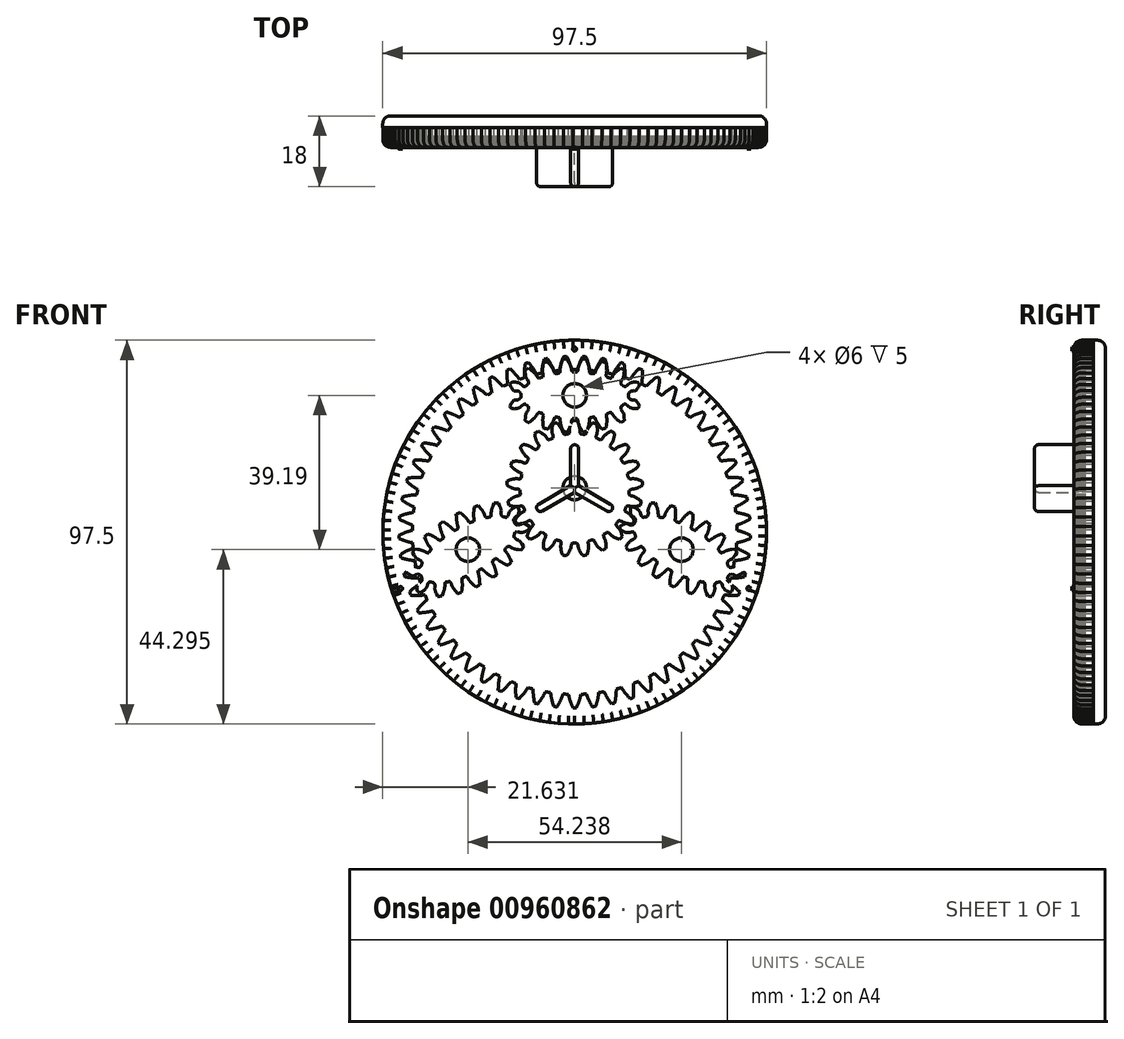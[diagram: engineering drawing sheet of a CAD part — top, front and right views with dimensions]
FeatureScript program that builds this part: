
annotation { "Feature Type Name" : "Feature", "Feature Type Description" : "" }
export const myFeature = defineFeature(function(context is Context, id is Id, definition is map)
    precondition{}
    {
        {
            var Q0;
            Q0=qCreatedBy(makeId("Front.planeOp"),FACE);
            var sketch = newSketch(context, id + "F0", { "sketchPlane" : qUnion([Q0])});
            skCircle(sketch, "E0", {"center": v(0, 0) * mm, "radius": 42.52 * mm});
            skCircle(sketch, "E1", {"center": v(0, 11.2) * mm, "radius": 15.75 * mm});
            skLineSegment(sketch, "E2", {"start": v(0, 11.2) * mm, "end": v(40.7, -12.3) * mm, "construction": true});
            skEllipse(sketch, "E3", {"center": v(0, 34.73) * mm, "majorRadius": 2 * mm, "minorRadius": 1 * mm, "majorAxis": v(1, 0)});
            skPoint(sketch, "E4", {"position": v(13.64, 3.33) * mm});
            skPoint(sketch, "E5", {"position": v(23.23, -11.2) * mm});
            skPoint(sketch, "E6", {"position": v(-15.56, 34.73) * mm});
            skPoint(sketch, "E7", {"position": v(0, 26.95) * mm});
            skPoint(sketch, "E8.center.orphan", {"position": v(27.12, -4.46) * mm});
            skLineSegment(sketch, "E9", {"start": v(27.12, -4.46) * mm, "end": v(23.23, -11.2) * mm, "construction": true});
            skEllipse(sketch, "E10", {"center": v(27.12, -4.46) * mm, "majorRadius": 2 * mm, "minorRadius": 1 * mm, "majorAxis": v(-0.87, 0.5)});
            skPoint(sketch, "E11", {"position": v(0, -4.55) * mm});
            skPoint(sketch, "E12", {"position": v(40.99, -11.3) * mm});
            skPoint(sketch, "E13", {"position": v(0, -42.52) * mm});
            skEllipse(sketch, "E14.MirrorC", {"center": v(-27.12, -4.46) * mm, "majorRadius": 2 * mm, "minorRadius": 1 * mm, "majorAxis": v(0.87, 0.5)});
            skSolve(sketch);
        }
        {
            var Q0;
            Q0=qCreatedBy(makeId("Top.planeOp"),FACE);
            var sketch = newSketch(context, id + "F1", { "sketchPlane" : qUnion([Q0])});
            skLineSegment(sketch, "E15", {"start": v(0, 8.57) * mm, "end": v(0, -10.97) * mm});
            skSolve(sketch);
        }
        {
            var Q0;
            Q0=qCreatedBy(makeId("Front.planeOp"),FACE);
            var sketch = newSketch(context, id + "F2", { "sketchPlane" : qUnion([Q0])});
            skLineSegment(sketch, "E16", {"start": v(-1.48, -8.52) * mm, "end": v(-1.41, -8.38) * mm});
            skLineSegment(sketch, "E17", {"start": v(-1.41, -8.38) * mm, "end": v(-1.35, -8.26) * mm});
            skLineSegment(sketch, "E18", {"start": v(-1.35, -8.26) * mm, "end": v(-1.3, -8.13) * mm});
            skLineSegment(sketch, "E19", {"start": v(-1.3, -8.13) * mm, "end": v(-1.25, -8.02) * mm});
            skLineSegment(sketch, "E20", {"start": v(-1.25, -8.02) * mm, "end": v(-1.2, -7.9) * mm});
            skLineSegment(sketch, "E21", {"start": v(-1.2, -7.9) * mm, "end": v(-1.15, -7.8) * mm});
            skLineSegment(sketch, "E22", {"start": v(-1.15, -7.8) * mm, "end": v(-1.1, -7.69) * mm});
            skLineSegment(sketch, "E23", {"start": v(-1.1, -7.69) * mm, "end": v(-1.07, -7.59) * mm});
            skLineSegment(sketch, "E24", {"start": v(-1.07, -7.59) * mm, "end": v(-1.04, -7.5) * mm});
            skLineSegment(sketch, "E25", {"start": v(-1.04, -7.5) * mm, "end": v(-1.01, -7.44) * mm});
            skLineSegment(sketch, "E26", {"start": v(-1.01, -7.44) * mm, "end": v(-1, -7.38) * mm});
            skLineSegment(sketch, "E27", {"start": v(-1, -7.38) * mm, "end": v(-0.97, -7.32) * mm});
            skLineSegment(sketch, "E28", {"start": v(-0.97, -7.32) * mm, "end": v(-0.93, -7.21) * mm});
            skLineSegment(sketch, "E29", {"start": v(-0.93, -7.21) * mm, "end": v(-0.9, -7.1) * mm});
            skLineSegment(sketch, "E30", {"start": v(-0.9, -7.1) * mm, "end": v(-0.86, -6.99) * mm});
            skLineSegment(sketch, "E31", {"start": v(-0.86, -6.99) * mm, "end": v(-0.83, -6.88) * mm});
            skLineSegment(sketch, "E32", {"start": v(-0.83, -6.88) * mm, "end": v(-0.8, -6.8) * mm});
            skLineSegment(sketch, "E33", {"start": v(-0.8, -6.8) * mm, "end": v(-0.78, -6.7) * mm});
            skLineSegment(sketch, "E34", {"start": v(-0.78, -6.7) * mm, "end": v(-0.76, -6.63) * mm});
            skLineSegment(sketch, "E35", {"start": v(-0.76, -6.63) * mm, "end": v(-0.74, -6.56) * mm});
            skLineSegment(sketch, "E36", {"start": v(-0.74, -6.56) * mm, "end": v(-0.66, -6.21) * mm});
            skLineSegment(sketch, "E37", {"start": v(-0.66, -6.21) * mm, "end": v(-0.65, -6.18) * mm});
            skLineSegment(sketch, "E38", {"start": v(-0.65, -6.18) * mm, "end": v(-0.64, -6.16) * mm});
            skLineSegment(sketch, "E39", {"start": v(-0.64, -6.16) * mm, "end": v(-0.63, -6.1) * mm});
            skLineSegment(sketch, "E40", {"start": v(-0.63, -6.1) * mm, "end": v(-0.61, -6.09) * mm});
            skLineSegment(sketch, "E41", {"start": v(-0.61, -6.09) * mm, "end": v(-0.6, -6.04) * mm});
            skLineSegment(sketch, "E42", {"start": v(-0.6, -6.04) * mm, "end": v(-0.57, -6) * mm});
            skLineSegment(sketch, "E43", {"start": v(-0.57, -6) * mm, "end": v(-0.54, -5.97) * mm});
            skLineSegment(sketch, "E44", {"start": v(-0.54, -5.97) * mm, "end": v(-0.52, -5.95) * mm});
            skLineSegment(sketch, "E45", {"start": v(-0.52, -5.95) * mm, "end": v(-0.49, -5.93) * mm});
            skLineSegment(sketch, "E46", {"start": v(-0.49, -5.93) * mm, "end": v(-0.47, -5.91) * mm});
            skLineSegment(sketch, "E47", {"start": v(-0.47, -5.91) * mm, "end": v(-0.46, -5.91) * mm});
            skLineSegment(sketch, "E48", {"start": v(-0.46, -5.91) * mm, "end": v(-0.45, -5.9) * mm});
            skLineSegment(sketch, "E49", {"start": v(-0.45, -5.9) * mm, "end": v(-0.44, -5.9) * mm});
            skLineSegment(sketch, "E50", {"start": v(-0.44, -5.9) * mm, "end": v(-0.43, -5.9) * mm});
            skLineSegment(sketch, "E51", {"start": v(-0.43, -5.9) * mm, "end": v(-0.26, -5.9) * mm});
            skLineSegment(sketch, "E52", {"start": v(-0.26, -5.9) * mm, "end": v(-0.05, -5.9) * mm});
            skLineSegment(sketch, "E53", {"start": v(-0.05, -5.9) * mm, "end": v(0.12, -5.9) * mm});
            skLineSegment(sketch, "E54", {"start": v(0.12, -5.9) * mm, "end": v(0.32, -5.9) * mm});
            skLineSegment(sketch, "E55", {"start": v(0.32, -5.9) * mm, "end": v(0.5, -5.9) * mm});
            skLineSegment(sketch, "E56", {"start": v(0.5, -5.9) * mm, "end": v(0.51, -5.9) * mm});
            skLineSegment(sketch, "E57", {"start": v(0.51, -5.9) * mm, "end": v(0.52, -5.9) * mm});
            skLineSegment(sketch, "E58", {"start": v(0.52, -5.9) * mm, "end": v(0.53, -5.9) * mm});
            skLineSegment(sketch, "E59", {"start": v(0.53, -5.9) * mm, "end": v(0.54, -5.91) * mm});
            skLineSegment(sketch, "E60", {"start": v(0.54, -5.91) * mm, "end": v(0.56, -5.92) * mm});
            skLineSegment(sketch, "E61", {"start": v(0.56, -5.92) * mm, "end": v(0.58, -5.94) * mm});
            skLineSegment(sketch, "E62", {"start": v(0.58, -5.94) * mm, "end": v(0.6, -5.96) * mm});
            skLineSegment(sketch, "E63", {"start": v(0.6, -5.96) * mm, "end": v(0.62, -5.98) * mm});
            skLineSegment(sketch, "E64", {"start": v(0.62, -5.98) * mm, "end": v(0.64, -6) * mm});
            skLineSegment(sketch, "E65", {"start": v(0.64, -6) * mm, "end": v(0.66, -6.03) * mm});
            skLineSegment(sketch, "E66", {"start": v(0.66, -6.03) * mm, "end": v(0.68, -6.07) * mm});
            skLineSegment(sketch, "E67", {"start": v(0.68, -6.07) * mm, "end": v(0.7, -6.11) * mm});
            skLineSegment(sketch, "E68", {"start": v(0.7, -6.11) * mm, "end": v(0.72, -6.16) * mm});
            skLineSegment(sketch, "E69", {"start": v(0.72, -6.16) * mm, "end": v(0.73, -6.18) * mm});
            skLineSegment(sketch, "E70", {"start": v(0.73, -6.18) * mm, "end": v(0.83, -6.58) * mm});
            skLineSegment(sketch, "E71", {"start": v(0.83, -6.58) * mm, "end": v(0.84, -6.66) * mm});
            skLineSegment(sketch, "E72", {"start": v(0.84, -6.66) * mm, "end": v(0.86, -6.73) * mm});
            skLineSegment(sketch, "E73", {"start": v(0.86, -6.73) * mm, "end": v(0.89, -6.81) * mm});
            skLineSegment(sketch, "E74", {"start": v(0.89, -6.81) * mm, "end": v(0.9, -6.88) * mm});
            skLineSegment(sketch, "E75", {"start": v(0.9, -6.88) * mm, "end": v(0.93, -6.97) * mm});
            skLineSegment(sketch, "E76", {"start": v(0.93, -6.97) * mm, "end": v(0.96, -7.05) * mm});
            skLineSegment(sketch, "E77", {"start": v(0.96, -7.05) * mm, "end": v(0.99, -7.14) * mm});
            skLineSegment(sketch, "E78", {"start": v(0.99, -7.14) * mm, "end": v(1.02, -7.22) * mm});
            skLineSegment(sketch, "E79", {"start": v(1.02, -7.22) * mm, "end": v(1.05, -7.31) * mm});
            skLineSegment(sketch, "E80", {"start": v(1.05, -7.31) * mm, "end": v(1.07, -7.38) * mm});
            skLineSegment(sketch, "E81", {"start": v(1.07, -7.38) * mm, "end": v(1.09, -7.42) * mm});
            skLineSegment(sketch, "E82", {"start": v(1.09, -7.42) * mm, "end": v(1.11, -7.5) * mm});
            skLineSegment(sketch, "E83", {"start": v(1.11, -7.5) * mm, "end": v(1.16, -7.6) * mm});
            skLineSegment(sketch, "E84", {"start": v(1.16, -7.6) * mm, "end": v(1.2, -7.74) * mm});
            skLineSegment(sketch, "E85", {"start": v(1.2, -7.74) * mm, "end": v(1.27, -7.88) * mm});
            skLineSegment(sketch, "E86", {"start": v(1.27, -7.88) * mm, "end": v(1.33, -8.02) * mm});
            skLineSegment(sketch, "E87", {"start": v(1.33, -8.02) * mm, "end": v(1.39, -8.16) * mm});
            skLineSegment(sketch, "E88", {"start": v(1.39, -8.16) * mm, "end": v(1.45, -8.3) * mm});
            skLineSegment(sketch, "E89", {"start": v(1.45, -8.3) * mm, "end": v(1.52, -8.43) * mm});
            skLineSegment(sketch, "E90", {"start": v(1.52, -8.43) * mm, "end": v(1.59, -8.57) * mm});
            skLineSegment(sketch, "E91", {"start": v(1.59, -8.57) * mm, "end": v(1.95, -9.28) * mm});
            skLineSegment(sketch, "E92", {"start": v(1.95, -9.28) * mm, "end": v(2, -9.28) * mm});
            skLineSegment(sketch, "E93", {"start": v(2, -9.28) * mm, "end": v(2.29, -9.26) * mm});
            skLineSegment(sketch, "E94", {"start": v(2.29, -9.26) * mm, "end": v(2.57, -9.24) * mm});
            skLineSegment(sketch, "E95", {"start": v(2.57, -9.24) * mm, "end": v(2.85, -9.22) * mm});
            skLineSegment(sketch, "E96", {"start": v(2.85, -9.22) * mm, "end": v(3.08, -9.2) * mm});
            skLineSegment(sketch, "E97", {"start": v(3.08, -9.2) * mm, "end": v(3.35, -8.36) * mm});
            skLineSegment(sketch, "E98", {"start": v(3.35, -8.36) * mm, "end": v(3.4, -8.2) * mm});
            skLineSegment(sketch, "E99", {"start": v(3.4, -8.2) * mm, "end": v(3.44, -8.05) * mm});
            skLineSegment(sketch, "E100", {"start": v(3.44, -8.05) * mm, "end": v(3.48, -7.9) * mm});
            skLineSegment(sketch, "E101", {"start": v(3.48, -7.9) * mm, "end": v(3.52, -7.76) * mm});
            skLineSegment(sketch, "E102", {"start": v(3.52, -7.76) * mm, "end": v(3.55, -7.64) * mm});
            skLineSegment(sketch, "E103", {"start": v(3.55, -7.64) * mm, "end": v(3.58, -7.5) * mm});
            skLineSegment(sketch, "E104", {"start": v(3.58, -7.5) * mm, "end": v(3.6, -7.4) * mm});
            skLineSegment(sketch, "E105", {"start": v(3.6, -7.4) * mm, "end": v(3.63, -7.29) * mm});
            skLineSegment(sketch, "E106", {"start": v(3.63, -7.29) * mm, "end": v(3.64, -7.22) * mm});
            skLineSegment(sketch, "E107", {"start": v(3.64, -7.22) * mm, "end": v(3.65, -7.19) * mm});
            skLineSegment(sketch, "E108", {"start": v(3.65, -7.19) * mm, "end": v(3.66, -7.12) * mm});
            skLineSegment(sketch, "E109", {"start": v(3.66, -7.12) * mm, "end": v(3.68, -7.04) * mm});
            skLineSegment(sketch, "E110", {"start": v(3.68, -7.04) * mm, "end": v(3.7, -6.95) * mm});
            skLineSegment(sketch, "E111", {"start": v(3.7, -6.95) * mm, "end": v(3.7, -6.86) * mm});
            skLineSegment(sketch, "E112", {"start": v(3.7, -6.86) * mm, "end": v(3.72, -6.76) * mm});
            skLineSegment(sketch, "E113", {"start": v(3.72, -6.76) * mm, "end": v(3.73, -6.68) * mm});
            skLineSegment(sketch, "E114", {"start": v(3.73, -6.68) * mm, "end": v(3.74, -6.6) * mm});
            skLineSegment(sketch, "E115", {"start": v(3.74, -6.6) * mm, "end": v(3.74, -6.54) * mm});
            skLineSegment(sketch, "E116", {"start": v(3.74, -6.54) * mm, "end": v(3.75, -6.48) * mm});
            skLineSegment(sketch, "E117", {"start": v(3.75, -6.48) * mm, "end": v(3.75, -6.43) * mm});
            skLineSegment(sketch, "E118", {"start": v(3.75, -6.43) * mm, "end": v(3.75, -6.38) * mm});
            skLineSegment(sketch, "E119", {"start": v(3.75, -6.38) * mm, "end": v(3.76, -6.1) * mm});
            skLineSegment(sketch, "E120", {"start": v(3.76, -6.1) * mm, "end": v(3.77, -6.09) * mm});
            skLineSegment(sketch, "E121", {"start": v(3.77, -6.09) * mm, "end": v(3.77, -6.01) * mm});
            skLineSegment(sketch, "E122", {"start": v(3.77, -6.01) * mm, "end": v(3.78, -5.98) * mm});
            skLineSegment(sketch, "E123", {"start": v(3.78, -5.98) * mm, "end": v(3.79, -5.95) * mm});
            skLineSegment(sketch, "E124", {"start": v(3.79, -5.95) * mm, "end": v(3.8, -5.9) * mm});
            skLineSegment(sketch, "E125", {"start": v(3.8, -5.9) * mm, "end": v(3.8, -5.87) * mm});
            skLineSegment(sketch, "E126", {"start": v(3.8, -5.87) * mm, "end": v(3.82, -5.85) * mm});
            skLineSegment(sketch, "E127", {"start": v(3.82, -5.85) * mm, "end": v(3.82, -5.8) * mm});
            skLineSegment(sketch, "E128", {"start": v(3.82, -5.8) * mm, "end": v(3.84, -5.78) * mm});
            skLineSegment(sketch, "E129", {"start": v(3.84, -5.78) * mm, "end": v(3.86, -5.74) * mm});
            skLineSegment(sketch, "E130", {"start": v(3.86, -5.74) * mm, "end": v(3.88, -5.7) * mm});
            skLineSegment(sketch, "E131", {"start": v(3.88, -5.7) * mm, "end": v(3.9, -5.68) * mm});
            skLineSegment(sketch, "E132", {"start": v(3.9, -5.68) * mm, "end": v(3.92, -5.66) * mm});
            skLineSegment(sketch, "E133", {"start": v(3.92, -5.66) * mm, "end": v(3.94, -5.65) * mm});
            skLineSegment(sketch, "E134", {"start": v(3.94, -5.65) * mm, "end": v(3.95, -5.64) * mm});
            skLineSegment(sketch, "E135", {"start": v(3.95, -5.64) * mm, "end": v(3.95, -5.64) * mm});
            skLineSegment(sketch, "E136", {"start": v(3.95, -5.64) * mm, "end": v(3.97, -5.64) * mm});
            skLineSegment(sketch, "E137", {"start": v(3.97, -5.64) * mm, "end": v(3.98, -5.63) * mm});
            skLineSegment(sketch, "E138", {"start": v(3.98, -5.63) * mm, "end": v(4.18, -5.6) * mm});
            skLineSegment(sketch, "E139", {"start": v(4.18, -5.6) * mm, "end": v(4.38, -5.57) * mm});
            skLineSegment(sketch, "E140", {"start": v(4.38, -5.57) * mm, "end": v(4.5, -5.55) * mm});
            skLineSegment(sketch, "E141", {"start": v(4.5, -5.55) * mm, "end": v(4.7, -5.52) * mm});
            skLineSegment(sketch, "E142", {"start": v(4.7, -5.52) * mm, "end": v(4.9, -5.48) * mm});
            skLineSegment(sketch, "E143", {"start": v(4.9, -5.48) * mm, "end": v(4.9, -5.49) * mm});
            skLineSegment(sketch, "E144", {"start": v(4.9, -5.49) * mm, "end": v(4.92, -5.49) * mm});
            skLineSegment(sketch, "E145", {"start": v(4.92, -5.49) * mm, "end": v(4.93, -5.49) * mm});
            skLineSegment(sketch, "E146", {"start": v(4.93, -5.49) * mm, "end": v(4.94, -5.49) * mm});
            skLineSegment(sketch, "E147", {"start": v(4.94, -5.49) * mm, "end": v(4.96, -5.5) * mm});
            skLineSegment(sketch, "E148", {"start": v(4.96, -5.5) * mm, "end": v(4.99, -5.51) * mm});
            skLineSegment(sketch, "E149", {"start": v(4.99, -5.51) * mm, "end": v(5.01, -5.53) * mm});
            skLineSegment(sketch, "E150", {"start": v(5.01, -5.53) * mm, "end": v(5.04, -5.55) * mm});
            skLineSegment(sketch, "E151", {"start": v(5.04, -5.55) * mm, "end": v(5.07, -5.58) * mm});
            skLineSegment(sketch, "E152", {"start": v(5.07, -5.58) * mm, "end": v(5.1, -5.61) * mm});
            skLineSegment(sketch, "E153", {"start": v(5.1, -5.61) * mm, "end": v(5.12, -5.63) * mm});
            skLineSegment(sketch, "E154", {"start": v(5.12, -5.63) * mm, "end": v(5.14, -5.68) * mm});
            skLineSegment(sketch, "E155", {"start": v(5.14, -5.68) * mm, "end": v(5.16, -5.7) * mm});
            skLineSegment(sketch, "E156", {"start": v(5.16, -5.7) * mm, "end": v(5.17, -5.73) * mm});
            skLineSegment(sketch, "E157", {"start": v(5.17, -5.73) * mm, "end": v(5.33, -6.11) * mm});
            skLineSegment(sketch, "E158", {"start": v(5.33, -6.11) * mm, "end": v(5.37, -6.2) * mm});
            skLineSegment(sketch, "E159", {"start": v(5.37, -6.2) * mm, "end": v(5.4, -6.28) * mm});
            skLineSegment(sketch, "E160", {"start": v(5.4, -6.28) * mm, "end": v(5.44, -6.37) * mm});
            skLineSegment(sketch, "E161", {"start": v(5.44, -6.37) * mm, "end": v(5.48, -6.45) * mm});
            skLineSegment(sketch, "E162", {"start": v(5.48, -6.45) * mm, "end": v(5.52, -6.54) * mm});
            skLineSegment(sketch, "E163", {"start": v(5.52, -6.54) * mm, "end": v(5.57, -6.62) * mm});
            skLineSegment(sketch, "E164", {"start": v(5.57, -6.62) * mm, "end": v(5.61, -6.71) * mm});
            skLineSegment(sketch, "E165", {"start": v(5.61, -6.71) * mm, "end": v(5.66, -6.8) * mm});
            skLineSegment(sketch, "E166", {"start": v(5.66, -6.8) * mm, "end": v(5.7, -6.86) * mm});
            skLineSegment(sketch, "E167", {"start": v(5.7, -6.86) * mm, "end": v(5.7, -6.9) * mm});
            skLineSegment(sketch, "E168", {"start": v(5.7, -6.9) * mm, "end": v(5.74, -6.95) * mm});
            skLineSegment(sketch, "E169", {"start": v(5.74, -6.95) * mm, "end": v(5.8, -7.04) * mm});
            skLineSegment(sketch, "E170", {"start": v(5.8, -7.04) * mm, "end": v(5.84, -7.13) * mm});
            skLineSegment(sketch, "E171", {"start": v(5.84, -7.13) * mm, "end": v(5.9, -7.23) * mm});
            skLineSegment(sketch, "E172", {"start": v(5.9, -7.23) * mm, "end": v(5.98, -7.34) * mm});
            skLineSegment(sketch, "E173", {"start": v(5.98, -7.34) * mm, "end": v(6.05, -7.45) * mm});
            skLineSegment(sketch, "E174", {"start": v(6.05, -7.45) * mm, "end": v(6.13, -7.57) * mm});
            skLineSegment(sketch, "E175", {"start": v(6.13, -7.57) * mm, "end": v(6.2, -7.68) * mm});
            skLineSegment(sketch, "E176", {"start": v(6.2, -7.68) * mm, "end": v(6.28, -7.78) * mm});
            skLineSegment(sketch, "E177", {"start": v(6.28, -7.78) * mm, "end": v(6.36, -7.9) * mm});
            skLineSegment(sketch, "E178", {"start": v(6.36, -7.9) * mm, "end": v(6.45, -8.01) * mm});
            skLineSegment(sketch, "E179", {"start": v(6.45, -8.01) * mm, "end": v(6.9, -8.58) * mm});
            skLineSegment(sketch, "E180", {"start": v(6.9, -8.58) * mm, "end": v(6.97, -8.56) * mm});
            skLineSegment(sketch, "E181", {"start": v(6.97, -8.56) * mm, "end": v(7.16, -8.52) * mm});
            skLineSegment(sketch, "E182", {"start": v(7.16, -8.52) * mm, "end": v(7.35, -8.47) * mm});
            skLineSegment(sketch, "E183", {"start": v(7.35, -8.47) * mm, "end": v(7.52, -8.43) * mm});
            skLineSegment(sketch, "E184", {"start": v(7.52, -8.43) * mm, "end": v(7.7, -8.38) * mm});
            skLineSegment(sketch, "E185", {"start": v(7.7, -8.38) * mm, "end": v(7.87, -8.33) * mm});
            skLineSegment(sketch, "E186", {"start": v(7.87, -8.33) * mm, "end": v(7.96, -8.31) * mm});
            skLineSegment(sketch, "E187", {"start": v(7.96, -8.31) * mm, "end": v(8.07, -7.58) * mm});
            skLineSegment(sketch, "E188", {"start": v(8.07, -7.58) * mm, "end": v(8.1, -7.45) * mm});
            skLineSegment(sketch, "E189", {"start": v(8.1, -7.45) * mm, "end": v(8.12, -7.3) * mm});
            skLineSegment(sketch, "E190", {"start": v(8.12, -7.3) * mm, "end": v(8.13, -7.14) * mm});
            skLineSegment(sketch, "E191", {"start": v(8.13, -7.14) * mm, "end": v(8.15, -7) * mm});
            skLineSegment(sketch, "E192", {"start": v(8.15, -7) * mm, "end": v(8.16, -6.88) * mm});
            skLineSegment(sketch, "E193", {"start": v(8.16, -6.88) * mm, "end": v(8.17, -6.76) * mm});
            skLineSegment(sketch, "E194", {"start": v(8.17, -6.76) * mm, "end": v(8.17, -6.65) * mm});
            skLineSegment(sketch, "E195", {"start": v(8.17, -6.65) * mm, "end": v(8.18, -6.54) * mm});
            skLineSegment(sketch, "E196", {"start": v(8.18, -6.54) * mm, "end": v(8.18, -6.42) * mm});
            skLineSegment(sketch, "E197", {"start": v(8.18, -6.42) * mm, "end": v(8.18, -6.32) * mm});
            skLineSegment(sketch, "E198", {"start": v(8.18, -6.32) * mm, "end": v(8.18, -6.26) * mm});
            skLineSegment(sketch, "E199", {"start": v(8.18, -6.26) * mm, "end": v(8.18, -6.23) * mm});
            skLineSegment(sketch, "E200", {"start": v(8.18, -6.23) * mm, "end": v(8.18, -6.2) * mm});
            skLineSegment(sketch, "E201", {"start": v(8.18, -6.2) * mm, "end": v(8.18, -6.1) * mm});
            skLineSegment(sketch, "E202", {"start": v(8.18, -6.1) * mm, "end": v(8.18, -6.02) * mm});
            skLineSegment(sketch, "E203", {"start": v(8.18, -6.02) * mm, "end": v(8.17, -5.95) * mm});
            skLineSegment(sketch, "E204", {"start": v(8.17, -5.95) * mm, "end": v(8.17, -5.89) * mm});
            skLineSegment(sketch, "E205", {"start": v(8.17, -5.89) * mm, "end": v(8.16, -5.83) * mm});
            skLineSegment(sketch, "E206", {"start": v(8.16, -5.83) * mm, "end": v(8.16, -5.78) * mm});
            skLineSegment(sketch, "E207", {"start": v(8.16, -5.78) * mm, "end": v(8.15, -5.75) * mm});
            skLineSegment(sketch, "E208", {"start": v(8.15, -5.75) * mm, "end": v(8.15, -5.72) * mm});
            skLineSegment(sketch, "E209", {"start": v(8.15, -5.72) * mm, "end": v(8.14, -5.72) * mm});
            skLineSegment(sketch, "E210", {"start": v(8.14, -5.72) * mm, "end": v(8.06, -5.39) * mm});
            skLineSegment(sketch, "E211", {"start": v(8.06, -5.39) * mm, "end": v(8.07, -5.38) * mm});
            skLineSegment(sketch, "E212", {"start": v(8.07, -5.38) * mm, "end": v(8.04, -5.27) * mm});
            skLineSegment(sketch, "E213", {"start": v(8.04, -5.27) * mm, "end": v(8.06, -5.27) * mm});
            skLineSegment(sketch, "E214", {"start": v(8.06, -5.27) * mm, "end": v(8.04, -5.16) * mm});
            skLineSegment(sketch, "E215", {"start": v(8.04, -5.16) * mm, "end": v(8.05, -5.16) * mm});
            skLineSegment(sketch, "E216", {"start": v(8.05, -5.16) * mm, "end": v(8.03, -5.07) * mm});
            skLineSegment(sketch, "E217", {"start": v(8.03, -5.07) * mm, "end": v(8.05, -5.06) * mm});
            skLineSegment(sketch, "E218", {"start": v(8.05, -5.06) * mm, "end": v(8.04, -4.98) * mm});
            skLineSegment(sketch, "E219", {"start": v(8.04, -4.98) * mm, "end": v(8.05, -4.98) * mm});
            skLineSegment(sketch, "E220", {"start": v(8.05, -4.98) * mm, "end": v(8.05, -4.92) * mm});
            skLineSegment(sketch, "E221", {"start": v(8.05, -4.92) * mm, "end": v(8.07, -4.9) * mm});
            skLineSegment(sketch, "E222", {"start": v(8.07, -4.9) * mm, "end": v(8.06, -4.85) * mm});
            skLineSegment(sketch, "E223", {"start": v(8.06, -4.85) * mm, "end": v(8.08, -4.82) * mm});
            skLineSegment(sketch, "E224", {"start": v(8.08, -4.82) * mm, "end": v(8.1, -4.8) * mm});
            skLineSegment(sketch, "E225", {"start": v(8.1, -4.8) * mm, "end": v(8.1, -4.75) * mm});
            skLineSegment(sketch, "E226", {"start": v(8.1, -4.75) * mm, "end": v(8.13, -4.71) * mm});
            skLineSegment(sketch, "E227", {"start": v(8.13, -4.71) * mm, "end": v(8.16, -4.68) * mm});
            skLineSegment(sketch, "E228", {"start": v(8.16, -4.68) * mm, "end": v(8.17, -4.66) * mm});
            skLineSegment(sketch, "E229", {"start": v(8.17, -4.66) * mm, "end": v(8.18, -4.66) * mm});
            skLineSegment(sketch, "E230", {"start": v(8.18, -4.66) * mm, "end": v(8.2, -4.65) * mm});
            skLineSegment(sketch, "E231", {"start": v(8.2, -4.65) * mm, "end": v(8.2, -4.64) * mm});
            skLineSegment(sketch, "E232", {"start": v(8.2, -4.64) * mm, "end": v(8.44, -4.56) * mm});
            skLineSegment(sketch, "E233", {"start": v(8.44, -4.56) * mm, "end": v(8.6, -4.5) * mm});
            skLineSegment(sketch, "E234", {"start": v(8.6, -4.5) * mm, "end": v(8.68, -4.47) * mm});
            skLineSegment(sketch, "E235", {"start": v(8.68, -4.47) * mm, "end": v(8.82, -4.42) * mm});
            skLineSegment(sketch, "E236", {"start": v(8.82, -4.42) * mm, "end": v(9.07, -4.32) * mm});
            skLineSegment(sketch, "E237", {"start": v(9.07, -4.32) * mm, "end": v(9.08, -4.32) * mm});
            skLineSegment(sketch, "E238", {"start": v(9.08, -4.32) * mm, "end": v(9.1, -4.32) * mm});
            skLineSegment(sketch, "E239", {"start": v(9.1, -4.32) * mm, "end": v(9.1, -4.32) * mm});
            skLineSegment(sketch, "E240", {"start": v(9.1, -4.32) * mm, "end": v(9.11, -4.32) * mm});
            skLineSegment(sketch, "E241", {"start": v(9.11, -4.32) * mm, "end": v(9.15, -4.32) * mm});
            skLineSegment(sketch, "E242", {"start": v(9.15, -4.32) * mm, "end": v(9.19, -4.33) * mm});
            skLineSegment(sketch, "E243", {"start": v(9.19, -4.33) * mm, "end": v(9.22, -4.35) * mm});
            skLineSegment(sketch, "E244", {"start": v(9.22, -4.35) * mm, "end": v(9.26, -4.36) * mm});
            skLineSegment(sketch, "E245", {"start": v(9.26, -4.36) * mm, "end": v(9.3, -4.39) * mm});
            skLineSegment(sketch, "E246", {"start": v(9.3, -4.39) * mm, "end": v(9.33, -4.41) * mm});
            skLineSegment(sketch, "E247", {"start": v(9.33, -4.41) * mm, "end": v(9.35, -4.43) * mm});
            skLineSegment(sketch, "E248", {"start": v(9.35, -4.43) * mm, "end": v(9.38, -4.47) * mm});
            skLineSegment(sketch, "E249", {"start": v(9.38, -4.47) * mm, "end": v(9.4, -4.49) * mm});
            skLineSegment(sketch, "E250", {"start": v(9.4, -4.49) * mm, "end": v(9.43, -4.5) * mm});
            skLineSegment(sketch, "E251", {"start": v(9.43, -4.5) * mm, "end": v(9.46, -4.56) * mm});
            skLineSegment(sketch, "E252", {"start": v(9.46, -4.56) * mm, "end": v(9.48, -4.58) * mm});
            skLineSegment(sketch, "E253", {"start": v(9.48, -4.58) * mm, "end": v(9.5, -4.6) * mm});
            skLineSegment(sketch, "E254", {"start": v(9.5, -4.6) * mm, "end": v(9.65, -4.87) * mm});
            skLineSegment(sketch, "E255", {"start": v(9.65, -4.87) * mm, "end": v(9.68, -4.92) * mm});
            skLineSegment(sketch, "E256", {"start": v(9.68, -4.92) * mm, "end": v(9.72, -4.97) * mm});
            skLineSegment(sketch, "E257", {"start": v(9.72, -4.97) * mm, "end": v(9.76, -5.03) * mm});
            skLineSegment(sketch, "E258", {"start": v(9.76, -5.03) * mm, "end": v(9.8, -5.1) * mm});
            skLineSegment(sketch, "E259", {"start": v(9.8, -5.1) * mm, "end": v(9.84, -5.15) * mm});
            skLineSegment(sketch, "E260", {"start": v(9.84, -5.15) * mm, "end": v(9.88, -5.21) * mm});
            skLineSegment(sketch, "E261", {"start": v(9.88, -5.21) * mm, "end": v(9.93, -5.27) * mm});
            skLineSegment(sketch, "E262", {"start": v(9.93, -5.27) * mm, "end": v(9.98, -5.34) * mm});
            skLineSegment(sketch, "E263", {"start": v(9.98, -5.34) * mm, "end": v(10.03, -5.4) * mm});
            skLineSegment(sketch, "E264", {"start": v(10.03, -5.4) * mm, "end": v(10.1, -5.48) * mm});
            skLineSegment(sketch, "E265", {"start": v(10.1, -5.48) * mm, "end": v(10.12, -5.51) * mm});
            skLineSegment(sketch, "E266", {"start": v(10.12, -5.51) * mm, "end": v(10.14, -5.54) * mm});
            skLineSegment(sketch, "E267", {"start": v(10.14, -5.54) * mm, "end": v(10.18, -5.58) * mm});
            skLineSegment(sketch, "E268", {"start": v(10.18, -5.58) * mm, "end": v(10.24, -5.65) * mm});
            skLineSegment(sketch, "E269", {"start": v(10.24, -5.65) * mm, "end": v(10.32, -5.73) * mm});
            skLineSegment(sketch, "E270", {"start": v(10.32, -5.73) * mm, "end": v(10.4, -5.81) * mm});
            skLineSegment(sketch, "E271", {"start": v(10.4, -5.81) * mm, "end": v(10.47, -5.89) * mm});
            skLineSegment(sketch, "E272", {"start": v(10.47, -5.89) * mm, "end": v(10.56, -5.97) * mm});
            skLineSegment(sketch, "E273", {"start": v(10.56, -5.97) * mm, "end": v(10.65, -6.06) * mm});
            skLineSegment(sketch, "E274", {"start": v(10.65, -6.06) * mm, "end": v(10.75, -6.15) * mm});
            skLineSegment(sketch, "E275", {"start": v(10.75, -6.15) * mm, "end": v(10.86, -6.25) * mm});
            skLineSegment(sketch, "E276", {"start": v(10.86, -6.25) * mm, "end": v(10.99, -6.34) * mm});
            skLineSegment(sketch, "E277", {"start": v(10.99, -6.34) * mm, "end": v(11.12, -6.44) * mm});
            skLineSegment(sketch, "E278", {"start": v(11.12, -6.44) * mm, "end": v(11.73, -6.89) * mm});
            skLineSegment(sketch, "E279", {"start": v(11.73, -6.89) * mm, "end": v(11.8, -6.85) * mm});
            skLineSegment(sketch, "E280", {"start": v(11.8, -6.85) * mm, "end": v(11.9, -6.8) * mm});
            skLineSegment(sketch, "E281", {"start": v(11.9, -6.8) * mm, "end": v(11.98, -6.76) * mm});
            skLineSegment(sketch, "E282", {"start": v(11.98, -6.76) * mm, "end": v(12.07, -6.71) * mm});
            skLineSegment(sketch, "E283", {"start": v(12.07, -6.71) * mm, "end": v(12.16, -6.66) * mm});
            skLineSegment(sketch, "E284", {"start": v(12.16, -6.66) * mm, "end": v(12.24, -6.62) * mm});
            skLineSegment(sketch, "E285", {"start": v(12.24, -6.62) * mm, "end": v(12.32, -6.57) * mm});
            skLineSegment(sketch, "E286", {"start": v(12.32, -6.57) * mm, "end": v(12.4, -6.53) * mm});
            skLineSegment(sketch, "E287", {"start": v(12.4, -6.53) * mm, "end": v(12.49, -6.48) * mm});
            skLineSegment(sketch, "E288", {"start": v(12.49, -6.48) * mm, "end": v(12.56, -6.44) * mm});
            skLineSegment(sketch, "E289", {"start": v(12.56, -6.44) * mm, "end": v(12.64, -6.4) * mm});
            skLineSegment(sketch, "E290", {"start": v(12.64, -6.4) * mm, "end": v(12.64, -6.39) * mm});
            skLineSegment(sketch, "E291", {"start": v(12.64, -6.39) * mm, "end": v(12.59, -5.58) * mm});
            skLineSegment(sketch, "E292", {"start": v(12.59, -5.58) * mm, "end": v(12.57, -5.42) * mm});
            skLineSegment(sketch, "E293", {"start": v(12.57, -5.42) * mm, "end": v(12.56, -5.27) * mm});
            skLineSegment(sketch, "E294", {"start": v(12.56, -5.27) * mm, "end": v(12.54, -5.14) * mm});
            skLineSegment(sketch, "E295", {"start": v(12.54, -5.14) * mm, "end": v(12.52, -5) * mm});
            skLineSegment(sketch, "E296", {"start": v(12.52, -5) * mm, "end": v(12.5, -4.88) * mm});
            skLineSegment(sketch, "E297", {"start": v(12.5, -4.88) * mm, "end": v(12.47, -4.77) * mm});
            skLineSegment(sketch, "E298", {"start": v(12.47, -4.77) * mm, "end": v(12.44, -4.66) * mm});
            skLineSegment(sketch, "E299", {"start": v(12.44, -4.66) * mm, "end": v(12.42, -4.56) * mm});
            skLineSegment(sketch, "E300", {"start": v(12.42, -4.56) * mm, "end": v(12.4, -4.47) * mm});
            skLineSegment(sketch, "E301", {"start": v(12.4, -4.47) * mm, "end": v(12.37, -4.39) * mm});
            skLineSegment(sketch, "E302", {"start": v(12.37, -4.39) * mm, "end": v(12.36, -4.36) * mm});
            skLineSegment(sketch, "E303", {"start": v(12.36, -4.36) * mm, "end": v(12.35, -4.34) * mm});
            skLineSegment(sketch, "E304", {"start": v(12.35, -4.34) * mm, "end": v(12.34, -4.31) * mm});
            skLineSegment(sketch, "E305", {"start": v(12.34, -4.31) * mm, "end": v(12.34, -4.31) * mm});
            skLineSegment(sketch, "E306", {"start": v(12.34, -4.31) * mm, "end": v(12.18, -4.17) * mm});
            skLineSegment(sketch, "E307", {"start": v(12.18, -4.17) * mm, "end": v(12.2, -4.14) * mm});
            skLineSegment(sketch, "E308", {"start": v(12.2, -4.14) * mm, "end": v(12.02, -3.96) * mm});
            skLineSegment(sketch, "E309", {"start": v(12.02, -3.96) * mm, "end": v(12.04, -3.93) * mm});
            skLineSegment(sketch, "E310", {"start": v(12.04, -3.93) * mm, "end": v(11.9, -3.78) * mm});
            skLineSegment(sketch, "E311", {"start": v(11.9, -3.78) * mm, "end": v(11.93, -3.74) * mm});
            skLineSegment(sketch, "E312", {"start": v(11.93, -3.74) * mm, "end": v(11.82, -3.6) * mm});
            skLineSegment(sketch, "E313", {"start": v(11.82, -3.6) * mm, "end": v(11.85, -3.56) * mm});
            skLineSegment(sketch, "E314", {"start": v(11.85, -3.56) * mm, "end": v(11.77, -3.45) * mm});
            skLineSegment(sketch, "E315", {"start": v(11.77, -3.45) * mm, "end": v(11.8, -3.4) * mm});
            skLineSegment(sketch, "E316", {"start": v(11.8, -3.4) * mm, "end": v(11.74, -3.3) * mm});
            skLineSegment(sketch, "E317", {"start": v(11.74, -3.3) * mm, "end": v(11.77, -3.27) * mm});
            skLineSegment(sketch, "E318", {"start": v(11.77, -3.27) * mm, "end": v(11.72, -3.18) * mm});
            skLineSegment(sketch, "E319", {"start": v(11.72, -3.18) * mm, "end": v(11.76, -3.14) * mm});
            skLineSegment(sketch, "E320", {"start": v(11.76, -3.14) * mm, "end": v(11.73, -3.08) * mm});
            skLineSegment(sketch, "E321", {"start": v(11.73, -3.08) * mm, "end": v(11.76, -3.04) * mm});
            skLineSegment(sketch, "E322", {"start": v(11.76, -3.04) * mm, "end": v(11.74, -3) * mm});
            skLineSegment(sketch, "E323", {"start": v(11.74, -3) * mm, "end": v(11.78, -2.95) * mm});
            skLineSegment(sketch, "E324", {"start": v(11.78, -2.95) * mm, "end": v(11.77, -2.92) * mm});
            skLineSegment(sketch, "E325", {"start": v(11.77, -2.92) * mm, "end": v(11.8, -2.87) * mm});
            skLineSegment(sketch, "E326", {"start": v(11.8, -2.87) * mm, "end": v(11.8, -2.86) * mm});
            skLineSegment(sketch, "E327", {"start": v(11.8, -2.86) * mm, "end": v(11.8, -2.85) * mm});
            skLineSegment(sketch, "E328", {"start": v(11.8, -2.85) * mm, "end": v(11.83, -2.83) * mm});
            skLineSegment(sketch, "E329", {"start": v(11.83, -2.83) * mm, "end": v(11.85, -2.8) * mm});
            skLineSegment(sketch, "E330", {"start": v(11.85, -2.8) * mm, "end": v(12.07, -2.63) * mm});
            skLineSegment(sketch, "E331", {"start": v(12.07, -2.63) * mm, "end": v(12.16, -2.55) * mm});
            skLineSegment(sketch, "E332", {"start": v(12.16, -2.55) * mm, "end": v(12.2, -2.52) * mm});
            skLineSegment(sketch, "E333", {"start": v(12.2, -2.52) * mm, "end": v(12.3, -2.44) * mm});
            skLineSegment(sketch, "E334", {"start": v(12.3, -2.44) * mm, "end": v(12.5, -2.25) * mm});
            skLineSegment(sketch, "E335", {"start": v(12.5, -2.25) * mm, "end": v(12.53, -2.24) * mm});
            skLineSegment(sketch, "E336", {"start": v(12.53, -2.24) * mm, "end": v(12.56, -2.22) * mm});
            skLineSegment(sketch, "E337", {"start": v(12.56, -2.22) * mm, "end": v(12.56, -2.22) * mm});
            skLineSegment(sketch, "E338", {"start": v(12.56, -2.22) * mm, "end": v(12.58, -2.22) * mm});
            skLineSegment(sketch, "E339", {"start": v(12.58, -2.22) * mm, "end": v(12.63, -2.2) * mm});
            skLineSegment(sketch, "E340", {"start": v(12.63, -2.2) * mm, "end": v(12.65, -2.2) * mm});
            skLineSegment(sketch, "E341", {"start": v(12.65, -2.2) * mm, "end": v(12.7, -2.18) * mm});
            skLineSegment(sketch, "E342", {"start": v(12.7, -2.18) * mm, "end": v(12.73, -2.2) * mm});
            skLineSegment(sketch, "E343", {"start": v(12.73, -2.2) * mm, "end": v(12.76, -2.18) * mm});
            skLineSegment(sketch, "E344", {"start": v(12.76, -2.18) * mm, "end": v(12.8, -2.2) * mm});
            skLineSegment(sketch, "E345", {"start": v(12.8, -2.2) * mm, "end": v(12.83, -2.19) * mm});
            skLineSegment(sketch, "E346", {"start": v(12.83, -2.19) * mm, "end": v(12.87, -2.22) * mm});
            skLineSegment(sketch, "E347", {"start": v(12.87, -2.22) * mm, "end": v(12.9, -2.2) * mm});
            skLineSegment(sketch, "E348", {"start": v(12.9, -2.2) * mm, "end": v(12.94, -2.24) * mm});
            skLineSegment(sketch, "E349", {"start": v(12.94, -2.24) * mm, "end": v(12.96, -2.23) * mm});
            skLineSegment(sketch, "E350", {"start": v(12.96, -2.23) * mm, "end": v(13.01, -2.27) * mm});
            skLineSegment(sketch, "E351", {"start": v(13.01, -2.27) * mm, "end": v(13.03, -2.26) * mm});
            skLineSegment(sketch, "E352", {"start": v(13.03, -2.26) * mm, "end": v(13.08, -2.3) * mm});
            skLineSegment(sketch, "E353", {"start": v(13.08, -2.3) * mm, "end": v(13.1, -2.3) * mm});
            skLineSegment(sketch, "E354", {"start": v(13.1, -2.3) * mm, "end": v(13.15, -2.35) * mm});
            skLineSegment(sketch, "E355", {"start": v(13.15, -2.35) * mm, "end": v(13.17, -2.34) * mm});
            skLineSegment(sketch, "E356", {"start": v(13.17, -2.34) * mm, "end": v(13.23, -2.4) * mm});
            skLineSegment(sketch, "E357", {"start": v(13.23, -2.4) * mm, "end": v(13.24, -2.4) * mm});
            skLineSegment(sketch, "E358", {"start": v(13.24, -2.4) * mm, "end": v(13.3, -2.45) * mm});
            skLineSegment(sketch, "E359", {"start": v(13.3, -2.45) * mm, "end": v(13.3, -2.45) * mm});
            skLineSegment(sketch, "E360", {"start": v(13.3, -2.45) * mm, "end": v(13.57, -2.73) * mm});
            skLineSegment(sketch, "E361", {"start": v(13.57, -2.73) * mm, "end": v(13.6, -2.75) * mm});
            skLineSegment(sketch, "E362", {"start": v(13.6, -2.75) * mm, "end": v(13.61, -2.77) * mm});
            skLineSegment(sketch, "E363", {"start": v(13.61, -2.77) * mm, "end": v(13.64, -2.8) * mm});
            skLineSegment(sketch, "E364", {"start": v(13.64, -2.8) * mm, "end": v(13.66, -2.81) * mm});
            skLineSegment(sketch, "E365", {"start": v(13.66, -2.81) * mm, "end": v(13.7, -2.84) * mm});
            skLineSegment(sketch, "E366", {"start": v(13.7, -2.84) * mm, "end": v(13.73, -2.87) * mm});
            skLineSegment(sketch, "E367", {"start": v(13.73, -2.87) * mm, "end": v(13.77, -2.9) * mm});
            skLineSegment(sketch, "E368", {"start": v(13.77, -2.9) * mm, "end": v(13.8, -2.92) * mm});
            skLineSegment(sketch, "E369", {"start": v(13.8, -2.92) * mm, "end": v(13.86, -2.96) * mm});
            skLineSegment(sketch, "E370", {"start": v(13.86, -2.96) * mm, "end": v(13.9, -2.99) * mm});
            skLineSegment(sketch, "E371", {"start": v(13.9, -2.99) * mm, "end": v(13.93, -3) * mm});
            skLineSegment(sketch, "E372", {"start": v(13.93, -3) * mm, "end": v(13.95, -3.02) * mm});
            skLineSegment(sketch, "E373", {"start": v(13.95, -3.02) * mm, "end": v(13.98, -3.03) * mm});
            skLineSegment(sketch, "E374", {"start": v(13.98, -3.03) * mm, "end": v(14.05, -3.06) * mm});
            skLineSegment(sketch, "E375", {"start": v(14.05, -3.06) * mm, "end": v(14.12, -3.1) * mm});
            skLineSegment(sketch, "E376", {"start": v(14.12, -3.1) * mm, "end": v(14.2, -3.14) * mm});
            skLineSegment(sketch, "E377", {"start": v(14.2, -3.14) * mm, "end": v(14.31, -3.18) * mm});
            skLineSegment(sketch, "E378", {"start": v(14.31, -3.18) * mm, "end": v(14.43, -3.22) * mm});
            skLineSegment(sketch, "E379", {"start": v(14.43, -3.22) * mm, "end": v(14.56, -3.25) * mm});
            skLineSegment(sketch, "E380", {"start": v(14.56, -3.25) * mm, "end": v(14.72, -3.29) * mm});
            skLineSegment(sketch, "E381", {"start": v(14.72, -3.29) * mm, "end": v(14.9, -3.32) * mm});
            skLineSegment(sketch, "E382", {"start": v(14.9, -3.32) * mm, "end": v(15.09, -3.34) * mm});
            skLineSegment(sketch, "E383", {"start": v(15.09, -3.34) * mm, "end": v(15.31, -3.34) * mm});
            skLineSegment(sketch, "E384", {"start": v(15.31, -3.34) * mm, "end": v(15.56, -3.33) * mm});
            skLineSegment(sketch, "E385", {"start": v(15.56, -3.33) * mm, "end": v(16.1, -3.28) * mm});
            skLineSegment(sketch, "E386", {"start": v(16.1, -3.28) * mm, "end": v(16.1, -3.27) * mm});
            skLineSegment(sketch, "E387", {"start": v(16.1, -3.27) * mm, "end": v(16.12, -3.24) * mm});
            skLineSegment(sketch, "E388", {"start": v(16.12, -3.24) * mm, "end": v(16.14, -3.2) * mm});
            skLineSegment(sketch, "E389", {"start": v(16.14, -3.2) * mm, "end": v(16.17, -3.17) * mm});
            skLineSegment(sketch, "E390", {"start": v(16.17, -3.17) * mm, "end": v(16.19, -3.14) * mm});
            skLineSegment(sketch, "E391", {"start": v(16.19, -3.14) * mm, "end": v(16.2, -3.1) * mm});
            skLineSegment(sketch, "E392", {"start": v(16.2, -3.1) * mm, "end": v(16.23, -3.07) * mm});
            skLineSegment(sketch, "E393", {"start": v(16.23, -3.07) * mm, "end": v(16.25, -3.04) * mm});
            skLineSegment(sketch, "E394", {"start": v(16.25, -3.04) * mm, "end": v(16.27, -3) * mm});
            skLineSegment(sketch, "E395", {"start": v(16.27, -3) * mm, "end": v(16.29, -2.98) * mm});
            skLineSegment(sketch, "E396", {"start": v(16.29, -2.98) * mm, "end": v(16.3, -2.94) * mm});
            skLineSegment(sketch, "E397", {"start": v(16.3, -2.94) * mm, "end": v(16.32, -2.91) * mm});
            skLineSegment(sketch, "E398", {"start": v(16.32, -2.91) * mm, "end": v(16.34, -2.88) * mm});
            skLineSegment(sketch, "E399", {"start": v(16.34, -2.88) * mm, "end": v(16.36, -2.85) * mm});
            skLineSegment(sketch, "E400", {"start": v(16.36, -2.85) * mm, "end": v(16.38, -2.81) * mm});
            skLineSegment(sketch, "E401", {"start": v(16.38, -2.81) * mm, "end": v(16.4, -2.78) * mm});
            skLineSegment(sketch, "E402", {"start": v(16.4, -2.78) * mm, "end": v(16.41, -2.75) * mm});
            skLineSegment(sketch, "E403", {"start": v(16.41, -2.75) * mm, "end": v(16.43, -2.72) * mm});
            skLineSegment(sketch, "E404", {"start": v(16.43, -2.72) * mm, "end": v(16.45, -2.69) * mm});
            skLineSegment(sketch, "E405", {"start": v(16.45, -2.69) * mm, "end": v(16.17, -2.14) * mm});
            skLineSegment(sketch, "E406", {"start": v(16.17, -2.14) * mm, "end": v(16.07, -1.96) * mm});
            skLineSegment(sketch, "E407", {"start": v(16.07, -1.96) * mm, "end": v(15.97, -1.8) * mm});
            skLineSegment(sketch, "E408", {"start": v(15.97, -1.8) * mm, "end": v(15.86, -1.65) * mm});
            skLineSegment(sketch, "E409", {"start": v(15.86, -1.65) * mm, "end": v(15.76, -1.52) * mm});
            skLineSegment(sketch, "E410", {"start": v(15.76, -1.52) * mm, "end": v(15.65, -1.4) * mm});
            skLineSegment(sketch, "E411", {"start": v(15.65, -1.4) * mm, "end": v(15.55, -1.3) * mm});
            skLineSegment(sketch, "E412", {"start": v(15.55, -1.3) * mm, "end": v(15.45, -1.2) * mm});
            skLineSegment(sketch, "E413", {"start": v(15.45, -1.2) * mm, "end": v(15.37, -1.14) * mm});
            skLineSegment(sketch, "E414", {"start": v(15.37, -1.14) * mm, "end": v(15.32, -1.1) * mm});
            skLineSegment(sketch, "E415", {"start": v(15.32, -1.1) * mm, "end": v(15.23, -1.14) * mm});
            skLineSegment(sketch, "E416", {"start": v(15.23, -1.14) * mm, "end": v(15.2, -1.12) * mm});
            skLineSegment(sketch, "E417", {"start": v(15.2, -1.12) * mm, "end": v(15.03, -1.17) * mm});
            skLineSegment(sketch, "E418", {"start": v(15.03, -1.17) * mm, "end": v(15.01, -1.14) * mm});
            skLineSegment(sketch, "E419", {"start": v(15.01, -1.14) * mm, "end": v(14.84, -1.18) * mm});
            skLineSegment(sketch, "E420", {"start": v(14.84, -1.18) * mm, "end": v(14.82, -1.14) * mm});
            skLineSegment(sketch, "E421", {"start": v(14.82, -1.14) * mm, "end": v(14.65, -1.17) * mm});
            skLineSegment(sketch, "E422", {"start": v(14.65, -1.17) * mm, "end": v(14.62, -1.12) * mm});
            skLineSegment(sketch, "E423", {"start": v(14.62, -1.12) * mm, "end": v(14.46, -1.13) * mm});
            skLineSegment(sketch, "E424", {"start": v(14.46, -1.13) * mm, "end": v(14.43, -1.07) * mm});
            skLineSegment(sketch, "E425", {"start": v(14.43, -1.07) * mm, "end": v(14.28, -1.08) * mm});
            skLineSegment(sketch, "E426", {"start": v(14.28, -1.08) * mm, "end": v(14.25, -1) * mm});
            skLineSegment(sketch, "E427", {"start": v(14.25, -1) * mm, "end": v(14.11, -1) * mm});
            skLineSegment(sketch, "E428", {"start": v(14.11, -1) * mm, "end": v(14.08, -0.91) * mm});
            skLineSegment(sketch, "E429", {"start": v(14.08, -0.91) * mm, "end": v(13.96, -0.9) * mm});
            skLineSegment(sketch, "E430", {"start": v(13.96, -0.9) * mm, "end": v(13.94, -0.8) * mm});
            skLineSegment(sketch, "E431", {"start": v(13.94, -0.8) * mm, "end": v(13.84, -0.78) * mm});
            skLineSegment(sketch, "E432", {"start": v(13.84, -0.78) * mm, "end": v(13.82, -0.66) * mm});
            skLineSegment(sketch, "E433", {"start": v(13.82, -0.66) * mm, "end": v(13.75, -0.64) * mm});
            skLineSegment(sketch, "E434", {"start": v(13.75, -0.64) * mm, "end": v(13.74, -0.52) * mm});
            skLineSegment(sketch, "E435", {"start": v(13.74, -0.52) * mm, "end": v(13.7, -0.5) * mm});
            skLineSegment(sketch, "E436", {"start": v(13.7, -0.5) * mm, "end": v(13.7, -0.5) * mm});
            skLineSegment(sketch, "E437", {"start": v(13.7, -0.5) * mm, "end": v(13.7, -0.49) * mm});
            skLineSegment(sketch, "E438", {"start": v(13.7, -0.49) * mm, "end": v(13.7, -0.35) * mm});
            skLineSegment(sketch, "E439", {"start": v(13.7, -0.35) * mm, "end": v(13.67, -0.34) * mm});
            skLineSegment(sketch, "E440", {"start": v(13.67, -0.34) * mm, "end": v(13.7, -0.08) * mm});
            skLineSegment(sketch, "E441", {"start": v(13.7, -0.08) * mm, "end": v(13.7, -0.02) * mm});
            skLineSegment(sketch, "E442", {"start": v(13.7, -0.02) * mm, "end": v(13.7, 0.02) * mm});
            skLineSegment(sketch, "E443", {"start": v(13.7, 0.02) * mm, "end": v(13.7, 0.08) * mm});
            skLineSegment(sketch, "E444", {"start": v(13.7, 0.08) * mm, "end": v(13.67, 0.35) * mm});
            skLineSegment(sketch, "E445", {"start": v(13.67, 0.35) * mm, "end": v(13.7, 0.35) * mm});
            skLineSegment(sketch, "E446", {"start": v(13.7, 0.35) * mm, "end": v(13.7, 0.5) * mm});
            skLineSegment(sketch, "E447", {"start": v(13.7, 0.5) * mm, "end": v(13.7, 0.5) * mm});
            skLineSegment(sketch, "E448", {"start": v(13.7, 0.5) * mm, "end": v(13.74, 0.52) * mm});
            skLineSegment(sketch, "E449", {"start": v(13.74, 0.52) * mm, "end": v(13.75, 0.65) * mm});
            skLineSegment(sketch, "E450", {"start": v(13.75, 0.65) * mm, "end": v(13.82, 0.67) * mm});
            skLineSegment(sketch, "E451", {"start": v(13.82, 0.67) * mm, "end": v(13.84, 0.78) * mm});
            skLineSegment(sketch, "E452", {"start": v(13.84, 0.78) * mm, "end": v(13.94, 0.8) * mm});
            skLineSegment(sketch, "E453", {"start": v(13.94, 0.8) * mm, "end": v(13.96, 0.9) * mm});
            skLineSegment(sketch, "E454", {"start": v(13.96, 0.9) * mm, "end": v(14.08, 0.91) * mm});
            skLineSegment(sketch, "E455", {"start": v(14.08, 0.91) * mm, "end": v(14.11, 1) * mm});
            skLineSegment(sketch, "E456", {"start": v(14.11, 1) * mm, "end": v(14.25, 1) * mm});
            skLineSegment(sketch, "E457", {"start": v(14.25, 1) * mm, "end": v(14.28, 1.08) * mm});
            skLineSegment(sketch, "E458", {"start": v(14.28, 1.08) * mm, "end": v(14.43, 1.08) * mm});
            skLineSegment(sketch, "E459", {"start": v(14.43, 1.08) * mm, "end": v(14.46, 1.14) * mm});
            skLineSegment(sketch, "E460", {"start": v(14.46, 1.14) * mm, "end": v(14.62, 1.12) * mm});
            skLineSegment(sketch, "E461", {"start": v(14.62, 1.12) * mm, "end": v(14.65, 1.17) * mm});
            skLineSegment(sketch, "E462", {"start": v(14.65, 1.17) * mm, "end": v(14.82, 1.14) * mm});
            skLineSegment(sketch, "E463", {"start": v(14.82, 1.14) * mm, "end": v(14.84, 1.18) * mm});
            skLineSegment(sketch, "E464", {"start": v(14.84, 1.18) * mm, "end": v(15.01, 1.14) * mm});
            skLineSegment(sketch, "E465", {"start": v(15.01, 1.14) * mm, "end": v(15.03, 1.17) * mm});
            skLineSegment(sketch, "E466", {"start": v(15.03, 1.17) * mm, "end": v(15.2, 1.12) * mm});
            skLineSegment(sketch, "E467", {"start": v(15.2, 1.12) * mm, "end": v(15.23, 1.14) * mm});
            skLineSegment(sketch, "E468", {"start": v(15.23, 1.14) * mm, "end": v(15.32, 1.11) * mm});
            skLineSegment(sketch, "E469", {"start": v(15.32, 1.11) * mm, "end": v(15.37, 1.14) * mm});
            skLineSegment(sketch, "E470", {"start": v(15.37, 1.14) * mm, "end": v(15.46, 1.2) * mm});
            skLineSegment(sketch, "E471", {"start": v(15.46, 1.2) * mm, "end": v(15.55, 1.3) * mm});
            skLineSegment(sketch, "E472", {"start": v(15.55, 1.3) * mm, "end": v(15.65, 1.4) * mm});
            skLineSegment(sketch, "E473", {"start": v(15.65, 1.4) * mm, "end": v(15.76, 1.52) * mm});
            skLineSegment(sketch, "E474", {"start": v(15.76, 1.52) * mm, "end": v(15.86, 1.65) * mm});
            skLineSegment(sketch, "E475", {"start": v(15.86, 1.65) * mm, "end": v(15.97, 1.8) * mm});
            skLineSegment(sketch, "E476", {"start": v(15.97, 1.8) * mm, "end": v(16.07, 1.97) * mm});
            skLineSegment(sketch, "E477", {"start": v(16.07, 1.97) * mm, "end": v(16.17, 2.14) * mm});
            skLineSegment(sketch, "E478", {"start": v(16.17, 2.14) * mm, "end": v(16.45, 2.69) * mm});
            skLineSegment(sketch, "E479", {"start": v(16.45, 2.69) * mm, "end": v(16.43, 2.7) * mm});
            skLineSegment(sketch, "E480", {"start": v(16.43, 2.7) * mm, "end": v(16.42, 2.74) * mm});
            skLineSegment(sketch, "E481", {"start": v(16.42, 2.74) * mm, "end": v(16.4, 2.77) * mm});
            skLineSegment(sketch, "E482", {"start": v(16.4, 2.77) * mm, "end": v(16.38, 2.8) * mm});
            skLineSegment(sketch, "E483", {"start": v(16.38, 2.8) * mm, "end": v(16.37, 2.84) * mm});
            skLineSegment(sketch, "E484", {"start": v(16.37, 2.84) * mm, "end": v(16.35, 2.87) * mm});
            skLineSegment(sketch, "E485", {"start": v(16.35, 2.87) * mm, "end": v(16.33, 2.9) * mm});
            skLineSegment(sketch, "E486", {"start": v(16.33, 2.9) * mm, "end": v(16.31, 2.93) * mm});
            skLineSegment(sketch, "E487", {"start": v(16.31, 2.93) * mm, "end": v(16.3, 2.97) * mm});
            skLineSegment(sketch, "E488", {"start": v(16.3, 2.97) * mm, "end": v(16.27, 3) * mm});
            skLineSegment(sketch, "E489", {"start": v(16.27, 3) * mm, "end": v(16.25, 3.03) * mm});
            skLineSegment(sketch, "E490", {"start": v(16.25, 3.03) * mm, "end": v(16.23, 3.07) * mm});
            skLineSegment(sketch, "E491", {"start": v(16.23, 3.07) * mm, "end": v(16.21, 3.1) * mm});
            skLineSegment(sketch, "E492", {"start": v(16.21, 3.1) * mm, "end": v(16.2, 3.13) * mm});
            skLineSegment(sketch, "E493", {"start": v(16.2, 3.13) * mm, "end": v(16.17, 3.16) * mm});
            skLineSegment(sketch, "E494", {"start": v(16.17, 3.16) * mm, "end": v(16.15, 3.2) * mm});
            skLineSegment(sketch, "E495", {"start": v(16.15, 3.2) * mm, "end": v(16.13, 3.23) * mm});
            skLineSegment(sketch, "E496", {"start": v(16.13, 3.23) * mm, "end": v(16.1, 3.26) * mm});
            skLineSegment(sketch, "E497", {"start": v(16.1, 3.26) * mm, "end": v(16.09, 3.3) * mm});
            skLineSegment(sketch, "E498", {"start": v(16.09, 3.3) * mm, "end": v(16.07, 3.32) * mm});
            skLineSegment(sketch, "E499", {"start": v(16.07, 3.32) * mm, "end": v(15.54, 3.37) * mm});
            skLineSegment(sketch, "E500", {"start": v(15.54, 3.37) * mm, "end": v(15.3, 3.38) * mm});
            skLineSegment(sketch, "E501", {"start": v(15.3, 3.38) * mm, "end": v(15.07, 3.37) * mm});
            skLineSegment(sketch, "E502", {"start": v(15.07, 3.37) * mm, "end": v(14.87, 3.35) * mm});
            skLineSegment(sketch, "E503", {"start": v(14.87, 3.35) * mm, "end": v(14.7, 3.32) * mm});
            skLineSegment(sketch, "E504", {"start": v(14.7, 3.32) * mm, "end": v(14.54, 3.29) * mm});
            skLineSegment(sketch, "E505", {"start": v(14.54, 3.29) * mm, "end": v(14.4, 3.25) * mm});
            skLineSegment(sketch, "E506", {"start": v(14.4, 3.25) * mm, "end": v(14.29, 3.2) * mm});
            skLineSegment(sketch, "E507", {"start": v(14.29, 3.2) * mm, "end": v(14.19, 3.17) * mm});
            skLineSegment(sketch, "E508", {"start": v(14.19, 3.17) * mm, "end": v(14.1, 3.13) * mm});
            skLineSegment(sketch, "E509", {"start": v(14.1, 3.13) * mm, "end": v(14.02, 3.1) * mm});
            skLineSegment(sketch, "E510", {"start": v(14.02, 3.1) * mm, "end": v(13.95, 3.06) * mm});
            skLineSegment(sketch, "E511", {"start": v(13.95, 3.06) * mm, "end": v(13.93, 3.04) * mm});
            skLineSegment(sketch, "E512", {"start": v(13.93, 3.04) * mm, "end": v(13.9, 3.03) * mm});
            skLineSegment(sketch, "E513", {"start": v(13.9, 3.03) * mm, "end": v(13.88, 3.02) * mm});
            skLineSegment(sketch, "E514", {"start": v(13.88, 3.02) * mm, "end": v(13.83, 2.98) * mm});
            skLineSegment(sketch, "E515", {"start": v(13.83, 2.98) * mm, "end": v(13.78, 2.95) * mm});
            skLineSegment(sketch, "E516", {"start": v(13.78, 2.95) * mm, "end": v(13.74, 2.92) * mm});
            skLineSegment(sketch, "E517", {"start": v(13.74, 2.92) * mm, "end": v(13.7, 2.9) * mm});
            skLineSegment(sketch, "E518", {"start": v(13.7, 2.9) * mm, "end": v(13.67, 2.86) * mm});
            skLineSegment(sketch, "E519", {"start": v(13.67, 2.86) * mm, "end": v(13.64, 2.84) * mm});
            skLineSegment(sketch, "E520", {"start": v(13.64, 2.84) * mm, "end": v(13.6, 2.81) * mm});
            skLineSegment(sketch, "E521", {"start": v(13.6, 2.81) * mm, "end": v(13.58, 2.8) * mm});
            skLineSegment(sketch, "E522", {"start": v(13.58, 2.8) * mm, "end": v(13.56, 2.77) * mm});
            skLineSegment(sketch, "E523", {"start": v(13.56, 2.77) * mm, "end": v(13.54, 2.75) * mm});
            skLineSegment(sketch, "E524", {"start": v(13.54, 2.75) * mm, "end": v(13.28, 2.48) * mm});
            skLineSegment(sketch, "E525", {"start": v(13.28, 2.48) * mm, "end": v(13.27, 2.48) * mm});
            skLineSegment(sketch, "E526", {"start": v(13.27, 2.48) * mm, "end": v(13.22, 2.42) * mm});
            skLineSegment(sketch, "E527", {"start": v(13.22, 2.42) * mm, "end": v(13.2, 2.43) * mm});
            skLineSegment(sketch, "E528", {"start": v(13.2, 2.43) * mm, "end": v(13.15, 2.37) * mm});
            skLineSegment(sketch, "E529", {"start": v(13.15, 2.37) * mm, "end": v(13.13, 2.38) * mm});
            skLineSegment(sketch, "E530", {"start": v(13.13, 2.38) * mm, "end": v(13.08, 2.32) * mm});
            skLineSegment(sketch, "E531", {"start": v(13.08, 2.32) * mm, "end": v(13.06, 2.33) * mm});
            skLineSegment(sketch, "E532", {"start": v(13.06, 2.33) * mm, "end": v(13.01, 2.29) * mm});
            skLineSegment(sketch, "E533", {"start": v(13.01, 2.29) * mm, "end": v(13, 2.3) * mm});
            skLineSegment(sketch, "E534", {"start": v(13, 2.3) * mm, "end": v(12.94, 2.26) * mm});
            skLineSegment(sketch, "E535", {"start": v(12.94, 2.26) * mm, "end": v(12.92, 2.27) * mm});
            skLineSegment(sketch, "E536", {"start": v(12.92, 2.27) * mm, "end": v(12.87, 2.23) * mm});
            skLineSegment(sketch, "E537", {"start": v(12.87, 2.23) * mm, "end": v(12.85, 2.25) * mm});
            skLineSegment(sketch, "E538", {"start": v(12.85, 2.25) * mm, "end": v(12.8, 2.21) * mm});
            skLineSegment(sketch, "E539", {"start": v(12.8, 2.21) * mm, "end": v(12.78, 2.23) * mm});
            skLineSegment(sketch, "E540", {"start": v(12.78, 2.23) * mm, "end": v(12.74, 2.2) * mm});
            skLineSegment(sketch, "E541", {"start": v(12.74, 2.2) * mm, "end": v(12.7, 2.23) * mm});
            skLineSegment(sketch, "E542", {"start": v(12.7, 2.23) * mm, "end": v(12.67, 2.2) * mm});
            skLineSegment(sketch, "E543", {"start": v(12.67, 2.2) * mm, "end": v(12.63, 2.23) * mm});
            skLineSegment(sketch, "E544", {"start": v(12.63, 2.23) * mm, "end": v(12.6, 2.22) * mm});
            skLineSegment(sketch, "E545", {"start": v(12.6, 2.22) * mm, "end": v(12.55, 2.24) * mm});
            skLineSegment(sketch, "E546", {"start": v(12.55, 2.24) * mm, "end": v(12.54, 2.24) * mm});
            skLineSegment(sketch, "E547", {"start": v(12.54, 2.24) * mm, "end": v(12.54, 2.24) * mm});
            skLineSegment(sketch, "E548", {"start": v(12.54, 2.24) * mm, "end": v(12.49, 2.28) * mm});
            skLineSegment(sketch, "E549", {"start": v(12.49, 2.28) * mm, "end": v(12.48, 2.27) * mm});
            skLineSegment(sketch, "E550", {"start": v(12.48, 2.27) * mm, "end": v(12.27, 2.46) * mm});
            skLineSegment(sketch, "E551", {"start": v(12.27, 2.46) * mm, "end": v(12.18, 2.54) * mm});
            skLineSegment(sketch, "E552", {"start": v(12.18, 2.54) * mm, "end": v(12.14, 2.57) * mm});
            skLineSegment(sketch, "E553", {"start": v(12.14, 2.57) * mm, "end": v(12.05, 2.65) * mm});
            skLineSegment(sketch, "E554", {"start": v(12.05, 2.65) * mm, "end": v(11.82, 2.82) * mm});
            skLineSegment(sketch, "E555", {"start": v(11.82, 2.82) * mm, "end": v(11.8, 2.85) * mm});
            skLineSegment(sketch, "E556", {"start": v(11.8, 2.85) * mm, "end": v(11.78, 2.87) * mm});
            skLineSegment(sketch, "E557", {"start": v(11.78, 2.87) * mm, "end": v(11.78, 2.88) * mm});
            skLineSegment(sketch, "E558", {"start": v(11.78, 2.88) * mm, "end": v(11.78, 2.9) * mm});
            skLineSegment(sketch, "E559", {"start": v(11.78, 2.9) * mm, "end": v(11.74, 2.94) * mm});
            skLineSegment(sketch, "E560", {"start": v(11.74, 2.94) * mm, "end": v(11.76, 2.97) * mm});
            skLineSegment(sketch, "E561", {"start": v(11.76, 2.97) * mm, "end": v(11.72, 3.01) * mm});
            skLineSegment(sketch, "E562", {"start": v(11.72, 3.01) * mm, "end": v(11.74, 3.06) * mm});
            skLineSegment(sketch, "E563", {"start": v(11.74, 3.06) * mm, "end": v(11.7, 3.1) * mm});
            skLineSegment(sketch, "E564", {"start": v(11.7, 3.1) * mm, "end": v(11.73, 3.16) * mm});
            skLineSegment(sketch, "E565", {"start": v(11.73, 3.16) * mm, "end": v(11.7, 3.2) * mm});
            skLineSegment(sketch, "E566", {"start": v(11.7, 3.2) * mm, "end": v(11.74, 3.28) * mm});
            skLineSegment(sketch, "E567", {"start": v(11.74, 3.28) * mm, "end": v(11.71, 3.32) * mm});
            skLineSegment(sketch, "E568", {"start": v(11.71, 3.32) * mm, "end": v(11.77, 3.42) * mm});
            skLineSegment(sketch, "E569", {"start": v(11.77, 3.42) * mm, "end": v(11.74, 3.46) * mm});
            skLineSegment(sketch, "E570", {"start": v(11.74, 3.46) * mm, "end": v(11.82, 3.58) * mm});
            skLineSegment(sketch, "E571", {"start": v(11.82, 3.58) * mm, "end": v(11.8, 3.62) * mm});
            skLineSegment(sketch, "E572", {"start": v(11.8, 3.62) * mm, "end": v(11.9, 3.76) * mm});
            skLineSegment(sketch, "E573", {"start": v(11.9, 3.76) * mm, "end": v(11.88, 3.8) * mm});
            skLineSegment(sketch, "E574", {"start": v(11.88, 3.8) * mm, "end": v(12, 3.95) * mm});
            skLineSegment(sketch, "E575", {"start": v(12, 3.95) * mm, "end": v(12, 3.98) * mm});
            skLineSegment(sketch, "E576", {"start": v(12, 3.98) * mm, "end": v(12.16, 4.15) * mm});
            skLineSegment(sketch, "E577", {"start": v(12.16, 4.15) * mm, "end": v(12.15, 4.18) * mm});
            skLineSegment(sketch, "E578", {"start": v(12.15, 4.18) * mm, "end": v(12.3, 4.33) * mm});
            skLineSegment(sketch, "E579", {"start": v(12.3, 4.33) * mm, "end": v(12.3, 4.34) * mm});
            skLineSegment(sketch, "E580", {"start": v(12.3, 4.34) * mm, "end": v(12.32, 4.36) * mm});
            skLineSegment(sketch, "E581", {"start": v(12.32, 4.36) * mm, "end": v(12.32, 4.37) * mm});
            skLineSegment(sketch, "E582", {"start": v(12.32, 4.37) * mm, "end": v(12.34, 4.41) * mm});
            skLineSegment(sketch, "E583", {"start": v(12.34, 4.41) * mm, "end": v(12.36, 4.49) * mm});
            skLineSegment(sketch, "E584", {"start": v(12.36, 4.49) * mm, "end": v(12.39, 4.58) * mm});
            skLineSegment(sketch, "E585", {"start": v(12.39, 4.58) * mm, "end": v(12.41, 4.68) * mm});
            skLineSegment(sketch, "E586", {"start": v(12.41, 4.68) * mm, "end": v(12.44, 4.8) * mm});
            skLineSegment(sketch, "E587", {"start": v(12.44, 4.8) * mm, "end": v(12.46, 4.91) * mm});
            skLineSegment(sketch, "E588", {"start": v(12.46, 4.91) * mm, "end": v(12.49, 5.04) * mm});
            skLineSegment(sketch, "E589", {"start": v(12.49, 5.04) * mm, "end": v(12.5, 5.17) * mm});
            skLineSegment(sketch, "E590", {"start": v(12.5, 5.17) * mm, "end": v(12.52, 5.3) * mm});
            skLineSegment(sketch, "E591", {"start": v(12.52, 5.3) * mm, "end": v(12.54, 5.46) * mm});
            skLineSegment(sketch, "E592", {"start": v(12.54, 5.46) * mm, "end": v(12.55, 5.61) * mm});
            skLineSegment(sketch, "E593", {"start": v(12.55, 5.61) * mm, "end": v(12.6, 6.41) * mm});
            skLineSegment(sketch, "E594", {"start": v(12.6, 6.41) * mm, "end": v(12.59, 6.42) * mm});
            skLineSegment(sketch, "E595", {"start": v(12.59, 6.42) * mm, "end": v(12.51, 6.47) * mm});
            skLineSegment(sketch, "E596", {"start": v(12.51, 6.47) * mm, "end": v(12.43, 6.51) * mm});
            skLineSegment(sketch, "E597", {"start": v(12.43, 6.51) * mm, "end": v(12.35, 6.56) * mm});
            skLineSegment(sketch, "E598", {"start": v(12.35, 6.56) * mm, "end": v(12.27, 6.6) * mm});
            skLineSegment(sketch, "E599", {"start": v(12.27, 6.6) * mm, "end": v(12.18, 6.65) * mm});
            skLineSegment(sketch, "E600", {"start": v(12.18, 6.65) * mm, "end": v(12.1, 6.7) * mm});
            skLineSegment(sketch, "E601", {"start": v(12.1, 6.7) * mm, "end": v(12, 6.74) * mm});
            skLineSegment(sketch, "E602", {"start": v(12, 6.74) * mm, "end": v(11.92, 6.8) * mm});
            skLineSegment(sketch, "E603", {"start": v(11.92, 6.8) * mm, "end": v(11.83, 6.84) * mm});
            skLineSegment(sketch, "E604", {"start": v(11.83, 6.84) * mm, "end": v(11.74, 6.88) * mm});
            skLineSegment(sketch, "E605", {"start": v(11.74, 6.88) * mm, "end": v(11.7, 6.9) * mm});
            skLineSegment(sketch, "E606", {"start": v(11.7, 6.9) * mm, "end": v(11.07, 6.46) * mm});
            skLineSegment(sketch, "E607", {"start": v(11.07, 6.46) * mm, "end": v(10.95, 6.36) * mm});
            skLineSegment(sketch, "E608", {"start": v(10.95, 6.36) * mm, "end": v(10.83, 6.27) * mm});
            skLineSegment(sketch, "E609", {"start": v(10.83, 6.27) * mm, "end": v(10.72, 6.17) * mm});
            skLineSegment(sketch, "E610", {"start": v(10.72, 6.17) * mm, "end": v(10.62, 6.08) * mm});
            skLineSegment(sketch, "E611", {"start": v(10.62, 6.08) * mm, "end": v(10.52, 6) * mm});
            skLineSegment(sketch, "E612", {"start": v(10.52, 6) * mm, "end": v(10.44, 5.9) * mm});
            skLineSegment(sketch, "E613", {"start": v(10.44, 5.9) * mm, "end": v(10.36, 5.83) * mm});
            skLineSegment(sketch, "E614", {"start": v(10.36, 5.83) * mm, "end": v(10.28, 5.75) * mm});
            skLineSegment(sketch, "E615", {"start": v(10.28, 5.75) * mm, "end": v(10.2, 5.67) * mm});
            skLineSegment(sketch, "E616", {"start": v(10.2, 5.67) * mm, "end": v(10.14, 5.6) * mm});
            skLineSegment(sketch, "E617", {"start": v(10.14, 5.6) * mm, "end": v(10.1, 5.55) * mm});
            skLineSegment(sketch, "E618", {"start": v(10.1, 5.55) * mm, "end": v(10.1, 5.54) * mm});
            skLineSegment(sketch, "E619", {"start": v(10.1, 5.54) * mm, "end": v(10.06, 5.5) * mm});
            skLineSegment(sketch, "E620", {"start": v(10.06, 5.5) * mm, "end": v(10, 5.43) * mm});
            skLineSegment(sketch, "E621", {"start": v(10, 5.43) * mm, "end": v(9.94, 5.35) * mm});
            skLineSegment(sketch, "E622", {"start": v(9.94, 5.35) * mm, "end": v(9.9, 5.28) * mm});
            skLineSegment(sketch, "E623", {"start": v(9.9, 5.28) * mm, "end": v(9.85, 5.23) * mm});
            skLineSegment(sketch, "E624", {"start": v(9.85, 5.23) * mm, "end": v(9.8, 5.17) * mm});
            skLineSegment(sketch, "E625", {"start": v(9.8, 5.17) * mm, "end": v(9.77, 5.1) * mm});
            skLineSegment(sketch, "E626", {"start": v(9.77, 5.1) * mm, "end": v(9.73, 5.05) * mm});
            skLineSegment(sketch, "E627", {"start": v(9.73, 5.05) * mm, "end": v(9.68, 4.98) * mm});
            skLineSegment(sketch, "E628", {"start": v(9.68, 4.98) * mm, "end": v(9.65, 4.93) * mm});
            skLineSegment(sketch, "E629", {"start": v(9.65, 4.93) * mm, "end": v(9.43, 4.58) * mm});
            skLineSegment(sketch, "E630", {"start": v(9.43, 4.58) * mm, "end": v(9.43, 4.58) * mm});
            skLineSegment(sketch, "E631", {"start": v(9.43, 4.58) * mm, "end": v(9.4, 4.53) * mm});
            skLineSegment(sketch, "E632", {"start": v(9.4, 4.53) * mm, "end": v(9.39, 4.53) * mm});
            skLineSegment(sketch, "E633", {"start": v(9.39, 4.53) * mm, "end": v(9.36, 4.48) * mm});
            skLineSegment(sketch, "E634", {"start": v(9.36, 4.48) * mm, "end": v(9.35, 4.48) * mm});
            skLineSegment(sketch, "E635", {"start": v(9.35, 4.48) * mm, "end": v(9.32, 4.44) * mm});
            skLineSegment(sketch, "E636", {"start": v(9.32, 4.44) * mm, "end": v(9.3, 4.45) * mm});
            skLineSegment(sketch, "E637", {"start": v(9.3, 4.45) * mm, "end": v(9.28, 4.41) * mm});
            skLineSegment(sketch, "E638", {"start": v(9.28, 4.41) * mm, "end": v(9.27, 4.42) * mm});
            skLineSegment(sketch, "E639", {"start": v(9.27, 4.42) * mm, "end": v(9.24, 4.39) * mm});
            skLineSegment(sketch, "E640", {"start": v(9.24, 4.39) * mm, "end": v(9.2, 4.37) * mm});
            skLineSegment(sketch, "E641", {"start": v(9.2, 4.37) * mm, "end": v(9.17, 4.35) * mm});
            skLineSegment(sketch, "E642", {"start": v(9.17, 4.35) * mm, "end": v(9.13, 4.34) * mm});
            skLineSegment(sketch, "E643", {"start": v(9.13, 4.34) * mm, "end": v(9.1, 4.33) * mm});
            skLineSegment(sketch, "E644", {"start": v(9.1, 4.33) * mm, "end": v(9.07, 4.33) * mm});
            skLineSegment(sketch, "E645", {"start": v(9.07, 4.33) * mm, "end": v(9.07, 4.33) * mm});
            skLineSegment(sketch, "E646", {"start": v(9.07, 4.33) * mm, "end": v(9.06, 4.33) * mm});
            skLineSegment(sketch, "E647", {"start": v(9.06, 4.33) * mm, "end": v(9.04, 4.34) * mm});
            skLineSegment(sketch, "E648", {"start": v(9.04, 4.34) * mm, "end": v(9.03, 4.34) * mm});
            skLineSegment(sketch, "E649", {"start": v(9.03, 4.34) * mm, "end": v(8.8, 4.43) * mm});
            skLineSegment(sketch, "E650", {"start": v(8.8, 4.43) * mm, "end": v(8.64, 4.49) * mm});
            skLineSegment(sketch, "E651", {"start": v(8.64, 4.49) * mm, "end": v(8.57, 4.52) * mm});
            skLineSegment(sketch, "E652", {"start": v(8.57, 4.52) * mm, "end": v(8.41, 4.57) * mm});
            skLineSegment(sketch, "E653", {"start": v(8.41, 4.57) * mm, "end": v(8.17, 4.65) * mm});
            skLineSegment(sketch, "E654", {"start": v(8.17, 4.65) * mm, "end": v(8.16, 4.66) * mm});
            skLineSegment(sketch, "E655", {"start": v(8.16, 4.66) * mm, "end": v(8.15, 4.67) * mm});
            skLineSegment(sketch, "E656", {"start": v(8.15, 4.67) * mm, "end": v(8.14, 4.67) * mm});
            skLineSegment(sketch, "E657", {"start": v(8.14, 4.67) * mm, "end": v(8.14, 4.68) * mm});
            skLineSegment(sketch, "E658", {"start": v(8.14, 4.68) * mm, "end": v(8.11, 4.7) * mm});
            skLineSegment(sketch, "E659", {"start": v(8.11, 4.7) * mm, "end": v(8.09, 4.75) * mm});
            skLineSegment(sketch, "E660", {"start": v(8.09, 4.75) * mm, "end": v(8.06, 4.77) * mm});
            skLineSegment(sketch, "E661", {"start": v(8.06, 4.77) * mm, "end": v(8.06, 4.8) * mm});
            skLineSegment(sketch, "E662", {"start": v(8.06, 4.8) * mm, "end": v(8.04, 4.84) * mm});
            skLineSegment(sketch, "E663", {"start": v(8.04, 4.84) * mm, "end": v(8.03, 4.86) * mm});
            skLineSegment(sketch, "E664", {"start": v(8.03, 4.86) * mm, "end": v(8.03, 4.92) * mm});
            skLineSegment(sketch, "E665", {"start": v(8.03, 4.92) * mm, "end": v(8.01, 4.93) * mm});
            skLineSegment(sketch, "E666", {"start": v(8.01, 4.93) * mm, "end": v(8.02, 5) * mm});
            skLineSegment(sketch, "E667", {"start": v(8.02, 5) * mm, "end": v(8, 5) * mm});
            skLineSegment(sketch, "E668", {"start": v(8, 5) * mm, "end": v(8.02, 5.08) * mm});
            skLineSegment(sketch, "E669", {"start": v(8.02, 5.08) * mm, "end": v(8, 5.09) * mm});
            skLineSegment(sketch, "E670", {"start": v(8, 5.09) * mm, "end": v(8.02, 5.17) * mm});
            skLineSegment(sketch, "E671", {"start": v(8.02, 5.17) * mm, "end": v(8, 5.18) * mm});
            skLineSegment(sketch, "E672", {"start": v(8, 5.18) * mm, "end": v(8.02, 5.27) * mm});
            skLineSegment(sketch, "E673", {"start": v(8.02, 5.27) * mm, "end": v(8.01, 5.28) * mm});
            skLineSegment(sketch, "E674", {"start": v(8.01, 5.28) * mm, "end": v(8.04, 5.39) * mm});
            skLineSegment(sketch, "E675", {"start": v(8.04, 5.39) * mm, "end": v(8.03, 5.4) * mm});
            skLineSegment(sketch, "E676", {"start": v(8.03, 5.4) * mm, "end": v(8.1, 5.72) * mm});
            skLineSegment(sketch, "E677", {"start": v(8.1, 5.72) * mm, "end": v(8.11, 5.73) * mm});
            skLineSegment(sketch, "E678", {"start": v(8.11, 5.73) * mm, "end": v(8.12, 5.76) * mm});
            skLineSegment(sketch, "E679", {"start": v(8.12, 5.76) * mm, "end": v(8.12, 5.8) * mm});
            skLineSegment(sketch, "E680", {"start": v(8.12, 5.8) * mm, "end": v(8.13, 5.84) * mm});
            skLineSegment(sketch, "E681", {"start": v(8.13, 5.84) * mm, "end": v(8.13, 5.9) * mm});
            skLineSegment(sketch, "E682", {"start": v(8.13, 5.9) * mm, "end": v(8.14, 5.96) * mm});
            skLineSegment(sketch, "E683", {"start": v(8.14, 5.96) * mm, "end": v(8.14, 6.03) * mm});
            skLineSegment(sketch, "E684", {"start": v(8.14, 6.03) * mm, "end": v(8.15, 6.12) * mm});
            skLineSegment(sketch, "E685", {"start": v(8.15, 6.12) * mm, "end": v(8.15, 6.2) * mm});
            skLineSegment(sketch, "E686", {"start": v(8.15, 6.2) * mm, "end": v(8.15, 6.25) * mm});
            skLineSegment(sketch, "E687", {"start": v(8.15, 6.25) * mm, "end": v(8.15, 6.27) * mm});
            skLineSegment(sketch, "E688", {"start": v(8.15, 6.27) * mm, "end": v(8.15, 6.33) * mm});
            skLineSegment(sketch, "E689", {"start": v(8.15, 6.33) * mm, "end": v(8.15, 6.44) * mm});
            skLineSegment(sketch, "E690", {"start": v(8.15, 6.44) * mm, "end": v(8.14, 6.56) * mm});
            skLineSegment(sketch, "E691", {"start": v(8.14, 6.56) * mm, "end": v(8.14, 6.67) * mm});
            skLineSegment(sketch, "E692", {"start": v(8.14, 6.67) * mm, "end": v(8.13, 6.78) * mm});
            skLineSegment(sketch, "E693", {"start": v(8.13, 6.78) * mm, "end": v(8.12, 6.9) * mm});
            skLineSegment(sketch, "E694", {"start": v(8.12, 6.9) * mm, "end": v(8.11, 7.02) * mm});
            skLineSegment(sketch, "E695", {"start": v(8.11, 7.02) * mm, "end": v(8.1, 7.16) * mm});
            skLineSegment(sketch, "E696", {"start": v(8.1, 7.16) * mm, "end": v(8.08, 7.3) * mm});
            skLineSegment(sketch, "E697", {"start": v(8.08, 7.3) * mm, "end": v(8.06, 7.46) * mm});
            skLineSegment(sketch, "E698", {"start": v(8.06, 7.46) * mm, "end": v(7.93, 8.32) * mm});
            skLineSegment(sketch, "E699", {"start": v(7.93, 8.32) * mm, "end": v(7.93, 8.32) * mm});
            skLineSegment(sketch, "E700", {"start": v(7.93, 8.32) * mm, "end": v(7.76, 8.37) * mm});
            skLineSegment(sketch, "E701", {"start": v(7.76, 8.37) * mm, "end": v(7.58, 8.41) * mm});
            skLineSegment(sketch, "E702", {"start": v(7.58, 8.41) * mm, "end": v(7.4, 8.46) * mm});
            skLineSegment(sketch, "E703", {"start": v(7.4, 8.46) * mm, "end": v(7.22, 8.5) * mm});
            skLineSegment(sketch, "E704", {"start": v(7.22, 8.5) * mm, "end": v(7.03, 8.55) * mm});
            skLineSegment(sketch, "E705", {"start": v(7.03, 8.55) * mm, "end": v(6.86, 8.6) * mm});
            skLineSegment(sketch, "E706", {"start": v(6.86, 8.6) * mm, "end": v(6.42, 8.03) * mm});
            skLineSegment(sketch, "E707", {"start": v(6.42, 8.03) * mm, "end": v(6.33, 7.9) * mm});
            skLineSegment(sketch, "E708", {"start": v(6.33, 7.9) * mm, "end": v(6.25, 7.8) * mm});
            skLineSegment(sketch, "E709", {"start": v(6.25, 7.8) * mm, "end": v(6.17, 7.69) * mm});
            skLineSegment(sketch, "E710", {"start": v(6.17, 7.69) * mm, "end": v(6.09, 7.58) * mm});
            skLineSegment(sketch, "E711", {"start": v(6.09, 7.58) * mm, "end": v(6.01, 7.47) * mm});
            skLineSegment(sketch, "E712", {"start": v(6.01, 7.47) * mm, "end": v(5.94, 7.35) * mm});
            skLineSegment(sketch, "E713", {"start": v(5.94, 7.35) * mm, "end": v(5.87, 7.24) * mm});
            skLineSegment(sketch, "E714", {"start": v(5.87, 7.24) * mm, "end": v(5.8, 7.13) * mm});
            skLineSegment(sketch, "E715", {"start": v(5.8, 7.13) * mm, "end": v(5.75, 7.05) * mm});
            skLineSegment(sketch, "E716", {"start": v(5.75, 7.05) * mm, "end": v(5.7, 6.96) * mm});
            skLineSegment(sketch, "E717", {"start": v(5.7, 6.96) * mm, "end": v(5.67, 6.9) * mm});
            skLineSegment(sketch, "E718", {"start": v(5.67, 6.9) * mm, "end": v(5.65, 6.87) * mm});
            skLineSegment(sketch, "E719", {"start": v(5.65, 6.87) * mm, "end": v(5.63, 6.82) * mm});
            skLineSegment(sketch, "E720", {"start": v(5.63, 6.82) * mm, "end": v(5.58, 6.72) * mm});
            skLineSegment(sketch, "E721", {"start": v(5.58, 6.72) * mm, "end": v(5.53, 6.63) * mm});
            skLineSegment(sketch, "E722", {"start": v(5.53, 6.63) * mm, "end": v(5.49, 6.55) * mm});
            skLineSegment(sketch, "E723", {"start": v(5.49, 6.55) * mm, "end": v(5.45, 6.46) * mm});
            skLineSegment(sketch, "E724", {"start": v(5.45, 6.46) * mm, "end": v(5.4, 6.37) * mm});
            skLineSegment(sketch, "E725", {"start": v(5.4, 6.37) * mm, "end": v(5.37, 6.3) * mm});
            skLineSegment(sketch, "E726", {"start": v(5.37, 6.3) * mm, "end": v(5.33, 6.2) * mm});
            skLineSegment(sketch, "E727", {"start": v(5.33, 6.2) * mm, "end": v(5.3, 6.12) * mm});
            skLineSegment(sketch, "E728", {"start": v(5.3, 6.12) * mm, "end": v(5.14, 5.74) * mm});
            skLineSegment(sketch, "E729", {"start": v(5.14, 5.74) * mm, "end": v(5.13, 5.74) * mm});
            skLineSegment(sketch, "E730", {"start": v(5.13, 5.74) * mm, "end": v(5.11, 5.69) * mm});
            skLineSegment(sketch, "E731", {"start": v(5.11, 5.69) * mm, "end": v(5.1, 5.69) * mm});
            skLineSegment(sketch, "E732", {"start": v(5.1, 5.69) * mm, "end": v(5.08, 5.64) * mm});
            skLineSegment(sketch, "E733", {"start": v(5.08, 5.64) * mm, "end": v(5.07, 5.64) * mm});
            skLineSegment(sketch, "E734", {"start": v(5.07, 5.64) * mm, "end": v(5.05, 5.6) * mm});
            skLineSegment(sketch, "E735", {"start": v(5.05, 5.6) * mm, "end": v(5.04, 5.6) * mm});
            skLineSegment(sketch, "E736", {"start": v(5.04, 5.6) * mm, "end": v(5.02, 5.57) * mm});
            skLineSegment(sketch, "E737", {"start": v(5.02, 5.57) * mm, "end": v(5, 5.55) * mm});
            skLineSegment(sketch, "E738", {"start": v(5, 5.55) * mm, "end": v(4.97, 5.53) * mm});
            skLineSegment(sketch, "E739", {"start": v(4.97, 5.53) * mm, "end": v(4.94, 5.51) * mm});
            skLineSegment(sketch, "E740", {"start": v(4.94, 5.51) * mm, "end": v(4.91, 5.5) * mm});
            skLineSegment(sketch, "E741", {"start": v(4.91, 5.5) * mm, "end": v(4.9, 5.5) * mm});
            skLineSegment(sketch, "E742", {"start": v(4.9, 5.5) * mm, "end": v(4.89, 5.5) * mm});
            skLineSegment(sketch, "E743", {"start": v(4.89, 5.5) * mm, "end": v(4.88, 5.5) * mm});
            skLineSegment(sketch, "E744", {"start": v(4.88, 5.5) * mm, "end": v(4.86, 5.5) * mm});
            skLineSegment(sketch, "E745", {"start": v(4.86, 5.5) * mm, "end": v(4.86, 5.5) * mm});
            skLineSegment(sketch, "E746", {"start": v(4.86, 5.5) * mm, "end": v(4.66, 5.53) * mm});
            skLineSegment(sketch, "E747", {"start": v(4.66, 5.53) * mm, "end": v(4.46, 5.56) * mm});
            skLineSegment(sketch, "E748", {"start": v(4.46, 5.56) * mm, "end": v(4.34, 5.58) * mm});
            skLineSegment(sketch, "E749", {"start": v(4.34, 5.58) * mm, "end": v(4.14, 5.61) * mm});
            skLineSegment(sketch, "E750", {"start": v(4.14, 5.61) * mm, "end": v(3.94, 5.64) * mm});
            skLineSegment(sketch, "E751", {"start": v(3.94, 5.64) * mm, "end": v(3.93, 5.64) * mm});
            skLineSegment(sketch, "E752", {"start": v(3.93, 5.64) * mm, "end": v(3.92, 5.65) * mm});
            skLineSegment(sketch, "E753", {"start": v(3.92, 5.65) * mm, "end": v(3.91, 5.65) * mm});
            skLineSegment(sketch, "E754", {"start": v(3.91, 5.65) * mm, "end": v(3.9, 5.66) * mm});
            skLineSegment(sketch, "E755", {"start": v(3.9, 5.66) * mm, "end": v(3.89, 5.67) * mm});
            skLineSegment(sketch, "E756", {"start": v(3.89, 5.67) * mm, "end": v(3.87, 5.69) * mm});
            skLineSegment(sketch, "E757", {"start": v(3.87, 5.69) * mm, "end": v(3.85, 5.71) * mm});
            skLineSegment(sketch, "E758", {"start": v(3.85, 5.71) * mm, "end": v(3.82, 5.75) * mm});
            skLineSegment(sketch, "E759", {"start": v(3.82, 5.75) * mm, "end": v(3.8, 5.79) * mm});
            skLineSegment(sketch, "E760", {"start": v(3.8, 5.79) * mm, "end": v(3.79, 5.83) * mm});
            skLineSegment(sketch, "E761", {"start": v(3.79, 5.83) * mm, "end": v(3.77, 5.86) * mm});
            skLineSegment(sketch, "E762", {"start": v(3.77, 5.86) * mm, "end": v(3.77, 5.9) * mm});
            skLineSegment(sketch, "E763", {"start": v(3.77, 5.9) * mm, "end": v(3.76, 5.93) * mm});
            skLineSegment(sketch, "E764", {"start": v(3.76, 5.93) * mm, "end": v(3.75, 5.96) * mm});
            skLineSegment(sketch, "E765", {"start": v(3.75, 5.96) * mm, "end": v(3.74, 6.02) * mm});
            skLineSegment(sketch, "E766", {"start": v(3.74, 6.02) * mm, "end": v(3.74, 6.02) * mm});
            skLineSegment(sketch, "E767", {"start": v(3.74, 6.02) * mm, "end": v(3.73, 6.1) * mm});
            skLineSegment(sketch, "E768", {"start": v(3.73, 6.1) * mm, "end": v(3.73, 6.1) * mm});
            skLineSegment(sketch, "E769", {"start": v(3.73, 6.1) * mm, "end": v(3.72, 6.38) * mm});
            skLineSegment(sketch, "E770", {"start": v(3.72, 6.38) * mm, "end": v(3.71, 6.44) * mm});
            skLineSegment(sketch, "E771", {"start": v(3.71, 6.44) * mm, "end": v(3.71, 6.48) * mm});
            skLineSegment(sketch, "E772", {"start": v(3.71, 6.48) * mm, "end": v(3.7, 6.54) * mm});
            skLineSegment(sketch, "E773", {"start": v(3.7, 6.54) * mm, "end": v(3.7, 6.61) * mm});
            skLineSegment(sketch, "E774", {"start": v(3.7, 6.61) * mm, "end": v(3.7, 6.69) * mm});
            skLineSegment(sketch, "E775", {"start": v(3.7, 6.69) * mm, "end": v(3.68, 6.77) * mm});
            skLineSegment(sketch, "E776", {"start": v(3.68, 6.77) * mm, "end": v(3.67, 6.86) * mm});
            skLineSegment(sketch, "E777", {"start": v(3.67, 6.86) * mm, "end": v(3.65, 6.96) * mm});
            skLineSegment(sketch, "E778", {"start": v(3.65, 6.96) * mm, "end": v(3.64, 7.04) * mm});
            skLineSegment(sketch, "E779", {"start": v(3.64, 7.04) * mm, "end": v(3.63, 7.13) * mm});
            skLineSegment(sketch, "E780", {"start": v(3.63, 7.13) * mm, "end": v(3.61, 7.19) * mm});
            skLineSegment(sketch, "E781", {"start": v(3.61, 7.19) * mm, "end": v(3.6, 7.23) * mm});
            skLineSegment(sketch, "E782", {"start": v(3.6, 7.23) * mm, "end": v(3.6, 7.3) * mm});
            skLineSegment(sketch, "E783", {"start": v(3.6, 7.3) * mm, "end": v(3.57, 7.4) * mm});
            skLineSegment(sketch, "E784", {"start": v(3.57, 7.4) * mm, "end": v(3.54, 7.52) * mm});
            skLineSegment(sketch, "E785", {"start": v(3.54, 7.52) * mm, "end": v(3.51, 7.64) * mm});
            skLineSegment(sketch, "E786", {"start": v(3.51, 7.64) * mm, "end": v(3.48, 7.77) * mm});
            skLineSegment(sketch, "E787", {"start": v(3.48, 7.77) * mm, "end": v(3.45, 7.9) * mm});
            skLineSegment(sketch, "E788", {"start": v(3.45, 7.9) * mm, "end": v(3.4, 8.05) * mm});
            skLineSegment(sketch, "E789", {"start": v(3.4, 8.05) * mm, "end": v(3.36, 8.2) * mm});
            skLineSegment(sketch, "E790", {"start": v(3.36, 8.2) * mm, "end": v(3.3, 8.37) * mm});
            skLineSegment(sketch, "E791", {"start": v(3.3, 8.37) * mm, "end": v(3.04, 9.2) * mm});
            skLineSegment(sketch, "E792", {"start": v(3.04, 9.2) * mm, "end": v(2.93, 9.21) * mm});
            skLineSegment(sketch, "E793", {"start": v(2.93, 9.21) * mm, "end": v(2.66, 9.23) * mm});
            skLineSegment(sketch, "E794", {"start": v(2.66, 9.23) * mm, "end": v(2.38, 9.26) * mm});
            skLineSegment(sketch, "E795", {"start": v(2.38, 9.26) * mm, "end": v(2.1, 9.28) * mm});
            skLineSegment(sketch, "E796", {"start": v(2.1, 9.28) * mm, "end": v(1.9, 9.29) * mm});
            skLineSegment(sketch, "E797", {"start": v(1.9, 9.29) * mm, "end": v(1.53, 8.53) * mm});
            skLineSegment(sketch, "E798", {"start": v(1.53, 8.53) * mm, "end": v(1.46, 8.4) * mm});
            skLineSegment(sketch, "E799", {"start": v(1.46, 8.4) * mm, "end": v(1.4, 8.26) * mm});
            skLineSegment(sketch, "E800", {"start": v(1.4, 8.26) * mm, "end": v(1.33, 8.11) * mm});
            skLineSegment(sketch, "E801", {"start": v(1.33, 8.11) * mm, "end": v(1.27, 7.98) * mm});
            skLineSegment(sketch, "E802", {"start": v(1.27, 7.98) * mm, "end": v(1.21, 7.84) * mm});
            skLineSegment(sketch, "E803", {"start": v(1.21, 7.84) * mm, "end": v(1.15, 7.7) * mm});
            skLineSegment(sketch, "E804", {"start": v(1.15, 7.7) * mm, "end": v(1.11, 7.59) * mm});
            skLineSegment(sketch, "E805", {"start": v(1.11, 7.59) * mm, "end": v(1.08, 7.5) * mm});
            skLineSegment(sketch, "E806", {"start": v(1.08, 7.5) * mm, "end": v(1.05, 7.43) * mm});
            skLineSegment(sketch, "E807", {"start": v(1.05, 7.43) * mm, "end": v(1.03, 7.38) * mm});
            skLineSegment(sketch, "E808", {"start": v(1.03, 7.38) * mm, "end": v(1, 7.32) * mm});
            skLineSegment(sketch, "E809", {"start": v(1, 7.32) * mm, "end": v(0.98, 7.23) * mm});
            skLineSegment(sketch, "E810", {"start": v(0.98, 7.23) * mm, "end": v(0.95, 7.14) * mm});
            skLineSegment(sketch, "E811", {"start": v(0.95, 7.14) * mm, "end": v(0.92, 7.05) * mm});
            skLineSegment(sketch, "E812", {"start": v(0.92, 7.05) * mm, "end": v(0.9, 6.97) * mm});
            skLineSegment(sketch, "E813", {"start": v(0.9, 6.97) * mm, "end": v(0.87, 6.9) * mm});
            skLineSegment(sketch, "E814", {"start": v(0.87, 6.9) * mm, "end": v(0.85, 6.81) * mm});
            skLineSegment(sketch, "E815", {"start": v(0.85, 6.81) * mm, "end": v(0.83, 6.73) * mm});
            skLineSegment(sketch, "E816", {"start": v(0.83, 6.73) * mm, "end": v(0.8, 6.66) * mm});
            skLineSegment(sketch, "E817", {"start": v(0.8, 6.66) * mm, "end": v(0.8, 6.59) * mm});
            skLineSegment(sketch, "E818", {"start": v(0.8, 6.59) * mm, "end": v(0.7, 6.19) * mm});
            skLineSegment(sketch, "E819", {"start": v(0.7, 6.19) * mm, "end": v(0.68, 6.16) * mm});
            skLineSegment(sketch, "E820", {"start": v(0.68, 6.16) * mm, "end": v(0.67, 6.12) * mm});
            skLineSegment(sketch, "E821", {"start": v(0.67, 6.12) * mm, "end": v(0.65, 6.07) * mm});
            skLineSegment(sketch, "E822", {"start": v(0.65, 6.07) * mm, "end": v(0.63, 6.04) * mm});
            skLineSegment(sketch, "E823", {"start": v(0.63, 6.04) * mm, "end": v(0.6, 6) * mm});
            skLineSegment(sketch, "E824", {"start": v(0.6, 6) * mm, "end": v(0.59, 5.98) * mm});
            skLineSegment(sketch, "E825", {"start": v(0.59, 5.98) * mm, "end": v(0.57, 5.96) * mm});
            skLineSegment(sketch, "E826", {"start": v(0.57, 5.96) * mm, "end": v(0.55, 5.94) * mm});
            skLineSegment(sketch, "E827", {"start": v(0.55, 5.94) * mm, "end": v(0.53, 5.93) * mm});
            skLineSegment(sketch, "E828", {"start": v(0.53, 5.93) * mm, "end": v(0.5, 5.92) * mm});
            skLineSegment(sketch, "E829", {"start": v(0.5, 5.92) * mm, "end": v(0.5, 5.91) * mm});
            skLineSegment(sketch, "E830", {"start": v(0.5, 5.91) * mm, "end": v(0.5, 5.9) * mm});
            skLineSegment(sketch, "E831", {"start": v(0.5, 5.9) * mm, "end": v(0.48, 5.9) * mm});
            skLineSegment(sketch, "E832", {"start": v(0.48, 5.9) * mm, "end": v(0.47, 5.9) * mm});
            skLineSegment(sketch, "E833", {"start": v(0.47, 5.9) * mm, "end": v(0.3, 5.9) * mm});
            skLineSegment(sketch, "E834", {"start": v(0.3, 5.9) * mm, "end": v(0.08, 5.9) * mm});
            skLineSegment(sketch, "E835", {"start": v(0.08, 5.9) * mm, "end": v(-0.08, 5.9) * mm});
            skLineSegment(sketch, "E836", {"start": v(-0.08, 5.9) * mm, "end": v(-0.29, 5.9) * mm});
            skLineSegment(sketch, "E837", {"start": v(-0.29, 5.9) * mm, "end": v(-0.47, 5.9) * mm});
            skLineSegment(sketch, "E838", {"start": v(-0.47, 5.9) * mm, "end": v(-0.48, 5.9) * mm});
            skLineSegment(sketch, "E839", {"start": v(-0.48, 5.9) * mm, "end": v(-0.48, 5.9) * mm});
            skLineSegment(sketch, "E840", {"start": v(-0.48, 5.9) * mm, "end": v(-0.5, 5.91) * mm});
            skLineSegment(sketch, "E841", {"start": v(-0.5, 5.91) * mm, "end": v(-0.5, 5.92) * mm});
            skLineSegment(sketch, "E842", {"start": v(-0.5, 5.92) * mm, "end": v(-0.52, 5.93) * mm});
            skLineSegment(sketch, "E843", {"start": v(-0.52, 5.93) * mm, "end": v(-0.54, 5.94) * mm});
            skLineSegment(sketch, "E844", {"start": v(-0.54, 5.94) * mm, "end": v(-0.57, 5.97) * mm});
            skLineSegment(sketch, "E845", {"start": v(-0.57, 5.97) * mm, "end": v(-0.6, 6) * mm});
            skLineSegment(sketch, "E846", {"start": v(-0.6, 6) * mm, "end": v(-0.62, 6.03) * mm});
            skLineSegment(sketch, "E847", {"start": v(-0.62, 6.03) * mm, "end": v(-0.64, 6.07) * mm});
            skLineSegment(sketch, "E848", {"start": v(-0.64, 6.07) * mm, "end": v(-0.66, 6.12) * mm});
            skLineSegment(sketch, "E849", {"start": v(-0.66, 6.12) * mm, "end": v(-0.68, 6.14) * mm});
            skLineSegment(sketch, "E850", {"start": v(-0.68, 6.14) * mm, "end": v(-0.69, 6.2) * mm});
            skLineSegment(sketch, "E851", {"start": v(-0.69, 6.2) * mm, "end": v(-0.7, 6.2) * mm});
            skLineSegment(sketch, "E852", {"start": v(-0.7, 6.2) * mm, "end": v(-0.78, 6.58) * mm});
            skLineSegment(sketch, "E853", {"start": v(-0.78, 6.58) * mm, "end": v(-0.8, 6.65) * mm});
            skLineSegment(sketch, "E854", {"start": v(-0.8, 6.65) * mm, "end": v(-0.82, 6.73) * mm});
            skLineSegment(sketch, "E855", {"start": v(-0.82, 6.73) * mm, "end": v(-0.85, 6.83) * mm});
            skLineSegment(sketch, "E856", {"start": v(-0.85, 6.83) * mm, "end": v(-0.88, 6.92) * mm});
            skLineSegment(sketch, "E857", {"start": v(-0.88, 6.92) * mm, "end": v(-0.9, 7.02) * mm});
            skLineSegment(sketch, "E858", {"start": v(-0.9, 7.02) * mm, "end": v(-0.94, 7.14) * mm});
            skLineSegment(sketch, "E859", {"start": v(-0.94, 7.14) * mm, "end": v(-0.98, 7.23) * mm});
            skLineSegment(sketch, "E860", {"start": v(-0.98, 7.23) * mm, "end": v(-1, 7.32) * mm});
            skLineSegment(sketch, "E861", {"start": v(-1, 7.32) * mm, "end": v(-1.03, 7.39) * mm});
            skLineSegment(sketch, "E862", {"start": v(-1.03, 7.39) * mm, "end": v(-1.05, 7.43) * mm});
            skLineSegment(sketch, "E863", {"start": v(-1.05, 7.43) * mm, "end": v(-1.07, 7.5) * mm});
            skLineSegment(sketch, "E864", {"start": v(-1.07, 7.5) * mm, "end": v(-1.1, 7.6) * mm});
            skLineSegment(sketch, "E865", {"start": v(-1.1, 7.6) * mm, "end": v(-1.15, 7.7) * mm});
            skLineSegment(sketch, "E866", {"start": v(-1.15, 7.7) * mm, "end": v(-1.19, 7.8) * mm});
            skLineSegment(sketch, "E867", {"start": v(-1.19, 7.8) * mm, "end": v(-1.24, 7.9) * mm});
            skLineSegment(sketch, "E868", {"start": v(-1.24, 7.9) * mm, "end": v(-1.28, 8.02) * mm});
            skLineSegment(sketch, "E869", {"start": v(-1.28, 8.02) * mm, "end": v(-1.34, 8.14) * mm});
            skLineSegment(sketch, "E870", {"start": v(-1.34, 8.14) * mm, "end": v(-1.4, 8.26) * mm});
            skLineSegment(sketch, "E871", {"start": v(-1.4, 8.26) * mm, "end": v(-1.45, 8.39) * mm});
            skLineSegment(sketch, "E872", {"start": v(-1.45, 8.39) * mm, "end": v(-1.52, 8.52) * mm});
            skLineSegment(sketch, "E873", {"start": v(-1.52, 8.52) * mm, "end": v(-1.9, 9.29) * mm});
            skLineSegment(sketch, "E874", {"start": v(-1.9, 9.29) * mm, "end": v(-2.13, 9.27) * mm});
            skLineSegment(sketch, "E875", {"start": v(-2.13, 9.27) * mm, "end": v(-2.5, 9.25) * mm});
            skLineSegment(sketch, "E876", {"start": v(-2.5, 9.25) * mm, "end": v(-2.86, 9.22) * mm});
            skLineSegment(sketch, "E877", {"start": v(-2.86, 9.22) * mm, "end": v(-3.03, 9.2) * mm});
            skLineSegment(sketch, "E878", {"start": v(-3.03, 9.2) * mm, "end": v(-3.28, 8.45) * mm});
            skLineSegment(sketch, "E879", {"start": v(-3.28, 8.45) * mm, "end": v(-3.32, 8.32) * mm});
            skLineSegment(sketch, "E880", {"start": v(-3.32, 8.32) * mm, "end": v(-3.36, 8.19) * mm});
            skLineSegment(sketch, "E881", {"start": v(-3.36, 8.19) * mm, "end": v(-3.4, 8.06) * mm});
            skLineSegment(sketch, "E882", {"start": v(-3.4, 8.06) * mm, "end": v(-3.44, 7.93) * mm});
            skLineSegment(sketch, "E883", {"start": v(-3.44, 7.93) * mm, "end": v(-3.47, 7.8) * mm});
            skLineSegment(sketch, "E884", {"start": v(-3.47, 7.8) * mm, "end": v(-3.5, 7.69) * mm});
            skLineSegment(sketch, "E885", {"start": v(-3.5, 7.69) * mm, "end": v(-3.53, 7.56) * mm});
            skLineSegment(sketch, "E886", {"start": v(-3.53, 7.56) * mm, "end": v(-3.56, 7.44) * mm});
            skLineSegment(sketch, "E887", {"start": v(-3.56, 7.44) * mm, "end": v(-3.58, 7.33) * mm});
            skLineSegment(sketch, "E888", {"start": v(-3.58, 7.33) * mm, "end": v(-3.6, 7.24) * mm});
            skLineSegment(sketch, "E889", {"start": v(-3.6, 7.24) * mm, "end": v(-3.61, 7.18) * mm});
            skLineSegment(sketch, "E890", {"start": v(-3.61, 7.18) * mm, "end": v(-3.63, 7.1) * mm});
            skLineSegment(sketch, "E891", {"start": v(-3.63, 7.1) * mm, "end": v(-3.64, 7) * mm});
            skLineSegment(sketch, "E892", {"start": v(-3.64, 7) * mm, "end": v(-3.66, 6.89) * mm});
            skLineSegment(sketch, "E893", {"start": v(-3.66, 6.89) * mm, "end": v(-3.68, 6.8) * mm});
            skLineSegment(sketch, "E894", {"start": v(-3.68, 6.8) * mm, "end": v(-3.69, 6.7) * mm});
            skLineSegment(sketch, "E895", {"start": v(-3.69, 6.7) * mm, "end": v(-3.7, 6.62) * mm});
            skLineSegment(sketch, "E896", {"start": v(-3.7, 6.62) * mm, "end": v(-3.7, 6.54) * mm});
            skLineSegment(sketch, "E897", {"start": v(-3.7, 6.54) * mm, "end": v(-3.7, 6.47) * mm});
            skLineSegment(sketch, "E898", {"start": v(-3.7, 6.47) * mm, "end": v(-3.71, 6.4) * mm});
            skLineSegment(sketch, "E899", {"start": v(-3.71, 6.4) * mm, "end": v(-3.73, 6.07) * mm});
            skLineSegment(sketch, "E900", {"start": v(-3.73, 6.07) * mm, "end": v(-3.73, 6.07) * mm});
            skLineSegment(sketch, "E901", {"start": v(-3.73, 6.07) * mm, "end": v(-3.74, 5.99) * mm});
            skLineSegment(sketch, "E902", {"start": v(-3.74, 5.99) * mm, "end": v(-3.75, 5.95) * mm});
            skLineSegment(sketch, "E903", {"start": v(-3.75, 5.95) * mm, "end": v(-3.76, 5.91) * mm});
            skLineSegment(sketch, "E904", {"start": v(-3.76, 5.91) * mm, "end": v(-3.77, 5.86) * mm});
            skLineSegment(sketch, "E905", {"start": v(-3.77, 5.86) * mm, "end": v(-3.78, 5.83) * mm});
            skLineSegment(sketch, "E906", {"start": v(-3.78, 5.83) * mm, "end": v(-3.8, 5.8) * mm});
            skLineSegment(sketch, "E907", {"start": v(-3.8, 5.8) * mm, "end": v(-3.8, 5.76) * mm});
            skLineSegment(sketch, "E908", {"start": v(-3.8, 5.76) * mm, "end": v(-3.83, 5.74) * mm});
            skLineSegment(sketch, "E909", {"start": v(-3.83, 5.74) * mm, "end": v(-3.85, 5.7) * mm});
            skLineSegment(sketch, "E910", {"start": v(-3.85, 5.7) * mm, "end": v(-3.87, 5.68) * mm});
            skLineSegment(sketch, "E911", {"start": v(-3.87, 5.68) * mm, "end": v(-3.9, 5.66) * mm});
            skLineSegment(sketch, "E912", {"start": v(-3.9, 5.66) * mm, "end": v(-3.9, 5.65) * mm});
            skLineSegment(sketch, "E913", {"start": v(-3.9, 5.65) * mm, "end": v(-3.92, 5.65) * mm});
            skLineSegment(sketch, "E914", {"start": v(-3.92, 5.65) * mm, "end": v(-3.93, 5.64) * mm});
            skLineSegment(sketch, "E915", {"start": v(-3.93, 5.64) * mm, "end": v(-3.95, 5.64) * mm});
            skLineSegment(sketch, "E916", {"start": v(-3.95, 5.64) * mm, "end": v(-4.05, 5.62) * mm});
            skLineSegment(sketch, "E917", {"start": v(-4.05, 5.62) * mm, "end": v(-4.3, 5.58) * mm});
            skLineSegment(sketch, "E918", {"start": v(-4.3, 5.58) * mm, "end": v(-4.49, 5.56) * mm});
            skLineSegment(sketch, "E919", {"start": v(-4.49, 5.56) * mm, "end": v(-4.75, 5.51) * mm});
            skLineSegment(sketch, "E920", {"start": v(-4.75, 5.51) * mm, "end": v(-4.85, 5.5) * mm});
            skLineSegment(sketch, "E921", {"start": v(-4.85, 5.5) * mm, "end": v(-4.85, 5.5) * mm});
            skLineSegment(sketch, "E922", {"start": v(-4.85, 5.5) * mm, "end": v(-4.88, 5.5) * mm});
            skLineSegment(sketch, "E923", {"start": v(-4.88, 5.5) * mm, "end": v(-4.89, 5.5) * mm});
            skLineSegment(sketch, "E924", {"start": v(-4.89, 5.5) * mm, "end": v(-4.9, 5.5) * mm});
            skLineSegment(sketch, "E925", {"start": v(-4.9, 5.5) * mm, "end": v(-4.92, 5.5) * mm});
            skLineSegment(sketch, "E926", {"start": v(-4.92, 5.5) * mm, "end": v(-4.94, 5.52) * mm});
            skLineSegment(sketch, "E927", {"start": v(-4.94, 5.52) * mm, "end": v(-4.97, 5.53) * mm});
            skLineSegment(sketch, "E928", {"start": v(-4.97, 5.53) * mm, "end": v(-5, 5.55) * mm});
            skLineSegment(sketch, "E929", {"start": v(-5, 5.55) * mm, "end": v(-5.02, 5.58) * mm});
            skLineSegment(sketch, "E930", {"start": v(-5.02, 5.58) * mm, "end": v(-5.05, 5.6) * mm});
            skLineSegment(sketch, "E931", {"start": v(-5.05, 5.6) * mm, "end": v(-5.07, 5.64) * mm});
            skLineSegment(sketch, "E932", {"start": v(-5.07, 5.64) * mm, "end": v(-5.08, 5.64) * mm});
            skLineSegment(sketch, "E933", {"start": v(-5.08, 5.64) * mm, "end": v(-5.1, 5.68) * mm});
            skLineSegment(sketch, "E934", {"start": v(-5.1, 5.68) * mm, "end": v(-5.1, 5.68) * mm});
            skLineSegment(sketch, "E935", {"start": v(-5.1, 5.68) * mm, "end": v(-5.12, 5.72) * mm});
            skLineSegment(sketch, "E936", {"start": v(-5.12, 5.72) * mm, "end": v(-5.12, 5.72) * mm});
            skLineSegment(sketch, "E937", {"start": v(-5.12, 5.72) * mm, "end": v(-5.14, 5.76) * mm});
            skLineSegment(sketch, "E938", {"start": v(-5.14, 5.76) * mm, "end": v(-5.14, 5.76) * mm});
            skLineSegment(sketch, "E939", {"start": v(-5.14, 5.76) * mm, "end": v(-5.27, 6.08) * mm});
            skLineSegment(sketch, "E940", {"start": v(-5.27, 6.08) * mm, "end": v(-5.3, 6.15) * mm});
            skLineSegment(sketch, "E941", {"start": v(-5.3, 6.15) * mm, "end": v(-5.33, 6.22) * mm});
            skLineSegment(sketch, "E942", {"start": v(-5.33, 6.22) * mm, "end": v(-5.36, 6.29) * mm});
            skLineSegment(sketch, "E943", {"start": v(-5.36, 6.29) * mm, "end": v(-5.4, 6.36) * mm});
            skLineSegment(sketch, "E944", {"start": v(-5.4, 6.36) * mm, "end": v(-5.43, 6.43) * mm});
            skLineSegment(sketch, "E945", {"start": v(-5.43, 6.43) * mm, "end": v(-5.47, 6.51) * mm});
            skLineSegment(sketch, "E946", {"start": v(-5.47, 6.51) * mm, "end": v(-5.51, 6.6) * mm});
            skLineSegment(sketch, "E947", {"start": v(-5.51, 6.6) * mm, "end": v(-5.56, 6.7) * mm});
            skLineSegment(sketch, "E948", {"start": v(-5.56, 6.7) * mm, "end": v(-5.6, 6.78) * mm});
            skLineSegment(sketch, "E949", {"start": v(-5.6, 6.78) * mm, "end": v(-5.65, 6.86) * mm});
            skLineSegment(sketch, "E950", {"start": v(-5.65, 6.86) * mm, "end": v(-5.67, 6.9) * mm});
            skLineSegment(sketch, "E951", {"start": v(-5.67, 6.9) * mm, "end": v(-5.72, 6.99) * mm});
            skLineSegment(sketch, "E952", {"start": v(-5.72, 6.99) * mm, "end": v(-5.78, 7.1) * mm});
            skLineSegment(sketch, "E953", {"start": v(-5.78, 7.1) * mm, "end": v(-5.85, 7.2) * mm});
            skLineSegment(sketch, "E954", {"start": v(-5.85, 7.2) * mm, "end": v(-5.92, 7.32) * mm});
            skLineSegment(sketch, "E955", {"start": v(-5.92, 7.32) * mm, "end": v(-6, 7.44) * mm});
            skLineSegment(sketch, "E956", {"start": v(-6, 7.44) * mm, "end": v(-6.08, 7.57) * mm});
            skLineSegment(sketch, "E957", {"start": v(-6.08, 7.57) * mm, "end": v(-6.17, 7.7) * mm});
            skLineSegment(sketch, "E958", {"start": v(-6.17, 7.7) * mm, "end": v(-6.27, 7.83) * mm});
            skLineSegment(sketch, "E959", {"start": v(-6.27, 7.83) * mm, "end": v(-6.37, 7.97) * mm});
            skLineSegment(sketch, "E960", {"start": v(-6.37, 7.97) * mm, "end": v(-6.85, 8.6) * mm});
            skLineSegment(sketch, "E961", {"start": v(-6.85, 8.6) * mm, "end": v(-7.2, 8.5) * mm});
            skLineSegment(sketch, "E962", {"start": v(-7.2, 8.5) * mm, "end": v(-7.6, 8.4) * mm});
            skLineSegment(sketch, "E963", {"start": v(-7.6, 8.4) * mm, "end": v(-7.92, 8.32) * mm});
            skLineSegment(sketch, "E964", {"start": v(-7.92, 8.32) * mm, "end": v(-8.04, 7.56) * mm});
            skLineSegment(sketch, "E965", {"start": v(-8.04, 7.56) * mm, "end": v(-8.06, 7.4) * mm});
            skLineSegment(sketch, "E966", {"start": v(-8.06, 7.4) * mm, "end": v(-8.08, 7.24) * mm});
            skLineSegment(sketch, "E967", {"start": v(-8.08, 7.24) * mm, "end": v(-8.1, 7.09) * mm});
            skLineSegment(sketch, "E968", {"start": v(-8.1, 7.09) * mm, "end": v(-8.12, 6.94) * mm});
            skLineSegment(sketch, "E969", {"start": v(-8.12, 6.94) * mm, "end": v(-8.13, 6.79) * mm});
            skLineSegment(sketch, "E970", {"start": v(-8.13, 6.79) * mm, "end": v(-8.14, 6.64) * mm});
            skLineSegment(sketch, "E971", {"start": v(-8.14, 6.64) * mm, "end": v(-8.14, 6.51) * mm});
            skLineSegment(sketch, "E972", {"start": v(-8.14, 6.51) * mm, "end": v(-8.14, 6.38) * mm});
            skLineSegment(sketch, "E973", {"start": v(-8.14, 6.38) * mm, "end": v(-8.15, 6.3) * mm});
            skLineSegment(sketch, "E974", {"start": v(-8.15, 6.3) * mm, "end": v(-8.14, 6.24) * mm});
            skLineSegment(sketch, "E975", {"start": v(-8.14, 6.24) * mm, "end": v(-8.14, 6.15) * mm});
            skLineSegment(sketch, "E976", {"start": v(-8.14, 6.15) * mm, "end": v(-8.14, 6.05) * mm});
            skLineSegment(sketch, "E977", {"start": v(-8.14, 6.05) * mm, "end": v(-8.13, 5.96) * mm});
            skLineSegment(sketch, "E978", {"start": v(-8.13, 5.96) * mm, "end": v(-8.13, 5.89) * mm});
            skLineSegment(sketch, "E979", {"start": v(-8.13, 5.89) * mm, "end": v(-8.12, 5.82) * mm});
            skLineSegment(sketch, "E980", {"start": v(-8.12, 5.82) * mm, "end": v(-8.11, 5.77) * mm});
            skLineSegment(sketch, "E981", {"start": v(-8.11, 5.77) * mm, "end": v(-8.1, 5.74) * mm});
            skLineSegment(sketch, "E982", {"start": v(-8.1, 5.74) * mm, "end": v(-8.1, 5.73) * mm});
            skLineSegment(sketch, "E983", {"start": v(-8.1, 5.73) * mm, "end": v(-8.03, 5.44) * mm});
            skLineSegment(sketch, "E984", {"start": v(-8.03, 5.44) * mm, "end": v(-8.04, 5.43) * mm});
            skLineSegment(sketch, "E985", {"start": v(-8.04, 5.43) * mm, "end": v(-8, 5.3) * mm});
            skLineSegment(sketch, "E986", {"start": v(-8, 5.3) * mm, "end": v(-8.02, 5.29) * mm});
            skLineSegment(sketch, "E987", {"start": v(-8.02, 5.29) * mm, "end": v(-8, 5.17) * mm});
            skLineSegment(sketch, "E988", {"start": v(-8, 5.17) * mm, "end": v(-8.01, 5.16) * mm});
            skLineSegment(sketch, "E989", {"start": v(-8.01, 5.16) * mm, "end": v(-8, 5.06) * mm});
            skLineSegment(sketch, "E990", {"start": v(-8, 5.06) * mm, "end": v(-8.02, 5.05) * mm});
            skLineSegment(sketch, "E991", {"start": v(-8.02, 5.05) * mm, "end": v(-8, 4.96) * mm});
            skLineSegment(sketch, "E992", {"start": v(-8, 4.96) * mm, "end": v(-8.03, 4.95) * mm});
            skLineSegment(sketch, "E993", {"start": v(-8.03, 4.95) * mm, "end": v(-8.02, 4.88) * mm});
            skLineSegment(sketch, "E994", {"start": v(-8.02, 4.88) * mm, "end": v(-8.04, 4.87) * mm});
            skLineSegment(sketch, "E995", {"start": v(-8.04, 4.87) * mm, "end": v(-8.04, 4.82) * mm});
            skLineSegment(sketch, "E996", {"start": v(-8.04, 4.82) * mm, "end": v(-8.07, 4.8) * mm});
            skLineSegment(sketch, "E997", {"start": v(-8.07, 4.8) * mm, "end": v(-8.06, 4.76) * mm});
            skLineSegment(sketch, "E998", {"start": v(-8.06, 4.76) * mm, "end": v(-8.1, 4.75) * mm});
            skLineSegment(sketch, "E999", {"start": v(-8.1, 4.75) * mm, "end": v(-8.1, 4.71) * mm});
            skLineSegment(sketch, "E1000", {"start": v(-8.1, 4.71) * mm, "end": v(-8.13, 4.68) * mm});
            skLineSegment(sketch, "E1001", {"start": v(-8.13, 4.68) * mm, "end": v(-8.15, 4.67) * mm});
            skLineSegment(sketch, "E1002", {"start": v(-8.15, 4.67) * mm, "end": v(-8.17, 4.66) * mm});
            skLineSegment(sketch, "E1003", {"start": v(-8.17, 4.66) * mm, "end": v(-8.19, 4.65) * mm});
            skLineSegment(sketch, "E1004", {"start": v(-8.19, 4.65) * mm, "end": v(-8.26, 4.62) * mm});
            skLineSegment(sketch, "E1005", {"start": v(-8.26, 4.62) * mm, "end": v(-8.51, 4.53) * mm});
            skLineSegment(sketch, "E1006", {"start": v(-8.51, 4.53) * mm, "end": v(-8.7, 4.47) * mm});
            skLineSegment(sketch, "E1007", {"start": v(-8.7, 4.47) * mm, "end": v(-8.94, 4.37) * mm});
            skLineSegment(sketch, "E1008", {"start": v(-8.94, 4.37) * mm, "end": v(-9, 4.34) * mm});
            skLineSegment(sketch, "E1009", {"start": v(-9, 4.34) * mm, "end": v(-9, 4.35) * mm});
            skLineSegment(sketch, "E1010", {"start": v(-9, 4.35) * mm, "end": v(-9.05, 4.33) * mm});
            skLineSegment(sketch, "E1011", {"start": v(-9.05, 4.33) * mm, "end": v(-9.07, 4.33) * mm});
            skLineSegment(sketch, "E1012", {"start": v(-9.07, 4.33) * mm, "end": v(-9.07, 4.33) * mm});
            skLineSegment(sketch, "E1013", {"start": v(-9.07, 4.33) * mm, "end": v(-9.09, 4.33) * mm});
            skLineSegment(sketch, "E1014", {"start": v(-9.09, 4.33) * mm, "end": v(-9.11, 4.34) * mm});
            skLineSegment(sketch, "E1015", {"start": v(-9.11, 4.34) * mm, "end": v(-9.14, 4.35) * mm});
            skLineSegment(sketch, "E1016", {"start": v(-9.14, 4.35) * mm, "end": v(-9.17, 4.34) * mm});
            skLineSegment(sketch, "E1017", {"start": v(-9.17, 4.34) * mm, "end": v(-9.19, 4.37) * mm});
            skLineSegment(sketch, "E1018", {"start": v(-9.19, 4.37) * mm, "end": v(-9.21, 4.36) * mm});
            skLineSegment(sketch, "E1019", {"start": v(-9.21, 4.36) * mm, "end": v(-9.23, 4.4) * mm});
            skLineSegment(sketch, "E1020", {"start": v(-9.23, 4.4) * mm, "end": v(-9.25, 4.4) * mm});
            skLineSegment(sketch, "E1021", {"start": v(-9.25, 4.4) * mm, "end": v(-9.28, 4.43) * mm});
            skLineSegment(sketch, "E1022", {"start": v(-9.28, 4.43) * mm, "end": v(-9.3, 4.42) * mm});
            skLineSegment(sketch, "E1023", {"start": v(-9.3, 4.42) * mm, "end": v(-9.32, 4.46) * mm});
            skLineSegment(sketch, "E1024", {"start": v(-9.32, 4.46) * mm, "end": v(-9.33, 4.46) * mm});
            skLineSegment(sketch, "E1025", {"start": v(-9.33, 4.46) * mm, "end": v(-9.37, 4.5) * mm});
            skLineSegment(sketch, "E1026", {"start": v(-9.37, 4.5) * mm, "end": v(-9.38, 4.5) * mm});
            skLineSegment(sketch, "E1027", {"start": v(-9.38, 4.5) * mm, "end": v(-9.4, 4.56) * mm});
            skLineSegment(sketch, "E1028", {"start": v(-9.4, 4.56) * mm, "end": v(-9.42, 4.56) * mm});
            skLineSegment(sketch, "E1029", {"start": v(-9.42, 4.56) * mm, "end": v(-9.45, 4.6) * mm});
            skLineSegment(sketch, "E1030", {"start": v(-9.45, 4.6) * mm, "end": v(-9.45, 4.6) * mm});
            skLineSegment(sketch, "E1031", {"start": v(-9.45, 4.6) * mm, "end": v(-9.62, 4.9) * mm});
            skLineSegment(sketch, "E1032", {"start": v(-9.62, 4.9) * mm, "end": v(-9.66, 4.95) * mm});
            skLineSegment(sketch, "E1033", {"start": v(-9.66, 4.95) * mm, "end": v(-9.7, 5.01) * mm});
            skLineSegment(sketch, "E1034", {"start": v(-9.7, 5.01) * mm, "end": v(-9.74, 5.08) * mm});
            skLineSegment(sketch, "E1035", {"start": v(-9.74, 5.08) * mm, "end": v(-9.8, 5.15) * mm});
            skLineSegment(sketch, "E1036", {"start": v(-9.8, 5.15) * mm, "end": v(-9.84, 5.22) * mm});
            skLineSegment(sketch, "E1037", {"start": v(-9.84, 5.22) * mm, "end": v(-9.9, 5.3) * mm});
            skLineSegment(sketch, "E1038", {"start": v(-9.9, 5.3) * mm, "end": v(-9.96, 5.37) * mm});
            skLineSegment(sketch, "E1039", {"start": v(-9.96, 5.37) * mm, "end": v(-10.03, 5.46) * mm});
            skLineSegment(sketch, "E1040", {"start": v(-10.03, 5.46) * mm, "end": v(-10.08, 5.52) * mm});
            skLineSegment(sketch, "E1041", {"start": v(-10.08, 5.52) * mm, "end": v(-10.12, 5.57) * mm});
            skLineSegment(sketch, "E1042", {"start": v(-10.12, 5.57) * mm, "end": v(-10.17, 5.63) * mm});
            skLineSegment(sketch, "E1043", {"start": v(-10.17, 5.63) * mm, "end": v(-10.26, 5.73) * mm});
            skLineSegment(sketch, "E1044", {"start": v(-10.26, 5.73) * mm, "end": v(-10.35, 5.82) * mm});
            skLineSegment(sketch, "E1045", {"start": v(-10.35, 5.82) * mm, "end": v(-10.45, 5.92) * mm});
            skLineSegment(sketch, "E1046", {"start": v(-10.45, 5.92) * mm, "end": v(-10.56, 6.03) * mm});
            skLineSegment(sketch, "E1047", {"start": v(-10.56, 6.03) * mm, "end": v(-10.68, 6.14) * mm});
            skLineSegment(sketch, "E1048", {"start": v(-10.68, 6.14) * mm, "end": v(-10.8, 6.25) * mm});
            skLineSegment(sketch, "E1049", {"start": v(-10.8, 6.25) * mm, "end": v(-10.95, 6.36) * mm});
            skLineSegment(sketch, "E1050", {"start": v(-10.95, 6.36) * mm, "end": v(-11.1, 6.48) * mm});
            skLineSegment(sketch, "E1051", {"start": v(-11.1, 6.48) * mm, "end": v(-11.7, 6.9) * mm});
            skLineSegment(sketch, "E1052", {"start": v(-11.7, 6.9) * mm, "end": v(-12.07, 6.7) * mm});
            skLineSegment(sketch, "E1053", {"start": v(-12.07, 6.7) * mm, "end": v(-12.45, 6.5) * mm});
            skLineSegment(sketch, "E1054", {"start": v(-12.45, 6.5) * mm, "end": v(-12.6, 6.41) * mm});
            skLineSegment(sketch, "E1055", {"start": v(-12.6, 6.41) * mm, "end": v(-12.55, 5.63) * mm});
            skLineSegment(sketch, "E1056", {"start": v(-12.55, 5.63) * mm, "end": v(-12.54, 5.44) * mm});
            skLineSegment(sketch, "E1057", {"start": v(-12.54, 5.44) * mm, "end": v(-12.52, 5.27) * mm});
            skLineSegment(sketch, "E1058", {"start": v(-12.52, 5.27) * mm, "end": v(-12.5, 5.1) * mm});
            skLineSegment(sketch, "E1059", {"start": v(-12.5, 5.1) * mm, "end": v(-12.47, 4.95) * mm});
            skLineSegment(sketch, "E1060", {"start": v(-12.47, 4.95) * mm, "end": v(-12.44, 4.8) * mm});
            skLineSegment(sketch, "E1061", {"start": v(-12.44, 4.8) * mm, "end": v(-12.41, 4.67) * mm});
            skLineSegment(sketch, "E1062", {"start": v(-12.41, 4.67) * mm, "end": v(-12.38, 4.55) * mm});
            skLineSegment(sketch, "E1063", {"start": v(-12.38, 4.55) * mm, "end": v(-12.35, 4.45) * mm});
            skLineSegment(sketch, "E1064", {"start": v(-12.35, 4.45) * mm, "end": v(-12.33, 4.39) * mm});
            skLineSegment(sketch, "E1065", {"start": v(-12.33, 4.39) * mm, "end": v(-12.31, 4.35) * mm});
            skLineSegment(sketch, "E1066", {"start": v(-12.31, 4.35) * mm, "end": v(-12.3, 4.33) * mm});
            skLineSegment(sketch, "E1067", {"start": v(-12.3, 4.33) * mm, "end": v(-12.18, 4.22) * mm});
            skLineSegment(sketch, "E1068", {"start": v(-12.18, 4.22) * mm, "end": v(-12.19, 4.19) * mm});
            skLineSegment(sketch, "E1069", {"start": v(-12.19, 4.19) * mm, "end": v(-12.02, 4.02) * mm});
            skLineSegment(sketch, "E1070", {"start": v(-12.02, 4.02) * mm, "end": v(-12.03, 3.98) * mm});
            skLineSegment(sketch, "E1071", {"start": v(-12.03, 3.98) * mm, "end": v(-11.9, 3.82) * mm});
            skLineSegment(sketch, "E1072", {"start": v(-11.9, 3.82) * mm, "end": v(-11.91, 3.78) * mm});
            skLineSegment(sketch, "E1073", {"start": v(-11.91, 3.78) * mm, "end": v(-11.8, 3.64) * mm});
            skLineSegment(sketch, "E1074", {"start": v(-11.8, 3.64) * mm, "end": v(-11.83, 3.6) * mm});
            skLineSegment(sketch, "E1075", {"start": v(-11.83, 3.6) * mm, "end": v(-11.74, 3.47) * mm});
            skLineSegment(sketch, "E1076", {"start": v(-11.74, 3.47) * mm, "end": v(-11.77, 3.43) * mm});
            skLineSegment(sketch, "E1077", {"start": v(-11.77, 3.43) * mm, "end": v(-11.7, 3.32) * mm});
            skLineSegment(sketch, "E1078", {"start": v(-11.7, 3.32) * mm, "end": v(-11.74, 3.28) * mm});
            skLineSegment(sketch, "E1079", {"start": v(-11.74, 3.28) * mm, "end": v(-11.7, 3.2) * mm});
            skLineSegment(sketch, "E1080", {"start": v(-11.7, 3.2) * mm, "end": v(-11.74, 3.15) * mm});
            skLineSegment(sketch, "E1081", {"start": v(-11.74, 3.15) * mm, "end": v(-11.7, 3.08) * mm});
            skLineSegment(sketch, "E1082", {"start": v(-11.7, 3.08) * mm, "end": v(-11.74, 3.03) * mm});
            skLineSegment(sketch, "E1083", {"start": v(-11.74, 3.03) * mm, "end": v(-11.72, 2.98) * mm});
            skLineSegment(sketch, "E1084", {"start": v(-11.72, 2.98) * mm, "end": v(-11.77, 2.94) * mm});
            skLineSegment(sketch, "E1085", {"start": v(-11.77, 2.94) * mm, "end": v(-11.77, 2.9) * mm});
            skLineSegment(sketch, "E1086", {"start": v(-11.77, 2.9) * mm, "end": v(-11.79, 2.86) * mm});
            skLineSegment(sketch, "E1087", {"start": v(-11.79, 2.86) * mm, "end": v(-11.8, 2.84) * mm});
            skLineSegment(sketch, "E1088", {"start": v(-11.8, 2.84) * mm, "end": v(-11.85, 2.8) * mm});
            skLineSegment(sketch, "E1089", {"start": v(-11.85, 2.8) * mm, "end": v(-11.85, 2.8) * mm});
            skLineSegment(sketch, "E1090", {"start": v(-11.85, 2.8) * mm, "end": v(-11.93, 2.74) * mm});
            skLineSegment(sketch, "E1091", {"start": v(-11.93, 2.74) * mm, "end": v(-12.1, 2.6) * mm});
            skLineSegment(sketch, "E1092", {"start": v(-12.1, 2.6) * mm, "end": v(-12.21, 2.5) * mm});
            skLineSegment(sketch, "E1093", {"start": v(-12.21, 2.5) * mm, "end": v(-12.37, 2.37) * mm});
            skLineSegment(sketch, "E1094", {"start": v(-12.37, 2.37) * mm, "end": v(-12.44, 2.3) * mm});
            skLineSegment(sketch, "E1095", {"start": v(-12.44, 2.3) * mm, "end": v(-12.45, 2.3) * mm});
            skLineSegment(sketch, "E1096", {"start": v(-12.45, 2.3) * mm, "end": v(-12.5, 2.25) * mm});
            skLineSegment(sketch, "E1097", {"start": v(-12.5, 2.25) * mm, "end": v(-12.51, 2.26) * mm});
            skLineSegment(sketch, "E1098", {"start": v(-12.51, 2.26) * mm, "end": v(-12.54, 2.24) * mm});
            skLineSegment(sketch, "E1099", {"start": v(-12.54, 2.24) * mm, "end": v(-12.57, 2.22) * mm});
            skLineSegment(sketch, "E1100", {"start": v(-12.57, 2.22) * mm, "end": v(-12.6, 2.24) * mm});
            skLineSegment(sketch, "E1101", {"start": v(-12.6, 2.24) * mm, "end": v(-12.65, 2.2) * mm});
            skLineSegment(sketch, "E1102", {"start": v(-12.65, 2.2) * mm, "end": v(-12.68, 2.23) * mm});
            skLineSegment(sketch, "E1103", {"start": v(-12.68, 2.23) * mm, "end": v(-12.72, 2.2) * mm});
            skLineSegment(sketch, "E1104", {"start": v(-12.72, 2.2) * mm, "end": v(-12.77, 2.23) * mm});
            skLineSegment(sketch, "E1105", {"start": v(-12.77, 2.23) * mm, "end": v(-12.8, 2.2) * mm});
            skLineSegment(sketch, "E1106", {"start": v(-12.8, 2.2) * mm, "end": v(-12.86, 2.25) * mm});
            skLineSegment(sketch, "E1107", {"start": v(-12.86, 2.25) * mm, "end": v(-12.88, 2.23) * mm});
            skLineSegment(sketch, "E1108", {"start": v(-12.88, 2.23) * mm, "end": v(-12.94, 2.28) * mm});
            skLineSegment(sketch, "E1109", {"start": v(-12.94, 2.28) * mm, "end": v(-12.97, 2.26) * mm});
            skLineSegment(sketch, "E1110", {"start": v(-12.97, 2.26) * mm, "end": v(-13.03, 2.32) * mm});
            skLineSegment(sketch, "E1111", {"start": v(-13.03, 2.32) * mm, "end": v(-13.05, 2.3) * mm});
            skLineSegment(sketch, "E1112", {"start": v(-13.05, 2.3) * mm, "end": v(-13.12, 2.37) * mm});
            skLineSegment(sketch, "E1113", {"start": v(-13.12, 2.37) * mm, "end": v(-13.13, 2.36) * mm});
            skLineSegment(sketch, "E1114", {"start": v(-13.13, 2.36) * mm, "end": v(-13.2, 2.42) * mm});
            skLineSegment(sketch, "E1115", {"start": v(-13.2, 2.42) * mm, "end": v(-13.21, 2.42) * mm});
            skLineSegment(sketch, "E1116", {"start": v(-13.21, 2.42) * mm, "end": v(-13.28, 2.49) * mm});
            skLineSegment(sketch, "E1117", {"start": v(-13.28, 2.49) * mm, "end": v(-13.3, 2.49) * mm});
            skLineSegment(sketch, "E1118", {"start": v(-13.3, 2.49) * mm, "end": v(-13.54, 2.74) * mm});
            skLineSegment(sketch, "E1119", {"start": v(-13.54, 2.74) * mm, "end": v(-13.56, 2.77) * mm});
            skLineSegment(sketch, "E1120", {"start": v(-13.56, 2.77) * mm, "end": v(-13.59, 2.8) * mm});
            skLineSegment(sketch, "E1121", {"start": v(-13.59, 2.8) * mm, "end": v(-13.62, 2.82) * mm});
            skLineSegment(sketch, "E1122", {"start": v(-13.62, 2.82) * mm, "end": v(-13.65, 2.85) * mm});
            skLineSegment(sketch, "E1123", {"start": v(-13.65, 2.85) * mm, "end": v(-13.7, 2.88) * mm});
            skLineSegment(sketch, "E1124", {"start": v(-13.7, 2.88) * mm, "end": v(-13.74, 2.92) * mm});
            skLineSegment(sketch, "E1125", {"start": v(-13.74, 2.92) * mm, "end": v(-13.8, 2.95) * mm});
            skLineSegment(sketch, "E1126", {"start": v(-13.8, 2.95) * mm, "end": v(-13.85, 3) * mm});
            skLineSegment(sketch, "E1127", {"start": v(-13.85, 3) * mm, "end": v(-13.9, 3.02) * mm});
            skLineSegment(sketch, "E1128", {"start": v(-13.9, 3.02) * mm, "end": v(-13.93, 3.04) * mm});
            skLineSegment(sketch, "E1129", {"start": v(-13.93, 3.04) * mm, "end": v(-13.99, 3.07) * mm});
            skLineSegment(sketch, "E1130", {"start": v(-13.99, 3.07) * mm, "end": v(-14.07, 3.12) * mm});
            skLineSegment(sketch, "E1131", {"start": v(-14.07, 3.12) * mm, "end": v(-14.17, 3.16) * mm});
            skLineSegment(sketch, "E1132", {"start": v(-14.17, 3.16) * mm, "end": v(-14.28, 3.2) * mm});
            skLineSegment(sketch, "E1133", {"start": v(-14.28, 3.2) * mm, "end": v(-14.4, 3.25) * mm});
            skLineSegment(sketch, "E1134", {"start": v(-14.4, 3.25) * mm, "end": v(-14.55, 3.29) * mm});
            skLineSegment(sketch, "E1135", {"start": v(-14.55, 3.29) * mm, "end": v(-14.72, 3.32) * mm});
            skLineSegment(sketch, "E1136", {"start": v(-14.72, 3.32) * mm, "end": v(-14.9, 3.35) * mm});
            skLineSegment(sketch, "E1137", {"start": v(-14.9, 3.35) * mm, "end": v(-15.1, 3.37) * mm});
            skLineSegment(sketch, "E1138", {"start": v(-15.1, 3.37) * mm, "end": v(-15.33, 3.37) * mm});
            skLineSegment(sketch, "E1139", {"start": v(-15.33, 3.37) * mm, "end": v(-15.65, 3.36) * mm});
            skLineSegment(sketch, "E1140", {"start": v(-15.65, 3.36) * mm, "end": v(-16.07, 3.3) * mm});
            skLineSegment(sketch, "E1141", {"start": v(-16.07, 3.3) * mm, "end": v(-16.18, 3.14) * mm});
            skLineSegment(sketch, "E1142", {"start": v(-16.18, 3.14) * mm, "end": v(-16.38, 2.8) * mm});
            skLineSegment(sketch, "E1143", {"start": v(-16.38, 2.8) * mm, "end": v(-16.45, 2.67) * mm});
            skLineSegment(sketch, "E1144", {"start": v(-16.45, 2.67) * mm, "end": v(-16.17, 2.13) * mm});
            skLineSegment(sketch, "E1145", {"start": v(-16.17, 2.13) * mm, "end": v(-16.06, 1.94) * mm});
            skLineSegment(sketch, "E1146", {"start": v(-16.06, 1.94) * mm, "end": v(-15.95, 1.76) * mm});
            skLineSegment(sketch, "E1147", {"start": v(-15.95, 1.76) * mm, "end": v(-15.84, 1.6) * mm});
            skLineSegment(sketch, "E1148", {"start": v(-15.84, 1.6) * mm, "end": v(-15.73, 1.47) * mm});
            skLineSegment(sketch, "E1149", {"start": v(-15.73, 1.47) * mm, "end": v(-15.63, 1.35) * mm});
            skLineSegment(sketch, "E1150", {"start": v(-15.63, 1.35) * mm, "end": v(-15.53, 1.25) * mm});
            skLineSegment(sketch, "E1151", {"start": v(-15.53, 1.25) * mm, "end": v(-15.41, 1.16) * mm});
            skLineSegment(sketch, "E1152", {"start": v(-15.41, 1.16) * mm, "end": v(-15.32, 1.1) * mm});
            skLineSegment(sketch, "E1153", {"start": v(-15.32, 1.1) * mm, "end": v(-15.2, 1.13) * mm});
            skLineSegment(sketch, "E1154", {"start": v(-15.2, 1.13) * mm, "end": v(-15.19, 1.1) * mm});
            skLineSegment(sketch, "E1155", {"start": v(-15.19, 1.1) * mm, "end": v(-15, 1.16) * mm});
            skLineSegment(sketch, "E1156", {"start": v(-15, 1.16) * mm, "end": v(-14.98, 1.13) * mm});
            skLineSegment(sketch, "E1157", {"start": v(-14.98, 1.13) * mm, "end": v(-14.8, 1.16) * mm});
            skLineSegment(sketch, "E1158", {"start": v(-14.8, 1.16) * mm, "end": v(-14.77, 1.12) * mm});
            skLineSegment(sketch, "E1159", {"start": v(-14.77, 1.12) * mm, "end": v(-14.6, 1.15) * mm});
            skLineSegment(sketch, "E1160", {"start": v(-14.6, 1.15) * mm, "end": v(-14.57, 1.1) * mm});
            skLineSegment(sketch, "E1161", {"start": v(-14.57, 1.1) * mm, "end": v(-14.41, 1.11) * mm});
            skLineSegment(sketch, "E1162", {"start": v(-14.41, 1.11) * mm, "end": v(-14.38, 1.05) * mm});
            skLineSegment(sketch, "E1163", {"start": v(-14.38, 1.05) * mm, "end": v(-14.23, 1.05) * mm});
            skLineSegment(sketch, "E1164", {"start": v(-14.23, 1.05) * mm, "end": v(-14.2, 0.94) * mm});
            skLineSegment(sketch, "E1165", {"start": v(-14.2, 0.94) * mm, "end": v(-14, 0.92) * mm});
            skLineSegment(sketch, "E1166", {"start": v(-14, 0.92) * mm, "end": v(-13.97, 0.78) * mm});
            skLineSegment(sketch, "E1167", {"start": v(-13.97, 0.78) * mm, "end": v(-13.83, 0.75) * mm});
            skLineSegment(sketch, "E1168", {"start": v(-13.83, 0.75) * mm, "end": v(-13.8, 0.59) * mm});
            skLineSegment(sketch, "E1169", {"start": v(-13.8, 0.59) * mm, "end": v(-13.71, 0.56) * mm});
            skLineSegment(sketch, "E1170", {"start": v(-13.71, 0.56) * mm, "end": v(-13.7, 0.5) * mm});
            skLineSegment(sketch, "E1171", {"start": v(-13.7, 0.5) * mm, "end": v(-13.69, 0.49) * mm});
            skLineSegment(sketch, "E1172", {"start": v(-13.69, 0.49) * mm, "end": v(-13.69, 0.42) * mm});
            skLineSegment(sketch, "E1173", {"start": v(-13.69, 0.42) * mm, "end": v(-13.67, 0.42) * mm});
            skLineSegment(sketch, "E1174", {"start": v(-13.67, 0.42) * mm, "end": v(-13.68, 0.21) * mm});
            skLineSegment(sketch, "E1175", {"start": v(-13.68, 0.21) * mm, "end": v(-13.68, 0.2) * mm});
            skLineSegment(sketch, "E1176", {"start": v(-13.68, 0.2) * mm, "end": v(-13.68, 0.18) * mm});
            skLineSegment(sketch, "E1177", {"start": v(-13.68, 0.18) * mm, "end": v(-13.69, 0.03) * mm});
            skLineSegment(sketch, "E1178", {"start": v(-13.69, 0.03) * mm, "end": v(-13.69, -0.05) * mm});
            skLineSegment(sketch, "E1179", {"start": v(-13.69, -0.05) * mm, "end": v(-13.68, -0.2) * mm});
            skLineSegment(sketch, "E1180", {"start": v(-13.68, -0.2) * mm, "end": v(-13.68, -0.23) * mm});
            skLineSegment(sketch, "E1181", {"start": v(-13.68, -0.23) * mm, "end": v(-13.68, -0.23) * mm});
            skLineSegment(sketch, "E1182", {"start": v(-13.68, -0.23) * mm, "end": v(-13.67, -0.43) * mm});
            skLineSegment(sketch, "E1183", {"start": v(-13.67, -0.43) * mm, "end": v(-13.68, -0.44) * mm});
            skLineSegment(sketch, "E1184", {"start": v(-13.68, -0.44) * mm, "end": v(-13.68, -0.5) * mm});
            skLineSegment(sketch, "E1185", {"start": v(-13.68, -0.5) * mm, "end": v(-13.7, -0.51) * mm});
            skLineSegment(sketch, "E1186", {"start": v(-13.7, -0.51) * mm, "end": v(-13.7, -0.57) * mm});
            skLineSegment(sketch, "E1187", {"start": v(-13.7, -0.57) * mm, "end": v(-13.8, -0.6) * mm});
            skLineSegment(sketch, "E1188", {"start": v(-13.8, -0.6) * mm, "end": v(-13.82, -0.77) * mm});
            skLineSegment(sketch, "E1189", {"start": v(-13.82, -0.77) * mm, "end": v(-13.96, -0.8) * mm});
            skLineSegment(sketch, "E1190", {"start": v(-13.96, -0.8) * mm, "end": v(-14, -0.94) * mm});
            skLineSegment(sketch, "E1191", {"start": v(-14, -0.94) * mm, "end": v(-14.19, -0.96) * mm});
            skLineSegment(sketch, "E1192", {"start": v(-14.19, -0.96) * mm, "end": v(-14.23, -1.07) * mm});
            skLineSegment(sketch, "E1193", {"start": v(-14.23, -1.07) * mm, "end": v(-14.37, -1.07) * mm});
            skLineSegment(sketch, "E1194", {"start": v(-14.37, -1.07) * mm, "end": v(-14.4, -1.13) * mm});
            skLineSegment(sketch, "E1195", {"start": v(-14.4, -1.13) * mm, "end": v(-14.56, -1.12) * mm});
            skLineSegment(sketch, "E1196", {"start": v(-14.56, -1.12) * mm, "end": v(-14.6, -1.17) * mm});
            skLineSegment(sketch, "E1197", {"start": v(-14.6, -1.17) * mm, "end": v(-14.77, -1.15) * mm});
            skLineSegment(sketch, "E1198", {"start": v(-14.77, -1.15) * mm, "end": v(-14.79, -1.2) * mm});
            skLineSegment(sketch, "E1199", {"start": v(-14.79, -1.2) * mm, "end": v(-14.97, -1.15) * mm});
            skLineSegment(sketch, "E1200", {"start": v(-14.97, -1.15) * mm, "end": v(-15, -1.19) * mm});
            skLineSegment(sketch, "E1201", {"start": v(-15, -1.19) * mm, "end": v(-15.18, -1.14) * mm});
            skLineSegment(sketch, "E1202", {"start": v(-15.18, -1.14) * mm, "end": v(-15.2, -1.16) * mm});
            skLineSegment(sketch, "E1203", {"start": v(-15.2, -1.16) * mm, "end": v(-15.3, -1.13) * mm});
            skLineSegment(sketch, "E1204", {"start": v(-15.3, -1.13) * mm, "end": v(-15.4, -1.19) * mm});
            skLineSegment(sketch, "E1205", {"start": v(-15.4, -1.19) * mm, "end": v(-15.52, -1.29) * mm});
            skLineSegment(sketch, "E1206", {"start": v(-15.52, -1.29) * mm, "end": v(-15.62, -1.39) * mm});
            skLineSegment(sketch, "E1207", {"start": v(-15.62, -1.39) * mm, "end": v(-15.72, -1.5) * mm});
            skLineSegment(sketch, "E1208", {"start": v(-15.72, -1.5) * mm, "end": v(-15.83, -1.64) * mm});
            skLineSegment(sketch, "E1209", {"start": v(-15.83, -1.64) * mm, "end": v(-15.94, -1.8) * mm});
            skLineSegment(sketch, "E1210", {"start": v(-15.94, -1.8) * mm, "end": v(-16.05, -1.97) * mm});
            skLineSegment(sketch, "E1211", {"start": v(-16.05, -1.97) * mm, "end": v(-16.16, -2.16) * mm});
            skLineSegment(sketch, "E1212", {"start": v(-16.16, -2.16) * mm, "end": v(-16.43, -2.7) * mm});
            skLineSegment(sketch, "E1213", {"start": v(-16.43, -2.7) * mm, "end": v(-16.25, -3.03) * mm});
            skLineSegment(sketch, "E1214", {"start": v(-16.25, -3.03) * mm, "end": v(-16.05, -3.34) * mm});
            skLineSegment(sketch, "E1215", {"start": v(-16.05, -3.34) * mm, "end": v(-15.62, -3.4) * mm});
            skLineSegment(sketch, "E1216", {"start": v(-15.62, -3.4) * mm, "end": v(-15.3, -3.4) * mm});
            skLineSegment(sketch, "E1217", {"start": v(-15.3, -3.4) * mm, "end": v(-15.08, -3.4) * mm});
            skLineSegment(sketch, "E1218", {"start": v(-15.08, -3.4) * mm, "end": v(-14.87, -3.38) * mm});
            skLineSegment(sketch, "E1219", {"start": v(-14.87, -3.38) * mm, "end": v(-14.7, -3.35) * mm});
            skLineSegment(sketch, "E1220", {"start": v(-14.7, -3.35) * mm, "end": v(-14.53, -3.31) * mm});
            skLineSegment(sketch, "E1221", {"start": v(-14.53, -3.31) * mm, "end": v(-14.39, -3.27) * mm});
            skLineSegment(sketch, "E1222", {"start": v(-14.39, -3.27) * mm, "end": v(-14.26, -3.23) * mm});
            skLineSegment(sketch, "E1223", {"start": v(-14.26, -3.23) * mm, "end": v(-14.15, -3.19) * mm});
            skLineSegment(sketch, "E1224", {"start": v(-14.15, -3.19) * mm, "end": v(-14.05, -3.14) * mm});
            skLineSegment(sketch, "E1225", {"start": v(-14.05, -3.14) * mm, "end": v(-13.97, -3.1) * mm});
            skLineSegment(sketch, "E1226", {"start": v(-13.97, -3.1) * mm, "end": v(-13.9, -3.07) * mm});
            skLineSegment(sketch, "E1227", {"start": v(-13.9, -3.07) * mm, "end": v(-13.87, -3.05) * mm});
            skLineSegment(sketch, "E1228", {"start": v(-13.87, -3.05) * mm, "end": v(-13.82, -3.02) * mm});
            skLineSegment(sketch, "E1229", {"start": v(-13.82, -3.02) * mm, "end": v(-13.77, -2.98) * mm});
            skLineSegment(sketch, "E1230", {"start": v(-13.77, -2.98) * mm, "end": v(-13.72, -2.94) * mm});
            skLineSegment(sketch, "E1231", {"start": v(-13.72, -2.94) * mm, "end": v(-13.67, -2.9) * mm});
            skLineSegment(sketch, "E1232", {"start": v(-13.67, -2.9) * mm, "end": v(-13.63, -2.87) * mm});
            skLineSegment(sketch, "E1233", {"start": v(-13.63, -2.87) * mm, "end": v(-13.6, -2.84) * mm});
            skLineSegment(sketch, "E1234", {"start": v(-13.6, -2.84) * mm, "end": v(-13.56, -2.81) * mm});
            skLineSegment(sketch, "E1235", {"start": v(-13.56, -2.81) * mm, "end": v(-13.53, -2.79) * mm});
            skLineSegment(sketch, "E1236", {"start": v(-13.53, -2.79) * mm, "end": v(-13.5, -2.76) * mm});
            skLineSegment(sketch, "E1237", {"start": v(-13.5, -2.76) * mm, "end": v(-13.27, -2.5) * mm});
            skLineSegment(sketch, "E1238", {"start": v(-13.27, -2.5) * mm, "end": v(-13.26, -2.5) * mm});
            skLineSegment(sketch, "E1239", {"start": v(-13.26, -2.5) * mm, "end": v(-13.19, -2.44) * mm});
            skLineSegment(sketch, "E1240", {"start": v(-13.19, -2.44) * mm, "end": v(-13.17, -2.44) * mm});
            skLineSegment(sketch, "E1241", {"start": v(-13.17, -2.44) * mm, "end": v(-13.1, -2.38) * mm});
            skLineSegment(sketch, "E1242", {"start": v(-13.1, -2.38) * mm, "end": v(-13.1, -2.39) * mm});
            skLineSegment(sketch, "E1243", {"start": v(-13.1, -2.39) * mm, "end": v(-13.02, -2.33) * mm});
            skLineSegment(sketch, "E1244", {"start": v(-13.02, -2.33) * mm, "end": v(-13, -2.34) * mm});
            skLineSegment(sketch, "E1245", {"start": v(-13, -2.34) * mm, "end": v(-12.94, -2.28) * mm});
            skLineSegment(sketch, "E1246", {"start": v(-12.94, -2.28) * mm, "end": v(-12.92, -2.3) * mm});
            skLineSegment(sketch, "E1247", {"start": v(-12.92, -2.3) * mm, "end": v(-12.86, -2.25) * mm});
            skLineSegment(sketch, "E1248", {"start": v(-12.86, -2.25) * mm, "end": v(-12.83, -2.27) * mm});
            skLineSegment(sketch, "E1249", {"start": v(-12.83, -2.27) * mm, "end": v(-12.78, -2.23) * mm});
            skLineSegment(sketch, "E1250", {"start": v(-12.78, -2.23) * mm, "end": v(-12.75, -2.25) * mm});
            skLineSegment(sketch, "E1251", {"start": v(-12.75, -2.25) * mm, "end": v(-12.7, -2.22) * mm});
            skLineSegment(sketch, "E1252", {"start": v(-12.7, -2.22) * mm, "end": v(-12.66, -2.25) * mm});
            skLineSegment(sketch, "E1253", {"start": v(-12.66, -2.25) * mm, "end": v(-12.62, -2.22) * mm});
            skLineSegment(sketch, "E1254", {"start": v(-12.62, -2.22) * mm, "end": v(-12.58, -2.26) * mm});
            skLineSegment(sketch, "E1255", {"start": v(-12.58, -2.26) * mm, "end": v(-12.54, -2.25) * mm});
            skLineSegment(sketch, "E1256", {"start": v(-12.54, -2.25) * mm, "end": v(-12.5, -2.26) * mm});
            skLineSegment(sketch, "E1257", {"start": v(-12.5, -2.26) * mm, "end": v(-12.48, -2.27) * mm});
            skLineSegment(sketch, "E1258", {"start": v(-12.48, -2.27) * mm, "end": v(-12.42, -2.32) * mm});
            skLineSegment(sketch, "E1259", {"start": v(-12.42, -2.32) * mm, "end": v(-12.42, -2.32) * mm});
            skLineSegment(sketch, "E1260", {"start": v(-12.42, -2.32) * mm, "end": v(-12.35, -2.38) * mm});
            skLineSegment(sketch, "E1261", {"start": v(-12.35, -2.38) * mm, "end": v(-12.2, -2.52) * mm});
            skLineSegment(sketch, "E1262", {"start": v(-12.2, -2.52) * mm, "end": v(-12.08, -2.62) * mm});
            skLineSegment(sketch, "E1263", {"start": v(-12.08, -2.62) * mm, "end": v(-11.9, -2.76) * mm});
            skLineSegment(sketch, "E1264", {"start": v(-11.9, -2.76) * mm, "end": v(-11.83, -2.81) * mm});
            skLineSegment(sketch, "E1265", {"start": v(-11.83, -2.81) * mm, "end": v(-11.8, -2.84) * mm});
            skLineSegment(sketch, "E1266", {"start": v(-11.8, -2.84) * mm, "end": v(-11.78, -2.87) * mm});
            skLineSegment(sketch, "E1267", {"start": v(-11.78, -2.87) * mm, "end": v(-11.75, -2.9) * mm});
            skLineSegment(sketch, "E1268", {"start": v(-11.75, -2.9) * mm, "end": v(-11.73, -2.92) * mm});
            skLineSegment(sketch, "E1269", {"start": v(-11.73, -2.92) * mm, "end": v(-11.75, -2.95) * mm});
            skLineSegment(sketch, "E1270", {"start": v(-11.75, -2.95) * mm, "end": v(-11.7, -3) * mm});
            skLineSegment(sketch, "E1271", {"start": v(-11.7, -3) * mm, "end": v(-11.72, -3.05) * mm});
            skLineSegment(sketch, "E1272", {"start": v(-11.72, -3.05) * mm, "end": v(-11.68, -3.1) * mm});
            skLineSegment(sketch, "E1273", {"start": v(-11.68, -3.1) * mm, "end": v(-11.71, -3.16) * mm});
            skLineSegment(sketch, "E1274", {"start": v(-11.71, -3.16) * mm, "end": v(-11.67, -3.2) * mm});
            skLineSegment(sketch, "E1275", {"start": v(-11.67, -3.2) * mm, "end": v(-11.72, -3.3) * mm});
            skLineSegment(sketch, "E1276", {"start": v(-11.72, -3.3) * mm, "end": v(-11.68, -3.34) * mm});
            skLineSegment(sketch, "E1277", {"start": v(-11.68, -3.34) * mm, "end": v(-11.75, -3.44) * mm});
            skLineSegment(sketch, "E1278", {"start": v(-11.75, -3.44) * mm, "end": v(-11.72, -3.49) * mm});
            skLineSegment(sketch, "E1279", {"start": v(-11.72, -3.49) * mm, "end": v(-11.8, -3.61) * mm});
            skLineSegment(sketch, "E1280", {"start": v(-11.8, -3.61) * mm, "end": v(-11.78, -3.65) * mm});
            skLineSegment(sketch, "E1281", {"start": v(-11.78, -3.65) * mm, "end": v(-11.89, -3.8) * mm});
            skLineSegment(sketch, "E1282", {"start": v(-11.89, -3.8) * mm, "end": v(-11.86, -3.83) * mm});
            skLineSegment(sketch, "E1283", {"start": v(-11.86, -3.83) * mm, "end": v(-12, -4) * mm});
            skLineSegment(sketch, "E1284", {"start": v(-12, -4) * mm, "end": v(-11.99, -4.03) * mm});
            skLineSegment(sketch, "E1285", {"start": v(-11.99, -4.03) * mm, "end": v(-12.16, -4.2) * mm});
            skLineSegment(sketch, "E1286", {"start": v(-12.16, -4.2) * mm, "end": v(-12.14, -4.23) * mm});
            skLineSegment(sketch, "E1287", {"start": v(-12.14, -4.23) * mm, "end": v(-12.28, -4.35) * mm});
            skLineSegment(sketch, "E1288", {"start": v(-12.28, -4.35) * mm, "end": v(-12.28, -4.37) * mm});
            skLineSegment(sketch, "E1289", {"start": v(-12.28, -4.37) * mm, "end": v(-12.3, -4.4) * mm});
            skLineSegment(sketch, "E1290", {"start": v(-12.3, -4.4) * mm, "end": v(-12.32, -4.47) * mm});
            skLineSegment(sketch, "E1291", {"start": v(-12.32, -4.47) * mm, "end": v(-12.35, -4.57) * mm});
            skLineSegment(sketch, "E1292", {"start": v(-12.35, -4.57) * mm, "end": v(-12.38, -4.69) * mm});
            skLineSegment(sketch, "E1293", {"start": v(-12.38, -4.69) * mm, "end": v(-12.4, -4.82) * mm});
            skLineSegment(sketch, "E1294", {"start": v(-12.4, -4.82) * mm, "end": v(-12.44, -4.96) * mm});
            skLineSegment(sketch, "E1295", {"start": v(-12.44, -4.96) * mm, "end": v(-12.46, -5.12) * mm});
            skLineSegment(sketch, "E1296", {"start": v(-12.46, -5.12) * mm, "end": v(-12.49, -5.29) * mm});
            skLineSegment(sketch, "E1297", {"start": v(-12.49, -5.29) * mm, "end": v(-12.5, -5.46) * mm});
            skLineSegment(sketch, "E1298", {"start": v(-12.5, -5.46) * mm, "end": v(-12.52, -5.64) * mm});
            skLineSegment(sketch, "E1299", {"start": v(-12.52, -5.64) * mm, "end": v(-12.57, -6.43) * mm});
            skLineSegment(sketch, "E1300", {"start": v(-12.57, -6.43) * mm, "end": v(-12.2, -6.64) * mm});
            skLineSegment(sketch, "E1301", {"start": v(-12.2, -6.64) * mm, "end": v(-11.8, -6.84) * mm});
            skLineSegment(sketch, "E1302", {"start": v(-11.8, -6.84) * mm, "end": v(-11.66, -6.92) * mm});
            skLineSegment(sketch, "E1303", {"start": v(-11.66, -6.92) * mm, "end": v(-11.07, -6.5) * mm});
            skLineSegment(sketch, "E1304", {"start": v(-11.07, -6.5) * mm, "end": v(-10.92, -6.38) * mm});
            skLineSegment(sketch, "E1305", {"start": v(-10.92, -6.38) * mm, "end": v(-10.77, -6.26) * mm});
            skLineSegment(sketch, "E1306", {"start": v(-10.77, -6.26) * mm, "end": v(-10.64, -6.15) * mm});
            skLineSegment(sketch, "E1307", {"start": v(-10.64, -6.15) * mm, "end": v(-10.53, -6.04) * mm});
            skLineSegment(sketch, "E1308", {"start": v(-10.53, -6.04) * mm, "end": v(-10.42, -5.94) * mm});
            skLineSegment(sketch, "E1309", {"start": v(-10.42, -5.94) * mm, "end": v(-10.32, -5.83) * mm});
            skLineSegment(sketch, "E1310", {"start": v(-10.32, -5.83) * mm, "end": v(-10.23, -5.74) * mm});
            skLineSegment(sketch, "E1311", {"start": v(-10.23, -5.74) * mm, "end": v(-10.14, -5.65) * mm});
            skLineSegment(sketch, "E1312", {"start": v(-10.14, -5.65) * mm, "end": v(-10.08, -5.58) * mm});
            skLineSegment(sketch, "E1313", {"start": v(-10.08, -5.58) * mm, "end": v(-10.04, -5.53) * mm});
            skLineSegment(sketch, "E1314", {"start": v(-10.04, -5.53) * mm, "end": v(-10, -5.47) * mm});
            skLineSegment(sketch, "E1315", {"start": v(-10, -5.47) * mm, "end": v(-9.93, -5.39) * mm});
            skLineSegment(sketch, "E1316", {"start": v(-9.93, -5.39) * mm, "end": v(-9.86, -5.3) * mm});
            skLineSegment(sketch, "E1317", {"start": v(-9.86, -5.3) * mm, "end": v(-9.8, -5.23) * mm});
            skLineSegment(sketch, "E1318", {"start": v(-9.8, -5.23) * mm, "end": v(-9.76, -5.16) * mm});
            skLineSegment(sketch, "E1319", {"start": v(-9.76, -5.16) * mm, "end": v(-9.71, -5.09) * mm});
            skLineSegment(sketch, "E1320", {"start": v(-9.71, -5.09) * mm, "end": v(-9.67, -5.02) * mm});
            skLineSegment(sketch, "E1321", {"start": v(-9.67, -5.02) * mm, "end": v(-9.63, -4.96) * mm});
            skLineSegment(sketch, "E1322", {"start": v(-9.63, -4.96) * mm, "end": v(-9.59, -4.9) * mm});
            skLineSegment(sketch, "E1323", {"start": v(-9.59, -4.9) * mm, "end": v(-9.42, -4.62) * mm});
            skLineSegment(sketch, "E1324", {"start": v(-9.42, -4.62) * mm, "end": v(-9.4, -4.6) * mm});
            skLineSegment(sketch, "E1325", {"start": v(-9.4, -4.6) * mm, "end": v(-9.38, -4.57) * mm});
            skLineSegment(sketch, "E1326", {"start": v(-9.38, -4.57) * mm, "end": v(-9.34, -4.52) * mm});
            skLineSegment(sketch, "E1327", {"start": v(-9.34, -4.52) * mm, "end": v(-9.32, -4.5) * mm});
            skLineSegment(sketch, "E1328", {"start": v(-9.32, -4.5) * mm, "end": v(-9.3, -4.48) * mm});
            skLineSegment(sketch, "E1329", {"start": v(-9.3, -4.48) * mm, "end": v(-9.26, -4.43) * mm});
            skLineSegment(sketch, "E1330", {"start": v(-9.26, -4.43) * mm, "end": v(-9.23, -4.42) * mm});
            skLineSegment(sketch, "E1331", {"start": v(-9.23, -4.42) * mm, "end": v(-9.2, -4.4) * mm});
            skLineSegment(sketch, "E1332", {"start": v(-9.2, -4.4) * mm, "end": v(-9.18, -4.37) * mm});
            skLineSegment(sketch, "E1333", {"start": v(-9.18, -4.37) * mm, "end": v(-9.15, -4.37) * mm});
            skLineSegment(sketch, "E1334", {"start": v(-9.15, -4.37) * mm, "end": v(-9.11, -4.36) * mm});
            skLineSegment(sketch, "E1335", {"start": v(-9.11, -4.36) * mm, "end": v(-9.08, -4.35) * mm});
            skLineSegment(sketch, "E1336", {"start": v(-9.08, -4.35) * mm, "end": v(-9.05, -4.34) * mm});
            skLineSegment(sketch, "E1337", {"start": v(-9.05, -4.34) * mm, "end": v(-9.03, -4.34) * mm});
            skLineSegment(sketch, "E1338", {"start": v(-9.03, -4.34) * mm, "end": v(-9, -4.35) * mm});
            skLineSegment(sketch, "E1339", {"start": v(-9, -4.35) * mm, "end": v(-8.98, -4.35) * mm});
            skLineSegment(sketch, "E1340", {"start": v(-8.98, -4.35) * mm, "end": v(-8.91, -4.38) * mm});
            skLineSegment(sketch, "E1341", {"start": v(-8.91, -4.38) * mm, "end": v(-8.66, -4.48) * mm});
            skLineSegment(sketch, "E1342", {"start": v(-8.66, -4.48) * mm, "end": v(-8.48, -4.54) * mm});
            skLineSegment(sketch, "E1343", {"start": v(-8.48, -4.54) * mm, "end": v(-8.22, -4.63) * mm});
            skLineSegment(sketch, "E1344", {"start": v(-8.22, -4.63) * mm, "end": v(-8.16, -4.66) * mm});
            skLineSegment(sketch, "E1345", {"start": v(-8.16, -4.66) * mm, "end": v(-8.14, -4.66) * mm});
            skLineSegment(sketch, "E1346", {"start": v(-8.14, -4.66) * mm, "end": v(-8.12, -4.67) * mm});
            skLineSegment(sketch, "E1347", {"start": v(-8.12, -4.67) * mm, "end": v(-8.1, -4.68) * mm});
            skLineSegment(sketch, "E1348", {"start": v(-8.1, -4.68) * mm, "end": v(-8.09, -4.7) * mm});
            skLineSegment(sketch, "E1349", {"start": v(-8.09, -4.7) * mm, "end": v(-8.06, -4.73) * mm});
            skLineSegment(sketch, "E1350", {"start": v(-8.06, -4.73) * mm, "end": v(-8.06, -4.76) * mm});
            skLineSegment(sketch, "E1351", {"start": v(-8.06, -4.76) * mm, "end": v(-8.03, -4.77) * mm});
            skLineSegment(sketch, "E1352", {"start": v(-8.03, -4.77) * mm, "end": v(-8.03, -4.81) * mm});
            skLineSegment(sketch, "E1353", {"start": v(-8.03, -4.81) * mm, "end": v(-8, -4.82) * mm});
            skLineSegment(sketch, "E1354", {"start": v(-8, -4.82) * mm, "end": v(-8.01, -4.88) * mm});
            skLineSegment(sketch, "E1355", {"start": v(-8.01, -4.88) * mm, "end": v(-7.99, -4.9) * mm});
            skLineSegment(sketch, "E1356", {"start": v(-7.99, -4.9) * mm, "end": v(-8, -4.96) * mm});
            skLineSegment(sketch, "E1357", {"start": v(-8, -4.96) * mm, "end": v(-7.97, -4.97) * mm});
            skLineSegment(sketch, "E1358", {"start": v(-7.97, -4.97) * mm, "end": v(-7.98, -5.05) * mm});
            skLineSegment(sketch, "E1359", {"start": v(-7.98, -5.05) * mm, "end": v(-7.97, -5.06) * mm});
            skLineSegment(sketch, "E1360", {"start": v(-7.97, -5.06) * mm, "end": v(-7.98, -5.16) * mm});
            skLineSegment(sketch, "E1361", {"start": v(-7.98, -5.16) * mm, "end": v(-7.97, -5.17) * mm});
            skLineSegment(sketch, "E1362", {"start": v(-7.97, -5.17) * mm, "end": v(-7.99, -5.3) * mm});
            skLineSegment(sketch, "E1363", {"start": v(-7.99, -5.3) * mm, "end": v(-7.98, -5.3) * mm});
            skLineSegment(sketch, "E1364", {"start": v(-7.98, -5.3) * mm, "end": v(-8, -5.44) * mm});
            skLineSegment(sketch, "E1365", {"start": v(-8, -5.44) * mm, "end": v(-8, -5.44) * mm});
            skLineSegment(sketch, "E1366", {"start": v(-8, -5.44) * mm, "end": v(-8.07, -5.73) * mm});
            skLineSegment(sketch, "E1367", {"start": v(-8.07, -5.73) * mm, "end": v(-8.07, -5.74) * mm});
            skLineSegment(sketch, "E1368", {"start": v(-8.07, -5.74) * mm, "end": v(-8.08, -5.78) * mm});
            skLineSegment(sketch, "E1369", {"start": v(-8.08, -5.78) * mm, "end": v(-8.09, -5.83) * mm});
            skLineSegment(sketch, "E1370", {"start": v(-8.09, -5.83) * mm, "end": v(-8.1, -5.9) * mm});
            skLineSegment(sketch, "E1371", {"start": v(-8.1, -5.9) * mm, "end": v(-8.1, -5.97) * mm});
            skLineSegment(sketch, "E1372", {"start": v(-8.1, -5.97) * mm, "end": v(-8.1, -6.06) * mm});
            skLineSegment(sketch, "E1373", {"start": v(-8.1, -6.06) * mm, "end": v(-8.1, -6.16) * mm});
            skLineSegment(sketch, "E1374", {"start": v(-8.1, -6.16) * mm, "end": v(-8.11, -6.24) * mm});
            skLineSegment(sketch, "E1375", {"start": v(-8.11, -6.24) * mm, "end": v(-8.11, -6.3) * mm});
            skLineSegment(sketch, "E1376", {"start": v(-8.11, -6.3) * mm, "end": v(-8.1, -6.4) * mm});
            skLineSegment(sketch, "E1377", {"start": v(-8.1, -6.4) * mm, "end": v(-8.1, -6.52) * mm});
            skLineSegment(sketch, "E1378", {"start": v(-8.1, -6.52) * mm, "end": v(-8.1, -6.66) * mm});
            skLineSegment(sketch, "E1379", {"start": v(-8.1, -6.66) * mm, "end": v(-8.1, -6.8) * mm});
            skLineSegment(sketch, "E1380", {"start": v(-8.1, -6.8) * mm, "end": v(-8.08, -6.94) * mm});
            skLineSegment(sketch, "E1381", {"start": v(-8.08, -6.94) * mm, "end": v(-8.06, -7.1) * mm});
            skLineSegment(sketch, "E1382", {"start": v(-8.06, -7.1) * mm, "end": v(-8.05, -7.25) * mm});
            skLineSegment(sketch, "E1383", {"start": v(-8.05, -7.25) * mm, "end": v(-8.03, -7.4) * mm});
            skLineSegment(sketch, "E1384", {"start": v(-8.03, -7.4) * mm, "end": v(-8, -7.57) * mm});
            skLineSegment(sketch, "E1385", {"start": v(-8, -7.57) * mm, "end": v(-7.88, -8.33) * mm});
            skLineSegment(sketch, "E1386", {"start": v(-7.88, -8.33) * mm, "end": v(-7.74, -8.37) * mm});
            skLineSegment(sketch, "E1387", {"start": v(-7.74, -8.37) * mm, "end": v(-7.33, -8.47) * mm});
            skLineSegment(sketch, "E1388", {"start": v(-7.33, -8.47) * mm, "end": v(-6.92, -8.57) * mm});
            skLineSegment(sketch, "E1389", {"start": v(-6.92, -8.57) * mm, "end": v(-6.8, -8.6) * mm});
            skLineSegment(sketch, "E1390", {"start": v(-6.8, -8.6) * mm, "end": v(-6.33, -7.98) * mm});
            skLineSegment(sketch, "E1391", {"start": v(-6.33, -7.98) * mm, "end": v(-6.23, -7.84) * mm});
            skLineSegment(sketch, "E1392", {"start": v(-6.23, -7.84) * mm, "end": v(-6.13, -7.7) * mm});
            skLineSegment(sketch, "E1393", {"start": v(-6.13, -7.7) * mm, "end": v(-6.04, -7.57) * mm});
            skLineSegment(sketch, "E1394", {"start": v(-6.04, -7.57) * mm, "end": v(-5.96, -7.45) * mm});
            skLineSegment(sketch, "E1395", {"start": v(-5.96, -7.45) * mm, "end": v(-5.88, -7.33) * mm});
            skLineSegment(sketch, "E1396", {"start": v(-5.88, -7.33) * mm, "end": v(-5.81, -7.21) * mm});
            skLineSegment(sketch, "E1397", {"start": v(-5.81, -7.21) * mm, "end": v(-5.74, -7.1) * mm});
            skLineSegment(sketch, "E1398", {"start": v(-5.74, -7.1) * mm, "end": v(-5.68, -6.99) * mm});
            skLineSegment(sketch, "E1399", {"start": v(-5.68, -6.99) * mm, "end": v(-5.64, -6.92) * mm});
            skLineSegment(sketch, "E1400", {"start": v(-5.64, -6.92) * mm, "end": v(-5.61, -6.86) * mm});
            skLineSegment(sketch, "E1401", {"start": v(-5.61, -6.86) * mm, "end": v(-5.57, -6.8) * mm});
            skLineSegment(sketch, "E1402", {"start": v(-5.57, -6.8) * mm, "end": v(-5.52, -6.7) * mm});
            skLineSegment(sketch, "E1403", {"start": v(-5.52, -6.7) * mm, "end": v(-5.48, -6.6) * mm});
            skLineSegment(sketch, "E1404", {"start": v(-5.48, -6.6) * mm, "end": v(-5.43, -6.52) * mm});
            skLineSegment(sketch, "E1405", {"start": v(-5.43, -6.52) * mm, "end": v(-5.4, -6.44) * mm});
            skLineSegment(sketch, "E1406", {"start": v(-5.4, -6.44) * mm, "end": v(-5.36, -6.36) * mm});
            skLineSegment(sketch, "E1407", {"start": v(-5.36, -6.36) * mm, "end": v(-5.33, -6.3) * mm});
            skLineSegment(sketch, "E1408", {"start": v(-5.33, -6.3) * mm, "end": v(-5.3, -6.22) * mm});
            skLineSegment(sketch, "E1409", {"start": v(-5.3, -6.22) * mm, "end": v(-5.26, -6.15) * mm});
            skLineSegment(sketch, "E1410", {"start": v(-5.26, -6.15) * mm, "end": v(-5.24, -6.1) * mm});
            skLineSegment(sketch, "E1411", {"start": v(-5.24, -6.1) * mm, "end": v(-5.1, -5.76) * mm});
            skLineSegment(sketch, "E1412", {"start": v(-5.1, -5.76) * mm, "end": v(-5.1, -5.74) * mm});
            skLineSegment(sketch, "E1413", {"start": v(-5.1, -5.74) * mm, "end": v(-5.07, -5.7) * mm});
            skLineSegment(sketch, "E1414", {"start": v(-5.07, -5.7) * mm, "end": v(-5.05, -5.66) * mm});
            skLineSegment(sketch, "E1415", {"start": v(-5.05, -5.66) * mm, "end": v(-5.03, -5.63) * mm});
            skLineSegment(sketch, "E1416", {"start": v(-5.03, -5.63) * mm, "end": v(-5, -5.6) * mm});
            skLineSegment(sketch, "E1417", {"start": v(-5, -5.6) * mm, "end": v(-4.98, -5.57) * mm});
            skLineSegment(sketch, "E1418", {"start": v(-4.98, -5.57) * mm, "end": v(-4.95, -5.55) * mm});
            skLineSegment(sketch, "E1419", {"start": v(-4.95, -5.55) * mm, "end": v(-4.92, -5.53) * mm});
            skLineSegment(sketch, "E1420", {"start": v(-4.92, -5.53) * mm, "end": v(-4.9, -5.51) * mm});
            skLineSegment(sketch, "E1421", {"start": v(-4.9, -5.51) * mm, "end": v(-4.87, -5.5) * mm});
            skLineSegment(sketch, "E1422", {"start": v(-4.87, -5.5) * mm, "end": v(-4.86, -5.5) * mm});
            skLineSegment(sketch, "E1423", {"start": v(-4.86, -5.5) * mm, "end": v(-4.85, -5.5) * mm});
            skLineSegment(sketch, "E1424", {"start": v(-4.85, -5.5) * mm, "end": v(-4.83, -5.5) * mm});
            skLineSegment(sketch, "E1425", {"start": v(-4.83, -5.5) * mm, "end": v(-4.82, -5.5) * mm});
            skLineSegment(sketch, "E1426", {"start": v(-4.82, -5.5) * mm, "end": v(-4.72, -5.52) * mm});
            skLineSegment(sketch, "E1427", {"start": v(-4.72, -5.52) * mm, "end": v(-4.46, -5.56) * mm});
            skLineSegment(sketch, "E1428", {"start": v(-4.46, -5.56) * mm, "end": v(-4.27, -5.59) * mm});
            skLineSegment(sketch, "E1429", {"start": v(-4.27, -5.59) * mm, "end": v(-4.02, -5.63) * mm});
            skLineSegment(sketch, "E1430", {"start": v(-4.02, -5.63) * mm, "end": v(-3.91, -5.64) * mm});
            skLineSegment(sketch, "E1431", {"start": v(-3.91, -5.64) * mm, "end": v(-3.9, -5.64) * mm});
            skLineSegment(sketch, "E1432", {"start": v(-3.9, -5.64) * mm, "end": v(-3.89, -5.65) * mm});
            skLineSegment(sketch, "E1433", {"start": v(-3.89, -5.65) * mm, "end": v(-3.87, -5.65) * mm});
            skLineSegment(sketch, "E1434", {"start": v(-3.87, -5.65) * mm, "end": v(-3.86, -5.66) * mm});
            skLineSegment(sketch, "E1435", {"start": v(-3.86, -5.66) * mm, "end": v(-3.84, -5.68) * mm});
            skLineSegment(sketch, "E1436", {"start": v(-3.84, -5.68) * mm, "end": v(-3.81, -5.7) * mm});
            skLineSegment(sketch, "E1437", {"start": v(-3.81, -5.7) * mm, "end": v(-3.8, -5.74) * mm});
            skLineSegment(sketch, "E1438", {"start": v(-3.8, -5.74) * mm, "end": v(-3.77, -5.78) * mm});
            skLineSegment(sketch, "E1439", {"start": v(-3.77, -5.78) * mm, "end": v(-3.75, -5.8) * mm});
            skLineSegment(sketch, "E1440", {"start": v(-3.75, -5.8) * mm, "end": v(-3.75, -5.85) * mm});
            skLineSegment(sketch, "E1441", {"start": v(-3.75, -5.85) * mm, "end": v(-3.73, -5.89) * mm});
            skLineSegment(sketch, "E1442", {"start": v(-3.73, -5.89) * mm, "end": v(-3.72, -5.92) * mm});
            skLineSegment(sketch, "E1443", {"start": v(-3.72, -5.92) * mm, "end": v(-3.71, -5.99) * mm});
            skLineSegment(sketch, "E1444", {"start": v(-3.71, -5.99) * mm, "end": v(-3.7, -5.99) * mm});
            skLineSegment(sketch, "E1445", {"start": v(-3.7, -5.99) * mm, "end": v(-3.7, -6.07) * mm});
            skLineSegment(sketch, "E1446", {"start": v(-3.7, -6.07) * mm, "end": v(-3.7, -6.07) * mm});
            skLineSegment(sketch, "E1447", {"start": v(-3.7, -6.07) * mm, "end": v(-3.68, -6.4) * mm});
            skLineSegment(sketch, "E1448", {"start": v(-3.68, -6.4) * mm, "end": v(-3.67, -6.47) * mm});
            skLineSegment(sketch, "E1449", {"start": v(-3.67, -6.47) * mm, "end": v(-3.67, -6.54) * mm});
            skLineSegment(sketch, "E1450", {"start": v(-3.67, -6.54) * mm, "end": v(-3.66, -6.62) * mm});
            skLineSegment(sketch, "E1451", {"start": v(-3.66, -6.62) * mm, "end": v(-3.65, -6.7) * mm});
            skLineSegment(sketch, "E1452", {"start": v(-3.65, -6.7) * mm, "end": v(-3.64, -6.8) * mm});
            skLineSegment(sketch, "E1453", {"start": v(-3.64, -6.8) * mm, "end": v(-3.62, -6.9) * mm});
            skLineSegment(sketch, "E1454", {"start": v(-3.62, -6.9) * mm, "end": v(-3.6, -7) * mm});
            skLineSegment(sketch, "E1455", {"start": v(-3.6, -7) * mm, "end": v(-3.6, -7.1) * mm});
            skLineSegment(sketch, "E1456", {"start": v(-3.6, -7.1) * mm, "end": v(-3.57, -7.18) * mm});
            skLineSegment(sketch, "E1457", {"start": v(-3.57, -7.18) * mm, "end": v(-3.56, -7.24) * mm});
            skLineSegment(sketch, "E1458", {"start": v(-3.56, -7.24) * mm, "end": v(-3.55, -7.32) * mm});
            skLineSegment(sketch, "E1459", {"start": v(-3.55, -7.32) * mm, "end": v(-3.52, -7.44) * mm});
            skLineSegment(sketch, "E1460", {"start": v(-3.52, -7.44) * mm, "end": v(-3.5, -7.56) * mm});
            skLineSegment(sketch, "E1461", {"start": v(-3.5, -7.56) * mm, "end": v(-3.46, -7.68) * mm});
            skLineSegment(sketch, "E1462", {"start": v(-3.46, -7.68) * mm, "end": v(-3.43, -7.8) * mm});
            skLineSegment(sketch, "E1463", {"start": v(-3.43, -7.8) * mm, "end": v(-3.4, -7.93) * mm});
            skLineSegment(sketch, "E1464", {"start": v(-3.4, -7.93) * mm, "end": v(-3.36, -8.06) * mm});
            skLineSegment(sketch, "E1465", {"start": v(-3.36, -8.06) * mm, "end": v(-3.33, -8.19) * mm});
            skLineSegment(sketch, "E1466", {"start": v(-3.33, -8.19) * mm, "end": v(-3.28, -8.32) * mm});
            skLineSegment(sketch, "E1467", {"start": v(-3.28, -8.32) * mm, "end": v(-3.24, -8.45) * mm});
            skLineSegment(sketch, "E1468", {"start": v(-3.24, -8.45) * mm, "end": v(-3, -9.2) * mm});
            skLineSegment(sketch, "E1469", {"start": v(-3, -9.2) * mm, "end": v(-2.98, -9.2) * mm});
            skLineSegment(sketch, "E1470", {"start": v(-2.98, -9.2) * mm, "end": v(-2.61, -9.24) * mm});
            skLineSegment(sketch, "E1471", {"start": v(-2.61, -9.24) * mm, "end": v(-2.25, -9.26) * mm});
            skLineSegment(sketch, "E1472", {"start": v(-2.25, -9.26) * mm, "end": v(-1.89, -9.29) * mm});
            skLineSegment(sketch, "E1473", {"start": v(-1.89, -9.29) * mm, "end": v(-1.86, -9.29) * mm});
            skLineSegment(sketch, "E1474", {"start": v(-1.86, -9.29) * mm, "end": v(-1.48, -8.52) * mm});
            skSolve(sketch);
        }
        {
            var Q0;
            Q0 = qSketchRegion(id + "F2", true);
            extrude(context, id + "F3", {"entities" : qUnion([Q0]), "depth" : 5 * mm, "offsetDistance" : 25 * mm});
        }
        {
            var Q0;
            Q0=qCreatedBy(makeId("Front.planeOp"),FACE);
            var sketch = newSketch(context, id + "F4", { "sketchPlane" : qUnion([Q0])});
            skCircle(sketch, "E1475", {"center": v(0, 0) * mm, "radius": 3 * mm});
            skSolve(sketch);
        }
        {
            var Q0;
            Q0 = qSketchRegion(id + "F4", true);
            var Q1;
            Q1=makeQuery(id+"F3.opExtrude","CAP_FACE",FACE,{"disambiguationData":[OSD([sQuery(id+"F2.wireOp",EDGE,"E16"),sQuery(id+"F2.wireOp",EDGE,"E17"),sQuery(id+"F2.wireOp",EDGE,"E18"),sQuery(id+"F2.wireOp",EDGE,"E19"),sQuery(id+"F2.wireOp",EDGE,"E20"),sQuery(id+"F2.wireOp",EDGE,"E21"),sQuery(id+"F2.wireOp",EDGE,"E22"),sQuery(id+"F2.wireOp",EDGE,"E23"),sQuery(id+"F2.wireOp",EDGE,"E24"),sQuery(id+"F2.wireOp",EDGE,"E25"),sQuery(id+"F2.wireOp",EDGE,"E26"),sQuery(id+"F2.wireOp",EDGE,"E27"),sQuery(id+"F2.wireOp",EDGE,"E28"),sQuery(id+"F2.wireOp",EDGE,"E29"),sQuery(id+"F2.wireOp",EDGE,"E30"),sQuery(id+"F2.wireOp",EDGE,"E31"),sQuery(id+"F2.wireOp",EDGE,"E32"),sQuery(id+"F2.wireOp",EDGE,"E33"),sQuery(id+"F2.wireOp",EDGE,"E34"),sQuery(id+"F2.wireOp",EDGE,"E35"),sQuery(id+"F2.wireOp",EDGE,"E36"),sQuery(id+"F2.wireOp",EDGE,"E37"),sQuery(id+"F2.wireOp",EDGE,"E38"),sQuery(id+"F2.wireOp",EDGE,"E39"),sQuery(id+"F2.wireOp",EDGE,"E40"),sQuery(id+"F2.wireOp",EDGE,"E41"),sQuery(id+"F2.wireOp",EDGE,"E42"),sQuery(id+"F2.wireOp",EDGE,"E43"),sQuery(id+"F2.wireOp",EDGE,"E44"),sQuery(id+"F2.wireOp",EDGE,"E45"),sQuery(id+"F2.wireOp",EDGE,"E46"),sQuery(id+"F2.wireOp",EDGE,"E47"),sQuery(id+"F2.wireOp",EDGE,"E48"),sQuery(id+"F2.wireOp",EDGE,"E49"),sQuery(id+"F2.wireOp",EDGE,"E50"),sQuery(id+"F2.wireOp",EDGE,"E51"),sQuery(id+"F2.wireOp",EDGE,"E52"),sQuery(id+"F2.wireOp",EDGE,"E53"),sQuery(id+"F2.wireOp",EDGE,"E54"),sQuery(id+"F2.wireOp",EDGE,"E55"),sQuery(id+"F2.wireOp",EDGE,"E56"),sQuery(id+"F2.wireOp",EDGE,"E57"),sQuery(id+"F2.wireOp",EDGE,"E58"),sQuery(id+"F2.wireOp",EDGE,"E59"),sQuery(id+"F2.wireOp",EDGE,"E60"),sQuery(id+"F2.wireOp",EDGE,"E61"),sQuery(id+"F2.wireOp",EDGE,"E62"),sQuery(id+"F2.wireOp",EDGE,"E63"),sQuery(id+"F2.wireOp",EDGE,"E64"),sQuery(id+"F2.wireOp",EDGE,"E65"),sQuery(id+"F2.wireOp",EDGE,"E66"),sQuery(id+"F2.wireOp",EDGE,"E67"),sQuery(id+"F2.wireOp",EDGE,"E68"),sQuery(id+"F2.wireOp",EDGE,"E69"),sQuery(id+"F2.wireOp",EDGE,"E70"),sQuery(id+"F2.wireOp",EDGE,"E71"),sQuery(id+"F2.wireOp",EDGE,"E72"),sQuery(id+"F2.wireOp",EDGE,"E73"),sQuery(id+"F2.wireOp",EDGE,"E74"),sQuery(id+"F2.wireOp",EDGE,"E75"),sQuery(id+"F2.wireOp",EDGE,"E76"),sQuery(id+"F2.wireOp",EDGE,"E77"),sQuery(id+"F2.wireOp",EDGE,"E78"),sQuery(id+"F2.wireOp",EDGE,"E79"),sQuery(id+"F2.wireOp",EDGE,"E80"),sQuery(id+"F2.wireOp",EDGE,"E81"),sQuery(id+"F2.wireOp",EDGE,"E82"),sQuery(id+"F2.wireOp",EDGE,"E83"),sQuery(id+"F2.wireOp",EDGE,"E84"),sQuery(id+"F2.wireOp",EDGE,"E85"),sQuery(id+"F2.wireOp",EDGE,"E86"),sQuery(id+"F2.wireOp",EDGE,"E87"),sQuery(id+"F2.wireOp",EDGE,"E88"),sQuery(id+"F2.wireOp",EDGE,"E89"),sQuery(id+"F2.wireOp",EDGE,"E90"),sQuery(id+"F2.wireOp",EDGE,"E91"),sQuery(id+"F2.wireOp",EDGE,"E92"),sQuery(id+"F2.wireOp",EDGE,"E93"),sQuery(id+"F2.wireOp",EDGE,"E94"),sQuery(id+"F2.wireOp",EDGE,"E95"),sQuery(id+"F2.wireOp",EDGE,"E96"),sQuery(id+"F2.wireOp",EDGE,"E97"),sQuery(id+"F2.wireOp",EDGE,"E98"),sQuery(id+"F2.wireOp",EDGE,"E99"),sQuery(id+"F2.wireOp",EDGE,"E100"),sQuery(id+"F2.wireOp",EDGE,"E101"),sQuery(id+"F2.wireOp",EDGE,"E102"),sQuery(id+"F2.wireOp",EDGE,"E103"),sQuery(id+"F2.wireOp",EDGE,"E104"),sQuery(id+"F2.wireOp",EDGE,"E105"),sQuery(id+"F2.wireOp",EDGE,"E106"),sQuery(id+"F2.wireOp",EDGE,"E107"),sQuery(id+"F2.wireOp",EDGE,"E108"),sQuery(id+"F2.wireOp",EDGE,"E109"),sQuery(id+"F2.wireOp",EDGE,"E110"),sQuery(id+"F2.wireOp",EDGE,"E111"),sQuery(id+"F2.wireOp",EDGE,"E112"),sQuery(id+"F2.wireOp",EDGE,"E113"),sQuery(id+"F2.wireOp",EDGE,"E114"),sQuery(id+"F2.wireOp",EDGE,"E115"),sQuery(id+"F2.wireOp",EDGE,"E116"),sQuery(id+"F2.wireOp",EDGE,"E117"),sQuery(id+"F2.wireOp",EDGE,"E118"),sQuery(id+"F2.wireOp",EDGE,"E119"),sQuery(id+"F2.wireOp",EDGE,"E120"),sQuery(id+"F2.wireOp",EDGE,"E121"),sQuery(id+"F2.wireOp",EDGE,"E122"),sQuery(id+"F2.wireOp",EDGE,"E123"),sQuery(id+"F2.wireOp",EDGE,"E124"),sQuery(id+"F2.wireOp",EDGE,"E125"),sQuery(id+"F2.wireOp",EDGE,"E126"),sQuery(id+"F2.wireOp",EDGE,"E127"),sQuery(id+"F2.wireOp",EDGE,"E128"),sQuery(id+"F2.wireOp",EDGE,"E129"),sQuery(id+"F2.wireOp",EDGE,"E130"),sQuery(id+"F2.wireOp",EDGE,"E131"),sQuery(id+"F2.wireOp",EDGE,"E132"),sQuery(id+"F2.wireOp",EDGE,"E133"),sQuery(id+"F2.wireOp",EDGE,"E134"),sQuery(id+"F2.wireOp",EDGE,"E135"),sQuery(id+"F2.wireOp",EDGE,"E136"),sQuery(id+"F2.wireOp",EDGE,"E137"),sQuery(id+"F2.wireOp",EDGE,"E138"),sQuery(id+"F2.wireOp",EDGE,"E139"),sQuery(id+"F2.wireOp",EDGE,"E140"),sQuery(id+"F2.wireOp",EDGE,"E141"),sQuery(id+"F2.wireOp",EDGE,"E142"),sQuery(id+"F2.wireOp",EDGE,"E143"),sQuery(id+"F2.wireOp",EDGE,"E144"),sQuery(id+"F2.wireOp",EDGE,"E145"),sQuery(id+"F2.wireOp",EDGE,"E146"),sQuery(id+"F2.wireOp",EDGE,"E147"),sQuery(id+"F2.wireOp",EDGE,"E148"),sQuery(id+"F2.wireOp",EDGE,"E149"),sQuery(id+"F2.wireOp",EDGE,"E150"),sQuery(id+"F2.wireOp",EDGE,"E151"),sQuery(id+"F2.wireOp",EDGE,"E152"),sQuery(id+"F2.wireOp",EDGE,"E153"),sQuery(id+"F2.wireOp",EDGE,"E154"),sQuery(id+"F2.wireOp",EDGE,"E155"),sQuery(id+"F2.wireOp",EDGE,"E156"),sQuery(id+"F2.wireOp",EDGE,"E157"),sQuery(id+"F2.wireOp",EDGE,"E158"),sQuery(id+"F2.wireOp",EDGE,"E159"),sQuery(id+"F2.wireOp",EDGE,"E160"),sQuery(id+"F2.wireOp",EDGE,"E161"),sQuery(id+"F2.wireOp",EDGE,"E162"),sQuery(id+"F2.wireOp",EDGE,"E163"),sQuery(id+"F2.wireOp",EDGE,"E164"),sQuery(id+"F2.wireOp",EDGE,"E165"),sQuery(id+"F2.wireOp",EDGE,"E166"),sQuery(id+"F2.wireOp",EDGE,"E167"),sQuery(id+"F2.wireOp",EDGE,"E168"),sQuery(id+"F2.wireOp",EDGE,"E169"),sQuery(id+"F2.wireOp",EDGE,"E170"),sQuery(id+"F2.wireOp",EDGE,"E171"),sQuery(id+"F2.wireOp",EDGE,"E172"),sQuery(id+"F2.wireOp",EDGE,"E173"),sQuery(id+"F2.wireOp",EDGE,"E174"),sQuery(id+"F2.wireOp",EDGE,"E175"),sQuery(id+"F2.wireOp",EDGE,"E176"),sQuery(id+"F2.wireOp",EDGE,"E177"),sQuery(id+"F2.wireOp",EDGE,"E178"),sQuery(id+"F2.wireOp",EDGE,"E179"),sQuery(id+"F2.wireOp",EDGE,"E180"),sQuery(id+"F2.wireOp",EDGE,"E181"),sQuery(id+"F2.wireOp",EDGE,"E182"),sQuery(id+"F2.wireOp",EDGE,"E183"),sQuery(id+"F2.wireOp",EDGE,"E184"),sQuery(id+"F2.wireOp",EDGE,"E185"),sQuery(id+"F2.wireOp",EDGE,"E186"),sQuery(id+"F2.wireOp",EDGE,"E187"),sQuery(id+"F2.wireOp",EDGE,"E188"),sQuery(id+"F2.wireOp",EDGE,"E189"),sQuery(id+"F2.wireOp",EDGE,"E190"),sQuery(id+"F2.wireOp",EDGE,"E191"),sQuery(id+"F2.wireOp",EDGE,"E192"),sQuery(id+"F2.wireOp",EDGE,"E193"),sQuery(id+"F2.wireOp",EDGE,"E194"),sQuery(id+"F2.wireOp",EDGE,"E195"),sQuery(id+"F2.wireOp",EDGE,"E196"),sQuery(id+"F2.wireOp",EDGE,"E197"),sQuery(id+"F2.wireOp",EDGE,"E198"),sQuery(id+"F2.wireOp",EDGE,"E199"),sQuery(id+"F2.wireOp",EDGE,"E200"),sQuery(id+"F2.wireOp",EDGE,"E201"),sQuery(id+"F2.wireOp",EDGE,"E202"),sQuery(id+"F2.wireOp",EDGE,"E203"),sQuery(id+"F2.wireOp",EDGE,"E204"),sQuery(id+"F2.wireOp",EDGE,"E205"),sQuery(id+"F2.wireOp",EDGE,"E206"),sQuery(id+"F2.wireOp",EDGE,"E207"),sQuery(id+"F2.wireOp",EDGE,"E208"),sQuery(id+"F2.wireOp",EDGE,"E209"),sQuery(id+"F2.wireOp",EDGE,"E210"),sQuery(id+"F2.wireOp",EDGE,"E211"),sQuery(id+"F2.wireOp",EDGE,"E212"),sQuery(id+"F2.wireOp",EDGE,"E213"),sQuery(id+"F2.wireOp",EDGE,"E214"),sQuery(id+"F2.wireOp",EDGE,"E215"),sQuery(id+"F2.wireOp",EDGE,"E216"),sQuery(id+"F2.wireOp",EDGE,"E217"),sQuery(id+"F2.wireOp",EDGE,"E218"),sQuery(id+"F2.wireOp",EDGE,"E219"),sQuery(id+"F2.wireOp",EDGE,"E220"),sQuery(id+"F2.wireOp",EDGE,"E221"),sQuery(id+"F2.wireOp",EDGE,"E222"),sQuery(id+"F2.wireOp",EDGE,"E223"),sQuery(id+"F2.wireOp",EDGE,"E224"),sQuery(id+"F2.wireOp",EDGE,"E225"),sQuery(id+"F2.wireOp",EDGE,"E226"),sQuery(id+"F2.wireOp",EDGE,"E227"),sQuery(id+"F2.wireOp",EDGE,"E228"),sQuery(id+"F2.wireOp",EDGE,"E229"),sQuery(id+"F2.wireOp",EDGE,"E230"),sQuery(id+"F2.wireOp",EDGE,"E231"),sQuery(id+"F2.wireOp",EDGE,"E232"),sQuery(id+"F2.wireOp",EDGE,"E233"),sQuery(id+"F2.wireOp",EDGE,"E234"),sQuery(id+"F2.wireOp",EDGE,"E235"),sQuery(id+"F2.wireOp",EDGE,"E236"),sQuery(id+"F2.wireOp",EDGE,"E237"),sQuery(id+"F2.wireOp",EDGE,"E238"),sQuery(id+"F2.wireOp",EDGE,"E239"),sQuery(id+"F2.wireOp",EDGE,"E240"),sQuery(id+"F2.wireOp",EDGE,"E241"),sQuery(id+"F2.wireOp",EDGE,"E242"),sQuery(id+"F2.wireOp",EDGE,"E243"),sQuery(id+"F2.wireOp",EDGE,"E244"),sQuery(id+"F2.wireOp",EDGE,"E245"),sQuery(id+"F2.wireOp",EDGE,"E246"),sQuery(id+"F2.wireOp",EDGE,"E247"),sQuery(id+"F2.wireOp",EDGE,"E248"),sQuery(id+"F2.wireOp",EDGE,"E249"),sQuery(id+"F2.wireOp",EDGE,"E250"),sQuery(id+"F2.wireOp",EDGE,"E251"),sQuery(id+"F2.wireOp",EDGE,"E252"),sQuery(id+"F2.wireOp",EDGE,"E253"),sQuery(id+"F2.wireOp",EDGE,"E254"),sQuery(id+"F2.wireOp",EDGE,"E255"),sQuery(id+"F2.wireOp",EDGE,"E256"),sQuery(id+"F2.wireOp",EDGE,"E257"),sQuery(id+"F2.wireOp",EDGE,"E258"),sQuery(id+"F2.wireOp",EDGE,"E259"),sQuery(id+"F2.wireOp",EDGE,"E260"),sQuery(id+"F2.wireOp",EDGE,"E261"),sQuery(id+"F2.wireOp",EDGE,"E262"),sQuery(id+"F2.wireOp",EDGE,"E263"),sQuery(id+"F2.wireOp",EDGE,"E264"),sQuery(id+"F2.wireOp",EDGE,"E265"),sQuery(id+"F2.wireOp",EDGE,"E266"),sQuery(id+"F2.wireOp",EDGE,"E267"),sQuery(id+"F2.wireOp",EDGE,"E268"),sQuery(id+"F2.wireOp",EDGE,"E269"),sQuery(id+"F2.wireOp",EDGE,"E270"),sQuery(id+"F2.wireOp",EDGE,"E271"),sQuery(id+"F2.wireOp",EDGE,"E272"),sQuery(id+"F2.wireOp",EDGE,"E273"),sQuery(id+"F2.wireOp",EDGE,"E274"),sQuery(id+"F2.wireOp",EDGE,"E275"),sQuery(id+"F2.wireOp",EDGE,"E276"),sQuery(id+"F2.wireOp",EDGE,"E277"),sQuery(id+"F2.wireOp",EDGE,"E278"),sQuery(id+"F2.wireOp",EDGE,"E279"),sQuery(id+"F2.wireOp",EDGE,"E280"),sQuery(id+"F2.wireOp",EDGE,"E281"),sQuery(id+"F2.wireOp",EDGE,"E282"),sQuery(id+"F2.wireOp",EDGE,"E283"),sQuery(id+"F2.wireOp",EDGE,"E284"),sQuery(id+"F2.wireOp",EDGE,"E285"),sQuery(id+"F2.wireOp",EDGE,"E286"),sQuery(id+"F2.wireOp",EDGE,"E287"),sQuery(id+"F2.wireOp",EDGE,"E288"),sQuery(id+"F2.wireOp",EDGE,"E289"),sQuery(id+"F2.wireOp",EDGE,"E290"),sQuery(id+"F2.wireOp",EDGE,"E291"),sQuery(id+"F2.wireOp",EDGE,"E292"),sQuery(id+"F2.wireOp",EDGE,"E293"),sQuery(id+"F2.wireOp",EDGE,"E294"),sQuery(id+"F2.wireOp",EDGE,"E295"),sQuery(id+"F2.wireOp",EDGE,"E296"),sQuery(id+"F2.wireOp",EDGE,"E297"),sQuery(id+"F2.wireOp",EDGE,"E298"),sQuery(id+"F2.wireOp",EDGE,"E299"),sQuery(id+"F2.wireOp",EDGE,"E300"),sQuery(id+"F2.wireOp",EDGE,"E301"),sQuery(id+"F2.wireOp",EDGE,"E302"),sQuery(id+"F2.wireOp",EDGE,"E303"),sQuery(id+"F2.wireOp",EDGE,"E304"),sQuery(id+"F2.wireOp",EDGE,"E305"),sQuery(id+"F2.wireOp",EDGE,"E306"),sQuery(id+"F2.wireOp",EDGE,"E307"),sQuery(id+"F2.wireOp",EDGE,"E308"),sQuery(id+"F2.wireOp",EDGE,"E309"),sQuery(id+"F2.wireOp",EDGE,"E310"),sQuery(id+"F2.wireOp",EDGE,"E311"),sQuery(id+"F2.wireOp",EDGE,"E312"),sQuery(id+"F2.wireOp",EDGE,"E313"),sQuery(id+"F2.wireOp",EDGE,"E314"),sQuery(id+"F2.wireOp",EDGE,"E315"),sQuery(id+"F2.wireOp",EDGE,"E316"),sQuery(id+"F2.wireOp",EDGE,"E317"),sQuery(id+"F2.wireOp",EDGE,"E318"),sQuery(id+"F2.wireOp",EDGE,"E319"),sQuery(id+"F2.wireOp",EDGE,"E320"),sQuery(id+"F2.wireOp",EDGE,"E321"),sQuery(id+"F2.wireOp",EDGE,"E322"),sQuery(id+"F2.wireOp",EDGE,"E323"),sQuery(id+"F2.wireOp",EDGE,"E324"),sQuery(id+"F2.wireOp",EDGE,"E325"),sQuery(id+"F2.wireOp",EDGE,"E326"),sQuery(id+"F2.wireOp",EDGE,"E327"),sQuery(id+"F2.wireOp",EDGE,"E328"),sQuery(id+"F2.wireOp",EDGE,"E329"),sQuery(id+"F2.wireOp",EDGE,"E330"),sQuery(id+"F2.wireOp",EDGE,"E331"),sQuery(id+"F2.wireOp",EDGE,"E332"),sQuery(id+"F2.wireOp",EDGE,"E333"),sQuery(id+"F2.wireOp",EDGE,"E334"),sQuery(id+"F2.wireOp",EDGE,"E335"),sQuery(id+"F2.wireOp",EDGE,"E336"),sQuery(id+"F2.wireOp",EDGE,"E337"),sQuery(id+"F2.wireOp",EDGE,"E338"),sQuery(id+"F2.wireOp",EDGE,"E339"),sQuery(id+"F2.wireOp",EDGE,"E340"),sQuery(id+"F2.wireOp",EDGE,"E341"),sQuery(id+"F2.wireOp",EDGE,"E342"),sQuery(id+"F2.wireOp",EDGE,"E343"),sQuery(id+"F2.wireOp",EDGE,"E344"),sQuery(id+"F2.wireOp",EDGE,"E345"),sQuery(id+"F2.wireOp",EDGE,"E346"),sQuery(id+"F2.wireOp",EDGE,"E347"),sQuery(id+"F2.wireOp",EDGE,"E348"),sQuery(id+"F2.wireOp",EDGE,"E349"),sQuery(id+"F2.wireOp",EDGE,"E350"),sQuery(id+"F2.wireOp",EDGE,"E351"),sQuery(id+"F2.wireOp",EDGE,"E352"),sQuery(id+"F2.wireOp",EDGE,"E353"),sQuery(id+"F2.wireOp",EDGE,"E354"),sQuery(id+"F2.wireOp",EDGE,"E355"),sQuery(id+"F2.wireOp",EDGE,"E356"),sQuery(id+"F2.wireOp",EDGE,"E357"),sQuery(id+"F2.wireOp",EDGE,"E358"),sQuery(id+"F2.wireOp",EDGE,"E359"),sQuery(id+"F2.wireOp",EDGE,"E360"),sQuery(id+"F2.wireOp",EDGE,"E361"),sQuery(id+"F2.wireOp",EDGE,"E362"),sQuery(id+"F2.wireOp",EDGE,"E363"),sQuery(id+"F2.wireOp",EDGE,"E364"),sQuery(id+"F2.wireOp",EDGE,"E365"),sQuery(id+"F2.wireOp",EDGE,"E366"),sQuery(id+"F2.wireOp",EDGE,"E367"),sQuery(id+"F2.wireOp",EDGE,"E368"),sQuery(id+"F2.wireOp",EDGE,"E369"),sQuery(id+"F2.wireOp",EDGE,"E370"),sQuery(id+"F2.wireOp",EDGE,"E371"),sQuery(id+"F2.wireOp",EDGE,"E372"),sQuery(id+"F2.wireOp",EDGE,"E373"),sQuery(id+"F2.wireOp",EDGE,"E374"),sQuery(id+"F2.wireOp",EDGE,"E375"),sQuery(id+"F2.wireOp",EDGE,"E376"),sQuery(id+"F2.wireOp",EDGE,"E377"),sQuery(id+"F2.wireOp",EDGE,"E378"),sQuery(id+"F2.wireOp",EDGE,"E379"),sQuery(id+"F2.wireOp",EDGE,"E380"),sQuery(id+"F2.wireOp",EDGE,"E381"),sQuery(id+"F2.wireOp",EDGE,"E382"),sQuery(id+"F2.wireOp",EDGE,"E383"),sQuery(id+"F2.wireOp",EDGE,"E384"),sQuery(id+"F2.wireOp",EDGE,"E385"),sQuery(id+"F2.wireOp",EDGE,"E386"),sQuery(id+"F2.wireOp",EDGE,"E387"),sQuery(id+"F2.wireOp",EDGE,"E388"),sQuery(id+"F2.wireOp",EDGE,"E389"),sQuery(id+"F2.wireOp",EDGE,"E390"),sQuery(id+"F2.wireOp",EDGE,"E391"),sQuery(id+"F2.wireOp",EDGE,"E392"),sQuery(id+"F2.wireOp",EDGE,"E393"),sQuery(id+"F2.wireOp",EDGE,"E394"),sQuery(id+"F2.wireOp",EDGE,"E395"),sQuery(id+"F2.wireOp",EDGE,"E396"),sQuery(id+"F2.wireOp",EDGE,"E397"),sQuery(id+"F2.wireOp",EDGE,"E398"),sQuery(id+"F2.wireOp",EDGE,"E399"),sQuery(id+"F2.wireOp",EDGE,"E400"),sQuery(id+"F2.wireOp",EDGE,"E401"),sQuery(id+"F2.wireOp",EDGE,"E402"),sQuery(id+"F2.wireOp",EDGE,"E403"),sQuery(id+"F2.wireOp",EDGE,"E404"),sQuery(id+"F2.wireOp",EDGE,"E405"),sQuery(id+"F2.wireOp",EDGE,"E406"),sQuery(id+"F2.wireOp",EDGE,"E407"),sQuery(id+"F2.wireOp",EDGE,"E408"),sQuery(id+"F2.wireOp",EDGE,"E409"),sQuery(id+"F2.wireOp",EDGE,"E410"),sQuery(id+"F2.wireOp",EDGE,"E411"),sQuery(id+"F2.wireOp",EDGE,"E412"),sQuery(id+"F2.wireOp",EDGE,"E413"),sQuery(id+"F2.wireOp",EDGE,"E414"),sQuery(id+"F2.wireOp",EDGE,"E415"),sQuery(id+"F2.wireOp",EDGE,"E416"),sQuery(id+"F2.wireOp",EDGE,"E417"),sQuery(id+"F2.wireOp",EDGE,"E418"),sQuery(id+"F2.wireOp",EDGE,"E419"),sQuery(id+"F2.wireOp",EDGE,"E420"),sQuery(id+"F2.wireOp",EDGE,"E421"),sQuery(id+"F2.wireOp",EDGE,"E422"),sQuery(id+"F2.wireOp",EDGE,"E423"),sQuery(id+"F2.wireOp",EDGE,"E424"),sQuery(id+"F2.wireOp",EDGE,"E425"),sQuery(id+"F2.wireOp",EDGE,"E426"),sQuery(id+"F2.wireOp",EDGE,"E427"),sQuery(id+"F2.wireOp",EDGE,"E428"),sQuery(id+"F2.wireOp",EDGE,"E429"),sQuery(id+"F2.wireOp",EDGE,"E430"),sQuery(id+"F2.wireOp",EDGE,"E431"),sQuery(id+"F2.wireOp",EDGE,"E432"),sQuery(id+"F2.wireOp",EDGE,"E433"),sQuery(id+"F2.wireOp",EDGE,"E434"),sQuery(id+"F2.wireOp",EDGE,"E435"),sQuery(id+"F2.wireOp",EDGE,"E436"),sQuery(id+"F2.wireOp",EDGE,"E437"),sQuery(id+"F2.wireOp",EDGE,"E438"),sQuery(id+"F2.wireOp",EDGE,"E439"),sQuery(id+"F2.wireOp",EDGE,"E440"),sQuery(id+"F2.wireOp",EDGE,"E441"),sQuery(id+"F2.wireOp",EDGE,"E442"),sQuery(id+"F2.wireOp",EDGE,"E443"),sQuery(id+"F2.wireOp",EDGE,"E444"),sQuery(id+"F2.wireOp",EDGE,"E445"),sQuery(id+"F2.wireOp",EDGE,"E446"),sQuery(id+"F2.wireOp",EDGE,"E447"),sQuery(id+"F2.wireOp",EDGE,"E447"),sQuery(id+"F2.wireOp",EDGE,"E447"),sQuery(id+"F2.wireOp",EDGE,"E448"),sQuery(id+"F2.wireOp",EDGE,"E449"),sQuery(id+"F2.wireOp",EDGE,"E450"),sQuery(id+"F2.wireOp",EDGE,"E451"),sQuery(id+"F2.wireOp",EDGE,"E452"),sQuery(id+"F2.wireOp",EDGE,"E453"),sQuery(id+"F2.wireOp",EDGE,"E454"),sQuery(id+"F2.wireOp",EDGE,"E455"),sQuery(id+"F2.wireOp",EDGE,"E456"),sQuery(id+"F2.wireOp",EDGE,"E457"),sQuery(id+"F2.wireOp",EDGE,"E458"),sQuery(id+"F2.wireOp",EDGE,"E459"),sQuery(id+"F2.wireOp",EDGE,"E460"),sQuery(id+"F2.wireOp",EDGE,"E461"),sQuery(id+"F2.wireOp",EDGE,"E462"),sQuery(id+"F2.wireOp",EDGE,"E463"),sQuery(id+"F2.wireOp",EDGE,"E464"),sQuery(id+"F2.wireOp",EDGE,"E465"),sQuery(id+"F2.wireOp",EDGE,"E466"),sQuery(id+"F2.wireOp",EDGE,"E467"),sQuery(id+"F2.wireOp",EDGE,"E468"),sQuery(id+"F2.wireOp",EDGE,"E469"),sQuery(id+"F2.wireOp",EDGE,"E470"),sQuery(id+"F2.wireOp",EDGE,"E471"),sQuery(id+"F2.wireOp",EDGE,"E472"),sQuery(id+"F2.wireOp",EDGE,"E473"),sQuery(id+"F2.wireOp",EDGE,"E474"),sQuery(id+"F2.wireOp",EDGE,"E475"),sQuery(id+"F2.wireOp",EDGE,"E476"),sQuery(id+"F2.wireOp",EDGE,"E477"),sQuery(id+"F2.wireOp",EDGE,"E478"),sQuery(id+"F2.wireOp",EDGE,"E479"),sQuery(id+"F2.wireOp",EDGE,"E480"),sQuery(id+"F2.wireOp",EDGE,"E481"),sQuery(id+"F2.wireOp",EDGE,"E482"),sQuery(id+"F2.wireOp",EDGE,"E483"),sQuery(id+"F2.wireOp",EDGE,"E484"),sQuery(id+"F2.wireOp",EDGE,"E485"),sQuery(id+"F2.wireOp",EDGE,"E486"),sQuery(id+"F2.wireOp",EDGE,"E487"),sQuery(id+"F2.wireOp",EDGE,"E488"),sQuery(id+"F2.wireOp",EDGE,"E489"),sQuery(id+"F2.wireOp",EDGE,"E490"),sQuery(id+"F2.wireOp",EDGE,"E491"),sQuery(id+"F2.wireOp",EDGE,"E492"),sQuery(id+"F2.wireOp",EDGE,"E493"),sQuery(id+"F2.wireOp",EDGE,"E494"),sQuery(id+"F2.wireOp",EDGE,"E495"),sQuery(id+"F2.wireOp",EDGE,"E496"),sQuery(id+"F2.wireOp",EDGE,"E497"),sQuery(id+"F2.wireOp",EDGE,"E498"),sQuery(id+"F2.wireOp",EDGE,"E499"),sQuery(id+"F2.wireOp",EDGE,"E500"),sQuery(id+"F2.wireOp",EDGE,"E501"),sQuery(id+"F2.wireOp",EDGE,"E502"),sQuery(id+"F2.wireOp",EDGE,"E503"),sQuery(id+"F2.wireOp",EDGE,"E504"),sQuery(id+"F2.wireOp",EDGE,"E505"),sQuery(id+"F2.wireOp",EDGE,"E506"),sQuery(id+"F2.wireOp",EDGE,"E507"),sQuery(id+"F2.wireOp",EDGE,"E508"),sQuery(id+"F2.wireOp",EDGE,"E509"),sQuery(id+"F2.wireOp",EDGE,"E510"),sQuery(id+"F2.wireOp",EDGE,"E511"),sQuery(id+"F2.wireOp",EDGE,"E512"),sQuery(id+"F2.wireOp",EDGE,"E513"),sQuery(id+"F2.wireOp",EDGE,"E514"),sQuery(id+"F2.wireOp",EDGE,"E515"),sQuery(id+"F2.wireOp",EDGE,"E516"),sQuery(id+"F2.wireOp",EDGE,"E517"),sQuery(id+"F2.wireOp",EDGE,"E518"),sQuery(id+"F2.wireOp",EDGE,"E519"),sQuery(id+"F2.wireOp",EDGE,"E520"),sQuery(id+"F2.wireOp",EDGE,"E521"),sQuery(id+"F2.wireOp",EDGE,"E522"),sQuery(id+"F2.wireOp",EDGE,"E523"),sQuery(id+"F2.wireOp",EDGE,"E524"),sQuery(id+"F2.wireOp",EDGE,"E525"),sQuery(id+"F2.wireOp",EDGE,"E526"),sQuery(id+"F2.wireOp",EDGE,"E527"),sQuery(id+"F2.wireOp",EDGE,"E528"),sQuery(id+"F2.wireOp",EDGE,"E529"),sQuery(id+"F2.wireOp",EDGE,"E530"),sQuery(id+"F2.wireOp",EDGE,"E531"),sQuery(id+"F2.wireOp",EDGE,"E532"),sQuery(id+"F2.wireOp",EDGE,"E533"),sQuery(id+"F2.wireOp",EDGE,"E534"),sQuery(id+"F2.wireOp",EDGE,"E535"),sQuery(id+"F2.wireOp",EDGE,"E536"),sQuery(id+"F2.wireOp",EDGE,"E537"),sQuery(id+"F2.wireOp",EDGE,"E538"),sQuery(id+"F2.wireOp",EDGE,"E539"),sQuery(id+"F2.wireOp",EDGE,"E540"),sQuery(id+"F2.wireOp",EDGE,"E541"),sQuery(id+"F2.wireOp",EDGE,"E542"),sQuery(id+"F2.wireOp",EDGE,"E543"),sQuery(id+"F2.wireOp",EDGE,"E544"),sQuery(id+"F2.wireOp",EDGE,"E545"),sQuery(id+"F2.wireOp",EDGE,"E546"),sQuery(id+"F2.wireOp",EDGE,"E547"),sQuery(id+"F2.wireOp",EDGE,"E547"),sQuery(id+"F2.wireOp",EDGE,"E548"),sQuery(id+"F2.wireOp",EDGE,"E549"),sQuery(id+"F2.wireOp",EDGE,"E550"),sQuery(id+"F2.wireOp",EDGE,"E551"),sQuery(id+"F2.wireOp",EDGE,"E552"),sQuery(id+"F2.wireOp",EDGE,"E553"),sQuery(id+"F2.wireOp",EDGE,"E554"),sQuery(id+"F2.wireOp",EDGE,"E555"),sQuery(id+"F2.wireOp",EDGE,"E556"),sQuery(id+"F2.wireOp",EDGE,"E557"),sQuery(id+"F2.wireOp",EDGE,"E558"),sQuery(id+"F2.wireOp",EDGE,"E559"),sQuery(id+"F2.wireOp",EDGE,"E560"),sQuery(id+"F2.wireOp",EDGE,"E561"),sQuery(id+"F2.wireOp",EDGE,"E562"),sQuery(id+"F2.wireOp",EDGE,"E563"),sQuery(id+"F2.wireOp",EDGE,"E564"),sQuery(id+"F2.wireOp",EDGE,"E565"),sQuery(id+"F2.wireOp",EDGE,"E566"),sQuery(id+"F2.wireOp",EDGE,"E567"),sQuery(id+"F2.wireOp",EDGE,"E568"),sQuery(id+"F2.wireOp",EDGE,"E569"),sQuery(id+"F2.wireOp",EDGE,"E570"),sQuery(id+"F2.wireOp",EDGE,"E571"),sQuery(id+"F2.wireOp",EDGE,"E572"),sQuery(id+"F2.wireOp",EDGE,"E573"),sQuery(id+"F2.wireOp",EDGE,"E574"),sQuery(id+"F2.wireOp",EDGE,"E575"),sQuery(id+"F2.wireOp",EDGE,"E576"),sQuery(id+"F2.wireOp",EDGE,"E577"),sQuery(id+"F2.wireOp",EDGE,"E578"),sQuery(id+"F2.wireOp",EDGE,"E579"),sQuery(id+"F2.wireOp",EDGE,"E580"),sQuery(id+"F2.wireOp",EDGE,"E581"),sQuery(id+"F2.wireOp",EDGE,"E582"),sQuery(id+"F2.wireOp",EDGE,"E583"),sQuery(id+"F2.wireOp",EDGE,"E584"),sQuery(id+"F2.wireOp",EDGE,"E585"),sQuery(id+"F2.wireOp",EDGE,"E586"),sQuery(id+"F2.wireOp",EDGE,"E587"),sQuery(id+"F2.wireOp",EDGE,"E588"),sQuery(id+"F2.wireOp",EDGE,"E589"),sQuery(id+"F2.wireOp",EDGE,"E590"),sQuery(id+"F2.wireOp",EDGE,"E591"),sQuery(id+"F2.wireOp",EDGE,"E592"),sQuery(id+"F2.wireOp",EDGE,"E593"),sQuery(id+"F2.wireOp",EDGE,"E594"),sQuery(id+"F2.wireOp",EDGE,"E595"),sQuery(id+"F2.wireOp",EDGE,"E596"),sQuery(id+"F2.wireOp",EDGE,"E597"),sQuery(id+"F2.wireOp",EDGE,"E598"),sQuery(id+"F2.wireOp",EDGE,"E599"),sQuery(id+"F2.wireOp",EDGE,"E600"),sQuery(id+"F2.wireOp",EDGE,"E601"),sQuery(id+"F2.wireOp",EDGE,"E602"),sQuery(id+"F2.wireOp",EDGE,"E603"),sQuery(id+"F2.wireOp",EDGE,"E604"),sQuery(id+"F2.wireOp",EDGE,"E605"),sQuery(id+"F2.wireOp",EDGE,"E606"),sQuery(id+"F2.wireOp",EDGE,"E607"),sQuery(id+"F2.wireOp",EDGE,"E608"),sQuery(id+"F2.wireOp",EDGE,"E609"),sQuery(id+"F2.wireOp",EDGE,"E610"),sQuery(id+"F2.wireOp",EDGE,"E611"),sQuery(id+"F2.wireOp",EDGE,"E612"),sQuery(id+"F2.wireOp",EDGE,"E613"),sQuery(id+"F2.wireOp",EDGE,"E614"),sQuery(id+"F2.wireOp",EDGE,"E615"),sQuery(id+"F2.wireOp",EDGE,"E616"),sQuery(id+"F2.wireOp",EDGE,"E617"),sQuery(id+"F2.wireOp",EDGE,"E618"),sQuery(id+"F2.wireOp",EDGE,"E619"),sQuery(id+"F2.wireOp",EDGE,"E620"),sQuery(id+"F2.wireOp",EDGE,"E621"),sQuery(id+"F2.wireOp",EDGE,"E622"),sQuery(id+"F2.wireOp",EDGE,"E623"),sQuery(id+"F2.wireOp",EDGE,"E624"),sQuery(id+"F2.wireOp",EDGE,"E625"),sQuery(id+"F2.wireOp",EDGE,"E626"),sQuery(id+"F2.wireOp",EDGE,"E627"),sQuery(id+"F2.wireOp",EDGE,"E628"),sQuery(id+"F2.wireOp",EDGE,"E629"),sQuery(id+"F2.wireOp",EDGE,"E630"),sQuery(id+"F2.wireOp",EDGE,"E631"),sQuery(id+"F2.wireOp",EDGE,"E632"),sQuery(id+"F2.wireOp",EDGE,"E633"),sQuery(id+"F2.wireOp",EDGE,"E634"),sQuery(id+"F2.wireOp",EDGE,"E635"),sQuery(id+"F2.wireOp",EDGE,"E636"),sQuery(id+"F2.wireOp",EDGE,"E637"),sQuery(id+"F2.wireOp",EDGE,"E638"),sQuery(id+"F2.wireOp",EDGE,"E639"),sQuery(id+"F2.wireOp",EDGE,"E640"),sQuery(id+"F2.wireOp",EDGE,"E641"),sQuery(id+"F2.wireOp",EDGE,"E642"),sQuery(id+"F2.wireOp",EDGE,"E643"),sQuery(id+"F2.wireOp",EDGE,"E644"),sQuery(id+"F2.wireOp",EDGE,"E645"),sQuery(id+"F2.wireOp",EDGE,"E646"),sQuery(id+"F2.wireOp",EDGE,"E647"),sQuery(id+"F2.wireOp",EDGE,"E648"),sQuery(id+"F2.wireOp",EDGE,"E649"),sQuery(id+"F2.wireOp",EDGE,"E650"),sQuery(id+"F2.wireOp",EDGE,"E651"),sQuery(id+"F2.wireOp",EDGE,"E652"),sQuery(id+"F2.wireOp",EDGE,"E653"),sQuery(id+"F2.wireOp",EDGE,"E654"),sQuery(id+"F2.wireOp",EDGE,"E655"),sQuery(id+"F2.wireOp",EDGE,"E656"),sQuery(id+"F2.wireOp",EDGE,"E657"),sQuery(id+"F2.wireOp",EDGE,"E658"),sQuery(id+"F2.wireOp",EDGE,"E659"),sQuery(id+"F2.wireOp",EDGE,"E660"),sQuery(id+"F2.wireOp",EDGE,"E661"),sQuery(id+"F2.wireOp",EDGE,"E662"),sQuery(id+"F2.wireOp",EDGE,"E663"),sQuery(id+"F2.wireOp",EDGE,"E664"),sQuery(id+"F2.wireOp",EDGE,"E665"),sQuery(id+"F2.wireOp",EDGE,"E666"),sQuery(id+"F2.wireOp",EDGE,"E667"),sQuery(id+"F2.wireOp",EDGE,"E668"),sQuery(id+"F2.wireOp",EDGE,"E669"),sQuery(id+"F2.wireOp",EDGE,"E670"),sQuery(id+"F2.wireOp",EDGE,"E671"),sQuery(id+"F2.wireOp",EDGE,"E672"),sQuery(id+"F2.wireOp",EDGE,"E673"),sQuery(id+"F2.wireOp",EDGE,"E674"),sQuery(id+"F2.wireOp",EDGE,"E675"),sQuery(id+"F2.wireOp",EDGE,"E676"),sQuery(id+"F2.wireOp",EDGE,"E677"),sQuery(id+"F2.wireOp",EDGE,"E678"),sQuery(id+"F2.wireOp",EDGE,"E679"),sQuery(id+"F2.wireOp",EDGE,"E680"),sQuery(id+"F2.wireOp",EDGE,"E681"),sQuery(id+"F2.wireOp",EDGE,"E682"),sQuery(id+"F2.wireOp",EDGE,"E683"),sQuery(id+"F2.wireOp",EDGE,"E684"),sQuery(id+"F2.wireOp",EDGE,"E685"),sQuery(id+"F2.wireOp",EDGE,"E686"),sQuery(id+"F2.wireOp",EDGE,"E687"),sQuery(id+"F2.wireOp",EDGE,"E688"),sQuery(id+"F2.wireOp",EDGE,"E689"),sQuery(id+"F2.wireOp",EDGE,"E690"),sQuery(id+"F2.wireOp",EDGE,"E691"),sQuery(id+"F2.wireOp",EDGE,"E692"),sQuery(id+"F2.wireOp",EDGE,"E693"),sQuery(id+"F2.wireOp",EDGE,"E694"),sQuery(id+"F2.wireOp",EDGE,"E695"),sQuery(id+"F2.wireOp",EDGE,"E696"),sQuery(id+"F2.wireOp",EDGE,"E697"),sQuery(id+"F2.wireOp",EDGE,"E698"),sQuery(id+"F2.wireOp",EDGE,"E699"),sQuery(id+"F2.wireOp",EDGE,"E700"),sQuery(id+"F2.wireOp",EDGE,"E701"),sQuery(id+"F2.wireOp",EDGE,"E702"),sQuery(id+"F2.wireOp",EDGE,"E703"),sQuery(id+"F2.wireOp",EDGE,"E704"),sQuery(id+"F2.wireOp",EDGE,"E705"),sQuery(id+"F2.wireOp",EDGE,"E706"),sQuery(id+"F2.wireOp",EDGE,"E707"),sQuery(id+"F2.wireOp",EDGE,"E708"),sQuery(id+"F2.wireOp",EDGE,"E709"),sQuery(id+"F2.wireOp",EDGE,"E710"),sQuery(id+"F2.wireOp",EDGE,"E711"),sQuery(id+"F2.wireOp",EDGE,"E712"),sQuery(id+"F2.wireOp",EDGE,"E713"),sQuery(id+"F2.wireOp",EDGE,"E714"),sQuery(id+"F2.wireOp",EDGE,"E715"),sQuery(id+"F2.wireOp",EDGE,"E716"),sQuery(id+"F2.wireOp",EDGE,"E717"),sQuery(id+"F2.wireOp",EDGE,"E718"),sQuery(id+"F2.wireOp",EDGE,"E719"),sQuery(id+"F2.wireOp",EDGE,"E720"),sQuery(id+"F2.wireOp",EDGE,"E721"),sQuery(id+"F2.wireOp",EDGE,"E722"),sQuery(id+"F2.wireOp",EDGE,"E723"),sQuery(id+"F2.wireOp",EDGE,"E724"),sQuery(id+"F2.wireOp",EDGE,"E725"),sQuery(id+"F2.wireOp",EDGE,"E726"),sQuery(id+"F2.wireOp",EDGE,"E727"),sQuery(id+"F2.wireOp",EDGE,"E728"),sQuery(id+"F2.wireOp",EDGE,"E729"),sQuery(id+"F2.wireOp",EDGE,"E730"),sQuery(id+"F2.wireOp",EDGE,"E731"),sQuery(id+"F2.wireOp",EDGE,"E732"),sQuery(id+"F2.wireOp",EDGE,"E733"),sQuery(id+"F2.wireOp",EDGE,"E734"),sQuery(id+"F2.wireOp",EDGE,"E735"),sQuery(id+"F2.wireOp",EDGE,"E736"),sQuery(id+"F2.wireOp",EDGE,"E737"),sQuery(id+"F2.wireOp",EDGE,"E738"),sQuery(id+"F2.wireOp",EDGE,"E739"),sQuery(id+"F2.wireOp",EDGE,"E740"),sQuery(id+"F2.wireOp",EDGE,"E741"),sQuery(id+"F2.wireOp",EDGE,"E742"),sQuery(id+"F2.wireOp",EDGE,"E743"),sQuery(id+"F2.wireOp",EDGE,"E744"),sQuery(id+"F2.wireOp",EDGE,"E745"),sQuery(id+"F2.wireOp",EDGE,"E746"),sQuery(id+"F2.wireOp",EDGE,"E747"),sQuery(id+"F2.wireOp",EDGE,"E748"),sQuery(id+"F2.wireOp",EDGE,"E749"),sQuery(id+"F2.wireOp",EDGE,"E750"),sQuery(id+"F2.wireOp",EDGE,"E751"),sQuery(id+"F2.wireOp",EDGE,"E752"),sQuery(id+"F2.wireOp",EDGE,"E753"),sQuery(id+"F2.wireOp",EDGE,"E754"),sQuery(id+"F2.wireOp",EDGE,"E755"),sQuery(id+"F2.wireOp",EDGE,"E756"),sQuery(id+"F2.wireOp",EDGE,"E757"),sQuery(id+"F2.wireOp",EDGE,"E758"),sQuery(id+"F2.wireOp",EDGE,"E759"),sQuery(id+"F2.wireOp",EDGE,"E760"),sQuery(id+"F2.wireOp",EDGE,"E761"),sQuery(id+"F2.wireOp",EDGE,"E762"),sQuery(id+"F2.wireOp",EDGE,"E763"),sQuery(id+"F2.wireOp",EDGE,"E764"),sQuery(id+"F2.wireOp",EDGE,"E765"),sQuery(id+"F2.wireOp",EDGE,"E766"),sQuery(id+"F2.wireOp",EDGE,"E767"),sQuery(id+"F2.wireOp",EDGE,"E768"),sQuery(id+"F2.wireOp",EDGE,"E769"),sQuery(id+"F2.wireOp",EDGE,"E770"),sQuery(id+"F2.wireOp",EDGE,"E771"),sQuery(id+"F2.wireOp",EDGE,"E772"),sQuery(id+"F2.wireOp",EDGE,"E773"),sQuery(id+"F2.wireOp",EDGE,"E774"),sQuery(id+"F2.wireOp",EDGE,"E775"),sQuery(id+"F2.wireOp",EDGE,"E776"),sQuery(id+"F2.wireOp",EDGE,"E777"),sQuery(id+"F2.wireOp",EDGE,"E778"),sQuery(id+"F2.wireOp",EDGE,"E779"),sQuery(id+"F2.wireOp",EDGE,"E780"),sQuery(id+"F2.wireOp",EDGE,"E781"),sQuery(id+"F2.wireOp",EDGE,"E782"),sQuery(id+"F2.wireOp",EDGE,"E783"),sQuery(id+"F2.wireOp",EDGE,"E784"),sQuery(id+"F2.wireOp",EDGE,"E785"),sQuery(id+"F2.wireOp",EDGE,"E786"),sQuery(id+"F2.wireOp",EDGE,"E787"),sQuery(id+"F2.wireOp",EDGE,"E788"),sQuery(id+"F2.wireOp",EDGE,"E789"),sQuery(id+"F2.wireOp",EDGE,"E790"),sQuery(id+"F2.wireOp",EDGE,"E791"),sQuery(id+"F2.wireOp",EDGE,"E792"),sQuery(id+"F2.wireOp",EDGE,"E793"),sQuery(id+"F2.wireOp",EDGE,"E794"),sQuery(id+"F2.wireOp",EDGE,"E795"),sQuery(id+"F2.wireOp",EDGE,"E796"),sQuery(id+"F2.wireOp",EDGE,"E797"),sQuery(id+"F2.wireOp",EDGE,"E798"),sQuery(id+"F2.wireOp",EDGE,"E799"),sQuery(id+"F2.wireOp",EDGE,"E800"),sQuery(id+"F2.wireOp",EDGE,"E801"),sQuery(id+"F2.wireOp",EDGE,"E802"),sQuery(id+"F2.wireOp",EDGE,"E803"),sQuery(id+"F2.wireOp",EDGE,"E804"),sQuery(id+"F2.wireOp",EDGE,"E805"),sQuery(id+"F2.wireOp",EDGE,"E806"),sQuery(id+"F2.wireOp",EDGE,"E807"),sQuery(id+"F2.wireOp",EDGE,"E808"),sQuery(id+"F2.wireOp",EDGE,"E809"),sQuery(id+"F2.wireOp",EDGE,"E810"),sQuery(id+"F2.wireOp",EDGE,"E811"),sQuery(id+"F2.wireOp",EDGE,"E812"),sQuery(id+"F2.wireOp",EDGE,"E813"),sQuery(id+"F2.wireOp",EDGE,"E814"),sQuery(id+"F2.wireOp",EDGE,"E815"),sQuery(id+"F2.wireOp",EDGE,"E816"),sQuery(id+"F2.wireOp",EDGE,"E817"),sQuery(id+"F2.wireOp",EDGE,"E818"),sQuery(id+"F2.wireOp",EDGE,"E819"),sQuery(id+"F2.wireOp",EDGE,"E820"),sQuery(id+"F2.wireOp",EDGE,"E821"),sQuery(id+"F2.wireOp",EDGE,"E822"),sQuery(id+"F2.wireOp",EDGE,"E823"),sQuery(id+"F2.wireOp",EDGE,"E824"),sQuery(id+"F2.wireOp",EDGE,"E825"),sQuery(id+"F2.wireOp",EDGE,"E826"),sQuery(id+"F2.wireOp",EDGE,"E827"),sQuery(id+"F2.wireOp",EDGE,"E828"),sQuery(id+"F2.wireOp",EDGE,"E829"),sQuery(id+"F2.wireOp",EDGE,"E830"),sQuery(id+"F2.wireOp",EDGE,"E831"),sQuery(id+"F2.wireOp",EDGE,"E832"),sQuery(id+"F2.wireOp",EDGE,"E833"),sQuery(id+"F2.wireOp",EDGE,"E834"),sQuery(id+"F2.wireOp",EDGE,"E835"),sQuery(id+"F2.wireOp",EDGE,"E836"),sQuery(id+"F2.wireOp",EDGE,"E837"),sQuery(id+"F2.wireOp",EDGE,"E838"),sQuery(id+"F2.wireOp",EDGE,"E839"),sQuery(id+"F2.wireOp",EDGE,"E840"),sQuery(id+"F2.wireOp",EDGE,"E841"),sQuery(id+"F2.wireOp",EDGE,"E842"),sQuery(id+"F2.wireOp",EDGE,"E843"),sQuery(id+"F2.wireOp",EDGE,"E844"),sQuery(id+"F2.wireOp",EDGE,"E845"),sQuery(id+"F2.wireOp",EDGE,"E846"),sQuery(id+"F2.wireOp",EDGE,"E847"),sQuery(id+"F2.wireOp",EDGE,"E848"),sQuery(id+"F2.wireOp",EDGE,"E849"),sQuery(id+"F2.wireOp",EDGE,"E850"),sQuery(id+"F2.wireOp",EDGE,"E851"),sQuery(id+"F2.wireOp",EDGE,"E852"),sQuery(id+"F2.wireOp",EDGE,"E853"),sQuery(id+"F2.wireOp",EDGE,"E854"),sQuery(id+"F2.wireOp",EDGE,"E855"),sQuery(id+"F2.wireOp",EDGE,"E856"),sQuery(id+"F2.wireOp",EDGE,"E857"),sQuery(id+"F2.wireOp",EDGE,"E858"),sQuery(id+"F2.wireOp",EDGE,"E859"),sQuery(id+"F2.wireOp",EDGE,"E860"),sQuery(id+"F2.wireOp",EDGE,"E861"),sQuery(id+"F2.wireOp",EDGE,"E862"),sQuery(id+"F2.wireOp",EDGE,"E863"),sQuery(id+"F2.wireOp",EDGE,"E864"),sQuery(id+"F2.wireOp",EDGE,"E865"),sQuery(id+"F2.wireOp",EDGE,"E866"),sQuery(id+"F2.wireOp",EDGE,"E867"),sQuery(id+"F2.wireOp",EDGE,"E868"),sQuery(id+"F2.wireOp",EDGE,"E869"),sQuery(id+"F2.wireOp",EDGE,"E870"),sQuery(id+"F2.wireOp",EDGE,"E871"),sQuery(id+"F2.wireOp",EDGE,"E872"),sQuery(id+"F2.wireOp",EDGE,"E873"),sQuery(id+"F2.wireOp",EDGE,"E874"),sQuery(id+"F2.wireOp",EDGE,"E875"),sQuery(id+"F2.wireOp",EDGE,"E876"),sQuery(id+"F2.wireOp",EDGE,"E877"),sQuery(id+"F2.wireOp",EDGE,"E878"),sQuery(id+"F2.wireOp",EDGE,"E879"),sQuery(id+"F2.wireOp",EDGE,"E880"),sQuery(id+"F2.wireOp",EDGE,"E881"),sQuery(id+"F2.wireOp",EDGE,"E882"),sQuery(id+"F2.wireOp",EDGE,"E883"),sQuery(id+"F2.wireOp",EDGE,"E884"),sQuery(id+"F2.wireOp",EDGE,"E885"),sQuery(id+"F2.wireOp",EDGE,"E886"),sQuery(id+"F2.wireOp",EDGE,"E887"),sQuery(id+"F2.wireOp",EDGE,"E888"),sQuery(id+"F2.wireOp",EDGE,"E889"),sQuery(id+"F2.wireOp",EDGE,"E890"),sQuery(id+"F2.wireOp",EDGE,"E891"),sQuery(id+"F2.wireOp",EDGE,"E892"),sQuery(id+"F2.wireOp",EDGE,"E893"),sQuery(id+"F2.wireOp",EDGE,"E894"),sQuery(id+"F2.wireOp",EDGE,"E895"),sQuery(id+"F2.wireOp",EDGE,"E896"),sQuery(id+"F2.wireOp",EDGE,"E897"),sQuery(id+"F2.wireOp",EDGE,"E898"),sQuery(id+"F2.wireOp",EDGE,"E899"),sQuery(id+"F2.wireOp",EDGE,"E900"),sQuery(id+"F2.wireOp",EDGE,"E901"),sQuery(id+"F2.wireOp",EDGE,"E902"),sQuery(id+"F2.wireOp",EDGE,"E903"),sQuery(id+"F2.wireOp",EDGE,"E904"),sQuery(id+"F2.wireOp",EDGE,"E905"),sQuery(id+"F2.wireOp",EDGE,"E906"),sQuery(id+"F2.wireOp",EDGE,"E907"),sQuery(id+"F2.wireOp",EDGE,"E908"),sQuery(id+"F2.wireOp",EDGE,"E909"),sQuery(id+"F2.wireOp",EDGE,"E910"),sQuery(id+"F2.wireOp",EDGE,"E911"),sQuery(id+"F2.wireOp",EDGE,"E912"),sQuery(id+"F2.wireOp",EDGE,"E913"),sQuery(id+"F2.wireOp",EDGE,"E914"),sQuery(id+"F2.wireOp",EDGE,"E915"),sQuery(id+"F2.wireOp",EDGE,"E916"),sQuery(id+"F2.wireOp",EDGE,"E917"),sQuery(id+"F2.wireOp",EDGE,"E918"),sQuery(id+"F2.wireOp",EDGE,"E919"),sQuery(id+"F2.wireOp",EDGE,"E920"),sQuery(id+"F2.wireOp",EDGE,"E921"),sQuery(id+"F2.wireOp",EDGE,"E922"),sQuery(id+"F2.wireOp",EDGE,"E923"),sQuery(id+"F2.wireOp",EDGE,"E924"),sQuery(id+"F2.wireOp",EDGE,"E925"),sQuery(id+"F2.wireOp",EDGE,"E926"),sQuery(id+"F2.wireOp",EDGE,"E927"),sQuery(id+"F2.wireOp",EDGE,"E928"),sQuery(id+"F2.wireOp",EDGE,"E929"),sQuery(id+"F2.wireOp",EDGE,"E930"),sQuery(id+"F2.wireOp",EDGE,"E931"),sQuery(id+"F2.wireOp",EDGE,"E932"),sQuery(id+"F2.wireOp",EDGE,"E933"),sQuery(id+"F2.wireOp",EDGE,"E934"),sQuery(id+"F2.wireOp",EDGE,"E935"),sQuery(id+"F2.wireOp",EDGE,"E936"),sQuery(id+"F2.wireOp",EDGE,"E937"),sQuery(id+"F2.wireOp",EDGE,"E938"),sQuery(id+"F2.wireOp",EDGE,"E939"),sQuery(id+"F2.wireOp",EDGE,"E940"),sQuery(id+"F2.wireOp",EDGE,"E941"),sQuery(id+"F2.wireOp",EDGE,"E942"),sQuery(id+"F2.wireOp",EDGE,"E943"),sQuery(id+"F2.wireOp",EDGE,"E944"),sQuery(id+"F2.wireOp",EDGE,"E945"),sQuery(id+"F2.wireOp",EDGE,"E946"),sQuery(id+"F2.wireOp",EDGE,"E947"),sQuery(id+"F2.wireOp",EDGE,"E948"),sQuery(id+"F2.wireOp",EDGE,"E949"),sQuery(id+"F2.wireOp",EDGE,"E950"),sQuery(id+"F2.wireOp",EDGE,"E951"),sQuery(id+"F2.wireOp",EDGE,"E952"),sQuery(id+"F2.wireOp",EDGE,"E953"),sQuery(id+"F2.wireOp",EDGE,"E954"),sQuery(id+"F2.wireOp",EDGE,"E955"),sQuery(id+"F2.wireOp",EDGE,"E956"),sQuery(id+"F2.wireOp",EDGE,"E957"),sQuery(id+"F2.wireOp",EDGE,"E958"),sQuery(id+"F2.wireOp",EDGE,"E959"),sQuery(id+"F2.wireOp",EDGE,"E960"),sQuery(id+"F2.wireOp",EDGE,"E961"),sQuery(id+"F2.wireOp",EDGE,"E962"),sQuery(id+"F2.wireOp",EDGE,"E963"),sQuery(id+"F2.wireOp",EDGE,"E964"),sQuery(id+"F2.wireOp",EDGE,"E965"),sQuery(id+"F2.wireOp",EDGE,"E966"),sQuery(id+"F2.wireOp",EDGE,"E967"),sQuery(id+"F2.wireOp",EDGE,"E968"),sQuery(id+"F2.wireOp",EDGE,"E969"),sQuery(id+"F2.wireOp",EDGE,"E970"),sQuery(id+"F2.wireOp",EDGE,"E971"),sQuery(id+"F2.wireOp",EDGE,"E972"),sQuery(id+"F2.wireOp",EDGE,"E973"),sQuery(id+"F2.wireOp",EDGE,"E974"),sQuery(id+"F2.wireOp",EDGE,"E975"),sQuery(id+"F2.wireOp",EDGE,"E976"),sQuery(id+"F2.wireOp",EDGE,"E977"),sQuery(id+"F2.wireOp",EDGE,"E978"),sQuery(id+"F2.wireOp",EDGE,"E979"),sQuery(id+"F2.wireOp",EDGE,"E980"),sQuery(id+"F2.wireOp",EDGE,"E981"),sQuery(id+"F2.wireOp",EDGE,"E982"),sQuery(id+"F2.wireOp",EDGE,"E983"),sQuery(id+"F2.wireOp",EDGE,"E984"),sQuery(id+"F2.wireOp",EDGE,"E985"),sQuery(id+"F2.wireOp",EDGE,"E986"),sQuery(id+"F2.wireOp",EDGE,"E987"),sQuery(id+"F2.wireOp",EDGE,"E988"),sQuery(id+"F2.wireOp",EDGE,"E989"),sQuery(id+"F2.wireOp",EDGE,"E990"),sQuery(id+"F2.wireOp",EDGE,"E991"),sQuery(id+"F2.wireOp",EDGE,"E992"),sQuery(id+"F2.wireOp",EDGE,"E993"),sQuery(id+"F2.wireOp",EDGE,"E994"),sQuery(id+"F2.wireOp",EDGE,"E995"),sQuery(id+"F2.wireOp",EDGE,"E996"),sQuery(id+"F2.wireOp",EDGE,"E997"),sQuery(id+"F2.wireOp",EDGE,"E998"),sQuery(id+"F2.wireOp",EDGE,"E999"),sQuery(id+"F2.wireOp",EDGE,"E1000"),sQuery(id+"F2.wireOp",EDGE,"E1001"),sQuery(id+"F2.wireOp",EDGE,"E1002"),sQuery(id+"F2.wireOp",EDGE,"E1003"),sQuery(id+"F2.wireOp",EDGE,"E1004"),sQuery(id+"F2.wireOp",EDGE,"E1005"),sQuery(id+"F2.wireOp",EDGE,"E1006"),sQuery(id+"F2.wireOp",EDGE,"E1007"),sQuery(id+"F2.wireOp",EDGE,"E1008"),sQuery(id+"F2.wireOp",EDGE,"E1009"),sQuery(id+"F2.wireOp",EDGE,"E1010"),sQuery(id+"F2.wireOp",EDGE,"E1011"),sQuery(id+"F2.wireOp",EDGE,"E1012"),sQuery(id+"F2.wireOp",EDGE,"E1013"),sQuery(id+"F2.wireOp",EDGE,"E1014"),sQuery(id+"F2.wireOp",EDGE,"E1015"),sQuery(id+"F2.wireOp",EDGE,"E1016"),sQuery(id+"F2.wireOp",EDGE,"E1017"),sQuery(id+"F2.wireOp",EDGE,"E1018"),sQuery(id+"F2.wireOp",EDGE,"E1019"),sQuery(id+"F2.wireOp",EDGE,"E1020"),sQuery(id+"F2.wireOp",EDGE,"E1021"),sQuery(id+"F2.wireOp",EDGE,"E1022"),sQuery(id+"F2.wireOp",EDGE,"E1023"),sQuery(id+"F2.wireOp",EDGE,"E1024"),sQuery(id+"F2.wireOp",EDGE,"E1025"),sQuery(id+"F2.wireOp",EDGE,"E1026"),sQuery(id+"F2.wireOp",EDGE,"E1027"),sQuery(id+"F2.wireOp",EDGE,"E1028"),sQuery(id+"F2.wireOp",EDGE,"E1029"),sQuery(id+"F2.wireOp",EDGE,"E1030"),sQuery(id+"F2.wireOp",EDGE,"E1031"),sQuery(id+"F2.wireOp",EDGE,"E1032"),sQuery(id+"F2.wireOp",EDGE,"E1033"),sQuery(id+"F2.wireOp",EDGE,"E1034"),sQuery(id+"F2.wireOp",EDGE,"E1035"),sQuery(id+"F2.wireOp",EDGE,"E1036"),sQuery(id+"F2.wireOp",EDGE,"E1037"),sQuery(id+"F2.wireOp",EDGE,"E1038"),sQuery(id+"F2.wireOp",EDGE,"E1039"),sQuery(id+"F2.wireOp",EDGE,"E1040"),sQuery(id+"F2.wireOp",EDGE,"E1041"),sQuery(id+"F2.wireOp",EDGE,"E1042"),sQuery(id+"F2.wireOp",EDGE,"E1043"),sQuery(id+"F2.wireOp",EDGE,"E1044"),sQuery(id+"F2.wireOp",EDGE,"E1045"),sQuery(id+"F2.wireOp",EDGE,"E1046"),sQuery(id+"F2.wireOp",EDGE,"E1047"),sQuery(id+"F2.wireOp",EDGE,"E1048"),sQuery(id+"F2.wireOp",EDGE,"E1049"),sQuery(id+"F2.wireOp",EDGE,"E1050"),sQuery(id+"F2.wireOp",EDGE,"E1051"),sQuery(id+"F2.wireOp",EDGE,"E1052"),sQuery(id+"F2.wireOp",EDGE,"E1053"),sQuery(id+"F2.wireOp",EDGE,"E1054"),sQuery(id+"F2.wireOp",EDGE,"E1055"),sQuery(id+"F2.wireOp",EDGE,"E1056"),sQuery(id+"F2.wireOp",EDGE,"E1057"),sQuery(id+"F2.wireOp",EDGE,"E1058"),sQuery(id+"F2.wireOp",EDGE,"E1059"),sQuery(id+"F2.wireOp",EDGE,"E1060"),sQuery(id+"F2.wireOp",EDGE,"E1061"),sQuery(id+"F2.wireOp",EDGE,"E1062"),sQuery(id+"F2.wireOp",EDGE,"E1063"),sQuery(id+"F2.wireOp",EDGE,"E1064"),sQuery(id+"F2.wireOp",EDGE,"E1065"),sQuery(id+"F2.wireOp",EDGE,"E1066"),sQuery(id+"F2.wireOp",EDGE,"E1067"),sQuery(id+"F2.wireOp",EDGE,"E1068"),sQuery(id+"F2.wireOp",EDGE,"E1069"),sQuery(id+"F2.wireOp",EDGE,"E1070"),sQuery(id+"F2.wireOp",EDGE,"E1071"),sQuery(id+"F2.wireOp",EDGE,"E1072"),sQuery(id+"F2.wireOp",EDGE,"E1073"),sQuery(id+"F2.wireOp",EDGE,"E1074"),sQuery(id+"F2.wireOp",EDGE,"E1075"),sQuery(id+"F2.wireOp",EDGE,"E1076"),sQuery(id+"F2.wireOp",EDGE,"E1077"),sQuery(id+"F2.wireOp",EDGE,"E1078"),sQuery(id+"F2.wireOp",EDGE,"E1079"),sQuery(id+"F2.wireOp",EDGE,"E1080"),sQuery(id+"F2.wireOp",EDGE,"E1081"),sQuery(id+"F2.wireOp",EDGE,"E1082"),sQuery(id+"F2.wireOp",EDGE,"E1083"),sQuery(id+"F2.wireOp",EDGE,"E1084"),sQuery(id+"F2.wireOp",EDGE,"E1085"),sQuery(id+"F2.wireOp",EDGE,"E1086"),sQuery(id+"F2.wireOp",EDGE,"E1087"),sQuery(id+"F2.wireOp",EDGE,"E1088"),sQuery(id+"F2.wireOp",EDGE,"E1089"),sQuery(id+"F2.wireOp",EDGE,"E1090"),sQuery(id+"F2.wireOp",EDGE,"E1091"),sQuery(id+"F2.wireOp",EDGE,"E1092"),sQuery(id+"F2.wireOp",EDGE,"E1093"),sQuery(id+"F2.wireOp",EDGE,"E1094"),sQuery(id+"F2.wireOp",EDGE,"E1095"),sQuery(id+"F2.wireOp",EDGE,"E1096"),sQuery(id+"F2.wireOp",EDGE,"E1097"),sQuery(id+"F2.wireOp",EDGE,"E1098"),sQuery(id+"F2.wireOp",EDGE,"E1099"),sQuery(id+"F2.wireOp",EDGE,"E1100"),sQuery(id+"F2.wireOp",EDGE,"E1101"),sQuery(id+"F2.wireOp",EDGE,"E1102"),sQuery(id+"F2.wireOp",EDGE,"E1103"),sQuery(id+"F2.wireOp",EDGE,"E1104"),sQuery(id+"F2.wireOp",EDGE,"E1105"),sQuery(id+"F2.wireOp",EDGE,"E1106"),sQuery(id+"F2.wireOp",EDGE,"E1107"),sQuery(id+"F2.wireOp",EDGE,"E1108"),sQuery(id+"F2.wireOp",EDGE,"E1109"),sQuery(id+"F2.wireOp",EDGE,"E1110"),sQuery(id+"F2.wireOp",EDGE,"E1111"),sQuery(id+"F2.wireOp",EDGE,"E1112"),sQuery(id+"F2.wireOp",EDGE,"E1113"),sQuery(id+"F2.wireOp",EDGE,"E1114"),sQuery(id+"F2.wireOp",EDGE,"E1115"),sQuery(id+"F2.wireOp",EDGE,"E1116"),sQuery(id+"F2.wireOp",EDGE,"E1117"),sQuery(id+"F2.wireOp",EDGE,"E1118"),sQuery(id+"F2.wireOp",EDGE,"E1119"),sQuery(id+"F2.wireOp",EDGE,"E1120"),sQuery(id+"F2.wireOp",EDGE,"E1121"),sQuery(id+"F2.wireOp",EDGE,"E1122"),sQuery(id+"F2.wireOp",EDGE,"E1123"),sQuery(id+"F2.wireOp",EDGE,"E1124"),sQuery(id+"F2.wireOp",EDGE,"E1125"),sQuery(id+"F2.wireOp",EDGE,"E1126"),sQuery(id+"F2.wireOp",EDGE,"E1127"),sQuery(id+"F2.wireOp",EDGE,"E1128"),sQuery(id+"F2.wireOp",EDGE,"E1129"),sQuery(id+"F2.wireOp",EDGE,"E1130"),sQuery(id+"F2.wireOp",EDGE,"E1131"),sQuery(id+"F2.wireOp",EDGE,"E1132"),sQuery(id+"F2.wireOp",EDGE,"E1133"),sQuery(id+"F2.wireOp",EDGE,"E1134"),sQuery(id+"F2.wireOp",EDGE,"E1135"),sQuery(id+"F2.wireOp",EDGE,"E1136"),sQuery(id+"F2.wireOp",EDGE,"E1137"),sQuery(id+"F2.wireOp",EDGE,"E1138"),sQuery(id+"F2.wireOp",EDGE,"E1139"),sQuery(id+"F2.wireOp",EDGE,"E1140"),sQuery(id+"F2.wireOp",EDGE,"E1141"),sQuery(id+"F2.wireOp",EDGE,"E1142"),sQuery(id+"F2.wireOp",EDGE,"E1143"),sQuery(id+"F2.wireOp",EDGE,"E1144"),sQuery(id+"F2.wireOp",EDGE,"E1145"),sQuery(id+"F2.wireOp",EDGE,"E1146"),sQuery(id+"F2.wireOp",EDGE,"E1147"),sQuery(id+"F2.wireOp",EDGE,"E1148"),sQuery(id+"F2.wireOp",EDGE,"E1149"),sQuery(id+"F2.wireOp",EDGE,"E1150"),sQuery(id+"F2.wireOp",EDGE,"E1151"),sQuery(id+"F2.wireOp",EDGE,"E1152"),sQuery(id+"F2.wireOp",EDGE,"E1153"),sQuery(id+"F2.wireOp",EDGE,"E1154"),sQuery(id+"F2.wireOp",EDGE,"E1155"),sQuery(id+"F2.wireOp",EDGE,"E1156"),sQuery(id+"F2.wireOp",EDGE,"E1157"),sQuery(id+"F2.wireOp",EDGE,"E1158"),sQuery(id+"F2.wireOp",EDGE,"E1159"),sQuery(id+"F2.wireOp",EDGE,"E1160"),sQuery(id+"F2.wireOp",EDGE,"E1161"),sQuery(id+"F2.wireOp",EDGE,"E1162"),sQuery(id+"F2.wireOp",EDGE,"E1163"),sQuery(id+"F2.wireOp",EDGE,"E1164"),sQuery(id+"F2.wireOp",EDGE,"E1165"),sQuery(id+"F2.wireOp",EDGE,"E1166"),sQuery(id+"F2.wireOp",EDGE,"E1167"),sQuery(id+"F2.wireOp",EDGE,"E1168"),sQuery(id+"F2.wireOp",EDGE,"E1169"),sQuery(id+"F2.wireOp",EDGE,"E1170"),sQuery(id+"F2.wireOp",EDGE,"E1171"),sQuery(id+"F2.wireOp",EDGE,"E1172"),sQuery(id+"F2.wireOp",EDGE,"E1173"),sQuery(id+"F2.wireOp",EDGE,"E1174"),sQuery(id+"F2.wireOp",EDGE,"E1175"),sQuery(id+"F2.wireOp",EDGE,"E1176"),sQuery(id+"F2.wireOp",EDGE,"E1177"),sQuery(id+"F2.wireOp",EDGE,"E1178"),sQuery(id+"F2.wireOp",EDGE,"E1179"),sQuery(id+"F2.wireOp",EDGE,"E1180"),sQuery(id+"F2.wireOp",EDGE,"E1181"),sQuery(id+"F2.wireOp",EDGE,"E1182"),sQuery(id+"F2.wireOp",EDGE,"E1183"),sQuery(id+"F2.wireOp",EDGE,"E1184"),sQuery(id+"F2.wireOp",EDGE,"E1185"),sQuery(id+"F2.wireOp",EDGE,"E1186"),sQuery(id+"F2.wireOp",EDGE,"E1187"),sQuery(id+"F2.wireOp",EDGE,"E1188"),sQuery(id+"F2.wireOp",EDGE,"E1189"),sQuery(id+"F2.wireOp",EDGE,"E1190"),sQuery(id+"F2.wireOp",EDGE,"E1191"),sQuery(id+"F2.wireOp",EDGE,"E1192"),sQuery(id+"F2.wireOp",EDGE,"E1193"),sQuery(id+"F2.wireOp",EDGE,"E1194"),sQuery(id+"F2.wireOp",EDGE,"E1195"),sQuery(id+"F2.wireOp",EDGE,"E1196"),sQuery(id+"F2.wireOp",EDGE,"E1197"),sQuery(id+"F2.wireOp",EDGE,"E1198"),sQuery(id+"F2.wireOp",EDGE,"E1199"),sQuery(id+"F2.wireOp",EDGE,"E1200"),sQuery(id+"F2.wireOp",EDGE,"E1201"),sQuery(id+"F2.wireOp",EDGE,"E1202"),sQuery(id+"F2.wireOp",EDGE,"E1203"),sQuery(id+"F2.wireOp",EDGE,"E1204"),sQuery(id+"F2.wireOp",EDGE,"E1205"),sQuery(id+"F2.wireOp",EDGE,"E1206"),sQuery(id+"F2.wireOp",EDGE,"E1207"),sQuery(id+"F2.wireOp",EDGE,"E1208"),sQuery(id+"F2.wireOp",EDGE,"E1209"),sQuery(id+"F2.wireOp",EDGE,"E1210"),sQuery(id+"F2.wireOp",EDGE,"E1211"),sQuery(id+"F2.wireOp",EDGE,"E1212"),sQuery(id+"F2.wireOp",EDGE,"E1213"),sQuery(id+"F2.wireOp",EDGE,"E1214"),sQuery(id+"F2.wireOp",EDGE,"E1215"),sQuery(id+"F2.wireOp",EDGE,"E1216"),sQuery(id+"F2.wireOp",EDGE,"E1217"),sQuery(id+"F2.wireOp",EDGE,"E1218"),sQuery(id+"F2.wireOp",EDGE,"E1219"),sQuery(id+"F2.wireOp",EDGE,"E1220"),sQuery(id+"F2.wireOp",EDGE,"E1221"),sQuery(id+"F2.wireOp",EDGE,"E1222"),sQuery(id+"F2.wireOp",EDGE,"E1223"),sQuery(id+"F2.wireOp",EDGE,"E1224"),sQuery(id+"F2.wireOp",EDGE,"E1225"),sQuery(id+"F2.wireOp",EDGE,"E1226"),sQuery(id+"F2.wireOp",EDGE,"E1227"),sQuery(id+"F2.wireOp",EDGE,"E1228"),sQuery(id+"F2.wireOp",EDGE,"E1229"),sQuery(id+"F2.wireOp",EDGE,"E1230"),sQuery(id+"F2.wireOp",EDGE,"E1231"),sQuery(id+"F2.wireOp",EDGE,"E1232"),sQuery(id+"F2.wireOp",EDGE,"E1233"),sQuery(id+"F2.wireOp",EDGE,"E1234"),sQuery(id+"F2.wireOp",EDGE,"E1235"),sQuery(id+"F2.wireOp",EDGE,"E1236"),sQuery(id+"F2.wireOp",EDGE,"E1237"),sQuery(id+"F2.wireOp",EDGE,"E1238"),sQuery(id+"F2.wireOp",EDGE,"E1239"),sQuery(id+"F2.wireOp",EDGE,"E1240"),sQuery(id+"F2.wireOp",EDGE,"E1241"),sQuery(id+"F2.wireOp",EDGE,"E1242"),sQuery(id+"F2.wireOp",EDGE,"E1243"),sQuery(id+"F2.wireOp",EDGE,"E1244"),sQuery(id+"F2.wireOp",EDGE,"E1245"),sQuery(id+"F2.wireOp",EDGE,"E1246"),sQuery(id+"F2.wireOp",EDGE,"E1247"),sQuery(id+"F2.wireOp",EDGE,"E1248"),sQuery(id+"F2.wireOp",EDGE,"E1249"),sQuery(id+"F2.wireOp",EDGE,"E1250"),sQuery(id+"F2.wireOp",EDGE,"E1251"),sQuery(id+"F2.wireOp",EDGE,"E1252"),sQuery(id+"F2.wireOp",EDGE,"E1253"),sQuery(id+"F2.wireOp",EDGE,"E1254"),sQuery(id+"F2.wireOp",EDGE,"E1255"),sQuery(id+"F2.wireOp",EDGE,"E1256"),sQuery(id+"F2.wireOp",EDGE,"E1257"),sQuery(id+"F2.wireOp",EDGE,"E1258"),sQuery(id+"F2.wireOp",EDGE,"E1259"),sQuery(id+"F2.wireOp",EDGE,"E1260"),sQuery(id+"F2.wireOp",EDGE,"E1261"),sQuery(id+"F2.wireOp",EDGE,"E1262"),sQuery(id+"F2.wireOp",EDGE,"E1263"),sQuery(id+"F2.wireOp",EDGE,"E1264"),sQuery(id+"F2.wireOp",EDGE,"E1265"),sQuery(id+"F2.wireOp",EDGE,"E1266"),sQuery(id+"F2.wireOp",EDGE,"E1267"),sQuery(id+"F2.wireOp",EDGE,"E1268"),sQuery(id+"F2.wireOp",EDGE,"E1269"),sQuery(id+"F2.wireOp",EDGE,"E1270"),sQuery(id+"F2.wireOp",EDGE,"E1271"),sQuery(id+"F2.wireOp",EDGE,"E1272"),sQuery(id+"F2.wireOp",EDGE,"E1273"),sQuery(id+"F2.wireOp",EDGE,"E1274"),sQuery(id+"F2.wireOp",EDGE,"E1275"),sQuery(id+"F2.wireOp",EDGE,"E1276"),sQuery(id+"F2.wireOp",EDGE,"E1277"),sQuery(id+"F2.wireOp",EDGE,"E1278"),sQuery(id+"F2.wireOp",EDGE,"E1279"),sQuery(id+"F2.wireOp",EDGE,"E1280"),sQuery(id+"F2.wireOp",EDGE,"E1281"),sQuery(id+"F2.wireOp",EDGE,"E1282"),sQuery(id+"F2.wireOp",EDGE,"E1283"),sQuery(id+"F2.wireOp",EDGE,"E1284"),sQuery(id+"F2.wireOp",EDGE,"E1285"),sQuery(id+"F2.wireOp",EDGE,"E1286"),sQuery(id+"F2.wireOp",EDGE,"E1287"),sQuery(id+"F2.wireOp",EDGE,"E1288"),sQuery(id+"F2.wireOp",EDGE,"E1289"),sQuery(id+"F2.wireOp",EDGE,"E1290"),sQuery(id+"F2.wireOp",EDGE,"E1291"),sQuery(id+"F2.wireOp",EDGE,"E1292"),sQuery(id+"F2.wireOp",EDGE,"E1293"),sQuery(id+"F2.wireOp",EDGE,"E1294"),sQuery(id+"F2.wireOp",EDGE,"E1295"),sQuery(id+"F2.wireOp",EDGE,"E1296"),sQuery(id+"F2.wireOp",EDGE,"E1297"),sQuery(id+"F2.wireOp",EDGE,"E1298"),sQuery(id+"F2.wireOp",EDGE,"E1299"),sQuery(id+"F2.wireOp",EDGE,"E1300"),sQuery(id+"F2.wireOp",EDGE,"E1301"),sQuery(id+"F2.wireOp",EDGE,"E1302"),sQuery(id+"F2.wireOp",EDGE,"E1303"),sQuery(id+"F2.wireOp",EDGE,"E1304"),sQuery(id+"F2.wireOp",EDGE,"E1305"),sQuery(id+"F2.wireOp",EDGE,"E1306"),sQuery(id+"F2.wireOp",EDGE,"E1307"),sQuery(id+"F2.wireOp",EDGE,"E1308"),sQuery(id+"F2.wireOp",EDGE,"E1309"),sQuery(id+"F2.wireOp",EDGE,"E1310"),sQuery(id+"F2.wireOp",EDGE,"E1311"),sQuery(id+"F2.wireOp",EDGE,"E1312"),sQuery(id+"F2.wireOp",EDGE,"E1313"),sQuery(id+"F2.wireOp",EDGE,"E1314"),sQuery(id+"F2.wireOp",EDGE,"E1315"),sQuery(id+"F2.wireOp",EDGE,"E1316"),sQuery(id+"F2.wireOp",EDGE,"E1317"),sQuery(id+"F2.wireOp",EDGE,"E1318"),sQuery(id+"F2.wireOp",EDGE,"E1319"),sQuery(id+"F2.wireOp",EDGE,"E1320"),sQuery(id+"F2.wireOp",EDGE,"E1321"),sQuery(id+"F2.wireOp",EDGE,"E1322"),sQuery(id+"F2.wireOp",EDGE,"E1323"),sQuery(id+"F2.wireOp",EDGE,"E1324"),sQuery(id+"F2.wireOp",EDGE,"E1325"),sQuery(id+"F2.wireOp",EDGE,"E1326"),sQuery(id+"F2.wireOp",EDGE,"E1327"),sQuery(id+"F2.wireOp",EDGE,"E1328"),sQuery(id+"F2.wireOp",EDGE,"E1329"),sQuery(id+"F2.wireOp",EDGE,"E1330"),sQuery(id+"F2.wireOp",EDGE,"E1331"),sQuery(id+"F2.wireOp",EDGE,"E1332"),sQuery(id+"F2.wireOp",EDGE,"E1333"),sQuery(id+"F2.wireOp",EDGE,"E1334"),sQuery(id+"F2.wireOp",EDGE,"E1335"),sQuery(id+"F2.wireOp",EDGE,"E1336"),sQuery(id+"F2.wireOp",EDGE,"E1337"),sQuery(id+"F2.wireOp",EDGE,"E1338"),sQuery(id+"F2.wireOp",EDGE,"E1339"),sQuery(id+"F2.wireOp",EDGE,"E1340"),sQuery(id+"F2.wireOp",EDGE,"E1341"),sQuery(id+"F2.wireOp",EDGE,"E1342"),sQuery(id+"F2.wireOp",EDGE,"E1343"),sQuery(id+"F2.wireOp",EDGE,"E1344"),sQuery(id+"F2.wireOp",EDGE,"E1345"),sQuery(id+"F2.wireOp",EDGE,"E1346"),sQuery(id+"F2.wireOp",EDGE,"E1347"),sQuery(id+"F2.wireOp",EDGE,"E1348"),sQuery(id+"F2.wireOp",EDGE,"E1349"),sQuery(id+"F2.wireOp",EDGE,"E1350"),sQuery(id+"F2.wireOp",EDGE,"E1351"),sQuery(id+"F2.wireOp",EDGE,"E1352"),sQuery(id+"F2.wireOp",EDGE,"E1353"),sQuery(id+"F2.wireOp",EDGE,"E1354"),sQuery(id+"F2.wireOp",EDGE,"E1355"),sQuery(id+"F2.wireOp",EDGE,"E1356"),sQuery(id+"F2.wireOp",EDGE,"E1357"),sQuery(id+"F2.wireOp",EDGE,"E1358"),sQuery(id+"F2.wireOp",EDGE,"E1359"),sQuery(id+"F2.wireOp",EDGE,"E1360"),sQuery(id+"F2.wireOp",EDGE,"E1361"),sQuery(id+"F2.wireOp",EDGE,"E1362"),sQuery(id+"F2.wireOp",EDGE,"E1363"),sQuery(id+"F2.wireOp",EDGE,"E1364"),sQuery(id+"F2.wireOp",EDGE,"E1365"),sQuery(id+"F2.wireOp",EDGE,"E1366"),sQuery(id+"F2.wireOp",EDGE,"E1367"),sQuery(id+"F2.wireOp",EDGE,"E1368"),sQuery(id+"F2.wireOp",EDGE,"E1369"),sQuery(id+"F2.wireOp",EDGE,"E1370"),sQuery(id+"F2.wireOp",EDGE,"E1371"),sQuery(id+"F2.wireOp",EDGE,"E1372"),sQuery(id+"F2.wireOp",EDGE,"E1373"),sQuery(id+"F2.wireOp",EDGE,"E1374"),sQuery(id+"F2.wireOp",EDGE,"E1375"),sQuery(id+"F2.wireOp",EDGE,"E1376"),sQuery(id+"F2.wireOp",EDGE,"E1377"),sQuery(id+"F2.wireOp",EDGE,"E1378"),sQuery(id+"F2.wireOp",EDGE,"E1379"),sQuery(id+"F2.wireOp",EDGE,"E1380"),sQuery(id+"F2.wireOp",EDGE,"E1381"),sQuery(id+"F2.wireOp",EDGE,"E1382"),sQuery(id+"F2.wireOp",EDGE,"E1383"),sQuery(id+"F2.wireOp",EDGE,"E1384"),sQuery(id+"F2.wireOp",EDGE,"E1385"),sQuery(id+"F2.wireOp",EDGE,"E1386"),sQuery(id+"F2.wireOp",EDGE,"E1387"),sQuery(id+"F2.wireOp",EDGE,"E1388"),sQuery(id+"F2.wireOp",EDGE,"E1389"),sQuery(id+"F2.wireOp",EDGE,"E1390"),sQuery(id+"F2.wireOp",EDGE,"E1391"),sQuery(id+"F2.wireOp",EDGE,"E1392"),sQuery(id+"F2.wireOp",EDGE,"E1393"),sQuery(id+"F2.wireOp",EDGE,"E1394"),sQuery(id+"F2.wireOp",EDGE,"E1395"),sQuery(id+"F2.wireOp",EDGE,"E1396"),sQuery(id+"F2.wireOp",EDGE,"E1397"),sQuery(id+"F2.wireOp",EDGE,"E1398"),sQuery(id+"F2.wireOp",EDGE,"E1399"),sQuery(id+"F2.wireOp",EDGE,"E1400"),sQuery(id+"F2.wireOp",EDGE,"E1401"),sQuery(id+"F2.wireOp",EDGE,"E1402"),sQuery(id+"F2.wireOp",EDGE,"E1403"),sQuery(id+"F2.wireOp",EDGE,"E1404"),sQuery(id+"F2.wireOp",EDGE,"E1405"),sQuery(id+"F2.wireOp",EDGE,"E1406"),sQuery(id+"F2.wireOp",EDGE,"E1407"),sQuery(id+"F2.wireOp",EDGE,"E1408"),sQuery(id+"F2.wireOp",EDGE,"E1409"),sQuery(id+"F2.wireOp",EDGE,"E1410"),sQuery(id+"F2.wireOp",EDGE,"E1411"),sQuery(id+"F2.wireOp",EDGE,"E1412"),sQuery(id+"F2.wireOp",EDGE,"E1413"),sQuery(id+"F2.wireOp",EDGE,"E1414"),sQuery(id+"F2.wireOp",EDGE,"E1415"),sQuery(id+"F2.wireOp",EDGE,"E1416"),sQuery(id+"F2.wireOp",EDGE,"E1417"),sQuery(id+"F2.wireOp",EDGE,"E1418"),sQuery(id+"F2.wireOp",EDGE,"E1419"),sQuery(id+"F2.wireOp",EDGE,"E1420"),sQuery(id+"F2.wireOp",EDGE,"E1421"),sQuery(id+"F2.wireOp",EDGE,"E1422"),sQuery(id+"F2.wireOp",EDGE,"E1423"),sQuery(id+"F2.wireOp",EDGE,"E1424"),sQuery(id+"F2.wireOp",EDGE,"E1425"),sQuery(id+"F2.wireOp",EDGE,"E1426"),sQuery(id+"F2.wireOp",EDGE,"E1427"),sQuery(id+"F2.wireOp",EDGE,"E1428"),sQuery(id+"F2.wireOp",EDGE,"E1429"),sQuery(id+"F2.wireOp",EDGE,"E1430"),sQuery(id+"F2.wireOp",EDGE,"E1431"),sQuery(id+"F2.wireOp",EDGE,"E1432"),sQuery(id+"F2.wireOp",EDGE,"E1433"),sQuery(id+"F2.wireOp",EDGE,"E1434"),sQuery(id+"F2.wireOp",EDGE,"E1435"),sQuery(id+"F2.wireOp",EDGE,"E1436"),sQuery(id+"F2.wireOp",EDGE,"E1437"),sQuery(id+"F2.wireOp",EDGE,"E1438"),sQuery(id+"F2.wireOp",EDGE,"E1439"),sQuery(id+"F2.wireOp",EDGE,"E1440"),sQuery(id+"F2.wireOp",EDGE,"E1441"),sQuery(id+"F2.wireOp",EDGE,"E1442"),sQuery(id+"F2.wireOp",EDGE,"E1443"),sQuery(id+"F2.wireOp",EDGE,"E1444"),sQuery(id+"F2.wireOp",EDGE,"E1445"),sQuery(id+"F2.wireOp",EDGE,"E1446"),sQuery(id+"F2.wireOp",EDGE,"E1447"),sQuery(id+"F2.wireOp",EDGE,"E1448"),sQuery(id+"F2.wireOp",EDGE,"E1449"),sQuery(id+"F2.wireOp",EDGE,"E1450"),sQuery(id+"F2.wireOp",EDGE,"E1451"),sQuery(id+"F2.wireOp",EDGE,"E1452"),sQuery(id+"F2.wireOp",EDGE,"E1453"),sQuery(id+"F2.wireOp",EDGE,"E1454"),sQuery(id+"F2.wireOp",EDGE,"E1455"),sQuery(id+"F2.wireOp",EDGE,"E1456"),sQuery(id+"F2.wireOp",EDGE,"E1457"),sQuery(id+"F2.wireOp",EDGE,"E1458"),sQuery(id+"F2.wireOp",EDGE,"E1459"),sQuery(id+"F2.wireOp",EDGE,"E1460"),sQuery(id+"F2.wireOp",EDGE,"E1461"),sQuery(id+"F2.wireOp",EDGE,"E1462"),sQuery(id+"F2.wireOp",EDGE,"E1463"),sQuery(id+"F2.wireOp",EDGE,"E1464"),sQuery(id+"F2.wireOp",EDGE,"E1465"),sQuery(id+"F2.wireOp",EDGE,"E1466"),sQuery(id+"F2.wireOp",EDGE,"E1467"),sQuery(id+"F2.wireOp",EDGE,"E1468"),sQuery(id+"F2.wireOp",EDGE,"E1469"),sQuery(id+"F2.wireOp",EDGE,"E1470"),sQuery(id+"F2.wireOp",EDGE,"E1471"),sQuery(id+"F2.wireOp",EDGE,"E1472"),sQuery(id+"F2.wireOp",EDGE,"E1473"),sQuery(id+"F2.wireOp",EDGE,"E1474")])],"isStart":false});
            extrude(context, id + "F5", {"entities" : qUnion([Q0]), "operationType" : NewBodyOperationType.REMOVE, "endBound" : BoundingType.UP_TO_SURFACE, "depth" : 25 * mm, "endBoundEntityFace" : qUnion([Q1]), "offsetDistance" : 25 * mm});
        }
        {
            var Q0;
            Q0=makeQuery(id+"F3.opExtrude","SWEPT_BODY",BODY,{"disambiguationData":[OSD([sQuery(id+"F2.wireOp",EDGE,"E16"),sQuery(id+"F2.wireOp",EDGE,"E17"),sQuery(id+"F2.wireOp",EDGE,"E18"),sQuery(id+"F2.wireOp",EDGE,"E19"),sQuery(id+"F2.wireOp",EDGE,"E20"),sQuery(id+"F2.wireOp",EDGE,"E21"),sQuery(id+"F2.wireOp",EDGE,"E22"),sQuery(id+"F2.wireOp",EDGE,"E23"),sQuery(id+"F2.wireOp",EDGE,"E24"),sQuery(id+"F2.wireOp",EDGE,"E25"),sQuery(id+"F2.wireOp",EDGE,"E26"),sQuery(id+"F2.wireOp",EDGE,"E27"),sQuery(id+"F2.wireOp",EDGE,"E28"),sQuery(id+"F2.wireOp",EDGE,"E29"),sQuery(id+"F2.wireOp",EDGE,"E30"),sQuery(id+"F2.wireOp",EDGE,"E31"),sQuery(id+"F2.wireOp",EDGE,"E32"),sQuery(id+"F2.wireOp",EDGE,"E33"),sQuery(id+"F2.wireOp",EDGE,"E34"),sQuery(id+"F2.wireOp",EDGE,"E35"),sQuery(id+"F2.wireOp",EDGE,"E36"),sQuery(id+"F2.wireOp",EDGE,"E37"),sQuery(id+"F2.wireOp",EDGE,"E38"),sQuery(id+"F2.wireOp",EDGE,"E39"),sQuery(id+"F2.wireOp",EDGE,"E40"),sQuery(id+"F2.wireOp",EDGE,"E41"),sQuery(id+"F2.wireOp",EDGE,"E42"),sQuery(id+"F2.wireOp",EDGE,"E43"),sQuery(id+"F2.wireOp",EDGE,"E44"),sQuery(id+"F2.wireOp",EDGE,"E45"),sQuery(id+"F2.wireOp",EDGE,"E46"),sQuery(id+"F2.wireOp",EDGE,"E47"),sQuery(id+"F2.wireOp",EDGE,"E48"),sQuery(id+"F2.wireOp",EDGE,"E49"),sQuery(id+"F2.wireOp",EDGE,"E50"),sQuery(id+"F2.wireOp",EDGE,"E51"),sQuery(id+"F2.wireOp",EDGE,"E52"),sQuery(id+"F2.wireOp",EDGE,"E53"),sQuery(id+"F2.wireOp",EDGE,"E54"),sQuery(id+"F2.wireOp",EDGE,"E55"),sQuery(id+"F2.wireOp",EDGE,"E56"),sQuery(id+"F2.wireOp",EDGE,"E57"),sQuery(id+"F2.wireOp",EDGE,"E58"),sQuery(id+"F2.wireOp",EDGE,"E59"),sQuery(id+"F2.wireOp",EDGE,"E60"),sQuery(id+"F2.wireOp",EDGE,"E61"),sQuery(id+"F2.wireOp",EDGE,"E62"),sQuery(id+"F2.wireOp",EDGE,"E63"),sQuery(id+"F2.wireOp",EDGE,"E64"),sQuery(id+"F2.wireOp",EDGE,"E65"),sQuery(id+"F2.wireOp",EDGE,"E66"),sQuery(id+"F2.wireOp",EDGE,"E67"),sQuery(id+"F2.wireOp",EDGE,"E68"),sQuery(id+"F2.wireOp",EDGE,"E69"),sQuery(id+"F2.wireOp",EDGE,"E70"),sQuery(id+"F2.wireOp",EDGE,"E71"),sQuery(id+"F2.wireOp",EDGE,"E72"),sQuery(id+"F2.wireOp",EDGE,"E73"),sQuery(id+"F2.wireOp",EDGE,"E74"),sQuery(id+"F2.wireOp",EDGE,"E75"),sQuery(id+"F2.wireOp",EDGE,"E76"),sQuery(id+"F2.wireOp",EDGE,"E77"),sQuery(id+"F2.wireOp",EDGE,"E78"),sQuery(id+"F2.wireOp",EDGE,"E79"),sQuery(id+"F2.wireOp",EDGE,"E80"),sQuery(id+"F2.wireOp",EDGE,"E81"),sQuery(id+"F2.wireOp",EDGE,"E82"),sQuery(id+"F2.wireOp",EDGE,"E83"),sQuery(id+"F2.wireOp",EDGE,"E84"),sQuery(id+"F2.wireOp",EDGE,"E85"),sQuery(id+"F2.wireOp",EDGE,"E86"),sQuery(id+"F2.wireOp",EDGE,"E87"),sQuery(id+"F2.wireOp",EDGE,"E88"),sQuery(id+"F2.wireOp",EDGE,"E89"),sQuery(id+"F2.wireOp",EDGE,"E90"),sQuery(id+"F2.wireOp",EDGE,"E91"),sQuery(id+"F2.wireOp",EDGE,"E92"),sQuery(id+"F2.wireOp",EDGE,"E93"),sQuery(id+"F2.wireOp",EDGE,"E94"),sQuery(id+"F2.wireOp",EDGE,"E95"),sQuery(id+"F2.wireOp",EDGE,"E96"),sQuery(id+"F2.wireOp",EDGE,"E97"),sQuery(id+"F2.wireOp",EDGE,"E98"),sQuery(id+"F2.wireOp",EDGE,"E99"),sQuery(id+"F2.wireOp",EDGE,"E100"),sQuery(id+"F2.wireOp",EDGE,"E101"),sQuery(id+"F2.wireOp",EDGE,"E102"),sQuery(id+"F2.wireOp",EDGE,"E103"),sQuery(id+"F2.wireOp",EDGE,"E104"),sQuery(id+"F2.wireOp",EDGE,"E105"),sQuery(id+"F2.wireOp",EDGE,"E106"),sQuery(id+"F2.wireOp",EDGE,"E107"),sQuery(id+"F2.wireOp",EDGE,"E108"),sQuery(id+"F2.wireOp",EDGE,"E109"),sQuery(id+"F2.wireOp",EDGE,"E110"),sQuery(id+"F2.wireOp",EDGE,"E111"),sQuery(id+"F2.wireOp",EDGE,"E112"),sQuery(id+"F2.wireOp",EDGE,"E113"),sQuery(id+"F2.wireOp",EDGE,"E114"),sQuery(id+"F2.wireOp",EDGE,"E115"),sQuery(id+"F2.wireOp",EDGE,"E116"),sQuery(id+"F2.wireOp",EDGE,"E117"),sQuery(id+"F2.wireOp",EDGE,"E118"),sQuery(id+"F2.wireOp",EDGE,"E119"),sQuery(id+"F2.wireOp",EDGE,"E120"),sQuery(id+"F2.wireOp",EDGE,"E121"),sQuery(id+"F2.wireOp",EDGE,"E122"),sQuery(id+"F2.wireOp",EDGE,"E123"),sQuery(id+"F2.wireOp",EDGE,"E124"),sQuery(id+"F2.wireOp",EDGE,"E125"),sQuery(id+"F2.wireOp",EDGE,"E126"),sQuery(id+"F2.wireOp",EDGE,"E127"),sQuery(id+"F2.wireOp",EDGE,"E128"),sQuery(id+"F2.wireOp",EDGE,"E129"),sQuery(id+"F2.wireOp",EDGE,"E130"),sQuery(id+"F2.wireOp",EDGE,"E131"),sQuery(id+"F2.wireOp",EDGE,"E132"),sQuery(id+"F2.wireOp",EDGE,"E133"),sQuery(id+"F2.wireOp",EDGE,"E134"),sQuery(id+"F2.wireOp",EDGE,"E135"),sQuery(id+"F2.wireOp",EDGE,"E136"),sQuery(id+"F2.wireOp",EDGE,"E137"),sQuery(id+"F2.wireOp",EDGE,"E138"),sQuery(id+"F2.wireOp",EDGE,"E139"),sQuery(id+"F2.wireOp",EDGE,"E140"),sQuery(id+"F2.wireOp",EDGE,"E141"),sQuery(id+"F2.wireOp",EDGE,"E142"),sQuery(id+"F2.wireOp",EDGE,"E143"),sQuery(id+"F2.wireOp",EDGE,"E144"),sQuery(id+"F2.wireOp",EDGE,"E145"),sQuery(id+"F2.wireOp",EDGE,"E146"),sQuery(id+"F2.wireOp",EDGE,"E147"),sQuery(id+"F2.wireOp",EDGE,"E148"),sQuery(id+"F2.wireOp",EDGE,"E149"),sQuery(id+"F2.wireOp",EDGE,"E150"),sQuery(id+"F2.wireOp",EDGE,"E151"),sQuery(id+"F2.wireOp",EDGE,"E152"),sQuery(id+"F2.wireOp",EDGE,"E153"),sQuery(id+"F2.wireOp",EDGE,"E154"),sQuery(id+"F2.wireOp",EDGE,"E155"),sQuery(id+"F2.wireOp",EDGE,"E156"),sQuery(id+"F2.wireOp",EDGE,"E157"),sQuery(id+"F2.wireOp",EDGE,"E158"),sQuery(id+"F2.wireOp",EDGE,"E159"),sQuery(id+"F2.wireOp",EDGE,"E160"),sQuery(id+"F2.wireOp",EDGE,"E161"),sQuery(id+"F2.wireOp",EDGE,"E162"),sQuery(id+"F2.wireOp",EDGE,"E163"),sQuery(id+"F2.wireOp",EDGE,"E164"),sQuery(id+"F2.wireOp",EDGE,"E165"),sQuery(id+"F2.wireOp",EDGE,"E166"),sQuery(id+"F2.wireOp",EDGE,"E167"),sQuery(id+"F2.wireOp",EDGE,"E168"),sQuery(id+"F2.wireOp",EDGE,"E169"),sQuery(id+"F2.wireOp",EDGE,"E170"),sQuery(id+"F2.wireOp",EDGE,"E171"),sQuery(id+"F2.wireOp",EDGE,"E172"),sQuery(id+"F2.wireOp",EDGE,"E173"),sQuery(id+"F2.wireOp",EDGE,"E174"),sQuery(id+"F2.wireOp",EDGE,"E175"),sQuery(id+"F2.wireOp",EDGE,"E176"),sQuery(id+"F2.wireOp",EDGE,"E177"),sQuery(id+"F2.wireOp",EDGE,"E178"),sQuery(id+"F2.wireOp",EDGE,"E179"),sQuery(id+"F2.wireOp",EDGE,"E180"),sQuery(id+"F2.wireOp",EDGE,"E181"),sQuery(id+"F2.wireOp",EDGE,"E182"),sQuery(id+"F2.wireOp",EDGE,"E183"),sQuery(id+"F2.wireOp",EDGE,"E184"),sQuery(id+"F2.wireOp",EDGE,"E185"),sQuery(id+"F2.wireOp",EDGE,"E186"),sQuery(id+"F2.wireOp",EDGE,"E187"),sQuery(id+"F2.wireOp",EDGE,"E188"),sQuery(id+"F2.wireOp",EDGE,"E189"),sQuery(id+"F2.wireOp",EDGE,"E190"),sQuery(id+"F2.wireOp",EDGE,"E191"),sQuery(id+"F2.wireOp",EDGE,"E192"),sQuery(id+"F2.wireOp",EDGE,"E193"),sQuery(id+"F2.wireOp",EDGE,"E194"),sQuery(id+"F2.wireOp",EDGE,"E195"),sQuery(id+"F2.wireOp",EDGE,"E196"),sQuery(id+"F2.wireOp",EDGE,"E197"),sQuery(id+"F2.wireOp",EDGE,"E198"),sQuery(id+"F2.wireOp",EDGE,"E199"),sQuery(id+"F2.wireOp",EDGE,"E200"),sQuery(id+"F2.wireOp",EDGE,"E201"),sQuery(id+"F2.wireOp",EDGE,"E202"),sQuery(id+"F2.wireOp",EDGE,"E203"),sQuery(id+"F2.wireOp",EDGE,"E204"),sQuery(id+"F2.wireOp",EDGE,"E205"),sQuery(id+"F2.wireOp",EDGE,"E206"),sQuery(id+"F2.wireOp",EDGE,"E207"),sQuery(id+"F2.wireOp",EDGE,"E208"),sQuery(id+"F2.wireOp",EDGE,"E209"),sQuery(id+"F2.wireOp",EDGE,"E210"),sQuery(id+"F2.wireOp",EDGE,"E211"),sQuery(id+"F2.wireOp",EDGE,"E212"),sQuery(id+"F2.wireOp",EDGE,"E213"),sQuery(id+"F2.wireOp",EDGE,"E214"),sQuery(id+"F2.wireOp",EDGE,"E215"),sQuery(id+"F2.wireOp",EDGE,"E216"),sQuery(id+"F2.wireOp",EDGE,"E217"),sQuery(id+"F2.wireOp",EDGE,"E218"),sQuery(id+"F2.wireOp",EDGE,"E219"),sQuery(id+"F2.wireOp",EDGE,"E220"),sQuery(id+"F2.wireOp",EDGE,"E221"),sQuery(id+"F2.wireOp",EDGE,"E222"),sQuery(id+"F2.wireOp",EDGE,"E223"),sQuery(id+"F2.wireOp",EDGE,"E224"),sQuery(id+"F2.wireOp",EDGE,"E225"),sQuery(id+"F2.wireOp",EDGE,"E226"),sQuery(id+"F2.wireOp",EDGE,"E227"),sQuery(id+"F2.wireOp",EDGE,"E228"),sQuery(id+"F2.wireOp",EDGE,"E229"),sQuery(id+"F2.wireOp",EDGE,"E230"),sQuery(id+"F2.wireOp",EDGE,"E231"),sQuery(id+"F2.wireOp",EDGE,"E232"),sQuery(id+"F2.wireOp",EDGE,"E233"),sQuery(id+"F2.wireOp",EDGE,"E234"),sQuery(id+"F2.wireOp",EDGE,"E235"),sQuery(id+"F2.wireOp",EDGE,"E236"),sQuery(id+"F2.wireOp",EDGE,"E237"),sQuery(id+"F2.wireOp",EDGE,"E238"),sQuery(id+"F2.wireOp",EDGE,"E239"),sQuery(id+"F2.wireOp",EDGE,"E240"),sQuery(id+"F2.wireOp",EDGE,"E241"),sQuery(id+"F2.wireOp",EDGE,"E242"),sQuery(id+"F2.wireOp",EDGE,"E243"),sQuery(id+"F2.wireOp",EDGE,"E244"),sQuery(id+"F2.wireOp",EDGE,"E245"),sQuery(id+"F2.wireOp",EDGE,"E246"),sQuery(id+"F2.wireOp",EDGE,"E247"),sQuery(id+"F2.wireOp",EDGE,"E248"),sQuery(id+"F2.wireOp",EDGE,"E249"),sQuery(id+"F2.wireOp",EDGE,"E250"),sQuery(id+"F2.wireOp",EDGE,"E251"),sQuery(id+"F2.wireOp",EDGE,"E252"),sQuery(id+"F2.wireOp",EDGE,"E253"),sQuery(id+"F2.wireOp",EDGE,"E254"),sQuery(id+"F2.wireOp",EDGE,"E255"),sQuery(id+"F2.wireOp",EDGE,"E256"),sQuery(id+"F2.wireOp",EDGE,"E257"),sQuery(id+"F2.wireOp",EDGE,"E258"),sQuery(id+"F2.wireOp",EDGE,"E259"),sQuery(id+"F2.wireOp",EDGE,"E260"),sQuery(id+"F2.wireOp",EDGE,"E261"),sQuery(id+"F2.wireOp",EDGE,"E262"),sQuery(id+"F2.wireOp",EDGE,"E263"),sQuery(id+"F2.wireOp",EDGE,"E264"),sQuery(id+"F2.wireOp",EDGE,"E265"),sQuery(id+"F2.wireOp",EDGE,"E266"),sQuery(id+"F2.wireOp",EDGE,"E267"),sQuery(id+"F2.wireOp",EDGE,"E268"),sQuery(id+"F2.wireOp",EDGE,"E269"),sQuery(id+"F2.wireOp",EDGE,"E270"),sQuery(id+"F2.wireOp",EDGE,"E271"),sQuery(id+"F2.wireOp",EDGE,"E272"),sQuery(id+"F2.wireOp",EDGE,"E273"),sQuery(id+"F2.wireOp",EDGE,"E274"),sQuery(id+"F2.wireOp",EDGE,"E275"),sQuery(id+"F2.wireOp",EDGE,"E276"),sQuery(id+"F2.wireOp",EDGE,"E277"),sQuery(id+"F2.wireOp",EDGE,"E278"),sQuery(id+"F2.wireOp",EDGE,"E279"),sQuery(id+"F2.wireOp",EDGE,"E280"),sQuery(id+"F2.wireOp",EDGE,"E281"),sQuery(id+"F2.wireOp",EDGE,"E282"),sQuery(id+"F2.wireOp",EDGE,"E283"),sQuery(id+"F2.wireOp",EDGE,"E284"),sQuery(id+"F2.wireOp",EDGE,"E285"),sQuery(id+"F2.wireOp",EDGE,"E286"),sQuery(id+"F2.wireOp",EDGE,"E287"),sQuery(id+"F2.wireOp",EDGE,"E288"),sQuery(id+"F2.wireOp",EDGE,"E289"),sQuery(id+"F2.wireOp",EDGE,"E290"),sQuery(id+"F2.wireOp",EDGE,"E291"),sQuery(id+"F2.wireOp",EDGE,"E292"),sQuery(id+"F2.wireOp",EDGE,"E293"),sQuery(id+"F2.wireOp",EDGE,"E294"),sQuery(id+"F2.wireOp",EDGE,"E295"),sQuery(id+"F2.wireOp",EDGE,"E296"),sQuery(id+"F2.wireOp",EDGE,"E297"),sQuery(id+"F2.wireOp",EDGE,"E298"),sQuery(id+"F2.wireOp",EDGE,"E299"),sQuery(id+"F2.wireOp",EDGE,"E300"),sQuery(id+"F2.wireOp",EDGE,"E301"),sQuery(id+"F2.wireOp",EDGE,"E302"),sQuery(id+"F2.wireOp",EDGE,"E303"),sQuery(id+"F2.wireOp",EDGE,"E304"),sQuery(id+"F2.wireOp",EDGE,"E305"),sQuery(id+"F2.wireOp",EDGE,"E306"),sQuery(id+"F2.wireOp",EDGE,"E307"),sQuery(id+"F2.wireOp",EDGE,"E308"),sQuery(id+"F2.wireOp",EDGE,"E309"),sQuery(id+"F2.wireOp",EDGE,"E310"),sQuery(id+"F2.wireOp",EDGE,"E311"),sQuery(id+"F2.wireOp",EDGE,"E312"),sQuery(id+"F2.wireOp",EDGE,"E313"),sQuery(id+"F2.wireOp",EDGE,"E314"),sQuery(id+"F2.wireOp",EDGE,"E315"),sQuery(id+"F2.wireOp",EDGE,"E316"),sQuery(id+"F2.wireOp",EDGE,"E317"),sQuery(id+"F2.wireOp",EDGE,"E318"),sQuery(id+"F2.wireOp",EDGE,"E319"),sQuery(id+"F2.wireOp",EDGE,"E320"),sQuery(id+"F2.wireOp",EDGE,"E321"),sQuery(id+"F2.wireOp",EDGE,"E322"),sQuery(id+"F2.wireOp",EDGE,"E323"),sQuery(id+"F2.wireOp",EDGE,"E324"),sQuery(id+"F2.wireOp",EDGE,"E325"),sQuery(id+"F2.wireOp",EDGE,"E326"),sQuery(id+"F2.wireOp",EDGE,"E327"),sQuery(id+"F2.wireOp",EDGE,"E328"),sQuery(id+"F2.wireOp",EDGE,"E329"),sQuery(id+"F2.wireOp",EDGE,"E330"),sQuery(id+"F2.wireOp",EDGE,"E331"),sQuery(id+"F2.wireOp",EDGE,"E332"),sQuery(id+"F2.wireOp",EDGE,"E333"),sQuery(id+"F2.wireOp",EDGE,"E334"),sQuery(id+"F2.wireOp",EDGE,"E335"),sQuery(id+"F2.wireOp",EDGE,"E336"),sQuery(id+"F2.wireOp",EDGE,"E337"),sQuery(id+"F2.wireOp",EDGE,"E338"),sQuery(id+"F2.wireOp",EDGE,"E339"),sQuery(id+"F2.wireOp",EDGE,"E340"),sQuery(id+"F2.wireOp",EDGE,"E341"),sQuery(id+"F2.wireOp",EDGE,"E342"),sQuery(id+"F2.wireOp",EDGE,"E343"),sQuery(id+"F2.wireOp",EDGE,"E344"),sQuery(id+"F2.wireOp",EDGE,"E345"),sQuery(id+"F2.wireOp",EDGE,"E346"),sQuery(id+"F2.wireOp",EDGE,"E347"),sQuery(id+"F2.wireOp",EDGE,"E348"),sQuery(id+"F2.wireOp",EDGE,"E349"),sQuery(id+"F2.wireOp",EDGE,"E350"),sQuery(id+"F2.wireOp",EDGE,"E351"),sQuery(id+"F2.wireOp",EDGE,"E352"),sQuery(id+"F2.wireOp",EDGE,"E353"),sQuery(id+"F2.wireOp",EDGE,"E354"),sQuery(id+"F2.wireOp",EDGE,"E355"),sQuery(id+"F2.wireOp",EDGE,"E356"),sQuery(id+"F2.wireOp",EDGE,"E357"),sQuery(id+"F2.wireOp",EDGE,"E358"),sQuery(id+"F2.wireOp",EDGE,"E359"),sQuery(id+"F2.wireOp",EDGE,"E360"),sQuery(id+"F2.wireOp",EDGE,"E361"),sQuery(id+"F2.wireOp",EDGE,"E362"),sQuery(id+"F2.wireOp",EDGE,"E363"),sQuery(id+"F2.wireOp",EDGE,"E364"),sQuery(id+"F2.wireOp",EDGE,"E365"),sQuery(id+"F2.wireOp",EDGE,"E366"),sQuery(id+"F2.wireOp",EDGE,"E367"),sQuery(id+"F2.wireOp",EDGE,"E368"),sQuery(id+"F2.wireOp",EDGE,"E369"),sQuery(id+"F2.wireOp",EDGE,"E370"),sQuery(id+"F2.wireOp",EDGE,"E371"),sQuery(id+"F2.wireOp",EDGE,"E372"),sQuery(id+"F2.wireOp",EDGE,"E373"),sQuery(id+"F2.wireOp",EDGE,"E374"),sQuery(id+"F2.wireOp",EDGE,"E375"),sQuery(id+"F2.wireOp",EDGE,"E376"),sQuery(id+"F2.wireOp",EDGE,"E377"),sQuery(id+"F2.wireOp",EDGE,"E378"),sQuery(id+"F2.wireOp",EDGE,"E379"),sQuery(id+"F2.wireOp",EDGE,"E380"),sQuery(id+"F2.wireOp",EDGE,"E381"),sQuery(id+"F2.wireOp",EDGE,"E382"),sQuery(id+"F2.wireOp",EDGE,"E383"),sQuery(id+"F2.wireOp",EDGE,"E384"),sQuery(id+"F2.wireOp",EDGE,"E385"),sQuery(id+"F2.wireOp",EDGE,"E386"),sQuery(id+"F2.wireOp",EDGE,"E387"),sQuery(id+"F2.wireOp",EDGE,"E388"),sQuery(id+"F2.wireOp",EDGE,"E389"),sQuery(id+"F2.wireOp",EDGE,"E390"),sQuery(id+"F2.wireOp",EDGE,"E391"),sQuery(id+"F2.wireOp",EDGE,"E392"),sQuery(id+"F2.wireOp",EDGE,"E393"),sQuery(id+"F2.wireOp",EDGE,"E394"),sQuery(id+"F2.wireOp",EDGE,"E395"),sQuery(id+"F2.wireOp",EDGE,"E396"),sQuery(id+"F2.wireOp",EDGE,"E397"),sQuery(id+"F2.wireOp",EDGE,"E398"),sQuery(id+"F2.wireOp",EDGE,"E399"),sQuery(id+"F2.wireOp",EDGE,"E400"),sQuery(id+"F2.wireOp",EDGE,"E401"),sQuery(id+"F2.wireOp",EDGE,"E402"),sQuery(id+"F2.wireOp",EDGE,"E403"),sQuery(id+"F2.wireOp",EDGE,"E404"),sQuery(id+"F2.wireOp",EDGE,"E405"),sQuery(id+"F2.wireOp",EDGE,"E406"),sQuery(id+"F2.wireOp",EDGE,"E407"),sQuery(id+"F2.wireOp",EDGE,"E408"),sQuery(id+"F2.wireOp",EDGE,"E409"),sQuery(id+"F2.wireOp",EDGE,"E410"),sQuery(id+"F2.wireOp",EDGE,"E411"),sQuery(id+"F2.wireOp",EDGE,"E412"),sQuery(id+"F2.wireOp",EDGE,"E413"),sQuery(id+"F2.wireOp",EDGE,"E414"),sQuery(id+"F2.wireOp",EDGE,"E415"),sQuery(id+"F2.wireOp",EDGE,"E416"),sQuery(id+"F2.wireOp",EDGE,"E417"),sQuery(id+"F2.wireOp",EDGE,"E418"),sQuery(id+"F2.wireOp",EDGE,"E419"),sQuery(id+"F2.wireOp",EDGE,"E420"),sQuery(id+"F2.wireOp",EDGE,"E421"),sQuery(id+"F2.wireOp",EDGE,"E422"),sQuery(id+"F2.wireOp",EDGE,"E423"),sQuery(id+"F2.wireOp",EDGE,"E424"),sQuery(id+"F2.wireOp",EDGE,"E425"),sQuery(id+"F2.wireOp",EDGE,"E426"),sQuery(id+"F2.wireOp",EDGE,"E427"),sQuery(id+"F2.wireOp",EDGE,"E428"),sQuery(id+"F2.wireOp",EDGE,"E429"),sQuery(id+"F2.wireOp",EDGE,"E430"),sQuery(id+"F2.wireOp",EDGE,"E431"),sQuery(id+"F2.wireOp",EDGE,"E432"),sQuery(id+"F2.wireOp",EDGE,"E433"),sQuery(id+"F2.wireOp",EDGE,"E434"),sQuery(id+"F2.wireOp",EDGE,"E435"),sQuery(id+"F2.wireOp",EDGE,"E436"),sQuery(id+"F2.wireOp",EDGE,"E437"),sQuery(id+"F2.wireOp",EDGE,"E438"),sQuery(id+"F2.wireOp",EDGE,"E439"),sQuery(id+"F2.wireOp",EDGE,"E440"),sQuery(id+"F2.wireOp",EDGE,"E441"),sQuery(id+"F2.wireOp",EDGE,"E442"),sQuery(id+"F2.wireOp",EDGE,"E443"),sQuery(id+"F2.wireOp",EDGE,"E444"),sQuery(id+"F2.wireOp",EDGE,"E445"),sQuery(id+"F2.wireOp",EDGE,"E446"),sQuery(id+"F2.wireOp",EDGE,"E447"),sQuery(id+"F2.wireOp",EDGE,"E447"),sQuery(id+"F2.wireOp",EDGE,"E447"),sQuery(id+"F2.wireOp",EDGE,"E448"),sQuery(id+"F2.wireOp",EDGE,"E449"),sQuery(id+"F2.wireOp",EDGE,"E450"),sQuery(id+"F2.wireOp",EDGE,"E451"),sQuery(id+"F2.wireOp",EDGE,"E452"),sQuery(id+"F2.wireOp",EDGE,"E453"),sQuery(id+"F2.wireOp",EDGE,"E454"),sQuery(id+"F2.wireOp",EDGE,"E455"),sQuery(id+"F2.wireOp",EDGE,"E456"),sQuery(id+"F2.wireOp",EDGE,"E457"),sQuery(id+"F2.wireOp",EDGE,"E458"),sQuery(id+"F2.wireOp",EDGE,"E459"),sQuery(id+"F2.wireOp",EDGE,"E460"),sQuery(id+"F2.wireOp",EDGE,"E461"),sQuery(id+"F2.wireOp",EDGE,"E462"),sQuery(id+"F2.wireOp",EDGE,"E463"),sQuery(id+"F2.wireOp",EDGE,"E464"),sQuery(id+"F2.wireOp",EDGE,"E465"),sQuery(id+"F2.wireOp",EDGE,"E466"),sQuery(id+"F2.wireOp",EDGE,"E467"),sQuery(id+"F2.wireOp",EDGE,"E468"),sQuery(id+"F2.wireOp",EDGE,"E469"),sQuery(id+"F2.wireOp",EDGE,"E470"),sQuery(id+"F2.wireOp",EDGE,"E471"),sQuery(id+"F2.wireOp",EDGE,"E472"),sQuery(id+"F2.wireOp",EDGE,"E473"),sQuery(id+"F2.wireOp",EDGE,"E474"),sQuery(id+"F2.wireOp",EDGE,"E475"),sQuery(id+"F2.wireOp",EDGE,"E476"),sQuery(id+"F2.wireOp",EDGE,"E477"),sQuery(id+"F2.wireOp",EDGE,"E478"),sQuery(id+"F2.wireOp",EDGE,"E479"),sQuery(id+"F2.wireOp",EDGE,"E480"),sQuery(id+"F2.wireOp",EDGE,"E481"),sQuery(id+"F2.wireOp",EDGE,"E482"),sQuery(id+"F2.wireOp",EDGE,"E483"),sQuery(id+"F2.wireOp",EDGE,"E484"),sQuery(id+"F2.wireOp",EDGE,"E485"),sQuery(id+"F2.wireOp",EDGE,"E486"),sQuery(id+"F2.wireOp",EDGE,"E487"),sQuery(id+"F2.wireOp",EDGE,"E488"),sQuery(id+"F2.wireOp",EDGE,"E489"),sQuery(id+"F2.wireOp",EDGE,"E490"),sQuery(id+"F2.wireOp",EDGE,"E491"),sQuery(id+"F2.wireOp",EDGE,"E492"),sQuery(id+"F2.wireOp",EDGE,"E493"),sQuery(id+"F2.wireOp",EDGE,"E494"),sQuery(id+"F2.wireOp",EDGE,"E495"),sQuery(id+"F2.wireOp",EDGE,"E496"),sQuery(id+"F2.wireOp",EDGE,"E497"),sQuery(id+"F2.wireOp",EDGE,"E498"),sQuery(id+"F2.wireOp",EDGE,"E499"),sQuery(id+"F2.wireOp",EDGE,"E500"),sQuery(id+"F2.wireOp",EDGE,"E501"),sQuery(id+"F2.wireOp",EDGE,"E502"),sQuery(id+"F2.wireOp",EDGE,"E503"),sQuery(id+"F2.wireOp",EDGE,"E504"),sQuery(id+"F2.wireOp",EDGE,"E505"),sQuery(id+"F2.wireOp",EDGE,"E506"),sQuery(id+"F2.wireOp",EDGE,"E507"),sQuery(id+"F2.wireOp",EDGE,"E508"),sQuery(id+"F2.wireOp",EDGE,"E509"),sQuery(id+"F2.wireOp",EDGE,"E510"),sQuery(id+"F2.wireOp",EDGE,"E511"),sQuery(id+"F2.wireOp",EDGE,"E512"),sQuery(id+"F2.wireOp",EDGE,"E513"),sQuery(id+"F2.wireOp",EDGE,"E514"),sQuery(id+"F2.wireOp",EDGE,"E515"),sQuery(id+"F2.wireOp",EDGE,"E516"),sQuery(id+"F2.wireOp",EDGE,"E517"),sQuery(id+"F2.wireOp",EDGE,"E518"),sQuery(id+"F2.wireOp",EDGE,"E519"),sQuery(id+"F2.wireOp",EDGE,"E520"),sQuery(id+"F2.wireOp",EDGE,"E521"),sQuery(id+"F2.wireOp",EDGE,"E522"),sQuery(id+"F2.wireOp",EDGE,"E523"),sQuery(id+"F2.wireOp",EDGE,"E524"),sQuery(id+"F2.wireOp",EDGE,"E525"),sQuery(id+"F2.wireOp",EDGE,"E526"),sQuery(id+"F2.wireOp",EDGE,"E527"),sQuery(id+"F2.wireOp",EDGE,"E528"),sQuery(id+"F2.wireOp",EDGE,"E529"),sQuery(id+"F2.wireOp",EDGE,"E530"),sQuery(id+"F2.wireOp",EDGE,"E531"),sQuery(id+"F2.wireOp",EDGE,"E532"),sQuery(id+"F2.wireOp",EDGE,"E533"),sQuery(id+"F2.wireOp",EDGE,"E534"),sQuery(id+"F2.wireOp",EDGE,"E535"),sQuery(id+"F2.wireOp",EDGE,"E536"),sQuery(id+"F2.wireOp",EDGE,"E537"),sQuery(id+"F2.wireOp",EDGE,"E538"),sQuery(id+"F2.wireOp",EDGE,"E539"),sQuery(id+"F2.wireOp",EDGE,"E540"),sQuery(id+"F2.wireOp",EDGE,"E541"),sQuery(id+"F2.wireOp",EDGE,"E542"),sQuery(id+"F2.wireOp",EDGE,"E543"),sQuery(id+"F2.wireOp",EDGE,"E544"),sQuery(id+"F2.wireOp",EDGE,"E545"),sQuery(id+"F2.wireOp",EDGE,"E546"),sQuery(id+"F2.wireOp",EDGE,"E547"),sQuery(id+"F2.wireOp",EDGE,"E547"),sQuery(id+"F2.wireOp",EDGE,"E548"),sQuery(id+"F2.wireOp",EDGE,"E549"),sQuery(id+"F2.wireOp",EDGE,"E550"),sQuery(id+"F2.wireOp",EDGE,"E551"),sQuery(id+"F2.wireOp",EDGE,"E552"),sQuery(id+"F2.wireOp",EDGE,"E553"),sQuery(id+"F2.wireOp",EDGE,"E554"),sQuery(id+"F2.wireOp",EDGE,"E555"),sQuery(id+"F2.wireOp",EDGE,"E556"),sQuery(id+"F2.wireOp",EDGE,"E557"),sQuery(id+"F2.wireOp",EDGE,"E558"),sQuery(id+"F2.wireOp",EDGE,"E559"),sQuery(id+"F2.wireOp",EDGE,"E560"),sQuery(id+"F2.wireOp",EDGE,"E561"),sQuery(id+"F2.wireOp",EDGE,"E562"),sQuery(id+"F2.wireOp",EDGE,"E563"),sQuery(id+"F2.wireOp",EDGE,"E564"),sQuery(id+"F2.wireOp",EDGE,"E565"),sQuery(id+"F2.wireOp",EDGE,"E566"),sQuery(id+"F2.wireOp",EDGE,"E567"),sQuery(id+"F2.wireOp",EDGE,"E568"),sQuery(id+"F2.wireOp",EDGE,"E569"),sQuery(id+"F2.wireOp",EDGE,"E570"),sQuery(id+"F2.wireOp",EDGE,"E571"),sQuery(id+"F2.wireOp",EDGE,"E572"),sQuery(id+"F2.wireOp",EDGE,"E573"),sQuery(id+"F2.wireOp",EDGE,"E574"),sQuery(id+"F2.wireOp",EDGE,"E575"),sQuery(id+"F2.wireOp",EDGE,"E576"),sQuery(id+"F2.wireOp",EDGE,"E577"),sQuery(id+"F2.wireOp",EDGE,"E578"),sQuery(id+"F2.wireOp",EDGE,"E579"),sQuery(id+"F2.wireOp",EDGE,"E580"),sQuery(id+"F2.wireOp",EDGE,"E581"),sQuery(id+"F2.wireOp",EDGE,"E582"),sQuery(id+"F2.wireOp",EDGE,"E583"),sQuery(id+"F2.wireOp",EDGE,"E584"),sQuery(id+"F2.wireOp",EDGE,"E585"),sQuery(id+"F2.wireOp",EDGE,"E586"),sQuery(id+"F2.wireOp",EDGE,"E587"),sQuery(id+"F2.wireOp",EDGE,"E588"),sQuery(id+"F2.wireOp",EDGE,"E589"),sQuery(id+"F2.wireOp",EDGE,"E590"),sQuery(id+"F2.wireOp",EDGE,"E591"),sQuery(id+"F2.wireOp",EDGE,"E592"),sQuery(id+"F2.wireOp",EDGE,"E593"),sQuery(id+"F2.wireOp",EDGE,"E594"),sQuery(id+"F2.wireOp",EDGE,"E595"),sQuery(id+"F2.wireOp",EDGE,"E596"),sQuery(id+"F2.wireOp",EDGE,"E597"),sQuery(id+"F2.wireOp",EDGE,"E598"),sQuery(id+"F2.wireOp",EDGE,"E599"),sQuery(id+"F2.wireOp",EDGE,"E600"),sQuery(id+"F2.wireOp",EDGE,"E601"),sQuery(id+"F2.wireOp",EDGE,"E602"),sQuery(id+"F2.wireOp",EDGE,"E603"),sQuery(id+"F2.wireOp",EDGE,"E604"),sQuery(id+"F2.wireOp",EDGE,"E605"),sQuery(id+"F2.wireOp",EDGE,"E606"),sQuery(id+"F2.wireOp",EDGE,"E607"),sQuery(id+"F2.wireOp",EDGE,"E608"),sQuery(id+"F2.wireOp",EDGE,"E609"),sQuery(id+"F2.wireOp",EDGE,"E610"),sQuery(id+"F2.wireOp",EDGE,"E611"),sQuery(id+"F2.wireOp",EDGE,"E612"),sQuery(id+"F2.wireOp",EDGE,"E613"),sQuery(id+"F2.wireOp",EDGE,"E614"),sQuery(id+"F2.wireOp",EDGE,"E615"),sQuery(id+"F2.wireOp",EDGE,"E616"),sQuery(id+"F2.wireOp",EDGE,"E617"),sQuery(id+"F2.wireOp",EDGE,"E618"),sQuery(id+"F2.wireOp",EDGE,"E619"),sQuery(id+"F2.wireOp",EDGE,"E620"),sQuery(id+"F2.wireOp",EDGE,"E621"),sQuery(id+"F2.wireOp",EDGE,"E622"),sQuery(id+"F2.wireOp",EDGE,"E623"),sQuery(id+"F2.wireOp",EDGE,"E624"),sQuery(id+"F2.wireOp",EDGE,"E625"),sQuery(id+"F2.wireOp",EDGE,"E626"),sQuery(id+"F2.wireOp",EDGE,"E627"),sQuery(id+"F2.wireOp",EDGE,"E628"),sQuery(id+"F2.wireOp",EDGE,"E629"),sQuery(id+"F2.wireOp",EDGE,"E630"),sQuery(id+"F2.wireOp",EDGE,"E631"),sQuery(id+"F2.wireOp",EDGE,"E632"),sQuery(id+"F2.wireOp",EDGE,"E633"),sQuery(id+"F2.wireOp",EDGE,"E634"),sQuery(id+"F2.wireOp",EDGE,"E635"),sQuery(id+"F2.wireOp",EDGE,"E636"),sQuery(id+"F2.wireOp",EDGE,"E637"),sQuery(id+"F2.wireOp",EDGE,"E638"),sQuery(id+"F2.wireOp",EDGE,"E639"),sQuery(id+"F2.wireOp",EDGE,"E640"),sQuery(id+"F2.wireOp",EDGE,"E641"),sQuery(id+"F2.wireOp",EDGE,"E642"),sQuery(id+"F2.wireOp",EDGE,"E643"),sQuery(id+"F2.wireOp",EDGE,"E644"),sQuery(id+"F2.wireOp",EDGE,"E645"),sQuery(id+"F2.wireOp",EDGE,"E646"),sQuery(id+"F2.wireOp",EDGE,"E647"),sQuery(id+"F2.wireOp",EDGE,"E648"),sQuery(id+"F2.wireOp",EDGE,"E649"),sQuery(id+"F2.wireOp",EDGE,"E650"),sQuery(id+"F2.wireOp",EDGE,"E651"),sQuery(id+"F2.wireOp",EDGE,"E652"),sQuery(id+"F2.wireOp",EDGE,"E653"),sQuery(id+"F2.wireOp",EDGE,"E654"),sQuery(id+"F2.wireOp",EDGE,"E655"),sQuery(id+"F2.wireOp",EDGE,"E656"),sQuery(id+"F2.wireOp",EDGE,"E657"),sQuery(id+"F2.wireOp",EDGE,"E658"),sQuery(id+"F2.wireOp",EDGE,"E659"),sQuery(id+"F2.wireOp",EDGE,"E660"),sQuery(id+"F2.wireOp",EDGE,"E661"),sQuery(id+"F2.wireOp",EDGE,"E662"),sQuery(id+"F2.wireOp",EDGE,"E663"),sQuery(id+"F2.wireOp",EDGE,"E664"),sQuery(id+"F2.wireOp",EDGE,"E665"),sQuery(id+"F2.wireOp",EDGE,"E666"),sQuery(id+"F2.wireOp",EDGE,"E667"),sQuery(id+"F2.wireOp",EDGE,"E668"),sQuery(id+"F2.wireOp",EDGE,"E669"),sQuery(id+"F2.wireOp",EDGE,"E670"),sQuery(id+"F2.wireOp",EDGE,"E671"),sQuery(id+"F2.wireOp",EDGE,"E672"),sQuery(id+"F2.wireOp",EDGE,"E673"),sQuery(id+"F2.wireOp",EDGE,"E674"),sQuery(id+"F2.wireOp",EDGE,"E675"),sQuery(id+"F2.wireOp",EDGE,"E676"),sQuery(id+"F2.wireOp",EDGE,"E677"),sQuery(id+"F2.wireOp",EDGE,"E678"),sQuery(id+"F2.wireOp",EDGE,"E679"),sQuery(id+"F2.wireOp",EDGE,"E680"),sQuery(id+"F2.wireOp",EDGE,"E681"),sQuery(id+"F2.wireOp",EDGE,"E682"),sQuery(id+"F2.wireOp",EDGE,"E683"),sQuery(id+"F2.wireOp",EDGE,"E684"),sQuery(id+"F2.wireOp",EDGE,"E685"),sQuery(id+"F2.wireOp",EDGE,"E686"),sQuery(id+"F2.wireOp",EDGE,"E687"),sQuery(id+"F2.wireOp",EDGE,"E688"),sQuery(id+"F2.wireOp",EDGE,"E689"),sQuery(id+"F2.wireOp",EDGE,"E690"),sQuery(id+"F2.wireOp",EDGE,"E691"),sQuery(id+"F2.wireOp",EDGE,"E692"),sQuery(id+"F2.wireOp",EDGE,"E693"),sQuery(id+"F2.wireOp",EDGE,"E694"),sQuery(id+"F2.wireOp",EDGE,"E695"),sQuery(id+"F2.wireOp",EDGE,"E696"),sQuery(id+"F2.wireOp",EDGE,"E697"),sQuery(id+"F2.wireOp",EDGE,"E698"),sQuery(id+"F2.wireOp",EDGE,"E699"),sQuery(id+"F2.wireOp",EDGE,"E700"),sQuery(id+"F2.wireOp",EDGE,"E701"),sQuery(id+"F2.wireOp",EDGE,"E702"),sQuery(id+"F2.wireOp",EDGE,"E703"),sQuery(id+"F2.wireOp",EDGE,"E704"),sQuery(id+"F2.wireOp",EDGE,"E705"),sQuery(id+"F2.wireOp",EDGE,"E706"),sQuery(id+"F2.wireOp",EDGE,"E707"),sQuery(id+"F2.wireOp",EDGE,"E708"),sQuery(id+"F2.wireOp",EDGE,"E709"),sQuery(id+"F2.wireOp",EDGE,"E710"),sQuery(id+"F2.wireOp",EDGE,"E711"),sQuery(id+"F2.wireOp",EDGE,"E712"),sQuery(id+"F2.wireOp",EDGE,"E713"),sQuery(id+"F2.wireOp",EDGE,"E714"),sQuery(id+"F2.wireOp",EDGE,"E715"),sQuery(id+"F2.wireOp",EDGE,"E716"),sQuery(id+"F2.wireOp",EDGE,"E717"),sQuery(id+"F2.wireOp",EDGE,"E718"),sQuery(id+"F2.wireOp",EDGE,"E719"),sQuery(id+"F2.wireOp",EDGE,"E720"),sQuery(id+"F2.wireOp",EDGE,"E721"),sQuery(id+"F2.wireOp",EDGE,"E722"),sQuery(id+"F2.wireOp",EDGE,"E723"),sQuery(id+"F2.wireOp",EDGE,"E724"),sQuery(id+"F2.wireOp",EDGE,"E725"),sQuery(id+"F2.wireOp",EDGE,"E726"),sQuery(id+"F2.wireOp",EDGE,"E727"),sQuery(id+"F2.wireOp",EDGE,"E728"),sQuery(id+"F2.wireOp",EDGE,"E729"),sQuery(id+"F2.wireOp",EDGE,"E730"),sQuery(id+"F2.wireOp",EDGE,"E731"),sQuery(id+"F2.wireOp",EDGE,"E732"),sQuery(id+"F2.wireOp",EDGE,"E733"),sQuery(id+"F2.wireOp",EDGE,"E734"),sQuery(id+"F2.wireOp",EDGE,"E735"),sQuery(id+"F2.wireOp",EDGE,"E736"),sQuery(id+"F2.wireOp",EDGE,"E737"),sQuery(id+"F2.wireOp",EDGE,"E738"),sQuery(id+"F2.wireOp",EDGE,"E739"),sQuery(id+"F2.wireOp",EDGE,"E740"),sQuery(id+"F2.wireOp",EDGE,"E741"),sQuery(id+"F2.wireOp",EDGE,"E742"),sQuery(id+"F2.wireOp",EDGE,"E743"),sQuery(id+"F2.wireOp",EDGE,"E744"),sQuery(id+"F2.wireOp",EDGE,"E745"),sQuery(id+"F2.wireOp",EDGE,"E746"),sQuery(id+"F2.wireOp",EDGE,"E747"),sQuery(id+"F2.wireOp",EDGE,"E748"),sQuery(id+"F2.wireOp",EDGE,"E749"),sQuery(id+"F2.wireOp",EDGE,"E750"),sQuery(id+"F2.wireOp",EDGE,"E751"),sQuery(id+"F2.wireOp",EDGE,"E752"),sQuery(id+"F2.wireOp",EDGE,"E753"),sQuery(id+"F2.wireOp",EDGE,"E754"),sQuery(id+"F2.wireOp",EDGE,"E755"),sQuery(id+"F2.wireOp",EDGE,"E756"),sQuery(id+"F2.wireOp",EDGE,"E757"),sQuery(id+"F2.wireOp",EDGE,"E758"),sQuery(id+"F2.wireOp",EDGE,"E759"),sQuery(id+"F2.wireOp",EDGE,"E760"),sQuery(id+"F2.wireOp",EDGE,"E761"),sQuery(id+"F2.wireOp",EDGE,"E762"),sQuery(id+"F2.wireOp",EDGE,"E763"),sQuery(id+"F2.wireOp",EDGE,"E764"),sQuery(id+"F2.wireOp",EDGE,"E765"),sQuery(id+"F2.wireOp",EDGE,"E766"),sQuery(id+"F2.wireOp",EDGE,"E767"),sQuery(id+"F2.wireOp",EDGE,"E768"),sQuery(id+"F2.wireOp",EDGE,"E769"),sQuery(id+"F2.wireOp",EDGE,"E770"),sQuery(id+"F2.wireOp",EDGE,"E771"),sQuery(id+"F2.wireOp",EDGE,"E772"),sQuery(id+"F2.wireOp",EDGE,"E773"),sQuery(id+"F2.wireOp",EDGE,"E774"),sQuery(id+"F2.wireOp",EDGE,"E775"),sQuery(id+"F2.wireOp",EDGE,"E776"),sQuery(id+"F2.wireOp",EDGE,"E777"),sQuery(id+"F2.wireOp",EDGE,"E778"),sQuery(id+"F2.wireOp",EDGE,"E779"),sQuery(id+"F2.wireOp",EDGE,"E780"),sQuery(id+"F2.wireOp",EDGE,"E781"),sQuery(id+"F2.wireOp",EDGE,"E782"),sQuery(id+"F2.wireOp",EDGE,"E783"),sQuery(id+"F2.wireOp",EDGE,"E784"),sQuery(id+"F2.wireOp",EDGE,"E785"),sQuery(id+"F2.wireOp",EDGE,"E786"),sQuery(id+"F2.wireOp",EDGE,"E787"),sQuery(id+"F2.wireOp",EDGE,"E788"),sQuery(id+"F2.wireOp",EDGE,"E789"),sQuery(id+"F2.wireOp",EDGE,"E790"),sQuery(id+"F2.wireOp",EDGE,"E791"),sQuery(id+"F2.wireOp",EDGE,"E792"),sQuery(id+"F2.wireOp",EDGE,"E793"),sQuery(id+"F2.wireOp",EDGE,"E794"),sQuery(id+"F2.wireOp",EDGE,"E795"),sQuery(id+"F2.wireOp",EDGE,"E796"),sQuery(id+"F2.wireOp",EDGE,"E797"),sQuery(id+"F2.wireOp",EDGE,"E798"),sQuery(id+"F2.wireOp",EDGE,"E799"),sQuery(id+"F2.wireOp",EDGE,"E800"),sQuery(id+"F2.wireOp",EDGE,"E801"),sQuery(id+"F2.wireOp",EDGE,"E802"),sQuery(id+"F2.wireOp",EDGE,"E803"),sQuery(id+"F2.wireOp",EDGE,"E804"),sQuery(id+"F2.wireOp",EDGE,"E805"),sQuery(id+"F2.wireOp",EDGE,"E806"),sQuery(id+"F2.wireOp",EDGE,"E807"),sQuery(id+"F2.wireOp",EDGE,"E808"),sQuery(id+"F2.wireOp",EDGE,"E809"),sQuery(id+"F2.wireOp",EDGE,"E810"),sQuery(id+"F2.wireOp",EDGE,"E811"),sQuery(id+"F2.wireOp",EDGE,"E812"),sQuery(id+"F2.wireOp",EDGE,"E813"),sQuery(id+"F2.wireOp",EDGE,"E814"),sQuery(id+"F2.wireOp",EDGE,"E815"),sQuery(id+"F2.wireOp",EDGE,"E816"),sQuery(id+"F2.wireOp",EDGE,"E817"),sQuery(id+"F2.wireOp",EDGE,"E818"),sQuery(id+"F2.wireOp",EDGE,"E819"),sQuery(id+"F2.wireOp",EDGE,"E820"),sQuery(id+"F2.wireOp",EDGE,"E821"),sQuery(id+"F2.wireOp",EDGE,"E822"),sQuery(id+"F2.wireOp",EDGE,"E823"),sQuery(id+"F2.wireOp",EDGE,"E824"),sQuery(id+"F2.wireOp",EDGE,"E825"),sQuery(id+"F2.wireOp",EDGE,"E826"),sQuery(id+"F2.wireOp",EDGE,"E827"),sQuery(id+"F2.wireOp",EDGE,"E828"),sQuery(id+"F2.wireOp",EDGE,"E829"),sQuery(id+"F2.wireOp",EDGE,"E830"),sQuery(id+"F2.wireOp",EDGE,"E831"),sQuery(id+"F2.wireOp",EDGE,"E832"),sQuery(id+"F2.wireOp",EDGE,"E833"),sQuery(id+"F2.wireOp",EDGE,"E834"),sQuery(id+"F2.wireOp",EDGE,"E835"),sQuery(id+"F2.wireOp",EDGE,"E836"),sQuery(id+"F2.wireOp",EDGE,"E837"),sQuery(id+"F2.wireOp",EDGE,"E838"),sQuery(id+"F2.wireOp",EDGE,"E839"),sQuery(id+"F2.wireOp",EDGE,"E840"),sQuery(id+"F2.wireOp",EDGE,"E841"),sQuery(id+"F2.wireOp",EDGE,"E842"),sQuery(id+"F2.wireOp",EDGE,"E843"),sQuery(id+"F2.wireOp",EDGE,"E844"),sQuery(id+"F2.wireOp",EDGE,"E845"),sQuery(id+"F2.wireOp",EDGE,"E846"),sQuery(id+"F2.wireOp",EDGE,"E847"),sQuery(id+"F2.wireOp",EDGE,"E848"),sQuery(id+"F2.wireOp",EDGE,"E849"),sQuery(id+"F2.wireOp",EDGE,"E850"),sQuery(id+"F2.wireOp",EDGE,"E851"),sQuery(id+"F2.wireOp",EDGE,"E852"),sQuery(id+"F2.wireOp",EDGE,"E853"),sQuery(id+"F2.wireOp",EDGE,"E854"),sQuery(id+"F2.wireOp",EDGE,"E855"),sQuery(id+"F2.wireOp",EDGE,"E856"),sQuery(id+"F2.wireOp",EDGE,"E857"),sQuery(id+"F2.wireOp",EDGE,"E858"),sQuery(id+"F2.wireOp",EDGE,"E859"),sQuery(id+"F2.wireOp",EDGE,"E860"),sQuery(id+"F2.wireOp",EDGE,"E861"),sQuery(id+"F2.wireOp",EDGE,"E862"),sQuery(id+"F2.wireOp",EDGE,"E863"),sQuery(id+"F2.wireOp",EDGE,"E864"),sQuery(id+"F2.wireOp",EDGE,"E865"),sQuery(id+"F2.wireOp",EDGE,"E866"),sQuery(id+"F2.wireOp",EDGE,"E867"),sQuery(id+"F2.wireOp",EDGE,"E868"),sQuery(id+"F2.wireOp",EDGE,"E869"),sQuery(id+"F2.wireOp",EDGE,"E870"),sQuery(id+"F2.wireOp",EDGE,"E871"),sQuery(id+"F2.wireOp",EDGE,"E872"),sQuery(id+"F2.wireOp",EDGE,"E873"),sQuery(id+"F2.wireOp",EDGE,"E874"),sQuery(id+"F2.wireOp",EDGE,"E875"),sQuery(id+"F2.wireOp",EDGE,"E876"),sQuery(id+"F2.wireOp",EDGE,"E877"),sQuery(id+"F2.wireOp",EDGE,"E878"),sQuery(id+"F2.wireOp",EDGE,"E879"),sQuery(id+"F2.wireOp",EDGE,"E880"),sQuery(id+"F2.wireOp",EDGE,"E881"),sQuery(id+"F2.wireOp",EDGE,"E882"),sQuery(id+"F2.wireOp",EDGE,"E883"),sQuery(id+"F2.wireOp",EDGE,"E884"),sQuery(id+"F2.wireOp",EDGE,"E885"),sQuery(id+"F2.wireOp",EDGE,"E886"),sQuery(id+"F2.wireOp",EDGE,"E887"),sQuery(id+"F2.wireOp",EDGE,"E888"),sQuery(id+"F2.wireOp",EDGE,"E889"),sQuery(id+"F2.wireOp",EDGE,"E890"),sQuery(id+"F2.wireOp",EDGE,"E891"),sQuery(id+"F2.wireOp",EDGE,"E892"),sQuery(id+"F2.wireOp",EDGE,"E893"),sQuery(id+"F2.wireOp",EDGE,"E894"),sQuery(id+"F2.wireOp",EDGE,"E895"),sQuery(id+"F2.wireOp",EDGE,"E896"),sQuery(id+"F2.wireOp",EDGE,"E897"),sQuery(id+"F2.wireOp",EDGE,"E898"),sQuery(id+"F2.wireOp",EDGE,"E899"),sQuery(id+"F2.wireOp",EDGE,"E900"),sQuery(id+"F2.wireOp",EDGE,"E901"),sQuery(id+"F2.wireOp",EDGE,"E902"),sQuery(id+"F2.wireOp",EDGE,"E903"),sQuery(id+"F2.wireOp",EDGE,"E904"),sQuery(id+"F2.wireOp",EDGE,"E905"),sQuery(id+"F2.wireOp",EDGE,"E906"),sQuery(id+"F2.wireOp",EDGE,"E907"),sQuery(id+"F2.wireOp",EDGE,"E908"),sQuery(id+"F2.wireOp",EDGE,"E909"),sQuery(id+"F2.wireOp",EDGE,"E910"),sQuery(id+"F2.wireOp",EDGE,"E911"),sQuery(id+"F2.wireOp",EDGE,"E912"),sQuery(id+"F2.wireOp",EDGE,"E913"),sQuery(id+"F2.wireOp",EDGE,"E914"),sQuery(id+"F2.wireOp",EDGE,"E915"),sQuery(id+"F2.wireOp",EDGE,"E916"),sQuery(id+"F2.wireOp",EDGE,"E917"),sQuery(id+"F2.wireOp",EDGE,"E918"),sQuery(id+"F2.wireOp",EDGE,"E919"),sQuery(id+"F2.wireOp",EDGE,"E920"),sQuery(id+"F2.wireOp",EDGE,"E921"),sQuery(id+"F2.wireOp",EDGE,"E922"),sQuery(id+"F2.wireOp",EDGE,"E923"),sQuery(id+"F2.wireOp",EDGE,"E924"),sQuery(id+"F2.wireOp",EDGE,"E925"),sQuery(id+"F2.wireOp",EDGE,"E926"),sQuery(id+"F2.wireOp",EDGE,"E927"),sQuery(id+"F2.wireOp",EDGE,"E928"),sQuery(id+"F2.wireOp",EDGE,"E929"),sQuery(id+"F2.wireOp",EDGE,"E930"),sQuery(id+"F2.wireOp",EDGE,"E931"),sQuery(id+"F2.wireOp",EDGE,"E932"),sQuery(id+"F2.wireOp",EDGE,"E933"),sQuery(id+"F2.wireOp",EDGE,"E934"),sQuery(id+"F2.wireOp",EDGE,"E935"),sQuery(id+"F2.wireOp",EDGE,"E936"),sQuery(id+"F2.wireOp",EDGE,"E937"),sQuery(id+"F2.wireOp",EDGE,"E938"),sQuery(id+"F2.wireOp",EDGE,"E939"),sQuery(id+"F2.wireOp",EDGE,"E940"),sQuery(id+"F2.wireOp",EDGE,"E941"),sQuery(id+"F2.wireOp",EDGE,"E942"),sQuery(id+"F2.wireOp",EDGE,"E943"),sQuery(id+"F2.wireOp",EDGE,"E944"),sQuery(id+"F2.wireOp",EDGE,"E945"),sQuery(id+"F2.wireOp",EDGE,"E946"),sQuery(id+"F2.wireOp",EDGE,"E947"),sQuery(id+"F2.wireOp",EDGE,"E948"),sQuery(id+"F2.wireOp",EDGE,"E949"),sQuery(id+"F2.wireOp",EDGE,"E950"),sQuery(id+"F2.wireOp",EDGE,"E951"),sQuery(id+"F2.wireOp",EDGE,"E952"),sQuery(id+"F2.wireOp",EDGE,"E953"),sQuery(id+"F2.wireOp",EDGE,"E954"),sQuery(id+"F2.wireOp",EDGE,"E955"),sQuery(id+"F2.wireOp",EDGE,"E956"),sQuery(id+"F2.wireOp",EDGE,"E957"),sQuery(id+"F2.wireOp",EDGE,"E958"),sQuery(id+"F2.wireOp",EDGE,"E959"),sQuery(id+"F2.wireOp",EDGE,"E960"),sQuery(id+"F2.wireOp",EDGE,"E961"),sQuery(id+"F2.wireOp",EDGE,"E962"),sQuery(id+"F2.wireOp",EDGE,"E963"),sQuery(id+"F2.wireOp",EDGE,"E964"),sQuery(id+"F2.wireOp",EDGE,"E965"),sQuery(id+"F2.wireOp",EDGE,"E966"),sQuery(id+"F2.wireOp",EDGE,"E967"),sQuery(id+"F2.wireOp",EDGE,"E968"),sQuery(id+"F2.wireOp",EDGE,"E969"),sQuery(id+"F2.wireOp",EDGE,"E970"),sQuery(id+"F2.wireOp",EDGE,"E971"),sQuery(id+"F2.wireOp",EDGE,"E972"),sQuery(id+"F2.wireOp",EDGE,"E973"),sQuery(id+"F2.wireOp",EDGE,"E974"),sQuery(id+"F2.wireOp",EDGE,"E975"),sQuery(id+"F2.wireOp",EDGE,"E976"),sQuery(id+"F2.wireOp",EDGE,"E977"),sQuery(id+"F2.wireOp",EDGE,"E978"),sQuery(id+"F2.wireOp",EDGE,"E979"),sQuery(id+"F2.wireOp",EDGE,"E980"),sQuery(id+"F2.wireOp",EDGE,"E981"),sQuery(id+"F2.wireOp",EDGE,"E982"),sQuery(id+"F2.wireOp",EDGE,"E983"),sQuery(id+"F2.wireOp",EDGE,"E984"),sQuery(id+"F2.wireOp",EDGE,"E985"),sQuery(id+"F2.wireOp",EDGE,"E986"),sQuery(id+"F2.wireOp",EDGE,"E987"),sQuery(id+"F2.wireOp",EDGE,"E988"),sQuery(id+"F2.wireOp",EDGE,"E989"),sQuery(id+"F2.wireOp",EDGE,"E990"),sQuery(id+"F2.wireOp",EDGE,"E991"),sQuery(id+"F2.wireOp",EDGE,"E992"),sQuery(id+"F2.wireOp",EDGE,"E993"),sQuery(id+"F2.wireOp",EDGE,"E994"),sQuery(id+"F2.wireOp",EDGE,"E995"),sQuery(id+"F2.wireOp",EDGE,"E996"),sQuery(id+"F2.wireOp",EDGE,"E997"),sQuery(id+"F2.wireOp",EDGE,"E998"),sQuery(id+"F2.wireOp",EDGE,"E999"),sQuery(id+"F2.wireOp",EDGE,"E1000"),sQuery(id+"F2.wireOp",EDGE,"E1001"),sQuery(id+"F2.wireOp",EDGE,"E1002"),sQuery(id+"F2.wireOp",EDGE,"E1003"),sQuery(id+"F2.wireOp",EDGE,"E1004"),sQuery(id+"F2.wireOp",EDGE,"E1005"),sQuery(id+"F2.wireOp",EDGE,"E1006"),sQuery(id+"F2.wireOp",EDGE,"E1007"),sQuery(id+"F2.wireOp",EDGE,"E1008"),sQuery(id+"F2.wireOp",EDGE,"E1009"),sQuery(id+"F2.wireOp",EDGE,"E1010"),sQuery(id+"F2.wireOp",EDGE,"E1011"),sQuery(id+"F2.wireOp",EDGE,"E1012"),sQuery(id+"F2.wireOp",EDGE,"E1013"),sQuery(id+"F2.wireOp",EDGE,"E1014"),sQuery(id+"F2.wireOp",EDGE,"E1015"),sQuery(id+"F2.wireOp",EDGE,"E1016"),sQuery(id+"F2.wireOp",EDGE,"E1017"),sQuery(id+"F2.wireOp",EDGE,"E1018"),sQuery(id+"F2.wireOp",EDGE,"E1019"),sQuery(id+"F2.wireOp",EDGE,"E1020"),sQuery(id+"F2.wireOp",EDGE,"E1021"),sQuery(id+"F2.wireOp",EDGE,"E1022"),sQuery(id+"F2.wireOp",EDGE,"E1023"),sQuery(id+"F2.wireOp",EDGE,"E1024"),sQuery(id+"F2.wireOp",EDGE,"E1025"),sQuery(id+"F2.wireOp",EDGE,"E1026"),sQuery(id+"F2.wireOp",EDGE,"E1027"),sQuery(id+"F2.wireOp",EDGE,"E1028"),sQuery(id+"F2.wireOp",EDGE,"E1029"),sQuery(id+"F2.wireOp",EDGE,"E1030"),sQuery(id+"F2.wireOp",EDGE,"E1031"),sQuery(id+"F2.wireOp",EDGE,"E1032"),sQuery(id+"F2.wireOp",EDGE,"E1033"),sQuery(id+"F2.wireOp",EDGE,"E1034"),sQuery(id+"F2.wireOp",EDGE,"E1035"),sQuery(id+"F2.wireOp",EDGE,"E1036"),sQuery(id+"F2.wireOp",EDGE,"E1037"),sQuery(id+"F2.wireOp",EDGE,"E1038"),sQuery(id+"F2.wireOp",EDGE,"E1039"),sQuery(id+"F2.wireOp",EDGE,"E1040"),sQuery(id+"F2.wireOp",EDGE,"E1041"),sQuery(id+"F2.wireOp",EDGE,"E1042"),sQuery(id+"F2.wireOp",EDGE,"E1043"),sQuery(id+"F2.wireOp",EDGE,"E1044"),sQuery(id+"F2.wireOp",EDGE,"E1045"),sQuery(id+"F2.wireOp",EDGE,"E1046"),sQuery(id+"F2.wireOp",EDGE,"E1047"),sQuery(id+"F2.wireOp",EDGE,"E1048"),sQuery(id+"F2.wireOp",EDGE,"E1049"),sQuery(id+"F2.wireOp",EDGE,"E1050"),sQuery(id+"F2.wireOp",EDGE,"E1051"),sQuery(id+"F2.wireOp",EDGE,"E1052"),sQuery(id+"F2.wireOp",EDGE,"E1053"),sQuery(id+"F2.wireOp",EDGE,"E1054"),sQuery(id+"F2.wireOp",EDGE,"E1055"),sQuery(id+"F2.wireOp",EDGE,"E1056"),sQuery(id+"F2.wireOp",EDGE,"E1057"),sQuery(id+"F2.wireOp",EDGE,"E1058"),sQuery(id+"F2.wireOp",EDGE,"E1059"),sQuery(id+"F2.wireOp",EDGE,"E1060"),sQuery(id+"F2.wireOp",EDGE,"E1061"),sQuery(id+"F2.wireOp",EDGE,"E1062"),sQuery(id+"F2.wireOp",EDGE,"E1063"),sQuery(id+"F2.wireOp",EDGE,"E1064"),sQuery(id+"F2.wireOp",EDGE,"E1065"),sQuery(id+"F2.wireOp",EDGE,"E1066"),sQuery(id+"F2.wireOp",EDGE,"E1067"),sQuery(id+"F2.wireOp",EDGE,"E1068"),sQuery(id+"F2.wireOp",EDGE,"E1069"),sQuery(id+"F2.wireOp",EDGE,"E1070"),sQuery(id+"F2.wireOp",EDGE,"E1071"),sQuery(id+"F2.wireOp",EDGE,"E1072"),sQuery(id+"F2.wireOp",EDGE,"E1073"),sQuery(id+"F2.wireOp",EDGE,"E1074"),sQuery(id+"F2.wireOp",EDGE,"E1075"),sQuery(id+"F2.wireOp",EDGE,"E1076"),sQuery(id+"F2.wireOp",EDGE,"E1077"),sQuery(id+"F2.wireOp",EDGE,"E1078"),sQuery(id+"F2.wireOp",EDGE,"E1079"),sQuery(id+"F2.wireOp",EDGE,"E1080"),sQuery(id+"F2.wireOp",EDGE,"E1081"),sQuery(id+"F2.wireOp",EDGE,"E1082"),sQuery(id+"F2.wireOp",EDGE,"E1083"),sQuery(id+"F2.wireOp",EDGE,"E1084"),sQuery(id+"F2.wireOp",EDGE,"E1085"),sQuery(id+"F2.wireOp",EDGE,"E1086"),sQuery(id+"F2.wireOp",EDGE,"E1087"),sQuery(id+"F2.wireOp",EDGE,"E1088"),sQuery(id+"F2.wireOp",EDGE,"E1089"),sQuery(id+"F2.wireOp",EDGE,"E1090"),sQuery(id+"F2.wireOp",EDGE,"E1091"),sQuery(id+"F2.wireOp",EDGE,"E1092"),sQuery(id+"F2.wireOp",EDGE,"E1093"),sQuery(id+"F2.wireOp",EDGE,"E1094"),sQuery(id+"F2.wireOp",EDGE,"E1095"),sQuery(id+"F2.wireOp",EDGE,"E1096"),sQuery(id+"F2.wireOp",EDGE,"E1097"),sQuery(id+"F2.wireOp",EDGE,"E1098"),sQuery(id+"F2.wireOp",EDGE,"E1099"),sQuery(id+"F2.wireOp",EDGE,"E1100"),sQuery(id+"F2.wireOp",EDGE,"E1101"),sQuery(id+"F2.wireOp",EDGE,"E1102"),sQuery(id+"F2.wireOp",EDGE,"E1103"),sQuery(id+"F2.wireOp",EDGE,"E1104"),sQuery(id+"F2.wireOp",EDGE,"E1105"),sQuery(id+"F2.wireOp",EDGE,"E1106"),sQuery(id+"F2.wireOp",EDGE,"E1107"),sQuery(id+"F2.wireOp",EDGE,"E1108"),sQuery(id+"F2.wireOp",EDGE,"E1109"),sQuery(id+"F2.wireOp",EDGE,"E1110"),sQuery(id+"F2.wireOp",EDGE,"E1111"),sQuery(id+"F2.wireOp",EDGE,"E1112"),sQuery(id+"F2.wireOp",EDGE,"E1113"),sQuery(id+"F2.wireOp",EDGE,"E1114"),sQuery(id+"F2.wireOp",EDGE,"E1115"),sQuery(id+"F2.wireOp",EDGE,"E1116"),sQuery(id+"F2.wireOp",EDGE,"E1117"),sQuery(id+"F2.wireOp",EDGE,"E1118"),sQuery(id+"F2.wireOp",EDGE,"E1119"),sQuery(id+"F2.wireOp",EDGE,"E1120"),sQuery(id+"F2.wireOp",EDGE,"E1121"),sQuery(id+"F2.wireOp",EDGE,"E1122"),sQuery(id+"F2.wireOp",EDGE,"E1123"),sQuery(id+"F2.wireOp",EDGE,"E1124"),sQuery(id+"F2.wireOp",EDGE,"E1125"),sQuery(id+"F2.wireOp",EDGE,"E1126"),sQuery(id+"F2.wireOp",EDGE,"E1127"),sQuery(id+"F2.wireOp",EDGE,"E1128"),sQuery(id+"F2.wireOp",EDGE,"E1129"),sQuery(id+"F2.wireOp",EDGE,"E1130"),sQuery(id+"F2.wireOp",EDGE,"E1131"),sQuery(id+"F2.wireOp",EDGE,"E1132"),sQuery(id+"F2.wireOp",EDGE,"E1133"),sQuery(id+"F2.wireOp",EDGE,"E1134"),sQuery(id+"F2.wireOp",EDGE,"E1135"),sQuery(id+"F2.wireOp",EDGE,"E1136"),sQuery(id+"F2.wireOp",EDGE,"E1137"),sQuery(id+"F2.wireOp",EDGE,"E1138"),sQuery(id+"F2.wireOp",EDGE,"E1139"),sQuery(id+"F2.wireOp",EDGE,"E1140"),sQuery(id+"F2.wireOp",EDGE,"E1141"),sQuery(id+"F2.wireOp",EDGE,"E1142"),sQuery(id+"F2.wireOp",EDGE,"E1143"),sQuery(id+"F2.wireOp",EDGE,"E1144"),sQuery(id+"F2.wireOp",EDGE,"E1145"),sQuery(id+"F2.wireOp",EDGE,"E1146"),sQuery(id+"F2.wireOp",EDGE,"E1147"),sQuery(id+"F2.wireOp",EDGE,"E1148"),sQuery(id+"F2.wireOp",EDGE,"E1149"),sQuery(id+"F2.wireOp",EDGE,"E1150"),sQuery(id+"F2.wireOp",EDGE,"E1151"),sQuery(id+"F2.wireOp",EDGE,"E1152"),sQuery(id+"F2.wireOp",EDGE,"E1153"),sQuery(id+"F2.wireOp",EDGE,"E1154"),sQuery(id+"F2.wireOp",EDGE,"E1155"),sQuery(id+"F2.wireOp",EDGE,"E1156"),sQuery(id+"F2.wireOp",EDGE,"E1157"),sQuery(id+"F2.wireOp",EDGE,"E1158"),sQuery(id+"F2.wireOp",EDGE,"E1159"),sQuery(id+"F2.wireOp",EDGE,"E1160"),sQuery(id+"F2.wireOp",EDGE,"E1161"),sQuery(id+"F2.wireOp",EDGE,"E1162"),sQuery(id+"F2.wireOp",EDGE,"E1163"),sQuery(id+"F2.wireOp",EDGE,"E1164"),sQuery(id+"F2.wireOp",EDGE,"E1165"),sQuery(id+"F2.wireOp",EDGE,"E1166"),sQuery(id+"F2.wireOp",EDGE,"E1167"),sQuery(id+"F2.wireOp",EDGE,"E1168"),sQuery(id+"F2.wireOp",EDGE,"E1169"),sQuery(id+"F2.wireOp",EDGE,"E1170"),sQuery(id+"F2.wireOp",EDGE,"E1171"),sQuery(id+"F2.wireOp",EDGE,"E1172"),sQuery(id+"F2.wireOp",EDGE,"E1173"),sQuery(id+"F2.wireOp",EDGE,"E1174"),sQuery(id+"F2.wireOp",EDGE,"E1175"),sQuery(id+"F2.wireOp",EDGE,"E1176"),sQuery(id+"F2.wireOp",EDGE,"E1177"),sQuery(id+"F2.wireOp",EDGE,"E1178"),sQuery(id+"F2.wireOp",EDGE,"E1179"),sQuery(id+"F2.wireOp",EDGE,"E1180"),sQuery(id+"F2.wireOp",EDGE,"E1181"),sQuery(id+"F2.wireOp",EDGE,"E1182"),sQuery(id+"F2.wireOp",EDGE,"E1183"),sQuery(id+"F2.wireOp",EDGE,"E1184"),sQuery(id+"F2.wireOp",EDGE,"E1185"),sQuery(id+"F2.wireOp",EDGE,"E1186"),sQuery(id+"F2.wireOp",EDGE,"E1187"),sQuery(id+"F2.wireOp",EDGE,"E1188"),sQuery(id+"F2.wireOp",EDGE,"E1189"),sQuery(id+"F2.wireOp",EDGE,"E1190"),sQuery(id+"F2.wireOp",EDGE,"E1191"),sQuery(id+"F2.wireOp",EDGE,"E1192"),sQuery(id+"F2.wireOp",EDGE,"E1193"),sQuery(id+"F2.wireOp",EDGE,"E1194"),sQuery(id+"F2.wireOp",EDGE,"E1195"),sQuery(id+"F2.wireOp",EDGE,"E1196"),sQuery(id+"F2.wireOp",EDGE,"E1197"),sQuery(id+"F2.wireOp",EDGE,"E1198"),sQuery(id+"F2.wireOp",EDGE,"E1199"),sQuery(id+"F2.wireOp",EDGE,"E1200"),sQuery(id+"F2.wireOp",EDGE,"E1201"),sQuery(id+"F2.wireOp",EDGE,"E1202"),sQuery(id+"F2.wireOp",EDGE,"E1203"),sQuery(id+"F2.wireOp",EDGE,"E1204"),sQuery(id+"F2.wireOp",EDGE,"E1205"),sQuery(id+"F2.wireOp",EDGE,"E1206"),sQuery(id+"F2.wireOp",EDGE,"E1207"),sQuery(id+"F2.wireOp",EDGE,"E1208"),sQuery(id+"F2.wireOp",EDGE,"E1209"),sQuery(id+"F2.wireOp",EDGE,"E1210"),sQuery(id+"F2.wireOp",EDGE,"E1211"),sQuery(id+"F2.wireOp",EDGE,"E1212"),sQuery(id+"F2.wireOp",EDGE,"E1213"),sQuery(id+"F2.wireOp",EDGE,"E1214"),sQuery(id+"F2.wireOp",EDGE,"E1215"),sQuery(id+"F2.wireOp",EDGE,"E1216"),sQuery(id+"F2.wireOp",EDGE,"E1217"),sQuery(id+"F2.wireOp",EDGE,"E1218"),sQuery(id+"F2.wireOp",EDGE,"E1219"),sQuery(id+"F2.wireOp",EDGE,"E1220"),sQuery(id+"F2.wireOp",EDGE,"E1221"),sQuery(id+"F2.wireOp",EDGE,"E1222"),sQuery(id+"F2.wireOp",EDGE,"E1223"),sQuery(id+"F2.wireOp",EDGE,"E1224"),sQuery(id+"F2.wireOp",EDGE,"E1225"),sQuery(id+"F2.wireOp",EDGE,"E1226"),sQuery(id+"F2.wireOp",EDGE,"E1227"),sQuery(id+"F2.wireOp",EDGE,"E1228"),sQuery(id+"F2.wireOp",EDGE,"E1229"),sQuery(id+"F2.wireOp",EDGE,"E1230"),sQuery(id+"F2.wireOp",EDGE,"E1231"),sQuery(id+"F2.wireOp",EDGE,"E1232"),sQuery(id+"F2.wireOp",EDGE,"E1233"),sQuery(id+"F2.wireOp",EDGE,"E1234"),sQuery(id+"F2.wireOp",EDGE,"E1235"),sQuery(id+"F2.wireOp",EDGE,"E1236"),sQuery(id+"F2.wireOp",EDGE,"E1237"),sQuery(id+"F2.wireOp",EDGE,"E1238"),sQuery(id+"F2.wireOp",EDGE,"E1239"),sQuery(id+"F2.wireOp",EDGE,"E1240"),sQuery(id+"F2.wireOp",EDGE,"E1241"),sQuery(id+"F2.wireOp",EDGE,"E1242"),sQuery(id+"F2.wireOp",EDGE,"E1243"),sQuery(id+"F2.wireOp",EDGE,"E1244"),sQuery(id+"F2.wireOp",EDGE,"E1245"),sQuery(id+"F2.wireOp",EDGE,"E1246"),sQuery(id+"F2.wireOp",EDGE,"E1247"),sQuery(id+"F2.wireOp",EDGE,"E1248"),sQuery(id+"F2.wireOp",EDGE,"E1249"),sQuery(id+"F2.wireOp",EDGE,"E1250"),sQuery(id+"F2.wireOp",EDGE,"E1251"),sQuery(id+"F2.wireOp",EDGE,"E1252"),sQuery(id+"F2.wireOp",EDGE,"E1253"),sQuery(id+"F2.wireOp",EDGE,"E1254"),sQuery(id+"F2.wireOp",EDGE,"E1255"),sQuery(id+"F2.wireOp",EDGE,"E1256"),sQuery(id+"F2.wireOp",EDGE,"E1257"),sQuery(id+"F2.wireOp",EDGE,"E1258"),sQuery(id+"F2.wireOp",EDGE,"E1259"),sQuery(id+"F2.wireOp",EDGE,"E1260"),sQuery(id+"F2.wireOp",EDGE,"E1261"),sQuery(id+"F2.wireOp",EDGE,"E1262"),sQuery(id+"F2.wireOp",EDGE,"E1263"),sQuery(id+"F2.wireOp",EDGE,"E1264"),sQuery(id+"F2.wireOp",EDGE,"E1265"),sQuery(id+"F2.wireOp",EDGE,"E1266"),sQuery(id+"F2.wireOp",EDGE,"E1267"),sQuery(id+"F2.wireOp",EDGE,"E1268"),sQuery(id+"F2.wireOp",EDGE,"E1269"),sQuery(id+"F2.wireOp",EDGE,"E1270"),sQuery(id+"F2.wireOp",EDGE,"E1271"),sQuery(id+"F2.wireOp",EDGE,"E1272"),sQuery(id+"F2.wireOp",EDGE,"E1273"),sQuery(id+"F2.wireOp",EDGE,"E1274"),sQuery(id+"F2.wireOp",EDGE,"E1275"),sQuery(id+"F2.wireOp",EDGE,"E1276"),sQuery(id+"F2.wireOp",EDGE,"E1277"),sQuery(id+"F2.wireOp",EDGE,"E1278"),sQuery(id+"F2.wireOp",EDGE,"E1279"),sQuery(id+"F2.wireOp",EDGE,"E1280"),sQuery(id+"F2.wireOp",EDGE,"E1281"),sQuery(id+"F2.wireOp",EDGE,"E1282"),sQuery(id+"F2.wireOp",EDGE,"E1283"),sQuery(id+"F2.wireOp",EDGE,"E1284"),sQuery(id+"F2.wireOp",EDGE,"E1285"),sQuery(id+"F2.wireOp",EDGE,"E1286"),sQuery(id+"F2.wireOp",EDGE,"E1287"),sQuery(id+"F2.wireOp",EDGE,"E1288"),sQuery(id+"F2.wireOp",EDGE,"E1289"),sQuery(id+"F2.wireOp",EDGE,"E1290"),sQuery(id+"F2.wireOp",EDGE,"E1291"),sQuery(id+"F2.wireOp",EDGE,"E1292"),sQuery(id+"F2.wireOp",EDGE,"E1293"),sQuery(id+"F2.wireOp",EDGE,"E1294"),sQuery(id+"F2.wireOp",EDGE,"E1295"),sQuery(id+"F2.wireOp",EDGE,"E1296"),sQuery(id+"F2.wireOp",EDGE,"E1297"),sQuery(id+"F2.wireOp",EDGE,"E1298"),sQuery(id+"F2.wireOp",EDGE,"E1299"),sQuery(id+"F2.wireOp",EDGE,"E1300"),sQuery(id+"F2.wireOp",EDGE,"E1301"),sQuery(id+"F2.wireOp",EDGE,"E1302"),sQuery(id+"F2.wireOp",EDGE,"E1303"),sQuery(id+"F2.wireOp",EDGE,"E1304"),sQuery(id+"F2.wireOp",EDGE,"E1305"),sQuery(id+"F2.wireOp",EDGE,"E1306"),sQuery(id+"F2.wireOp",EDGE,"E1307"),sQuery(id+"F2.wireOp",EDGE,"E1308"),sQuery(id+"F2.wireOp",EDGE,"E1309"),sQuery(id+"F2.wireOp",EDGE,"E1310"),sQuery(id+"F2.wireOp",EDGE,"E1311"),sQuery(id+"F2.wireOp",EDGE,"E1312"),sQuery(id+"F2.wireOp",EDGE,"E1313"),sQuery(id+"F2.wireOp",EDGE,"E1314"),sQuery(id+"F2.wireOp",EDGE,"E1315"),sQuery(id+"F2.wireOp",EDGE,"E1316"),sQuery(id+"F2.wireOp",EDGE,"E1317"),sQuery(id+"F2.wireOp",EDGE,"E1318"),sQuery(id+"F2.wireOp",EDGE,"E1319"),sQuery(id+"F2.wireOp",EDGE,"E1320"),sQuery(id+"F2.wireOp",EDGE,"E1321"),sQuery(id+"F2.wireOp",EDGE,"E1322"),sQuery(id+"F2.wireOp",EDGE,"E1323"),sQuery(id+"F2.wireOp",EDGE,"E1324"),sQuery(id+"F2.wireOp",EDGE,"E1325"),sQuery(id+"F2.wireOp",EDGE,"E1326"),sQuery(id+"F2.wireOp",EDGE,"E1327"),sQuery(id+"F2.wireOp",EDGE,"E1328"),sQuery(id+"F2.wireOp",EDGE,"E1329"),sQuery(id+"F2.wireOp",EDGE,"E1330"),sQuery(id+"F2.wireOp",EDGE,"E1331"),sQuery(id+"F2.wireOp",EDGE,"E1332"),sQuery(id+"F2.wireOp",EDGE,"E1333"),sQuery(id+"F2.wireOp",EDGE,"E1334"),sQuery(id+"F2.wireOp",EDGE,"E1335"),sQuery(id+"F2.wireOp",EDGE,"E1336"),sQuery(id+"F2.wireOp",EDGE,"E1337"),sQuery(id+"F2.wireOp",EDGE,"E1338"),sQuery(id+"F2.wireOp",EDGE,"E1339"),sQuery(id+"F2.wireOp",EDGE,"E1340"),sQuery(id+"F2.wireOp",EDGE,"E1341"),sQuery(id+"F2.wireOp",EDGE,"E1342"),sQuery(id+"F2.wireOp",EDGE,"E1343"),sQuery(id+"F2.wireOp",EDGE,"E1344"),sQuery(id+"F2.wireOp",EDGE,"E1345"),sQuery(id+"F2.wireOp",EDGE,"E1346"),sQuery(id+"F2.wireOp",EDGE,"E1347"),sQuery(id+"F2.wireOp",EDGE,"E1348"),sQuery(id+"F2.wireOp",EDGE,"E1349"),sQuery(id+"F2.wireOp",EDGE,"E1350"),sQuery(id+"F2.wireOp",EDGE,"E1351"),sQuery(id+"F2.wireOp",EDGE,"E1352"),sQuery(id+"F2.wireOp",EDGE,"E1353"),sQuery(id+"F2.wireOp",EDGE,"E1354"),sQuery(id+"F2.wireOp",EDGE,"E1355"),sQuery(id+"F2.wireOp",EDGE,"E1356"),sQuery(id+"F2.wireOp",EDGE,"E1357"),sQuery(id+"F2.wireOp",EDGE,"E1358"),sQuery(id+"F2.wireOp",EDGE,"E1359"),sQuery(id+"F2.wireOp",EDGE,"E1360"),sQuery(id+"F2.wireOp",EDGE,"E1361"),sQuery(id+"F2.wireOp",EDGE,"E1362"),sQuery(id+"F2.wireOp",EDGE,"E1363"),sQuery(id+"F2.wireOp",EDGE,"E1364"),sQuery(id+"F2.wireOp",EDGE,"E1365"),sQuery(id+"F2.wireOp",EDGE,"E1366"),sQuery(id+"F2.wireOp",EDGE,"E1367"),sQuery(id+"F2.wireOp",EDGE,"E1368"),sQuery(id+"F2.wireOp",EDGE,"E1369"),sQuery(id+"F2.wireOp",EDGE,"E1370"),sQuery(id+"F2.wireOp",EDGE,"E1371"),sQuery(id+"F2.wireOp",EDGE,"E1372"),sQuery(id+"F2.wireOp",EDGE,"E1373"),sQuery(id+"F2.wireOp",EDGE,"E1374"),sQuery(id+"F2.wireOp",EDGE,"E1375"),sQuery(id+"F2.wireOp",EDGE,"E1376"),sQuery(id+"F2.wireOp",EDGE,"E1377"),sQuery(id+"F2.wireOp",EDGE,"E1378"),sQuery(id+"F2.wireOp",EDGE,"E1379"),sQuery(id+"F2.wireOp",EDGE,"E1380"),sQuery(id+"F2.wireOp",EDGE,"E1381"),sQuery(id+"F2.wireOp",EDGE,"E1382"),sQuery(id+"F2.wireOp",EDGE,"E1383"),sQuery(id+"F2.wireOp",EDGE,"E1384"),sQuery(id+"F2.wireOp",EDGE,"E1385"),sQuery(id+"F2.wireOp",EDGE,"E1386"),sQuery(id+"F2.wireOp",EDGE,"E1387"),sQuery(id+"F2.wireOp",EDGE,"E1388"),sQuery(id+"F2.wireOp",EDGE,"E1389"),sQuery(id+"F2.wireOp",EDGE,"E1390"),sQuery(id+"F2.wireOp",EDGE,"E1391"),sQuery(id+"F2.wireOp",EDGE,"E1392"),sQuery(id+"F2.wireOp",EDGE,"E1393"),sQuery(id+"F2.wireOp",EDGE,"E1394"),sQuery(id+"F2.wireOp",EDGE,"E1395"),sQuery(id+"F2.wireOp",EDGE,"E1396"),sQuery(id+"F2.wireOp",EDGE,"E1397"),sQuery(id+"F2.wireOp",EDGE,"E1398"),sQuery(id+"F2.wireOp",EDGE,"E1399"),sQuery(id+"F2.wireOp",EDGE,"E1400"),sQuery(id+"F2.wireOp",EDGE,"E1401"),sQuery(id+"F2.wireOp",EDGE,"E1402"),sQuery(id+"F2.wireOp",EDGE,"E1403"),sQuery(id+"F2.wireOp",EDGE,"E1404"),sQuery(id+"F2.wireOp",EDGE,"E1405"),sQuery(id+"F2.wireOp",EDGE,"E1406"),sQuery(id+"F2.wireOp",EDGE,"E1407"),sQuery(id+"F2.wireOp",EDGE,"E1408"),sQuery(id+"F2.wireOp",EDGE,"E1409"),sQuery(id+"F2.wireOp",EDGE,"E1410"),sQuery(id+"F2.wireOp",EDGE,"E1411"),sQuery(id+"F2.wireOp",EDGE,"E1412"),sQuery(id+"F2.wireOp",EDGE,"E1413"),sQuery(id+"F2.wireOp",EDGE,"E1414"),sQuery(id+"F2.wireOp",EDGE,"E1415"),sQuery(id+"F2.wireOp",EDGE,"E1416"),sQuery(id+"F2.wireOp",EDGE,"E1417"),sQuery(id+"F2.wireOp",EDGE,"E1418"),sQuery(id+"F2.wireOp",EDGE,"E1419"),sQuery(id+"F2.wireOp",EDGE,"E1420"),sQuery(id+"F2.wireOp",EDGE,"E1421"),sQuery(id+"F2.wireOp",EDGE,"E1422"),sQuery(id+"F2.wireOp",EDGE,"E1423"),sQuery(id+"F2.wireOp",EDGE,"E1424"),sQuery(id+"F2.wireOp",EDGE,"E1425"),sQuery(id+"F2.wireOp",EDGE,"E1426"),sQuery(id+"F2.wireOp",EDGE,"E1427"),sQuery(id+"F2.wireOp",EDGE,"E1428"),sQuery(id+"F2.wireOp",EDGE,"E1429"),sQuery(id+"F2.wireOp",EDGE,"E1430"),sQuery(id+"F2.wireOp",EDGE,"E1431"),sQuery(id+"F2.wireOp",EDGE,"E1432"),sQuery(id+"F2.wireOp",EDGE,"E1433"),sQuery(id+"F2.wireOp",EDGE,"E1434"),sQuery(id+"F2.wireOp",EDGE,"E1435"),sQuery(id+"F2.wireOp",EDGE,"E1436"),sQuery(id+"F2.wireOp",EDGE,"E1437"),sQuery(id+"F2.wireOp",EDGE,"E1438"),sQuery(id+"F2.wireOp",EDGE,"E1439"),sQuery(id+"F2.wireOp",EDGE,"E1440"),sQuery(id+"F2.wireOp",EDGE,"E1441"),sQuery(id+"F2.wireOp",EDGE,"E1442"),sQuery(id+"F2.wireOp",EDGE,"E1443"),sQuery(id+"F2.wireOp",EDGE,"E1444"),sQuery(id+"F2.wireOp",EDGE,"E1445"),sQuery(id+"F2.wireOp",EDGE,"E1446"),sQuery(id+"F2.wireOp",EDGE,"E1447"),sQuery(id+"F2.wireOp",EDGE,"E1448"),sQuery(id+"F2.wireOp",EDGE,"E1449"),sQuery(id+"F2.wireOp",EDGE,"E1450"),sQuery(id+"F2.wireOp",EDGE,"E1451"),sQuery(id+"F2.wireOp",EDGE,"E1452"),sQuery(id+"F2.wireOp",EDGE,"E1453"),sQuery(id+"F2.wireOp",EDGE,"E1454"),sQuery(id+"F2.wireOp",EDGE,"E1455"),sQuery(id+"F2.wireOp",EDGE,"E1456"),sQuery(id+"F2.wireOp",EDGE,"E1457"),sQuery(id+"F2.wireOp",EDGE,"E1458"),sQuery(id+"F2.wireOp",EDGE,"E1459"),sQuery(id+"F2.wireOp",EDGE,"E1460"),sQuery(id+"F2.wireOp",EDGE,"E1461"),sQuery(id+"F2.wireOp",EDGE,"E1462"),sQuery(id+"F2.wireOp",EDGE,"E1463"),sQuery(id+"F2.wireOp",EDGE,"E1464"),sQuery(id+"F2.wireOp",EDGE,"E1465"),sQuery(id+"F2.wireOp",EDGE,"E1466"),sQuery(id+"F2.wireOp",EDGE,"E1467"),sQuery(id+"F2.wireOp",EDGE,"E1468"),sQuery(id+"F2.wireOp",EDGE,"E1469"),sQuery(id+"F2.wireOp",EDGE,"E1470"),sQuery(id+"F2.wireOp",EDGE,"E1471"),sQuery(id+"F2.wireOp",EDGE,"E1472"),sQuery(id+"F2.wireOp",EDGE,"E1473"),sQuery(id+"F2.wireOp",EDGE,"E1474")])]});
            var Q1;
            Q1=sQuery(id+"F1.wireOp",EDGE,"E15");
            transform(context, id + "F6", {"entities" : qUnion([Q0]), "transformType" : TransformType.ROTATION, "transformAxis" : qUnion([Q1]), "angle" : 30 * degree, "makeCopy" : true});
        }
        {
            var Q0;
            Q0=makeQuery(id+"F3.opExtrude","SWEPT_BODY",BODY,{"disambiguationData":[OSD([sQuery(id+"F2.wireOp",EDGE,"E16"),sQuery(id+"F2.wireOp",EDGE,"E17"),sQuery(id+"F2.wireOp",EDGE,"E18"),sQuery(id+"F2.wireOp",EDGE,"E19"),sQuery(id+"F2.wireOp",EDGE,"E20"),sQuery(id+"F2.wireOp",EDGE,"E21"),sQuery(id+"F2.wireOp",EDGE,"E22"),sQuery(id+"F2.wireOp",EDGE,"E23"),sQuery(id+"F2.wireOp",EDGE,"E24"),sQuery(id+"F2.wireOp",EDGE,"E25"),sQuery(id+"F2.wireOp",EDGE,"E26"),sQuery(id+"F2.wireOp",EDGE,"E27"),sQuery(id+"F2.wireOp",EDGE,"E28"),sQuery(id+"F2.wireOp",EDGE,"E29"),sQuery(id+"F2.wireOp",EDGE,"E30"),sQuery(id+"F2.wireOp",EDGE,"E31"),sQuery(id+"F2.wireOp",EDGE,"E32"),sQuery(id+"F2.wireOp",EDGE,"E33"),sQuery(id+"F2.wireOp",EDGE,"E34"),sQuery(id+"F2.wireOp",EDGE,"E35"),sQuery(id+"F2.wireOp",EDGE,"E36"),sQuery(id+"F2.wireOp",EDGE,"E37"),sQuery(id+"F2.wireOp",EDGE,"E38"),sQuery(id+"F2.wireOp",EDGE,"E39"),sQuery(id+"F2.wireOp",EDGE,"E40"),sQuery(id+"F2.wireOp",EDGE,"E41"),sQuery(id+"F2.wireOp",EDGE,"E42"),sQuery(id+"F2.wireOp",EDGE,"E43"),sQuery(id+"F2.wireOp",EDGE,"E44"),sQuery(id+"F2.wireOp",EDGE,"E45"),sQuery(id+"F2.wireOp",EDGE,"E46"),sQuery(id+"F2.wireOp",EDGE,"E47"),sQuery(id+"F2.wireOp",EDGE,"E48"),sQuery(id+"F2.wireOp",EDGE,"E49"),sQuery(id+"F2.wireOp",EDGE,"E50"),sQuery(id+"F2.wireOp",EDGE,"E51"),sQuery(id+"F2.wireOp",EDGE,"E52"),sQuery(id+"F2.wireOp",EDGE,"E53"),sQuery(id+"F2.wireOp",EDGE,"E54"),sQuery(id+"F2.wireOp",EDGE,"E55"),sQuery(id+"F2.wireOp",EDGE,"E56"),sQuery(id+"F2.wireOp",EDGE,"E57"),sQuery(id+"F2.wireOp",EDGE,"E58"),sQuery(id+"F2.wireOp",EDGE,"E59"),sQuery(id+"F2.wireOp",EDGE,"E60"),sQuery(id+"F2.wireOp",EDGE,"E61"),sQuery(id+"F2.wireOp",EDGE,"E62"),sQuery(id+"F2.wireOp",EDGE,"E63"),sQuery(id+"F2.wireOp",EDGE,"E64"),sQuery(id+"F2.wireOp",EDGE,"E65"),sQuery(id+"F2.wireOp",EDGE,"E66"),sQuery(id+"F2.wireOp",EDGE,"E67"),sQuery(id+"F2.wireOp",EDGE,"E68"),sQuery(id+"F2.wireOp",EDGE,"E69"),sQuery(id+"F2.wireOp",EDGE,"E70"),sQuery(id+"F2.wireOp",EDGE,"E71"),sQuery(id+"F2.wireOp",EDGE,"E72"),sQuery(id+"F2.wireOp",EDGE,"E73"),sQuery(id+"F2.wireOp",EDGE,"E74"),sQuery(id+"F2.wireOp",EDGE,"E75"),sQuery(id+"F2.wireOp",EDGE,"E76"),sQuery(id+"F2.wireOp",EDGE,"E77"),sQuery(id+"F2.wireOp",EDGE,"E78"),sQuery(id+"F2.wireOp",EDGE,"E79"),sQuery(id+"F2.wireOp",EDGE,"E80"),sQuery(id+"F2.wireOp",EDGE,"E81"),sQuery(id+"F2.wireOp",EDGE,"E82"),sQuery(id+"F2.wireOp",EDGE,"E83"),sQuery(id+"F2.wireOp",EDGE,"E84"),sQuery(id+"F2.wireOp",EDGE,"E85"),sQuery(id+"F2.wireOp",EDGE,"E86"),sQuery(id+"F2.wireOp",EDGE,"E87"),sQuery(id+"F2.wireOp",EDGE,"E88"),sQuery(id+"F2.wireOp",EDGE,"E89"),sQuery(id+"F2.wireOp",EDGE,"E90"),sQuery(id+"F2.wireOp",EDGE,"E91"),sQuery(id+"F2.wireOp",EDGE,"E92"),sQuery(id+"F2.wireOp",EDGE,"E93"),sQuery(id+"F2.wireOp",EDGE,"E94"),sQuery(id+"F2.wireOp",EDGE,"E95"),sQuery(id+"F2.wireOp",EDGE,"E96"),sQuery(id+"F2.wireOp",EDGE,"E97"),sQuery(id+"F2.wireOp",EDGE,"E98"),sQuery(id+"F2.wireOp",EDGE,"E99"),sQuery(id+"F2.wireOp",EDGE,"E100"),sQuery(id+"F2.wireOp",EDGE,"E101"),sQuery(id+"F2.wireOp",EDGE,"E102"),sQuery(id+"F2.wireOp",EDGE,"E103"),sQuery(id+"F2.wireOp",EDGE,"E104"),sQuery(id+"F2.wireOp",EDGE,"E105"),sQuery(id+"F2.wireOp",EDGE,"E106"),sQuery(id+"F2.wireOp",EDGE,"E107"),sQuery(id+"F2.wireOp",EDGE,"E108"),sQuery(id+"F2.wireOp",EDGE,"E109"),sQuery(id+"F2.wireOp",EDGE,"E110"),sQuery(id+"F2.wireOp",EDGE,"E111"),sQuery(id+"F2.wireOp",EDGE,"E112"),sQuery(id+"F2.wireOp",EDGE,"E113"),sQuery(id+"F2.wireOp",EDGE,"E114"),sQuery(id+"F2.wireOp",EDGE,"E115"),sQuery(id+"F2.wireOp",EDGE,"E116"),sQuery(id+"F2.wireOp",EDGE,"E117"),sQuery(id+"F2.wireOp",EDGE,"E118"),sQuery(id+"F2.wireOp",EDGE,"E119"),sQuery(id+"F2.wireOp",EDGE,"E120"),sQuery(id+"F2.wireOp",EDGE,"E121"),sQuery(id+"F2.wireOp",EDGE,"E122"),sQuery(id+"F2.wireOp",EDGE,"E123"),sQuery(id+"F2.wireOp",EDGE,"E124"),sQuery(id+"F2.wireOp",EDGE,"E125"),sQuery(id+"F2.wireOp",EDGE,"E126"),sQuery(id+"F2.wireOp",EDGE,"E127"),sQuery(id+"F2.wireOp",EDGE,"E128"),sQuery(id+"F2.wireOp",EDGE,"E129"),sQuery(id+"F2.wireOp",EDGE,"E130"),sQuery(id+"F2.wireOp",EDGE,"E131"),sQuery(id+"F2.wireOp",EDGE,"E132"),sQuery(id+"F2.wireOp",EDGE,"E133"),sQuery(id+"F2.wireOp",EDGE,"E134"),sQuery(id+"F2.wireOp",EDGE,"E135"),sQuery(id+"F2.wireOp",EDGE,"E136"),sQuery(id+"F2.wireOp",EDGE,"E137"),sQuery(id+"F2.wireOp",EDGE,"E138"),sQuery(id+"F2.wireOp",EDGE,"E139"),sQuery(id+"F2.wireOp",EDGE,"E140"),sQuery(id+"F2.wireOp",EDGE,"E141"),sQuery(id+"F2.wireOp",EDGE,"E142"),sQuery(id+"F2.wireOp",EDGE,"E143"),sQuery(id+"F2.wireOp",EDGE,"E144"),sQuery(id+"F2.wireOp",EDGE,"E145"),sQuery(id+"F2.wireOp",EDGE,"E146"),sQuery(id+"F2.wireOp",EDGE,"E147"),sQuery(id+"F2.wireOp",EDGE,"E148"),sQuery(id+"F2.wireOp",EDGE,"E149"),sQuery(id+"F2.wireOp",EDGE,"E150"),sQuery(id+"F2.wireOp",EDGE,"E151"),sQuery(id+"F2.wireOp",EDGE,"E152"),sQuery(id+"F2.wireOp",EDGE,"E153"),sQuery(id+"F2.wireOp",EDGE,"E154"),sQuery(id+"F2.wireOp",EDGE,"E155"),sQuery(id+"F2.wireOp",EDGE,"E156"),sQuery(id+"F2.wireOp",EDGE,"E157"),sQuery(id+"F2.wireOp",EDGE,"E158"),sQuery(id+"F2.wireOp",EDGE,"E159"),sQuery(id+"F2.wireOp",EDGE,"E160"),sQuery(id+"F2.wireOp",EDGE,"E161"),sQuery(id+"F2.wireOp",EDGE,"E162"),sQuery(id+"F2.wireOp",EDGE,"E163"),sQuery(id+"F2.wireOp",EDGE,"E164"),sQuery(id+"F2.wireOp",EDGE,"E165"),sQuery(id+"F2.wireOp",EDGE,"E166"),sQuery(id+"F2.wireOp",EDGE,"E167"),sQuery(id+"F2.wireOp",EDGE,"E168"),sQuery(id+"F2.wireOp",EDGE,"E169"),sQuery(id+"F2.wireOp",EDGE,"E170"),sQuery(id+"F2.wireOp",EDGE,"E171"),sQuery(id+"F2.wireOp",EDGE,"E172"),sQuery(id+"F2.wireOp",EDGE,"E173"),sQuery(id+"F2.wireOp",EDGE,"E174"),sQuery(id+"F2.wireOp",EDGE,"E175"),sQuery(id+"F2.wireOp",EDGE,"E176"),sQuery(id+"F2.wireOp",EDGE,"E177"),sQuery(id+"F2.wireOp",EDGE,"E178"),sQuery(id+"F2.wireOp",EDGE,"E179"),sQuery(id+"F2.wireOp",EDGE,"E180"),sQuery(id+"F2.wireOp",EDGE,"E181"),sQuery(id+"F2.wireOp",EDGE,"E182"),sQuery(id+"F2.wireOp",EDGE,"E183"),sQuery(id+"F2.wireOp",EDGE,"E184"),sQuery(id+"F2.wireOp",EDGE,"E185"),sQuery(id+"F2.wireOp",EDGE,"E186"),sQuery(id+"F2.wireOp",EDGE,"E187"),sQuery(id+"F2.wireOp",EDGE,"E188"),sQuery(id+"F2.wireOp",EDGE,"E189"),sQuery(id+"F2.wireOp",EDGE,"E190"),sQuery(id+"F2.wireOp",EDGE,"E191"),sQuery(id+"F2.wireOp",EDGE,"E192"),sQuery(id+"F2.wireOp",EDGE,"E193"),sQuery(id+"F2.wireOp",EDGE,"E194"),sQuery(id+"F2.wireOp",EDGE,"E195"),sQuery(id+"F2.wireOp",EDGE,"E196"),sQuery(id+"F2.wireOp",EDGE,"E197"),sQuery(id+"F2.wireOp",EDGE,"E198"),sQuery(id+"F2.wireOp",EDGE,"E199"),sQuery(id+"F2.wireOp",EDGE,"E200"),sQuery(id+"F2.wireOp",EDGE,"E201"),sQuery(id+"F2.wireOp",EDGE,"E202"),sQuery(id+"F2.wireOp",EDGE,"E203"),sQuery(id+"F2.wireOp",EDGE,"E204"),sQuery(id+"F2.wireOp",EDGE,"E205"),sQuery(id+"F2.wireOp",EDGE,"E206"),sQuery(id+"F2.wireOp",EDGE,"E207"),sQuery(id+"F2.wireOp",EDGE,"E208"),sQuery(id+"F2.wireOp",EDGE,"E209"),sQuery(id+"F2.wireOp",EDGE,"E210"),sQuery(id+"F2.wireOp",EDGE,"E211"),sQuery(id+"F2.wireOp",EDGE,"E212"),sQuery(id+"F2.wireOp",EDGE,"E213"),sQuery(id+"F2.wireOp",EDGE,"E214"),sQuery(id+"F2.wireOp",EDGE,"E215"),sQuery(id+"F2.wireOp",EDGE,"E216"),sQuery(id+"F2.wireOp",EDGE,"E217"),sQuery(id+"F2.wireOp",EDGE,"E218"),sQuery(id+"F2.wireOp",EDGE,"E219"),sQuery(id+"F2.wireOp",EDGE,"E220"),sQuery(id+"F2.wireOp",EDGE,"E221"),sQuery(id+"F2.wireOp",EDGE,"E222"),sQuery(id+"F2.wireOp",EDGE,"E223"),sQuery(id+"F2.wireOp",EDGE,"E224"),sQuery(id+"F2.wireOp",EDGE,"E225"),sQuery(id+"F2.wireOp",EDGE,"E226"),sQuery(id+"F2.wireOp",EDGE,"E227"),sQuery(id+"F2.wireOp",EDGE,"E228"),sQuery(id+"F2.wireOp",EDGE,"E229"),sQuery(id+"F2.wireOp",EDGE,"E230"),sQuery(id+"F2.wireOp",EDGE,"E231"),sQuery(id+"F2.wireOp",EDGE,"E232"),sQuery(id+"F2.wireOp",EDGE,"E233"),sQuery(id+"F2.wireOp",EDGE,"E234"),sQuery(id+"F2.wireOp",EDGE,"E235"),sQuery(id+"F2.wireOp",EDGE,"E236"),sQuery(id+"F2.wireOp",EDGE,"E237"),sQuery(id+"F2.wireOp",EDGE,"E238"),sQuery(id+"F2.wireOp",EDGE,"E239"),sQuery(id+"F2.wireOp",EDGE,"E240"),sQuery(id+"F2.wireOp",EDGE,"E241"),sQuery(id+"F2.wireOp",EDGE,"E242"),sQuery(id+"F2.wireOp",EDGE,"E243"),sQuery(id+"F2.wireOp",EDGE,"E244"),sQuery(id+"F2.wireOp",EDGE,"E245"),sQuery(id+"F2.wireOp",EDGE,"E246"),sQuery(id+"F2.wireOp",EDGE,"E247"),sQuery(id+"F2.wireOp",EDGE,"E248"),sQuery(id+"F2.wireOp",EDGE,"E249"),sQuery(id+"F2.wireOp",EDGE,"E250"),sQuery(id+"F2.wireOp",EDGE,"E251"),sQuery(id+"F2.wireOp",EDGE,"E252"),sQuery(id+"F2.wireOp",EDGE,"E253"),sQuery(id+"F2.wireOp",EDGE,"E254"),sQuery(id+"F2.wireOp",EDGE,"E255"),sQuery(id+"F2.wireOp",EDGE,"E256"),sQuery(id+"F2.wireOp",EDGE,"E257"),sQuery(id+"F2.wireOp",EDGE,"E258"),sQuery(id+"F2.wireOp",EDGE,"E259"),sQuery(id+"F2.wireOp",EDGE,"E260"),sQuery(id+"F2.wireOp",EDGE,"E261"),sQuery(id+"F2.wireOp",EDGE,"E262"),sQuery(id+"F2.wireOp",EDGE,"E263"),sQuery(id+"F2.wireOp",EDGE,"E264"),sQuery(id+"F2.wireOp",EDGE,"E265"),sQuery(id+"F2.wireOp",EDGE,"E266"),sQuery(id+"F2.wireOp",EDGE,"E267"),sQuery(id+"F2.wireOp",EDGE,"E268"),sQuery(id+"F2.wireOp",EDGE,"E269"),sQuery(id+"F2.wireOp",EDGE,"E270"),sQuery(id+"F2.wireOp",EDGE,"E271"),sQuery(id+"F2.wireOp",EDGE,"E272"),sQuery(id+"F2.wireOp",EDGE,"E273"),sQuery(id+"F2.wireOp",EDGE,"E274"),sQuery(id+"F2.wireOp",EDGE,"E275"),sQuery(id+"F2.wireOp",EDGE,"E276"),sQuery(id+"F2.wireOp",EDGE,"E277"),sQuery(id+"F2.wireOp",EDGE,"E278"),sQuery(id+"F2.wireOp",EDGE,"E279"),sQuery(id+"F2.wireOp",EDGE,"E280"),sQuery(id+"F2.wireOp",EDGE,"E281"),sQuery(id+"F2.wireOp",EDGE,"E282"),sQuery(id+"F2.wireOp",EDGE,"E283"),sQuery(id+"F2.wireOp",EDGE,"E284"),sQuery(id+"F2.wireOp",EDGE,"E285"),sQuery(id+"F2.wireOp",EDGE,"E286"),sQuery(id+"F2.wireOp",EDGE,"E287"),sQuery(id+"F2.wireOp",EDGE,"E288"),sQuery(id+"F2.wireOp",EDGE,"E289"),sQuery(id+"F2.wireOp",EDGE,"E290"),sQuery(id+"F2.wireOp",EDGE,"E291"),sQuery(id+"F2.wireOp",EDGE,"E292"),sQuery(id+"F2.wireOp",EDGE,"E293"),sQuery(id+"F2.wireOp",EDGE,"E294"),sQuery(id+"F2.wireOp",EDGE,"E295"),sQuery(id+"F2.wireOp",EDGE,"E296"),sQuery(id+"F2.wireOp",EDGE,"E297"),sQuery(id+"F2.wireOp",EDGE,"E298"),sQuery(id+"F2.wireOp",EDGE,"E299"),sQuery(id+"F2.wireOp",EDGE,"E300"),sQuery(id+"F2.wireOp",EDGE,"E301"),sQuery(id+"F2.wireOp",EDGE,"E302"),sQuery(id+"F2.wireOp",EDGE,"E303"),sQuery(id+"F2.wireOp",EDGE,"E304"),sQuery(id+"F2.wireOp",EDGE,"E305"),sQuery(id+"F2.wireOp",EDGE,"E306"),sQuery(id+"F2.wireOp",EDGE,"E307"),sQuery(id+"F2.wireOp",EDGE,"E308"),sQuery(id+"F2.wireOp",EDGE,"E309"),sQuery(id+"F2.wireOp",EDGE,"E310"),sQuery(id+"F2.wireOp",EDGE,"E311"),sQuery(id+"F2.wireOp",EDGE,"E312"),sQuery(id+"F2.wireOp",EDGE,"E313"),sQuery(id+"F2.wireOp",EDGE,"E314"),sQuery(id+"F2.wireOp",EDGE,"E315"),sQuery(id+"F2.wireOp",EDGE,"E316"),sQuery(id+"F2.wireOp",EDGE,"E317"),sQuery(id+"F2.wireOp",EDGE,"E318"),sQuery(id+"F2.wireOp",EDGE,"E319"),sQuery(id+"F2.wireOp",EDGE,"E320"),sQuery(id+"F2.wireOp",EDGE,"E321"),sQuery(id+"F2.wireOp",EDGE,"E322"),sQuery(id+"F2.wireOp",EDGE,"E323"),sQuery(id+"F2.wireOp",EDGE,"E324"),sQuery(id+"F2.wireOp",EDGE,"E325"),sQuery(id+"F2.wireOp",EDGE,"E326"),sQuery(id+"F2.wireOp",EDGE,"E327"),sQuery(id+"F2.wireOp",EDGE,"E328"),sQuery(id+"F2.wireOp",EDGE,"E329"),sQuery(id+"F2.wireOp",EDGE,"E330"),sQuery(id+"F2.wireOp",EDGE,"E331"),sQuery(id+"F2.wireOp",EDGE,"E332"),sQuery(id+"F2.wireOp",EDGE,"E333"),sQuery(id+"F2.wireOp",EDGE,"E334"),sQuery(id+"F2.wireOp",EDGE,"E335"),sQuery(id+"F2.wireOp",EDGE,"E336"),sQuery(id+"F2.wireOp",EDGE,"E337"),sQuery(id+"F2.wireOp",EDGE,"E338"),sQuery(id+"F2.wireOp",EDGE,"E339"),sQuery(id+"F2.wireOp",EDGE,"E340"),sQuery(id+"F2.wireOp",EDGE,"E341"),sQuery(id+"F2.wireOp",EDGE,"E342"),sQuery(id+"F2.wireOp",EDGE,"E343"),sQuery(id+"F2.wireOp",EDGE,"E344"),sQuery(id+"F2.wireOp",EDGE,"E345"),sQuery(id+"F2.wireOp",EDGE,"E346"),sQuery(id+"F2.wireOp",EDGE,"E347"),sQuery(id+"F2.wireOp",EDGE,"E348"),sQuery(id+"F2.wireOp",EDGE,"E349"),sQuery(id+"F2.wireOp",EDGE,"E350"),sQuery(id+"F2.wireOp",EDGE,"E351"),sQuery(id+"F2.wireOp",EDGE,"E352"),sQuery(id+"F2.wireOp",EDGE,"E353"),sQuery(id+"F2.wireOp",EDGE,"E354"),sQuery(id+"F2.wireOp",EDGE,"E355"),sQuery(id+"F2.wireOp",EDGE,"E356"),sQuery(id+"F2.wireOp",EDGE,"E357"),sQuery(id+"F2.wireOp",EDGE,"E358"),sQuery(id+"F2.wireOp",EDGE,"E359"),sQuery(id+"F2.wireOp",EDGE,"E360"),sQuery(id+"F2.wireOp",EDGE,"E361"),sQuery(id+"F2.wireOp",EDGE,"E362"),sQuery(id+"F2.wireOp",EDGE,"E363"),sQuery(id+"F2.wireOp",EDGE,"E364"),sQuery(id+"F2.wireOp",EDGE,"E365"),sQuery(id+"F2.wireOp",EDGE,"E366"),sQuery(id+"F2.wireOp",EDGE,"E367"),sQuery(id+"F2.wireOp",EDGE,"E368"),sQuery(id+"F2.wireOp",EDGE,"E369"),sQuery(id+"F2.wireOp",EDGE,"E370"),sQuery(id+"F2.wireOp",EDGE,"E371"),sQuery(id+"F2.wireOp",EDGE,"E372"),sQuery(id+"F2.wireOp",EDGE,"E373"),sQuery(id+"F2.wireOp",EDGE,"E374"),sQuery(id+"F2.wireOp",EDGE,"E375"),sQuery(id+"F2.wireOp",EDGE,"E376"),sQuery(id+"F2.wireOp",EDGE,"E377"),sQuery(id+"F2.wireOp",EDGE,"E378"),sQuery(id+"F2.wireOp",EDGE,"E379"),sQuery(id+"F2.wireOp",EDGE,"E380"),sQuery(id+"F2.wireOp",EDGE,"E381"),sQuery(id+"F2.wireOp",EDGE,"E382"),sQuery(id+"F2.wireOp",EDGE,"E383"),sQuery(id+"F2.wireOp",EDGE,"E384"),sQuery(id+"F2.wireOp",EDGE,"E385"),sQuery(id+"F2.wireOp",EDGE,"E386"),sQuery(id+"F2.wireOp",EDGE,"E387"),sQuery(id+"F2.wireOp",EDGE,"E388"),sQuery(id+"F2.wireOp",EDGE,"E389"),sQuery(id+"F2.wireOp",EDGE,"E390"),sQuery(id+"F2.wireOp",EDGE,"E391"),sQuery(id+"F2.wireOp",EDGE,"E392"),sQuery(id+"F2.wireOp",EDGE,"E393"),sQuery(id+"F2.wireOp",EDGE,"E394"),sQuery(id+"F2.wireOp",EDGE,"E395"),sQuery(id+"F2.wireOp",EDGE,"E396"),sQuery(id+"F2.wireOp",EDGE,"E397"),sQuery(id+"F2.wireOp",EDGE,"E398"),sQuery(id+"F2.wireOp",EDGE,"E399"),sQuery(id+"F2.wireOp",EDGE,"E400"),sQuery(id+"F2.wireOp",EDGE,"E401"),sQuery(id+"F2.wireOp",EDGE,"E402"),sQuery(id+"F2.wireOp",EDGE,"E403"),sQuery(id+"F2.wireOp",EDGE,"E404"),sQuery(id+"F2.wireOp",EDGE,"E405"),sQuery(id+"F2.wireOp",EDGE,"E406"),sQuery(id+"F2.wireOp",EDGE,"E407"),sQuery(id+"F2.wireOp",EDGE,"E408"),sQuery(id+"F2.wireOp",EDGE,"E409"),sQuery(id+"F2.wireOp",EDGE,"E410"),sQuery(id+"F2.wireOp",EDGE,"E411"),sQuery(id+"F2.wireOp",EDGE,"E412"),sQuery(id+"F2.wireOp",EDGE,"E413"),sQuery(id+"F2.wireOp",EDGE,"E414"),sQuery(id+"F2.wireOp",EDGE,"E415"),sQuery(id+"F2.wireOp",EDGE,"E416"),sQuery(id+"F2.wireOp",EDGE,"E417"),sQuery(id+"F2.wireOp",EDGE,"E418"),sQuery(id+"F2.wireOp",EDGE,"E419"),sQuery(id+"F2.wireOp",EDGE,"E420"),sQuery(id+"F2.wireOp",EDGE,"E421"),sQuery(id+"F2.wireOp",EDGE,"E422"),sQuery(id+"F2.wireOp",EDGE,"E423"),sQuery(id+"F2.wireOp",EDGE,"E424"),sQuery(id+"F2.wireOp",EDGE,"E425"),sQuery(id+"F2.wireOp",EDGE,"E426"),sQuery(id+"F2.wireOp",EDGE,"E427"),sQuery(id+"F2.wireOp",EDGE,"E428"),sQuery(id+"F2.wireOp",EDGE,"E429"),sQuery(id+"F2.wireOp",EDGE,"E430"),sQuery(id+"F2.wireOp",EDGE,"E431"),sQuery(id+"F2.wireOp",EDGE,"E432"),sQuery(id+"F2.wireOp",EDGE,"E433"),sQuery(id+"F2.wireOp",EDGE,"E434"),sQuery(id+"F2.wireOp",EDGE,"E435"),sQuery(id+"F2.wireOp",EDGE,"E436"),sQuery(id+"F2.wireOp",EDGE,"E437"),sQuery(id+"F2.wireOp",EDGE,"E438"),sQuery(id+"F2.wireOp",EDGE,"E439"),sQuery(id+"F2.wireOp",EDGE,"E440"),sQuery(id+"F2.wireOp",EDGE,"E441"),sQuery(id+"F2.wireOp",EDGE,"E442"),sQuery(id+"F2.wireOp",EDGE,"E443"),sQuery(id+"F2.wireOp",EDGE,"E444"),sQuery(id+"F2.wireOp",EDGE,"E445"),sQuery(id+"F2.wireOp",EDGE,"E446"),sQuery(id+"F2.wireOp",EDGE,"E447"),sQuery(id+"F2.wireOp",EDGE,"E447"),sQuery(id+"F2.wireOp",EDGE,"E447"),sQuery(id+"F2.wireOp",EDGE,"E448"),sQuery(id+"F2.wireOp",EDGE,"E449"),sQuery(id+"F2.wireOp",EDGE,"E450"),sQuery(id+"F2.wireOp",EDGE,"E451"),sQuery(id+"F2.wireOp",EDGE,"E452"),sQuery(id+"F2.wireOp",EDGE,"E453"),sQuery(id+"F2.wireOp",EDGE,"E454"),sQuery(id+"F2.wireOp",EDGE,"E455"),sQuery(id+"F2.wireOp",EDGE,"E456"),sQuery(id+"F2.wireOp",EDGE,"E457"),sQuery(id+"F2.wireOp",EDGE,"E458"),sQuery(id+"F2.wireOp",EDGE,"E459"),sQuery(id+"F2.wireOp",EDGE,"E460"),sQuery(id+"F2.wireOp",EDGE,"E461"),sQuery(id+"F2.wireOp",EDGE,"E462"),sQuery(id+"F2.wireOp",EDGE,"E463"),sQuery(id+"F2.wireOp",EDGE,"E464"),sQuery(id+"F2.wireOp",EDGE,"E465"),sQuery(id+"F2.wireOp",EDGE,"E466"),sQuery(id+"F2.wireOp",EDGE,"E467"),sQuery(id+"F2.wireOp",EDGE,"E468"),sQuery(id+"F2.wireOp",EDGE,"E469"),sQuery(id+"F2.wireOp",EDGE,"E470"),sQuery(id+"F2.wireOp",EDGE,"E471"),sQuery(id+"F2.wireOp",EDGE,"E472"),sQuery(id+"F2.wireOp",EDGE,"E473"),sQuery(id+"F2.wireOp",EDGE,"E474"),sQuery(id+"F2.wireOp",EDGE,"E475"),sQuery(id+"F2.wireOp",EDGE,"E476"),sQuery(id+"F2.wireOp",EDGE,"E477"),sQuery(id+"F2.wireOp",EDGE,"E478"),sQuery(id+"F2.wireOp",EDGE,"E479"),sQuery(id+"F2.wireOp",EDGE,"E480"),sQuery(id+"F2.wireOp",EDGE,"E481"),sQuery(id+"F2.wireOp",EDGE,"E482"),sQuery(id+"F2.wireOp",EDGE,"E483"),sQuery(id+"F2.wireOp",EDGE,"E484"),sQuery(id+"F2.wireOp",EDGE,"E485"),sQuery(id+"F2.wireOp",EDGE,"E486"),sQuery(id+"F2.wireOp",EDGE,"E487"),sQuery(id+"F2.wireOp",EDGE,"E488"),sQuery(id+"F2.wireOp",EDGE,"E489"),sQuery(id+"F2.wireOp",EDGE,"E490"),sQuery(id+"F2.wireOp",EDGE,"E491"),sQuery(id+"F2.wireOp",EDGE,"E492"),sQuery(id+"F2.wireOp",EDGE,"E493"),sQuery(id+"F2.wireOp",EDGE,"E494"),sQuery(id+"F2.wireOp",EDGE,"E495"),sQuery(id+"F2.wireOp",EDGE,"E496"),sQuery(id+"F2.wireOp",EDGE,"E497"),sQuery(id+"F2.wireOp",EDGE,"E498"),sQuery(id+"F2.wireOp",EDGE,"E499"),sQuery(id+"F2.wireOp",EDGE,"E500"),sQuery(id+"F2.wireOp",EDGE,"E501"),sQuery(id+"F2.wireOp",EDGE,"E502"),sQuery(id+"F2.wireOp",EDGE,"E503"),sQuery(id+"F2.wireOp",EDGE,"E504"),sQuery(id+"F2.wireOp",EDGE,"E505"),sQuery(id+"F2.wireOp",EDGE,"E506"),sQuery(id+"F2.wireOp",EDGE,"E507"),sQuery(id+"F2.wireOp",EDGE,"E508"),sQuery(id+"F2.wireOp",EDGE,"E509"),sQuery(id+"F2.wireOp",EDGE,"E510"),sQuery(id+"F2.wireOp",EDGE,"E511"),sQuery(id+"F2.wireOp",EDGE,"E512"),sQuery(id+"F2.wireOp",EDGE,"E513"),sQuery(id+"F2.wireOp",EDGE,"E514"),sQuery(id+"F2.wireOp",EDGE,"E515"),sQuery(id+"F2.wireOp",EDGE,"E516"),sQuery(id+"F2.wireOp",EDGE,"E517"),sQuery(id+"F2.wireOp",EDGE,"E518"),sQuery(id+"F2.wireOp",EDGE,"E519"),sQuery(id+"F2.wireOp",EDGE,"E520"),sQuery(id+"F2.wireOp",EDGE,"E521"),sQuery(id+"F2.wireOp",EDGE,"E522"),sQuery(id+"F2.wireOp",EDGE,"E523"),sQuery(id+"F2.wireOp",EDGE,"E524"),sQuery(id+"F2.wireOp",EDGE,"E525"),sQuery(id+"F2.wireOp",EDGE,"E526"),sQuery(id+"F2.wireOp",EDGE,"E527"),sQuery(id+"F2.wireOp",EDGE,"E528"),sQuery(id+"F2.wireOp",EDGE,"E529"),sQuery(id+"F2.wireOp",EDGE,"E530"),sQuery(id+"F2.wireOp",EDGE,"E531"),sQuery(id+"F2.wireOp",EDGE,"E532"),sQuery(id+"F2.wireOp",EDGE,"E533"),sQuery(id+"F2.wireOp",EDGE,"E534"),sQuery(id+"F2.wireOp",EDGE,"E535"),sQuery(id+"F2.wireOp",EDGE,"E536"),sQuery(id+"F2.wireOp",EDGE,"E537"),sQuery(id+"F2.wireOp",EDGE,"E538"),sQuery(id+"F2.wireOp",EDGE,"E539"),sQuery(id+"F2.wireOp",EDGE,"E540"),sQuery(id+"F2.wireOp",EDGE,"E541"),sQuery(id+"F2.wireOp",EDGE,"E542"),sQuery(id+"F2.wireOp",EDGE,"E543"),sQuery(id+"F2.wireOp",EDGE,"E544"),sQuery(id+"F2.wireOp",EDGE,"E545"),sQuery(id+"F2.wireOp",EDGE,"E546"),sQuery(id+"F2.wireOp",EDGE,"E547"),sQuery(id+"F2.wireOp",EDGE,"E547"),sQuery(id+"F2.wireOp",EDGE,"E548"),sQuery(id+"F2.wireOp",EDGE,"E549"),sQuery(id+"F2.wireOp",EDGE,"E550"),sQuery(id+"F2.wireOp",EDGE,"E551"),sQuery(id+"F2.wireOp",EDGE,"E552"),sQuery(id+"F2.wireOp",EDGE,"E553"),sQuery(id+"F2.wireOp",EDGE,"E554"),sQuery(id+"F2.wireOp",EDGE,"E555"),sQuery(id+"F2.wireOp",EDGE,"E556"),sQuery(id+"F2.wireOp",EDGE,"E557"),sQuery(id+"F2.wireOp",EDGE,"E558"),sQuery(id+"F2.wireOp",EDGE,"E559"),sQuery(id+"F2.wireOp",EDGE,"E560"),sQuery(id+"F2.wireOp",EDGE,"E561"),sQuery(id+"F2.wireOp",EDGE,"E562"),sQuery(id+"F2.wireOp",EDGE,"E563"),sQuery(id+"F2.wireOp",EDGE,"E564"),sQuery(id+"F2.wireOp",EDGE,"E565"),sQuery(id+"F2.wireOp",EDGE,"E566"),sQuery(id+"F2.wireOp",EDGE,"E567"),sQuery(id+"F2.wireOp",EDGE,"E568"),sQuery(id+"F2.wireOp",EDGE,"E569"),sQuery(id+"F2.wireOp",EDGE,"E570"),sQuery(id+"F2.wireOp",EDGE,"E571"),sQuery(id+"F2.wireOp",EDGE,"E572"),sQuery(id+"F2.wireOp",EDGE,"E573"),sQuery(id+"F2.wireOp",EDGE,"E574"),sQuery(id+"F2.wireOp",EDGE,"E575"),sQuery(id+"F2.wireOp",EDGE,"E576"),sQuery(id+"F2.wireOp",EDGE,"E577"),sQuery(id+"F2.wireOp",EDGE,"E578"),sQuery(id+"F2.wireOp",EDGE,"E579"),sQuery(id+"F2.wireOp",EDGE,"E580"),sQuery(id+"F2.wireOp",EDGE,"E581"),sQuery(id+"F2.wireOp",EDGE,"E582"),sQuery(id+"F2.wireOp",EDGE,"E583"),sQuery(id+"F2.wireOp",EDGE,"E584"),sQuery(id+"F2.wireOp",EDGE,"E585"),sQuery(id+"F2.wireOp",EDGE,"E586"),sQuery(id+"F2.wireOp",EDGE,"E587"),sQuery(id+"F2.wireOp",EDGE,"E588"),sQuery(id+"F2.wireOp",EDGE,"E589"),sQuery(id+"F2.wireOp",EDGE,"E590"),sQuery(id+"F2.wireOp",EDGE,"E591"),sQuery(id+"F2.wireOp",EDGE,"E592"),sQuery(id+"F2.wireOp",EDGE,"E593"),sQuery(id+"F2.wireOp",EDGE,"E594"),sQuery(id+"F2.wireOp",EDGE,"E595"),sQuery(id+"F2.wireOp",EDGE,"E596"),sQuery(id+"F2.wireOp",EDGE,"E597"),sQuery(id+"F2.wireOp",EDGE,"E598"),sQuery(id+"F2.wireOp",EDGE,"E599"),sQuery(id+"F2.wireOp",EDGE,"E600"),sQuery(id+"F2.wireOp",EDGE,"E601"),sQuery(id+"F2.wireOp",EDGE,"E602"),sQuery(id+"F2.wireOp",EDGE,"E603"),sQuery(id+"F2.wireOp",EDGE,"E604"),sQuery(id+"F2.wireOp",EDGE,"E605"),sQuery(id+"F2.wireOp",EDGE,"E606"),sQuery(id+"F2.wireOp",EDGE,"E607"),sQuery(id+"F2.wireOp",EDGE,"E608"),sQuery(id+"F2.wireOp",EDGE,"E609"),sQuery(id+"F2.wireOp",EDGE,"E610"),sQuery(id+"F2.wireOp",EDGE,"E611"),sQuery(id+"F2.wireOp",EDGE,"E612"),sQuery(id+"F2.wireOp",EDGE,"E613"),sQuery(id+"F2.wireOp",EDGE,"E614"),sQuery(id+"F2.wireOp",EDGE,"E615"),sQuery(id+"F2.wireOp",EDGE,"E616"),sQuery(id+"F2.wireOp",EDGE,"E617"),sQuery(id+"F2.wireOp",EDGE,"E618"),sQuery(id+"F2.wireOp",EDGE,"E619"),sQuery(id+"F2.wireOp",EDGE,"E620"),sQuery(id+"F2.wireOp",EDGE,"E621"),sQuery(id+"F2.wireOp",EDGE,"E622"),sQuery(id+"F2.wireOp",EDGE,"E623"),sQuery(id+"F2.wireOp",EDGE,"E624"),sQuery(id+"F2.wireOp",EDGE,"E625"),sQuery(id+"F2.wireOp",EDGE,"E626"),sQuery(id+"F2.wireOp",EDGE,"E627"),sQuery(id+"F2.wireOp",EDGE,"E628"),sQuery(id+"F2.wireOp",EDGE,"E629"),sQuery(id+"F2.wireOp",EDGE,"E630"),sQuery(id+"F2.wireOp",EDGE,"E631"),sQuery(id+"F2.wireOp",EDGE,"E632"),sQuery(id+"F2.wireOp",EDGE,"E633"),sQuery(id+"F2.wireOp",EDGE,"E634"),sQuery(id+"F2.wireOp",EDGE,"E635"),sQuery(id+"F2.wireOp",EDGE,"E636"),sQuery(id+"F2.wireOp",EDGE,"E637"),sQuery(id+"F2.wireOp",EDGE,"E638"),sQuery(id+"F2.wireOp",EDGE,"E639"),sQuery(id+"F2.wireOp",EDGE,"E640"),sQuery(id+"F2.wireOp",EDGE,"E641"),sQuery(id+"F2.wireOp",EDGE,"E642"),sQuery(id+"F2.wireOp",EDGE,"E643"),sQuery(id+"F2.wireOp",EDGE,"E644"),sQuery(id+"F2.wireOp",EDGE,"E645"),sQuery(id+"F2.wireOp",EDGE,"E646"),sQuery(id+"F2.wireOp",EDGE,"E647"),sQuery(id+"F2.wireOp",EDGE,"E648"),sQuery(id+"F2.wireOp",EDGE,"E649"),sQuery(id+"F2.wireOp",EDGE,"E650"),sQuery(id+"F2.wireOp",EDGE,"E651"),sQuery(id+"F2.wireOp",EDGE,"E652"),sQuery(id+"F2.wireOp",EDGE,"E653"),sQuery(id+"F2.wireOp",EDGE,"E654"),sQuery(id+"F2.wireOp",EDGE,"E655"),sQuery(id+"F2.wireOp",EDGE,"E656"),sQuery(id+"F2.wireOp",EDGE,"E657"),sQuery(id+"F2.wireOp",EDGE,"E658"),sQuery(id+"F2.wireOp",EDGE,"E659"),sQuery(id+"F2.wireOp",EDGE,"E660"),sQuery(id+"F2.wireOp",EDGE,"E661"),sQuery(id+"F2.wireOp",EDGE,"E662"),sQuery(id+"F2.wireOp",EDGE,"E663"),sQuery(id+"F2.wireOp",EDGE,"E664"),sQuery(id+"F2.wireOp",EDGE,"E665"),sQuery(id+"F2.wireOp",EDGE,"E666"),sQuery(id+"F2.wireOp",EDGE,"E667"),sQuery(id+"F2.wireOp",EDGE,"E668"),sQuery(id+"F2.wireOp",EDGE,"E669"),sQuery(id+"F2.wireOp",EDGE,"E670"),sQuery(id+"F2.wireOp",EDGE,"E671"),sQuery(id+"F2.wireOp",EDGE,"E672"),sQuery(id+"F2.wireOp",EDGE,"E673"),sQuery(id+"F2.wireOp",EDGE,"E674"),sQuery(id+"F2.wireOp",EDGE,"E675"),sQuery(id+"F2.wireOp",EDGE,"E676"),sQuery(id+"F2.wireOp",EDGE,"E677"),sQuery(id+"F2.wireOp",EDGE,"E678"),sQuery(id+"F2.wireOp",EDGE,"E679"),sQuery(id+"F2.wireOp",EDGE,"E680"),sQuery(id+"F2.wireOp",EDGE,"E681"),sQuery(id+"F2.wireOp",EDGE,"E682"),sQuery(id+"F2.wireOp",EDGE,"E683"),sQuery(id+"F2.wireOp",EDGE,"E684"),sQuery(id+"F2.wireOp",EDGE,"E685"),sQuery(id+"F2.wireOp",EDGE,"E686"),sQuery(id+"F2.wireOp",EDGE,"E687"),sQuery(id+"F2.wireOp",EDGE,"E688"),sQuery(id+"F2.wireOp",EDGE,"E689"),sQuery(id+"F2.wireOp",EDGE,"E690"),sQuery(id+"F2.wireOp",EDGE,"E691"),sQuery(id+"F2.wireOp",EDGE,"E692"),sQuery(id+"F2.wireOp",EDGE,"E693"),sQuery(id+"F2.wireOp",EDGE,"E694"),sQuery(id+"F2.wireOp",EDGE,"E695"),sQuery(id+"F2.wireOp",EDGE,"E696"),sQuery(id+"F2.wireOp",EDGE,"E697"),sQuery(id+"F2.wireOp",EDGE,"E698"),sQuery(id+"F2.wireOp",EDGE,"E699"),sQuery(id+"F2.wireOp",EDGE,"E700"),sQuery(id+"F2.wireOp",EDGE,"E701"),sQuery(id+"F2.wireOp",EDGE,"E702"),sQuery(id+"F2.wireOp",EDGE,"E703"),sQuery(id+"F2.wireOp",EDGE,"E704"),sQuery(id+"F2.wireOp",EDGE,"E705"),sQuery(id+"F2.wireOp",EDGE,"E706"),sQuery(id+"F2.wireOp",EDGE,"E707"),sQuery(id+"F2.wireOp",EDGE,"E708"),sQuery(id+"F2.wireOp",EDGE,"E709"),sQuery(id+"F2.wireOp",EDGE,"E710"),sQuery(id+"F2.wireOp",EDGE,"E711"),sQuery(id+"F2.wireOp",EDGE,"E712"),sQuery(id+"F2.wireOp",EDGE,"E713"),sQuery(id+"F2.wireOp",EDGE,"E714"),sQuery(id+"F2.wireOp",EDGE,"E715"),sQuery(id+"F2.wireOp",EDGE,"E716"),sQuery(id+"F2.wireOp",EDGE,"E717"),sQuery(id+"F2.wireOp",EDGE,"E718"),sQuery(id+"F2.wireOp",EDGE,"E719"),sQuery(id+"F2.wireOp",EDGE,"E720"),sQuery(id+"F2.wireOp",EDGE,"E721"),sQuery(id+"F2.wireOp",EDGE,"E722"),sQuery(id+"F2.wireOp",EDGE,"E723"),sQuery(id+"F2.wireOp",EDGE,"E724"),sQuery(id+"F2.wireOp",EDGE,"E725"),sQuery(id+"F2.wireOp",EDGE,"E726"),sQuery(id+"F2.wireOp",EDGE,"E727"),sQuery(id+"F2.wireOp",EDGE,"E728"),sQuery(id+"F2.wireOp",EDGE,"E729"),sQuery(id+"F2.wireOp",EDGE,"E730"),sQuery(id+"F2.wireOp",EDGE,"E731"),sQuery(id+"F2.wireOp",EDGE,"E732"),sQuery(id+"F2.wireOp",EDGE,"E733"),sQuery(id+"F2.wireOp",EDGE,"E734"),sQuery(id+"F2.wireOp",EDGE,"E735"),sQuery(id+"F2.wireOp",EDGE,"E736"),sQuery(id+"F2.wireOp",EDGE,"E737"),sQuery(id+"F2.wireOp",EDGE,"E738"),sQuery(id+"F2.wireOp",EDGE,"E739"),sQuery(id+"F2.wireOp",EDGE,"E740"),sQuery(id+"F2.wireOp",EDGE,"E741"),sQuery(id+"F2.wireOp",EDGE,"E742"),sQuery(id+"F2.wireOp",EDGE,"E743"),sQuery(id+"F2.wireOp",EDGE,"E744"),sQuery(id+"F2.wireOp",EDGE,"E745"),sQuery(id+"F2.wireOp",EDGE,"E746"),sQuery(id+"F2.wireOp",EDGE,"E747"),sQuery(id+"F2.wireOp",EDGE,"E748"),sQuery(id+"F2.wireOp",EDGE,"E749"),sQuery(id+"F2.wireOp",EDGE,"E750"),sQuery(id+"F2.wireOp",EDGE,"E751"),sQuery(id+"F2.wireOp",EDGE,"E752"),sQuery(id+"F2.wireOp",EDGE,"E753"),sQuery(id+"F2.wireOp",EDGE,"E754"),sQuery(id+"F2.wireOp",EDGE,"E755"),sQuery(id+"F2.wireOp",EDGE,"E756"),sQuery(id+"F2.wireOp",EDGE,"E757"),sQuery(id+"F2.wireOp",EDGE,"E758"),sQuery(id+"F2.wireOp",EDGE,"E759"),sQuery(id+"F2.wireOp",EDGE,"E760"),sQuery(id+"F2.wireOp",EDGE,"E761"),sQuery(id+"F2.wireOp",EDGE,"E762"),sQuery(id+"F2.wireOp",EDGE,"E763"),sQuery(id+"F2.wireOp",EDGE,"E764"),sQuery(id+"F2.wireOp",EDGE,"E765"),sQuery(id+"F2.wireOp",EDGE,"E766"),sQuery(id+"F2.wireOp",EDGE,"E767"),sQuery(id+"F2.wireOp",EDGE,"E768"),sQuery(id+"F2.wireOp",EDGE,"E769"),sQuery(id+"F2.wireOp",EDGE,"E770"),sQuery(id+"F2.wireOp",EDGE,"E771"),sQuery(id+"F2.wireOp",EDGE,"E772"),sQuery(id+"F2.wireOp",EDGE,"E773"),sQuery(id+"F2.wireOp",EDGE,"E774"),sQuery(id+"F2.wireOp",EDGE,"E775"),sQuery(id+"F2.wireOp",EDGE,"E776"),sQuery(id+"F2.wireOp",EDGE,"E777"),sQuery(id+"F2.wireOp",EDGE,"E778"),sQuery(id+"F2.wireOp",EDGE,"E779"),sQuery(id+"F2.wireOp",EDGE,"E780"),sQuery(id+"F2.wireOp",EDGE,"E781"),sQuery(id+"F2.wireOp",EDGE,"E782"),sQuery(id+"F2.wireOp",EDGE,"E783"),sQuery(id+"F2.wireOp",EDGE,"E784"),sQuery(id+"F2.wireOp",EDGE,"E785"),sQuery(id+"F2.wireOp",EDGE,"E786"),sQuery(id+"F2.wireOp",EDGE,"E787"),sQuery(id+"F2.wireOp",EDGE,"E788"),sQuery(id+"F2.wireOp",EDGE,"E789"),sQuery(id+"F2.wireOp",EDGE,"E790"),sQuery(id+"F2.wireOp",EDGE,"E791"),sQuery(id+"F2.wireOp",EDGE,"E792"),sQuery(id+"F2.wireOp",EDGE,"E793"),sQuery(id+"F2.wireOp",EDGE,"E794"),sQuery(id+"F2.wireOp",EDGE,"E795"),sQuery(id+"F2.wireOp",EDGE,"E796"),sQuery(id+"F2.wireOp",EDGE,"E797"),sQuery(id+"F2.wireOp",EDGE,"E798"),sQuery(id+"F2.wireOp",EDGE,"E799"),sQuery(id+"F2.wireOp",EDGE,"E800"),sQuery(id+"F2.wireOp",EDGE,"E801"),sQuery(id+"F2.wireOp",EDGE,"E802"),sQuery(id+"F2.wireOp",EDGE,"E803"),sQuery(id+"F2.wireOp",EDGE,"E804"),sQuery(id+"F2.wireOp",EDGE,"E805"),sQuery(id+"F2.wireOp",EDGE,"E806"),sQuery(id+"F2.wireOp",EDGE,"E807"),sQuery(id+"F2.wireOp",EDGE,"E808"),sQuery(id+"F2.wireOp",EDGE,"E809"),sQuery(id+"F2.wireOp",EDGE,"E810"),sQuery(id+"F2.wireOp",EDGE,"E811"),sQuery(id+"F2.wireOp",EDGE,"E812"),sQuery(id+"F2.wireOp",EDGE,"E813"),sQuery(id+"F2.wireOp",EDGE,"E814"),sQuery(id+"F2.wireOp",EDGE,"E815"),sQuery(id+"F2.wireOp",EDGE,"E816"),sQuery(id+"F2.wireOp",EDGE,"E817"),sQuery(id+"F2.wireOp",EDGE,"E818"),sQuery(id+"F2.wireOp",EDGE,"E819"),sQuery(id+"F2.wireOp",EDGE,"E820"),sQuery(id+"F2.wireOp",EDGE,"E821"),sQuery(id+"F2.wireOp",EDGE,"E822"),sQuery(id+"F2.wireOp",EDGE,"E823"),sQuery(id+"F2.wireOp",EDGE,"E824"),sQuery(id+"F2.wireOp",EDGE,"E825"),sQuery(id+"F2.wireOp",EDGE,"E826"),sQuery(id+"F2.wireOp",EDGE,"E827"),sQuery(id+"F2.wireOp",EDGE,"E828"),sQuery(id+"F2.wireOp",EDGE,"E829"),sQuery(id+"F2.wireOp",EDGE,"E830"),sQuery(id+"F2.wireOp",EDGE,"E831"),sQuery(id+"F2.wireOp",EDGE,"E832"),sQuery(id+"F2.wireOp",EDGE,"E833"),sQuery(id+"F2.wireOp",EDGE,"E834"),sQuery(id+"F2.wireOp",EDGE,"E835"),sQuery(id+"F2.wireOp",EDGE,"E836"),sQuery(id+"F2.wireOp",EDGE,"E837"),sQuery(id+"F2.wireOp",EDGE,"E838"),sQuery(id+"F2.wireOp",EDGE,"E839"),sQuery(id+"F2.wireOp",EDGE,"E840"),sQuery(id+"F2.wireOp",EDGE,"E841"),sQuery(id+"F2.wireOp",EDGE,"E842"),sQuery(id+"F2.wireOp",EDGE,"E843"),sQuery(id+"F2.wireOp",EDGE,"E844"),sQuery(id+"F2.wireOp",EDGE,"E845"),sQuery(id+"F2.wireOp",EDGE,"E846"),sQuery(id+"F2.wireOp",EDGE,"E847"),sQuery(id+"F2.wireOp",EDGE,"E848"),sQuery(id+"F2.wireOp",EDGE,"E849"),sQuery(id+"F2.wireOp",EDGE,"E850"),sQuery(id+"F2.wireOp",EDGE,"E851"),sQuery(id+"F2.wireOp",EDGE,"E852"),sQuery(id+"F2.wireOp",EDGE,"E853"),sQuery(id+"F2.wireOp",EDGE,"E854"),sQuery(id+"F2.wireOp",EDGE,"E855"),sQuery(id+"F2.wireOp",EDGE,"E856"),sQuery(id+"F2.wireOp",EDGE,"E857"),sQuery(id+"F2.wireOp",EDGE,"E858"),sQuery(id+"F2.wireOp",EDGE,"E859"),sQuery(id+"F2.wireOp",EDGE,"E860"),sQuery(id+"F2.wireOp",EDGE,"E861"),sQuery(id+"F2.wireOp",EDGE,"E862"),sQuery(id+"F2.wireOp",EDGE,"E863"),sQuery(id+"F2.wireOp",EDGE,"E864"),sQuery(id+"F2.wireOp",EDGE,"E865"),sQuery(id+"F2.wireOp",EDGE,"E866"),sQuery(id+"F2.wireOp",EDGE,"E867"),sQuery(id+"F2.wireOp",EDGE,"E868"),sQuery(id+"F2.wireOp",EDGE,"E869"),sQuery(id+"F2.wireOp",EDGE,"E870"),sQuery(id+"F2.wireOp",EDGE,"E871"),sQuery(id+"F2.wireOp",EDGE,"E872"),sQuery(id+"F2.wireOp",EDGE,"E873"),sQuery(id+"F2.wireOp",EDGE,"E874"),sQuery(id+"F2.wireOp",EDGE,"E875"),sQuery(id+"F2.wireOp",EDGE,"E876"),sQuery(id+"F2.wireOp",EDGE,"E877"),sQuery(id+"F2.wireOp",EDGE,"E878"),sQuery(id+"F2.wireOp",EDGE,"E879"),sQuery(id+"F2.wireOp",EDGE,"E880"),sQuery(id+"F2.wireOp",EDGE,"E881"),sQuery(id+"F2.wireOp",EDGE,"E882"),sQuery(id+"F2.wireOp",EDGE,"E883"),sQuery(id+"F2.wireOp",EDGE,"E884"),sQuery(id+"F2.wireOp",EDGE,"E885"),sQuery(id+"F2.wireOp",EDGE,"E886"),sQuery(id+"F2.wireOp",EDGE,"E887"),sQuery(id+"F2.wireOp",EDGE,"E888"),sQuery(id+"F2.wireOp",EDGE,"E889"),sQuery(id+"F2.wireOp",EDGE,"E890"),sQuery(id+"F2.wireOp",EDGE,"E891"),sQuery(id+"F2.wireOp",EDGE,"E892"),sQuery(id+"F2.wireOp",EDGE,"E893"),sQuery(id+"F2.wireOp",EDGE,"E894"),sQuery(id+"F2.wireOp",EDGE,"E895"),sQuery(id+"F2.wireOp",EDGE,"E896"),sQuery(id+"F2.wireOp",EDGE,"E897"),sQuery(id+"F2.wireOp",EDGE,"E898"),sQuery(id+"F2.wireOp",EDGE,"E899"),sQuery(id+"F2.wireOp",EDGE,"E900"),sQuery(id+"F2.wireOp",EDGE,"E901"),sQuery(id+"F2.wireOp",EDGE,"E902"),sQuery(id+"F2.wireOp",EDGE,"E903"),sQuery(id+"F2.wireOp",EDGE,"E904"),sQuery(id+"F2.wireOp",EDGE,"E905"),sQuery(id+"F2.wireOp",EDGE,"E906"),sQuery(id+"F2.wireOp",EDGE,"E907"),sQuery(id+"F2.wireOp",EDGE,"E908"),sQuery(id+"F2.wireOp",EDGE,"E909"),sQuery(id+"F2.wireOp",EDGE,"E910"),sQuery(id+"F2.wireOp",EDGE,"E911"),sQuery(id+"F2.wireOp",EDGE,"E912"),sQuery(id+"F2.wireOp",EDGE,"E913"),sQuery(id+"F2.wireOp",EDGE,"E914"),sQuery(id+"F2.wireOp",EDGE,"E915"),sQuery(id+"F2.wireOp",EDGE,"E916"),sQuery(id+"F2.wireOp",EDGE,"E917"),sQuery(id+"F2.wireOp",EDGE,"E918"),sQuery(id+"F2.wireOp",EDGE,"E919"),sQuery(id+"F2.wireOp",EDGE,"E920"),sQuery(id+"F2.wireOp",EDGE,"E921"),sQuery(id+"F2.wireOp",EDGE,"E922"),sQuery(id+"F2.wireOp",EDGE,"E923"),sQuery(id+"F2.wireOp",EDGE,"E924"),sQuery(id+"F2.wireOp",EDGE,"E925"),sQuery(id+"F2.wireOp",EDGE,"E926"),sQuery(id+"F2.wireOp",EDGE,"E927"),sQuery(id+"F2.wireOp",EDGE,"E928"),sQuery(id+"F2.wireOp",EDGE,"E929"),sQuery(id+"F2.wireOp",EDGE,"E930"),sQuery(id+"F2.wireOp",EDGE,"E931"),sQuery(id+"F2.wireOp",EDGE,"E932"),sQuery(id+"F2.wireOp",EDGE,"E933"),sQuery(id+"F2.wireOp",EDGE,"E934"),sQuery(id+"F2.wireOp",EDGE,"E935"),sQuery(id+"F2.wireOp",EDGE,"E936"),sQuery(id+"F2.wireOp",EDGE,"E937"),sQuery(id+"F2.wireOp",EDGE,"E938"),sQuery(id+"F2.wireOp",EDGE,"E939"),sQuery(id+"F2.wireOp",EDGE,"E940"),sQuery(id+"F2.wireOp",EDGE,"E941"),sQuery(id+"F2.wireOp",EDGE,"E942"),sQuery(id+"F2.wireOp",EDGE,"E943"),sQuery(id+"F2.wireOp",EDGE,"E944"),sQuery(id+"F2.wireOp",EDGE,"E945"),sQuery(id+"F2.wireOp",EDGE,"E946"),sQuery(id+"F2.wireOp",EDGE,"E947"),sQuery(id+"F2.wireOp",EDGE,"E948"),sQuery(id+"F2.wireOp",EDGE,"E949"),sQuery(id+"F2.wireOp",EDGE,"E950"),sQuery(id+"F2.wireOp",EDGE,"E951"),sQuery(id+"F2.wireOp",EDGE,"E952"),sQuery(id+"F2.wireOp",EDGE,"E953"),sQuery(id+"F2.wireOp",EDGE,"E954"),sQuery(id+"F2.wireOp",EDGE,"E955"),sQuery(id+"F2.wireOp",EDGE,"E956"),sQuery(id+"F2.wireOp",EDGE,"E957"),sQuery(id+"F2.wireOp",EDGE,"E958"),sQuery(id+"F2.wireOp",EDGE,"E959"),sQuery(id+"F2.wireOp",EDGE,"E960"),sQuery(id+"F2.wireOp",EDGE,"E961"),sQuery(id+"F2.wireOp",EDGE,"E962"),sQuery(id+"F2.wireOp",EDGE,"E963"),sQuery(id+"F2.wireOp",EDGE,"E964"),sQuery(id+"F2.wireOp",EDGE,"E965"),sQuery(id+"F2.wireOp",EDGE,"E966"),sQuery(id+"F2.wireOp",EDGE,"E967"),sQuery(id+"F2.wireOp",EDGE,"E968"),sQuery(id+"F2.wireOp",EDGE,"E969"),sQuery(id+"F2.wireOp",EDGE,"E970"),sQuery(id+"F2.wireOp",EDGE,"E971"),sQuery(id+"F2.wireOp",EDGE,"E972"),sQuery(id+"F2.wireOp",EDGE,"E973"),sQuery(id+"F2.wireOp",EDGE,"E974"),sQuery(id+"F2.wireOp",EDGE,"E975"),sQuery(id+"F2.wireOp",EDGE,"E976"),sQuery(id+"F2.wireOp",EDGE,"E977"),sQuery(id+"F2.wireOp",EDGE,"E978"),sQuery(id+"F2.wireOp",EDGE,"E979"),sQuery(id+"F2.wireOp",EDGE,"E980"),sQuery(id+"F2.wireOp",EDGE,"E981"),sQuery(id+"F2.wireOp",EDGE,"E982"),sQuery(id+"F2.wireOp",EDGE,"E983"),sQuery(id+"F2.wireOp",EDGE,"E984"),sQuery(id+"F2.wireOp",EDGE,"E985"),sQuery(id+"F2.wireOp",EDGE,"E986"),sQuery(id+"F2.wireOp",EDGE,"E987"),sQuery(id+"F2.wireOp",EDGE,"E988"),sQuery(id+"F2.wireOp",EDGE,"E989"),sQuery(id+"F2.wireOp",EDGE,"E990"),sQuery(id+"F2.wireOp",EDGE,"E991"),sQuery(id+"F2.wireOp",EDGE,"E992"),sQuery(id+"F2.wireOp",EDGE,"E993"),sQuery(id+"F2.wireOp",EDGE,"E994"),sQuery(id+"F2.wireOp",EDGE,"E995"),sQuery(id+"F2.wireOp",EDGE,"E996"),sQuery(id+"F2.wireOp",EDGE,"E997"),sQuery(id+"F2.wireOp",EDGE,"E998"),sQuery(id+"F2.wireOp",EDGE,"E999"),sQuery(id+"F2.wireOp",EDGE,"E1000"),sQuery(id+"F2.wireOp",EDGE,"E1001"),sQuery(id+"F2.wireOp",EDGE,"E1002"),sQuery(id+"F2.wireOp",EDGE,"E1003"),sQuery(id+"F2.wireOp",EDGE,"E1004"),sQuery(id+"F2.wireOp",EDGE,"E1005"),sQuery(id+"F2.wireOp",EDGE,"E1006"),sQuery(id+"F2.wireOp",EDGE,"E1007"),sQuery(id+"F2.wireOp",EDGE,"E1008"),sQuery(id+"F2.wireOp",EDGE,"E1009"),sQuery(id+"F2.wireOp",EDGE,"E1010"),sQuery(id+"F2.wireOp",EDGE,"E1011"),sQuery(id+"F2.wireOp",EDGE,"E1012"),sQuery(id+"F2.wireOp",EDGE,"E1013"),sQuery(id+"F2.wireOp",EDGE,"E1014"),sQuery(id+"F2.wireOp",EDGE,"E1015"),sQuery(id+"F2.wireOp",EDGE,"E1016"),sQuery(id+"F2.wireOp",EDGE,"E1017"),sQuery(id+"F2.wireOp",EDGE,"E1018"),sQuery(id+"F2.wireOp",EDGE,"E1019"),sQuery(id+"F2.wireOp",EDGE,"E1020"),sQuery(id+"F2.wireOp",EDGE,"E1021"),sQuery(id+"F2.wireOp",EDGE,"E1022"),sQuery(id+"F2.wireOp",EDGE,"E1023"),sQuery(id+"F2.wireOp",EDGE,"E1024"),sQuery(id+"F2.wireOp",EDGE,"E1025"),sQuery(id+"F2.wireOp",EDGE,"E1026"),sQuery(id+"F2.wireOp",EDGE,"E1027"),sQuery(id+"F2.wireOp",EDGE,"E1028"),sQuery(id+"F2.wireOp",EDGE,"E1029"),sQuery(id+"F2.wireOp",EDGE,"E1030"),sQuery(id+"F2.wireOp",EDGE,"E1031"),sQuery(id+"F2.wireOp",EDGE,"E1032"),sQuery(id+"F2.wireOp",EDGE,"E1033"),sQuery(id+"F2.wireOp",EDGE,"E1034"),sQuery(id+"F2.wireOp",EDGE,"E1035"),sQuery(id+"F2.wireOp",EDGE,"E1036"),sQuery(id+"F2.wireOp",EDGE,"E1037"),sQuery(id+"F2.wireOp",EDGE,"E1038"),sQuery(id+"F2.wireOp",EDGE,"E1039"),sQuery(id+"F2.wireOp",EDGE,"E1040"),sQuery(id+"F2.wireOp",EDGE,"E1041"),sQuery(id+"F2.wireOp",EDGE,"E1042"),sQuery(id+"F2.wireOp",EDGE,"E1043"),sQuery(id+"F2.wireOp",EDGE,"E1044"),sQuery(id+"F2.wireOp",EDGE,"E1045"),sQuery(id+"F2.wireOp",EDGE,"E1046"),sQuery(id+"F2.wireOp",EDGE,"E1047"),sQuery(id+"F2.wireOp",EDGE,"E1048"),sQuery(id+"F2.wireOp",EDGE,"E1049"),sQuery(id+"F2.wireOp",EDGE,"E1050"),sQuery(id+"F2.wireOp",EDGE,"E1051"),sQuery(id+"F2.wireOp",EDGE,"E1052"),sQuery(id+"F2.wireOp",EDGE,"E1053"),sQuery(id+"F2.wireOp",EDGE,"E1054"),sQuery(id+"F2.wireOp",EDGE,"E1055"),sQuery(id+"F2.wireOp",EDGE,"E1056"),sQuery(id+"F2.wireOp",EDGE,"E1057"),sQuery(id+"F2.wireOp",EDGE,"E1058"),sQuery(id+"F2.wireOp",EDGE,"E1059"),sQuery(id+"F2.wireOp",EDGE,"E1060"),sQuery(id+"F2.wireOp",EDGE,"E1061"),sQuery(id+"F2.wireOp",EDGE,"E1062"),sQuery(id+"F2.wireOp",EDGE,"E1063"),sQuery(id+"F2.wireOp",EDGE,"E1064"),sQuery(id+"F2.wireOp",EDGE,"E1065"),sQuery(id+"F2.wireOp",EDGE,"E1066"),sQuery(id+"F2.wireOp",EDGE,"E1067"),sQuery(id+"F2.wireOp",EDGE,"E1068"),sQuery(id+"F2.wireOp",EDGE,"E1069"),sQuery(id+"F2.wireOp",EDGE,"E1070"),sQuery(id+"F2.wireOp",EDGE,"E1071"),sQuery(id+"F2.wireOp",EDGE,"E1072"),sQuery(id+"F2.wireOp",EDGE,"E1073"),sQuery(id+"F2.wireOp",EDGE,"E1074"),sQuery(id+"F2.wireOp",EDGE,"E1075"),sQuery(id+"F2.wireOp",EDGE,"E1076"),sQuery(id+"F2.wireOp",EDGE,"E1077"),sQuery(id+"F2.wireOp",EDGE,"E1078"),sQuery(id+"F2.wireOp",EDGE,"E1079"),sQuery(id+"F2.wireOp",EDGE,"E1080"),sQuery(id+"F2.wireOp",EDGE,"E1081"),sQuery(id+"F2.wireOp",EDGE,"E1082"),sQuery(id+"F2.wireOp",EDGE,"E1083"),sQuery(id+"F2.wireOp",EDGE,"E1084"),sQuery(id+"F2.wireOp",EDGE,"E1085"),sQuery(id+"F2.wireOp",EDGE,"E1086"),sQuery(id+"F2.wireOp",EDGE,"E1087"),sQuery(id+"F2.wireOp",EDGE,"E1088"),sQuery(id+"F2.wireOp",EDGE,"E1089"),sQuery(id+"F2.wireOp",EDGE,"E1090"),sQuery(id+"F2.wireOp",EDGE,"E1091"),sQuery(id+"F2.wireOp",EDGE,"E1092"),sQuery(id+"F2.wireOp",EDGE,"E1093"),sQuery(id+"F2.wireOp",EDGE,"E1094"),sQuery(id+"F2.wireOp",EDGE,"E1095"),sQuery(id+"F2.wireOp",EDGE,"E1096"),sQuery(id+"F2.wireOp",EDGE,"E1097"),sQuery(id+"F2.wireOp",EDGE,"E1098"),sQuery(id+"F2.wireOp",EDGE,"E1099"),sQuery(id+"F2.wireOp",EDGE,"E1100"),sQuery(id+"F2.wireOp",EDGE,"E1101"),sQuery(id+"F2.wireOp",EDGE,"E1102"),sQuery(id+"F2.wireOp",EDGE,"E1103"),sQuery(id+"F2.wireOp",EDGE,"E1104"),sQuery(id+"F2.wireOp",EDGE,"E1105"),sQuery(id+"F2.wireOp",EDGE,"E1106"),sQuery(id+"F2.wireOp",EDGE,"E1107"),sQuery(id+"F2.wireOp",EDGE,"E1108"),sQuery(id+"F2.wireOp",EDGE,"E1109"),sQuery(id+"F2.wireOp",EDGE,"E1110"),sQuery(id+"F2.wireOp",EDGE,"E1111"),sQuery(id+"F2.wireOp",EDGE,"E1112"),sQuery(id+"F2.wireOp",EDGE,"E1113"),sQuery(id+"F2.wireOp",EDGE,"E1114"),sQuery(id+"F2.wireOp",EDGE,"E1115"),sQuery(id+"F2.wireOp",EDGE,"E1116"),sQuery(id+"F2.wireOp",EDGE,"E1117"),sQuery(id+"F2.wireOp",EDGE,"E1118"),sQuery(id+"F2.wireOp",EDGE,"E1119"),sQuery(id+"F2.wireOp",EDGE,"E1120"),sQuery(id+"F2.wireOp",EDGE,"E1121"),sQuery(id+"F2.wireOp",EDGE,"E1122"),sQuery(id+"F2.wireOp",EDGE,"E1123"),sQuery(id+"F2.wireOp",EDGE,"E1124"),sQuery(id+"F2.wireOp",EDGE,"E1125"),sQuery(id+"F2.wireOp",EDGE,"E1126"),sQuery(id+"F2.wireOp",EDGE,"E1127"),sQuery(id+"F2.wireOp",EDGE,"E1128"),sQuery(id+"F2.wireOp",EDGE,"E1129"),sQuery(id+"F2.wireOp",EDGE,"E1130"),sQuery(id+"F2.wireOp",EDGE,"E1131"),sQuery(id+"F2.wireOp",EDGE,"E1132"),sQuery(id+"F2.wireOp",EDGE,"E1133"),sQuery(id+"F2.wireOp",EDGE,"E1134"),sQuery(id+"F2.wireOp",EDGE,"E1135"),sQuery(id+"F2.wireOp",EDGE,"E1136"),sQuery(id+"F2.wireOp",EDGE,"E1137"),sQuery(id+"F2.wireOp",EDGE,"E1138"),sQuery(id+"F2.wireOp",EDGE,"E1139"),sQuery(id+"F2.wireOp",EDGE,"E1140"),sQuery(id+"F2.wireOp",EDGE,"E1141"),sQuery(id+"F2.wireOp",EDGE,"E1142"),sQuery(id+"F2.wireOp",EDGE,"E1143"),sQuery(id+"F2.wireOp",EDGE,"E1144"),sQuery(id+"F2.wireOp",EDGE,"E1145"),sQuery(id+"F2.wireOp",EDGE,"E1146"),sQuery(id+"F2.wireOp",EDGE,"E1147"),sQuery(id+"F2.wireOp",EDGE,"E1148"),sQuery(id+"F2.wireOp",EDGE,"E1149"),sQuery(id+"F2.wireOp",EDGE,"E1150"),sQuery(id+"F2.wireOp",EDGE,"E1151"),sQuery(id+"F2.wireOp",EDGE,"E1152"),sQuery(id+"F2.wireOp",EDGE,"E1153"),sQuery(id+"F2.wireOp",EDGE,"E1154"),sQuery(id+"F2.wireOp",EDGE,"E1155"),sQuery(id+"F2.wireOp",EDGE,"E1156"),sQuery(id+"F2.wireOp",EDGE,"E1157"),sQuery(id+"F2.wireOp",EDGE,"E1158"),sQuery(id+"F2.wireOp",EDGE,"E1159"),sQuery(id+"F2.wireOp",EDGE,"E1160"),sQuery(id+"F2.wireOp",EDGE,"E1161"),sQuery(id+"F2.wireOp",EDGE,"E1162"),sQuery(id+"F2.wireOp",EDGE,"E1163"),sQuery(id+"F2.wireOp",EDGE,"E1164"),sQuery(id+"F2.wireOp",EDGE,"E1165"),sQuery(id+"F2.wireOp",EDGE,"E1166"),sQuery(id+"F2.wireOp",EDGE,"E1167"),sQuery(id+"F2.wireOp",EDGE,"E1168"),sQuery(id+"F2.wireOp",EDGE,"E1169"),sQuery(id+"F2.wireOp",EDGE,"E1170"),sQuery(id+"F2.wireOp",EDGE,"E1171"),sQuery(id+"F2.wireOp",EDGE,"E1172"),sQuery(id+"F2.wireOp",EDGE,"E1173"),sQuery(id+"F2.wireOp",EDGE,"E1174"),sQuery(id+"F2.wireOp",EDGE,"E1175"),sQuery(id+"F2.wireOp",EDGE,"E1176"),sQuery(id+"F2.wireOp",EDGE,"E1177"),sQuery(id+"F2.wireOp",EDGE,"E1178"),sQuery(id+"F2.wireOp",EDGE,"E1179"),sQuery(id+"F2.wireOp",EDGE,"E1180"),sQuery(id+"F2.wireOp",EDGE,"E1181"),sQuery(id+"F2.wireOp",EDGE,"E1182"),sQuery(id+"F2.wireOp",EDGE,"E1183"),sQuery(id+"F2.wireOp",EDGE,"E1184"),sQuery(id+"F2.wireOp",EDGE,"E1185"),sQuery(id+"F2.wireOp",EDGE,"E1186"),sQuery(id+"F2.wireOp",EDGE,"E1187"),sQuery(id+"F2.wireOp",EDGE,"E1188"),sQuery(id+"F2.wireOp",EDGE,"E1189"),sQuery(id+"F2.wireOp",EDGE,"E1190"),sQuery(id+"F2.wireOp",EDGE,"E1191"),sQuery(id+"F2.wireOp",EDGE,"E1192"),sQuery(id+"F2.wireOp",EDGE,"E1193"),sQuery(id+"F2.wireOp",EDGE,"E1194"),sQuery(id+"F2.wireOp",EDGE,"E1195"),sQuery(id+"F2.wireOp",EDGE,"E1196"),sQuery(id+"F2.wireOp",EDGE,"E1197"),sQuery(id+"F2.wireOp",EDGE,"E1198"),sQuery(id+"F2.wireOp",EDGE,"E1199"),sQuery(id+"F2.wireOp",EDGE,"E1200"),sQuery(id+"F2.wireOp",EDGE,"E1201"),sQuery(id+"F2.wireOp",EDGE,"E1202"),sQuery(id+"F2.wireOp",EDGE,"E1203"),sQuery(id+"F2.wireOp",EDGE,"E1204"),sQuery(id+"F2.wireOp",EDGE,"E1205"),sQuery(id+"F2.wireOp",EDGE,"E1206"),sQuery(id+"F2.wireOp",EDGE,"E1207"),sQuery(id+"F2.wireOp",EDGE,"E1208"),sQuery(id+"F2.wireOp",EDGE,"E1209"),sQuery(id+"F2.wireOp",EDGE,"E1210"),sQuery(id+"F2.wireOp",EDGE,"E1211"),sQuery(id+"F2.wireOp",EDGE,"E1212"),sQuery(id+"F2.wireOp",EDGE,"E1213"),sQuery(id+"F2.wireOp",EDGE,"E1214"),sQuery(id+"F2.wireOp",EDGE,"E1215"),sQuery(id+"F2.wireOp",EDGE,"E1216"),sQuery(id+"F2.wireOp",EDGE,"E1217"),sQuery(id+"F2.wireOp",EDGE,"E1218"),sQuery(id+"F2.wireOp",EDGE,"E1219"),sQuery(id+"F2.wireOp",EDGE,"E1220"),sQuery(id+"F2.wireOp",EDGE,"E1221"),sQuery(id+"F2.wireOp",EDGE,"E1222"),sQuery(id+"F2.wireOp",EDGE,"E1223"),sQuery(id+"F2.wireOp",EDGE,"E1224"),sQuery(id+"F2.wireOp",EDGE,"E1225"),sQuery(id+"F2.wireOp",EDGE,"E1226"),sQuery(id+"F2.wireOp",EDGE,"E1227"),sQuery(id+"F2.wireOp",EDGE,"E1228"),sQuery(id+"F2.wireOp",EDGE,"E1229"),sQuery(id+"F2.wireOp",EDGE,"E1230"),sQuery(id+"F2.wireOp",EDGE,"E1231"),sQuery(id+"F2.wireOp",EDGE,"E1232"),sQuery(id+"F2.wireOp",EDGE,"E1233"),sQuery(id+"F2.wireOp",EDGE,"E1234"),sQuery(id+"F2.wireOp",EDGE,"E1235"),sQuery(id+"F2.wireOp",EDGE,"E1236"),sQuery(id+"F2.wireOp",EDGE,"E1237"),sQuery(id+"F2.wireOp",EDGE,"E1238"),sQuery(id+"F2.wireOp",EDGE,"E1239"),sQuery(id+"F2.wireOp",EDGE,"E1240"),sQuery(id+"F2.wireOp",EDGE,"E1241"),sQuery(id+"F2.wireOp",EDGE,"E1242"),sQuery(id+"F2.wireOp",EDGE,"E1243"),sQuery(id+"F2.wireOp",EDGE,"E1244"),sQuery(id+"F2.wireOp",EDGE,"E1245"),sQuery(id+"F2.wireOp",EDGE,"E1246"),sQuery(id+"F2.wireOp",EDGE,"E1247"),sQuery(id+"F2.wireOp",EDGE,"E1248"),sQuery(id+"F2.wireOp",EDGE,"E1249"),sQuery(id+"F2.wireOp",EDGE,"E1250"),sQuery(id+"F2.wireOp",EDGE,"E1251"),sQuery(id+"F2.wireOp",EDGE,"E1252"),sQuery(id+"F2.wireOp",EDGE,"E1253"),sQuery(id+"F2.wireOp",EDGE,"E1254"),sQuery(id+"F2.wireOp",EDGE,"E1255"),sQuery(id+"F2.wireOp",EDGE,"E1256"),sQuery(id+"F2.wireOp",EDGE,"E1257"),sQuery(id+"F2.wireOp",EDGE,"E1258"),sQuery(id+"F2.wireOp",EDGE,"E1259"),sQuery(id+"F2.wireOp",EDGE,"E1260"),sQuery(id+"F2.wireOp",EDGE,"E1261"),sQuery(id+"F2.wireOp",EDGE,"E1262"),sQuery(id+"F2.wireOp",EDGE,"E1263"),sQuery(id+"F2.wireOp",EDGE,"E1264"),sQuery(id+"F2.wireOp",EDGE,"E1265"),sQuery(id+"F2.wireOp",EDGE,"E1266"),sQuery(id+"F2.wireOp",EDGE,"E1267"),sQuery(id+"F2.wireOp",EDGE,"E1268"),sQuery(id+"F2.wireOp",EDGE,"E1269"),sQuery(id+"F2.wireOp",EDGE,"E1270"),sQuery(id+"F2.wireOp",EDGE,"E1271"),sQuery(id+"F2.wireOp",EDGE,"E1272"),sQuery(id+"F2.wireOp",EDGE,"E1273"),sQuery(id+"F2.wireOp",EDGE,"E1274"),sQuery(id+"F2.wireOp",EDGE,"E1275"),sQuery(id+"F2.wireOp",EDGE,"E1276"),sQuery(id+"F2.wireOp",EDGE,"E1277"),sQuery(id+"F2.wireOp",EDGE,"E1278"),sQuery(id+"F2.wireOp",EDGE,"E1279"),sQuery(id+"F2.wireOp",EDGE,"E1280"),sQuery(id+"F2.wireOp",EDGE,"E1281"),sQuery(id+"F2.wireOp",EDGE,"E1282"),sQuery(id+"F2.wireOp",EDGE,"E1283"),sQuery(id+"F2.wireOp",EDGE,"E1284"),sQuery(id+"F2.wireOp",EDGE,"E1285"),sQuery(id+"F2.wireOp",EDGE,"E1286"),sQuery(id+"F2.wireOp",EDGE,"E1287"),sQuery(id+"F2.wireOp",EDGE,"E1288"),sQuery(id+"F2.wireOp",EDGE,"E1289"),sQuery(id+"F2.wireOp",EDGE,"E1290"),sQuery(id+"F2.wireOp",EDGE,"E1291"),sQuery(id+"F2.wireOp",EDGE,"E1292"),sQuery(id+"F2.wireOp",EDGE,"E1293"),sQuery(id+"F2.wireOp",EDGE,"E1294"),sQuery(id+"F2.wireOp",EDGE,"E1295"),sQuery(id+"F2.wireOp",EDGE,"E1296"),sQuery(id+"F2.wireOp",EDGE,"E1297"),sQuery(id+"F2.wireOp",EDGE,"E1298"),sQuery(id+"F2.wireOp",EDGE,"E1299"),sQuery(id+"F2.wireOp",EDGE,"E1300"),sQuery(id+"F2.wireOp",EDGE,"E1301"),sQuery(id+"F2.wireOp",EDGE,"E1302"),sQuery(id+"F2.wireOp",EDGE,"E1303"),sQuery(id+"F2.wireOp",EDGE,"E1304"),sQuery(id+"F2.wireOp",EDGE,"E1305"),sQuery(id+"F2.wireOp",EDGE,"E1306"),sQuery(id+"F2.wireOp",EDGE,"E1307"),sQuery(id+"F2.wireOp",EDGE,"E1308"),sQuery(id+"F2.wireOp",EDGE,"E1309"),sQuery(id+"F2.wireOp",EDGE,"E1310"),sQuery(id+"F2.wireOp",EDGE,"E1311"),sQuery(id+"F2.wireOp",EDGE,"E1312"),sQuery(id+"F2.wireOp",EDGE,"E1313"),sQuery(id+"F2.wireOp",EDGE,"E1314"),sQuery(id+"F2.wireOp",EDGE,"E1315"),sQuery(id+"F2.wireOp",EDGE,"E1316"),sQuery(id+"F2.wireOp",EDGE,"E1317"),sQuery(id+"F2.wireOp",EDGE,"E1318"),sQuery(id+"F2.wireOp",EDGE,"E1319"),sQuery(id+"F2.wireOp",EDGE,"E1320"),sQuery(id+"F2.wireOp",EDGE,"E1321"),sQuery(id+"F2.wireOp",EDGE,"E1322"),sQuery(id+"F2.wireOp",EDGE,"E1323"),sQuery(id+"F2.wireOp",EDGE,"E1324"),sQuery(id+"F2.wireOp",EDGE,"E1325"),sQuery(id+"F2.wireOp",EDGE,"E1326"),sQuery(id+"F2.wireOp",EDGE,"E1327"),sQuery(id+"F2.wireOp",EDGE,"E1328"),sQuery(id+"F2.wireOp",EDGE,"E1329"),sQuery(id+"F2.wireOp",EDGE,"E1330"),sQuery(id+"F2.wireOp",EDGE,"E1331"),sQuery(id+"F2.wireOp",EDGE,"E1332"),sQuery(id+"F2.wireOp",EDGE,"E1333"),sQuery(id+"F2.wireOp",EDGE,"E1334"),sQuery(id+"F2.wireOp",EDGE,"E1335"),sQuery(id+"F2.wireOp",EDGE,"E1336"),sQuery(id+"F2.wireOp",EDGE,"E1337"),sQuery(id+"F2.wireOp",EDGE,"E1338"),sQuery(id+"F2.wireOp",EDGE,"E1339"),sQuery(id+"F2.wireOp",EDGE,"E1340"),sQuery(id+"F2.wireOp",EDGE,"E1341"),sQuery(id+"F2.wireOp",EDGE,"E1342"),sQuery(id+"F2.wireOp",EDGE,"E1343"),sQuery(id+"F2.wireOp",EDGE,"E1344"),sQuery(id+"F2.wireOp",EDGE,"E1345"),sQuery(id+"F2.wireOp",EDGE,"E1346"),sQuery(id+"F2.wireOp",EDGE,"E1347"),sQuery(id+"F2.wireOp",EDGE,"E1348"),sQuery(id+"F2.wireOp",EDGE,"E1349"),sQuery(id+"F2.wireOp",EDGE,"E1350"),sQuery(id+"F2.wireOp",EDGE,"E1351"),sQuery(id+"F2.wireOp",EDGE,"E1352"),sQuery(id+"F2.wireOp",EDGE,"E1353"),sQuery(id+"F2.wireOp",EDGE,"E1354"),sQuery(id+"F2.wireOp",EDGE,"E1355"),sQuery(id+"F2.wireOp",EDGE,"E1356"),sQuery(id+"F2.wireOp",EDGE,"E1357"),sQuery(id+"F2.wireOp",EDGE,"E1358"),sQuery(id+"F2.wireOp",EDGE,"E1359"),sQuery(id+"F2.wireOp",EDGE,"E1360"),sQuery(id+"F2.wireOp",EDGE,"E1361"),sQuery(id+"F2.wireOp",EDGE,"E1362"),sQuery(id+"F2.wireOp",EDGE,"E1363"),sQuery(id+"F2.wireOp",EDGE,"E1364"),sQuery(id+"F2.wireOp",EDGE,"E1365"),sQuery(id+"F2.wireOp",EDGE,"E1366"),sQuery(id+"F2.wireOp",EDGE,"E1367"),sQuery(id+"F2.wireOp",EDGE,"E1368"),sQuery(id+"F2.wireOp",EDGE,"E1369"),sQuery(id+"F2.wireOp",EDGE,"E1370"),sQuery(id+"F2.wireOp",EDGE,"E1371"),sQuery(id+"F2.wireOp",EDGE,"E1372"),sQuery(id+"F2.wireOp",EDGE,"E1373"),sQuery(id+"F2.wireOp",EDGE,"E1374"),sQuery(id+"F2.wireOp",EDGE,"E1375"),sQuery(id+"F2.wireOp",EDGE,"E1376"),sQuery(id+"F2.wireOp",EDGE,"E1377"),sQuery(id+"F2.wireOp",EDGE,"E1378"),sQuery(id+"F2.wireOp",EDGE,"E1379"),sQuery(id+"F2.wireOp",EDGE,"E1380"),sQuery(id+"F2.wireOp",EDGE,"E1381"),sQuery(id+"F2.wireOp",EDGE,"E1382"),sQuery(id+"F2.wireOp",EDGE,"E1383"),sQuery(id+"F2.wireOp",EDGE,"E1384"),sQuery(id+"F2.wireOp",EDGE,"E1385"),sQuery(id+"F2.wireOp",EDGE,"E1386"),sQuery(id+"F2.wireOp",EDGE,"E1387"),sQuery(id+"F2.wireOp",EDGE,"E1388"),sQuery(id+"F2.wireOp",EDGE,"E1389"),sQuery(id+"F2.wireOp",EDGE,"E1390"),sQuery(id+"F2.wireOp",EDGE,"E1391"),sQuery(id+"F2.wireOp",EDGE,"E1392"),sQuery(id+"F2.wireOp",EDGE,"E1393"),sQuery(id+"F2.wireOp",EDGE,"E1394"),sQuery(id+"F2.wireOp",EDGE,"E1395"),sQuery(id+"F2.wireOp",EDGE,"E1396"),sQuery(id+"F2.wireOp",EDGE,"E1397"),sQuery(id+"F2.wireOp",EDGE,"E1398"),sQuery(id+"F2.wireOp",EDGE,"E1399"),sQuery(id+"F2.wireOp",EDGE,"E1400"),sQuery(id+"F2.wireOp",EDGE,"E1401"),sQuery(id+"F2.wireOp",EDGE,"E1402"),sQuery(id+"F2.wireOp",EDGE,"E1403"),sQuery(id+"F2.wireOp",EDGE,"E1404"),sQuery(id+"F2.wireOp",EDGE,"E1405"),sQuery(id+"F2.wireOp",EDGE,"E1406"),sQuery(id+"F2.wireOp",EDGE,"E1407"),sQuery(id+"F2.wireOp",EDGE,"E1408"),sQuery(id+"F2.wireOp",EDGE,"E1409"),sQuery(id+"F2.wireOp",EDGE,"E1410"),sQuery(id+"F2.wireOp",EDGE,"E1411"),sQuery(id+"F2.wireOp",EDGE,"E1412"),sQuery(id+"F2.wireOp",EDGE,"E1413"),sQuery(id+"F2.wireOp",EDGE,"E1414"),sQuery(id+"F2.wireOp",EDGE,"E1415"),sQuery(id+"F2.wireOp",EDGE,"E1416"),sQuery(id+"F2.wireOp",EDGE,"E1417"),sQuery(id+"F2.wireOp",EDGE,"E1418"),sQuery(id+"F2.wireOp",EDGE,"E1419"),sQuery(id+"F2.wireOp",EDGE,"E1420"),sQuery(id+"F2.wireOp",EDGE,"E1421"),sQuery(id+"F2.wireOp",EDGE,"E1422"),sQuery(id+"F2.wireOp",EDGE,"E1423"),sQuery(id+"F2.wireOp",EDGE,"E1424"),sQuery(id+"F2.wireOp",EDGE,"E1425"),sQuery(id+"F2.wireOp",EDGE,"E1426"),sQuery(id+"F2.wireOp",EDGE,"E1427"),sQuery(id+"F2.wireOp",EDGE,"E1428"),sQuery(id+"F2.wireOp",EDGE,"E1429"),sQuery(id+"F2.wireOp",EDGE,"E1430"),sQuery(id+"F2.wireOp",EDGE,"E1431"),sQuery(id+"F2.wireOp",EDGE,"E1432"),sQuery(id+"F2.wireOp",EDGE,"E1433"),sQuery(id+"F2.wireOp",EDGE,"E1434"),sQuery(id+"F2.wireOp",EDGE,"E1435"),sQuery(id+"F2.wireOp",EDGE,"E1436"),sQuery(id+"F2.wireOp",EDGE,"E1437"),sQuery(id+"F2.wireOp",EDGE,"E1438"),sQuery(id+"F2.wireOp",EDGE,"E1439"),sQuery(id+"F2.wireOp",EDGE,"E1440"),sQuery(id+"F2.wireOp",EDGE,"E1441"),sQuery(id+"F2.wireOp",EDGE,"E1442"),sQuery(id+"F2.wireOp",EDGE,"E1443"),sQuery(id+"F2.wireOp",EDGE,"E1444"),sQuery(id+"F2.wireOp",EDGE,"E1445"),sQuery(id+"F2.wireOp",EDGE,"E1446"),sQuery(id+"F2.wireOp",EDGE,"E1447"),sQuery(id+"F2.wireOp",EDGE,"E1448"),sQuery(id+"F2.wireOp",EDGE,"E1449"),sQuery(id+"F2.wireOp",EDGE,"E1450"),sQuery(id+"F2.wireOp",EDGE,"E1451"),sQuery(id+"F2.wireOp",EDGE,"E1452"),sQuery(id+"F2.wireOp",EDGE,"E1453"),sQuery(id+"F2.wireOp",EDGE,"E1454"),sQuery(id+"F2.wireOp",EDGE,"E1455"),sQuery(id+"F2.wireOp",EDGE,"E1456"),sQuery(id+"F2.wireOp",EDGE,"E1457"),sQuery(id+"F2.wireOp",EDGE,"E1458"),sQuery(id+"F2.wireOp",EDGE,"E1459"),sQuery(id+"F2.wireOp",EDGE,"E1460"),sQuery(id+"F2.wireOp",EDGE,"E1461"),sQuery(id+"F2.wireOp",EDGE,"E1462"),sQuery(id+"F2.wireOp",EDGE,"E1463"),sQuery(id+"F2.wireOp",EDGE,"E1464"),sQuery(id+"F2.wireOp",EDGE,"E1465"),sQuery(id+"F2.wireOp",EDGE,"E1466"),sQuery(id+"F2.wireOp",EDGE,"E1467"),sQuery(id+"F2.wireOp",EDGE,"E1468"),sQuery(id+"F2.wireOp",EDGE,"E1469"),sQuery(id+"F2.wireOp",EDGE,"E1470"),sQuery(id+"F2.wireOp",EDGE,"E1471"),sQuery(id+"F2.wireOp",EDGE,"E1472"),sQuery(id+"F2.wireOp",EDGE,"E1473"),sQuery(id+"F2.wireOp",EDGE,"E1474")])]});
            var Q1;
            Q1=sQuery(id+"F1.wireOp",EDGE,"E15");
            transform(context, id + "F7", {"entities" : qUnion([Q0]), "transformType" : TransformType.ROTATION, "transformAxis" : qUnion([Q1]), "angle" : 30 * degree, "oppositeDirection" : true, "makeCopy" : true});
        }
        {
            var Q0;
            Q0=makeQuery(id+"F7.opPattern","COPY",BODY,{"derivedFrom":makeQuery(id+"F3.opExtrude","SWEPT_BODY",BODY,{"disambiguationData":[OSD([sQuery(id+"F2.wireOp",EDGE,"E16"),sQuery(id+"F2.wireOp",EDGE,"E17"),sQuery(id+"F2.wireOp",EDGE,"E18"),sQuery(id+"F2.wireOp",EDGE,"E19"),sQuery(id+"F2.wireOp",EDGE,"E20"),sQuery(id+"F2.wireOp",EDGE,"E21"),sQuery(id+"F2.wireOp",EDGE,"E22"),sQuery(id+"F2.wireOp",EDGE,"E23"),sQuery(id+"F2.wireOp",EDGE,"E24"),sQuery(id+"F2.wireOp",EDGE,"E25"),sQuery(id+"F2.wireOp",EDGE,"E26"),sQuery(id+"F2.wireOp",EDGE,"E27"),sQuery(id+"F2.wireOp",EDGE,"E28"),sQuery(id+"F2.wireOp",EDGE,"E29"),sQuery(id+"F2.wireOp",EDGE,"E30"),sQuery(id+"F2.wireOp",EDGE,"E31"),sQuery(id+"F2.wireOp",EDGE,"E32"),sQuery(id+"F2.wireOp",EDGE,"E33"),sQuery(id+"F2.wireOp",EDGE,"E34"),sQuery(id+"F2.wireOp",EDGE,"E35"),sQuery(id+"F2.wireOp",EDGE,"E36"),sQuery(id+"F2.wireOp",EDGE,"E37"),sQuery(id+"F2.wireOp",EDGE,"E38"),sQuery(id+"F2.wireOp",EDGE,"E39"),sQuery(id+"F2.wireOp",EDGE,"E40"),sQuery(id+"F2.wireOp",EDGE,"E41"),sQuery(id+"F2.wireOp",EDGE,"E42"),sQuery(id+"F2.wireOp",EDGE,"E43"),sQuery(id+"F2.wireOp",EDGE,"E44"),sQuery(id+"F2.wireOp",EDGE,"E45"),sQuery(id+"F2.wireOp",EDGE,"E46"),sQuery(id+"F2.wireOp",EDGE,"E47"),sQuery(id+"F2.wireOp",EDGE,"E48"),sQuery(id+"F2.wireOp",EDGE,"E49"),sQuery(id+"F2.wireOp",EDGE,"E50"),sQuery(id+"F2.wireOp",EDGE,"E51"),sQuery(id+"F2.wireOp",EDGE,"E52"),sQuery(id+"F2.wireOp",EDGE,"E53"),sQuery(id+"F2.wireOp",EDGE,"E54"),sQuery(id+"F2.wireOp",EDGE,"E55"),sQuery(id+"F2.wireOp",EDGE,"E56"),sQuery(id+"F2.wireOp",EDGE,"E57"),sQuery(id+"F2.wireOp",EDGE,"E58"),sQuery(id+"F2.wireOp",EDGE,"E59"),sQuery(id+"F2.wireOp",EDGE,"E60"),sQuery(id+"F2.wireOp",EDGE,"E61"),sQuery(id+"F2.wireOp",EDGE,"E62"),sQuery(id+"F2.wireOp",EDGE,"E63"),sQuery(id+"F2.wireOp",EDGE,"E64"),sQuery(id+"F2.wireOp",EDGE,"E65"),sQuery(id+"F2.wireOp",EDGE,"E66"),sQuery(id+"F2.wireOp",EDGE,"E67"),sQuery(id+"F2.wireOp",EDGE,"E68"),sQuery(id+"F2.wireOp",EDGE,"E69"),sQuery(id+"F2.wireOp",EDGE,"E70"),sQuery(id+"F2.wireOp",EDGE,"E71"),sQuery(id+"F2.wireOp",EDGE,"E72"),sQuery(id+"F2.wireOp",EDGE,"E73"),sQuery(id+"F2.wireOp",EDGE,"E74"),sQuery(id+"F2.wireOp",EDGE,"E75"),sQuery(id+"F2.wireOp",EDGE,"E76"),sQuery(id+"F2.wireOp",EDGE,"E77"),sQuery(id+"F2.wireOp",EDGE,"E78"),sQuery(id+"F2.wireOp",EDGE,"E79"),sQuery(id+"F2.wireOp",EDGE,"E80"),sQuery(id+"F2.wireOp",EDGE,"E81"),sQuery(id+"F2.wireOp",EDGE,"E82"),sQuery(id+"F2.wireOp",EDGE,"E83"),sQuery(id+"F2.wireOp",EDGE,"E84"),sQuery(id+"F2.wireOp",EDGE,"E85"),sQuery(id+"F2.wireOp",EDGE,"E86"),sQuery(id+"F2.wireOp",EDGE,"E87"),sQuery(id+"F2.wireOp",EDGE,"E88"),sQuery(id+"F2.wireOp",EDGE,"E89"),sQuery(id+"F2.wireOp",EDGE,"E90"),sQuery(id+"F2.wireOp",EDGE,"E91"),sQuery(id+"F2.wireOp",EDGE,"E92"),sQuery(id+"F2.wireOp",EDGE,"E93"),sQuery(id+"F2.wireOp",EDGE,"E94"),sQuery(id+"F2.wireOp",EDGE,"E95"),sQuery(id+"F2.wireOp",EDGE,"E96"),sQuery(id+"F2.wireOp",EDGE,"E97"),sQuery(id+"F2.wireOp",EDGE,"E98"),sQuery(id+"F2.wireOp",EDGE,"E99"),sQuery(id+"F2.wireOp",EDGE,"E100"),sQuery(id+"F2.wireOp",EDGE,"E101"),sQuery(id+"F2.wireOp",EDGE,"E102"),sQuery(id+"F2.wireOp",EDGE,"E103"),sQuery(id+"F2.wireOp",EDGE,"E104"),sQuery(id+"F2.wireOp",EDGE,"E105"),sQuery(id+"F2.wireOp",EDGE,"E106"),sQuery(id+"F2.wireOp",EDGE,"E107"),sQuery(id+"F2.wireOp",EDGE,"E108"),sQuery(id+"F2.wireOp",EDGE,"E109"),sQuery(id+"F2.wireOp",EDGE,"E110"),sQuery(id+"F2.wireOp",EDGE,"E111"),sQuery(id+"F2.wireOp",EDGE,"E112"),sQuery(id+"F2.wireOp",EDGE,"E113"),sQuery(id+"F2.wireOp",EDGE,"E114"),sQuery(id+"F2.wireOp",EDGE,"E115"),sQuery(id+"F2.wireOp",EDGE,"E116"),sQuery(id+"F2.wireOp",EDGE,"E117"),sQuery(id+"F2.wireOp",EDGE,"E118"),sQuery(id+"F2.wireOp",EDGE,"E119"),sQuery(id+"F2.wireOp",EDGE,"E120"),sQuery(id+"F2.wireOp",EDGE,"E121"),sQuery(id+"F2.wireOp",EDGE,"E122"),sQuery(id+"F2.wireOp",EDGE,"E123"),sQuery(id+"F2.wireOp",EDGE,"E124"),sQuery(id+"F2.wireOp",EDGE,"E125"),sQuery(id+"F2.wireOp",EDGE,"E126"),sQuery(id+"F2.wireOp",EDGE,"E127"),sQuery(id+"F2.wireOp",EDGE,"E128"),sQuery(id+"F2.wireOp",EDGE,"E129"),sQuery(id+"F2.wireOp",EDGE,"E130"),sQuery(id+"F2.wireOp",EDGE,"E131"),sQuery(id+"F2.wireOp",EDGE,"E132"),sQuery(id+"F2.wireOp",EDGE,"E133"),sQuery(id+"F2.wireOp",EDGE,"E134"),sQuery(id+"F2.wireOp",EDGE,"E135"),sQuery(id+"F2.wireOp",EDGE,"E136"),sQuery(id+"F2.wireOp",EDGE,"E137"),sQuery(id+"F2.wireOp",EDGE,"E138"),sQuery(id+"F2.wireOp",EDGE,"E139"),sQuery(id+"F2.wireOp",EDGE,"E140"),sQuery(id+"F2.wireOp",EDGE,"E141"),sQuery(id+"F2.wireOp",EDGE,"E142"),sQuery(id+"F2.wireOp",EDGE,"E143"),sQuery(id+"F2.wireOp",EDGE,"E144"),sQuery(id+"F2.wireOp",EDGE,"E145"),sQuery(id+"F2.wireOp",EDGE,"E146"),sQuery(id+"F2.wireOp",EDGE,"E147"),sQuery(id+"F2.wireOp",EDGE,"E148"),sQuery(id+"F2.wireOp",EDGE,"E149"),sQuery(id+"F2.wireOp",EDGE,"E150"),sQuery(id+"F2.wireOp",EDGE,"E151"),sQuery(id+"F2.wireOp",EDGE,"E152"),sQuery(id+"F2.wireOp",EDGE,"E153"),sQuery(id+"F2.wireOp",EDGE,"E154"),sQuery(id+"F2.wireOp",EDGE,"E155"),sQuery(id+"F2.wireOp",EDGE,"E156"),sQuery(id+"F2.wireOp",EDGE,"E157"),sQuery(id+"F2.wireOp",EDGE,"E158"),sQuery(id+"F2.wireOp",EDGE,"E159"),sQuery(id+"F2.wireOp",EDGE,"E160"),sQuery(id+"F2.wireOp",EDGE,"E161"),sQuery(id+"F2.wireOp",EDGE,"E162"),sQuery(id+"F2.wireOp",EDGE,"E163"),sQuery(id+"F2.wireOp",EDGE,"E164"),sQuery(id+"F2.wireOp",EDGE,"E165"),sQuery(id+"F2.wireOp",EDGE,"E166"),sQuery(id+"F2.wireOp",EDGE,"E167"),sQuery(id+"F2.wireOp",EDGE,"E168"),sQuery(id+"F2.wireOp",EDGE,"E169"),sQuery(id+"F2.wireOp",EDGE,"E170"),sQuery(id+"F2.wireOp",EDGE,"E171"),sQuery(id+"F2.wireOp",EDGE,"E172"),sQuery(id+"F2.wireOp",EDGE,"E173"),sQuery(id+"F2.wireOp",EDGE,"E174"),sQuery(id+"F2.wireOp",EDGE,"E175"),sQuery(id+"F2.wireOp",EDGE,"E176"),sQuery(id+"F2.wireOp",EDGE,"E177"),sQuery(id+"F2.wireOp",EDGE,"E178"),sQuery(id+"F2.wireOp",EDGE,"E179"),sQuery(id+"F2.wireOp",EDGE,"E180"),sQuery(id+"F2.wireOp",EDGE,"E181"),sQuery(id+"F2.wireOp",EDGE,"E182"),sQuery(id+"F2.wireOp",EDGE,"E183"),sQuery(id+"F2.wireOp",EDGE,"E184"),sQuery(id+"F2.wireOp",EDGE,"E185"),sQuery(id+"F2.wireOp",EDGE,"E186"),sQuery(id+"F2.wireOp",EDGE,"E187"),sQuery(id+"F2.wireOp",EDGE,"E188"),sQuery(id+"F2.wireOp",EDGE,"E189"),sQuery(id+"F2.wireOp",EDGE,"E190"),sQuery(id+"F2.wireOp",EDGE,"E191"),sQuery(id+"F2.wireOp",EDGE,"E192"),sQuery(id+"F2.wireOp",EDGE,"E193"),sQuery(id+"F2.wireOp",EDGE,"E194"),sQuery(id+"F2.wireOp",EDGE,"E195"),sQuery(id+"F2.wireOp",EDGE,"E196"),sQuery(id+"F2.wireOp",EDGE,"E197"),sQuery(id+"F2.wireOp",EDGE,"E198"),sQuery(id+"F2.wireOp",EDGE,"E199"),sQuery(id+"F2.wireOp",EDGE,"E200"),sQuery(id+"F2.wireOp",EDGE,"E201"),sQuery(id+"F2.wireOp",EDGE,"E202"),sQuery(id+"F2.wireOp",EDGE,"E203"),sQuery(id+"F2.wireOp",EDGE,"E204"),sQuery(id+"F2.wireOp",EDGE,"E205"),sQuery(id+"F2.wireOp",EDGE,"E206"),sQuery(id+"F2.wireOp",EDGE,"E207"),sQuery(id+"F2.wireOp",EDGE,"E208"),sQuery(id+"F2.wireOp",EDGE,"E209"),sQuery(id+"F2.wireOp",EDGE,"E210"),sQuery(id+"F2.wireOp",EDGE,"E211"),sQuery(id+"F2.wireOp",EDGE,"E212"),sQuery(id+"F2.wireOp",EDGE,"E213"),sQuery(id+"F2.wireOp",EDGE,"E214"),sQuery(id+"F2.wireOp",EDGE,"E215"),sQuery(id+"F2.wireOp",EDGE,"E216"),sQuery(id+"F2.wireOp",EDGE,"E217"),sQuery(id+"F2.wireOp",EDGE,"E218"),sQuery(id+"F2.wireOp",EDGE,"E219"),sQuery(id+"F2.wireOp",EDGE,"E220"),sQuery(id+"F2.wireOp",EDGE,"E221"),sQuery(id+"F2.wireOp",EDGE,"E222"),sQuery(id+"F2.wireOp",EDGE,"E223"),sQuery(id+"F2.wireOp",EDGE,"E224"),sQuery(id+"F2.wireOp",EDGE,"E225"),sQuery(id+"F2.wireOp",EDGE,"E226"),sQuery(id+"F2.wireOp",EDGE,"E227"),sQuery(id+"F2.wireOp",EDGE,"E228"),sQuery(id+"F2.wireOp",EDGE,"E229"),sQuery(id+"F2.wireOp",EDGE,"E230"),sQuery(id+"F2.wireOp",EDGE,"E231"),sQuery(id+"F2.wireOp",EDGE,"E232"),sQuery(id+"F2.wireOp",EDGE,"E233"),sQuery(id+"F2.wireOp",EDGE,"E234"),sQuery(id+"F2.wireOp",EDGE,"E235"),sQuery(id+"F2.wireOp",EDGE,"E236"),sQuery(id+"F2.wireOp",EDGE,"E237"),sQuery(id+"F2.wireOp",EDGE,"E238"),sQuery(id+"F2.wireOp",EDGE,"E239"),sQuery(id+"F2.wireOp",EDGE,"E240"),sQuery(id+"F2.wireOp",EDGE,"E241"),sQuery(id+"F2.wireOp",EDGE,"E242"),sQuery(id+"F2.wireOp",EDGE,"E243"),sQuery(id+"F2.wireOp",EDGE,"E244"),sQuery(id+"F2.wireOp",EDGE,"E245"),sQuery(id+"F2.wireOp",EDGE,"E246"),sQuery(id+"F2.wireOp",EDGE,"E247"),sQuery(id+"F2.wireOp",EDGE,"E248"),sQuery(id+"F2.wireOp",EDGE,"E249"),sQuery(id+"F2.wireOp",EDGE,"E250"),sQuery(id+"F2.wireOp",EDGE,"E251"),sQuery(id+"F2.wireOp",EDGE,"E252"),sQuery(id+"F2.wireOp",EDGE,"E253"),sQuery(id+"F2.wireOp",EDGE,"E254"),sQuery(id+"F2.wireOp",EDGE,"E255"),sQuery(id+"F2.wireOp",EDGE,"E256"),sQuery(id+"F2.wireOp",EDGE,"E257"),sQuery(id+"F2.wireOp",EDGE,"E258"),sQuery(id+"F2.wireOp",EDGE,"E259"),sQuery(id+"F2.wireOp",EDGE,"E260"),sQuery(id+"F2.wireOp",EDGE,"E261"),sQuery(id+"F2.wireOp",EDGE,"E262"),sQuery(id+"F2.wireOp",EDGE,"E263"),sQuery(id+"F2.wireOp",EDGE,"E264"),sQuery(id+"F2.wireOp",EDGE,"E265"),sQuery(id+"F2.wireOp",EDGE,"E266"),sQuery(id+"F2.wireOp",EDGE,"E267"),sQuery(id+"F2.wireOp",EDGE,"E268"),sQuery(id+"F2.wireOp",EDGE,"E269"),sQuery(id+"F2.wireOp",EDGE,"E270"),sQuery(id+"F2.wireOp",EDGE,"E271"),sQuery(id+"F2.wireOp",EDGE,"E272"),sQuery(id+"F2.wireOp",EDGE,"E273"),sQuery(id+"F2.wireOp",EDGE,"E274"),sQuery(id+"F2.wireOp",EDGE,"E275"),sQuery(id+"F2.wireOp",EDGE,"E276"),sQuery(id+"F2.wireOp",EDGE,"E277"),sQuery(id+"F2.wireOp",EDGE,"E278"),sQuery(id+"F2.wireOp",EDGE,"E279"),sQuery(id+"F2.wireOp",EDGE,"E280"),sQuery(id+"F2.wireOp",EDGE,"E281"),sQuery(id+"F2.wireOp",EDGE,"E282"),sQuery(id+"F2.wireOp",EDGE,"E283"),sQuery(id+"F2.wireOp",EDGE,"E284"),sQuery(id+"F2.wireOp",EDGE,"E285"),sQuery(id+"F2.wireOp",EDGE,"E286"),sQuery(id+"F2.wireOp",EDGE,"E287"),sQuery(id+"F2.wireOp",EDGE,"E288"),sQuery(id+"F2.wireOp",EDGE,"E289"),sQuery(id+"F2.wireOp",EDGE,"E290"),sQuery(id+"F2.wireOp",EDGE,"E291"),sQuery(id+"F2.wireOp",EDGE,"E292"),sQuery(id+"F2.wireOp",EDGE,"E293"),sQuery(id+"F2.wireOp",EDGE,"E294"),sQuery(id+"F2.wireOp",EDGE,"E295"),sQuery(id+"F2.wireOp",EDGE,"E296"),sQuery(id+"F2.wireOp",EDGE,"E297"),sQuery(id+"F2.wireOp",EDGE,"E298"),sQuery(id+"F2.wireOp",EDGE,"E299"),sQuery(id+"F2.wireOp",EDGE,"E300"),sQuery(id+"F2.wireOp",EDGE,"E301"),sQuery(id+"F2.wireOp",EDGE,"E302"),sQuery(id+"F2.wireOp",EDGE,"E303"),sQuery(id+"F2.wireOp",EDGE,"E304"),sQuery(id+"F2.wireOp",EDGE,"E305"),sQuery(id+"F2.wireOp",EDGE,"E306"),sQuery(id+"F2.wireOp",EDGE,"E307"),sQuery(id+"F2.wireOp",EDGE,"E308"),sQuery(id+"F2.wireOp",EDGE,"E309"),sQuery(id+"F2.wireOp",EDGE,"E310"),sQuery(id+"F2.wireOp",EDGE,"E311"),sQuery(id+"F2.wireOp",EDGE,"E312"),sQuery(id+"F2.wireOp",EDGE,"E313"),sQuery(id+"F2.wireOp",EDGE,"E314"),sQuery(id+"F2.wireOp",EDGE,"E315"),sQuery(id+"F2.wireOp",EDGE,"E316"),sQuery(id+"F2.wireOp",EDGE,"E317"),sQuery(id+"F2.wireOp",EDGE,"E318"),sQuery(id+"F2.wireOp",EDGE,"E319"),sQuery(id+"F2.wireOp",EDGE,"E320"),sQuery(id+"F2.wireOp",EDGE,"E321"),sQuery(id+"F2.wireOp",EDGE,"E322"),sQuery(id+"F2.wireOp",EDGE,"E323"),sQuery(id+"F2.wireOp",EDGE,"E324"),sQuery(id+"F2.wireOp",EDGE,"E325"),sQuery(id+"F2.wireOp",EDGE,"E326"),sQuery(id+"F2.wireOp",EDGE,"E327"),sQuery(id+"F2.wireOp",EDGE,"E328"),sQuery(id+"F2.wireOp",EDGE,"E329"),sQuery(id+"F2.wireOp",EDGE,"E330"),sQuery(id+"F2.wireOp",EDGE,"E331"),sQuery(id+"F2.wireOp",EDGE,"E332"),sQuery(id+"F2.wireOp",EDGE,"E333"),sQuery(id+"F2.wireOp",EDGE,"E334"),sQuery(id+"F2.wireOp",EDGE,"E335"),sQuery(id+"F2.wireOp",EDGE,"E336"),sQuery(id+"F2.wireOp",EDGE,"E337"),sQuery(id+"F2.wireOp",EDGE,"E338"),sQuery(id+"F2.wireOp",EDGE,"E339"),sQuery(id+"F2.wireOp",EDGE,"E340"),sQuery(id+"F2.wireOp",EDGE,"E341"),sQuery(id+"F2.wireOp",EDGE,"E342"),sQuery(id+"F2.wireOp",EDGE,"E343"),sQuery(id+"F2.wireOp",EDGE,"E344"),sQuery(id+"F2.wireOp",EDGE,"E345"),sQuery(id+"F2.wireOp",EDGE,"E346"),sQuery(id+"F2.wireOp",EDGE,"E347"),sQuery(id+"F2.wireOp",EDGE,"E348"),sQuery(id+"F2.wireOp",EDGE,"E349"),sQuery(id+"F2.wireOp",EDGE,"E350"),sQuery(id+"F2.wireOp",EDGE,"E351"),sQuery(id+"F2.wireOp",EDGE,"E352"),sQuery(id+"F2.wireOp",EDGE,"E353"),sQuery(id+"F2.wireOp",EDGE,"E354"),sQuery(id+"F2.wireOp",EDGE,"E355"),sQuery(id+"F2.wireOp",EDGE,"E356"),sQuery(id+"F2.wireOp",EDGE,"E357"),sQuery(id+"F2.wireOp",EDGE,"E358"),sQuery(id+"F2.wireOp",EDGE,"E359"),sQuery(id+"F2.wireOp",EDGE,"E360"),sQuery(id+"F2.wireOp",EDGE,"E361"),sQuery(id+"F2.wireOp",EDGE,"E362"),sQuery(id+"F2.wireOp",EDGE,"E363"),sQuery(id+"F2.wireOp",EDGE,"E364"),sQuery(id+"F2.wireOp",EDGE,"E365"),sQuery(id+"F2.wireOp",EDGE,"E366"),sQuery(id+"F2.wireOp",EDGE,"E367"),sQuery(id+"F2.wireOp",EDGE,"E368"),sQuery(id+"F2.wireOp",EDGE,"E369"),sQuery(id+"F2.wireOp",EDGE,"E370"),sQuery(id+"F2.wireOp",EDGE,"E371"),sQuery(id+"F2.wireOp",EDGE,"E372"),sQuery(id+"F2.wireOp",EDGE,"E373"),sQuery(id+"F2.wireOp",EDGE,"E374"),sQuery(id+"F2.wireOp",EDGE,"E375"),sQuery(id+"F2.wireOp",EDGE,"E376"),sQuery(id+"F2.wireOp",EDGE,"E377"),sQuery(id+"F2.wireOp",EDGE,"E378"),sQuery(id+"F2.wireOp",EDGE,"E379"),sQuery(id+"F2.wireOp",EDGE,"E380"),sQuery(id+"F2.wireOp",EDGE,"E381"),sQuery(id+"F2.wireOp",EDGE,"E382"),sQuery(id+"F2.wireOp",EDGE,"E383"),sQuery(id+"F2.wireOp",EDGE,"E384"),sQuery(id+"F2.wireOp",EDGE,"E385"),sQuery(id+"F2.wireOp",EDGE,"E386"),sQuery(id+"F2.wireOp",EDGE,"E387"),sQuery(id+"F2.wireOp",EDGE,"E388"),sQuery(id+"F2.wireOp",EDGE,"E389"),sQuery(id+"F2.wireOp",EDGE,"E390"),sQuery(id+"F2.wireOp",EDGE,"E391"),sQuery(id+"F2.wireOp",EDGE,"E392"),sQuery(id+"F2.wireOp",EDGE,"E393"),sQuery(id+"F2.wireOp",EDGE,"E394"),sQuery(id+"F2.wireOp",EDGE,"E395"),sQuery(id+"F2.wireOp",EDGE,"E396"),sQuery(id+"F2.wireOp",EDGE,"E397"),sQuery(id+"F2.wireOp",EDGE,"E398"),sQuery(id+"F2.wireOp",EDGE,"E399"),sQuery(id+"F2.wireOp",EDGE,"E400"),sQuery(id+"F2.wireOp",EDGE,"E401"),sQuery(id+"F2.wireOp",EDGE,"E402"),sQuery(id+"F2.wireOp",EDGE,"E403"),sQuery(id+"F2.wireOp",EDGE,"E404"),sQuery(id+"F2.wireOp",EDGE,"E405"),sQuery(id+"F2.wireOp",EDGE,"E406"),sQuery(id+"F2.wireOp",EDGE,"E407"),sQuery(id+"F2.wireOp",EDGE,"E408"),sQuery(id+"F2.wireOp",EDGE,"E409"),sQuery(id+"F2.wireOp",EDGE,"E410"),sQuery(id+"F2.wireOp",EDGE,"E411"),sQuery(id+"F2.wireOp",EDGE,"E412"),sQuery(id+"F2.wireOp",EDGE,"E413"),sQuery(id+"F2.wireOp",EDGE,"E414"),sQuery(id+"F2.wireOp",EDGE,"E415"),sQuery(id+"F2.wireOp",EDGE,"E416"),sQuery(id+"F2.wireOp",EDGE,"E417"),sQuery(id+"F2.wireOp",EDGE,"E418"),sQuery(id+"F2.wireOp",EDGE,"E419"),sQuery(id+"F2.wireOp",EDGE,"E420"),sQuery(id+"F2.wireOp",EDGE,"E421"),sQuery(id+"F2.wireOp",EDGE,"E422"),sQuery(id+"F2.wireOp",EDGE,"E423"),sQuery(id+"F2.wireOp",EDGE,"E424"),sQuery(id+"F2.wireOp",EDGE,"E425"),sQuery(id+"F2.wireOp",EDGE,"E426"),sQuery(id+"F2.wireOp",EDGE,"E427"),sQuery(id+"F2.wireOp",EDGE,"E428"),sQuery(id+"F2.wireOp",EDGE,"E429"),sQuery(id+"F2.wireOp",EDGE,"E430"),sQuery(id+"F2.wireOp",EDGE,"E431"),sQuery(id+"F2.wireOp",EDGE,"E432"),sQuery(id+"F2.wireOp",EDGE,"E433"),sQuery(id+"F2.wireOp",EDGE,"E434"),sQuery(id+"F2.wireOp",EDGE,"E435"),sQuery(id+"F2.wireOp",EDGE,"E436"),sQuery(id+"F2.wireOp",EDGE,"E437"),sQuery(id+"F2.wireOp",EDGE,"E438"),sQuery(id+"F2.wireOp",EDGE,"E439"),sQuery(id+"F2.wireOp",EDGE,"E440"),sQuery(id+"F2.wireOp",EDGE,"E441"),sQuery(id+"F2.wireOp",EDGE,"E442"),sQuery(id+"F2.wireOp",EDGE,"E443"),sQuery(id+"F2.wireOp",EDGE,"E444"),sQuery(id+"F2.wireOp",EDGE,"E445"),sQuery(id+"F2.wireOp",EDGE,"E446"),sQuery(id+"F2.wireOp",EDGE,"E447"),sQuery(id+"F2.wireOp",EDGE,"E447"),sQuery(id+"F2.wireOp",EDGE,"E447"),sQuery(id+"F2.wireOp",EDGE,"E448"),sQuery(id+"F2.wireOp",EDGE,"E449"),sQuery(id+"F2.wireOp",EDGE,"E450"),sQuery(id+"F2.wireOp",EDGE,"E451"),sQuery(id+"F2.wireOp",EDGE,"E452"),sQuery(id+"F2.wireOp",EDGE,"E453"),sQuery(id+"F2.wireOp",EDGE,"E454"),sQuery(id+"F2.wireOp",EDGE,"E455"),sQuery(id+"F2.wireOp",EDGE,"E456"),sQuery(id+"F2.wireOp",EDGE,"E457"),sQuery(id+"F2.wireOp",EDGE,"E458"),sQuery(id+"F2.wireOp",EDGE,"E459"),sQuery(id+"F2.wireOp",EDGE,"E460"),sQuery(id+"F2.wireOp",EDGE,"E461"),sQuery(id+"F2.wireOp",EDGE,"E462"),sQuery(id+"F2.wireOp",EDGE,"E463"),sQuery(id+"F2.wireOp",EDGE,"E464"),sQuery(id+"F2.wireOp",EDGE,"E465"),sQuery(id+"F2.wireOp",EDGE,"E466"),sQuery(id+"F2.wireOp",EDGE,"E467"),sQuery(id+"F2.wireOp",EDGE,"E468"),sQuery(id+"F2.wireOp",EDGE,"E469"),sQuery(id+"F2.wireOp",EDGE,"E470"),sQuery(id+"F2.wireOp",EDGE,"E471"),sQuery(id+"F2.wireOp",EDGE,"E472"),sQuery(id+"F2.wireOp",EDGE,"E473"),sQuery(id+"F2.wireOp",EDGE,"E474"),sQuery(id+"F2.wireOp",EDGE,"E475"),sQuery(id+"F2.wireOp",EDGE,"E476"),sQuery(id+"F2.wireOp",EDGE,"E477"),sQuery(id+"F2.wireOp",EDGE,"E478"),sQuery(id+"F2.wireOp",EDGE,"E479"),sQuery(id+"F2.wireOp",EDGE,"E480"),sQuery(id+"F2.wireOp",EDGE,"E481"),sQuery(id+"F2.wireOp",EDGE,"E482"),sQuery(id+"F2.wireOp",EDGE,"E483"),sQuery(id+"F2.wireOp",EDGE,"E484"),sQuery(id+"F2.wireOp",EDGE,"E485"),sQuery(id+"F2.wireOp",EDGE,"E486"),sQuery(id+"F2.wireOp",EDGE,"E487"),sQuery(id+"F2.wireOp",EDGE,"E488"),sQuery(id+"F2.wireOp",EDGE,"E489"),sQuery(id+"F2.wireOp",EDGE,"E490"),sQuery(id+"F2.wireOp",EDGE,"E491"),sQuery(id+"F2.wireOp",EDGE,"E492"),sQuery(id+"F2.wireOp",EDGE,"E493"),sQuery(id+"F2.wireOp",EDGE,"E494"),sQuery(id+"F2.wireOp",EDGE,"E495"),sQuery(id+"F2.wireOp",EDGE,"E496"),sQuery(id+"F2.wireOp",EDGE,"E497"),sQuery(id+"F2.wireOp",EDGE,"E498"),sQuery(id+"F2.wireOp",EDGE,"E499"),sQuery(id+"F2.wireOp",EDGE,"E500"),sQuery(id+"F2.wireOp",EDGE,"E501"),sQuery(id+"F2.wireOp",EDGE,"E502"),sQuery(id+"F2.wireOp",EDGE,"E503"),sQuery(id+"F2.wireOp",EDGE,"E504"),sQuery(id+"F2.wireOp",EDGE,"E505"),sQuery(id+"F2.wireOp",EDGE,"E506"),sQuery(id+"F2.wireOp",EDGE,"E507"),sQuery(id+"F2.wireOp",EDGE,"E508"),sQuery(id+"F2.wireOp",EDGE,"E509"),sQuery(id+"F2.wireOp",EDGE,"E510"),sQuery(id+"F2.wireOp",EDGE,"E511"),sQuery(id+"F2.wireOp",EDGE,"E512"),sQuery(id+"F2.wireOp",EDGE,"E513"),sQuery(id+"F2.wireOp",EDGE,"E514"),sQuery(id+"F2.wireOp",EDGE,"E515"),sQuery(id+"F2.wireOp",EDGE,"E516"),sQuery(id+"F2.wireOp",EDGE,"E517"),sQuery(id+"F2.wireOp",EDGE,"E518"),sQuery(id+"F2.wireOp",EDGE,"E519"),sQuery(id+"F2.wireOp",EDGE,"E520"),sQuery(id+"F2.wireOp",EDGE,"E521"),sQuery(id+"F2.wireOp",EDGE,"E522"),sQuery(id+"F2.wireOp",EDGE,"E523"),sQuery(id+"F2.wireOp",EDGE,"E524"),sQuery(id+"F2.wireOp",EDGE,"E525"),sQuery(id+"F2.wireOp",EDGE,"E526"),sQuery(id+"F2.wireOp",EDGE,"E527"),sQuery(id+"F2.wireOp",EDGE,"E528"),sQuery(id+"F2.wireOp",EDGE,"E529"),sQuery(id+"F2.wireOp",EDGE,"E530"),sQuery(id+"F2.wireOp",EDGE,"E531"),sQuery(id+"F2.wireOp",EDGE,"E532"),sQuery(id+"F2.wireOp",EDGE,"E533"),sQuery(id+"F2.wireOp",EDGE,"E534"),sQuery(id+"F2.wireOp",EDGE,"E535"),sQuery(id+"F2.wireOp",EDGE,"E536"),sQuery(id+"F2.wireOp",EDGE,"E537"),sQuery(id+"F2.wireOp",EDGE,"E538"),sQuery(id+"F2.wireOp",EDGE,"E539"),sQuery(id+"F2.wireOp",EDGE,"E540"),sQuery(id+"F2.wireOp",EDGE,"E541"),sQuery(id+"F2.wireOp",EDGE,"E542"),sQuery(id+"F2.wireOp",EDGE,"E543"),sQuery(id+"F2.wireOp",EDGE,"E544"),sQuery(id+"F2.wireOp",EDGE,"E545"),sQuery(id+"F2.wireOp",EDGE,"E546"),sQuery(id+"F2.wireOp",EDGE,"E547"),sQuery(id+"F2.wireOp",EDGE,"E547"),sQuery(id+"F2.wireOp",EDGE,"E548"),sQuery(id+"F2.wireOp",EDGE,"E549"),sQuery(id+"F2.wireOp",EDGE,"E550"),sQuery(id+"F2.wireOp",EDGE,"E551"),sQuery(id+"F2.wireOp",EDGE,"E552"),sQuery(id+"F2.wireOp",EDGE,"E553"),sQuery(id+"F2.wireOp",EDGE,"E554"),sQuery(id+"F2.wireOp",EDGE,"E555"),sQuery(id+"F2.wireOp",EDGE,"E556"),sQuery(id+"F2.wireOp",EDGE,"E557"),sQuery(id+"F2.wireOp",EDGE,"E558"),sQuery(id+"F2.wireOp",EDGE,"E559"),sQuery(id+"F2.wireOp",EDGE,"E560"),sQuery(id+"F2.wireOp",EDGE,"E561"),sQuery(id+"F2.wireOp",EDGE,"E562"),sQuery(id+"F2.wireOp",EDGE,"E563"),sQuery(id+"F2.wireOp",EDGE,"E564"),sQuery(id+"F2.wireOp",EDGE,"E565"),sQuery(id+"F2.wireOp",EDGE,"E566"),sQuery(id+"F2.wireOp",EDGE,"E567"),sQuery(id+"F2.wireOp",EDGE,"E568"),sQuery(id+"F2.wireOp",EDGE,"E569"),sQuery(id+"F2.wireOp",EDGE,"E570"),sQuery(id+"F2.wireOp",EDGE,"E571"),sQuery(id+"F2.wireOp",EDGE,"E572"),sQuery(id+"F2.wireOp",EDGE,"E573"),sQuery(id+"F2.wireOp",EDGE,"E574"),sQuery(id+"F2.wireOp",EDGE,"E575"),sQuery(id+"F2.wireOp",EDGE,"E576"),sQuery(id+"F2.wireOp",EDGE,"E577"),sQuery(id+"F2.wireOp",EDGE,"E578"),sQuery(id+"F2.wireOp",EDGE,"E579"),sQuery(id+"F2.wireOp",EDGE,"E580"),sQuery(id+"F2.wireOp",EDGE,"E581"),sQuery(id+"F2.wireOp",EDGE,"E582"),sQuery(id+"F2.wireOp",EDGE,"E583"),sQuery(id+"F2.wireOp",EDGE,"E584"),sQuery(id+"F2.wireOp",EDGE,"E585"),sQuery(id+"F2.wireOp",EDGE,"E586"),sQuery(id+"F2.wireOp",EDGE,"E587"),sQuery(id+"F2.wireOp",EDGE,"E588"),sQuery(id+"F2.wireOp",EDGE,"E589"),sQuery(id+"F2.wireOp",EDGE,"E590"),sQuery(id+"F2.wireOp",EDGE,"E591"),sQuery(id+"F2.wireOp",EDGE,"E592"),sQuery(id+"F2.wireOp",EDGE,"E593"),sQuery(id+"F2.wireOp",EDGE,"E594"),sQuery(id+"F2.wireOp",EDGE,"E595"),sQuery(id+"F2.wireOp",EDGE,"E596"),sQuery(id+"F2.wireOp",EDGE,"E597"),sQuery(id+"F2.wireOp",EDGE,"E598"),sQuery(id+"F2.wireOp",EDGE,"E599"),sQuery(id+"F2.wireOp",EDGE,"E600"),sQuery(id+"F2.wireOp",EDGE,"E601"),sQuery(id+"F2.wireOp",EDGE,"E602"),sQuery(id+"F2.wireOp",EDGE,"E603"),sQuery(id+"F2.wireOp",EDGE,"E604"),sQuery(id+"F2.wireOp",EDGE,"E605"),sQuery(id+"F2.wireOp",EDGE,"E606"),sQuery(id+"F2.wireOp",EDGE,"E607"),sQuery(id+"F2.wireOp",EDGE,"E608"),sQuery(id+"F2.wireOp",EDGE,"E609"),sQuery(id+"F2.wireOp",EDGE,"E610"),sQuery(id+"F2.wireOp",EDGE,"E611"),sQuery(id+"F2.wireOp",EDGE,"E612"),sQuery(id+"F2.wireOp",EDGE,"E613"),sQuery(id+"F2.wireOp",EDGE,"E614"),sQuery(id+"F2.wireOp",EDGE,"E615"),sQuery(id+"F2.wireOp",EDGE,"E616"),sQuery(id+"F2.wireOp",EDGE,"E617"),sQuery(id+"F2.wireOp",EDGE,"E618"),sQuery(id+"F2.wireOp",EDGE,"E619"),sQuery(id+"F2.wireOp",EDGE,"E620"),sQuery(id+"F2.wireOp",EDGE,"E621"),sQuery(id+"F2.wireOp",EDGE,"E622"),sQuery(id+"F2.wireOp",EDGE,"E623"),sQuery(id+"F2.wireOp",EDGE,"E624"),sQuery(id+"F2.wireOp",EDGE,"E625"),sQuery(id+"F2.wireOp",EDGE,"E626"),sQuery(id+"F2.wireOp",EDGE,"E627"),sQuery(id+"F2.wireOp",EDGE,"E628"),sQuery(id+"F2.wireOp",EDGE,"E629"),sQuery(id+"F2.wireOp",EDGE,"E630"),sQuery(id+"F2.wireOp",EDGE,"E631"),sQuery(id+"F2.wireOp",EDGE,"E632"),sQuery(id+"F2.wireOp",EDGE,"E633"),sQuery(id+"F2.wireOp",EDGE,"E634"),sQuery(id+"F2.wireOp",EDGE,"E635"),sQuery(id+"F2.wireOp",EDGE,"E636"),sQuery(id+"F2.wireOp",EDGE,"E637"),sQuery(id+"F2.wireOp",EDGE,"E638"),sQuery(id+"F2.wireOp",EDGE,"E639"),sQuery(id+"F2.wireOp",EDGE,"E640"),sQuery(id+"F2.wireOp",EDGE,"E641"),sQuery(id+"F2.wireOp",EDGE,"E642"),sQuery(id+"F2.wireOp",EDGE,"E643"),sQuery(id+"F2.wireOp",EDGE,"E644"),sQuery(id+"F2.wireOp",EDGE,"E645"),sQuery(id+"F2.wireOp",EDGE,"E646"),sQuery(id+"F2.wireOp",EDGE,"E647"),sQuery(id+"F2.wireOp",EDGE,"E648"),sQuery(id+"F2.wireOp",EDGE,"E649"),sQuery(id+"F2.wireOp",EDGE,"E650"),sQuery(id+"F2.wireOp",EDGE,"E651"),sQuery(id+"F2.wireOp",EDGE,"E652"),sQuery(id+"F2.wireOp",EDGE,"E653"),sQuery(id+"F2.wireOp",EDGE,"E654"),sQuery(id+"F2.wireOp",EDGE,"E655"),sQuery(id+"F2.wireOp",EDGE,"E656"),sQuery(id+"F2.wireOp",EDGE,"E657"),sQuery(id+"F2.wireOp",EDGE,"E658"),sQuery(id+"F2.wireOp",EDGE,"E659"),sQuery(id+"F2.wireOp",EDGE,"E660"),sQuery(id+"F2.wireOp",EDGE,"E661"),sQuery(id+"F2.wireOp",EDGE,"E662"),sQuery(id+"F2.wireOp",EDGE,"E663"),sQuery(id+"F2.wireOp",EDGE,"E664"),sQuery(id+"F2.wireOp",EDGE,"E665"),sQuery(id+"F2.wireOp",EDGE,"E666"),sQuery(id+"F2.wireOp",EDGE,"E667"),sQuery(id+"F2.wireOp",EDGE,"E668"),sQuery(id+"F2.wireOp",EDGE,"E669"),sQuery(id+"F2.wireOp",EDGE,"E670"),sQuery(id+"F2.wireOp",EDGE,"E671"),sQuery(id+"F2.wireOp",EDGE,"E672"),sQuery(id+"F2.wireOp",EDGE,"E673"),sQuery(id+"F2.wireOp",EDGE,"E674"),sQuery(id+"F2.wireOp",EDGE,"E675"),sQuery(id+"F2.wireOp",EDGE,"E676"),sQuery(id+"F2.wireOp",EDGE,"E677"),sQuery(id+"F2.wireOp",EDGE,"E678"),sQuery(id+"F2.wireOp",EDGE,"E679"),sQuery(id+"F2.wireOp",EDGE,"E680"),sQuery(id+"F2.wireOp",EDGE,"E681"),sQuery(id+"F2.wireOp",EDGE,"E682"),sQuery(id+"F2.wireOp",EDGE,"E683"),sQuery(id+"F2.wireOp",EDGE,"E684"),sQuery(id+"F2.wireOp",EDGE,"E685"),sQuery(id+"F2.wireOp",EDGE,"E686"),sQuery(id+"F2.wireOp",EDGE,"E687"),sQuery(id+"F2.wireOp",EDGE,"E688"),sQuery(id+"F2.wireOp",EDGE,"E689"),sQuery(id+"F2.wireOp",EDGE,"E690"),sQuery(id+"F2.wireOp",EDGE,"E691"),sQuery(id+"F2.wireOp",EDGE,"E692"),sQuery(id+"F2.wireOp",EDGE,"E693"),sQuery(id+"F2.wireOp",EDGE,"E694"),sQuery(id+"F2.wireOp",EDGE,"E695"),sQuery(id+"F2.wireOp",EDGE,"E696"),sQuery(id+"F2.wireOp",EDGE,"E697"),sQuery(id+"F2.wireOp",EDGE,"E698"),sQuery(id+"F2.wireOp",EDGE,"E699"),sQuery(id+"F2.wireOp",EDGE,"E700"),sQuery(id+"F2.wireOp",EDGE,"E701"),sQuery(id+"F2.wireOp",EDGE,"E702"),sQuery(id+"F2.wireOp",EDGE,"E703"),sQuery(id+"F2.wireOp",EDGE,"E704"),sQuery(id+"F2.wireOp",EDGE,"E705"),sQuery(id+"F2.wireOp",EDGE,"E706"),sQuery(id+"F2.wireOp",EDGE,"E707"),sQuery(id+"F2.wireOp",EDGE,"E708"),sQuery(id+"F2.wireOp",EDGE,"E709"),sQuery(id+"F2.wireOp",EDGE,"E710"),sQuery(id+"F2.wireOp",EDGE,"E711"),sQuery(id+"F2.wireOp",EDGE,"E712"),sQuery(id+"F2.wireOp",EDGE,"E713"),sQuery(id+"F2.wireOp",EDGE,"E714"),sQuery(id+"F2.wireOp",EDGE,"E715"),sQuery(id+"F2.wireOp",EDGE,"E716"),sQuery(id+"F2.wireOp",EDGE,"E717"),sQuery(id+"F2.wireOp",EDGE,"E718"),sQuery(id+"F2.wireOp",EDGE,"E719"),sQuery(id+"F2.wireOp",EDGE,"E720"),sQuery(id+"F2.wireOp",EDGE,"E721"),sQuery(id+"F2.wireOp",EDGE,"E722"),sQuery(id+"F2.wireOp",EDGE,"E723"),sQuery(id+"F2.wireOp",EDGE,"E724"),sQuery(id+"F2.wireOp",EDGE,"E725"),sQuery(id+"F2.wireOp",EDGE,"E726"),sQuery(id+"F2.wireOp",EDGE,"E727"),sQuery(id+"F2.wireOp",EDGE,"E728"),sQuery(id+"F2.wireOp",EDGE,"E729"),sQuery(id+"F2.wireOp",EDGE,"E730"),sQuery(id+"F2.wireOp",EDGE,"E731"),sQuery(id+"F2.wireOp",EDGE,"E732"),sQuery(id+"F2.wireOp",EDGE,"E733"),sQuery(id+"F2.wireOp",EDGE,"E734"),sQuery(id+"F2.wireOp",EDGE,"E735"),sQuery(id+"F2.wireOp",EDGE,"E736"),sQuery(id+"F2.wireOp",EDGE,"E737"),sQuery(id+"F2.wireOp",EDGE,"E738"),sQuery(id+"F2.wireOp",EDGE,"E739"),sQuery(id+"F2.wireOp",EDGE,"E740"),sQuery(id+"F2.wireOp",EDGE,"E741"),sQuery(id+"F2.wireOp",EDGE,"E742"),sQuery(id+"F2.wireOp",EDGE,"E743"),sQuery(id+"F2.wireOp",EDGE,"E744"),sQuery(id+"F2.wireOp",EDGE,"E745"),sQuery(id+"F2.wireOp",EDGE,"E746"),sQuery(id+"F2.wireOp",EDGE,"E747"),sQuery(id+"F2.wireOp",EDGE,"E748"),sQuery(id+"F2.wireOp",EDGE,"E749"),sQuery(id+"F2.wireOp",EDGE,"E750"),sQuery(id+"F2.wireOp",EDGE,"E751"),sQuery(id+"F2.wireOp",EDGE,"E752"),sQuery(id+"F2.wireOp",EDGE,"E753"),sQuery(id+"F2.wireOp",EDGE,"E754"),sQuery(id+"F2.wireOp",EDGE,"E755"),sQuery(id+"F2.wireOp",EDGE,"E756"),sQuery(id+"F2.wireOp",EDGE,"E757"),sQuery(id+"F2.wireOp",EDGE,"E758"),sQuery(id+"F2.wireOp",EDGE,"E759"),sQuery(id+"F2.wireOp",EDGE,"E760"),sQuery(id+"F2.wireOp",EDGE,"E761"),sQuery(id+"F2.wireOp",EDGE,"E762"),sQuery(id+"F2.wireOp",EDGE,"E763"),sQuery(id+"F2.wireOp",EDGE,"E764"),sQuery(id+"F2.wireOp",EDGE,"E765"),sQuery(id+"F2.wireOp",EDGE,"E766"),sQuery(id+"F2.wireOp",EDGE,"E767"),sQuery(id+"F2.wireOp",EDGE,"E768"),sQuery(id+"F2.wireOp",EDGE,"E769"),sQuery(id+"F2.wireOp",EDGE,"E770"),sQuery(id+"F2.wireOp",EDGE,"E771"),sQuery(id+"F2.wireOp",EDGE,"E772"),sQuery(id+"F2.wireOp",EDGE,"E773"),sQuery(id+"F2.wireOp",EDGE,"E774"),sQuery(id+"F2.wireOp",EDGE,"E775"),sQuery(id+"F2.wireOp",EDGE,"E776"),sQuery(id+"F2.wireOp",EDGE,"E777"),sQuery(id+"F2.wireOp",EDGE,"E778"),sQuery(id+"F2.wireOp",EDGE,"E779"),sQuery(id+"F2.wireOp",EDGE,"E780"),sQuery(id+"F2.wireOp",EDGE,"E781"),sQuery(id+"F2.wireOp",EDGE,"E782"),sQuery(id+"F2.wireOp",EDGE,"E783"),sQuery(id+"F2.wireOp",EDGE,"E784"),sQuery(id+"F2.wireOp",EDGE,"E785"),sQuery(id+"F2.wireOp",EDGE,"E786"),sQuery(id+"F2.wireOp",EDGE,"E787"),sQuery(id+"F2.wireOp",EDGE,"E788"),sQuery(id+"F2.wireOp",EDGE,"E789"),sQuery(id+"F2.wireOp",EDGE,"E790"),sQuery(id+"F2.wireOp",EDGE,"E791"),sQuery(id+"F2.wireOp",EDGE,"E792"),sQuery(id+"F2.wireOp",EDGE,"E793"),sQuery(id+"F2.wireOp",EDGE,"E794"),sQuery(id+"F2.wireOp",EDGE,"E795"),sQuery(id+"F2.wireOp",EDGE,"E796"),sQuery(id+"F2.wireOp",EDGE,"E797"),sQuery(id+"F2.wireOp",EDGE,"E798"),sQuery(id+"F2.wireOp",EDGE,"E799"),sQuery(id+"F2.wireOp",EDGE,"E800"),sQuery(id+"F2.wireOp",EDGE,"E801"),sQuery(id+"F2.wireOp",EDGE,"E802"),sQuery(id+"F2.wireOp",EDGE,"E803"),sQuery(id+"F2.wireOp",EDGE,"E804"),sQuery(id+"F2.wireOp",EDGE,"E805"),sQuery(id+"F2.wireOp",EDGE,"E806"),sQuery(id+"F2.wireOp",EDGE,"E807"),sQuery(id+"F2.wireOp",EDGE,"E808"),sQuery(id+"F2.wireOp",EDGE,"E809"),sQuery(id+"F2.wireOp",EDGE,"E810"),sQuery(id+"F2.wireOp",EDGE,"E811"),sQuery(id+"F2.wireOp",EDGE,"E812"),sQuery(id+"F2.wireOp",EDGE,"E813"),sQuery(id+"F2.wireOp",EDGE,"E814"),sQuery(id+"F2.wireOp",EDGE,"E815"),sQuery(id+"F2.wireOp",EDGE,"E816"),sQuery(id+"F2.wireOp",EDGE,"E817"),sQuery(id+"F2.wireOp",EDGE,"E818"),sQuery(id+"F2.wireOp",EDGE,"E819"),sQuery(id+"F2.wireOp",EDGE,"E820"),sQuery(id+"F2.wireOp",EDGE,"E821"),sQuery(id+"F2.wireOp",EDGE,"E822"),sQuery(id+"F2.wireOp",EDGE,"E823"),sQuery(id+"F2.wireOp",EDGE,"E824"),sQuery(id+"F2.wireOp",EDGE,"E825"),sQuery(id+"F2.wireOp",EDGE,"E826"),sQuery(id+"F2.wireOp",EDGE,"E827"),sQuery(id+"F2.wireOp",EDGE,"E828"),sQuery(id+"F2.wireOp",EDGE,"E829"),sQuery(id+"F2.wireOp",EDGE,"E830"),sQuery(id+"F2.wireOp",EDGE,"E831"),sQuery(id+"F2.wireOp",EDGE,"E832"),sQuery(id+"F2.wireOp",EDGE,"E833"),sQuery(id+"F2.wireOp",EDGE,"E834"),sQuery(id+"F2.wireOp",EDGE,"E835"),sQuery(id+"F2.wireOp",EDGE,"E836"),sQuery(id+"F2.wireOp",EDGE,"E837"),sQuery(id+"F2.wireOp",EDGE,"E838"),sQuery(id+"F2.wireOp",EDGE,"E839"),sQuery(id+"F2.wireOp",EDGE,"E840"),sQuery(id+"F2.wireOp",EDGE,"E841"),sQuery(id+"F2.wireOp",EDGE,"E842"),sQuery(id+"F2.wireOp",EDGE,"E843"),sQuery(id+"F2.wireOp",EDGE,"E844"),sQuery(id+"F2.wireOp",EDGE,"E845"),sQuery(id+"F2.wireOp",EDGE,"E846"),sQuery(id+"F2.wireOp",EDGE,"E847"),sQuery(id+"F2.wireOp",EDGE,"E848"),sQuery(id+"F2.wireOp",EDGE,"E849"),sQuery(id+"F2.wireOp",EDGE,"E850"),sQuery(id+"F2.wireOp",EDGE,"E851"),sQuery(id+"F2.wireOp",EDGE,"E852"),sQuery(id+"F2.wireOp",EDGE,"E853"),sQuery(id+"F2.wireOp",EDGE,"E854"),sQuery(id+"F2.wireOp",EDGE,"E855"),sQuery(id+"F2.wireOp",EDGE,"E856"),sQuery(id+"F2.wireOp",EDGE,"E857"),sQuery(id+"F2.wireOp",EDGE,"E858"),sQuery(id+"F2.wireOp",EDGE,"E859"),sQuery(id+"F2.wireOp",EDGE,"E860"),sQuery(id+"F2.wireOp",EDGE,"E861"),sQuery(id+"F2.wireOp",EDGE,"E862"),sQuery(id+"F2.wireOp",EDGE,"E863"),sQuery(id+"F2.wireOp",EDGE,"E864"),sQuery(id+"F2.wireOp",EDGE,"E865"),sQuery(id+"F2.wireOp",EDGE,"E866"),sQuery(id+"F2.wireOp",EDGE,"E867"),sQuery(id+"F2.wireOp",EDGE,"E868"),sQuery(id+"F2.wireOp",EDGE,"E869"),sQuery(id+"F2.wireOp",EDGE,"E870"),sQuery(id+"F2.wireOp",EDGE,"E871"),sQuery(id+"F2.wireOp",EDGE,"E872"),sQuery(id+"F2.wireOp",EDGE,"E873"),sQuery(id+"F2.wireOp",EDGE,"E874"),sQuery(id+"F2.wireOp",EDGE,"E875"),sQuery(id+"F2.wireOp",EDGE,"E876"),sQuery(id+"F2.wireOp",EDGE,"E877"),sQuery(id+"F2.wireOp",EDGE,"E878"),sQuery(id+"F2.wireOp",EDGE,"E879"),sQuery(id+"F2.wireOp",EDGE,"E880"),sQuery(id+"F2.wireOp",EDGE,"E881"),sQuery(id+"F2.wireOp",EDGE,"E882"),sQuery(id+"F2.wireOp",EDGE,"E883"),sQuery(id+"F2.wireOp",EDGE,"E884"),sQuery(id+"F2.wireOp",EDGE,"E885"),sQuery(id+"F2.wireOp",EDGE,"E886"),sQuery(id+"F2.wireOp",EDGE,"E887"),sQuery(id+"F2.wireOp",EDGE,"E888"),sQuery(id+"F2.wireOp",EDGE,"E889"),sQuery(id+"F2.wireOp",EDGE,"E890"),sQuery(id+"F2.wireOp",EDGE,"E891"),sQuery(id+"F2.wireOp",EDGE,"E892"),sQuery(id+"F2.wireOp",EDGE,"E893"),sQuery(id+"F2.wireOp",EDGE,"E894"),sQuery(id+"F2.wireOp",EDGE,"E895"),sQuery(id+"F2.wireOp",EDGE,"E896"),sQuery(id+"F2.wireOp",EDGE,"E897"),sQuery(id+"F2.wireOp",EDGE,"E898"),sQuery(id+"F2.wireOp",EDGE,"E899"),sQuery(id+"F2.wireOp",EDGE,"E900"),sQuery(id+"F2.wireOp",EDGE,"E901"),sQuery(id+"F2.wireOp",EDGE,"E902"),sQuery(id+"F2.wireOp",EDGE,"E903"),sQuery(id+"F2.wireOp",EDGE,"E904"),sQuery(id+"F2.wireOp",EDGE,"E905"),sQuery(id+"F2.wireOp",EDGE,"E906"),sQuery(id+"F2.wireOp",EDGE,"E907"),sQuery(id+"F2.wireOp",EDGE,"E908"),sQuery(id+"F2.wireOp",EDGE,"E909"),sQuery(id+"F2.wireOp",EDGE,"E910"),sQuery(id+"F2.wireOp",EDGE,"E911"),sQuery(id+"F2.wireOp",EDGE,"E912"),sQuery(id+"F2.wireOp",EDGE,"E913"),sQuery(id+"F2.wireOp",EDGE,"E914"),sQuery(id+"F2.wireOp",EDGE,"E915"),sQuery(id+"F2.wireOp",EDGE,"E916"),sQuery(id+"F2.wireOp",EDGE,"E917"),sQuery(id+"F2.wireOp",EDGE,"E918"),sQuery(id+"F2.wireOp",EDGE,"E919"),sQuery(id+"F2.wireOp",EDGE,"E920"),sQuery(id+"F2.wireOp",EDGE,"E921"),sQuery(id+"F2.wireOp",EDGE,"E922"),sQuery(id+"F2.wireOp",EDGE,"E923"),sQuery(id+"F2.wireOp",EDGE,"E924"),sQuery(id+"F2.wireOp",EDGE,"E925"),sQuery(id+"F2.wireOp",EDGE,"E926"),sQuery(id+"F2.wireOp",EDGE,"E927"),sQuery(id+"F2.wireOp",EDGE,"E928"),sQuery(id+"F2.wireOp",EDGE,"E929"),sQuery(id+"F2.wireOp",EDGE,"E930"),sQuery(id+"F2.wireOp",EDGE,"E931"),sQuery(id+"F2.wireOp",EDGE,"E932"),sQuery(id+"F2.wireOp",EDGE,"E933"),sQuery(id+"F2.wireOp",EDGE,"E934"),sQuery(id+"F2.wireOp",EDGE,"E935"),sQuery(id+"F2.wireOp",EDGE,"E936"),sQuery(id+"F2.wireOp",EDGE,"E937"),sQuery(id+"F2.wireOp",EDGE,"E938"),sQuery(id+"F2.wireOp",EDGE,"E939"),sQuery(id+"F2.wireOp",EDGE,"E940"),sQuery(id+"F2.wireOp",EDGE,"E941"),sQuery(id+"F2.wireOp",EDGE,"E942"),sQuery(id+"F2.wireOp",EDGE,"E943"),sQuery(id+"F2.wireOp",EDGE,"E944"),sQuery(id+"F2.wireOp",EDGE,"E945"),sQuery(id+"F2.wireOp",EDGE,"E946"),sQuery(id+"F2.wireOp",EDGE,"E947"),sQuery(id+"F2.wireOp",EDGE,"E948"),sQuery(id+"F2.wireOp",EDGE,"E949"),sQuery(id+"F2.wireOp",EDGE,"E950"),sQuery(id+"F2.wireOp",EDGE,"E951"),sQuery(id+"F2.wireOp",EDGE,"E952"),sQuery(id+"F2.wireOp",EDGE,"E953"),sQuery(id+"F2.wireOp",EDGE,"E954"),sQuery(id+"F2.wireOp",EDGE,"E955"),sQuery(id+"F2.wireOp",EDGE,"E956"),sQuery(id+"F2.wireOp",EDGE,"E957"),sQuery(id+"F2.wireOp",EDGE,"E958"),sQuery(id+"F2.wireOp",EDGE,"E959"),sQuery(id+"F2.wireOp",EDGE,"E960"),sQuery(id+"F2.wireOp",EDGE,"E961"),sQuery(id+"F2.wireOp",EDGE,"E962"),sQuery(id+"F2.wireOp",EDGE,"E963"),sQuery(id+"F2.wireOp",EDGE,"E964"),sQuery(id+"F2.wireOp",EDGE,"E965"),sQuery(id+"F2.wireOp",EDGE,"E966"),sQuery(id+"F2.wireOp",EDGE,"E967"),sQuery(id+"F2.wireOp",EDGE,"E968"),sQuery(id+"F2.wireOp",EDGE,"E969"),sQuery(id+"F2.wireOp",EDGE,"E970"),sQuery(id+"F2.wireOp",EDGE,"E971"),sQuery(id+"F2.wireOp",EDGE,"E972"),sQuery(id+"F2.wireOp",EDGE,"E973"),sQuery(id+"F2.wireOp",EDGE,"E974"),sQuery(id+"F2.wireOp",EDGE,"E975"),sQuery(id+"F2.wireOp",EDGE,"E976"),sQuery(id+"F2.wireOp",EDGE,"E977"),sQuery(id+"F2.wireOp",EDGE,"E978"),sQuery(id+"F2.wireOp",EDGE,"E979"),sQuery(id+"F2.wireOp",EDGE,"E980"),sQuery(id+"F2.wireOp",EDGE,"E981"),sQuery(id+"F2.wireOp",EDGE,"E982"),sQuery(id+"F2.wireOp",EDGE,"E983"),sQuery(id+"F2.wireOp",EDGE,"E984"),sQuery(id+"F2.wireOp",EDGE,"E985"),sQuery(id+"F2.wireOp",EDGE,"E986"),sQuery(id+"F2.wireOp",EDGE,"E987"),sQuery(id+"F2.wireOp",EDGE,"E988"),sQuery(id+"F2.wireOp",EDGE,"E989"),sQuery(id+"F2.wireOp",EDGE,"E990"),sQuery(id+"F2.wireOp",EDGE,"E991"),sQuery(id+"F2.wireOp",EDGE,"E992"),sQuery(id+"F2.wireOp",EDGE,"E993"),sQuery(id+"F2.wireOp",EDGE,"E994"),sQuery(id+"F2.wireOp",EDGE,"E995"),sQuery(id+"F2.wireOp",EDGE,"E996"),sQuery(id+"F2.wireOp",EDGE,"E997"),sQuery(id+"F2.wireOp",EDGE,"E998"),sQuery(id+"F2.wireOp",EDGE,"E999"),sQuery(id+"F2.wireOp",EDGE,"E1000"),sQuery(id+"F2.wireOp",EDGE,"E1001"),sQuery(id+"F2.wireOp",EDGE,"E1002"),sQuery(id+"F2.wireOp",EDGE,"E1003"),sQuery(id+"F2.wireOp",EDGE,"E1004"),sQuery(id+"F2.wireOp",EDGE,"E1005"),sQuery(id+"F2.wireOp",EDGE,"E1006"),sQuery(id+"F2.wireOp",EDGE,"E1007"),sQuery(id+"F2.wireOp",EDGE,"E1008"),sQuery(id+"F2.wireOp",EDGE,"E1009"),sQuery(id+"F2.wireOp",EDGE,"E1010"),sQuery(id+"F2.wireOp",EDGE,"E1011"),sQuery(id+"F2.wireOp",EDGE,"E1012"),sQuery(id+"F2.wireOp",EDGE,"E1013"),sQuery(id+"F2.wireOp",EDGE,"E1014"),sQuery(id+"F2.wireOp",EDGE,"E1015"),sQuery(id+"F2.wireOp",EDGE,"E1016"),sQuery(id+"F2.wireOp",EDGE,"E1017"),sQuery(id+"F2.wireOp",EDGE,"E1018"),sQuery(id+"F2.wireOp",EDGE,"E1019"),sQuery(id+"F2.wireOp",EDGE,"E1020"),sQuery(id+"F2.wireOp",EDGE,"E1021"),sQuery(id+"F2.wireOp",EDGE,"E1022"),sQuery(id+"F2.wireOp",EDGE,"E1023"),sQuery(id+"F2.wireOp",EDGE,"E1024"),sQuery(id+"F2.wireOp",EDGE,"E1025"),sQuery(id+"F2.wireOp",EDGE,"E1026"),sQuery(id+"F2.wireOp",EDGE,"E1027"),sQuery(id+"F2.wireOp",EDGE,"E1028"),sQuery(id+"F2.wireOp",EDGE,"E1029"),sQuery(id+"F2.wireOp",EDGE,"E1030"),sQuery(id+"F2.wireOp",EDGE,"E1031"),sQuery(id+"F2.wireOp",EDGE,"E1032"),sQuery(id+"F2.wireOp",EDGE,"E1033"),sQuery(id+"F2.wireOp",EDGE,"E1034"),sQuery(id+"F2.wireOp",EDGE,"E1035"),sQuery(id+"F2.wireOp",EDGE,"E1036"),sQuery(id+"F2.wireOp",EDGE,"E1037"),sQuery(id+"F2.wireOp",EDGE,"E1038"),sQuery(id+"F2.wireOp",EDGE,"E1039"),sQuery(id+"F2.wireOp",EDGE,"E1040"),sQuery(id+"F2.wireOp",EDGE,"E1041"),sQuery(id+"F2.wireOp",EDGE,"E1042"),sQuery(id+"F2.wireOp",EDGE,"E1043"),sQuery(id+"F2.wireOp",EDGE,"E1044"),sQuery(id+"F2.wireOp",EDGE,"E1045"),sQuery(id+"F2.wireOp",EDGE,"E1046"),sQuery(id+"F2.wireOp",EDGE,"E1047"),sQuery(id+"F2.wireOp",EDGE,"E1048"),sQuery(id+"F2.wireOp",EDGE,"E1049"),sQuery(id+"F2.wireOp",EDGE,"E1050"),sQuery(id+"F2.wireOp",EDGE,"E1051"),sQuery(id+"F2.wireOp",EDGE,"E1052"),sQuery(id+"F2.wireOp",EDGE,"E1053"),sQuery(id+"F2.wireOp",EDGE,"E1054"),sQuery(id+"F2.wireOp",EDGE,"E1055"),sQuery(id+"F2.wireOp",EDGE,"E1056"),sQuery(id+"F2.wireOp",EDGE,"E1057"),sQuery(id+"F2.wireOp",EDGE,"E1058"),sQuery(id+"F2.wireOp",EDGE,"E1059"),sQuery(id+"F2.wireOp",EDGE,"E1060"),sQuery(id+"F2.wireOp",EDGE,"E1061"),sQuery(id+"F2.wireOp",EDGE,"E1062"),sQuery(id+"F2.wireOp",EDGE,"E1063"),sQuery(id+"F2.wireOp",EDGE,"E1064"),sQuery(id+"F2.wireOp",EDGE,"E1065"),sQuery(id+"F2.wireOp",EDGE,"E1066"),sQuery(id+"F2.wireOp",EDGE,"E1067"),sQuery(id+"F2.wireOp",EDGE,"E1068"),sQuery(id+"F2.wireOp",EDGE,"E1069"),sQuery(id+"F2.wireOp",EDGE,"E1070"),sQuery(id+"F2.wireOp",EDGE,"E1071"),sQuery(id+"F2.wireOp",EDGE,"E1072"),sQuery(id+"F2.wireOp",EDGE,"E1073"),sQuery(id+"F2.wireOp",EDGE,"E1074"),sQuery(id+"F2.wireOp",EDGE,"E1075"),sQuery(id+"F2.wireOp",EDGE,"E1076"),sQuery(id+"F2.wireOp",EDGE,"E1077"),sQuery(id+"F2.wireOp",EDGE,"E1078"),sQuery(id+"F2.wireOp",EDGE,"E1079"),sQuery(id+"F2.wireOp",EDGE,"E1080"),sQuery(id+"F2.wireOp",EDGE,"E1081"),sQuery(id+"F2.wireOp",EDGE,"E1082"),sQuery(id+"F2.wireOp",EDGE,"E1083"),sQuery(id+"F2.wireOp",EDGE,"E1084"),sQuery(id+"F2.wireOp",EDGE,"E1085"),sQuery(id+"F2.wireOp",EDGE,"E1086"),sQuery(id+"F2.wireOp",EDGE,"E1087"),sQuery(id+"F2.wireOp",EDGE,"E1088"),sQuery(id+"F2.wireOp",EDGE,"E1089"),sQuery(id+"F2.wireOp",EDGE,"E1090"),sQuery(id+"F2.wireOp",EDGE,"E1091"),sQuery(id+"F2.wireOp",EDGE,"E1092"),sQuery(id+"F2.wireOp",EDGE,"E1093"),sQuery(id+"F2.wireOp",EDGE,"E1094"),sQuery(id+"F2.wireOp",EDGE,"E1095"),sQuery(id+"F2.wireOp",EDGE,"E1096"),sQuery(id+"F2.wireOp",EDGE,"E1097"),sQuery(id+"F2.wireOp",EDGE,"E1098"),sQuery(id+"F2.wireOp",EDGE,"E1099"),sQuery(id+"F2.wireOp",EDGE,"E1100"),sQuery(id+"F2.wireOp",EDGE,"E1101"),sQuery(id+"F2.wireOp",EDGE,"E1102"),sQuery(id+"F2.wireOp",EDGE,"E1103"),sQuery(id+"F2.wireOp",EDGE,"E1104"),sQuery(id+"F2.wireOp",EDGE,"E1105"),sQuery(id+"F2.wireOp",EDGE,"E1106"),sQuery(id+"F2.wireOp",EDGE,"E1107"),sQuery(id+"F2.wireOp",EDGE,"E1108"),sQuery(id+"F2.wireOp",EDGE,"E1109"),sQuery(id+"F2.wireOp",EDGE,"E1110"),sQuery(id+"F2.wireOp",EDGE,"E1111"),sQuery(id+"F2.wireOp",EDGE,"E1112"),sQuery(id+"F2.wireOp",EDGE,"E1113"),sQuery(id+"F2.wireOp",EDGE,"E1114"),sQuery(id+"F2.wireOp",EDGE,"E1115"),sQuery(id+"F2.wireOp",EDGE,"E1116"),sQuery(id+"F2.wireOp",EDGE,"E1117"),sQuery(id+"F2.wireOp",EDGE,"E1118"),sQuery(id+"F2.wireOp",EDGE,"E1119"),sQuery(id+"F2.wireOp",EDGE,"E1120"),sQuery(id+"F2.wireOp",EDGE,"E1121"),sQuery(id+"F2.wireOp",EDGE,"E1122"),sQuery(id+"F2.wireOp",EDGE,"E1123"),sQuery(id+"F2.wireOp",EDGE,"E1124"),sQuery(id+"F2.wireOp",EDGE,"E1125"),sQuery(id+"F2.wireOp",EDGE,"E1126"),sQuery(id+"F2.wireOp",EDGE,"E1127"),sQuery(id+"F2.wireOp",EDGE,"E1128"),sQuery(id+"F2.wireOp",EDGE,"E1129"),sQuery(id+"F2.wireOp",EDGE,"E1130"),sQuery(id+"F2.wireOp",EDGE,"E1131"),sQuery(id+"F2.wireOp",EDGE,"E1132"),sQuery(id+"F2.wireOp",EDGE,"E1133"),sQuery(id+"F2.wireOp",EDGE,"E1134"),sQuery(id+"F2.wireOp",EDGE,"E1135"),sQuery(id+"F2.wireOp",EDGE,"E1136"),sQuery(id+"F2.wireOp",EDGE,"E1137"),sQuery(id+"F2.wireOp",EDGE,"E1138"),sQuery(id+"F2.wireOp",EDGE,"E1139"),sQuery(id+"F2.wireOp",EDGE,"E1140"),sQuery(id+"F2.wireOp",EDGE,"E1141"),sQuery(id+"F2.wireOp",EDGE,"E1142"),sQuery(id+"F2.wireOp",EDGE,"E1143"),sQuery(id+"F2.wireOp",EDGE,"E1144"),sQuery(id+"F2.wireOp",EDGE,"E1145"),sQuery(id+"F2.wireOp",EDGE,"E1146"),sQuery(id+"F2.wireOp",EDGE,"E1147"),sQuery(id+"F2.wireOp",EDGE,"E1148"),sQuery(id+"F2.wireOp",EDGE,"E1149"),sQuery(id+"F2.wireOp",EDGE,"E1150"),sQuery(id+"F2.wireOp",EDGE,"E1151"),sQuery(id+"F2.wireOp",EDGE,"E1152"),sQuery(id+"F2.wireOp",EDGE,"E1153"),sQuery(id+"F2.wireOp",EDGE,"E1154"),sQuery(id+"F2.wireOp",EDGE,"E1155"),sQuery(id+"F2.wireOp",EDGE,"E1156"),sQuery(id+"F2.wireOp",EDGE,"E1157"),sQuery(id+"F2.wireOp",EDGE,"E1158"),sQuery(id+"F2.wireOp",EDGE,"E1159"),sQuery(id+"F2.wireOp",EDGE,"E1160"),sQuery(id+"F2.wireOp",EDGE,"E1161"),sQuery(id+"F2.wireOp",EDGE,"E1162"),sQuery(id+"F2.wireOp",EDGE,"E1163"),sQuery(id+"F2.wireOp",EDGE,"E1164"),sQuery(id+"F2.wireOp",EDGE,"E1165"),sQuery(id+"F2.wireOp",EDGE,"E1166"),sQuery(id+"F2.wireOp",EDGE,"E1167"),sQuery(id+"F2.wireOp",EDGE,"E1168"),sQuery(id+"F2.wireOp",EDGE,"E1169"),sQuery(id+"F2.wireOp",EDGE,"E1170"),sQuery(id+"F2.wireOp",EDGE,"E1171"),sQuery(id+"F2.wireOp",EDGE,"E1172"),sQuery(id+"F2.wireOp",EDGE,"E1173"),sQuery(id+"F2.wireOp",EDGE,"E1174"),sQuery(id+"F2.wireOp",EDGE,"E1175"),sQuery(id+"F2.wireOp",EDGE,"E1176"),sQuery(id+"F2.wireOp",EDGE,"E1177"),sQuery(id+"F2.wireOp",EDGE,"E1178"),sQuery(id+"F2.wireOp",EDGE,"E1179"),sQuery(id+"F2.wireOp",EDGE,"E1180"),sQuery(id+"F2.wireOp",EDGE,"E1181"),sQuery(id+"F2.wireOp",EDGE,"E1182"),sQuery(id+"F2.wireOp",EDGE,"E1183"),sQuery(id+"F2.wireOp",EDGE,"E1184"),sQuery(id+"F2.wireOp",EDGE,"E1185"),sQuery(id+"F2.wireOp",EDGE,"E1186"),sQuery(id+"F2.wireOp",EDGE,"E1187"),sQuery(id+"F2.wireOp",EDGE,"E1188"),sQuery(id+"F2.wireOp",EDGE,"E1189"),sQuery(id+"F2.wireOp",EDGE,"E1190"),sQuery(id+"F2.wireOp",EDGE,"E1191"),sQuery(id+"F2.wireOp",EDGE,"E1192"),sQuery(id+"F2.wireOp",EDGE,"E1193"),sQuery(id+"F2.wireOp",EDGE,"E1194"),sQuery(id+"F2.wireOp",EDGE,"E1195"),sQuery(id+"F2.wireOp",EDGE,"E1196"),sQuery(id+"F2.wireOp",EDGE,"E1197"),sQuery(id+"F2.wireOp",EDGE,"E1198"),sQuery(id+"F2.wireOp",EDGE,"E1199"),sQuery(id+"F2.wireOp",EDGE,"E1200"),sQuery(id+"F2.wireOp",EDGE,"E1201"),sQuery(id+"F2.wireOp",EDGE,"E1202"),sQuery(id+"F2.wireOp",EDGE,"E1203"),sQuery(id+"F2.wireOp",EDGE,"E1204"),sQuery(id+"F2.wireOp",EDGE,"E1205"),sQuery(id+"F2.wireOp",EDGE,"E1206"),sQuery(id+"F2.wireOp",EDGE,"E1207"),sQuery(id+"F2.wireOp",EDGE,"E1208"),sQuery(id+"F2.wireOp",EDGE,"E1209"),sQuery(id+"F2.wireOp",EDGE,"E1210"),sQuery(id+"F2.wireOp",EDGE,"E1211"),sQuery(id+"F2.wireOp",EDGE,"E1212"),sQuery(id+"F2.wireOp",EDGE,"E1213"),sQuery(id+"F2.wireOp",EDGE,"E1214"),sQuery(id+"F2.wireOp",EDGE,"E1215"),sQuery(id+"F2.wireOp",EDGE,"E1216"),sQuery(id+"F2.wireOp",EDGE,"E1217"),sQuery(id+"F2.wireOp",EDGE,"E1218"),sQuery(id+"F2.wireOp",EDGE,"E1219"),sQuery(id+"F2.wireOp",EDGE,"E1220"),sQuery(id+"F2.wireOp",EDGE,"E1221"),sQuery(id+"F2.wireOp",EDGE,"E1222"),sQuery(id+"F2.wireOp",EDGE,"E1223"),sQuery(id+"F2.wireOp",EDGE,"E1224"),sQuery(id+"F2.wireOp",EDGE,"E1225"),sQuery(id+"F2.wireOp",EDGE,"E1226"),sQuery(id+"F2.wireOp",EDGE,"E1227"),sQuery(id+"F2.wireOp",EDGE,"E1228"),sQuery(id+"F2.wireOp",EDGE,"E1229"),sQuery(id+"F2.wireOp",EDGE,"E1230"),sQuery(id+"F2.wireOp",EDGE,"E1231"),sQuery(id+"F2.wireOp",EDGE,"E1232"),sQuery(id+"F2.wireOp",EDGE,"E1233"),sQuery(id+"F2.wireOp",EDGE,"E1234"),sQuery(id+"F2.wireOp",EDGE,"E1235"),sQuery(id+"F2.wireOp",EDGE,"E1236"),sQuery(id+"F2.wireOp",EDGE,"E1237"),sQuery(id+"F2.wireOp",EDGE,"E1238"),sQuery(id+"F2.wireOp",EDGE,"E1239"),sQuery(id+"F2.wireOp",EDGE,"E1240"),sQuery(id+"F2.wireOp",EDGE,"E1241"),sQuery(id+"F2.wireOp",EDGE,"E1242"),sQuery(id+"F2.wireOp",EDGE,"E1243"),sQuery(id+"F2.wireOp",EDGE,"E1244"),sQuery(id+"F2.wireOp",EDGE,"E1245"),sQuery(id+"F2.wireOp",EDGE,"E1246"),sQuery(id+"F2.wireOp",EDGE,"E1247"),sQuery(id+"F2.wireOp",EDGE,"E1248"),sQuery(id+"F2.wireOp",EDGE,"E1249"),sQuery(id+"F2.wireOp",EDGE,"E1250"),sQuery(id+"F2.wireOp",EDGE,"E1251"),sQuery(id+"F2.wireOp",EDGE,"E1252"),sQuery(id+"F2.wireOp",EDGE,"E1253"),sQuery(id+"F2.wireOp",EDGE,"E1254"),sQuery(id+"F2.wireOp",EDGE,"E1255"),sQuery(id+"F2.wireOp",EDGE,"E1256"),sQuery(id+"F2.wireOp",EDGE,"E1257"),sQuery(id+"F2.wireOp",EDGE,"E1258"),sQuery(id+"F2.wireOp",EDGE,"E1259"),sQuery(id+"F2.wireOp",EDGE,"E1260"),sQuery(id+"F2.wireOp",EDGE,"E1261"),sQuery(id+"F2.wireOp",EDGE,"E1262"),sQuery(id+"F2.wireOp",EDGE,"E1263"),sQuery(id+"F2.wireOp",EDGE,"E1264"),sQuery(id+"F2.wireOp",EDGE,"E1265"),sQuery(id+"F2.wireOp",EDGE,"E1266"),sQuery(id+"F2.wireOp",EDGE,"E1267"),sQuery(id+"F2.wireOp",EDGE,"E1268"),sQuery(id+"F2.wireOp",EDGE,"E1269"),sQuery(id+"F2.wireOp",EDGE,"E1270"),sQuery(id+"F2.wireOp",EDGE,"E1271"),sQuery(id+"F2.wireOp",EDGE,"E1272"),sQuery(id+"F2.wireOp",EDGE,"E1273"),sQuery(id+"F2.wireOp",EDGE,"E1274"),sQuery(id+"F2.wireOp",EDGE,"E1275"),sQuery(id+"F2.wireOp",EDGE,"E1276"),sQuery(id+"F2.wireOp",EDGE,"E1277"),sQuery(id+"F2.wireOp",EDGE,"E1278"),sQuery(id+"F2.wireOp",EDGE,"E1279"),sQuery(id+"F2.wireOp",EDGE,"E1280"),sQuery(id+"F2.wireOp",EDGE,"E1281"),sQuery(id+"F2.wireOp",EDGE,"E1282"),sQuery(id+"F2.wireOp",EDGE,"E1283"),sQuery(id+"F2.wireOp",EDGE,"E1284"),sQuery(id+"F2.wireOp",EDGE,"E1285"),sQuery(id+"F2.wireOp",EDGE,"E1286"),sQuery(id+"F2.wireOp",EDGE,"E1287"),sQuery(id+"F2.wireOp",EDGE,"E1288"),sQuery(id+"F2.wireOp",EDGE,"E1289"),sQuery(id+"F2.wireOp",EDGE,"E1290"),sQuery(id+"F2.wireOp",EDGE,"E1291"),sQuery(id+"F2.wireOp",EDGE,"E1292"),sQuery(id+"F2.wireOp",EDGE,"E1293"),sQuery(id+"F2.wireOp",EDGE,"E1294"),sQuery(id+"F2.wireOp",EDGE,"E1295"),sQuery(id+"F2.wireOp",EDGE,"E1296"),sQuery(id+"F2.wireOp",EDGE,"E1297"),sQuery(id+"F2.wireOp",EDGE,"E1298"),sQuery(id+"F2.wireOp",EDGE,"E1299"),sQuery(id+"F2.wireOp",EDGE,"E1300"),sQuery(id+"F2.wireOp",EDGE,"E1301"),sQuery(id+"F2.wireOp",EDGE,"E1302"),sQuery(id+"F2.wireOp",EDGE,"E1303"),sQuery(id+"F2.wireOp",EDGE,"E1304"),sQuery(id+"F2.wireOp",EDGE,"E1305"),sQuery(id+"F2.wireOp",EDGE,"E1306"),sQuery(id+"F2.wireOp",EDGE,"E1307"),sQuery(id+"F2.wireOp",EDGE,"E1308"),sQuery(id+"F2.wireOp",EDGE,"E1309"),sQuery(id+"F2.wireOp",EDGE,"E1310"),sQuery(id+"F2.wireOp",EDGE,"E1311"),sQuery(id+"F2.wireOp",EDGE,"E1312"),sQuery(id+"F2.wireOp",EDGE,"E1313"),sQuery(id+"F2.wireOp",EDGE,"E1314"),sQuery(id+"F2.wireOp",EDGE,"E1315"),sQuery(id+"F2.wireOp",EDGE,"E1316"),sQuery(id+"F2.wireOp",EDGE,"E1317"),sQuery(id+"F2.wireOp",EDGE,"E1318"),sQuery(id+"F2.wireOp",EDGE,"E1319"),sQuery(id+"F2.wireOp",EDGE,"E1320"),sQuery(id+"F2.wireOp",EDGE,"E1321"),sQuery(id+"F2.wireOp",EDGE,"E1322"),sQuery(id+"F2.wireOp",EDGE,"E1323"),sQuery(id+"F2.wireOp",EDGE,"E1324"),sQuery(id+"F2.wireOp",EDGE,"E1325"),sQuery(id+"F2.wireOp",EDGE,"E1326"),sQuery(id+"F2.wireOp",EDGE,"E1327"),sQuery(id+"F2.wireOp",EDGE,"E1328"),sQuery(id+"F2.wireOp",EDGE,"E1329"),sQuery(id+"F2.wireOp",EDGE,"E1330"),sQuery(id+"F2.wireOp",EDGE,"E1331"),sQuery(id+"F2.wireOp",EDGE,"E1332"),sQuery(id+"F2.wireOp",EDGE,"E1333"),sQuery(id+"F2.wireOp",EDGE,"E1334"),sQuery(id+"F2.wireOp",EDGE,"E1335"),sQuery(id+"F2.wireOp",EDGE,"E1336"),sQuery(id+"F2.wireOp",EDGE,"E1337"),sQuery(id+"F2.wireOp",EDGE,"E1338"),sQuery(id+"F2.wireOp",EDGE,"E1339"),sQuery(id+"F2.wireOp",EDGE,"E1340"),sQuery(id+"F2.wireOp",EDGE,"E1341"),sQuery(id+"F2.wireOp",EDGE,"E1342"),sQuery(id+"F2.wireOp",EDGE,"E1343"),sQuery(id+"F2.wireOp",EDGE,"E1344"),sQuery(id+"F2.wireOp",EDGE,"E1345"),sQuery(id+"F2.wireOp",EDGE,"E1346"),sQuery(id+"F2.wireOp",EDGE,"E1347"),sQuery(id+"F2.wireOp",EDGE,"E1348"),sQuery(id+"F2.wireOp",EDGE,"E1349"),sQuery(id+"F2.wireOp",EDGE,"E1350"),sQuery(id+"F2.wireOp",EDGE,"E1351"),sQuery(id+"F2.wireOp",EDGE,"E1352"),sQuery(id+"F2.wireOp",EDGE,"E1353"),sQuery(id+"F2.wireOp",EDGE,"E1354"),sQuery(id+"F2.wireOp",EDGE,"E1355"),sQuery(id+"F2.wireOp",EDGE,"E1356"),sQuery(id+"F2.wireOp",EDGE,"E1357"),sQuery(id+"F2.wireOp",EDGE,"E1358"),sQuery(id+"F2.wireOp",EDGE,"E1359"),sQuery(id+"F2.wireOp",EDGE,"E1360"),sQuery(id+"F2.wireOp",EDGE,"E1361"),sQuery(id+"F2.wireOp",EDGE,"E1362"),sQuery(id+"F2.wireOp",EDGE,"E1363"),sQuery(id+"F2.wireOp",EDGE,"E1364"),sQuery(id+"F2.wireOp",EDGE,"E1365"),sQuery(id+"F2.wireOp",EDGE,"E1366"),sQuery(id+"F2.wireOp",EDGE,"E1367"),sQuery(id+"F2.wireOp",EDGE,"E1368"),sQuery(id+"F2.wireOp",EDGE,"E1369"),sQuery(id+"F2.wireOp",EDGE,"E1370"),sQuery(id+"F2.wireOp",EDGE,"E1371"),sQuery(id+"F2.wireOp",EDGE,"E1372"),sQuery(id+"F2.wireOp",EDGE,"E1373"),sQuery(id+"F2.wireOp",EDGE,"E1374"),sQuery(id+"F2.wireOp",EDGE,"E1375"),sQuery(id+"F2.wireOp",EDGE,"E1376"),sQuery(id+"F2.wireOp",EDGE,"E1377"),sQuery(id+"F2.wireOp",EDGE,"E1378"),sQuery(id+"F2.wireOp",EDGE,"E1379"),sQuery(id+"F2.wireOp",EDGE,"E1380"),sQuery(id+"F2.wireOp",EDGE,"E1381"),sQuery(id+"F2.wireOp",EDGE,"E1382"),sQuery(id+"F2.wireOp",EDGE,"E1383"),sQuery(id+"F2.wireOp",EDGE,"E1384"),sQuery(id+"F2.wireOp",EDGE,"E1385"),sQuery(id+"F2.wireOp",EDGE,"E1386"),sQuery(id+"F2.wireOp",EDGE,"E1387"),sQuery(id+"F2.wireOp",EDGE,"E1388"),sQuery(id+"F2.wireOp",EDGE,"E1389"),sQuery(id+"F2.wireOp",EDGE,"E1390"),sQuery(id+"F2.wireOp",EDGE,"E1391"),sQuery(id+"F2.wireOp",EDGE,"E1392"),sQuery(id+"F2.wireOp",EDGE,"E1393"),sQuery(id+"F2.wireOp",EDGE,"E1394"),sQuery(id+"F2.wireOp",EDGE,"E1395"),sQuery(id+"F2.wireOp",EDGE,"E1396"),sQuery(id+"F2.wireOp",EDGE,"E1397"),sQuery(id+"F2.wireOp",EDGE,"E1398"),sQuery(id+"F2.wireOp",EDGE,"E1399"),sQuery(id+"F2.wireOp",EDGE,"E1400"),sQuery(id+"F2.wireOp",EDGE,"E1401"),sQuery(id+"F2.wireOp",EDGE,"E1402"),sQuery(id+"F2.wireOp",EDGE,"E1403"),sQuery(id+"F2.wireOp",EDGE,"E1404"),sQuery(id+"F2.wireOp",EDGE,"E1405"),sQuery(id+"F2.wireOp",EDGE,"E1406"),sQuery(id+"F2.wireOp",EDGE,"E1407"),sQuery(id+"F2.wireOp",EDGE,"E1408"),sQuery(id+"F2.wireOp",EDGE,"E1409"),sQuery(id+"F2.wireOp",EDGE,"E1410"),sQuery(id+"F2.wireOp",EDGE,"E1411"),sQuery(id+"F2.wireOp",EDGE,"E1412"),sQuery(id+"F2.wireOp",EDGE,"E1413"),sQuery(id+"F2.wireOp",EDGE,"E1414"),sQuery(id+"F2.wireOp",EDGE,"E1415"),sQuery(id+"F2.wireOp",EDGE,"E1416"),sQuery(id+"F2.wireOp",EDGE,"E1417"),sQuery(id+"F2.wireOp",EDGE,"E1418"),sQuery(id+"F2.wireOp",EDGE,"E1419"),sQuery(id+"F2.wireOp",EDGE,"E1420"),sQuery(id+"F2.wireOp",EDGE,"E1421"),sQuery(id+"F2.wireOp",EDGE,"E1422"),sQuery(id+"F2.wireOp",EDGE,"E1423"),sQuery(id+"F2.wireOp",EDGE,"E1424"),sQuery(id+"F2.wireOp",EDGE,"E1425"),sQuery(id+"F2.wireOp",EDGE,"E1426"),sQuery(id+"F2.wireOp",EDGE,"E1427"),sQuery(id+"F2.wireOp",EDGE,"E1428"),sQuery(id+"F2.wireOp",EDGE,"E1429"),sQuery(id+"F2.wireOp",EDGE,"E1430"),sQuery(id+"F2.wireOp",EDGE,"E1431"),sQuery(id+"F2.wireOp",EDGE,"E1432"),sQuery(id+"F2.wireOp",EDGE,"E1433"),sQuery(id+"F2.wireOp",EDGE,"E1434"),sQuery(id+"F2.wireOp",EDGE,"E1435"),sQuery(id+"F2.wireOp",EDGE,"E1436"),sQuery(id+"F2.wireOp",EDGE,"E1437"),sQuery(id+"F2.wireOp",EDGE,"E1438"),sQuery(id+"F2.wireOp",EDGE,"E1439"),sQuery(id+"F2.wireOp",EDGE,"E1440"),sQuery(id+"F2.wireOp",EDGE,"E1441"),sQuery(id+"F2.wireOp",EDGE,"E1442"),sQuery(id+"F2.wireOp",EDGE,"E1443"),sQuery(id+"F2.wireOp",EDGE,"E1444"),sQuery(id+"F2.wireOp",EDGE,"E1445"),sQuery(id+"F2.wireOp",EDGE,"E1446"),sQuery(id+"F2.wireOp",EDGE,"E1447"),sQuery(id+"F2.wireOp",EDGE,"E1448"),sQuery(id+"F2.wireOp",EDGE,"E1449"),sQuery(id+"F2.wireOp",EDGE,"E1450"),sQuery(id+"F2.wireOp",EDGE,"E1451"),sQuery(id+"F2.wireOp",EDGE,"E1452"),sQuery(id+"F2.wireOp",EDGE,"E1453"),sQuery(id+"F2.wireOp",EDGE,"E1454"),sQuery(id+"F2.wireOp",EDGE,"E1455"),sQuery(id+"F2.wireOp",EDGE,"E1456"),sQuery(id+"F2.wireOp",EDGE,"E1457"),sQuery(id+"F2.wireOp",EDGE,"E1458"),sQuery(id+"F2.wireOp",EDGE,"E1459"),sQuery(id+"F2.wireOp",EDGE,"E1460"),sQuery(id+"F2.wireOp",EDGE,"E1461"),sQuery(id+"F2.wireOp",EDGE,"E1462"),sQuery(id+"F2.wireOp",EDGE,"E1463"),sQuery(id+"F2.wireOp",EDGE,"E1464"),sQuery(id+"F2.wireOp",EDGE,"E1465"),sQuery(id+"F2.wireOp",EDGE,"E1466"),sQuery(id+"F2.wireOp",EDGE,"E1467"),sQuery(id+"F2.wireOp",EDGE,"E1468"),sQuery(id+"F2.wireOp",EDGE,"E1469"),sQuery(id+"F2.wireOp",EDGE,"E1470"),sQuery(id+"F2.wireOp",EDGE,"E1471"),sQuery(id+"F2.wireOp",EDGE,"E1472"),sQuery(id+"F2.wireOp",EDGE,"E1473"),sQuery(id+"F2.wireOp",EDGE,"E1474")])]}),"instanceName":"1"});
            var Q1;
            Q1=sQuery(id+"F0.wireOp",VERTEX,"E0.center");
            var Q2;
            Q2=sQuery(id+"F0.wireOp",VERTEX,"E8.center.orphan");
            transform(context, id + "F8", {"entities" : qUnion([Q0]), "transformType" : TransformType.TRANSLATION_ENTITY, "oppositeDirectionEntity" : false, "transformLine" : qUnion([Q1, Q2]), "makeCopy" : false});
        }
        {
            var Q0;
            Q0=makeQuery(id+"F6.opPattern","COPY",BODY,{"derivedFrom":makeQuery(id+"F3.opExtrude","SWEPT_BODY",BODY,{"disambiguationData":[OSD([sQuery(id+"F2.wireOp",EDGE,"E16"),sQuery(id+"F2.wireOp",EDGE,"E17"),sQuery(id+"F2.wireOp",EDGE,"E18"),sQuery(id+"F2.wireOp",EDGE,"E19"),sQuery(id+"F2.wireOp",EDGE,"E20"),sQuery(id+"F2.wireOp",EDGE,"E21"),sQuery(id+"F2.wireOp",EDGE,"E22"),sQuery(id+"F2.wireOp",EDGE,"E23"),sQuery(id+"F2.wireOp",EDGE,"E24"),sQuery(id+"F2.wireOp",EDGE,"E25"),sQuery(id+"F2.wireOp",EDGE,"E26"),sQuery(id+"F2.wireOp",EDGE,"E27"),sQuery(id+"F2.wireOp",EDGE,"E28"),sQuery(id+"F2.wireOp",EDGE,"E29"),sQuery(id+"F2.wireOp",EDGE,"E30"),sQuery(id+"F2.wireOp",EDGE,"E31"),sQuery(id+"F2.wireOp",EDGE,"E32"),sQuery(id+"F2.wireOp",EDGE,"E33"),sQuery(id+"F2.wireOp",EDGE,"E34"),sQuery(id+"F2.wireOp",EDGE,"E35"),sQuery(id+"F2.wireOp",EDGE,"E36"),sQuery(id+"F2.wireOp",EDGE,"E37"),sQuery(id+"F2.wireOp",EDGE,"E38"),sQuery(id+"F2.wireOp",EDGE,"E39"),sQuery(id+"F2.wireOp",EDGE,"E40"),sQuery(id+"F2.wireOp",EDGE,"E41"),sQuery(id+"F2.wireOp",EDGE,"E42"),sQuery(id+"F2.wireOp",EDGE,"E43"),sQuery(id+"F2.wireOp",EDGE,"E44"),sQuery(id+"F2.wireOp",EDGE,"E45"),sQuery(id+"F2.wireOp",EDGE,"E46"),sQuery(id+"F2.wireOp",EDGE,"E47"),sQuery(id+"F2.wireOp",EDGE,"E48"),sQuery(id+"F2.wireOp",EDGE,"E49"),sQuery(id+"F2.wireOp",EDGE,"E50"),sQuery(id+"F2.wireOp",EDGE,"E51"),sQuery(id+"F2.wireOp",EDGE,"E52"),sQuery(id+"F2.wireOp",EDGE,"E53"),sQuery(id+"F2.wireOp",EDGE,"E54"),sQuery(id+"F2.wireOp",EDGE,"E55"),sQuery(id+"F2.wireOp",EDGE,"E56"),sQuery(id+"F2.wireOp",EDGE,"E57"),sQuery(id+"F2.wireOp",EDGE,"E58"),sQuery(id+"F2.wireOp",EDGE,"E59"),sQuery(id+"F2.wireOp",EDGE,"E60"),sQuery(id+"F2.wireOp",EDGE,"E61"),sQuery(id+"F2.wireOp",EDGE,"E62"),sQuery(id+"F2.wireOp",EDGE,"E63"),sQuery(id+"F2.wireOp",EDGE,"E64"),sQuery(id+"F2.wireOp",EDGE,"E65"),sQuery(id+"F2.wireOp",EDGE,"E66"),sQuery(id+"F2.wireOp",EDGE,"E67"),sQuery(id+"F2.wireOp",EDGE,"E68"),sQuery(id+"F2.wireOp",EDGE,"E69"),sQuery(id+"F2.wireOp",EDGE,"E70"),sQuery(id+"F2.wireOp",EDGE,"E71"),sQuery(id+"F2.wireOp",EDGE,"E72"),sQuery(id+"F2.wireOp",EDGE,"E73"),sQuery(id+"F2.wireOp",EDGE,"E74"),sQuery(id+"F2.wireOp",EDGE,"E75"),sQuery(id+"F2.wireOp",EDGE,"E76"),sQuery(id+"F2.wireOp",EDGE,"E77"),sQuery(id+"F2.wireOp",EDGE,"E78"),sQuery(id+"F2.wireOp",EDGE,"E79"),sQuery(id+"F2.wireOp",EDGE,"E80"),sQuery(id+"F2.wireOp",EDGE,"E81"),sQuery(id+"F2.wireOp",EDGE,"E82"),sQuery(id+"F2.wireOp",EDGE,"E83"),sQuery(id+"F2.wireOp",EDGE,"E84"),sQuery(id+"F2.wireOp",EDGE,"E85"),sQuery(id+"F2.wireOp",EDGE,"E86"),sQuery(id+"F2.wireOp",EDGE,"E87"),sQuery(id+"F2.wireOp",EDGE,"E88"),sQuery(id+"F2.wireOp",EDGE,"E89"),sQuery(id+"F2.wireOp",EDGE,"E90"),sQuery(id+"F2.wireOp",EDGE,"E91"),sQuery(id+"F2.wireOp",EDGE,"E92"),sQuery(id+"F2.wireOp",EDGE,"E93"),sQuery(id+"F2.wireOp",EDGE,"E94"),sQuery(id+"F2.wireOp",EDGE,"E95"),sQuery(id+"F2.wireOp",EDGE,"E96"),sQuery(id+"F2.wireOp",EDGE,"E97"),sQuery(id+"F2.wireOp",EDGE,"E98"),sQuery(id+"F2.wireOp",EDGE,"E99"),sQuery(id+"F2.wireOp",EDGE,"E100"),sQuery(id+"F2.wireOp",EDGE,"E101"),sQuery(id+"F2.wireOp",EDGE,"E102"),sQuery(id+"F2.wireOp",EDGE,"E103"),sQuery(id+"F2.wireOp",EDGE,"E104"),sQuery(id+"F2.wireOp",EDGE,"E105"),sQuery(id+"F2.wireOp",EDGE,"E106"),sQuery(id+"F2.wireOp",EDGE,"E107"),sQuery(id+"F2.wireOp",EDGE,"E108"),sQuery(id+"F2.wireOp",EDGE,"E109"),sQuery(id+"F2.wireOp",EDGE,"E110"),sQuery(id+"F2.wireOp",EDGE,"E111"),sQuery(id+"F2.wireOp",EDGE,"E112"),sQuery(id+"F2.wireOp",EDGE,"E113"),sQuery(id+"F2.wireOp",EDGE,"E114"),sQuery(id+"F2.wireOp",EDGE,"E115"),sQuery(id+"F2.wireOp",EDGE,"E116"),sQuery(id+"F2.wireOp",EDGE,"E117"),sQuery(id+"F2.wireOp",EDGE,"E118"),sQuery(id+"F2.wireOp",EDGE,"E119"),sQuery(id+"F2.wireOp",EDGE,"E120"),sQuery(id+"F2.wireOp",EDGE,"E121"),sQuery(id+"F2.wireOp",EDGE,"E122"),sQuery(id+"F2.wireOp",EDGE,"E123"),sQuery(id+"F2.wireOp",EDGE,"E124"),sQuery(id+"F2.wireOp",EDGE,"E125"),sQuery(id+"F2.wireOp",EDGE,"E126"),sQuery(id+"F2.wireOp",EDGE,"E127"),sQuery(id+"F2.wireOp",EDGE,"E128"),sQuery(id+"F2.wireOp",EDGE,"E129"),sQuery(id+"F2.wireOp",EDGE,"E130"),sQuery(id+"F2.wireOp",EDGE,"E131"),sQuery(id+"F2.wireOp",EDGE,"E132"),sQuery(id+"F2.wireOp",EDGE,"E133"),sQuery(id+"F2.wireOp",EDGE,"E134"),sQuery(id+"F2.wireOp",EDGE,"E135"),sQuery(id+"F2.wireOp",EDGE,"E136"),sQuery(id+"F2.wireOp",EDGE,"E137"),sQuery(id+"F2.wireOp",EDGE,"E138"),sQuery(id+"F2.wireOp",EDGE,"E139"),sQuery(id+"F2.wireOp",EDGE,"E140"),sQuery(id+"F2.wireOp",EDGE,"E141"),sQuery(id+"F2.wireOp",EDGE,"E142"),sQuery(id+"F2.wireOp",EDGE,"E143"),sQuery(id+"F2.wireOp",EDGE,"E144"),sQuery(id+"F2.wireOp",EDGE,"E145"),sQuery(id+"F2.wireOp",EDGE,"E146"),sQuery(id+"F2.wireOp",EDGE,"E147"),sQuery(id+"F2.wireOp",EDGE,"E148"),sQuery(id+"F2.wireOp",EDGE,"E149"),sQuery(id+"F2.wireOp",EDGE,"E150"),sQuery(id+"F2.wireOp",EDGE,"E151"),sQuery(id+"F2.wireOp",EDGE,"E152"),sQuery(id+"F2.wireOp",EDGE,"E153"),sQuery(id+"F2.wireOp",EDGE,"E154"),sQuery(id+"F2.wireOp",EDGE,"E155"),sQuery(id+"F2.wireOp",EDGE,"E156"),sQuery(id+"F2.wireOp",EDGE,"E157"),sQuery(id+"F2.wireOp",EDGE,"E158"),sQuery(id+"F2.wireOp",EDGE,"E159"),sQuery(id+"F2.wireOp",EDGE,"E160"),sQuery(id+"F2.wireOp",EDGE,"E161"),sQuery(id+"F2.wireOp",EDGE,"E162"),sQuery(id+"F2.wireOp",EDGE,"E163"),sQuery(id+"F2.wireOp",EDGE,"E164"),sQuery(id+"F2.wireOp",EDGE,"E165"),sQuery(id+"F2.wireOp",EDGE,"E166"),sQuery(id+"F2.wireOp",EDGE,"E167"),sQuery(id+"F2.wireOp",EDGE,"E168"),sQuery(id+"F2.wireOp",EDGE,"E169"),sQuery(id+"F2.wireOp",EDGE,"E170"),sQuery(id+"F2.wireOp",EDGE,"E171"),sQuery(id+"F2.wireOp",EDGE,"E172"),sQuery(id+"F2.wireOp",EDGE,"E173"),sQuery(id+"F2.wireOp",EDGE,"E174"),sQuery(id+"F2.wireOp",EDGE,"E175"),sQuery(id+"F2.wireOp",EDGE,"E176"),sQuery(id+"F2.wireOp",EDGE,"E177"),sQuery(id+"F2.wireOp",EDGE,"E178"),sQuery(id+"F2.wireOp",EDGE,"E179"),sQuery(id+"F2.wireOp",EDGE,"E180"),sQuery(id+"F2.wireOp",EDGE,"E181"),sQuery(id+"F2.wireOp",EDGE,"E182"),sQuery(id+"F2.wireOp",EDGE,"E183"),sQuery(id+"F2.wireOp",EDGE,"E184"),sQuery(id+"F2.wireOp",EDGE,"E185"),sQuery(id+"F2.wireOp",EDGE,"E186"),sQuery(id+"F2.wireOp",EDGE,"E187"),sQuery(id+"F2.wireOp",EDGE,"E188"),sQuery(id+"F2.wireOp",EDGE,"E189"),sQuery(id+"F2.wireOp",EDGE,"E190"),sQuery(id+"F2.wireOp",EDGE,"E191"),sQuery(id+"F2.wireOp",EDGE,"E192"),sQuery(id+"F2.wireOp",EDGE,"E193"),sQuery(id+"F2.wireOp",EDGE,"E194"),sQuery(id+"F2.wireOp",EDGE,"E195"),sQuery(id+"F2.wireOp",EDGE,"E196"),sQuery(id+"F2.wireOp",EDGE,"E197"),sQuery(id+"F2.wireOp",EDGE,"E198"),sQuery(id+"F2.wireOp",EDGE,"E199"),sQuery(id+"F2.wireOp",EDGE,"E200"),sQuery(id+"F2.wireOp",EDGE,"E201"),sQuery(id+"F2.wireOp",EDGE,"E202"),sQuery(id+"F2.wireOp",EDGE,"E203"),sQuery(id+"F2.wireOp",EDGE,"E204"),sQuery(id+"F2.wireOp",EDGE,"E205"),sQuery(id+"F2.wireOp",EDGE,"E206"),sQuery(id+"F2.wireOp",EDGE,"E207"),sQuery(id+"F2.wireOp",EDGE,"E208"),sQuery(id+"F2.wireOp",EDGE,"E209"),sQuery(id+"F2.wireOp",EDGE,"E210"),sQuery(id+"F2.wireOp",EDGE,"E211"),sQuery(id+"F2.wireOp",EDGE,"E212"),sQuery(id+"F2.wireOp",EDGE,"E213"),sQuery(id+"F2.wireOp",EDGE,"E214"),sQuery(id+"F2.wireOp",EDGE,"E215"),sQuery(id+"F2.wireOp",EDGE,"E216"),sQuery(id+"F2.wireOp",EDGE,"E217"),sQuery(id+"F2.wireOp",EDGE,"E218"),sQuery(id+"F2.wireOp",EDGE,"E219"),sQuery(id+"F2.wireOp",EDGE,"E220"),sQuery(id+"F2.wireOp",EDGE,"E221"),sQuery(id+"F2.wireOp",EDGE,"E222"),sQuery(id+"F2.wireOp",EDGE,"E223"),sQuery(id+"F2.wireOp",EDGE,"E224"),sQuery(id+"F2.wireOp",EDGE,"E225"),sQuery(id+"F2.wireOp",EDGE,"E226"),sQuery(id+"F2.wireOp",EDGE,"E227"),sQuery(id+"F2.wireOp",EDGE,"E228"),sQuery(id+"F2.wireOp",EDGE,"E229"),sQuery(id+"F2.wireOp",EDGE,"E230"),sQuery(id+"F2.wireOp",EDGE,"E231"),sQuery(id+"F2.wireOp",EDGE,"E232"),sQuery(id+"F2.wireOp",EDGE,"E233"),sQuery(id+"F2.wireOp",EDGE,"E234"),sQuery(id+"F2.wireOp",EDGE,"E235"),sQuery(id+"F2.wireOp",EDGE,"E236"),sQuery(id+"F2.wireOp",EDGE,"E237"),sQuery(id+"F2.wireOp",EDGE,"E238"),sQuery(id+"F2.wireOp",EDGE,"E239"),sQuery(id+"F2.wireOp",EDGE,"E240"),sQuery(id+"F2.wireOp",EDGE,"E241"),sQuery(id+"F2.wireOp",EDGE,"E242"),sQuery(id+"F2.wireOp",EDGE,"E243"),sQuery(id+"F2.wireOp",EDGE,"E244"),sQuery(id+"F2.wireOp",EDGE,"E245"),sQuery(id+"F2.wireOp",EDGE,"E246"),sQuery(id+"F2.wireOp",EDGE,"E247"),sQuery(id+"F2.wireOp",EDGE,"E248"),sQuery(id+"F2.wireOp",EDGE,"E249"),sQuery(id+"F2.wireOp",EDGE,"E250"),sQuery(id+"F2.wireOp",EDGE,"E251"),sQuery(id+"F2.wireOp",EDGE,"E252"),sQuery(id+"F2.wireOp",EDGE,"E253"),sQuery(id+"F2.wireOp",EDGE,"E254"),sQuery(id+"F2.wireOp",EDGE,"E255"),sQuery(id+"F2.wireOp",EDGE,"E256"),sQuery(id+"F2.wireOp",EDGE,"E257"),sQuery(id+"F2.wireOp",EDGE,"E258"),sQuery(id+"F2.wireOp",EDGE,"E259"),sQuery(id+"F2.wireOp",EDGE,"E260"),sQuery(id+"F2.wireOp",EDGE,"E261"),sQuery(id+"F2.wireOp",EDGE,"E262"),sQuery(id+"F2.wireOp",EDGE,"E263"),sQuery(id+"F2.wireOp",EDGE,"E264"),sQuery(id+"F2.wireOp",EDGE,"E265"),sQuery(id+"F2.wireOp",EDGE,"E266"),sQuery(id+"F2.wireOp",EDGE,"E267"),sQuery(id+"F2.wireOp",EDGE,"E268"),sQuery(id+"F2.wireOp",EDGE,"E269"),sQuery(id+"F2.wireOp",EDGE,"E270"),sQuery(id+"F2.wireOp",EDGE,"E271"),sQuery(id+"F2.wireOp",EDGE,"E272"),sQuery(id+"F2.wireOp",EDGE,"E273"),sQuery(id+"F2.wireOp",EDGE,"E274"),sQuery(id+"F2.wireOp",EDGE,"E275"),sQuery(id+"F2.wireOp",EDGE,"E276"),sQuery(id+"F2.wireOp",EDGE,"E277"),sQuery(id+"F2.wireOp",EDGE,"E278"),sQuery(id+"F2.wireOp",EDGE,"E279"),sQuery(id+"F2.wireOp",EDGE,"E280"),sQuery(id+"F2.wireOp",EDGE,"E281"),sQuery(id+"F2.wireOp",EDGE,"E282"),sQuery(id+"F2.wireOp",EDGE,"E283"),sQuery(id+"F2.wireOp",EDGE,"E284"),sQuery(id+"F2.wireOp",EDGE,"E285"),sQuery(id+"F2.wireOp",EDGE,"E286"),sQuery(id+"F2.wireOp",EDGE,"E287"),sQuery(id+"F2.wireOp",EDGE,"E288"),sQuery(id+"F2.wireOp",EDGE,"E289"),sQuery(id+"F2.wireOp",EDGE,"E290"),sQuery(id+"F2.wireOp",EDGE,"E291"),sQuery(id+"F2.wireOp",EDGE,"E292"),sQuery(id+"F2.wireOp",EDGE,"E293"),sQuery(id+"F2.wireOp",EDGE,"E294"),sQuery(id+"F2.wireOp",EDGE,"E295"),sQuery(id+"F2.wireOp",EDGE,"E296"),sQuery(id+"F2.wireOp",EDGE,"E297"),sQuery(id+"F2.wireOp",EDGE,"E298"),sQuery(id+"F2.wireOp",EDGE,"E299"),sQuery(id+"F2.wireOp",EDGE,"E300"),sQuery(id+"F2.wireOp",EDGE,"E301"),sQuery(id+"F2.wireOp",EDGE,"E302"),sQuery(id+"F2.wireOp",EDGE,"E303"),sQuery(id+"F2.wireOp",EDGE,"E304"),sQuery(id+"F2.wireOp",EDGE,"E305"),sQuery(id+"F2.wireOp",EDGE,"E306"),sQuery(id+"F2.wireOp",EDGE,"E307"),sQuery(id+"F2.wireOp",EDGE,"E308"),sQuery(id+"F2.wireOp",EDGE,"E309"),sQuery(id+"F2.wireOp",EDGE,"E310"),sQuery(id+"F2.wireOp",EDGE,"E311"),sQuery(id+"F2.wireOp",EDGE,"E312"),sQuery(id+"F2.wireOp",EDGE,"E313"),sQuery(id+"F2.wireOp",EDGE,"E314"),sQuery(id+"F2.wireOp",EDGE,"E315"),sQuery(id+"F2.wireOp",EDGE,"E316"),sQuery(id+"F2.wireOp",EDGE,"E317"),sQuery(id+"F2.wireOp",EDGE,"E318"),sQuery(id+"F2.wireOp",EDGE,"E319"),sQuery(id+"F2.wireOp",EDGE,"E320"),sQuery(id+"F2.wireOp",EDGE,"E321"),sQuery(id+"F2.wireOp",EDGE,"E322"),sQuery(id+"F2.wireOp",EDGE,"E323"),sQuery(id+"F2.wireOp",EDGE,"E324"),sQuery(id+"F2.wireOp",EDGE,"E325"),sQuery(id+"F2.wireOp",EDGE,"E326"),sQuery(id+"F2.wireOp",EDGE,"E327"),sQuery(id+"F2.wireOp",EDGE,"E328"),sQuery(id+"F2.wireOp",EDGE,"E329"),sQuery(id+"F2.wireOp",EDGE,"E330"),sQuery(id+"F2.wireOp",EDGE,"E331"),sQuery(id+"F2.wireOp",EDGE,"E332"),sQuery(id+"F2.wireOp",EDGE,"E333"),sQuery(id+"F2.wireOp",EDGE,"E334"),sQuery(id+"F2.wireOp",EDGE,"E335"),sQuery(id+"F2.wireOp",EDGE,"E336"),sQuery(id+"F2.wireOp",EDGE,"E337"),sQuery(id+"F2.wireOp",EDGE,"E338"),sQuery(id+"F2.wireOp",EDGE,"E339"),sQuery(id+"F2.wireOp",EDGE,"E340"),sQuery(id+"F2.wireOp",EDGE,"E341"),sQuery(id+"F2.wireOp",EDGE,"E342"),sQuery(id+"F2.wireOp",EDGE,"E343"),sQuery(id+"F2.wireOp",EDGE,"E344"),sQuery(id+"F2.wireOp",EDGE,"E345"),sQuery(id+"F2.wireOp",EDGE,"E346"),sQuery(id+"F2.wireOp",EDGE,"E347"),sQuery(id+"F2.wireOp",EDGE,"E348"),sQuery(id+"F2.wireOp",EDGE,"E349"),sQuery(id+"F2.wireOp",EDGE,"E350"),sQuery(id+"F2.wireOp",EDGE,"E351"),sQuery(id+"F2.wireOp",EDGE,"E352"),sQuery(id+"F2.wireOp",EDGE,"E353"),sQuery(id+"F2.wireOp",EDGE,"E354"),sQuery(id+"F2.wireOp",EDGE,"E355"),sQuery(id+"F2.wireOp",EDGE,"E356"),sQuery(id+"F2.wireOp",EDGE,"E357"),sQuery(id+"F2.wireOp",EDGE,"E358"),sQuery(id+"F2.wireOp",EDGE,"E359"),sQuery(id+"F2.wireOp",EDGE,"E360"),sQuery(id+"F2.wireOp",EDGE,"E361"),sQuery(id+"F2.wireOp",EDGE,"E362"),sQuery(id+"F2.wireOp",EDGE,"E363"),sQuery(id+"F2.wireOp",EDGE,"E364"),sQuery(id+"F2.wireOp",EDGE,"E365"),sQuery(id+"F2.wireOp",EDGE,"E366"),sQuery(id+"F2.wireOp",EDGE,"E367"),sQuery(id+"F2.wireOp",EDGE,"E368"),sQuery(id+"F2.wireOp",EDGE,"E369"),sQuery(id+"F2.wireOp",EDGE,"E370"),sQuery(id+"F2.wireOp",EDGE,"E371"),sQuery(id+"F2.wireOp",EDGE,"E372"),sQuery(id+"F2.wireOp",EDGE,"E373"),sQuery(id+"F2.wireOp",EDGE,"E374"),sQuery(id+"F2.wireOp",EDGE,"E375"),sQuery(id+"F2.wireOp",EDGE,"E376"),sQuery(id+"F2.wireOp",EDGE,"E377"),sQuery(id+"F2.wireOp",EDGE,"E378"),sQuery(id+"F2.wireOp",EDGE,"E379"),sQuery(id+"F2.wireOp",EDGE,"E380"),sQuery(id+"F2.wireOp",EDGE,"E381"),sQuery(id+"F2.wireOp",EDGE,"E382"),sQuery(id+"F2.wireOp",EDGE,"E383"),sQuery(id+"F2.wireOp",EDGE,"E384"),sQuery(id+"F2.wireOp",EDGE,"E385"),sQuery(id+"F2.wireOp",EDGE,"E386"),sQuery(id+"F2.wireOp",EDGE,"E387"),sQuery(id+"F2.wireOp",EDGE,"E388"),sQuery(id+"F2.wireOp",EDGE,"E389"),sQuery(id+"F2.wireOp",EDGE,"E390"),sQuery(id+"F2.wireOp",EDGE,"E391"),sQuery(id+"F2.wireOp",EDGE,"E392"),sQuery(id+"F2.wireOp",EDGE,"E393"),sQuery(id+"F2.wireOp",EDGE,"E394"),sQuery(id+"F2.wireOp",EDGE,"E395"),sQuery(id+"F2.wireOp",EDGE,"E396"),sQuery(id+"F2.wireOp",EDGE,"E397"),sQuery(id+"F2.wireOp",EDGE,"E398"),sQuery(id+"F2.wireOp",EDGE,"E399"),sQuery(id+"F2.wireOp",EDGE,"E400"),sQuery(id+"F2.wireOp",EDGE,"E401"),sQuery(id+"F2.wireOp",EDGE,"E402"),sQuery(id+"F2.wireOp",EDGE,"E403"),sQuery(id+"F2.wireOp",EDGE,"E404"),sQuery(id+"F2.wireOp",EDGE,"E405"),sQuery(id+"F2.wireOp",EDGE,"E406"),sQuery(id+"F2.wireOp",EDGE,"E407"),sQuery(id+"F2.wireOp",EDGE,"E408"),sQuery(id+"F2.wireOp",EDGE,"E409"),sQuery(id+"F2.wireOp",EDGE,"E410"),sQuery(id+"F2.wireOp",EDGE,"E411"),sQuery(id+"F2.wireOp",EDGE,"E412"),sQuery(id+"F2.wireOp",EDGE,"E413"),sQuery(id+"F2.wireOp",EDGE,"E414"),sQuery(id+"F2.wireOp",EDGE,"E415"),sQuery(id+"F2.wireOp",EDGE,"E416"),sQuery(id+"F2.wireOp",EDGE,"E417"),sQuery(id+"F2.wireOp",EDGE,"E418"),sQuery(id+"F2.wireOp",EDGE,"E419"),sQuery(id+"F2.wireOp",EDGE,"E420"),sQuery(id+"F2.wireOp",EDGE,"E421"),sQuery(id+"F2.wireOp",EDGE,"E422"),sQuery(id+"F2.wireOp",EDGE,"E423"),sQuery(id+"F2.wireOp",EDGE,"E424"),sQuery(id+"F2.wireOp",EDGE,"E425"),sQuery(id+"F2.wireOp",EDGE,"E426"),sQuery(id+"F2.wireOp",EDGE,"E427"),sQuery(id+"F2.wireOp",EDGE,"E428"),sQuery(id+"F2.wireOp",EDGE,"E429"),sQuery(id+"F2.wireOp",EDGE,"E430"),sQuery(id+"F2.wireOp",EDGE,"E431"),sQuery(id+"F2.wireOp",EDGE,"E432"),sQuery(id+"F2.wireOp",EDGE,"E433"),sQuery(id+"F2.wireOp",EDGE,"E434"),sQuery(id+"F2.wireOp",EDGE,"E435"),sQuery(id+"F2.wireOp",EDGE,"E436"),sQuery(id+"F2.wireOp",EDGE,"E437"),sQuery(id+"F2.wireOp",EDGE,"E438"),sQuery(id+"F2.wireOp",EDGE,"E439"),sQuery(id+"F2.wireOp",EDGE,"E440"),sQuery(id+"F2.wireOp",EDGE,"E441"),sQuery(id+"F2.wireOp",EDGE,"E442"),sQuery(id+"F2.wireOp",EDGE,"E443"),sQuery(id+"F2.wireOp",EDGE,"E444"),sQuery(id+"F2.wireOp",EDGE,"E445"),sQuery(id+"F2.wireOp",EDGE,"E446"),sQuery(id+"F2.wireOp",EDGE,"E447"),sQuery(id+"F2.wireOp",EDGE,"E447"),sQuery(id+"F2.wireOp",EDGE,"E447"),sQuery(id+"F2.wireOp",EDGE,"E448"),sQuery(id+"F2.wireOp",EDGE,"E449"),sQuery(id+"F2.wireOp",EDGE,"E450"),sQuery(id+"F2.wireOp",EDGE,"E451"),sQuery(id+"F2.wireOp",EDGE,"E452"),sQuery(id+"F2.wireOp",EDGE,"E453"),sQuery(id+"F2.wireOp",EDGE,"E454"),sQuery(id+"F2.wireOp",EDGE,"E455"),sQuery(id+"F2.wireOp",EDGE,"E456"),sQuery(id+"F2.wireOp",EDGE,"E457"),sQuery(id+"F2.wireOp",EDGE,"E458"),sQuery(id+"F2.wireOp",EDGE,"E459"),sQuery(id+"F2.wireOp",EDGE,"E460"),sQuery(id+"F2.wireOp",EDGE,"E461"),sQuery(id+"F2.wireOp",EDGE,"E462"),sQuery(id+"F2.wireOp",EDGE,"E463"),sQuery(id+"F2.wireOp",EDGE,"E464"),sQuery(id+"F2.wireOp",EDGE,"E465"),sQuery(id+"F2.wireOp",EDGE,"E466"),sQuery(id+"F2.wireOp",EDGE,"E467"),sQuery(id+"F2.wireOp",EDGE,"E468"),sQuery(id+"F2.wireOp",EDGE,"E469"),sQuery(id+"F2.wireOp",EDGE,"E470"),sQuery(id+"F2.wireOp",EDGE,"E471"),sQuery(id+"F2.wireOp",EDGE,"E472"),sQuery(id+"F2.wireOp",EDGE,"E473"),sQuery(id+"F2.wireOp",EDGE,"E474"),sQuery(id+"F2.wireOp",EDGE,"E475"),sQuery(id+"F2.wireOp",EDGE,"E476"),sQuery(id+"F2.wireOp",EDGE,"E477"),sQuery(id+"F2.wireOp",EDGE,"E478"),sQuery(id+"F2.wireOp",EDGE,"E479"),sQuery(id+"F2.wireOp",EDGE,"E480"),sQuery(id+"F2.wireOp",EDGE,"E481"),sQuery(id+"F2.wireOp",EDGE,"E482"),sQuery(id+"F2.wireOp",EDGE,"E483"),sQuery(id+"F2.wireOp",EDGE,"E484"),sQuery(id+"F2.wireOp",EDGE,"E485"),sQuery(id+"F2.wireOp",EDGE,"E486"),sQuery(id+"F2.wireOp",EDGE,"E487"),sQuery(id+"F2.wireOp",EDGE,"E488"),sQuery(id+"F2.wireOp",EDGE,"E489"),sQuery(id+"F2.wireOp",EDGE,"E490"),sQuery(id+"F2.wireOp",EDGE,"E491"),sQuery(id+"F2.wireOp",EDGE,"E492"),sQuery(id+"F2.wireOp",EDGE,"E493"),sQuery(id+"F2.wireOp",EDGE,"E494"),sQuery(id+"F2.wireOp",EDGE,"E495"),sQuery(id+"F2.wireOp",EDGE,"E496"),sQuery(id+"F2.wireOp",EDGE,"E497"),sQuery(id+"F2.wireOp",EDGE,"E498"),sQuery(id+"F2.wireOp",EDGE,"E499"),sQuery(id+"F2.wireOp",EDGE,"E500"),sQuery(id+"F2.wireOp",EDGE,"E501"),sQuery(id+"F2.wireOp",EDGE,"E502"),sQuery(id+"F2.wireOp",EDGE,"E503"),sQuery(id+"F2.wireOp",EDGE,"E504"),sQuery(id+"F2.wireOp",EDGE,"E505"),sQuery(id+"F2.wireOp",EDGE,"E506"),sQuery(id+"F2.wireOp",EDGE,"E507"),sQuery(id+"F2.wireOp",EDGE,"E508"),sQuery(id+"F2.wireOp",EDGE,"E509"),sQuery(id+"F2.wireOp",EDGE,"E510"),sQuery(id+"F2.wireOp",EDGE,"E511"),sQuery(id+"F2.wireOp",EDGE,"E512"),sQuery(id+"F2.wireOp",EDGE,"E513"),sQuery(id+"F2.wireOp",EDGE,"E514"),sQuery(id+"F2.wireOp",EDGE,"E515"),sQuery(id+"F2.wireOp",EDGE,"E516"),sQuery(id+"F2.wireOp",EDGE,"E517"),sQuery(id+"F2.wireOp",EDGE,"E518"),sQuery(id+"F2.wireOp",EDGE,"E519"),sQuery(id+"F2.wireOp",EDGE,"E520"),sQuery(id+"F2.wireOp",EDGE,"E521"),sQuery(id+"F2.wireOp",EDGE,"E522"),sQuery(id+"F2.wireOp",EDGE,"E523"),sQuery(id+"F2.wireOp",EDGE,"E524"),sQuery(id+"F2.wireOp",EDGE,"E525"),sQuery(id+"F2.wireOp",EDGE,"E526"),sQuery(id+"F2.wireOp",EDGE,"E527"),sQuery(id+"F2.wireOp",EDGE,"E528"),sQuery(id+"F2.wireOp",EDGE,"E529"),sQuery(id+"F2.wireOp",EDGE,"E530"),sQuery(id+"F2.wireOp",EDGE,"E531"),sQuery(id+"F2.wireOp",EDGE,"E532"),sQuery(id+"F2.wireOp",EDGE,"E533"),sQuery(id+"F2.wireOp",EDGE,"E534"),sQuery(id+"F2.wireOp",EDGE,"E535"),sQuery(id+"F2.wireOp",EDGE,"E536"),sQuery(id+"F2.wireOp",EDGE,"E537"),sQuery(id+"F2.wireOp",EDGE,"E538"),sQuery(id+"F2.wireOp",EDGE,"E539"),sQuery(id+"F2.wireOp",EDGE,"E540"),sQuery(id+"F2.wireOp",EDGE,"E541"),sQuery(id+"F2.wireOp",EDGE,"E542"),sQuery(id+"F2.wireOp",EDGE,"E543"),sQuery(id+"F2.wireOp",EDGE,"E544"),sQuery(id+"F2.wireOp",EDGE,"E545"),sQuery(id+"F2.wireOp",EDGE,"E546"),sQuery(id+"F2.wireOp",EDGE,"E547"),sQuery(id+"F2.wireOp",EDGE,"E547"),sQuery(id+"F2.wireOp",EDGE,"E548"),sQuery(id+"F2.wireOp",EDGE,"E549"),sQuery(id+"F2.wireOp",EDGE,"E550"),sQuery(id+"F2.wireOp",EDGE,"E551"),sQuery(id+"F2.wireOp",EDGE,"E552"),sQuery(id+"F2.wireOp",EDGE,"E553"),sQuery(id+"F2.wireOp",EDGE,"E554"),sQuery(id+"F2.wireOp",EDGE,"E555"),sQuery(id+"F2.wireOp",EDGE,"E556"),sQuery(id+"F2.wireOp",EDGE,"E557"),sQuery(id+"F2.wireOp",EDGE,"E558"),sQuery(id+"F2.wireOp",EDGE,"E559"),sQuery(id+"F2.wireOp",EDGE,"E560"),sQuery(id+"F2.wireOp",EDGE,"E561"),sQuery(id+"F2.wireOp",EDGE,"E562"),sQuery(id+"F2.wireOp",EDGE,"E563"),sQuery(id+"F2.wireOp",EDGE,"E564"),sQuery(id+"F2.wireOp",EDGE,"E565"),sQuery(id+"F2.wireOp",EDGE,"E566"),sQuery(id+"F2.wireOp",EDGE,"E567"),sQuery(id+"F2.wireOp",EDGE,"E568"),sQuery(id+"F2.wireOp",EDGE,"E569"),sQuery(id+"F2.wireOp",EDGE,"E570"),sQuery(id+"F2.wireOp",EDGE,"E571"),sQuery(id+"F2.wireOp",EDGE,"E572"),sQuery(id+"F2.wireOp",EDGE,"E573"),sQuery(id+"F2.wireOp",EDGE,"E574"),sQuery(id+"F2.wireOp",EDGE,"E575"),sQuery(id+"F2.wireOp",EDGE,"E576"),sQuery(id+"F2.wireOp",EDGE,"E577"),sQuery(id+"F2.wireOp",EDGE,"E578"),sQuery(id+"F2.wireOp",EDGE,"E579"),sQuery(id+"F2.wireOp",EDGE,"E580"),sQuery(id+"F2.wireOp",EDGE,"E581"),sQuery(id+"F2.wireOp",EDGE,"E582"),sQuery(id+"F2.wireOp",EDGE,"E583"),sQuery(id+"F2.wireOp",EDGE,"E584"),sQuery(id+"F2.wireOp",EDGE,"E585"),sQuery(id+"F2.wireOp",EDGE,"E586"),sQuery(id+"F2.wireOp",EDGE,"E587"),sQuery(id+"F2.wireOp",EDGE,"E588"),sQuery(id+"F2.wireOp",EDGE,"E589"),sQuery(id+"F2.wireOp",EDGE,"E590"),sQuery(id+"F2.wireOp",EDGE,"E591"),sQuery(id+"F2.wireOp",EDGE,"E592"),sQuery(id+"F2.wireOp",EDGE,"E593"),sQuery(id+"F2.wireOp",EDGE,"E594"),sQuery(id+"F2.wireOp",EDGE,"E595"),sQuery(id+"F2.wireOp",EDGE,"E596"),sQuery(id+"F2.wireOp",EDGE,"E597"),sQuery(id+"F2.wireOp",EDGE,"E598"),sQuery(id+"F2.wireOp",EDGE,"E599"),sQuery(id+"F2.wireOp",EDGE,"E600"),sQuery(id+"F2.wireOp",EDGE,"E601"),sQuery(id+"F2.wireOp",EDGE,"E602"),sQuery(id+"F2.wireOp",EDGE,"E603"),sQuery(id+"F2.wireOp",EDGE,"E604"),sQuery(id+"F2.wireOp",EDGE,"E605"),sQuery(id+"F2.wireOp",EDGE,"E606"),sQuery(id+"F2.wireOp",EDGE,"E607"),sQuery(id+"F2.wireOp",EDGE,"E608"),sQuery(id+"F2.wireOp",EDGE,"E609"),sQuery(id+"F2.wireOp",EDGE,"E610"),sQuery(id+"F2.wireOp",EDGE,"E611"),sQuery(id+"F2.wireOp",EDGE,"E612"),sQuery(id+"F2.wireOp",EDGE,"E613"),sQuery(id+"F2.wireOp",EDGE,"E614"),sQuery(id+"F2.wireOp",EDGE,"E615"),sQuery(id+"F2.wireOp",EDGE,"E616"),sQuery(id+"F2.wireOp",EDGE,"E617"),sQuery(id+"F2.wireOp",EDGE,"E618"),sQuery(id+"F2.wireOp",EDGE,"E619"),sQuery(id+"F2.wireOp",EDGE,"E620"),sQuery(id+"F2.wireOp",EDGE,"E621"),sQuery(id+"F2.wireOp",EDGE,"E622"),sQuery(id+"F2.wireOp",EDGE,"E623"),sQuery(id+"F2.wireOp",EDGE,"E624"),sQuery(id+"F2.wireOp",EDGE,"E625"),sQuery(id+"F2.wireOp",EDGE,"E626"),sQuery(id+"F2.wireOp",EDGE,"E627"),sQuery(id+"F2.wireOp",EDGE,"E628"),sQuery(id+"F2.wireOp",EDGE,"E629"),sQuery(id+"F2.wireOp",EDGE,"E630"),sQuery(id+"F2.wireOp",EDGE,"E631"),sQuery(id+"F2.wireOp",EDGE,"E632"),sQuery(id+"F2.wireOp",EDGE,"E633"),sQuery(id+"F2.wireOp",EDGE,"E634"),sQuery(id+"F2.wireOp",EDGE,"E635"),sQuery(id+"F2.wireOp",EDGE,"E636"),sQuery(id+"F2.wireOp",EDGE,"E637"),sQuery(id+"F2.wireOp",EDGE,"E638"),sQuery(id+"F2.wireOp",EDGE,"E639"),sQuery(id+"F2.wireOp",EDGE,"E640"),sQuery(id+"F2.wireOp",EDGE,"E641"),sQuery(id+"F2.wireOp",EDGE,"E642"),sQuery(id+"F2.wireOp",EDGE,"E643"),sQuery(id+"F2.wireOp",EDGE,"E644"),sQuery(id+"F2.wireOp",EDGE,"E645"),sQuery(id+"F2.wireOp",EDGE,"E646"),sQuery(id+"F2.wireOp",EDGE,"E647"),sQuery(id+"F2.wireOp",EDGE,"E648"),sQuery(id+"F2.wireOp",EDGE,"E649"),sQuery(id+"F2.wireOp",EDGE,"E650"),sQuery(id+"F2.wireOp",EDGE,"E651"),sQuery(id+"F2.wireOp",EDGE,"E652"),sQuery(id+"F2.wireOp",EDGE,"E653"),sQuery(id+"F2.wireOp",EDGE,"E654"),sQuery(id+"F2.wireOp",EDGE,"E655"),sQuery(id+"F2.wireOp",EDGE,"E656"),sQuery(id+"F2.wireOp",EDGE,"E657"),sQuery(id+"F2.wireOp",EDGE,"E658"),sQuery(id+"F2.wireOp",EDGE,"E659"),sQuery(id+"F2.wireOp",EDGE,"E660"),sQuery(id+"F2.wireOp",EDGE,"E661"),sQuery(id+"F2.wireOp",EDGE,"E662"),sQuery(id+"F2.wireOp",EDGE,"E663"),sQuery(id+"F2.wireOp",EDGE,"E664"),sQuery(id+"F2.wireOp",EDGE,"E665"),sQuery(id+"F2.wireOp",EDGE,"E666"),sQuery(id+"F2.wireOp",EDGE,"E667"),sQuery(id+"F2.wireOp",EDGE,"E668"),sQuery(id+"F2.wireOp",EDGE,"E669"),sQuery(id+"F2.wireOp",EDGE,"E670"),sQuery(id+"F2.wireOp",EDGE,"E671"),sQuery(id+"F2.wireOp",EDGE,"E672"),sQuery(id+"F2.wireOp",EDGE,"E673"),sQuery(id+"F2.wireOp",EDGE,"E674"),sQuery(id+"F2.wireOp",EDGE,"E675"),sQuery(id+"F2.wireOp",EDGE,"E676"),sQuery(id+"F2.wireOp",EDGE,"E677"),sQuery(id+"F2.wireOp",EDGE,"E678"),sQuery(id+"F2.wireOp",EDGE,"E679"),sQuery(id+"F2.wireOp",EDGE,"E680"),sQuery(id+"F2.wireOp",EDGE,"E681"),sQuery(id+"F2.wireOp",EDGE,"E682"),sQuery(id+"F2.wireOp",EDGE,"E683"),sQuery(id+"F2.wireOp",EDGE,"E684"),sQuery(id+"F2.wireOp",EDGE,"E685"),sQuery(id+"F2.wireOp",EDGE,"E686"),sQuery(id+"F2.wireOp",EDGE,"E687"),sQuery(id+"F2.wireOp",EDGE,"E688"),sQuery(id+"F2.wireOp",EDGE,"E689"),sQuery(id+"F2.wireOp",EDGE,"E690"),sQuery(id+"F2.wireOp",EDGE,"E691"),sQuery(id+"F2.wireOp",EDGE,"E692"),sQuery(id+"F2.wireOp",EDGE,"E693"),sQuery(id+"F2.wireOp",EDGE,"E694"),sQuery(id+"F2.wireOp",EDGE,"E695"),sQuery(id+"F2.wireOp",EDGE,"E696"),sQuery(id+"F2.wireOp",EDGE,"E697"),sQuery(id+"F2.wireOp",EDGE,"E698"),sQuery(id+"F2.wireOp",EDGE,"E699"),sQuery(id+"F2.wireOp",EDGE,"E700"),sQuery(id+"F2.wireOp",EDGE,"E701"),sQuery(id+"F2.wireOp",EDGE,"E702"),sQuery(id+"F2.wireOp",EDGE,"E703"),sQuery(id+"F2.wireOp",EDGE,"E704"),sQuery(id+"F2.wireOp",EDGE,"E705"),sQuery(id+"F2.wireOp",EDGE,"E706"),sQuery(id+"F2.wireOp",EDGE,"E707"),sQuery(id+"F2.wireOp",EDGE,"E708"),sQuery(id+"F2.wireOp",EDGE,"E709"),sQuery(id+"F2.wireOp",EDGE,"E710"),sQuery(id+"F2.wireOp",EDGE,"E711"),sQuery(id+"F2.wireOp",EDGE,"E712"),sQuery(id+"F2.wireOp",EDGE,"E713"),sQuery(id+"F2.wireOp",EDGE,"E714"),sQuery(id+"F2.wireOp",EDGE,"E715"),sQuery(id+"F2.wireOp",EDGE,"E716"),sQuery(id+"F2.wireOp",EDGE,"E717"),sQuery(id+"F2.wireOp",EDGE,"E718"),sQuery(id+"F2.wireOp",EDGE,"E719"),sQuery(id+"F2.wireOp",EDGE,"E720"),sQuery(id+"F2.wireOp",EDGE,"E721"),sQuery(id+"F2.wireOp",EDGE,"E722"),sQuery(id+"F2.wireOp",EDGE,"E723"),sQuery(id+"F2.wireOp",EDGE,"E724"),sQuery(id+"F2.wireOp",EDGE,"E725"),sQuery(id+"F2.wireOp",EDGE,"E726"),sQuery(id+"F2.wireOp",EDGE,"E727"),sQuery(id+"F2.wireOp",EDGE,"E728"),sQuery(id+"F2.wireOp",EDGE,"E729"),sQuery(id+"F2.wireOp",EDGE,"E730"),sQuery(id+"F2.wireOp",EDGE,"E731"),sQuery(id+"F2.wireOp",EDGE,"E732"),sQuery(id+"F2.wireOp",EDGE,"E733"),sQuery(id+"F2.wireOp",EDGE,"E734"),sQuery(id+"F2.wireOp",EDGE,"E735"),sQuery(id+"F2.wireOp",EDGE,"E736"),sQuery(id+"F2.wireOp",EDGE,"E737"),sQuery(id+"F2.wireOp",EDGE,"E738"),sQuery(id+"F2.wireOp",EDGE,"E739"),sQuery(id+"F2.wireOp",EDGE,"E740"),sQuery(id+"F2.wireOp",EDGE,"E741"),sQuery(id+"F2.wireOp",EDGE,"E742"),sQuery(id+"F2.wireOp",EDGE,"E743"),sQuery(id+"F2.wireOp",EDGE,"E744"),sQuery(id+"F2.wireOp",EDGE,"E745"),sQuery(id+"F2.wireOp",EDGE,"E746"),sQuery(id+"F2.wireOp",EDGE,"E747"),sQuery(id+"F2.wireOp",EDGE,"E748"),sQuery(id+"F2.wireOp",EDGE,"E749"),sQuery(id+"F2.wireOp",EDGE,"E750"),sQuery(id+"F2.wireOp",EDGE,"E751"),sQuery(id+"F2.wireOp",EDGE,"E752"),sQuery(id+"F2.wireOp",EDGE,"E753"),sQuery(id+"F2.wireOp",EDGE,"E754"),sQuery(id+"F2.wireOp",EDGE,"E755"),sQuery(id+"F2.wireOp",EDGE,"E756"),sQuery(id+"F2.wireOp",EDGE,"E757"),sQuery(id+"F2.wireOp",EDGE,"E758"),sQuery(id+"F2.wireOp",EDGE,"E759"),sQuery(id+"F2.wireOp",EDGE,"E760"),sQuery(id+"F2.wireOp",EDGE,"E761"),sQuery(id+"F2.wireOp",EDGE,"E762"),sQuery(id+"F2.wireOp",EDGE,"E763"),sQuery(id+"F2.wireOp",EDGE,"E764"),sQuery(id+"F2.wireOp",EDGE,"E765"),sQuery(id+"F2.wireOp",EDGE,"E766"),sQuery(id+"F2.wireOp",EDGE,"E767"),sQuery(id+"F2.wireOp",EDGE,"E768"),sQuery(id+"F2.wireOp",EDGE,"E769"),sQuery(id+"F2.wireOp",EDGE,"E770"),sQuery(id+"F2.wireOp",EDGE,"E771"),sQuery(id+"F2.wireOp",EDGE,"E772"),sQuery(id+"F2.wireOp",EDGE,"E773"),sQuery(id+"F2.wireOp",EDGE,"E774"),sQuery(id+"F2.wireOp",EDGE,"E775"),sQuery(id+"F2.wireOp",EDGE,"E776"),sQuery(id+"F2.wireOp",EDGE,"E777"),sQuery(id+"F2.wireOp",EDGE,"E778"),sQuery(id+"F2.wireOp",EDGE,"E779"),sQuery(id+"F2.wireOp",EDGE,"E780"),sQuery(id+"F2.wireOp",EDGE,"E781"),sQuery(id+"F2.wireOp",EDGE,"E782"),sQuery(id+"F2.wireOp",EDGE,"E783"),sQuery(id+"F2.wireOp",EDGE,"E784"),sQuery(id+"F2.wireOp",EDGE,"E785"),sQuery(id+"F2.wireOp",EDGE,"E786"),sQuery(id+"F2.wireOp",EDGE,"E787"),sQuery(id+"F2.wireOp",EDGE,"E788"),sQuery(id+"F2.wireOp",EDGE,"E789"),sQuery(id+"F2.wireOp",EDGE,"E790"),sQuery(id+"F2.wireOp",EDGE,"E791"),sQuery(id+"F2.wireOp",EDGE,"E792"),sQuery(id+"F2.wireOp",EDGE,"E793"),sQuery(id+"F2.wireOp",EDGE,"E794"),sQuery(id+"F2.wireOp",EDGE,"E795"),sQuery(id+"F2.wireOp",EDGE,"E796"),sQuery(id+"F2.wireOp",EDGE,"E797"),sQuery(id+"F2.wireOp",EDGE,"E798"),sQuery(id+"F2.wireOp",EDGE,"E799"),sQuery(id+"F2.wireOp",EDGE,"E800"),sQuery(id+"F2.wireOp",EDGE,"E801"),sQuery(id+"F2.wireOp",EDGE,"E802"),sQuery(id+"F2.wireOp",EDGE,"E803"),sQuery(id+"F2.wireOp",EDGE,"E804"),sQuery(id+"F2.wireOp",EDGE,"E805"),sQuery(id+"F2.wireOp",EDGE,"E806"),sQuery(id+"F2.wireOp",EDGE,"E807"),sQuery(id+"F2.wireOp",EDGE,"E808"),sQuery(id+"F2.wireOp",EDGE,"E809"),sQuery(id+"F2.wireOp",EDGE,"E810"),sQuery(id+"F2.wireOp",EDGE,"E811"),sQuery(id+"F2.wireOp",EDGE,"E812"),sQuery(id+"F2.wireOp",EDGE,"E813"),sQuery(id+"F2.wireOp",EDGE,"E814"),sQuery(id+"F2.wireOp",EDGE,"E815"),sQuery(id+"F2.wireOp",EDGE,"E816"),sQuery(id+"F2.wireOp",EDGE,"E817"),sQuery(id+"F2.wireOp",EDGE,"E818"),sQuery(id+"F2.wireOp",EDGE,"E819"),sQuery(id+"F2.wireOp",EDGE,"E820"),sQuery(id+"F2.wireOp",EDGE,"E821"),sQuery(id+"F2.wireOp",EDGE,"E822"),sQuery(id+"F2.wireOp",EDGE,"E823"),sQuery(id+"F2.wireOp",EDGE,"E824"),sQuery(id+"F2.wireOp",EDGE,"E825"),sQuery(id+"F2.wireOp",EDGE,"E826"),sQuery(id+"F2.wireOp",EDGE,"E827"),sQuery(id+"F2.wireOp",EDGE,"E828"),sQuery(id+"F2.wireOp",EDGE,"E829"),sQuery(id+"F2.wireOp",EDGE,"E830"),sQuery(id+"F2.wireOp",EDGE,"E831"),sQuery(id+"F2.wireOp",EDGE,"E832"),sQuery(id+"F2.wireOp",EDGE,"E833"),sQuery(id+"F2.wireOp",EDGE,"E834"),sQuery(id+"F2.wireOp",EDGE,"E835"),sQuery(id+"F2.wireOp",EDGE,"E836"),sQuery(id+"F2.wireOp",EDGE,"E837"),sQuery(id+"F2.wireOp",EDGE,"E838"),sQuery(id+"F2.wireOp",EDGE,"E839"),sQuery(id+"F2.wireOp",EDGE,"E840"),sQuery(id+"F2.wireOp",EDGE,"E841"),sQuery(id+"F2.wireOp",EDGE,"E842"),sQuery(id+"F2.wireOp",EDGE,"E843"),sQuery(id+"F2.wireOp",EDGE,"E844"),sQuery(id+"F2.wireOp",EDGE,"E845"),sQuery(id+"F2.wireOp",EDGE,"E846"),sQuery(id+"F2.wireOp",EDGE,"E847"),sQuery(id+"F2.wireOp",EDGE,"E848"),sQuery(id+"F2.wireOp",EDGE,"E849"),sQuery(id+"F2.wireOp",EDGE,"E850"),sQuery(id+"F2.wireOp",EDGE,"E851"),sQuery(id+"F2.wireOp",EDGE,"E852"),sQuery(id+"F2.wireOp",EDGE,"E853"),sQuery(id+"F2.wireOp",EDGE,"E854"),sQuery(id+"F2.wireOp",EDGE,"E855"),sQuery(id+"F2.wireOp",EDGE,"E856"),sQuery(id+"F2.wireOp",EDGE,"E857"),sQuery(id+"F2.wireOp",EDGE,"E858"),sQuery(id+"F2.wireOp",EDGE,"E859"),sQuery(id+"F2.wireOp",EDGE,"E860"),sQuery(id+"F2.wireOp",EDGE,"E861"),sQuery(id+"F2.wireOp",EDGE,"E862"),sQuery(id+"F2.wireOp",EDGE,"E863"),sQuery(id+"F2.wireOp",EDGE,"E864"),sQuery(id+"F2.wireOp",EDGE,"E865"),sQuery(id+"F2.wireOp",EDGE,"E866"),sQuery(id+"F2.wireOp",EDGE,"E867"),sQuery(id+"F2.wireOp",EDGE,"E868"),sQuery(id+"F2.wireOp",EDGE,"E869"),sQuery(id+"F2.wireOp",EDGE,"E870"),sQuery(id+"F2.wireOp",EDGE,"E871"),sQuery(id+"F2.wireOp",EDGE,"E872"),sQuery(id+"F2.wireOp",EDGE,"E873"),sQuery(id+"F2.wireOp",EDGE,"E874"),sQuery(id+"F2.wireOp",EDGE,"E875"),sQuery(id+"F2.wireOp",EDGE,"E876"),sQuery(id+"F2.wireOp",EDGE,"E877"),sQuery(id+"F2.wireOp",EDGE,"E878"),sQuery(id+"F2.wireOp",EDGE,"E879"),sQuery(id+"F2.wireOp",EDGE,"E880"),sQuery(id+"F2.wireOp",EDGE,"E881"),sQuery(id+"F2.wireOp",EDGE,"E882"),sQuery(id+"F2.wireOp",EDGE,"E883"),sQuery(id+"F2.wireOp",EDGE,"E884"),sQuery(id+"F2.wireOp",EDGE,"E885"),sQuery(id+"F2.wireOp",EDGE,"E886"),sQuery(id+"F2.wireOp",EDGE,"E887"),sQuery(id+"F2.wireOp",EDGE,"E888"),sQuery(id+"F2.wireOp",EDGE,"E889"),sQuery(id+"F2.wireOp",EDGE,"E890"),sQuery(id+"F2.wireOp",EDGE,"E891"),sQuery(id+"F2.wireOp",EDGE,"E892"),sQuery(id+"F2.wireOp",EDGE,"E893"),sQuery(id+"F2.wireOp",EDGE,"E894"),sQuery(id+"F2.wireOp",EDGE,"E895"),sQuery(id+"F2.wireOp",EDGE,"E896"),sQuery(id+"F2.wireOp",EDGE,"E897"),sQuery(id+"F2.wireOp",EDGE,"E898"),sQuery(id+"F2.wireOp",EDGE,"E899"),sQuery(id+"F2.wireOp",EDGE,"E900"),sQuery(id+"F2.wireOp",EDGE,"E901"),sQuery(id+"F2.wireOp",EDGE,"E902"),sQuery(id+"F2.wireOp",EDGE,"E903"),sQuery(id+"F2.wireOp",EDGE,"E904"),sQuery(id+"F2.wireOp",EDGE,"E905"),sQuery(id+"F2.wireOp",EDGE,"E906"),sQuery(id+"F2.wireOp",EDGE,"E907"),sQuery(id+"F2.wireOp",EDGE,"E908"),sQuery(id+"F2.wireOp",EDGE,"E909"),sQuery(id+"F2.wireOp",EDGE,"E910"),sQuery(id+"F2.wireOp",EDGE,"E911"),sQuery(id+"F2.wireOp",EDGE,"E912"),sQuery(id+"F2.wireOp",EDGE,"E913"),sQuery(id+"F2.wireOp",EDGE,"E914"),sQuery(id+"F2.wireOp",EDGE,"E915"),sQuery(id+"F2.wireOp",EDGE,"E916"),sQuery(id+"F2.wireOp",EDGE,"E917"),sQuery(id+"F2.wireOp",EDGE,"E918"),sQuery(id+"F2.wireOp",EDGE,"E919"),sQuery(id+"F2.wireOp",EDGE,"E920"),sQuery(id+"F2.wireOp",EDGE,"E921"),sQuery(id+"F2.wireOp",EDGE,"E922"),sQuery(id+"F2.wireOp",EDGE,"E923"),sQuery(id+"F2.wireOp",EDGE,"E924"),sQuery(id+"F2.wireOp",EDGE,"E925"),sQuery(id+"F2.wireOp",EDGE,"E926"),sQuery(id+"F2.wireOp",EDGE,"E927"),sQuery(id+"F2.wireOp",EDGE,"E928"),sQuery(id+"F2.wireOp",EDGE,"E929"),sQuery(id+"F2.wireOp",EDGE,"E930"),sQuery(id+"F2.wireOp",EDGE,"E931"),sQuery(id+"F2.wireOp",EDGE,"E932"),sQuery(id+"F2.wireOp",EDGE,"E933"),sQuery(id+"F2.wireOp",EDGE,"E934"),sQuery(id+"F2.wireOp",EDGE,"E935"),sQuery(id+"F2.wireOp",EDGE,"E936"),sQuery(id+"F2.wireOp",EDGE,"E937"),sQuery(id+"F2.wireOp",EDGE,"E938"),sQuery(id+"F2.wireOp",EDGE,"E939"),sQuery(id+"F2.wireOp",EDGE,"E940"),sQuery(id+"F2.wireOp",EDGE,"E941"),sQuery(id+"F2.wireOp",EDGE,"E942"),sQuery(id+"F2.wireOp",EDGE,"E943"),sQuery(id+"F2.wireOp",EDGE,"E944"),sQuery(id+"F2.wireOp",EDGE,"E945"),sQuery(id+"F2.wireOp",EDGE,"E946"),sQuery(id+"F2.wireOp",EDGE,"E947"),sQuery(id+"F2.wireOp",EDGE,"E948"),sQuery(id+"F2.wireOp",EDGE,"E949"),sQuery(id+"F2.wireOp",EDGE,"E950"),sQuery(id+"F2.wireOp",EDGE,"E951"),sQuery(id+"F2.wireOp",EDGE,"E952"),sQuery(id+"F2.wireOp",EDGE,"E953"),sQuery(id+"F2.wireOp",EDGE,"E954"),sQuery(id+"F2.wireOp",EDGE,"E955"),sQuery(id+"F2.wireOp",EDGE,"E956"),sQuery(id+"F2.wireOp",EDGE,"E957"),sQuery(id+"F2.wireOp",EDGE,"E958"),sQuery(id+"F2.wireOp",EDGE,"E959"),sQuery(id+"F2.wireOp",EDGE,"E960"),sQuery(id+"F2.wireOp",EDGE,"E961"),sQuery(id+"F2.wireOp",EDGE,"E962"),sQuery(id+"F2.wireOp",EDGE,"E963"),sQuery(id+"F2.wireOp",EDGE,"E964"),sQuery(id+"F2.wireOp",EDGE,"E965"),sQuery(id+"F2.wireOp",EDGE,"E966"),sQuery(id+"F2.wireOp",EDGE,"E967"),sQuery(id+"F2.wireOp",EDGE,"E968"),sQuery(id+"F2.wireOp",EDGE,"E969"),sQuery(id+"F2.wireOp",EDGE,"E970"),sQuery(id+"F2.wireOp",EDGE,"E971"),sQuery(id+"F2.wireOp",EDGE,"E972"),sQuery(id+"F2.wireOp",EDGE,"E973"),sQuery(id+"F2.wireOp",EDGE,"E974"),sQuery(id+"F2.wireOp",EDGE,"E975"),sQuery(id+"F2.wireOp",EDGE,"E976"),sQuery(id+"F2.wireOp",EDGE,"E977"),sQuery(id+"F2.wireOp",EDGE,"E978"),sQuery(id+"F2.wireOp",EDGE,"E979"),sQuery(id+"F2.wireOp",EDGE,"E980"),sQuery(id+"F2.wireOp",EDGE,"E981"),sQuery(id+"F2.wireOp",EDGE,"E982"),sQuery(id+"F2.wireOp",EDGE,"E983"),sQuery(id+"F2.wireOp",EDGE,"E984"),sQuery(id+"F2.wireOp",EDGE,"E985"),sQuery(id+"F2.wireOp",EDGE,"E986"),sQuery(id+"F2.wireOp",EDGE,"E987"),sQuery(id+"F2.wireOp",EDGE,"E988"),sQuery(id+"F2.wireOp",EDGE,"E989"),sQuery(id+"F2.wireOp",EDGE,"E990"),sQuery(id+"F2.wireOp",EDGE,"E991"),sQuery(id+"F2.wireOp",EDGE,"E992"),sQuery(id+"F2.wireOp",EDGE,"E993"),sQuery(id+"F2.wireOp",EDGE,"E994"),sQuery(id+"F2.wireOp",EDGE,"E995"),sQuery(id+"F2.wireOp",EDGE,"E996"),sQuery(id+"F2.wireOp",EDGE,"E997"),sQuery(id+"F2.wireOp",EDGE,"E998"),sQuery(id+"F2.wireOp",EDGE,"E999"),sQuery(id+"F2.wireOp",EDGE,"E1000"),sQuery(id+"F2.wireOp",EDGE,"E1001"),sQuery(id+"F2.wireOp",EDGE,"E1002"),sQuery(id+"F2.wireOp",EDGE,"E1003"),sQuery(id+"F2.wireOp",EDGE,"E1004"),sQuery(id+"F2.wireOp",EDGE,"E1005"),sQuery(id+"F2.wireOp",EDGE,"E1006"),sQuery(id+"F2.wireOp",EDGE,"E1007"),sQuery(id+"F2.wireOp",EDGE,"E1008"),sQuery(id+"F2.wireOp",EDGE,"E1009"),sQuery(id+"F2.wireOp",EDGE,"E1010"),sQuery(id+"F2.wireOp",EDGE,"E1011"),sQuery(id+"F2.wireOp",EDGE,"E1012"),sQuery(id+"F2.wireOp",EDGE,"E1013"),sQuery(id+"F2.wireOp",EDGE,"E1014"),sQuery(id+"F2.wireOp",EDGE,"E1015"),sQuery(id+"F2.wireOp",EDGE,"E1016"),sQuery(id+"F2.wireOp",EDGE,"E1017"),sQuery(id+"F2.wireOp",EDGE,"E1018"),sQuery(id+"F2.wireOp",EDGE,"E1019"),sQuery(id+"F2.wireOp",EDGE,"E1020"),sQuery(id+"F2.wireOp",EDGE,"E1021"),sQuery(id+"F2.wireOp",EDGE,"E1022"),sQuery(id+"F2.wireOp",EDGE,"E1023"),sQuery(id+"F2.wireOp",EDGE,"E1024"),sQuery(id+"F2.wireOp",EDGE,"E1025"),sQuery(id+"F2.wireOp",EDGE,"E1026"),sQuery(id+"F2.wireOp",EDGE,"E1027"),sQuery(id+"F2.wireOp",EDGE,"E1028"),sQuery(id+"F2.wireOp",EDGE,"E1029"),sQuery(id+"F2.wireOp",EDGE,"E1030"),sQuery(id+"F2.wireOp",EDGE,"E1031"),sQuery(id+"F2.wireOp",EDGE,"E1032"),sQuery(id+"F2.wireOp",EDGE,"E1033"),sQuery(id+"F2.wireOp",EDGE,"E1034"),sQuery(id+"F2.wireOp",EDGE,"E1035"),sQuery(id+"F2.wireOp",EDGE,"E1036"),sQuery(id+"F2.wireOp",EDGE,"E1037"),sQuery(id+"F2.wireOp",EDGE,"E1038"),sQuery(id+"F2.wireOp",EDGE,"E1039"),sQuery(id+"F2.wireOp",EDGE,"E1040"),sQuery(id+"F2.wireOp",EDGE,"E1041"),sQuery(id+"F2.wireOp",EDGE,"E1042"),sQuery(id+"F2.wireOp",EDGE,"E1043"),sQuery(id+"F2.wireOp",EDGE,"E1044"),sQuery(id+"F2.wireOp",EDGE,"E1045"),sQuery(id+"F2.wireOp",EDGE,"E1046"),sQuery(id+"F2.wireOp",EDGE,"E1047"),sQuery(id+"F2.wireOp",EDGE,"E1048"),sQuery(id+"F2.wireOp",EDGE,"E1049"),sQuery(id+"F2.wireOp",EDGE,"E1050"),sQuery(id+"F2.wireOp",EDGE,"E1051"),sQuery(id+"F2.wireOp",EDGE,"E1052"),sQuery(id+"F2.wireOp",EDGE,"E1053"),sQuery(id+"F2.wireOp",EDGE,"E1054"),sQuery(id+"F2.wireOp",EDGE,"E1055"),sQuery(id+"F2.wireOp",EDGE,"E1056"),sQuery(id+"F2.wireOp",EDGE,"E1057"),sQuery(id+"F2.wireOp",EDGE,"E1058"),sQuery(id+"F2.wireOp",EDGE,"E1059"),sQuery(id+"F2.wireOp",EDGE,"E1060"),sQuery(id+"F2.wireOp",EDGE,"E1061"),sQuery(id+"F2.wireOp",EDGE,"E1062"),sQuery(id+"F2.wireOp",EDGE,"E1063"),sQuery(id+"F2.wireOp",EDGE,"E1064"),sQuery(id+"F2.wireOp",EDGE,"E1065"),sQuery(id+"F2.wireOp",EDGE,"E1066"),sQuery(id+"F2.wireOp",EDGE,"E1067"),sQuery(id+"F2.wireOp",EDGE,"E1068"),sQuery(id+"F2.wireOp",EDGE,"E1069"),sQuery(id+"F2.wireOp",EDGE,"E1070"),sQuery(id+"F2.wireOp",EDGE,"E1071"),sQuery(id+"F2.wireOp",EDGE,"E1072"),sQuery(id+"F2.wireOp",EDGE,"E1073"),sQuery(id+"F2.wireOp",EDGE,"E1074"),sQuery(id+"F2.wireOp",EDGE,"E1075"),sQuery(id+"F2.wireOp",EDGE,"E1076"),sQuery(id+"F2.wireOp",EDGE,"E1077"),sQuery(id+"F2.wireOp",EDGE,"E1078"),sQuery(id+"F2.wireOp",EDGE,"E1079"),sQuery(id+"F2.wireOp",EDGE,"E1080"),sQuery(id+"F2.wireOp",EDGE,"E1081"),sQuery(id+"F2.wireOp",EDGE,"E1082"),sQuery(id+"F2.wireOp",EDGE,"E1083"),sQuery(id+"F2.wireOp",EDGE,"E1084"),sQuery(id+"F2.wireOp",EDGE,"E1085"),sQuery(id+"F2.wireOp",EDGE,"E1086"),sQuery(id+"F2.wireOp",EDGE,"E1087"),sQuery(id+"F2.wireOp",EDGE,"E1088"),sQuery(id+"F2.wireOp",EDGE,"E1089"),sQuery(id+"F2.wireOp",EDGE,"E1090"),sQuery(id+"F2.wireOp",EDGE,"E1091"),sQuery(id+"F2.wireOp",EDGE,"E1092"),sQuery(id+"F2.wireOp",EDGE,"E1093"),sQuery(id+"F2.wireOp",EDGE,"E1094"),sQuery(id+"F2.wireOp",EDGE,"E1095"),sQuery(id+"F2.wireOp",EDGE,"E1096"),sQuery(id+"F2.wireOp",EDGE,"E1097"),sQuery(id+"F2.wireOp",EDGE,"E1098"),sQuery(id+"F2.wireOp",EDGE,"E1099"),sQuery(id+"F2.wireOp",EDGE,"E1100"),sQuery(id+"F2.wireOp",EDGE,"E1101"),sQuery(id+"F2.wireOp",EDGE,"E1102"),sQuery(id+"F2.wireOp",EDGE,"E1103"),sQuery(id+"F2.wireOp",EDGE,"E1104"),sQuery(id+"F2.wireOp",EDGE,"E1105"),sQuery(id+"F2.wireOp",EDGE,"E1106"),sQuery(id+"F2.wireOp",EDGE,"E1107"),sQuery(id+"F2.wireOp",EDGE,"E1108"),sQuery(id+"F2.wireOp",EDGE,"E1109"),sQuery(id+"F2.wireOp",EDGE,"E1110"),sQuery(id+"F2.wireOp",EDGE,"E1111"),sQuery(id+"F2.wireOp",EDGE,"E1112"),sQuery(id+"F2.wireOp",EDGE,"E1113"),sQuery(id+"F2.wireOp",EDGE,"E1114"),sQuery(id+"F2.wireOp",EDGE,"E1115"),sQuery(id+"F2.wireOp",EDGE,"E1116"),sQuery(id+"F2.wireOp",EDGE,"E1117"),sQuery(id+"F2.wireOp",EDGE,"E1118"),sQuery(id+"F2.wireOp",EDGE,"E1119"),sQuery(id+"F2.wireOp",EDGE,"E1120"),sQuery(id+"F2.wireOp",EDGE,"E1121"),sQuery(id+"F2.wireOp",EDGE,"E1122"),sQuery(id+"F2.wireOp",EDGE,"E1123"),sQuery(id+"F2.wireOp",EDGE,"E1124"),sQuery(id+"F2.wireOp",EDGE,"E1125"),sQuery(id+"F2.wireOp",EDGE,"E1126"),sQuery(id+"F2.wireOp",EDGE,"E1127"),sQuery(id+"F2.wireOp",EDGE,"E1128"),sQuery(id+"F2.wireOp",EDGE,"E1129"),sQuery(id+"F2.wireOp",EDGE,"E1130"),sQuery(id+"F2.wireOp",EDGE,"E1131"),sQuery(id+"F2.wireOp",EDGE,"E1132"),sQuery(id+"F2.wireOp",EDGE,"E1133"),sQuery(id+"F2.wireOp",EDGE,"E1134"),sQuery(id+"F2.wireOp",EDGE,"E1135"),sQuery(id+"F2.wireOp",EDGE,"E1136"),sQuery(id+"F2.wireOp",EDGE,"E1137"),sQuery(id+"F2.wireOp",EDGE,"E1138"),sQuery(id+"F2.wireOp",EDGE,"E1139"),sQuery(id+"F2.wireOp",EDGE,"E1140"),sQuery(id+"F2.wireOp",EDGE,"E1141"),sQuery(id+"F2.wireOp",EDGE,"E1142"),sQuery(id+"F2.wireOp",EDGE,"E1143"),sQuery(id+"F2.wireOp",EDGE,"E1144"),sQuery(id+"F2.wireOp",EDGE,"E1145"),sQuery(id+"F2.wireOp",EDGE,"E1146"),sQuery(id+"F2.wireOp",EDGE,"E1147"),sQuery(id+"F2.wireOp",EDGE,"E1148"),sQuery(id+"F2.wireOp",EDGE,"E1149"),sQuery(id+"F2.wireOp",EDGE,"E1150"),sQuery(id+"F2.wireOp",EDGE,"E1151"),sQuery(id+"F2.wireOp",EDGE,"E1152"),sQuery(id+"F2.wireOp",EDGE,"E1153"),sQuery(id+"F2.wireOp",EDGE,"E1154"),sQuery(id+"F2.wireOp",EDGE,"E1155"),sQuery(id+"F2.wireOp",EDGE,"E1156"),sQuery(id+"F2.wireOp",EDGE,"E1157"),sQuery(id+"F2.wireOp",EDGE,"E1158"),sQuery(id+"F2.wireOp",EDGE,"E1159"),sQuery(id+"F2.wireOp",EDGE,"E1160"),sQuery(id+"F2.wireOp",EDGE,"E1161"),sQuery(id+"F2.wireOp",EDGE,"E1162"),sQuery(id+"F2.wireOp",EDGE,"E1163"),sQuery(id+"F2.wireOp",EDGE,"E1164"),sQuery(id+"F2.wireOp",EDGE,"E1165"),sQuery(id+"F2.wireOp",EDGE,"E1166"),sQuery(id+"F2.wireOp",EDGE,"E1167"),sQuery(id+"F2.wireOp",EDGE,"E1168"),sQuery(id+"F2.wireOp",EDGE,"E1169"),sQuery(id+"F2.wireOp",EDGE,"E1170"),sQuery(id+"F2.wireOp",EDGE,"E1171"),sQuery(id+"F2.wireOp",EDGE,"E1172"),sQuery(id+"F2.wireOp",EDGE,"E1173"),sQuery(id+"F2.wireOp",EDGE,"E1174"),sQuery(id+"F2.wireOp",EDGE,"E1175"),sQuery(id+"F2.wireOp",EDGE,"E1176"),sQuery(id+"F2.wireOp",EDGE,"E1177"),sQuery(id+"F2.wireOp",EDGE,"E1178"),sQuery(id+"F2.wireOp",EDGE,"E1179"),sQuery(id+"F2.wireOp",EDGE,"E1180"),sQuery(id+"F2.wireOp",EDGE,"E1181"),sQuery(id+"F2.wireOp",EDGE,"E1182"),sQuery(id+"F2.wireOp",EDGE,"E1183"),sQuery(id+"F2.wireOp",EDGE,"E1184"),sQuery(id+"F2.wireOp",EDGE,"E1185"),sQuery(id+"F2.wireOp",EDGE,"E1186"),sQuery(id+"F2.wireOp",EDGE,"E1187"),sQuery(id+"F2.wireOp",EDGE,"E1188"),sQuery(id+"F2.wireOp",EDGE,"E1189"),sQuery(id+"F2.wireOp",EDGE,"E1190"),sQuery(id+"F2.wireOp",EDGE,"E1191"),sQuery(id+"F2.wireOp",EDGE,"E1192"),sQuery(id+"F2.wireOp",EDGE,"E1193"),sQuery(id+"F2.wireOp",EDGE,"E1194"),sQuery(id+"F2.wireOp",EDGE,"E1195"),sQuery(id+"F2.wireOp",EDGE,"E1196"),sQuery(id+"F2.wireOp",EDGE,"E1197"),sQuery(id+"F2.wireOp",EDGE,"E1198"),sQuery(id+"F2.wireOp",EDGE,"E1199"),sQuery(id+"F2.wireOp",EDGE,"E1200"),sQuery(id+"F2.wireOp",EDGE,"E1201"),sQuery(id+"F2.wireOp",EDGE,"E1202"),sQuery(id+"F2.wireOp",EDGE,"E1203"),sQuery(id+"F2.wireOp",EDGE,"E1204"),sQuery(id+"F2.wireOp",EDGE,"E1205"),sQuery(id+"F2.wireOp",EDGE,"E1206"),sQuery(id+"F2.wireOp",EDGE,"E1207"),sQuery(id+"F2.wireOp",EDGE,"E1208"),sQuery(id+"F2.wireOp",EDGE,"E1209"),sQuery(id+"F2.wireOp",EDGE,"E1210"),sQuery(id+"F2.wireOp",EDGE,"E1211"),sQuery(id+"F2.wireOp",EDGE,"E1212"),sQuery(id+"F2.wireOp",EDGE,"E1213"),sQuery(id+"F2.wireOp",EDGE,"E1214"),sQuery(id+"F2.wireOp",EDGE,"E1215"),sQuery(id+"F2.wireOp",EDGE,"E1216"),sQuery(id+"F2.wireOp",EDGE,"E1217"),sQuery(id+"F2.wireOp",EDGE,"E1218"),sQuery(id+"F2.wireOp",EDGE,"E1219"),sQuery(id+"F2.wireOp",EDGE,"E1220"),sQuery(id+"F2.wireOp",EDGE,"E1221"),sQuery(id+"F2.wireOp",EDGE,"E1222"),sQuery(id+"F2.wireOp",EDGE,"E1223"),sQuery(id+"F2.wireOp",EDGE,"E1224"),sQuery(id+"F2.wireOp",EDGE,"E1225"),sQuery(id+"F2.wireOp",EDGE,"E1226"),sQuery(id+"F2.wireOp",EDGE,"E1227"),sQuery(id+"F2.wireOp",EDGE,"E1228"),sQuery(id+"F2.wireOp",EDGE,"E1229"),sQuery(id+"F2.wireOp",EDGE,"E1230"),sQuery(id+"F2.wireOp",EDGE,"E1231"),sQuery(id+"F2.wireOp",EDGE,"E1232"),sQuery(id+"F2.wireOp",EDGE,"E1233"),sQuery(id+"F2.wireOp",EDGE,"E1234"),sQuery(id+"F2.wireOp",EDGE,"E1235"),sQuery(id+"F2.wireOp",EDGE,"E1236"),sQuery(id+"F2.wireOp",EDGE,"E1237"),sQuery(id+"F2.wireOp",EDGE,"E1238"),sQuery(id+"F2.wireOp",EDGE,"E1239"),sQuery(id+"F2.wireOp",EDGE,"E1240"),sQuery(id+"F2.wireOp",EDGE,"E1241"),sQuery(id+"F2.wireOp",EDGE,"E1242"),sQuery(id+"F2.wireOp",EDGE,"E1243"),sQuery(id+"F2.wireOp",EDGE,"E1244"),sQuery(id+"F2.wireOp",EDGE,"E1245"),sQuery(id+"F2.wireOp",EDGE,"E1246"),sQuery(id+"F2.wireOp",EDGE,"E1247"),sQuery(id+"F2.wireOp",EDGE,"E1248"),sQuery(id+"F2.wireOp",EDGE,"E1249"),sQuery(id+"F2.wireOp",EDGE,"E1250"),sQuery(id+"F2.wireOp",EDGE,"E1251"),sQuery(id+"F2.wireOp",EDGE,"E1252"),sQuery(id+"F2.wireOp",EDGE,"E1253"),sQuery(id+"F2.wireOp",EDGE,"E1254"),sQuery(id+"F2.wireOp",EDGE,"E1255"),sQuery(id+"F2.wireOp",EDGE,"E1256"),sQuery(id+"F2.wireOp",EDGE,"E1257"),sQuery(id+"F2.wireOp",EDGE,"E1258"),sQuery(id+"F2.wireOp",EDGE,"E1259"),sQuery(id+"F2.wireOp",EDGE,"E1260"),sQuery(id+"F2.wireOp",EDGE,"E1261"),sQuery(id+"F2.wireOp",EDGE,"E1262"),sQuery(id+"F2.wireOp",EDGE,"E1263"),sQuery(id+"F2.wireOp",EDGE,"E1264"),sQuery(id+"F2.wireOp",EDGE,"E1265"),sQuery(id+"F2.wireOp",EDGE,"E1266"),sQuery(id+"F2.wireOp",EDGE,"E1267"),sQuery(id+"F2.wireOp",EDGE,"E1268"),sQuery(id+"F2.wireOp",EDGE,"E1269"),sQuery(id+"F2.wireOp",EDGE,"E1270"),sQuery(id+"F2.wireOp",EDGE,"E1271"),sQuery(id+"F2.wireOp",EDGE,"E1272"),sQuery(id+"F2.wireOp",EDGE,"E1273"),sQuery(id+"F2.wireOp",EDGE,"E1274"),sQuery(id+"F2.wireOp",EDGE,"E1275"),sQuery(id+"F2.wireOp",EDGE,"E1276"),sQuery(id+"F2.wireOp",EDGE,"E1277"),sQuery(id+"F2.wireOp",EDGE,"E1278"),sQuery(id+"F2.wireOp",EDGE,"E1279"),sQuery(id+"F2.wireOp",EDGE,"E1280"),sQuery(id+"F2.wireOp",EDGE,"E1281"),sQuery(id+"F2.wireOp",EDGE,"E1282"),sQuery(id+"F2.wireOp",EDGE,"E1283"),sQuery(id+"F2.wireOp",EDGE,"E1284"),sQuery(id+"F2.wireOp",EDGE,"E1285"),sQuery(id+"F2.wireOp",EDGE,"E1286"),sQuery(id+"F2.wireOp",EDGE,"E1287"),sQuery(id+"F2.wireOp",EDGE,"E1288"),sQuery(id+"F2.wireOp",EDGE,"E1289"),sQuery(id+"F2.wireOp",EDGE,"E1290"),sQuery(id+"F2.wireOp",EDGE,"E1291"),sQuery(id+"F2.wireOp",EDGE,"E1292"),sQuery(id+"F2.wireOp",EDGE,"E1293"),sQuery(id+"F2.wireOp",EDGE,"E1294"),sQuery(id+"F2.wireOp",EDGE,"E1295"),sQuery(id+"F2.wireOp",EDGE,"E1296"),sQuery(id+"F2.wireOp",EDGE,"E1297"),sQuery(id+"F2.wireOp",EDGE,"E1298"),sQuery(id+"F2.wireOp",EDGE,"E1299"),sQuery(id+"F2.wireOp",EDGE,"E1300"),sQuery(id+"F2.wireOp",EDGE,"E1301"),sQuery(id+"F2.wireOp",EDGE,"E1302"),sQuery(id+"F2.wireOp",EDGE,"E1303"),sQuery(id+"F2.wireOp",EDGE,"E1304"),sQuery(id+"F2.wireOp",EDGE,"E1305"),sQuery(id+"F2.wireOp",EDGE,"E1306"),sQuery(id+"F2.wireOp",EDGE,"E1307"),sQuery(id+"F2.wireOp",EDGE,"E1308"),sQuery(id+"F2.wireOp",EDGE,"E1309"),sQuery(id+"F2.wireOp",EDGE,"E1310"),sQuery(id+"F2.wireOp",EDGE,"E1311"),sQuery(id+"F2.wireOp",EDGE,"E1312"),sQuery(id+"F2.wireOp",EDGE,"E1313"),sQuery(id+"F2.wireOp",EDGE,"E1314"),sQuery(id+"F2.wireOp",EDGE,"E1315"),sQuery(id+"F2.wireOp",EDGE,"E1316"),sQuery(id+"F2.wireOp",EDGE,"E1317"),sQuery(id+"F2.wireOp",EDGE,"E1318"),sQuery(id+"F2.wireOp",EDGE,"E1319"),sQuery(id+"F2.wireOp",EDGE,"E1320"),sQuery(id+"F2.wireOp",EDGE,"E1321"),sQuery(id+"F2.wireOp",EDGE,"E1322"),sQuery(id+"F2.wireOp",EDGE,"E1323"),sQuery(id+"F2.wireOp",EDGE,"E1324"),sQuery(id+"F2.wireOp",EDGE,"E1325"),sQuery(id+"F2.wireOp",EDGE,"E1326"),sQuery(id+"F2.wireOp",EDGE,"E1327"),sQuery(id+"F2.wireOp",EDGE,"E1328"),sQuery(id+"F2.wireOp",EDGE,"E1329"),sQuery(id+"F2.wireOp",EDGE,"E1330"),sQuery(id+"F2.wireOp",EDGE,"E1331"),sQuery(id+"F2.wireOp",EDGE,"E1332"),sQuery(id+"F2.wireOp",EDGE,"E1333"),sQuery(id+"F2.wireOp",EDGE,"E1334"),sQuery(id+"F2.wireOp",EDGE,"E1335"),sQuery(id+"F2.wireOp",EDGE,"E1336"),sQuery(id+"F2.wireOp",EDGE,"E1337"),sQuery(id+"F2.wireOp",EDGE,"E1338"),sQuery(id+"F2.wireOp",EDGE,"E1339"),sQuery(id+"F2.wireOp",EDGE,"E1340"),sQuery(id+"F2.wireOp",EDGE,"E1341"),sQuery(id+"F2.wireOp",EDGE,"E1342"),sQuery(id+"F2.wireOp",EDGE,"E1343"),sQuery(id+"F2.wireOp",EDGE,"E1344"),sQuery(id+"F2.wireOp",EDGE,"E1345"),sQuery(id+"F2.wireOp",EDGE,"E1346"),sQuery(id+"F2.wireOp",EDGE,"E1347"),sQuery(id+"F2.wireOp",EDGE,"E1348"),sQuery(id+"F2.wireOp",EDGE,"E1349"),sQuery(id+"F2.wireOp",EDGE,"E1350"),sQuery(id+"F2.wireOp",EDGE,"E1351"),sQuery(id+"F2.wireOp",EDGE,"E1352"),sQuery(id+"F2.wireOp",EDGE,"E1353"),sQuery(id+"F2.wireOp",EDGE,"E1354"),sQuery(id+"F2.wireOp",EDGE,"E1355"),sQuery(id+"F2.wireOp",EDGE,"E1356"),sQuery(id+"F2.wireOp",EDGE,"E1357"),sQuery(id+"F2.wireOp",EDGE,"E1358"),sQuery(id+"F2.wireOp",EDGE,"E1359"),sQuery(id+"F2.wireOp",EDGE,"E1360"),sQuery(id+"F2.wireOp",EDGE,"E1361"),sQuery(id+"F2.wireOp",EDGE,"E1362"),sQuery(id+"F2.wireOp",EDGE,"E1363"),sQuery(id+"F2.wireOp",EDGE,"E1364"),sQuery(id+"F2.wireOp",EDGE,"E1365"),sQuery(id+"F2.wireOp",EDGE,"E1366"),sQuery(id+"F2.wireOp",EDGE,"E1367"),sQuery(id+"F2.wireOp",EDGE,"E1368"),sQuery(id+"F2.wireOp",EDGE,"E1369"),sQuery(id+"F2.wireOp",EDGE,"E1370"),sQuery(id+"F2.wireOp",EDGE,"E1371"),sQuery(id+"F2.wireOp",EDGE,"E1372"),sQuery(id+"F2.wireOp",EDGE,"E1373"),sQuery(id+"F2.wireOp",EDGE,"E1374"),sQuery(id+"F2.wireOp",EDGE,"E1375"),sQuery(id+"F2.wireOp",EDGE,"E1376"),sQuery(id+"F2.wireOp",EDGE,"E1377"),sQuery(id+"F2.wireOp",EDGE,"E1378"),sQuery(id+"F2.wireOp",EDGE,"E1379"),sQuery(id+"F2.wireOp",EDGE,"E1380"),sQuery(id+"F2.wireOp",EDGE,"E1381"),sQuery(id+"F2.wireOp",EDGE,"E1382"),sQuery(id+"F2.wireOp",EDGE,"E1383"),sQuery(id+"F2.wireOp",EDGE,"E1384"),sQuery(id+"F2.wireOp",EDGE,"E1385"),sQuery(id+"F2.wireOp",EDGE,"E1386"),sQuery(id+"F2.wireOp",EDGE,"E1387"),sQuery(id+"F2.wireOp",EDGE,"E1388"),sQuery(id+"F2.wireOp",EDGE,"E1389"),sQuery(id+"F2.wireOp",EDGE,"E1390"),sQuery(id+"F2.wireOp",EDGE,"E1391"),sQuery(id+"F2.wireOp",EDGE,"E1392"),sQuery(id+"F2.wireOp",EDGE,"E1393"),sQuery(id+"F2.wireOp",EDGE,"E1394"),sQuery(id+"F2.wireOp",EDGE,"E1395"),sQuery(id+"F2.wireOp",EDGE,"E1396"),sQuery(id+"F2.wireOp",EDGE,"E1397"),sQuery(id+"F2.wireOp",EDGE,"E1398"),sQuery(id+"F2.wireOp",EDGE,"E1399"),sQuery(id+"F2.wireOp",EDGE,"E1400"),sQuery(id+"F2.wireOp",EDGE,"E1401"),sQuery(id+"F2.wireOp",EDGE,"E1402"),sQuery(id+"F2.wireOp",EDGE,"E1403"),sQuery(id+"F2.wireOp",EDGE,"E1404"),sQuery(id+"F2.wireOp",EDGE,"E1405"),sQuery(id+"F2.wireOp",EDGE,"E1406"),sQuery(id+"F2.wireOp",EDGE,"E1407"),sQuery(id+"F2.wireOp",EDGE,"E1408"),sQuery(id+"F2.wireOp",EDGE,"E1409"),sQuery(id+"F2.wireOp",EDGE,"E1410"),sQuery(id+"F2.wireOp",EDGE,"E1411"),sQuery(id+"F2.wireOp",EDGE,"E1412"),sQuery(id+"F2.wireOp",EDGE,"E1413"),sQuery(id+"F2.wireOp",EDGE,"E1414"),sQuery(id+"F2.wireOp",EDGE,"E1415"),sQuery(id+"F2.wireOp",EDGE,"E1416"),sQuery(id+"F2.wireOp",EDGE,"E1417"),sQuery(id+"F2.wireOp",EDGE,"E1418"),sQuery(id+"F2.wireOp",EDGE,"E1419"),sQuery(id+"F2.wireOp",EDGE,"E1420"),sQuery(id+"F2.wireOp",EDGE,"E1421"),sQuery(id+"F2.wireOp",EDGE,"E1422"),sQuery(id+"F2.wireOp",EDGE,"E1423"),sQuery(id+"F2.wireOp",EDGE,"E1424"),sQuery(id+"F2.wireOp",EDGE,"E1425"),sQuery(id+"F2.wireOp",EDGE,"E1426"),sQuery(id+"F2.wireOp",EDGE,"E1427"),sQuery(id+"F2.wireOp",EDGE,"E1428"),sQuery(id+"F2.wireOp",EDGE,"E1429"),sQuery(id+"F2.wireOp",EDGE,"E1430"),sQuery(id+"F2.wireOp",EDGE,"E1431"),sQuery(id+"F2.wireOp",EDGE,"E1432"),sQuery(id+"F2.wireOp",EDGE,"E1433"),sQuery(id+"F2.wireOp",EDGE,"E1434"),sQuery(id+"F2.wireOp",EDGE,"E1435"),sQuery(id+"F2.wireOp",EDGE,"E1436"),sQuery(id+"F2.wireOp",EDGE,"E1437"),sQuery(id+"F2.wireOp",EDGE,"E1438"),sQuery(id+"F2.wireOp",EDGE,"E1439"),sQuery(id+"F2.wireOp",EDGE,"E1440"),sQuery(id+"F2.wireOp",EDGE,"E1441"),sQuery(id+"F2.wireOp",EDGE,"E1442"),sQuery(id+"F2.wireOp",EDGE,"E1443"),sQuery(id+"F2.wireOp",EDGE,"E1444"),sQuery(id+"F2.wireOp",EDGE,"E1445"),sQuery(id+"F2.wireOp",EDGE,"E1446"),sQuery(id+"F2.wireOp",EDGE,"E1447"),sQuery(id+"F2.wireOp",EDGE,"E1448"),sQuery(id+"F2.wireOp",EDGE,"E1449"),sQuery(id+"F2.wireOp",EDGE,"E1450"),sQuery(id+"F2.wireOp",EDGE,"E1451"),sQuery(id+"F2.wireOp",EDGE,"E1452"),sQuery(id+"F2.wireOp",EDGE,"E1453"),sQuery(id+"F2.wireOp",EDGE,"E1454"),sQuery(id+"F2.wireOp",EDGE,"E1455"),sQuery(id+"F2.wireOp",EDGE,"E1456"),sQuery(id+"F2.wireOp",EDGE,"E1457"),sQuery(id+"F2.wireOp",EDGE,"E1458"),sQuery(id+"F2.wireOp",EDGE,"E1459"),sQuery(id+"F2.wireOp",EDGE,"E1460"),sQuery(id+"F2.wireOp",EDGE,"E1461"),sQuery(id+"F2.wireOp",EDGE,"E1462"),sQuery(id+"F2.wireOp",EDGE,"E1463"),sQuery(id+"F2.wireOp",EDGE,"E1464"),sQuery(id+"F2.wireOp",EDGE,"E1465"),sQuery(id+"F2.wireOp",EDGE,"E1466"),sQuery(id+"F2.wireOp",EDGE,"E1467"),sQuery(id+"F2.wireOp",EDGE,"E1468"),sQuery(id+"F2.wireOp",EDGE,"E1469"),sQuery(id+"F2.wireOp",EDGE,"E1470"),sQuery(id+"F2.wireOp",EDGE,"E1471"),sQuery(id+"F2.wireOp",EDGE,"E1472"),sQuery(id+"F2.wireOp",EDGE,"E1473"),sQuery(id+"F2.wireOp",EDGE,"E1474")])]}),"instanceName":"1"});
            var Q1;
            Q1=sQuery(id+"F0.wireOp",VERTEX,"E0.center");
            var Q2;
            Q2=sQuery(id+"F0.wireOp",VERTEX,"E14.MirrorC.center");
            transform(context, id + "F9", {"entities" : qUnion([Q0]), "transformType" : TransformType.TRANSLATION_ENTITY, "oppositeDirectionEntity" : false, "transformLine" : qUnion([Q1, Q2]), "makeCopy" : false});
        }
        {
            var Q0;
            Q0=makeQuery(id+"F3.opExtrude","SWEPT_BODY",BODY,{"disambiguationData":[OSD([sQuery(id+"F2.wireOp",EDGE,"E16"),sQuery(id+"F2.wireOp",EDGE,"E17"),sQuery(id+"F2.wireOp",EDGE,"E18"),sQuery(id+"F2.wireOp",EDGE,"E19"),sQuery(id+"F2.wireOp",EDGE,"E20"),sQuery(id+"F2.wireOp",EDGE,"E21"),sQuery(id+"F2.wireOp",EDGE,"E22"),sQuery(id+"F2.wireOp",EDGE,"E23"),sQuery(id+"F2.wireOp",EDGE,"E24"),sQuery(id+"F2.wireOp",EDGE,"E25"),sQuery(id+"F2.wireOp",EDGE,"E26"),sQuery(id+"F2.wireOp",EDGE,"E27"),sQuery(id+"F2.wireOp",EDGE,"E28"),sQuery(id+"F2.wireOp",EDGE,"E29"),sQuery(id+"F2.wireOp",EDGE,"E30"),sQuery(id+"F2.wireOp",EDGE,"E31"),sQuery(id+"F2.wireOp",EDGE,"E32"),sQuery(id+"F2.wireOp",EDGE,"E33"),sQuery(id+"F2.wireOp",EDGE,"E34"),sQuery(id+"F2.wireOp",EDGE,"E35"),sQuery(id+"F2.wireOp",EDGE,"E36"),sQuery(id+"F2.wireOp",EDGE,"E37"),sQuery(id+"F2.wireOp",EDGE,"E38"),sQuery(id+"F2.wireOp",EDGE,"E39"),sQuery(id+"F2.wireOp",EDGE,"E40"),sQuery(id+"F2.wireOp",EDGE,"E41"),sQuery(id+"F2.wireOp",EDGE,"E42"),sQuery(id+"F2.wireOp",EDGE,"E43"),sQuery(id+"F2.wireOp",EDGE,"E44"),sQuery(id+"F2.wireOp",EDGE,"E45"),sQuery(id+"F2.wireOp",EDGE,"E46"),sQuery(id+"F2.wireOp",EDGE,"E47"),sQuery(id+"F2.wireOp",EDGE,"E48"),sQuery(id+"F2.wireOp",EDGE,"E49"),sQuery(id+"F2.wireOp",EDGE,"E50"),sQuery(id+"F2.wireOp",EDGE,"E51"),sQuery(id+"F2.wireOp",EDGE,"E52"),sQuery(id+"F2.wireOp",EDGE,"E53"),sQuery(id+"F2.wireOp",EDGE,"E54"),sQuery(id+"F2.wireOp",EDGE,"E55"),sQuery(id+"F2.wireOp",EDGE,"E56"),sQuery(id+"F2.wireOp",EDGE,"E57"),sQuery(id+"F2.wireOp",EDGE,"E58"),sQuery(id+"F2.wireOp",EDGE,"E59"),sQuery(id+"F2.wireOp",EDGE,"E60"),sQuery(id+"F2.wireOp",EDGE,"E61"),sQuery(id+"F2.wireOp",EDGE,"E62"),sQuery(id+"F2.wireOp",EDGE,"E63"),sQuery(id+"F2.wireOp",EDGE,"E64"),sQuery(id+"F2.wireOp",EDGE,"E65"),sQuery(id+"F2.wireOp",EDGE,"E66"),sQuery(id+"F2.wireOp",EDGE,"E67"),sQuery(id+"F2.wireOp",EDGE,"E68"),sQuery(id+"F2.wireOp",EDGE,"E69"),sQuery(id+"F2.wireOp",EDGE,"E70"),sQuery(id+"F2.wireOp",EDGE,"E71"),sQuery(id+"F2.wireOp",EDGE,"E72"),sQuery(id+"F2.wireOp",EDGE,"E73"),sQuery(id+"F2.wireOp",EDGE,"E74"),sQuery(id+"F2.wireOp",EDGE,"E75"),sQuery(id+"F2.wireOp",EDGE,"E76"),sQuery(id+"F2.wireOp",EDGE,"E77"),sQuery(id+"F2.wireOp",EDGE,"E78"),sQuery(id+"F2.wireOp",EDGE,"E79"),sQuery(id+"F2.wireOp",EDGE,"E80"),sQuery(id+"F2.wireOp",EDGE,"E81"),sQuery(id+"F2.wireOp",EDGE,"E82"),sQuery(id+"F2.wireOp",EDGE,"E83"),sQuery(id+"F2.wireOp",EDGE,"E84"),sQuery(id+"F2.wireOp",EDGE,"E85"),sQuery(id+"F2.wireOp",EDGE,"E86"),sQuery(id+"F2.wireOp",EDGE,"E87"),sQuery(id+"F2.wireOp",EDGE,"E88"),sQuery(id+"F2.wireOp",EDGE,"E89"),sQuery(id+"F2.wireOp",EDGE,"E90"),sQuery(id+"F2.wireOp",EDGE,"E91"),sQuery(id+"F2.wireOp",EDGE,"E92"),sQuery(id+"F2.wireOp",EDGE,"E93"),sQuery(id+"F2.wireOp",EDGE,"E94"),sQuery(id+"F2.wireOp",EDGE,"E95"),sQuery(id+"F2.wireOp",EDGE,"E96"),sQuery(id+"F2.wireOp",EDGE,"E97"),sQuery(id+"F2.wireOp",EDGE,"E98"),sQuery(id+"F2.wireOp",EDGE,"E99"),sQuery(id+"F2.wireOp",EDGE,"E100"),sQuery(id+"F2.wireOp",EDGE,"E101"),sQuery(id+"F2.wireOp",EDGE,"E102"),sQuery(id+"F2.wireOp",EDGE,"E103"),sQuery(id+"F2.wireOp",EDGE,"E104"),sQuery(id+"F2.wireOp",EDGE,"E105"),sQuery(id+"F2.wireOp",EDGE,"E106"),sQuery(id+"F2.wireOp",EDGE,"E107"),sQuery(id+"F2.wireOp",EDGE,"E108"),sQuery(id+"F2.wireOp",EDGE,"E109"),sQuery(id+"F2.wireOp",EDGE,"E110"),sQuery(id+"F2.wireOp",EDGE,"E111"),sQuery(id+"F2.wireOp",EDGE,"E112"),sQuery(id+"F2.wireOp",EDGE,"E113"),sQuery(id+"F2.wireOp",EDGE,"E114"),sQuery(id+"F2.wireOp",EDGE,"E115"),sQuery(id+"F2.wireOp",EDGE,"E116"),sQuery(id+"F2.wireOp",EDGE,"E117"),sQuery(id+"F2.wireOp",EDGE,"E118"),sQuery(id+"F2.wireOp",EDGE,"E119"),sQuery(id+"F2.wireOp",EDGE,"E120"),sQuery(id+"F2.wireOp",EDGE,"E121"),sQuery(id+"F2.wireOp",EDGE,"E122"),sQuery(id+"F2.wireOp",EDGE,"E123"),sQuery(id+"F2.wireOp",EDGE,"E124"),sQuery(id+"F2.wireOp",EDGE,"E125"),sQuery(id+"F2.wireOp",EDGE,"E126"),sQuery(id+"F2.wireOp",EDGE,"E127"),sQuery(id+"F2.wireOp",EDGE,"E128"),sQuery(id+"F2.wireOp",EDGE,"E129"),sQuery(id+"F2.wireOp",EDGE,"E130"),sQuery(id+"F2.wireOp",EDGE,"E131"),sQuery(id+"F2.wireOp",EDGE,"E132"),sQuery(id+"F2.wireOp",EDGE,"E133"),sQuery(id+"F2.wireOp",EDGE,"E134"),sQuery(id+"F2.wireOp",EDGE,"E135"),sQuery(id+"F2.wireOp",EDGE,"E136"),sQuery(id+"F2.wireOp",EDGE,"E137"),sQuery(id+"F2.wireOp",EDGE,"E138"),sQuery(id+"F2.wireOp",EDGE,"E139"),sQuery(id+"F2.wireOp",EDGE,"E140"),sQuery(id+"F2.wireOp",EDGE,"E141"),sQuery(id+"F2.wireOp",EDGE,"E142"),sQuery(id+"F2.wireOp",EDGE,"E143"),sQuery(id+"F2.wireOp",EDGE,"E144"),sQuery(id+"F2.wireOp",EDGE,"E145"),sQuery(id+"F2.wireOp",EDGE,"E146"),sQuery(id+"F2.wireOp",EDGE,"E147"),sQuery(id+"F2.wireOp",EDGE,"E148"),sQuery(id+"F2.wireOp",EDGE,"E149"),sQuery(id+"F2.wireOp",EDGE,"E150"),sQuery(id+"F2.wireOp",EDGE,"E151"),sQuery(id+"F2.wireOp",EDGE,"E152"),sQuery(id+"F2.wireOp",EDGE,"E153"),sQuery(id+"F2.wireOp",EDGE,"E154"),sQuery(id+"F2.wireOp",EDGE,"E155"),sQuery(id+"F2.wireOp",EDGE,"E156"),sQuery(id+"F2.wireOp",EDGE,"E157"),sQuery(id+"F2.wireOp",EDGE,"E158"),sQuery(id+"F2.wireOp",EDGE,"E159"),sQuery(id+"F2.wireOp",EDGE,"E160"),sQuery(id+"F2.wireOp",EDGE,"E161"),sQuery(id+"F2.wireOp",EDGE,"E162"),sQuery(id+"F2.wireOp",EDGE,"E163"),sQuery(id+"F2.wireOp",EDGE,"E164"),sQuery(id+"F2.wireOp",EDGE,"E165"),sQuery(id+"F2.wireOp",EDGE,"E166"),sQuery(id+"F2.wireOp",EDGE,"E167"),sQuery(id+"F2.wireOp",EDGE,"E168"),sQuery(id+"F2.wireOp",EDGE,"E169"),sQuery(id+"F2.wireOp",EDGE,"E170"),sQuery(id+"F2.wireOp",EDGE,"E171"),sQuery(id+"F2.wireOp",EDGE,"E172"),sQuery(id+"F2.wireOp",EDGE,"E173"),sQuery(id+"F2.wireOp",EDGE,"E174"),sQuery(id+"F2.wireOp",EDGE,"E175"),sQuery(id+"F2.wireOp",EDGE,"E176"),sQuery(id+"F2.wireOp",EDGE,"E177"),sQuery(id+"F2.wireOp",EDGE,"E178"),sQuery(id+"F2.wireOp",EDGE,"E179"),sQuery(id+"F2.wireOp",EDGE,"E180"),sQuery(id+"F2.wireOp",EDGE,"E181"),sQuery(id+"F2.wireOp",EDGE,"E182"),sQuery(id+"F2.wireOp",EDGE,"E183"),sQuery(id+"F2.wireOp",EDGE,"E184"),sQuery(id+"F2.wireOp",EDGE,"E185"),sQuery(id+"F2.wireOp",EDGE,"E186"),sQuery(id+"F2.wireOp",EDGE,"E187"),sQuery(id+"F2.wireOp",EDGE,"E188"),sQuery(id+"F2.wireOp",EDGE,"E189"),sQuery(id+"F2.wireOp",EDGE,"E190"),sQuery(id+"F2.wireOp",EDGE,"E191"),sQuery(id+"F2.wireOp",EDGE,"E192"),sQuery(id+"F2.wireOp",EDGE,"E193"),sQuery(id+"F2.wireOp",EDGE,"E194"),sQuery(id+"F2.wireOp",EDGE,"E195"),sQuery(id+"F2.wireOp",EDGE,"E196"),sQuery(id+"F2.wireOp",EDGE,"E197"),sQuery(id+"F2.wireOp",EDGE,"E198"),sQuery(id+"F2.wireOp",EDGE,"E199"),sQuery(id+"F2.wireOp",EDGE,"E200"),sQuery(id+"F2.wireOp",EDGE,"E201"),sQuery(id+"F2.wireOp",EDGE,"E202"),sQuery(id+"F2.wireOp",EDGE,"E203"),sQuery(id+"F2.wireOp",EDGE,"E204"),sQuery(id+"F2.wireOp",EDGE,"E205"),sQuery(id+"F2.wireOp",EDGE,"E206"),sQuery(id+"F2.wireOp",EDGE,"E207"),sQuery(id+"F2.wireOp",EDGE,"E208"),sQuery(id+"F2.wireOp",EDGE,"E209"),sQuery(id+"F2.wireOp",EDGE,"E210"),sQuery(id+"F2.wireOp",EDGE,"E211"),sQuery(id+"F2.wireOp",EDGE,"E212"),sQuery(id+"F2.wireOp",EDGE,"E213"),sQuery(id+"F2.wireOp",EDGE,"E214"),sQuery(id+"F2.wireOp",EDGE,"E215"),sQuery(id+"F2.wireOp",EDGE,"E216"),sQuery(id+"F2.wireOp",EDGE,"E217"),sQuery(id+"F2.wireOp",EDGE,"E218"),sQuery(id+"F2.wireOp",EDGE,"E219"),sQuery(id+"F2.wireOp",EDGE,"E220"),sQuery(id+"F2.wireOp",EDGE,"E221"),sQuery(id+"F2.wireOp",EDGE,"E222"),sQuery(id+"F2.wireOp",EDGE,"E223"),sQuery(id+"F2.wireOp",EDGE,"E224"),sQuery(id+"F2.wireOp",EDGE,"E225"),sQuery(id+"F2.wireOp",EDGE,"E226"),sQuery(id+"F2.wireOp",EDGE,"E227"),sQuery(id+"F2.wireOp",EDGE,"E228"),sQuery(id+"F2.wireOp",EDGE,"E229"),sQuery(id+"F2.wireOp",EDGE,"E230"),sQuery(id+"F2.wireOp",EDGE,"E231"),sQuery(id+"F2.wireOp",EDGE,"E232"),sQuery(id+"F2.wireOp",EDGE,"E233"),sQuery(id+"F2.wireOp",EDGE,"E234"),sQuery(id+"F2.wireOp",EDGE,"E235"),sQuery(id+"F2.wireOp",EDGE,"E236"),sQuery(id+"F2.wireOp",EDGE,"E237"),sQuery(id+"F2.wireOp",EDGE,"E238"),sQuery(id+"F2.wireOp",EDGE,"E239"),sQuery(id+"F2.wireOp",EDGE,"E240"),sQuery(id+"F2.wireOp",EDGE,"E241"),sQuery(id+"F2.wireOp",EDGE,"E242"),sQuery(id+"F2.wireOp",EDGE,"E243"),sQuery(id+"F2.wireOp",EDGE,"E244"),sQuery(id+"F2.wireOp",EDGE,"E245"),sQuery(id+"F2.wireOp",EDGE,"E246"),sQuery(id+"F2.wireOp",EDGE,"E247"),sQuery(id+"F2.wireOp",EDGE,"E248"),sQuery(id+"F2.wireOp",EDGE,"E249"),sQuery(id+"F2.wireOp",EDGE,"E250"),sQuery(id+"F2.wireOp",EDGE,"E251"),sQuery(id+"F2.wireOp",EDGE,"E252"),sQuery(id+"F2.wireOp",EDGE,"E253"),sQuery(id+"F2.wireOp",EDGE,"E254"),sQuery(id+"F2.wireOp",EDGE,"E255"),sQuery(id+"F2.wireOp",EDGE,"E256"),sQuery(id+"F2.wireOp",EDGE,"E257"),sQuery(id+"F2.wireOp",EDGE,"E258"),sQuery(id+"F2.wireOp",EDGE,"E259"),sQuery(id+"F2.wireOp",EDGE,"E260"),sQuery(id+"F2.wireOp",EDGE,"E261"),sQuery(id+"F2.wireOp",EDGE,"E262"),sQuery(id+"F2.wireOp",EDGE,"E263"),sQuery(id+"F2.wireOp",EDGE,"E264"),sQuery(id+"F2.wireOp",EDGE,"E265"),sQuery(id+"F2.wireOp",EDGE,"E266"),sQuery(id+"F2.wireOp",EDGE,"E267"),sQuery(id+"F2.wireOp",EDGE,"E268"),sQuery(id+"F2.wireOp",EDGE,"E269"),sQuery(id+"F2.wireOp",EDGE,"E270"),sQuery(id+"F2.wireOp",EDGE,"E271"),sQuery(id+"F2.wireOp",EDGE,"E272"),sQuery(id+"F2.wireOp",EDGE,"E273"),sQuery(id+"F2.wireOp",EDGE,"E274"),sQuery(id+"F2.wireOp",EDGE,"E275"),sQuery(id+"F2.wireOp",EDGE,"E276"),sQuery(id+"F2.wireOp",EDGE,"E277"),sQuery(id+"F2.wireOp",EDGE,"E278"),sQuery(id+"F2.wireOp",EDGE,"E279"),sQuery(id+"F2.wireOp",EDGE,"E280"),sQuery(id+"F2.wireOp",EDGE,"E281"),sQuery(id+"F2.wireOp",EDGE,"E282"),sQuery(id+"F2.wireOp",EDGE,"E283"),sQuery(id+"F2.wireOp",EDGE,"E284"),sQuery(id+"F2.wireOp",EDGE,"E285"),sQuery(id+"F2.wireOp",EDGE,"E286"),sQuery(id+"F2.wireOp",EDGE,"E287"),sQuery(id+"F2.wireOp",EDGE,"E288"),sQuery(id+"F2.wireOp",EDGE,"E289"),sQuery(id+"F2.wireOp",EDGE,"E290"),sQuery(id+"F2.wireOp",EDGE,"E291"),sQuery(id+"F2.wireOp",EDGE,"E292"),sQuery(id+"F2.wireOp",EDGE,"E293"),sQuery(id+"F2.wireOp",EDGE,"E294"),sQuery(id+"F2.wireOp",EDGE,"E295"),sQuery(id+"F2.wireOp",EDGE,"E296"),sQuery(id+"F2.wireOp",EDGE,"E297"),sQuery(id+"F2.wireOp",EDGE,"E298"),sQuery(id+"F2.wireOp",EDGE,"E299"),sQuery(id+"F2.wireOp",EDGE,"E300"),sQuery(id+"F2.wireOp",EDGE,"E301"),sQuery(id+"F2.wireOp",EDGE,"E302"),sQuery(id+"F2.wireOp",EDGE,"E303"),sQuery(id+"F2.wireOp",EDGE,"E304"),sQuery(id+"F2.wireOp",EDGE,"E305"),sQuery(id+"F2.wireOp",EDGE,"E306"),sQuery(id+"F2.wireOp",EDGE,"E307"),sQuery(id+"F2.wireOp",EDGE,"E308"),sQuery(id+"F2.wireOp",EDGE,"E309"),sQuery(id+"F2.wireOp",EDGE,"E310"),sQuery(id+"F2.wireOp",EDGE,"E311"),sQuery(id+"F2.wireOp",EDGE,"E312"),sQuery(id+"F2.wireOp",EDGE,"E313"),sQuery(id+"F2.wireOp",EDGE,"E314"),sQuery(id+"F2.wireOp",EDGE,"E315"),sQuery(id+"F2.wireOp",EDGE,"E316"),sQuery(id+"F2.wireOp",EDGE,"E317"),sQuery(id+"F2.wireOp",EDGE,"E318"),sQuery(id+"F2.wireOp",EDGE,"E319"),sQuery(id+"F2.wireOp",EDGE,"E320"),sQuery(id+"F2.wireOp",EDGE,"E321"),sQuery(id+"F2.wireOp",EDGE,"E322"),sQuery(id+"F2.wireOp",EDGE,"E323"),sQuery(id+"F2.wireOp",EDGE,"E324"),sQuery(id+"F2.wireOp",EDGE,"E325"),sQuery(id+"F2.wireOp",EDGE,"E326"),sQuery(id+"F2.wireOp",EDGE,"E327"),sQuery(id+"F2.wireOp",EDGE,"E328"),sQuery(id+"F2.wireOp",EDGE,"E329"),sQuery(id+"F2.wireOp",EDGE,"E330"),sQuery(id+"F2.wireOp",EDGE,"E331"),sQuery(id+"F2.wireOp",EDGE,"E332"),sQuery(id+"F2.wireOp",EDGE,"E333"),sQuery(id+"F2.wireOp",EDGE,"E334"),sQuery(id+"F2.wireOp",EDGE,"E335"),sQuery(id+"F2.wireOp",EDGE,"E336"),sQuery(id+"F2.wireOp",EDGE,"E337"),sQuery(id+"F2.wireOp",EDGE,"E338"),sQuery(id+"F2.wireOp",EDGE,"E339"),sQuery(id+"F2.wireOp",EDGE,"E340"),sQuery(id+"F2.wireOp",EDGE,"E341"),sQuery(id+"F2.wireOp",EDGE,"E342"),sQuery(id+"F2.wireOp",EDGE,"E343"),sQuery(id+"F2.wireOp",EDGE,"E344"),sQuery(id+"F2.wireOp",EDGE,"E345"),sQuery(id+"F2.wireOp",EDGE,"E346"),sQuery(id+"F2.wireOp",EDGE,"E347"),sQuery(id+"F2.wireOp",EDGE,"E348"),sQuery(id+"F2.wireOp",EDGE,"E349"),sQuery(id+"F2.wireOp",EDGE,"E350"),sQuery(id+"F2.wireOp",EDGE,"E351"),sQuery(id+"F2.wireOp",EDGE,"E352"),sQuery(id+"F2.wireOp",EDGE,"E353"),sQuery(id+"F2.wireOp",EDGE,"E354"),sQuery(id+"F2.wireOp",EDGE,"E355"),sQuery(id+"F2.wireOp",EDGE,"E356"),sQuery(id+"F2.wireOp",EDGE,"E357"),sQuery(id+"F2.wireOp",EDGE,"E358"),sQuery(id+"F2.wireOp",EDGE,"E359"),sQuery(id+"F2.wireOp",EDGE,"E360"),sQuery(id+"F2.wireOp",EDGE,"E361"),sQuery(id+"F2.wireOp",EDGE,"E362"),sQuery(id+"F2.wireOp",EDGE,"E363"),sQuery(id+"F2.wireOp",EDGE,"E364"),sQuery(id+"F2.wireOp",EDGE,"E365"),sQuery(id+"F2.wireOp",EDGE,"E366"),sQuery(id+"F2.wireOp",EDGE,"E367"),sQuery(id+"F2.wireOp",EDGE,"E368"),sQuery(id+"F2.wireOp",EDGE,"E369"),sQuery(id+"F2.wireOp",EDGE,"E370"),sQuery(id+"F2.wireOp",EDGE,"E371"),sQuery(id+"F2.wireOp",EDGE,"E372"),sQuery(id+"F2.wireOp",EDGE,"E373"),sQuery(id+"F2.wireOp",EDGE,"E374"),sQuery(id+"F2.wireOp",EDGE,"E375"),sQuery(id+"F2.wireOp",EDGE,"E376"),sQuery(id+"F2.wireOp",EDGE,"E377"),sQuery(id+"F2.wireOp",EDGE,"E378"),sQuery(id+"F2.wireOp",EDGE,"E379"),sQuery(id+"F2.wireOp",EDGE,"E380"),sQuery(id+"F2.wireOp",EDGE,"E381"),sQuery(id+"F2.wireOp",EDGE,"E382"),sQuery(id+"F2.wireOp",EDGE,"E383"),sQuery(id+"F2.wireOp",EDGE,"E384"),sQuery(id+"F2.wireOp",EDGE,"E385"),sQuery(id+"F2.wireOp",EDGE,"E386"),sQuery(id+"F2.wireOp",EDGE,"E387"),sQuery(id+"F2.wireOp",EDGE,"E388"),sQuery(id+"F2.wireOp",EDGE,"E389"),sQuery(id+"F2.wireOp",EDGE,"E390"),sQuery(id+"F2.wireOp",EDGE,"E391"),sQuery(id+"F2.wireOp",EDGE,"E392"),sQuery(id+"F2.wireOp",EDGE,"E393"),sQuery(id+"F2.wireOp",EDGE,"E394"),sQuery(id+"F2.wireOp",EDGE,"E395"),sQuery(id+"F2.wireOp",EDGE,"E396"),sQuery(id+"F2.wireOp",EDGE,"E397"),sQuery(id+"F2.wireOp",EDGE,"E398"),sQuery(id+"F2.wireOp",EDGE,"E399"),sQuery(id+"F2.wireOp",EDGE,"E400"),sQuery(id+"F2.wireOp",EDGE,"E401"),sQuery(id+"F2.wireOp",EDGE,"E402"),sQuery(id+"F2.wireOp",EDGE,"E403"),sQuery(id+"F2.wireOp",EDGE,"E404"),sQuery(id+"F2.wireOp",EDGE,"E405"),sQuery(id+"F2.wireOp",EDGE,"E406"),sQuery(id+"F2.wireOp",EDGE,"E407"),sQuery(id+"F2.wireOp",EDGE,"E408"),sQuery(id+"F2.wireOp",EDGE,"E409"),sQuery(id+"F2.wireOp",EDGE,"E410"),sQuery(id+"F2.wireOp",EDGE,"E411"),sQuery(id+"F2.wireOp",EDGE,"E412"),sQuery(id+"F2.wireOp",EDGE,"E413"),sQuery(id+"F2.wireOp",EDGE,"E414"),sQuery(id+"F2.wireOp",EDGE,"E415"),sQuery(id+"F2.wireOp",EDGE,"E416"),sQuery(id+"F2.wireOp",EDGE,"E417"),sQuery(id+"F2.wireOp",EDGE,"E418"),sQuery(id+"F2.wireOp",EDGE,"E419"),sQuery(id+"F2.wireOp",EDGE,"E420"),sQuery(id+"F2.wireOp",EDGE,"E421"),sQuery(id+"F2.wireOp",EDGE,"E422"),sQuery(id+"F2.wireOp",EDGE,"E423"),sQuery(id+"F2.wireOp",EDGE,"E424"),sQuery(id+"F2.wireOp",EDGE,"E425"),sQuery(id+"F2.wireOp",EDGE,"E426"),sQuery(id+"F2.wireOp",EDGE,"E427"),sQuery(id+"F2.wireOp",EDGE,"E428"),sQuery(id+"F2.wireOp",EDGE,"E429"),sQuery(id+"F2.wireOp",EDGE,"E430"),sQuery(id+"F2.wireOp",EDGE,"E431"),sQuery(id+"F2.wireOp",EDGE,"E432"),sQuery(id+"F2.wireOp",EDGE,"E433"),sQuery(id+"F2.wireOp",EDGE,"E434"),sQuery(id+"F2.wireOp",EDGE,"E435"),sQuery(id+"F2.wireOp",EDGE,"E436"),sQuery(id+"F2.wireOp",EDGE,"E437"),sQuery(id+"F2.wireOp",EDGE,"E438"),sQuery(id+"F2.wireOp",EDGE,"E439"),sQuery(id+"F2.wireOp",EDGE,"E440"),sQuery(id+"F2.wireOp",EDGE,"E441"),sQuery(id+"F2.wireOp",EDGE,"E442"),sQuery(id+"F2.wireOp",EDGE,"E443"),sQuery(id+"F2.wireOp",EDGE,"E444"),sQuery(id+"F2.wireOp",EDGE,"E445"),sQuery(id+"F2.wireOp",EDGE,"E446"),sQuery(id+"F2.wireOp",EDGE,"E447"),sQuery(id+"F2.wireOp",EDGE,"E447"),sQuery(id+"F2.wireOp",EDGE,"E447"),sQuery(id+"F2.wireOp",EDGE,"E448"),sQuery(id+"F2.wireOp",EDGE,"E449"),sQuery(id+"F2.wireOp",EDGE,"E450"),sQuery(id+"F2.wireOp",EDGE,"E451"),sQuery(id+"F2.wireOp",EDGE,"E452"),sQuery(id+"F2.wireOp",EDGE,"E453"),sQuery(id+"F2.wireOp",EDGE,"E454"),sQuery(id+"F2.wireOp",EDGE,"E455"),sQuery(id+"F2.wireOp",EDGE,"E456"),sQuery(id+"F2.wireOp",EDGE,"E457"),sQuery(id+"F2.wireOp",EDGE,"E458"),sQuery(id+"F2.wireOp",EDGE,"E459"),sQuery(id+"F2.wireOp",EDGE,"E460"),sQuery(id+"F2.wireOp",EDGE,"E461"),sQuery(id+"F2.wireOp",EDGE,"E462"),sQuery(id+"F2.wireOp",EDGE,"E463"),sQuery(id+"F2.wireOp",EDGE,"E464"),sQuery(id+"F2.wireOp",EDGE,"E465"),sQuery(id+"F2.wireOp",EDGE,"E466"),sQuery(id+"F2.wireOp",EDGE,"E467"),sQuery(id+"F2.wireOp",EDGE,"E468"),sQuery(id+"F2.wireOp",EDGE,"E469"),sQuery(id+"F2.wireOp",EDGE,"E470"),sQuery(id+"F2.wireOp",EDGE,"E471"),sQuery(id+"F2.wireOp",EDGE,"E472"),sQuery(id+"F2.wireOp",EDGE,"E473"),sQuery(id+"F2.wireOp",EDGE,"E474"),sQuery(id+"F2.wireOp",EDGE,"E475"),sQuery(id+"F2.wireOp",EDGE,"E476"),sQuery(id+"F2.wireOp",EDGE,"E477"),sQuery(id+"F2.wireOp",EDGE,"E478"),sQuery(id+"F2.wireOp",EDGE,"E479"),sQuery(id+"F2.wireOp",EDGE,"E480"),sQuery(id+"F2.wireOp",EDGE,"E481"),sQuery(id+"F2.wireOp",EDGE,"E482"),sQuery(id+"F2.wireOp",EDGE,"E483"),sQuery(id+"F2.wireOp",EDGE,"E484"),sQuery(id+"F2.wireOp",EDGE,"E485"),sQuery(id+"F2.wireOp",EDGE,"E486"),sQuery(id+"F2.wireOp",EDGE,"E487"),sQuery(id+"F2.wireOp",EDGE,"E488"),sQuery(id+"F2.wireOp",EDGE,"E489"),sQuery(id+"F2.wireOp",EDGE,"E490"),sQuery(id+"F2.wireOp",EDGE,"E491"),sQuery(id+"F2.wireOp",EDGE,"E492"),sQuery(id+"F2.wireOp",EDGE,"E493"),sQuery(id+"F2.wireOp",EDGE,"E494"),sQuery(id+"F2.wireOp",EDGE,"E495"),sQuery(id+"F2.wireOp",EDGE,"E496"),sQuery(id+"F2.wireOp",EDGE,"E497"),sQuery(id+"F2.wireOp",EDGE,"E498"),sQuery(id+"F2.wireOp",EDGE,"E499"),sQuery(id+"F2.wireOp",EDGE,"E500"),sQuery(id+"F2.wireOp",EDGE,"E501"),sQuery(id+"F2.wireOp",EDGE,"E502"),sQuery(id+"F2.wireOp",EDGE,"E503"),sQuery(id+"F2.wireOp",EDGE,"E504"),sQuery(id+"F2.wireOp",EDGE,"E505"),sQuery(id+"F2.wireOp",EDGE,"E506"),sQuery(id+"F2.wireOp",EDGE,"E507"),sQuery(id+"F2.wireOp",EDGE,"E508"),sQuery(id+"F2.wireOp",EDGE,"E509"),sQuery(id+"F2.wireOp",EDGE,"E510"),sQuery(id+"F2.wireOp",EDGE,"E511"),sQuery(id+"F2.wireOp",EDGE,"E512"),sQuery(id+"F2.wireOp",EDGE,"E513"),sQuery(id+"F2.wireOp",EDGE,"E514"),sQuery(id+"F2.wireOp",EDGE,"E515"),sQuery(id+"F2.wireOp",EDGE,"E516"),sQuery(id+"F2.wireOp",EDGE,"E517"),sQuery(id+"F2.wireOp",EDGE,"E518"),sQuery(id+"F2.wireOp",EDGE,"E519"),sQuery(id+"F2.wireOp",EDGE,"E520"),sQuery(id+"F2.wireOp",EDGE,"E521"),sQuery(id+"F2.wireOp",EDGE,"E522"),sQuery(id+"F2.wireOp",EDGE,"E523"),sQuery(id+"F2.wireOp",EDGE,"E524"),sQuery(id+"F2.wireOp",EDGE,"E525"),sQuery(id+"F2.wireOp",EDGE,"E526"),sQuery(id+"F2.wireOp",EDGE,"E527"),sQuery(id+"F2.wireOp",EDGE,"E528"),sQuery(id+"F2.wireOp",EDGE,"E529"),sQuery(id+"F2.wireOp",EDGE,"E530"),sQuery(id+"F2.wireOp",EDGE,"E531"),sQuery(id+"F2.wireOp",EDGE,"E532"),sQuery(id+"F2.wireOp",EDGE,"E533"),sQuery(id+"F2.wireOp",EDGE,"E534"),sQuery(id+"F2.wireOp",EDGE,"E535"),sQuery(id+"F2.wireOp",EDGE,"E536"),sQuery(id+"F2.wireOp",EDGE,"E537"),sQuery(id+"F2.wireOp",EDGE,"E538"),sQuery(id+"F2.wireOp",EDGE,"E539"),sQuery(id+"F2.wireOp",EDGE,"E540"),sQuery(id+"F2.wireOp",EDGE,"E541"),sQuery(id+"F2.wireOp",EDGE,"E542"),sQuery(id+"F2.wireOp",EDGE,"E543"),sQuery(id+"F2.wireOp",EDGE,"E544"),sQuery(id+"F2.wireOp",EDGE,"E545"),sQuery(id+"F2.wireOp",EDGE,"E546"),sQuery(id+"F2.wireOp",EDGE,"E547"),sQuery(id+"F2.wireOp",EDGE,"E547"),sQuery(id+"F2.wireOp",EDGE,"E548"),sQuery(id+"F2.wireOp",EDGE,"E549"),sQuery(id+"F2.wireOp",EDGE,"E550"),sQuery(id+"F2.wireOp",EDGE,"E551"),sQuery(id+"F2.wireOp",EDGE,"E552"),sQuery(id+"F2.wireOp",EDGE,"E553"),sQuery(id+"F2.wireOp",EDGE,"E554"),sQuery(id+"F2.wireOp",EDGE,"E555"),sQuery(id+"F2.wireOp",EDGE,"E556"),sQuery(id+"F2.wireOp",EDGE,"E557"),sQuery(id+"F2.wireOp",EDGE,"E558"),sQuery(id+"F2.wireOp",EDGE,"E559"),sQuery(id+"F2.wireOp",EDGE,"E560"),sQuery(id+"F2.wireOp",EDGE,"E561"),sQuery(id+"F2.wireOp",EDGE,"E562"),sQuery(id+"F2.wireOp",EDGE,"E563"),sQuery(id+"F2.wireOp",EDGE,"E564"),sQuery(id+"F2.wireOp",EDGE,"E565"),sQuery(id+"F2.wireOp",EDGE,"E566"),sQuery(id+"F2.wireOp",EDGE,"E567"),sQuery(id+"F2.wireOp",EDGE,"E568"),sQuery(id+"F2.wireOp",EDGE,"E569"),sQuery(id+"F2.wireOp",EDGE,"E570"),sQuery(id+"F2.wireOp",EDGE,"E571"),sQuery(id+"F2.wireOp",EDGE,"E572"),sQuery(id+"F2.wireOp",EDGE,"E573"),sQuery(id+"F2.wireOp",EDGE,"E574"),sQuery(id+"F2.wireOp",EDGE,"E575"),sQuery(id+"F2.wireOp",EDGE,"E576"),sQuery(id+"F2.wireOp",EDGE,"E577"),sQuery(id+"F2.wireOp",EDGE,"E578"),sQuery(id+"F2.wireOp",EDGE,"E579"),sQuery(id+"F2.wireOp",EDGE,"E580"),sQuery(id+"F2.wireOp",EDGE,"E581"),sQuery(id+"F2.wireOp",EDGE,"E582"),sQuery(id+"F2.wireOp",EDGE,"E583"),sQuery(id+"F2.wireOp",EDGE,"E584"),sQuery(id+"F2.wireOp",EDGE,"E585"),sQuery(id+"F2.wireOp",EDGE,"E586"),sQuery(id+"F2.wireOp",EDGE,"E587"),sQuery(id+"F2.wireOp",EDGE,"E588"),sQuery(id+"F2.wireOp",EDGE,"E589"),sQuery(id+"F2.wireOp",EDGE,"E590"),sQuery(id+"F2.wireOp",EDGE,"E591"),sQuery(id+"F2.wireOp",EDGE,"E592"),sQuery(id+"F2.wireOp",EDGE,"E593"),sQuery(id+"F2.wireOp",EDGE,"E594"),sQuery(id+"F2.wireOp",EDGE,"E595"),sQuery(id+"F2.wireOp",EDGE,"E596"),sQuery(id+"F2.wireOp",EDGE,"E597"),sQuery(id+"F2.wireOp",EDGE,"E598"),sQuery(id+"F2.wireOp",EDGE,"E599"),sQuery(id+"F2.wireOp",EDGE,"E600"),sQuery(id+"F2.wireOp",EDGE,"E601"),sQuery(id+"F2.wireOp",EDGE,"E602"),sQuery(id+"F2.wireOp",EDGE,"E603"),sQuery(id+"F2.wireOp",EDGE,"E604"),sQuery(id+"F2.wireOp",EDGE,"E605"),sQuery(id+"F2.wireOp",EDGE,"E606"),sQuery(id+"F2.wireOp",EDGE,"E607"),sQuery(id+"F2.wireOp",EDGE,"E608"),sQuery(id+"F2.wireOp",EDGE,"E609"),sQuery(id+"F2.wireOp",EDGE,"E610"),sQuery(id+"F2.wireOp",EDGE,"E611"),sQuery(id+"F2.wireOp",EDGE,"E612"),sQuery(id+"F2.wireOp",EDGE,"E613"),sQuery(id+"F2.wireOp",EDGE,"E614"),sQuery(id+"F2.wireOp",EDGE,"E615"),sQuery(id+"F2.wireOp",EDGE,"E616"),sQuery(id+"F2.wireOp",EDGE,"E617"),sQuery(id+"F2.wireOp",EDGE,"E618"),sQuery(id+"F2.wireOp",EDGE,"E619"),sQuery(id+"F2.wireOp",EDGE,"E620"),sQuery(id+"F2.wireOp",EDGE,"E621"),sQuery(id+"F2.wireOp",EDGE,"E622"),sQuery(id+"F2.wireOp",EDGE,"E623"),sQuery(id+"F2.wireOp",EDGE,"E624"),sQuery(id+"F2.wireOp",EDGE,"E625"),sQuery(id+"F2.wireOp",EDGE,"E626"),sQuery(id+"F2.wireOp",EDGE,"E627"),sQuery(id+"F2.wireOp",EDGE,"E628"),sQuery(id+"F2.wireOp",EDGE,"E629"),sQuery(id+"F2.wireOp",EDGE,"E630"),sQuery(id+"F2.wireOp",EDGE,"E631"),sQuery(id+"F2.wireOp",EDGE,"E632"),sQuery(id+"F2.wireOp",EDGE,"E633"),sQuery(id+"F2.wireOp",EDGE,"E634"),sQuery(id+"F2.wireOp",EDGE,"E635"),sQuery(id+"F2.wireOp",EDGE,"E636"),sQuery(id+"F2.wireOp",EDGE,"E637"),sQuery(id+"F2.wireOp",EDGE,"E638"),sQuery(id+"F2.wireOp",EDGE,"E639"),sQuery(id+"F2.wireOp",EDGE,"E640"),sQuery(id+"F2.wireOp",EDGE,"E641"),sQuery(id+"F2.wireOp",EDGE,"E642"),sQuery(id+"F2.wireOp",EDGE,"E643"),sQuery(id+"F2.wireOp",EDGE,"E644"),sQuery(id+"F2.wireOp",EDGE,"E645"),sQuery(id+"F2.wireOp",EDGE,"E646"),sQuery(id+"F2.wireOp",EDGE,"E647"),sQuery(id+"F2.wireOp",EDGE,"E648"),sQuery(id+"F2.wireOp",EDGE,"E649"),sQuery(id+"F2.wireOp",EDGE,"E650"),sQuery(id+"F2.wireOp",EDGE,"E651"),sQuery(id+"F2.wireOp",EDGE,"E652"),sQuery(id+"F2.wireOp",EDGE,"E653"),sQuery(id+"F2.wireOp",EDGE,"E654"),sQuery(id+"F2.wireOp",EDGE,"E655"),sQuery(id+"F2.wireOp",EDGE,"E656"),sQuery(id+"F2.wireOp",EDGE,"E657"),sQuery(id+"F2.wireOp",EDGE,"E658"),sQuery(id+"F2.wireOp",EDGE,"E659"),sQuery(id+"F2.wireOp",EDGE,"E660"),sQuery(id+"F2.wireOp",EDGE,"E661"),sQuery(id+"F2.wireOp",EDGE,"E662"),sQuery(id+"F2.wireOp",EDGE,"E663"),sQuery(id+"F2.wireOp",EDGE,"E664"),sQuery(id+"F2.wireOp",EDGE,"E665"),sQuery(id+"F2.wireOp",EDGE,"E666"),sQuery(id+"F2.wireOp",EDGE,"E667"),sQuery(id+"F2.wireOp",EDGE,"E668"),sQuery(id+"F2.wireOp",EDGE,"E669"),sQuery(id+"F2.wireOp",EDGE,"E670"),sQuery(id+"F2.wireOp",EDGE,"E671"),sQuery(id+"F2.wireOp",EDGE,"E672"),sQuery(id+"F2.wireOp",EDGE,"E673"),sQuery(id+"F2.wireOp",EDGE,"E674"),sQuery(id+"F2.wireOp",EDGE,"E675"),sQuery(id+"F2.wireOp",EDGE,"E676"),sQuery(id+"F2.wireOp",EDGE,"E677"),sQuery(id+"F2.wireOp",EDGE,"E678"),sQuery(id+"F2.wireOp",EDGE,"E679"),sQuery(id+"F2.wireOp",EDGE,"E680"),sQuery(id+"F2.wireOp",EDGE,"E681"),sQuery(id+"F2.wireOp",EDGE,"E682"),sQuery(id+"F2.wireOp",EDGE,"E683"),sQuery(id+"F2.wireOp",EDGE,"E684"),sQuery(id+"F2.wireOp",EDGE,"E685"),sQuery(id+"F2.wireOp",EDGE,"E686"),sQuery(id+"F2.wireOp",EDGE,"E687"),sQuery(id+"F2.wireOp",EDGE,"E688"),sQuery(id+"F2.wireOp",EDGE,"E689"),sQuery(id+"F2.wireOp",EDGE,"E690"),sQuery(id+"F2.wireOp",EDGE,"E691"),sQuery(id+"F2.wireOp",EDGE,"E692"),sQuery(id+"F2.wireOp",EDGE,"E693"),sQuery(id+"F2.wireOp",EDGE,"E694"),sQuery(id+"F2.wireOp",EDGE,"E695"),sQuery(id+"F2.wireOp",EDGE,"E696"),sQuery(id+"F2.wireOp",EDGE,"E697"),sQuery(id+"F2.wireOp",EDGE,"E698"),sQuery(id+"F2.wireOp",EDGE,"E699"),sQuery(id+"F2.wireOp",EDGE,"E700"),sQuery(id+"F2.wireOp",EDGE,"E701"),sQuery(id+"F2.wireOp",EDGE,"E702"),sQuery(id+"F2.wireOp",EDGE,"E703"),sQuery(id+"F2.wireOp",EDGE,"E704"),sQuery(id+"F2.wireOp",EDGE,"E705"),sQuery(id+"F2.wireOp",EDGE,"E706"),sQuery(id+"F2.wireOp",EDGE,"E707"),sQuery(id+"F2.wireOp",EDGE,"E708"),sQuery(id+"F2.wireOp",EDGE,"E709"),sQuery(id+"F2.wireOp",EDGE,"E710"),sQuery(id+"F2.wireOp",EDGE,"E711"),sQuery(id+"F2.wireOp",EDGE,"E712"),sQuery(id+"F2.wireOp",EDGE,"E713"),sQuery(id+"F2.wireOp",EDGE,"E714"),sQuery(id+"F2.wireOp",EDGE,"E715"),sQuery(id+"F2.wireOp",EDGE,"E716"),sQuery(id+"F2.wireOp",EDGE,"E717"),sQuery(id+"F2.wireOp",EDGE,"E718"),sQuery(id+"F2.wireOp",EDGE,"E719"),sQuery(id+"F2.wireOp",EDGE,"E720"),sQuery(id+"F2.wireOp",EDGE,"E721"),sQuery(id+"F2.wireOp",EDGE,"E722"),sQuery(id+"F2.wireOp",EDGE,"E723"),sQuery(id+"F2.wireOp",EDGE,"E724"),sQuery(id+"F2.wireOp",EDGE,"E725"),sQuery(id+"F2.wireOp",EDGE,"E726"),sQuery(id+"F2.wireOp",EDGE,"E727"),sQuery(id+"F2.wireOp",EDGE,"E728"),sQuery(id+"F2.wireOp",EDGE,"E729"),sQuery(id+"F2.wireOp",EDGE,"E730"),sQuery(id+"F2.wireOp",EDGE,"E731"),sQuery(id+"F2.wireOp",EDGE,"E732"),sQuery(id+"F2.wireOp",EDGE,"E733"),sQuery(id+"F2.wireOp",EDGE,"E734"),sQuery(id+"F2.wireOp",EDGE,"E735"),sQuery(id+"F2.wireOp",EDGE,"E736"),sQuery(id+"F2.wireOp",EDGE,"E737"),sQuery(id+"F2.wireOp",EDGE,"E738"),sQuery(id+"F2.wireOp",EDGE,"E739"),sQuery(id+"F2.wireOp",EDGE,"E740"),sQuery(id+"F2.wireOp",EDGE,"E741"),sQuery(id+"F2.wireOp",EDGE,"E742"),sQuery(id+"F2.wireOp",EDGE,"E743"),sQuery(id+"F2.wireOp",EDGE,"E744"),sQuery(id+"F2.wireOp",EDGE,"E745"),sQuery(id+"F2.wireOp",EDGE,"E746"),sQuery(id+"F2.wireOp",EDGE,"E747"),sQuery(id+"F2.wireOp",EDGE,"E748"),sQuery(id+"F2.wireOp",EDGE,"E749"),sQuery(id+"F2.wireOp",EDGE,"E750"),sQuery(id+"F2.wireOp",EDGE,"E751"),sQuery(id+"F2.wireOp",EDGE,"E752"),sQuery(id+"F2.wireOp",EDGE,"E753"),sQuery(id+"F2.wireOp",EDGE,"E754"),sQuery(id+"F2.wireOp",EDGE,"E755"),sQuery(id+"F2.wireOp",EDGE,"E756"),sQuery(id+"F2.wireOp",EDGE,"E757"),sQuery(id+"F2.wireOp",EDGE,"E758"),sQuery(id+"F2.wireOp",EDGE,"E759"),sQuery(id+"F2.wireOp",EDGE,"E760"),sQuery(id+"F2.wireOp",EDGE,"E761"),sQuery(id+"F2.wireOp",EDGE,"E762"),sQuery(id+"F2.wireOp",EDGE,"E763"),sQuery(id+"F2.wireOp",EDGE,"E764"),sQuery(id+"F2.wireOp",EDGE,"E765"),sQuery(id+"F2.wireOp",EDGE,"E766"),sQuery(id+"F2.wireOp",EDGE,"E767"),sQuery(id+"F2.wireOp",EDGE,"E768"),sQuery(id+"F2.wireOp",EDGE,"E769"),sQuery(id+"F2.wireOp",EDGE,"E770"),sQuery(id+"F2.wireOp",EDGE,"E771"),sQuery(id+"F2.wireOp",EDGE,"E772"),sQuery(id+"F2.wireOp",EDGE,"E773"),sQuery(id+"F2.wireOp",EDGE,"E774"),sQuery(id+"F2.wireOp",EDGE,"E775"),sQuery(id+"F2.wireOp",EDGE,"E776"),sQuery(id+"F2.wireOp",EDGE,"E777"),sQuery(id+"F2.wireOp",EDGE,"E778"),sQuery(id+"F2.wireOp",EDGE,"E779"),sQuery(id+"F2.wireOp",EDGE,"E780"),sQuery(id+"F2.wireOp",EDGE,"E781"),sQuery(id+"F2.wireOp",EDGE,"E782"),sQuery(id+"F2.wireOp",EDGE,"E783"),sQuery(id+"F2.wireOp",EDGE,"E784"),sQuery(id+"F2.wireOp",EDGE,"E785"),sQuery(id+"F2.wireOp",EDGE,"E786"),sQuery(id+"F2.wireOp",EDGE,"E787"),sQuery(id+"F2.wireOp",EDGE,"E788"),sQuery(id+"F2.wireOp",EDGE,"E789"),sQuery(id+"F2.wireOp",EDGE,"E790"),sQuery(id+"F2.wireOp",EDGE,"E791"),sQuery(id+"F2.wireOp",EDGE,"E792"),sQuery(id+"F2.wireOp",EDGE,"E793"),sQuery(id+"F2.wireOp",EDGE,"E794"),sQuery(id+"F2.wireOp",EDGE,"E795"),sQuery(id+"F2.wireOp",EDGE,"E796"),sQuery(id+"F2.wireOp",EDGE,"E797"),sQuery(id+"F2.wireOp",EDGE,"E798"),sQuery(id+"F2.wireOp",EDGE,"E799"),sQuery(id+"F2.wireOp",EDGE,"E800"),sQuery(id+"F2.wireOp",EDGE,"E801"),sQuery(id+"F2.wireOp",EDGE,"E802"),sQuery(id+"F2.wireOp",EDGE,"E803"),sQuery(id+"F2.wireOp",EDGE,"E804"),sQuery(id+"F2.wireOp",EDGE,"E805"),sQuery(id+"F2.wireOp",EDGE,"E806"),sQuery(id+"F2.wireOp",EDGE,"E807"),sQuery(id+"F2.wireOp",EDGE,"E808"),sQuery(id+"F2.wireOp",EDGE,"E809"),sQuery(id+"F2.wireOp",EDGE,"E810"),sQuery(id+"F2.wireOp",EDGE,"E811"),sQuery(id+"F2.wireOp",EDGE,"E812"),sQuery(id+"F2.wireOp",EDGE,"E813"),sQuery(id+"F2.wireOp",EDGE,"E814"),sQuery(id+"F2.wireOp",EDGE,"E815"),sQuery(id+"F2.wireOp",EDGE,"E816"),sQuery(id+"F2.wireOp",EDGE,"E817"),sQuery(id+"F2.wireOp",EDGE,"E818"),sQuery(id+"F2.wireOp",EDGE,"E819"),sQuery(id+"F2.wireOp",EDGE,"E820"),sQuery(id+"F2.wireOp",EDGE,"E821"),sQuery(id+"F2.wireOp",EDGE,"E822"),sQuery(id+"F2.wireOp",EDGE,"E823"),sQuery(id+"F2.wireOp",EDGE,"E824"),sQuery(id+"F2.wireOp",EDGE,"E825"),sQuery(id+"F2.wireOp",EDGE,"E826"),sQuery(id+"F2.wireOp",EDGE,"E827"),sQuery(id+"F2.wireOp",EDGE,"E828"),sQuery(id+"F2.wireOp",EDGE,"E829"),sQuery(id+"F2.wireOp",EDGE,"E830"),sQuery(id+"F2.wireOp",EDGE,"E831"),sQuery(id+"F2.wireOp",EDGE,"E832"),sQuery(id+"F2.wireOp",EDGE,"E833"),sQuery(id+"F2.wireOp",EDGE,"E834"),sQuery(id+"F2.wireOp",EDGE,"E835"),sQuery(id+"F2.wireOp",EDGE,"E836"),sQuery(id+"F2.wireOp",EDGE,"E837"),sQuery(id+"F2.wireOp",EDGE,"E838"),sQuery(id+"F2.wireOp",EDGE,"E839"),sQuery(id+"F2.wireOp",EDGE,"E840"),sQuery(id+"F2.wireOp",EDGE,"E841"),sQuery(id+"F2.wireOp",EDGE,"E842"),sQuery(id+"F2.wireOp",EDGE,"E843"),sQuery(id+"F2.wireOp",EDGE,"E844"),sQuery(id+"F2.wireOp",EDGE,"E845"),sQuery(id+"F2.wireOp",EDGE,"E846"),sQuery(id+"F2.wireOp",EDGE,"E847"),sQuery(id+"F2.wireOp",EDGE,"E848"),sQuery(id+"F2.wireOp",EDGE,"E849"),sQuery(id+"F2.wireOp",EDGE,"E850"),sQuery(id+"F2.wireOp",EDGE,"E851"),sQuery(id+"F2.wireOp",EDGE,"E852"),sQuery(id+"F2.wireOp",EDGE,"E853"),sQuery(id+"F2.wireOp",EDGE,"E854"),sQuery(id+"F2.wireOp",EDGE,"E855"),sQuery(id+"F2.wireOp",EDGE,"E856"),sQuery(id+"F2.wireOp",EDGE,"E857"),sQuery(id+"F2.wireOp",EDGE,"E858"),sQuery(id+"F2.wireOp",EDGE,"E859"),sQuery(id+"F2.wireOp",EDGE,"E860"),sQuery(id+"F2.wireOp",EDGE,"E861"),sQuery(id+"F2.wireOp",EDGE,"E862"),sQuery(id+"F2.wireOp",EDGE,"E863"),sQuery(id+"F2.wireOp",EDGE,"E864"),sQuery(id+"F2.wireOp",EDGE,"E865"),sQuery(id+"F2.wireOp",EDGE,"E866"),sQuery(id+"F2.wireOp",EDGE,"E867"),sQuery(id+"F2.wireOp",EDGE,"E868"),sQuery(id+"F2.wireOp",EDGE,"E869"),sQuery(id+"F2.wireOp",EDGE,"E870"),sQuery(id+"F2.wireOp",EDGE,"E871"),sQuery(id+"F2.wireOp",EDGE,"E872"),sQuery(id+"F2.wireOp",EDGE,"E873"),sQuery(id+"F2.wireOp",EDGE,"E874"),sQuery(id+"F2.wireOp",EDGE,"E875"),sQuery(id+"F2.wireOp",EDGE,"E876"),sQuery(id+"F2.wireOp",EDGE,"E877"),sQuery(id+"F2.wireOp",EDGE,"E878"),sQuery(id+"F2.wireOp",EDGE,"E879"),sQuery(id+"F2.wireOp",EDGE,"E880"),sQuery(id+"F2.wireOp",EDGE,"E881"),sQuery(id+"F2.wireOp",EDGE,"E882"),sQuery(id+"F2.wireOp",EDGE,"E883"),sQuery(id+"F2.wireOp",EDGE,"E884"),sQuery(id+"F2.wireOp",EDGE,"E885"),sQuery(id+"F2.wireOp",EDGE,"E886"),sQuery(id+"F2.wireOp",EDGE,"E887"),sQuery(id+"F2.wireOp",EDGE,"E888"),sQuery(id+"F2.wireOp",EDGE,"E889"),sQuery(id+"F2.wireOp",EDGE,"E890"),sQuery(id+"F2.wireOp",EDGE,"E891"),sQuery(id+"F2.wireOp",EDGE,"E892"),sQuery(id+"F2.wireOp",EDGE,"E893"),sQuery(id+"F2.wireOp",EDGE,"E894"),sQuery(id+"F2.wireOp",EDGE,"E895"),sQuery(id+"F2.wireOp",EDGE,"E896"),sQuery(id+"F2.wireOp",EDGE,"E897"),sQuery(id+"F2.wireOp",EDGE,"E898"),sQuery(id+"F2.wireOp",EDGE,"E899"),sQuery(id+"F2.wireOp",EDGE,"E900"),sQuery(id+"F2.wireOp",EDGE,"E901"),sQuery(id+"F2.wireOp",EDGE,"E902"),sQuery(id+"F2.wireOp",EDGE,"E903"),sQuery(id+"F2.wireOp",EDGE,"E904"),sQuery(id+"F2.wireOp",EDGE,"E905"),sQuery(id+"F2.wireOp",EDGE,"E906"),sQuery(id+"F2.wireOp",EDGE,"E907"),sQuery(id+"F2.wireOp",EDGE,"E908"),sQuery(id+"F2.wireOp",EDGE,"E909"),sQuery(id+"F2.wireOp",EDGE,"E910"),sQuery(id+"F2.wireOp",EDGE,"E911"),sQuery(id+"F2.wireOp",EDGE,"E912"),sQuery(id+"F2.wireOp",EDGE,"E913"),sQuery(id+"F2.wireOp",EDGE,"E914"),sQuery(id+"F2.wireOp",EDGE,"E915"),sQuery(id+"F2.wireOp",EDGE,"E916"),sQuery(id+"F2.wireOp",EDGE,"E917"),sQuery(id+"F2.wireOp",EDGE,"E918"),sQuery(id+"F2.wireOp",EDGE,"E919"),sQuery(id+"F2.wireOp",EDGE,"E920"),sQuery(id+"F2.wireOp",EDGE,"E921"),sQuery(id+"F2.wireOp",EDGE,"E922"),sQuery(id+"F2.wireOp",EDGE,"E923"),sQuery(id+"F2.wireOp",EDGE,"E924"),sQuery(id+"F2.wireOp",EDGE,"E925"),sQuery(id+"F2.wireOp",EDGE,"E926"),sQuery(id+"F2.wireOp",EDGE,"E927"),sQuery(id+"F2.wireOp",EDGE,"E928"),sQuery(id+"F2.wireOp",EDGE,"E929"),sQuery(id+"F2.wireOp",EDGE,"E930"),sQuery(id+"F2.wireOp",EDGE,"E931"),sQuery(id+"F2.wireOp",EDGE,"E932"),sQuery(id+"F2.wireOp",EDGE,"E933"),sQuery(id+"F2.wireOp",EDGE,"E934"),sQuery(id+"F2.wireOp",EDGE,"E935"),sQuery(id+"F2.wireOp",EDGE,"E936"),sQuery(id+"F2.wireOp",EDGE,"E937"),sQuery(id+"F2.wireOp",EDGE,"E938"),sQuery(id+"F2.wireOp",EDGE,"E939"),sQuery(id+"F2.wireOp",EDGE,"E940"),sQuery(id+"F2.wireOp",EDGE,"E941"),sQuery(id+"F2.wireOp",EDGE,"E942"),sQuery(id+"F2.wireOp",EDGE,"E943"),sQuery(id+"F2.wireOp",EDGE,"E944"),sQuery(id+"F2.wireOp",EDGE,"E945"),sQuery(id+"F2.wireOp",EDGE,"E946"),sQuery(id+"F2.wireOp",EDGE,"E947"),sQuery(id+"F2.wireOp",EDGE,"E948"),sQuery(id+"F2.wireOp",EDGE,"E949"),sQuery(id+"F2.wireOp",EDGE,"E950"),sQuery(id+"F2.wireOp",EDGE,"E951"),sQuery(id+"F2.wireOp",EDGE,"E952"),sQuery(id+"F2.wireOp",EDGE,"E953"),sQuery(id+"F2.wireOp",EDGE,"E954"),sQuery(id+"F2.wireOp",EDGE,"E955"),sQuery(id+"F2.wireOp",EDGE,"E956"),sQuery(id+"F2.wireOp",EDGE,"E957"),sQuery(id+"F2.wireOp",EDGE,"E958"),sQuery(id+"F2.wireOp",EDGE,"E959"),sQuery(id+"F2.wireOp",EDGE,"E960"),sQuery(id+"F2.wireOp",EDGE,"E961"),sQuery(id+"F2.wireOp",EDGE,"E962"),sQuery(id+"F2.wireOp",EDGE,"E963"),sQuery(id+"F2.wireOp",EDGE,"E964"),sQuery(id+"F2.wireOp",EDGE,"E965"),sQuery(id+"F2.wireOp",EDGE,"E966"),sQuery(id+"F2.wireOp",EDGE,"E967"),sQuery(id+"F2.wireOp",EDGE,"E968"),sQuery(id+"F2.wireOp",EDGE,"E969"),sQuery(id+"F2.wireOp",EDGE,"E970"),sQuery(id+"F2.wireOp",EDGE,"E971"),sQuery(id+"F2.wireOp",EDGE,"E972"),sQuery(id+"F2.wireOp",EDGE,"E973"),sQuery(id+"F2.wireOp",EDGE,"E974"),sQuery(id+"F2.wireOp",EDGE,"E975"),sQuery(id+"F2.wireOp",EDGE,"E976"),sQuery(id+"F2.wireOp",EDGE,"E977"),sQuery(id+"F2.wireOp",EDGE,"E978"),sQuery(id+"F2.wireOp",EDGE,"E979"),sQuery(id+"F2.wireOp",EDGE,"E980"),sQuery(id+"F2.wireOp",EDGE,"E981"),sQuery(id+"F2.wireOp",EDGE,"E982"),sQuery(id+"F2.wireOp",EDGE,"E983"),sQuery(id+"F2.wireOp",EDGE,"E984"),sQuery(id+"F2.wireOp",EDGE,"E985"),sQuery(id+"F2.wireOp",EDGE,"E986"),sQuery(id+"F2.wireOp",EDGE,"E987"),sQuery(id+"F2.wireOp",EDGE,"E988"),sQuery(id+"F2.wireOp",EDGE,"E989"),sQuery(id+"F2.wireOp",EDGE,"E990"),sQuery(id+"F2.wireOp",EDGE,"E991"),sQuery(id+"F2.wireOp",EDGE,"E992"),sQuery(id+"F2.wireOp",EDGE,"E993"),sQuery(id+"F2.wireOp",EDGE,"E994"),sQuery(id+"F2.wireOp",EDGE,"E995"),sQuery(id+"F2.wireOp",EDGE,"E996"),sQuery(id+"F2.wireOp",EDGE,"E997"),sQuery(id+"F2.wireOp",EDGE,"E998"),sQuery(id+"F2.wireOp",EDGE,"E999"),sQuery(id+"F2.wireOp",EDGE,"E1000"),sQuery(id+"F2.wireOp",EDGE,"E1001"),sQuery(id+"F2.wireOp",EDGE,"E1002"),sQuery(id+"F2.wireOp",EDGE,"E1003"),sQuery(id+"F2.wireOp",EDGE,"E1004"),sQuery(id+"F2.wireOp",EDGE,"E1005"),sQuery(id+"F2.wireOp",EDGE,"E1006"),sQuery(id+"F2.wireOp",EDGE,"E1007"),sQuery(id+"F2.wireOp",EDGE,"E1008"),sQuery(id+"F2.wireOp",EDGE,"E1009"),sQuery(id+"F2.wireOp",EDGE,"E1010"),sQuery(id+"F2.wireOp",EDGE,"E1011"),sQuery(id+"F2.wireOp",EDGE,"E1012"),sQuery(id+"F2.wireOp",EDGE,"E1013"),sQuery(id+"F2.wireOp",EDGE,"E1014"),sQuery(id+"F2.wireOp",EDGE,"E1015"),sQuery(id+"F2.wireOp",EDGE,"E1016"),sQuery(id+"F2.wireOp",EDGE,"E1017"),sQuery(id+"F2.wireOp",EDGE,"E1018"),sQuery(id+"F2.wireOp",EDGE,"E1019"),sQuery(id+"F2.wireOp",EDGE,"E1020"),sQuery(id+"F2.wireOp",EDGE,"E1021"),sQuery(id+"F2.wireOp",EDGE,"E1022"),sQuery(id+"F2.wireOp",EDGE,"E1023"),sQuery(id+"F2.wireOp",EDGE,"E1024"),sQuery(id+"F2.wireOp",EDGE,"E1025"),sQuery(id+"F2.wireOp",EDGE,"E1026"),sQuery(id+"F2.wireOp",EDGE,"E1027"),sQuery(id+"F2.wireOp",EDGE,"E1028"),sQuery(id+"F2.wireOp",EDGE,"E1029"),sQuery(id+"F2.wireOp",EDGE,"E1030"),sQuery(id+"F2.wireOp",EDGE,"E1031"),sQuery(id+"F2.wireOp",EDGE,"E1032"),sQuery(id+"F2.wireOp",EDGE,"E1033"),sQuery(id+"F2.wireOp",EDGE,"E1034"),sQuery(id+"F2.wireOp",EDGE,"E1035"),sQuery(id+"F2.wireOp",EDGE,"E1036"),sQuery(id+"F2.wireOp",EDGE,"E1037"),sQuery(id+"F2.wireOp",EDGE,"E1038"),sQuery(id+"F2.wireOp",EDGE,"E1039"),sQuery(id+"F2.wireOp",EDGE,"E1040"),sQuery(id+"F2.wireOp",EDGE,"E1041"),sQuery(id+"F2.wireOp",EDGE,"E1042"),sQuery(id+"F2.wireOp",EDGE,"E1043"),sQuery(id+"F2.wireOp",EDGE,"E1044"),sQuery(id+"F2.wireOp",EDGE,"E1045"),sQuery(id+"F2.wireOp",EDGE,"E1046"),sQuery(id+"F2.wireOp",EDGE,"E1047"),sQuery(id+"F2.wireOp",EDGE,"E1048"),sQuery(id+"F2.wireOp",EDGE,"E1049"),sQuery(id+"F2.wireOp",EDGE,"E1050"),sQuery(id+"F2.wireOp",EDGE,"E1051"),sQuery(id+"F2.wireOp",EDGE,"E1052"),sQuery(id+"F2.wireOp",EDGE,"E1053"),sQuery(id+"F2.wireOp",EDGE,"E1054"),sQuery(id+"F2.wireOp",EDGE,"E1055"),sQuery(id+"F2.wireOp",EDGE,"E1056"),sQuery(id+"F2.wireOp",EDGE,"E1057"),sQuery(id+"F2.wireOp",EDGE,"E1058"),sQuery(id+"F2.wireOp",EDGE,"E1059"),sQuery(id+"F2.wireOp",EDGE,"E1060"),sQuery(id+"F2.wireOp",EDGE,"E1061"),sQuery(id+"F2.wireOp",EDGE,"E1062"),sQuery(id+"F2.wireOp",EDGE,"E1063"),sQuery(id+"F2.wireOp",EDGE,"E1064"),sQuery(id+"F2.wireOp",EDGE,"E1065"),sQuery(id+"F2.wireOp",EDGE,"E1066"),sQuery(id+"F2.wireOp",EDGE,"E1067"),sQuery(id+"F2.wireOp",EDGE,"E1068"),sQuery(id+"F2.wireOp",EDGE,"E1069"),sQuery(id+"F2.wireOp",EDGE,"E1070"),sQuery(id+"F2.wireOp",EDGE,"E1071"),sQuery(id+"F2.wireOp",EDGE,"E1072"),sQuery(id+"F2.wireOp",EDGE,"E1073"),sQuery(id+"F2.wireOp",EDGE,"E1074"),sQuery(id+"F2.wireOp",EDGE,"E1075"),sQuery(id+"F2.wireOp",EDGE,"E1076"),sQuery(id+"F2.wireOp",EDGE,"E1077"),sQuery(id+"F2.wireOp",EDGE,"E1078"),sQuery(id+"F2.wireOp",EDGE,"E1079"),sQuery(id+"F2.wireOp",EDGE,"E1080"),sQuery(id+"F2.wireOp",EDGE,"E1081"),sQuery(id+"F2.wireOp",EDGE,"E1082"),sQuery(id+"F2.wireOp",EDGE,"E1083"),sQuery(id+"F2.wireOp",EDGE,"E1084"),sQuery(id+"F2.wireOp",EDGE,"E1085"),sQuery(id+"F2.wireOp",EDGE,"E1086"),sQuery(id+"F2.wireOp",EDGE,"E1087"),sQuery(id+"F2.wireOp",EDGE,"E1088"),sQuery(id+"F2.wireOp",EDGE,"E1089"),sQuery(id+"F2.wireOp",EDGE,"E1090"),sQuery(id+"F2.wireOp",EDGE,"E1091"),sQuery(id+"F2.wireOp",EDGE,"E1092"),sQuery(id+"F2.wireOp",EDGE,"E1093"),sQuery(id+"F2.wireOp",EDGE,"E1094"),sQuery(id+"F2.wireOp",EDGE,"E1095"),sQuery(id+"F2.wireOp",EDGE,"E1096"),sQuery(id+"F2.wireOp",EDGE,"E1097"),sQuery(id+"F2.wireOp",EDGE,"E1098"),sQuery(id+"F2.wireOp",EDGE,"E1099"),sQuery(id+"F2.wireOp",EDGE,"E1100"),sQuery(id+"F2.wireOp",EDGE,"E1101"),sQuery(id+"F2.wireOp",EDGE,"E1102"),sQuery(id+"F2.wireOp",EDGE,"E1103"),sQuery(id+"F2.wireOp",EDGE,"E1104"),sQuery(id+"F2.wireOp",EDGE,"E1105"),sQuery(id+"F2.wireOp",EDGE,"E1106"),sQuery(id+"F2.wireOp",EDGE,"E1107"),sQuery(id+"F2.wireOp",EDGE,"E1108"),sQuery(id+"F2.wireOp",EDGE,"E1109"),sQuery(id+"F2.wireOp",EDGE,"E1110"),sQuery(id+"F2.wireOp",EDGE,"E1111"),sQuery(id+"F2.wireOp",EDGE,"E1112"),sQuery(id+"F2.wireOp",EDGE,"E1113"),sQuery(id+"F2.wireOp",EDGE,"E1114"),sQuery(id+"F2.wireOp",EDGE,"E1115"),sQuery(id+"F2.wireOp",EDGE,"E1116"),sQuery(id+"F2.wireOp",EDGE,"E1117"),sQuery(id+"F2.wireOp",EDGE,"E1118"),sQuery(id+"F2.wireOp",EDGE,"E1119"),sQuery(id+"F2.wireOp",EDGE,"E1120"),sQuery(id+"F2.wireOp",EDGE,"E1121"),sQuery(id+"F2.wireOp",EDGE,"E1122"),sQuery(id+"F2.wireOp",EDGE,"E1123"),sQuery(id+"F2.wireOp",EDGE,"E1124"),sQuery(id+"F2.wireOp",EDGE,"E1125"),sQuery(id+"F2.wireOp",EDGE,"E1126"),sQuery(id+"F2.wireOp",EDGE,"E1127"),sQuery(id+"F2.wireOp",EDGE,"E1128"),sQuery(id+"F2.wireOp",EDGE,"E1129"),sQuery(id+"F2.wireOp",EDGE,"E1130"),sQuery(id+"F2.wireOp",EDGE,"E1131"),sQuery(id+"F2.wireOp",EDGE,"E1132"),sQuery(id+"F2.wireOp",EDGE,"E1133"),sQuery(id+"F2.wireOp",EDGE,"E1134"),sQuery(id+"F2.wireOp",EDGE,"E1135"),sQuery(id+"F2.wireOp",EDGE,"E1136"),sQuery(id+"F2.wireOp",EDGE,"E1137"),sQuery(id+"F2.wireOp",EDGE,"E1138"),sQuery(id+"F2.wireOp",EDGE,"E1139"),sQuery(id+"F2.wireOp",EDGE,"E1140"),sQuery(id+"F2.wireOp",EDGE,"E1141"),sQuery(id+"F2.wireOp",EDGE,"E1142"),sQuery(id+"F2.wireOp",EDGE,"E1143"),sQuery(id+"F2.wireOp",EDGE,"E1144"),sQuery(id+"F2.wireOp",EDGE,"E1145"),sQuery(id+"F2.wireOp",EDGE,"E1146"),sQuery(id+"F2.wireOp",EDGE,"E1147"),sQuery(id+"F2.wireOp",EDGE,"E1148"),sQuery(id+"F2.wireOp",EDGE,"E1149"),sQuery(id+"F2.wireOp",EDGE,"E1150"),sQuery(id+"F2.wireOp",EDGE,"E1151"),sQuery(id+"F2.wireOp",EDGE,"E1152"),sQuery(id+"F2.wireOp",EDGE,"E1153"),sQuery(id+"F2.wireOp",EDGE,"E1154"),sQuery(id+"F2.wireOp",EDGE,"E1155"),sQuery(id+"F2.wireOp",EDGE,"E1156"),sQuery(id+"F2.wireOp",EDGE,"E1157"),sQuery(id+"F2.wireOp",EDGE,"E1158"),sQuery(id+"F2.wireOp",EDGE,"E1159"),sQuery(id+"F2.wireOp",EDGE,"E1160"),sQuery(id+"F2.wireOp",EDGE,"E1161"),sQuery(id+"F2.wireOp",EDGE,"E1162"),sQuery(id+"F2.wireOp",EDGE,"E1163"),sQuery(id+"F2.wireOp",EDGE,"E1164"),sQuery(id+"F2.wireOp",EDGE,"E1165"),sQuery(id+"F2.wireOp",EDGE,"E1166"),sQuery(id+"F2.wireOp",EDGE,"E1167"),sQuery(id+"F2.wireOp",EDGE,"E1168"),sQuery(id+"F2.wireOp",EDGE,"E1169"),sQuery(id+"F2.wireOp",EDGE,"E1170"),sQuery(id+"F2.wireOp",EDGE,"E1171"),sQuery(id+"F2.wireOp",EDGE,"E1172"),sQuery(id+"F2.wireOp",EDGE,"E1173"),sQuery(id+"F2.wireOp",EDGE,"E1174"),sQuery(id+"F2.wireOp",EDGE,"E1175"),sQuery(id+"F2.wireOp",EDGE,"E1176"),sQuery(id+"F2.wireOp",EDGE,"E1177"),sQuery(id+"F2.wireOp",EDGE,"E1178"),sQuery(id+"F2.wireOp",EDGE,"E1179"),sQuery(id+"F2.wireOp",EDGE,"E1180"),sQuery(id+"F2.wireOp",EDGE,"E1181"),sQuery(id+"F2.wireOp",EDGE,"E1182"),sQuery(id+"F2.wireOp",EDGE,"E1183"),sQuery(id+"F2.wireOp",EDGE,"E1184"),sQuery(id+"F2.wireOp",EDGE,"E1185"),sQuery(id+"F2.wireOp",EDGE,"E1186"),sQuery(id+"F2.wireOp",EDGE,"E1187"),sQuery(id+"F2.wireOp",EDGE,"E1188"),sQuery(id+"F2.wireOp",EDGE,"E1189"),sQuery(id+"F2.wireOp",EDGE,"E1190"),sQuery(id+"F2.wireOp",EDGE,"E1191"),sQuery(id+"F2.wireOp",EDGE,"E1192"),sQuery(id+"F2.wireOp",EDGE,"E1193"),sQuery(id+"F2.wireOp",EDGE,"E1194"),sQuery(id+"F2.wireOp",EDGE,"E1195"),sQuery(id+"F2.wireOp",EDGE,"E1196"),sQuery(id+"F2.wireOp",EDGE,"E1197"),sQuery(id+"F2.wireOp",EDGE,"E1198"),sQuery(id+"F2.wireOp",EDGE,"E1199"),sQuery(id+"F2.wireOp",EDGE,"E1200"),sQuery(id+"F2.wireOp",EDGE,"E1201"),sQuery(id+"F2.wireOp",EDGE,"E1202"),sQuery(id+"F2.wireOp",EDGE,"E1203"),sQuery(id+"F2.wireOp",EDGE,"E1204"),sQuery(id+"F2.wireOp",EDGE,"E1205"),sQuery(id+"F2.wireOp",EDGE,"E1206"),sQuery(id+"F2.wireOp",EDGE,"E1207"),sQuery(id+"F2.wireOp",EDGE,"E1208"),sQuery(id+"F2.wireOp",EDGE,"E1209"),sQuery(id+"F2.wireOp",EDGE,"E1210"),sQuery(id+"F2.wireOp",EDGE,"E1211"),sQuery(id+"F2.wireOp",EDGE,"E1212"),sQuery(id+"F2.wireOp",EDGE,"E1213"),sQuery(id+"F2.wireOp",EDGE,"E1214"),sQuery(id+"F2.wireOp",EDGE,"E1215"),sQuery(id+"F2.wireOp",EDGE,"E1216"),sQuery(id+"F2.wireOp",EDGE,"E1217"),sQuery(id+"F2.wireOp",EDGE,"E1218"),sQuery(id+"F2.wireOp",EDGE,"E1219"),sQuery(id+"F2.wireOp",EDGE,"E1220"),sQuery(id+"F2.wireOp",EDGE,"E1221"),sQuery(id+"F2.wireOp",EDGE,"E1222"),sQuery(id+"F2.wireOp",EDGE,"E1223"),sQuery(id+"F2.wireOp",EDGE,"E1224"),sQuery(id+"F2.wireOp",EDGE,"E1225"),sQuery(id+"F2.wireOp",EDGE,"E1226"),sQuery(id+"F2.wireOp",EDGE,"E1227"),sQuery(id+"F2.wireOp",EDGE,"E1228"),sQuery(id+"F2.wireOp",EDGE,"E1229"),sQuery(id+"F2.wireOp",EDGE,"E1230"),sQuery(id+"F2.wireOp",EDGE,"E1231"),sQuery(id+"F2.wireOp",EDGE,"E1232"),sQuery(id+"F2.wireOp",EDGE,"E1233"),sQuery(id+"F2.wireOp",EDGE,"E1234"),sQuery(id+"F2.wireOp",EDGE,"E1235"),sQuery(id+"F2.wireOp",EDGE,"E1236"),sQuery(id+"F2.wireOp",EDGE,"E1237"),sQuery(id+"F2.wireOp",EDGE,"E1238"),sQuery(id+"F2.wireOp",EDGE,"E1239"),sQuery(id+"F2.wireOp",EDGE,"E1240"),sQuery(id+"F2.wireOp",EDGE,"E1241"),sQuery(id+"F2.wireOp",EDGE,"E1242"),sQuery(id+"F2.wireOp",EDGE,"E1243"),sQuery(id+"F2.wireOp",EDGE,"E1244"),sQuery(id+"F2.wireOp",EDGE,"E1245"),sQuery(id+"F2.wireOp",EDGE,"E1246"),sQuery(id+"F2.wireOp",EDGE,"E1247"),sQuery(id+"F2.wireOp",EDGE,"E1248"),sQuery(id+"F2.wireOp",EDGE,"E1249"),sQuery(id+"F2.wireOp",EDGE,"E1250"),sQuery(id+"F2.wireOp",EDGE,"E1251"),sQuery(id+"F2.wireOp",EDGE,"E1252"),sQuery(id+"F2.wireOp",EDGE,"E1253"),sQuery(id+"F2.wireOp",EDGE,"E1254"),sQuery(id+"F2.wireOp",EDGE,"E1255"),sQuery(id+"F2.wireOp",EDGE,"E1256"),sQuery(id+"F2.wireOp",EDGE,"E1257"),sQuery(id+"F2.wireOp",EDGE,"E1258"),sQuery(id+"F2.wireOp",EDGE,"E1259"),sQuery(id+"F2.wireOp",EDGE,"E1260"),sQuery(id+"F2.wireOp",EDGE,"E1261"),sQuery(id+"F2.wireOp",EDGE,"E1262"),sQuery(id+"F2.wireOp",EDGE,"E1263"),sQuery(id+"F2.wireOp",EDGE,"E1264"),sQuery(id+"F2.wireOp",EDGE,"E1265"),sQuery(id+"F2.wireOp",EDGE,"E1266"),sQuery(id+"F2.wireOp",EDGE,"E1267"),sQuery(id+"F2.wireOp",EDGE,"E1268"),sQuery(id+"F2.wireOp",EDGE,"E1269"),sQuery(id+"F2.wireOp",EDGE,"E1270"),sQuery(id+"F2.wireOp",EDGE,"E1271"),sQuery(id+"F2.wireOp",EDGE,"E1272"),sQuery(id+"F2.wireOp",EDGE,"E1273"),sQuery(id+"F2.wireOp",EDGE,"E1274"),sQuery(id+"F2.wireOp",EDGE,"E1275"),sQuery(id+"F2.wireOp",EDGE,"E1276"),sQuery(id+"F2.wireOp",EDGE,"E1277"),sQuery(id+"F2.wireOp",EDGE,"E1278"),sQuery(id+"F2.wireOp",EDGE,"E1279"),sQuery(id+"F2.wireOp",EDGE,"E1280"),sQuery(id+"F2.wireOp",EDGE,"E1281"),sQuery(id+"F2.wireOp",EDGE,"E1282"),sQuery(id+"F2.wireOp",EDGE,"E1283"),sQuery(id+"F2.wireOp",EDGE,"E1284"),sQuery(id+"F2.wireOp",EDGE,"E1285"),sQuery(id+"F2.wireOp",EDGE,"E1286"),sQuery(id+"F2.wireOp",EDGE,"E1287"),sQuery(id+"F2.wireOp",EDGE,"E1288"),sQuery(id+"F2.wireOp",EDGE,"E1289"),sQuery(id+"F2.wireOp",EDGE,"E1290"),sQuery(id+"F2.wireOp",EDGE,"E1291"),sQuery(id+"F2.wireOp",EDGE,"E1292"),sQuery(id+"F2.wireOp",EDGE,"E1293"),sQuery(id+"F2.wireOp",EDGE,"E1294"),sQuery(id+"F2.wireOp",EDGE,"E1295"),sQuery(id+"F2.wireOp",EDGE,"E1296"),sQuery(id+"F2.wireOp",EDGE,"E1297"),sQuery(id+"F2.wireOp",EDGE,"E1298"),sQuery(id+"F2.wireOp",EDGE,"E1299"),sQuery(id+"F2.wireOp",EDGE,"E1300"),sQuery(id+"F2.wireOp",EDGE,"E1301"),sQuery(id+"F2.wireOp",EDGE,"E1302"),sQuery(id+"F2.wireOp",EDGE,"E1303"),sQuery(id+"F2.wireOp",EDGE,"E1304"),sQuery(id+"F2.wireOp",EDGE,"E1305"),sQuery(id+"F2.wireOp",EDGE,"E1306"),sQuery(id+"F2.wireOp",EDGE,"E1307"),sQuery(id+"F2.wireOp",EDGE,"E1308"),sQuery(id+"F2.wireOp",EDGE,"E1309"),sQuery(id+"F2.wireOp",EDGE,"E1310"),sQuery(id+"F2.wireOp",EDGE,"E1311"),sQuery(id+"F2.wireOp",EDGE,"E1312"),sQuery(id+"F2.wireOp",EDGE,"E1313"),sQuery(id+"F2.wireOp",EDGE,"E1314"),sQuery(id+"F2.wireOp",EDGE,"E1315"),sQuery(id+"F2.wireOp",EDGE,"E1316"),sQuery(id+"F2.wireOp",EDGE,"E1317"),sQuery(id+"F2.wireOp",EDGE,"E1318"),sQuery(id+"F2.wireOp",EDGE,"E1319"),sQuery(id+"F2.wireOp",EDGE,"E1320"),sQuery(id+"F2.wireOp",EDGE,"E1321"),sQuery(id+"F2.wireOp",EDGE,"E1322"),sQuery(id+"F2.wireOp",EDGE,"E1323"),sQuery(id+"F2.wireOp",EDGE,"E1324"),sQuery(id+"F2.wireOp",EDGE,"E1325"),sQuery(id+"F2.wireOp",EDGE,"E1326"),sQuery(id+"F2.wireOp",EDGE,"E1327"),sQuery(id+"F2.wireOp",EDGE,"E1328"),sQuery(id+"F2.wireOp",EDGE,"E1329"),sQuery(id+"F2.wireOp",EDGE,"E1330"),sQuery(id+"F2.wireOp",EDGE,"E1331"),sQuery(id+"F2.wireOp",EDGE,"E1332"),sQuery(id+"F2.wireOp",EDGE,"E1333"),sQuery(id+"F2.wireOp",EDGE,"E1334"),sQuery(id+"F2.wireOp",EDGE,"E1335"),sQuery(id+"F2.wireOp",EDGE,"E1336"),sQuery(id+"F2.wireOp",EDGE,"E1337"),sQuery(id+"F2.wireOp",EDGE,"E1338"),sQuery(id+"F2.wireOp",EDGE,"E1339"),sQuery(id+"F2.wireOp",EDGE,"E1340"),sQuery(id+"F2.wireOp",EDGE,"E1341"),sQuery(id+"F2.wireOp",EDGE,"E1342"),sQuery(id+"F2.wireOp",EDGE,"E1343"),sQuery(id+"F2.wireOp",EDGE,"E1344"),sQuery(id+"F2.wireOp",EDGE,"E1345"),sQuery(id+"F2.wireOp",EDGE,"E1346"),sQuery(id+"F2.wireOp",EDGE,"E1347"),sQuery(id+"F2.wireOp",EDGE,"E1348"),sQuery(id+"F2.wireOp",EDGE,"E1349"),sQuery(id+"F2.wireOp",EDGE,"E1350"),sQuery(id+"F2.wireOp",EDGE,"E1351"),sQuery(id+"F2.wireOp",EDGE,"E1352"),sQuery(id+"F2.wireOp",EDGE,"E1353"),sQuery(id+"F2.wireOp",EDGE,"E1354"),sQuery(id+"F2.wireOp",EDGE,"E1355"),sQuery(id+"F2.wireOp",EDGE,"E1356"),sQuery(id+"F2.wireOp",EDGE,"E1357"),sQuery(id+"F2.wireOp",EDGE,"E1358"),sQuery(id+"F2.wireOp",EDGE,"E1359"),sQuery(id+"F2.wireOp",EDGE,"E1360"),sQuery(id+"F2.wireOp",EDGE,"E1361"),sQuery(id+"F2.wireOp",EDGE,"E1362"),sQuery(id+"F2.wireOp",EDGE,"E1363"),sQuery(id+"F2.wireOp",EDGE,"E1364"),sQuery(id+"F2.wireOp",EDGE,"E1365"),sQuery(id+"F2.wireOp",EDGE,"E1366"),sQuery(id+"F2.wireOp",EDGE,"E1367"),sQuery(id+"F2.wireOp",EDGE,"E1368"),sQuery(id+"F2.wireOp",EDGE,"E1369"),sQuery(id+"F2.wireOp",EDGE,"E1370"),sQuery(id+"F2.wireOp",EDGE,"E1371"),sQuery(id+"F2.wireOp",EDGE,"E1372"),sQuery(id+"F2.wireOp",EDGE,"E1373"),sQuery(id+"F2.wireOp",EDGE,"E1374"),sQuery(id+"F2.wireOp",EDGE,"E1375"),sQuery(id+"F2.wireOp",EDGE,"E1376"),sQuery(id+"F2.wireOp",EDGE,"E1377"),sQuery(id+"F2.wireOp",EDGE,"E1378"),sQuery(id+"F2.wireOp",EDGE,"E1379"),sQuery(id+"F2.wireOp",EDGE,"E1380"),sQuery(id+"F2.wireOp",EDGE,"E1381"),sQuery(id+"F2.wireOp",EDGE,"E1382"),sQuery(id+"F2.wireOp",EDGE,"E1383"),sQuery(id+"F2.wireOp",EDGE,"E1384"),sQuery(id+"F2.wireOp",EDGE,"E1385"),sQuery(id+"F2.wireOp",EDGE,"E1386"),sQuery(id+"F2.wireOp",EDGE,"E1387"),sQuery(id+"F2.wireOp",EDGE,"E1388"),sQuery(id+"F2.wireOp",EDGE,"E1389"),sQuery(id+"F2.wireOp",EDGE,"E1390"),sQuery(id+"F2.wireOp",EDGE,"E1391"),sQuery(id+"F2.wireOp",EDGE,"E1392"),sQuery(id+"F2.wireOp",EDGE,"E1393"),sQuery(id+"F2.wireOp",EDGE,"E1394"),sQuery(id+"F2.wireOp",EDGE,"E1395"),sQuery(id+"F2.wireOp",EDGE,"E1396"),sQuery(id+"F2.wireOp",EDGE,"E1397"),sQuery(id+"F2.wireOp",EDGE,"E1398"),sQuery(id+"F2.wireOp",EDGE,"E1399"),sQuery(id+"F2.wireOp",EDGE,"E1400"),sQuery(id+"F2.wireOp",EDGE,"E1401"),sQuery(id+"F2.wireOp",EDGE,"E1402"),sQuery(id+"F2.wireOp",EDGE,"E1403"),sQuery(id+"F2.wireOp",EDGE,"E1404"),sQuery(id+"F2.wireOp",EDGE,"E1405"),sQuery(id+"F2.wireOp",EDGE,"E1406"),sQuery(id+"F2.wireOp",EDGE,"E1407"),sQuery(id+"F2.wireOp",EDGE,"E1408"),sQuery(id+"F2.wireOp",EDGE,"E1409"),sQuery(id+"F2.wireOp",EDGE,"E1410"),sQuery(id+"F2.wireOp",EDGE,"E1411"),sQuery(id+"F2.wireOp",EDGE,"E1412"),sQuery(id+"F2.wireOp",EDGE,"E1413"),sQuery(id+"F2.wireOp",EDGE,"E1414"),sQuery(id+"F2.wireOp",EDGE,"E1415"),sQuery(id+"F2.wireOp",EDGE,"E1416"),sQuery(id+"F2.wireOp",EDGE,"E1417"),sQuery(id+"F2.wireOp",EDGE,"E1418"),sQuery(id+"F2.wireOp",EDGE,"E1419"),sQuery(id+"F2.wireOp",EDGE,"E1420"),sQuery(id+"F2.wireOp",EDGE,"E1421"),sQuery(id+"F2.wireOp",EDGE,"E1422"),sQuery(id+"F2.wireOp",EDGE,"E1423"),sQuery(id+"F2.wireOp",EDGE,"E1424"),sQuery(id+"F2.wireOp",EDGE,"E1425"),sQuery(id+"F2.wireOp",EDGE,"E1426"),sQuery(id+"F2.wireOp",EDGE,"E1427"),sQuery(id+"F2.wireOp",EDGE,"E1428"),sQuery(id+"F2.wireOp",EDGE,"E1429"),sQuery(id+"F2.wireOp",EDGE,"E1430"),sQuery(id+"F2.wireOp",EDGE,"E1431"),sQuery(id+"F2.wireOp",EDGE,"E1432"),sQuery(id+"F2.wireOp",EDGE,"E1433"),sQuery(id+"F2.wireOp",EDGE,"E1434"),sQuery(id+"F2.wireOp",EDGE,"E1435"),sQuery(id+"F2.wireOp",EDGE,"E1436"),sQuery(id+"F2.wireOp",EDGE,"E1437"),sQuery(id+"F2.wireOp",EDGE,"E1438"),sQuery(id+"F2.wireOp",EDGE,"E1439"),sQuery(id+"F2.wireOp",EDGE,"E1440"),sQuery(id+"F2.wireOp",EDGE,"E1441"),sQuery(id+"F2.wireOp",EDGE,"E1442"),sQuery(id+"F2.wireOp",EDGE,"E1443"),sQuery(id+"F2.wireOp",EDGE,"E1444"),sQuery(id+"F2.wireOp",EDGE,"E1445"),sQuery(id+"F2.wireOp",EDGE,"E1446"),sQuery(id+"F2.wireOp",EDGE,"E1447"),sQuery(id+"F2.wireOp",EDGE,"E1448"),sQuery(id+"F2.wireOp",EDGE,"E1449"),sQuery(id+"F2.wireOp",EDGE,"E1450"),sQuery(id+"F2.wireOp",EDGE,"E1451"),sQuery(id+"F2.wireOp",EDGE,"E1452"),sQuery(id+"F2.wireOp",EDGE,"E1453"),sQuery(id+"F2.wireOp",EDGE,"E1454"),sQuery(id+"F2.wireOp",EDGE,"E1455"),sQuery(id+"F2.wireOp",EDGE,"E1456"),sQuery(id+"F2.wireOp",EDGE,"E1457"),sQuery(id+"F2.wireOp",EDGE,"E1458"),sQuery(id+"F2.wireOp",EDGE,"E1459"),sQuery(id+"F2.wireOp",EDGE,"E1460"),sQuery(id+"F2.wireOp",EDGE,"E1461"),sQuery(id+"F2.wireOp",EDGE,"E1462"),sQuery(id+"F2.wireOp",EDGE,"E1463"),sQuery(id+"F2.wireOp",EDGE,"E1464"),sQuery(id+"F2.wireOp",EDGE,"E1465"),sQuery(id+"F2.wireOp",EDGE,"E1466"),sQuery(id+"F2.wireOp",EDGE,"E1467"),sQuery(id+"F2.wireOp",EDGE,"E1468"),sQuery(id+"F2.wireOp",EDGE,"E1469"),sQuery(id+"F2.wireOp",EDGE,"E1470"),sQuery(id+"F2.wireOp",EDGE,"E1471"),sQuery(id+"F2.wireOp",EDGE,"E1472"),sQuery(id+"F2.wireOp",EDGE,"E1473"),sQuery(id+"F2.wireOp",EDGE,"E1474")])]});
            var Q1;
            Q1=sQuery(id+"F0.wireOp",VERTEX,"E0.center");
            var Q2;
            Q2=sQuery(id+"F0.wireOp",VERTEX,"E3.center");
            transform(context, id + "F10", {"entities" : qUnion([Q0]), "transformType" : TransformType.TRANSLATION_ENTITY, "oppositeDirectionEntity" : false, "transformLine" : qUnion([Q1, Q2]), "makeCopy" : false});
        }
        {
            var Q0;
            Q0=qCreatedBy(makeId("Front.planeOp"),FACE);
            var sketch = newSketch(context, id + "F11", { "sketchPlane" : qUnion([Q0])});
            skLineSegment(sketch, "E1476", {"start": v(14.68, -1.33) * mm, "end": v(14.85, -1.32) * mm});
            skLineSegment(sketch, "E1477", {"start": v(14.85, -1.32) * mm, "end": v(15.03, -1.3) * mm});
            skLineSegment(sketch, "E1478", {"start": v(15.03, -1.3) * mm, "end": v(15.2, -1.28) * mm});
            skLineSegment(sketch, "E1479", {"start": v(15.2, -1.28) * mm, "end": v(15.36, -1.25) * mm});
            skLineSegment(sketch, "E1480", {"start": v(15.36, -1.25) * mm, "end": v(15.53, -1.2) * mm});
            skLineSegment(sketch, "E1481", {"start": v(15.53, -1.2) * mm, "end": v(15.7, -1.16) * mm});
            skLineSegment(sketch, "E1482", {"start": v(15.7, -1.16) * mm, "end": v(15.87, -1.1) * mm});
            skLineSegment(sketch, "E1483", {"start": v(15.87, -1.1) * mm, "end": v(16.03, -1.05) * mm});
            skLineSegment(sketch, "E1484", {"start": v(16.03, -1.05) * mm, "end": v(16.2, -1) * mm});
            skLineSegment(sketch, "E1485", {"start": v(16.2, -1) * mm, "end": v(16.35, -0.93) * mm});
            skLineSegment(sketch, "E1486", {"start": v(16.35, -0.93) * mm, "end": v(16.52, -0.86) * mm});
            skLineSegment(sketch, "E1487", {"start": v(16.52, -0.86) * mm, "end": v(16.67, -0.79) * mm});
            skLineSegment(sketch, "E1488", {"start": v(16.67, -0.79) * mm, "end": v(16.84, -0.7) * mm});
            skLineSegment(sketch, "E1489", {"start": v(16.84, -0.7) * mm, "end": v(17, -0.63) * mm});
            skLineSegment(sketch, "E1490", {"start": v(17, -0.63) * mm, "end": v(17.15, -0.54) * mm});
            skLineSegment(sketch, "E1491", {"start": v(17.15, -0.54) * mm, "end": v(17.18, -0.53) * mm});
            skLineSegment(sketch, "E1492", {"start": v(17.18, -0.53) * mm, "end": v(17.19, -0.34) * mm});
            skLineSegment(sketch, "E1493", {"start": v(17.19, -0.34) * mm, "end": v(17.19, -0.15) * mm});
            skLineSegment(sketch, "E1494", {"start": v(17.19, -0.15) * mm, "end": v(17.19, 0.05) * mm});
            skLineSegment(sketch, "E1495", {"start": v(17.19, 0.05) * mm, "end": v(17.19, 0.24) * mm});
            skLineSegment(sketch, "E1496", {"start": v(17.19, 0.24) * mm, "end": v(17.18, 0.43) * mm});
            skLineSegment(sketch, "E1497", {"start": v(17.18, 0.43) * mm, "end": v(17.18, 0.53) * mm});
            skLineSegment(sketch, "E1498", {"start": v(17.18, 0.53) * mm, "end": v(17.02, 0.62) * mm});
            skLineSegment(sketch, "E1499", {"start": v(17.02, 0.62) * mm, "end": v(16.86, 0.7) * mm});
            skLineSegment(sketch, "E1500", {"start": v(16.86, 0.7) * mm, "end": v(16.7, 0.78) * mm});
            skLineSegment(sketch, "E1501", {"start": v(16.7, 0.78) * mm, "end": v(16.52, 0.86) * mm});
            skLineSegment(sketch, "E1502", {"start": v(16.52, 0.86) * mm, "end": v(16.36, 0.93) * mm});
            skLineSegment(sketch, "E1503", {"start": v(16.36, 0.93) * mm, "end": v(16.19, 1) * mm});
            skLineSegment(sketch, "E1504", {"start": v(16.19, 1) * mm, "end": v(16.02, 1.06) * mm});
            skLineSegment(sketch, "E1505", {"start": v(16.02, 1.06) * mm, "end": v(15.85, 1.12) * mm});
            skLineSegment(sketch, "E1506", {"start": v(15.85, 1.12) * mm, "end": v(15.68, 1.17) * mm});
            skLineSegment(sketch, "E1507", {"start": v(15.68, 1.17) * mm, "end": v(15.5, 1.22) * mm});
            skLineSegment(sketch, "E1508", {"start": v(15.5, 1.22) * mm, "end": v(15.31, 1.26) * mm});
            skLineSegment(sketch, "E1509", {"start": v(15.31, 1.26) * mm, "end": v(15.12, 1.3) * mm});
            skLineSegment(sketch, "E1510", {"start": v(15.12, 1.3) * mm, "end": v(14.95, 1.32) * mm});
            skLineSegment(sketch, "E1511", {"start": v(14.95, 1.32) * mm, "end": v(14.78, 1.33) * mm});
            skLineSegment(sketch, "E1512", {"start": v(14.78, 1.33) * mm, "end": v(14.74, 1.33) * mm});
            skLineSegment(sketch, "E1513", {"start": v(14.74, 1.33) * mm, "end": v(14.55, 1.32) * mm});
            skLineSegment(sketch, "E1514", {"start": v(14.55, 1.32) * mm, "end": v(14.35, 1.32) * mm});
            skLineSegment(sketch, "E1515", {"start": v(14.35, 1.32) * mm, "end": v(14.18, 1.33) * mm});
            skLineSegment(sketch, "E1516", {"start": v(14.18, 1.33) * mm, "end": v(14, 1.37) * mm});
            skLineSegment(sketch, "E1517", {"start": v(14, 1.37) * mm, "end": v(13.85, 1.45) * mm});
            skLineSegment(sketch, "E1518", {"start": v(13.85, 1.45) * mm, "end": v(13.75, 1.54) * mm});
            skLineSegment(sketch, "E1519", {"start": v(13.75, 1.54) * mm, "end": v(13.72, 1.73) * mm});
            skLineSegment(sketch, "E1520", {"start": v(13.72, 1.73) * mm, "end": v(13.69, 1.91) * mm});
            skLineSegment(sketch, "E1521", {"start": v(13.69, 1.91) * mm, "end": v(13.66, 2.1) * mm});
            skLineSegment(sketch, "E1522", {"start": v(13.66, 2.1) * mm, "end": v(13.62, 2.28) * mm});
            skLineSegment(sketch, "E1523", {"start": v(13.62, 2.28) * mm, "end": v(13.6, 2.47) * mm});
            skLineSegment(sketch, "E1524", {"start": v(13.6, 2.47) * mm, "end": v(13.59, 2.57) * mm});
            skLineSegment(sketch, "E1525", {"start": v(13.59, 2.57) * mm, "end": v(13.67, 2.73) * mm});
            skLineSegment(sketch, "E1526", {"start": v(13.67, 2.73) * mm, "end": v(13.8, 2.84) * mm});
            skLineSegment(sketch, "E1527", {"start": v(13.8, 2.84) * mm, "end": v(13.95, 2.93) * mm});
            skLineSegment(sketch, "E1528", {"start": v(13.95, 2.93) * mm, "end": v(14.13, 2.99) * mm});
            skLineSegment(sketch, "E1529", {"start": v(14.13, 2.99) * mm, "end": v(14.3, 3.04) * mm});
            skLineSegment(sketch, "E1530", {"start": v(14.3, 3.04) * mm, "end": v(14.47, 3.1) * mm});
            skLineSegment(sketch, "E1531", {"start": v(14.47, 3.1) * mm, "end": v(14.63, 3.15) * mm});
            skLineSegment(sketch, "E1532", {"start": v(14.63, 3.15) * mm, "end": v(14.8, 3.22) * mm});
            skLineSegment(sketch, "E1533", {"start": v(14.8, 3.22) * mm, "end": v(14.95, 3.3) * mm});
            skLineSegment(sketch, "E1534", {"start": v(14.95, 3.3) * mm, "end": v(15.1, 3.38) * mm});
            skLineSegment(sketch, "E1535", {"start": v(15.1, 3.38) * mm, "end": v(15.24, 3.47) * mm});
            skLineSegment(sketch, "E1536", {"start": v(15.24, 3.47) * mm, "end": v(15.39, 3.57) * mm});
            skLineSegment(sketch, "E1537", {"start": v(15.39, 3.57) * mm, "end": v(15.53, 3.67) * mm});
            skLineSegment(sketch, "E1538", {"start": v(15.53, 3.67) * mm, "end": v(15.67, 3.77) * mm});
            skLineSegment(sketch, "E1539", {"start": v(15.67, 3.77) * mm, "end": v(15.81, 3.88) * mm});
            skLineSegment(sketch, "E1540", {"start": v(15.81, 3.88) * mm, "end": v(15.94, 3.99) * mm});
            skLineSegment(sketch, "E1541", {"start": v(15.94, 3.99) * mm, "end": v(16.08, 4.1) * mm});
            skLineSegment(sketch, "E1542", {"start": v(16.08, 4.1) * mm, "end": v(16.21, 4.23) * mm});
            skLineSegment(sketch, "E1543", {"start": v(16.21, 4.23) * mm, "end": v(16.34, 4.35) * mm});
            skLineSegment(sketch, "E1544", {"start": v(16.34, 4.35) * mm, "end": v(16.46, 4.47) * mm});
            skLineSegment(sketch, "E1545", {"start": v(16.46, 4.47) * mm, "end": v(16.57, 4.58) * mm});
            skLineSegment(sketch, "E1546", {"start": v(16.57, 4.58) * mm, "end": v(16.52, 4.76) * mm});
            skLineSegment(sketch, "E1547", {"start": v(16.52, 4.76) * mm, "end": v(16.47, 4.94) * mm});
            skLineSegment(sketch, "E1548", {"start": v(16.47, 4.94) * mm, "end": v(16.4, 5.14) * mm});
            skLineSegment(sketch, "E1549", {"start": v(16.4, 5.14) * mm, "end": v(16.35, 5.32) * mm});
            skLineSegment(sketch, "E1550", {"start": v(16.35, 5.32) * mm, "end": v(16.3, 5.5) * mm});
            skLineSegment(sketch, "E1551", {"start": v(16.3, 5.5) * mm, "end": v(16.26, 5.58) * mm});
            skLineSegment(sketch, "E1552", {"start": v(16.26, 5.58) * mm, "end": v(16.08, 5.62) * mm});
            skLineSegment(sketch, "E1553", {"start": v(16.08, 5.62) * mm, "end": v(15.9, 5.65) * mm});
            skLineSegment(sketch, "E1554", {"start": v(15.9, 5.65) * mm, "end": v(15.72, 5.68) * mm});
            skLineSegment(sketch, "E1555", {"start": v(15.72, 5.68) * mm, "end": v(15.53, 5.7) * mm});
            skLineSegment(sketch, "E1556", {"start": v(15.53, 5.7) * mm, "end": v(15.36, 5.72) * mm});
            skLineSegment(sketch, "E1557", {"start": v(15.36, 5.72) * mm, "end": v(15.17, 5.74) * mm});
            skLineSegment(sketch, "E1558", {"start": v(15.17, 5.74) * mm, "end": v(15, 5.75) * mm});
            skLineSegment(sketch, "E1559", {"start": v(15, 5.75) * mm, "end": v(14.81, 5.76) * mm});
            skLineSegment(sketch, "E1560", {"start": v(14.81, 5.76) * mm, "end": v(14.74, 5.76) * mm});
            skLineSegment(sketch, "E1561", {"start": v(14.74, 5.76) * mm, "end": v(14.54, 5.75) * mm});
            skLineSegment(sketch, "E1562", {"start": v(14.54, 5.75) * mm, "end": v(14.37, 5.74) * mm});
            skLineSegment(sketch, "E1563", {"start": v(14.37, 5.74) * mm, "end": v(14.18, 5.73) * mm});
            skLineSegment(sketch, "E1564", {"start": v(14.18, 5.73) * mm, "end": v(14, 5.7) * mm});
            skLineSegment(sketch, "E1565", {"start": v(14, 5.7) * mm, "end": v(13.83, 5.67) * mm});
            skLineSegment(sketch, "E1566", {"start": v(13.83, 5.67) * mm, "end": v(13.67, 5.62) * mm});
            skLineSegment(sketch, "E1567", {"start": v(13.67, 5.62) * mm, "end": v(13.5, 5.56) * mm});
            skLineSegment(sketch, "E1568", {"start": v(13.5, 5.56) * mm, "end": v(13.33, 5.5) * mm});
            skLineSegment(sketch, "E1569", {"start": v(13.33, 5.5) * mm, "end": v(13.15, 5.47) * mm});
            skLineSegment(sketch, "E1570", {"start": v(13.15, 5.47) * mm, "end": v(13, 5.46) * mm});
            skLineSegment(sketch, "E1571", {"start": v(13, 5.46) * mm, "end": v(12.82, 5.48) * mm});
            skLineSegment(sketch, "E1572", {"start": v(12.82, 5.48) * mm, "end": v(12.69, 5.54) * mm});
            skLineSegment(sketch, "E1573", {"start": v(12.69, 5.54) * mm, "end": v(12.6, 5.71) * mm});
            skLineSegment(sketch, "E1574", {"start": v(12.6, 5.71) * mm, "end": v(12.51, 5.88) * mm});
            skLineSegment(sketch, "E1575", {"start": v(12.51, 5.88) * mm, "end": v(12.43, 6.05) * mm});
            skLineSegment(sketch, "E1576", {"start": v(12.43, 6.05) * mm, "end": v(12.34, 6.21) * mm});
            skLineSegment(sketch, "E1577", {"start": v(12.34, 6.21) * mm, "end": v(12.26, 6.38) * mm});
            skLineSegment(sketch, "E1578", {"start": v(12.26, 6.38) * mm, "end": v(12.22, 6.48) * mm});
            skLineSegment(sketch, "E1579", {"start": v(12.22, 6.48) * mm, "end": v(12.26, 6.66) * mm});
            skLineSegment(sketch, "E1580", {"start": v(12.26, 6.66) * mm, "end": v(12.35, 6.8) * mm});
            skLineSegment(sketch, "E1581", {"start": v(12.35, 6.8) * mm, "end": v(12.46, 6.93) * mm});
            skLineSegment(sketch, "E1582", {"start": v(12.46, 6.93) * mm, "end": v(12.62, 7.03) * mm});
            skLineSegment(sketch, "E1583", {"start": v(12.62, 7.03) * mm, "end": v(12.77, 7.14) * mm});
            skLineSegment(sketch, "E1584", {"start": v(12.77, 7.14) * mm, "end": v(12.91, 7.24) * mm});
            skLineSegment(sketch, "E1585", {"start": v(12.91, 7.24) * mm, "end": v(13.05, 7.34) * mm});
            skLineSegment(sketch, "E1586", {"start": v(13.05, 7.34) * mm, "end": v(13.18, 7.46) * mm});
            skLineSegment(sketch, "E1587", {"start": v(13.18, 7.46) * mm, "end": v(13.3, 7.58) * mm});
            skLineSegment(sketch, "E1588", {"start": v(13.3, 7.58) * mm, "end": v(13.42, 7.7) * mm});
            skLineSegment(sketch, "E1589", {"start": v(13.42, 7.7) * mm, "end": v(13.54, 7.83) * mm});
            skLineSegment(sketch, "E1590", {"start": v(13.54, 7.83) * mm, "end": v(13.65, 7.96) * mm});
            skLineSegment(sketch, "E1591", {"start": v(13.65, 7.96) * mm, "end": v(13.76, 8.1) * mm});
            skLineSegment(sketch, "E1592", {"start": v(13.76, 8.1) * mm, "end": v(13.86, 8.24) * mm});
            skLineSegment(sketch, "E1593", {"start": v(13.86, 8.24) * mm, "end": v(13.96, 8.39) * mm});
            skLineSegment(sketch, "E1594", {"start": v(13.96, 8.39) * mm, "end": v(14.06, 8.53) * mm});
            skLineSegment(sketch, "E1595", {"start": v(14.06, 8.53) * mm, "end": v(14.15, 8.69) * mm});
            skLineSegment(sketch, "E1596", {"start": v(14.15, 8.69) * mm, "end": v(14.24, 8.84) * mm});
            skLineSegment(sketch, "E1597", {"start": v(14.24, 8.84) * mm, "end": v(14.33, 8.99) * mm});
            skLineSegment(sketch, "E1598", {"start": v(14.33, 8.99) * mm, "end": v(14.41, 9.14) * mm});
            skLineSegment(sketch, "E1599", {"start": v(14.41, 9.14) * mm, "end": v(14.48, 9.28) * mm});
            skLineSegment(sketch, "E1600", {"start": v(14.48, 9.28) * mm, "end": v(14.38, 9.44) * mm});
            skLineSegment(sketch, "E1601", {"start": v(14.38, 9.44) * mm, "end": v(14.27, 9.6) * mm});
            skLineSegment(sketch, "E1602", {"start": v(14.27, 9.6) * mm, "end": v(14.16, 9.76) * mm});
            skLineSegment(sketch, "E1603", {"start": v(14.16, 9.76) * mm, "end": v(14.05, 9.92) * mm});
            skLineSegment(sketch, "E1604", {"start": v(14.05, 9.92) * mm, "end": v(13.94, 10.07) * mm});
            skLineSegment(sketch, "E1605", {"start": v(13.94, 10.07) * mm, "end": v(13.89, 10.15) * mm});
            skLineSegment(sketch, "E1606", {"start": v(13.89, 10.15) * mm, "end": v(13.7, 10.13) * mm});
            skLineSegment(sketch, "E1607", {"start": v(13.7, 10.13) * mm, "end": v(13.53, 10.1) * mm});
            skLineSegment(sketch, "E1608", {"start": v(13.53, 10.1) * mm, "end": v(13.34, 10.08) * mm});
            skLineSegment(sketch, "E1609", {"start": v(13.34, 10.08) * mm, "end": v(13.16, 10.05) * mm});
            skLineSegment(sketch, "E1610", {"start": v(13.16, 10.05) * mm, "end": v(12.99, 10.02) * mm});
            skLineSegment(sketch, "E1611", {"start": v(12.99, 10.02) * mm, "end": v(12.8, 9.98) * mm});
            skLineSegment(sketch, "E1612", {"start": v(12.8, 9.98) * mm, "end": v(12.63, 9.93) * mm});
            skLineSegment(sketch, "E1613", {"start": v(12.63, 9.93) * mm, "end": v(12.45, 9.88) * mm});
            skLineSegment(sketch, "E1614", {"start": v(12.45, 9.88) * mm, "end": v(12.29, 9.83) * mm});
            skLineSegment(sketch, "E1615", {"start": v(12.29, 9.83) * mm, "end": v(12.11, 9.77) * mm});
            skLineSegment(sketch, "E1616", {"start": v(12.11, 9.77) * mm, "end": v(11.93, 9.7) * mm});
            skLineSegment(sketch, "E1617", {"start": v(11.93, 9.7) * mm, "end": v(11.76, 9.62) * mm});
            skLineSegment(sketch, "E1618", {"start": v(11.76, 9.62) * mm, "end": v(11.6, 9.54) * mm});
            skLineSegment(sketch, "E1619", {"start": v(11.6, 9.54) * mm, "end": v(11.45, 9.45) * mm});
            skLineSegment(sketch, "E1620", {"start": v(11.45, 9.45) * mm, "end": v(11.3, 9.34) * mm});
            skLineSegment(sketch, "E1621", {"start": v(11.3, 9.34) * mm, "end": v(11.14, 9.23) * mm});
            skLineSegment(sketch, "E1622", {"start": v(11.14, 9.23) * mm, "end": v(11, 9.15) * mm});
            skLineSegment(sketch, "E1623", {"start": v(11, 9.15) * mm, "end": v(10.83, 9.07) * mm});
            skLineSegment(sketch, "E1624", {"start": v(10.83, 9.07) * mm, "end": v(10.65, 9.03) * mm});
            skLineSegment(sketch, "E1625", {"start": v(10.65, 9.03) * mm, "end": v(10.62, 9.03) * mm});
            skLineSegment(sketch, "E1626", {"start": v(10.62, 9.03) * mm, "end": v(10.49, 9.05) * mm});
            skLineSegment(sketch, "E1627", {"start": v(10.49, 9.05) * mm, "end": v(10.35, 9.19) * mm});
            skLineSegment(sketch, "E1628", {"start": v(10.35, 9.19) * mm, "end": v(10.22, 9.32) * mm});
            skLineSegment(sketch, "E1629", {"start": v(10.22, 9.32) * mm, "end": v(10.1, 9.46) * mm});
            skLineSegment(sketch, "E1630", {"start": v(10.1, 9.46) * mm, "end": v(9.96, 9.6) * mm});
            skLineSegment(sketch, "E1631", {"start": v(9.96, 9.6) * mm, "end": v(9.83, 9.73) * mm});
            skLineSegment(sketch, "E1632", {"start": v(9.83, 9.73) * mm, "end": v(9.77, 9.81) * mm});
            skLineSegment(sketch, "E1633", {"start": v(9.77, 9.81) * mm, "end": v(9.75, 10) * mm});
            skLineSegment(sketch, "E1634", {"start": v(9.75, 10) * mm, "end": v(9.8, 10.16) * mm});
            skLineSegment(sketch, "E1635", {"start": v(9.8, 10.16) * mm, "end": v(9.87, 10.31) * mm});
            skLineSegment(sketch, "E1636", {"start": v(9.87, 10.31) * mm, "end": v(9.98, 10.46) * mm});
            skLineSegment(sketch, "E1637", {"start": v(9.98, 10.46) * mm, "end": v(10.1, 10.6) * mm});
            skLineSegment(sketch, "E1638", {"start": v(10.1, 10.6) * mm, "end": v(10.2, 10.74) * mm});
            skLineSegment(sketch, "E1639", {"start": v(10.2, 10.74) * mm, "end": v(10.3, 10.88) * mm});
            skLineSegment(sketch, "E1640", {"start": v(10.3, 10.88) * mm, "end": v(10.4, 11.03) * mm});
            skLineSegment(sketch, "E1641", {"start": v(10.4, 11.03) * mm, "end": v(10.48, 11.18) * mm});
            skLineSegment(sketch, "E1642", {"start": v(10.48, 11.18) * mm, "end": v(10.56, 11.33) * mm});
            skLineSegment(sketch, "E1643", {"start": v(10.56, 11.33) * mm, "end": v(10.63, 11.49) * mm});
            skLineSegment(sketch, "E1644", {"start": v(10.63, 11.49) * mm, "end": v(10.7, 11.65) * mm});
            skLineSegment(sketch, "E1645", {"start": v(10.7, 11.65) * mm, "end": v(10.76, 11.81) * mm});
            skLineSegment(sketch, "E1646", {"start": v(10.76, 11.81) * mm, "end": v(10.81, 11.98) * mm});
            skLineSegment(sketch, "E1647", {"start": v(10.81, 11.98) * mm, "end": v(10.87, 12.15) * mm});
            skLineSegment(sketch, "E1648", {"start": v(10.87, 12.15) * mm, "end": v(10.92, 12.31) * mm});
            skLineSegment(sketch, "E1649", {"start": v(10.92, 12.31) * mm, "end": v(10.96, 12.49) * mm});
            skLineSegment(sketch, "E1650", {"start": v(10.96, 12.49) * mm, "end": v(11, 12.66) * mm});
            skLineSegment(sketch, "E1651", {"start": v(11, 12.66) * mm, "end": v(11.04, 12.83) * mm});
            skLineSegment(sketch, "E1652", {"start": v(11.04, 12.83) * mm, "end": v(11.07, 13) * mm});
            skLineSegment(sketch, "E1653", {"start": v(11.07, 13) * mm, "end": v(11.1, 13.15) * mm});
            skLineSegment(sketch, "E1654", {"start": v(11.1, 13.15) * mm, "end": v(10.96, 13.27) * mm});
            skLineSegment(sketch, "E1655", {"start": v(10.96, 13.27) * mm, "end": v(10.81, 13.4) * mm});
            skLineSegment(sketch, "E1656", {"start": v(10.81, 13.4) * mm, "end": v(10.65, 13.52) * mm});
            skLineSegment(sketch, "E1657", {"start": v(10.65, 13.52) * mm, "end": v(10.5, 13.64) * mm});
            skLineSegment(sketch, "E1658", {"start": v(10.5, 13.64) * mm, "end": v(10.35, 13.75) * mm});
            skLineSegment(sketch, "E1659", {"start": v(10.35, 13.75) * mm, "end": v(10.28, 13.8) * mm});
            skLineSegment(sketch, "E1660", {"start": v(10.28, 13.8) * mm, "end": v(10.1, 13.73) * mm});
            skLineSegment(sketch, "E1661", {"start": v(10.1, 13.73) * mm, "end": v(9.95, 13.67) * mm});
            skLineSegment(sketch, "E1662", {"start": v(9.95, 13.67) * mm, "end": v(9.77, 13.58) * mm});
            skLineSegment(sketch, "E1663", {"start": v(9.77, 13.58) * mm, "end": v(9.6, 13.5) * mm});
            skLineSegment(sketch, "E1664", {"start": v(9.6, 13.5) * mm, "end": v(9.45, 13.42) * mm});
            skLineSegment(sketch, "E1665", {"start": v(9.45, 13.42) * mm, "end": v(9.3, 13.32) * mm});
            skLineSegment(sketch, "E1666", {"start": v(9.3, 13.32) * mm, "end": v(9.14, 13.23) * mm});
            skLineSegment(sketch, "E1667", {"start": v(9.14, 13.23) * mm, "end": v(8.98, 13.13) * mm});
            skLineSegment(sketch, "E1668", {"start": v(8.98, 13.13) * mm, "end": v(8.84, 13.04) * mm});
            skLineSegment(sketch, "E1669", {"start": v(8.84, 13.04) * mm, "end": v(8.7, 12.92) * mm});
            skLineSegment(sketch, "E1670", {"start": v(8.7, 12.92) * mm, "end": v(8.54, 12.8) * mm});
            skLineSegment(sketch, "E1671", {"start": v(8.54, 12.8) * mm, "end": v(8.4, 12.68) * mm});
            skLineSegment(sketch, "E1672", {"start": v(8.4, 12.68) * mm, "end": v(8.27, 12.56) * mm});
            skLineSegment(sketch, "E1673", {"start": v(8.27, 12.56) * mm, "end": v(8.15, 12.43) * mm});
            skLineSegment(sketch, "E1674", {"start": v(8.15, 12.43) * mm, "end": v(8.04, 12.28) * mm});
            skLineSegment(sketch, "E1675", {"start": v(8.04, 12.28) * mm, "end": v(7.92, 12.13) * mm});
            skLineSegment(sketch, "E1676", {"start": v(7.92, 12.13) * mm, "end": v(7.81, 12) * mm});
            skLineSegment(sketch, "E1677", {"start": v(7.81, 12) * mm, "end": v(7.67, 11.88) * mm});
            skLineSegment(sketch, "E1678", {"start": v(7.67, 11.88) * mm, "end": v(7.51, 11.79) * mm});
            skLineSegment(sketch, "E1679", {"start": v(7.51, 11.79) * mm, "end": v(7.37, 11.76) * mm});
            skLineSegment(sketch, "E1680", {"start": v(7.37, 11.76) * mm, "end": v(7.32, 11.77) * mm});
            skLineSegment(sketch, "E1681", {"start": v(7.32, 11.77) * mm, "end": v(7.15, 11.86) * mm});
            skLineSegment(sketch, "E1682", {"start": v(7.15, 11.86) * mm, "end": v(6.99, 11.95) * mm});
            skLineSegment(sketch, "E1683", {"start": v(6.99, 11.95) * mm, "end": v(6.83, 12.04) * mm});
            skLineSegment(sketch, "E1684", {"start": v(6.83, 12.04) * mm, "end": v(6.66, 12.13) * mm});
            skLineSegment(sketch, "E1685", {"start": v(6.66, 12.13) * mm, "end": v(6.5, 12.23) * mm});
            skLineSegment(sketch, "E1686", {"start": v(6.5, 12.23) * mm, "end": v(6.42, 12.3) * mm});
            skLineSegment(sketch, "E1687", {"start": v(6.42, 12.3) * mm, "end": v(6.36, 12.47) * mm});
            skLineSegment(sketch, "E1688", {"start": v(6.36, 12.47) * mm, "end": v(6.36, 12.65) * mm});
            skLineSegment(sketch, "E1689", {"start": v(6.36, 12.65) * mm, "end": v(6.4, 12.83) * mm});
            skLineSegment(sketch, "E1690", {"start": v(6.4, 12.83) * mm, "end": v(6.47, 13) * mm});
            skLineSegment(sketch, "E1691", {"start": v(6.47, 13) * mm, "end": v(6.54, 13.18) * mm});
            skLineSegment(sketch, "E1692", {"start": v(6.54, 13.18) * mm, "end": v(6.6, 13.34) * mm});
            skLineSegment(sketch, "E1693", {"start": v(6.6, 13.34) * mm, "end": v(6.65, 13.5) * mm});
            skLineSegment(sketch, "E1694", {"start": v(6.65, 13.5) * mm, "end": v(6.7, 13.66) * mm});
            skLineSegment(sketch, "E1695", {"start": v(6.7, 13.66) * mm, "end": v(6.72, 13.83) * mm});
            skLineSegment(sketch, "E1696", {"start": v(6.72, 13.83) * mm, "end": v(6.75, 14) * mm});
            skLineSegment(sketch, "E1697", {"start": v(6.75, 14) * mm, "end": v(6.77, 14.19) * mm});
            skLineSegment(sketch, "E1698", {"start": v(6.77, 14.19) * mm, "end": v(6.79, 14.36) * mm});
            skLineSegment(sketch, "E1699", {"start": v(6.79, 14.36) * mm, "end": v(6.8, 14.54) * mm});
            skLineSegment(sketch, "E1700", {"start": v(6.8, 14.54) * mm, "end": v(6.8, 14.7) * mm});
            skLineSegment(sketch, "E1701", {"start": v(6.8, 14.7) * mm, "end": v(6.8, 14.89) * mm});
            skLineSegment(sketch, "E1702", {"start": v(6.8, 14.89) * mm, "end": v(6.8, 15.07) * mm});
            skLineSegment(sketch, "E1703", {"start": v(6.8, 15.07) * mm, "end": v(6.79, 15.24) * mm});
            skLineSegment(sketch, "E1704", {"start": v(6.79, 15.24) * mm, "end": v(6.78, 15.42) * mm});
            skLineSegment(sketch, "E1705", {"start": v(6.78, 15.42) * mm, "end": v(6.76, 15.59) * mm});
            skLineSegment(sketch, "E1706", {"start": v(6.76, 15.59) * mm, "end": v(6.74, 15.77) * mm});
            skLineSegment(sketch, "E1707", {"start": v(6.74, 15.77) * mm, "end": v(6.73, 15.86) * mm});
            skLineSegment(sketch, "E1708", {"start": v(6.73, 15.86) * mm, "end": v(6.55, 15.93) * mm});
            skLineSegment(sketch, "E1709", {"start": v(6.55, 15.93) * mm, "end": v(6.38, 16) * mm});
            skLineSegment(sketch, "E1710", {"start": v(6.38, 16) * mm, "end": v(6.19, 16.08) * mm});
            skLineSegment(sketch, "E1711", {"start": v(6.19, 16.08) * mm, "end": v(6.01, 16.14) * mm});
            skLineSegment(sketch, "E1712", {"start": v(6.01, 16.14) * mm, "end": v(5.84, 16.2) * mm});
            skLineSegment(sketch, "E1713", {"start": v(5.84, 16.2) * mm, "end": v(5.75, 16.24) * mm});
            skLineSegment(sketch, "E1714", {"start": v(5.75, 16.24) * mm, "end": v(5.6, 16.12) * mm});
            skLineSegment(sketch, "E1715", {"start": v(5.6, 16.12) * mm, "end": v(5.48, 16) * mm});
            skLineSegment(sketch, "E1716", {"start": v(5.48, 16) * mm, "end": v(5.33, 15.88) * mm});
            skLineSegment(sketch, "E1717", {"start": v(5.33, 15.88) * mm, "end": v(5.2, 15.75) * mm});
            skLineSegment(sketch, "E1718", {"start": v(5.2, 15.75) * mm, "end": v(5.08, 15.63) * mm});
            skLineSegment(sketch, "E1719", {"start": v(5.08, 15.63) * mm, "end": v(4.95, 15.49) * mm});
            skLineSegment(sketch, "E1720", {"start": v(4.95, 15.49) * mm, "end": v(4.83, 15.36) * mm});
            skLineSegment(sketch, "E1721", {"start": v(4.83, 15.36) * mm, "end": v(4.71, 15.22) * mm});
            skLineSegment(sketch, "E1722", {"start": v(4.71, 15.22) * mm, "end": v(4.6, 15.08) * mm});
            skLineSegment(sketch, "E1723", {"start": v(4.6, 15.08) * mm, "end": v(4.5, 14.93) * mm});
            skLineSegment(sketch, "E1724", {"start": v(4.5, 14.93) * mm, "end": v(4.38, 14.77) * mm});
            skLineSegment(sketch, "E1725", {"start": v(4.38, 14.77) * mm, "end": v(4.28, 14.6) * mm});
            skLineSegment(sketch, "E1726", {"start": v(4.28, 14.6) * mm, "end": v(4.2, 14.45) * mm});
            skLineSegment(sketch, "E1727", {"start": v(4.2, 14.45) * mm, "end": v(4.12, 14.3) * mm});
            skLineSegment(sketch, "E1728", {"start": v(4.12, 14.3) * mm, "end": v(4.06, 14.12) * mm});
            skLineSegment(sketch, "E1729", {"start": v(4.06, 14.12) * mm, "end": v(4, 13.94) * mm});
            skLineSegment(sketch, "E1730", {"start": v(4, 13.94) * mm, "end": v(3.92, 13.79) * mm});
            skLineSegment(sketch, "E1731", {"start": v(3.92, 13.79) * mm, "end": v(3.83, 13.63) * mm});
            skLineSegment(sketch, "E1732", {"start": v(3.83, 13.63) * mm, "end": v(3.7, 13.5) * mm});
            skLineSegment(sketch, "E1733", {"start": v(3.7, 13.5) * mm, "end": v(3.55, 13.42) * mm});
            skLineSegment(sketch, "E1734", {"start": v(3.55, 13.42) * mm, "end": v(3.52, 13.42) * mm});
            skLineSegment(sketch, "E1735", {"start": v(3.52, 13.42) * mm, "end": v(3.34, 13.46) * mm});
            skLineSegment(sketch, "E1736", {"start": v(3.34, 13.46) * mm, "end": v(3.15, 13.5) * mm});
            skLineSegment(sketch, "E1737", {"start": v(3.15, 13.5) * mm, "end": v(2.97, 13.54) * mm});
            skLineSegment(sketch, "E1738", {"start": v(2.97, 13.54) * mm, "end": v(2.79, 13.58) * mm});
            skLineSegment(sketch, "E1739", {"start": v(2.79, 13.58) * mm, "end": v(2.6, 13.62) * mm});
            skLineSegment(sketch, "E1740", {"start": v(2.6, 13.62) * mm, "end": v(2.5, 13.66) * mm});
            skLineSegment(sketch, "E1741", {"start": v(2.5, 13.66) * mm, "end": v(2.4, 13.8) * mm});
            skLineSegment(sketch, "E1742", {"start": v(2.4, 13.8) * mm, "end": v(2.35, 13.98) * mm});
            skLineSegment(sketch, "E1743", {"start": v(2.35, 13.98) * mm, "end": v(2.33, 14.16) * mm});
            skLineSegment(sketch, "E1744", {"start": v(2.33, 14.16) * mm, "end": v(2.34, 14.35) * mm});
            skLineSegment(sketch, "E1745", {"start": v(2.34, 14.35) * mm, "end": v(2.36, 14.54) * mm});
            skLineSegment(sketch, "E1746", {"start": v(2.36, 14.54) * mm, "end": v(2.37, 14.7) * mm});
            skLineSegment(sketch, "E1747", {"start": v(2.37, 14.7) * mm, "end": v(2.37, 14.88) * mm});
            skLineSegment(sketch, "E1748", {"start": v(2.37, 14.88) * mm, "end": v(2.36, 15.05) * mm});
            skLineSegment(sketch, "E1749", {"start": v(2.36, 15.05) * mm, "end": v(2.34, 15.22) * mm});
            skLineSegment(sketch, "E1750", {"start": v(2.34, 15.22) * mm, "end": v(2.32, 15.4) * mm});
            skLineSegment(sketch, "E1751", {"start": v(2.32, 15.4) * mm, "end": v(2.29, 15.57) * mm});
            skLineSegment(sketch, "E1752", {"start": v(2.29, 15.57) * mm, "end": v(2.25, 15.74) * mm});
            skLineSegment(sketch, "E1753", {"start": v(2.25, 15.74) * mm, "end": v(2.2, 15.92) * mm});
            skLineSegment(sketch, "E1754", {"start": v(2.2, 15.92) * mm, "end": v(2.16, 16.08) * mm});
            skLineSegment(sketch, "E1755", {"start": v(2.16, 16.08) * mm, "end": v(2.1, 16.25) * mm});
            skLineSegment(sketch, "E1756", {"start": v(2.1, 16.25) * mm, "end": v(2.05, 16.42) * mm});
            skLineSegment(sketch, "E1757", {"start": v(2.05, 16.42) * mm, "end": v(2, 16.58) * mm});
            skLineSegment(sketch, "E1758", {"start": v(2, 16.58) * mm, "end": v(1.93, 16.75) * mm});
            skLineSegment(sketch, "E1759", {"start": v(1.93, 16.75) * mm, "end": v(1.86, 16.9) * mm});
            skLineSegment(sketch, "E1760", {"start": v(1.86, 16.9) * mm, "end": v(1.79, 17.07) * mm});
            skLineSegment(sketch, "E1761", {"start": v(1.79, 17.07) * mm, "end": v(1.75, 17.15) * mm});
            skLineSegment(sketch, "E1762", {"start": v(1.75, 17.15) * mm, "end": v(1.56, 17.17) * mm});
            skLineSegment(sketch, "E1763", {"start": v(1.56, 17.17) * mm, "end": v(1.38, 17.19) * mm});
            skLineSegment(sketch, "E1764", {"start": v(1.38, 17.19) * mm, "end": v(1.17, 17.2) * mm});
            skLineSegment(sketch, "E1765", {"start": v(1.17, 17.2) * mm, "end": v(0.99, 17.22) * mm});
            skLineSegment(sketch, "E1766", {"start": v(0.99, 17.22) * mm, "end": v(0.8, 17.23) * mm});
            skLineSegment(sketch, "E1767", {"start": v(0.8, 17.23) * mm, "end": v(0.7, 17.23) * mm});
            skLineSegment(sketch, "E1768", {"start": v(0.7, 17.23) * mm, "end": v(0.6, 17.07) * mm});
            skLineSegment(sketch, "E1769", {"start": v(0.6, 17.07) * mm, "end": v(0.51, 16.93) * mm});
            skLineSegment(sketch, "E1770", {"start": v(0.51, 16.93) * mm, "end": v(0.41, 16.76) * mm});
            skLineSegment(sketch, "E1771", {"start": v(0.41, 16.76) * mm, "end": v(0.32, 16.6) * mm});
            skLineSegment(sketch, "E1772", {"start": v(0.32, 16.6) * mm, "end": v(0.24, 16.45) * mm});
            skLineSegment(sketch, "E1773", {"start": v(0.24, 16.45) * mm, "end": v(0.16, 16.28) * mm});
            skLineSegment(sketch, "E1774", {"start": v(0.16, 16.28) * mm, "end": v(0.09, 16.12) * mm});
            skLineSegment(sketch, "E1775", {"start": v(0.09, 16.12) * mm, "end": v(0.01, 15.95) * mm});
            skLineSegment(sketch, "E1776", {"start": v(0.01, 15.95) * mm, "end": v(-0.05, 15.79) * mm});
            skLineSegment(sketch, "E1777", {"start": v(-0.05, 15.79) * mm, "end": v(-0.1, 15.6) * mm});
            skLineSegment(sketch, "E1778", {"start": v(-0.1, 15.6) * mm, "end": v(-0.17, 15.42) * mm});
            skLineSegment(sketch, "E1779", {"start": v(-0.17, 15.42) * mm, "end": v(-0.22, 15.24) * mm});
            skLineSegment(sketch, "E1780", {"start": v(-0.22, 15.24) * mm, "end": v(-0.25, 15.07) * mm});
            skLineSegment(sketch, "E1781", {"start": v(-0.25, 15.07) * mm, "end": v(-0.28, 14.9) * mm});
            skLineSegment(sketch, "E1782", {"start": v(-0.28, 14.9) * mm, "end": v(-0.29, 14.7) * mm});
            skLineSegment(sketch, "E1783", {"start": v(-0.29, 14.7) * mm, "end": v(-0.3, 14.52) * mm});
            skLineSegment(sketch, "E1784", {"start": v(-0.3, 14.52) * mm, "end": v(-0.32, 14.35) * mm});
            skLineSegment(sketch, "E1785", {"start": v(-0.32, 14.35) * mm, "end": v(-0.36, 14.17) * mm});
            skLineSegment(sketch, "E1786", {"start": v(-0.36, 14.17) * mm, "end": v(-0.45, 14) * mm});
            skLineSegment(sketch, "E1787", {"start": v(-0.45, 14) * mm, "end": v(-0.56, 13.9) * mm});
            skLineSegment(sketch, "E1788", {"start": v(-0.56, 13.9) * mm, "end": v(-0.75, 13.87) * mm});
            skLineSegment(sketch, "E1789", {"start": v(-0.75, 13.87) * mm, "end": v(-0.94, 13.85) * mm});
            skLineSegment(sketch, "E1790", {"start": v(-0.94, 13.85) * mm, "end": v(-1.13, 13.84) * mm});
            skLineSegment(sketch, "E1791", {"start": v(-1.13, 13.84) * mm, "end": v(-1.31, 13.82) * mm});
            skLineSegment(sketch, "E1792", {"start": v(-1.31, 13.82) * mm, "end": v(-1.5, 13.8) * mm});
            skLineSegment(sketch, "E1793", {"start": v(-1.5, 13.8) * mm, "end": v(-1.53, 13.8) * mm});
            skLineSegment(sketch, "E1794", {"start": v(-1.53, 13.8) * mm, "end": v(-1.63, 13.81) * mm});
            skLineSegment(sketch, "E1795", {"start": v(-1.63, 13.81) * mm, "end": v(-1.78, 13.92) * mm});
            skLineSegment(sketch, "E1796", {"start": v(-1.78, 13.92) * mm, "end": v(-1.88, 14.07) * mm});
            skLineSegment(sketch, "E1797", {"start": v(-1.88, 14.07) * mm, "end": v(-1.95, 14.24) * mm});
            skLineSegment(sketch, "E1798", {"start": v(-1.95, 14.24) * mm, "end": v(-2, 14.42) * mm});
            skLineSegment(sketch, "E1799", {"start": v(-2, 14.42) * mm, "end": v(-2.03, 14.6) * mm});
            skLineSegment(sketch, "E1800", {"start": v(-2.03, 14.6) * mm, "end": v(-2.07, 14.77) * mm});
            skLineSegment(sketch, "E1801", {"start": v(-2.07, 14.77) * mm, "end": v(-2.12, 14.93) * mm});
            skLineSegment(sketch, "E1802", {"start": v(-2.12, 14.93) * mm, "end": v(-2.18, 15.1) * mm});
            skLineSegment(sketch, "E1803", {"start": v(-2.18, 15.1) * mm, "end": v(-2.25, 15.25) * mm});
            skLineSegment(sketch, "E1804", {"start": v(-2.25, 15.25) * mm, "end": v(-2.32, 15.41) * mm});
            skLineSegment(sketch, "E1805", {"start": v(-2.32, 15.41) * mm, "end": v(-2.4, 15.57) * mm});
            skLineSegment(sketch, "E1806", {"start": v(-2.4, 15.57) * mm, "end": v(-2.5, 15.72) * mm});
            skLineSegment(sketch, "E1807", {"start": v(-2.5, 15.72) * mm, "end": v(-2.59, 15.88) * mm});
            skLineSegment(sketch, "E1808", {"start": v(-2.59, 15.88) * mm, "end": v(-2.68, 16.02) * mm});
            skLineSegment(sketch, "E1809", {"start": v(-2.68, 16.02) * mm, "end": v(-2.78, 16.17) * mm});
            skLineSegment(sketch, "E1810", {"start": v(-2.78, 16.17) * mm, "end": v(-2.88, 16.31) * mm});
            skLineSegment(sketch, "E1811", {"start": v(-2.88, 16.31) * mm, "end": v(-2.99, 16.45) * mm});
            skLineSegment(sketch, "E1812", {"start": v(-2.99, 16.45) * mm, "end": v(-3.1, 16.59) * mm});
            skLineSegment(sketch, "E1813", {"start": v(-3.1, 16.59) * mm, "end": v(-3.2, 16.72) * mm});
            skLineSegment(sketch, "E1814", {"start": v(-3.2, 16.72) * mm, "end": v(-3.32, 16.86) * mm});
            skLineSegment(sketch, "E1815", {"start": v(-3.32, 16.86) * mm, "end": v(-3.39, 16.93) * mm});
            skLineSegment(sketch, "E1816", {"start": v(-3.39, 16.93) * mm, "end": v(-3.57, 16.89) * mm});
            skLineSegment(sketch, "E1817", {"start": v(-3.57, 16.89) * mm, "end": v(-3.75, 16.85) * mm});
            skLineSegment(sketch, "E1818", {"start": v(-3.75, 16.85) * mm, "end": v(-3.95, 16.8) * mm});
            skLineSegment(sketch, "E1819", {"start": v(-3.95, 16.8) * mm, "end": v(-4.14, 16.76) * mm});
            skLineSegment(sketch, "E1820", {"start": v(-4.14, 16.76) * mm, "end": v(-4.32, 16.72) * mm});
            skLineSegment(sketch, "E1821", {"start": v(-4.32, 16.72) * mm, "end": v(-4.41, 16.7) * mm});
            skLineSegment(sketch, "E1822", {"start": v(-4.41, 16.7) * mm, "end": v(-4.46, 16.51) * mm});
            skLineSegment(sketch, "E1823", {"start": v(-4.46, 16.51) * mm, "end": v(-4.5, 16.35) * mm});
            skLineSegment(sketch, "E1824", {"start": v(-4.5, 16.35) * mm, "end": v(-4.55, 16.16) * mm});
            skLineSegment(sketch, "E1825", {"start": v(-4.55, 16.16) * mm, "end": v(-4.59, 15.98) * mm});
            skLineSegment(sketch, "E1826", {"start": v(-4.59, 15.98) * mm, "end": v(-4.62, 15.8) * mm});
            skLineSegment(sketch, "E1827", {"start": v(-4.62, 15.8) * mm, "end": v(-4.65, 15.62) * mm});
            skLineSegment(sketch, "E1828", {"start": v(-4.65, 15.62) * mm, "end": v(-4.67, 15.44) * mm});
            skLineSegment(sketch, "E1829", {"start": v(-4.67, 15.44) * mm, "end": v(-4.69, 15.26) * mm});
            skLineSegment(sketch, "E1830", {"start": v(-4.69, 15.26) * mm, "end": v(-4.7, 15.09) * mm});
            skLineSegment(sketch, "E1831", {"start": v(-4.7, 15.09) * mm, "end": v(-4.7, 14.9) * mm});
            skLineSegment(sketch, "E1832", {"start": v(-4.7, 14.9) * mm, "end": v(-4.7, 14.7) * mm});
            skLineSegment(sketch, "E1833", {"start": v(-4.7, 14.7) * mm, "end": v(-4.7, 14.52) * mm});
            skLineSegment(sketch, "E1834", {"start": v(-4.7, 14.52) * mm, "end": v(-4.68, 14.34) * mm});
            skLineSegment(sketch, "E1835", {"start": v(-4.68, 14.34) * mm, "end": v(-4.66, 14.17) * mm});
            skLineSegment(sketch, "E1836", {"start": v(-4.66, 14.17) * mm, "end": v(-4.6, 13.99) * mm});
            skLineSegment(sketch, "E1837", {"start": v(-4.6, 13.99) * mm, "end": v(-4.56, 13.8) * mm});
            skLineSegment(sketch, "E1838", {"start": v(-4.56, 13.8) * mm, "end": v(-4.53, 13.64) * mm});
            skLineSegment(sketch, "E1839", {"start": v(-4.53, 13.64) * mm, "end": v(-4.53, 13.45) * mm});
            skLineSegment(sketch, "E1840", {"start": v(-4.53, 13.45) * mm, "end": v(-4.56, 13.27) * mm});
            skLineSegment(sketch, "E1841", {"start": v(-4.56, 13.27) * mm, "end": v(-4.64, 13.13) * mm});
            skLineSegment(sketch, "E1842", {"start": v(-4.64, 13.13) * mm, "end": v(-4.81, 13.05) * mm});
            skLineSegment(sketch, "E1843", {"start": v(-4.81, 13.05) * mm, "end": v(-4.98, 12.98) * mm});
            skLineSegment(sketch, "E1844", {"start": v(-4.98, 12.98) * mm, "end": v(-5.16, 12.9) * mm});
            skLineSegment(sketch, "E1845", {"start": v(-5.16, 12.9) * mm, "end": v(-5.33, 12.83) * mm});
            skLineSegment(sketch, "E1846", {"start": v(-5.33, 12.83) * mm, "end": v(-5.5, 12.76) * mm});
            skLineSegment(sketch, "E1847", {"start": v(-5.5, 12.76) * mm, "end": v(-5.6, 12.73) * mm});
            skLineSegment(sketch, "E1848", {"start": v(-5.6, 12.73) * mm, "end": v(-5.78, 12.78) * mm});
            skLineSegment(sketch, "E1849", {"start": v(-5.78, 12.78) * mm, "end": v(-5.92, 12.88) * mm});
            skLineSegment(sketch, "E1850", {"start": v(-5.92, 12.88) * mm, "end": v(-6.03, 13) * mm});
            skLineSegment(sketch, "E1851", {"start": v(-6.03, 13) * mm, "end": v(-6.13, 13.17) * mm});
            skLineSegment(sketch, "E1852", {"start": v(-6.13, 13.17) * mm, "end": v(-6.22, 13.33) * mm});
            skLineSegment(sketch, "E1853", {"start": v(-6.22, 13.33) * mm, "end": v(-6.3, 13.48) * mm});
            skLineSegment(sketch, "E1854", {"start": v(-6.3, 13.48) * mm, "end": v(-6.4, 13.62) * mm});
            skLineSegment(sketch, "E1855", {"start": v(-6.4, 13.62) * mm, "end": v(-6.5, 13.76) * mm});
            skLineSegment(sketch, "E1856", {"start": v(-6.5, 13.76) * mm, "end": v(-6.62, 13.9) * mm});
            skLineSegment(sketch, "E1857", {"start": v(-6.62, 13.9) * mm, "end": v(-6.73, 14.02) * mm});
            skLineSegment(sketch, "E1858", {"start": v(-6.73, 14.02) * mm, "end": v(-6.85, 14.15) * mm});
            skLineSegment(sketch, "E1859", {"start": v(-6.85, 14.15) * mm, "end": v(-6.97, 14.27) * mm});
            skLineSegment(sketch, "E1860", {"start": v(-6.97, 14.27) * mm, "end": v(-7.1, 14.38) * mm});
            skLineSegment(sketch, "E1861", {"start": v(-7.1, 14.38) * mm, "end": v(-7.24, 14.5) * mm});
            skLineSegment(sketch, "E1862", {"start": v(-7.24, 14.5) * mm, "end": v(-7.38, 14.61) * mm});
            skLineSegment(sketch, "E1863", {"start": v(-7.38, 14.61) * mm, "end": v(-7.51, 14.72) * mm});
            skLineSegment(sketch, "E1864", {"start": v(-7.51, 14.72) * mm, "end": v(-7.66, 14.82) * mm});
            skLineSegment(sketch, "E1865", {"start": v(-7.66, 14.82) * mm, "end": v(-7.8, 14.93) * mm});
            skLineSegment(sketch, "E1866", {"start": v(-7.8, 14.93) * mm, "end": v(-7.95, 15.02) * mm});
            skLineSegment(sketch, "E1867", {"start": v(-7.95, 15.02) * mm, "end": v(-8.1, 15.12) * mm});
            skLineSegment(sketch, "E1868", {"start": v(-8.1, 15.12) * mm, "end": v(-8.23, 15.2) * mm});
            skLineSegment(sketch, "E1869", {"start": v(-8.23, 15.2) * mm, "end": v(-8.4, 15.1) * mm});
            skLineSegment(sketch, "E1870", {"start": v(-8.4, 15.1) * mm, "end": v(-8.56, 15.01) * mm});
            skLineSegment(sketch, "E1871", {"start": v(-8.56, 15.01) * mm, "end": v(-8.73, 14.91) * mm});
            skLineSegment(sketch, "E1872", {"start": v(-8.73, 14.91) * mm, "end": v(-8.9, 14.82) * mm});
            skLineSegment(sketch, "E1873", {"start": v(-8.9, 14.82) * mm, "end": v(-9.06, 14.72) * mm});
            skLineSegment(sketch, "E1874", {"start": v(-9.06, 14.72) * mm, "end": v(-9.14, 14.67) * mm});
            skLineSegment(sketch, "E1875", {"start": v(-9.14, 14.67) * mm, "end": v(-9.13, 14.48) * mm});
            skLineSegment(sketch, "E1876", {"start": v(-9.13, 14.48) * mm, "end": v(-9.12, 14.31) * mm});
            skLineSegment(sketch, "E1877", {"start": v(-9.12, 14.31) * mm, "end": v(-9.11, 14.12) * mm});
            skLineSegment(sketch, "E1878", {"start": v(-9.11, 14.12) * mm, "end": v(-9.1, 13.93) * mm});
            skLineSegment(sketch, "E1879", {"start": v(-9.1, 13.93) * mm, "end": v(-9.07, 13.76) * mm});
            skLineSegment(sketch, "E1880", {"start": v(-9.07, 13.76) * mm, "end": v(-9.05, 13.57) * mm});
            skLineSegment(sketch, "E1881", {"start": v(-9.05, 13.57) * mm, "end": v(-9.02, 13.4) * mm});
            skLineSegment(sketch, "E1882", {"start": v(-9.02, 13.4) * mm, "end": v(-8.98, 13.22) * mm});
            skLineSegment(sketch, "E1883", {"start": v(-8.98, 13.22) * mm, "end": v(-8.94, 13.05) * mm});
            skLineSegment(sketch, "E1884", {"start": v(-8.94, 13.05) * mm, "end": v(-8.9, 12.87) * mm});
            skLineSegment(sketch, "E1885", {"start": v(-8.9, 12.87) * mm, "end": v(-8.84, 12.68) * mm});
            skLineSegment(sketch, "E1886", {"start": v(-8.84, 12.68) * mm, "end": v(-8.77, 12.5) * mm});
            skLineSegment(sketch, "E1887", {"start": v(-8.77, 12.5) * mm, "end": v(-8.7, 12.34) * mm});
            skLineSegment(sketch, "E1888", {"start": v(-8.7, 12.34) * mm, "end": v(-8.63, 12.19) * mm});
            skLineSegment(sketch, "E1889", {"start": v(-8.63, 12.19) * mm, "end": v(-8.53, 12.02) * mm});
            skLineSegment(sketch, "E1890", {"start": v(-8.53, 12.02) * mm, "end": v(-8.43, 11.86) * mm});
            skLineSegment(sketch, "E1891", {"start": v(-8.43, 11.86) * mm, "end": v(-8.35, 11.71) * mm});
            skLineSegment(sketch, "E1892", {"start": v(-8.35, 11.71) * mm, "end": v(-8.3, 11.54) * mm});
            skLineSegment(sketch, "E1893", {"start": v(-8.3, 11.54) * mm, "end": v(-8.27, 11.36) * mm});
            skLineSegment(sketch, "E1894", {"start": v(-8.27, 11.36) * mm, "end": v(-8.3, 11.2) * mm});
            skLineSegment(sketch, "E1895", {"start": v(-8.3, 11.2) * mm, "end": v(-8.45, 11.07) * mm});
            skLineSegment(sketch, "E1896", {"start": v(-8.45, 11.07) * mm, "end": v(-8.6, 10.95) * mm});
            skLineSegment(sketch, "E1897", {"start": v(-8.6, 10.95) * mm, "end": v(-8.74, 10.83) * mm});
            skLineSegment(sketch, "E1898", {"start": v(-8.74, 10.83) * mm, "end": v(-8.88, 10.71) * mm});
            skLineSegment(sketch, "E1899", {"start": v(-8.88, 10.71) * mm, "end": v(-9.02, 10.6) * mm});
            skLineSegment(sketch, "E1900", {"start": v(-9.02, 10.6) * mm, "end": v(-9.11, 10.53) * mm});
            skLineSegment(sketch, "E1901", {"start": v(-9.11, 10.53) * mm, "end": v(-9.2, 10.52) * mm});
            skLineSegment(sketch, "E1902", {"start": v(-9.2, 10.52) * mm, "end": v(-9.38, 10.55) * mm});
            skLineSegment(sketch, "E1903", {"start": v(-9.38, 10.55) * mm, "end": v(-9.54, 10.63) * mm});
            skLineSegment(sketch, "E1904", {"start": v(-9.54, 10.63) * mm, "end": v(-9.68, 10.73) * mm});
            skLineSegment(sketch, "E1905", {"start": v(-9.68, 10.73) * mm, "end": v(-9.82, 10.86) * mm});
            skLineSegment(sketch, "E1906", {"start": v(-9.82, 10.86) * mm, "end": v(-9.96, 11) * mm});
            skLineSegment(sketch, "E1907", {"start": v(-9.96, 11) * mm, "end": v(-10.1, 11.11) * mm});
            skLineSegment(sketch, "E1908", {"start": v(-10.1, 11.11) * mm, "end": v(-10.23, 11.22) * mm});
            skLineSegment(sketch, "E1909", {"start": v(-10.23, 11.22) * mm, "end": v(-10.37, 11.31) * mm});
            skLineSegment(sketch, "E1910", {"start": v(-10.37, 11.31) * mm, "end": v(-10.52, 11.4) * mm});
            skLineSegment(sketch, "E1911", {"start": v(-10.52, 11.4) * mm, "end": v(-10.67, 11.5) * mm});
            skLineSegment(sketch, "E1912", {"start": v(-10.67, 11.5) * mm, "end": v(-10.83, 11.57) * mm});
            skLineSegment(sketch, "E1913", {"start": v(-10.83, 11.57) * mm, "end": v(-10.98, 11.65) * mm});
            skLineSegment(sketch, "E1914", {"start": v(-10.98, 11.65) * mm, "end": v(-11.14, 11.72) * mm});
            skLineSegment(sketch, "E1915", {"start": v(-11.14, 11.72) * mm, "end": v(-11.3, 11.78) * mm});
            skLineSegment(sketch, "E1916", {"start": v(-11.3, 11.78) * mm, "end": v(-11.46, 11.84) * mm});
            skLineSegment(sketch, "E1917", {"start": v(-11.46, 11.84) * mm, "end": v(-11.63, 11.9) * mm});
            skLineSegment(sketch, "E1918", {"start": v(-11.63, 11.9) * mm, "end": v(-11.8, 11.96) * mm});
            skLineSegment(sketch, "E1919", {"start": v(-11.8, 11.96) * mm, "end": v(-11.97, 12.01) * mm});
            skLineSegment(sketch, "E1920", {"start": v(-11.97, 12.01) * mm, "end": v(-12.14, 12.06) * mm});
            skLineSegment(sketch, "E1921", {"start": v(-12.14, 12.06) * mm, "end": v(-12.31, 12.1) * mm});
            skLineSegment(sketch, "E1922", {"start": v(-12.31, 12.1) * mm, "end": v(-12.34, 12.11) * mm});
            skLineSegment(sketch, "E1923", {"start": v(-12.34, 12.11) * mm, "end": v(-12.47, 11.98) * mm});
            skLineSegment(sketch, "E1924", {"start": v(-12.47, 11.98) * mm, "end": v(-12.6, 11.84) * mm});
            skLineSegment(sketch, "E1925", {"start": v(-12.6, 11.84) * mm, "end": v(-12.74, 11.7) * mm});
            skLineSegment(sketch, "E1926", {"start": v(-12.74, 11.7) * mm, "end": v(-12.87, 11.55) * mm});
            skLineSegment(sketch, "E1927", {"start": v(-12.87, 11.55) * mm, "end": v(-13, 11.41) * mm});
            skLineSegment(sketch, "E1928", {"start": v(-13, 11.41) * mm, "end": v(-13.06, 11.34) * mm});
            skLineSegment(sketch, "E1929", {"start": v(-13.06, 11.34) * mm, "end": v(-13, 11.16) * mm});
            skLineSegment(sketch, "E1930", {"start": v(-13, 11.16) * mm, "end": v(-12.94, 11) * mm});
            skLineSegment(sketch, "E1931", {"start": v(-12.94, 11) * mm, "end": v(-12.87, 10.82) * mm});
            skLineSegment(sketch, "E1932", {"start": v(-12.87, 10.82) * mm, "end": v(-12.8, 10.65) * mm});
            skLineSegment(sketch, "E1933", {"start": v(-12.8, 10.65) * mm, "end": v(-12.73, 10.5) * mm});
            skLineSegment(sketch, "E1934", {"start": v(-12.73, 10.5) * mm, "end": v(-12.65, 10.32) * mm});
            skLineSegment(sketch, "E1935", {"start": v(-12.65, 10.32) * mm, "end": v(-12.57, 10.16) * mm});
            skLineSegment(sketch, "E1936", {"start": v(-12.57, 10.16) * mm, "end": v(-12.48, 10) * mm});
            skLineSegment(sketch, "E1937", {"start": v(-12.48, 10) * mm, "end": v(-12.4, 9.85) * mm});
            skLineSegment(sketch, "E1938", {"start": v(-12.4, 9.85) * mm, "end": v(-12.3, 9.7) * mm});
            skLineSegment(sketch, "E1939", {"start": v(-12.3, 9.7) * mm, "end": v(-12.19, 9.53) * mm});
            skLineSegment(sketch, "E1940", {"start": v(-12.19, 9.53) * mm, "end": v(-12.07, 9.38) * mm});
            skLineSegment(sketch, "E1941", {"start": v(-12.07, 9.38) * mm, "end": v(-11.96, 9.25) * mm});
            skLineSegment(sketch, "E1942", {"start": v(-11.96, 9.25) * mm, "end": v(-11.84, 9.12) * mm});
            skLineSegment(sketch, "E1943", {"start": v(-11.84, 9.12) * mm, "end": v(-11.7, 9) * mm});
            skLineSegment(sketch, "E1944", {"start": v(-11.7, 9) * mm, "end": v(-11.56, 8.87) * mm});
            skLineSegment(sketch, "E1945", {"start": v(-11.56, 8.87) * mm, "end": v(-11.44, 8.75) * mm});
            skLineSegment(sketch, "E1946", {"start": v(-11.44, 8.75) * mm, "end": v(-11.33, 8.6) * mm});
            skLineSegment(sketch, "E1947", {"start": v(-11.33, 8.6) * mm, "end": v(-11.25, 8.43) * mm});
            skLineSegment(sketch, "E1948", {"start": v(-11.25, 8.43) * mm, "end": v(-11.24, 8.27) * mm});
            skLineSegment(sketch, "E1949", {"start": v(-11.24, 8.27) * mm, "end": v(-11.34, 8.1) * mm});
            skLineSegment(sketch, "E1950", {"start": v(-11.34, 8.1) * mm, "end": v(-11.44, 7.95) * mm});
            skLineSegment(sketch, "E1951", {"start": v(-11.44, 7.95) * mm, "end": v(-11.54, 7.8) * mm});
            skLineSegment(sketch, "E1952", {"start": v(-11.54, 7.8) * mm, "end": v(-11.65, 7.64) * mm});
            skLineSegment(sketch, "E1953", {"start": v(-11.65, 7.64) * mm, "end": v(-11.75, 7.48) * mm});
            skLineSegment(sketch, "E1954", {"start": v(-11.75, 7.48) * mm, "end": v(-11.81, 7.4) * mm});
            skLineSegment(sketch, "E1955", {"start": v(-11.81, 7.4) * mm, "end": v(-11.98, 7.34) * mm});
            skLineSegment(sketch, "E1956", {"start": v(-11.98, 7.34) * mm, "end": v(-12.04, 7.34) * mm});
            skLineSegment(sketch, "E1957", {"start": v(-12.04, 7.34) * mm, "end": v(-12.22, 7.36) * mm});
            skLineSegment(sketch, "E1958", {"start": v(-12.22, 7.36) * mm, "end": v(-12.4, 7.4) * mm});
            skLineSegment(sketch, "E1959", {"start": v(-12.4, 7.4) * mm, "end": v(-12.56, 7.5) * mm});
            skLineSegment(sketch, "E1960", {"start": v(-12.56, 7.5) * mm, "end": v(-12.73, 7.57) * mm});
            skLineSegment(sketch, "E1961", {"start": v(-12.73, 7.57) * mm, "end": v(-12.89, 7.65) * mm});
            skLineSegment(sketch, "E1962", {"start": v(-12.89, 7.65) * mm, "end": v(-13.05, 7.7) * mm});
            skLineSegment(sketch, "E1963", {"start": v(-13.05, 7.7) * mm, "end": v(-13.2, 7.76) * mm});
            skLineSegment(sketch, "E1964", {"start": v(-13.2, 7.76) * mm, "end": v(-13.37, 7.8) * mm});
            skLineSegment(sketch, "E1965", {"start": v(-13.37, 7.8) * mm, "end": v(-13.54, 7.84) * mm});
            skLineSegment(sketch, "E1966", {"start": v(-13.54, 7.84) * mm, "end": v(-13.7, 7.88) * mm});
            skLineSegment(sketch, "E1967", {"start": v(-13.7, 7.88) * mm, "end": v(-13.88, 7.9) * mm});
            skLineSegment(sketch, "E1968", {"start": v(-13.88, 7.9) * mm, "end": v(-14.05, 7.93) * mm});
            skLineSegment(sketch, "E1969", {"start": v(-14.05, 7.93) * mm, "end": v(-14.22, 7.94) * mm});
            skLineSegment(sketch, "E1970", {"start": v(-14.22, 7.94) * mm, "end": v(-14.4, 7.96) * mm});
            skLineSegment(sketch, "E1971", {"start": v(-14.4, 7.96) * mm, "end": v(-14.57, 7.96) * mm});
            skLineSegment(sketch, "E1972", {"start": v(-14.57, 7.96) * mm, "end": v(-14.74, 7.97) * mm});
            skLineSegment(sketch, "E1973", {"start": v(-14.74, 7.97) * mm, "end": v(-14.87, 7.97) * mm});
            skLineSegment(sketch, "E1974", {"start": v(-14.87, 7.97) * mm, "end": v(-15.04, 7.97) * mm});
            skLineSegment(sketch, "E1975", {"start": v(-15.04, 7.97) * mm, "end": v(-15.21, 7.96) * mm});
            skLineSegment(sketch, "E1976", {"start": v(-15.21, 7.96) * mm, "end": v(-15.37, 7.95) * mm});
            skLineSegment(sketch, "E1977", {"start": v(-15.37, 7.95) * mm, "end": v(-15.45, 7.79) * mm});
            skLineSegment(sketch, "E1978", {"start": v(-15.45, 7.79) * mm, "end": v(-15.54, 7.62) * mm});
            skLineSegment(sketch, "E1979", {"start": v(-15.54, 7.62) * mm, "end": v(-15.63, 7.43) * mm});
            skLineSegment(sketch, "E1980", {"start": v(-15.63, 7.43) * mm, "end": v(-15.7, 7.26) * mm});
            skLineSegment(sketch, "E1981", {"start": v(-15.7, 7.26) * mm, "end": v(-15.78, 7.1) * mm});
            skLineSegment(sketch, "E1982", {"start": v(-15.78, 7.1) * mm, "end": v(-15.82, 7) * mm});
            skLineSegment(sketch, "E1983", {"start": v(-15.82, 7) * mm, "end": v(-15.71, 6.86) * mm});
            skLineSegment(sketch, "E1984", {"start": v(-15.71, 6.86) * mm, "end": v(-15.61, 6.72) * mm});
            skLineSegment(sketch, "E1985", {"start": v(-15.61, 6.72) * mm, "end": v(-15.5, 6.57) * mm});
            skLineSegment(sketch, "E1986", {"start": v(-15.5, 6.57) * mm, "end": v(-15.37, 6.42) * mm});
            skLineSegment(sketch, "E1987", {"start": v(-15.37, 6.42) * mm, "end": v(-15.26, 6.3) * mm});
            skLineSegment(sketch, "E1988", {"start": v(-15.26, 6.3) * mm, "end": v(-15.13, 6.15) * mm});
            skLineSegment(sketch, "E1989", {"start": v(-15.13, 6.15) * mm, "end": v(-15, 6.03) * mm});
            skLineSegment(sketch, "E1990", {"start": v(-15, 6.03) * mm, "end": v(-14.88, 5.9) * mm});
            skLineSegment(sketch, "E1991", {"start": v(-14.88, 5.9) * mm, "end": v(-14.75, 5.78) * mm});
            skLineSegment(sketch, "E1992", {"start": v(-14.75, 5.78) * mm, "end": v(-14.6, 5.66) * mm});
            skLineSegment(sketch, "E1993", {"start": v(-14.6, 5.66) * mm, "end": v(-14.46, 5.54) * mm});
            skLineSegment(sketch, "E1994", {"start": v(-14.46, 5.54) * mm, "end": v(-14.3, 5.42) * mm});
            skLineSegment(sketch, "E1995", {"start": v(-14.3, 5.42) * mm, "end": v(-14.16, 5.33) * mm});
            skLineSegment(sketch, "E1996", {"start": v(-14.16, 5.33) * mm, "end": v(-14, 5.24) * mm});
            skLineSegment(sketch, "E1997", {"start": v(-14, 5.24) * mm, "end": v(-13.83, 5.16) * mm});
            skLineSegment(sketch, "E1998", {"start": v(-13.83, 5.16) * mm, "end": v(-13.66, 5.09) * mm});
            skLineSegment(sketch, "E1999", {"start": v(-13.66, 5.09) * mm, "end": v(-13.51, 5) * mm});
            skLineSegment(sketch, "E2000", {"start": v(-13.51, 5) * mm, "end": v(-13.36, 4.9) * mm});
            skLineSegment(sketch, "E2001", {"start": v(-13.36, 4.9) * mm, "end": v(-13.24, 4.76) * mm});
            skLineSegment(sketch, "E2002", {"start": v(-13.24, 4.76) * mm, "end": v(-13.18, 4.6) * mm});
            skLineSegment(sketch, "E2003", {"start": v(-13.18, 4.6) * mm, "end": v(-13.23, 4.42) * mm});
            skLineSegment(sketch, "E2004", {"start": v(-13.23, 4.42) * mm, "end": v(-13.28, 4.24) * mm});
            skLineSegment(sketch, "E2005", {"start": v(-13.28, 4.24) * mm, "end": v(-13.33, 4.06) * mm});
            skLineSegment(sketch, "E2006", {"start": v(-13.33, 4.06) * mm, "end": v(-13.38, 3.88) * mm});
            skLineSegment(sketch, "E2007", {"start": v(-13.38, 3.88) * mm, "end": v(-13.43, 3.7) * mm});
            skLineSegment(sketch, "E2008", {"start": v(-13.43, 3.7) * mm, "end": v(-13.47, 3.6) * mm});
            skLineSegment(sketch, "E2009", {"start": v(-13.47, 3.6) * mm, "end": v(-13.62, 3.5) * mm});
            skLineSegment(sketch, "E2010", {"start": v(-13.62, 3.5) * mm, "end": v(-13.78, 3.45) * mm});
            skLineSegment(sketch, "E2011", {"start": v(-13.78, 3.45) * mm, "end": v(-13.95, 3.44) * mm});
            skLineSegment(sketch, "E2012", {"start": v(-13.95, 3.44) * mm, "end": v(-14.14, 3.47) * mm});
            skLineSegment(sketch, "E2013", {"start": v(-14.14, 3.47) * mm, "end": v(-14.33, 3.5) * mm});
            skLineSegment(sketch, "E2014", {"start": v(-14.33, 3.5) * mm, "end": v(-14.5, 3.52) * mm});
            skLineSegment(sketch, "E2015", {"start": v(-14.5, 3.52) * mm, "end": v(-14.67, 3.54) * mm});
            skLineSegment(sketch, "E2016", {"start": v(-14.67, 3.54) * mm, "end": v(-14.84, 3.54) * mm});
            skLineSegment(sketch, "E2017", {"start": v(-14.84, 3.54) * mm, "end": v(-14.86, 3.54) * mm});
            skLineSegment(sketch, "E2018", {"start": v(-14.86, 3.54) * mm, "end": v(-15.04, 3.54) * mm});
            skLineSegment(sketch, "E2019", {"start": v(-15.04, 3.54) * mm, "end": v(-15.2, 3.53) * mm});
            skLineSegment(sketch, "E2020", {"start": v(-15.2, 3.53) * mm, "end": v(-15.38, 3.5) * mm});
            skLineSegment(sketch, "E2021", {"start": v(-15.38, 3.5) * mm, "end": v(-15.56, 3.49) * mm});
            skLineSegment(sketch, "E2022", {"start": v(-15.56, 3.49) * mm, "end": v(-15.73, 3.46) * mm});
            skLineSegment(sketch, "E2023", {"start": v(-15.73, 3.46) * mm, "end": v(-15.9, 3.42) * mm});
            skLineSegment(sketch, "E2024", {"start": v(-15.9, 3.42) * mm, "end": v(-16.08, 3.38) * mm});
            skLineSegment(sketch, "E2025", {"start": v(-16.08, 3.38) * mm, "end": v(-16.25, 3.34) * mm});
            skLineSegment(sketch, "E2026", {"start": v(-16.25, 3.34) * mm, "end": v(-16.41, 3.3) * mm});
            skLineSegment(sketch, "E2027", {"start": v(-16.41, 3.3) * mm, "end": v(-16.59, 3.24) * mm});
            skLineSegment(sketch, "E2028", {"start": v(-16.59, 3.24) * mm, "end": v(-16.75, 3.2) * mm});
            skLineSegment(sketch, "E2029", {"start": v(-16.75, 3.2) * mm, "end": v(-16.92, 3.13) * mm});
            skLineSegment(sketch, "E2030", {"start": v(-16.92, 3.13) * mm, "end": v(-17.03, 3.09) * mm});
            skLineSegment(sketch, "E2031", {"start": v(-17.03, 3.09) * mm, "end": v(-17.06, 2.9) * mm});
            skLineSegment(sketch, "E2032", {"start": v(-17.06, 2.9) * mm, "end": v(-17.1, 2.72) * mm});
            skLineSegment(sketch, "E2033", {"start": v(-17.1, 2.72) * mm, "end": v(-17.13, 2.52) * mm});
            skLineSegment(sketch, "E2034", {"start": v(-17.13, 2.52) * mm, "end": v(-17.15, 2.33) * mm});
            skLineSegment(sketch, "E2035", {"start": v(-17.15, 2.33) * mm, "end": v(-17.18, 2.14) * mm});
            skLineSegment(sketch, "E2036", {"start": v(-17.18, 2.14) * mm, "end": v(-17.19, 2.05) * mm});
            skLineSegment(sketch, "E2037", {"start": v(-17.19, 2.05) * mm, "end": v(-17.04, 1.94) * mm});
            skLineSegment(sketch, "E2038", {"start": v(-17.04, 1.94) * mm, "end": v(-16.9, 1.84) * mm});
            skLineSegment(sketch, "E2039", {"start": v(-16.9, 1.84) * mm, "end": v(-16.74, 1.73) * mm});
            skLineSegment(sketch, "E2040", {"start": v(-16.74, 1.73) * mm, "end": v(-16.59, 1.63) * mm});
            skLineSegment(sketch, "E2041", {"start": v(-16.59, 1.63) * mm, "end": v(-16.44, 1.53) * mm});
            skLineSegment(sketch, "E2042", {"start": v(-16.44, 1.53) * mm, "end": v(-16.28, 1.44) * mm});
            skLineSegment(sketch, "E2043", {"start": v(-16.28, 1.44) * mm, "end": v(-16.12, 1.35) * mm});
            skLineSegment(sketch, "E2044", {"start": v(-16.12, 1.35) * mm, "end": v(-15.96, 1.27) * mm});
            skLineSegment(sketch, "E2045", {"start": v(-15.96, 1.27) * mm, "end": v(-15.8, 1.2) * mm});
            skLineSegment(sketch, "E2046", {"start": v(-15.8, 1.2) * mm, "end": v(-15.63, 1.12) * mm});
            skLineSegment(sketch, "E2047", {"start": v(-15.63, 1.12) * mm, "end": v(-15.45, 1.05) * mm});
            skLineSegment(sketch, "E2048", {"start": v(-15.45, 1.05) * mm, "end": v(-15.27, 0.98) * mm});
            skLineSegment(sketch, "E2049", {"start": v(-15.27, 0.98) * mm, "end": v(-15.1, 0.94) * mm});
            skLineSegment(sketch, "E2050", {"start": v(-15.1, 0.94) * mm, "end": v(-14.93, 0.9) * mm});
            skLineSegment(sketch, "E2051", {"start": v(-14.93, 0.9) * mm, "end": v(-14.74, 0.88) * mm});
            skLineSegment(sketch, "E2052", {"start": v(-14.74, 0.88) * mm, "end": v(-14.56, 0.85) * mm});
            skLineSegment(sketch, "E2053", {"start": v(-14.56, 0.85) * mm, "end": v(-14.39, 0.82) * mm});
            skLineSegment(sketch, "E2054", {"start": v(-14.39, 0.82) * mm, "end": v(-14.22, 0.76) * mm});
            skLineSegment(sketch, "E2055", {"start": v(-14.22, 0.76) * mm, "end": v(-14.06, 0.66) * mm});
            skLineSegment(sketch, "E2056", {"start": v(-14.06, 0.66) * mm, "end": v(-13.95, 0.54) * mm});
            skLineSegment(sketch, "E2057", {"start": v(-13.95, 0.54) * mm, "end": v(-13.95, 0.35) * mm});
            skLineSegment(sketch, "E2058", {"start": v(-13.95, 0.35) * mm, "end": v(-13.94, 0.16) * mm});
            skLineSegment(sketch, "E2059", {"start": v(-13.94, 0.16) * mm, "end": v(-13.94, -0.03) * mm});
            skLineSegment(sketch, "E2060", {"start": v(-13.94, -0.03) * mm, "end": v(-13.93, -0.22) * mm});
            skLineSegment(sketch, "E2061", {"start": v(-13.93, -0.22) * mm, "end": v(-13.93, -0.4) * mm});
            skLineSegment(sketch, "E2062", {"start": v(-13.93, -0.4) * mm, "end": v(-13.94, -0.5) * mm});
            skLineSegment(sketch, "E2063", {"start": v(-13.94, -0.5) * mm, "end": v(-14.05, -0.65) * mm});
            skLineSegment(sketch, "E2064", {"start": v(-14.05, -0.65) * mm, "end": v(-14.2, -0.75) * mm});
            skLineSegment(sketch, "E2065", {"start": v(-14.2, -0.75) * mm, "end": v(-14.35, -0.8) * mm});
            skLineSegment(sketch, "E2066", {"start": v(-14.35, -0.8) * mm, "end": v(-14.54, -0.84) * mm});
            skLineSegment(sketch, "E2067", {"start": v(-14.54, -0.84) * mm, "end": v(-14.72, -0.87) * mm});
            skLineSegment(sketch, "E2068", {"start": v(-14.72, -0.87) * mm, "end": v(-14.9, -0.9) * mm});
            skLineSegment(sketch, "E2069", {"start": v(-14.9, -0.9) * mm, "end": v(-15.06, -0.93) * mm});
            skLineSegment(sketch, "E2070", {"start": v(-15.06, -0.93) * mm, "end": v(-15.23, -0.97) * mm});
            skLineSegment(sketch, "E2071", {"start": v(-15.23, -0.97) * mm, "end": v(-15.4, -1.03) * mm});
            skLineSegment(sketch, "E2072", {"start": v(-15.4, -1.03) * mm, "end": v(-15.55, -1.09) * mm});
            skLineSegment(sketch, "E2073", {"start": v(-15.55, -1.09) * mm, "end": v(-15.71, -1.15) * mm});
            skLineSegment(sketch, "E2074", {"start": v(-15.71, -1.15) * mm, "end": v(-15.87, -1.22) * mm});
            skLineSegment(sketch, "E2075", {"start": v(-15.87, -1.22) * mm, "end": v(-16.02, -1.3) * mm});
            skLineSegment(sketch, "E2076", {"start": v(-16.02, -1.3) * mm, "end": v(-16.18, -1.38) * mm});
            skLineSegment(sketch, "E2077", {"start": v(-16.18, -1.38) * mm, "end": v(-16.33, -1.47) * mm});
            skLineSegment(sketch, "E2078", {"start": v(-16.33, -1.47) * mm, "end": v(-16.48, -1.56) * mm});
            skLineSegment(sketch, "E2079", {"start": v(-16.48, -1.56) * mm, "end": v(-16.64, -1.66) * mm});
            skLineSegment(sketch, "E2080", {"start": v(-16.64, -1.66) * mm, "end": v(-16.78, -1.76) * mm});
            skLineSegment(sketch, "E2081", {"start": v(-16.78, -1.76) * mm, "end": v(-16.92, -1.85) * mm});
            skLineSegment(sketch, "E2082", {"start": v(-16.92, -1.85) * mm, "end": v(-17.07, -1.96) * mm});
            skLineSegment(sketch, "E2083", {"start": v(-17.07, -1.96) * mm, "end": v(-17.19, -2.05) * mm});
            skLineSegment(sketch, "E2084", {"start": v(-17.19, -2.05) * mm, "end": v(-17.17, -2.24) * mm});
            skLineSegment(sketch, "E2085", {"start": v(-17.17, -2.24) * mm, "end": v(-17.14, -2.42) * mm});
            skLineSegment(sketch, "E2086", {"start": v(-17.14, -2.42) * mm, "end": v(-17.11, -2.63) * mm});
            skLineSegment(sketch, "E2087", {"start": v(-17.11, -2.63) * mm, "end": v(-17.08, -2.81) * mm});
            skLineSegment(sketch, "E2088", {"start": v(-17.08, -2.81) * mm, "end": v(-17.05, -3) * mm});
            skLineSegment(sketch, "E2089", {"start": v(-17.05, -3) * mm, "end": v(-17.03, -3.09) * mm});
            skLineSegment(sketch, "E2090", {"start": v(-17.03, -3.09) * mm, "end": v(-16.86, -3.15) * mm});
            skLineSegment(sketch, "E2091", {"start": v(-16.86, -3.15) * mm, "end": v(-16.7, -3.2) * mm});
            skLineSegment(sketch, "E2092", {"start": v(-16.7, -3.2) * mm, "end": v(-16.5, -3.27) * mm});
            skLineSegment(sketch, "E2093", {"start": v(-16.5, -3.27) * mm, "end": v(-16.33, -3.32) * mm});
            skLineSegment(sketch, "E2094", {"start": v(-16.33, -3.32) * mm, "end": v(-16.16, -3.36) * mm});
            skLineSegment(sketch, "E2095", {"start": v(-16.16, -3.36) * mm, "end": v(-15.98, -3.4) * mm});
            skLineSegment(sketch, "E2096", {"start": v(-15.98, -3.4) * mm, "end": v(-15.8, -3.44) * mm});
            skLineSegment(sketch, "E2097", {"start": v(-15.8, -3.44) * mm, "end": v(-15.62, -3.47) * mm});
            skLineSegment(sketch, "E2098", {"start": v(-15.62, -3.47) * mm, "end": v(-15.46, -3.5) * mm});
            skLineSegment(sketch, "E2099", {"start": v(-15.46, -3.5) * mm, "end": v(-15.27, -3.52) * mm});
            skLineSegment(sketch, "E2100", {"start": v(-15.27, -3.52) * mm, "end": v(-15.07, -3.54) * mm});
            skLineSegment(sketch, "E2101", {"start": v(-15.07, -3.54) * mm, "end": v(-14.88, -3.54) * mm});
            skLineSegment(sketch, "E2102", {"start": v(-14.88, -3.54) * mm, "end": v(-14.7, -3.54) * mm});
            skLineSegment(sketch, "E2103", {"start": v(-14.7, -3.54) * mm, "end": v(-14.53, -3.52) * mm});
            skLineSegment(sketch, "E2104", {"start": v(-14.53, -3.52) * mm, "end": v(-14.35, -3.5) * mm});
            skLineSegment(sketch, "E2105", {"start": v(-14.35, -3.5) * mm, "end": v(-14.16, -3.46) * mm});
            skLineSegment(sketch, "E2106", {"start": v(-14.16, -3.46) * mm, "end": v(-14, -3.44) * mm});
            skLineSegment(sketch, "E2107", {"start": v(-14, -3.44) * mm, "end": v(-13.81, -3.45) * mm});
            skLineSegment(sketch, "E2108", {"start": v(-13.81, -3.45) * mm, "end": v(-13.63, -3.5) * mm});
            skLineSegment(sketch, "E2109", {"start": v(-13.63, -3.5) * mm, "end": v(-13.5, -3.58) * mm});
            skLineSegment(sketch, "E2110", {"start": v(-13.5, -3.58) * mm, "end": v(-13.43, -3.76) * mm});
            skLineSegment(sketch, "E2111", {"start": v(-13.43, -3.76) * mm, "end": v(-13.37, -3.94) * mm});
            skLineSegment(sketch, "E2112", {"start": v(-13.37, -3.94) * mm, "end": v(-13.31, -4.12) * mm});
            skLineSegment(sketch, "E2113", {"start": v(-13.31, -4.12) * mm, "end": v(-13.25, -4.3) * mm});
            skLineSegment(sketch, "E2114", {"start": v(-13.25, -4.3) * mm, "end": v(-13.2, -4.47) * mm});
            skLineSegment(sketch, "E2115", {"start": v(-13.2, -4.47) * mm, "end": v(-13.17, -4.57) * mm});
            skLineSegment(sketch, "E2116", {"start": v(-13.17, -4.57) * mm, "end": v(-13.23, -4.75) * mm});
            skLineSegment(sketch, "E2117", {"start": v(-13.23, -4.75) * mm, "end": v(-13.34, -4.88) * mm});
            skLineSegment(sketch, "E2118", {"start": v(-13.34, -4.88) * mm, "end": v(-13.48, -4.98) * mm});
            skLineSegment(sketch, "E2119", {"start": v(-13.48, -4.98) * mm, "end": v(-13.65, -5.07) * mm});
            skLineSegment(sketch, "E2120", {"start": v(-13.65, -5.07) * mm, "end": v(-13.82, -5.15) * mm});
            skLineSegment(sketch, "E2121", {"start": v(-13.82, -5.15) * mm, "end": v(-13.97, -5.22) * mm});
            skLineSegment(sketch, "E2122", {"start": v(-13.97, -5.22) * mm, "end": v(-14.12, -5.3) * mm});
            skLineSegment(sketch, "E2123", {"start": v(-14.12, -5.3) * mm, "end": v(-14.27, -5.4) * mm});
            skLineSegment(sketch, "E2124", {"start": v(-14.27, -5.4) * mm, "end": v(-14.4, -5.5) * mm});
            skLineSegment(sketch, "E2125", {"start": v(-14.4, -5.5) * mm, "end": v(-14.54, -5.6) * mm});
            skLineSegment(sketch, "E2126", {"start": v(-14.54, -5.6) * mm, "end": v(-14.68, -5.71) * mm});
            skLineSegment(sketch, "E2127", {"start": v(-14.68, -5.71) * mm, "end": v(-14.8, -5.83) * mm});
            skLineSegment(sketch, "E2128", {"start": v(-14.8, -5.83) * mm, "end": v(-14.93, -5.95) * mm});
            skLineSegment(sketch, "E2129", {"start": v(-14.93, -5.95) * mm, "end": v(-15.06, -6.07) * mm});
            skLineSegment(sketch, "E2130", {"start": v(-15.06, -6.07) * mm, "end": v(-15.18, -6.2) * mm});
            skLineSegment(sketch, "E2131", {"start": v(-15.18, -6.2) * mm, "end": v(-15.3, -6.33) * mm});
            skLineSegment(sketch, "E2132", {"start": v(-15.3, -6.33) * mm, "end": v(-15.41, -6.47) * mm});
            skLineSegment(sketch, "E2133", {"start": v(-15.41, -6.47) * mm, "end": v(-15.52, -6.6) * mm});
            skLineSegment(sketch, "E2134", {"start": v(-15.52, -6.6) * mm, "end": v(-15.63, -6.74) * mm});
            skLineSegment(sketch, "E2135", {"start": v(-15.63, -6.74) * mm, "end": v(-15.73, -6.88) * mm});
            skLineSegment(sketch, "E2136", {"start": v(-15.73, -6.88) * mm, "end": v(-15.82, -7) * mm});
            skLineSegment(sketch, "E2137", {"start": v(-15.82, -7) * mm, "end": v(-15.75, -7.18) * mm});
            skLineSegment(sketch, "E2138", {"start": v(-15.75, -7.18) * mm, "end": v(-15.67, -7.35) * mm});
            skLineSegment(sketch, "E2139", {"start": v(-15.67, -7.35) * mm, "end": v(-15.58, -7.53) * mm});
            skLineSegment(sketch, "E2140", {"start": v(-15.58, -7.53) * mm, "end": v(-15.5, -7.7) * mm});
            skLineSegment(sketch, "E2141", {"start": v(-15.5, -7.7) * mm, "end": v(-15.41, -7.87) * mm});
            skLineSegment(sketch, "E2142", {"start": v(-15.41, -7.87) * mm, "end": v(-15.37, -7.95) * mm});
            skLineSegment(sketch, "E2143", {"start": v(-15.37, -7.95) * mm, "end": v(-15.18, -7.96) * mm});
            skLineSegment(sketch, "E2144", {"start": v(-15.18, -7.96) * mm, "end": v(-15, -7.97) * mm});
            skLineSegment(sketch, "E2145", {"start": v(-15, -7.97) * mm, "end": v(-14.82, -7.97) * mm});
            skLineSegment(sketch, "E2146", {"start": v(-14.82, -7.97) * mm, "end": v(-14.63, -7.97) * mm});
            skLineSegment(sketch, "E2147", {"start": v(-14.63, -7.97) * mm, "end": v(-14.46, -7.96) * mm});
            skLineSegment(sketch, "E2148", {"start": v(-14.46, -7.96) * mm, "end": v(-14.27, -7.95) * mm});
            skLineSegment(sketch, "E2149", {"start": v(-14.27, -7.95) * mm, "end": v(-14.1, -7.93) * mm});
            skLineSegment(sketch, "E2150", {"start": v(-14.1, -7.93) * mm, "end": v(-13.9, -7.9) * mm});
            skLineSegment(sketch, "E2151", {"start": v(-13.9, -7.9) * mm, "end": v(-13.74, -7.88) * mm});
            skLineSegment(sketch, "E2152", {"start": v(-13.74, -7.88) * mm, "end": v(-13.55, -7.85) * mm});
            skLineSegment(sketch, "E2153", {"start": v(-13.55, -7.85) * mm, "end": v(-13.36, -7.8) * mm});
            skLineSegment(sketch, "E2154", {"start": v(-13.36, -7.8) * mm, "end": v(-13.18, -7.75) * mm});
            skLineSegment(sketch, "E2155", {"start": v(-13.18, -7.75) * mm, "end": v(-13.02, -7.7) * mm});
            skLineSegment(sketch, "E2156", {"start": v(-13.02, -7.7) * mm, "end": v(-12.85, -7.63) * mm});
            skLineSegment(sketch, "E2157", {"start": v(-12.85, -7.63) * mm, "end": v(-12.68, -7.55) * mm});
            skLineSegment(sketch, "E2158", {"start": v(-12.68, -7.55) * mm, "end": v(-12.52, -7.46) * mm});
            skLineSegment(sketch, "E2159", {"start": v(-12.52, -7.46) * mm, "end": v(-12.36, -7.4) * mm});
            skLineSegment(sketch, "E2160", {"start": v(-12.36, -7.4) * mm, "end": v(-12.18, -7.35) * mm});
            skLineSegment(sketch, "E2161", {"start": v(-12.18, -7.35) * mm, "end": v(-12, -7.34) * mm});
            skLineSegment(sketch, "E2162", {"start": v(-12, -7.34) * mm, "end": v(-11.84, -7.38) * mm});
            skLineSegment(sketch, "E2163", {"start": v(-11.84, -7.38) * mm, "end": v(-11.73, -7.53) * mm});
            skLineSegment(sketch, "E2164", {"start": v(-11.73, -7.53) * mm, "end": v(-11.62, -7.69) * mm});
            skLineSegment(sketch, "E2165", {"start": v(-11.62, -7.69) * mm, "end": v(-11.51, -7.84) * mm});
            skLineSegment(sketch, "E2166", {"start": v(-11.51, -7.84) * mm, "end": v(-11.4, -8) * mm});
            skLineSegment(sketch, "E2167", {"start": v(-11.4, -8) * mm, "end": v(-11.3, -8.15) * mm});
            skLineSegment(sketch, "E2168", {"start": v(-11.3, -8.15) * mm, "end": v(-11.24, -8.24) * mm});
            skLineSegment(sketch, "E2169", {"start": v(-11.24, -8.24) * mm, "end": v(-11.25, -8.42) * mm});
            skLineSegment(sketch, "E2170", {"start": v(-11.25, -8.42) * mm, "end": v(-11.32, -8.58) * mm});
            skLineSegment(sketch, "E2171", {"start": v(-11.32, -8.58) * mm, "end": v(-11.41, -8.72) * mm});
            skLineSegment(sketch, "E2172", {"start": v(-11.41, -8.72) * mm, "end": v(-11.55, -8.85) * mm});
            skLineSegment(sketch, "E2173", {"start": v(-11.55, -8.85) * mm, "end": v(-11.69, -8.98) * mm});
            skLineSegment(sketch, "E2174", {"start": v(-11.69, -8.98) * mm, "end": v(-11.81, -9.1) * mm});
            skLineSegment(sketch, "E2175", {"start": v(-11.81, -9.1) * mm, "end": v(-11.93, -9.22) * mm});
            skLineSegment(sketch, "E2176", {"start": v(-11.93, -9.22) * mm, "end": v(-12.05, -9.35) * mm});
            skLineSegment(sketch, "E2177", {"start": v(-12.05, -9.35) * mm, "end": v(-12.15, -9.48) * mm});
            skLineSegment(sketch, "E2178", {"start": v(-12.15, -9.48) * mm, "end": v(-12.25, -9.62) * mm});
            skLineSegment(sketch, "E2179", {"start": v(-12.25, -9.62) * mm, "end": v(-12.34, -9.77) * mm});
            skLineSegment(sketch, "E2180", {"start": v(-12.34, -9.77) * mm, "end": v(-12.43, -9.92) * mm});
            skLineSegment(sketch, "E2181", {"start": v(-12.43, -9.92) * mm, "end": v(-12.52, -10.07) * mm});
            skLineSegment(sketch, "E2182", {"start": v(-12.52, -10.07) * mm, "end": v(-12.6, -10.22) * mm});
            skLineSegment(sketch, "E2183", {"start": v(-12.6, -10.22) * mm, "end": v(-12.68, -10.38) * mm});
            skLineSegment(sketch, "E2184", {"start": v(-12.68, -10.38) * mm, "end": v(-12.75, -10.54) * mm});
            skLineSegment(sketch, "E2185", {"start": v(-12.75, -10.54) * mm, "end": v(-12.82, -10.7) * mm});
            skLineSegment(sketch, "E2186", {"start": v(-12.82, -10.7) * mm, "end": v(-12.89, -10.87) * mm});
            skLineSegment(sketch, "E2187", {"start": v(-12.89, -10.87) * mm, "end": v(-12.95, -11.03) * mm});
            skLineSegment(sketch, "E2188", {"start": v(-12.95, -11.03) * mm, "end": v(-13, -11.2) * mm});
            skLineSegment(sketch, "E2189", {"start": v(-13, -11.2) * mm, "end": v(-13.06, -11.34) * mm});
            skLineSegment(sketch, "E2190", {"start": v(-13.06, -11.34) * mm, "end": v(-12.93, -11.48) * mm});
            skLineSegment(sketch, "E2191", {"start": v(-12.93, -11.48) * mm, "end": v(-12.8, -11.62) * mm});
            skLineSegment(sketch, "E2192", {"start": v(-12.8, -11.62) * mm, "end": v(-12.67, -11.77) * mm});
            skLineSegment(sketch, "E2193", {"start": v(-12.67, -11.77) * mm, "end": v(-12.54, -11.9) * mm});
            skLineSegment(sketch, "E2194", {"start": v(-12.54, -11.9) * mm, "end": v(-12.4, -12.05) * mm});
            skLineSegment(sketch, "E2195", {"start": v(-12.4, -12.05) * mm, "end": v(-12.34, -12.11) * mm});
            skLineSegment(sketch, "E2196", {"start": v(-12.34, -12.11) * mm, "end": v(-12.16, -12.07) * mm});
            skLineSegment(sketch, "E2197", {"start": v(-12.16, -12.07) * mm, "end": v(-12, -12.02) * mm});
            skLineSegment(sketch, "E2198", {"start": v(-12, -12.02) * mm, "end": v(-11.81, -11.96) * mm});
            skLineSegment(sketch, "E2199", {"start": v(-11.81, -11.96) * mm, "end": v(-11.64, -11.9) * mm});
            skLineSegment(sketch, "E2200", {"start": v(-11.64, -11.9) * mm, "end": v(-11.47, -11.85) * mm});
            skLineSegment(sketch, "E2201", {"start": v(-11.47, -11.85) * mm, "end": v(-11.3, -11.78) * mm});
            skLineSegment(sketch, "E2202", {"start": v(-11.3, -11.78) * mm, "end": v(-11.13, -11.71) * mm});
            skLineSegment(sketch, "E2203", {"start": v(-11.13, -11.71) * mm, "end": v(-10.96, -11.64) * mm});
            skLineSegment(sketch, "E2204", {"start": v(-10.96, -11.64) * mm, "end": v(-10.8, -11.56) * mm});
            skLineSegment(sketch, "E2205", {"start": v(-10.8, -11.56) * mm, "end": v(-10.64, -11.48) * mm});
            skLineSegment(sketch, "E2206", {"start": v(-10.64, -11.48) * mm, "end": v(-10.47, -11.38) * mm});
            skLineSegment(sketch, "E2207", {"start": v(-10.47, -11.38) * mm, "end": v(-10.31, -11.28) * mm});
            skLineSegment(sketch, "E2208", {"start": v(-10.31, -11.28) * mm, "end": v(-10.17, -11.17) * mm});
            skLineSegment(sketch, "E2209", {"start": v(-10.17, -11.17) * mm, "end": v(-10.03, -11.06) * mm});
            skLineSegment(sketch, "E2210", {"start": v(-10.03, -11.06) * mm, "end": v(-9.9, -10.93) * mm});
            skLineSegment(sketch, "E2211", {"start": v(-9.9, -10.93) * mm, "end": v(-9.77, -10.8) * mm});
            skLineSegment(sketch, "E2212", {"start": v(-9.77, -10.8) * mm, "end": v(-9.63, -10.7) * mm});
            skLineSegment(sketch, "E2213", {"start": v(-9.63, -10.7) * mm, "end": v(-9.48, -10.6) * mm});
            skLineSegment(sketch, "E2214", {"start": v(-9.48, -10.6) * mm, "end": v(-9.3, -10.53) * mm});
            skLineSegment(sketch, "E2215", {"start": v(-9.3, -10.53) * mm, "end": v(-9.14, -10.53) * mm});
            skLineSegment(sketch, "E2216", {"start": v(-9.14, -10.53) * mm, "end": v(-9, -10.64) * mm});
            skLineSegment(sketch, "E2217", {"start": v(-9, -10.64) * mm, "end": v(-8.84, -10.75) * mm});
            skLineSegment(sketch, "E2218", {"start": v(-8.84, -10.75) * mm, "end": v(-8.7, -10.87) * mm});
            skLineSegment(sketch, "E2219", {"start": v(-8.7, -10.87) * mm, "end": v(-8.54, -10.98) * mm});
            skLineSegment(sketch, "E2220", {"start": v(-8.54, -10.98) * mm, "end": v(-8.4, -11.1) * mm});
            skLineSegment(sketch, "E2221", {"start": v(-8.4, -11.1) * mm, "end": v(-8.32, -11.17) * mm});
            skLineSegment(sketch, "E2222", {"start": v(-8.32, -11.17) * mm, "end": v(-8.27, -11.34) * mm});
            skLineSegment(sketch, "E2223", {"start": v(-8.27, -11.34) * mm, "end": v(-8.29, -11.51) * mm});
            skLineSegment(sketch, "E2224", {"start": v(-8.29, -11.51) * mm, "end": v(-8.34, -11.68) * mm});
            skLineSegment(sketch, "E2225", {"start": v(-8.34, -11.68) * mm, "end": v(-8.43, -11.84) * mm});
            skLineSegment(sketch, "E2226", {"start": v(-8.43, -11.84) * mm, "end": v(-8.52, -12) * mm});
            skLineSegment(sketch, "E2227", {"start": v(-8.52, -12) * mm, "end": v(-8.6, -12.15) * mm});
            skLineSegment(sketch, "E2228", {"start": v(-8.6, -12.15) * mm, "end": v(-8.69, -12.3) * mm});
            skLineSegment(sketch, "E2229", {"start": v(-8.69, -12.3) * mm, "end": v(-8.76, -12.47) * mm});
            skLineSegment(sketch, "E2230", {"start": v(-8.76, -12.47) * mm, "end": v(-8.82, -12.63) * mm});
            skLineSegment(sketch, "E2231", {"start": v(-8.82, -12.63) * mm, "end": v(-8.87, -12.79) * mm});
            skLineSegment(sketch, "E2232", {"start": v(-8.87, -12.79) * mm, "end": v(-8.92, -12.95) * mm});
            skLineSegment(sketch, "E2233", {"start": v(-8.92, -12.95) * mm, "end": v(-8.96, -13.12) * mm});
            skLineSegment(sketch, "E2234", {"start": v(-8.96, -13.12) * mm, "end": v(-9, -13.3) * mm});
            skLineSegment(sketch, "E2235", {"start": v(-9, -13.3) * mm, "end": v(-9.03, -13.47) * mm});
            skLineSegment(sketch, "E2236", {"start": v(-9.03, -13.47) * mm, "end": v(-9.06, -13.64) * mm});
            skLineSegment(sketch, "E2237", {"start": v(-9.06, -13.64) * mm, "end": v(-9.08, -13.81) * mm});
            skLineSegment(sketch, "E2238", {"start": v(-9.08, -13.81) * mm, "end": v(-9.1, -14) * mm});
            skLineSegment(sketch, "E2239", {"start": v(-9.1, -14) * mm, "end": v(-9.12, -14.17) * mm});
            skLineSegment(sketch, "E2240", {"start": v(-9.12, -14.17) * mm, "end": v(-9.13, -14.34) * mm});
            skLineSegment(sketch, "E2241", {"start": v(-9.13, -14.34) * mm, "end": v(-9.13, -14.52) * mm});
            skLineSegment(sketch, "E2242", {"start": v(-9.13, -14.52) * mm, "end": v(-9.14, -14.67) * mm});
            skLineSegment(sketch, "E2243", {"start": v(-9.14, -14.67) * mm, "end": v(-8.98, -14.77) * mm});
            skLineSegment(sketch, "E2244", {"start": v(-8.98, -14.77) * mm, "end": v(-8.81, -14.86) * mm});
            skLineSegment(sketch, "E2245", {"start": v(-8.81, -14.86) * mm, "end": v(-8.64, -14.97) * mm});
            skLineSegment(sketch, "E2246", {"start": v(-8.64, -14.97) * mm, "end": v(-8.47, -15.06) * mm});
            skLineSegment(sketch, "E2247", {"start": v(-8.47, -15.06) * mm, "end": v(-8.3, -15.15) * mm});
            skLineSegment(sketch, "E2248", {"start": v(-8.3, -15.15) * mm, "end": v(-8.23, -15.2) * mm});
            skLineSegment(sketch, "E2249", {"start": v(-8.23, -15.2) * mm, "end": v(-8.07, -15.1) * mm});
            skLineSegment(sketch, "E2250", {"start": v(-8.07, -15.1) * mm, "end": v(-7.92, -15) * mm});
            skLineSegment(sketch, "E2251", {"start": v(-7.92, -15) * mm, "end": v(-7.76, -14.9) * mm});
            skLineSegment(sketch, "E2252", {"start": v(-7.76, -14.9) * mm, "end": v(-7.61, -14.8) * mm});
            skLineSegment(sketch, "E2253", {"start": v(-7.61, -14.8) * mm, "end": v(-7.47, -14.68) * mm});
            skLineSegment(sketch, "E2254", {"start": v(-7.47, -14.68) * mm, "end": v(-7.32, -14.57) * mm});
            skLineSegment(sketch, "E2255", {"start": v(-7.32, -14.57) * mm, "end": v(-7.19, -14.46) * mm});
            skLineSegment(sketch, "E2256", {"start": v(-7.19, -14.46) * mm, "end": v(-7.05, -14.33) * mm});
            skLineSegment(sketch, "E2257", {"start": v(-7.05, -14.33) * mm, "end": v(-6.92, -14.22) * mm});
            skLineSegment(sketch, "E2258", {"start": v(-6.92, -14.22) * mm, "end": v(-6.79, -14.08) * mm});
            skLineSegment(sketch, "E2259", {"start": v(-6.79, -14.08) * mm, "end": v(-6.66, -13.94) * mm});
            skLineSegment(sketch, "E2260", {"start": v(-6.66, -13.94) * mm, "end": v(-6.53, -13.8) * mm});
            skLineSegment(sketch, "E2261", {"start": v(-6.53, -13.8) * mm, "end": v(-6.43, -13.66) * mm});
            skLineSegment(sketch, "E2262", {"start": v(-6.43, -13.66) * mm, "end": v(-6.33, -13.51) * mm});
            skLineSegment(sketch, "E2263", {"start": v(-6.33, -13.51) * mm, "end": v(-6.24, -13.35) * mm});
            skLineSegment(sketch, "E2264", {"start": v(-6.24, -13.35) * mm, "end": v(-6.15, -13.18) * mm});
            skLineSegment(sketch, "E2265", {"start": v(-6.15, -13.18) * mm, "end": v(-6.06, -13.04) * mm});
            skLineSegment(sketch, "E2266", {"start": v(-6.06, -13.04) * mm, "end": v(-5.94, -12.9) * mm});
            skLineSegment(sketch, "E2267", {"start": v(-5.94, -12.9) * mm, "end": v(-5.8, -12.79) * mm});
            skLineSegment(sketch, "E2268", {"start": v(-5.8, -12.79) * mm, "end": v(-5.63, -12.73) * mm});
            skLineSegment(sketch, "E2269", {"start": v(-5.63, -12.73) * mm, "end": v(-5.46, -12.8) * mm});
            skLineSegment(sketch, "E2270", {"start": v(-5.46, -12.8) * mm, "end": v(-5.28, -12.86) * mm});
            skLineSegment(sketch, "E2271", {"start": v(-5.28, -12.86) * mm, "end": v(-5.1, -12.93) * mm});
            skLineSegment(sketch, "E2272", {"start": v(-5.1, -12.93) * mm, "end": v(-4.93, -13) * mm});
            skLineSegment(sketch, "E2273", {"start": v(-4.93, -13) * mm, "end": v(-4.75, -13.06) * mm});
            skLineSegment(sketch, "E2274", {"start": v(-4.75, -13.06) * mm, "end": v(-4.66, -13.1) * mm});
            skLineSegment(sketch, "E2275", {"start": v(-4.66, -13.1) * mm, "end": v(-4.56, -13.26) * mm});
            skLineSegment(sketch, "E2276", {"start": v(-4.56, -13.26) * mm, "end": v(-4.53, -13.43) * mm});
            skLineSegment(sketch, "E2277", {"start": v(-4.53, -13.43) * mm, "end": v(-4.53, -13.6) * mm});
            skLineSegment(sketch, "E2278", {"start": v(-4.53, -13.6) * mm, "end": v(-4.57, -13.78) * mm});
            skLineSegment(sketch, "E2279", {"start": v(-4.57, -13.78) * mm, "end": v(-4.6, -13.96) * mm});
            skLineSegment(sketch, "E2280", {"start": v(-4.6, -13.96) * mm, "end": v(-4.65, -14.13) * mm});
            skLineSegment(sketch, "E2281", {"start": v(-4.65, -14.13) * mm, "end": v(-4.68, -14.3) * mm});
            skLineSegment(sketch, "E2282", {"start": v(-4.68, -14.3) * mm, "end": v(-4.7, -14.48) * mm});
            skLineSegment(sketch, "E2283", {"start": v(-4.7, -14.48) * mm, "end": v(-4.7, -14.65) * mm});
            skLineSegment(sketch, "E2284", {"start": v(-4.7, -14.65) * mm, "end": v(-4.7, -14.82) * mm});
            skLineSegment(sketch, "E2285", {"start": v(-4.7, -14.82) * mm, "end": v(-4.7, -14.99) * mm});
            skLineSegment(sketch, "E2286", {"start": v(-4.7, -14.99) * mm, "end": v(-4.7, -15.16) * mm});
            skLineSegment(sketch, "E2287", {"start": v(-4.7, -15.16) * mm, "end": v(-4.68, -15.34) * mm});
            skLineSegment(sketch, "E2288", {"start": v(-4.68, -15.34) * mm, "end": v(-4.66, -15.51) * mm});
            skLineSegment(sketch, "E2289", {"start": v(-4.66, -15.51) * mm, "end": v(-4.64, -15.69) * mm});
            skLineSegment(sketch, "E2290", {"start": v(-4.64, -15.69) * mm, "end": v(-4.6, -15.86) * mm});
            skLineSegment(sketch, "E2291", {"start": v(-4.6, -15.86) * mm, "end": v(-4.57, -16.04) * mm});
            skLineSegment(sketch, "E2292", {"start": v(-4.57, -16.04) * mm, "end": v(-4.54, -16.2) * mm});
            skLineSegment(sketch, "E2293", {"start": v(-4.54, -16.2) * mm, "end": v(-4.5, -16.37) * mm});
            skLineSegment(sketch, "E2294", {"start": v(-4.5, -16.37) * mm, "end": v(-4.45, -16.55) * mm});
            skLineSegment(sketch, "E2295", {"start": v(-4.45, -16.55) * mm, "end": v(-4.41, -16.7) * mm});
            skLineSegment(sketch, "E2296", {"start": v(-4.41, -16.7) * mm, "end": v(-4.23, -16.74) * mm});
            skLineSegment(sketch, "E2297", {"start": v(-4.23, -16.74) * mm, "end": v(-4.04, -16.78) * mm});
            skLineSegment(sketch, "E2298", {"start": v(-4.04, -16.78) * mm, "end": v(-3.85, -16.83) * mm});
            skLineSegment(sketch, "E2299", {"start": v(-3.85, -16.83) * mm, "end": v(-3.66, -16.87) * mm});
            skLineSegment(sketch, "E2300", {"start": v(-3.66, -16.87) * mm, "end": v(-3.48, -16.9) * mm});
            skLineSegment(sketch, "E2301", {"start": v(-3.48, -16.9) * mm, "end": v(-3.39, -16.93) * mm});
            skLineSegment(sketch, "E2302", {"start": v(-3.39, -16.93) * mm, "end": v(-3.26, -16.79) * mm});
            skLineSegment(sketch, "E2303", {"start": v(-3.26, -16.79) * mm, "end": v(-3.15, -16.66) * mm});
            skLineSegment(sketch, "E2304", {"start": v(-3.15, -16.66) * mm, "end": v(-3.03, -16.5) * mm});
            skLineSegment(sketch, "E2305", {"start": v(-3.03, -16.5) * mm, "end": v(-2.92, -16.36) * mm});
            skLineSegment(sketch, "E2306", {"start": v(-2.92, -16.36) * mm, "end": v(-2.81, -16.22) * mm});
            skLineSegment(sketch, "E2307", {"start": v(-2.81, -16.22) * mm, "end": v(-2.7, -16.06) * mm});
            skLineSegment(sketch, "E2308", {"start": v(-2.7, -16.06) * mm, "end": v(-2.6, -15.91) * mm});
            skLineSegment(sketch, "E2309", {"start": v(-2.6, -15.91) * mm, "end": v(-2.51, -15.76) * mm});
            skLineSegment(sketch, "E2310", {"start": v(-2.51, -15.76) * mm, "end": v(-2.43, -15.6) * mm});
            skLineSegment(sketch, "E2311", {"start": v(-2.43, -15.6) * mm, "end": v(-2.34, -15.44) * mm});
            skLineSegment(sketch, "E2312", {"start": v(-2.34, -15.44) * mm, "end": v(-2.25, -15.27) * mm});
            skLineSegment(sketch, "E2313", {"start": v(-2.25, -15.27) * mm, "end": v(-2.18, -15.1) * mm});
            skLineSegment(sketch, "E2314", {"start": v(-2.18, -15.1) * mm, "end": v(-2.12, -14.93) * mm});
            skLineSegment(sketch, "E2315", {"start": v(-2.12, -14.93) * mm, "end": v(-2.07, -14.76) * mm});
            skLineSegment(sketch, "E2316", {"start": v(-2.07, -14.76) * mm, "end": v(-2.03, -14.58) * mm});
            skLineSegment(sketch, "E2317", {"start": v(-2.03, -14.58) * mm, "end": v(-2, -14.4) * mm});
            skLineSegment(sketch, "E2318", {"start": v(-2, -14.4) * mm, "end": v(-1.95, -14.23) * mm});
            skLineSegment(sketch, "E2319", {"start": v(-1.95, -14.23) * mm, "end": v(-1.87, -14.06) * mm});
            skLineSegment(sketch, "E2320", {"start": v(-1.87, -14.06) * mm, "end": v(-1.77, -13.9) * mm});
            skLineSegment(sketch, "E2321", {"start": v(-1.77, -13.9) * mm, "end": v(-1.63, -13.81) * mm});
            skLineSegment(sketch, "E2322", {"start": v(-1.63, -13.81) * mm, "end": v(-1.45, -13.82) * mm});
            skLineSegment(sketch, "E2323", {"start": v(-1.45, -13.82) * mm, "end": v(-1.26, -13.83) * mm});
            skLineSegment(sketch, "E2324", {"start": v(-1.26, -13.83) * mm, "end": v(-1.07, -13.84) * mm});
            skLineSegment(sketch, "E2325", {"start": v(-1.07, -13.84) * mm, "end": v(-0.88, -13.85) * mm});
            skLineSegment(sketch, "E2326", {"start": v(-0.88, -13.85) * mm, "end": v(-0.7, -13.86) * mm});
            skLineSegment(sketch, "E2327", {"start": v(-0.7, -13.86) * mm, "end": v(-0.6, -13.88) * mm});
            skLineSegment(sketch, "E2328", {"start": v(-0.6, -13.88) * mm, "end": v(-0.45, -14) * mm});
            skLineSegment(sketch, "E2329", {"start": v(-0.45, -14) * mm, "end": v(-0.37, -14.15) * mm});
            skLineSegment(sketch, "E2330", {"start": v(-0.37, -14.15) * mm, "end": v(-0.32, -14.31) * mm});
            skLineSegment(sketch, "E2331", {"start": v(-0.32, -14.31) * mm, "end": v(-0.3, -14.5) * mm});
            skLineSegment(sketch, "E2332", {"start": v(-0.3, -14.5) * mm, "end": v(-0.3, -14.68) * mm});
            skLineSegment(sketch, "E2333", {"start": v(-0.3, -14.68) * mm, "end": v(-0.28, -14.85) * mm});
            skLineSegment(sketch, "E2334", {"start": v(-0.28, -14.85) * mm, "end": v(-0.26, -15.03) * mm});
            skLineSegment(sketch, "E2335", {"start": v(-0.26, -15.03) * mm, "end": v(-0.22, -15.2) * mm});
            skLineSegment(sketch, "E2336", {"start": v(-0.22, -15.2) * mm, "end": v(-0.18, -15.37) * mm});
            skLineSegment(sketch, "E2337", {"start": v(-0.18, -15.37) * mm, "end": v(-0.14, -15.53) * mm});
            skLineSegment(sketch, "E2338", {"start": v(-0.14, -15.53) * mm, "end": v(-0.08, -15.7) * mm});
            skLineSegment(sketch, "E2339", {"start": v(-0.08, -15.7) * mm, "end": v(-0.02, -15.85) * mm});
            skLineSegment(sketch, "E2340", {"start": v(-0.02, -15.85) * mm, "end": v(0.04, -16.02) * mm});
            skLineSegment(sketch, "E2341", {"start": v(0.04, -16.02) * mm, "end": v(0.11, -16.18) * mm});
            skLineSegment(sketch, "E2342", {"start": v(0.11, -16.18) * mm, "end": v(0.19, -16.34) * mm});
            skLineSegment(sketch, "E2343", {"start": v(0.19, -16.34) * mm, "end": v(0.27, -16.5) * mm});
            skLineSegment(sketch, "E2344", {"start": v(0.27, -16.5) * mm, "end": v(0.35, -16.65) * mm});
            skLineSegment(sketch, "E2345", {"start": v(0.35, -16.65) * mm, "end": v(0.44, -16.8) * mm});
            skLineSegment(sketch, "E2346", {"start": v(0.44, -16.8) * mm, "end": v(0.53, -16.95) * mm});
            skLineSegment(sketch, "E2347", {"start": v(0.53, -16.95) * mm, "end": v(0.62, -17.1) * mm});
            skLineSegment(sketch, "E2348", {"start": v(0.62, -17.1) * mm, "end": v(0.7, -17.23) * mm});
            skLineSegment(sketch, "E2349", {"start": v(0.7, -17.23) * mm, "end": v(0.9, -17.22) * mm});
            skLineSegment(sketch, "E2350", {"start": v(0.9, -17.22) * mm, "end": v(1.08, -17.21) * mm});
            skLineSegment(sketch, "E2351", {"start": v(1.08, -17.21) * mm, "end": v(1.28, -17.2) * mm});
            skLineSegment(sketch, "E2352", {"start": v(1.28, -17.2) * mm, "end": v(1.47, -17.18) * mm});
            skLineSegment(sketch, "E2353", {"start": v(1.47, -17.18) * mm, "end": v(1.66, -17.16) * mm});
            skLineSegment(sketch, "E2354", {"start": v(1.66, -17.16) * mm, "end": v(1.75, -17.15) * mm});
            skLineSegment(sketch, "E2355", {"start": v(1.75, -17.15) * mm, "end": v(1.83, -16.98) * mm});
            skLineSegment(sketch, "E2356", {"start": v(1.83, -16.98) * mm, "end": v(1.9, -16.83) * mm});
            skLineSegment(sketch, "E2357", {"start": v(1.9, -16.83) * mm, "end": v(1.97, -16.65) * mm});
            skLineSegment(sketch, "E2358", {"start": v(1.97, -16.65) * mm, "end": v(2.03, -16.47) * mm});
            skLineSegment(sketch, "E2359", {"start": v(2.03, -16.47) * mm, "end": v(2.09, -16.3) * mm});
            skLineSegment(sketch, "E2360", {"start": v(2.09, -16.3) * mm, "end": v(2.15, -16.13) * mm});
            skLineSegment(sketch, "E2361", {"start": v(2.15, -16.13) * mm, "end": v(2.2, -15.96) * mm});
            skLineSegment(sketch, "E2362", {"start": v(2.2, -15.96) * mm, "end": v(2.24, -15.78) * mm});
            skLineSegment(sketch, "E2363", {"start": v(2.24, -15.78) * mm, "end": v(2.28, -15.61) * mm});
            skLineSegment(sketch, "E2364", {"start": v(2.28, -15.61) * mm, "end": v(2.31, -15.43) * mm});
            skLineSegment(sketch, "E2365", {"start": v(2.31, -15.43) * mm, "end": v(2.34, -15.24) * mm});
            skLineSegment(sketch, "E2366", {"start": v(2.34, -15.24) * mm, "end": v(2.36, -15.05) * mm});
            skLineSegment(sketch, "E2367", {"start": v(2.36, -15.05) * mm, "end": v(2.37, -14.87) * mm});
            skLineSegment(sketch, "E2368", {"start": v(2.37, -14.87) * mm, "end": v(2.37, -14.7) * mm});
            skLineSegment(sketch, "E2369", {"start": v(2.37, -14.7) * mm, "end": v(2.35, -14.5) * mm});
            skLineSegment(sketch, "E2370", {"start": v(2.35, -14.5) * mm, "end": v(2.33, -14.32) * mm});
            skLineSegment(sketch, "E2371", {"start": v(2.33, -14.32) * mm, "end": v(2.33, -14.15) * mm});
            skLineSegment(sketch, "E2372", {"start": v(2.33, -14.15) * mm, "end": v(2.35, -13.97) * mm});
            skLineSegment(sketch, "E2373", {"start": v(2.35, -13.97) * mm, "end": v(2.4, -13.8) * mm});
            skLineSegment(sketch, "E2374", {"start": v(2.4, -13.8) * mm, "end": v(2.5, -13.66) * mm});
            skLineSegment(sketch, "E2375", {"start": v(2.5, -13.66) * mm, "end": v(2.69, -13.61) * mm});
            skLineSegment(sketch, "E2376", {"start": v(2.69, -13.61) * mm, "end": v(2.87, -13.57) * mm});
            skLineSegment(sketch, "E2377", {"start": v(2.87, -13.57) * mm, "end": v(3.05, -13.52) * mm});
            skLineSegment(sketch, "E2378", {"start": v(3.05, -13.52) * mm, "end": v(3.24, -13.48) * mm});
            skLineSegment(sketch, "E2379", {"start": v(3.24, -13.48) * mm, "end": v(3.42, -13.43) * mm});
            skLineSegment(sketch, "E2380", {"start": v(3.42, -13.43) * mm, "end": v(3.52, -13.42) * mm});
            skLineSegment(sketch, "E2381", {"start": v(3.52, -13.42) * mm, "end": v(3.69, -13.49) * mm});
            skLineSegment(sketch, "E2382", {"start": v(3.69, -13.49) * mm, "end": v(3.8, -13.61) * mm});
            skLineSegment(sketch, "E2383", {"start": v(3.8, -13.61) * mm, "end": v(3.9, -13.75) * mm});
            skLineSegment(sketch, "E2384", {"start": v(3.9, -13.75) * mm, "end": v(3.98, -13.93) * mm});
            skLineSegment(sketch, "E2385", {"start": v(3.98, -13.93) * mm, "end": v(4.05, -14.1) * mm});
            skLineSegment(sketch, "E2386", {"start": v(4.05, -14.1) * mm, "end": v(4.1, -14.26) * mm});
            skLineSegment(sketch, "E2387", {"start": v(4.1, -14.26) * mm, "end": v(4.18, -14.42) * mm});
            skLineSegment(sketch, "E2388", {"start": v(4.18, -14.42) * mm, "end": v(4.26, -14.57) * mm});
            skLineSegment(sketch, "E2389", {"start": v(4.26, -14.57) * mm, "end": v(4.35, -14.72) * mm});
            skLineSegment(sketch, "E2390", {"start": v(4.35, -14.72) * mm, "end": v(4.44, -14.86) * mm});
            skLineSegment(sketch, "E2391", {"start": v(4.44, -14.86) * mm, "end": v(4.55, -15) * mm});
            skLineSegment(sketch, "E2392", {"start": v(4.55, -15) * mm, "end": v(4.65, -15.14) * mm});
            skLineSegment(sketch, "E2393", {"start": v(4.65, -15.14) * mm, "end": v(4.76, -15.27) * mm});
            skLineSegment(sketch, "E2394", {"start": v(4.76, -15.27) * mm, "end": v(4.88, -15.4) * mm});
            skLineSegment(sketch, "E2395", {"start": v(4.88, -15.4) * mm, "end": v(5, -15.54) * mm});
            skLineSegment(sketch, "E2396", {"start": v(5, -15.54) * mm, "end": v(5.11, -15.66) * mm});
            skLineSegment(sketch, "E2397", {"start": v(5.11, -15.66) * mm, "end": v(5.24, -15.8) * mm});
            skLineSegment(sketch, "E2398", {"start": v(5.24, -15.8) * mm, "end": v(5.37, -15.91) * mm});
            skLineSegment(sketch, "E2399", {"start": v(5.37, -15.91) * mm, "end": v(5.5, -16.03) * mm});
            skLineSegment(sketch, "E2400", {"start": v(5.5, -16.03) * mm, "end": v(5.63, -16.14) * mm});
            skLineSegment(sketch, "E2401", {"start": v(5.63, -16.14) * mm, "end": v(5.75, -16.24) * mm});
            skLineSegment(sketch, "E2402", {"start": v(5.75, -16.24) * mm, "end": v(5.93, -16.18) * mm});
            skLineSegment(sketch, "E2403", {"start": v(5.93, -16.18) * mm, "end": v(6.1, -16.11) * mm});
            skLineSegment(sketch, "E2404", {"start": v(6.1, -16.11) * mm, "end": v(6.3, -16.04) * mm});
            skLineSegment(sketch, "E2405", {"start": v(6.3, -16.04) * mm, "end": v(6.47, -15.97) * mm});
            skLineSegment(sketch, "E2406", {"start": v(6.47, -15.97) * mm, "end": v(6.64, -15.9) * mm});
            skLineSegment(sketch, "E2407", {"start": v(6.64, -15.9) * mm, "end": v(6.73, -15.86) * mm});
            skLineSegment(sketch, "E2408", {"start": v(6.73, -15.86) * mm, "end": v(6.75, -15.67) * mm});
            skLineSegment(sketch, "E2409", {"start": v(6.75, -15.67) * mm, "end": v(6.77, -15.5) * mm});
            skLineSegment(sketch, "E2410", {"start": v(6.77, -15.5) * mm, "end": v(6.78, -15.3) * mm});
            skLineSegment(sketch, "E2411", {"start": v(6.78, -15.3) * mm, "end": v(6.8, -15.12) * mm});
            skLineSegment(sketch, "E2412", {"start": v(6.8, -15.12) * mm, "end": v(6.8, -14.95) * mm});
            skLineSegment(sketch, "E2413", {"start": v(6.8, -14.95) * mm, "end": v(6.8, -14.76) * mm});
            skLineSegment(sketch, "E2414", {"start": v(6.8, -14.76) * mm, "end": v(6.8, -14.58) * mm});
            skLineSegment(sketch, "E2415", {"start": v(6.8, -14.58) * mm, "end": v(6.79, -14.4) * mm});
            skLineSegment(sketch, "E2416", {"start": v(6.79, -14.4) * mm, "end": v(6.78, -14.23) * mm});
            skLineSegment(sketch, "E2417", {"start": v(6.78, -14.23) * mm, "end": v(6.76, -14.04) * mm});
            skLineSegment(sketch, "E2418", {"start": v(6.76, -14.04) * mm, "end": v(6.73, -13.85) * mm});
            skLineSegment(sketch, "E2419", {"start": v(6.73, -13.85) * mm, "end": v(6.7, -13.66) * mm});
            skLineSegment(sketch, "E2420", {"start": v(6.7, -13.66) * mm, "end": v(6.65, -13.5) * mm});
            skLineSegment(sketch, "E2421", {"start": v(6.65, -13.5) * mm, "end": v(6.6, -13.33) * mm});
            skLineSegment(sketch, "E2422", {"start": v(6.6, -13.33) * mm, "end": v(6.52, -13.15) * mm});
            skLineSegment(sketch, "E2423", {"start": v(6.52, -13.15) * mm, "end": v(6.45, -12.98) * mm});
            skLineSegment(sketch, "E2424", {"start": v(6.45, -12.98) * mm, "end": v(6.4, -12.82) * mm});
            skLineSegment(sketch, "E2425", {"start": v(6.4, -12.82) * mm, "end": v(6.36, -12.64) * mm});
            skLineSegment(sketch, "E2426", {"start": v(6.36, -12.64) * mm, "end": v(6.36, -12.45) * mm});
            skLineSegment(sketch, "E2427", {"start": v(6.36, -12.45) * mm, "end": v(6.42, -12.3) * mm});
            skLineSegment(sketch, "E2428", {"start": v(6.42, -12.3) * mm, "end": v(6.58, -12.2) * mm});
            skLineSegment(sketch, "E2429", {"start": v(6.58, -12.2) * mm, "end": v(6.74, -12.1) * mm});
            skLineSegment(sketch, "E2430", {"start": v(6.74, -12.1) * mm, "end": v(6.9, -12) * mm});
            skLineSegment(sketch, "E2431", {"start": v(6.9, -12) * mm, "end": v(7.06, -11.9) * mm});
            skLineSegment(sketch, "E2432", {"start": v(7.06, -11.9) * mm, "end": v(7.22, -11.8) * mm});
            skLineSegment(sketch, "E2433", {"start": v(7.22, -11.8) * mm, "end": v(7.32, -11.77) * mm});
            skLineSegment(sketch, "E2434", {"start": v(7.32, -11.77) * mm, "end": v(7.5, -11.78) * mm});
            skLineSegment(sketch, "E2435", {"start": v(7.5, -11.78) * mm, "end": v(7.65, -11.86) * mm});
            skLineSegment(sketch, "E2436", {"start": v(7.65, -11.86) * mm, "end": v(7.78, -11.97) * mm});
            skLineSegment(sketch, "E2437", {"start": v(7.78, -11.97) * mm, "end": v(7.9, -12.12) * mm});
            skLineSegment(sketch, "E2438", {"start": v(7.9, -12.12) * mm, "end": v(8.02, -12.26) * mm});
            skLineSegment(sketch, "E2439", {"start": v(8.02, -12.26) * mm, "end": v(8.13, -12.4) * mm});
            skLineSegment(sketch, "E2440", {"start": v(8.13, -12.4) * mm, "end": v(8.24, -12.53) * mm});
            skLineSegment(sketch, "E2441", {"start": v(8.24, -12.53) * mm, "end": v(8.37, -12.65) * mm});
            skLineSegment(sketch, "E2442", {"start": v(8.37, -12.65) * mm, "end": v(8.5, -12.76) * mm});
            skLineSegment(sketch, "E2443", {"start": v(8.5, -12.76) * mm, "end": v(8.62, -12.87) * mm});
            skLineSegment(sketch, "E2444", {"start": v(8.62, -12.87) * mm, "end": v(8.76, -12.98) * mm});
            skLineSegment(sketch, "E2445", {"start": v(8.76, -12.98) * mm, "end": v(8.9, -13.08) * mm});
            skLineSegment(sketch, "E2446", {"start": v(8.9, -13.08) * mm, "end": v(9.05, -13.17) * mm});
            skLineSegment(sketch, "E2447", {"start": v(9.05, -13.17) * mm, "end": v(9.2, -13.27) * mm});
            skLineSegment(sketch, "E2448", {"start": v(9.2, -13.27) * mm, "end": v(9.35, -13.36) * mm});
            skLineSegment(sketch, "E2449", {"start": v(9.35, -13.36) * mm, "end": v(9.5, -13.44) * mm});
            skLineSegment(sketch, "E2450", {"start": v(9.5, -13.44) * mm, "end": v(9.66, -13.53) * mm});
            skLineSegment(sketch, "E2451", {"start": v(9.66, -13.53) * mm, "end": v(9.82, -13.6) * mm});
            skLineSegment(sketch, "E2452", {"start": v(9.82, -13.6) * mm, "end": v(9.98, -13.68) * mm});
            skLineSegment(sketch, "E2453", {"start": v(9.98, -13.68) * mm, "end": v(10.14, -13.75) * mm});
            skLineSegment(sketch, "E2454", {"start": v(10.14, -13.75) * mm, "end": v(10.28, -13.8) * mm});
            skLineSegment(sketch, "E2455", {"start": v(10.28, -13.8) * mm, "end": v(10.43, -13.7) * mm});
            skLineSegment(sketch, "E2456", {"start": v(10.43, -13.7) * mm, "end": v(10.58, -13.58) * mm});
            skLineSegment(sketch, "E2457", {"start": v(10.58, -13.58) * mm, "end": v(10.74, -13.45) * mm});
            skLineSegment(sketch, "E2458", {"start": v(10.74, -13.45) * mm, "end": v(10.88, -13.33) * mm});
            skLineSegment(sketch, "E2459", {"start": v(10.88, -13.33) * mm, "end": v(11.03, -13.21) * mm});
            skLineSegment(sketch, "E2460", {"start": v(11.03, -13.21) * mm, "end": v(11.1, -13.15) * mm});
            skLineSegment(sketch, "E2461", {"start": v(11.1, -13.15) * mm, "end": v(11.07, -12.97) * mm});
            skLineSegment(sketch, "E2462", {"start": v(11.07, -12.97) * mm, "end": v(11.03, -12.8) * mm});
            skLineSegment(sketch, "E2463", {"start": v(11.03, -12.8) * mm, "end": v(11, -12.61) * mm});
            skLineSegment(sketch, "E2464", {"start": v(11, -12.61) * mm, "end": v(10.95, -12.43) * mm});
            skLineSegment(sketch, "E2465", {"start": v(10.95, -12.43) * mm, "end": v(10.9, -12.26) * mm});
            skLineSegment(sketch, "E2466", {"start": v(10.9, -12.26) * mm, "end": v(10.85, -12.08) * mm});
            skLineSegment(sketch, "E2467", {"start": v(10.85, -12.08) * mm, "end": v(10.8, -11.91) * mm});
            skLineSegment(sketch, "E2468", {"start": v(10.8, -11.91) * mm, "end": v(10.73, -11.74) * mm});
            skLineSegment(sketch, "E2469", {"start": v(10.73, -11.74) * mm, "end": v(10.67, -11.58) * mm});
            skLineSegment(sketch, "E2470", {"start": v(10.67, -11.58) * mm, "end": v(10.6, -11.4) * mm});
            skLineSegment(sketch, "E2471", {"start": v(10.6, -11.4) * mm, "end": v(10.5, -11.23) * mm});
            skLineSegment(sketch, "E2472", {"start": v(10.5, -11.23) * mm, "end": v(10.42, -11.07) * mm});
            skLineSegment(sketch, "E2473", {"start": v(10.42, -11.07) * mm, "end": v(10.33, -10.92) * mm});
            skLineSegment(sketch, "E2474", {"start": v(10.33, -10.92) * mm, "end": v(10.23, -10.77) * mm});
            skLineSegment(sketch, "E2475", {"start": v(10.23, -10.77) * mm, "end": v(10.1, -10.63) * mm});
            skLineSegment(sketch, "E2476", {"start": v(10.1, -10.63) * mm, "end": v(9.98, -10.48) * mm});
            skLineSegment(sketch, "E2477", {"start": v(9.98, -10.48) * mm, "end": v(9.89, -10.34) * mm});
            skLineSegment(sketch, "E2478", {"start": v(9.89, -10.34) * mm, "end": v(9.8, -10.18) * mm});
            skLineSegment(sketch, "E2479", {"start": v(9.8, -10.18) * mm, "end": v(9.75, -10) * mm});
            skLineSegment(sketch, "E2480", {"start": v(9.75, -10) * mm, "end": v(9.76, -9.84) * mm});
            skLineSegment(sketch, "E2481", {"start": v(9.76, -9.84) * mm, "end": v(9.88, -9.7) * mm});
            skLineSegment(sketch, "E2482", {"start": v(9.88, -9.7) * mm, "end": v(10, -9.56) * mm});
            skLineSegment(sketch, "E2483", {"start": v(10, -9.56) * mm, "end": v(10.13, -9.42) * mm});
            skLineSegment(sketch, "E2484", {"start": v(10.13, -9.42) * mm, "end": v(10.26, -9.28) * mm});
            skLineSegment(sketch, "E2485", {"start": v(10.26, -9.28) * mm, "end": v(10.38, -9.14) * mm});
            skLineSegment(sketch, "E2486", {"start": v(10.38, -9.14) * mm, "end": v(10.46, -9.07) * mm});
            skLineSegment(sketch, "E2487", {"start": v(10.46, -9.07) * mm, "end": v(10.63, -9.03) * mm});
            skLineSegment(sketch, "E2488", {"start": v(10.63, -9.03) * mm, "end": v(10.8, -9.06) * mm});
            skLineSegment(sketch, "E2489", {"start": v(10.8, -9.06) * mm, "end": v(10.96, -9.13) * mm});
            skLineSegment(sketch, "E2490", {"start": v(10.96, -9.13) * mm, "end": v(11.12, -9.23) * mm});
            skLineSegment(sketch, "E2491", {"start": v(11.12, -9.23) * mm, "end": v(11.28, -9.34) * mm});
            skLineSegment(sketch, "E2492", {"start": v(11.28, -9.34) * mm, "end": v(11.42, -9.43) * mm});
            skLineSegment(sketch, "E2493", {"start": v(11.42, -9.43) * mm, "end": v(11.56, -9.52) * mm});
            skLineSegment(sketch, "E2494", {"start": v(11.56, -9.52) * mm, "end": v(11.72, -9.6) * mm});
            skLineSegment(sketch, "E2495", {"start": v(11.72, -9.6) * mm, "end": v(11.88, -9.68) * mm});
            skLineSegment(sketch, "E2496", {"start": v(11.88, -9.68) * mm, "end": v(12.03, -9.74) * mm});
            skLineSegment(sketch, "E2497", {"start": v(12.03, -9.74) * mm, "end": v(12.2, -9.8) * mm});
            skLineSegment(sketch, "E2498", {"start": v(12.2, -9.8) * mm, "end": v(12.36, -9.85) * mm});
            skLineSegment(sketch, "E2499", {"start": v(12.36, -9.85) * mm, "end": v(12.53, -9.9) * mm});
            skLineSegment(sketch, "E2500", {"start": v(12.53, -9.9) * mm, "end": v(12.7, -9.95) * mm});
            skLineSegment(sketch, "E2501", {"start": v(12.7, -9.95) * mm, "end": v(12.87, -10) * mm});
            skLineSegment(sketch, "E2502", {"start": v(12.87, -10) * mm, "end": v(13.04, -10.03) * mm});
            skLineSegment(sketch, "E2503", {"start": v(13.04, -10.03) * mm, "end": v(13.22, -10.06) * mm});
            skLineSegment(sketch, "E2504", {"start": v(13.22, -10.06) * mm, "end": v(13.4, -10.09) * mm});
            skLineSegment(sketch, "E2505", {"start": v(13.4, -10.09) * mm, "end": v(13.56, -10.11) * mm});
            skLineSegment(sketch, "E2506", {"start": v(13.56, -10.11) * mm, "end": v(13.74, -10.13) * mm});
            skLineSegment(sketch, "E2507", {"start": v(13.74, -10.13) * mm, "end": v(13.89, -10.15) * mm});
            skLineSegment(sketch, "E2508", {"start": v(13.89, -10.15) * mm, "end": v(14, -10) * mm});
            skLineSegment(sketch, "E2509", {"start": v(14, -10) * mm, "end": v(14.1, -9.84) * mm});
            skLineSegment(sketch, "E2510", {"start": v(14.1, -9.84) * mm, "end": v(14.22, -9.67) * mm});
            skLineSegment(sketch, "E2511", {"start": v(14.22, -9.67) * mm, "end": v(14.33, -9.52) * mm});
            skLineSegment(sketch, "E2512", {"start": v(14.33, -9.52) * mm, "end": v(14.43, -9.36) * mm});
            skLineSegment(sketch, "E2513", {"start": v(14.43, -9.36) * mm, "end": v(14.48, -9.28) * mm});
            skLineSegment(sketch, "E2514", {"start": v(14.48, -9.28) * mm, "end": v(14.4, -9.11) * mm});
            skLineSegment(sketch, "E2515", {"start": v(14.4, -9.11) * mm, "end": v(14.31, -8.96) * mm});
            skLineSegment(sketch, "E2516", {"start": v(14.31, -8.96) * mm, "end": v(14.22, -8.8) * mm});
            skLineSegment(sketch, "E2517", {"start": v(14.22, -8.8) * mm, "end": v(14.12, -8.64) * mm});
            skLineSegment(sketch, "E2518", {"start": v(14.12, -8.64) * mm, "end": v(14.03, -8.49) * mm});
            skLineSegment(sketch, "E2519", {"start": v(14.03, -8.49) * mm, "end": v(13.92, -8.33) * mm});
            skLineSegment(sketch, "E2520", {"start": v(13.92, -8.33) * mm, "end": v(13.82, -8.19) * mm});
            skLineSegment(sketch, "E2521", {"start": v(13.82, -8.19) * mm, "end": v(13.71, -8.04) * mm});
            skLineSegment(sketch, "E2522", {"start": v(13.71, -8.04) * mm, "end": v(13.6, -7.9) * mm});
            skLineSegment(sketch, "E2523", {"start": v(13.6, -7.9) * mm, "end": v(13.48, -7.76) * mm});
            skLineSegment(sketch, "E2524", {"start": v(13.48, -7.76) * mm, "end": v(13.35, -7.62) * mm});
            skLineSegment(sketch, "E2525", {"start": v(13.35, -7.62) * mm, "end": v(13.21, -7.49) * mm});
            skLineSegment(sketch, "E2526", {"start": v(13.21, -7.49) * mm, "end": v(13.08, -7.37) * mm});
            skLineSegment(sketch, "E2527", {"start": v(13.08, -7.37) * mm, "end": v(12.94, -7.26) * mm});
            skLineSegment(sketch, "E2528", {"start": v(12.94, -7.26) * mm, "end": v(12.79, -7.16) * mm});
            skLineSegment(sketch, "E2529", {"start": v(12.79, -7.16) * mm, "end": v(12.63, -7.06) * mm});
            skLineSegment(sketch, "E2530", {"start": v(12.63, -7.06) * mm, "end": v(12.5, -6.95) * mm});
            skLineSegment(sketch, "E2531", {"start": v(12.5, -6.95) * mm, "end": v(12.36, -6.82) * mm});
            skLineSegment(sketch, "E2532", {"start": v(12.36, -6.82) * mm, "end": v(12.26, -6.67) * mm});
            skLineSegment(sketch, "E2533", {"start": v(12.26, -6.67) * mm, "end": v(12.22, -6.5) * mm});
            skLineSegment(sketch, "E2534", {"start": v(12.22, -6.5) * mm, "end": v(12.3, -6.34) * mm});
            skLineSegment(sketch, "E2535", {"start": v(12.3, -6.34) * mm, "end": v(12.38, -6.17) * mm});
            skLineSegment(sketch, "E2536", {"start": v(12.38, -6.17) * mm, "end": v(12.45, -6) * mm});
            skLineSegment(sketch, "E2537", {"start": v(12.45, -6) * mm, "end": v(12.53, -5.82) * mm});
            skLineSegment(sketch, "E2538", {"start": v(12.53, -5.82) * mm, "end": v(12.6, -5.65) * mm});
            skLineSegment(sketch, "E2539", {"start": v(12.6, -5.65) * mm, "end": v(12.66, -5.56) * mm});
            skLineSegment(sketch, "E2540", {"start": v(12.66, -5.56) * mm, "end": v(12.82, -5.48) * mm});
            skLineSegment(sketch, "E2541", {"start": v(12.82, -5.48) * mm, "end": v(13, -5.46) * mm});
            skLineSegment(sketch, "E2542", {"start": v(13, -5.46) * mm, "end": v(13.16, -5.47) * mm});
            skLineSegment(sketch, "E2543", {"start": v(13.16, -5.47) * mm, "end": v(13.34, -5.53) * mm});
            skLineSegment(sketch, "E2544", {"start": v(13.34, -5.53) * mm, "end": v(13.52, -5.58) * mm});
            skLineSegment(sketch, "E2545", {"start": v(13.52, -5.58) * mm, "end": v(13.69, -5.63) * mm});
            skLineSegment(sketch, "E2546", {"start": v(13.69, -5.63) * mm, "end": v(13.86, -5.67) * mm});
            skLineSegment(sketch, "E2547", {"start": v(13.86, -5.67) * mm, "end": v(14.03, -5.7) * mm});
            skLineSegment(sketch, "E2548", {"start": v(14.03, -5.7) * mm, "end": v(14.2, -5.73) * mm});
            skLineSegment(sketch, "E2549", {"start": v(14.2, -5.73) * mm, "end": v(14.37, -5.74) * mm});
            skLineSegment(sketch, "E2550", {"start": v(14.37, -5.74) * mm, "end": v(14.54, -5.75) * mm});
            skLineSegment(sketch, "E2551", {"start": v(14.54, -5.75) * mm, "end": v(14.71, -5.76) * mm});
            skLineSegment(sketch, "E2552", {"start": v(14.71, -5.76) * mm, "end": v(14.89, -5.75) * mm});
            skLineSegment(sketch, "E2553", {"start": v(14.89, -5.75) * mm, "end": v(15.06, -5.75) * mm});
            skLineSegment(sketch, "E2554", {"start": v(15.06, -5.75) * mm, "end": v(15.24, -5.74) * mm});
            skLineSegment(sketch, "E2555", {"start": v(15.24, -5.74) * mm, "end": v(15.41, -5.72) * mm});
            skLineSegment(sketch, "E2556", {"start": v(15.41, -5.72) * mm, "end": v(15.6, -5.7) * mm});
            skLineSegment(sketch, "E2557", {"start": v(15.6, -5.7) * mm, "end": v(15.77, -5.67) * mm});
            skLineSegment(sketch, "E2558", {"start": v(15.77, -5.67) * mm, "end": v(15.94, -5.65) * mm});
            skLineSegment(sketch, "E2559", {"start": v(15.94, -5.65) * mm, "end": v(16.11, -5.61) * mm});
            skLineSegment(sketch, "E2560", {"start": v(16.11, -5.61) * mm, "end": v(16.26, -5.58) * mm});
            skLineSegment(sketch, "E2561", {"start": v(16.26, -5.58) * mm, "end": v(16.32, -5.4) * mm});
            skLineSegment(sketch, "E2562", {"start": v(16.32, -5.4) * mm, "end": v(16.38, -5.23) * mm});
            skLineSegment(sketch, "E2563", {"start": v(16.38, -5.23) * mm, "end": v(16.44, -5.03) * mm});
            skLineSegment(sketch, "E2564", {"start": v(16.44, -5.03) * mm, "end": v(16.5, -4.85) * mm});
            skLineSegment(sketch, "E2565", {"start": v(16.5, -4.85) * mm, "end": v(16.54, -4.67) * mm});
            skLineSegment(sketch, "E2566", {"start": v(16.54, -4.67) * mm, "end": v(16.57, -4.58) * mm});
            skLineSegment(sketch, "E2567", {"start": v(16.57, -4.58) * mm, "end": v(16.44, -4.45) * mm});
            skLineSegment(sketch, "E2568", {"start": v(16.44, -4.45) * mm, "end": v(16.32, -4.33) * mm});
            skLineSegment(sketch, "E2569", {"start": v(16.32, -4.33) * mm, "end": v(16.18, -4.2) * mm});
            skLineSegment(sketch, "E2570", {"start": v(16.18, -4.2) * mm, "end": v(16.04, -4.07) * mm});
            skLineSegment(sketch, "E2571", {"start": v(16.04, -4.07) * mm, "end": v(15.9, -3.96) * mm});
            skLineSegment(sketch, "E2572", {"start": v(15.9, -3.96) * mm, "end": v(15.76, -3.84) * mm});
            skLineSegment(sketch, "E2573", {"start": v(15.76, -3.84) * mm, "end": v(15.62, -3.73) * mm});
            skLineSegment(sketch, "E2574", {"start": v(15.62, -3.73) * mm, "end": v(15.47, -3.62) * mm});
            skLineSegment(sketch, "E2575", {"start": v(15.47, -3.62) * mm, "end": v(15.33, -3.53) * mm});
            skLineSegment(sketch, "E2576", {"start": v(15.33, -3.53) * mm, "end": v(15.17, -3.43) * mm});
            skLineSegment(sketch, "E2577", {"start": v(15.17, -3.43) * mm, "end": v(15, -3.33) * mm});
            skLineSegment(sketch, "E2578", {"start": v(15, -3.33) * mm, "end": v(14.83, -3.24) * mm});
            skLineSegment(sketch, "E2579", {"start": v(14.83, -3.24) * mm, "end": v(14.67, -3.17) * mm});
            skLineSegment(sketch, "E2580", {"start": v(14.67, -3.17) * mm, "end": v(14.5, -3.1) * mm});
            skLineSegment(sketch, "E2581", {"start": v(14.5, -3.1) * mm, "end": v(14.33, -3.05) * mm});
            skLineSegment(sketch, "E2582", {"start": v(14.33, -3.05) * mm, "end": v(14.14, -3) * mm});
            skLineSegment(sketch, "E2583", {"start": v(14.14, -3) * mm, "end": v(13.98, -2.94) * mm});
            skLineSegment(sketch, "E2584", {"start": v(13.98, -2.94) * mm, "end": v(13.82, -2.86) * mm});
            skLineSegment(sketch, "E2585", {"start": v(13.82, -2.86) * mm, "end": v(13.68, -2.74) * mm});
            skLineSegment(sketch, "E2586", {"start": v(13.68, -2.74) * mm, "end": v(13.6, -2.6) * mm});
            skLineSegment(sketch, "E2587", {"start": v(13.6, -2.6) * mm, "end": v(13.62, -2.41) * mm});
            skLineSegment(sketch, "E2588", {"start": v(13.62, -2.41) * mm, "end": v(13.64, -2.23) * mm});
            skLineSegment(sketch, "E2589", {"start": v(13.64, -2.23) * mm, "end": v(13.67, -2.04) * mm});
            skLineSegment(sketch, "E2590", {"start": v(13.67, -2.04) * mm, "end": v(13.69, -1.85) * mm});
            skLineSegment(sketch, "E2591", {"start": v(13.69, -1.85) * mm, "end": v(13.71, -1.67) * mm});
            skLineSegment(sketch, "E2592", {"start": v(13.71, -1.67) * mm, "end": v(13.74, -1.57) * mm});
            skLineSegment(sketch, "E2593", {"start": v(13.74, -1.57) * mm, "end": v(13.86, -1.44) * mm});
            skLineSegment(sketch, "E2594", {"start": v(13.86, -1.44) * mm, "end": v(14.02, -1.37) * mm});
            skLineSegment(sketch, "E2595", {"start": v(14.02, -1.37) * mm, "end": v(14.19, -1.33) * mm});
            skLineSegment(sketch, "E2596", {"start": v(14.19, -1.33) * mm, "end": v(14.38, -1.33) * mm});
            skLineSegment(sketch, "E2597", {"start": v(14.38, -1.33) * mm, "end": v(14.57, -1.33) * mm});
            skLineSegment(sketch, "E2598", {"start": v(14.57, -1.33) * mm, "end": v(14.68, -1.33) * mm});
            skSolve(sketch);
        }
        {
            var Q0;
            Q0 = qSketchRegion(id + "F11", true);
            extrude(context, id + "F12", {"entities" : qUnion([Q0]), "depth" : 5 * mm, "offsetDistance" : 25 * mm});
        }
        {
            var Q0;
            Q0=qCreatedBy(makeId("Front.planeOp"),FACE);
            var sketch = newSketch(context, id + "F13", { "sketchPlane" : qUnion([Q0])});
            skCircle(sketch, "E2599", {"center": v(0, 0) * mm, "radius": 3 * mm});
            skSolve(sketch);
        }
        {
            var Q0;
            Q0 = qSketchRegion(id + "F13", true);
            var Q1;
            Q1=makeQuery(id+"F12.opExtrude","CAP_FACE",FACE,{"disambiguationData":[OSD([sQuery(id+"F11.wireOp",EDGE,"E1476"),sQuery(id+"F11.wireOp",EDGE,"E1477"),sQuery(id+"F11.wireOp",EDGE,"E1478"),sQuery(id+"F11.wireOp",EDGE,"E1479"),sQuery(id+"F11.wireOp",EDGE,"E1480"),sQuery(id+"F11.wireOp",EDGE,"E1481"),sQuery(id+"F11.wireOp",EDGE,"E1482"),sQuery(id+"F11.wireOp",EDGE,"E1483"),sQuery(id+"F11.wireOp",EDGE,"E1484"),sQuery(id+"F11.wireOp",EDGE,"E1485"),sQuery(id+"F11.wireOp",EDGE,"E1486"),sQuery(id+"F11.wireOp",EDGE,"E1487"),sQuery(id+"F11.wireOp",EDGE,"E1488"),sQuery(id+"F11.wireOp",EDGE,"E1489"),sQuery(id+"F11.wireOp",EDGE,"E1490"),sQuery(id+"F11.wireOp",EDGE,"E1491"),sQuery(id+"F11.wireOp",EDGE,"E1492"),sQuery(id+"F11.wireOp",EDGE,"E1493"),sQuery(id+"F11.wireOp",EDGE,"E1494"),sQuery(id+"F11.wireOp",EDGE,"E1495"),sQuery(id+"F11.wireOp",EDGE,"E1496"),sQuery(id+"F11.wireOp",EDGE,"E1497"),sQuery(id+"F11.wireOp",EDGE,"E1498"),sQuery(id+"F11.wireOp",EDGE,"E1499"),sQuery(id+"F11.wireOp",EDGE,"E1500"),sQuery(id+"F11.wireOp",EDGE,"E1501"),sQuery(id+"F11.wireOp",EDGE,"E1502"),sQuery(id+"F11.wireOp",EDGE,"E1503"),sQuery(id+"F11.wireOp",EDGE,"E1504"),sQuery(id+"F11.wireOp",EDGE,"E1505"),sQuery(id+"F11.wireOp",EDGE,"E1506"),sQuery(id+"F11.wireOp",EDGE,"E1507"),sQuery(id+"F11.wireOp",EDGE,"E1508"),sQuery(id+"F11.wireOp",EDGE,"E1509"),sQuery(id+"F11.wireOp",EDGE,"E1510"),sQuery(id+"F11.wireOp",EDGE,"E1511"),sQuery(id+"F11.wireOp",EDGE,"E1512"),sQuery(id+"F11.wireOp",EDGE,"E1513"),sQuery(id+"F11.wireOp",EDGE,"E1514"),sQuery(id+"F11.wireOp",EDGE,"E1515"),sQuery(id+"F11.wireOp",EDGE,"E1516"),sQuery(id+"F11.wireOp",EDGE,"E1517"),sQuery(id+"F11.wireOp",EDGE,"E1518"),sQuery(id+"F11.wireOp",EDGE,"E1519"),sQuery(id+"F11.wireOp",EDGE,"E1520"),sQuery(id+"F11.wireOp",EDGE,"E1521"),sQuery(id+"F11.wireOp",EDGE,"E1522"),sQuery(id+"F11.wireOp",EDGE,"E1523"),sQuery(id+"F11.wireOp",EDGE,"E1524"),sQuery(id+"F11.wireOp",EDGE,"E1525"),sQuery(id+"F11.wireOp",EDGE,"E1526"),sQuery(id+"F11.wireOp",EDGE,"E1527"),sQuery(id+"F11.wireOp",EDGE,"E1528"),sQuery(id+"F11.wireOp",EDGE,"E1529"),sQuery(id+"F11.wireOp",EDGE,"E1530"),sQuery(id+"F11.wireOp",EDGE,"E1531"),sQuery(id+"F11.wireOp",EDGE,"E1532"),sQuery(id+"F11.wireOp",EDGE,"E1533"),sQuery(id+"F11.wireOp",EDGE,"E1534"),sQuery(id+"F11.wireOp",EDGE,"E1535"),sQuery(id+"F11.wireOp",EDGE,"E1536"),sQuery(id+"F11.wireOp",EDGE,"E1537"),sQuery(id+"F11.wireOp",EDGE,"E1538"),sQuery(id+"F11.wireOp",EDGE,"E1539"),sQuery(id+"F11.wireOp",EDGE,"E1540"),sQuery(id+"F11.wireOp",EDGE,"E1541"),sQuery(id+"F11.wireOp",EDGE,"E1542"),sQuery(id+"F11.wireOp",EDGE,"E1543"),sQuery(id+"F11.wireOp",EDGE,"E1544"),sQuery(id+"F11.wireOp",EDGE,"E1545"),sQuery(id+"F11.wireOp",EDGE,"E1546"),sQuery(id+"F11.wireOp",EDGE,"E1547"),sQuery(id+"F11.wireOp",EDGE,"E1548"),sQuery(id+"F11.wireOp",EDGE,"E1549"),sQuery(id+"F11.wireOp",EDGE,"E1550"),sQuery(id+"F11.wireOp",EDGE,"E1551"),sQuery(id+"F11.wireOp",EDGE,"E1552"),sQuery(id+"F11.wireOp",EDGE,"E1553"),sQuery(id+"F11.wireOp",EDGE,"E1554"),sQuery(id+"F11.wireOp",EDGE,"E1555"),sQuery(id+"F11.wireOp",EDGE,"E1556"),sQuery(id+"F11.wireOp",EDGE,"E1557"),sQuery(id+"F11.wireOp",EDGE,"E1558"),sQuery(id+"F11.wireOp",EDGE,"E1559"),sQuery(id+"F11.wireOp",EDGE,"E1560"),sQuery(id+"F11.wireOp",EDGE,"E1561"),sQuery(id+"F11.wireOp",EDGE,"E1562"),sQuery(id+"F11.wireOp",EDGE,"E1563"),sQuery(id+"F11.wireOp",EDGE,"E1564"),sQuery(id+"F11.wireOp",EDGE,"E1565"),sQuery(id+"F11.wireOp",EDGE,"E1566"),sQuery(id+"F11.wireOp",EDGE,"E1567"),sQuery(id+"F11.wireOp",EDGE,"E1568"),sQuery(id+"F11.wireOp",EDGE,"E1569"),sQuery(id+"F11.wireOp",EDGE,"E1570"),sQuery(id+"F11.wireOp",EDGE,"E1571"),sQuery(id+"F11.wireOp",EDGE,"E1572"),sQuery(id+"F11.wireOp",EDGE,"E1573"),sQuery(id+"F11.wireOp",EDGE,"E1574"),sQuery(id+"F11.wireOp",EDGE,"E1575"),sQuery(id+"F11.wireOp",EDGE,"E1576"),sQuery(id+"F11.wireOp",EDGE,"E1577"),sQuery(id+"F11.wireOp",EDGE,"E1578"),sQuery(id+"F11.wireOp",EDGE,"E1579"),sQuery(id+"F11.wireOp",EDGE,"E1580"),sQuery(id+"F11.wireOp",EDGE,"E1581"),sQuery(id+"F11.wireOp",EDGE,"E1582"),sQuery(id+"F11.wireOp",EDGE,"E1583"),sQuery(id+"F11.wireOp",EDGE,"E1584"),sQuery(id+"F11.wireOp",EDGE,"E1585"),sQuery(id+"F11.wireOp",EDGE,"E1586"),sQuery(id+"F11.wireOp",EDGE,"E1587"),sQuery(id+"F11.wireOp",EDGE,"E1588"),sQuery(id+"F11.wireOp",EDGE,"E1589"),sQuery(id+"F11.wireOp",EDGE,"E1590"),sQuery(id+"F11.wireOp",EDGE,"E1591"),sQuery(id+"F11.wireOp",EDGE,"E1592"),sQuery(id+"F11.wireOp",EDGE,"E1593"),sQuery(id+"F11.wireOp",EDGE,"E1594"),sQuery(id+"F11.wireOp",EDGE,"E1595"),sQuery(id+"F11.wireOp",EDGE,"E1596"),sQuery(id+"F11.wireOp",EDGE,"E1597"),sQuery(id+"F11.wireOp",EDGE,"E1598"),sQuery(id+"F11.wireOp",EDGE,"E1599"),sQuery(id+"F11.wireOp",EDGE,"E1600"),sQuery(id+"F11.wireOp",EDGE,"E1601"),sQuery(id+"F11.wireOp",EDGE,"E1602"),sQuery(id+"F11.wireOp",EDGE,"E1603"),sQuery(id+"F11.wireOp",EDGE,"E1604"),sQuery(id+"F11.wireOp",EDGE,"E1605"),sQuery(id+"F11.wireOp",EDGE,"E1606"),sQuery(id+"F11.wireOp",EDGE,"E1607"),sQuery(id+"F11.wireOp",EDGE,"E1608"),sQuery(id+"F11.wireOp",EDGE,"E1609"),sQuery(id+"F11.wireOp",EDGE,"E1610"),sQuery(id+"F11.wireOp",EDGE,"E1611"),sQuery(id+"F11.wireOp",EDGE,"E1612"),sQuery(id+"F11.wireOp",EDGE,"E1613"),sQuery(id+"F11.wireOp",EDGE,"E1614"),sQuery(id+"F11.wireOp",EDGE,"E1615"),sQuery(id+"F11.wireOp",EDGE,"E1616"),sQuery(id+"F11.wireOp",EDGE,"E1617"),sQuery(id+"F11.wireOp",EDGE,"E1618"),sQuery(id+"F11.wireOp",EDGE,"E1619"),sQuery(id+"F11.wireOp",EDGE,"E1620"),sQuery(id+"F11.wireOp",EDGE,"E1621"),sQuery(id+"F11.wireOp",EDGE,"E1622"),sQuery(id+"F11.wireOp",EDGE,"E1623"),sQuery(id+"F11.wireOp",EDGE,"E1624"),sQuery(id+"F11.wireOp",EDGE,"E1625"),sQuery(id+"F11.wireOp",EDGE,"E1626"),sQuery(id+"F11.wireOp",EDGE,"E1627"),sQuery(id+"F11.wireOp",EDGE,"E1628"),sQuery(id+"F11.wireOp",EDGE,"E1629"),sQuery(id+"F11.wireOp",EDGE,"E1630"),sQuery(id+"F11.wireOp",EDGE,"E1631"),sQuery(id+"F11.wireOp",EDGE,"E1632"),sQuery(id+"F11.wireOp",EDGE,"E1633"),sQuery(id+"F11.wireOp",EDGE,"E1634"),sQuery(id+"F11.wireOp",EDGE,"E1635"),sQuery(id+"F11.wireOp",EDGE,"E1636"),sQuery(id+"F11.wireOp",EDGE,"E1637"),sQuery(id+"F11.wireOp",EDGE,"E1638"),sQuery(id+"F11.wireOp",EDGE,"E1639"),sQuery(id+"F11.wireOp",EDGE,"E1640"),sQuery(id+"F11.wireOp",EDGE,"E1641"),sQuery(id+"F11.wireOp",EDGE,"E1642"),sQuery(id+"F11.wireOp",EDGE,"E1643"),sQuery(id+"F11.wireOp",EDGE,"E1644"),sQuery(id+"F11.wireOp",EDGE,"E1645"),sQuery(id+"F11.wireOp",EDGE,"E1646"),sQuery(id+"F11.wireOp",EDGE,"E1647"),sQuery(id+"F11.wireOp",EDGE,"E1648"),sQuery(id+"F11.wireOp",EDGE,"E1649"),sQuery(id+"F11.wireOp",EDGE,"E1650"),sQuery(id+"F11.wireOp",EDGE,"E1651"),sQuery(id+"F11.wireOp",EDGE,"E1652"),sQuery(id+"F11.wireOp",EDGE,"E1653"),sQuery(id+"F11.wireOp",EDGE,"E1654"),sQuery(id+"F11.wireOp",EDGE,"E1655"),sQuery(id+"F11.wireOp",EDGE,"E1656"),sQuery(id+"F11.wireOp",EDGE,"E1657"),sQuery(id+"F11.wireOp",EDGE,"E1658"),sQuery(id+"F11.wireOp",EDGE,"E1659"),sQuery(id+"F11.wireOp",EDGE,"E1660"),sQuery(id+"F11.wireOp",EDGE,"E1661"),sQuery(id+"F11.wireOp",EDGE,"E1662"),sQuery(id+"F11.wireOp",EDGE,"E1663"),sQuery(id+"F11.wireOp",EDGE,"E1664"),sQuery(id+"F11.wireOp",EDGE,"E1665"),sQuery(id+"F11.wireOp",EDGE,"E1666"),sQuery(id+"F11.wireOp",EDGE,"E1667"),sQuery(id+"F11.wireOp",EDGE,"E1668"),sQuery(id+"F11.wireOp",EDGE,"E1669"),sQuery(id+"F11.wireOp",EDGE,"E1670"),sQuery(id+"F11.wireOp",EDGE,"E1671"),sQuery(id+"F11.wireOp",EDGE,"E1672"),sQuery(id+"F11.wireOp",EDGE,"E1673"),sQuery(id+"F11.wireOp",EDGE,"E1674"),sQuery(id+"F11.wireOp",EDGE,"E1675"),sQuery(id+"F11.wireOp",EDGE,"E1676"),sQuery(id+"F11.wireOp",EDGE,"E1677"),sQuery(id+"F11.wireOp",EDGE,"E1678"),sQuery(id+"F11.wireOp",EDGE,"E1679"),sQuery(id+"F11.wireOp",EDGE,"E1680"),sQuery(id+"F11.wireOp",EDGE,"E1681"),sQuery(id+"F11.wireOp",EDGE,"E1682"),sQuery(id+"F11.wireOp",EDGE,"E1683"),sQuery(id+"F11.wireOp",EDGE,"E1684"),sQuery(id+"F11.wireOp",EDGE,"E1685"),sQuery(id+"F11.wireOp",EDGE,"E1686"),sQuery(id+"F11.wireOp",EDGE,"E1687"),sQuery(id+"F11.wireOp",EDGE,"E1688"),sQuery(id+"F11.wireOp",EDGE,"E1689"),sQuery(id+"F11.wireOp",EDGE,"E1690"),sQuery(id+"F11.wireOp",EDGE,"E1691"),sQuery(id+"F11.wireOp",EDGE,"E1692"),sQuery(id+"F11.wireOp",EDGE,"E1693"),sQuery(id+"F11.wireOp",EDGE,"E1694"),sQuery(id+"F11.wireOp",EDGE,"E1695"),sQuery(id+"F11.wireOp",EDGE,"E1696"),sQuery(id+"F11.wireOp",EDGE,"E1697"),sQuery(id+"F11.wireOp",EDGE,"E1698"),sQuery(id+"F11.wireOp",EDGE,"E1699"),sQuery(id+"F11.wireOp",EDGE,"E1700"),sQuery(id+"F11.wireOp",EDGE,"E1701"),sQuery(id+"F11.wireOp",EDGE,"E1702"),sQuery(id+"F11.wireOp",EDGE,"E1703"),sQuery(id+"F11.wireOp",EDGE,"E1704"),sQuery(id+"F11.wireOp",EDGE,"E1705"),sQuery(id+"F11.wireOp",EDGE,"E1706"),sQuery(id+"F11.wireOp",EDGE,"E1707"),sQuery(id+"F11.wireOp",EDGE,"E1708"),sQuery(id+"F11.wireOp",EDGE,"E1709"),sQuery(id+"F11.wireOp",EDGE,"E1710"),sQuery(id+"F11.wireOp",EDGE,"E1711"),sQuery(id+"F11.wireOp",EDGE,"E1712"),sQuery(id+"F11.wireOp",EDGE,"E1713"),sQuery(id+"F11.wireOp",EDGE,"E1714"),sQuery(id+"F11.wireOp",EDGE,"E1715"),sQuery(id+"F11.wireOp",EDGE,"E1716"),sQuery(id+"F11.wireOp",EDGE,"E1717"),sQuery(id+"F11.wireOp",EDGE,"E1718"),sQuery(id+"F11.wireOp",EDGE,"E1719"),sQuery(id+"F11.wireOp",EDGE,"E1720"),sQuery(id+"F11.wireOp",EDGE,"E1721"),sQuery(id+"F11.wireOp",EDGE,"E1722"),sQuery(id+"F11.wireOp",EDGE,"E1723"),sQuery(id+"F11.wireOp",EDGE,"E1724"),sQuery(id+"F11.wireOp",EDGE,"E1725"),sQuery(id+"F11.wireOp",EDGE,"E1726"),sQuery(id+"F11.wireOp",EDGE,"E1727"),sQuery(id+"F11.wireOp",EDGE,"E1728"),sQuery(id+"F11.wireOp",EDGE,"E1729"),sQuery(id+"F11.wireOp",EDGE,"E1730"),sQuery(id+"F11.wireOp",EDGE,"E1731"),sQuery(id+"F11.wireOp",EDGE,"E1732"),sQuery(id+"F11.wireOp",EDGE,"E1733"),sQuery(id+"F11.wireOp",EDGE,"E1734"),sQuery(id+"F11.wireOp",EDGE,"E1735"),sQuery(id+"F11.wireOp",EDGE,"E1736"),sQuery(id+"F11.wireOp",EDGE,"E1737"),sQuery(id+"F11.wireOp",EDGE,"E1738"),sQuery(id+"F11.wireOp",EDGE,"E1739"),sQuery(id+"F11.wireOp",EDGE,"E1740"),sQuery(id+"F11.wireOp",EDGE,"E1741"),sQuery(id+"F11.wireOp",EDGE,"E1742"),sQuery(id+"F11.wireOp",EDGE,"E1743"),sQuery(id+"F11.wireOp",EDGE,"E1744"),sQuery(id+"F11.wireOp",EDGE,"E1745"),sQuery(id+"F11.wireOp",EDGE,"E1746"),sQuery(id+"F11.wireOp",EDGE,"E1747"),sQuery(id+"F11.wireOp",EDGE,"E1748"),sQuery(id+"F11.wireOp",EDGE,"E1749"),sQuery(id+"F11.wireOp",EDGE,"E1750"),sQuery(id+"F11.wireOp",EDGE,"E1751"),sQuery(id+"F11.wireOp",EDGE,"E1752"),sQuery(id+"F11.wireOp",EDGE,"E1753"),sQuery(id+"F11.wireOp",EDGE,"E1754"),sQuery(id+"F11.wireOp",EDGE,"E1755"),sQuery(id+"F11.wireOp",EDGE,"E1756"),sQuery(id+"F11.wireOp",EDGE,"E1757"),sQuery(id+"F11.wireOp",EDGE,"E1758"),sQuery(id+"F11.wireOp",EDGE,"E1759"),sQuery(id+"F11.wireOp",EDGE,"E1760"),sQuery(id+"F11.wireOp",EDGE,"E1761"),sQuery(id+"F11.wireOp",EDGE,"E1762"),sQuery(id+"F11.wireOp",EDGE,"E1763"),sQuery(id+"F11.wireOp",EDGE,"E1764"),sQuery(id+"F11.wireOp",EDGE,"E1765"),sQuery(id+"F11.wireOp",EDGE,"E1766"),sQuery(id+"F11.wireOp",EDGE,"E1767"),sQuery(id+"F11.wireOp",EDGE,"E1768"),sQuery(id+"F11.wireOp",EDGE,"E1769"),sQuery(id+"F11.wireOp",EDGE,"E1770"),sQuery(id+"F11.wireOp",EDGE,"E1771"),sQuery(id+"F11.wireOp",EDGE,"E1772"),sQuery(id+"F11.wireOp",EDGE,"E1773"),sQuery(id+"F11.wireOp",EDGE,"E1774"),sQuery(id+"F11.wireOp",EDGE,"E1775"),sQuery(id+"F11.wireOp",EDGE,"E1776"),sQuery(id+"F11.wireOp",EDGE,"E1777"),sQuery(id+"F11.wireOp",EDGE,"E1778"),sQuery(id+"F11.wireOp",EDGE,"E1779"),sQuery(id+"F11.wireOp",EDGE,"E1780"),sQuery(id+"F11.wireOp",EDGE,"E1781"),sQuery(id+"F11.wireOp",EDGE,"E1782"),sQuery(id+"F11.wireOp",EDGE,"E1783"),sQuery(id+"F11.wireOp",EDGE,"E1784"),sQuery(id+"F11.wireOp",EDGE,"E1785"),sQuery(id+"F11.wireOp",EDGE,"E1786"),sQuery(id+"F11.wireOp",EDGE,"E1787"),sQuery(id+"F11.wireOp",EDGE,"E1788"),sQuery(id+"F11.wireOp",EDGE,"E1789"),sQuery(id+"F11.wireOp",EDGE,"E1790"),sQuery(id+"F11.wireOp",EDGE,"E1791"),sQuery(id+"F11.wireOp",EDGE,"E1792"),sQuery(id+"F11.wireOp",EDGE,"E1793"),sQuery(id+"F11.wireOp",EDGE,"E1794"),sQuery(id+"F11.wireOp",EDGE,"E1795"),sQuery(id+"F11.wireOp",EDGE,"E1796"),sQuery(id+"F11.wireOp",EDGE,"E1797"),sQuery(id+"F11.wireOp",EDGE,"E1798"),sQuery(id+"F11.wireOp",EDGE,"E1799"),sQuery(id+"F11.wireOp",EDGE,"E1800"),sQuery(id+"F11.wireOp",EDGE,"E1801"),sQuery(id+"F11.wireOp",EDGE,"E1802"),sQuery(id+"F11.wireOp",EDGE,"E1803"),sQuery(id+"F11.wireOp",EDGE,"E1804"),sQuery(id+"F11.wireOp",EDGE,"E1805"),sQuery(id+"F11.wireOp",EDGE,"E1806"),sQuery(id+"F11.wireOp",EDGE,"E1807"),sQuery(id+"F11.wireOp",EDGE,"E1808"),sQuery(id+"F11.wireOp",EDGE,"E1809"),sQuery(id+"F11.wireOp",EDGE,"E1810"),sQuery(id+"F11.wireOp",EDGE,"E1811"),sQuery(id+"F11.wireOp",EDGE,"E1812"),sQuery(id+"F11.wireOp",EDGE,"E1813"),sQuery(id+"F11.wireOp",EDGE,"E1814"),sQuery(id+"F11.wireOp",EDGE,"E1815"),sQuery(id+"F11.wireOp",EDGE,"E1816"),sQuery(id+"F11.wireOp",EDGE,"E1817"),sQuery(id+"F11.wireOp",EDGE,"E1818"),sQuery(id+"F11.wireOp",EDGE,"E1819"),sQuery(id+"F11.wireOp",EDGE,"E1820"),sQuery(id+"F11.wireOp",EDGE,"E1821"),sQuery(id+"F11.wireOp",EDGE,"E1822"),sQuery(id+"F11.wireOp",EDGE,"E1823"),sQuery(id+"F11.wireOp",EDGE,"E1824"),sQuery(id+"F11.wireOp",EDGE,"E1825"),sQuery(id+"F11.wireOp",EDGE,"E1826"),sQuery(id+"F11.wireOp",EDGE,"E1827"),sQuery(id+"F11.wireOp",EDGE,"E1828"),sQuery(id+"F11.wireOp",EDGE,"E1829"),sQuery(id+"F11.wireOp",EDGE,"E1830"),sQuery(id+"F11.wireOp",EDGE,"E1831"),sQuery(id+"F11.wireOp",EDGE,"E1832"),sQuery(id+"F11.wireOp",EDGE,"E1833"),sQuery(id+"F11.wireOp",EDGE,"E1834"),sQuery(id+"F11.wireOp",EDGE,"E1835"),sQuery(id+"F11.wireOp",EDGE,"E1836"),sQuery(id+"F11.wireOp",EDGE,"E1837"),sQuery(id+"F11.wireOp",EDGE,"E1838"),sQuery(id+"F11.wireOp",EDGE,"E1839"),sQuery(id+"F11.wireOp",EDGE,"E1840"),sQuery(id+"F11.wireOp",EDGE,"E1841"),sQuery(id+"F11.wireOp",EDGE,"E1842"),sQuery(id+"F11.wireOp",EDGE,"E1843"),sQuery(id+"F11.wireOp",EDGE,"E1844"),sQuery(id+"F11.wireOp",EDGE,"E1845"),sQuery(id+"F11.wireOp",EDGE,"E1846"),sQuery(id+"F11.wireOp",EDGE,"E1847"),sQuery(id+"F11.wireOp",EDGE,"E1848"),sQuery(id+"F11.wireOp",EDGE,"E1849"),sQuery(id+"F11.wireOp",EDGE,"E1850"),sQuery(id+"F11.wireOp",EDGE,"E1851"),sQuery(id+"F11.wireOp",EDGE,"E1852"),sQuery(id+"F11.wireOp",EDGE,"E1853"),sQuery(id+"F11.wireOp",EDGE,"E1854"),sQuery(id+"F11.wireOp",EDGE,"E1855"),sQuery(id+"F11.wireOp",EDGE,"E1856"),sQuery(id+"F11.wireOp",EDGE,"E1857"),sQuery(id+"F11.wireOp",EDGE,"E1858"),sQuery(id+"F11.wireOp",EDGE,"E1859"),sQuery(id+"F11.wireOp",EDGE,"E1860"),sQuery(id+"F11.wireOp",EDGE,"E1861"),sQuery(id+"F11.wireOp",EDGE,"E1862"),sQuery(id+"F11.wireOp",EDGE,"E1863"),sQuery(id+"F11.wireOp",EDGE,"E1864"),sQuery(id+"F11.wireOp",EDGE,"E1865"),sQuery(id+"F11.wireOp",EDGE,"E1866"),sQuery(id+"F11.wireOp",EDGE,"E1867"),sQuery(id+"F11.wireOp",EDGE,"E1868"),sQuery(id+"F11.wireOp",EDGE,"E1869"),sQuery(id+"F11.wireOp",EDGE,"E1870"),sQuery(id+"F11.wireOp",EDGE,"E1871"),sQuery(id+"F11.wireOp",EDGE,"E1872"),sQuery(id+"F11.wireOp",EDGE,"E1873"),sQuery(id+"F11.wireOp",EDGE,"E1874"),sQuery(id+"F11.wireOp",EDGE,"E1875"),sQuery(id+"F11.wireOp",EDGE,"E1876"),sQuery(id+"F11.wireOp",EDGE,"E1877"),sQuery(id+"F11.wireOp",EDGE,"E1878"),sQuery(id+"F11.wireOp",EDGE,"E1879"),sQuery(id+"F11.wireOp",EDGE,"E1880"),sQuery(id+"F11.wireOp",EDGE,"E1881"),sQuery(id+"F11.wireOp",EDGE,"E1882"),sQuery(id+"F11.wireOp",EDGE,"E1883"),sQuery(id+"F11.wireOp",EDGE,"E1884"),sQuery(id+"F11.wireOp",EDGE,"E1885"),sQuery(id+"F11.wireOp",EDGE,"E1886"),sQuery(id+"F11.wireOp",EDGE,"E1887"),sQuery(id+"F11.wireOp",EDGE,"E1888"),sQuery(id+"F11.wireOp",EDGE,"E1889"),sQuery(id+"F11.wireOp",EDGE,"E1890"),sQuery(id+"F11.wireOp",EDGE,"E1891"),sQuery(id+"F11.wireOp",EDGE,"E1892"),sQuery(id+"F11.wireOp",EDGE,"E1893"),sQuery(id+"F11.wireOp",EDGE,"E1894"),sQuery(id+"F11.wireOp",EDGE,"E1895"),sQuery(id+"F11.wireOp",EDGE,"E1896"),sQuery(id+"F11.wireOp",EDGE,"E1897"),sQuery(id+"F11.wireOp",EDGE,"E1898"),sQuery(id+"F11.wireOp",EDGE,"E1899"),sQuery(id+"F11.wireOp",EDGE,"E1900"),sQuery(id+"F11.wireOp",EDGE,"E1901"),sQuery(id+"F11.wireOp",EDGE,"E1902"),sQuery(id+"F11.wireOp",EDGE,"E1903"),sQuery(id+"F11.wireOp",EDGE,"E1904"),sQuery(id+"F11.wireOp",EDGE,"E1905"),sQuery(id+"F11.wireOp",EDGE,"E1906"),sQuery(id+"F11.wireOp",EDGE,"E1907"),sQuery(id+"F11.wireOp",EDGE,"E1908"),sQuery(id+"F11.wireOp",EDGE,"E1909"),sQuery(id+"F11.wireOp",EDGE,"E1910"),sQuery(id+"F11.wireOp",EDGE,"E1911"),sQuery(id+"F11.wireOp",EDGE,"E1912"),sQuery(id+"F11.wireOp",EDGE,"E1913"),sQuery(id+"F11.wireOp",EDGE,"E1914"),sQuery(id+"F11.wireOp",EDGE,"E1915"),sQuery(id+"F11.wireOp",EDGE,"E1916"),sQuery(id+"F11.wireOp",EDGE,"E1917"),sQuery(id+"F11.wireOp",EDGE,"E1918"),sQuery(id+"F11.wireOp",EDGE,"E1919"),sQuery(id+"F11.wireOp",EDGE,"E1920"),sQuery(id+"F11.wireOp",EDGE,"E1921"),sQuery(id+"F11.wireOp",EDGE,"E1922"),sQuery(id+"F11.wireOp",EDGE,"E1923"),sQuery(id+"F11.wireOp",EDGE,"E1924"),sQuery(id+"F11.wireOp",EDGE,"E1925"),sQuery(id+"F11.wireOp",EDGE,"E1926"),sQuery(id+"F11.wireOp",EDGE,"E1927"),sQuery(id+"F11.wireOp",EDGE,"E1928"),sQuery(id+"F11.wireOp",EDGE,"E1929"),sQuery(id+"F11.wireOp",EDGE,"E1930"),sQuery(id+"F11.wireOp",EDGE,"E1931"),sQuery(id+"F11.wireOp",EDGE,"E1932"),sQuery(id+"F11.wireOp",EDGE,"E1933"),sQuery(id+"F11.wireOp",EDGE,"E1934"),sQuery(id+"F11.wireOp",EDGE,"E1935"),sQuery(id+"F11.wireOp",EDGE,"E1936"),sQuery(id+"F11.wireOp",EDGE,"E1937"),sQuery(id+"F11.wireOp",EDGE,"E1938"),sQuery(id+"F11.wireOp",EDGE,"E1939"),sQuery(id+"F11.wireOp",EDGE,"E1940"),sQuery(id+"F11.wireOp",EDGE,"E1941"),sQuery(id+"F11.wireOp",EDGE,"E1942"),sQuery(id+"F11.wireOp",EDGE,"E1943"),sQuery(id+"F11.wireOp",EDGE,"E1944"),sQuery(id+"F11.wireOp",EDGE,"E1945"),sQuery(id+"F11.wireOp",EDGE,"E1946"),sQuery(id+"F11.wireOp",EDGE,"E1947"),sQuery(id+"F11.wireOp",EDGE,"E1948"),sQuery(id+"F11.wireOp",EDGE,"E1949"),sQuery(id+"F11.wireOp",EDGE,"E1950"),sQuery(id+"F11.wireOp",EDGE,"E1951"),sQuery(id+"F11.wireOp",EDGE,"E1952"),sQuery(id+"F11.wireOp",EDGE,"E1953"),sQuery(id+"F11.wireOp",EDGE,"E1954"),sQuery(id+"F11.wireOp",EDGE,"E1955"),sQuery(id+"F11.wireOp",EDGE,"E1956"),sQuery(id+"F11.wireOp",EDGE,"E1957"),sQuery(id+"F11.wireOp",EDGE,"E1958"),sQuery(id+"F11.wireOp",EDGE,"E1959"),sQuery(id+"F11.wireOp",EDGE,"E1960"),sQuery(id+"F11.wireOp",EDGE,"E1961"),sQuery(id+"F11.wireOp",EDGE,"E1962"),sQuery(id+"F11.wireOp",EDGE,"E1963"),sQuery(id+"F11.wireOp",EDGE,"E1964"),sQuery(id+"F11.wireOp",EDGE,"E1965"),sQuery(id+"F11.wireOp",EDGE,"E1966"),sQuery(id+"F11.wireOp",EDGE,"E1967"),sQuery(id+"F11.wireOp",EDGE,"E1968"),sQuery(id+"F11.wireOp",EDGE,"E1969"),sQuery(id+"F11.wireOp",EDGE,"E1970"),sQuery(id+"F11.wireOp",EDGE,"E1971"),sQuery(id+"F11.wireOp",EDGE,"E1972"),sQuery(id+"F11.wireOp",EDGE,"E1973"),sQuery(id+"F11.wireOp",EDGE,"E1974"),sQuery(id+"F11.wireOp",EDGE,"E1975"),sQuery(id+"F11.wireOp",EDGE,"E1976"),sQuery(id+"F11.wireOp",EDGE,"E1977"),sQuery(id+"F11.wireOp",EDGE,"E1978"),sQuery(id+"F11.wireOp",EDGE,"E1979"),sQuery(id+"F11.wireOp",EDGE,"E1980"),sQuery(id+"F11.wireOp",EDGE,"E1981"),sQuery(id+"F11.wireOp",EDGE,"E1982"),sQuery(id+"F11.wireOp",EDGE,"E1983"),sQuery(id+"F11.wireOp",EDGE,"E1984"),sQuery(id+"F11.wireOp",EDGE,"E1985"),sQuery(id+"F11.wireOp",EDGE,"E1986"),sQuery(id+"F11.wireOp",EDGE,"E1987"),sQuery(id+"F11.wireOp",EDGE,"E1988"),sQuery(id+"F11.wireOp",EDGE,"E1989"),sQuery(id+"F11.wireOp",EDGE,"E1990"),sQuery(id+"F11.wireOp",EDGE,"E1991"),sQuery(id+"F11.wireOp",EDGE,"E1992"),sQuery(id+"F11.wireOp",EDGE,"E1993"),sQuery(id+"F11.wireOp",EDGE,"E1994"),sQuery(id+"F11.wireOp",EDGE,"E1995"),sQuery(id+"F11.wireOp",EDGE,"E1996"),sQuery(id+"F11.wireOp",EDGE,"E1997"),sQuery(id+"F11.wireOp",EDGE,"E1998"),sQuery(id+"F11.wireOp",EDGE,"E1999"),sQuery(id+"F11.wireOp",EDGE,"E2000"),sQuery(id+"F11.wireOp",EDGE,"E2001"),sQuery(id+"F11.wireOp",EDGE,"E2002"),sQuery(id+"F11.wireOp",EDGE,"E2003"),sQuery(id+"F11.wireOp",EDGE,"E2004"),sQuery(id+"F11.wireOp",EDGE,"E2005"),sQuery(id+"F11.wireOp",EDGE,"E2006"),sQuery(id+"F11.wireOp",EDGE,"E2007"),sQuery(id+"F11.wireOp",EDGE,"E2008"),sQuery(id+"F11.wireOp",EDGE,"E2009"),sQuery(id+"F11.wireOp",EDGE,"E2010"),sQuery(id+"F11.wireOp",EDGE,"E2011"),sQuery(id+"F11.wireOp",EDGE,"E2012"),sQuery(id+"F11.wireOp",EDGE,"E2013"),sQuery(id+"F11.wireOp",EDGE,"E2014"),sQuery(id+"F11.wireOp",EDGE,"E2015"),sQuery(id+"F11.wireOp",EDGE,"E2016"),sQuery(id+"F11.wireOp",EDGE,"E2017"),sQuery(id+"F11.wireOp",EDGE,"E2018"),sQuery(id+"F11.wireOp",EDGE,"E2019"),sQuery(id+"F11.wireOp",EDGE,"E2020"),sQuery(id+"F11.wireOp",EDGE,"E2021"),sQuery(id+"F11.wireOp",EDGE,"E2022"),sQuery(id+"F11.wireOp",EDGE,"E2023"),sQuery(id+"F11.wireOp",EDGE,"E2024"),sQuery(id+"F11.wireOp",EDGE,"E2025"),sQuery(id+"F11.wireOp",EDGE,"E2026"),sQuery(id+"F11.wireOp",EDGE,"E2027"),sQuery(id+"F11.wireOp",EDGE,"E2028"),sQuery(id+"F11.wireOp",EDGE,"E2029"),sQuery(id+"F11.wireOp",EDGE,"E2030"),sQuery(id+"F11.wireOp",EDGE,"E2031"),sQuery(id+"F11.wireOp",EDGE,"E2032"),sQuery(id+"F11.wireOp",EDGE,"E2033"),sQuery(id+"F11.wireOp",EDGE,"E2034"),sQuery(id+"F11.wireOp",EDGE,"E2035"),sQuery(id+"F11.wireOp",EDGE,"E2036"),sQuery(id+"F11.wireOp",EDGE,"E2037"),sQuery(id+"F11.wireOp",EDGE,"E2038"),sQuery(id+"F11.wireOp",EDGE,"E2039"),sQuery(id+"F11.wireOp",EDGE,"E2040"),sQuery(id+"F11.wireOp",EDGE,"E2041"),sQuery(id+"F11.wireOp",EDGE,"E2042"),sQuery(id+"F11.wireOp",EDGE,"E2043"),sQuery(id+"F11.wireOp",EDGE,"E2044"),sQuery(id+"F11.wireOp",EDGE,"E2045"),sQuery(id+"F11.wireOp",EDGE,"E2046"),sQuery(id+"F11.wireOp",EDGE,"E2047"),sQuery(id+"F11.wireOp",EDGE,"E2048"),sQuery(id+"F11.wireOp",EDGE,"E2049"),sQuery(id+"F11.wireOp",EDGE,"E2050"),sQuery(id+"F11.wireOp",EDGE,"E2051"),sQuery(id+"F11.wireOp",EDGE,"E2052"),sQuery(id+"F11.wireOp",EDGE,"E2053"),sQuery(id+"F11.wireOp",EDGE,"E2054"),sQuery(id+"F11.wireOp",EDGE,"E2055"),sQuery(id+"F11.wireOp",EDGE,"E2056"),sQuery(id+"F11.wireOp",EDGE,"E2057"),sQuery(id+"F11.wireOp",EDGE,"E2058"),sQuery(id+"F11.wireOp",EDGE,"E2059"),sQuery(id+"F11.wireOp",EDGE,"E2060"),sQuery(id+"F11.wireOp",EDGE,"E2061"),sQuery(id+"F11.wireOp",EDGE,"E2062"),sQuery(id+"F11.wireOp",EDGE,"E2063"),sQuery(id+"F11.wireOp",EDGE,"E2064"),sQuery(id+"F11.wireOp",EDGE,"E2065"),sQuery(id+"F11.wireOp",EDGE,"E2066"),sQuery(id+"F11.wireOp",EDGE,"E2067"),sQuery(id+"F11.wireOp",EDGE,"E2068"),sQuery(id+"F11.wireOp",EDGE,"E2069"),sQuery(id+"F11.wireOp",EDGE,"E2070"),sQuery(id+"F11.wireOp",EDGE,"E2071"),sQuery(id+"F11.wireOp",EDGE,"E2072"),sQuery(id+"F11.wireOp",EDGE,"E2073"),sQuery(id+"F11.wireOp",EDGE,"E2074"),sQuery(id+"F11.wireOp",EDGE,"E2075"),sQuery(id+"F11.wireOp",EDGE,"E2076"),sQuery(id+"F11.wireOp",EDGE,"E2077"),sQuery(id+"F11.wireOp",EDGE,"E2078"),sQuery(id+"F11.wireOp",EDGE,"E2079"),sQuery(id+"F11.wireOp",EDGE,"E2080"),sQuery(id+"F11.wireOp",EDGE,"E2081"),sQuery(id+"F11.wireOp",EDGE,"E2082"),sQuery(id+"F11.wireOp",EDGE,"E2083"),sQuery(id+"F11.wireOp",EDGE,"E2084"),sQuery(id+"F11.wireOp",EDGE,"E2085"),sQuery(id+"F11.wireOp",EDGE,"E2086"),sQuery(id+"F11.wireOp",EDGE,"E2087"),sQuery(id+"F11.wireOp",EDGE,"E2088"),sQuery(id+"F11.wireOp",EDGE,"E2089"),sQuery(id+"F11.wireOp",EDGE,"E2090"),sQuery(id+"F11.wireOp",EDGE,"E2091"),sQuery(id+"F11.wireOp",EDGE,"E2092"),sQuery(id+"F11.wireOp",EDGE,"E2093"),sQuery(id+"F11.wireOp",EDGE,"E2094"),sQuery(id+"F11.wireOp",EDGE,"E2095"),sQuery(id+"F11.wireOp",EDGE,"E2096"),sQuery(id+"F11.wireOp",EDGE,"E2097"),sQuery(id+"F11.wireOp",EDGE,"E2098"),sQuery(id+"F11.wireOp",EDGE,"E2099"),sQuery(id+"F11.wireOp",EDGE,"E2100"),sQuery(id+"F11.wireOp",EDGE,"E2101"),sQuery(id+"F11.wireOp",EDGE,"E2102"),sQuery(id+"F11.wireOp",EDGE,"E2103"),sQuery(id+"F11.wireOp",EDGE,"E2104"),sQuery(id+"F11.wireOp",EDGE,"E2105"),sQuery(id+"F11.wireOp",EDGE,"E2106"),sQuery(id+"F11.wireOp",EDGE,"E2107"),sQuery(id+"F11.wireOp",EDGE,"E2108"),sQuery(id+"F11.wireOp",EDGE,"E2109"),sQuery(id+"F11.wireOp",EDGE,"E2110"),sQuery(id+"F11.wireOp",EDGE,"E2111"),sQuery(id+"F11.wireOp",EDGE,"E2112"),sQuery(id+"F11.wireOp",EDGE,"E2113"),sQuery(id+"F11.wireOp",EDGE,"E2114"),sQuery(id+"F11.wireOp",EDGE,"E2115"),sQuery(id+"F11.wireOp",EDGE,"E2116"),sQuery(id+"F11.wireOp",EDGE,"E2117"),sQuery(id+"F11.wireOp",EDGE,"E2118"),sQuery(id+"F11.wireOp",EDGE,"E2119"),sQuery(id+"F11.wireOp",EDGE,"E2120"),sQuery(id+"F11.wireOp",EDGE,"E2121"),sQuery(id+"F11.wireOp",EDGE,"E2122"),sQuery(id+"F11.wireOp",EDGE,"E2123"),sQuery(id+"F11.wireOp",EDGE,"E2124"),sQuery(id+"F11.wireOp",EDGE,"E2125"),sQuery(id+"F11.wireOp",EDGE,"E2126"),sQuery(id+"F11.wireOp",EDGE,"E2127"),sQuery(id+"F11.wireOp",EDGE,"E2128"),sQuery(id+"F11.wireOp",EDGE,"E2129"),sQuery(id+"F11.wireOp",EDGE,"E2130"),sQuery(id+"F11.wireOp",EDGE,"E2131"),sQuery(id+"F11.wireOp",EDGE,"E2132"),sQuery(id+"F11.wireOp",EDGE,"E2133"),sQuery(id+"F11.wireOp",EDGE,"E2134"),sQuery(id+"F11.wireOp",EDGE,"E2135"),sQuery(id+"F11.wireOp",EDGE,"E2136"),sQuery(id+"F11.wireOp",EDGE,"E2137"),sQuery(id+"F11.wireOp",EDGE,"E2138"),sQuery(id+"F11.wireOp",EDGE,"E2139"),sQuery(id+"F11.wireOp",EDGE,"E2140"),sQuery(id+"F11.wireOp",EDGE,"E2141"),sQuery(id+"F11.wireOp",EDGE,"E2142"),sQuery(id+"F11.wireOp",EDGE,"E2143"),sQuery(id+"F11.wireOp",EDGE,"E2144"),sQuery(id+"F11.wireOp",EDGE,"E2145"),sQuery(id+"F11.wireOp",EDGE,"E2146"),sQuery(id+"F11.wireOp",EDGE,"E2147"),sQuery(id+"F11.wireOp",EDGE,"E2148"),sQuery(id+"F11.wireOp",EDGE,"E2149"),sQuery(id+"F11.wireOp",EDGE,"E2150"),sQuery(id+"F11.wireOp",EDGE,"E2151"),sQuery(id+"F11.wireOp",EDGE,"E2152"),sQuery(id+"F11.wireOp",EDGE,"E2153"),sQuery(id+"F11.wireOp",EDGE,"E2154"),sQuery(id+"F11.wireOp",EDGE,"E2155"),sQuery(id+"F11.wireOp",EDGE,"E2156"),sQuery(id+"F11.wireOp",EDGE,"E2157"),sQuery(id+"F11.wireOp",EDGE,"E2158"),sQuery(id+"F11.wireOp",EDGE,"E2159"),sQuery(id+"F11.wireOp",EDGE,"E2160"),sQuery(id+"F11.wireOp",EDGE,"E2161"),sQuery(id+"F11.wireOp",EDGE,"E2162"),sQuery(id+"F11.wireOp",EDGE,"E2163"),sQuery(id+"F11.wireOp",EDGE,"E2164"),sQuery(id+"F11.wireOp",EDGE,"E2165"),sQuery(id+"F11.wireOp",EDGE,"E2166"),sQuery(id+"F11.wireOp",EDGE,"E2167"),sQuery(id+"F11.wireOp",EDGE,"E2168"),sQuery(id+"F11.wireOp",EDGE,"E2169"),sQuery(id+"F11.wireOp",EDGE,"E2170"),sQuery(id+"F11.wireOp",EDGE,"E2171"),sQuery(id+"F11.wireOp",EDGE,"E2172"),sQuery(id+"F11.wireOp",EDGE,"E2173"),sQuery(id+"F11.wireOp",EDGE,"E2174"),sQuery(id+"F11.wireOp",EDGE,"E2175"),sQuery(id+"F11.wireOp",EDGE,"E2176"),sQuery(id+"F11.wireOp",EDGE,"E2177"),sQuery(id+"F11.wireOp",EDGE,"E2178"),sQuery(id+"F11.wireOp",EDGE,"E2179"),sQuery(id+"F11.wireOp",EDGE,"E2180"),sQuery(id+"F11.wireOp",EDGE,"E2181"),sQuery(id+"F11.wireOp",EDGE,"E2182"),sQuery(id+"F11.wireOp",EDGE,"E2183"),sQuery(id+"F11.wireOp",EDGE,"E2184"),sQuery(id+"F11.wireOp",EDGE,"E2185"),sQuery(id+"F11.wireOp",EDGE,"E2186"),sQuery(id+"F11.wireOp",EDGE,"E2187"),sQuery(id+"F11.wireOp",EDGE,"E2188"),sQuery(id+"F11.wireOp",EDGE,"E2189"),sQuery(id+"F11.wireOp",EDGE,"E2190"),sQuery(id+"F11.wireOp",EDGE,"E2191"),sQuery(id+"F11.wireOp",EDGE,"E2192"),sQuery(id+"F11.wireOp",EDGE,"E2193"),sQuery(id+"F11.wireOp",EDGE,"E2194"),sQuery(id+"F11.wireOp",EDGE,"E2195"),sQuery(id+"F11.wireOp",EDGE,"E2196"),sQuery(id+"F11.wireOp",EDGE,"E2197"),sQuery(id+"F11.wireOp",EDGE,"E2198"),sQuery(id+"F11.wireOp",EDGE,"E2199"),sQuery(id+"F11.wireOp",EDGE,"E2200"),sQuery(id+"F11.wireOp",EDGE,"E2201"),sQuery(id+"F11.wireOp",EDGE,"E2202"),sQuery(id+"F11.wireOp",EDGE,"E2203"),sQuery(id+"F11.wireOp",EDGE,"E2204"),sQuery(id+"F11.wireOp",EDGE,"E2205"),sQuery(id+"F11.wireOp",EDGE,"E2206"),sQuery(id+"F11.wireOp",EDGE,"E2207"),sQuery(id+"F11.wireOp",EDGE,"E2208"),sQuery(id+"F11.wireOp",EDGE,"E2209"),sQuery(id+"F11.wireOp",EDGE,"E2210"),sQuery(id+"F11.wireOp",EDGE,"E2211"),sQuery(id+"F11.wireOp",EDGE,"E2212"),sQuery(id+"F11.wireOp",EDGE,"E2213"),sQuery(id+"F11.wireOp",EDGE,"E2214"),sQuery(id+"F11.wireOp",EDGE,"E2215"),sQuery(id+"F11.wireOp",EDGE,"E2216"),sQuery(id+"F11.wireOp",EDGE,"E2217"),sQuery(id+"F11.wireOp",EDGE,"E2218"),sQuery(id+"F11.wireOp",EDGE,"E2219"),sQuery(id+"F11.wireOp",EDGE,"E2220"),sQuery(id+"F11.wireOp",EDGE,"E2221"),sQuery(id+"F11.wireOp",EDGE,"E2222"),sQuery(id+"F11.wireOp",EDGE,"E2223"),sQuery(id+"F11.wireOp",EDGE,"E2224"),sQuery(id+"F11.wireOp",EDGE,"E2225"),sQuery(id+"F11.wireOp",EDGE,"E2226"),sQuery(id+"F11.wireOp",EDGE,"E2227"),sQuery(id+"F11.wireOp",EDGE,"E2228"),sQuery(id+"F11.wireOp",EDGE,"E2229"),sQuery(id+"F11.wireOp",EDGE,"E2230"),sQuery(id+"F11.wireOp",EDGE,"E2231"),sQuery(id+"F11.wireOp",EDGE,"E2232"),sQuery(id+"F11.wireOp",EDGE,"E2233"),sQuery(id+"F11.wireOp",EDGE,"E2234"),sQuery(id+"F11.wireOp",EDGE,"E2235"),sQuery(id+"F11.wireOp",EDGE,"E2236"),sQuery(id+"F11.wireOp",EDGE,"E2237"),sQuery(id+"F11.wireOp",EDGE,"E2238"),sQuery(id+"F11.wireOp",EDGE,"E2239"),sQuery(id+"F11.wireOp",EDGE,"E2240"),sQuery(id+"F11.wireOp",EDGE,"E2241"),sQuery(id+"F11.wireOp",EDGE,"E2242"),sQuery(id+"F11.wireOp",EDGE,"E2243"),sQuery(id+"F11.wireOp",EDGE,"E2244"),sQuery(id+"F11.wireOp",EDGE,"E2245"),sQuery(id+"F11.wireOp",EDGE,"E2246"),sQuery(id+"F11.wireOp",EDGE,"E2247"),sQuery(id+"F11.wireOp",EDGE,"E2248"),sQuery(id+"F11.wireOp",EDGE,"E2249"),sQuery(id+"F11.wireOp",EDGE,"E2250"),sQuery(id+"F11.wireOp",EDGE,"E2251"),sQuery(id+"F11.wireOp",EDGE,"E2252"),sQuery(id+"F11.wireOp",EDGE,"E2253"),sQuery(id+"F11.wireOp",EDGE,"E2254"),sQuery(id+"F11.wireOp",EDGE,"E2255"),sQuery(id+"F11.wireOp",EDGE,"E2256"),sQuery(id+"F11.wireOp",EDGE,"E2257"),sQuery(id+"F11.wireOp",EDGE,"E2258"),sQuery(id+"F11.wireOp",EDGE,"E2259"),sQuery(id+"F11.wireOp",EDGE,"E2260"),sQuery(id+"F11.wireOp",EDGE,"E2261"),sQuery(id+"F11.wireOp",EDGE,"E2262"),sQuery(id+"F11.wireOp",EDGE,"E2263"),sQuery(id+"F11.wireOp",EDGE,"E2264"),sQuery(id+"F11.wireOp",EDGE,"E2265"),sQuery(id+"F11.wireOp",EDGE,"E2266"),sQuery(id+"F11.wireOp",EDGE,"E2267"),sQuery(id+"F11.wireOp",EDGE,"E2268"),sQuery(id+"F11.wireOp",EDGE,"E2269"),sQuery(id+"F11.wireOp",EDGE,"E2270"),sQuery(id+"F11.wireOp",EDGE,"E2271"),sQuery(id+"F11.wireOp",EDGE,"E2272"),sQuery(id+"F11.wireOp",EDGE,"E2273"),sQuery(id+"F11.wireOp",EDGE,"E2274"),sQuery(id+"F11.wireOp",EDGE,"E2275"),sQuery(id+"F11.wireOp",EDGE,"E2276"),sQuery(id+"F11.wireOp",EDGE,"E2277"),sQuery(id+"F11.wireOp",EDGE,"E2278"),sQuery(id+"F11.wireOp",EDGE,"E2279"),sQuery(id+"F11.wireOp",EDGE,"E2280"),sQuery(id+"F11.wireOp",EDGE,"E2281"),sQuery(id+"F11.wireOp",EDGE,"E2282"),sQuery(id+"F11.wireOp",EDGE,"E2283"),sQuery(id+"F11.wireOp",EDGE,"E2284"),sQuery(id+"F11.wireOp",EDGE,"E2285"),sQuery(id+"F11.wireOp",EDGE,"E2286"),sQuery(id+"F11.wireOp",EDGE,"E2287"),sQuery(id+"F11.wireOp",EDGE,"E2288"),sQuery(id+"F11.wireOp",EDGE,"E2289"),sQuery(id+"F11.wireOp",EDGE,"E2290"),sQuery(id+"F11.wireOp",EDGE,"E2291"),sQuery(id+"F11.wireOp",EDGE,"E2292"),sQuery(id+"F11.wireOp",EDGE,"E2293"),sQuery(id+"F11.wireOp",EDGE,"E2294"),sQuery(id+"F11.wireOp",EDGE,"E2295"),sQuery(id+"F11.wireOp",EDGE,"E2296"),sQuery(id+"F11.wireOp",EDGE,"E2297"),sQuery(id+"F11.wireOp",EDGE,"E2298"),sQuery(id+"F11.wireOp",EDGE,"E2299"),sQuery(id+"F11.wireOp",EDGE,"E2300"),sQuery(id+"F11.wireOp",EDGE,"E2301"),sQuery(id+"F11.wireOp",EDGE,"E2302"),sQuery(id+"F11.wireOp",EDGE,"E2303"),sQuery(id+"F11.wireOp",EDGE,"E2304"),sQuery(id+"F11.wireOp",EDGE,"E2305"),sQuery(id+"F11.wireOp",EDGE,"E2306"),sQuery(id+"F11.wireOp",EDGE,"E2307"),sQuery(id+"F11.wireOp",EDGE,"E2308"),sQuery(id+"F11.wireOp",EDGE,"E2309"),sQuery(id+"F11.wireOp",EDGE,"E2310"),sQuery(id+"F11.wireOp",EDGE,"E2311"),sQuery(id+"F11.wireOp",EDGE,"E2312"),sQuery(id+"F11.wireOp",EDGE,"E2313"),sQuery(id+"F11.wireOp",EDGE,"E2314"),sQuery(id+"F11.wireOp",EDGE,"E2315"),sQuery(id+"F11.wireOp",EDGE,"E2316"),sQuery(id+"F11.wireOp",EDGE,"E2317"),sQuery(id+"F11.wireOp",EDGE,"E2318"),sQuery(id+"F11.wireOp",EDGE,"E2319"),sQuery(id+"F11.wireOp",EDGE,"E2320"),sQuery(id+"F11.wireOp",EDGE,"E2321"),sQuery(id+"F11.wireOp",EDGE,"E2322"),sQuery(id+"F11.wireOp",EDGE,"E2323"),sQuery(id+"F11.wireOp",EDGE,"E2324"),sQuery(id+"F11.wireOp",EDGE,"E2325"),sQuery(id+"F11.wireOp",EDGE,"E2326"),sQuery(id+"F11.wireOp",EDGE,"E2327"),sQuery(id+"F11.wireOp",EDGE,"E2328"),sQuery(id+"F11.wireOp",EDGE,"E2329"),sQuery(id+"F11.wireOp",EDGE,"E2330"),sQuery(id+"F11.wireOp",EDGE,"E2331"),sQuery(id+"F11.wireOp",EDGE,"E2332"),sQuery(id+"F11.wireOp",EDGE,"E2333"),sQuery(id+"F11.wireOp",EDGE,"E2334"),sQuery(id+"F11.wireOp",EDGE,"E2335"),sQuery(id+"F11.wireOp",EDGE,"E2336"),sQuery(id+"F11.wireOp",EDGE,"E2337"),sQuery(id+"F11.wireOp",EDGE,"E2338"),sQuery(id+"F11.wireOp",EDGE,"E2339"),sQuery(id+"F11.wireOp",EDGE,"E2340"),sQuery(id+"F11.wireOp",EDGE,"E2341"),sQuery(id+"F11.wireOp",EDGE,"E2342"),sQuery(id+"F11.wireOp",EDGE,"E2343"),sQuery(id+"F11.wireOp",EDGE,"E2344"),sQuery(id+"F11.wireOp",EDGE,"E2345"),sQuery(id+"F11.wireOp",EDGE,"E2346"),sQuery(id+"F11.wireOp",EDGE,"E2347"),sQuery(id+"F11.wireOp",EDGE,"E2348"),sQuery(id+"F11.wireOp",EDGE,"E2349"),sQuery(id+"F11.wireOp",EDGE,"E2350"),sQuery(id+"F11.wireOp",EDGE,"E2351"),sQuery(id+"F11.wireOp",EDGE,"E2352"),sQuery(id+"F11.wireOp",EDGE,"E2353"),sQuery(id+"F11.wireOp",EDGE,"E2354"),sQuery(id+"F11.wireOp",EDGE,"E2355"),sQuery(id+"F11.wireOp",EDGE,"E2356"),sQuery(id+"F11.wireOp",EDGE,"E2357"),sQuery(id+"F11.wireOp",EDGE,"E2358"),sQuery(id+"F11.wireOp",EDGE,"E2359"),sQuery(id+"F11.wireOp",EDGE,"E2360"),sQuery(id+"F11.wireOp",EDGE,"E2361"),sQuery(id+"F11.wireOp",EDGE,"E2362"),sQuery(id+"F11.wireOp",EDGE,"E2363"),sQuery(id+"F11.wireOp",EDGE,"E2364"),sQuery(id+"F11.wireOp",EDGE,"E2365"),sQuery(id+"F11.wireOp",EDGE,"E2366"),sQuery(id+"F11.wireOp",EDGE,"E2367"),sQuery(id+"F11.wireOp",EDGE,"E2368"),sQuery(id+"F11.wireOp",EDGE,"E2369"),sQuery(id+"F11.wireOp",EDGE,"E2370"),sQuery(id+"F11.wireOp",EDGE,"E2371"),sQuery(id+"F11.wireOp",EDGE,"E2372"),sQuery(id+"F11.wireOp",EDGE,"E2373"),sQuery(id+"F11.wireOp",EDGE,"E2374"),sQuery(id+"F11.wireOp",EDGE,"E2375"),sQuery(id+"F11.wireOp",EDGE,"E2376"),sQuery(id+"F11.wireOp",EDGE,"E2377"),sQuery(id+"F11.wireOp",EDGE,"E2378"),sQuery(id+"F11.wireOp",EDGE,"E2379"),sQuery(id+"F11.wireOp",EDGE,"E2380"),sQuery(id+"F11.wireOp",EDGE,"E2381"),sQuery(id+"F11.wireOp",EDGE,"E2382"),sQuery(id+"F11.wireOp",EDGE,"E2383"),sQuery(id+"F11.wireOp",EDGE,"E2384"),sQuery(id+"F11.wireOp",EDGE,"E2385"),sQuery(id+"F11.wireOp",EDGE,"E2386"),sQuery(id+"F11.wireOp",EDGE,"E2387"),sQuery(id+"F11.wireOp",EDGE,"E2388"),sQuery(id+"F11.wireOp",EDGE,"E2389"),sQuery(id+"F11.wireOp",EDGE,"E2390"),sQuery(id+"F11.wireOp",EDGE,"E2391"),sQuery(id+"F11.wireOp",EDGE,"E2392"),sQuery(id+"F11.wireOp",EDGE,"E2393"),sQuery(id+"F11.wireOp",EDGE,"E2394"),sQuery(id+"F11.wireOp",EDGE,"E2395"),sQuery(id+"F11.wireOp",EDGE,"E2396"),sQuery(id+"F11.wireOp",EDGE,"E2397"),sQuery(id+"F11.wireOp",EDGE,"E2398"),sQuery(id+"F11.wireOp",EDGE,"E2399"),sQuery(id+"F11.wireOp",EDGE,"E2400"),sQuery(id+"F11.wireOp",EDGE,"E2401"),sQuery(id+"F11.wireOp",EDGE,"E2402"),sQuery(id+"F11.wireOp",EDGE,"E2403"),sQuery(id+"F11.wireOp",EDGE,"E2404"),sQuery(id+"F11.wireOp",EDGE,"E2405"),sQuery(id+"F11.wireOp",EDGE,"E2406"),sQuery(id+"F11.wireOp",EDGE,"E2407"),sQuery(id+"F11.wireOp",EDGE,"E2408"),sQuery(id+"F11.wireOp",EDGE,"E2409"),sQuery(id+"F11.wireOp",EDGE,"E2410"),sQuery(id+"F11.wireOp",EDGE,"E2411"),sQuery(id+"F11.wireOp",EDGE,"E2412"),sQuery(id+"F11.wireOp",EDGE,"E2413"),sQuery(id+"F11.wireOp",EDGE,"E2414"),sQuery(id+"F11.wireOp",EDGE,"E2415"),sQuery(id+"F11.wireOp",EDGE,"E2416"),sQuery(id+"F11.wireOp",EDGE,"E2417"),sQuery(id+"F11.wireOp",EDGE,"E2418"),sQuery(id+"F11.wireOp",EDGE,"E2419"),sQuery(id+"F11.wireOp",EDGE,"E2420"),sQuery(id+"F11.wireOp",EDGE,"E2421"),sQuery(id+"F11.wireOp",EDGE,"E2422"),sQuery(id+"F11.wireOp",EDGE,"E2423"),sQuery(id+"F11.wireOp",EDGE,"E2424"),sQuery(id+"F11.wireOp",EDGE,"E2425"),sQuery(id+"F11.wireOp",EDGE,"E2426"),sQuery(id+"F11.wireOp",EDGE,"E2427"),sQuery(id+"F11.wireOp",EDGE,"E2428"),sQuery(id+"F11.wireOp",EDGE,"E2429"),sQuery(id+"F11.wireOp",EDGE,"E2430"),sQuery(id+"F11.wireOp",EDGE,"E2431"),sQuery(id+"F11.wireOp",EDGE,"E2432"),sQuery(id+"F11.wireOp",EDGE,"E2433"),sQuery(id+"F11.wireOp",EDGE,"E2434"),sQuery(id+"F11.wireOp",EDGE,"E2435"),sQuery(id+"F11.wireOp",EDGE,"E2436"),sQuery(id+"F11.wireOp",EDGE,"E2437"),sQuery(id+"F11.wireOp",EDGE,"E2438"),sQuery(id+"F11.wireOp",EDGE,"E2439"),sQuery(id+"F11.wireOp",EDGE,"E2440"),sQuery(id+"F11.wireOp",EDGE,"E2441"),sQuery(id+"F11.wireOp",EDGE,"E2442"),sQuery(id+"F11.wireOp",EDGE,"E2443"),sQuery(id+"F11.wireOp",EDGE,"E2444"),sQuery(id+"F11.wireOp",EDGE,"E2445"),sQuery(id+"F11.wireOp",EDGE,"E2446"),sQuery(id+"F11.wireOp",EDGE,"E2447"),sQuery(id+"F11.wireOp",EDGE,"E2448"),sQuery(id+"F11.wireOp",EDGE,"E2449"),sQuery(id+"F11.wireOp",EDGE,"E2450"),sQuery(id+"F11.wireOp",EDGE,"E2451"),sQuery(id+"F11.wireOp",EDGE,"E2452"),sQuery(id+"F11.wireOp",EDGE,"E2453"),sQuery(id+"F11.wireOp",EDGE,"E2454"),sQuery(id+"F11.wireOp",EDGE,"E2455"),sQuery(id+"F11.wireOp",EDGE,"E2456"),sQuery(id+"F11.wireOp",EDGE,"E2457"),sQuery(id+"F11.wireOp",EDGE,"E2458"),sQuery(id+"F11.wireOp",EDGE,"E2459"),sQuery(id+"F11.wireOp",EDGE,"E2460"),sQuery(id+"F11.wireOp",EDGE,"E2461"),sQuery(id+"F11.wireOp",EDGE,"E2462"),sQuery(id+"F11.wireOp",EDGE,"E2463"),sQuery(id+"F11.wireOp",EDGE,"E2464"),sQuery(id+"F11.wireOp",EDGE,"E2465"),sQuery(id+"F11.wireOp",EDGE,"E2466"),sQuery(id+"F11.wireOp",EDGE,"E2467"),sQuery(id+"F11.wireOp",EDGE,"E2468"),sQuery(id+"F11.wireOp",EDGE,"E2469"),sQuery(id+"F11.wireOp",EDGE,"E2470"),sQuery(id+"F11.wireOp",EDGE,"E2471"),sQuery(id+"F11.wireOp",EDGE,"E2472"),sQuery(id+"F11.wireOp",EDGE,"E2473"),sQuery(id+"F11.wireOp",EDGE,"E2474"),sQuery(id+"F11.wireOp",EDGE,"E2475"),sQuery(id+"F11.wireOp",EDGE,"E2476"),sQuery(id+"F11.wireOp",EDGE,"E2477"),sQuery(id+"F11.wireOp",EDGE,"E2478"),sQuery(id+"F11.wireOp",EDGE,"E2479"),sQuery(id+"F11.wireOp",EDGE,"E2480"),sQuery(id+"F11.wireOp",EDGE,"E2481"),sQuery(id+"F11.wireOp",EDGE,"E2482"),sQuery(id+"F11.wireOp",EDGE,"E2483"),sQuery(id+"F11.wireOp",EDGE,"E2484"),sQuery(id+"F11.wireOp",EDGE,"E2485"),sQuery(id+"F11.wireOp",EDGE,"E2486"),sQuery(id+"F11.wireOp",EDGE,"E2487"),sQuery(id+"F11.wireOp",EDGE,"E2488"),sQuery(id+"F11.wireOp",EDGE,"E2489"),sQuery(id+"F11.wireOp",EDGE,"E2490"),sQuery(id+"F11.wireOp",EDGE,"E2491"),sQuery(id+"F11.wireOp",EDGE,"E2492"),sQuery(id+"F11.wireOp",EDGE,"E2493"),sQuery(id+"F11.wireOp",EDGE,"E2494"),sQuery(id+"F11.wireOp",EDGE,"E2495"),sQuery(id+"F11.wireOp",EDGE,"E2496"),sQuery(id+"F11.wireOp",EDGE,"E2497"),sQuery(id+"F11.wireOp",EDGE,"E2498"),sQuery(id+"F11.wireOp",EDGE,"E2499"),sQuery(id+"F11.wireOp",EDGE,"E2500"),sQuery(id+"F11.wireOp",EDGE,"E2501"),sQuery(id+"F11.wireOp",EDGE,"E2502"),sQuery(id+"F11.wireOp",EDGE,"E2503"),sQuery(id+"F11.wireOp",EDGE,"E2504"),sQuery(id+"F11.wireOp",EDGE,"E2505"),sQuery(id+"F11.wireOp",EDGE,"E2506"),sQuery(id+"F11.wireOp",EDGE,"E2507"),sQuery(id+"F11.wireOp",EDGE,"E2508"),sQuery(id+"F11.wireOp",EDGE,"E2509"),sQuery(id+"F11.wireOp",EDGE,"E2510"),sQuery(id+"F11.wireOp",EDGE,"E2511"),sQuery(id+"F11.wireOp",EDGE,"E2512"),sQuery(id+"F11.wireOp",EDGE,"E2513"),sQuery(id+"F11.wireOp",EDGE,"E2514"),sQuery(id+"F11.wireOp",EDGE,"E2515"),sQuery(id+"F11.wireOp",EDGE,"E2516"),sQuery(id+"F11.wireOp",EDGE,"E2517"),sQuery(id+"F11.wireOp",EDGE,"E2518"),sQuery(id+"F11.wireOp",EDGE,"E2519"),sQuery(id+"F11.wireOp",EDGE,"E2520"),sQuery(id+"F11.wireOp",EDGE,"E2521"),sQuery(id+"F11.wireOp",EDGE,"E2522"),sQuery(id+"F11.wireOp",EDGE,"E2523"),sQuery(id+"F11.wireOp",EDGE,"E2524"),sQuery(id+"F11.wireOp",EDGE,"E2525"),sQuery(id+"F11.wireOp",EDGE,"E2526"),sQuery(id+"F11.wireOp",EDGE,"E2527"),sQuery(id+"F11.wireOp",EDGE,"E2528"),sQuery(id+"F11.wireOp",EDGE,"E2529"),sQuery(id+"F11.wireOp",EDGE,"E2530"),sQuery(id+"F11.wireOp",EDGE,"E2531"),sQuery(id+"F11.wireOp",EDGE,"E2532"),sQuery(id+"F11.wireOp",EDGE,"E2533"),sQuery(id+"F11.wireOp",EDGE,"E2534"),sQuery(id+"F11.wireOp",EDGE,"E2535"),sQuery(id+"F11.wireOp",EDGE,"E2536"),sQuery(id+"F11.wireOp",EDGE,"E2537"),sQuery(id+"F11.wireOp",EDGE,"E2538"),sQuery(id+"F11.wireOp",EDGE,"E2539"),sQuery(id+"F11.wireOp",EDGE,"E2540"),sQuery(id+"F11.wireOp",EDGE,"E2541"),sQuery(id+"F11.wireOp",EDGE,"E2542"),sQuery(id+"F11.wireOp",EDGE,"E2543"),sQuery(id+"F11.wireOp",EDGE,"E2544"),sQuery(id+"F11.wireOp",EDGE,"E2545"),sQuery(id+"F11.wireOp",EDGE,"E2546"),sQuery(id+"F11.wireOp",EDGE,"E2547"),sQuery(id+"F11.wireOp",EDGE,"E2548"),sQuery(id+"F11.wireOp",EDGE,"E2549"),sQuery(id+"F11.wireOp",EDGE,"E2550"),sQuery(id+"F11.wireOp",EDGE,"E2551"),sQuery(id+"F11.wireOp",EDGE,"E2552"),sQuery(id+"F11.wireOp",EDGE,"E2553"),sQuery(id+"F11.wireOp",EDGE,"E2554"),sQuery(id+"F11.wireOp",EDGE,"E2555"),sQuery(id+"F11.wireOp",EDGE,"E2556"),sQuery(id+"F11.wireOp",EDGE,"E2557"),sQuery(id+"F11.wireOp",EDGE,"E2558"),sQuery(id+"F11.wireOp",EDGE,"E2559"),sQuery(id+"F11.wireOp",EDGE,"E2560"),sQuery(id+"F11.wireOp",EDGE,"E2561"),sQuery(id+"F11.wireOp",EDGE,"E2562"),sQuery(id+"F11.wireOp",EDGE,"E2563"),sQuery(id+"F11.wireOp",EDGE,"E2564"),sQuery(id+"F11.wireOp",EDGE,"E2565"),sQuery(id+"F11.wireOp",EDGE,"E2566"),sQuery(id+"F11.wireOp",EDGE,"E2567"),sQuery(id+"F11.wireOp",EDGE,"E2568"),sQuery(id+"F11.wireOp",EDGE,"E2569"),sQuery(id+"F11.wireOp",EDGE,"E2570"),sQuery(id+"F11.wireOp",EDGE,"E2571"),sQuery(id+"F11.wireOp",EDGE,"E2572"),sQuery(id+"F11.wireOp",EDGE,"E2573"),sQuery(id+"F11.wireOp",EDGE,"E2574"),sQuery(id+"F11.wireOp",EDGE,"E2575"),sQuery(id+"F11.wireOp",EDGE,"E2576"),sQuery(id+"F11.wireOp",EDGE,"E2577"),sQuery(id+"F11.wireOp",EDGE,"E2578"),sQuery(id+"F11.wireOp",EDGE,"E2579"),sQuery(id+"F11.wireOp",EDGE,"E2580"),sQuery(id+"F11.wireOp",EDGE,"E2581"),sQuery(id+"F11.wireOp",EDGE,"E2582"),sQuery(id+"F11.wireOp",EDGE,"E2583"),sQuery(id+"F11.wireOp",EDGE,"E2584"),sQuery(id+"F11.wireOp",EDGE,"E2585"),sQuery(id+"F11.wireOp",EDGE,"E2586"),sQuery(id+"F11.wireOp",EDGE,"E2587"),sQuery(id+"F11.wireOp",EDGE,"E2588"),sQuery(id+"F11.wireOp",EDGE,"E2589"),sQuery(id+"F11.wireOp",EDGE,"E2590"),sQuery(id+"F11.wireOp",EDGE,"E2591"),sQuery(id+"F11.wireOp",EDGE,"E2592"),sQuery(id+"F11.wireOp",EDGE,"E2593"),sQuery(id+"F11.wireOp",EDGE,"E2594"),sQuery(id+"F11.wireOp",EDGE,"E2595"),sQuery(id+"F11.wireOp",EDGE,"E2596"),sQuery(id+"F11.wireOp",EDGE,"E2597"),sQuery(id+"F11.wireOp",EDGE,"E2598")])],"isStart":false});
            extrude(context, id + "F14", {"entities" : qUnion([Q0]), "operationType" : NewBodyOperationType.REMOVE, "endBound" : BoundingType.UP_TO_SURFACE, "depth" : 25 * mm, "endBoundEntityFace" : qUnion([Q1]), "offsetDistance" : 25 * mm});
        }
        {
            var Q0;
            Q0=makeQuery(id+"F12.opExtrude","SWEPT_BODY",BODY,{"disambiguationData":[OSD([sQuery(id+"F11.wireOp",EDGE,"E1476"),sQuery(id+"F11.wireOp",EDGE,"E1477"),sQuery(id+"F11.wireOp",EDGE,"E1478"),sQuery(id+"F11.wireOp",EDGE,"E1479"),sQuery(id+"F11.wireOp",EDGE,"E1480"),sQuery(id+"F11.wireOp",EDGE,"E1481"),sQuery(id+"F11.wireOp",EDGE,"E1482"),sQuery(id+"F11.wireOp",EDGE,"E1483"),sQuery(id+"F11.wireOp",EDGE,"E1484"),sQuery(id+"F11.wireOp",EDGE,"E1485"),sQuery(id+"F11.wireOp",EDGE,"E1486"),sQuery(id+"F11.wireOp",EDGE,"E1487"),sQuery(id+"F11.wireOp",EDGE,"E1488"),sQuery(id+"F11.wireOp",EDGE,"E1489"),sQuery(id+"F11.wireOp",EDGE,"E1490"),sQuery(id+"F11.wireOp",EDGE,"E1491"),sQuery(id+"F11.wireOp",EDGE,"E1492"),sQuery(id+"F11.wireOp",EDGE,"E1493"),sQuery(id+"F11.wireOp",EDGE,"E1494"),sQuery(id+"F11.wireOp",EDGE,"E1495"),sQuery(id+"F11.wireOp",EDGE,"E1496"),sQuery(id+"F11.wireOp",EDGE,"E1497"),sQuery(id+"F11.wireOp",EDGE,"E1498"),sQuery(id+"F11.wireOp",EDGE,"E1499"),sQuery(id+"F11.wireOp",EDGE,"E1500"),sQuery(id+"F11.wireOp",EDGE,"E1501"),sQuery(id+"F11.wireOp",EDGE,"E1502"),sQuery(id+"F11.wireOp",EDGE,"E1503"),sQuery(id+"F11.wireOp",EDGE,"E1504"),sQuery(id+"F11.wireOp",EDGE,"E1505"),sQuery(id+"F11.wireOp",EDGE,"E1506"),sQuery(id+"F11.wireOp",EDGE,"E1507"),sQuery(id+"F11.wireOp",EDGE,"E1508"),sQuery(id+"F11.wireOp",EDGE,"E1509"),sQuery(id+"F11.wireOp",EDGE,"E1510"),sQuery(id+"F11.wireOp",EDGE,"E1511"),sQuery(id+"F11.wireOp",EDGE,"E1512"),sQuery(id+"F11.wireOp",EDGE,"E1513"),sQuery(id+"F11.wireOp",EDGE,"E1514"),sQuery(id+"F11.wireOp",EDGE,"E1515"),sQuery(id+"F11.wireOp",EDGE,"E1516"),sQuery(id+"F11.wireOp",EDGE,"E1517"),sQuery(id+"F11.wireOp",EDGE,"E1518"),sQuery(id+"F11.wireOp",EDGE,"E1519"),sQuery(id+"F11.wireOp",EDGE,"E1520"),sQuery(id+"F11.wireOp",EDGE,"E1521"),sQuery(id+"F11.wireOp",EDGE,"E1522"),sQuery(id+"F11.wireOp",EDGE,"E1523"),sQuery(id+"F11.wireOp",EDGE,"E1524"),sQuery(id+"F11.wireOp",EDGE,"E1525"),sQuery(id+"F11.wireOp",EDGE,"E1526"),sQuery(id+"F11.wireOp",EDGE,"E1527"),sQuery(id+"F11.wireOp",EDGE,"E1528"),sQuery(id+"F11.wireOp",EDGE,"E1529"),sQuery(id+"F11.wireOp",EDGE,"E1530"),sQuery(id+"F11.wireOp",EDGE,"E1531"),sQuery(id+"F11.wireOp",EDGE,"E1532"),sQuery(id+"F11.wireOp",EDGE,"E1533"),sQuery(id+"F11.wireOp",EDGE,"E1534"),sQuery(id+"F11.wireOp",EDGE,"E1535"),sQuery(id+"F11.wireOp",EDGE,"E1536"),sQuery(id+"F11.wireOp",EDGE,"E1537"),sQuery(id+"F11.wireOp",EDGE,"E1538"),sQuery(id+"F11.wireOp",EDGE,"E1539"),sQuery(id+"F11.wireOp",EDGE,"E1540"),sQuery(id+"F11.wireOp",EDGE,"E1541"),sQuery(id+"F11.wireOp",EDGE,"E1542"),sQuery(id+"F11.wireOp",EDGE,"E1543"),sQuery(id+"F11.wireOp",EDGE,"E1544"),sQuery(id+"F11.wireOp",EDGE,"E1545"),sQuery(id+"F11.wireOp",EDGE,"E1546"),sQuery(id+"F11.wireOp",EDGE,"E1547"),sQuery(id+"F11.wireOp",EDGE,"E1548"),sQuery(id+"F11.wireOp",EDGE,"E1549"),sQuery(id+"F11.wireOp",EDGE,"E1550"),sQuery(id+"F11.wireOp",EDGE,"E1551"),sQuery(id+"F11.wireOp",EDGE,"E1552"),sQuery(id+"F11.wireOp",EDGE,"E1553"),sQuery(id+"F11.wireOp",EDGE,"E1554"),sQuery(id+"F11.wireOp",EDGE,"E1555"),sQuery(id+"F11.wireOp",EDGE,"E1556"),sQuery(id+"F11.wireOp",EDGE,"E1557"),sQuery(id+"F11.wireOp",EDGE,"E1558"),sQuery(id+"F11.wireOp",EDGE,"E1559"),sQuery(id+"F11.wireOp",EDGE,"E1560"),sQuery(id+"F11.wireOp",EDGE,"E1561"),sQuery(id+"F11.wireOp",EDGE,"E1562"),sQuery(id+"F11.wireOp",EDGE,"E1563"),sQuery(id+"F11.wireOp",EDGE,"E1564"),sQuery(id+"F11.wireOp",EDGE,"E1565"),sQuery(id+"F11.wireOp",EDGE,"E1566"),sQuery(id+"F11.wireOp",EDGE,"E1567"),sQuery(id+"F11.wireOp",EDGE,"E1568"),sQuery(id+"F11.wireOp",EDGE,"E1569"),sQuery(id+"F11.wireOp",EDGE,"E1570"),sQuery(id+"F11.wireOp",EDGE,"E1571"),sQuery(id+"F11.wireOp",EDGE,"E1572"),sQuery(id+"F11.wireOp",EDGE,"E1573"),sQuery(id+"F11.wireOp",EDGE,"E1574"),sQuery(id+"F11.wireOp",EDGE,"E1575"),sQuery(id+"F11.wireOp",EDGE,"E1576"),sQuery(id+"F11.wireOp",EDGE,"E1577"),sQuery(id+"F11.wireOp",EDGE,"E1578"),sQuery(id+"F11.wireOp",EDGE,"E1579"),sQuery(id+"F11.wireOp",EDGE,"E1580"),sQuery(id+"F11.wireOp",EDGE,"E1581"),sQuery(id+"F11.wireOp",EDGE,"E1582"),sQuery(id+"F11.wireOp",EDGE,"E1583"),sQuery(id+"F11.wireOp",EDGE,"E1584"),sQuery(id+"F11.wireOp",EDGE,"E1585"),sQuery(id+"F11.wireOp",EDGE,"E1586"),sQuery(id+"F11.wireOp",EDGE,"E1587"),sQuery(id+"F11.wireOp",EDGE,"E1588"),sQuery(id+"F11.wireOp",EDGE,"E1589"),sQuery(id+"F11.wireOp",EDGE,"E1590"),sQuery(id+"F11.wireOp",EDGE,"E1591"),sQuery(id+"F11.wireOp",EDGE,"E1592"),sQuery(id+"F11.wireOp",EDGE,"E1593"),sQuery(id+"F11.wireOp",EDGE,"E1594"),sQuery(id+"F11.wireOp",EDGE,"E1595"),sQuery(id+"F11.wireOp",EDGE,"E1596"),sQuery(id+"F11.wireOp",EDGE,"E1597"),sQuery(id+"F11.wireOp",EDGE,"E1598"),sQuery(id+"F11.wireOp",EDGE,"E1599"),sQuery(id+"F11.wireOp",EDGE,"E1600"),sQuery(id+"F11.wireOp",EDGE,"E1601"),sQuery(id+"F11.wireOp",EDGE,"E1602"),sQuery(id+"F11.wireOp",EDGE,"E1603"),sQuery(id+"F11.wireOp",EDGE,"E1604"),sQuery(id+"F11.wireOp",EDGE,"E1605"),sQuery(id+"F11.wireOp",EDGE,"E1606"),sQuery(id+"F11.wireOp",EDGE,"E1607"),sQuery(id+"F11.wireOp",EDGE,"E1608"),sQuery(id+"F11.wireOp",EDGE,"E1609"),sQuery(id+"F11.wireOp",EDGE,"E1610"),sQuery(id+"F11.wireOp",EDGE,"E1611"),sQuery(id+"F11.wireOp",EDGE,"E1612"),sQuery(id+"F11.wireOp",EDGE,"E1613"),sQuery(id+"F11.wireOp",EDGE,"E1614"),sQuery(id+"F11.wireOp",EDGE,"E1615"),sQuery(id+"F11.wireOp",EDGE,"E1616"),sQuery(id+"F11.wireOp",EDGE,"E1617"),sQuery(id+"F11.wireOp",EDGE,"E1618"),sQuery(id+"F11.wireOp",EDGE,"E1619"),sQuery(id+"F11.wireOp",EDGE,"E1620"),sQuery(id+"F11.wireOp",EDGE,"E1621"),sQuery(id+"F11.wireOp",EDGE,"E1622"),sQuery(id+"F11.wireOp",EDGE,"E1623"),sQuery(id+"F11.wireOp",EDGE,"E1624"),sQuery(id+"F11.wireOp",EDGE,"E1625"),sQuery(id+"F11.wireOp",EDGE,"E1626"),sQuery(id+"F11.wireOp",EDGE,"E1627"),sQuery(id+"F11.wireOp",EDGE,"E1628"),sQuery(id+"F11.wireOp",EDGE,"E1629"),sQuery(id+"F11.wireOp",EDGE,"E1630"),sQuery(id+"F11.wireOp",EDGE,"E1631"),sQuery(id+"F11.wireOp",EDGE,"E1632"),sQuery(id+"F11.wireOp",EDGE,"E1633"),sQuery(id+"F11.wireOp",EDGE,"E1634"),sQuery(id+"F11.wireOp",EDGE,"E1635"),sQuery(id+"F11.wireOp",EDGE,"E1636"),sQuery(id+"F11.wireOp",EDGE,"E1637"),sQuery(id+"F11.wireOp",EDGE,"E1638"),sQuery(id+"F11.wireOp",EDGE,"E1639"),sQuery(id+"F11.wireOp",EDGE,"E1640"),sQuery(id+"F11.wireOp",EDGE,"E1641"),sQuery(id+"F11.wireOp",EDGE,"E1642"),sQuery(id+"F11.wireOp",EDGE,"E1643"),sQuery(id+"F11.wireOp",EDGE,"E1644"),sQuery(id+"F11.wireOp",EDGE,"E1645"),sQuery(id+"F11.wireOp",EDGE,"E1646"),sQuery(id+"F11.wireOp",EDGE,"E1647"),sQuery(id+"F11.wireOp",EDGE,"E1648"),sQuery(id+"F11.wireOp",EDGE,"E1649"),sQuery(id+"F11.wireOp",EDGE,"E1650"),sQuery(id+"F11.wireOp",EDGE,"E1651"),sQuery(id+"F11.wireOp",EDGE,"E1652"),sQuery(id+"F11.wireOp",EDGE,"E1653"),sQuery(id+"F11.wireOp",EDGE,"E1654"),sQuery(id+"F11.wireOp",EDGE,"E1655"),sQuery(id+"F11.wireOp",EDGE,"E1656"),sQuery(id+"F11.wireOp",EDGE,"E1657"),sQuery(id+"F11.wireOp",EDGE,"E1658"),sQuery(id+"F11.wireOp",EDGE,"E1659"),sQuery(id+"F11.wireOp",EDGE,"E1660"),sQuery(id+"F11.wireOp",EDGE,"E1661"),sQuery(id+"F11.wireOp",EDGE,"E1662"),sQuery(id+"F11.wireOp",EDGE,"E1663"),sQuery(id+"F11.wireOp",EDGE,"E1664"),sQuery(id+"F11.wireOp",EDGE,"E1665"),sQuery(id+"F11.wireOp",EDGE,"E1666"),sQuery(id+"F11.wireOp",EDGE,"E1667"),sQuery(id+"F11.wireOp",EDGE,"E1668"),sQuery(id+"F11.wireOp",EDGE,"E1669"),sQuery(id+"F11.wireOp",EDGE,"E1670"),sQuery(id+"F11.wireOp",EDGE,"E1671"),sQuery(id+"F11.wireOp",EDGE,"E1672"),sQuery(id+"F11.wireOp",EDGE,"E1673"),sQuery(id+"F11.wireOp",EDGE,"E1674"),sQuery(id+"F11.wireOp",EDGE,"E1675"),sQuery(id+"F11.wireOp",EDGE,"E1676"),sQuery(id+"F11.wireOp",EDGE,"E1677"),sQuery(id+"F11.wireOp",EDGE,"E1678"),sQuery(id+"F11.wireOp",EDGE,"E1679"),sQuery(id+"F11.wireOp",EDGE,"E1680"),sQuery(id+"F11.wireOp",EDGE,"E1681"),sQuery(id+"F11.wireOp",EDGE,"E1682"),sQuery(id+"F11.wireOp",EDGE,"E1683"),sQuery(id+"F11.wireOp",EDGE,"E1684"),sQuery(id+"F11.wireOp",EDGE,"E1685"),sQuery(id+"F11.wireOp",EDGE,"E1686"),sQuery(id+"F11.wireOp",EDGE,"E1687"),sQuery(id+"F11.wireOp",EDGE,"E1688"),sQuery(id+"F11.wireOp",EDGE,"E1689"),sQuery(id+"F11.wireOp",EDGE,"E1690"),sQuery(id+"F11.wireOp",EDGE,"E1691"),sQuery(id+"F11.wireOp",EDGE,"E1692"),sQuery(id+"F11.wireOp",EDGE,"E1693"),sQuery(id+"F11.wireOp",EDGE,"E1694"),sQuery(id+"F11.wireOp",EDGE,"E1695"),sQuery(id+"F11.wireOp",EDGE,"E1696"),sQuery(id+"F11.wireOp",EDGE,"E1697"),sQuery(id+"F11.wireOp",EDGE,"E1698"),sQuery(id+"F11.wireOp",EDGE,"E1699"),sQuery(id+"F11.wireOp",EDGE,"E1700"),sQuery(id+"F11.wireOp",EDGE,"E1701"),sQuery(id+"F11.wireOp",EDGE,"E1702"),sQuery(id+"F11.wireOp",EDGE,"E1703"),sQuery(id+"F11.wireOp",EDGE,"E1704"),sQuery(id+"F11.wireOp",EDGE,"E1705"),sQuery(id+"F11.wireOp",EDGE,"E1706"),sQuery(id+"F11.wireOp",EDGE,"E1707"),sQuery(id+"F11.wireOp",EDGE,"E1708"),sQuery(id+"F11.wireOp",EDGE,"E1709"),sQuery(id+"F11.wireOp",EDGE,"E1710"),sQuery(id+"F11.wireOp",EDGE,"E1711"),sQuery(id+"F11.wireOp",EDGE,"E1712"),sQuery(id+"F11.wireOp",EDGE,"E1713"),sQuery(id+"F11.wireOp",EDGE,"E1714"),sQuery(id+"F11.wireOp",EDGE,"E1715"),sQuery(id+"F11.wireOp",EDGE,"E1716"),sQuery(id+"F11.wireOp",EDGE,"E1717"),sQuery(id+"F11.wireOp",EDGE,"E1718"),sQuery(id+"F11.wireOp",EDGE,"E1719"),sQuery(id+"F11.wireOp",EDGE,"E1720"),sQuery(id+"F11.wireOp",EDGE,"E1721"),sQuery(id+"F11.wireOp",EDGE,"E1722"),sQuery(id+"F11.wireOp",EDGE,"E1723"),sQuery(id+"F11.wireOp",EDGE,"E1724"),sQuery(id+"F11.wireOp",EDGE,"E1725"),sQuery(id+"F11.wireOp",EDGE,"E1726"),sQuery(id+"F11.wireOp",EDGE,"E1727"),sQuery(id+"F11.wireOp",EDGE,"E1728"),sQuery(id+"F11.wireOp",EDGE,"E1729"),sQuery(id+"F11.wireOp",EDGE,"E1730"),sQuery(id+"F11.wireOp",EDGE,"E1731"),sQuery(id+"F11.wireOp",EDGE,"E1732"),sQuery(id+"F11.wireOp",EDGE,"E1733"),sQuery(id+"F11.wireOp",EDGE,"E1734"),sQuery(id+"F11.wireOp",EDGE,"E1735"),sQuery(id+"F11.wireOp",EDGE,"E1736"),sQuery(id+"F11.wireOp",EDGE,"E1737"),sQuery(id+"F11.wireOp",EDGE,"E1738"),sQuery(id+"F11.wireOp",EDGE,"E1739"),sQuery(id+"F11.wireOp",EDGE,"E1740"),sQuery(id+"F11.wireOp",EDGE,"E1741"),sQuery(id+"F11.wireOp",EDGE,"E1742"),sQuery(id+"F11.wireOp",EDGE,"E1743"),sQuery(id+"F11.wireOp",EDGE,"E1744"),sQuery(id+"F11.wireOp",EDGE,"E1745"),sQuery(id+"F11.wireOp",EDGE,"E1746"),sQuery(id+"F11.wireOp",EDGE,"E1747"),sQuery(id+"F11.wireOp",EDGE,"E1748"),sQuery(id+"F11.wireOp",EDGE,"E1749"),sQuery(id+"F11.wireOp",EDGE,"E1750"),sQuery(id+"F11.wireOp",EDGE,"E1751"),sQuery(id+"F11.wireOp",EDGE,"E1752"),sQuery(id+"F11.wireOp",EDGE,"E1753"),sQuery(id+"F11.wireOp",EDGE,"E1754"),sQuery(id+"F11.wireOp",EDGE,"E1755"),sQuery(id+"F11.wireOp",EDGE,"E1756"),sQuery(id+"F11.wireOp",EDGE,"E1757"),sQuery(id+"F11.wireOp",EDGE,"E1758"),sQuery(id+"F11.wireOp",EDGE,"E1759"),sQuery(id+"F11.wireOp",EDGE,"E1760"),sQuery(id+"F11.wireOp",EDGE,"E1761"),sQuery(id+"F11.wireOp",EDGE,"E1762"),sQuery(id+"F11.wireOp",EDGE,"E1763"),sQuery(id+"F11.wireOp",EDGE,"E1764"),sQuery(id+"F11.wireOp",EDGE,"E1765"),sQuery(id+"F11.wireOp",EDGE,"E1766"),sQuery(id+"F11.wireOp",EDGE,"E1767"),sQuery(id+"F11.wireOp",EDGE,"E1768"),sQuery(id+"F11.wireOp",EDGE,"E1769"),sQuery(id+"F11.wireOp",EDGE,"E1770"),sQuery(id+"F11.wireOp",EDGE,"E1771"),sQuery(id+"F11.wireOp",EDGE,"E1772"),sQuery(id+"F11.wireOp",EDGE,"E1773"),sQuery(id+"F11.wireOp",EDGE,"E1774"),sQuery(id+"F11.wireOp",EDGE,"E1775"),sQuery(id+"F11.wireOp",EDGE,"E1776"),sQuery(id+"F11.wireOp",EDGE,"E1777"),sQuery(id+"F11.wireOp",EDGE,"E1778"),sQuery(id+"F11.wireOp",EDGE,"E1779"),sQuery(id+"F11.wireOp",EDGE,"E1780"),sQuery(id+"F11.wireOp",EDGE,"E1781"),sQuery(id+"F11.wireOp",EDGE,"E1782"),sQuery(id+"F11.wireOp",EDGE,"E1783"),sQuery(id+"F11.wireOp",EDGE,"E1784"),sQuery(id+"F11.wireOp",EDGE,"E1785"),sQuery(id+"F11.wireOp",EDGE,"E1786"),sQuery(id+"F11.wireOp",EDGE,"E1787"),sQuery(id+"F11.wireOp",EDGE,"E1788"),sQuery(id+"F11.wireOp",EDGE,"E1789"),sQuery(id+"F11.wireOp",EDGE,"E1790"),sQuery(id+"F11.wireOp",EDGE,"E1791"),sQuery(id+"F11.wireOp",EDGE,"E1792"),sQuery(id+"F11.wireOp",EDGE,"E1793"),sQuery(id+"F11.wireOp",EDGE,"E1794"),sQuery(id+"F11.wireOp",EDGE,"E1795"),sQuery(id+"F11.wireOp",EDGE,"E1796"),sQuery(id+"F11.wireOp",EDGE,"E1797"),sQuery(id+"F11.wireOp",EDGE,"E1798"),sQuery(id+"F11.wireOp",EDGE,"E1799"),sQuery(id+"F11.wireOp",EDGE,"E1800"),sQuery(id+"F11.wireOp",EDGE,"E1801"),sQuery(id+"F11.wireOp",EDGE,"E1802"),sQuery(id+"F11.wireOp",EDGE,"E1803"),sQuery(id+"F11.wireOp",EDGE,"E1804"),sQuery(id+"F11.wireOp",EDGE,"E1805"),sQuery(id+"F11.wireOp",EDGE,"E1806"),sQuery(id+"F11.wireOp",EDGE,"E1807"),sQuery(id+"F11.wireOp",EDGE,"E1808"),sQuery(id+"F11.wireOp",EDGE,"E1809"),sQuery(id+"F11.wireOp",EDGE,"E1810"),sQuery(id+"F11.wireOp",EDGE,"E1811"),sQuery(id+"F11.wireOp",EDGE,"E1812"),sQuery(id+"F11.wireOp",EDGE,"E1813"),sQuery(id+"F11.wireOp",EDGE,"E1814"),sQuery(id+"F11.wireOp",EDGE,"E1815"),sQuery(id+"F11.wireOp",EDGE,"E1816"),sQuery(id+"F11.wireOp",EDGE,"E1817"),sQuery(id+"F11.wireOp",EDGE,"E1818"),sQuery(id+"F11.wireOp",EDGE,"E1819"),sQuery(id+"F11.wireOp",EDGE,"E1820"),sQuery(id+"F11.wireOp",EDGE,"E1821"),sQuery(id+"F11.wireOp",EDGE,"E1822"),sQuery(id+"F11.wireOp",EDGE,"E1823"),sQuery(id+"F11.wireOp",EDGE,"E1824"),sQuery(id+"F11.wireOp",EDGE,"E1825"),sQuery(id+"F11.wireOp",EDGE,"E1826"),sQuery(id+"F11.wireOp",EDGE,"E1827"),sQuery(id+"F11.wireOp",EDGE,"E1828"),sQuery(id+"F11.wireOp",EDGE,"E1829"),sQuery(id+"F11.wireOp",EDGE,"E1830"),sQuery(id+"F11.wireOp",EDGE,"E1831"),sQuery(id+"F11.wireOp",EDGE,"E1832"),sQuery(id+"F11.wireOp",EDGE,"E1833"),sQuery(id+"F11.wireOp",EDGE,"E1834"),sQuery(id+"F11.wireOp",EDGE,"E1835"),sQuery(id+"F11.wireOp",EDGE,"E1836"),sQuery(id+"F11.wireOp",EDGE,"E1837"),sQuery(id+"F11.wireOp",EDGE,"E1838"),sQuery(id+"F11.wireOp",EDGE,"E1839"),sQuery(id+"F11.wireOp",EDGE,"E1840"),sQuery(id+"F11.wireOp",EDGE,"E1841"),sQuery(id+"F11.wireOp",EDGE,"E1842"),sQuery(id+"F11.wireOp",EDGE,"E1843"),sQuery(id+"F11.wireOp",EDGE,"E1844"),sQuery(id+"F11.wireOp",EDGE,"E1845"),sQuery(id+"F11.wireOp",EDGE,"E1846"),sQuery(id+"F11.wireOp",EDGE,"E1847"),sQuery(id+"F11.wireOp",EDGE,"E1848"),sQuery(id+"F11.wireOp",EDGE,"E1849"),sQuery(id+"F11.wireOp",EDGE,"E1850"),sQuery(id+"F11.wireOp",EDGE,"E1851"),sQuery(id+"F11.wireOp",EDGE,"E1852"),sQuery(id+"F11.wireOp",EDGE,"E1853"),sQuery(id+"F11.wireOp",EDGE,"E1854"),sQuery(id+"F11.wireOp",EDGE,"E1855"),sQuery(id+"F11.wireOp",EDGE,"E1856"),sQuery(id+"F11.wireOp",EDGE,"E1857"),sQuery(id+"F11.wireOp",EDGE,"E1858"),sQuery(id+"F11.wireOp",EDGE,"E1859"),sQuery(id+"F11.wireOp",EDGE,"E1860"),sQuery(id+"F11.wireOp",EDGE,"E1861"),sQuery(id+"F11.wireOp",EDGE,"E1862"),sQuery(id+"F11.wireOp",EDGE,"E1863"),sQuery(id+"F11.wireOp",EDGE,"E1864"),sQuery(id+"F11.wireOp",EDGE,"E1865"),sQuery(id+"F11.wireOp",EDGE,"E1866"),sQuery(id+"F11.wireOp",EDGE,"E1867"),sQuery(id+"F11.wireOp",EDGE,"E1868"),sQuery(id+"F11.wireOp",EDGE,"E1869"),sQuery(id+"F11.wireOp",EDGE,"E1870"),sQuery(id+"F11.wireOp",EDGE,"E1871"),sQuery(id+"F11.wireOp",EDGE,"E1872"),sQuery(id+"F11.wireOp",EDGE,"E1873"),sQuery(id+"F11.wireOp",EDGE,"E1874"),sQuery(id+"F11.wireOp",EDGE,"E1875"),sQuery(id+"F11.wireOp",EDGE,"E1876"),sQuery(id+"F11.wireOp",EDGE,"E1877"),sQuery(id+"F11.wireOp",EDGE,"E1878"),sQuery(id+"F11.wireOp",EDGE,"E1879"),sQuery(id+"F11.wireOp",EDGE,"E1880"),sQuery(id+"F11.wireOp",EDGE,"E1881"),sQuery(id+"F11.wireOp",EDGE,"E1882"),sQuery(id+"F11.wireOp",EDGE,"E1883"),sQuery(id+"F11.wireOp",EDGE,"E1884"),sQuery(id+"F11.wireOp",EDGE,"E1885"),sQuery(id+"F11.wireOp",EDGE,"E1886"),sQuery(id+"F11.wireOp",EDGE,"E1887"),sQuery(id+"F11.wireOp",EDGE,"E1888"),sQuery(id+"F11.wireOp",EDGE,"E1889"),sQuery(id+"F11.wireOp",EDGE,"E1890"),sQuery(id+"F11.wireOp",EDGE,"E1891"),sQuery(id+"F11.wireOp",EDGE,"E1892"),sQuery(id+"F11.wireOp",EDGE,"E1893"),sQuery(id+"F11.wireOp",EDGE,"E1894"),sQuery(id+"F11.wireOp",EDGE,"E1895"),sQuery(id+"F11.wireOp",EDGE,"E1896"),sQuery(id+"F11.wireOp",EDGE,"E1897"),sQuery(id+"F11.wireOp",EDGE,"E1898"),sQuery(id+"F11.wireOp",EDGE,"E1899"),sQuery(id+"F11.wireOp",EDGE,"E1900"),sQuery(id+"F11.wireOp",EDGE,"E1901"),sQuery(id+"F11.wireOp",EDGE,"E1902"),sQuery(id+"F11.wireOp",EDGE,"E1903"),sQuery(id+"F11.wireOp",EDGE,"E1904"),sQuery(id+"F11.wireOp",EDGE,"E1905"),sQuery(id+"F11.wireOp",EDGE,"E1906"),sQuery(id+"F11.wireOp",EDGE,"E1907"),sQuery(id+"F11.wireOp",EDGE,"E1908"),sQuery(id+"F11.wireOp",EDGE,"E1909"),sQuery(id+"F11.wireOp",EDGE,"E1910"),sQuery(id+"F11.wireOp",EDGE,"E1911"),sQuery(id+"F11.wireOp",EDGE,"E1912"),sQuery(id+"F11.wireOp",EDGE,"E1913"),sQuery(id+"F11.wireOp",EDGE,"E1914"),sQuery(id+"F11.wireOp",EDGE,"E1915"),sQuery(id+"F11.wireOp",EDGE,"E1916"),sQuery(id+"F11.wireOp",EDGE,"E1917"),sQuery(id+"F11.wireOp",EDGE,"E1918"),sQuery(id+"F11.wireOp",EDGE,"E1919"),sQuery(id+"F11.wireOp",EDGE,"E1920"),sQuery(id+"F11.wireOp",EDGE,"E1921"),sQuery(id+"F11.wireOp",EDGE,"E1922"),sQuery(id+"F11.wireOp",EDGE,"E1923"),sQuery(id+"F11.wireOp",EDGE,"E1924"),sQuery(id+"F11.wireOp",EDGE,"E1925"),sQuery(id+"F11.wireOp",EDGE,"E1926"),sQuery(id+"F11.wireOp",EDGE,"E1927"),sQuery(id+"F11.wireOp",EDGE,"E1928"),sQuery(id+"F11.wireOp",EDGE,"E1929"),sQuery(id+"F11.wireOp",EDGE,"E1930"),sQuery(id+"F11.wireOp",EDGE,"E1931"),sQuery(id+"F11.wireOp",EDGE,"E1932"),sQuery(id+"F11.wireOp",EDGE,"E1933"),sQuery(id+"F11.wireOp",EDGE,"E1934"),sQuery(id+"F11.wireOp",EDGE,"E1935"),sQuery(id+"F11.wireOp",EDGE,"E1936"),sQuery(id+"F11.wireOp",EDGE,"E1937"),sQuery(id+"F11.wireOp",EDGE,"E1938"),sQuery(id+"F11.wireOp",EDGE,"E1939"),sQuery(id+"F11.wireOp",EDGE,"E1940"),sQuery(id+"F11.wireOp",EDGE,"E1941"),sQuery(id+"F11.wireOp",EDGE,"E1942"),sQuery(id+"F11.wireOp",EDGE,"E1943"),sQuery(id+"F11.wireOp",EDGE,"E1944"),sQuery(id+"F11.wireOp",EDGE,"E1945"),sQuery(id+"F11.wireOp",EDGE,"E1946"),sQuery(id+"F11.wireOp",EDGE,"E1947"),sQuery(id+"F11.wireOp",EDGE,"E1948"),sQuery(id+"F11.wireOp",EDGE,"E1949"),sQuery(id+"F11.wireOp",EDGE,"E1950"),sQuery(id+"F11.wireOp",EDGE,"E1951"),sQuery(id+"F11.wireOp",EDGE,"E1952"),sQuery(id+"F11.wireOp",EDGE,"E1953"),sQuery(id+"F11.wireOp",EDGE,"E1954"),sQuery(id+"F11.wireOp",EDGE,"E1955"),sQuery(id+"F11.wireOp",EDGE,"E1956"),sQuery(id+"F11.wireOp",EDGE,"E1957"),sQuery(id+"F11.wireOp",EDGE,"E1958"),sQuery(id+"F11.wireOp",EDGE,"E1959"),sQuery(id+"F11.wireOp",EDGE,"E1960"),sQuery(id+"F11.wireOp",EDGE,"E1961"),sQuery(id+"F11.wireOp",EDGE,"E1962"),sQuery(id+"F11.wireOp",EDGE,"E1963"),sQuery(id+"F11.wireOp",EDGE,"E1964"),sQuery(id+"F11.wireOp",EDGE,"E1965"),sQuery(id+"F11.wireOp",EDGE,"E1966"),sQuery(id+"F11.wireOp",EDGE,"E1967"),sQuery(id+"F11.wireOp",EDGE,"E1968"),sQuery(id+"F11.wireOp",EDGE,"E1969"),sQuery(id+"F11.wireOp",EDGE,"E1970"),sQuery(id+"F11.wireOp",EDGE,"E1971"),sQuery(id+"F11.wireOp",EDGE,"E1972"),sQuery(id+"F11.wireOp",EDGE,"E1973"),sQuery(id+"F11.wireOp",EDGE,"E1974"),sQuery(id+"F11.wireOp",EDGE,"E1975"),sQuery(id+"F11.wireOp",EDGE,"E1976"),sQuery(id+"F11.wireOp",EDGE,"E1977"),sQuery(id+"F11.wireOp",EDGE,"E1978"),sQuery(id+"F11.wireOp",EDGE,"E1979"),sQuery(id+"F11.wireOp",EDGE,"E1980"),sQuery(id+"F11.wireOp",EDGE,"E1981"),sQuery(id+"F11.wireOp",EDGE,"E1982"),sQuery(id+"F11.wireOp",EDGE,"E1983"),sQuery(id+"F11.wireOp",EDGE,"E1984"),sQuery(id+"F11.wireOp",EDGE,"E1985"),sQuery(id+"F11.wireOp",EDGE,"E1986"),sQuery(id+"F11.wireOp",EDGE,"E1987"),sQuery(id+"F11.wireOp",EDGE,"E1988"),sQuery(id+"F11.wireOp",EDGE,"E1989"),sQuery(id+"F11.wireOp",EDGE,"E1990"),sQuery(id+"F11.wireOp",EDGE,"E1991"),sQuery(id+"F11.wireOp",EDGE,"E1992"),sQuery(id+"F11.wireOp",EDGE,"E1993"),sQuery(id+"F11.wireOp",EDGE,"E1994"),sQuery(id+"F11.wireOp",EDGE,"E1995"),sQuery(id+"F11.wireOp",EDGE,"E1996"),sQuery(id+"F11.wireOp",EDGE,"E1997"),sQuery(id+"F11.wireOp",EDGE,"E1998"),sQuery(id+"F11.wireOp",EDGE,"E1999"),sQuery(id+"F11.wireOp",EDGE,"E2000"),sQuery(id+"F11.wireOp",EDGE,"E2001"),sQuery(id+"F11.wireOp",EDGE,"E2002"),sQuery(id+"F11.wireOp",EDGE,"E2003"),sQuery(id+"F11.wireOp",EDGE,"E2004"),sQuery(id+"F11.wireOp",EDGE,"E2005"),sQuery(id+"F11.wireOp",EDGE,"E2006"),sQuery(id+"F11.wireOp",EDGE,"E2007"),sQuery(id+"F11.wireOp",EDGE,"E2008"),sQuery(id+"F11.wireOp",EDGE,"E2009"),sQuery(id+"F11.wireOp",EDGE,"E2010"),sQuery(id+"F11.wireOp",EDGE,"E2011"),sQuery(id+"F11.wireOp",EDGE,"E2012"),sQuery(id+"F11.wireOp",EDGE,"E2013"),sQuery(id+"F11.wireOp",EDGE,"E2014"),sQuery(id+"F11.wireOp",EDGE,"E2015"),sQuery(id+"F11.wireOp",EDGE,"E2016"),sQuery(id+"F11.wireOp",EDGE,"E2017"),sQuery(id+"F11.wireOp",EDGE,"E2018"),sQuery(id+"F11.wireOp",EDGE,"E2019"),sQuery(id+"F11.wireOp",EDGE,"E2020"),sQuery(id+"F11.wireOp",EDGE,"E2021"),sQuery(id+"F11.wireOp",EDGE,"E2022"),sQuery(id+"F11.wireOp",EDGE,"E2023"),sQuery(id+"F11.wireOp",EDGE,"E2024"),sQuery(id+"F11.wireOp",EDGE,"E2025"),sQuery(id+"F11.wireOp",EDGE,"E2026"),sQuery(id+"F11.wireOp",EDGE,"E2027"),sQuery(id+"F11.wireOp",EDGE,"E2028"),sQuery(id+"F11.wireOp",EDGE,"E2029"),sQuery(id+"F11.wireOp",EDGE,"E2030"),sQuery(id+"F11.wireOp",EDGE,"E2031"),sQuery(id+"F11.wireOp",EDGE,"E2032"),sQuery(id+"F11.wireOp",EDGE,"E2033"),sQuery(id+"F11.wireOp",EDGE,"E2034"),sQuery(id+"F11.wireOp",EDGE,"E2035"),sQuery(id+"F11.wireOp",EDGE,"E2036"),sQuery(id+"F11.wireOp",EDGE,"E2037"),sQuery(id+"F11.wireOp",EDGE,"E2038"),sQuery(id+"F11.wireOp",EDGE,"E2039"),sQuery(id+"F11.wireOp",EDGE,"E2040"),sQuery(id+"F11.wireOp",EDGE,"E2041"),sQuery(id+"F11.wireOp",EDGE,"E2042"),sQuery(id+"F11.wireOp",EDGE,"E2043"),sQuery(id+"F11.wireOp",EDGE,"E2044"),sQuery(id+"F11.wireOp",EDGE,"E2045"),sQuery(id+"F11.wireOp",EDGE,"E2046"),sQuery(id+"F11.wireOp",EDGE,"E2047"),sQuery(id+"F11.wireOp",EDGE,"E2048"),sQuery(id+"F11.wireOp",EDGE,"E2049"),sQuery(id+"F11.wireOp",EDGE,"E2050"),sQuery(id+"F11.wireOp",EDGE,"E2051"),sQuery(id+"F11.wireOp",EDGE,"E2052"),sQuery(id+"F11.wireOp",EDGE,"E2053"),sQuery(id+"F11.wireOp",EDGE,"E2054"),sQuery(id+"F11.wireOp",EDGE,"E2055"),sQuery(id+"F11.wireOp",EDGE,"E2056"),sQuery(id+"F11.wireOp",EDGE,"E2057"),sQuery(id+"F11.wireOp",EDGE,"E2058"),sQuery(id+"F11.wireOp",EDGE,"E2059"),sQuery(id+"F11.wireOp",EDGE,"E2060"),sQuery(id+"F11.wireOp",EDGE,"E2061"),sQuery(id+"F11.wireOp",EDGE,"E2062"),sQuery(id+"F11.wireOp",EDGE,"E2063"),sQuery(id+"F11.wireOp",EDGE,"E2064"),sQuery(id+"F11.wireOp",EDGE,"E2065"),sQuery(id+"F11.wireOp",EDGE,"E2066"),sQuery(id+"F11.wireOp",EDGE,"E2067"),sQuery(id+"F11.wireOp",EDGE,"E2068"),sQuery(id+"F11.wireOp",EDGE,"E2069"),sQuery(id+"F11.wireOp",EDGE,"E2070"),sQuery(id+"F11.wireOp",EDGE,"E2071"),sQuery(id+"F11.wireOp",EDGE,"E2072"),sQuery(id+"F11.wireOp",EDGE,"E2073"),sQuery(id+"F11.wireOp",EDGE,"E2074"),sQuery(id+"F11.wireOp",EDGE,"E2075"),sQuery(id+"F11.wireOp",EDGE,"E2076"),sQuery(id+"F11.wireOp",EDGE,"E2077"),sQuery(id+"F11.wireOp",EDGE,"E2078"),sQuery(id+"F11.wireOp",EDGE,"E2079"),sQuery(id+"F11.wireOp",EDGE,"E2080"),sQuery(id+"F11.wireOp",EDGE,"E2081"),sQuery(id+"F11.wireOp",EDGE,"E2082"),sQuery(id+"F11.wireOp",EDGE,"E2083"),sQuery(id+"F11.wireOp",EDGE,"E2084"),sQuery(id+"F11.wireOp",EDGE,"E2085"),sQuery(id+"F11.wireOp",EDGE,"E2086"),sQuery(id+"F11.wireOp",EDGE,"E2087"),sQuery(id+"F11.wireOp",EDGE,"E2088"),sQuery(id+"F11.wireOp",EDGE,"E2089"),sQuery(id+"F11.wireOp",EDGE,"E2090"),sQuery(id+"F11.wireOp",EDGE,"E2091"),sQuery(id+"F11.wireOp",EDGE,"E2092"),sQuery(id+"F11.wireOp",EDGE,"E2093"),sQuery(id+"F11.wireOp",EDGE,"E2094"),sQuery(id+"F11.wireOp",EDGE,"E2095"),sQuery(id+"F11.wireOp",EDGE,"E2096"),sQuery(id+"F11.wireOp",EDGE,"E2097"),sQuery(id+"F11.wireOp",EDGE,"E2098"),sQuery(id+"F11.wireOp",EDGE,"E2099"),sQuery(id+"F11.wireOp",EDGE,"E2100"),sQuery(id+"F11.wireOp",EDGE,"E2101"),sQuery(id+"F11.wireOp",EDGE,"E2102"),sQuery(id+"F11.wireOp",EDGE,"E2103"),sQuery(id+"F11.wireOp",EDGE,"E2104"),sQuery(id+"F11.wireOp",EDGE,"E2105"),sQuery(id+"F11.wireOp",EDGE,"E2106"),sQuery(id+"F11.wireOp",EDGE,"E2107"),sQuery(id+"F11.wireOp",EDGE,"E2108"),sQuery(id+"F11.wireOp",EDGE,"E2109"),sQuery(id+"F11.wireOp",EDGE,"E2110"),sQuery(id+"F11.wireOp",EDGE,"E2111"),sQuery(id+"F11.wireOp",EDGE,"E2112"),sQuery(id+"F11.wireOp",EDGE,"E2113"),sQuery(id+"F11.wireOp",EDGE,"E2114"),sQuery(id+"F11.wireOp",EDGE,"E2115"),sQuery(id+"F11.wireOp",EDGE,"E2116"),sQuery(id+"F11.wireOp",EDGE,"E2117"),sQuery(id+"F11.wireOp",EDGE,"E2118"),sQuery(id+"F11.wireOp",EDGE,"E2119"),sQuery(id+"F11.wireOp",EDGE,"E2120"),sQuery(id+"F11.wireOp",EDGE,"E2121"),sQuery(id+"F11.wireOp",EDGE,"E2122"),sQuery(id+"F11.wireOp",EDGE,"E2123"),sQuery(id+"F11.wireOp",EDGE,"E2124"),sQuery(id+"F11.wireOp",EDGE,"E2125"),sQuery(id+"F11.wireOp",EDGE,"E2126"),sQuery(id+"F11.wireOp",EDGE,"E2127"),sQuery(id+"F11.wireOp",EDGE,"E2128"),sQuery(id+"F11.wireOp",EDGE,"E2129"),sQuery(id+"F11.wireOp",EDGE,"E2130"),sQuery(id+"F11.wireOp",EDGE,"E2131"),sQuery(id+"F11.wireOp",EDGE,"E2132"),sQuery(id+"F11.wireOp",EDGE,"E2133"),sQuery(id+"F11.wireOp",EDGE,"E2134"),sQuery(id+"F11.wireOp",EDGE,"E2135"),sQuery(id+"F11.wireOp",EDGE,"E2136"),sQuery(id+"F11.wireOp",EDGE,"E2137"),sQuery(id+"F11.wireOp",EDGE,"E2138"),sQuery(id+"F11.wireOp",EDGE,"E2139"),sQuery(id+"F11.wireOp",EDGE,"E2140"),sQuery(id+"F11.wireOp",EDGE,"E2141"),sQuery(id+"F11.wireOp",EDGE,"E2142"),sQuery(id+"F11.wireOp",EDGE,"E2143"),sQuery(id+"F11.wireOp",EDGE,"E2144"),sQuery(id+"F11.wireOp",EDGE,"E2145"),sQuery(id+"F11.wireOp",EDGE,"E2146"),sQuery(id+"F11.wireOp",EDGE,"E2147"),sQuery(id+"F11.wireOp",EDGE,"E2148"),sQuery(id+"F11.wireOp",EDGE,"E2149"),sQuery(id+"F11.wireOp",EDGE,"E2150"),sQuery(id+"F11.wireOp",EDGE,"E2151"),sQuery(id+"F11.wireOp",EDGE,"E2152"),sQuery(id+"F11.wireOp",EDGE,"E2153"),sQuery(id+"F11.wireOp",EDGE,"E2154"),sQuery(id+"F11.wireOp",EDGE,"E2155"),sQuery(id+"F11.wireOp",EDGE,"E2156"),sQuery(id+"F11.wireOp",EDGE,"E2157"),sQuery(id+"F11.wireOp",EDGE,"E2158"),sQuery(id+"F11.wireOp",EDGE,"E2159"),sQuery(id+"F11.wireOp",EDGE,"E2160"),sQuery(id+"F11.wireOp",EDGE,"E2161"),sQuery(id+"F11.wireOp",EDGE,"E2162"),sQuery(id+"F11.wireOp",EDGE,"E2163"),sQuery(id+"F11.wireOp",EDGE,"E2164"),sQuery(id+"F11.wireOp",EDGE,"E2165"),sQuery(id+"F11.wireOp",EDGE,"E2166"),sQuery(id+"F11.wireOp",EDGE,"E2167"),sQuery(id+"F11.wireOp",EDGE,"E2168"),sQuery(id+"F11.wireOp",EDGE,"E2169"),sQuery(id+"F11.wireOp",EDGE,"E2170"),sQuery(id+"F11.wireOp",EDGE,"E2171"),sQuery(id+"F11.wireOp",EDGE,"E2172"),sQuery(id+"F11.wireOp",EDGE,"E2173"),sQuery(id+"F11.wireOp",EDGE,"E2174"),sQuery(id+"F11.wireOp",EDGE,"E2175"),sQuery(id+"F11.wireOp",EDGE,"E2176"),sQuery(id+"F11.wireOp",EDGE,"E2177"),sQuery(id+"F11.wireOp",EDGE,"E2178"),sQuery(id+"F11.wireOp",EDGE,"E2179"),sQuery(id+"F11.wireOp",EDGE,"E2180"),sQuery(id+"F11.wireOp",EDGE,"E2181"),sQuery(id+"F11.wireOp",EDGE,"E2182"),sQuery(id+"F11.wireOp",EDGE,"E2183"),sQuery(id+"F11.wireOp",EDGE,"E2184"),sQuery(id+"F11.wireOp",EDGE,"E2185"),sQuery(id+"F11.wireOp",EDGE,"E2186"),sQuery(id+"F11.wireOp",EDGE,"E2187"),sQuery(id+"F11.wireOp",EDGE,"E2188"),sQuery(id+"F11.wireOp",EDGE,"E2189"),sQuery(id+"F11.wireOp",EDGE,"E2190"),sQuery(id+"F11.wireOp",EDGE,"E2191"),sQuery(id+"F11.wireOp",EDGE,"E2192"),sQuery(id+"F11.wireOp",EDGE,"E2193"),sQuery(id+"F11.wireOp",EDGE,"E2194"),sQuery(id+"F11.wireOp",EDGE,"E2195"),sQuery(id+"F11.wireOp",EDGE,"E2196"),sQuery(id+"F11.wireOp",EDGE,"E2197"),sQuery(id+"F11.wireOp",EDGE,"E2198"),sQuery(id+"F11.wireOp",EDGE,"E2199"),sQuery(id+"F11.wireOp",EDGE,"E2200"),sQuery(id+"F11.wireOp",EDGE,"E2201"),sQuery(id+"F11.wireOp",EDGE,"E2202"),sQuery(id+"F11.wireOp",EDGE,"E2203"),sQuery(id+"F11.wireOp",EDGE,"E2204"),sQuery(id+"F11.wireOp",EDGE,"E2205"),sQuery(id+"F11.wireOp",EDGE,"E2206"),sQuery(id+"F11.wireOp",EDGE,"E2207"),sQuery(id+"F11.wireOp",EDGE,"E2208"),sQuery(id+"F11.wireOp",EDGE,"E2209"),sQuery(id+"F11.wireOp",EDGE,"E2210"),sQuery(id+"F11.wireOp",EDGE,"E2211"),sQuery(id+"F11.wireOp",EDGE,"E2212"),sQuery(id+"F11.wireOp",EDGE,"E2213"),sQuery(id+"F11.wireOp",EDGE,"E2214"),sQuery(id+"F11.wireOp",EDGE,"E2215"),sQuery(id+"F11.wireOp",EDGE,"E2216"),sQuery(id+"F11.wireOp",EDGE,"E2217"),sQuery(id+"F11.wireOp",EDGE,"E2218"),sQuery(id+"F11.wireOp",EDGE,"E2219"),sQuery(id+"F11.wireOp",EDGE,"E2220"),sQuery(id+"F11.wireOp",EDGE,"E2221"),sQuery(id+"F11.wireOp",EDGE,"E2222"),sQuery(id+"F11.wireOp",EDGE,"E2223"),sQuery(id+"F11.wireOp",EDGE,"E2224"),sQuery(id+"F11.wireOp",EDGE,"E2225"),sQuery(id+"F11.wireOp",EDGE,"E2226"),sQuery(id+"F11.wireOp",EDGE,"E2227"),sQuery(id+"F11.wireOp",EDGE,"E2228"),sQuery(id+"F11.wireOp",EDGE,"E2229"),sQuery(id+"F11.wireOp",EDGE,"E2230"),sQuery(id+"F11.wireOp",EDGE,"E2231"),sQuery(id+"F11.wireOp",EDGE,"E2232"),sQuery(id+"F11.wireOp",EDGE,"E2233"),sQuery(id+"F11.wireOp",EDGE,"E2234"),sQuery(id+"F11.wireOp",EDGE,"E2235"),sQuery(id+"F11.wireOp",EDGE,"E2236"),sQuery(id+"F11.wireOp",EDGE,"E2237"),sQuery(id+"F11.wireOp",EDGE,"E2238"),sQuery(id+"F11.wireOp",EDGE,"E2239"),sQuery(id+"F11.wireOp",EDGE,"E2240"),sQuery(id+"F11.wireOp",EDGE,"E2241"),sQuery(id+"F11.wireOp",EDGE,"E2242"),sQuery(id+"F11.wireOp",EDGE,"E2243"),sQuery(id+"F11.wireOp",EDGE,"E2244"),sQuery(id+"F11.wireOp",EDGE,"E2245"),sQuery(id+"F11.wireOp",EDGE,"E2246"),sQuery(id+"F11.wireOp",EDGE,"E2247"),sQuery(id+"F11.wireOp",EDGE,"E2248"),sQuery(id+"F11.wireOp",EDGE,"E2249"),sQuery(id+"F11.wireOp",EDGE,"E2250"),sQuery(id+"F11.wireOp",EDGE,"E2251"),sQuery(id+"F11.wireOp",EDGE,"E2252"),sQuery(id+"F11.wireOp",EDGE,"E2253"),sQuery(id+"F11.wireOp",EDGE,"E2254"),sQuery(id+"F11.wireOp",EDGE,"E2255"),sQuery(id+"F11.wireOp",EDGE,"E2256"),sQuery(id+"F11.wireOp",EDGE,"E2257"),sQuery(id+"F11.wireOp",EDGE,"E2258"),sQuery(id+"F11.wireOp",EDGE,"E2259"),sQuery(id+"F11.wireOp",EDGE,"E2260"),sQuery(id+"F11.wireOp",EDGE,"E2261"),sQuery(id+"F11.wireOp",EDGE,"E2262"),sQuery(id+"F11.wireOp",EDGE,"E2263"),sQuery(id+"F11.wireOp",EDGE,"E2264"),sQuery(id+"F11.wireOp",EDGE,"E2265"),sQuery(id+"F11.wireOp",EDGE,"E2266"),sQuery(id+"F11.wireOp",EDGE,"E2267"),sQuery(id+"F11.wireOp",EDGE,"E2268"),sQuery(id+"F11.wireOp",EDGE,"E2269"),sQuery(id+"F11.wireOp",EDGE,"E2270"),sQuery(id+"F11.wireOp",EDGE,"E2271"),sQuery(id+"F11.wireOp",EDGE,"E2272"),sQuery(id+"F11.wireOp",EDGE,"E2273"),sQuery(id+"F11.wireOp",EDGE,"E2274"),sQuery(id+"F11.wireOp",EDGE,"E2275"),sQuery(id+"F11.wireOp",EDGE,"E2276"),sQuery(id+"F11.wireOp",EDGE,"E2277"),sQuery(id+"F11.wireOp",EDGE,"E2278"),sQuery(id+"F11.wireOp",EDGE,"E2279"),sQuery(id+"F11.wireOp",EDGE,"E2280"),sQuery(id+"F11.wireOp",EDGE,"E2281"),sQuery(id+"F11.wireOp",EDGE,"E2282"),sQuery(id+"F11.wireOp",EDGE,"E2283"),sQuery(id+"F11.wireOp",EDGE,"E2284"),sQuery(id+"F11.wireOp",EDGE,"E2285"),sQuery(id+"F11.wireOp",EDGE,"E2286"),sQuery(id+"F11.wireOp",EDGE,"E2287"),sQuery(id+"F11.wireOp",EDGE,"E2288"),sQuery(id+"F11.wireOp",EDGE,"E2289"),sQuery(id+"F11.wireOp",EDGE,"E2290"),sQuery(id+"F11.wireOp",EDGE,"E2291"),sQuery(id+"F11.wireOp",EDGE,"E2292"),sQuery(id+"F11.wireOp",EDGE,"E2293"),sQuery(id+"F11.wireOp",EDGE,"E2294"),sQuery(id+"F11.wireOp",EDGE,"E2295"),sQuery(id+"F11.wireOp",EDGE,"E2296"),sQuery(id+"F11.wireOp",EDGE,"E2297"),sQuery(id+"F11.wireOp",EDGE,"E2298"),sQuery(id+"F11.wireOp",EDGE,"E2299"),sQuery(id+"F11.wireOp",EDGE,"E2300"),sQuery(id+"F11.wireOp",EDGE,"E2301"),sQuery(id+"F11.wireOp",EDGE,"E2302"),sQuery(id+"F11.wireOp",EDGE,"E2303"),sQuery(id+"F11.wireOp",EDGE,"E2304"),sQuery(id+"F11.wireOp",EDGE,"E2305"),sQuery(id+"F11.wireOp",EDGE,"E2306"),sQuery(id+"F11.wireOp",EDGE,"E2307"),sQuery(id+"F11.wireOp",EDGE,"E2308"),sQuery(id+"F11.wireOp",EDGE,"E2309"),sQuery(id+"F11.wireOp",EDGE,"E2310"),sQuery(id+"F11.wireOp",EDGE,"E2311"),sQuery(id+"F11.wireOp",EDGE,"E2312"),sQuery(id+"F11.wireOp",EDGE,"E2313"),sQuery(id+"F11.wireOp",EDGE,"E2314"),sQuery(id+"F11.wireOp",EDGE,"E2315"),sQuery(id+"F11.wireOp",EDGE,"E2316"),sQuery(id+"F11.wireOp",EDGE,"E2317"),sQuery(id+"F11.wireOp",EDGE,"E2318"),sQuery(id+"F11.wireOp",EDGE,"E2319"),sQuery(id+"F11.wireOp",EDGE,"E2320"),sQuery(id+"F11.wireOp",EDGE,"E2321"),sQuery(id+"F11.wireOp",EDGE,"E2322"),sQuery(id+"F11.wireOp",EDGE,"E2323"),sQuery(id+"F11.wireOp",EDGE,"E2324"),sQuery(id+"F11.wireOp",EDGE,"E2325"),sQuery(id+"F11.wireOp",EDGE,"E2326"),sQuery(id+"F11.wireOp",EDGE,"E2327"),sQuery(id+"F11.wireOp",EDGE,"E2328"),sQuery(id+"F11.wireOp",EDGE,"E2329"),sQuery(id+"F11.wireOp",EDGE,"E2330"),sQuery(id+"F11.wireOp",EDGE,"E2331"),sQuery(id+"F11.wireOp",EDGE,"E2332"),sQuery(id+"F11.wireOp",EDGE,"E2333"),sQuery(id+"F11.wireOp",EDGE,"E2334"),sQuery(id+"F11.wireOp",EDGE,"E2335"),sQuery(id+"F11.wireOp",EDGE,"E2336"),sQuery(id+"F11.wireOp",EDGE,"E2337"),sQuery(id+"F11.wireOp",EDGE,"E2338"),sQuery(id+"F11.wireOp",EDGE,"E2339"),sQuery(id+"F11.wireOp",EDGE,"E2340"),sQuery(id+"F11.wireOp",EDGE,"E2341"),sQuery(id+"F11.wireOp",EDGE,"E2342"),sQuery(id+"F11.wireOp",EDGE,"E2343"),sQuery(id+"F11.wireOp",EDGE,"E2344"),sQuery(id+"F11.wireOp",EDGE,"E2345"),sQuery(id+"F11.wireOp",EDGE,"E2346"),sQuery(id+"F11.wireOp",EDGE,"E2347"),sQuery(id+"F11.wireOp",EDGE,"E2348"),sQuery(id+"F11.wireOp",EDGE,"E2349"),sQuery(id+"F11.wireOp",EDGE,"E2350"),sQuery(id+"F11.wireOp",EDGE,"E2351"),sQuery(id+"F11.wireOp",EDGE,"E2352"),sQuery(id+"F11.wireOp",EDGE,"E2353"),sQuery(id+"F11.wireOp",EDGE,"E2354"),sQuery(id+"F11.wireOp",EDGE,"E2355"),sQuery(id+"F11.wireOp",EDGE,"E2356"),sQuery(id+"F11.wireOp",EDGE,"E2357"),sQuery(id+"F11.wireOp",EDGE,"E2358"),sQuery(id+"F11.wireOp",EDGE,"E2359"),sQuery(id+"F11.wireOp",EDGE,"E2360"),sQuery(id+"F11.wireOp",EDGE,"E2361"),sQuery(id+"F11.wireOp",EDGE,"E2362"),sQuery(id+"F11.wireOp",EDGE,"E2363"),sQuery(id+"F11.wireOp",EDGE,"E2364"),sQuery(id+"F11.wireOp",EDGE,"E2365"),sQuery(id+"F11.wireOp",EDGE,"E2366"),sQuery(id+"F11.wireOp",EDGE,"E2367"),sQuery(id+"F11.wireOp",EDGE,"E2368"),sQuery(id+"F11.wireOp",EDGE,"E2369"),sQuery(id+"F11.wireOp",EDGE,"E2370"),sQuery(id+"F11.wireOp",EDGE,"E2371"),sQuery(id+"F11.wireOp",EDGE,"E2372"),sQuery(id+"F11.wireOp",EDGE,"E2373"),sQuery(id+"F11.wireOp",EDGE,"E2374"),sQuery(id+"F11.wireOp",EDGE,"E2375"),sQuery(id+"F11.wireOp",EDGE,"E2376"),sQuery(id+"F11.wireOp",EDGE,"E2377"),sQuery(id+"F11.wireOp",EDGE,"E2378"),sQuery(id+"F11.wireOp",EDGE,"E2379"),sQuery(id+"F11.wireOp",EDGE,"E2380"),sQuery(id+"F11.wireOp",EDGE,"E2381"),sQuery(id+"F11.wireOp",EDGE,"E2382"),sQuery(id+"F11.wireOp",EDGE,"E2383"),sQuery(id+"F11.wireOp",EDGE,"E2384"),sQuery(id+"F11.wireOp",EDGE,"E2385"),sQuery(id+"F11.wireOp",EDGE,"E2386"),sQuery(id+"F11.wireOp",EDGE,"E2387"),sQuery(id+"F11.wireOp",EDGE,"E2388"),sQuery(id+"F11.wireOp",EDGE,"E2389"),sQuery(id+"F11.wireOp",EDGE,"E2390"),sQuery(id+"F11.wireOp",EDGE,"E2391"),sQuery(id+"F11.wireOp",EDGE,"E2392"),sQuery(id+"F11.wireOp",EDGE,"E2393"),sQuery(id+"F11.wireOp",EDGE,"E2394"),sQuery(id+"F11.wireOp",EDGE,"E2395"),sQuery(id+"F11.wireOp",EDGE,"E2396"),sQuery(id+"F11.wireOp",EDGE,"E2397"),sQuery(id+"F11.wireOp",EDGE,"E2398"),sQuery(id+"F11.wireOp",EDGE,"E2399"),sQuery(id+"F11.wireOp",EDGE,"E2400"),sQuery(id+"F11.wireOp",EDGE,"E2401"),sQuery(id+"F11.wireOp",EDGE,"E2402"),sQuery(id+"F11.wireOp",EDGE,"E2403"),sQuery(id+"F11.wireOp",EDGE,"E2404"),sQuery(id+"F11.wireOp",EDGE,"E2405"),sQuery(id+"F11.wireOp",EDGE,"E2406"),sQuery(id+"F11.wireOp",EDGE,"E2407"),sQuery(id+"F11.wireOp",EDGE,"E2408"),sQuery(id+"F11.wireOp",EDGE,"E2409"),sQuery(id+"F11.wireOp",EDGE,"E2410"),sQuery(id+"F11.wireOp",EDGE,"E2411"),sQuery(id+"F11.wireOp",EDGE,"E2412"),sQuery(id+"F11.wireOp",EDGE,"E2413"),sQuery(id+"F11.wireOp",EDGE,"E2414"),sQuery(id+"F11.wireOp",EDGE,"E2415"),sQuery(id+"F11.wireOp",EDGE,"E2416"),sQuery(id+"F11.wireOp",EDGE,"E2417"),sQuery(id+"F11.wireOp",EDGE,"E2418"),sQuery(id+"F11.wireOp",EDGE,"E2419"),sQuery(id+"F11.wireOp",EDGE,"E2420"),sQuery(id+"F11.wireOp",EDGE,"E2421"),sQuery(id+"F11.wireOp",EDGE,"E2422"),sQuery(id+"F11.wireOp",EDGE,"E2423"),sQuery(id+"F11.wireOp",EDGE,"E2424"),sQuery(id+"F11.wireOp",EDGE,"E2425"),sQuery(id+"F11.wireOp",EDGE,"E2426"),sQuery(id+"F11.wireOp",EDGE,"E2427"),sQuery(id+"F11.wireOp",EDGE,"E2428"),sQuery(id+"F11.wireOp",EDGE,"E2429"),sQuery(id+"F11.wireOp",EDGE,"E2430"),sQuery(id+"F11.wireOp",EDGE,"E2431"),sQuery(id+"F11.wireOp",EDGE,"E2432"),sQuery(id+"F11.wireOp",EDGE,"E2433"),sQuery(id+"F11.wireOp",EDGE,"E2434"),sQuery(id+"F11.wireOp",EDGE,"E2435"),sQuery(id+"F11.wireOp",EDGE,"E2436"),sQuery(id+"F11.wireOp",EDGE,"E2437"),sQuery(id+"F11.wireOp",EDGE,"E2438"),sQuery(id+"F11.wireOp",EDGE,"E2439"),sQuery(id+"F11.wireOp",EDGE,"E2440"),sQuery(id+"F11.wireOp",EDGE,"E2441"),sQuery(id+"F11.wireOp",EDGE,"E2442"),sQuery(id+"F11.wireOp",EDGE,"E2443"),sQuery(id+"F11.wireOp",EDGE,"E2444"),sQuery(id+"F11.wireOp",EDGE,"E2445"),sQuery(id+"F11.wireOp",EDGE,"E2446"),sQuery(id+"F11.wireOp",EDGE,"E2447"),sQuery(id+"F11.wireOp",EDGE,"E2448"),sQuery(id+"F11.wireOp",EDGE,"E2449"),sQuery(id+"F11.wireOp",EDGE,"E2450"),sQuery(id+"F11.wireOp",EDGE,"E2451"),sQuery(id+"F11.wireOp",EDGE,"E2452"),sQuery(id+"F11.wireOp",EDGE,"E2453"),sQuery(id+"F11.wireOp",EDGE,"E2454"),sQuery(id+"F11.wireOp",EDGE,"E2455"),sQuery(id+"F11.wireOp",EDGE,"E2456"),sQuery(id+"F11.wireOp",EDGE,"E2457"),sQuery(id+"F11.wireOp",EDGE,"E2458"),sQuery(id+"F11.wireOp",EDGE,"E2459"),sQuery(id+"F11.wireOp",EDGE,"E2460"),sQuery(id+"F11.wireOp",EDGE,"E2461"),sQuery(id+"F11.wireOp",EDGE,"E2462"),sQuery(id+"F11.wireOp",EDGE,"E2463"),sQuery(id+"F11.wireOp",EDGE,"E2464"),sQuery(id+"F11.wireOp",EDGE,"E2465"),sQuery(id+"F11.wireOp",EDGE,"E2466"),sQuery(id+"F11.wireOp",EDGE,"E2467"),sQuery(id+"F11.wireOp",EDGE,"E2468"),sQuery(id+"F11.wireOp",EDGE,"E2469"),sQuery(id+"F11.wireOp",EDGE,"E2470"),sQuery(id+"F11.wireOp",EDGE,"E2471"),sQuery(id+"F11.wireOp",EDGE,"E2472"),sQuery(id+"F11.wireOp",EDGE,"E2473"),sQuery(id+"F11.wireOp",EDGE,"E2474"),sQuery(id+"F11.wireOp",EDGE,"E2475"),sQuery(id+"F11.wireOp",EDGE,"E2476"),sQuery(id+"F11.wireOp",EDGE,"E2477"),sQuery(id+"F11.wireOp",EDGE,"E2478"),sQuery(id+"F11.wireOp",EDGE,"E2479"),sQuery(id+"F11.wireOp",EDGE,"E2480"),sQuery(id+"F11.wireOp",EDGE,"E2481"),sQuery(id+"F11.wireOp",EDGE,"E2482"),sQuery(id+"F11.wireOp",EDGE,"E2483"),sQuery(id+"F11.wireOp",EDGE,"E2484"),sQuery(id+"F11.wireOp",EDGE,"E2485"),sQuery(id+"F11.wireOp",EDGE,"E2486"),sQuery(id+"F11.wireOp",EDGE,"E2487"),sQuery(id+"F11.wireOp",EDGE,"E2488"),sQuery(id+"F11.wireOp",EDGE,"E2489"),sQuery(id+"F11.wireOp",EDGE,"E2490"),sQuery(id+"F11.wireOp",EDGE,"E2491"),sQuery(id+"F11.wireOp",EDGE,"E2492"),sQuery(id+"F11.wireOp",EDGE,"E2493"),sQuery(id+"F11.wireOp",EDGE,"E2494"),sQuery(id+"F11.wireOp",EDGE,"E2495"),sQuery(id+"F11.wireOp",EDGE,"E2496"),sQuery(id+"F11.wireOp",EDGE,"E2497"),sQuery(id+"F11.wireOp",EDGE,"E2498"),sQuery(id+"F11.wireOp",EDGE,"E2499"),sQuery(id+"F11.wireOp",EDGE,"E2500"),sQuery(id+"F11.wireOp",EDGE,"E2501"),sQuery(id+"F11.wireOp",EDGE,"E2502"),sQuery(id+"F11.wireOp",EDGE,"E2503"),sQuery(id+"F11.wireOp",EDGE,"E2504"),sQuery(id+"F11.wireOp",EDGE,"E2505"),sQuery(id+"F11.wireOp",EDGE,"E2506"),sQuery(id+"F11.wireOp",EDGE,"E2507"),sQuery(id+"F11.wireOp",EDGE,"E2508"),sQuery(id+"F11.wireOp",EDGE,"E2509"),sQuery(id+"F11.wireOp",EDGE,"E2510"),sQuery(id+"F11.wireOp",EDGE,"E2511"),sQuery(id+"F11.wireOp",EDGE,"E2512"),sQuery(id+"F11.wireOp",EDGE,"E2513"),sQuery(id+"F11.wireOp",EDGE,"E2514"),sQuery(id+"F11.wireOp",EDGE,"E2515"),sQuery(id+"F11.wireOp",EDGE,"E2516"),sQuery(id+"F11.wireOp",EDGE,"E2517"),sQuery(id+"F11.wireOp",EDGE,"E2518"),sQuery(id+"F11.wireOp",EDGE,"E2519"),sQuery(id+"F11.wireOp",EDGE,"E2520"),sQuery(id+"F11.wireOp",EDGE,"E2521"),sQuery(id+"F11.wireOp",EDGE,"E2522"),sQuery(id+"F11.wireOp",EDGE,"E2523"),sQuery(id+"F11.wireOp",EDGE,"E2524"),sQuery(id+"F11.wireOp",EDGE,"E2525"),sQuery(id+"F11.wireOp",EDGE,"E2526"),sQuery(id+"F11.wireOp",EDGE,"E2527"),sQuery(id+"F11.wireOp",EDGE,"E2528"),sQuery(id+"F11.wireOp",EDGE,"E2529"),sQuery(id+"F11.wireOp",EDGE,"E2530"),sQuery(id+"F11.wireOp",EDGE,"E2531"),sQuery(id+"F11.wireOp",EDGE,"E2532"),sQuery(id+"F11.wireOp",EDGE,"E2533"),sQuery(id+"F11.wireOp",EDGE,"E2534"),sQuery(id+"F11.wireOp",EDGE,"E2535"),sQuery(id+"F11.wireOp",EDGE,"E2536"),sQuery(id+"F11.wireOp",EDGE,"E2537"),sQuery(id+"F11.wireOp",EDGE,"E2538"),sQuery(id+"F11.wireOp",EDGE,"E2539"),sQuery(id+"F11.wireOp",EDGE,"E2540"),sQuery(id+"F11.wireOp",EDGE,"E2541"),sQuery(id+"F11.wireOp",EDGE,"E2542"),sQuery(id+"F11.wireOp",EDGE,"E2543"),sQuery(id+"F11.wireOp",EDGE,"E2544"),sQuery(id+"F11.wireOp",EDGE,"E2545"),sQuery(id+"F11.wireOp",EDGE,"E2546"),sQuery(id+"F11.wireOp",EDGE,"E2547"),sQuery(id+"F11.wireOp",EDGE,"E2548"),sQuery(id+"F11.wireOp",EDGE,"E2549"),sQuery(id+"F11.wireOp",EDGE,"E2550"),sQuery(id+"F11.wireOp",EDGE,"E2551"),sQuery(id+"F11.wireOp",EDGE,"E2552"),sQuery(id+"F11.wireOp",EDGE,"E2553"),sQuery(id+"F11.wireOp",EDGE,"E2554"),sQuery(id+"F11.wireOp",EDGE,"E2555"),sQuery(id+"F11.wireOp",EDGE,"E2556"),sQuery(id+"F11.wireOp",EDGE,"E2557"),sQuery(id+"F11.wireOp",EDGE,"E2558"),sQuery(id+"F11.wireOp",EDGE,"E2559"),sQuery(id+"F11.wireOp",EDGE,"E2560"),sQuery(id+"F11.wireOp",EDGE,"E2561"),sQuery(id+"F11.wireOp",EDGE,"E2562"),sQuery(id+"F11.wireOp",EDGE,"E2563"),sQuery(id+"F11.wireOp",EDGE,"E2564"),sQuery(id+"F11.wireOp",EDGE,"E2565"),sQuery(id+"F11.wireOp",EDGE,"E2566"),sQuery(id+"F11.wireOp",EDGE,"E2567"),sQuery(id+"F11.wireOp",EDGE,"E2568"),sQuery(id+"F11.wireOp",EDGE,"E2569"),sQuery(id+"F11.wireOp",EDGE,"E2570"),sQuery(id+"F11.wireOp",EDGE,"E2571"),sQuery(id+"F11.wireOp",EDGE,"E2572"),sQuery(id+"F11.wireOp",EDGE,"E2573"),sQuery(id+"F11.wireOp",EDGE,"E2574"),sQuery(id+"F11.wireOp",EDGE,"E2575"),sQuery(id+"F11.wireOp",EDGE,"E2576"),sQuery(id+"F11.wireOp",EDGE,"E2577"),sQuery(id+"F11.wireOp",EDGE,"E2578"),sQuery(id+"F11.wireOp",EDGE,"E2579"),sQuery(id+"F11.wireOp",EDGE,"E2580"),sQuery(id+"F11.wireOp",EDGE,"E2581"),sQuery(id+"F11.wireOp",EDGE,"E2582"),sQuery(id+"F11.wireOp",EDGE,"E2583"),sQuery(id+"F11.wireOp",EDGE,"E2584"),sQuery(id+"F11.wireOp",EDGE,"E2585"),sQuery(id+"F11.wireOp",EDGE,"E2586"),sQuery(id+"F11.wireOp",EDGE,"E2587"),sQuery(id+"F11.wireOp",EDGE,"E2588"),sQuery(id+"F11.wireOp",EDGE,"E2589"),sQuery(id+"F11.wireOp",EDGE,"E2590"),sQuery(id+"F11.wireOp",EDGE,"E2591"),sQuery(id+"F11.wireOp",EDGE,"E2592"),sQuery(id+"F11.wireOp",EDGE,"E2593"),sQuery(id+"F11.wireOp",EDGE,"E2594"),sQuery(id+"F11.wireOp",EDGE,"E2595"),sQuery(id+"F11.wireOp",EDGE,"E2596"),sQuery(id+"F11.wireOp",EDGE,"E2597"),sQuery(id+"F11.wireOp",EDGE,"E2598")])]});
            var Q1;
            Q1=sQuery(id+"F1.wireOp",EDGE,"E15");
            transform(context, id + "F15", {"entities" : qUnion([Q0]), "transformType" : TransformType.ROTATION, "transformAxis" : qUnion([Q1]), "angle" : 90 * degree, "makeCopy" : false});
        }
        {
            var Q0;
            Q0=makeQuery(id+"F12.opExtrude","SWEPT_BODY",BODY,{"disambiguationData":[OSD([sQuery(id+"F11.wireOp",EDGE,"E1476"),sQuery(id+"F11.wireOp",EDGE,"E1477"),sQuery(id+"F11.wireOp",EDGE,"E1478"),sQuery(id+"F11.wireOp",EDGE,"E1479"),sQuery(id+"F11.wireOp",EDGE,"E1480"),sQuery(id+"F11.wireOp",EDGE,"E1481"),sQuery(id+"F11.wireOp",EDGE,"E1482"),sQuery(id+"F11.wireOp",EDGE,"E1483"),sQuery(id+"F11.wireOp",EDGE,"E1484"),sQuery(id+"F11.wireOp",EDGE,"E1485"),sQuery(id+"F11.wireOp",EDGE,"E1486"),sQuery(id+"F11.wireOp",EDGE,"E1487"),sQuery(id+"F11.wireOp",EDGE,"E1488"),sQuery(id+"F11.wireOp",EDGE,"E1489"),sQuery(id+"F11.wireOp",EDGE,"E1490"),sQuery(id+"F11.wireOp",EDGE,"E1491"),sQuery(id+"F11.wireOp",EDGE,"E1492"),sQuery(id+"F11.wireOp",EDGE,"E1493"),sQuery(id+"F11.wireOp",EDGE,"E1494"),sQuery(id+"F11.wireOp",EDGE,"E1495"),sQuery(id+"F11.wireOp",EDGE,"E1496"),sQuery(id+"F11.wireOp",EDGE,"E1497"),sQuery(id+"F11.wireOp",EDGE,"E1498"),sQuery(id+"F11.wireOp",EDGE,"E1499"),sQuery(id+"F11.wireOp",EDGE,"E1500"),sQuery(id+"F11.wireOp",EDGE,"E1501"),sQuery(id+"F11.wireOp",EDGE,"E1502"),sQuery(id+"F11.wireOp",EDGE,"E1503"),sQuery(id+"F11.wireOp",EDGE,"E1504"),sQuery(id+"F11.wireOp",EDGE,"E1505"),sQuery(id+"F11.wireOp",EDGE,"E1506"),sQuery(id+"F11.wireOp",EDGE,"E1507"),sQuery(id+"F11.wireOp",EDGE,"E1508"),sQuery(id+"F11.wireOp",EDGE,"E1509"),sQuery(id+"F11.wireOp",EDGE,"E1510"),sQuery(id+"F11.wireOp",EDGE,"E1511"),sQuery(id+"F11.wireOp",EDGE,"E1512"),sQuery(id+"F11.wireOp",EDGE,"E1513"),sQuery(id+"F11.wireOp",EDGE,"E1514"),sQuery(id+"F11.wireOp",EDGE,"E1515"),sQuery(id+"F11.wireOp",EDGE,"E1516"),sQuery(id+"F11.wireOp",EDGE,"E1517"),sQuery(id+"F11.wireOp",EDGE,"E1518"),sQuery(id+"F11.wireOp",EDGE,"E1519"),sQuery(id+"F11.wireOp",EDGE,"E1520"),sQuery(id+"F11.wireOp",EDGE,"E1521"),sQuery(id+"F11.wireOp",EDGE,"E1522"),sQuery(id+"F11.wireOp",EDGE,"E1523"),sQuery(id+"F11.wireOp",EDGE,"E1524"),sQuery(id+"F11.wireOp",EDGE,"E1525"),sQuery(id+"F11.wireOp",EDGE,"E1526"),sQuery(id+"F11.wireOp",EDGE,"E1527"),sQuery(id+"F11.wireOp",EDGE,"E1528"),sQuery(id+"F11.wireOp",EDGE,"E1529"),sQuery(id+"F11.wireOp",EDGE,"E1530"),sQuery(id+"F11.wireOp",EDGE,"E1531"),sQuery(id+"F11.wireOp",EDGE,"E1532"),sQuery(id+"F11.wireOp",EDGE,"E1533"),sQuery(id+"F11.wireOp",EDGE,"E1534"),sQuery(id+"F11.wireOp",EDGE,"E1535"),sQuery(id+"F11.wireOp",EDGE,"E1536"),sQuery(id+"F11.wireOp",EDGE,"E1537"),sQuery(id+"F11.wireOp",EDGE,"E1538"),sQuery(id+"F11.wireOp",EDGE,"E1539"),sQuery(id+"F11.wireOp",EDGE,"E1540"),sQuery(id+"F11.wireOp",EDGE,"E1541"),sQuery(id+"F11.wireOp",EDGE,"E1542"),sQuery(id+"F11.wireOp",EDGE,"E1543"),sQuery(id+"F11.wireOp",EDGE,"E1544"),sQuery(id+"F11.wireOp",EDGE,"E1545"),sQuery(id+"F11.wireOp",EDGE,"E1546"),sQuery(id+"F11.wireOp",EDGE,"E1547"),sQuery(id+"F11.wireOp",EDGE,"E1548"),sQuery(id+"F11.wireOp",EDGE,"E1549"),sQuery(id+"F11.wireOp",EDGE,"E1550"),sQuery(id+"F11.wireOp",EDGE,"E1551"),sQuery(id+"F11.wireOp",EDGE,"E1552"),sQuery(id+"F11.wireOp",EDGE,"E1553"),sQuery(id+"F11.wireOp",EDGE,"E1554"),sQuery(id+"F11.wireOp",EDGE,"E1555"),sQuery(id+"F11.wireOp",EDGE,"E1556"),sQuery(id+"F11.wireOp",EDGE,"E1557"),sQuery(id+"F11.wireOp",EDGE,"E1558"),sQuery(id+"F11.wireOp",EDGE,"E1559"),sQuery(id+"F11.wireOp",EDGE,"E1560"),sQuery(id+"F11.wireOp",EDGE,"E1561"),sQuery(id+"F11.wireOp",EDGE,"E1562"),sQuery(id+"F11.wireOp",EDGE,"E1563"),sQuery(id+"F11.wireOp",EDGE,"E1564"),sQuery(id+"F11.wireOp",EDGE,"E1565"),sQuery(id+"F11.wireOp",EDGE,"E1566"),sQuery(id+"F11.wireOp",EDGE,"E1567"),sQuery(id+"F11.wireOp",EDGE,"E1568"),sQuery(id+"F11.wireOp",EDGE,"E1569"),sQuery(id+"F11.wireOp",EDGE,"E1570"),sQuery(id+"F11.wireOp",EDGE,"E1571"),sQuery(id+"F11.wireOp",EDGE,"E1572"),sQuery(id+"F11.wireOp",EDGE,"E1573"),sQuery(id+"F11.wireOp",EDGE,"E1574"),sQuery(id+"F11.wireOp",EDGE,"E1575"),sQuery(id+"F11.wireOp",EDGE,"E1576"),sQuery(id+"F11.wireOp",EDGE,"E1577"),sQuery(id+"F11.wireOp",EDGE,"E1578"),sQuery(id+"F11.wireOp",EDGE,"E1579"),sQuery(id+"F11.wireOp",EDGE,"E1580"),sQuery(id+"F11.wireOp",EDGE,"E1581"),sQuery(id+"F11.wireOp",EDGE,"E1582"),sQuery(id+"F11.wireOp",EDGE,"E1583"),sQuery(id+"F11.wireOp",EDGE,"E1584"),sQuery(id+"F11.wireOp",EDGE,"E1585"),sQuery(id+"F11.wireOp",EDGE,"E1586"),sQuery(id+"F11.wireOp",EDGE,"E1587"),sQuery(id+"F11.wireOp",EDGE,"E1588"),sQuery(id+"F11.wireOp",EDGE,"E1589"),sQuery(id+"F11.wireOp",EDGE,"E1590"),sQuery(id+"F11.wireOp",EDGE,"E1591"),sQuery(id+"F11.wireOp",EDGE,"E1592"),sQuery(id+"F11.wireOp",EDGE,"E1593"),sQuery(id+"F11.wireOp",EDGE,"E1594"),sQuery(id+"F11.wireOp",EDGE,"E1595"),sQuery(id+"F11.wireOp",EDGE,"E1596"),sQuery(id+"F11.wireOp",EDGE,"E1597"),sQuery(id+"F11.wireOp",EDGE,"E1598"),sQuery(id+"F11.wireOp",EDGE,"E1599"),sQuery(id+"F11.wireOp",EDGE,"E1600"),sQuery(id+"F11.wireOp",EDGE,"E1601"),sQuery(id+"F11.wireOp",EDGE,"E1602"),sQuery(id+"F11.wireOp",EDGE,"E1603"),sQuery(id+"F11.wireOp",EDGE,"E1604"),sQuery(id+"F11.wireOp",EDGE,"E1605"),sQuery(id+"F11.wireOp",EDGE,"E1606"),sQuery(id+"F11.wireOp",EDGE,"E1607"),sQuery(id+"F11.wireOp",EDGE,"E1608"),sQuery(id+"F11.wireOp",EDGE,"E1609"),sQuery(id+"F11.wireOp",EDGE,"E1610"),sQuery(id+"F11.wireOp",EDGE,"E1611"),sQuery(id+"F11.wireOp",EDGE,"E1612"),sQuery(id+"F11.wireOp",EDGE,"E1613"),sQuery(id+"F11.wireOp",EDGE,"E1614"),sQuery(id+"F11.wireOp",EDGE,"E1615"),sQuery(id+"F11.wireOp",EDGE,"E1616"),sQuery(id+"F11.wireOp",EDGE,"E1617"),sQuery(id+"F11.wireOp",EDGE,"E1618"),sQuery(id+"F11.wireOp",EDGE,"E1619"),sQuery(id+"F11.wireOp",EDGE,"E1620"),sQuery(id+"F11.wireOp",EDGE,"E1621"),sQuery(id+"F11.wireOp",EDGE,"E1622"),sQuery(id+"F11.wireOp",EDGE,"E1623"),sQuery(id+"F11.wireOp",EDGE,"E1624"),sQuery(id+"F11.wireOp",EDGE,"E1625"),sQuery(id+"F11.wireOp",EDGE,"E1626"),sQuery(id+"F11.wireOp",EDGE,"E1627"),sQuery(id+"F11.wireOp",EDGE,"E1628"),sQuery(id+"F11.wireOp",EDGE,"E1629"),sQuery(id+"F11.wireOp",EDGE,"E1630"),sQuery(id+"F11.wireOp",EDGE,"E1631"),sQuery(id+"F11.wireOp",EDGE,"E1632"),sQuery(id+"F11.wireOp",EDGE,"E1633"),sQuery(id+"F11.wireOp",EDGE,"E1634"),sQuery(id+"F11.wireOp",EDGE,"E1635"),sQuery(id+"F11.wireOp",EDGE,"E1636"),sQuery(id+"F11.wireOp",EDGE,"E1637"),sQuery(id+"F11.wireOp",EDGE,"E1638"),sQuery(id+"F11.wireOp",EDGE,"E1639"),sQuery(id+"F11.wireOp",EDGE,"E1640"),sQuery(id+"F11.wireOp",EDGE,"E1641"),sQuery(id+"F11.wireOp",EDGE,"E1642"),sQuery(id+"F11.wireOp",EDGE,"E1643"),sQuery(id+"F11.wireOp",EDGE,"E1644"),sQuery(id+"F11.wireOp",EDGE,"E1645"),sQuery(id+"F11.wireOp",EDGE,"E1646"),sQuery(id+"F11.wireOp",EDGE,"E1647"),sQuery(id+"F11.wireOp",EDGE,"E1648"),sQuery(id+"F11.wireOp",EDGE,"E1649"),sQuery(id+"F11.wireOp",EDGE,"E1650"),sQuery(id+"F11.wireOp",EDGE,"E1651"),sQuery(id+"F11.wireOp",EDGE,"E1652"),sQuery(id+"F11.wireOp",EDGE,"E1653"),sQuery(id+"F11.wireOp",EDGE,"E1654"),sQuery(id+"F11.wireOp",EDGE,"E1655"),sQuery(id+"F11.wireOp",EDGE,"E1656"),sQuery(id+"F11.wireOp",EDGE,"E1657"),sQuery(id+"F11.wireOp",EDGE,"E1658"),sQuery(id+"F11.wireOp",EDGE,"E1659"),sQuery(id+"F11.wireOp",EDGE,"E1660"),sQuery(id+"F11.wireOp",EDGE,"E1661"),sQuery(id+"F11.wireOp",EDGE,"E1662"),sQuery(id+"F11.wireOp",EDGE,"E1663"),sQuery(id+"F11.wireOp",EDGE,"E1664"),sQuery(id+"F11.wireOp",EDGE,"E1665"),sQuery(id+"F11.wireOp",EDGE,"E1666"),sQuery(id+"F11.wireOp",EDGE,"E1667"),sQuery(id+"F11.wireOp",EDGE,"E1668"),sQuery(id+"F11.wireOp",EDGE,"E1669"),sQuery(id+"F11.wireOp",EDGE,"E1670"),sQuery(id+"F11.wireOp",EDGE,"E1671"),sQuery(id+"F11.wireOp",EDGE,"E1672"),sQuery(id+"F11.wireOp",EDGE,"E1673"),sQuery(id+"F11.wireOp",EDGE,"E1674"),sQuery(id+"F11.wireOp",EDGE,"E1675"),sQuery(id+"F11.wireOp",EDGE,"E1676"),sQuery(id+"F11.wireOp",EDGE,"E1677"),sQuery(id+"F11.wireOp",EDGE,"E1678"),sQuery(id+"F11.wireOp",EDGE,"E1679"),sQuery(id+"F11.wireOp",EDGE,"E1680"),sQuery(id+"F11.wireOp",EDGE,"E1681"),sQuery(id+"F11.wireOp",EDGE,"E1682"),sQuery(id+"F11.wireOp",EDGE,"E1683"),sQuery(id+"F11.wireOp",EDGE,"E1684"),sQuery(id+"F11.wireOp",EDGE,"E1685"),sQuery(id+"F11.wireOp",EDGE,"E1686"),sQuery(id+"F11.wireOp",EDGE,"E1687"),sQuery(id+"F11.wireOp",EDGE,"E1688"),sQuery(id+"F11.wireOp",EDGE,"E1689"),sQuery(id+"F11.wireOp",EDGE,"E1690"),sQuery(id+"F11.wireOp",EDGE,"E1691"),sQuery(id+"F11.wireOp",EDGE,"E1692"),sQuery(id+"F11.wireOp",EDGE,"E1693"),sQuery(id+"F11.wireOp",EDGE,"E1694"),sQuery(id+"F11.wireOp",EDGE,"E1695"),sQuery(id+"F11.wireOp",EDGE,"E1696"),sQuery(id+"F11.wireOp",EDGE,"E1697"),sQuery(id+"F11.wireOp",EDGE,"E1698"),sQuery(id+"F11.wireOp",EDGE,"E1699"),sQuery(id+"F11.wireOp",EDGE,"E1700"),sQuery(id+"F11.wireOp",EDGE,"E1701"),sQuery(id+"F11.wireOp",EDGE,"E1702"),sQuery(id+"F11.wireOp",EDGE,"E1703"),sQuery(id+"F11.wireOp",EDGE,"E1704"),sQuery(id+"F11.wireOp",EDGE,"E1705"),sQuery(id+"F11.wireOp",EDGE,"E1706"),sQuery(id+"F11.wireOp",EDGE,"E1707"),sQuery(id+"F11.wireOp",EDGE,"E1708"),sQuery(id+"F11.wireOp",EDGE,"E1709"),sQuery(id+"F11.wireOp",EDGE,"E1710"),sQuery(id+"F11.wireOp",EDGE,"E1711"),sQuery(id+"F11.wireOp",EDGE,"E1712"),sQuery(id+"F11.wireOp",EDGE,"E1713"),sQuery(id+"F11.wireOp",EDGE,"E1714"),sQuery(id+"F11.wireOp",EDGE,"E1715"),sQuery(id+"F11.wireOp",EDGE,"E1716"),sQuery(id+"F11.wireOp",EDGE,"E1717"),sQuery(id+"F11.wireOp",EDGE,"E1718"),sQuery(id+"F11.wireOp",EDGE,"E1719"),sQuery(id+"F11.wireOp",EDGE,"E1720"),sQuery(id+"F11.wireOp",EDGE,"E1721"),sQuery(id+"F11.wireOp",EDGE,"E1722"),sQuery(id+"F11.wireOp",EDGE,"E1723"),sQuery(id+"F11.wireOp",EDGE,"E1724"),sQuery(id+"F11.wireOp",EDGE,"E1725"),sQuery(id+"F11.wireOp",EDGE,"E1726"),sQuery(id+"F11.wireOp",EDGE,"E1727"),sQuery(id+"F11.wireOp",EDGE,"E1728"),sQuery(id+"F11.wireOp",EDGE,"E1729"),sQuery(id+"F11.wireOp",EDGE,"E1730"),sQuery(id+"F11.wireOp",EDGE,"E1731"),sQuery(id+"F11.wireOp",EDGE,"E1732"),sQuery(id+"F11.wireOp",EDGE,"E1733"),sQuery(id+"F11.wireOp",EDGE,"E1734"),sQuery(id+"F11.wireOp",EDGE,"E1735"),sQuery(id+"F11.wireOp",EDGE,"E1736"),sQuery(id+"F11.wireOp",EDGE,"E1737"),sQuery(id+"F11.wireOp",EDGE,"E1738"),sQuery(id+"F11.wireOp",EDGE,"E1739"),sQuery(id+"F11.wireOp",EDGE,"E1740"),sQuery(id+"F11.wireOp",EDGE,"E1741"),sQuery(id+"F11.wireOp",EDGE,"E1742"),sQuery(id+"F11.wireOp",EDGE,"E1743"),sQuery(id+"F11.wireOp",EDGE,"E1744"),sQuery(id+"F11.wireOp",EDGE,"E1745"),sQuery(id+"F11.wireOp",EDGE,"E1746"),sQuery(id+"F11.wireOp",EDGE,"E1747"),sQuery(id+"F11.wireOp",EDGE,"E1748"),sQuery(id+"F11.wireOp",EDGE,"E1749"),sQuery(id+"F11.wireOp",EDGE,"E1750"),sQuery(id+"F11.wireOp",EDGE,"E1751"),sQuery(id+"F11.wireOp",EDGE,"E1752"),sQuery(id+"F11.wireOp",EDGE,"E1753"),sQuery(id+"F11.wireOp",EDGE,"E1754"),sQuery(id+"F11.wireOp",EDGE,"E1755"),sQuery(id+"F11.wireOp",EDGE,"E1756"),sQuery(id+"F11.wireOp",EDGE,"E1757"),sQuery(id+"F11.wireOp",EDGE,"E1758"),sQuery(id+"F11.wireOp",EDGE,"E1759"),sQuery(id+"F11.wireOp",EDGE,"E1760"),sQuery(id+"F11.wireOp",EDGE,"E1761"),sQuery(id+"F11.wireOp",EDGE,"E1762"),sQuery(id+"F11.wireOp",EDGE,"E1763"),sQuery(id+"F11.wireOp",EDGE,"E1764"),sQuery(id+"F11.wireOp",EDGE,"E1765"),sQuery(id+"F11.wireOp",EDGE,"E1766"),sQuery(id+"F11.wireOp",EDGE,"E1767"),sQuery(id+"F11.wireOp",EDGE,"E1768"),sQuery(id+"F11.wireOp",EDGE,"E1769"),sQuery(id+"F11.wireOp",EDGE,"E1770"),sQuery(id+"F11.wireOp",EDGE,"E1771"),sQuery(id+"F11.wireOp",EDGE,"E1772"),sQuery(id+"F11.wireOp",EDGE,"E1773"),sQuery(id+"F11.wireOp",EDGE,"E1774"),sQuery(id+"F11.wireOp",EDGE,"E1775"),sQuery(id+"F11.wireOp",EDGE,"E1776"),sQuery(id+"F11.wireOp",EDGE,"E1777"),sQuery(id+"F11.wireOp",EDGE,"E1778"),sQuery(id+"F11.wireOp",EDGE,"E1779"),sQuery(id+"F11.wireOp",EDGE,"E1780"),sQuery(id+"F11.wireOp",EDGE,"E1781"),sQuery(id+"F11.wireOp",EDGE,"E1782"),sQuery(id+"F11.wireOp",EDGE,"E1783"),sQuery(id+"F11.wireOp",EDGE,"E1784"),sQuery(id+"F11.wireOp",EDGE,"E1785"),sQuery(id+"F11.wireOp",EDGE,"E1786"),sQuery(id+"F11.wireOp",EDGE,"E1787"),sQuery(id+"F11.wireOp",EDGE,"E1788"),sQuery(id+"F11.wireOp",EDGE,"E1789"),sQuery(id+"F11.wireOp",EDGE,"E1790"),sQuery(id+"F11.wireOp",EDGE,"E1791"),sQuery(id+"F11.wireOp",EDGE,"E1792"),sQuery(id+"F11.wireOp",EDGE,"E1793"),sQuery(id+"F11.wireOp",EDGE,"E1794"),sQuery(id+"F11.wireOp",EDGE,"E1795"),sQuery(id+"F11.wireOp",EDGE,"E1796"),sQuery(id+"F11.wireOp",EDGE,"E1797"),sQuery(id+"F11.wireOp",EDGE,"E1798"),sQuery(id+"F11.wireOp",EDGE,"E1799"),sQuery(id+"F11.wireOp",EDGE,"E1800"),sQuery(id+"F11.wireOp",EDGE,"E1801"),sQuery(id+"F11.wireOp",EDGE,"E1802"),sQuery(id+"F11.wireOp",EDGE,"E1803"),sQuery(id+"F11.wireOp",EDGE,"E1804"),sQuery(id+"F11.wireOp",EDGE,"E1805"),sQuery(id+"F11.wireOp",EDGE,"E1806"),sQuery(id+"F11.wireOp",EDGE,"E1807"),sQuery(id+"F11.wireOp",EDGE,"E1808"),sQuery(id+"F11.wireOp",EDGE,"E1809"),sQuery(id+"F11.wireOp",EDGE,"E1810"),sQuery(id+"F11.wireOp",EDGE,"E1811"),sQuery(id+"F11.wireOp",EDGE,"E1812"),sQuery(id+"F11.wireOp",EDGE,"E1813"),sQuery(id+"F11.wireOp",EDGE,"E1814"),sQuery(id+"F11.wireOp",EDGE,"E1815"),sQuery(id+"F11.wireOp",EDGE,"E1816"),sQuery(id+"F11.wireOp",EDGE,"E1817"),sQuery(id+"F11.wireOp",EDGE,"E1818"),sQuery(id+"F11.wireOp",EDGE,"E1819"),sQuery(id+"F11.wireOp",EDGE,"E1820"),sQuery(id+"F11.wireOp",EDGE,"E1821"),sQuery(id+"F11.wireOp",EDGE,"E1822"),sQuery(id+"F11.wireOp",EDGE,"E1823"),sQuery(id+"F11.wireOp",EDGE,"E1824"),sQuery(id+"F11.wireOp",EDGE,"E1825"),sQuery(id+"F11.wireOp",EDGE,"E1826"),sQuery(id+"F11.wireOp",EDGE,"E1827"),sQuery(id+"F11.wireOp",EDGE,"E1828"),sQuery(id+"F11.wireOp",EDGE,"E1829"),sQuery(id+"F11.wireOp",EDGE,"E1830"),sQuery(id+"F11.wireOp",EDGE,"E1831"),sQuery(id+"F11.wireOp",EDGE,"E1832"),sQuery(id+"F11.wireOp",EDGE,"E1833"),sQuery(id+"F11.wireOp",EDGE,"E1834"),sQuery(id+"F11.wireOp",EDGE,"E1835"),sQuery(id+"F11.wireOp",EDGE,"E1836"),sQuery(id+"F11.wireOp",EDGE,"E1837"),sQuery(id+"F11.wireOp",EDGE,"E1838"),sQuery(id+"F11.wireOp",EDGE,"E1839"),sQuery(id+"F11.wireOp",EDGE,"E1840"),sQuery(id+"F11.wireOp",EDGE,"E1841"),sQuery(id+"F11.wireOp",EDGE,"E1842"),sQuery(id+"F11.wireOp",EDGE,"E1843"),sQuery(id+"F11.wireOp",EDGE,"E1844"),sQuery(id+"F11.wireOp",EDGE,"E1845"),sQuery(id+"F11.wireOp",EDGE,"E1846"),sQuery(id+"F11.wireOp",EDGE,"E1847"),sQuery(id+"F11.wireOp",EDGE,"E1848"),sQuery(id+"F11.wireOp",EDGE,"E1849"),sQuery(id+"F11.wireOp",EDGE,"E1850"),sQuery(id+"F11.wireOp",EDGE,"E1851"),sQuery(id+"F11.wireOp",EDGE,"E1852"),sQuery(id+"F11.wireOp",EDGE,"E1853"),sQuery(id+"F11.wireOp",EDGE,"E1854"),sQuery(id+"F11.wireOp",EDGE,"E1855"),sQuery(id+"F11.wireOp",EDGE,"E1856"),sQuery(id+"F11.wireOp",EDGE,"E1857"),sQuery(id+"F11.wireOp",EDGE,"E1858"),sQuery(id+"F11.wireOp",EDGE,"E1859"),sQuery(id+"F11.wireOp",EDGE,"E1860"),sQuery(id+"F11.wireOp",EDGE,"E1861"),sQuery(id+"F11.wireOp",EDGE,"E1862"),sQuery(id+"F11.wireOp",EDGE,"E1863"),sQuery(id+"F11.wireOp",EDGE,"E1864"),sQuery(id+"F11.wireOp",EDGE,"E1865"),sQuery(id+"F11.wireOp",EDGE,"E1866"),sQuery(id+"F11.wireOp",EDGE,"E1867"),sQuery(id+"F11.wireOp",EDGE,"E1868"),sQuery(id+"F11.wireOp",EDGE,"E1869"),sQuery(id+"F11.wireOp",EDGE,"E1870"),sQuery(id+"F11.wireOp",EDGE,"E1871"),sQuery(id+"F11.wireOp",EDGE,"E1872"),sQuery(id+"F11.wireOp",EDGE,"E1873"),sQuery(id+"F11.wireOp",EDGE,"E1874"),sQuery(id+"F11.wireOp",EDGE,"E1875"),sQuery(id+"F11.wireOp",EDGE,"E1876"),sQuery(id+"F11.wireOp",EDGE,"E1877"),sQuery(id+"F11.wireOp",EDGE,"E1878"),sQuery(id+"F11.wireOp",EDGE,"E1879"),sQuery(id+"F11.wireOp",EDGE,"E1880"),sQuery(id+"F11.wireOp",EDGE,"E1881"),sQuery(id+"F11.wireOp",EDGE,"E1882"),sQuery(id+"F11.wireOp",EDGE,"E1883"),sQuery(id+"F11.wireOp",EDGE,"E1884"),sQuery(id+"F11.wireOp",EDGE,"E1885"),sQuery(id+"F11.wireOp",EDGE,"E1886"),sQuery(id+"F11.wireOp",EDGE,"E1887"),sQuery(id+"F11.wireOp",EDGE,"E1888"),sQuery(id+"F11.wireOp",EDGE,"E1889"),sQuery(id+"F11.wireOp",EDGE,"E1890"),sQuery(id+"F11.wireOp",EDGE,"E1891"),sQuery(id+"F11.wireOp",EDGE,"E1892"),sQuery(id+"F11.wireOp",EDGE,"E1893"),sQuery(id+"F11.wireOp",EDGE,"E1894"),sQuery(id+"F11.wireOp",EDGE,"E1895"),sQuery(id+"F11.wireOp",EDGE,"E1896"),sQuery(id+"F11.wireOp",EDGE,"E1897"),sQuery(id+"F11.wireOp",EDGE,"E1898"),sQuery(id+"F11.wireOp",EDGE,"E1899"),sQuery(id+"F11.wireOp",EDGE,"E1900"),sQuery(id+"F11.wireOp",EDGE,"E1901"),sQuery(id+"F11.wireOp",EDGE,"E1902"),sQuery(id+"F11.wireOp",EDGE,"E1903"),sQuery(id+"F11.wireOp",EDGE,"E1904"),sQuery(id+"F11.wireOp",EDGE,"E1905"),sQuery(id+"F11.wireOp",EDGE,"E1906"),sQuery(id+"F11.wireOp",EDGE,"E1907"),sQuery(id+"F11.wireOp",EDGE,"E1908"),sQuery(id+"F11.wireOp",EDGE,"E1909"),sQuery(id+"F11.wireOp",EDGE,"E1910"),sQuery(id+"F11.wireOp",EDGE,"E1911"),sQuery(id+"F11.wireOp",EDGE,"E1912"),sQuery(id+"F11.wireOp",EDGE,"E1913"),sQuery(id+"F11.wireOp",EDGE,"E1914"),sQuery(id+"F11.wireOp",EDGE,"E1915"),sQuery(id+"F11.wireOp",EDGE,"E1916"),sQuery(id+"F11.wireOp",EDGE,"E1917"),sQuery(id+"F11.wireOp",EDGE,"E1918"),sQuery(id+"F11.wireOp",EDGE,"E1919"),sQuery(id+"F11.wireOp",EDGE,"E1920"),sQuery(id+"F11.wireOp",EDGE,"E1921"),sQuery(id+"F11.wireOp",EDGE,"E1922"),sQuery(id+"F11.wireOp",EDGE,"E1923"),sQuery(id+"F11.wireOp",EDGE,"E1924"),sQuery(id+"F11.wireOp",EDGE,"E1925"),sQuery(id+"F11.wireOp",EDGE,"E1926"),sQuery(id+"F11.wireOp",EDGE,"E1927"),sQuery(id+"F11.wireOp",EDGE,"E1928"),sQuery(id+"F11.wireOp",EDGE,"E1929"),sQuery(id+"F11.wireOp",EDGE,"E1930"),sQuery(id+"F11.wireOp",EDGE,"E1931"),sQuery(id+"F11.wireOp",EDGE,"E1932"),sQuery(id+"F11.wireOp",EDGE,"E1933"),sQuery(id+"F11.wireOp",EDGE,"E1934"),sQuery(id+"F11.wireOp",EDGE,"E1935"),sQuery(id+"F11.wireOp",EDGE,"E1936"),sQuery(id+"F11.wireOp",EDGE,"E1937"),sQuery(id+"F11.wireOp",EDGE,"E1938"),sQuery(id+"F11.wireOp",EDGE,"E1939"),sQuery(id+"F11.wireOp",EDGE,"E1940"),sQuery(id+"F11.wireOp",EDGE,"E1941"),sQuery(id+"F11.wireOp",EDGE,"E1942"),sQuery(id+"F11.wireOp",EDGE,"E1943"),sQuery(id+"F11.wireOp",EDGE,"E1944"),sQuery(id+"F11.wireOp",EDGE,"E1945"),sQuery(id+"F11.wireOp",EDGE,"E1946"),sQuery(id+"F11.wireOp",EDGE,"E1947"),sQuery(id+"F11.wireOp",EDGE,"E1948"),sQuery(id+"F11.wireOp",EDGE,"E1949"),sQuery(id+"F11.wireOp",EDGE,"E1950"),sQuery(id+"F11.wireOp",EDGE,"E1951"),sQuery(id+"F11.wireOp",EDGE,"E1952"),sQuery(id+"F11.wireOp",EDGE,"E1953"),sQuery(id+"F11.wireOp",EDGE,"E1954"),sQuery(id+"F11.wireOp",EDGE,"E1955"),sQuery(id+"F11.wireOp",EDGE,"E1956"),sQuery(id+"F11.wireOp",EDGE,"E1957"),sQuery(id+"F11.wireOp",EDGE,"E1958"),sQuery(id+"F11.wireOp",EDGE,"E1959"),sQuery(id+"F11.wireOp",EDGE,"E1960"),sQuery(id+"F11.wireOp",EDGE,"E1961"),sQuery(id+"F11.wireOp",EDGE,"E1962"),sQuery(id+"F11.wireOp",EDGE,"E1963"),sQuery(id+"F11.wireOp",EDGE,"E1964"),sQuery(id+"F11.wireOp",EDGE,"E1965"),sQuery(id+"F11.wireOp",EDGE,"E1966"),sQuery(id+"F11.wireOp",EDGE,"E1967"),sQuery(id+"F11.wireOp",EDGE,"E1968"),sQuery(id+"F11.wireOp",EDGE,"E1969"),sQuery(id+"F11.wireOp",EDGE,"E1970"),sQuery(id+"F11.wireOp",EDGE,"E1971"),sQuery(id+"F11.wireOp",EDGE,"E1972"),sQuery(id+"F11.wireOp",EDGE,"E1973"),sQuery(id+"F11.wireOp",EDGE,"E1974"),sQuery(id+"F11.wireOp",EDGE,"E1975"),sQuery(id+"F11.wireOp",EDGE,"E1976"),sQuery(id+"F11.wireOp",EDGE,"E1977"),sQuery(id+"F11.wireOp",EDGE,"E1978"),sQuery(id+"F11.wireOp",EDGE,"E1979"),sQuery(id+"F11.wireOp",EDGE,"E1980"),sQuery(id+"F11.wireOp",EDGE,"E1981"),sQuery(id+"F11.wireOp",EDGE,"E1982"),sQuery(id+"F11.wireOp",EDGE,"E1983"),sQuery(id+"F11.wireOp",EDGE,"E1984"),sQuery(id+"F11.wireOp",EDGE,"E1985"),sQuery(id+"F11.wireOp",EDGE,"E1986"),sQuery(id+"F11.wireOp",EDGE,"E1987"),sQuery(id+"F11.wireOp",EDGE,"E1988"),sQuery(id+"F11.wireOp",EDGE,"E1989"),sQuery(id+"F11.wireOp",EDGE,"E1990"),sQuery(id+"F11.wireOp",EDGE,"E1991"),sQuery(id+"F11.wireOp",EDGE,"E1992"),sQuery(id+"F11.wireOp",EDGE,"E1993"),sQuery(id+"F11.wireOp",EDGE,"E1994"),sQuery(id+"F11.wireOp",EDGE,"E1995"),sQuery(id+"F11.wireOp",EDGE,"E1996"),sQuery(id+"F11.wireOp",EDGE,"E1997"),sQuery(id+"F11.wireOp",EDGE,"E1998"),sQuery(id+"F11.wireOp",EDGE,"E1999"),sQuery(id+"F11.wireOp",EDGE,"E2000"),sQuery(id+"F11.wireOp",EDGE,"E2001"),sQuery(id+"F11.wireOp",EDGE,"E2002"),sQuery(id+"F11.wireOp",EDGE,"E2003"),sQuery(id+"F11.wireOp",EDGE,"E2004"),sQuery(id+"F11.wireOp",EDGE,"E2005"),sQuery(id+"F11.wireOp",EDGE,"E2006"),sQuery(id+"F11.wireOp",EDGE,"E2007"),sQuery(id+"F11.wireOp",EDGE,"E2008"),sQuery(id+"F11.wireOp",EDGE,"E2009"),sQuery(id+"F11.wireOp",EDGE,"E2010"),sQuery(id+"F11.wireOp",EDGE,"E2011"),sQuery(id+"F11.wireOp",EDGE,"E2012"),sQuery(id+"F11.wireOp",EDGE,"E2013"),sQuery(id+"F11.wireOp",EDGE,"E2014"),sQuery(id+"F11.wireOp",EDGE,"E2015"),sQuery(id+"F11.wireOp",EDGE,"E2016"),sQuery(id+"F11.wireOp",EDGE,"E2017"),sQuery(id+"F11.wireOp",EDGE,"E2018"),sQuery(id+"F11.wireOp",EDGE,"E2019"),sQuery(id+"F11.wireOp",EDGE,"E2020"),sQuery(id+"F11.wireOp",EDGE,"E2021"),sQuery(id+"F11.wireOp",EDGE,"E2022"),sQuery(id+"F11.wireOp",EDGE,"E2023"),sQuery(id+"F11.wireOp",EDGE,"E2024"),sQuery(id+"F11.wireOp",EDGE,"E2025"),sQuery(id+"F11.wireOp",EDGE,"E2026"),sQuery(id+"F11.wireOp",EDGE,"E2027"),sQuery(id+"F11.wireOp",EDGE,"E2028"),sQuery(id+"F11.wireOp",EDGE,"E2029"),sQuery(id+"F11.wireOp",EDGE,"E2030"),sQuery(id+"F11.wireOp",EDGE,"E2031"),sQuery(id+"F11.wireOp",EDGE,"E2032"),sQuery(id+"F11.wireOp",EDGE,"E2033"),sQuery(id+"F11.wireOp",EDGE,"E2034"),sQuery(id+"F11.wireOp",EDGE,"E2035"),sQuery(id+"F11.wireOp",EDGE,"E2036"),sQuery(id+"F11.wireOp",EDGE,"E2037"),sQuery(id+"F11.wireOp",EDGE,"E2038"),sQuery(id+"F11.wireOp",EDGE,"E2039"),sQuery(id+"F11.wireOp",EDGE,"E2040"),sQuery(id+"F11.wireOp",EDGE,"E2041"),sQuery(id+"F11.wireOp",EDGE,"E2042"),sQuery(id+"F11.wireOp",EDGE,"E2043"),sQuery(id+"F11.wireOp",EDGE,"E2044"),sQuery(id+"F11.wireOp",EDGE,"E2045"),sQuery(id+"F11.wireOp",EDGE,"E2046"),sQuery(id+"F11.wireOp",EDGE,"E2047"),sQuery(id+"F11.wireOp",EDGE,"E2048"),sQuery(id+"F11.wireOp",EDGE,"E2049"),sQuery(id+"F11.wireOp",EDGE,"E2050"),sQuery(id+"F11.wireOp",EDGE,"E2051"),sQuery(id+"F11.wireOp",EDGE,"E2052"),sQuery(id+"F11.wireOp",EDGE,"E2053"),sQuery(id+"F11.wireOp",EDGE,"E2054"),sQuery(id+"F11.wireOp",EDGE,"E2055"),sQuery(id+"F11.wireOp",EDGE,"E2056"),sQuery(id+"F11.wireOp",EDGE,"E2057"),sQuery(id+"F11.wireOp",EDGE,"E2058"),sQuery(id+"F11.wireOp",EDGE,"E2059"),sQuery(id+"F11.wireOp",EDGE,"E2060"),sQuery(id+"F11.wireOp",EDGE,"E2061"),sQuery(id+"F11.wireOp",EDGE,"E2062"),sQuery(id+"F11.wireOp",EDGE,"E2063"),sQuery(id+"F11.wireOp",EDGE,"E2064"),sQuery(id+"F11.wireOp",EDGE,"E2065"),sQuery(id+"F11.wireOp",EDGE,"E2066"),sQuery(id+"F11.wireOp",EDGE,"E2067"),sQuery(id+"F11.wireOp",EDGE,"E2068"),sQuery(id+"F11.wireOp",EDGE,"E2069"),sQuery(id+"F11.wireOp",EDGE,"E2070"),sQuery(id+"F11.wireOp",EDGE,"E2071"),sQuery(id+"F11.wireOp",EDGE,"E2072"),sQuery(id+"F11.wireOp",EDGE,"E2073"),sQuery(id+"F11.wireOp",EDGE,"E2074"),sQuery(id+"F11.wireOp",EDGE,"E2075"),sQuery(id+"F11.wireOp",EDGE,"E2076"),sQuery(id+"F11.wireOp",EDGE,"E2077"),sQuery(id+"F11.wireOp",EDGE,"E2078"),sQuery(id+"F11.wireOp",EDGE,"E2079"),sQuery(id+"F11.wireOp",EDGE,"E2080"),sQuery(id+"F11.wireOp",EDGE,"E2081"),sQuery(id+"F11.wireOp",EDGE,"E2082"),sQuery(id+"F11.wireOp",EDGE,"E2083"),sQuery(id+"F11.wireOp",EDGE,"E2084"),sQuery(id+"F11.wireOp",EDGE,"E2085"),sQuery(id+"F11.wireOp",EDGE,"E2086"),sQuery(id+"F11.wireOp",EDGE,"E2087"),sQuery(id+"F11.wireOp",EDGE,"E2088"),sQuery(id+"F11.wireOp",EDGE,"E2089"),sQuery(id+"F11.wireOp",EDGE,"E2090"),sQuery(id+"F11.wireOp",EDGE,"E2091"),sQuery(id+"F11.wireOp",EDGE,"E2092"),sQuery(id+"F11.wireOp",EDGE,"E2093"),sQuery(id+"F11.wireOp",EDGE,"E2094"),sQuery(id+"F11.wireOp",EDGE,"E2095"),sQuery(id+"F11.wireOp",EDGE,"E2096"),sQuery(id+"F11.wireOp",EDGE,"E2097"),sQuery(id+"F11.wireOp",EDGE,"E2098"),sQuery(id+"F11.wireOp",EDGE,"E2099"),sQuery(id+"F11.wireOp",EDGE,"E2100"),sQuery(id+"F11.wireOp",EDGE,"E2101"),sQuery(id+"F11.wireOp",EDGE,"E2102"),sQuery(id+"F11.wireOp",EDGE,"E2103"),sQuery(id+"F11.wireOp",EDGE,"E2104"),sQuery(id+"F11.wireOp",EDGE,"E2105"),sQuery(id+"F11.wireOp",EDGE,"E2106"),sQuery(id+"F11.wireOp",EDGE,"E2107"),sQuery(id+"F11.wireOp",EDGE,"E2108"),sQuery(id+"F11.wireOp",EDGE,"E2109"),sQuery(id+"F11.wireOp",EDGE,"E2110"),sQuery(id+"F11.wireOp",EDGE,"E2111"),sQuery(id+"F11.wireOp",EDGE,"E2112"),sQuery(id+"F11.wireOp",EDGE,"E2113"),sQuery(id+"F11.wireOp",EDGE,"E2114"),sQuery(id+"F11.wireOp",EDGE,"E2115"),sQuery(id+"F11.wireOp",EDGE,"E2116"),sQuery(id+"F11.wireOp",EDGE,"E2117"),sQuery(id+"F11.wireOp",EDGE,"E2118"),sQuery(id+"F11.wireOp",EDGE,"E2119"),sQuery(id+"F11.wireOp",EDGE,"E2120"),sQuery(id+"F11.wireOp",EDGE,"E2121"),sQuery(id+"F11.wireOp",EDGE,"E2122"),sQuery(id+"F11.wireOp",EDGE,"E2123"),sQuery(id+"F11.wireOp",EDGE,"E2124"),sQuery(id+"F11.wireOp",EDGE,"E2125"),sQuery(id+"F11.wireOp",EDGE,"E2126"),sQuery(id+"F11.wireOp",EDGE,"E2127"),sQuery(id+"F11.wireOp",EDGE,"E2128"),sQuery(id+"F11.wireOp",EDGE,"E2129"),sQuery(id+"F11.wireOp",EDGE,"E2130"),sQuery(id+"F11.wireOp",EDGE,"E2131"),sQuery(id+"F11.wireOp",EDGE,"E2132"),sQuery(id+"F11.wireOp",EDGE,"E2133"),sQuery(id+"F11.wireOp",EDGE,"E2134"),sQuery(id+"F11.wireOp",EDGE,"E2135"),sQuery(id+"F11.wireOp",EDGE,"E2136"),sQuery(id+"F11.wireOp",EDGE,"E2137"),sQuery(id+"F11.wireOp",EDGE,"E2138"),sQuery(id+"F11.wireOp",EDGE,"E2139"),sQuery(id+"F11.wireOp",EDGE,"E2140"),sQuery(id+"F11.wireOp",EDGE,"E2141"),sQuery(id+"F11.wireOp",EDGE,"E2142"),sQuery(id+"F11.wireOp",EDGE,"E2143"),sQuery(id+"F11.wireOp",EDGE,"E2144"),sQuery(id+"F11.wireOp",EDGE,"E2145"),sQuery(id+"F11.wireOp",EDGE,"E2146"),sQuery(id+"F11.wireOp",EDGE,"E2147"),sQuery(id+"F11.wireOp",EDGE,"E2148"),sQuery(id+"F11.wireOp",EDGE,"E2149"),sQuery(id+"F11.wireOp",EDGE,"E2150"),sQuery(id+"F11.wireOp",EDGE,"E2151"),sQuery(id+"F11.wireOp",EDGE,"E2152"),sQuery(id+"F11.wireOp",EDGE,"E2153"),sQuery(id+"F11.wireOp",EDGE,"E2154"),sQuery(id+"F11.wireOp",EDGE,"E2155"),sQuery(id+"F11.wireOp",EDGE,"E2156"),sQuery(id+"F11.wireOp",EDGE,"E2157"),sQuery(id+"F11.wireOp",EDGE,"E2158"),sQuery(id+"F11.wireOp",EDGE,"E2159"),sQuery(id+"F11.wireOp",EDGE,"E2160"),sQuery(id+"F11.wireOp",EDGE,"E2161"),sQuery(id+"F11.wireOp",EDGE,"E2162"),sQuery(id+"F11.wireOp",EDGE,"E2163"),sQuery(id+"F11.wireOp",EDGE,"E2164"),sQuery(id+"F11.wireOp",EDGE,"E2165"),sQuery(id+"F11.wireOp",EDGE,"E2166"),sQuery(id+"F11.wireOp",EDGE,"E2167"),sQuery(id+"F11.wireOp",EDGE,"E2168"),sQuery(id+"F11.wireOp",EDGE,"E2169"),sQuery(id+"F11.wireOp",EDGE,"E2170"),sQuery(id+"F11.wireOp",EDGE,"E2171"),sQuery(id+"F11.wireOp",EDGE,"E2172"),sQuery(id+"F11.wireOp",EDGE,"E2173"),sQuery(id+"F11.wireOp",EDGE,"E2174"),sQuery(id+"F11.wireOp",EDGE,"E2175"),sQuery(id+"F11.wireOp",EDGE,"E2176"),sQuery(id+"F11.wireOp",EDGE,"E2177"),sQuery(id+"F11.wireOp",EDGE,"E2178"),sQuery(id+"F11.wireOp",EDGE,"E2179"),sQuery(id+"F11.wireOp",EDGE,"E2180"),sQuery(id+"F11.wireOp",EDGE,"E2181"),sQuery(id+"F11.wireOp",EDGE,"E2182"),sQuery(id+"F11.wireOp",EDGE,"E2183"),sQuery(id+"F11.wireOp",EDGE,"E2184"),sQuery(id+"F11.wireOp",EDGE,"E2185"),sQuery(id+"F11.wireOp",EDGE,"E2186"),sQuery(id+"F11.wireOp",EDGE,"E2187"),sQuery(id+"F11.wireOp",EDGE,"E2188"),sQuery(id+"F11.wireOp",EDGE,"E2189"),sQuery(id+"F11.wireOp",EDGE,"E2190"),sQuery(id+"F11.wireOp",EDGE,"E2191"),sQuery(id+"F11.wireOp",EDGE,"E2192"),sQuery(id+"F11.wireOp",EDGE,"E2193"),sQuery(id+"F11.wireOp",EDGE,"E2194"),sQuery(id+"F11.wireOp",EDGE,"E2195"),sQuery(id+"F11.wireOp",EDGE,"E2196"),sQuery(id+"F11.wireOp",EDGE,"E2197"),sQuery(id+"F11.wireOp",EDGE,"E2198"),sQuery(id+"F11.wireOp",EDGE,"E2199"),sQuery(id+"F11.wireOp",EDGE,"E2200"),sQuery(id+"F11.wireOp",EDGE,"E2201"),sQuery(id+"F11.wireOp",EDGE,"E2202"),sQuery(id+"F11.wireOp",EDGE,"E2203"),sQuery(id+"F11.wireOp",EDGE,"E2204"),sQuery(id+"F11.wireOp",EDGE,"E2205"),sQuery(id+"F11.wireOp",EDGE,"E2206"),sQuery(id+"F11.wireOp",EDGE,"E2207"),sQuery(id+"F11.wireOp",EDGE,"E2208"),sQuery(id+"F11.wireOp",EDGE,"E2209"),sQuery(id+"F11.wireOp",EDGE,"E2210"),sQuery(id+"F11.wireOp",EDGE,"E2211"),sQuery(id+"F11.wireOp",EDGE,"E2212"),sQuery(id+"F11.wireOp",EDGE,"E2213"),sQuery(id+"F11.wireOp",EDGE,"E2214"),sQuery(id+"F11.wireOp",EDGE,"E2215"),sQuery(id+"F11.wireOp",EDGE,"E2216"),sQuery(id+"F11.wireOp",EDGE,"E2217"),sQuery(id+"F11.wireOp",EDGE,"E2218"),sQuery(id+"F11.wireOp",EDGE,"E2219"),sQuery(id+"F11.wireOp",EDGE,"E2220"),sQuery(id+"F11.wireOp",EDGE,"E2221"),sQuery(id+"F11.wireOp",EDGE,"E2222"),sQuery(id+"F11.wireOp",EDGE,"E2223"),sQuery(id+"F11.wireOp",EDGE,"E2224"),sQuery(id+"F11.wireOp",EDGE,"E2225"),sQuery(id+"F11.wireOp",EDGE,"E2226"),sQuery(id+"F11.wireOp",EDGE,"E2227"),sQuery(id+"F11.wireOp",EDGE,"E2228"),sQuery(id+"F11.wireOp",EDGE,"E2229"),sQuery(id+"F11.wireOp",EDGE,"E2230"),sQuery(id+"F11.wireOp",EDGE,"E2231"),sQuery(id+"F11.wireOp",EDGE,"E2232"),sQuery(id+"F11.wireOp",EDGE,"E2233"),sQuery(id+"F11.wireOp",EDGE,"E2234"),sQuery(id+"F11.wireOp",EDGE,"E2235"),sQuery(id+"F11.wireOp",EDGE,"E2236"),sQuery(id+"F11.wireOp",EDGE,"E2237"),sQuery(id+"F11.wireOp",EDGE,"E2238"),sQuery(id+"F11.wireOp",EDGE,"E2239"),sQuery(id+"F11.wireOp",EDGE,"E2240"),sQuery(id+"F11.wireOp",EDGE,"E2241"),sQuery(id+"F11.wireOp",EDGE,"E2242"),sQuery(id+"F11.wireOp",EDGE,"E2243"),sQuery(id+"F11.wireOp",EDGE,"E2244"),sQuery(id+"F11.wireOp",EDGE,"E2245"),sQuery(id+"F11.wireOp",EDGE,"E2246"),sQuery(id+"F11.wireOp",EDGE,"E2247"),sQuery(id+"F11.wireOp",EDGE,"E2248"),sQuery(id+"F11.wireOp",EDGE,"E2249"),sQuery(id+"F11.wireOp",EDGE,"E2250"),sQuery(id+"F11.wireOp",EDGE,"E2251"),sQuery(id+"F11.wireOp",EDGE,"E2252"),sQuery(id+"F11.wireOp",EDGE,"E2253"),sQuery(id+"F11.wireOp",EDGE,"E2254"),sQuery(id+"F11.wireOp",EDGE,"E2255"),sQuery(id+"F11.wireOp",EDGE,"E2256"),sQuery(id+"F11.wireOp",EDGE,"E2257"),sQuery(id+"F11.wireOp",EDGE,"E2258"),sQuery(id+"F11.wireOp",EDGE,"E2259"),sQuery(id+"F11.wireOp",EDGE,"E2260"),sQuery(id+"F11.wireOp",EDGE,"E2261"),sQuery(id+"F11.wireOp",EDGE,"E2262"),sQuery(id+"F11.wireOp",EDGE,"E2263"),sQuery(id+"F11.wireOp",EDGE,"E2264"),sQuery(id+"F11.wireOp",EDGE,"E2265"),sQuery(id+"F11.wireOp",EDGE,"E2266"),sQuery(id+"F11.wireOp",EDGE,"E2267"),sQuery(id+"F11.wireOp",EDGE,"E2268"),sQuery(id+"F11.wireOp",EDGE,"E2269"),sQuery(id+"F11.wireOp",EDGE,"E2270"),sQuery(id+"F11.wireOp",EDGE,"E2271"),sQuery(id+"F11.wireOp",EDGE,"E2272"),sQuery(id+"F11.wireOp",EDGE,"E2273"),sQuery(id+"F11.wireOp",EDGE,"E2274"),sQuery(id+"F11.wireOp",EDGE,"E2275"),sQuery(id+"F11.wireOp",EDGE,"E2276"),sQuery(id+"F11.wireOp",EDGE,"E2277"),sQuery(id+"F11.wireOp",EDGE,"E2278"),sQuery(id+"F11.wireOp",EDGE,"E2279"),sQuery(id+"F11.wireOp",EDGE,"E2280"),sQuery(id+"F11.wireOp",EDGE,"E2281"),sQuery(id+"F11.wireOp",EDGE,"E2282"),sQuery(id+"F11.wireOp",EDGE,"E2283"),sQuery(id+"F11.wireOp",EDGE,"E2284"),sQuery(id+"F11.wireOp",EDGE,"E2285"),sQuery(id+"F11.wireOp",EDGE,"E2286"),sQuery(id+"F11.wireOp",EDGE,"E2287"),sQuery(id+"F11.wireOp",EDGE,"E2288"),sQuery(id+"F11.wireOp",EDGE,"E2289"),sQuery(id+"F11.wireOp",EDGE,"E2290"),sQuery(id+"F11.wireOp",EDGE,"E2291"),sQuery(id+"F11.wireOp",EDGE,"E2292"),sQuery(id+"F11.wireOp",EDGE,"E2293"),sQuery(id+"F11.wireOp",EDGE,"E2294"),sQuery(id+"F11.wireOp",EDGE,"E2295"),sQuery(id+"F11.wireOp",EDGE,"E2296"),sQuery(id+"F11.wireOp",EDGE,"E2297"),sQuery(id+"F11.wireOp",EDGE,"E2298"),sQuery(id+"F11.wireOp",EDGE,"E2299"),sQuery(id+"F11.wireOp",EDGE,"E2300"),sQuery(id+"F11.wireOp",EDGE,"E2301"),sQuery(id+"F11.wireOp",EDGE,"E2302"),sQuery(id+"F11.wireOp",EDGE,"E2303"),sQuery(id+"F11.wireOp",EDGE,"E2304"),sQuery(id+"F11.wireOp",EDGE,"E2305"),sQuery(id+"F11.wireOp",EDGE,"E2306"),sQuery(id+"F11.wireOp",EDGE,"E2307"),sQuery(id+"F11.wireOp",EDGE,"E2308"),sQuery(id+"F11.wireOp",EDGE,"E2309"),sQuery(id+"F11.wireOp",EDGE,"E2310"),sQuery(id+"F11.wireOp",EDGE,"E2311"),sQuery(id+"F11.wireOp",EDGE,"E2312"),sQuery(id+"F11.wireOp",EDGE,"E2313"),sQuery(id+"F11.wireOp",EDGE,"E2314"),sQuery(id+"F11.wireOp",EDGE,"E2315"),sQuery(id+"F11.wireOp",EDGE,"E2316"),sQuery(id+"F11.wireOp",EDGE,"E2317"),sQuery(id+"F11.wireOp",EDGE,"E2318"),sQuery(id+"F11.wireOp",EDGE,"E2319"),sQuery(id+"F11.wireOp",EDGE,"E2320"),sQuery(id+"F11.wireOp",EDGE,"E2321"),sQuery(id+"F11.wireOp",EDGE,"E2322"),sQuery(id+"F11.wireOp",EDGE,"E2323"),sQuery(id+"F11.wireOp",EDGE,"E2324"),sQuery(id+"F11.wireOp",EDGE,"E2325"),sQuery(id+"F11.wireOp",EDGE,"E2326"),sQuery(id+"F11.wireOp",EDGE,"E2327"),sQuery(id+"F11.wireOp",EDGE,"E2328"),sQuery(id+"F11.wireOp",EDGE,"E2329"),sQuery(id+"F11.wireOp",EDGE,"E2330"),sQuery(id+"F11.wireOp",EDGE,"E2331"),sQuery(id+"F11.wireOp",EDGE,"E2332"),sQuery(id+"F11.wireOp",EDGE,"E2333"),sQuery(id+"F11.wireOp",EDGE,"E2334"),sQuery(id+"F11.wireOp",EDGE,"E2335"),sQuery(id+"F11.wireOp",EDGE,"E2336"),sQuery(id+"F11.wireOp",EDGE,"E2337"),sQuery(id+"F11.wireOp",EDGE,"E2338"),sQuery(id+"F11.wireOp",EDGE,"E2339"),sQuery(id+"F11.wireOp",EDGE,"E2340"),sQuery(id+"F11.wireOp",EDGE,"E2341"),sQuery(id+"F11.wireOp",EDGE,"E2342"),sQuery(id+"F11.wireOp",EDGE,"E2343"),sQuery(id+"F11.wireOp",EDGE,"E2344"),sQuery(id+"F11.wireOp",EDGE,"E2345"),sQuery(id+"F11.wireOp",EDGE,"E2346"),sQuery(id+"F11.wireOp",EDGE,"E2347"),sQuery(id+"F11.wireOp",EDGE,"E2348"),sQuery(id+"F11.wireOp",EDGE,"E2349"),sQuery(id+"F11.wireOp",EDGE,"E2350"),sQuery(id+"F11.wireOp",EDGE,"E2351"),sQuery(id+"F11.wireOp",EDGE,"E2352"),sQuery(id+"F11.wireOp",EDGE,"E2353"),sQuery(id+"F11.wireOp",EDGE,"E2354"),sQuery(id+"F11.wireOp",EDGE,"E2355"),sQuery(id+"F11.wireOp",EDGE,"E2356"),sQuery(id+"F11.wireOp",EDGE,"E2357"),sQuery(id+"F11.wireOp",EDGE,"E2358"),sQuery(id+"F11.wireOp",EDGE,"E2359"),sQuery(id+"F11.wireOp",EDGE,"E2360"),sQuery(id+"F11.wireOp",EDGE,"E2361"),sQuery(id+"F11.wireOp",EDGE,"E2362"),sQuery(id+"F11.wireOp",EDGE,"E2363"),sQuery(id+"F11.wireOp",EDGE,"E2364"),sQuery(id+"F11.wireOp",EDGE,"E2365"),sQuery(id+"F11.wireOp",EDGE,"E2366"),sQuery(id+"F11.wireOp",EDGE,"E2367"),sQuery(id+"F11.wireOp",EDGE,"E2368"),sQuery(id+"F11.wireOp",EDGE,"E2369"),sQuery(id+"F11.wireOp",EDGE,"E2370"),sQuery(id+"F11.wireOp",EDGE,"E2371"),sQuery(id+"F11.wireOp",EDGE,"E2372"),sQuery(id+"F11.wireOp",EDGE,"E2373"),sQuery(id+"F11.wireOp",EDGE,"E2374"),sQuery(id+"F11.wireOp",EDGE,"E2375"),sQuery(id+"F11.wireOp",EDGE,"E2376"),sQuery(id+"F11.wireOp",EDGE,"E2377"),sQuery(id+"F11.wireOp",EDGE,"E2378"),sQuery(id+"F11.wireOp",EDGE,"E2379"),sQuery(id+"F11.wireOp",EDGE,"E2380"),sQuery(id+"F11.wireOp",EDGE,"E2381"),sQuery(id+"F11.wireOp",EDGE,"E2382"),sQuery(id+"F11.wireOp",EDGE,"E2383"),sQuery(id+"F11.wireOp",EDGE,"E2384"),sQuery(id+"F11.wireOp",EDGE,"E2385"),sQuery(id+"F11.wireOp",EDGE,"E2386"),sQuery(id+"F11.wireOp",EDGE,"E2387"),sQuery(id+"F11.wireOp",EDGE,"E2388"),sQuery(id+"F11.wireOp",EDGE,"E2389"),sQuery(id+"F11.wireOp",EDGE,"E2390"),sQuery(id+"F11.wireOp",EDGE,"E2391"),sQuery(id+"F11.wireOp",EDGE,"E2392"),sQuery(id+"F11.wireOp",EDGE,"E2393"),sQuery(id+"F11.wireOp",EDGE,"E2394"),sQuery(id+"F11.wireOp",EDGE,"E2395"),sQuery(id+"F11.wireOp",EDGE,"E2396"),sQuery(id+"F11.wireOp",EDGE,"E2397"),sQuery(id+"F11.wireOp",EDGE,"E2398"),sQuery(id+"F11.wireOp",EDGE,"E2399"),sQuery(id+"F11.wireOp",EDGE,"E2400"),sQuery(id+"F11.wireOp",EDGE,"E2401"),sQuery(id+"F11.wireOp",EDGE,"E2402"),sQuery(id+"F11.wireOp",EDGE,"E2403"),sQuery(id+"F11.wireOp",EDGE,"E2404"),sQuery(id+"F11.wireOp",EDGE,"E2405"),sQuery(id+"F11.wireOp",EDGE,"E2406"),sQuery(id+"F11.wireOp",EDGE,"E2407"),sQuery(id+"F11.wireOp",EDGE,"E2408"),sQuery(id+"F11.wireOp",EDGE,"E2409"),sQuery(id+"F11.wireOp",EDGE,"E2410"),sQuery(id+"F11.wireOp",EDGE,"E2411"),sQuery(id+"F11.wireOp",EDGE,"E2412"),sQuery(id+"F11.wireOp",EDGE,"E2413"),sQuery(id+"F11.wireOp",EDGE,"E2414"),sQuery(id+"F11.wireOp",EDGE,"E2415"),sQuery(id+"F11.wireOp",EDGE,"E2416"),sQuery(id+"F11.wireOp",EDGE,"E2417"),sQuery(id+"F11.wireOp",EDGE,"E2418"),sQuery(id+"F11.wireOp",EDGE,"E2419"),sQuery(id+"F11.wireOp",EDGE,"E2420"),sQuery(id+"F11.wireOp",EDGE,"E2421"),sQuery(id+"F11.wireOp",EDGE,"E2422"),sQuery(id+"F11.wireOp",EDGE,"E2423"),sQuery(id+"F11.wireOp",EDGE,"E2424"),sQuery(id+"F11.wireOp",EDGE,"E2425"),sQuery(id+"F11.wireOp",EDGE,"E2426"),sQuery(id+"F11.wireOp",EDGE,"E2427"),sQuery(id+"F11.wireOp",EDGE,"E2428"),sQuery(id+"F11.wireOp",EDGE,"E2429"),sQuery(id+"F11.wireOp",EDGE,"E2430"),sQuery(id+"F11.wireOp",EDGE,"E2431"),sQuery(id+"F11.wireOp",EDGE,"E2432"),sQuery(id+"F11.wireOp",EDGE,"E2433"),sQuery(id+"F11.wireOp",EDGE,"E2434"),sQuery(id+"F11.wireOp",EDGE,"E2435"),sQuery(id+"F11.wireOp",EDGE,"E2436"),sQuery(id+"F11.wireOp",EDGE,"E2437"),sQuery(id+"F11.wireOp",EDGE,"E2438"),sQuery(id+"F11.wireOp",EDGE,"E2439"),sQuery(id+"F11.wireOp",EDGE,"E2440"),sQuery(id+"F11.wireOp",EDGE,"E2441"),sQuery(id+"F11.wireOp",EDGE,"E2442"),sQuery(id+"F11.wireOp",EDGE,"E2443"),sQuery(id+"F11.wireOp",EDGE,"E2444"),sQuery(id+"F11.wireOp",EDGE,"E2445"),sQuery(id+"F11.wireOp",EDGE,"E2446"),sQuery(id+"F11.wireOp",EDGE,"E2447"),sQuery(id+"F11.wireOp",EDGE,"E2448"),sQuery(id+"F11.wireOp",EDGE,"E2449"),sQuery(id+"F11.wireOp",EDGE,"E2450"),sQuery(id+"F11.wireOp",EDGE,"E2451"),sQuery(id+"F11.wireOp",EDGE,"E2452"),sQuery(id+"F11.wireOp",EDGE,"E2453"),sQuery(id+"F11.wireOp",EDGE,"E2454"),sQuery(id+"F11.wireOp",EDGE,"E2455"),sQuery(id+"F11.wireOp",EDGE,"E2456"),sQuery(id+"F11.wireOp",EDGE,"E2457"),sQuery(id+"F11.wireOp",EDGE,"E2458"),sQuery(id+"F11.wireOp",EDGE,"E2459"),sQuery(id+"F11.wireOp",EDGE,"E2460"),sQuery(id+"F11.wireOp",EDGE,"E2461"),sQuery(id+"F11.wireOp",EDGE,"E2462"),sQuery(id+"F11.wireOp",EDGE,"E2463"),sQuery(id+"F11.wireOp",EDGE,"E2464"),sQuery(id+"F11.wireOp",EDGE,"E2465"),sQuery(id+"F11.wireOp",EDGE,"E2466"),sQuery(id+"F11.wireOp",EDGE,"E2467"),sQuery(id+"F11.wireOp",EDGE,"E2468"),sQuery(id+"F11.wireOp",EDGE,"E2469"),sQuery(id+"F11.wireOp",EDGE,"E2470"),sQuery(id+"F11.wireOp",EDGE,"E2471"),sQuery(id+"F11.wireOp",EDGE,"E2472"),sQuery(id+"F11.wireOp",EDGE,"E2473"),sQuery(id+"F11.wireOp",EDGE,"E2474"),sQuery(id+"F11.wireOp",EDGE,"E2475"),sQuery(id+"F11.wireOp",EDGE,"E2476"),sQuery(id+"F11.wireOp",EDGE,"E2477"),sQuery(id+"F11.wireOp",EDGE,"E2478"),sQuery(id+"F11.wireOp",EDGE,"E2479"),sQuery(id+"F11.wireOp",EDGE,"E2480"),sQuery(id+"F11.wireOp",EDGE,"E2481"),sQuery(id+"F11.wireOp",EDGE,"E2482"),sQuery(id+"F11.wireOp",EDGE,"E2483"),sQuery(id+"F11.wireOp",EDGE,"E2484"),sQuery(id+"F11.wireOp",EDGE,"E2485"),sQuery(id+"F11.wireOp",EDGE,"E2486"),sQuery(id+"F11.wireOp",EDGE,"E2487"),sQuery(id+"F11.wireOp",EDGE,"E2488"),sQuery(id+"F11.wireOp",EDGE,"E2489"),sQuery(id+"F11.wireOp",EDGE,"E2490"),sQuery(id+"F11.wireOp",EDGE,"E2491"),sQuery(id+"F11.wireOp",EDGE,"E2492"),sQuery(id+"F11.wireOp",EDGE,"E2493"),sQuery(id+"F11.wireOp",EDGE,"E2494"),sQuery(id+"F11.wireOp",EDGE,"E2495"),sQuery(id+"F11.wireOp",EDGE,"E2496"),sQuery(id+"F11.wireOp",EDGE,"E2497"),sQuery(id+"F11.wireOp",EDGE,"E2498"),sQuery(id+"F11.wireOp",EDGE,"E2499"),sQuery(id+"F11.wireOp",EDGE,"E2500"),sQuery(id+"F11.wireOp",EDGE,"E2501"),sQuery(id+"F11.wireOp",EDGE,"E2502"),sQuery(id+"F11.wireOp",EDGE,"E2503"),sQuery(id+"F11.wireOp",EDGE,"E2504"),sQuery(id+"F11.wireOp",EDGE,"E2505"),sQuery(id+"F11.wireOp",EDGE,"E2506"),sQuery(id+"F11.wireOp",EDGE,"E2507"),sQuery(id+"F11.wireOp",EDGE,"E2508"),sQuery(id+"F11.wireOp",EDGE,"E2509"),sQuery(id+"F11.wireOp",EDGE,"E2510"),sQuery(id+"F11.wireOp",EDGE,"E2511"),sQuery(id+"F11.wireOp",EDGE,"E2512"),sQuery(id+"F11.wireOp",EDGE,"E2513"),sQuery(id+"F11.wireOp",EDGE,"E2514"),sQuery(id+"F11.wireOp",EDGE,"E2515"),sQuery(id+"F11.wireOp",EDGE,"E2516"),sQuery(id+"F11.wireOp",EDGE,"E2517"),sQuery(id+"F11.wireOp",EDGE,"E2518"),sQuery(id+"F11.wireOp",EDGE,"E2519"),sQuery(id+"F11.wireOp",EDGE,"E2520"),sQuery(id+"F11.wireOp",EDGE,"E2521"),sQuery(id+"F11.wireOp",EDGE,"E2522"),sQuery(id+"F11.wireOp",EDGE,"E2523"),sQuery(id+"F11.wireOp",EDGE,"E2524"),sQuery(id+"F11.wireOp",EDGE,"E2525"),sQuery(id+"F11.wireOp",EDGE,"E2526"),sQuery(id+"F11.wireOp",EDGE,"E2527"),sQuery(id+"F11.wireOp",EDGE,"E2528"),sQuery(id+"F11.wireOp",EDGE,"E2529"),sQuery(id+"F11.wireOp",EDGE,"E2530"),sQuery(id+"F11.wireOp",EDGE,"E2531"),sQuery(id+"F11.wireOp",EDGE,"E2532"),sQuery(id+"F11.wireOp",EDGE,"E2533"),sQuery(id+"F11.wireOp",EDGE,"E2534"),sQuery(id+"F11.wireOp",EDGE,"E2535"),sQuery(id+"F11.wireOp",EDGE,"E2536"),sQuery(id+"F11.wireOp",EDGE,"E2537"),sQuery(id+"F11.wireOp",EDGE,"E2538"),sQuery(id+"F11.wireOp",EDGE,"E2539"),sQuery(id+"F11.wireOp",EDGE,"E2540"),sQuery(id+"F11.wireOp",EDGE,"E2541"),sQuery(id+"F11.wireOp",EDGE,"E2542"),sQuery(id+"F11.wireOp",EDGE,"E2543"),sQuery(id+"F11.wireOp",EDGE,"E2544"),sQuery(id+"F11.wireOp",EDGE,"E2545"),sQuery(id+"F11.wireOp",EDGE,"E2546"),sQuery(id+"F11.wireOp",EDGE,"E2547"),sQuery(id+"F11.wireOp",EDGE,"E2548"),sQuery(id+"F11.wireOp",EDGE,"E2549"),sQuery(id+"F11.wireOp",EDGE,"E2550"),sQuery(id+"F11.wireOp",EDGE,"E2551"),sQuery(id+"F11.wireOp",EDGE,"E2552"),sQuery(id+"F11.wireOp",EDGE,"E2553"),sQuery(id+"F11.wireOp",EDGE,"E2554"),sQuery(id+"F11.wireOp",EDGE,"E2555"),sQuery(id+"F11.wireOp",EDGE,"E2556"),sQuery(id+"F11.wireOp",EDGE,"E2557"),sQuery(id+"F11.wireOp",EDGE,"E2558"),sQuery(id+"F11.wireOp",EDGE,"E2559"),sQuery(id+"F11.wireOp",EDGE,"E2560"),sQuery(id+"F11.wireOp",EDGE,"E2561"),sQuery(id+"F11.wireOp",EDGE,"E2562"),sQuery(id+"F11.wireOp",EDGE,"E2563"),sQuery(id+"F11.wireOp",EDGE,"E2564"),sQuery(id+"F11.wireOp",EDGE,"E2565"),sQuery(id+"F11.wireOp",EDGE,"E2566"),sQuery(id+"F11.wireOp",EDGE,"E2567"),sQuery(id+"F11.wireOp",EDGE,"E2568"),sQuery(id+"F11.wireOp",EDGE,"E2569"),sQuery(id+"F11.wireOp",EDGE,"E2570"),sQuery(id+"F11.wireOp",EDGE,"E2571"),sQuery(id+"F11.wireOp",EDGE,"E2572"),sQuery(id+"F11.wireOp",EDGE,"E2573"),sQuery(id+"F11.wireOp",EDGE,"E2574"),sQuery(id+"F11.wireOp",EDGE,"E2575"),sQuery(id+"F11.wireOp",EDGE,"E2576"),sQuery(id+"F11.wireOp",EDGE,"E2577"),sQuery(id+"F11.wireOp",EDGE,"E2578"),sQuery(id+"F11.wireOp",EDGE,"E2579"),sQuery(id+"F11.wireOp",EDGE,"E2580"),sQuery(id+"F11.wireOp",EDGE,"E2581"),sQuery(id+"F11.wireOp",EDGE,"E2582"),sQuery(id+"F11.wireOp",EDGE,"E2583"),sQuery(id+"F11.wireOp",EDGE,"E2584"),sQuery(id+"F11.wireOp",EDGE,"E2585"),sQuery(id+"F11.wireOp",EDGE,"E2586"),sQuery(id+"F11.wireOp",EDGE,"E2587"),sQuery(id+"F11.wireOp",EDGE,"E2588"),sQuery(id+"F11.wireOp",EDGE,"E2589"),sQuery(id+"F11.wireOp",EDGE,"E2590"),sQuery(id+"F11.wireOp",EDGE,"E2591"),sQuery(id+"F11.wireOp",EDGE,"E2592"),sQuery(id+"F11.wireOp",EDGE,"E2593"),sQuery(id+"F11.wireOp",EDGE,"E2594"),sQuery(id+"F11.wireOp",EDGE,"E2595"),sQuery(id+"F11.wireOp",EDGE,"E2596"),sQuery(id+"F11.wireOp",EDGE,"E2597"),sQuery(id+"F11.wireOp",EDGE,"E2598")])]});
            var Q1;
            Q1=sQuery(id+"F0.wireOp",VERTEX,"E0.center");
            var Q2;
            Q2=sQuery(id+"F0.wireOp",VERTEX,"E2.start");
            transform(context, id + "F16", {"entities" : qUnion([Q0]), "transformType" : TransformType.TRANSLATION_ENTITY, "oppositeDirectionEntity" : false, "transformLine" : qUnion([Q1, Q2]), "makeCopy" : false});
        }
        {
            var Q0;
            Q0=qCreatedBy(makeId("Front.planeOp"),FACE);
            var sketch = newSketch(context, id + "F17", { "sketchPlane" : qUnion([Q0])});
            skLineSegment(sketch, "E2600", {"start": v(48.75, 0) * mm, "end": v(48.69, 2.44) * mm});
            skLineSegment(sketch, "E2601", {"start": v(48.69, 2.44) * mm, "end": v(48.5, 4.87) * mm});
            skLineSegment(sketch, "E2602", {"start": v(48.5, 4.87) * mm, "end": v(48.2, 7.29) * mm});
            skLineSegment(sketch, "E2603", {"start": v(48.2, 7.29) * mm, "end": v(47.78, 9.69) * mm});
            skLineSegment(sketch, "E2604", {"start": v(47.78, 9.69) * mm, "end": v(47.23, 12.06) * mm});
            skLineSegment(sketch, "E2605", {"start": v(47.23, 12.06) * mm, "end": v(46.57, 14.41) * mm});
            skLineSegment(sketch, "E2606", {"start": v(46.57, 14.41) * mm, "end": v(45.8, 16.72) * mm});
            skLineSegment(sketch, "E2607", {"start": v(45.8, 16.72) * mm, "end": v(44.9, 18.99) * mm});
            skLineSegment(sketch, "E2608", {"start": v(44.9, 18.99) * mm, "end": v(43.9, 21.2) * mm});
            skLineSegment(sketch, "E2609", {"start": v(43.9, 21.2) * mm, "end": v(42.78, 23.38) * mm});
            skLineSegment(sketch, "E2610", {"start": v(42.78, 23.38) * mm, "end": v(41.56, 25.48) * mm});
            skLineSegment(sketch, "E2611", {"start": v(41.56, 25.48) * mm, "end": v(40.23, 27.53) * mm});
            skLineSegment(sketch, "E2612", {"start": v(40.23, 27.53) * mm, "end": v(38.8, 29.5) * mm});
            skLineSegment(sketch, "E2613", {"start": v(38.8, 29.5) * mm, "end": v(37.29, 31.4) * mm});
            skLineSegment(sketch, "E2614", {"start": v(37.29, 31.4) * mm, "end": v(35.67, 33.23) * mm});
            skLineSegment(sketch, "E2615", {"start": v(35.67, 33.23) * mm, "end": v(33.96, 34.97) * mm});
            skLineSegment(sketch, "E2616", {"start": v(33.96, 34.97) * mm, "end": v(32.17, 36.63) * mm});
            skLineSegment(sketch, "E2617", {"start": v(32.17, 36.63) * mm, "end": v(30.3, 38.2) * mm});
            skLineSegment(sketch, "E2618", {"start": v(30.3, 38.2) * mm, "end": v(28.36, 39.66) * mm});
            skLineSegment(sketch, "E2619", {"start": v(28.36, 39.66) * mm, "end": v(26.34, 41.03) * mm});
            skLineSegment(sketch, "E2620", {"start": v(26.34, 41.03) * mm, "end": v(24.26, 42.3) * mm});
            skLineSegment(sketch, "E2621", {"start": v(24.26, 42.3) * mm, "end": v(22.11, 43.45) * mm});
            skLineSegment(sketch, "E2622", {"start": v(22.11, 43.45) * mm, "end": v(19.91, 44.5) * mm});
            skLineSegment(sketch, "E2623", {"start": v(19.91, 44.5) * mm, "end": v(17.66, 45.44) * mm});
            skLineSegment(sketch, "E2624", {"start": v(17.66, 45.44) * mm, "end": v(15.37, 46.27) * mm});
            skLineSegment(sketch, "E2625", {"start": v(15.37, 46.27) * mm, "end": v(13.04, 46.98) * mm});
            skLineSegment(sketch, "E2626", {"start": v(13.04, 46.98) * mm, "end": v(10.68, 47.57) * mm});
            skLineSegment(sketch, "E2627", {"start": v(10.68, 47.57) * mm, "end": v(8.29, 48.04) * mm});
            skLineSegment(sketch, "E2628", {"start": v(8.29, 48.04) * mm, "end": v(5.87, 48.4) * mm});
            skLineSegment(sketch, "E2629", {"start": v(5.87, 48.4) * mm, "end": v(3.45, 48.63) * mm});
            skLineSegment(sketch, "E2630", {"start": v(3.45, 48.63) * mm, "end": v(1.01, 48.74) * mm});
            skLineSegment(sketch, "E2631", {"start": v(1.01, 48.74) * mm, "end": v(-1.42, 48.73) * mm});
            skLineSegment(sketch, "E2632", {"start": v(-1.42, 48.73) * mm, "end": v(-3.86, 48.6) * mm});
            skLineSegment(sketch, "E2633", {"start": v(-3.86, 48.6) * mm, "end": v(-6.28, 48.35) * mm});
            skLineSegment(sketch, "E2634", {"start": v(-6.28, 48.35) * mm, "end": v(-8.7, 47.97) * mm});
            skLineSegment(sketch, "E2635", {"start": v(-8.7, 47.97) * mm, "end": v(-11.08, 47.48) * mm});
            skLineSegment(sketch, "E2636", {"start": v(-11.08, 47.48) * mm, "end": v(-13.44, 46.87) * mm});
            skLineSegment(sketch, "E2637", {"start": v(-13.44, 46.87) * mm, "end": v(-15.76, 46.14) * mm});
            skLineSegment(sketch, "E2638", {"start": v(-15.76, 46.14) * mm, "end": v(-18.05, 45.3) * mm});
            skLineSegment(sketch, "E2639", {"start": v(-18.05, 45.3) * mm, "end": v(-20.29, 44.33) * mm});
            skLineSegment(sketch, "E2640", {"start": v(-20.29, 44.33) * mm, "end": v(-22.48, 43.26) * mm});
            skLineSegment(sketch, "E2641", {"start": v(-22.48, 43.26) * mm, "end": v(-24.61, 42.08) * mm});
            skLineSegment(sketch, "E2642", {"start": v(-24.61, 42.08) * mm, "end": v(-26.68, 40.8) * mm});
            skLineSegment(sketch, "E2643", {"start": v(-26.68, 40.8) * mm, "end": v(-28.7, 39.42) * mm});
            skLineSegment(sketch, "E2644", {"start": v(-28.7, 39.42) * mm, "end": v(-30.62, 37.93) * mm});
            skLineSegment(sketch, "E2645", {"start": v(-30.62, 37.93) * mm, "end": v(-32.48, 36.36) * mm});
            skLineSegment(sketch, "E2646", {"start": v(-32.48, 36.36) * mm, "end": v(-34.26, 34.69) * mm});
            skLineSegment(sketch, "E2647", {"start": v(-34.26, 34.69) * mm, "end": v(-35.95, 32.93) * mm});
            skLineSegment(sketch, "E2648", {"start": v(-35.95, 32.93) * mm, "end": v(-37.55, 31.1) * mm});
            skLineSegment(sketch, "E2649", {"start": v(-37.55, 31.1) * mm, "end": v(-39.06, 29.18) * mm});
            skLineSegment(sketch, "E2650", {"start": v(-39.06, 29.18) * mm, "end": v(-40.47, 27.2) * mm});
            skLineSegment(sketch, "E2651", {"start": v(-40.47, 27.2) * mm, "end": v(-41.77, 25.13) * mm});
            skLineSegment(sketch, "E2652", {"start": v(-41.77, 25.13) * mm, "end": v(-42.98, 23.01) * mm});
            skLineSegment(sketch, "E2653", {"start": v(-42.98, 23.01) * mm, "end": v(-44.07, 20.84) * mm});
            skLineSegment(sketch, "E2654", {"start": v(-44.07, 20.84) * mm, "end": v(-45.06, 18.6) * mm});
            skLineSegment(sketch, "E2655", {"start": v(-45.06, 18.6) * mm, "end": v(-45.93, 16.33) * mm});
            skLineSegment(sketch, "E2656", {"start": v(-45.93, 16.33) * mm, "end": v(-46.7, 14.02) * mm});
            skLineSegment(sketch, "E2657", {"start": v(-46.7, 14.02) * mm, "end": v(-47.34, 11.67) * mm});
            skLineSegment(sketch, "E2658", {"start": v(-47.34, 11.67) * mm, "end": v(-47.86, 9.29) * mm});
            skLineSegment(sketch, "E2659", {"start": v(-47.86, 9.29) * mm, "end": v(-48.26, 6.88) * mm});
            skLineSegment(sketch, "E2660", {"start": v(-48.26, 6.88) * mm, "end": v(-48.55, 4.46) * mm});
            skLineSegment(sketch, "E2661", {"start": v(-48.55, 4.46) * mm, "end": v(-48.7, 2.03) * mm});
            skLineSegment(sketch, "E2662", {"start": v(-48.7, 2.03) * mm, "end": v(-48.75, -0.4) * mm});
            skLineSegment(sketch, "E2663", {"start": v(-48.75, -0.4) * mm, "end": v(-48.67, -2.84) * mm});
            skLineSegment(sketch, "E2664", {"start": v(-48.67, -2.84) * mm, "end": v(-48.46, -5.27) * mm});
            skLineSegment(sketch, "E2665", {"start": v(-48.46, -5.27) * mm, "end": v(-48.14, -7.69) * mm});
            skLineSegment(sketch, "E2666", {"start": v(-48.14, -7.69) * mm, "end": v(-47.7, -10.08) * mm});
            skLineSegment(sketch, "E2667", {"start": v(-47.7, -10.08) * mm, "end": v(-47.13, -12.45) * mm});
            skLineSegment(sketch, "E2668", {"start": v(-47.13, -12.45) * mm, "end": v(-46.45, -14.8) * mm});
            skLineSegment(sketch, "E2669", {"start": v(-46.45, -14.8) * mm, "end": v(-45.65, -17.1) * mm});
            skLineSegment(sketch, "E2670", {"start": v(-45.65, -17.1) * mm, "end": v(-44.74, -19.36) * mm});
            skLineSegment(sketch, "E2671", {"start": v(-44.74, -19.36) * mm, "end": v(-43.72, -21.57) * mm});
            skLineSegment(sketch, "E2672", {"start": v(-43.72, -21.57) * mm, "end": v(-42.59, -23.73) * mm});
            skLineSegment(sketch, "E2673", {"start": v(-42.59, -23.73) * mm, "end": v(-41.35, -25.83) * mm});
            skLineSegment(sketch, "E2674", {"start": v(-41.35, -25.83) * mm, "end": v(-40, -27.86) * mm});
            skLineSegment(sketch, "E2675", {"start": v(-40, -27.86) * mm, "end": v(-38.56, -29.82) * mm});
            skLineSegment(sketch, "E2676", {"start": v(-38.56, -29.82) * mm, "end": v(-37.02, -31.71) * mm});
            skLineSegment(sketch, "E2677", {"start": v(-37.02, -31.71) * mm, "end": v(-35.4, -33.53) * mm});
            skLineSegment(sketch, "E2678", {"start": v(-35.4, -33.53) * mm, "end": v(-33.67, -35.25) * mm});
            skLineSegment(sketch, "E2679", {"start": v(-33.67, -35.25) * mm, "end": v(-31.87, -36.9) * mm});
            skLineSegment(sketch, "E2680", {"start": v(-31.87, -36.9) * mm, "end": v(-29.98, -38.44) * mm});
            skLineSegment(sketch, "E2681", {"start": v(-29.98, -38.44) * mm, "end": v(-28.02, -39.89) * mm});
            skLineSegment(sketch, "E2682", {"start": v(-28.02, -39.89) * mm, "end": v(-26, -41.24) * mm});
            skLineSegment(sketch, "E2683", {"start": v(-26, -41.24) * mm, "end": v(-23.9, -42.49) * mm});
            skLineSegment(sketch, "E2684", {"start": v(-23.9, -42.49) * mm, "end": v(-21.75, -43.63) * mm});
            skLineSegment(sketch, "E2685", {"start": v(-21.75, -43.63) * mm, "end": v(-19.54, -44.66) * mm});
            skLineSegment(sketch, "E2686", {"start": v(-19.54, -44.66) * mm, "end": v(-17.28, -45.58) * mm});
            skLineSegment(sketch, "E2687", {"start": v(-17.28, -45.58) * mm, "end": v(-14.98, -46.39) * mm});
            skLineSegment(sketch, "E2688", {"start": v(-14.98, -46.39) * mm, "end": v(-12.65, -47.08) * mm});
            skLineSegment(sketch, "E2689", {"start": v(-12.65, -47.08) * mm, "end": v(-10.28, -47.65) * mm});
            skLineSegment(sketch, "E2690", {"start": v(-10.28, -47.65) * mm, "end": v(-7.88, -48.1) * mm});
            skLineSegment(sketch, "E2691", {"start": v(-7.88, -48.1) * mm, "end": v(-5.47, -48.44) * mm});
            skLineSegment(sketch, "E2692", {"start": v(-5.47, -48.44) * mm, "end": v(-3.04, -48.65) * mm});
            skLineSegment(sketch, "E2693", {"start": v(-3.04, -48.65) * mm, "end": v(-0.6, -48.74) * mm});
            skLineSegment(sketch, "E2694", {"start": v(-0.6, -48.74) * mm, "end": v(1.83, -48.71) * mm});
            skLineSegment(sketch, "E2695", {"start": v(1.83, -48.71) * mm, "end": v(4.26, -48.56) * mm});
            skLineSegment(sketch, "E2696", {"start": v(4.26, -48.56) * mm, "end": v(6.69, -48.29) * mm});
            skLineSegment(sketch, "E2697", {"start": v(6.69, -48.29) * mm, "end": v(9.1, -47.9) * mm});
            skLineSegment(sketch, "E2698", {"start": v(9.1, -47.9) * mm, "end": v(11.47, -47.38) * mm});
            skLineSegment(sketch, "E2699", {"start": v(11.47, -47.38) * mm, "end": v(13.83, -46.74) * mm});
            skLineSegment(sketch, "E2700", {"start": v(13.83, -46.74) * mm, "end": v(16.15, -46) * mm});
            skLineSegment(sketch, "E2701", {"start": v(16.15, -46) * mm, "end": v(18.43, -45.13) * mm});
            skLineSegment(sketch, "E2702", {"start": v(18.43, -45.13) * mm, "end": v(20.66, -44.15) * mm});
            skLineSegment(sketch, "E2703", {"start": v(20.66, -44.15) * mm, "end": v(22.84, -43.07) * mm});
            skLineSegment(sketch, "E2704", {"start": v(22.84, -43.07) * mm, "end": v(24.96, -41.87) * mm});
            skLineSegment(sketch, "E2705", {"start": v(24.96, -41.87) * mm, "end": v(27.02, -40.57) * mm});
            skLineSegment(sketch, "E2706", {"start": v(27.02, -40.57) * mm, "end": v(29.02, -39.17) * mm});
            skLineSegment(sketch, "E2707", {"start": v(29.02, -39.17) * mm, "end": v(30.94, -37.67) * mm});
            skLineSegment(sketch, "E2708", {"start": v(30.94, -37.67) * mm, "end": v(32.78, -36.08) * mm});
            skLineSegment(sketch, "E2709", {"start": v(32.78, -36.08) * mm, "end": v(34.55, -34.4) * mm});
            skLineSegment(sketch, "E2710", {"start": v(34.55, -34.4) * mm, "end": v(36.22, -32.62) * mm});
            skLineSegment(sketch, "E2711", {"start": v(36.22, -32.62) * mm, "end": v(37.8, -30.77) * mm});
            skLineSegment(sketch, "E2712", {"start": v(37.8, -30.77) * mm, "end": v(39.3, -28.84) * mm});
            skLineSegment(sketch, "E2713", {"start": v(39.3, -28.84) * mm, "end": v(40.7, -26.84) * mm});
            skLineSegment(sketch, "E2714", {"start": v(40.7, -26.84) * mm, "end": v(41.98, -24.78) * mm});
            skLineSegment(sketch, "E2715", {"start": v(41.98, -24.78) * mm, "end": v(43.17, -22.65) * mm});
            skLineSegment(sketch, "E2716", {"start": v(43.17, -22.65) * mm, "end": v(44.25, -20.46) * mm});
            skLineSegment(sketch, "E2717", {"start": v(44.25, -20.46) * mm, "end": v(45.21, -18.22) * mm});
            skLineSegment(sketch, "E2718", {"start": v(45.21, -18.22) * mm, "end": v(46.07, -15.94) * mm});
            skLineSegment(sketch, "E2719", {"start": v(46.07, -15.94) * mm, "end": v(46.8, -13.62) * mm});
            skLineSegment(sketch, "E2720", {"start": v(46.8, -13.62) * mm, "end": v(47.43, -11.26) * mm});
            skLineSegment(sketch, "E2721", {"start": v(47.43, -11.26) * mm, "end": v(47.93, -8.88) * mm});
            skLineSegment(sketch, "E2722", {"start": v(47.93, -8.88) * mm, "end": v(48.32, -6.47) * mm});
            skLineSegment(sketch, "E2723", {"start": v(48.32, -6.47) * mm, "end": v(48.58, -4.05) * mm});
            skLineSegment(sketch, "E2724", {"start": v(48.58, -4.05) * mm, "end": v(48.72, -1.61) * mm});
            skLineSegment(sketch, "E2725", {"start": v(48.72, -1.61) * mm, "end": v(48.75, 0) * mm});
            skLineSegment(sketch, "E2726", {"start": v(41.22, -1.58) * mm, "end": v(41.26, -1.57) * mm});
            skLineSegment(sketch, "E2727", {"start": v(41.26, -1.57) * mm, "end": v(41.43, -1.54) * mm});
            skLineSegment(sketch, "E2728", {"start": v(41.43, -1.54) * mm, "end": v(41.6, -1.5) * mm});
            skLineSegment(sketch, "E2729", {"start": v(41.6, -1.5) * mm, "end": v(41.78, -1.45) * mm});
            skLineSegment(sketch, "E2730", {"start": v(41.78, -1.45) * mm, "end": v(41.96, -1.4) * mm});
            skLineSegment(sketch, "E2731", {"start": v(41.96, -1.4) * mm, "end": v(42.13, -1.36) * mm});
            skLineSegment(sketch, "E2732", {"start": v(42.13, -1.36) * mm, "end": v(42.3, -1.31) * mm});
            skLineSegment(sketch, "E2733", {"start": v(42.3, -1.31) * mm, "end": v(42.48, -1.26) * mm});
            skLineSegment(sketch, "E2734", {"start": v(42.48, -1.26) * mm, "end": v(42.65, -1.2) * mm});
            skLineSegment(sketch, "E2735", {"start": v(42.65, -1.2) * mm, "end": v(42.82, -1.15) * mm});
            skLineSegment(sketch, "E2736", {"start": v(42.82, -1.15) * mm, "end": v(43, -1.09) * mm});
            skLineSegment(sketch, "E2737", {"start": v(43, -1.09) * mm, "end": v(43.17, -1.02) * mm});
            skLineSegment(sketch, "E2738", {"start": v(43.17, -1.02) * mm, "end": v(43.36, -0.95) * mm});
            skLineSegment(sketch, "E2739", {"start": v(43.36, -0.95) * mm, "end": v(43.52, -0.89) * mm});
            skLineSegment(sketch, "E2740", {"start": v(43.52, -0.89) * mm, "end": v(43.68, -0.82) * mm});
            skLineSegment(sketch, "E2741", {"start": v(43.68, -0.82) * mm, "end": v(43.85, -0.75) * mm});
            skLineSegment(sketch, "E2742", {"start": v(43.85, -0.75) * mm, "end": v(44.02, -0.68) * mm});
            skLineSegment(sketch, "E2743", {"start": v(44.02, -0.68) * mm, "end": v(44.2, -0.6) * mm});
            skLineSegment(sketch, "E2744", {"start": v(44.2, -0.6) * mm, "end": v(44.37, -0.53) * mm});
            skLineSegment(sketch, "E2745", {"start": v(44.37, -0.53) * mm, "end": v(44.56, -0.44) * mm});
            skLineSegment(sketch, "E2746", {"start": v(44.56, -0.44) * mm, "end": v(44.62, -0.41) * mm});
            skLineSegment(sketch, "E2747", {"start": v(44.62, -0.41) * mm, "end": v(44.62, -0.23) * mm});
            skLineSegment(sketch, "E2748", {"start": v(44.62, -0.23) * mm, "end": v(44.62, -0.04) * mm});
            skLineSegment(sketch, "E2749", {"start": v(44.62, -0.04) * mm, "end": v(44.62, 0.14) * mm});
            skLineSegment(sketch, "E2750", {"start": v(44.62, 0.14) * mm, "end": v(44.62, 0.33) * mm});
            skLineSegment(sketch, "E2751", {"start": v(44.62, 0.33) * mm, "end": v(44.62, 0.42) * mm});
            skLineSegment(sketch, "E2752", {"start": v(44.62, 0.42) * mm, "end": v(44.45, 0.5) * mm});
            skLineSegment(sketch, "E2753", {"start": v(44.45, 0.5) * mm, "end": v(44.28, 0.57) * mm});
            skLineSegment(sketch, "E2754", {"start": v(44.28, 0.57) * mm, "end": v(44.12, 0.65) * mm});
            skLineSegment(sketch, "E2755", {"start": v(44.12, 0.65) * mm, "end": v(43.96, 0.72) * mm});
            skLineSegment(sketch, "E2756", {"start": v(43.96, 0.72) * mm, "end": v(43.8, 0.78) * mm});
            skLineSegment(sketch, "E2757", {"start": v(43.8, 0.78) * mm, "end": v(43.63, 0.85) * mm});
            skLineSegment(sketch, "E2758", {"start": v(43.63, 0.85) * mm, "end": v(43.45, 0.92) * mm});
            skLineSegment(sketch, "E2759", {"start": v(43.45, 0.92) * mm, "end": v(43.27, 0.99) * mm});
            skLineSegment(sketch, "E2760", {"start": v(43.27, 0.99) * mm, "end": v(43.1, 1.05) * mm});
            skLineSegment(sketch, "E2761", {"start": v(43.1, 1.05) * mm, "end": v(42.92, 1.12) * mm});
            skLineSegment(sketch, "E2762", {"start": v(42.92, 1.12) * mm, "end": v(42.74, 1.18) * mm});
            skLineSegment(sketch, "E2763", {"start": v(42.74, 1.18) * mm, "end": v(42.56, 1.24) * mm});
            skLineSegment(sketch, "E2764", {"start": v(42.56, 1.24) * mm, "end": v(42.39, 1.3) * mm});
            skLineSegment(sketch, "E2765", {"start": v(42.39, 1.3) * mm, "end": v(42.2, 1.35) * mm});
            skLineSegment(sketch, "E2766", {"start": v(42.2, 1.35) * mm, "end": v(42.03, 1.4) * mm});
            skLineSegment(sketch, "E2767", {"start": v(42.03, 1.4) * mm, "end": v(41.86, 1.44) * mm});
            skLineSegment(sketch, "E2768", {"start": v(41.86, 1.44) * mm, "end": v(41.67, 1.49) * mm});
            skLineSegment(sketch, "E2769", {"start": v(41.67, 1.49) * mm, "end": v(41.49, 1.53) * mm});
            skLineSegment(sketch, "E2770", {"start": v(41.49, 1.53) * mm, "end": v(41.3, 1.57) * mm});
            skLineSegment(sketch, "E2771", {"start": v(41.3, 1.57) * mm, "end": v(41.22, 1.59) * mm});
            skLineSegment(sketch, "E2772", {"start": v(41.22, 1.59) * mm, "end": v(41.21, 1.77) * mm});
            skLineSegment(sketch, "E2773", {"start": v(41.21, 1.77) * mm, "end": v(41.2, 1.97) * mm});
            skLineSegment(sketch, "E2774", {"start": v(41.2, 1.97) * mm, "end": v(41.2, 2.16) * mm});
            skLineSegment(sketch, "E2775", {"start": v(41.2, 2.16) * mm, "end": v(41.18, 2.36) * mm});
            skLineSegment(sketch, "E2776", {"start": v(41.18, 2.36) * mm, "end": v(41.17, 2.55) * mm});
            skLineSegment(sketch, "E2777", {"start": v(41.17, 2.55) * mm, "end": v(41.16, 2.74) * mm});
            skLineSegment(sketch, "E2778", {"start": v(41.16, 2.74) * mm, "end": v(41.15, 2.93) * mm});
            skLineSegment(sketch, "E2779", {"start": v(41.15, 2.93) * mm, "end": v(41.15, 2.97) * mm});
            skLineSegment(sketch, "E2780", {"start": v(41.15, 2.97) * mm, "end": v(41.31, 3.02) * mm});
            skLineSegment(sketch, "E2781", {"start": v(41.31, 3.02) * mm, "end": v(41.48, 3.08) * mm});
            skLineSegment(sketch, "E2782", {"start": v(41.48, 3.08) * mm, "end": v(41.65, 3.14) * mm});
            skLineSegment(sketch, "E2783", {"start": v(41.65, 3.14) * mm, "end": v(41.82, 3.2) * mm});
            skLineSegment(sketch, "E2784", {"start": v(41.82, 3.2) * mm, "end": v(41.98, 3.26) * mm});
            skLineSegment(sketch, "E2785", {"start": v(41.98, 3.26) * mm, "end": v(42.15, 3.33) * mm});
            skLineSegment(sketch, "E2786", {"start": v(42.15, 3.33) * mm, "end": v(42.32, 3.4) * mm});
            skLineSegment(sketch, "E2787", {"start": v(42.32, 3.4) * mm, "end": v(42.48, 3.48) * mm});
            skLineSegment(sketch, "E2788", {"start": v(42.48, 3.48) * mm, "end": v(42.64, 3.55) * mm});
            skLineSegment(sketch, "E2789", {"start": v(42.64, 3.55) * mm, "end": v(42.8, 3.63) * mm});
            skLineSegment(sketch, "E2790", {"start": v(42.8, 3.63) * mm, "end": v(42.97, 3.7) * mm});
            skLineSegment(sketch, "E2791", {"start": v(42.97, 3.7) * mm, "end": v(43.15, 3.8) * mm});
            skLineSegment(sketch, "E2792", {"start": v(43.15, 3.8) * mm, "end": v(43.3, 3.88) * mm});
            skLineSegment(sketch, "E2793", {"start": v(43.3, 3.88) * mm, "end": v(43.45, 3.96) * mm});
            skLineSegment(sketch, "E2794", {"start": v(43.45, 3.96) * mm, "end": v(43.61, 4.04) * mm});
            skLineSegment(sketch, "E2795", {"start": v(43.61, 4.04) * mm, "end": v(43.78, 4.13) * mm});
            skLineSegment(sketch, "E2796", {"start": v(43.78, 4.13) * mm, "end": v(43.94, 4.23) * mm});
            skLineSegment(sketch, "E2797", {"start": v(43.94, 4.23) * mm, "end": v(44.1, 4.33) * mm});
            skLineSegment(sketch, "E2798", {"start": v(44.1, 4.33) * mm, "end": v(44.28, 4.43) * mm});
            skLineSegment(sketch, "E2799", {"start": v(44.28, 4.43) * mm, "end": v(44.4, 4.5) * mm});
            skLineSegment(sketch, "E2800", {"start": v(44.4, 4.5) * mm, "end": v(44.38, 4.68) * mm});
            skLineSegment(sketch, "E2801", {"start": v(44.38, 4.68) * mm, "end": v(44.36, 4.87) * mm});
            skLineSegment(sketch, "E2802", {"start": v(44.36, 4.87) * mm, "end": v(44.34, 5.05) * mm});
            skLineSegment(sketch, "E2803", {"start": v(44.34, 5.05) * mm, "end": v(44.32, 5.24) * mm});
            skLineSegment(sketch, "E2804", {"start": v(44.32, 5.24) * mm, "end": v(44.3, 5.32) * mm});
            skLineSegment(sketch, "E2805", {"start": v(44.3, 5.32) * mm, "end": v(44.12, 5.39) * mm});
            skLineSegment(sketch, "E2806", {"start": v(44.12, 5.39) * mm, "end": v(43.95, 5.44) * mm});
            skLineSegment(sketch, "E2807", {"start": v(43.95, 5.44) * mm, "end": v(43.78, 5.5) * mm});
            skLineSegment(sketch, "E2808", {"start": v(43.78, 5.5) * mm, "end": v(43.61, 5.55) * mm});
            skLineSegment(sketch, "E2809", {"start": v(43.61, 5.55) * mm, "end": v(43.45, 5.6) * mm});
            skLineSegment(sketch, "E2810", {"start": v(43.45, 5.6) * mm, "end": v(43.27, 5.65) * mm});
            skLineSegment(sketch, "E2811", {"start": v(43.27, 5.65) * mm, "end": v(43.09, 5.7) * mm});
            skLineSegment(sketch, "E2812", {"start": v(43.09, 5.7) * mm, "end": v(42.9, 5.74) * mm});
            skLineSegment(sketch, "E2813", {"start": v(42.9, 5.74) * mm, "end": v(42.72, 5.79) * mm});
            skLineSegment(sketch, "E2814", {"start": v(42.72, 5.79) * mm, "end": v(42.53, 5.83) * mm});
            skLineSegment(sketch, "E2815", {"start": v(42.53, 5.83) * mm, "end": v(42.35, 5.87) * mm});
            skLineSegment(sketch, "E2816", {"start": v(42.35, 5.87) * mm, "end": v(42.17, 5.91) * mm});
            skLineSegment(sketch, "E2817", {"start": v(42.17, 5.91) * mm, "end": v(42, 5.95) * mm});
            skLineSegment(sketch, "E2818", {"start": v(42, 5.95) * mm, "end": v(41.8, 5.98) * mm});
            skLineSegment(sketch, "E2819", {"start": v(41.8, 5.98) * mm, "end": v(41.62, 6.01) * mm});
            skLineSegment(sketch, "E2820", {"start": v(41.62, 6.01) * mm, "end": v(41.44, 6.04) * mm});
            skLineSegment(sketch, "E2821", {"start": v(41.44, 6.04) * mm, "end": v(41.26, 6.06) * mm});
            skLineSegment(sketch, "E2822", {"start": v(41.26, 6.06) * mm, "end": v(41.07, 6.08) * mm});
            skLineSegment(sketch, "E2823", {"start": v(41.07, 6.08) * mm, "end": v(40.88, 6.1) * mm});
            skLineSegment(sketch, "E2824", {"start": v(40.88, 6.1) * mm, "end": v(40.8, 6.11) * mm});
            skLineSegment(sketch, "E2825", {"start": v(40.8, 6.11) * mm, "end": v(40.77, 6.3) * mm});
            skLineSegment(sketch, "E2826", {"start": v(40.77, 6.3) * mm, "end": v(40.74, 6.5) * mm});
            skLineSegment(sketch, "E2827", {"start": v(40.74, 6.5) * mm, "end": v(40.7, 6.68) * mm});
            skLineSegment(sketch, "E2828", {"start": v(40.7, 6.68) * mm, "end": v(40.67, 6.87) * mm});
            skLineSegment(sketch, "E2829", {"start": v(40.67, 6.87) * mm, "end": v(40.64, 7.06) * mm});
            skLineSegment(sketch, "E2830", {"start": v(40.64, 7.06) * mm, "end": v(40.6, 7.26) * mm});
            skLineSegment(sketch, "E2831", {"start": v(40.6, 7.26) * mm, "end": v(40.58, 7.44) * mm});
            skLineSegment(sketch, "E2832", {"start": v(40.58, 7.44) * mm, "end": v(40.57, 7.48) * mm});
            skLineSegment(sketch, "E2833", {"start": v(40.57, 7.48) * mm, "end": v(40.73, 7.55) * mm});
            skLineSegment(sketch, "E2834", {"start": v(40.73, 7.55) * mm, "end": v(40.9, 7.62) * mm});
            skLineSegment(sketch, "E2835", {"start": v(40.9, 7.62) * mm, "end": v(41.05, 7.7) * mm});
            skLineSegment(sketch, "E2836", {"start": v(41.05, 7.7) * mm, "end": v(41.21, 7.78) * mm});
            skLineSegment(sketch, "E2837", {"start": v(41.21, 7.78) * mm, "end": v(41.37, 7.86) * mm});
            skLineSegment(sketch, "E2838", {"start": v(41.37, 7.86) * mm, "end": v(41.52, 7.95) * mm});
            skLineSegment(sketch, "E2839", {"start": v(41.52, 7.95) * mm, "end": v(41.69, 8.04) * mm});
            skLineSegment(sketch, "E2840", {"start": v(41.69, 8.04) * mm, "end": v(41.84, 8.13) * mm});
            skLineSegment(sketch, "E2841", {"start": v(41.84, 8.13) * mm, "end": v(41.99, 8.22) * mm});
            skLineSegment(sketch, "E2842", {"start": v(41.99, 8.22) * mm, "end": v(42.14, 8.31) * mm});
            skLineSegment(sketch, "E2843", {"start": v(42.14, 8.31) * mm, "end": v(42.3, 8.41) * mm});
            skLineSegment(sketch, "E2844", {"start": v(42.3, 8.41) * mm, "end": v(42.47, 8.52) * mm});
            skLineSegment(sketch, "E2845", {"start": v(42.47, 8.52) * mm, "end": v(42.61, 8.62) * mm});
            skLineSegment(sketch, "E2846", {"start": v(42.61, 8.62) * mm, "end": v(42.76, 8.71) * mm});
            skLineSegment(sketch, "E2847", {"start": v(42.76, 8.71) * mm, "end": v(42.9, 8.82) * mm});
            skLineSegment(sketch, "E2848", {"start": v(42.9, 8.82) * mm, "end": v(43.06, 8.93) * mm});
            skLineSegment(sketch, "E2849", {"start": v(43.06, 8.93) * mm, "end": v(43.2, 9.04) * mm});
            skLineSegment(sketch, "E2850", {"start": v(43.2, 9.04) * mm, "end": v(43.36, 9.15) * mm});
            skLineSegment(sketch, "E2851", {"start": v(43.36, 9.15) * mm, "end": v(43.52, 9.27) * mm});
            skLineSegment(sketch, "E2852", {"start": v(43.52, 9.27) * mm, "end": v(43.63, 9.36) * mm});
            skLineSegment(sketch, "E2853", {"start": v(43.63, 9.36) * mm, "end": v(43.6, 9.54) * mm});
            skLineSegment(sketch, "E2854", {"start": v(43.6, 9.54) * mm, "end": v(43.55, 9.72) * mm});
            skLineSegment(sketch, "E2855", {"start": v(43.55, 9.72) * mm, "end": v(43.51, 9.9) * mm});
            skLineSegment(sketch, "E2856", {"start": v(43.51, 9.9) * mm, "end": v(43.47, 10.08) * mm});
            skLineSegment(sketch, "E2857", {"start": v(43.47, 10.08) * mm, "end": v(43.45, 10.17) * mm});
            skLineSegment(sketch, "E2858", {"start": v(43.45, 10.17) * mm, "end": v(43.26, 10.2) * mm});
            skLineSegment(sketch, "E2859", {"start": v(43.26, 10.2) * mm, "end": v(43.09, 10.24) * mm});
            skLineSegment(sketch, "E2860", {"start": v(43.09, 10.24) * mm, "end": v(42.91, 10.28) * mm});
            skLineSegment(sketch, "E2861", {"start": v(42.91, 10.28) * mm, "end": v(42.74, 10.31) * mm});
            skLineSegment(sketch, "E2862", {"start": v(42.74, 10.31) * mm, "end": v(42.57, 10.34) * mm});
            skLineSegment(sketch, "E2863", {"start": v(42.57, 10.34) * mm, "end": v(42.39, 10.37) * mm});
            skLineSegment(sketch, "E2864", {"start": v(42.39, 10.37) * mm, "end": v(42.2, 10.4) * mm});
            skLineSegment(sketch, "E2865", {"start": v(42.2, 10.4) * mm, "end": v(42.01, 10.43) * mm});
            skLineSegment(sketch, "E2866", {"start": v(42.01, 10.43) * mm, "end": v(41.82, 10.45) * mm});
            skLineSegment(sketch, "E2867", {"start": v(41.82, 10.45) * mm, "end": v(41.64, 10.48) * mm});
            skLineSegment(sketch, "E2868", {"start": v(41.64, 10.48) * mm, "end": v(41.45, 10.5) * mm});
            skLineSegment(sketch, "E2869", {"start": v(41.45, 10.5) * mm, "end": v(41.26, 10.51) * mm});
            skLineSegment(sketch, "E2870", {"start": v(41.26, 10.51) * mm, "end": v(41.08, 10.53) * mm});
            skLineSegment(sketch, "E2871", {"start": v(41.08, 10.53) * mm, "end": v(40.89, 10.54) * mm});
            skLineSegment(sketch, "E2872", {"start": v(40.89, 10.54) * mm, "end": v(40.7, 10.55) * mm});
            skLineSegment(sketch, "E2873", {"start": v(40.7, 10.55) * mm, "end": v(40.53, 10.56) * mm});
            skLineSegment(sketch, "E2874", {"start": v(40.53, 10.56) * mm, "end": v(40.34, 10.56) * mm});
            skLineSegment(sketch, "E2875", {"start": v(40.34, 10.56) * mm, "end": v(40.15, 10.57) * mm});
            skLineSegment(sketch, "E2876", {"start": v(40.15, 10.57) * mm, "end": v(39.96, 10.56) * mm});
            skLineSegment(sketch, "E2877", {"start": v(39.96, 10.56) * mm, "end": v(39.88, 10.56) * mm});
            skLineSegment(sketch, "E2878", {"start": v(39.88, 10.56) * mm, "end": v(39.83, 10.74) * mm});
            skLineSegment(sketch, "E2879", {"start": v(39.83, 10.74) * mm, "end": v(39.77, 10.93) * mm});
            skLineSegment(sketch, "E2880", {"start": v(39.77, 10.93) * mm, "end": v(39.72, 11.12) * mm});
            skLineSegment(sketch, "E2881", {"start": v(39.72, 11.12) * mm, "end": v(39.67, 11.3) * mm});
            skLineSegment(sketch, "E2882", {"start": v(39.67, 11.3) * mm, "end": v(39.62, 11.49) * mm});
            skLineSegment(sketch, "E2883", {"start": v(39.62, 11.49) * mm, "end": v(39.56, 11.68) * mm});
            skLineSegment(sketch, "E2884", {"start": v(39.56, 11.68) * mm, "end": v(39.51, 11.86) * mm});
            skLineSegment(sketch, "E2885", {"start": v(39.51, 11.86) * mm, "end": v(39.5, 11.9) * mm});
            skLineSegment(sketch, "E2886", {"start": v(39.5, 11.9) * mm, "end": v(39.65, 11.98) * mm});
            skLineSegment(sketch, "E2887", {"start": v(39.65, 11.98) * mm, "end": v(39.8, 12.08) * mm});
            skLineSegment(sketch, "E2888", {"start": v(39.8, 12.08) * mm, "end": v(39.95, 12.17) * mm});
            skLineSegment(sketch, "E2889", {"start": v(39.95, 12.17) * mm, "end": v(40.1, 12.27) * mm});
            skLineSegment(sketch, "E2890", {"start": v(40.1, 12.27) * mm, "end": v(40.25, 12.37) * mm});
            skLineSegment(sketch, "E2891", {"start": v(40.25, 12.37) * mm, "end": v(40.4, 12.47) * mm});
            skLineSegment(sketch, "E2892", {"start": v(40.4, 12.47) * mm, "end": v(40.55, 12.58) * mm});
            skLineSegment(sketch, "E2893", {"start": v(40.55, 12.58) * mm, "end": v(40.69, 12.68) * mm});
            skLineSegment(sketch, "E2894", {"start": v(40.69, 12.68) * mm, "end": v(40.83, 12.79) * mm});
            skLineSegment(sketch, "E2895", {"start": v(40.83, 12.79) * mm, "end": v(40.97, 12.9) * mm});
            skLineSegment(sketch, "E2896", {"start": v(40.97, 12.9) * mm, "end": v(41.12, 13.02) * mm});
            skLineSegment(sketch, "E2897", {"start": v(41.12, 13.02) * mm, "end": v(41.27, 13.14) * mm});
            skLineSegment(sketch, "E2898", {"start": v(41.27, 13.14) * mm, "end": v(41.4, 13.25) * mm});
            skLineSegment(sketch, "E2899", {"start": v(41.4, 13.25) * mm, "end": v(41.54, 13.37) * mm});
            skLineSegment(sketch, "E2900", {"start": v(41.54, 13.37) * mm, "end": v(41.67, 13.48) * mm});
            skLineSegment(sketch, "E2901", {"start": v(41.67, 13.48) * mm, "end": v(41.81, 13.6) * mm});
            skLineSegment(sketch, "E2902", {"start": v(41.81, 13.6) * mm, "end": v(41.95, 13.74) * mm});
            skLineSegment(sketch, "E2903", {"start": v(41.95, 13.74) * mm, "end": v(42.1, 13.87) * mm});
            skLineSegment(sketch, "E2904", {"start": v(42.1, 13.87) * mm, "end": v(42.24, 14) * mm});
            skLineSegment(sketch, "E2905", {"start": v(42.24, 14) * mm, "end": v(42.34, 14.1) * mm});
            skLineSegment(sketch, "E2906", {"start": v(42.34, 14.1) * mm, "end": v(42.28, 14.28) * mm});
            skLineSegment(sketch, "E2907", {"start": v(42.28, 14.28) * mm, "end": v(42.22, 14.45) * mm});
            skLineSegment(sketch, "E2908", {"start": v(42.22, 14.45) * mm, "end": v(42.16, 14.63) * mm});
            skLineSegment(sketch, "E2909", {"start": v(42.16, 14.63) * mm, "end": v(42.1, 14.8) * mm});
            skLineSegment(sketch, "E2910", {"start": v(42.1, 14.8) * mm, "end": v(42.07, 14.88) * mm});
            skLineSegment(sketch, "E2911", {"start": v(42.07, 14.88) * mm, "end": v(41.88, 14.9) * mm});
            skLineSegment(sketch, "E2912", {"start": v(41.88, 14.9) * mm, "end": v(41.7, 14.92) * mm});
            skLineSegment(sketch, "E2913", {"start": v(41.7, 14.92) * mm, "end": v(41.52, 14.94) * mm});
            skLineSegment(sketch, "E2914", {"start": v(41.52, 14.94) * mm, "end": v(41.35, 14.95) * mm});
            skLineSegment(sketch, "E2915", {"start": v(41.35, 14.95) * mm, "end": v(41.18, 14.96) * mm});
            skLineSegment(sketch, "E2916", {"start": v(41.18, 14.96) * mm, "end": v(40.99, 14.97) * mm});
            skLineSegment(sketch, "E2917", {"start": v(40.99, 14.97) * mm, "end": v(40.8, 14.98) * mm});
            skLineSegment(sketch, "E2918", {"start": v(40.8, 14.98) * mm, "end": v(40.6, 14.99) * mm});
            skLineSegment(sketch, "E2919", {"start": v(40.6, 14.99) * mm, "end": v(40.42, 15) * mm});
            skLineSegment(sketch, "E2920", {"start": v(40.42, 15) * mm, "end": v(40.23, 15) * mm});
            skLineSegment(sketch, "E2921", {"start": v(40.23, 15) * mm, "end": v(40.16, 15) * mm});
            skLineSegment(sketch, "E2922", {"start": v(40.16, 15) * mm, "end": v(39.97, 15) * mm});
            skLineSegment(sketch, "E2923", {"start": v(39.97, 15) * mm, "end": v(39.78, 14.99) * mm});
            skLineSegment(sketch, "E2924", {"start": v(39.78, 14.99) * mm, "end": v(39.6, 14.98) * mm});
            skLineSegment(sketch, "E2925", {"start": v(39.6, 14.98) * mm, "end": v(39.42, 14.97) * mm});
            skLineSegment(sketch, "E2926", {"start": v(39.42, 14.97) * mm, "end": v(39.24, 14.96) * mm});
            skLineSegment(sketch, "E2927", {"start": v(39.24, 14.96) * mm, "end": v(39.07, 14.95) * mm});
            skLineSegment(sketch, "E2928", {"start": v(39.07, 14.95) * mm, "end": v(38.88, 14.93) * mm});
            skLineSegment(sketch, "E2929", {"start": v(38.88, 14.93) * mm, "end": v(38.7, 14.91) * mm});
            skLineSegment(sketch, "E2930", {"start": v(38.7, 14.91) * mm, "end": v(38.5, 14.89) * mm});
            skLineSegment(sketch, "E2931", {"start": v(38.5, 14.89) * mm, "end": v(38.47, 14.88) * mm});
            skLineSegment(sketch, "E2932", {"start": v(38.47, 14.88) * mm, "end": v(38.4, 15.06) * mm});
            skLineSegment(sketch, "E2933", {"start": v(38.4, 15.06) * mm, "end": v(38.33, 15.24) * mm});
            skLineSegment(sketch, "E2934", {"start": v(38.33, 15.24) * mm, "end": v(38.26, 15.42) * mm});
            skLineSegment(sketch, "E2935", {"start": v(38.26, 15.42) * mm, "end": v(38.19, 15.6) * mm});
            skLineSegment(sketch, "E2936", {"start": v(38.19, 15.6) * mm, "end": v(38.11, 15.78) * mm});
            skLineSegment(sketch, "E2937", {"start": v(38.11, 15.78) * mm, "end": v(38.04, 15.96) * mm});
            skLineSegment(sketch, "E2938", {"start": v(38.04, 15.96) * mm, "end": v(37.97, 16.14) * mm});
            skLineSegment(sketch, "E2939", {"start": v(37.97, 16.14) * mm, "end": v(37.96, 16.17) * mm});
            skLineSegment(sketch, "E2940", {"start": v(37.96, 16.17) * mm, "end": v(38.1, 16.27) * mm});
            skLineSegment(sketch, "E2941", {"start": v(38.1, 16.27) * mm, "end": v(38.24, 16.38) * mm});
            skLineSegment(sketch, "E2942", {"start": v(38.24, 16.38) * mm, "end": v(38.37, 16.5) * mm});
            skLineSegment(sketch, "E2943", {"start": v(38.37, 16.5) * mm, "end": v(38.52, 16.6) * mm});
            skLineSegment(sketch, "E2944", {"start": v(38.52, 16.6) * mm, "end": v(38.65, 16.72) * mm});
            skLineSegment(sketch, "E2945", {"start": v(38.65, 16.72) * mm, "end": v(38.78, 16.84) * mm});
            skLineSegment(sketch, "E2946", {"start": v(38.78, 16.84) * mm, "end": v(38.92, 16.96) * mm});
            skLineSegment(sketch, "E2947", {"start": v(38.92, 16.96) * mm, "end": v(39.05, 17.08) * mm});
            skLineSegment(sketch, "E2948", {"start": v(39.05, 17.08) * mm, "end": v(39.18, 17.2) * mm});
            skLineSegment(sketch, "E2949", {"start": v(39.18, 17.2) * mm, "end": v(39.3, 17.33) * mm});
            skLineSegment(sketch, "E2950", {"start": v(39.3, 17.33) * mm, "end": v(39.44, 17.46) * mm});
            skLineSegment(sketch, "E2951", {"start": v(39.44, 17.46) * mm, "end": v(39.58, 17.6) * mm});
            skLineSegment(sketch, "E2952", {"start": v(39.58, 17.6) * mm, "end": v(39.7, 17.73) * mm});
            skLineSegment(sketch, "E2953", {"start": v(39.7, 17.73) * mm, "end": v(39.82, 17.85) * mm});
            skLineSegment(sketch, "E2954", {"start": v(39.82, 17.85) * mm, "end": v(39.94, 17.99) * mm});
            skLineSegment(sketch, "E2955", {"start": v(39.94, 17.99) * mm, "end": v(40.06, 18.12) * mm});
            skLineSegment(sketch, "E2956", {"start": v(40.06, 18.12) * mm, "end": v(40.19, 18.27) * mm});
            skLineSegment(sketch, "E2957", {"start": v(40.19, 18.27) * mm, "end": v(40.31, 18.41) * mm});
            skLineSegment(sketch, "E2958", {"start": v(40.31, 18.41) * mm, "end": v(40.44, 18.57) * mm});
            skLineSegment(sketch, "E2959", {"start": v(40.44, 18.57) * mm, "end": v(40.53, 18.67) * mm});
            skLineSegment(sketch, "E2960", {"start": v(40.53, 18.67) * mm, "end": v(40.45, 18.84) * mm});
            skLineSegment(sketch, "E2961", {"start": v(40.45, 18.84) * mm, "end": v(40.38, 19) * mm});
            skLineSegment(sketch, "E2962", {"start": v(40.38, 19) * mm, "end": v(40.3, 19.17) * mm});
            skLineSegment(sketch, "E2963", {"start": v(40.3, 19.17) * mm, "end": v(40.22, 19.34) * mm});
            skLineSegment(sketch, "E2964", {"start": v(40.22, 19.34) * mm, "end": v(40.18, 19.42) * mm});
            skLineSegment(sketch, "E2965", {"start": v(40.18, 19.42) * mm, "end": v(40.17, 19.42) * mm});
            skLineSegment(sketch, "E2966", {"start": v(40.17, 19.42) * mm, "end": v(39.99, 19.42) * mm});
            skLineSegment(sketch, "E2967", {"start": v(39.99, 19.42) * mm, "end": v(39.8, 19.42) * mm});
            skLineSegment(sketch, "E2968", {"start": v(39.8, 19.42) * mm, "end": v(39.63, 19.41) * mm});
            skLineSegment(sketch, "E2969", {"start": v(39.63, 19.41) * mm, "end": v(39.45, 19.4) * mm});
            skLineSegment(sketch, "E2970", {"start": v(39.45, 19.4) * mm, "end": v(39.28, 19.4) * mm});
            skLineSegment(sketch, "E2971", {"start": v(39.28, 19.4) * mm, "end": v(39.1, 19.4) * mm});
            skLineSegment(sketch, "E2972", {"start": v(39.1, 19.4) * mm, "end": v(38.9, 19.38) * mm});
            skLineSegment(sketch, "E2973", {"start": v(38.9, 19.38) * mm, "end": v(38.71, 19.36) * mm});
            skLineSegment(sketch, "E2974", {"start": v(38.71, 19.36) * mm, "end": v(38.53, 19.35) * mm});
            skLineSegment(sketch, "E2975", {"start": v(38.53, 19.35) * mm, "end": v(38.34, 19.33) * mm});
            skLineSegment(sketch, "E2976", {"start": v(38.34, 19.33) * mm, "end": v(38.15, 19.3) * mm});
            skLineSegment(sketch, "E2977", {"start": v(38.15, 19.3) * mm, "end": v(37.96, 19.28) * mm});
            skLineSegment(sketch, "E2978", {"start": v(37.96, 19.28) * mm, "end": v(37.79, 19.26) * mm});
            skLineSegment(sketch, "E2979", {"start": v(37.79, 19.26) * mm, "end": v(37.6, 19.23) * mm});
            skLineSegment(sketch, "E2980", {"start": v(37.6, 19.23) * mm, "end": v(37.41, 19.2) * mm});
            skLineSegment(sketch, "E2981", {"start": v(37.41, 19.2) * mm, "end": v(37.24, 19.17) * mm});
            skLineSegment(sketch, "E2982", {"start": v(37.24, 19.17) * mm, "end": v(37.06, 19.13) * mm});
            skLineSegment(sketch, "E2983", {"start": v(37.06, 19.13) * mm, "end": v(36.87, 19.1) * mm});
            skLineSegment(sketch, "E2984", {"start": v(36.87, 19.1) * mm, "end": v(36.68, 19.05) * mm});
            skLineSegment(sketch, "E2985", {"start": v(36.68, 19.05) * mm, "end": v(36.6, 19.03) * mm});
            skLineSegment(sketch, "E2986", {"start": v(36.6, 19.03) * mm, "end": v(36.51, 19.2) * mm});
            skLineSegment(sketch, "E2987", {"start": v(36.51, 19.2) * mm, "end": v(36.42, 19.37) * mm});
            skLineSegment(sketch, "E2988", {"start": v(36.42, 19.37) * mm, "end": v(36.33, 19.53) * mm});
            skLineSegment(sketch, "E2989", {"start": v(36.33, 19.53) * mm, "end": v(36.24, 19.7) * mm});
            skLineSegment(sketch, "E2990", {"start": v(36.24, 19.7) * mm, "end": v(36.15, 19.87) * mm});
            skLineSegment(sketch, "E2991", {"start": v(36.15, 19.87) * mm, "end": v(36.05, 20.05) * mm});
            skLineSegment(sketch, "E2992", {"start": v(36.05, 20.05) * mm, "end": v(35.96, 20.21) * mm});
            skLineSegment(sketch, "E2993", {"start": v(35.96, 20.21) * mm, "end": v(35.95, 20.25) * mm});
            skLineSegment(sketch, "E2994", {"start": v(35.95, 20.25) * mm, "end": v(36.07, 20.36) * mm});
            skLineSegment(sketch, "E2995", {"start": v(36.07, 20.36) * mm, "end": v(36.2, 20.49) * mm});
            skLineSegment(sketch, "E2996", {"start": v(36.2, 20.49) * mm, "end": v(36.33, 20.61) * mm});
            skLineSegment(sketch, "E2997", {"start": v(36.33, 20.61) * mm, "end": v(36.46, 20.74) * mm});
            skLineSegment(sketch, "E2998", {"start": v(36.46, 20.74) * mm, "end": v(36.57, 20.87) * mm});
            skLineSegment(sketch, "E2999", {"start": v(36.57, 20.87) * mm, "end": v(36.7, 21) * mm});
            skLineSegment(sketch, "E3000", {"start": v(36.7, 21) * mm, "end": v(36.82, 21.14) * mm});
            skLineSegment(sketch, "E3001", {"start": v(36.82, 21.14) * mm, "end": v(36.93, 21.27) * mm});
            skLineSegment(sketch, "E3002", {"start": v(36.93, 21.27) * mm, "end": v(37.05, 21.4) * mm});
            skLineSegment(sketch, "E3003", {"start": v(37.05, 21.4) * mm, "end": v(37.16, 21.55) * mm});
            skLineSegment(sketch, "E3004", {"start": v(37.16, 21.55) * mm, "end": v(37.28, 21.7) * mm});
            skLineSegment(sketch, "E3005", {"start": v(37.28, 21.7) * mm, "end": v(37.4, 21.85) * mm});
            skLineSegment(sketch, "E3006", {"start": v(37.4, 21.85) * mm, "end": v(37.5, 21.99) * mm});
            skLineSegment(sketch, "E3007", {"start": v(37.5, 21.99) * mm, "end": v(37.61, 22.13) * mm});
            skLineSegment(sketch, "E3008", {"start": v(37.61, 22.13) * mm, "end": v(37.72, 22.27) * mm});
            skLineSegment(sketch, "E3009", {"start": v(37.72, 22.27) * mm, "end": v(37.83, 22.42) * mm});
            skLineSegment(sketch, "E3010", {"start": v(37.83, 22.42) * mm, "end": v(37.93, 22.58) * mm});
            skLineSegment(sketch, "E3011", {"start": v(37.93, 22.58) * mm, "end": v(38.04, 22.74) * mm});
            skLineSegment(sketch, "E3012", {"start": v(38.04, 22.74) * mm, "end": v(38.15, 22.9) * mm});
            skLineSegment(sketch, "E3013", {"start": v(38.15, 22.9) * mm, "end": v(38.23, 23.02) * mm});
            skLineSegment(sketch, "E3014", {"start": v(38.23, 23.02) * mm, "end": v(38.14, 23.18) * mm});
            skLineSegment(sketch, "E3015", {"start": v(38.14, 23.18) * mm, "end": v(38.04, 23.33) * mm});
            skLineSegment(sketch, "E3016", {"start": v(38.04, 23.33) * mm, "end": v(37.94, 23.5) * mm});
            skLineSegment(sketch, "E3017", {"start": v(37.94, 23.5) * mm, "end": v(37.84, 23.65) * mm});
            skLineSegment(sketch, "E3018", {"start": v(37.84, 23.65) * mm, "end": v(37.8, 23.72) * mm});
            skLineSegment(sketch, "E3019", {"start": v(37.8, 23.72) * mm, "end": v(37.6, 23.7) * mm});
            skLineSegment(sketch, "E3020", {"start": v(37.6, 23.7) * mm, "end": v(37.43, 23.68) * mm});
            skLineSegment(sketch, "E3021", {"start": v(37.43, 23.68) * mm, "end": v(37.25, 23.66) * mm});
            skLineSegment(sketch, "E3022", {"start": v(37.25, 23.66) * mm, "end": v(37.08, 23.63) * mm});
            skLineSegment(sketch, "E3023", {"start": v(37.08, 23.63) * mm, "end": v(36.9, 23.6) * mm});
            skLineSegment(sketch, "E3024", {"start": v(36.9, 23.6) * mm, "end": v(36.72, 23.57) * mm});
            skLineSegment(sketch, "E3025", {"start": v(36.72, 23.57) * mm, "end": v(36.54, 23.54) * mm});
            skLineSegment(sketch, "E3026", {"start": v(36.54, 23.54) * mm, "end": v(36.35, 23.5) * mm});
            skLineSegment(sketch, "E3027", {"start": v(36.35, 23.5) * mm, "end": v(36.16, 23.47) * mm});
            skLineSegment(sketch, "E3028", {"start": v(36.16, 23.47) * mm, "end": v(35.98, 23.43) * mm});
            skLineSegment(sketch, "E3029", {"start": v(35.98, 23.43) * mm, "end": v(35.8, 23.39) * mm});
            skLineSegment(sketch, "E3030", {"start": v(35.8, 23.39) * mm, "end": v(35.61, 23.34) * mm});
            skLineSegment(sketch, "E3031", {"start": v(35.61, 23.34) * mm, "end": v(35.44, 23.3) * mm});
            skLineSegment(sketch, "E3032", {"start": v(35.44, 23.3) * mm, "end": v(35.25, 23.25) * mm});
            skLineSegment(sketch, "E3033", {"start": v(35.25, 23.25) * mm, "end": v(35.07, 23.2) * mm});
            skLineSegment(sketch, "E3034", {"start": v(35.07, 23.2) * mm, "end": v(34.9, 23.15) * mm});
            skLineSegment(sketch, "E3035", {"start": v(34.9, 23.15) * mm, "end": v(34.73, 23.1) * mm});
            skLineSegment(sketch, "E3036", {"start": v(34.73, 23.1) * mm, "end": v(34.55, 23.03) * mm});
            skLineSegment(sketch, "E3037", {"start": v(34.55, 23.03) * mm, "end": v(34.36, 22.97) * mm});
            skLineSegment(sketch, "E3038", {"start": v(34.36, 22.97) * mm, "end": v(34.29, 22.94) * mm});
            skLineSegment(sketch, "E3039", {"start": v(34.29, 22.94) * mm, "end": v(34.18, 23.1) * mm});
            skLineSegment(sketch, "E3040", {"start": v(34.18, 23.1) * mm, "end": v(34.07, 23.26) * mm});
            skLineSegment(sketch, "E3041", {"start": v(34.07, 23.26) * mm, "end": v(33.96, 23.41) * mm});
            skLineSegment(sketch, "E3042", {"start": v(33.96, 23.41) * mm, "end": v(33.85, 23.58) * mm});
            skLineSegment(sketch, "E3043", {"start": v(33.85, 23.58) * mm, "end": v(33.74, 23.73) * mm});
            skLineSegment(sketch, "E3044", {"start": v(33.74, 23.73) * mm, "end": v(33.63, 23.9) * mm});
            skLineSegment(sketch, "E3045", {"start": v(33.63, 23.9) * mm, "end": v(33.52, 24.05) * mm});
            skLineSegment(sketch, "E3046", {"start": v(33.52, 24.05) * mm, "end": v(33.5, 24.08) * mm});
            skLineSegment(sketch, "E3047", {"start": v(33.5, 24.08) * mm, "end": v(33.61, 24.2) * mm});
            skLineSegment(sketch, "E3048", {"start": v(33.61, 24.2) * mm, "end": v(33.73, 24.35) * mm});
            skLineSegment(sketch, "E3049", {"start": v(33.73, 24.35) * mm, "end": v(33.84, 24.48) * mm});
            skLineSegment(sketch, "E3050", {"start": v(33.84, 24.48) * mm, "end": v(33.95, 24.63) * mm});
            skLineSegment(sketch, "E3051", {"start": v(33.95, 24.63) * mm, "end": v(34.06, 24.77) * mm});
            skLineSegment(sketch, "E3052", {"start": v(34.06, 24.77) * mm, "end": v(34.16, 24.91) * mm});
            skLineSegment(sketch, "E3053", {"start": v(34.16, 24.91) * mm, "end": v(34.27, 25.07) * mm});
            skLineSegment(sketch, "E3054", {"start": v(34.27, 25.07) * mm, "end": v(34.37, 25.2) * mm});
            skLineSegment(sketch, "E3055", {"start": v(34.37, 25.2) * mm, "end": v(34.47, 25.35) * mm});
            skLineSegment(sketch, "E3056", {"start": v(34.47, 25.35) * mm, "end": v(34.57, 25.5) * mm});
            skLineSegment(sketch, "E3057", {"start": v(34.57, 25.5) * mm, "end": v(34.67, 25.66) * mm});
            skLineSegment(sketch, "E3058", {"start": v(34.67, 25.66) * mm, "end": v(34.77, 25.83) * mm});
            skLineSegment(sketch, "E3059", {"start": v(34.77, 25.83) * mm, "end": v(34.86, 25.98) * mm});
            skLineSegment(sketch, "E3060", {"start": v(34.86, 25.98) * mm, "end": v(34.95, 26.13) * mm});
            skLineSegment(sketch, "E3061", {"start": v(34.95, 26.13) * mm, "end": v(35.04, 26.29) * mm});
            skLineSegment(sketch, "E3062", {"start": v(35.04, 26.29) * mm, "end": v(35.13, 26.45) * mm});
            skLineSegment(sketch, "E3063", {"start": v(35.13, 26.45) * mm, "end": v(35.22, 26.61) * mm});
            skLineSegment(sketch, "E3064", {"start": v(35.22, 26.61) * mm, "end": v(35.31, 26.78) * mm});
            skLineSegment(sketch, "E3065", {"start": v(35.31, 26.78) * mm, "end": v(35.4, 26.96) * mm});
            skLineSegment(sketch, "E3066", {"start": v(35.4, 26.96) * mm, "end": v(35.47, 27.08) * mm});
            skLineSegment(sketch, "E3067", {"start": v(35.47, 27.08) * mm, "end": v(35.35, 27.23) * mm});
            skLineSegment(sketch, "E3068", {"start": v(35.35, 27.23) * mm, "end": v(35.24, 27.38) * mm});
            skLineSegment(sketch, "E3069", {"start": v(35.24, 27.38) * mm, "end": v(35.13, 27.52) * mm});
            skLineSegment(sketch, "E3070", {"start": v(35.13, 27.52) * mm, "end": v(35.01, 27.67) * mm});
            skLineSegment(sketch, "E3071", {"start": v(35.01, 27.67) * mm, "end": v(34.96, 27.74) * mm});
            skLineSegment(sketch, "E3072", {"start": v(34.96, 27.74) * mm, "end": v(34.77, 27.7) * mm});
            skLineSegment(sketch, "E3073", {"start": v(34.77, 27.7) * mm, "end": v(34.6, 27.65) * mm});
            skLineSegment(sketch, "E3074", {"start": v(34.6, 27.65) * mm, "end": v(34.42, 27.6) * mm});
            skLineSegment(sketch, "E3075", {"start": v(34.42, 27.6) * mm, "end": v(34.25, 27.57) * mm});
            skLineSegment(sketch, "E3076", {"start": v(34.25, 27.57) * mm, "end": v(34.09, 27.52) * mm});
            skLineSegment(sketch, "E3077", {"start": v(34.09, 27.52) * mm, "end": v(33.9, 27.47) * mm});
            skLineSegment(sketch, "E3078", {"start": v(33.9, 27.47) * mm, "end": v(33.73, 27.42) * mm});
            skLineSegment(sketch, "E3079", {"start": v(33.73, 27.42) * mm, "end": v(33.54, 27.36) * mm});
            skLineSegment(sketch, "E3080", {"start": v(33.54, 27.36) * mm, "end": v(33.36, 27.3) * mm});
            skLineSegment(sketch, "E3081", {"start": v(33.36, 27.3) * mm, "end": v(33.18, 27.24) * mm});
            skLineSegment(sketch, "E3082", {"start": v(33.18, 27.24) * mm, "end": v(33, 27.18) * mm});
            skLineSegment(sketch, "E3083", {"start": v(33, 27.18) * mm, "end": v(32.83, 27.12) * mm});
            skLineSegment(sketch, "E3084", {"start": v(32.83, 27.12) * mm, "end": v(32.66, 27.06) * mm});
            skLineSegment(sketch, "E3085", {"start": v(32.66, 27.06) * mm, "end": v(32.48, 26.99) * mm});
            skLineSegment(sketch, "E3086", {"start": v(32.48, 26.99) * mm, "end": v(32.3, 26.92) * mm});
            skLineSegment(sketch, "E3087", {"start": v(32.3, 26.92) * mm, "end": v(32.15, 26.85) * mm});
            skLineSegment(sketch, "E3088", {"start": v(32.15, 26.85) * mm, "end": v(31.98, 26.77) * mm});
            skLineSegment(sketch, "E3089", {"start": v(31.98, 26.77) * mm, "end": v(31.8, 26.7) * mm});
            skLineSegment(sketch, "E3090", {"start": v(31.8, 26.7) * mm, "end": v(31.63, 26.6) * mm});
            skLineSegment(sketch, "E3091", {"start": v(31.63, 26.6) * mm, "end": v(31.56, 26.57) * mm});
            skLineSegment(sketch, "E3092", {"start": v(31.56, 26.57) * mm, "end": v(31.43, 26.71) * mm});
            skLineSegment(sketch, "E3093", {"start": v(31.43, 26.71) * mm, "end": v(31.3, 26.86) * mm});
            skLineSegment(sketch, "E3094", {"start": v(31.3, 26.86) * mm, "end": v(31.18, 27) * mm});
            skLineSegment(sketch, "E3095", {"start": v(31.18, 27) * mm, "end": v(31.05, 27.16) * mm});
            skLineSegment(sketch, "E3096", {"start": v(31.05, 27.16) * mm, "end": v(30.93, 27.3) * mm});
            skLineSegment(sketch, "E3097", {"start": v(30.93, 27.3) * mm, "end": v(30.8, 27.45) * mm});
            skLineSegment(sketch, "E3098", {"start": v(30.8, 27.45) * mm, "end": v(30.67, 27.6) * mm});
            skLineSegment(sketch, "E3099", {"start": v(30.67, 27.6) * mm, "end": v(30.65, 27.62) * mm});
            skLineSegment(sketch, "E3100", {"start": v(30.65, 27.62) * mm, "end": v(30.75, 27.76) * mm});
            skLineSegment(sketch, "E3101", {"start": v(30.75, 27.76) * mm, "end": v(30.85, 27.9) * mm});
            skLineSegment(sketch, "E3102", {"start": v(30.85, 27.9) * mm, "end": v(30.94, 28.06) * mm});
            skLineSegment(sketch, "E3103", {"start": v(30.94, 28.06) * mm, "end": v(31.04, 28.21) * mm});
            skLineSegment(sketch, "E3104", {"start": v(31.04, 28.21) * mm, "end": v(31.12, 28.36) * mm});
            skLineSegment(sketch, "E3105", {"start": v(31.12, 28.36) * mm, "end": v(31.21, 28.52) * mm});
            skLineSegment(sketch, "E3106", {"start": v(31.21, 28.52) * mm, "end": v(31.3, 28.68) * mm});
            skLineSegment(sketch, "E3107", {"start": v(31.3, 28.68) * mm, "end": v(31.39, 28.83) * mm});
            skLineSegment(sketch, "E3108", {"start": v(31.39, 28.83) * mm, "end": v(31.47, 29) * mm});
            skLineSegment(sketch, "E3109", {"start": v(31.47, 29) * mm, "end": v(31.55, 29.15) * mm});
            skLineSegment(sketch, "E3110", {"start": v(31.55, 29.15) * mm, "end": v(31.63, 29.32) * mm});
            skLineSegment(sketch, "E3111", {"start": v(31.63, 29.32) * mm, "end": v(31.72, 29.5) * mm});
            skLineSegment(sketch, "E3112", {"start": v(31.72, 29.5) * mm, "end": v(31.8, 29.65) * mm});
            skLineSegment(sketch, "E3113", {"start": v(31.8, 29.65) * mm, "end": v(31.86, 29.82) * mm});
            skLineSegment(sketch, "E3114", {"start": v(31.86, 29.82) * mm, "end": v(31.94, 29.98) * mm});
            skLineSegment(sketch, "E3115", {"start": v(31.94, 29.98) * mm, "end": v(32, 30.15) * mm});
            skLineSegment(sketch, "E3116", {"start": v(32, 30.15) * mm, "end": v(32.08, 30.33) * mm});
            skLineSegment(sketch, "E3117", {"start": v(32.08, 30.33) * mm, "end": v(32.15, 30.5) * mm});
            skLineSegment(sketch, "E3118", {"start": v(32.15, 30.5) * mm, "end": v(32.22, 30.7) * mm});
            skLineSegment(sketch, "E3119", {"start": v(32.22, 30.7) * mm, "end": v(32.27, 30.82) * mm});
            skLineSegment(sketch, "E3120", {"start": v(32.27, 30.82) * mm, "end": v(32.15, 30.96) * mm});
            skLineSegment(sketch, "E3121", {"start": v(32.15, 30.96) * mm, "end": v(32.02, 31.09) * mm});
            skLineSegment(sketch, "E3122", {"start": v(32.02, 31.09) * mm, "end": v(31.89, 31.22) * mm});
            skLineSegment(sketch, "E3123", {"start": v(31.89, 31.22) * mm, "end": v(31.76, 31.35) * mm});
            skLineSegment(sketch, "E3124", {"start": v(31.76, 31.35) * mm, "end": v(31.7, 31.42) * mm});
            skLineSegment(sketch, "E3125", {"start": v(31.7, 31.42) * mm, "end": v(31.51, 31.35) * mm});
            skLineSegment(sketch, "E3126", {"start": v(31.51, 31.35) * mm, "end": v(31.34, 31.3) * mm});
            skLineSegment(sketch, "E3127", {"start": v(31.34, 31.3) * mm, "end": v(31.18, 31.23) * mm});
            skLineSegment(sketch, "E3128", {"start": v(31.18, 31.23) * mm, "end": v(31.01, 31.17) * mm});
            skLineSegment(sketch, "E3129", {"start": v(31.01, 31.17) * mm, "end": v(30.85, 31.1) * mm});
            skLineSegment(sketch, "E3130", {"start": v(30.85, 31.1) * mm, "end": v(30.68, 31.03) * mm});
            skLineSegment(sketch, "E3131", {"start": v(30.68, 31.03) * mm, "end": v(30.5, 30.96) * mm});
            skLineSegment(sketch, "E3132", {"start": v(30.5, 30.96) * mm, "end": v(30.33, 30.89) * mm});
            skLineSegment(sketch, "E3133", {"start": v(30.33, 30.89) * mm, "end": v(30.16, 30.8) * mm});
            skLineSegment(sketch, "E3134", {"start": v(30.16, 30.8) * mm, "end": v(29.99, 30.73) * mm});
            skLineSegment(sketch, "E3135", {"start": v(29.99, 30.73) * mm, "end": v(29.81, 30.65) * mm});
            skLineSegment(sketch, "E3136", {"start": v(29.81, 30.65) * mm, "end": v(29.65, 30.57) * mm});
            skLineSegment(sketch, "E3137", {"start": v(29.65, 30.57) * mm, "end": v(29.49, 30.48) * mm});
            skLineSegment(sketch, "E3138", {"start": v(29.49, 30.48) * mm, "end": v(29.32, 30.4) * mm});
            skLineSegment(sketch, "E3139", {"start": v(29.32, 30.4) * mm, "end": v(29.15, 30.3) * mm});
            skLineSegment(sketch, "E3140", {"start": v(29.15, 30.3) * mm, "end": v(29, 30.22) * mm});
            skLineSegment(sketch, "E3141", {"start": v(29, 30.22) * mm, "end": v(28.84, 30.13) * mm});
            skLineSegment(sketch, "E3142", {"start": v(28.84, 30.13) * mm, "end": v(28.67, 30.03) * mm});
            skLineSegment(sketch, "E3143", {"start": v(28.67, 30.03) * mm, "end": v(28.5, 29.92) * mm});
            skLineSegment(sketch, "E3144", {"start": v(28.5, 29.92) * mm, "end": v(28.44, 29.88) * mm});
            skLineSegment(sketch, "E3145", {"start": v(28.44, 29.88) * mm, "end": v(28.3, 30) * mm});
            skLineSegment(sketch, "E3146", {"start": v(28.3, 30) * mm, "end": v(28.16, 30.15) * mm});
            skLineSegment(sketch, "E3147", {"start": v(28.16, 30.15) * mm, "end": v(28.02, 30.27) * mm});
            skLineSegment(sketch, "E3148", {"start": v(28.02, 30.27) * mm, "end": v(27.88, 30.4) * mm});
            skLineSegment(sketch, "E3149", {"start": v(27.88, 30.4) * mm, "end": v(27.74, 30.54) * mm});
            skLineSegment(sketch, "E3150", {"start": v(27.74, 30.54) * mm, "end": v(27.59, 30.67) * mm});
            skLineSegment(sketch, "E3151", {"start": v(27.59, 30.67) * mm, "end": v(27.45, 30.8) * mm});
            skLineSegment(sketch, "E3152", {"start": v(27.45, 30.8) * mm, "end": v(27.43, 30.82) * mm});
            skLineSegment(sketch, "E3153", {"start": v(27.43, 30.82) * mm, "end": v(27.5, 30.97) * mm});
            skLineSegment(sketch, "E3154", {"start": v(27.5, 30.97) * mm, "end": v(27.6, 31.13) * mm});
            skLineSegment(sketch, "E3155", {"start": v(27.6, 31.13) * mm, "end": v(27.67, 31.3) * mm});
            skLineSegment(sketch, "E3156", {"start": v(27.67, 31.3) * mm, "end": v(27.75, 31.46) * mm});
            skLineSegment(sketch, "E3157", {"start": v(27.75, 31.46) * mm, "end": v(27.82, 31.61) * mm});
            skLineSegment(sketch, "E3158", {"start": v(27.82, 31.61) * mm, "end": v(27.89, 31.78) * mm});
            skLineSegment(sketch, "E3159", {"start": v(27.89, 31.78) * mm, "end": v(27.96, 31.95) * mm});
            skLineSegment(sketch, "E3160", {"start": v(27.96, 31.95) * mm, "end": v(28.02, 32.11) * mm});
            skLineSegment(sketch, "E3161", {"start": v(28.02, 32.11) * mm, "end": v(28.09, 32.28) * mm});
            skLineSegment(sketch, "E3162", {"start": v(28.09, 32.28) * mm, "end": v(28.15, 32.45) * mm});
            skLineSegment(sketch, "E3163", {"start": v(28.15, 32.45) * mm, "end": v(28.22, 32.63) * mm});
            skLineSegment(sketch, "E3164", {"start": v(28.22, 32.63) * mm, "end": v(28.28, 32.8) * mm});
            skLineSegment(sketch, "E3165", {"start": v(28.28, 32.8) * mm, "end": v(28.34, 32.97) * mm});
            skLineSegment(sketch, "E3166", {"start": v(28.34, 32.97) * mm, "end": v(28.39, 33.14) * mm});
            skLineSegment(sketch, "E3167", {"start": v(28.39, 33.14) * mm, "end": v(28.44, 33.31) * mm});
            skLineSegment(sketch, "E3168", {"start": v(28.44, 33.31) * mm, "end": v(28.5, 33.49) * mm});
            skLineSegment(sketch, "E3169", {"start": v(28.5, 33.49) * mm, "end": v(28.55, 33.67) * mm});
            skLineSegment(sketch, "E3170", {"start": v(28.55, 33.67) * mm, "end": v(28.6, 33.86) * mm});
            skLineSegment(sketch, "E3171", {"start": v(28.6, 33.86) * mm, "end": v(28.65, 34.05) * mm});
            skLineSegment(sketch, "E3172", {"start": v(28.65, 34.05) * mm, "end": v(28.69, 34.19) * mm});
            skLineSegment(sketch, "E3173", {"start": v(28.69, 34.19) * mm, "end": v(28.55, 34.3) * mm});
            skLineSegment(sketch, "E3174", {"start": v(28.55, 34.3) * mm, "end": v(28.4, 34.42) * mm});
            skLineSegment(sketch, "E3175", {"start": v(28.4, 34.42) * mm, "end": v(28.26, 34.54) * mm});
            skLineSegment(sketch, "E3176", {"start": v(28.26, 34.54) * mm, "end": v(28.12, 34.66) * mm});
            skLineSegment(sketch, "E3177", {"start": v(28.12, 34.66) * mm, "end": v(28.05, 34.71) * mm});
            skLineSegment(sketch, "E3178", {"start": v(28.05, 34.71) * mm, "end": v(27.87, 34.63) * mm});
            skLineSegment(sketch, "E3179", {"start": v(27.87, 34.63) * mm, "end": v(27.71, 34.55) * mm});
            skLineSegment(sketch, "E3180", {"start": v(27.71, 34.55) * mm, "end": v(27.55, 34.47) * mm});
            skLineSegment(sketch, "E3181", {"start": v(27.55, 34.47) * mm, "end": v(27.4, 34.39) * mm});
            skLineSegment(sketch, "E3182", {"start": v(27.4, 34.39) * mm, "end": v(27.25, 34.31) * mm});
            skLineSegment(sketch, "E3183", {"start": v(27.25, 34.31) * mm, "end": v(27.08, 34.22) * mm});
            skLineSegment(sketch, "E3184", {"start": v(27.08, 34.22) * mm, "end": v(26.91, 34.13) * mm});
            skLineSegment(sketch, "E3185", {"start": v(26.91, 34.13) * mm, "end": v(26.75, 34.03) * mm});
            skLineSegment(sketch, "E3186", {"start": v(26.75, 34.03) * mm, "end": v(26.59, 33.94) * mm});
            skLineSegment(sketch, "E3187", {"start": v(26.59, 33.94) * mm, "end": v(26.42, 33.84) * mm});
            skLineSegment(sketch, "E3188", {"start": v(26.42, 33.84) * mm, "end": v(26.26, 33.74) * mm});
            skLineSegment(sketch, "E3189", {"start": v(26.26, 33.74) * mm, "end": v(26.1, 33.64) * mm});
            skLineSegment(sketch, "E3190", {"start": v(26.1, 33.64) * mm, "end": v(25.95, 33.54) * mm});
            skLineSegment(sketch, "E3191", {"start": v(25.95, 33.54) * mm, "end": v(25.8, 33.44) * mm});
            skLineSegment(sketch, "E3192", {"start": v(25.8, 33.44) * mm, "end": v(25.64, 33.33) * mm});
            skLineSegment(sketch, "E3193", {"start": v(25.64, 33.33) * mm, "end": v(25.5, 33.23) * mm});
            skLineSegment(sketch, "E3194", {"start": v(25.5, 33.23) * mm, "end": v(25.35, 33.12) * mm});
            skLineSegment(sketch, "E3195", {"start": v(25.35, 33.12) * mm, "end": v(25.2, 33) * mm});
            skLineSegment(sketch, "E3196", {"start": v(25.2, 33) * mm, "end": v(25.04, 32.88) * mm});
            skLineSegment(sketch, "E3197", {"start": v(25.04, 32.88) * mm, "end": v(24.98, 32.83) * mm});
            skLineSegment(sketch, "E3198", {"start": v(24.98, 32.83) * mm, "end": v(24.83, 32.94) * mm});
            skLineSegment(sketch, "E3199", {"start": v(24.83, 32.94) * mm, "end": v(24.67, 33.06) * mm});
            skLineSegment(sketch, "E3200", {"start": v(24.67, 33.06) * mm, "end": v(24.52, 33.17) * mm});
            skLineSegment(sketch, "E3201", {"start": v(24.52, 33.17) * mm, "end": v(24.36, 33.3) * mm});
            skLineSegment(sketch, "E3202", {"start": v(24.36, 33.3) * mm, "end": v(24.2, 33.4) * mm});
            skLineSegment(sketch, "E3203", {"start": v(24.2, 33.4) * mm, "end": v(24.05, 33.52) * mm});
            skLineSegment(sketch, "E3204", {"start": v(24.05, 33.52) * mm, "end": v(23.9, 33.63) * mm});
            skLineSegment(sketch, "E3205", {"start": v(23.9, 33.63) * mm, "end": v(23.87, 33.65) * mm});
            skLineSegment(sketch, "E3206", {"start": v(23.87, 33.65) * mm, "end": v(23.93, 33.8) * mm});
            skLineSegment(sketch, "E3207", {"start": v(23.93, 33.8) * mm, "end": v(24, 33.98) * mm});
            skLineSegment(sketch, "E3208", {"start": v(24, 33.98) * mm, "end": v(24.06, 34.14) * mm});
            skLineSegment(sketch, "E3209", {"start": v(24.06, 34.14) * mm, "end": v(24.12, 34.32) * mm});
            skLineSegment(sketch, "E3210", {"start": v(24.12, 34.32) * mm, "end": v(24.17, 34.48) * mm});
            skLineSegment(sketch, "E3211", {"start": v(24.17, 34.48) * mm, "end": v(24.22, 34.65) * mm});
            skLineSegment(sketch, "E3212", {"start": v(24.22, 34.65) * mm, "end": v(24.28, 34.84) * mm});
            skLineSegment(sketch, "E3213", {"start": v(24.28, 34.84) * mm, "end": v(24.32, 35) * mm});
            skLineSegment(sketch, "E3214", {"start": v(24.32, 35) * mm, "end": v(24.37, 35.17) * mm});
            skLineSegment(sketch, "E3215", {"start": v(24.37, 35.17) * mm, "end": v(24.41, 35.35) * mm});
            skLineSegment(sketch, "E3216", {"start": v(24.41, 35.35) * mm, "end": v(24.46, 35.53) * mm});
            skLineSegment(sketch, "E3217", {"start": v(24.46, 35.53) * mm, "end": v(24.5, 35.72) * mm});
            skLineSegment(sketch, "E3218", {"start": v(24.5, 35.72) * mm, "end": v(24.54, 35.89) * mm});
            skLineSegment(sketch, "E3219", {"start": v(24.54, 35.89) * mm, "end": v(24.57, 36.06) * mm});
            skLineSegment(sketch, "E3220", {"start": v(24.57, 36.06) * mm, "end": v(24.6, 36.24) * mm});
            skLineSegment(sketch, "E3221", {"start": v(24.6, 36.24) * mm, "end": v(24.64, 36.42) * mm});
            skLineSegment(sketch, "E3222", {"start": v(24.64, 36.42) * mm, "end": v(24.67, 36.6) * mm});
            skLineSegment(sketch, "E3223", {"start": v(24.67, 36.6) * mm, "end": v(24.7, 36.8) * mm});
            skLineSegment(sketch, "E3224", {"start": v(24.7, 36.8) * mm, "end": v(24.73, 37) * mm});
            skLineSegment(sketch, "E3225", {"start": v(24.73, 37) * mm, "end": v(24.75, 37.13) * mm});
            skLineSegment(sketch, "E3226", {"start": v(24.75, 37.13) * mm, "end": v(24.6, 37.24) * mm});
            skLineSegment(sketch, "E3227", {"start": v(24.6, 37.24) * mm, "end": v(24.44, 37.34) * mm});
            skLineSegment(sketch, "E3228", {"start": v(24.44, 37.34) * mm, "end": v(24.29, 37.44) * mm});
            skLineSegment(sketch, "E3229", {"start": v(24.29, 37.44) * mm, "end": v(24.13, 37.54) * mm});
            skLineSegment(sketch, "E3230", {"start": v(24.13, 37.54) * mm, "end": v(24.06, 37.59) * mm});
            skLineSegment(sketch, "E3231", {"start": v(24.06, 37.59) * mm, "end": v(23.9, 37.49) * mm});
            skLineSegment(sketch, "E3232", {"start": v(23.9, 37.49) * mm, "end": v(23.74, 37.39) * mm});
            skLineSegment(sketch, "E3233", {"start": v(23.74, 37.39) * mm, "end": v(23.6, 37.3) * mm});
            skLineSegment(sketch, "E3234", {"start": v(23.6, 37.3) * mm, "end": v(23.45, 37.2) * mm});
            skLineSegment(sketch, "E3235", {"start": v(23.45, 37.2) * mm, "end": v(23.3, 37.1) * mm});
            skLineSegment(sketch, "E3236", {"start": v(23.3, 37.1) * mm, "end": v(23.15, 37) * mm});
            skLineSegment(sketch, "E3237", {"start": v(23.15, 37) * mm, "end": v(23, 36.88) * mm});
            skLineSegment(sketch, "E3238", {"start": v(23, 36.88) * mm, "end": v(22.84, 36.77) * mm});
            skLineSegment(sketch, "E3239", {"start": v(22.84, 36.77) * mm, "end": v(22.7, 36.66) * mm});
            skLineSegment(sketch, "E3240", {"start": v(22.7, 36.66) * mm, "end": v(22.54, 36.54) * mm});
            skLineSegment(sketch, "E3241", {"start": v(22.54, 36.54) * mm, "end": v(22.4, 36.43) * mm});
            skLineSegment(sketch, "E3242", {"start": v(22.4, 36.43) * mm, "end": v(22.24, 36.3) * mm});
            skLineSegment(sketch, "E3243", {"start": v(22.24, 36.3) * mm, "end": v(22.1, 36.2) * mm});
            skLineSegment(sketch, "E3244", {"start": v(22.1, 36.2) * mm, "end": v(21.96, 36.07) * mm});
            skLineSegment(sketch, "E3245", {"start": v(21.96, 36.07) * mm, "end": v(21.82, 35.95) * mm});
            skLineSegment(sketch, "E3246", {"start": v(21.82, 35.95) * mm, "end": v(21.69, 35.83) * mm});
            skLineSegment(sketch, "E3247", {"start": v(21.69, 35.83) * mm, "end": v(21.55, 35.7) * mm});
            skLineSegment(sketch, "E3248", {"start": v(21.55, 35.7) * mm, "end": v(21.41, 35.57) * mm});
            skLineSegment(sketch, "E3249", {"start": v(21.41, 35.57) * mm, "end": v(21.28, 35.43) * mm});
            skLineSegment(sketch, "E3250", {"start": v(21.28, 35.43) * mm, "end": v(21.22, 35.38) * mm});
            skLineSegment(sketch, "E3251", {"start": v(21.22, 35.38) * mm, "end": v(21.06, 35.47) * mm});
            skLineSegment(sketch, "E3252", {"start": v(21.06, 35.47) * mm, "end": v(20.89, 35.57) * mm});
            skLineSegment(sketch, "E3253", {"start": v(20.89, 35.57) * mm, "end": v(20.72, 35.67) * mm});
            skLineSegment(sketch, "E3254", {"start": v(20.72, 35.67) * mm, "end": v(20.55, 35.77) * mm});
            skLineSegment(sketch, "E3255", {"start": v(20.55, 35.77) * mm, "end": v(20.39, 35.86) * mm});
            skLineSegment(sketch, "E3256", {"start": v(20.39, 35.86) * mm, "end": v(20.22, 35.96) * mm});
            skLineSegment(sketch, "E3257", {"start": v(20.22, 35.96) * mm, "end": v(20.05, 36.06) * mm});
            skLineSegment(sketch, "E3258", {"start": v(20.05, 36.06) * mm, "end": v(20.02, 36.07) * mm});
            skLineSegment(sketch, "E3259", {"start": v(20.02, 36.07) * mm, "end": v(20.07, 36.24) * mm});
            skLineSegment(sketch, "E3260", {"start": v(20.07, 36.24) * mm, "end": v(20.11, 36.41) * mm});
            skLineSegment(sketch, "E3261", {"start": v(20.11, 36.41) * mm, "end": v(20.16, 36.58) * mm});
            skLineSegment(sketch, "E3262", {"start": v(20.16, 36.58) * mm, "end": v(20.2, 36.76) * mm});
            skLineSegment(sketch, "E3263", {"start": v(20.2, 36.76) * mm, "end": v(20.23, 36.93) * mm});
            skLineSegment(sketch, "E3264", {"start": v(20.23, 36.93) * mm, "end": v(20.26, 37.1) * mm});
            skLineSegment(sketch, "E3265", {"start": v(20.26, 37.1) * mm, "end": v(20.3, 37.3) * mm});
            skLineSegment(sketch, "E3266", {"start": v(20.3, 37.3) * mm, "end": v(20.32, 37.46) * mm});
            skLineSegment(sketch, "E3267", {"start": v(20.32, 37.46) * mm, "end": v(20.35, 37.64) * mm});
            skLineSegment(sketch, "E3268", {"start": v(20.35, 37.64) * mm, "end": v(20.38, 37.82) * mm});
            skLineSegment(sketch, "E3269", {"start": v(20.38, 37.82) * mm, "end": v(20.4, 38) * mm});
            skLineSegment(sketch, "E3270", {"start": v(20.4, 38) * mm, "end": v(20.42, 38.2) * mm});
            skLineSegment(sketch, "E3271", {"start": v(20.42, 38.2) * mm, "end": v(20.44, 38.37) * mm});
            skLineSegment(sketch, "E3272", {"start": v(20.44, 38.37) * mm, "end": v(20.46, 38.55) * mm});
            skLineSegment(sketch, "E3273", {"start": v(20.46, 38.55) * mm, "end": v(20.47, 38.73) * mm});
            skLineSegment(sketch, "E3274", {"start": v(20.47, 38.73) * mm, "end": v(20.48, 38.91) * mm});
            skLineSegment(sketch, "E3275", {"start": v(20.48, 38.91) * mm, "end": v(20.5, 39.1) * mm});
            skLineSegment(sketch, "E3276", {"start": v(20.5, 39.1) * mm, "end": v(20.5, 39.3) * mm});
            skLineSegment(sketch, "E3277", {"start": v(20.5, 39.3) * mm, "end": v(20.51, 39.5) * mm});
            skLineSegment(sketch, "E3278", {"start": v(20.51, 39.5) * mm, "end": v(20.52, 39.63) * mm});
            skLineSegment(sketch, "E3279", {"start": v(20.52, 39.63) * mm, "end": v(20.35, 39.72) * mm});
            skLineSegment(sketch, "E3280", {"start": v(20.35, 39.72) * mm, "end": v(20.19, 39.8) * mm});
            skLineSegment(sketch, "E3281", {"start": v(20.19, 39.8) * mm, "end": v(20.02, 39.88) * mm});
            skLineSegment(sketch, "E3282", {"start": v(20.02, 39.88) * mm, "end": v(19.86, 39.97) * mm});
            skLineSegment(sketch, "E3283", {"start": v(19.86, 39.97) * mm, "end": v(19.78, 40) * mm});
            skLineSegment(sketch, "E3284", {"start": v(19.78, 40) * mm, "end": v(19.63, 39.89) * mm});
            skLineSegment(sketch, "E3285", {"start": v(19.63, 39.89) * mm, "end": v(19.49, 39.77) * mm});
            skLineSegment(sketch, "E3286", {"start": v(19.49, 39.77) * mm, "end": v(19.35, 39.66) * mm});
            skLineSegment(sketch, "E3287", {"start": v(19.35, 39.66) * mm, "end": v(19.21, 39.55) * mm});
            skLineSegment(sketch, "E3288", {"start": v(19.21, 39.55) * mm, "end": v(19.08, 39.44) * mm});
            skLineSegment(sketch, "E3289", {"start": v(19.08, 39.44) * mm, "end": v(18.94, 39.31) * mm});
            skLineSegment(sketch, "E3290", {"start": v(18.94, 39.31) * mm, "end": v(18.8, 39.19) * mm});
            skLineSegment(sketch, "E3291", {"start": v(18.8, 39.19) * mm, "end": v(18.66, 39.06) * mm});
            skLineSegment(sketch, "E3292", {"start": v(18.66, 39.06) * mm, "end": v(18.52, 38.93) * mm});
            skLineSegment(sketch, "E3293", {"start": v(18.52, 38.93) * mm, "end": v(18.38, 38.8) * mm});
            skLineSegment(sketch, "E3294", {"start": v(18.38, 38.8) * mm, "end": v(18.25, 38.67) * mm});
            skLineSegment(sketch, "E3295", {"start": v(18.25, 38.67) * mm, "end": v(18.12, 38.54) * mm});
            skLineSegment(sketch, "E3296", {"start": v(18.12, 38.54) * mm, "end": v(18, 38.4) * mm});
            skLineSegment(sketch, "E3297", {"start": v(18, 38.4) * mm, "end": v(17.86, 38.27) * mm});
            skLineSegment(sketch, "E3298", {"start": v(17.86, 38.27) * mm, "end": v(17.73, 38.13) * mm});
            skLineSegment(sketch, "E3299", {"start": v(17.73, 38.13) * mm, "end": v(17.62, 38) * mm});
            skLineSegment(sketch, "E3300", {"start": v(17.62, 38) * mm, "end": v(17.5, 37.86) * mm});
            skLineSegment(sketch, "E3301", {"start": v(17.5, 37.86) * mm, "end": v(17.37, 37.71) * mm});
            skLineSegment(sketch, "E3302", {"start": v(17.37, 37.71) * mm, "end": v(17.25, 37.56) * mm});
            skLineSegment(sketch, "E3303", {"start": v(17.25, 37.56) * mm, "end": v(17.2, 37.5) * mm});
            skLineSegment(sketch, "E3304", {"start": v(17.2, 37.5) * mm, "end": v(17.03, 37.57) * mm});
            skLineSegment(sketch, "E3305", {"start": v(17.03, 37.57) * mm, "end": v(16.85, 37.66) * mm});
            skLineSegment(sketch, "E3306", {"start": v(16.85, 37.66) * mm, "end": v(16.67, 37.73) * mm});
            skLineSegment(sketch, "E3307", {"start": v(16.67, 37.73) * mm, "end": v(16.5, 37.81) * mm});
            skLineSegment(sketch, "E3308", {"start": v(16.5, 37.81) * mm, "end": v(16.32, 37.89) * mm});
            skLineSegment(sketch, "E3309", {"start": v(16.32, 37.89) * mm, "end": v(16.14, 37.97) * mm});
            skLineSegment(sketch, "E3310", {"start": v(16.14, 37.97) * mm, "end": v(15.97, 38.04) * mm});
            skLineSegment(sketch, "E3311", {"start": v(15.97, 38.04) * mm, "end": v(15.94, 38.06) * mm});
            skLineSegment(sketch, "E3312", {"start": v(15.94, 38.06) * mm, "end": v(15.96, 38.23) * mm});
            skLineSegment(sketch, "E3313", {"start": v(15.96, 38.23) * mm, "end": v(15.99, 38.4) * mm});
            skLineSegment(sketch, "E3314", {"start": v(15.99, 38.4) * mm, "end": v(16, 38.58) * mm});
            skLineSegment(sketch, "E3315", {"start": v(16, 38.58) * mm, "end": v(16.03, 38.76) * mm});
            skLineSegment(sketch, "E3316", {"start": v(16.03, 38.76) * mm, "end": v(16.04, 38.93) * mm});
            skLineSegment(sketch, "E3317", {"start": v(16.04, 38.93) * mm, "end": v(16.06, 39.11) * mm});
            skLineSegment(sketch, "E3318", {"start": v(16.06, 39.11) * mm, "end": v(16.07, 39.3) * mm});
            skLineSegment(sketch, "E3319", {"start": v(16.07, 39.3) * mm, "end": v(16.08, 39.47) * mm});
            skLineSegment(sketch, "E3320", {"start": v(16.08, 39.47) * mm, "end": v(16.09, 39.65) * mm});
            skLineSegment(sketch, "E3321", {"start": v(16.09, 39.65) * mm, "end": v(16.1, 39.83) * mm});
            skLineSegment(sketch, "E3322", {"start": v(16.1, 39.83) * mm, "end": v(16.1, 40.02) * mm});
            skLineSegment(sketch, "E3323", {"start": v(16.1, 40.02) * mm, "end": v(16.1, 40.21) * mm});
            skLineSegment(sketch, "E3324", {"start": v(16.1, 40.21) * mm, "end": v(16.1, 40.39) * mm});
            skLineSegment(sketch, "E3325", {"start": v(16.1, 40.39) * mm, "end": v(16.1, 40.56) * mm});
            skLineSegment(sketch, "E3326", {"start": v(16.1, 40.56) * mm, "end": v(16.09, 40.74) * mm});
            skLineSegment(sketch, "E3327", {"start": v(16.09, 40.74) * mm, "end": v(16.08, 40.93) * mm});
            skLineSegment(sketch, "E3328", {"start": v(16.08, 40.93) * mm, "end": v(16.07, 41.12) * mm});
            skLineSegment(sketch, "E3329", {"start": v(16.07, 41.12) * mm, "end": v(16.06, 41.31) * mm});
            skLineSegment(sketch, "E3330", {"start": v(16.06, 41.31) * mm, "end": v(16.04, 41.5) * mm});
            skLineSegment(sketch, "E3331", {"start": v(16.04, 41.5) * mm, "end": v(16.03, 41.65) * mm});
            skLineSegment(sketch, "E3332", {"start": v(16.03, 41.65) * mm, "end": v(15.86, 41.71) * mm});
            skLineSegment(sketch, "E3333", {"start": v(15.86, 41.71) * mm, "end": v(15.69, 41.78) * mm});
            skLineSegment(sketch, "E3334", {"start": v(15.69, 41.78) * mm, "end": v(15.52, 41.84) * mm});
            skLineSegment(sketch, "E3335", {"start": v(15.52, 41.84) * mm, "end": v(15.34, 41.9) * mm});
            skLineSegment(sketch, "E3336", {"start": v(15.34, 41.9) * mm, "end": v(15.26, 41.94) * mm});
            skLineSegment(sketch, "E3337", {"start": v(15.26, 41.94) * mm, "end": v(15.12, 41.8) * mm});
            skLineSegment(sketch, "E3338", {"start": v(15.12, 41.8) * mm, "end": v(15, 41.68) * mm});
            skLineSegment(sketch, "E3339", {"start": v(15, 41.68) * mm, "end": v(14.87, 41.55) * mm});
            skLineSegment(sketch, "E3340", {"start": v(14.87, 41.55) * mm, "end": v(14.75, 41.42) * mm});
            skLineSegment(sketch, "E3341", {"start": v(14.75, 41.42) * mm, "end": v(14.63, 41.3) * mm});
            skLineSegment(sketch, "E3342", {"start": v(14.63, 41.3) * mm, "end": v(14.5, 41.16) * mm});
            skLineSegment(sketch, "E3343", {"start": v(14.5, 41.16) * mm, "end": v(14.38, 41.02) * mm});
            skLineSegment(sketch, "E3344", {"start": v(14.38, 41.02) * mm, "end": v(14.25, 40.88) * mm});
            skLineSegment(sketch, "E3345", {"start": v(14.25, 40.88) * mm, "end": v(14.13, 40.73) * mm});
            skLineSegment(sketch, "E3346", {"start": v(14.13, 40.73) * mm, "end": v(14, 40.59) * mm});
            skLineSegment(sketch, "E3347", {"start": v(14, 40.59) * mm, "end": v(13.88, 40.44) * mm});
            skLineSegment(sketch, "E3348", {"start": v(13.88, 40.44) * mm, "end": v(13.77, 40.3) * mm});
            skLineSegment(sketch, "E3349", {"start": v(13.77, 40.3) * mm, "end": v(13.66, 40.15) * mm});
            skLineSegment(sketch, "E3350", {"start": v(13.66, 40.15) * mm, "end": v(13.54, 40) * mm});
            skLineSegment(sketch, "E3351", {"start": v(13.54, 40) * mm, "end": v(13.43, 39.85) * mm});
            skLineSegment(sketch, "E3352", {"start": v(13.43, 39.85) * mm, "end": v(13.33, 39.7) * mm});
            skLineSegment(sketch, "E3353", {"start": v(13.33, 39.7) * mm, "end": v(13.22, 39.55) * mm});
            skLineSegment(sketch, "E3354", {"start": v(13.22, 39.55) * mm, "end": v(13.12, 39.4) * mm});
            skLineSegment(sketch, "E3355", {"start": v(13.12, 39.4) * mm, "end": v(13.01, 39.23) * mm});
            skLineSegment(sketch, "E3356", {"start": v(13.01, 39.23) * mm, "end": v(12.97, 39.16) * mm});
            skLineSegment(sketch, "E3357", {"start": v(12.97, 39.16) * mm, "end": v(12.8, 39.22) * mm});
            skLineSegment(sketch, "E3358", {"start": v(12.8, 39.22) * mm, "end": v(12.6, 39.28) * mm});
            skLineSegment(sketch, "E3359", {"start": v(12.6, 39.28) * mm, "end": v(12.42, 39.34) * mm});
            skLineSegment(sketch, "E3360", {"start": v(12.42, 39.34) * mm, "end": v(12.23, 39.4) * mm});
            skLineSegment(sketch, "E3361", {"start": v(12.23, 39.4) * mm, "end": v(12.05, 39.45) * mm});
            skLineSegment(sketch, "E3362", {"start": v(12.05, 39.45) * mm, "end": v(11.86, 39.51) * mm});
            skLineSegment(sketch, "E3363", {"start": v(11.86, 39.51) * mm, "end": v(11.68, 39.57) * mm});
            skLineSegment(sketch, "E3364", {"start": v(11.68, 39.57) * mm, "end": v(11.65, 39.58) * mm});
            skLineSegment(sketch, "E3365", {"start": v(11.65, 39.58) * mm, "end": v(11.66, 39.75) * mm});
            skLineSegment(sketch, "E3366", {"start": v(11.66, 39.75) * mm, "end": v(11.67, 39.93) * mm});
            skLineSegment(sketch, "E3367", {"start": v(11.67, 39.93) * mm, "end": v(11.67, 40.1) * mm});
            skLineSegment(sketch, "E3368", {"start": v(11.67, 40.1) * mm, "end": v(11.67, 40.3) * mm});
            skLineSegment(sketch, "E3369", {"start": v(11.67, 40.3) * mm, "end": v(11.66, 40.46) * mm});
            skLineSegment(sketch, "E3370", {"start": v(11.66, 40.46) * mm, "end": v(11.66, 40.64) * mm});
            skLineSegment(sketch, "E3371", {"start": v(11.66, 40.64) * mm, "end": v(11.65, 40.83) * mm});
            skLineSegment(sketch, "E3372", {"start": v(11.65, 40.83) * mm, "end": v(11.64, 41) * mm});
            skLineSegment(sketch, "E3373", {"start": v(11.64, 41) * mm, "end": v(11.63, 41.18) * mm});
            skLineSegment(sketch, "E3374", {"start": v(11.63, 41.18) * mm, "end": v(11.61, 41.36) * mm});
            skLineSegment(sketch, "E3375", {"start": v(11.61, 41.36) * mm, "end": v(11.6, 41.55) * mm});
            skLineSegment(sketch, "E3376", {"start": v(11.6, 41.55) * mm, "end": v(11.58, 41.74) * mm});
            skLineSegment(sketch, "E3377", {"start": v(11.58, 41.74) * mm, "end": v(11.56, 41.91) * mm});
            skLineSegment(sketch, "E3378", {"start": v(11.56, 41.91) * mm, "end": v(11.53, 42.09) * mm});
            skLineSegment(sketch, "E3379", {"start": v(11.53, 42.09) * mm, "end": v(11.5, 42.27) * mm});
            skLineSegment(sketch, "E3380", {"start": v(11.5, 42.27) * mm, "end": v(11.48, 42.45) * mm});
            skLineSegment(sketch, "E3381", {"start": v(11.48, 42.45) * mm, "end": v(11.45, 42.64) * mm});
            skLineSegment(sketch, "E3382", {"start": v(11.45, 42.64) * mm, "end": v(11.42, 42.83) * mm});
            skLineSegment(sketch, "E3383", {"start": v(11.42, 42.83) * mm, "end": v(11.38, 43.02) * mm});
            skLineSegment(sketch, "E3384", {"start": v(11.38, 43.02) * mm, "end": v(11.35, 43.16) * mm});
            skLineSegment(sketch, "E3385", {"start": v(11.35, 43.16) * mm, "end": v(11.18, 43.2) * mm});
            skLineSegment(sketch, "E3386", {"start": v(11.18, 43.2) * mm, "end": v(11, 43.25) * mm});
            skLineSegment(sketch, "E3387", {"start": v(11, 43.25) * mm, "end": v(10.82, 43.3) * mm});
            skLineSegment(sketch, "E3388", {"start": v(10.82, 43.3) * mm, "end": v(10.64, 43.34) * mm});
            skLineSegment(sketch, "E3389", {"start": v(10.64, 43.34) * mm, "end": v(10.55, 43.36) * mm});
            skLineSegment(sketch, "E3390", {"start": v(10.55, 43.36) * mm, "end": v(10.43, 43.21) * mm});
            skLineSegment(sketch, "E3391", {"start": v(10.43, 43.21) * mm, "end": v(10.32, 43.07) * mm});
            skLineSegment(sketch, "E3392", {"start": v(10.32, 43.07) * mm, "end": v(10.2, 42.93) * mm});
            skLineSegment(sketch, "E3393", {"start": v(10.2, 42.93) * mm, "end": v(10.1, 42.8) * mm});
            skLineSegment(sketch, "E3394", {"start": v(10.1, 42.8) * mm, "end": v(10, 42.66) * mm});
            skLineSegment(sketch, "E3395", {"start": v(10, 42.66) * mm, "end": v(9.89, 42.5) * mm});
            skLineSegment(sketch, "E3396", {"start": v(9.89, 42.5) * mm, "end": v(9.78, 42.35) * mm});
            skLineSegment(sketch, "E3397", {"start": v(9.78, 42.35) * mm, "end": v(9.67, 42.2) * mm});
            skLineSegment(sketch, "E3398", {"start": v(9.67, 42.2) * mm, "end": v(9.56, 42.04) * mm});
            skLineSegment(sketch, "E3399", {"start": v(9.56, 42.04) * mm, "end": v(9.45, 41.88) * mm});
            skLineSegment(sketch, "E3400", {"start": v(9.45, 41.88) * mm, "end": v(9.35, 41.72) * mm});
            skLineSegment(sketch, "E3401", {"start": v(9.35, 41.72) * mm, "end": v(9.25, 41.57) * mm});
            skLineSegment(sketch, "E3402", {"start": v(9.25, 41.57) * mm, "end": v(9.16, 41.41) * mm});
            skLineSegment(sketch, "E3403", {"start": v(9.16, 41.41) * mm, "end": v(9.06, 41.25) * mm});
            skLineSegment(sketch, "E3404", {"start": v(9.06, 41.25) * mm, "end": v(8.97, 41.09) * mm});
            skLineSegment(sketch, "E3405", {"start": v(8.97, 41.09) * mm, "end": v(8.88, 40.93) * mm});
            skLineSegment(sketch, "E3406", {"start": v(8.88, 40.93) * mm, "end": v(8.8, 40.77) * mm});
            skLineSegment(sketch, "E3407", {"start": v(8.8, 40.77) * mm, "end": v(8.7, 40.6) * mm});
            skLineSegment(sketch, "E3408", {"start": v(8.7, 40.6) * mm, "end": v(8.62, 40.42) * mm});
            skLineSegment(sketch, "E3409", {"start": v(8.62, 40.42) * mm, "end": v(8.58, 40.35) * mm});
            skLineSegment(sketch, "E3410", {"start": v(8.58, 40.35) * mm, "end": v(8.4, 40.39) * mm});
            skLineSegment(sketch, "E3411", {"start": v(8.4, 40.39) * mm, "end": v(8.2, 40.43) * mm});
            skLineSegment(sketch, "E3412", {"start": v(8.2, 40.43) * mm, "end": v(8.02, 40.47) * mm});
            skLineSegment(sketch, "E3413", {"start": v(8.02, 40.47) * mm, "end": v(7.83, 40.5) * mm});
            skLineSegment(sketch, "E3414", {"start": v(7.83, 40.5) * mm, "end": v(7.64, 40.54) * mm});
            skLineSegment(sketch, "E3415", {"start": v(7.64, 40.54) * mm, "end": v(7.45, 40.58) * mm});
            skLineSegment(sketch, "E3416", {"start": v(7.45, 40.58) * mm, "end": v(7.26, 40.61) * mm});
            skLineSegment(sketch, "E3417", {"start": v(7.26, 40.61) * mm, "end": v(7.23, 40.62) * mm});
            skLineSegment(sketch, "E3418", {"start": v(7.23, 40.62) * mm, "end": v(7.22, 40.8) * mm});
            skLineSegment(sketch, "E3419", {"start": v(7.22, 40.8) * mm, "end": v(7.2, 40.97) * mm});
            skLineSegment(sketch, "E3420", {"start": v(7.2, 40.97) * mm, "end": v(7.19, 41.15) * mm});
            skLineSegment(sketch, "E3421", {"start": v(7.19, 41.15) * mm, "end": v(7.17, 41.33) * mm});
            skLineSegment(sketch, "E3422", {"start": v(7.17, 41.33) * mm, "end": v(7.14, 41.5) * mm});
            skLineSegment(sketch, "E3423", {"start": v(7.14, 41.5) * mm, "end": v(7.12, 41.68) * mm});
            skLineSegment(sketch, "E3424", {"start": v(7.12, 41.68) * mm, "end": v(7.09, 41.86) * mm});
            skLineSegment(sketch, "E3425", {"start": v(7.09, 41.86) * mm, "end": v(7.06, 42.03) * mm});
            skLineSegment(sketch, "E3426", {"start": v(7.06, 42.03) * mm, "end": v(7.03, 42.2) * mm});
            skLineSegment(sketch, "E3427", {"start": v(7.03, 42.2) * mm, "end": v(7, 42.39) * mm});
            skLineSegment(sketch, "E3428", {"start": v(7, 42.39) * mm, "end": v(6.96, 42.57) * mm});
            skLineSegment(sketch, "E3429", {"start": v(6.96, 42.57) * mm, "end": v(6.91, 42.76) * mm});
            skLineSegment(sketch, "E3430", {"start": v(6.91, 42.76) * mm, "end": v(6.87, 42.93) * mm});
            skLineSegment(sketch, "E3431", {"start": v(6.87, 42.93) * mm, "end": v(6.83, 43.1) * mm});
            skLineSegment(sketch, "E3432", {"start": v(6.83, 43.1) * mm, "end": v(6.79, 43.28) * mm});
            skLineSegment(sketch, "E3433", {"start": v(6.79, 43.28) * mm, "end": v(6.74, 43.45) * mm});
            skLineSegment(sketch, "E3434", {"start": v(6.74, 43.45) * mm, "end": v(6.7, 43.64) * mm});
            skLineSegment(sketch, "E3435", {"start": v(6.7, 43.64) * mm, "end": v(6.64, 43.82) * mm});
            skLineSegment(sketch, "E3436", {"start": v(6.64, 43.82) * mm, "end": v(6.58, 44.01) * mm});
            skLineSegment(sketch, "E3437", {"start": v(6.58, 44.01) * mm, "end": v(6.54, 44.15) * mm});
            skLineSegment(sketch, "E3438", {"start": v(6.54, 44.15) * mm, "end": v(6.36, 44.17) * mm});
            skLineSegment(sketch, "E3439", {"start": v(6.36, 44.17) * mm, "end": v(6.17, 44.2) * mm});
            skLineSegment(sketch, "E3440", {"start": v(6.17, 44.2) * mm, "end": v(5.99, 44.22) * mm});
            skLineSegment(sketch, "E3441", {"start": v(5.99, 44.22) * mm, "end": v(5.8, 44.25) * mm});
            skLineSegment(sketch, "E3442", {"start": v(5.8, 44.25) * mm, "end": v(5.72, 44.26) * mm});
            skLineSegment(sketch, "E3443", {"start": v(5.72, 44.26) * mm, "end": v(5.61, 44.1) * mm});
            skLineSegment(sketch, "E3444", {"start": v(5.61, 44.1) * mm, "end": v(5.52, 43.95) * mm});
            skLineSegment(sketch, "E3445", {"start": v(5.52, 43.95) * mm, "end": v(5.42, 43.8) * mm});
            skLineSegment(sketch, "E3446", {"start": v(5.42, 43.8) * mm, "end": v(5.33, 43.64) * mm});
            skLineSegment(sketch, "E3447", {"start": v(5.33, 43.64) * mm, "end": v(5.25, 43.5) * mm});
            skLineSegment(sketch, "E3448", {"start": v(5.25, 43.5) * mm, "end": v(5.15, 43.33) * mm});
            skLineSegment(sketch, "E3449", {"start": v(5.15, 43.33) * mm, "end": v(5.06, 43.17) * mm});
            skLineSegment(sketch, "E3450", {"start": v(5.06, 43.17) * mm, "end": v(4.97, 43) * mm});
            skLineSegment(sketch, "E3451", {"start": v(4.97, 43) * mm, "end": v(4.88, 42.84) * mm});
            skLineSegment(sketch, "E3452", {"start": v(4.88, 42.84) * mm, "end": v(4.79, 42.67) * mm});
            skLineSegment(sketch, "E3453", {"start": v(4.79, 42.67) * mm, "end": v(4.7, 42.5) * mm});
            skLineSegment(sketch, "E3454", {"start": v(4.7, 42.5) * mm, "end": v(4.62, 42.33) * mm});
            skLineSegment(sketch, "E3455", {"start": v(4.62, 42.33) * mm, "end": v(4.55, 42.17) * mm});
            skLineSegment(sketch, "E3456", {"start": v(4.55, 42.17) * mm, "end": v(4.47, 42) * mm});
            skLineSegment(sketch, "E3457", {"start": v(4.47, 42) * mm, "end": v(4.4, 41.82) * mm});
            skLineSegment(sketch, "E3458", {"start": v(4.4, 41.82) * mm, "end": v(4.32, 41.66) * mm});
            skLineSegment(sketch, "E3459", {"start": v(4.32, 41.66) * mm, "end": v(4.25, 41.49) * mm});
            skLineSegment(sketch, "E3460", {"start": v(4.25, 41.49) * mm, "end": v(4.19, 41.3) * mm});
            skLineSegment(sketch, "E3461", {"start": v(4.19, 41.3) * mm, "end": v(4.12, 41.13) * mm});
            skLineSegment(sketch, "E3462", {"start": v(4.12, 41.13) * mm, "end": v(4.1, 41.05) * mm});
            skLineSegment(sketch, "E3463", {"start": v(4.1, 41.05) * mm, "end": v(3.9, 41.07) * mm});
            skLineSegment(sketch, "E3464", {"start": v(3.9, 41.07) * mm, "end": v(3.7, 41.09) * mm});
            skLineSegment(sketch, "E3465", {"start": v(3.7, 41.09) * mm, "end": v(3.52, 41.1) * mm});
            skLineSegment(sketch, "E3466", {"start": v(3.52, 41.1) * mm, "end": v(3.32, 41.12) * mm});
            skLineSegment(sketch, "E3467", {"start": v(3.32, 41.12) * mm, "end": v(3.14, 41.13) * mm});
            skLineSegment(sketch, "E3468", {"start": v(3.14, 41.13) * mm, "end": v(2.94, 41.15) * mm});
            skLineSegment(sketch, "E3469", {"start": v(2.94, 41.15) * mm, "end": v(2.75, 41.17) * mm});
            skLineSegment(sketch, "E3470", {"start": v(2.75, 41.17) * mm, "end": v(2.72, 41.17) * mm});
            skLineSegment(sketch, "E3471", {"start": v(2.72, 41.17) * mm, "end": v(2.69, 41.34) * mm});
            skLineSegment(sketch, "E3472", {"start": v(2.69, 41.34) * mm, "end": v(2.65, 41.52) * mm});
            skLineSegment(sketch, "E3473", {"start": v(2.65, 41.52) * mm, "end": v(2.62, 41.69) * mm});
            skLineSegment(sketch, "E3474", {"start": v(2.62, 41.69) * mm, "end": v(2.58, 41.87) * mm});
            skLineSegment(sketch, "E3475", {"start": v(2.58, 41.87) * mm, "end": v(2.53, 42.03) * mm});
            skLineSegment(sketch, "E3476", {"start": v(2.53, 42.03) * mm, "end": v(2.5, 42.2) * mm});
            skLineSegment(sketch, "E3477", {"start": v(2.5, 42.2) * mm, "end": v(2.44, 42.4) * mm});
            skLineSegment(sketch, "E3478", {"start": v(2.44, 42.4) * mm, "end": v(2.4, 42.55) * mm});
            skLineSegment(sketch, "E3479", {"start": v(2.4, 42.55) * mm, "end": v(2.34, 42.72) * mm});
            skLineSegment(sketch, "E3480", {"start": v(2.34, 42.72) * mm, "end": v(2.29, 42.9) * mm});
            skLineSegment(sketch, "E3481", {"start": v(2.29, 42.9) * mm, "end": v(2.23, 43.08) * mm});
            skLineSegment(sketch, "E3482", {"start": v(2.23, 43.08) * mm, "end": v(2.17, 43.26) * mm});
            skLineSegment(sketch, "E3483", {"start": v(2.17, 43.26) * mm, "end": v(2.11, 43.43) * mm});
            skLineSegment(sketch, "E3484", {"start": v(2.11, 43.43) * mm, "end": v(2.05, 43.6) * mm});
            skLineSegment(sketch, "E3485", {"start": v(2.05, 43.6) * mm, "end": v(1.99, 43.76) * mm});
            skLineSegment(sketch, "E3486", {"start": v(1.99, 43.76) * mm, "end": v(1.92, 43.93) * mm});
            skLineSegment(sketch, "E3487", {"start": v(1.92, 43.93) * mm, "end": v(1.85, 44.1) * mm});
            skLineSegment(sketch, "E3488", {"start": v(1.85, 44.1) * mm, "end": v(1.78, 44.29) * mm});
            skLineSegment(sketch, "E3489", {"start": v(1.78, 44.29) * mm, "end": v(1.7, 44.47) * mm});
            skLineSegment(sketch, "E3490", {"start": v(1.7, 44.47) * mm, "end": v(1.64, 44.6) * mm});
            skLineSegment(sketch, "E3491", {"start": v(1.64, 44.6) * mm, "end": v(1.46, 44.6) * mm});
            skLineSegment(sketch, "E3492", {"start": v(1.46, 44.6) * mm, "end": v(1.27, 44.61) * mm});
            skLineSegment(sketch, "E3493", {"start": v(1.27, 44.61) * mm, "end": v(1.09, 44.62) * mm});
            skLineSegment(sketch, "E3494", {"start": v(1.09, 44.62) * mm, "end": v(0.9, 44.62) * mm});
            skLineSegment(sketch, "E3495", {"start": v(0.9, 44.62) * mm, "end": v(0.81, 44.62) * mm});
            skLineSegment(sketch, "E3496", {"start": v(0.81, 44.62) * mm, "end": v(0.73, 44.45) * mm});
            skLineSegment(sketch, "E3497", {"start": v(0.73, 44.45) * mm, "end": v(0.65, 44.29) * mm});
            skLineSegment(sketch, "E3498", {"start": v(0.65, 44.29) * mm, "end": v(0.57, 44.13) * mm});
            skLineSegment(sketch, "E3499", {"start": v(0.57, 44.13) * mm, "end": v(0.5, 43.97) * mm});
            skLineSegment(sketch, "E3500", {"start": v(0.5, 43.97) * mm, "end": v(0.43, 43.81) * mm});
            skLineSegment(sketch, "E3501", {"start": v(0.43, 43.81) * mm, "end": v(0.35, 43.64) * mm});
            skLineSegment(sketch, "E3502", {"start": v(0.35, 43.64) * mm, "end": v(0.28, 43.47) * mm});
            skLineSegment(sketch, "E3503", {"start": v(0.28, 43.47) * mm, "end": v(0.2, 43.29) * mm});
            skLineSegment(sketch, "E3504", {"start": v(0.2, 43.29) * mm, "end": v(0.14, 43.11) * mm});
            skLineSegment(sketch, "E3505", {"start": v(0.14, 43.11) * mm, "end": v(0.07, 42.94) * mm});
            skLineSegment(sketch, "E3506", {"start": v(0.07, 42.94) * mm, "end": v(0, 42.76) * mm});
            skLineSegment(sketch, "E3507", {"start": v(0, 42.76) * mm, "end": v(-0.06, 42.58) * mm});
            skLineSegment(sketch, "E3508", {"start": v(-0.06, 42.58) * mm, "end": v(-0.12, 42.41) * mm});
            skLineSegment(sketch, "E3509", {"start": v(-0.12, 42.41) * mm, "end": v(-0.18, 42.23) * mm});
            skLineSegment(sketch, "E3510", {"start": v(-0.18, 42.23) * mm, "end": v(-0.23, 42.05) * mm});
            skLineSegment(sketch, "E3511", {"start": v(-0.23, 42.05) * mm, "end": v(-0.28, 41.88) * mm});
            skLineSegment(sketch, "E3512", {"start": v(-0.28, 41.88) * mm, "end": v(-0.33, 41.7) * mm});
            skLineSegment(sketch, "E3513", {"start": v(-0.33, 41.7) * mm, "end": v(-0.38, 41.52) * mm});
            skLineSegment(sketch, "E3514", {"start": v(-0.38, 41.52) * mm, "end": v(-0.43, 41.33) * mm});
            skLineSegment(sketch, "E3515", {"start": v(-0.43, 41.33) * mm, "end": v(-0.45, 41.25) * mm});
            skLineSegment(sketch, "E3516", {"start": v(-0.45, 41.25) * mm, "end": v(-0.64, 41.25) * mm});
            skLineSegment(sketch, "E3517", {"start": v(-0.64, 41.25) * mm, "end": v(-0.83, 41.24) * mm});
            skLineSegment(sketch, "E3518", {"start": v(-0.83, 41.24) * mm, "end": v(-1.02, 41.24) * mm});
            skLineSegment(sketch, "E3519", {"start": v(-1.02, 41.24) * mm, "end": v(-1.22, 41.24) * mm});
            skLineSegment(sketch, "E3520", {"start": v(-1.22, 41.24) * mm, "end": v(-1.4, 41.23) * mm});
            skLineSegment(sketch, "E3521", {"start": v(-1.4, 41.23) * mm, "end": v(-1.6, 41.22) * mm});
            skLineSegment(sketch, "E3522", {"start": v(-1.6, 41.22) * mm, "end": v(-1.77, 41.22) * mm});
            skLineSegment(sketch, "E3523", {"start": v(-1.77, 41.22) * mm, "end": v(-1.83, 41.22) * mm});
            skLineSegment(sketch, "E3524", {"start": v(-1.83, 41.22) * mm, "end": v(-1.88, 41.38) * mm});
            skLineSegment(sketch, "E3525", {"start": v(-1.88, 41.38) * mm, "end": v(-1.93, 41.56) * mm});
            skLineSegment(sketch, "E3526", {"start": v(-1.93, 41.56) * mm, "end": v(-1.99, 41.72) * mm});
            skLineSegment(sketch, "E3527", {"start": v(-1.99, 41.72) * mm, "end": v(-2.05, 41.9) * mm});
            skLineSegment(sketch, "E3528", {"start": v(-2.05, 41.9) * mm, "end": v(-2.1, 42.06) * mm});
            skLineSegment(sketch, "E3529", {"start": v(-2.1, 42.06) * mm, "end": v(-2.17, 42.23) * mm});
            skLineSegment(sketch, "E3530", {"start": v(-2.17, 42.23) * mm, "end": v(-2.24, 42.4) * mm});
            skLineSegment(sketch, "E3531", {"start": v(-2.24, 42.4) * mm, "end": v(-2.3, 42.56) * mm});
            skLineSegment(sketch, "E3532", {"start": v(-2.3, 42.56) * mm, "end": v(-2.37, 42.72) * mm});
            skLineSegment(sketch, "E3533", {"start": v(-2.37, 42.72) * mm, "end": v(-2.44, 42.9) * mm});
            skLineSegment(sketch, "E3534", {"start": v(-2.44, 42.9) * mm, "end": v(-2.52, 43.06) * mm});
            skLineSegment(sketch, "E3535", {"start": v(-2.52, 43.06) * mm, "end": v(-2.6, 43.24) * mm});
            skLineSegment(sketch, "E3536", {"start": v(-2.6, 43.24) * mm, "end": v(-2.68, 43.4) * mm});
            skLineSegment(sketch, "E3537", {"start": v(-2.68, 43.4) * mm, "end": v(-2.76, 43.55) * mm});
            skLineSegment(sketch, "E3538", {"start": v(-2.76, 43.55) * mm, "end": v(-2.84, 43.71) * mm});
            skLineSegment(sketch, "E3539", {"start": v(-2.84, 43.71) * mm, "end": v(-2.92, 43.88) * mm});
            skLineSegment(sketch, "E3540", {"start": v(-2.92, 43.88) * mm, "end": v(-3.01, 44.04) * mm});
            skLineSegment(sketch, "E3541", {"start": v(-3.01, 44.04) * mm, "end": v(-3.1, 44.21) * mm});
            skLineSegment(sketch, "E3542", {"start": v(-3.1, 44.21) * mm, "end": v(-3.2, 44.39) * mm});
            skLineSegment(sketch, "E3543", {"start": v(-3.2, 44.39) * mm, "end": v(-3.27, 44.5) * mm});
            skLineSegment(sketch, "E3544", {"start": v(-3.27, 44.5) * mm, "end": v(-3.46, 44.5) * mm});
            skLineSegment(sketch, "E3545", {"start": v(-3.46, 44.5) * mm, "end": v(-3.64, 44.48) * mm});
            skLineSegment(sketch, "E3546", {"start": v(-3.64, 44.48) * mm, "end": v(-3.83, 44.46) * mm});
            skLineSegment(sketch, "E3547", {"start": v(-3.83, 44.46) * mm, "end": v(-4, 44.45) * mm});
            skLineSegment(sketch, "E3548", {"start": v(-4, 44.45) * mm, "end": v(-4.1, 44.44) * mm});
            skLineSegment(sketch, "E3549", {"start": v(-4.1, 44.44) * mm, "end": v(-4.16, 44.26) * mm});
            skLineSegment(sketch, "E3550", {"start": v(-4.16, 44.26) * mm, "end": v(-4.23, 44.09) * mm});
            skLineSegment(sketch, "E3551", {"start": v(-4.23, 44.09) * mm, "end": v(-4.28, 43.92) * mm});
            skLineSegment(sketch, "E3552", {"start": v(-4.28, 43.92) * mm, "end": v(-4.34, 43.75) * mm});
            skLineSegment(sketch, "E3553", {"start": v(-4.34, 43.75) * mm, "end": v(-4.4, 43.6) * mm});
            skLineSegment(sketch, "E3554", {"start": v(-4.4, 43.6) * mm, "end": v(-4.45, 43.41) * mm});
            skLineSegment(sketch, "E3555", {"start": v(-4.45, 43.41) * mm, "end": v(-4.5, 43.23) * mm});
            skLineSegment(sketch, "E3556", {"start": v(-4.5, 43.23) * mm, "end": v(-4.56, 43.05) * mm});
            skLineSegment(sketch, "E3557", {"start": v(-4.56, 43.05) * mm, "end": v(-4.6, 42.87) * mm});
            skLineSegment(sketch, "E3558", {"start": v(-4.6, 42.87) * mm, "end": v(-4.66, 42.68) * mm});
            skLineSegment(sketch, "E3559", {"start": v(-4.66, 42.68) * mm, "end": v(-4.7, 42.5) * mm});
            skLineSegment(sketch, "E3560", {"start": v(-4.7, 42.5) * mm, "end": v(-4.75, 42.32) * mm});
            skLineSegment(sketch, "E3561", {"start": v(-4.75, 42.32) * mm, "end": v(-4.78, 42.14) * mm});
            skLineSegment(sketch, "E3562", {"start": v(-4.78, 42.14) * mm, "end": v(-4.82, 41.95) * mm});
            skLineSegment(sketch, "E3563", {"start": v(-4.82, 41.95) * mm, "end": v(-4.86, 41.77) * mm});
            skLineSegment(sketch, "E3564", {"start": v(-4.86, 41.77) * mm, "end": v(-4.9, 41.6) * mm});
            skLineSegment(sketch, "E3565", {"start": v(-4.9, 41.6) * mm, "end": v(-4.92, 41.41) * mm});
            skLineSegment(sketch, "E3566", {"start": v(-4.92, 41.41) * mm, "end": v(-4.95, 41.23) * mm});
            skLineSegment(sketch, "E3567", {"start": v(-4.95, 41.23) * mm, "end": v(-4.97, 41.03) * mm});
            skLineSegment(sketch, "E3568", {"start": v(-4.97, 41.03) * mm, "end": v(-4.98, 40.95) * mm});
            skLineSegment(sketch, "E3569", {"start": v(-4.98, 40.95) * mm, "end": v(-5.17, 40.93) * mm});
            skLineSegment(sketch, "E3570", {"start": v(-5.17, 40.93) * mm, "end": v(-5.37, 40.9) * mm});
            skLineSegment(sketch, "E3571", {"start": v(-5.37, 40.9) * mm, "end": v(-5.55, 40.88) * mm});
            skLineSegment(sketch, "E3572", {"start": v(-5.55, 40.88) * mm, "end": v(-5.75, 40.85) * mm});
            skLineSegment(sketch, "E3573", {"start": v(-5.75, 40.85) * mm, "end": v(-5.94, 40.82) * mm});
            skLineSegment(sketch, "E3574", {"start": v(-5.94, 40.82) * mm, "end": v(-6.13, 40.8) * mm});
            skLineSegment(sketch, "E3575", {"start": v(-6.13, 40.8) * mm, "end": v(-6.32, 40.77) * mm});
            skLineSegment(sketch, "E3576", {"start": v(-6.32, 40.77) * mm, "end": v(-6.35, 40.77) * mm});
            skLineSegment(sketch, "E3577", {"start": v(-6.35, 40.77) * mm, "end": v(-6.42, 40.92) * mm});
            skLineSegment(sketch, "E3578", {"start": v(-6.42, 40.92) * mm, "end": v(-6.5, 41.1) * mm});
            skLineSegment(sketch, "E3579", {"start": v(-6.5, 41.1) * mm, "end": v(-6.56, 41.25) * mm});
            skLineSegment(sketch, "E3580", {"start": v(-6.56, 41.25) * mm, "end": v(-6.64, 41.42) * mm});
            skLineSegment(sketch, "E3581", {"start": v(-6.64, 41.42) * mm, "end": v(-6.72, 41.57) * mm});
            skLineSegment(sketch, "E3582", {"start": v(-6.72, 41.57) * mm, "end": v(-6.8, 41.73) * mm});
            skLineSegment(sketch, "E3583", {"start": v(-6.8, 41.73) * mm, "end": v(-6.89, 41.9) * mm});
            skLineSegment(sketch, "E3584", {"start": v(-6.89, 41.9) * mm, "end": v(-6.97, 42.05) * mm});
            skLineSegment(sketch, "E3585", {"start": v(-6.97, 42.05) * mm, "end": v(-7.06, 42.2) * mm});
            skLineSegment(sketch, "E3586", {"start": v(-7.06, 42.2) * mm, "end": v(-7.15, 42.36) * mm});
            skLineSegment(sketch, "E3587", {"start": v(-7.15, 42.36) * mm, "end": v(-7.24, 42.52) * mm});
            skLineSegment(sketch, "E3588", {"start": v(-7.24, 42.52) * mm, "end": v(-7.34, 42.7) * mm});
            skLineSegment(sketch, "E3589", {"start": v(-7.34, 42.7) * mm, "end": v(-7.44, 42.84) * mm});
            skLineSegment(sketch, "E3590", {"start": v(-7.44, 42.84) * mm, "end": v(-7.53, 42.98) * mm});
            skLineSegment(sketch, "E3591", {"start": v(-7.53, 42.98) * mm, "end": v(-7.63, 43.14) * mm});
            skLineSegment(sketch, "E3592", {"start": v(-7.63, 43.14) * mm, "end": v(-7.73, 43.29) * mm});
            skLineSegment(sketch, "E3593", {"start": v(-7.73, 43.29) * mm, "end": v(-7.84, 43.45) * mm});
            skLineSegment(sketch, "E3594", {"start": v(-7.84, 43.45) * mm, "end": v(-7.95, 43.6) * mm});
            skLineSegment(sketch, "E3595", {"start": v(-7.95, 43.6) * mm, "end": v(-8.07, 43.77) * mm});
            skLineSegment(sketch, "E3596", {"start": v(-8.07, 43.77) * mm, "end": v(-8.15, 43.88) * mm});
            skLineSegment(sketch, "E3597", {"start": v(-8.15, 43.88) * mm, "end": v(-8.33, 43.84) * mm});
            skLineSegment(sketch, "E3598", {"start": v(-8.33, 43.84) * mm, "end": v(-8.51, 43.8) * mm});
            skLineSegment(sketch, "E3599", {"start": v(-8.51, 43.8) * mm, "end": v(-8.7, 43.77) * mm});
            skLineSegment(sketch, "E3600", {"start": v(-8.7, 43.77) * mm, "end": v(-8.87, 43.74) * mm});
            skLineSegment(sketch, "E3601", {"start": v(-8.87, 43.74) * mm, "end": v(-8.96, 43.72) * mm});
            skLineSegment(sketch, "E3602", {"start": v(-8.96, 43.72) * mm, "end": v(-9, 43.53) * mm});
            skLineSegment(sketch, "E3603", {"start": v(-9, 43.53) * mm, "end": v(-9.05, 43.36) * mm});
            skLineSegment(sketch, "E3604", {"start": v(-9.05, 43.36) * mm, "end": v(-9.09, 43.18) * mm});
            skLineSegment(sketch, "E3605", {"start": v(-9.09, 43.18) * mm, "end": v(-9.13, 43.01) * mm});
            skLineSegment(sketch, "E3606", {"start": v(-9.13, 43.01) * mm, "end": v(-9.16, 42.84) * mm});
            skLineSegment(sketch, "E3607", {"start": v(-9.16, 42.84) * mm, "end": v(-9.2, 42.66) * mm});
            skLineSegment(sketch, "E3608", {"start": v(-9.2, 42.66) * mm, "end": v(-9.23, 42.47) * mm});
            skLineSegment(sketch, "E3609", {"start": v(-9.23, 42.47) * mm, "end": v(-9.27, 42.29) * mm});
            skLineSegment(sketch, "E3610", {"start": v(-9.27, 42.29) * mm, "end": v(-9.3, 42.1) * mm});
            skLineSegment(sketch, "E3611", {"start": v(-9.3, 42.1) * mm, "end": v(-9.32, 41.91) * mm});
            skLineSegment(sketch, "E3612", {"start": v(-9.32, 41.91) * mm, "end": v(-9.35, 41.73) * mm});
            skLineSegment(sketch, "E3613", {"start": v(-9.35, 41.73) * mm, "end": v(-9.37, 41.54) * mm});
            skLineSegment(sketch, "E3614", {"start": v(-9.37, 41.54) * mm, "end": v(-9.4, 41.36) * mm});
            skLineSegment(sketch, "E3615", {"start": v(-9.4, 41.36) * mm, "end": v(-9.4, 41.17) * mm});
            skLineSegment(sketch, "E3616", {"start": v(-9.4, 41.17) * mm, "end": v(-9.42, 40.98) * mm});
            skLineSegment(sketch, "E3617", {"start": v(-9.42, 40.98) * mm, "end": v(-9.44, 40.8) * mm});
            skLineSegment(sketch, "E3618", {"start": v(-9.44, 40.8) * mm, "end": v(-9.45, 40.62) * mm});
            skLineSegment(sketch, "E3619", {"start": v(-9.45, 40.62) * mm, "end": v(-9.45, 40.43) * mm});
            skLineSegment(sketch, "E3620", {"start": v(-9.45, 40.43) * mm, "end": v(-9.46, 40.24) * mm});
            skLineSegment(sketch, "E3621", {"start": v(-9.46, 40.24) * mm, "end": v(-9.46, 40.16) * mm});
            skLineSegment(sketch, "E3622", {"start": v(-9.46, 40.16) * mm, "end": v(-9.64, 40.11) * mm});
            skLineSegment(sketch, "E3623", {"start": v(-9.64, 40.11) * mm, "end": v(-9.83, 40.06) * mm});
            skLineSegment(sketch, "E3624", {"start": v(-9.83, 40.06) * mm, "end": v(-10.02, 40.02) * mm});
            skLineSegment(sketch, "E3625", {"start": v(-10.02, 40.02) * mm, "end": v(-10.2, 39.97) * mm});
            skLineSegment(sketch, "E3626", {"start": v(-10.2, 39.97) * mm, "end": v(-10.39, 39.92) * mm});
            skLineSegment(sketch, "E3627", {"start": v(-10.39, 39.92) * mm, "end": v(-10.58, 39.87) * mm});
            skLineSegment(sketch, "E3628", {"start": v(-10.58, 39.87) * mm, "end": v(-10.77, 39.83) * mm});
            skLineSegment(sketch, "E3629", {"start": v(-10.77, 39.83) * mm, "end": v(-10.8, 39.82) * mm});
            skLineSegment(sketch, "E3630", {"start": v(-10.8, 39.82) * mm, "end": v(-10.88, 39.97) * mm});
            skLineSegment(sketch, "E3631", {"start": v(-10.88, 39.97) * mm, "end": v(-10.97, 40.13) * mm});
            skLineSegment(sketch, "E3632", {"start": v(-10.97, 40.13) * mm, "end": v(-11.06, 40.28) * mm});
            skLineSegment(sketch, "E3633", {"start": v(-11.06, 40.28) * mm, "end": v(-11.16, 40.44) * mm});
            skLineSegment(sketch, "E3634", {"start": v(-11.16, 40.44) * mm, "end": v(-11.25, 40.58) * mm});
            skLineSegment(sketch, "E3635", {"start": v(-11.25, 40.58) * mm, "end": v(-11.35, 40.73) * mm});
            skLineSegment(sketch, "E3636", {"start": v(-11.35, 40.73) * mm, "end": v(-11.45, 40.89) * mm});
            skLineSegment(sketch, "E3637", {"start": v(-11.45, 40.89) * mm, "end": v(-11.55, 41.03) * mm});
            skLineSegment(sketch, "E3638", {"start": v(-11.55, 41.03) * mm, "end": v(-11.66, 41.17) * mm});
            skLineSegment(sketch, "E3639", {"start": v(-11.66, 41.17) * mm, "end": v(-11.76, 41.32) * mm});
            skLineSegment(sketch, "E3640", {"start": v(-11.76, 41.32) * mm, "end": v(-11.88, 41.47) * mm});
            skLineSegment(sketch, "E3641", {"start": v(-11.88, 41.47) * mm, "end": v(-12, 41.62) * mm});
            skLineSegment(sketch, "E3642", {"start": v(-12, 41.62) * mm, "end": v(-12.1, 41.76) * mm});
            skLineSegment(sketch, "E3643", {"start": v(-12.1, 41.76) * mm, "end": v(-12.21, 41.9) * mm});
            skLineSegment(sketch, "E3644", {"start": v(-12.21, 41.9) * mm, "end": v(-12.33, 42.03) * mm});
            skLineSegment(sketch, "E3645", {"start": v(-12.33, 42.03) * mm, "end": v(-12.45, 42.18) * mm});
            skLineSegment(sketch, "E3646", {"start": v(-12.45, 42.18) * mm, "end": v(-12.57, 42.32) * mm});
            skLineSegment(sketch, "E3647", {"start": v(-12.57, 42.32) * mm, "end": v(-12.7, 42.46) * mm});
            skLineSegment(sketch, "E3648", {"start": v(-12.7, 42.46) * mm, "end": v(-12.83, 42.61) * mm});
            skLineSegment(sketch, "E3649", {"start": v(-12.83, 42.61) * mm, "end": v(-12.93, 42.72) * mm});
            skLineSegment(sketch, "E3650", {"start": v(-12.93, 42.72) * mm, "end": v(-13.1, 42.66) * mm});
            skLineSegment(sketch, "E3651", {"start": v(-13.1, 42.66) * mm, "end": v(-13.28, 42.6) * mm});
            skLineSegment(sketch, "E3652", {"start": v(-13.28, 42.6) * mm, "end": v(-13.46, 42.55) * mm});
            skLineSegment(sketch, "E3653", {"start": v(-13.46, 42.55) * mm, "end": v(-13.63, 42.5) * mm});
            skLineSegment(sketch, "E3654", {"start": v(-13.63, 42.5) * mm, "end": v(-13.72, 42.47) * mm});
            skLineSegment(sketch, "E3655", {"start": v(-13.72, 42.47) * mm, "end": v(-13.74, 42.28) * mm});
            skLineSegment(sketch, "E3656", {"start": v(-13.74, 42.28) * mm, "end": v(-13.76, 42.1) * mm});
            skLineSegment(sketch, "E3657", {"start": v(-13.76, 42.1) * mm, "end": v(-13.78, 41.92) * mm});
            skLineSegment(sketch, "E3658", {"start": v(-13.78, 41.92) * mm, "end": v(-13.8, 41.75) * mm});
            skLineSegment(sketch, "E3659", {"start": v(-13.8, 41.75) * mm, "end": v(-13.82, 41.58) * mm});
            skLineSegment(sketch, "E3660", {"start": v(-13.82, 41.58) * mm, "end": v(-13.83, 41.39) * mm});
            skLineSegment(sketch, "E3661", {"start": v(-13.83, 41.39) * mm, "end": v(-13.85, 41.2) * mm});
            skLineSegment(sketch, "E3662", {"start": v(-13.85, 41.2) * mm, "end": v(-13.86, 41) * mm});
            skLineSegment(sketch, "E3663", {"start": v(-13.86, 41) * mm, "end": v(-13.87, 40.82) * mm});
            skLineSegment(sketch, "E3664", {"start": v(-13.87, 40.82) * mm, "end": v(-13.88, 40.63) * mm});
            skLineSegment(sketch, "E3665", {"start": v(-13.88, 40.63) * mm, "end": v(-13.88, 40.44) * mm});
            skLineSegment(sketch, "E3666", {"start": v(-13.88, 40.44) * mm, "end": v(-13.88, 40.26) * mm});
            skLineSegment(sketch, "E3667", {"start": v(-13.88, 40.26) * mm, "end": v(-13.88, 40.08) * mm});
            skLineSegment(sketch, "E3668", {"start": v(-13.88, 40.08) * mm, "end": v(-13.88, 39.88) * mm});
            skLineSegment(sketch, "E3669", {"start": v(-13.88, 39.88) * mm, "end": v(-13.88, 39.7) * mm});
            skLineSegment(sketch, "E3670", {"start": v(-13.88, 39.7) * mm, "end": v(-13.87, 39.52) * mm});
            skLineSegment(sketch, "E3671", {"start": v(-13.87, 39.52) * mm, "end": v(-13.86, 39.34) * mm});
            skLineSegment(sketch, "E3672", {"start": v(-13.86, 39.34) * mm, "end": v(-13.84, 39.15) * mm});
            skLineSegment(sketch, "E3673", {"start": v(-13.84, 39.15) * mm, "end": v(-13.82, 38.95) * mm});
            skLineSegment(sketch, "E3674", {"start": v(-13.82, 38.95) * mm, "end": v(-13.82, 38.87) * mm});
            skLineSegment(sketch, "E3675", {"start": v(-13.82, 38.87) * mm, "end": v(-14, 38.8) * mm});
            skLineSegment(sketch, "E3676", {"start": v(-14, 38.8) * mm, "end": v(-14.18, 38.74) * mm});
            skLineSegment(sketch, "E3677", {"start": v(-14.18, 38.74) * mm, "end": v(-14.36, 38.67) * mm});
            skLineSegment(sketch, "E3678", {"start": v(-14.36, 38.67) * mm, "end": v(-14.54, 38.6) * mm});
            skLineSegment(sketch, "E3679", {"start": v(-14.54, 38.6) * mm, "end": v(-14.72, 38.54) * mm});
            skLineSegment(sketch, "E3680", {"start": v(-14.72, 38.54) * mm, "end": v(-14.9, 38.47) * mm});
            skLineSegment(sketch, "E3681", {"start": v(-14.9, 38.47) * mm, "end": v(-15.08, 38.4) * mm});
            skLineSegment(sketch, "E3682", {"start": v(-15.08, 38.4) * mm, "end": v(-15.11, 38.4) * mm});
            skLineSegment(sketch, "E3683", {"start": v(-15.11, 38.4) * mm, "end": v(-15.21, 38.53) * mm});
            skLineSegment(sketch, "E3684", {"start": v(-15.21, 38.53) * mm, "end": v(-15.32, 38.68) * mm});
            skLineSegment(sketch, "E3685", {"start": v(-15.32, 38.68) * mm, "end": v(-15.42, 38.82) * mm});
            skLineSegment(sketch, "E3686", {"start": v(-15.42, 38.82) * mm, "end": v(-15.54, 38.96) * mm});
            skLineSegment(sketch, "E3687", {"start": v(-15.54, 38.96) * mm, "end": v(-15.65, 39.1) * mm});
            skLineSegment(sketch, "E3688", {"start": v(-15.65, 39.1) * mm, "end": v(-15.76, 39.24) * mm});
            skLineSegment(sketch, "E3689", {"start": v(-15.76, 39.24) * mm, "end": v(-15.88, 39.38) * mm});
            skLineSegment(sketch, "E3690", {"start": v(-15.88, 39.38) * mm, "end": v(-16, 39.5) * mm});
            skLineSegment(sketch, "E3691", {"start": v(-16, 39.5) * mm, "end": v(-16.11, 39.64) * mm});
            skLineSegment(sketch, "E3692", {"start": v(-16.11, 39.64) * mm, "end": v(-16.24, 39.77) * mm});
            skLineSegment(sketch, "E3693", {"start": v(-16.24, 39.77) * mm, "end": v(-16.37, 39.91) * mm});
            skLineSegment(sketch, "E3694", {"start": v(-16.37, 39.91) * mm, "end": v(-16.5, 40.05) * mm});
            skLineSegment(sketch, "E3695", {"start": v(-16.5, 40.05) * mm, "end": v(-16.62, 40.17) * mm});
            skLineSegment(sketch, "E3696", {"start": v(-16.62, 40.17) * mm, "end": v(-16.75, 40.3) * mm});
            skLineSegment(sketch, "E3697", {"start": v(-16.75, 40.3) * mm, "end": v(-16.88, 40.42) * mm});
            skLineSegment(sketch, "E3698", {"start": v(-16.88, 40.42) * mm, "end": v(-17.01, 40.55) * mm});
            skLineSegment(sketch, "E3699", {"start": v(-17.01, 40.55) * mm, "end": v(-17.15, 40.68) * mm});
            skLineSegment(sketch, "E3700", {"start": v(-17.15, 40.68) * mm, "end": v(-17.3, 40.81) * mm});
            skLineSegment(sketch, "E3701", {"start": v(-17.3, 40.81) * mm, "end": v(-17.44, 40.94) * mm});
            skLineSegment(sketch, "E3702", {"start": v(-17.44, 40.94) * mm, "end": v(-17.55, 41.03) * mm});
            skLineSegment(sketch, "E3703", {"start": v(-17.55, 41.03) * mm, "end": v(-17.72, 40.96) * mm});
            skLineSegment(sketch, "E3704", {"start": v(-17.72, 40.96) * mm, "end": v(-17.89, 40.89) * mm});
            skLineSegment(sketch, "E3705", {"start": v(-17.89, 40.89) * mm, "end": v(-18.05, 40.81) * mm});
            skLineSegment(sketch, "E3706", {"start": v(-18.05, 40.81) * mm, "end": v(-18.22, 40.74) * mm});
            skLineSegment(sketch, "E3707", {"start": v(-18.22, 40.74) * mm, "end": v(-18.3, 40.7) * mm});
            skLineSegment(sketch, "E3708", {"start": v(-18.3, 40.7) * mm, "end": v(-18.3, 40.51) * mm});
            skLineSegment(sketch, "E3709", {"start": v(-18.3, 40.51) * mm, "end": v(-18.31, 40.33) * mm});
            skLineSegment(sketch, "E3710", {"start": v(-18.31, 40.33) * mm, "end": v(-18.31, 40.15) * mm});
            skLineSegment(sketch, "E3711", {"start": v(-18.31, 40.15) * mm, "end": v(-18.31, 39.98) * mm});
            skLineSegment(sketch, "E3712", {"start": v(-18.31, 39.98) * mm, "end": v(-18.3, 39.8) * mm});
            skLineSegment(sketch, "E3713", {"start": v(-18.3, 39.8) * mm, "end": v(-18.3, 39.62) * mm});
            skLineSegment(sketch, "E3714", {"start": v(-18.3, 39.62) * mm, "end": v(-18.3, 39.43) * mm});
            skLineSegment(sketch, "E3715", {"start": v(-18.3, 39.43) * mm, "end": v(-18.29, 39.24) * mm});
            skLineSegment(sketch, "E3716", {"start": v(-18.29, 39.24) * mm, "end": v(-18.28, 39.05) * mm});
            skLineSegment(sketch, "E3717", {"start": v(-18.28, 39.05) * mm, "end": v(-18.26, 38.86) * mm});
            skLineSegment(sketch, "E3718", {"start": v(-18.26, 38.86) * mm, "end": v(-18.25, 38.67) * mm});
            skLineSegment(sketch, "E3719", {"start": v(-18.25, 38.67) * mm, "end": v(-18.23, 38.48) * mm});
            skLineSegment(sketch, "E3720", {"start": v(-18.23, 38.48) * mm, "end": v(-18.2, 38.3) * mm});
            skLineSegment(sketch, "E3721", {"start": v(-18.2, 38.3) * mm, "end": v(-18.18, 38.11) * mm});
            skLineSegment(sketch, "E3722", {"start": v(-18.18, 38.11) * mm, "end": v(-18.16, 37.93) * mm});
            skLineSegment(sketch, "E3723", {"start": v(-18.16, 37.93) * mm, "end": v(-18.13, 37.76) * mm});
            skLineSegment(sketch, "E3724", {"start": v(-18.13, 37.76) * mm, "end": v(-18.1, 37.57) * mm});
            skLineSegment(sketch, "E3725", {"start": v(-18.1, 37.57) * mm, "end": v(-18.06, 37.39) * mm});
            skLineSegment(sketch, "E3726", {"start": v(-18.06, 37.39) * mm, "end": v(-18.03, 37.2) * mm});
            skLineSegment(sketch, "E3727", {"start": v(-18.03, 37.2) * mm, "end": v(-18, 37.12) * mm});
            skLineSegment(sketch, "E3728", {"start": v(-18, 37.12) * mm, "end": v(-18.18, 37.03) * mm});
            skLineSegment(sketch, "E3729", {"start": v(-18.18, 37.03) * mm, "end": v(-18.35, 36.95) * mm});
            skLineSegment(sketch, "E3730", {"start": v(-18.35, 36.95) * mm, "end": v(-18.52, 36.86) * mm});
            skLineSegment(sketch, "E3731", {"start": v(-18.52, 36.86) * mm, "end": v(-18.7, 36.77) * mm});
            skLineSegment(sketch, "E3732", {"start": v(-18.7, 36.77) * mm, "end": v(-18.87, 36.69) * mm});
            skLineSegment(sketch, "E3733", {"start": v(-18.87, 36.69) * mm, "end": v(-19.04, 36.6) * mm});
            skLineSegment(sketch, "E3734", {"start": v(-19.04, 36.6) * mm, "end": v(-19.21, 36.51) * mm});
            skLineSegment(sketch, "E3735", {"start": v(-19.21, 36.51) * mm, "end": v(-19.24, 36.5) * mm});
            skLineSegment(sketch, "E3736", {"start": v(-19.24, 36.5) * mm, "end": v(-19.36, 36.62) * mm});
            skLineSegment(sketch, "E3737", {"start": v(-19.36, 36.62) * mm, "end": v(-19.48, 36.76) * mm});
            skLineSegment(sketch, "E3738", {"start": v(-19.48, 36.76) * mm, "end": v(-19.6, 36.89) * mm});
            skLineSegment(sketch, "E3739", {"start": v(-19.6, 36.89) * mm, "end": v(-19.73, 37.02) * mm});
            skLineSegment(sketch, "E3740", {"start": v(-19.73, 37.02) * mm, "end": v(-19.85, 37.14) * mm});
            skLineSegment(sketch, "E3741", {"start": v(-19.85, 37.14) * mm, "end": v(-19.98, 37.26) * mm});
            skLineSegment(sketch, "E3742", {"start": v(-19.98, 37.26) * mm, "end": v(-20.12, 37.4) * mm});
            skLineSegment(sketch, "E3743", {"start": v(-20.12, 37.4) * mm, "end": v(-20.24, 37.5) * mm});
            skLineSegment(sketch, "E3744", {"start": v(-20.24, 37.5) * mm, "end": v(-20.38, 37.63) * mm});
            skLineSegment(sketch, "E3745", {"start": v(-20.38, 37.63) * mm, "end": v(-20.51, 37.75) * mm});
            skLineSegment(sketch, "E3746", {"start": v(-20.51, 37.75) * mm, "end": v(-20.66, 37.87) * mm});
            skLineSegment(sketch, "E3747", {"start": v(-20.66, 37.87) * mm, "end": v(-20.8, 38) * mm});
            skLineSegment(sketch, "E3748", {"start": v(-20.8, 38) * mm, "end": v(-20.94, 38.1) * mm});
            skLineSegment(sketch, "E3749", {"start": v(-20.94, 38.1) * mm, "end": v(-21.08, 38.21) * mm});
            skLineSegment(sketch, "E3750", {"start": v(-21.08, 38.21) * mm, "end": v(-21.22, 38.32) * mm});
            skLineSegment(sketch, "E3751", {"start": v(-21.22, 38.32) * mm, "end": v(-21.37, 38.43) * mm});
            skLineSegment(sketch, "E3752", {"start": v(-21.37, 38.43) * mm, "end": v(-21.52, 38.55) * mm});
            skLineSegment(sketch, "E3753", {"start": v(-21.52, 38.55) * mm, "end": v(-21.68, 38.66) * mm});
            skLineSegment(sketch, "E3754", {"start": v(-21.68, 38.66) * mm, "end": v(-21.84, 38.78) * mm});
            skLineSegment(sketch, "E3755", {"start": v(-21.84, 38.78) * mm, "end": v(-21.95, 38.86) * mm});
            skLineSegment(sketch, "E3756", {"start": v(-21.95, 38.86) * mm, "end": v(-22.11, 38.76) * mm});
            skLineSegment(sketch, "E3757", {"start": v(-22.11, 38.76) * mm, "end": v(-22.27, 38.67) * mm});
            skLineSegment(sketch, "E3758", {"start": v(-22.27, 38.67) * mm, "end": v(-22.43, 38.58) * mm});
            skLineSegment(sketch, "E3759", {"start": v(-22.43, 38.58) * mm, "end": v(-22.6, 38.49) * mm});
            skLineSegment(sketch, "E3760", {"start": v(-22.6, 38.49) * mm, "end": v(-22.67, 38.44) * mm});
            skLineSegment(sketch, "E3761", {"start": v(-22.67, 38.44) * mm, "end": v(-22.65, 38.25) * mm});
            skLineSegment(sketch, "E3762", {"start": v(-22.65, 38.25) * mm, "end": v(-22.64, 38.07) * mm});
            skLineSegment(sketch, "E3763", {"start": v(-22.64, 38.07) * mm, "end": v(-22.62, 37.9) * mm});
            skLineSegment(sketch, "E3764", {"start": v(-22.62, 37.9) * mm, "end": v(-22.6, 37.72) * mm});
            skLineSegment(sketch, "E3765", {"start": v(-22.6, 37.72) * mm, "end": v(-22.58, 37.55) * mm});
            skLineSegment(sketch, "E3766", {"start": v(-22.58, 37.55) * mm, "end": v(-22.55, 37.36) * mm});
            skLineSegment(sketch, "E3767", {"start": v(-22.55, 37.36) * mm, "end": v(-22.52, 37.18) * mm});
            skLineSegment(sketch, "E3768", {"start": v(-22.52, 37.18) * mm, "end": v(-22.5, 36.99) * mm});
            skLineSegment(sketch, "E3769", {"start": v(-22.5, 36.99) * mm, "end": v(-22.46, 36.8) * mm});
            skLineSegment(sketch, "E3770", {"start": v(-22.46, 36.8) * mm, "end": v(-22.43, 36.61) * mm});
            skLineSegment(sketch, "E3771", {"start": v(-22.43, 36.61) * mm, "end": v(-22.39, 36.43) * mm});
            skLineSegment(sketch, "E3772", {"start": v(-22.39, 36.43) * mm, "end": v(-22.35, 36.25) * mm});
            skLineSegment(sketch, "E3773", {"start": v(-22.35, 36.25) * mm, "end": v(-22.31, 36.07) * mm});
            skLineSegment(sketch, "E3774", {"start": v(-22.31, 36.07) * mm, "end": v(-22.27, 35.88) * mm});
            skLineSegment(sketch, "E3775", {"start": v(-22.27, 35.88) * mm, "end": v(-22.22, 35.7) * mm});
            skLineSegment(sketch, "E3776", {"start": v(-22.22, 35.7) * mm, "end": v(-22.17, 35.53) * mm});
            skLineSegment(sketch, "E3777", {"start": v(-22.17, 35.53) * mm, "end": v(-22.12, 35.35) * mm});
            skLineSegment(sketch, "E3778", {"start": v(-22.12, 35.35) * mm, "end": v(-22.07, 35.17) * mm});
            skLineSegment(sketch, "E3779", {"start": v(-22.07, 35.17) * mm, "end": v(-22, 34.99) * mm});
            skLineSegment(sketch, "E3780", {"start": v(-22, 34.99) * mm, "end": v(-21.98, 34.9) * mm});
            skLineSegment(sketch, "E3781", {"start": v(-21.98, 34.9) * mm, "end": v(-22.14, 34.8) * mm});
            skLineSegment(sketch, "E3782", {"start": v(-22.14, 34.8) * mm, "end": v(-22.3, 34.7) * mm});
            skLineSegment(sketch, "E3783", {"start": v(-22.3, 34.7) * mm, "end": v(-22.47, 34.6) * mm});
            skLineSegment(sketch, "E3784", {"start": v(-22.47, 34.6) * mm, "end": v(-22.63, 34.5) * mm});
            skLineSegment(sketch, "E3785", {"start": v(-22.63, 34.5) * mm, "end": v(-22.79, 34.39) * mm});
            skLineSegment(sketch, "E3786", {"start": v(-22.79, 34.39) * mm, "end": v(-22.95, 34.28) * mm});
            skLineSegment(sketch, "E3787", {"start": v(-22.95, 34.28) * mm, "end": v(-23.11, 34.18) * mm});
            skLineSegment(sketch, "E3788", {"start": v(-23.11, 34.18) * mm, "end": v(-23.14, 34.16) * mm});
            skLineSegment(sketch, "E3789", {"start": v(-23.14, 34.16) * mm, "end": v(-23.27, 34.27) * mm});
            skLineSegment(sketch, "E3790", {"start": v(-23.27, 34.27) * mm, "end": v(-23.4, 34.4) * mm});
            skLineSegment(sketch, "E3791", {"start": v(-23.4, 34.4) * mm, "end": v(-23.54, 34.5) * mm});
            skLineSegment(sketch, "E3792", {"start": v(-23.54, 34.5) * mm, "end": v(-23.68, 34.62) * mm});
            skLineSegment(sketch, "E3793", {"start": v(-23.68, 34.62) * mm, "end": v(-23.82, 34.73) * mm});
            skLineSegment(sketch, "E3794", {"start": v(-23.82, 34.73) * mm, "end": v(-23.96, 34.84) * mm});
            skLineSegment(sketch, "E3795", {"start": v(-23.96, 34.84) * mm, "end": v(-24.1, 34.95) * mm});
            skLineSegment(sketch, "E3796", {"start": v(-24.1, 34.95) * mm, "end": v(-24.25, 35.05) * mm});
            skLineSegment(sketch, "E3797", {"start": v(-24.25, 35.05) * mm, "end": v(-24.4, 35.16) * mm});
            skLineSegment(sketch, "E3798", {"start": v(-24.4, 35.16) * mm, "end": v(-24.54, 35.26) * mm});
            skLineSegment(sketch, "E3799", {"start": v(-24.54, 35.26) * mm, "end": v(-24.7, 35.37) * mm});
            skLineSegment(sketch, "E3800", {"start": v(-24.7, 35.37) * mm, "end": v(-24.86, 35.47) * mm});
            skLineSegment(sketch, "E3801", {"start": v(-24.86, 35.47) * mm, "end": v(-25, 35.57) * mm});
            skLineSegment(sketch, "E3802", {"start": v(-25, 35.57) * mm, "end": v(-25.15, 35.66) * mm});
            skLineSegment(sketch, "E3803", {"start": v(-25.15, 35.66) * mm, "end": v(-25.3, 35.75) * mm});
            skLineSegment(sketch, "E3804", {"start": v(-25.3, 35.75) * mm, "end": v(-25.47, 35.85) * mm});
            skLineSegment(sketch, "E3805", {"start": v(-25.47, 35.85) * mm, "end": v(-25.63, 35.94) * mm});
            skLineSegment(sketch, "E3806", {"start": v(-25.63, 35.94) * mm, "end": v(-25.8, 36.04) * mm});
            skLineSegment(sketch, "E3807", {"start": v(-25.8, 36.04) * mm, "end": v(-25.97, 36.14) * mm});
            skLineSegment(sketch, "E3808", {"start": v(-25.97, 36.14) * mm, "end": v(-26.1, 36.2) * mm});
            skLineSegment(sketch, "E3809", {"start": v(-26.1, 36.2) * mm, "end": v(-26.24, 36.1) * mm});
            skLineSegment(sketch, "E3810", {"start": v(-26.24, 36.1) * mm, "end": v(-26.4, 35.99) * mm});
            skLineSegment(sketch, "E3811", {"start": v(-26.4, 35.99) * mm, "end": v(-26.54, 35.88) * mm});
            skLineSegment(sketch, "E3812", {"start": v(-26.54, 35.88) * mm, "end": v(-26.7, 35.77) * mm});
            skLineSegment(sketch, "E3813", {"start": v(-26.7, 35.77) * mm, "end": v(-26.76, 35.71) * mm});
            skLineSegment(sketch, "E3814", {"start": v(-26.76, 35.71) * mm, "end": v(-26.72, 35.53) * mm});
            skLineSegment(sketch, "E3815", {"start": v(-26.72, 35.53) * mm, "end": v(-26.69, 35.35) * mm});
            skLineSegment(sketch, "E3816", {"start": v(-26.69, 35.35) * mm, "end": v(-26.65, 35.17) * mm});
            skLineSegment(sketch, "E3817", {"start": v(-26.65, 35.17) * mm, "end": v(-26.6, 35) * mm});
            skLineSegment(sketch, "E3818", {"start": v(-26.6, 35) * mm, "end": v(-26.57, 34.84) * mm});
            skLineSegment(sketch, "E3819", {"start": v(-26.57, 34.84) * mm, "end": v(-26.52, 34.66) * mm});
            skLineSegment(sketch, "E3820", {"start": v(-26.52, 34.66) * mm, "end": v(-26.47, 34.47) * mm});
            skLineSegment(sketch, "E3821", {"start": v(-26.47, 34.47) * mm, "end": v(-26.42, 34.29) * mm});
            skLineSegment(sketch, "E3822", {"start": v(-26.42, 34.29) * mm, "end": v(-26.37, 34.1) * mm});
            skLineSegment(sketch, "E3823", {"start": v(-26.37, 34.1) * mm, "end": v(-26.32, 33.93) * mm});
            skLineSegment(sketch, "E3824", {"start": v(-26.32, 33.93) * mm, "end": v(-26.26, 33.75) * mm});
            skLineSegment(sketch, "E3825", {"start": v(-26.26, 33.75) * mm, "end": v(-26.2, 33.57) * mm});
            skLineSegment(sketch, "E3826", {"start": v(-26.2, 33.57) * mm, "end": v(-26.14, 33.4) * mm});
            skLineSegment(sketch, "E3827", {"start": v(-26.14, 33.4) * mm, "end": v(-26.08, 33.22) * mm});
            skLineSegment(sketch, "E3828", {"start": v(-26.08, 33.22) * mm, "end": v(-26.01, 33.04) * mm});
            skLineSegment(sketch, "E3829", {"start": v(-26.01, 33.04) * mm, "end": v(-25.95, 32.88) * mm});
            skLineSegment(sketch, "E3830", {"start": v(-25.95, 32.88) * mm, "end": v(-25.88, 32.7) * mm});
            skLineSegment(sketch, "E3831", {"start": v(-25.88, 32.7) * mm, "end": v(-25.8, 32.53) * mm});
            skLineSegment(sketch, "E3832", {"start": v(-25.8, 32.53) * mm, "end": v(-25.72, 32.35) * mm});
            skLineSegment(sketch, "E3833", {"start": v(-25.72, 32.35) * mm, "end": v(-25.69, 32.28) * mm});
            skLineSegment(sketch, "E3834", {"start": v(-25.69, 32.28) * mm, "end": v(-25.83, 32.16) * mm});
            skLineSegment(sketch, "E3835", {"start": v(-25.83, 32.16) * mm, "end": v(-25.99, 32.04) * mm});
            skLineSegment(sketch, "E3836", {"start": v(-25.99, 32.04) * mm, "end": v(-26.14, 31.92) * mm});
            skLineSegment(sketch, "E3837", {"start": v(-26.14, 31.92) * mm, "end": v(-26.29, 31.8) * mm});
            skLineSegment(sketch, "E3838", {"start": v(-26.29, 31.8) * mm, "end": v(-26.43, 31.67) * mm});
            skLineSegment(sketch, "E3839", {"start": v(-26.43, 31.67) * mm, "end": v(-26.59, 31.54) * mm});
            skLineSegment(sketch, "E3840", {"start": v(-26.59, 31.54) * mm, "end": v(-26.73, 31.43) * mm});
            skLineSegment(sketch, "E3841", {"start": v(-26.73, 31.43) * mm, "end": v(-26.76, 31.4) * mm});
            skLineSegment(sketch, "E3842", {"start": v(-26.76, 31.4) * mm, "end": v(-26.9, 31.5) * mm});
            skLineSegment(sketch, "E3843", {"start": v(-26.9, 31.5) * mm, "end": v(-27.05, 31.6) * mm});
            skLineSegment(sketch, "E3844", {"start": v(-27.05, 31.6) * mm, "end": v(-27.2, 31.7) * mm});
            skLineSegment(sketch, "E3845", {"start": v(-27.2, 31.7) * mm, "end": v(-27.35, 31.8) * mm});
            skLineSegment(sketch, "E3846", {"start": v(-27.35, 31.8) * mm, "end": v(-27.5, 31.9) * mm});
            skLineSegment(sketch, "E3847", {"start": v(-27.5, 31.9) * mm, "end": v(-27.65, 32) * mm});
            skLineSegment(sketch, "E3848", {"start": v(-27.65, 32) * mm, "end": v(-27.8, 32.09) * mm});
            skLineSegment(sketch, "E3849", {"start": v(-27.8, 32.09) * mm, "end": v(-27.96, 32.17) * mm});
            skLineSegment(sketch, "E3850", {"start": v(-27.96, 32.17) * mm, "end": v(-28.1, 32.26) * mm});
            skLineSegment(sketch, "E3851", {"start": v(-28.1, 32.26) * mm, "end": v(-28.27, 32.35) * mm});
            skLineSegment(sketch, "E3852", {"start": v(-28.27, 32.35) * mm, "end": v(-28.44, 32.43) * mm});
            skLineSegment(sketch, "E3853", {"start": v(-28.44, 32.43) * mm, "end": v(-28.61, 32.52) * mm});
            skLineSegment(sketch, "E3854", {"start": v(-28.61, 32.52) * mm, "end": v(-28.77, 32.6) * mm});
            skLineSegment(sketch, "E3855", {"start": v(-28.77, 32.6) * mm, "end": v(-28.92, 32.68) * mm});
            skLineSegment(sketch, "E3856", {"start": v(-28.92, 32.68) * mm, "end": v(-29.09, 32.75) * mm});
            skLineSegment(sketch, "E3857", {"start": v(-29.09, 32.75) * mm, "end": v(-29.26, 32.83) * mm});
            skLineSegment(sketch, "E3858", {"start": v(-29.26, 32.83) * mm, "end": v(-29.43, 32.9) * mm});
            skLineSegment(sketch, "E3859", {"start": v(-29.43, 32.9) * mm, "end": v(-29.6, 32.98) * mm});
            skLineSegment(sketch, "E3860", {"start": v(-29.6, 32.98) * mm, "end": v(-29.79, 33.06) * mm});
            skLineSegment(sketch, "E3861", {"start": v(-29.79, 33.06) * mm, "end": v(-29.92, 33.11) * mm});
            skLineSegment(sketch, "E3862", {"start": v(-29.92, 33.11) * mm, "end": v(-30.06, 33) * mm});
            skLineSegment(sketch, "E3863", {"start": v(-30.06, 33) * mm, "end": v(-30.2, 32.87) * mm});
            skLineSegment(sketch, "E3864", {"start": v(-30.2, 32.87) * mm, "end": v(-30.33, 32.74) * mm});
            skLineSegment(sketch, "E3865", {"start": v(-30.33, 32.74) * mm, "end": v(-30.46, 32.61) * mm});
            skLineSegment(sketch, "E3866", {"start": v(-30.46, 32.61) * mm, "end": v(-30.53, 32.55) * mm});
            skLineSegment(sketch, "E3867", {"start": v(-30.53, 32.55) * mm, "end": v(-30.47, 32.37) * mm});
            skLineSegment(sketch, "E3868", {"start": v(-30.47, 32.37) * mm, "end": v(-30.41, 32.2) * mm});
            skLineSegment(sketch, "E3869", {"start": v(-30.41, 32.2) * mm, "end": v(-30.36, 32.03) * mm});
            skLineSegment(sketch, "E3870", {"start": v(-30.36, 32.03) * mm, "end": v(-30.3, 31.86) * mm});
            skLineSegment(sketch, "E3871", {"start": v(-30.3, 31.86) * mm, "end": v(-30.24, 31.7) * mm});
            skLineSegment(sketch, "E3872", {"start": v(-30.24, 31.7) * mm, "end": v(-30.17, 31.53) * mm});
            skLineSegment(sketch, "E3873", {"start": v(-30.17, 31.53) * mm, "end": v(-30.1, 31.35) * mm});
            skLineSegment(sketch, "E3874", {"start": v(-30.1, 31.35) * mm, "end": v(-30.04, 31.17) * mm});
            skLineSegment(sketch, "E3875", {"start": v(-30.04, 31.17) * mm, "end": v(-29.96, 31) * mm});
            skLineSegment(sketch, "E3876", {"start": v(-29.96, 31) * mm, "end": v(-29.89, 30.82) * mm});
            skLineSegment(sketch, "E3877", {"start": v(-29.89, 30.82) * mm, "end": v(-29.81, 30.65) * mm});
            skLineSegment(sketch, "E3878", {"start": v(-29.81, 30.65) * mm, "end": v(-29.73, 30.48) * mm});
            skLineSegment(sketch, "E3879", {"start": v(-29.73, 30.48) * mm, "end": v(-29.66, 30.32) * mm});
            skLineSegment(sketch, "E3880", {"start": v(-29.66, 30.32) * mm, "end": v(-29.57, 30.15) * mm});
            skLineSegment(sketch, "E3881", {"start": v(-29.57, 30.15) * mm, "end": v(-29.49, 29.98) * mm});
            skLineSegment(sketch, "E3882", {"start": v(-29.49, 29.98) * mm, "end": v(-29.4, 29.83) * mm});
            skLineSegment(sketch, "E3883", {"start": v(-29.4, 29.83) * mm, "end": v(-29.32, 29.66) * mm});
            skLineSegment(sketch, "E3884", {"start": v(-29.32, 29.66) * mm, "end": v(-29.22, 29.5) * mm});
            skLineSegment(sketch, "E3885", {"start": v(-29.22, 29.5) * mm, "end": v(-29.12, 29.33) * mm});
            skLineSegment(sketch, "E3886", {"start": v(-29.12, 29.33) * mm, "end": v(-29.08, 29.26) * mm});
            skLineSegment(sketch, "E3887", {"start": v(-29.08, 29.26) * mm, "end": v(-29.22, 29.12) * mm});
            skLineSegment(sketch, "E3888", {"start": v(-29.22, 29.12) * mm, "end": v(-29.36, 28.98) * mm});
            skLineSegment(sketch, "E3889", {"start": v(-29.36, 28.98) * mm, "end": v(-29.49, 28.85) * mm});
            skLineSegment(sketch, "E3890", {"start": v(-29.49, 28.85) * mm, "end": v(-29.63, 28.7) * mm});
            skLineSegment(sketch, "E3891", {"start": v(-29.63, 28.7) * mm, "end": v(-29.76, 28.57) * mm});
            skLineSegment(sketch, "E3892", {"start": v(-29.76, 28.57) * mm, "end": v(-29.9, 28.43) * mm});
            skLineSegment(sketch, "E3893", {"start": v(-29.9, 28.43) * mm, "end": v(-30.03, 28.3) * mm});
            skLineSegment(sketch, "E3894", {"start": v(-30.03, 28.3) * mm, "end": v(-30.05, 28.27) * mm});
            skLineSegment(sketch, "E3895", {"start": v(-30.05, 28.27) * mm, "end": v(-30.2, 28.35) * mm});
            skLineSegment(sketch, "E3896", {"start": v(-30.2, 28.35) * mm, "end": v(-30.36, 28.44) * mm});
            skLineSegment(sketch, "E3897", {"start": v(-30.36, 28.44) * mm, "end": v(-30.51, 28.52) * mm});
            skLineSegment(sketch, "E3898", {"start": v(-30.51, 28.52) * mm, "end": v(-30.68, 28.6) * mm});
            skLineSegment(sketch, "E3899", {"start": v(-30.68, 28.6) * mm, "end": v(-30.83, 28.68) * mm});
            skLineSegment(sketch, "E3900", {"start": v(-30.83, 28.68) * mm, "end": v(-31, 28.76) * mm});
            skLineSegment(sketch, "E3901", {"start": v(-31, 28.76) * mm, "end": v(-31.17, 28.83) * mm});
            skLineSegment(sketch, "E3902", {"start": v(-31.17, 28.83) * mm, "end": v(-31.32, 28.9) * mm});
            skLineSegment(sketch, "E3903", {"start": v(-31.32, 28.9) * mm, "end": v(-31.49, 28.97) * mm});
            skLineSegment(sketch, "E3904", {"start": v(-31.49, 28.97) * mm, "end": v(-31.66, 29.04) * mm});
            skLineSegment(sketch, "E3905", {"start": v(-31.66, 29.04) * mm, "end": v(-31.83, 29.1) * mm});
            skLineSegment(sketch, "E3906", {"start": v(-31.83, 29.1) * mm, "end": v(-32.02, 29.18) * mm});
            skLineSegment(sketch, "E3907", {"start": v(-32.02, 29.18) * mm, "end": v(-32.18, 29.24) * mm});
            skLineSegment(sketch, "E3908", {"start": v(-32.18, 29.24) * mm, "end": v(-32.34, 29.3) * mm});
            skLineSegment(sketch, "E3909", {"start": v(-32.34, 29.3) * mm, "end": v(-32.51, 29.35) * mm});
            skLineSegment(sketch, "E3910", {"start": v(-32.51, 29.35) * mm, "end": v(-32.69, 29.41) * mm});
            skLineSegment(sketch, "E3911", {"start": v(-32.69, 29.41) * mm, "end": v(-32.87, 29.47) * mm});
            skLineSegment(sketch, "E3912", {"start": v(-32.87, 29.47) * mm, "end": v(-33.05, 29.53) * mm});
            skLineSegment(sketch, "E3913", {"start": v(-33.05, 29.53) * mm, "end": v(-33.24, 29.58) * mm});
            skLineSegment(sketch, "E3914", {"start": v(-33.24, 29.58) * mm, "end": v(-33.38, 29.62) * mm});
            skLineSegment(sketch, "E3915", {"start": v(-33.38, 29.62) * mm, "end": v(-33.5, 29.48) * mm});
            skLineSegment(sketch, "E3916", {"start": v(-33.5, 29.48) * mm, "end": v(-33.62, 29.34) * mm});
            skLineSegment(sketch, "E3917", {"start": v(-33.62, 29.34) * mm, "end": v(-33.74, 29.2) * mm});
            skLineSegment(sketch, "E3918", {"start": v(-33.74, 29.2) * mm, "end": v(-33.87, 29.07) * mm});
            skLineSegment(sketch, "E3919", {"start": v(-33.87, 29.07) * mm, "end": v(-33.92, 29) * mm});
            skLineSegment(sketch, "E3920", {"start": v(-33.92, 29) * mm, "end": v(-33.85, 28.82) * mm});
            skLineSegment(sketch, "E3921", {"start": v(-33.85, 28.82) * mm, "end": v(-33.77, 28.66) * mm});
            skLineSegment(sketch, "E3922", {"start": v(-33.77, 28.66) * mm, "end": v(-33.7, 28.5) * mm});
            skLineSegment(sketch, "E3923", {"start": v(-33.7, 28.5) * mm, "end": v(-33.62, 28.34) * mm});
            skLineSegment(sketch, "E3924", {"start": v(-33.62, 28.34) * mm, "end": v(-33.54, 28.18) * mm});
            skLineSegment(sketch, "E3925", {"start": v(-33.54, 28.18) * mm, "end": v(-33.46, 28.02) * mm});
            skLineSegment(sketch, "E3926", {"start": v(-33.46, 28.02) * mm, "end": v(-33.37, 27.85) * mm});
            skLineSegment(sketch, "E3927", {"start": v(-33.37, 27.85) * mm, "end": v(-33.28, 27.68) * mm});
            skLineSegment(sketch, "E3928", {"start": v(-33.28, 27.68) * mm, "end": v(-33.2, 27.51) * mm});
            skLineSegment(sketch, "E3929", {"start": v(-33.2, 27.51) * mm, "end": v(-33.1, 27.35) * mm});
            skLineSegment(sketch, "E3930", {"start": v(-33.1, 27.35) * mm, "end": v(-33, 27.19) * mm});
            skLineSegment(sketch, "E3931", {"start": v(-33, 27.19) * mm, "end": v(-32.9, 27.03) * mm});
            skLineSegment(sketch, "E3932", {"start": v(-32.9, 27.03) * mm, "end": v(-32.81, 26.87) * mm});
            skLineSegment(sketch, "E3933", {"start": v(-32.81, 26.87) * mm, "end": v(-32.7, 26.7) * mm});
            skLineSegment(sketch, "E3934", {"start": v(-32.7, 26.7) * mm, "end": v(-32.6, 26.56) * mm});
            skLineSegment(sketch, "E3935", {"start": v(-32.6, 26.56) * mm, "end": v(-32.51, 26.4) * mm});
            skLineSegment(sketch, "E3936", {"start": v(-32.51, 26.4) * mm, "end": v(-32.4, 26.26) * mm});
            skLineSegment(sketch, "E3937", {"start": v(-32.4, 26.26) * mm, "end": v(-32.3, 26.1) * mm});
            skLineSegment(sketch, "E3938", {"start": v(-32.3, 26.1) * mm, "end": v(-32.17, 25.95) * mm});
            skLineSegment(sketch, "E3939", {"start": v(-32.17, 25.95) * mm, "end": v(-32.12, 25.88) * mm});
            skLineSegment(sketch, "E3940", {"start": v(-32.12, 25.88) * mm, "end": v(-32.24, 25.73) * mm});
            skLineSegment(sketch, "E3941", {"start": v(-32.24, 25.73) * mm, "end": v(-32.37, 25.58) * mm});
            skLineSegment(sketch, "E3942", {"start": v(-32.37, 25.58) * mm, "end": v(-32.48, 25.43) * mm});
            skLineSegment(sketch, "E3943", {"start": v(-32.48, 25.43) * mm, "end": v(-32.6, 25.27) * mm});
            skLineSegment(sketch, "E3944", {"start": v(-32.6, 25.27) * mm, "end": v(-32.72, 25.12) * mm});
            skLineSegment(sketch, "E3945", {"start": v(-32.72, 25.12) * mm, "end": v(-32.84, 24.97) * mm});
            skLineSegment(sketch, "E3946", {"start": v(-32.84, 24.97) * mm, "end": v(-32.96, 24.82) * mm});
            skLineSegment(sketch, "E3947", {"start": v(-32.96, 24.82) * mm, "end": v(-32.98, 24.8) * mm});
            skLineSegment(sketch, "E3948", {"start": v(-32.98, 24.8) * mm, "end": v(-33.13, 24.86) * mm});
            skLineSegment(sketch, "E3949", {"start": v(-33.13, 24.86) * mm, "end": v(-33.3, 24.93) * mm});
            skLineSegment(sketch, "E3950", {"start": v(-33.3, 24.93) * mm, "end": v(-33.47, 25) * mm});
            skLineSegment(sketch, "E3951", {"start": v(-33.47, 25) * mm, "end": v(-33.64, 25.06) * mm});
            skLineSegment(sketch, "E3952", {"start": v(-33.64, 25.06) * mm, "end": v(-33.8, 25.12) * mm});
            skLineSegment(sketch, "E3953", {"start": v(-33.8, 25.12) * mm, "end": v(-33.97, 25.17) * mm});
            skLineSegment(sketch, "E3954", {"start": v(-33.97, 25.17) * mm, "end": v(-34.15, 25.23) * mm});
            skLineSegment(sketch, "E3955", {"start": v(-34.15, 25.23) * mm, "end": v(-34.31, 25.28) * mm});
            skLineSegment(sketch, "E3956", {"start": v(-34.31, 25.28) * mm, "end": v(-34.48, 25.33) * mm});
            skLineSegment(sketch, "E3957", {"start": v(-34.48, 25.33) * mm, "end": v(-34.66, 25.38) * mm});
            skLineSegment(sketch, "E3958", {"start": v(-34.66, 25.38) * mm, "end": v(-34.84, 25.43) * mm});
            skLineSegment(sketch, "E3959", {"start": v(-34.84, 25.43) * mm, "end": v(-35.03, 25.48) * mm});
            skLineSegment(sketch, "E3960", {"start": v(-35.03, 25.48) * mm, "end": v(-35.2, 25.52) * mm});
            skLineSegment(sketch, "E3961", {"start": v(-35.2, 25.52) * mm, "end": v(-35.37, 25.56) * mm});
            skLineSegment(sketch, "E3962", {"start": v(-35.37, 25.56) * mm, "end": v(-35.54, 25.6) * mm});
            skLineSegment(sketch, "E3963", {"start": v(-35.54, 25.6) * mm, "end": v(-35.73, 25.64) * mm});
            skLineSegment(sketch, "E3964", {"start": v(-35.73, 25.64) * mm, "end": v(-35.91, 25.68) * mm});
            skLineSegment(sketch, "E3965", {"start": v(-35.91, 25.68) * mm, "end": v(-36.1, 25.71) * mm});
            skLineSegment(sketch, "E3966", {"start": v(-36.1, 25.71) * mm, "end": v(-36.3, 25.75) * mm});
            skLineSegment(sketch, "E3967", {"start": v(-36.3, 25.75) * mm, "end": v(-36.44, 25.77) * mm});
            skLineSegment(sketch, "E3968", {"start": v(-36.44, 25.77) * mm, "end": v(-36.54, 25.62) * mm});
            skLineSegment(sketch, "E3969", {"start": v(-36.54, 25.62) * mm, "end": v(-36.65, 25.47) * mm});
            skLineSegment(sketch, "E3970", {"start": v(-36.65, 25.47) * mm, "end": v(-36.75, 25.32) * mm});
            skLineSegment(sketch, "E3971", {"start": v(-36.75, 25.32) * mm, "end": v(-36.86, 25.16) * mm});
            skLineSegment(sketch, "E3972", {"start": v(-36.86, 25.16) * mm, "end": v(-36.9, 25.09) * mm});
            skLineSegment(sketch, "E3973", {"start": v(-36.9, 25.09) * mm, "end": v(-36.81, 24.92) * mm});
            skLineSegment(sketch, "E3974", {"start": v(-36.81, 24.92) * mm, "end": v(-36.72, 24.77) * mm});
            skLineSegment(sketch, "E3975", {"start": v(-36.72, 24.77) * mm, "end": v(-36.62, 24.62) * mm});
            skLineSegment(sketch, "E3976", {"start": v(-36.62, 24.62) * mm, "end": v(-36.53, 24.47) * mm});
            skLineSegment(sketch, "E3977", {"start": v(-36.53, 24.47) * mm, "end": v(-36.44, 24.32) * mm});
            skLineSegment(sketch, "E3978", {"start": v(-36.44, 24.32) * mm, "end": v(-36.34, 24.17) * mm});
            skLineSegment(sketch, "E3979", {"start": v(-36.34, 24.17) * mm, "end": v(-36.23, 24) * mm});
            skLineSegment(sketch, "E3980", {"start": v(-36.23, 24) * mm, "end": v(-36.12, 23.85) * mm});
            skLineSegment(sketch, "E3981", {"start": v(-36.12, 23.85) * mm, "end": v(-36.02, 23.7) * mm});
            skLineSegment(sketch, "E3982", {"start": v(-36.02, 23.7) * mm, "end": v(-35.9, 23.54) * mm});
            skLineSegment(sketch, "E3983", {"start": v(-35.9, 23.54) * mm, "end": v(-35.8, 23.4) * mm});
            skLineSegment(sketch, "E3984", {"start": v(-35.8, 23.4) * mm, "end": v(-35.68, 23.24) * mm});
            skLineSegment(sketch, "E3985", {"start": v(-35.68, 23.24) * mm, "end": v(-35.57, 23.1) * mm});
            skLineSegment(sketch, "E3986", {"start": v(-35.57, 23.1) * mm, "end": v(-35.45, 22.95) * mm});
            skLineSegment(sketch, "E3987", {"start": v(-35.45, 22.95) * mm, "end": v(-35.33, 22.8) * mm});
            skLineSegment(sketch, "E3988", {"start": v(-35.33, 22.8) * mm, "end": v(-35.22, 22.67) * mm});
            skLineSegment(sketch, "E3989", {"start": v(-35.22, 22.67) * mm, "end": v(-35.1, 22.53) * mm});
            skLineSegment(sketch, "E3990", {"start": v(-35.1, 22.53) * mm, "end": v(-34.97, 22.4) * mm});
            skLineSegment(sketch, "E3991", {"start": v(-34.97, 22.4) * mm, "end": v(-34.83, 22.25) * mm});
            skLineSegment(sketch, "E3992", {"start": v(-34.83, 22.25) * mm, "end": v(-34.78, 22.2) * mm});
            skLineSegment(sketch, "E3993", {"start": v(-34.78, 22.2) * mm, "end": v(-34.88, 22.03) * mm});
            skLineSegment(sketch, "E3994", {"start": v(-34.88, 22.03) * mm, "end": v(-34.98, 21.86) * mm});
            skLineSegment(sketch, "E3995", {"start": v(-34.98, 21.86) * mm, "end": v(-35.08, 21.7) * mm});
            skLineSegment(sketch, "E3996", {"start": v(-35.08, 21.7) * mm, "end": v(-35.19, 21.53) * mm});
            skLineSegment(sketch, "E3997", {"start": v(-35.19, 21.53) * mm, "end": v(-35.28, 21.37) * mm});
            skLineSegment(sketch, "E3998", {"start": v(-35.28, 21.37) * mm, "end": v(-35.39, 21.2) * mm});
            skLineSegment(sketch, "E3999", {"start": v(-35.39, 21.2) * mm, "end": v(-35.49, 21.04) * mm});
            skLineSegment(sketch, "E4000", {"start": v(-35.49, 21.04) * mm, "end": v(-35.5, 21.02) * mm});
            skLineSegment(sketch, "E4001", {"start": v(-35.5, 21.02) * mm, "end": v(-35.67, 21.06) * mm});
            skLineSegment(sketch, "E4002", {"start": v(-35.67, 21.06) * mm, "end": v(-35.84, 21.11) * mm});
            skLineSegment(sketch, "E4003", {"start": v(-35.84, 21.11) * mm, "end": v(-36.01, 21.16) * mm});
            skLineSegment(sketch, "E4004", {"start": v(-36.01, 21.16) * mm, "end": v(-36.2, 21.2) * mm});
            skLineSegment(sketch, "E4005", {"start": v(-36.2, 21.2) * mm, "end": v(-36.36, 21.24) * mm});
            skLineSegment(sketch, "E4006", {"start": v(-36.36, 21.24) * mm, "end": v(-36.53, 21.28) * mm});
            skLineSegment(sketch, "E4007", {"start": v(-36.53, 21.28) * mm, "end": v(-36.72, 21.32) * mm});
            skLineSegment(sketch, "E4008", {"start": v(-36.72, 21.32) * mm, "end": v(-36.89, 21.35) * mm});
            skLineSegment(sketch, "E4009", {"start": v(-36.89, 21.35) * mm, "end": v(-37.06, 21.38) * mm});
            skLineSegment(sketch, "E4010", {"start": v(-37.06, 21.38) * mm, "end": v(-37.24, 21.42) * mm});
            skLineSegment(sketch, "E4011", {"start": v(-37.24, 21.42) * mm, "end": v(-37.43, 21.44) * mm});
            skLineSegment(sketch, "E4012", {"start": v(-37.43, 21.44) * mm, "end": v(-37.62, 21.47) * mm});
            skLineSegment(sketch, "E4013", {"start": v(-37.62, 21.47) * mm, "end": v(-37.8, 21.5) * mm});
            skLineSegment(sketch, "E4014", {"start": v(-37.8, 21.5) * mm, "end": v(-37.97, 21.51) * mm});
            skLineSegment(sketch, "E4015", {"start": v(-37.97, 21.51) * mm, "end": v(-38.15, 21.53) * mm});
            skLineSegment(sketch, "E4016", {"start": v(-38.15, 21.53) * mm, "end": v(-38.33, 21.55) * mm});
            skLineSegment(sketch, "E4017", {"start": v(-38.33, 21.55) * mm, "end": v(-38.52, 21.57) * mm});
            skLineSegment(sketch, "E4018", {"start": v(-38.52, 21.57) * mm, "end": v(-38.71, 21.58) * mm});
            skLineSegment(sketch, "E4019", {"start": v(-38.71, 21.58) * mm, "end": v(-38.9, 21.6) * mm});
            skLineSegment(sketch, "E4020", {"start": v(-38.9, 21.6) * mm, "end": v(-39.05, 21.6) * mm});
            skLineSegment(sketch, "E4021", {"start": v(-39.05, 21.6) * mm, "end": v(-39.14, 21.44) * mm});
            skLineSegment(sketch, "E4022", {"start": v(-39.14, 21.44) * mm, "end": v(-39.23, 21.28) * mm});
            skLineSegment(sketch, "E4023", {"start": v(-39.23, 21.28) * mm, "end": v(-39.31, 21.12) * mm});
            skLineSegment(sketch, "E4024", {"start": v(-39.31, 21.12) * mm, "end": v(-39.4, 20.96) * mm});
            skLineSegment(sketch, "E4025", {"start": v(-39.4, 20.96) * mm, "end": v(-39.44, 20.88) * mm});
            skLineSegment(sketch, "E4026", {"start": v(-39.44, 20.88) * mm, "end": v(-39.33, 20.72) * mm});
            skLineSegment(sketch, "E4027", {"start": v(-39.33, 20.72) * mm, "end": v(-39.22, 20.58) * mm});
            skLineSegment(sketch, "E4028", {"start": v(-39.22, 20.58) * mm, "end": v(-39.1, 20.44) * mm});
            skLineSegment(sketch, "E4029", {"start": v(-39.1, 20.44) * mm, "end": v(-39, 20.3) * mm});
            skLineSegment(sketch, "E4030", {"start": v(-39, 20.3) * mm, "end": v(-38.9, 20.17) * mm});
            skLineSegment(sketch, "E4031", {"start": v(-38.9, 20.17) * mm, "end": v(-38.77, 20.02) * mm});
            skLineSegment(sketch, "E4032", {"start": v(-38.77, 20.02) * mm, "end": v(-38.65, 19.88) * mm});
            skLineSegment(sketch, "E4033", {"start": v(-38.65, 19.88) * mm, "end": v(-38.53, 19.73) * mm});
            skLineSegment(sketch, "E4034", {"start": v(-38.53, 19.73) * mm, "end": v(-38.4, 19.6) * mm});
            skLineSegment(sketch, "E4035", {"start": v(-38.4, 19.6) * mm, "end": v(-38.28, 19.45) * mm});
            skLineSegment(sketch, "E4036", {"start": v(-38.28, 19.45) * mm, "end": v(-38.15, 19.31) * mm});
            skLineSegment(sketch, "E4037", {"start": v(-38.15, 19.31) * mm, "end": v(-38.02, 19.18) * mm});
            skLineSegment(sketch, "E4038", {"start": v(-38.02, 19.18) * mm, "end": v(-37.9, 19.05) * mm});
            skLineSegment(sketch, "E4039", {"start": v(-37.9, 19.05) * mm, "end": v(-37.76, 18.91) * mm});
            skLineSegment(sketch, "E4040", {"start": v(-37.76, 18.91) * mm, "end": v(-37.63, 18.78) * mm});
            skLineSegment(sketch, "E4041", {"start": v(-37.63, 18.78) * mm, "end": v(-37.5, 18.66) * mm});
            skLineSegment(sketch, "E4042", {"start": v(-37.5, 18.66) * mm, "end": v(-37.36, 18.53) * mm});
            skLineSegment(sketch, "E4043", {"start": v(-37.36, 18.53) * mm, "end": v(-37.22, 18.4) * mm});
            skLineSegment(sketch, "E4044", {"start": v(-37.22, 18.4) * mm, "end": v(-37.07, 18.28) * mm});
            skLineSegment(sketch, "E4045", {"start": v(-37.07, 18.28) * mm, "end": v(-37, 18.23) * mm});
            skLineSegment(sketch, "E4046", {"start": v(-37, 18.23) * mm, "end": v(-37.09, 18.06) * mm});
            skLineSegment(sketch, "E4047", {"start": v(-37.09, 18.06) * mm, "end": v(-37.17, 17.88) * mm});
            skLineSegment(sketch, "E4048", {"start": v(-37.17, 17.88) * mm, "end": v(-37.26, 17.71) * mm});
            skLineSegment(sketch, "E4049", {"start": v(-37.26, 17.71) * mm, "end": v(-37.34, 17.53) * mm});
            skLineSegment(sketch, "E4050", {"start": v(-37.34, 17.53) * mm, "end": v(-37.42, 17.36) * mm});
            skLineSegment(sketch, "E4051", {"start": v(-37.42, 17.36) * mm, "end": v(-37.5, 17.18) * mm});
            skLineSegment(sketch, "E4052", {"start": v(-37.5, 17.18) * mm, "end": v(-37.59, 17.01) * mm});
            skLineSegment(sketch, "E4053", {"start": v(-37.59, 17.01) * mm, "end": v(-37.6, 16.98) * mm});
            skLineSegment(sketch, "E4054", {"start": v(-37.6, 16.98) * mm, "end": v(-37.77, 17.01) * mm});
            skLineSegment(sketch, "E4055", {"start": v(-37.77, 17.01) * mm, "end": v(-37.95, 17.04) * mm});
            skLineSegment(sketch, "E4056", {"start": v(-37.95, 17.04) * mm, "end": v(-38.12, 17.07) * mm});
            skLineSegment(sketch, "E4057", {"start": v(-38.12, 17.07) * mm, "end": v(-38.3, 17.1) * mm});
            skLineSegment(sketch, "E4058", {"start": v(-38.3, 17.1) * mm, "end": v(-38.47, 17.12) * mm});
            skLineSegment(sketch, "E4059", {"start": v(-38.47, 17.12) * mm, "end": v(-38.65, 17.14) * mm});
            skLineSegment(sketch, "E4060", {"start": v(-38.65, 17.14) * mm, "end": v(-38.84, 17.15) * mm});
            skLineSegment(sketch, "E4061", {"start": v(-38.84, 17.15) * mm, "end": v(-39.01, 17.17) * mm});
            skLineSegment(sketch, "E4062", {"start": v(-39.01, 17.17) * mm, "end": v(-39.19, 17.18) * mm});
            skLineSegment(sketch, "E4063", {"start": v(-39.19, 17.18) * mm, "end": v(-39.37, 17.19) * mm});
            skLineSegment(sketch, "E4064", {"start": v(-39.37, 17.19) * mm, "end": v(-39.56, 17.2) * mm});
            skLineSegment(sketch, "E4065", {"start": v(-39.56, 17.2) * mm, "end": v(-39.75, 17.2) * mm});
            skLineSegment(sketch, "E4066", {"start": v(-39.75, 17.2) * mm, "end": v(-39.93, 17.2) * mm});
            skLineSegment(sketch, "E4067", {"start": v(-39.93, 17.2) * mm, "end": v(-40.1, 17.2) * mm});
            skLineSegment(sketch, "E4068", {"start": v(-40.1, 17.2) * mm, "end": v(-40.16, 17.2) * mm});
            skLineSegment(sketch, "E4069", {"start": v(-40.16, 17.2) * mm, "end": v(-40.34, 17.2) * mm});
            skLineSegment(sketch, "E4070", {"start": v(-40.34, 17.2) * mm, "end": v(-40.53, 17.2) * mm});
            skLineSegment(sketch, "E4071", {"start": v(-40.53, 17.2) * mm, "end": v(-40.72, 17.2) * mm});
            skLineSegment(sketch, "E4072", {"start": v(-40.72, 17.2) * mm, "end": v(-40.92, 17.2) * mm});
            skLineSegment(sketch, "E4073", {"start": v(-40.92, 17.2) * mm, "end": v(-41.12, 17.18) * mm});
            skLineSegment(sketch, "E4074", {"start": v(-41.12, 17.18) * mm, "end": v(-41.19, 17.18) * mm});
            skLineSegment(sketch, "E4075", {"start": v(-41.19, 17.18) * mm, "end": v(-41.26, 17) * mm});
            skLineSegment(sketch, "E4076", {"start": v(-41.26, 17) * mm, "end": v(-41.33, 16.84) * mm});
            skLineSegment(sketch, "E4077", {"start": v(-41.33, 16.84) * mm, "end": v(-41.4, 16.67) * mm});
            skLineSegment(sketch, "E4078", {"start": v(-41.4, 16.67) * mm, "end": v(-41.47, 16.5) * mm});
            skLineSegment(sketch, "E4079", {"start": v(-41.47, 16.5) * mm, "end": v(-41.5, 16.41) * mm});
            skLineSegment(sketch, "E4080", {"start": v(-41.5, 16.41) * mm, "end": v(-41.37, 16.27) * mm});
            skLineSegment(sketch, "E4081", {"start": v(-41.37, 16.27) * mm, "end": v(-41.24, 16.14) * mm});
            skLineSegment(sketch, "E4082", {"start": v(-41.24, 16.14) * mm, "end": v(-41.12, 16.01) * mm});
            skLineSegment(sketch, "E4083", {"start": v(-41.12, 16.01) * mm, "end": v(-41, 15.89) * mm});
            skLineSegment(sketch, "E4084", {"start": v(-41, 15.89) * mm, "end": v(-40.88, 15.77) * mm});
            skLineSegment(sketch, "E4085", {"start": v(-40.88, 15.77) * mm, "end": v(-40.74, 15.63) * mm});
            skLineSegment(sketch, "E4086", {"start": v(-40.74, 15.63) * mm, "end": v(-40.6, 15.5) * mm});
            skLineSegment(sketch, "E4087", {"start": v(-40.6, 15.5) * mm, "end": v(-40.47, 15.37) * mm});
            skLineSegment(sketch, "E4088", {"start": v(-40.47, 15.37) * mm, "end": v(-40.33, 15.25) * mm});
            skLineSegment(sketch, "E4089", {"start": v(-40.33, 15.25) * mm, "end": v(-40.18, 15.12) * mm});
            skLineSegment(sketch, "E4090", {"start": v(-40.18, 15.12) * mm, "end": v(-40.04, 15) * mm});
            skLineSegment(sketch, "E4091", {"start": v(-40.04, 15) * mm, "end": v(-39.9, 14.88) * mm});
            skLineSegment(sketch, "E4092", {"start": v(-39.9, 14.88) * mm, "end": v(-39.76, 14.76) * mm});
            skLineSegment(sketch, "E4093", {"start": v(-39.76, 14.76) * mm, "end": v(-39.6, 14.64) * mm});
            skLineSegment(sketch, "E4094", {"start": v(-39.6, 14.64) * mm, "end": v(-39.46, 14.53) * mm});
            skLineSegment(sketch, "E4095", {"start": v(-39.46, 14.53) * mm, "end": v(-39.32, 14.42) * mm});
            skLineSegment(sketch, "E4096", {"start": v(-39.32, 14.42) * mm, "end": v(-39.17, 14.31) * mm});
            skLineSegment(sketch, "E4097", {"start": v(-39.17, 14.31) * mm, "end": v(-39.02, 14.2) * mm});
            skLineSegment(sketch, "E4098", {"start": v(-39.02, 14.2) * mm, "end": v(-38.85, 14.1) * mm});
            skLineSegment(sketch, "E4099", {"start": v(-38.85, 14.1) * mm, "end": v(-38.79, 14.05) * mm});
            skLineSegment(sketch, "E4100", {"start": v(-38.79, 14.05) * mm, "end": v(-38.85, 13.87) * mm});
            skLineSegment(sketch, "E4101", {"start": v(-38.85, 13.87) * mm, "end": v(-38.92, 13.68) * mm});
            skLineSegment(sketch, "E4102", {"start": v(-38.92, 13.68) * mm, "end": v(-38.98, 13.5) * mm});
            skLineSegment(sketch, "E4103", {"start": v(-38.98, 13.5) * mm, "end": v(-39.04, 13.32) * mm});
            skLineSegment(sketch, "E4104", {"start": v(-39.04, 13.32) * mm, "end": v(-39.1, 13.14) * mm});
            skLineSegment(sketch, "E4105", {"start": v(-39.1, 13.14) * mm, "end": v(-39.17, 12.95) * mm});
            skLineSegment(sketch, "E4106", {"start": v(-39.17, 12.95) * mm, "end": v(-39.23, 12.77) * mm});
            skLineSegment(sketch, "E4107", {"start": v(-39.23, 12.77) * mm, "end": v(-39.24, 12.74) * mm});
            skLineSegment(sketch, "E4108", {"start": v(-39.24, 12.74) * mm, "end": v(-39.41, 12.76) * mm});
            skLineSegment(sketch, "E4109", {"start": v(-39.41, 12.76) * mm, "end": v(-39.6, 12.77) * mm});
            skLineSegment(sketch, "E4110", {"start": v(-39.6, 12.77) * mm, "end": v(-39.77, 12.77) * mm});
            skLineSegment(sketch, "E4111", {"start": v(-39.77, 12.77) * mm, "end": v(-39.95, 12.78) * mm});
            skLineSegment(sketch, "E4112", {"start": v(-39.95, 12.78) * mm, "end": v(-40.12, 12.78) * mm});
            skLineSegment(sketch, "E4113", {"start": v(-40.12, 12.78) * mm, "end": v(-40.17, 12.78) * mm});
            skLineSegment(sketch, "E4114", {"start": v(-40.17, 12.78) * mm, "end": v(-40.35, 12.78) * mm});
            skLineSegment(sketch, "E4115", {"start": v(-40.35, 12.78) * mm, "end": v(-40.54, 12.77) * mm});
            skLineSegment(sketch, "E4116", {"start": v(-40.54, 12.77) * mm, "end": v(-40.71, 12.77) * mm});
            skLineSegment(sketch, "E4117", {"start": v(-40.71, 12.77) * mm, "end": v(-40.9, 12.76) * mm});
            skLineSegment(sketch, "E4118", {"start": v(-40.9, 12.76) * mm, "end": v(-41.07, 12.75) * mm});
            skLineSegment(sketch, "E4119", {"start": v(-41.07, 12.75) * mm, "end": v(-41.27, 12.74) * mm});
            skLineSegment(sketch, "E4120", {"start": v(-41.27, 12.74) * mm, "end": v(-41.46, 12.72) * mm});
            skLineSegment(sketch, "E4121", {"start": v(-41.46, 12.72) * mm, "end": v(-41.63, 12.7) * mm});
            skLineSegment(sketch, "E4122", {"start": v(-41.63, 12.7) * mm, "end": v(-41.81, 12.69) * mm});
            skLineSegment(sketch, "E4123", {"start": v(-41.81, 12.69) * mm, "end": v(-42, 12.66) * mm});
            skLineSegment(sketch, "E4124", {"start": v(-42, 12.66) * mm, "end": v(-42.18, 12.64) * mm});
            skLineSegment(sketch, "E4125", {"start": v(-42.18, 12.64) * mm, "end": v(-42.37, 12.62) * mm});
            skLineSegment(sketch, "E4126", {"start": v(-42.37, 12.62) * mm, "end": v(-42.56, 12.59) * mm});
            skLineSegment(sketch, "E4127", {"start": v(-42.56, 12.59) * mm, "end": v(-42.76, 12.56) * mm});
            skLineSegment(sketch, "E4128", {"start": v(-42.76, 12.56) * mm, "end": v(-42.83, 12.54) * mm});
            skLineSegment(sketch, "E4129", {"start": v(-42.83, 12.54) * mm, "end": v(-42.88, 12.37) * mm});
            skLineSegment(sketch, "E4130", {"start": v(-42.88, 12.37) * mm, "end": v(-42.93, 12.19) * mm});
            skLineSegment(sketch, "E4131", {"start": v(-42.93, 12.19) * mm, "end": v(-42.98, 12.01) * mm});
            skLineSegment(sketch, "E4132", {"start": v(-42.98, 12.01) * mm, "end": v(-43.03, 11.83) * mm});
            skLineSegment(sketch, "E4133", {"start": v(-43.03, 11.83) * mm, "end": v(-43.05, 11.75) * mm});
            skLineSegment(sketch, "E4134", {"start": v(-43.05, 11.75) * mm, "end": v(-42.9, 11.62) * mm});
            skLineSegment(sketch, "E4135", {"start": v(-42.9, 11.62) * mm, "end": v(-42.77, 11.5) * mm});
            skLineSegment(sketch, "E4136", {"start": v(-42.77, 11.5) * mm, "end": v(-42.63, 11.4) * mm});
            skLineSegment(sketch, "E4137", {"start": v(-42.63, 11.4) * mm, "end": v(-42.5, 11.28) * mm});
            skLineSegment(sketch, "E4138", {"start": v(-42.5, 11.28) * mm, "end": v(-42.36, 11.17) * mm});
            skLineSegment(sketch, "E4139", {"start": v(-42.36, 11.17) * mm, "end": v(-42.21, 11.06) * mm});
            skLineSegment(sketch, "E4140", {"start": v(-42.21, 11.06) * mm, "end": v(-42.06, 10.94) * mm});
            skLineSegment(sketch, "E4141", {"start": v(-42.06, 10.94) * mm, "end": v(-41.91, 10.83) * mm});
            skLineSegment(sketch, "E4142", {"start": v(-41.91, 10.83) * mm, "end": v(-41.76, 10.72) * mm});
            skLineSegment(sketch, "E4143", {"start": v(-41.76, 10.72) * mm, "end": v(-41.6, 10.6) * mm});
            skLineSegment(sketch, "E4144", {"start": v(-41.6, 10.6) * mm, "end": v(-41.45, 10.5) * mm});
            skLineSegment(sketch, "E4145", {"start": v(-41.45, 10.5) * mm, "end": v(-41.3, 10.4) * mm});
            skLineSegment(sketch, "E4146", {"start": v(-41.3, 10.4) * mm, "end": v(-41.14, 10.3) * mm});
            skLineSegment(sketch, "E4147", {"start": v(-41.14, 10.3) * mm, "end": v(-40.98, 10.2) * mm});
            skLineSegment(sketch, "E4148", {"start": v(-40.98, 10.2) * mm, "end": v(-40.82, 10.1) * mm});
            skLineSegment(sketch, "E4149", {"start": v(-40.82, 10.1) * mm, "end": v(-40.67, 10) * mm});
            skLineSegment(sketch, "E4150", {"start": v(-40.67, 10) * mm, "end": v(-40.5, 9.92) * mm});
            skLineSegment(sketch, "E4151", {"start": v(-40.5, 9.92) * mm, "end": v(-40.34, 9.82) * mm});
            skLineSegment(sketch, "E4152", {"start": v(-40.34, 9.82) * mm, "end": v(-40.17, 9.73) * mm});
            skLineSegment(sketch, "E4153", {"start": v(-40.17, 9.73) * mm, "end": v(-40.1, 9.7) * mm});
            skLineSegment(sketch, "E4154", {"start": v(-40.1, 9.7) * mm, "end": v(-40.14, 9.51) * mm});
            skLineSegment(sketch, "E4155", {"start": v(-40.14, 9.51) * mm, "end": v(-40.18, 9.32) * mm});
            skLineSegment(sketch, "E4156", {"start": v(-40.18, 9.32) * mm, "end": v(-40.23, 9.14) * mm});
            skLineSegment(sketch, "E4157", {"start": v(-40.23, 9.14) * mm, "end": v(-40.27, 8.94) * mm});
            skLineSegment(sketch, "E4158", {"start": v(-40.27, 8.94) * mm, "end": v(-40.31, 8.76) * mm});
            skLineSegment(sketch, "E4159", {"start": v(-40.31, 8.76) * mm, "end": v(-40.35, 8.56) * mm});
            skLineSegment(sketch, "E4160", {"start": v(-40.35, 8.56) * mm, "end": v(-40.4, 8.38) * mm});
            skLineSegment(sketch, "E4161", {"start": v(-40.4, 8.38) * mm, "end": v(-40.4, 8.35) * mm});
            skLineSegment(sketch, "E4162", {"start": v(-40.4, 8.35) * mm, "end": v(-40.57, 8.34) * mm});
            skLineSegment(sketch, "E4163", {"start": v(-40.57, 8.34) * mm, "end": v(-40.76, 8.33) * mm});
            skLineSegment(sketch, "E4164", {"start": v(-40.76, 8.33) * mm, "end": v(-40.93, 8.32) * mm});
            skLineSegment(sketch, "E4165", {"start": v(-40.93, 8.32) * mm, "end": v(-41.11, 8.3) * mm});
            skLineSegment(sketch, "E4166", {"start": v(-41.11, 8.3) * mm, "end": v(-41.29, 8.29) * mm});
            skLineSegment(sketch, "E4167", {"start": v(-41.29, 8.29) * mm, "end": v(-41.46, 8.27) * mm});
            skLineSegment(sketch, "E4168", {"start": v(-41.46, 8.27) * mm, "end": v(-41.65, 8.24) * mm});
            skLineSegment(sketch, "E4169", {"start": v(-41.65, 8.24) * mm, "end": v(-41.82, 8.22) * mm});
            skLineSegment(sketch, "E4170", {"start": v(-41.82, 8.22) * mm, "end": v(-42, 8.2) * mm});
            skLineSegment(sketch, "E4171", {"start": v(-42, 8.2) * mm, "end": v(-42.18, 8.16) * mm});
            skLineSegment(sketch, "E4172", {"start": v(-42.18, 8.16) * mm, "end": v(-42.36, 8.13) * mm});
            skLineSegment(sketch, "E4173", {"start": v(-42.36, 8.13) * mm, "end": v(-42.55, 8.1) * mm});
            skLineSegment(sketch, "E4174", {"start": v(-42.55, 8.1) * mm, "end": v(-42.72, 8.06) * mm});
            skLineSegment(sketch, "E4175", {"start": v(-42.72, 8.06) * mm, "end": v(-42.9, 8.02) * mm});
            skLineSegment(sketch, "E4176", {"start": v(-42.9, 8.02) * mm, "end": v(-43.07, 7.98) * mm});
            skLineSegment(sketch, "E4177", {"start": v(-43.07, 7.98) * mm, "end": v(-43.25, 7.94) * mm});
            skLineSegment(sketch, "E4178", {"start": v(-43.25, 7.94) * mm, "end": v(-43.43, 7.9) * mm});
            skLineSegment(sketch, "E4179", {"start": v(-43.43, 7.9) * mm, "end": v(-43.62, 7.85) * mm});
            skLineSegment(sketch, "E4180", {"start": v(-43.62, 7.85) * mm, "end": v(-43.81, 7.8) * mm});
            skLineSegment(sketch, "E4181", {"start": v(-43.81, 7.8) * mm, "end": v(-43.95, 7.76) * mm});
            skLineSegment(sketch, "E4182", {"start": v(-43.95, 7.76) * mm, "end": v(-43.98, 7.57) * mm});
            skLineSegment(sketch, "E4183", {"start": v(-43.98, 7.57) * mm, "end": v(-44, 7.4) * mm});
            skLineSegment(sketch, "E4184", {"start": v(-44, 7.4) * mm, "end": v(-44.04, 7.21) * mm});
            skLineSegment(sketch, "E4185", {"start": v(-44.04, 7.21) * mm, "end": v(-44.07, 7.03) * mm});
            skLineSegment(sketch, "E4186", {"start": v(-44.07, 7.03) * mm, "end": v(-44.08, 6.94) * mm});
            skLineSegment(sketch, "E4187", {"start": v(-44.08, 6.94) * mm, "end": v(-43.93, 6.83) * mm});
            skLineSegment(sketch, "E4188", {"start": v(-43.93, 6.83) * mm, "end": v(-43.77, 6.73) * mm});
            skLineSegment(sketch, "E4189", {"start": v(-43.77, 6.73) * mm, "end": v(-43.63, 6.63) * mm});
            skLineSegment(sketch, "E4190", {"start": v(-43.63, 6.63) * mm, "end": v(-43.48, 6.54) * mm});
            skLineSegment(sketch, "E4191", {"start": v(-43.48, 6.54) * mm, "end": v(-43.33, 6.45) * mm});
            skLineSegment(sketch, "E4192", {"start": v(-43.33, 6.45) * mm, "end": v(-43.17, 6.35) * mm});
            skLineSegment(sketch, "E4193", {"start": v(-43.17, 6.35) * mm, "end": v(-43.01, 6.25) * mm});
            skLineSegment(sketch, "E4194", {"start": v(-43.01, 6.25) * mm, "end": v(-42.85, 6.15) * mm});
            skLineSegment(sketch, "E4195", {"start": v(-42.85, 6.15) * mm, "end": v(-42.68, 6.06) * mm});
            skLineSegment(sketch, "E4196", {"start": v(-42.68, 6.06) * mm, "end": v(-42.52, 5.97) * mm});
            skLineSegment(sketch, "E4197", {"start": v(-42.52, 5.97) * mm, "end": v(-42.35, 5.88) * mm});
            skLineSegment(sketch, "E4198", {"start": v(-42.35, 5.88) * mm, "end": v(-42.18, 5.8) * mm});
            skLineSegment(sketch, "E4199", {"start": v(-42.18, 5.8) * mm, "end": v(-42.02, 5.71) * mm});
            skLineSegment(sketch, "E4200", {"start": v(-42.02, 5.71) * mm, "end": v(-41.85, 5.63) * mm});
            skLineSegment(sketch, "E4201", {"start": v(-41.85, 5.63) * mm, "end": v(-41.68, 5.55) * mm});
            skLineSegment(sketch, "E4202", {"start": v(-41.68, 5.55) * mm, "end": v(-41.52, 5.47) * mm});
            skLineSegment(sketch, "E4203", {"start": v(-41.52, 5.47) * mm, "end": v(-41.35, 5.4) * mm});
            skLineSegment(sketch, "E4204", {"start": v(-41.35, 5.4) * mm, "end": v(-41.18, 5.33) * mm});
            skLineSegment(sketch, "E4205", {"start": v(-41.18, 5.33) * mm, "end": v(-41, 5.26) * mm});
            skLineSegment(sketch, "E4206", {"start": v(-41, 5.26) * mm, "end": v(-40.92, 5.23) * mm});
            skLineSegment(sketch, "E4207", {"start": v(-40.92, 5.23) * mm, "end": v(-40.94, 5.04) * mm});
            skLineSegment(sketch, "E4208", {"start": v(-40.94, 5.04) * mm, "end": v(-40.97, 4.84) * mm});
            skLineSegment(sketch, "E4209", {"start": v(-40.97, 4.84) * mm, "end": v(-40.99, 4.66) * mm});
            skLineSegment(sketch, "E4210", {"start": v(-40.99, 4.66) * mm, "end": v(-41, 4.46) * mm});
            skLineSegment(sketch, "E4211", {"start": v(-41, 4.46) * mm, "end": v(-41.03, 4.27) * mm});
            skLineSegment(sketch, "E4212", {"start": v(-41.03, 4.27) * mm, "end": v(-41.05, 4.07) * mm});
            skLineSegment(sketch, "E4213", {"start": v(-41.05, 4.07) * mm, "end": v(-41.07, 3.89) * mm});
            skLineSegment(sketch, "E4214", {"start": v(-41.07, 3.89) * mm, "end": v(-41.08, 3.85) * mm});
            skLineSegment(sketch, "E4215", {"start": v(-41.08, 3.85) * mm, "end": v(-41.25, 3.83) * mm});
            skLineSegment(sketch, "E4216", {"start": v(-41.25, 3.83) * mm, "end": v(-41.42, 3.8) * mm});
            skLineSegment(sketch, "E4217", {"start": v(-41.42, 3.8) * mm, "end": v(-41.6, 3.77) * mm});
            skLineSegment(sketch, "E4218", {"start": v(-41.6, 3.77) * mm, "end": v(-41.78, 3.73) * mm});
            skLineSegment(sketch, "E4219", {"start": v(-41.78, 3.73) * mm, "end": v(-41.95, 3.7) * mm});
            skLineSegment(sketch, "E4220", {"start": v(-41.95, 3.7) * mm, "end": v(-42.12, 3.66) * mm});
            skLineSegment(sketch, "E4221", {"start": v(-42.12, 3.66) * mm, "end": v(-42.3, 3.61) * mm});
            skLineSegment(sketch, "E4222", {"start": v(-42.3, 3.61) * mm, "end": v(-42.47, 3.57) * mm});
            skLineSegment(sketch, "E4223", {"start": v(-42.47, 3.57) * mm, "end": v(-42.64, 3.52) * mm});
            skLineSegment(sketch, "E4224", {"start": v(-42.64, 3.52) * mm, "end": v(-42.82, 3.47) * mm});
            skLineSegment(sketch, "E4225", {"start": v(-42.82, 3.47) * mm, "end": v(-43, 3.42) * mm});
            skLineSegment(sketch, "E4226", {"start": v(-43, 3.42) * mm, "end": v(-43.18, 3.36) * mm});
            skLineSegment(sketch, "E4227", {"start": v(-43.18, 3.36) * mm, "end": v(-43.35, 3.31) * mm});
            skLineSegment(sketch, "E4228", {"start": v(-43.35, 3.31) * mm, "end": v(-43.52, 3.25) * mm});
            skLineSegment(sketch, "E4229", {"start": v(-43.52, 3.25) * mm, "end": v(-43.69, 3.2) * mm});
            skLineSegment(sketch, "E4230", {"start": v(-43.69, 3.2) * mm, "end": v(-43.86, 3.13) * mm});
            skLineSegment(sketch, "E4231", {"start": v(-43.86, 3.13) * mm, "end": v(-44.04, 3.07) * mm});
            skLineSegment(sketch, "E4232", {"start": v(-44.04, 3.07) * mm, "end": v(-44.22, 3) * mm});
            skLineSegment(sketch, "E4233", {"start": v(-44.22, 3) * mm, "end": v(-44.4, 2.93) * mm});
            skLineSegment(sketch, "E4234", {"start": v(-44.4, 2.93) * mm, "end": v(-44.53, 2.88) * mm});
            skLineSegment(sketch, "E4235", {"start": v(-44.53, 2.88) * mm, "end": v(-44.54, 2.7) * mm});
            skLineSegment(sketch, "E4236", {"start": v(-44.54, 2.7) * mm, "end": v(-44.56, 2.5) * mm});
            skLineSegment(sketch, "E4237", {"start": v(-44.56, 2.5) * mm, "end": v(-44.57, 2.32) * mm});
            skLineSegment(sketch, "E4238", {"start": v(-44.57, 2.32) * mm, "end": v(-44.57, 2.14) * mm});
            skLineSegment(sketch, "E4239", {"start": v(-44.57, 2.14) * mm, "end": v(-44.58, 2.05) * mm});
            skLineSegment(sketch, "E4240", {"start": v(-44.58, 2.05) * mm, "end": v(-44.41, 1.96) * mm});
            skLineSegment(sketch, "E4241", {"start": v(-44.41, 1.96) * mm, "end": v(-44.25, 1.87) * mm});
            skLineSegment(sketch, "E4242", {"start": v(-44.25, 1.87) * mm, "end": v(-44.1, 1.8) * mm});
            skLineSegment(sketch, "E4243", {"start": v(-44.1, 1.8) * mm, "end": v(-43.93, 1.71) * mm});
            skLineSegment(sketch, "E4244", {"start": v(-43.93, 1.71) * mm, "end": v(-43.78, 1.64) * mm});
            skLineSegment(sketch, "E4245", {"start": v(-43.78, 1.64) * mm, "end": v(-43.6, 1.56) * mm});
            skLineSegment(sketch, "E4246", {"start": v(-43.6, 1.56) * mm, "end": v(-43.44, 1.48) * mm});
            skLineSegment(sketch, "E4247", {"start": v(-43.44, 1.48) * mm, "end": v(-43.26, 1.4) * mm});
            skLineSegment(sketch, "E4248", {"start": v(-43.26, 1.4) * mm, "end": v(-43.1, 1.33) * mm});
            skLineSegment(sketch, "E4249", {"start": v(-43.1, 1.33) * mm, "end": v(-42.92, 1.25) * mm});
            skLineSegment(sketch, "E4250", {"start": v(-42.92, 1.25) * mm, "end": v(-42.74, 1.18) * mm});
            skLineSegment(sketch, "E4251", {"start": v(-42.74, 1.18) * mm, "end": v(-42.57, 1.12) * mm});
            skLineSegment(sketch, "E4252", {"start": v(-42.57, 1.12) * mm, "end": v(-42.4, 1.05) * mm});
            skLineSegment(sketch, "E4253", {"start": v(-42.4, 1.05) * mm, "end": v(-42.22, 0.99) * mm});
            skLineSegment(sketch, "E4254", {"start": v(-42.22, 0.99) * mm, "end": v(-42.04, 0.93) * mm});
            skLineSegment(sketch, "E4255", {"start": v(-42.04, 0.93) * mm, "end": v(-41.87, 0.87) * mm});
            skLineSegment(sketch, "E4256", {"start": v(-41.87, 0.87) * mm, "end": v(-41.7, 0.82) * mm});
            skLineSegment(sketch, "E4257", {"start": v(-41.7, 0.82) * mm, "end": v(-41.51, 0.77) * mm});
            skLineSegment(sketch, "E4258", {"start": v(-41.51, 0.77) * mm, "end": v(-41.32, 0.71) * mm});
            skLineSegment(sketch, "E4259", {"start": v(-41.32, 0.71) * mm, "end": v(-41.25, 0.7) * mm});
            skLineSegment(sketch, "E4260", {"start": v(-41.25, 0.7) * mm, "end": v(-41.25, 0.5) * mm});
            skLineSegment(sketch, "E4261", {"start": v(-41.25, 0.5) * mm, "end": v(-41.25, 0.3) * mm});
            skLineSegment(sketch, "E4262", {"start": v(-41.25, 0.3) * mm, "end": v(-41.25, 0.12) * mm});
            skLineSegment(sketch, "E4263", {"start": v(-41.25, 0.12) * mm, "end": v(-41.25, -0.08) * mm});
            skLineSegment(sketch, "E4264", {"start": v(-41.25, -0.08) * mm, "end": v(-41.25, -0.27) * mm});
            skLineSegment(sketch, "E4265", {"start": v(-41.25, -0.27) * mm, "end": v(-41.25, -0.47) * mm});
            skLineSegment(sketch, "E4266", {"start": v(-41.25, -0.47) * mm, "end": v(-41.25, -0.65) * mm});
            skLineSegment(sketch, "E4267", {"start": v(-41.25, -0.65) * mm, "end": v(-41.25, -0.69) * mm});
            skLineSegment(sketch, "E4268", {"start": v(-41.25, -0.69) * mm, "end": v(-41.42, -0.73) * mm});
            skLineSegment(sketch, "E4269", {"start": v(-41.42, -0.73) * mm, "end": v(-41.6, -0.78) * mm});
            skLineSegment(sketch, "E4270", {"start": v(-41.6, -0.78) * mm, "end": v(-41.76, -0.83) * mm});
            skLineSegment(sketch, "E4271", {"start": v(-41.76, -0.83) * mm, "end": v(-41.93, -0.89) * mm});
            skLineSegment(sketch, "E4272", {"start": v(-41.93, -0.89) * mm, "end": v(-42.1, -0.94) * mm});
            skLineSegment(sketch, "E4273", {"start": v(-42.1, -0.94) * mm, "end": v(-42.27, -1) * mm});
            skLineSegment(sketch, "E4274", {"start": v(-42.27, -1) * mm, "end": v(-42.44, -1.06) * mm});
            skLineSegment(sketch, "E4275", {"start": v(-42.44, -1.06) * mm, "end": v(-42.6, -1.12) * mm});
            skLineSegment(sketch, "E4276", {"start": v(-42.6, -1.12) * mm, "end": v(-42.77, -1.19) * mm});
            skLineSegment(sketch, "E4277", {"start": v(-42.77, -1.19) * mm, "end": v(-42.94, -1.26) * mm});
            skLineSegment(sketch, "E4278", {"start": v(-42.94, -1.26) * mm, "end": v(-43.11, -1.33) * mm});
            skLineSegment(sketch, "E4279", {"start": v(-43.11, -1.33) * mm, "end": v(-43.3, -1.4) * mm});
            skLineSegment(sketch, "E4280", {"start": v(-43.3, -1.4) * mm, "end": v(-43.45, -1.48) * mm});
            skLineSegment(sketch, "E4281", {"start": v(-43.45, -1.48) * mm, "end": v(-43.6, -1.55) * mm});
            skLineSegment(sketch, "E4282", {"start": v(-43.6, -1.55) * mm, "end": v(-43.77, -1.63) * mm});
            skLineSegment(sketch, "E4283", {"start": v(-43.77, -1.63) * mm, "end": v(-43.94, -1.7) * mm});
            skLineSegment(sketch, "E4284", {"start": v(-43.94, -1.7) * mm, "end": v(-44.1, -1.8) * mm});
            skLineSegment(sketch, "E4285", {"start": v(-44.1, -1.8) * mm, "end": v(-44.28, -1.88) * mm});
            skLineSegment(sketch, "E4286", {"start": v(-44.28, -1.88) * mm, "end": v(-44.46, -1.98) * mm});
            skLineSegment(sketch, "E4287", {"start": v(-44.46, -1.98) * mm, "end": v(-44.58, -2.04) * mm});
            skLineSegment(sketch, "E4288", {"start": v(-44.58, -2.04) * mm, "end": v(-44.57, -2.23) * mm});
            skLineSegment(sketch, "E4289", {"start": v(-44.57, -2.23) * mm, "end": v(-44.56, -2.41) * mm});
            skLineSegment(sketch, "E4290", {"start": v(-44.56, -2.41) * mm, "end": v(-44.55, -2.6) * mm});
            skLineSegment(sketch, "E4291", {"start": v(-44.55, -2.6) * mm, "end": v(-44.54, -2.78) * mm});
            skLineSegment(sketch, "E4292", {"start": v(-44.54, -2.78) * mm, "end": v(-44.53, -2.87) * mm});
            skLineSegment(sketch, "E4293", {"start": v(-44.53, -2.87) * mm, "end": v(-44.36, -2.94) * mm});
            skLineSegment(sketch, "E4294", {"start": v(-44.36, -2.94) * mm, "end": v(-44.19, -3) * mm});
            skLineSegment(sketch, "E4295", {"start": v(-44.19, -3) * mm, "end": v(-44.02, -3.07) * mm});
            skLineSegment(sketch, "E4296", {"start": v(-44.02, -3.07) * mm, "end": v(-43.86, -3.13) * mm});
            skLineSegment(sketch, "E4297", {"start": v(-43.86, -3.13) * mm, "end": v(-43.7, -3.19) * mm});
            skLineSegment(sketch, "E4298", {"start": v(-43.7, -3.19) * mm, "end": v(-43.52, -3.25) * mm});
            skLineSegment(sketch, "E4299", {"start": v(-43.52, -3.25) * mm, "end": v(-43.34, -3.3) * mm});
            skLineSegment(sketch, "E4300", {"start": v(-43.34, -3.3) * mm, "end": v(-43.15, -3.37) * mm});
            skLineSegment(sketch, "E4301", {"start": v(-43.15, -3.37) * mm, "end": v(-42.97, -3.42) * mm});
            skLineSegment(sketch, "E4302", {"start": v(-42.97, -3.42) * mm, "end": v(-42.8, -3.47) * mm});
            skLineSegment(sketch, "E4303", {"start": v(-42.8, -3.47) * mm, "end": v(-42.61, -3.52) * mm});
            skLineSegment(sketch, "E4304", {"start": v(-42.61, -3.52) * mm, "end": v(-42.43, -3.57) * mm});
            skLineSegment(sketch, "E4305", {"start": v(-42.43, -3.57) * mm, "end": v(-42.26, -3.62) * mm});
            skLineSegment(sketch, "E4306", {"start": v(-42.26, -3.62) * mm, "end": v(-42.07, -3.66) * mm});
            skLineSegment(sketch, "E4307", {"start": v(-42.07, -3.66) * mm, "end": v(-41.89, -3.7) * mm});
            skLineSegment(sketch, "E4308", {"start": v(-41.89, -3.7) * mm, "end": v(-41.72, -3.74) * mm});
            skLineSegment(sketch, "E4309", {"start": v(-41.72, -3.74) * mm, "end": v(-41.53, -3.77) * mm});
            skLineSegment(sketch, "E4310", {"start": v(-41.53, -3.77) * mm, "end": v(-41.34, -3.8) * mm});
            skLineSegment(sketch, "E4311", {"start": v(-41.34, -3.8) * mm, "end": v(-41.15, -3.84) * mm});
            skLineSegment(sketch, "E4312", {"start": v(-41.15, -3.84) * mm, "end": v(-41.07, -3.85) * mm});
            skLineSegment(sketch, "E4313", {"start": v(-41.07, -3.85) * mm, "end": v(-41.05, -4.03) * mm});
            skLineSegment(sketch, "E4314", {"start": v(-41.05, -4.03) * mm, "end": v(-41.03, -4.23) * mm});
            skLineSegment(sketch, "E4315", {"start": v(-41.03, -4.23) * mm, "end": v(-41.01, -4.42) * mm});
            skLineSegment(sketch, "E4316", {"start": v(-41.01, -4.42) * mm, "end": v(-41, -4.62) * mm});
            skLineSegment(sketch, "E4317", {"start": v(-41, -4.62) * mm, "end": v(-40.97, -4.8) * mm});
            skLineSegment(sketch, "E4318", {"start": v(-40.97, -4.8) * mm, "end": v(-40.95, -5) * mm});
            skLineSegment(sketch, "E4319", {"start": v(-40.95, -5) * mm, "end": v(-40.93, -5.19) * mm});
            skLineSegment(sketch, "E4320", {"start": v(-40.93, -5.19) * mm, "end": v(-40.92, -5.22) * mm});
            skLineSegment(sketch, "E4321", {"start": v(-40.92, -5.22) * mm, "end": v(-41.08, -5.28) * mm});
            skLineSegment(sketch, "E4322", {"start": v(-41.08, -5.28) * mm, "end": v(-41.25, -5.35) * mm});
            skLineSegment(sketch, "E4323", {"start": v(-41.25, -5.35) * mm, "end": v(-41.41, -5.42) * mm});
            skLineSegment(sketch, "E4324", {"start": v(-41.41, -5.42) * mm, "end": v(-41.58, -5.5) * mm});
            skLineSegment(sketch, "E4325", {"start": v(-41.58, -5.5) * mm, "end": v(-41.74, -5.57) * mm});
            skLineSegment(sketch, "E4326", {"start": v(-41.74, -5.57) * mm, "end": v(-41.9, -5.64) * mm});
            skLineSegment(sketch, "E4327", {"start": v(-41.9, -5.64) * mm, "end": v(-42.07, -5.73) * mm});
            skLineSegment(sketch, "E4328", {"start": v(-42.07, -5.73) * mm, "end": v(-42.22, -5.8) * mm});
            skLineSegment(sketch, "E4329", {"start": v(-42.22, -5.8) * mm, "end": v(-42.38, -5.89) * mm});
            skLineSegment(sketch, "E4330", {"start": v(-42.38, -5.89) * mm, "end": v(-42.54, -5.97) * mm});
            skLineSegment(sketch, "E4331", {"start": v(-42.54, -5.97) * mm, "end": v(-42.7, -6.06) * mm});
            skLineSegment(sketch, "E4332", {"start": v(-42.7, -6.06) * mm, "end": v(-42.87, -6.16) * mm});
            skLineSegment(sketch, "E4333", {"start": v(-42.87, -6.16) * mm, "end": v(-43.02, -6.25) * mm});
            skLineSegment(sketch, "E4334", {"start": v(-43.02, -6.25) * mm, "end": v(-43.17, -6.34) * mm});
            skLineSegment(sketch, "E4335", {"start": v(-43.17, -6.34) * mm, "end": v(-43.33, -6.43) * mm});
            skLineSegment(sketch, "E4336", {"start": v(-43.33, -6.43) * mm, "end": v(-43.48, -6.53) * mm});
            skLineSegment(sketch, "E4337", {"start": v(-43.48, -6.53) * mm, "end": v(-43.64, -6.64) * mm});
            skLineSegment(sketch, "E4338", {"start": v(-43.64, -6.64) * mm, "end": v(-43.8, -6.74) * mm});
            skLineSegment(sketch, "E4339", {"start": v(-43.8, -6.74) * mm, "end": v(-43.97, -6.85) * mm});
            skLineSegment(sketch, "E4340", {"start": v(-43.97, -6.85) * mm, "end": v(-44.08, -6.93) * mm});
            skLineSegment(sketch, "E4341", {"start": v(-44.08, -6.93) * mm, "end": v(-44.05, -7.12) * mm});
            skLineSegment(sketch, "E4342", {"start": v(-44.05, -7.12) * mm, "end": v(-44.02, -7.3) * mm});
            skLineSegment(sketch, "E4343", {"start": v(-44.02, -7.3) * mm, "end": v(-44, -7.48) * mm});
            skLineSegment(sketch, "E4344", {"start": v(-44, -7.48) * mm, "end": v(-43.96, -7.66) * mm});
            skLineSegment(sketch, "E4345", {"start": v(-43.96, -7.66) * mm, "end": v(-43.95, -7.75) * mm});
            skLineSegment(sketch, "E4346", {"start": v(-43.95, -7.75) * mm, "end": v(-43.76, -7.8) * mm});
            skLineSegment(sketch, "E4347", {"start": v(-43.76, -7.8) * mm, "end": v(-43.59, -7.85) * mm});
            skLineSegment(sketch, "E4348", {"start": v(-43.59, -7.85) * mm, "end": v(-43.41, -7.9) * mm});
            skLineSegment(sketch, "E4349", {"start": v(-43.41, -7.9) * mm, "end": v(-43.24, -7.93) * mm});
            skLineSegment(sketch, "E4350", {"start": v(-43.24, -7.93) * mm, "end": v(-43.08, -7.97) * mm});
            skLineSegment(sketch, "E4351", {"start": v(-43.08, -7.97) * mm, "end": v(-42.9, -8.01) * mm});
            skLineSegment(sketch, "E4352", {"start": v(-42.9, -8.01) * mm, "end": v(-42.71, -8.05) * mm});
            skLineSegment(sketch, "E4353", {"start": v(-42.71, -8.05) * mm, "end": v(-42.52, -8.1) * mm});
            skLineSegment(sketch, "E4354", {"start": v(-42.52, -8.1) * mm, "end": v(-42.34, -8.13) * mm});
            skLineSegment(sketch, "E4355", {"start": v(-42.34, -8.13) * mm, "end": v(-42.15, -8.16) * mm});
            skLineSegment(sketch, "E4356", {"start": v(-42.15, -8.16) * mm, "end": v(-41.96, -8.2) * mm});
            skLineSegment(sketch, "E4357", {"start": v(-41.96, -8.2) * mm, "end": v(-41.78, -8.22) * mm});
            skLineSegment(sketch, "E4358", {"start": v(-41.78, -8.22) * mm, "end": v(-41.6, -8.24) * mm});
            skLineSegment(sketch, "E4359", {"start": v(-41.6, -8.24) * mm, "end": v(-41.4, -8.27) * mm});
            skLineSegment(sketch, "E4360", {"start": v(-41.4, -8.27) * mm, "end": v(-41.23, -8.29) * mm});
            skLineSegment(sketch, "E4361", {"start": v(-41.23, -8.29) * mm, "end": v(-41.05, -8.3) * mm});
            skLineSegment(sketch, "E4362", {"start": v(-41.05, -8.3) * mm, "end": v(-40.86, -8.32) * mm});
            skLineSegment(sketch, "E4363", {"start": v(-40.86, -8.32) * mm, "end": v(-40.67, -8.33) * mm});
            skLineSegment(sketch, "E4364", {"start": v(-40.67, -8.33) * mm, "end": v(-40.48, -8.34) * mm});
            skLineSegment(sketch, "E4365", {"start": v(-40.48, -8.34) * mm, "end": v(-40.4, -8.34) * mm});
            skLineSegment(sketch, "E4366", {"start": v(-40.4, -8.34) * mm, "end": v(-40.36, -8.53) * mm});
            skLineSegment(sketch, "E4367", {"start": v(-40.36, -8.53) * mm, "end": v(-40.32, -8.72) * mm});
            skLineSegment(sketch, "E4368", {"start": v(-40.32, -8.72) * mm, "end": v(-40.28, -8.9) * mm});
            skLineSegment(sketch, "E4369", {"start": v(-40.28, -8.9) * mm, "end": v(-40.23, -9.1) * mm});
            skLineSegment(sketch, "E4370", {"start": v(-40.23, -9.1) * mm, "end": v(-40.2, -9.28) * mm});
            skLineSegment(sketch, "E4371", {"start": v(-40.2, -9.28) * mm, "end": v(-40.15, -9.48) * mm});
            skLineSegment(sketch, "E4372", {"start": v(-40.15, -9.48) * mm, "end": v(-40.1, -9.66) * mm});
            skLineSegment(sketch, "E4373", {"start": v(-40.1, -9.66) * mm, "end": v(-40.1, -9.7) * mm});
            skLineSegment(sketch, "E4374", {"start": v(-40.1, -9.7) * mm, "end": v(-40.25, -9.77) * mm});
            skLineSegment(sketch, "E4375", {"start": v(-40.25, -9.77) * mm, "end": v(-40.41, -9.86) * mm});
            skLineSegment(sketch, "E4376", {"start": v(-40.41, -9.86) * mm, "end": v(-40.57, -9.94) * mm});
            skLineSegment(sketch, "E4377", {"start": v(-40.57, -9.94) * mm, "end": v(-40.72, -10.03) * mm});
            skLineSegment(sketch, "E4378", {"start": v(-40.72, -10.03) * mm, "end": v(-40.87, -10.12) * mm});
            skLineSegment(sketch, "E4379", {"start": v(-40.87, -10.12) * mm, "end": v(-41.03, -10.22) * mm});
            skLineSegment(sketch, "E4380", {"start": v(-41.03, -10.22) * mm, "end": v(-41.18, -10.32) * mm});
            skLineSegment(sketch, "E4381", {"start": v(-41.18, -10.32) * mm, "end": v(-41.33, -10.41) * mm});
            skLineSegment(sketch, "E4382", {"start": v(-41.33, -10.41) * mm, "end": v(-41.47, -10.51) * mm});
            skLineSegment(sketch, "E4383", {"start": v(-41.47, -10.51) * mm, "end": v(-41.62, -10.62) * mm});
            skLineSegment(sketch, "E4384", {"start": v(-41.62, -10.62) * mm, "end": v(-41.78, -10.73) * mm});
            skLineSegment(sketch, "E4385", {"start": v(-41.78, -10.73) * mm, "end": v(-41.94, -10.84) * mm});
            skLineSegment(sketch, "E4386", {"start": v(-41.94, -10.84) * mm, "end": v(-42.07, -10.94) * mm});
            skLineSegment(sketch, "E4387", {"start": v(-42.07, -10.94) * mm, "end": v(-42.21, -11.05) * mm});
            skLineSegment(sketch, "E4388", {"start": v(-42.21, -11.05) * mm, "end": v(-42.36, -11.16) * mm});
            skLineSegment(sketch, "E4389", {"start": v(-42.36, -11.16) * mm, "end": v(-42.5, -11.28) * mm});
            skLineSegment(sketch, "E4390", {"start": v(-42.5, -11.28) * mm, "end": v(-42.65, -11.4) * mm});
            skLineSegment(sketch, "E4391", {"start": v(-42.65, -11.4) * mm, "end": v(-42.8, -11.52) * mm});
            skLineSegment(sketch, "E4392", {"start": v(-42.8, -11.52) * mm, "end": v(-42.95, -11.65) * mm});
            skLineSegment(sketch, "E4393", {"start": v(-42.95, -11.65) * mm, "end": v(-43.05, -11.74) * mm});
            skLineSegment(sketch, "E4394", {"start": v(-43.05, -11.74) * mm, "end": v(-43, -11.92) * mm});
            skLineSegment(sketch, "E4395", {"start": v(-43, -11.92) * mm, "end": v(-42.95, -12.1) * mm});
            skLineSegment(sketch, "E4396", {"start": v(-42.95, -12.1) * mm, "end": v(-42.9, -12.27) * mm});
            skLineSegment(sketch, "E4397", {"start": v(-42.9, -12.27) * mm, "end": v(-42.85, -12.45) * mm});
            skLineSegment(sketch, "E4398", {"start": v(-42.85, -12.45) * mm, "end": v(-42.83, -12.54) * mm});
            skLineSegment(sketch, "E4399", {"start": v(-42.83, -12.54) * mm, "end": v(-42.64, -12.57) * mm});
            skLineSegment(sketch, "E4400", {"start": v(-42.64, -12.57) * mm, "end": v(-42.46, -12.6) * mm});
            skLineSegment(sketch, "E4401", {"start": v(-42.46, -12.6) * mm, "end": v(-42.28, -12.62) * mm});
            skLineSegment(sketch, "E4402", {"start": v(-42.28, -12.62) * mm, "end": v(-42.1, -12.64) * mm});
            skLineSegment(sketch, "E4403", {"start": v(-42.1, -12.64) * mm, "end": v(-41.94, -12.66) * mm});
            skLineSegment(sketch, "E4404", {"start": v(-41.94, -12.66) * mm, "end": v(-41.75, -12.68) * mm});
            skLineSegment(sketch, "E4405", {"start": v(-41.75, -12.68) * mm, "end": v(-41.56, -12.7) * mm});
            skLineSegment(sketch, "E4406", {"start": v(-41.56, -12.7) * mm, "end": v(-41.37, -12.72) * mm});
            skLineSegment(sketch, "E4407", {"start": v(-41.37, -12.72) * mm, "end": v(-41.19, -12.74) * mm});
            skLineSegment(sketch, "E4408", {"start": v(-41.19, -12.74) * mm, "end": v(-41, -12.75) * mm});
            skLineSegment(sketch, "E4409", {"start": v(-41, -12.75) * mm, "end": v(-40.8, -12.76) * mm});
            skLineSegment(sketch, "E4410", {"start": v(-40.8, -12.76) * mm, "end": v(-40.62, -12.76) * mm});
            skLineSegment(sketch, "E4411", {"start": v(-40.62, -12.76) * mm, "end": v(-40.44, -12.77) * mm});
            skLineSegment(sketch, "E4412", {"start": v(-40.44, -12.77) * mm, "end": v(-40.25, -12.77) * mm});
            skLineSegment(sketch, "E4413", {"start": v(-40.25, -12.77) * mm, "end": v(-40.06, -12.77) * mm});
            skLineSegment(sketch, "E4414", {"start": v(-40.06, -12.77) * mm, "end": v(-39.89, -12.77) * mm});
            skLineSegment(sketch, "E4415", {"start": v(-39.89, -12.77) * mm, "end": v(-39.7, -12.76) * mm});
            skLineSegment(sketch, "E4416", {"start": v(-39.7, -12.76) * mm, "end": v(-39.51, -12.75) * mm});
            skLineSegment(sketch, "E4417", {"start": v(-39.51, -12.75) * mm, "end": v(-39.32, -12.74) * mm});
            skLineSegment(sketch, "E4418", {"start": v(-39.32, -12.74) * mm, "end": v(-39.23, -12.74) * mm});
            skLineSegment(sketch, "E4419", {"start": v(-39.23, -12.74) * mm, "end": v(-39.18, -12.91) * mm});
            skLineSegment(sketch, "E4420", {"start": v(-39.18, -12.91) * mm, "end": v(-39.11, -13.1) * mm});
            skLineSegment(sketch, "E4421", {"start": v(-39.11, -13.1) * mm, "end": v(-39.05, -13.28) * mm});
            skLineSegment(sketch, "E4422", {"start": v(-39.05, -13.28) * mm, "end": v(-38.99, -13.47) * mm});
            skLineSegment(sketch, "E4423", {"start": v(-38.99, -13.47) * mm, "end": v(-38.93, -13.65) * mm});
            skLineSegment(sketch, "E4424", {"start": v(-38.93, -13.65) * mm, "end": v(-38.86, -13.83) * mm});
            skLineSegment(sketch, "E4425", {"start": v(-38.86, -13.83) * mm, "end": v(-38.8, -14.01) * mm});
            skLineSegment(sketch, "E4426", {"start": v(-38.8, -14.01) * mm, "end": v(-38.8, -14.05) * mm});
            skLineSegment(sketch, "E4427", {"start": v(-38.8, -14.05) * mm, "end": v(-38.93, -14.14) * mm});
            skLineSegment(sketch, "E4428", {"start": v(-38.93, -14.14) * mm, "end": v(-39.08, -14.24) * mm});
            skLineSegment(sketch, "E4429", {"start": v(-39.08, -14.24) * mm, "end": v(-39.22, -14.34) * mm});
            skLineSegment(sketch, "E4430", {"start": v(-39.22, -14.34) * mm, "end": v(-39.37, -14.45) * mm});
            skLineSegment(sketch, "E4431", {"start": v(-39.37, -14.45) * mm, "end": v(-39.51, -14.56) * mm});
            skLineSegment(sketch, "E4432", {"start": v(-39.51, -14.56) * mm, "end": v(-39.65, -14.67) * mm});
            skLineSegment(sketch, "E4433", {"start": v(-39.65, -14.67) * mm, "end": v(-39.8, -14.79) * mm});
            skLineSegment(sketch, "E4434", {"start": v(-39.8, -14.79) * mm, "end": v(-39.93, -14.9) * mm});
            skLineSegment(sketch, "E4435", {"start": v(-39.93, -14.9) * mm, "end": v(-40.07, -15.01) * mm});
            skLineSegment(sketch, "E4436", {"start": v(-40.07, -15.01) * mm, "end": v(-40.2, -15.13) * mm});
            skLineSegment(sketch, "E4437", {"start": v(-40.2, -15.13) * mm, "end": v(-40.34, -15.26) * mm});
            skLineSegment(sketch, "E4438", {"start": v(-40.34, -15.26) * mm, "end": v(-40.49, -15.39) * mm});
            skLineSegment(sketch, "E4439", {"start": v(-40.49, -15.39) * mm, "end": v(-40.61, -15.5) * mm});
            skLineSegment(sketch, "E4440", {"start": v(-40.61, -15.5) * mm, "end": v(-40.74, -15.63) * mm});
            skLineSegment(sketch, "E4441", {"start": v(-40.74, -15.63) * mm, "end": v(-40.87, -15.75) * mm});
            skLineSegment(sketch, "E4442", {"start": v(-40.87, -15.75) * mm, "end": v(-41, -15.88) * mm});
            skLineSegment(sketch, "E4443", {"start": v(-41, -15.88) * mm, "end": v(-41.13, -16.02) * mm});
            skLineSegment(sketch, "E4444", {"start": v(-41.13, -16.02) * mm, "end": v(-41.27, -16.16) * mm});
            skLineSegment(sketch, "E4445", {"start": v(-41.27, -16.16) * mm, "end": v(-41.4, -16.3) * mm});
            skLineSegment(sketch, "E4446", {"start": v(-41.4, -16.3) * mm, "end": v(-41.5, -16.4) * mm});
            skLineSegment(sketch, "E4447", {"start": v(-41.5, -16.4) * mm, "end": v(-41.43, -16.58) * mm});
            skLineSegment(sketch, "E4448", {"start": v(-41.43, -16.58) * mm, "end": v(-41.36, -16.75) * mm});
            skLineSegment(sketch, "E4449", {"start": v(-41.36, -16.75) * mm, "end": v(-41.3, -16.92) * mm});
            skLineSegment(sketch, "E4450", {"start": v(-41.3, -16.92) * mm, "end": v(-41.22, -17.09) * mm});
            skLineSegment(sketch, "E4451", {"start": v(-41.22, -17.09) * mm, "end": v(-41.19, -17.17) * mm});
            skLineSegment(sketch, "E4452", {"start": v(-41.19, -17.17) * mm, "end": v(-41, -17.18) * mm});
            skLineSegment(sketch, "E4453", {"start": v(-41, -17.18) * mm, "end": v(-40.82, -17.19) * mm});
            skLineSegment(sketch, "E4454", {"start": v(-40.82, -17.19) * mm, "end": v(-40.64, -17.2) * mm});
            skLineSegment(sketch, "E4455", {"start": v(-40.64, -17.2) * mm, "end": v(-40.46, -17.2) * mm});
            skLineSegment(sketch, "E4456", {"start": v(-40.46, -17.2) * mm, "end": v(-40.3, -17.2) * mm});
            skLineSegment(sketch, "E4457", {"start": v(-40.3, -17.2) * mm, "end": v(-40.1, -17.2) * mm});
            skLineSegment(sketch, "E4458", {"start": v(-40.1, -17.2) * mm, "end": v(-39.91, -17.2) * mm});
            skLineSegment(sketch, "E4459", {"start": v(-39.91, -17.2) * mm, "end": v(-39.72, -17.2) * mm});
            skLineSegment(sketch, "E4460", {"start": v(-39.72, -17.2) * mm, "end": v(-39.53, -17.19) * mm});
            skLineSegment(sketch, "E4461", {"start": v(-39.53, -17.19) * mm, "end": v(-39.35, -17.18) * mm});
            skLineSegment(sketch, "E4462", {"start": v(-39.35, -17.18) * mm, "end": v(-39.16, -17.17) * mm});
            skLineSegment(sketch, "E4463", {"start": v(-39.16, -17.17) * mm, "end": v(-38.97, -17.16) * mm});
            skLineSegment(sketch, "E4464", {"start": v(-38.97, -17.16) * mm, "end": v(-38.8, -17.14) * mm});
            skLineSegment(sketch, "E4465", {"start": v(-38.8, -17.14) * mm, "end": v(-38.6, -17.12) * mm});
            skLineSegment(sketch, "E4466", {"start": v(-38.6, -17.12) * mm, "end": v(-38.42, -17.1) * mm});
            skLineSegment(sketch, "E4467", {"start": v(-38.42, -17.1) * mm, "end": v(-38.24, -17.08) * mm});
            skLineSegment(sketch, "E4468", {"start": v(-38.24, -17.08) * mm, "end": v(-38.05, -17.05) * mm});
            skLineSegment(sketch, "E4469", {"start": v(-38.05, -17.05) * mm, "end": v(-37.87, -17.02) * mm});
            skLineSegment(sketch, "E4470", {"start": v(-37.87, -17.02) * mm, "end": v(-37.67, -16.99) * mm});
            skLineSegment(sketch, "E4471", {"start": v(-37.67, -16.99) * mm, "end": v(-37.6, -16.97) * mm});
            skLineSegment(sketch, "E4472", {"start": v(-37.6, -16.97) * mm, "end": v(-37.52, -17.15) * mm});
            skLineSegment(sketch, "E4473", {"start": v(-37.52, -17.15) * mm, "end": v(-37.43, -17.33) * mm});
            skLineSegment(sketch, "E4474", {"start": v(-37.43, -17.33) * mm, "end": v(-37.35, -17.5) * mm});
            skLineSegment(sketch, "E4475", {"start": v(-37.35, -17.5) * mm, "end": v(-37.27, -17.68) * mm});
            skLineSegment(sketch, "E4476", {"start": v(-37.27, -17.68) * mm, "end": v(-37.19, -17.85) * mm});
            skLineSegment(sketch, "E4477", {"start": v(-37.19, -17.85) * mm, "end": v(-37.1, -18.02) * mm});
            skLineSegment(sketch, "E4478", {"start": v(-37.1, -18.02) * mm, "end": v(-37.02, -18.2) * mm});
            skLineSegment(sketch, "E4479", {"start": v(-37.02, -18.2) * mm, "end": v(-37.01, -18.23) * mm});
            skLineSegment(sketch, "E4480", {"start": v(-37.01, -18.23) * mm, "end": v(-37.14, -18.34) * mm});
            skLineSegment(sketch, "E4481", {"start": v(-37.14, -18.34) * mm, "end": v(-37.28, -18.46) * mm});
            skLineSegment(sketch, "E4482", {"start": v(-37.28, -18.46) * mm, "end": v(-37.4, -18.57) * mm});
            skLineSegment(sketch, "E4483", {"start": v(-37.4, -18.57) * mm, "end": v(-37.54, -18.7) * mm});
            skLineSegment(sketch, "E4484", {"start": v(-37.54, -18.7) * mm, "end": v(-37.67, -18.82) * mm});
            skLineSegment(sketch, "E4485", {"start": v(-37.67, -18.82) * mm, "end": v(-37.8, -18.94) * mm});
            skLineSegment(sketch, "E4486", {"start": v(-37.8, -18.94) * mm, "end": v(-37.93, -19.08) * mm});
            skLineSegment(sketch, "E4487", {"start": v(-37.93, -19.08) * mm, "end": v(-38.05, -19.2) * mm});
            skLineSegment(sketch, "E4488", {"start": v(-38.05, -19.2) * mm, "end": v(-38.17, -19.33) * mm});
            skLineSegment(sketch, "E4489", {"start": v(-38.17, -19.33) * mm, "end": v(-38.3, -19.46) * mm});
            skLineSegment(sketch, "E4490", {"start": v(-38.3, -19.46) * mm, "end": v(-38.42, -19.6) * mm});
            skLineSegment(sketch, "E4491", {"start": v(-38.42, -19.6) * mm, "end": v(-38.55, -19.75) * mm});
            skLineSegment(sketch, "E4492", {"start": v(-38.55, -19.75) * mm, "end": v(-38.66, -19.88) * mm});
            skLineSegment(sketch, "E4493", {"start": v(-38.66, -19.88) * mm, "end": v(-38.77, -20.01) * mm});
            skLineSegment(sketch, "E4494", {"start": v(-38.77, -20.01) * mm, "end": v(-38.89, -20.15) * mm});
            skLineSegment(sketch, "E4495", {"start": v(-38.89, -20.15) * mm, "end": v(-39, -20.3) * mm});
            skLineSegment(sketch, "E4496", {"start": v(-39, -20.3) * mm, "end": v(-39.12, -20.45) * mm});
            skLineSegment(sketch, "E4497", {"start": v(-39.12, -20.45) * mm, "end": v(-39.24, -20.6) * mm});
            skLineSegment(sketch, "E4498", {"start": v(-39.24, -20.6) * mm, "end": v(-39.36, -20.76) * mm});
            skLineSegment(sketch, "E4499", {"start": v(-39.36, -20.76) * mm, "end": v(-39.44, -20.87) * mm});
            skLineSegment(sketch, "E4500", {"start": v(-39.44, -20.87) * mm, "end": v(-39.36, -21.03) * mm});
            skLineSegment(sketch, "E4501", {"start": v(-39.36, -21.03) * mm, "end": v(-39.27, -21.2) * mm});
            skLineSegment(sketch, "E4502", {"start": v(-39.27, -21.2) * mm, "end": v(-39.18, -21.36) * mm});
            skLineSegment(sketch, "E4503", {"start": v(-39.18, -21.36) * mm, "end": v(-39.1, -21.52) * mm});
            skLineSegment(sketch, "E4504", {"start": v(-39.1, -21.52) * mm, "end": v(-39.05, -21.6) * mm});
            skLineSegment(sketch, "E4505", {"start": v(-39.05, -21.6) * mm, "end": v(-38.86, -21.59) * mm});
            skLineSegment(sketch, "E4506", {"start": v(-38.86, -21.59) * mm, "end": v(-38.68, -21.57) * mm});
            skLineSegment(sketch, "E4507", {"start": v(-38.68, -21.57) * mm, "end": v(-38.5, -21.56) * mm});
            skLineSegment(sketch, "E4508", {"start": v(-38.5, -21.56) * mm, "end": v(-38.32, -21.55) * mm});
            skLineSegment(sketch, "E4509", {"start": v(-38.32, -21.55) * mm, "end": v(-38.15, -21.53) * mm});
            skLineSegment(sketch, "E4510", {"start": v(-38.15, -21.53) * mm, "end": v(-37.97, -21.5) * mm});
            skLineSegment(sketch, "E4511", {"start": v(-37.97, -21.5) * mm, "end": v(-37.78, -21.49) * mm});
            skLineSegment(sketch, "E4512", {"start": v(-37.78, -21.49) * mm, "end": v(-37.59, -21.46) * mm});
            skLineSegment(sketch, "E4513", {"start": v(-37.59, -21.46) * mm, "end": v(-37.4, -21.43) * mm});
            skLineSegment(sketch, "E4514", {"start": v(-37.4, -21.43) * mm, "end": v(-37.22, -21.4) * mm});
            skLineSegment(sketch, "E4515", {"start": v(-37.22, -21.4) * mm, "end": v(-37.03, -21.37) * mm});
            skLineSegment(sketch, "E4516", {"start": v(-37.03, -21.37) * mm, "end": v(-36.85, -21.34) * mm});
            skLineSegment(sketch, "E4517", {"start": v(-36.85, -21.34) * mm, "end": v(-36.67, -21.3) * mm});
            skLineSegment(sketch, "E4518", {"start": v(-36.67, -21.3) * mm, "end": v(-36.48, -21.26) * mm});
            skLineSegment(sketch, "E4519", {"start": v(-36.48, -21.26) * mm, "end": v(-36.3, -21.22) * mm});
            skLineSegment(sketch, "E4520", {"start": v(-36.3, -21.22) * mm, "end": v(-36.13, -21.18) * mm});
            skLineSegment(sketch, "E4521", {"start": v(-36.13, -21.18) * mm, "end": v(-35.95, -21.14) * mm});
            skLineSegment(sketch, "E4522", {"start": v(-35.95, -21.14) * mm, "end": v(-35.76, -21.09) * mm});
            skLineSegment(sketch, "E4523", {"start": v(-35.76, -21.09) * mm, "end": v(-35.58, -21.03) * mm});
            skLineSegment(sketch, "E4524", {"start": v(-35.58, -21.03) * mm, "end": v(-35.5, -21) * mm});
            skLineSegment(sketch, "E4525", {"start": v(-35.5, -21) * mm, "end": v(-35.4, -21.17) * mm});
            skLineSegment(sketch, "E4526", {"start": v(-35.4, -21.17) * mm, "end": v(-35.3, -21.34) * mm});
            skLineSegment(sketch, "E4527", {"start": v(-35.3, -21.34) * mm, "end": v(-35.2, -21.5) * mm});
            skLineSegment(sketch, "E4528", {"start": v(-35.2, -21.5) * mm, "end": v(-35.1, -21.67) * mm});
            skLineSegment(sketch, "E4529", {"start": v(-35.1, -21.67) * mm, "end": v(-35, -21.83) * mm});
            skLineSegment(sketch, "E4530", {"start": v(-35, -21.83) * mm, "end": v(-34.9, -22) * mm});
            skLineSegment(sketch, "E4531", {"start": v(-34.9, -22) * mm, "end": v(-34.8, -22.16) * mm});
            skLineSegment(sketch, "E4532", {"start": v(-34.8, -22.16) * mm, "end": v(-34.78, -22.19) * mm});
            skLineSegment(sketch, "E4533", {"start": v(-34.78, -22.19) * mm, "end": v(-34.9, -22.31) * mm});
            skLineSegment(sketch, "E4534", {"start": v(-34.9, -22.31) * mm, "end": v(-35.02, -22.44) * mm});
            skLineSegment(sketch, "E4535", {"start": v(-35.02, -22.44) * mm, "end": v(-35.14, -22.57) * mm});
            skLineSegment(sketch, "E4536", {"start": v(-35.14, -22.57) * mm, "end": v(-35.26, -22.71) * mm});
            skLineSegment(sketch, "E4537", {"start": v(-35.26, -22.71) * mm, "end": v(-35.37, -22.85) * mm});
            skLineSegment(sketch, "E4538", {"start": v(-35.37, -22.85) * mm, "end": v(-35.48, -22.99) * mm});
            skLineSegment(sketch, "E4539", {"start": v(-35.48, -22.99) * mm, "end": v(-35.6, -23.13) * mm});
            skLineSegment(sketch, "E4540", {"start": v(-35.6, -23.13) * mm, "end": v(-35.7, -23.27) * mm});
            skLineSegment(sketch, "E4541", {"start": v(-35.7, -23.27) * mm, "end": v(-35.81, -23.4) * mm});
            skLineSegment(sketch, "E4542", {"start": v(-35.81, -23.4) * mm, "end": v(-35.92, -23.56) * mm});
            skLineSegment(sketch, "E4543", {"start": v(-35.92, -23.56) * mm, "end": v(-36.03, -23.7) * mm});
            skLineSegment(sketch, "E4544", {"start": v(-36.03, -23.7) * mm, "end": v(-36.14, -23.87) * mm});
            skLineSegment(sketch, "E4545", {"start": v(-36.14, -23.87) * mm, "end": v(-36.24, -24.01) * mm});
            skLineSegment(sketch, "E4546", {"start": v(-36.24, -24.01) * mm, "end": v(-36.34, -24.16) * mm});
            skLineSegment(sketch, "E4547", {"start": v(-36.34, -24.16) * mm, "end": v(-36.44, -24.3) * mm});
            skLineSegment(sketch, "E4548", {"start": v(-36.44, -24.3) * mm, "end": v(-36.53, -24.47) * mm});
            skLineSegment(sketch, "E4549", {"start": v(-36.53, -24.47) * mm, "end": v(-36.63, -24.63) * mm});
            skLineSegment(sketch, "E4550", {"start": v(-36.63, -24.63) * mm, "end": v(-36.74, -24.8) * mm});
            skLineSegment(sketch, "E4551", {"start": v(-36.74, -24.8) * mm, "end": v(-36.84, -24.96) * mm});
            skLineSegment(sketch, "E4552", {"start": v(-36.84, -24.96) * mm, "end": v(-36.9, -25.08) * mm});
            skLineSegment(sketch, "E4553", {"start": v(-36.9, -25.08) * mm, "end": v(-36.8, -25.24) * mm});
            skLineSegment(sketch, "E4554", {"start": v(-36.8, -25.24) * mm, "end": v(-36.7, -25.39) * mm});
            skLineSegment(sketch, "E4555", {"start": v(-36.7, -25.39) * mm, "end": v(-36.6, -25.54) * mm});
            skLineSegment(sketch, "E4556", {"start": v(-36.6, -25.54) * mm, "end": v(-36.49, -25.7) * mm});
            skLineSegment(sketch, "E4557", {"start": v(-36.49, -25.7) * mm, "end": v(-36.44, -25.76) * mm});
            skLineSegment(sketch, "E4558", {"start": v(-36.44, -25.76) * mm, "end": v(-36.25, -25.73) * mm});
            skLineSegment(sketch, "E4559", {"start": v(-36.25, -25.73) * mm, "end": v(-36.07, -25.7) * mm});
            skLineSegment(sketch, "E4560", {"start": v(-36.07, -25.7) * mm, "end": v(-35.9, -25.66) * mm});
            skLineSegment(sketch, "E4561", {"start": v(-35.9, -25.66) * mm, "end": v(-35.72, -25.63) * mm});
            skLineSegment(sketch, "E4562", {"start": v(-35.72, -25.63) * mm, "end": v(-35.55, -25.6) * mm});
            skLineSegment(sketch, "E4563", {"start": v(-35.55, -25.6) * mm, "end": v(-35.37, -25.55) * mm});
            skLineSegment(sketch, "E4564", {"start": v(-35.37, -25.55) * mm, "end": v(-35.19, -25.51) * mm});
            skLineSegment(sketch, "E4565", {"start": v(-35.19, -25.51) * mm, "end": v(-35, -25.47) * mm});
            skLineSegment(sketch, "E4566", {"start": v(-35, -25.47) * mm, "end": v(-34.82, -25.42) * mm});
            skLineSegment(sketch, "E4567", {"start": v(-34.82, -25.42) * mm, "end": v(-34.64, -25.37) * mm});
            skLineSegment(sketch, "E4568", {"start": v(-34.64, -25.37) * mm, "end": v(-34.45, -25.32) * mm});
            skLineSegment(sketch, "E4569", {"start": v(-34.45, -25.32) * mm, "end": v(-34.27, -25.26) * mm});
            skLineSegment(sketch, "E4570", {"start": v(-34.27, -25.26) * mm, "end": v(-34.1, -25.2) * mm});
            skLineSegment(sketch, "E4571", {"start": v(-34.1, -25.2) * mm, "end": v(-33.92, -25.15) * mm});
            skLineSegment(sketch, "E4572", {"start": v(-33.92, -25.15) * mm, "end": v(-33.74, -25.09) * mm});
            skLineSegment(sketch, "E4573", {"start": v(-33.74, -25.09) * mm, "end": v(-33.58, -25.03) * mm});
            skLineSegment(sketch, "E4574", {"start": v(-33.58, -25.03) * mm, "end": v(-33.4, -24.96) * mm});
            skLineSegment(sketch, "E4575", {"start": v(-33.4, -24.96) * mm, "end": v(-33.23, -24.9) * mm});
            skLineSegment(sketch, "E4576", {"start": v(-33.23, -24.9) * mm, "end": v(-33.05, -24.82) * mm});
            skLineSegment(sketch, "E4577", {"start": v(-33.05, -24.82) * mm, "end": v(-32.97, -24.78) * mm});
            skLineSegment(sketch, "E4578", {"start": v(-32.97, -24.78) * mm, "end": v(-32.86, -24.93) * mm});
            skLineSegment(sketch, "E4579", {"start": v(-32.86, -24.93) * mm, "end": v(-32.74, -25.1) * mm});
            skLineSegment(sketch, "E4580", {"start": v(-32.74, -25.1) * mm, "end": v(-32.62, -25.24) * mm});
            skLineSegment(sketch, "E4581", {"start": v(-32.62, -25.24) * mm, "end": v(-32.5, -25.4) * mm});
            skLineSegment(sketch, "E4582", {"start": v(-32.5, -25.4) * mm, "end": v(-32.39, -25.55) * mm});
            skLineSegment(sketch, "E4583", {"start": v(-32.39, -25.55) * mm, "end": v(-32.26, -25.7) * mm});
            skLineSegment(sketch, "E4584", {"start": v(-32.26, -25.7) * mm, "end": v(-32.15, -25.85) * mm});
            skLineSegment(sketch, "E4585", {"start": v(-32.15, -25.85) * mm, "end": v(-32.13, -25.88) * mm});
            skLineSegment(sketch, "E4586", {"start": v(-32.13, -25.88) * mm, "end": v(-32.23, -26.01) * mm});
            skLineSegment(sketch, "E4587", {"start": v(-32.23, -26.01) * mm, "end": v(-32.34, -26.16) * mm});
            skLineSegment(sketch, "E4588", {"start": v(-32.34, -26.16) * mm, "end": v(-32.44, -26.3) * mm});
            skLineSegment(sketch, "E4589", {"start": v(-32.44, -26.3) * mm, "end": v(-32.55, -26.45) * mm});
            skLineSegment(sketch, "E4590", {"start": v(-32.55, -26.45) * mm, "end": v(-32.64, -26.6) * mm});
            skLineSegment(sketch, "E4591", {"start": v(-32.64, -26.6) * mm, "end": v(-32.74, -26.75) * mm});
            skLineSegment(sketch, "E4592", {"start": v(-32.74, -26.75) * mm, "end": v(-32.84, -26.9) * mm});
            skLineSegment(sketch, "E4593", {"start": v(-32.84, -26.9) * mm, "end": v(-32.93, -27.05) * mm});
            skLineSegment(sketch, "E4594", {"start": v(-32.93, -27.05) * mm, "end": v(-33.02, -27.2) * mm});
            skLineSegment(sketch, "E4595", {"start": v(-33.02, -27.2) * mm, "end": v(-33.11, -27.36) * mm});
            skLineSegment(sketch, "E4596", {"start": v(-33.11, -27.36) * mm, "end": v(-33.2, -27.53) * mm});
            skLineSegment(sketch, "E4597", {"start": v(-33.2, -27.53) * mm, "end": v(-33.3, -27.7) * mm});
            skLineSegment(sketch, "E4598", {"start": v(-33.3, -27.7) * mm, "end": v(-33.38, -27.85) * mm});
            skLineSegment(sketch, "E4599", {"start": v(-33.38, -27.85) * mm, "end": v(-33.46, -28) * mm});
            skLineSegment(sketch, "E4600", {"start": v(-33.46, -28) * mm, "end": v(-33.54, -28.17) * mm});
            skLineSegment(sketch, "E4601", {"start": v(-33.54, -28.17) * mm, "end": v(-33.62, -28.34) * mm});
            skLineSegment(sketch, "E4602", {"start": v(-33.62, -28.34) * mm, "end": v(-33.7, -28.5) * mm});
            skLineSegment(sketch, "E4603", {"start": v(-33.7, -28.5) * mm, "end": v(-33.78, -28.68) * mm});
            skLineSegment(sketch, "E4604", {"start": v(-33.78, -28.68) * mm, "end": v(-33.87, -28.86) * mm});
            skLineSegment(sketch, "E4605", {"start": v(-33.87, -28.86) * mm, "end": v(-33.92, -29) * mm});
            skLineSegment(sketch, "E4606", {"start": v(-33.92, -29) * mm, "end": v(-33.8, -29.13) * mm});
            skLineSegment(sketch, "E4607", {"start": v(-33.8, -29.13) * mm, "end": v(-33.68, -29.27) * mm});
            skLineSegment(sketch, "E4608", {"start": v(-33.68, -29.27) * mm, "end": v(-33.56, -29.4) * mm});
            skLineSegment(sketch, "E4609", {"start": v(-33.56, -29.4) * mm, "end": v(-33.44, -29.55) * mm});
            skLineSegment(sketch, "E4610", {"start": v(-33.44, -29.55) * mm, "end": v(-33.38, -29.62) * mm});
            skLineSegment(sketch, "E4611", {"start": v(-33.38, -29.62) * mm, "end": v(-33.2, -29.56) * mm});
            skLineSegment(sketch, "E4612", {"start": v(-33.2, -29.56) * mm, "end": v(-33.02, -29.51) * mm});
            skLineSegment(sketch, "E4613", {"start": v(-33.02, -29.51) * mm, "end": v(-32.85, -29.46) * mm});
            skLineSegment(sketch, "E4614", {"start": v(-32.85, -29.46) * mm, "end": v(-32.68, -29.4) * mm});
            skLineSegment(sketch, "E4615", {"start": v(-32.68, -29.4) * mm, "end": v(-32.52, -29.35) * mm});
            skLineSegment(sketch, "E4616", {"start": v(-32.52, -29.35) * mm, "end": v(-32.34, -29.29) * mm});
            skLineSegment(sketch, "E4617", {"start": v(-32.34, -29.29) * mm, "end": v(-32.17, -29.23) * mm});
            skLineSegment(sketch, "E4618", {"start": v(-32.17, -29.23) * mm, "end": v(-31.99, -29.16) * mm});
            skLineSegment(sketch, "E4619", {"start": v(-31.99, -29.16) * mm, "end": v(-31.81, -29.1) * mm});
            skLineSegment(sketch, "E4620", {"start": v(-31.81, -29.1) * mm, "end": v(-31.63, -29.02) * mm});
            skLineSegment(sketch, "E4621", {"start": v(-31.63, -29.02) * mm, "end": v(-31.46, -28.95) * mm});
            skLineSegment(sketch, "E4622", {"start": v(-31.46, -28.95) * mm, "end": v(-31.29, -28.88) * mm});
            skLineSegment(sketch, "E4623", {"start": v(-31.29, -28.88) * mm, "end": v(-31.12, -28.8) * mm});
            skLineSegment(sketch, "E4624", {"start": v(-31.12, -28.8) * mm, "end": v(-30.95, -28.73) * mm});
            skLineSegment(sketch, "E4625", {"start": v(-30.95, -28.73) * mm, "end": v(-30.78, -28.65) * mm});
            skLineSegment(sketch, "E4626", {"start": v(-30.78, -28.65) * mm, "end": v(-30.62, -28.57) * mm});
            skLineSegment(sketch, "E4627", {"start": v(-30.62, -28.57) * mm, "end": v(-30.45, -28.48) * mm});
            skLineSegment(sketch, "E4628", {"start": v(-30.45, -28.48) * mm, "end": v(-30.29, -28.4) * mm});
            skLineSegment(sketch, "E4629", {"start": v(-30.29, -28.4) * mm, "end": v(-30.12, -28.3) * mm});
            skLineSegment(sketch, "E4630", {"start": v(-30.12, -28.3) * mm, "end": v(-30.05, -28.26) * mm});
            skLineSegment(sketch, "E4631", {"start": v(-30.05, -28.26) * mm, "end": v(-29.92, -28.4) * mm});
            skLineSegment(sketch, "E4632", {"start": v(-29.92, -28.4) * mm, "end": v(-29.78, -28.54) * mm});
            skLineSegment(sketch, "E4633", {"start": v(-29.78, -28.54) * mm, "end": v(-29.65, -28.68) * mm});
            skLineSegment(sketch, "E4634", {"start": v(-29.65, -28.68) * mm, "end": v(-29.51, -28.82) * mm});
            skLineSegment(sketch, "E4635", {"start": v(-29.51, -28.82) * mm, "end": v(-29.38, -28.95) * mm});
            skLineSegment(sketch, "E4636", {"start": v(-29.38, -28.95) * mm, "end": v(-29.24, -29.1) * mm});
            skLineSegment(sketch, "E4637", {"start": v(-29.24, -29.1) * mm, "end": v(-29.1, -29.23) * mm});
            skLineSegment(sketch, "E4638", {"start": v(-29.1, -29.23) * mm, "end": v(-29.09, -29.26) * mm});
            skLineSegment(sketch, "E4639", {"start": v(-29.09, -29.26) * mm, "end": v(-29.17, -29.4) * mm});
            skLineSegment(sketch, "E4640", {"start": v(-29.17, -29.4) * mm, "end": v(-29.27, -29.56) * mm});
            skLineSegment(sketch, "E4641", {"start": v(-29.27, -29.56) * mm, "end": v(-29.35, -29.71) * mm});
            skLineSegment(sketch, "E4642", {"start": v(-29.35, -29.71) * mm, "end": v(-29.44, -29.87) * mm});
            skLineSegment(sketch, "E4643", {"start": v(-29.44, -29.87) * mm, "end": v(-29.52, -30.03) * mm});
            skLineSegment(sketch, "E4644", {"start": v(-29.52, -30.03) * mm, "end": v(-29.6, -30.19) * mm});
            skLineSegment(sketch, "E4645", {"start": v(-29.6, -30.19) * mm, "end": v(-29.68, -30.36) * mm});
            skLineSegment(sketch, "E4646", {"start": v(-29.68, -30.36) * mm, "end": v(-29.75, -30.51) * mm});
            skLineSegment(sketch, "E4647", {"start": v(-29.75, -30.51) * mm, "end": v(-29.83, -30.67) * mm});
            skLineSegment(sketch, "E4648", {"start": v(-29.83, -30.67) * mm, "end": v(-29.9, -30.84) * mm});
            skLineSegment(sketch, "E4649", {"start": v(-29.9, -30.84) * mm, "end": v(-29.97, -31.01) * mm});
            skLineSegment(sketch, "E4650", {"start": v(-29.97, -31.01) * mm, "end": v(-30.05, -31.2) * mm});
            skLineSegment(sketch, "E4651", {"start": v(-30.05, -31.2) * mm, "end": v(-30.11, -31.35) * mm});
            skLineSegment(sketch, "E4652", {"start": v(-30.11, -31.35) * mm, "end": v(-30.17, -31.52) * mm});
            skLineSegment(sketch, "E4653", {"start": v(-30.17, -31.52) * mm, "end": v(-30.24, -31.69) * mm});
            skLineSegment(sketch, "E4654", {"start": v(-30.24, -31.69) * mm, "end": v(-30.3, -31.86) * mm});
            skLineSegment(sketch, "E4655", {"start": v(-30.3, -31.86) * mm, "end": v(-30.36, -32.04) * mm});
            skLineSegment(sketch, "E4656", {"start": v(-30.36, -32.04) * mm, "end": v(-30.42, -32.22) * mm});
            skLineSegment(sketch, "E4657", {"start": v(-30.42, -32.22) * mm, "end": v(-30.49, -32.41) * mm});
            skLineSegment(sketch, "E4658", {"start": v(-30.49, -32.41) * mm, "end": v(-30.53, -32.55) * mm});
            skLineSegment(sketch, "E4659", {"start": v(-30.53, -32.55) * mm, "end": v(-30.4, -32.67) * mm});
            skLineSegment(sketch, "E4660", {"start": v(-30.4, -32.67) * mm, "end": v(-30.26, -32.8) * mm});
            skLineSegment(sketch, "E4661", {"start": v(-30.26, -32.8) * mm, "end": v(-30.12, -32.92) * mm});
            skLineSegment(sketch, "E4662", {"start": v(-30.12, -32.92) * mm, "end": v(-29.98, -33.05) * mm});
            skLineSegment(sketch, "E4663", {"start": v(-29.98, -33.05) * mm, "end": v(-29.92, -33.1) * mm});
            skLineSegment(sketch, "E4664", {"start": v(-29.92, -33.1) * mm, "end": v(-29.74, -33.03) * mm});
            skLineSegment(sketch, "E4665", {"start": v(-29.74, -33.03) * mm, "end": v(-29.57, -32.96) * mm});
            skLineSegment(sketch, "E4666", {"start": v(-29.57, -32.96) * mm, "end": v(-29.41, -32.9) * mm});
            skLineSegment(sketch, "E4667", {"start": v(-29.41, -32.9) * mm, "end": v(-29.25, -32.82) * mm});
            skLineSegment(sketch, "E4668", {"start": v(-29.25, -32.82) * mm, "end": v(-29.1, -32.75) * mm});
            skLineSegment(sketch, "E4669", {"start": v(-29.1, -32.75) * mm, "end": v(-28.93, -32.67) * mm});
            skLineSegment(sketch, "E4670", {"start": v(-28.93, -32.67) * mm, "end": v(-28.76, -32.59) * mm});
            skLineSegment(sketch, "E4671", {"start": v(-28.76, -32.59) * mm, "end": v(-28.58, -32.5) * mm});
            skLineSegment(sketch, "E4672", {"start": v(-28.58, -32.5) * mm, "end": v(-28.42, -32.42) * mm});
            skLineSegment(sketch, "E4673", {"start": v(-28.42, -32.42) * mm, "end": v(-28.25, -32.33) * mm});
            skLineSegment(sketch, "E4674", {"start": v(-28.25, -32.33) * mm, "end": v(-28.08, -32.24) * mm});
            skLineSegment(sketch, "E4675", {"start": v(-28.08, -32.24) * mm, "end": v(-27.92, -32.15) * mm});
            skLineSegment(sketch, "E4676", {"start": v(-27.92, -32.15) * mm, "end": v(-27.76, -32.06) * mm});
            skLineSegment(sketch, "E4677", {"start": v(-27.76, -32.06) * mm, "end": v(-27.6, -31.96) * mm});
            skLineSegment(sketch, "E4678", {"start": v(-27.6, -31.96) * mm, "end": v(-27.44, -31.86) * mm});
            skLineSegment(sketch, "E4679", {"start": v(-27.44, -31.86) * mm, "end": v(-27.3, -31.77) * mm});
            skLineSegment(sketch, "E4680", {"start": v(-27.3, -31.77) * mm, "end": v(-27.14, -31.66) * mm});
            skLineSegment(sketch, "E4681", {"start": v(-27.14, -31.66) * mm, "end": v(-26.98, -31.56) * mm});
            skLineSegment(sketch, "E4682", {"start": v(-26.98, -31.56) * mm, "end": v(-26.82, -31.44) * mm});
            skLineSegment(sketch, "E4683", {"start": v(-26.82, -31.44) * mm, "end": v(-26.75, -31.4) * mm});
            skLineSegment(sketch, "E4684", {"start": v(-26.75, -31.4) * mm, "end": v(-26.61, -31.52) * mm});
            skLineSegment(sketch, "E4685", {"start": v(-26.61, -31.52) * mm, "end": v(-26.46, -31.64) * mm});
            skLineSegment(sketch, "E4686", {"start": v(-26.46, -31.64) * mm, "end": v(-26.31, -31.76) * mm});
            skLineSegment(sketch, "E4687", {"start": v(-26.31, -31.76) * mm, "end": v(-26.16, -31.9) * mm});
            skLineSegment(sketch, "E4688", {"start": v(-26.16, -31.9) * mm, "end": v(-26.01, -32) * mm});
            skLineSegment(sketch, "E4689", {"start": v(-26.01, -32) * mm, "end": v(-25.86, -32.13) * mm});
            skLineSegment(sketch, "E4690", {"start": v(-25.86, -32.13) * mm, "end": v(-25.72, -32.26) * mm});
            skLineSegment(sketch, "E4691", {"start": v(-25.72, -32.26) * mm, "end": v(-25.7, -32.28) * mm});
            skLineSegment(sketch, "E4692", {"start": v(-25.7, -32.28) * mm, "end": v(-25.76, -32.43) * mm});
            skLineSegment(sketch, "E4693", {"start": v(-25.76, -32.43) * mm, "end": v(-25.84, -32.6) * mm});
            skLineSegment(sketch, "E4694", {"start": v(-25.84, -32.6) * mm, "end": v(-25.9, -32.76) * mm});
            skLineSegment(sketch, "E4695", {"start": v(-25.9, -32.76) * mm, "end": v(-25.97, -32.93) * mm});
            skLineSegment(sketch, "E4696", {"start": v(-25.97, -32.93) * mm, "end": v(-26.03, -33.1) * mm});
            skLineSegment(sketch, "E4697", {"start": v(-26.03, -33.1) * mm, "end": v(-26.1, -33.26) * mm});
            skLineSegment(sketch, "E4698", {"start": v(-26.1, -33.26) * mm, "end": v(-26.16, -33.44) * mm});
            skLineSegment(sketch, "E4699", {"start": v(-26.16, -33.44) * mm, "end": v(-26.21, -33.6) * mm});
            skLineSegment(sketch, "E4700", {"start": v(-26.21, -33.6) * mm, "end": v(-26.27, -33.77) * mm});
            skLineSegment(sketch, "E4701", {"start": v(-26.27, -33.77) * mm, "end": v(-26.32, -33.94) * mm});
            skLineSegment(sketch, "E4702", {"start": v(-26.32, -33.94) * mm, "end": v(-26.38, -34.12) * mm});
            skLineSegment(sketch, "E4703", {"start": v(-26.38, -34.12) * mm, "end": v(-26.43, -34.31) * mm});
            skLineSegment(sketch, "E4704", {"start": v(-26.43, -34.31) * mm, "end": v(-26.48, -34.48) * mm});
            skLineSegment(sketch, "E4705", {"start": v(-26.48, -34.48) * mm, "end": v(-26.52, -34.65) * mm});
            skLineSegment(sketch, "E4706", {"start": v(-26.52, -34.65) * mm, "end": v(-26.57, -34.82) * mm});
            skLineSegment(sketch, "E4707", {"start": v(-26.57, -34.82) * mm, "end": v(-26.61, -35) * mm});
            skLineSegment(sketch, "E4708", {"start": v(-26.61, -35) * mm, "end": v(-26.65, -35.19) * mm});
            skLineSegment(sketch, "E4709", {"start": v(-26.65, -35.19) * mm, "end": v(-26.7, -35.38) * mm});
            skLineSegment(sketch, "E4710", {"start": v(-26.7, -35.38) * mm, "end": v(-26.73, -35.57) * mm});
            skLineSegment(sketch, "E4711", {"start": v(-26.73, -35.57) * mm, "end": v(-26.76, -35.7) * mm});
            skLineSegment(sketch, "E4712", {"start": v(-26.76, -35.7) * mm, "end": v(-26.61, -35.82) * mm});
            skLineSegment(sketch, "E4713", {"start": v(-26.61, -35.82) * mm, "end": v(-26.47, -35.93) * mm});
            skLineSegment(sketch, "E4714", {"start": v(-26.47, -35.93) * mm, "end": v(-26.32, -36.04) * mm});
            skLineSegment(sketch, "E4715", {"start": v(-26.32, -36.04) * mm, "end": v(-26.17, -36.15) * mm});
            skLineSegment(sketch, "E4716", {"start": v(-26.17, -36.15) * mm, "end": v(-26.1, -36.2) * mm});
            skLineSegment(sketch, "E4717", {"start": v(-26.1, -36.2) * mm, "end": v(-25.93, -36.1) * mm});
            skLineSegment(sketch, "E4718", {"start": v(-25.93, -36.1) * mm, "end": v(-25.77, -36.02) * mm});
            skLineSegment(sketch, "E4719", {"start": v(-25.77, -36.02) * mm, "end": v(-25.61, -35.93) * mm});
            skLineSegment(sketch, "E4720", {"start": v(-25.61, -35.93) * mm, "end": v(-25.46, -35.84) * mm});
            skLineSegment(sketch, "E4721", {"start": v(-25.46, -35.84) * mm, "end": v(-25.32, -35.75) * mm});
            skLineSegment(sketch, "E4722", {"start": v(-25.32, -35.75) * mm, "end": v(-25.16, -35.65) * mm});
            skLineSegment(sketch, "E4723", {"start": v(-25.16, -35.65) * mm, "end": v(-25, -35.55) * mm});
            skLineSegment(sketch, "E4724", {"start": v(-25, -35.55) * mm, "end": v(-24.83, -35.45) * mm});
            skLineSegment(sketch, "E4725", {"start": v(-24.83, -35.45) * mm, "end": v(-24.68, -35.35) * mm});
            skLineSegment(sketch, "E4726", {"start": v(-24.68, -35.35) * mm, "end": v(-24.52, -35.24) * mm});
            skLineSegment(sketch, "E4727", {"start": v(-24.52, -35.24) * mm, "end": v(-24.37, -35.13) * mm});
            skLineSegment(sketch, "E4728", {"start": v(-24.37, -35.13) * mm, "end": v(-24.21, -35.02) * mm});
            skLineSegment(sketch, "E4729", {"start": v(-24.21, -35.02) * mm, "end": v(-24.07, -34.92) * mm});
            skLineSegment(sketch, "E4730", {"start": v(-24.07, -34.92) * mm, "end": v(-23.91, -34.8) * mm});
            skLineSegment(sketch, "E4731", {"start": v(-23.91, -34.8) * mm, "end": v(-23.77, -34.69) * mm});
            skLineSegment(sketch, "E4732", {"start": v(-23.77, -34.69) * mm, "end": v(-23.63, -34.58) * mm});
            skLineSegment(sketch, "E4733", {"start": v(-23.63, -34.58) * mm, "end": v(-23.49, -34.45) * mm});
            skLineSegment(sketch, "E4734", {"start": v(-23.49, -34.45) * mm, "end": v(-23.34, -34.33) * mm});
            skLineSegment(sketch, "E4735", {"start": v(-23.34, -34.33) * mm, "end": v(-23.2, -34.2) * mm});
            skLineSegment(sketch, "E4736", {"start": v(-23.2, -34.2) * mm, "end": v(-23.14, -34.15) * mm});
            skLineSegment(sketch, "E4737", {"start": v(-23.14, -34.15) * mm, "end": v(-22.98, -34.25) * mm});
            skLineSegment(sketch, "E4738", {"start": v(-22.98, -34.25) * mm, "end": v(-22.82, -34.36) * mm});
            skLineSegment(sketch, "E4739", {"start": v(-22.82, -34.36) * mm, "end": v(-22.66, -34.47) * mm});
            skLineSegment(sketch, "E4740", {"start": v(-22.66, -34.47) * mm, "end": v(-22.5, -34.57) * mm});
            skLineSegment(sketch, "E4741", {"start": v(-22.5, -34.57) * mm, "end": v(-22.33, -34.68) * mm});
            skLineSegment(sketch, "E4742", {"start": v(-22.33, -34.68) * mm, "end": v(-22.17, -34.78) * mm});
            skLineSegment(sketch, "E4743", {"start": v(-22.17, -34.78) * mm, "end": v(-22.01, -34.89) * mm});
            skLineSegment(sketch, "E4744", {"start": v(-22.01, -34.89) * mm, "end": v(-21.98, -34.9) * mm});
            skLineSegment(sketch, "E4745", {"start": v(-21.98, -34.9) * mm, "end": v(-22.04, -35.07) * mm});
            skLineSegment(sketch, "E4746", {"start": v(-22.04, -35.07) * mm, "end": v(-22.1, -35.24) * mm});
            skLineSegment(sketch, "E4747", {"start": v(-22.1, -35.24) * mm, "end": v(-22.14, -35.41) * mm});
            skLineSegment(sketch, "E4748", {"start": v(-22.14, -35.41) * mm, "end": v(-22.2, -35.59) * mm});
            skLineSegment(sketch, "E4749", {"start": v(-22.2, -35.59) * mm, "end": v(-22.24, -35.76) * mm});
            skLineSegment(sketch, "E4750", {"start": v(-22.24, -35.76) * mm, "end": v(-22.28, -35.93) * mm});
            skLineSegment(sketch, "E4751", {"start": v(-22.28, -35.93) * mm, "end": v(-22.32, -36.11) * mm});
            skLineSegment(sketch, "E4752", {"start": v(-22.32, -36.11) * mm, "end": v(-22.36, -36.28) * mm});
            skLineSegment(sketch, "E4753", {"start": v(-22.36, -36.28) * mm, "end": v(-22.4, -36.45) * mm});
            skLineSegment(sketch, "E4754", {"start": v(-22.4, -36.45) * mm, "end": v(-22.43, -36.63) * mm});
            skLineSegment(sketch, "E4755", {"start": v(-22.43, -36.63) * mm, "end": v(-22.46, -36.82) * mm});
            skLineSegment(sketch, "E4756", {"start": v(-22.46, -36.82) * mm, "end": v(-22.5, -37.01) * mm});
            skLineSegment(sketch, "E4757", {"start": v(-22.5, -37.01) * mm, "end": v(-22.52, -37.18) * mm});
            skLineSegment(sketch, "E4758", {"start": v(-22.52, -37.18) * mm, "end": v(-22.55, -37.35) * mm});
            skLineSegment(sketch, "E4759", {"start": v(-22.55, -37.35) * mm, "end": v(-22.57, -37.53) * mm});
            skLineSegment(sketch, "E4760", {"start": v(-22.57, -37.53) * mm, "end": v(-22.6, -37.72) * mm});
            skLineSegment(sketch, "E4761", {"start": v(-22.6, -37.72) * mm, "end": v(-22.62, -37.9) * mm});
            skLineSegment(sketch, "E4762", {"start": v(-22.62, -37.9) * mm, "end": v(-22.64, -38.1) * mm});
            skLineSegment(sketch, "E4763", {"start": v(-22.64, -38.1) * mm, "end": v(-22.66, -38.3) * mm});
            skLineSegment(sketch, "E4764", {"start": v(-22.66, -38.3) * mm, "end": v(-22.67, -38.43) * mm});
            skLineSegment(sketch, "E4765", {"start": v(-22.67, -38.43) * mm, "end": v(-22.51, -38.53) * mm});
            skLineSegment(sketch, "E4766", {"start": v(-22.51, -38.53) * mm, "end": v(-22.35, -38.62) * mm});
            skLineSegment(sketch, "E4767", {"start": v(-22.35, -38.62) * mm, "end": v(-22.2, -38.71) * mm});
            skLineSegment(sketch, "E4768", {"start": v(-22.2, -38.71) * mm, "end": v(-22.03, -38.8) * mm});
            skLineSegment(sketch, "E4769", {"start": v(-22.03, -38.8) * mm, "end": v(-21.95, -38.85) * mm});
            skLineSegment(sketch, "E4770", {"start": v(-21.95, -38.85) * mm, "end": v(-21.8, -38.74) * mm});
            skLineSegment(sketch, "E4771", {"start": v(-21.8, -38.74) * mm, "end": v(-21.65, -38.63) * mm});
            skLineSegment(sketch, "E4772", {"start": v(-21.65, -38.63) * mm, "end": v(-21.5, -38.53) * mm});
            skLineSegment(sketch, "E4773", {"start": v(-21.5, -38.53) * mm, "end": v(-21.36, -38.42) * mm});
            skLineSegment(sketch, "E4774", {"start": v(-21.36, -38.42) * mm, "end": v(-21.23, -38.32) * mm});
            skLineSegment(sketch, "E4775", {"start": v(-21.23, -38.32) * mm, "end": v(-21.08, -38.2) * mm});
            skLineSegment(sketch, "E4776", {"start": v(-21.08, -38.2) * mm, "end": v(-20.93, -38.09) * mm});
            skLineSegment(sketch, "E4777", {"start": v(-20.93, -38.09) * mm, "end": v(-20.78, -37.97) * mm});
            skLineSegment(sketch, "E4778", {"start": v(-20.78, -37.97) * mm, "end": v(-20.64, -37.85) * mm});
            skLineSegment(sketch, "E4779", {"start": v(-20.64, -37.85) * mm, "end": v(-20.5, -37.72) * mm});
            skLineSegment(sketch, "E4780", {"start": v(-20.5, -37.72) * mm, "end": v(-20.35, -37.6) * mm});
            skLineSegment(sketch, "E4781", {"start": v(-20.35, -37.6) * mm, "end": v(-20.21, -37.47) * mm});
            skLineSegment(sketch, "E4782", {"start": v(-20.21, -37.47) * mm, "end": v(-20.08, -37.35) * mm});
            skLineSegment(sketch, "E4783", {"start": v(-20.08, -37.35) * mm, "end": v(-19.94, -37.22) * mm});
            skLineSegment(sketch, "E4784", {"start": v(-19.94, -37.22) * mm, "end": v(-19.8, -37.09) * mm});
            skLineSegment(sketch, "E4785", {"start": v(-19.8, -37.09) * mm, "end": v(-19.68, -36.97) * mm});
            skLineSegment(sketch, "E4786", {"start": v(-19.68, -36.97) * mm, "end": v(-19.55, -36.83) * mm});
            skLineSegment(sketch, "E4787", {"start": v(-19.55, -36.83) * mm, "end": v(-19.42, -36.7) * mm});
            skLineSegment(sketch, "E4788", {"start": v(-19.42, -36.7) * mm, "end": v(-19.3, -36.55) * mm});
            skLineSegment(sketch, "E4789", {"start": v(-19.3, -36.55) * mm, "end": v(-19.24, -36.48) * mm});
            skLineSegment(sketch, "E4790", {"start": v(-19.24, -36.48) * mm, "end": v(-19.07, -36.57) * mm});
            skLineSegment(sketch, "E4791", {"start": v(-19.07, -36.57) * mm, "end": v(-18.9, -36.66) * mm});
            skLineSegment(sketch, "E4792", {"start": v(-18.9, -36.66) * mm, "end": v(-18.73, -36.75) * mm});
            skLineSegment(sketch, "E4793", {"start": v(-18.73, -36.75) * mm, "end": v(-18.55, -36.84) * mm});
            skLineSegment(sketch, "E4794", {"start": v(-18.55, -36.84) * mm, "end": v(-18.38, -36.92) * mm});
            skLineSegment(sketch, "E4795", {"start": v(-18.38, -36.92) * mm, "end": v(-18.2, -37.01) * mm});
            skLineSegment(sketch, "E4796", {"start": v(-18.2, -37.01) * mm, "end": v(-18.04, -37.1) * mm});
            skLineSegment(sketch, "E4797", {"start": v(-18.04, -37.1) * mm, "end": v(-18, -37.11) * mm});
            skLineSegment(sketch, "E4798", {"start": v(-18, -37.11) * mm, "end": v(-18.04, -37.28) * mm});
            skLineSegment(sketch, "E4799", {"start": v(-18.04, -37.28) * mm, "end": v(-18.08, -37.46) * mm});
            skLineSegment(sketch, "E4800", {"start": v(-18.08, -37.46) * mm, "end": v(-18.11, -37.63) * mm});
            skLineSegment(sketch, "E4801", {"start": v(-18.11, -37.63) * mm, "end": v(-18.14, -37.81) * mm});
            skLineSegment(sketch, "E4802", {"start": v(-18.14, -37.81) * mm, "end": v(-18.17, -37.98) * mm});
            skLineSegment(sketch, "E4803", {"start": v(-18.17, -37.98) * mm, "end": v(-18.2, -38.16) * mm});
            skLineSegment(sketch, "E4804", {"start": v(-18.2, -38.16) * mm, "end": v(-18.21, -38.35) * mm});
            skLineSegment(sketch, "E4805", {"start": v(-18.21, -38.35) * mm, "end": v(-18.23, -38.52) * mm});
            skLineSegment(sketch, "E4806", {"start": v(-18.23, -38.52) * mm, "end": v(-18.25, -38.7) * mm});
            skLineSegment(sketch, "E4807", {"start": v(-18.25, -38.7) * mm, "end": v(-18.26, -38.88) * mm});
            skLineSegment(sketch, "E4808", {"start": v(-18.26, -38.88) * mm, "end": v(-18.28, -39.07) * mm});
            skLineSegment(sketch, "E4809", {"start": v(-18.28, -39.07) * mm, "end": v(-18.29, -39.26) * mm});
            skLineSegment(sketch, "E4810", {"start": v(-18.29, -39.26) * mm, "end": v(-18.3, -39.43) * mm});
            skLineSegment(sketch, "E4811", {"start": v(-18.3, -39.43) * mm, "end": v(-18.3, -39.6) * mm});
            skLineSegment(sketch, "E4812", {"start": v(-18.3, -39.6) * mm, "end": v(-18.3, -39.79) * mm});
            skLineSegment(sketch, "E4813", {"start": v(-18.3, -39.79) * mm, "end": v(-18.31, -39.97) * mm});
            skLineSegment(sketch, "E4814", {"start": v(-18.31, -39.97) * mm, "end": v(-18.31, -40.16) * mm});
            skLineSegment(sketch, "E4815", {"start": v(-18.31, -40.16) * mm, "end": v(-18.31, -40.36) * mm});
            skLineSegment(sketch, "E4816", {"start": v(-18.31, -40.36) * mm, "end": v(-18.3, -40.56) * mm});
            skLineSegment(sketch, "E4817", {"start": v(-18.3, -40.56) * mm, "end": v(-18.3, -40.7) * mm});
            skLineSegment(sketch, "E4818", {"start": v(-18.3, -40.7) * mm, "end": v(-18.14, -40.77) * mm});
            skLineSegment(sketch, "E4819", {"start": v(-18.14, -40.77) * mm, "end": v(-17.97, -40.85) * mm});
            skLineSegment(sketch, "E4820", {"start": v(-17.97, -40.85) * mm, "end": v(-17.8, -40.92) * mm});
            skLineSegment(sketch, "E4821", {"start": v(-17.8, -40.92) * mm, "end": v(-17.63, -41) * mm});
            skLineSegment(sketch, "E4822", {"start": v(-17.63, -41) * mm, "end": v(-17.55, -41.03) * mm});
            skLineSegment(sketch, "E4823", {"start": v(-17.55, -41.03) * mm, "end": v(-17.4, -40.9) * mm});
            skLineSegment(sketch, "E4824", {"start": v(-17.4, -40.9) * mm, "end": v(-17.27, -40.78) * mm});
            skLineSegment(sketch, "E4825", {"start": v(-17.27, -40.78) * mm, "end": v(-17.14, -40.66) * mm});
            skLineSegment(sketch, "E4826", {"start": v(-17.14, -40.66) * mm, "end": v(-17, -40.54) * mm});
            skLineSegment(sketch, "E4827", {"start": v(-17, -40.54) * mm, "end": v(-16.88, -40.42) * mm});
            skLineSegment(sketch, "E4828", {"start": v(-16.88, -40.42) * mm, "end": v(-16.75, -40.3) * mm});
            skLineSegment(sketch, "E4829", {"start": v(-16.75, -40.3) * mm, "end": v(-16.62, -40.16) * mm});
            skLineSegment(sketch, "E4830", {"start": v(-16.62, -40.16) * mm, "end": v(-16.48, -40.02) * mm});
            skLineSegment(sketch, "E4831", {"start": v(-16.48, -40.02) * mm, "end": v(-16.35, -39.89) * mm});
            skLineSegment(sketch, "E4832", {"start": v(-16.35, -39.89) * mm, "end": v(-16.22, -39.75) * mm});
            skLineSegment(sketch, "E4833", {"start": v(-16.22, -39.75) * mm, "end": v(-16.1, -39.6) * mm});
            skLineSegment(sketch, "E4834", {"start": v(-16.1, -39.6) * mm, "end": v(-15.97, -39.47) * mm});
            skLineSegment(sketch, "E4835", {"start": v(-15.97, -39.47) * mm, "end": v(-15.85, -39.33) * mm});
            skLineSegment(sketch, "E4836", {"start": v(-15.85, -39.33) * mm, "end": v(-15.73, -39.19) * mm});
            skLineSegment(sketch, "E4837", {"start": v(-15.73, -39.19) * mm, "end": v(-15.6, -39.04) * mm});
            skLineSegment(sketch, "E4838", {"start": v(-15.6, -39.04) * mm, "end": v(-15.5, -38.9) * mm});
            skLineSegment(sketch, "E4839", {"start": v(-15.5, -38.9) * mm, "end": v(-15.38, -38.76) * mm});
            skLineSegment(sketch, "E4840", {"start": v(-15.38, -38.76) * mm, "end": v(-15.27, -38.6) * mm});
            skLineSegment(sketch, "E4841", {"start": v(-15.27, -38.6) * mm, "end": v(-15.16, -38.45) * mm});
            skLineSegment(sketch, "E4842", {"start": v(-15.16, -38.45) * mm, "end": v(-15.1, -38.38) * mm});
            skLineSegment(sketch, "E4843", {"start": v(-15.1, -38.38) * mm, "end": v(-14.93, -38.45) * mm});
            skLineSegment(sketch, "E4844", {"start": v(-14.93, -38.45) * mm, "end": v(-14.75, -38.52) * mm});
            skLineSegment(sketch, "E4845", {"start": v(-14.75, -38.52) * mm, "end": v(-14.57, -38.59) * mm});
            skLineSegment(sketch, "E4846", {"start": v(-14.57, -38.59) * mm, "end": v(-14.39, -38.66) * mm});
            skLineSegment(sketch, "E4847", {"start": v(-14.39, -38.66) * mm, "end": v(-14.21, -38.72) * mm});
            skLineSegment(sketch, "E4848", {"start": v(-14.21, -38.72) * mm, "end": v(-14.02, -38.79) * mm});
            skLineSegment(sketch, "E4849", {"start": v(-14.02, -38.79) * mm, "end": v(-13.85, -38.86) * mm});
            skLineSegment(sketch, "E4850", {"start": v(-13.85, -38.86) * mm, "end": v(-13.82, -38.87) * mm});
            skLineSegment(sketch, "E4851", {"start": v(-13.82, -38.87) * mm, "end": v(-13.83, -39.04) * mm});
            skLineSegment(sketch, "E4852", {"start": v(-13.83, -39.04) * mm, "end": v(-13.85, -39.22) * mm});
            skLineSegment(sketch, "E4853", {"start": v(-13.85, -39.22) * mm, "end": v(-13.86, -39.4) * mm});
            skLineSegment(sketch, "E4854", {"start": v(-13.86, -39.4) * mm, "end": v(-13.87, -39.58) * mm});
            skLineSegment(sketch, "E4855", {"start": v(-13.87, -39.58) * mm, "end": v(-13.88, -39.75) * mm});
            skLineSegment(sketch, "E4856", {"start": v(-13.88, -39.75) * mm, "end": v(-13.88, -39.93) * mm});
            skLineSegment(sketch, "E4857", {"start": v(-13.88, -39.93) * mm, "end": v(-13.88, -40.12) * mm});
            skLineSegment(sketch, "E4858", {"start": v(-13.88, -40.12) * mm, "end": v(-13.88, -40.3) * mm});
            skLineSegment(sketch, "E4859", {"start": v(-13.88, -40.3) * mm, "end": v(-13.88, -40.47) * mm});
            skLineSegment(sketch, "E4860", {"start": v(-13.88, -40.47) * mm, "end": v(-13.88, -40.65) * mm});
            skLineSegment(sketch, "E4861", {"start": v(-13.88, -40.65) * mm, "end": v(-13.87, -40.84) * mm});
            skLineSegment(sketch, "E4862", {"start": v(-13.87, -40.84) * mm, "end": v(-13.86, -41.03) * mm});
            skLineSegment(sketch, "E4863", {"start": v(-13.86, -41.03) * mm, "end": v(-13.85, -41.2) * mm});
            skLineSegment(sketch, "E4864", {"start": v(-13.85, -41.2) * mm, "end": v(-13.83, -41.38) * mm});
            skLineSegment(sketch, "E4865", {"start": v(-13.83, -41.38) * mm, "end": v(-13.82, -41.56) * mm});
            skLineSegment(sketch, "E4866", {"start": v(-13.82, -41.56) * mm, "end": v(-13.8, -41.75) * mm});
            skLineSegment(sketch, "E4867", {"start": v(-13.8, -41.75) * mm, "end": v(-13.78, -41.93) * mm});
            skLineSegment(sketch, "E4868", {"start": v(-13.78, -41.93) * mm, "end": v(-13.76, -42.13) * mm});
            skLineSegment(sketch, "E4869", {"start": v(-13.76, -42.13) * mm, "end": v(-13.74, -42.32) * mm});
            skLineSegment(sketch, "E4870", {"start": v(-13.74, -42.32) * mm, "end": v(-13.72, -42.46) * mm});
            skLineSegment(sketch, "E4871", {"start": v(-13.72, -42.46) * mm, "end": v(-13.54, -42.52) * mm});
            skLineSegment(sketch, "E4872", {"start": v(-13.54, -42.52) * mm, "end": v(-13.36, -42.57) * mm});
            skLineSegment(sketch, "E4873", {"start": v(-13.36, -42.57) * mm, "end": v(-13.19, -42.63) * mm});
            skLineSegment(sketch, "E4874", {"start": v(-13.19, -42.63) * mm, "end": v(-13.01, -42.68) * mm});
            skLineSegment(sketch, "E4875", {"start": v(-13.01, -42.68) * mm, "end": v(-12.93, -42.7) * mm});
            skLineSegment(sketch, "E4876", {"start": v(-12.93, -42.7) * mm, "end": v(-12.8, -42.57) * mm});
            skLineSegment(sketch, "E4877", {"start": v(-12.8, -42.57) * mm, "end": v(-12.68, -42.43) * mm});
            skLineSegment(sketch, "E4878", {"start": v(-12.68, -42.43) * mm, "end": v(-12.56, -42.3) * mm});
            skLineSegment(sketch, "E4879", {"start": v(-12.56, -42.3) * mm, "end": v(-12.44, -42.17) * mm});
            skLineSegment(sketch, "E4880", {"start": v(-12.44, -42.17) * mm, "end": v(-12.33, -42.03) * mm});
            skLineSegment(sketch, "E4881", {"start": v(-12.33, -42.03) * mm, "end": v(-12.21, -41.89) * mm});
            skLineSegment(sketch, "E4882", {"start": v(-12.21, -41.89) * mm, "end": v(-12.1, -41.74) * mm});
            skLineSegment(sketch, "E4883", {"start": v(-12.1, -41.74) * mm, "end": v(-11.98, -41.6) * mm});
            skLineSegment(sketch, "E4884", {"start": v(-11.98, -41.6) * mm, "end": v(-11.86, -41.44) * mm});
            skLineSegment(sketch, "E4885", {"start": v(-11.86, -41.44) * mm, "end": v(-11.75, -41.3) * mm});
            skLineSegment(sketch, "E4886", {"start": v(-11.75, -41.3) * mm, "end": v(-11.64, -41.14) * mm});
            skLineSegment(sketch, "E4887", {"start": v(-11.64, -41.14) * mm, "end": v(-11.53, -40.99) * mm});
            skLineSegment(sketch, "E4888", {"start": v(-11.53, -40.99) * mm, "end": v(-11.43, -40.84) * mm});
            skLineSegment(sketch, "E4889", {"start": v(-11.43, -40.84) * mm, "end": v(-11.32, -40.68) * mm});
            skLineSegment(sketch, "E4890", {"start": v(-11.32, -40.68) * mm, "end": v(-11.22, -40.52) * mm});
            skLineSegment(sketch, "E4891", {"start": v(-11.22, -40.52) * mm, "end": v(-11.12, -40.37) * mm});
            skLineSegment(sketch, "E4892", {"start": v(-11.12, -40.37) * mm, "end": v(-11.03, -40.21) * mm});
            skLineSegment(sketch, "E4893", {"start": v(-11.03, -40.21) * mm, "end": v(-10.93, -40.05) * mm});
            skLineSegment(sketch, "E4894", {"start": v(-10.93, -40.05) * mm, "end": v(-10.83, -39.88) * mm});
            skLineSegment(sketch, "E4895", {"start": v(-10.83, -39.88) * mm, "end": v(-10.8, -39.8) * mm});
            skLineSegment(sketch, "E4896", {"start": v(-10.8, -39.8) * mm, "end": v(-10.61, -39.86) * mm});
            skLineSegment(sketch, "E4897", {"start": v(-10.61, -39.86) * mm, "end": v(-10.42, -39.9) * mm});
            skLineSegment(sketch, "E4898", {"start": v(-10.42, -39.9) * mm, "end": v(-10.24, -39.96) * mm});
            skLineSegment(sketch, "E4899", {"start": v(-10.24, -39.96) * mm, "end": v(-10.05, -40) * mm});
            skLineSegment(sketch, "E4900", {"start": v(-10.05, -40) * mm, "end": v(-9.86, -40.05) * mm});
            skLineSegment(sketch, "E4901", {"start": v(-9.86, -40.05) * mm, "end": v(-9.67, -40.1) * mm});
            skLineSegment(sketch, "E4902", {"start": v(-9.67, -40.1) * mm, "end": v(-9.49, -40.15) * mm});
            skLineSegment(sketch, "E4903", {"start": v(-9.49, -40.15) * mm, "end": v(-9.46, -40.15) * mm});
            skLineSegment(sketch, "E4904", {"start": v(-9.46, -40.15) * mm, "end": v(-9.45, -40.32) * mm});
            skLineSegment(sketch, "E4905", {"start": v(-9.45, -40.32) * mm, "end": v(-9.45, -40.5) * mm});
            skLineSegment(sketch, "E4906", {"start": v(-9.45, -40.5) * mm, "end": v(-9.44, -40.68) * mm});
            skLineSegment(sketch, "E4907", {"start": v(-9.44, -40.68) * mm, "end": v(-9.43, -40.87) * mm});
            skLineSegment(sketch, "E4908", {"start": v(-9.43, -40.87) * mm, "end": v(-9.42, -41.04) * mm});
            skLineSegment(sketch, "E4909", {"start": v(-9.42, -41.04) * mm, "end": v(-9.4, -41.22) * mm});
            skLineSegment(sketch, "E4910", {"start": v(-9.4, -41.22) * mm, "end": v(-9.39, -41.4) * mm});
            skLineSegment(sketch, "E4911", {"start": v(-9.39, -41.4) * mm, "end": v(-9.37, -41.57) * mm});
            skLineSegment(sketch, "E4912", {"start": v(-9.37, -41.57) * mm, "end": v(-9.34, -41.75) * mm});
            skLineSegment(sketch, "E4913", {"start": v(-9.34, -41.75) * mm, "end": v(-9.32, -41.93) * mm});
            skLineSegment(sketch, "E4914", {"start": v(-9.32, -41.93) * mm, "end": v(-9.3, -42.12) * mm});
            skLineSegment(sketch, "E4915", {"start": v(-9.3, -42.12) * mm, "end": v(-9.26, -42.3) * mm});
            skLineSegment(sketch, "E4916", {"start": v(-9.26, -42.3) * mm, "end": v(-9.23, -42.48) * mm});
            skLineSegment(sketch, "E4917", {"start": v(-9.23, -42.48) * mm, "end": v(-9.2, -42.65) * mm});
            skLineSegment(sketch, "E4918", {"start": v(-9.2, -42.65) * mm, "end": v(-9.16, -42.83) * mm});
            skLineSegment(sketch, "E4919", {"start": v(-9.16, -42.83) * mm, "end": v(-9.13, -43.01) * mm});
            skLineSegment(sketch, "E4920", {"start": v(-9.13, -43.01) * mm, "end": v(-9.09, -43.2) * mm});
            skLineSegment(sketch, "E4921", {"start": v(-9.09, -43.2) * mm, "end": v(-9.04, -43.38) * mm});
            skLineSegment(sketch, "E4922", {"start": v(-9.04, -43.38) * mm, "end": v(-9, -43.58) * mm});
            skLineSegment(sketch, "E4923", {"start": v(-9, -43.58) * mm, "end": v(-8.96, -43.71) * mm});
            skLineSegment(sketch, "E4924", {"start": v(-8.96, -43.71) * mm, "end": v(-8.78, -43.75) * mm});
            skLineSegment(sketch, "E4925", {"start": v(-8.78, -43.75) * mm, "end": v(-8.6, -43.79) * mm});
            skLineSegment(sketch, "E4926", {"start": v(-8.6, -43.79) * mm, "end": v(-8.42, -43.82) * mm});
            skLineSegment(sketch, "E4927", {"start": v(-8.42, -43.82) * mm, "end": v(-8.24, -43.85) * mm});
            skLineSegment(sketch, "E4928", {"start": v(-8.24, -43.85) * mm, "end": v(-8.15, -43.87) * mm});
            skLineSegment(sketch, "E4929", {"start": v(-8.15, -43.87) * mm, "end": v(-8.04, -43.72) * mm});
            skLineSegment(sketch, "E4930", {"start": v(-8.04, -43.72) * mm, "end": v(-7.93, -43.57) * mm});
            skLineSegment(sketch, "E4931", {"start": v(-7.93, -43.57) * mm, "end": v(-7.83, -43.42) * mm});
            skLineSegment(sketch, "E4932", {"start": v(-7.83, -43.42) * mm, "end": v(-7.73, -43.28) * mm});
            skLineSegment(sketch, "E4933", {"start": v(-7.73, -43.28) * mm, "end": v(-7.63, -43.14) * mm});
            skLineSegment(sketch, "E4934", {"start": v(-7.63, -43.14) * mm, "end": v(-7.53, -42.98) * mm});
            skLineSegment(sketch, "E4935", {"start": v(-7.53, -42.98) * mm, "end": v(-7.43, -42.82) * mm});
            skLineSegment(sketch, "E4936", {"start": v(-7.43, -42.82) * mm, "end": v(-7.33, -42.66) * mm});
            skLineSegment(sketch, "E4937", {"start": v(-7.33, -42.66) * mm, "end": v(-7.23, -42.5) * mm});
            skLineSegment(sketch, "E4938", {"start": v(-7.23, -42.5) * mm, "end": v(-7.13, -42.33) * mm});
            skLineSegment(sketch, "E4939", {"start": v(-7.13, -42.33) * mm, "end": v(-7.04, -42.17) * mm});
            skLineSegment(sketch, "E4940", {"start": v(-7.04, -42.17) * mm, "end": v(-6.95, -42) * mm});
            skLineSegment(sketch, "E4941", {"start": v(-6.95, -42) * mm, "end": v(-6.86, -41.85) * mm});
            skLineSegment(sketch, "E4942", {"start": v(-6.86, -41.85) * mm, "end": v(-6.77, -41.68) * mm});
            skLineSegment(sketch, "E4943", {"start": v(-6.77, -41.68) * mm, "end": v(-6.7, -41.51) * mm});
            skLineSegment(sketch, "E4944", {"start": v(-6.7, -41.51) * mm, "end": v(-6.61, -41.35) * mm});
            skLineSegment(sketch, "E4945", {"start": v(-6.61, -41.35) * mm, "end": v(-6.53, -41.18) * mm});
            skLineSegment(sketch, "E4946", {"start": v(-6.53, -41.18) * mm, "end": v(-6.46, -41) * mm});
            skLineSegment(sketch, "E4947", {"start": v(-6.46, -41) * mm, "end": v(-6.38, -40.83) * mm});
            skLineSegment(sketch, "E4948", {"start": v(-6.38, -40.83) * mm, "end": v(-6.35, -40.76) * mm});
            skLineSegment(sketch, "E4949", {"start": v(-6.35, -40.76) * mm, "end": v(-6.16, -40.78) * mm});
            skLineSegment(sketch, "E4950", {"start": v(-6.16, -40.78) * mm, "end": v(-5.97, -40.81) * mm});
            skLineSegment(sketch, "E4951", {"start": v(-5.97, -40.81) * mm, "end": v(-5.78, -40.84) * mm});
            skLineSegment(sketch, "E4952", {"start": v(-5.78, -40.84) * mm, "end": v(-5.58, -40.87) * mm});
            skLineSegment(sketch, "E4953", {"start": v(-5.58, -40.87) * mm, "end": v(-5.4, -40.9) * mm});
            skLineSegment(sketch, "E4954", {"start": v(-5.4, -40.9) * mm, "end": v(-5.2, -40.92) * mm});
            skLineSegment(sketch, "E4955", {"start": v(-5.2, -40.92) * mm, "end": v(-5.01, -40.95) * mm});
            skLineSegment(sketch, "E4956", {"start": v(-5.01, -40.95) * mm, "end": v(-4.98, -40.95) * mm});
            skLineSegment(sketch, "E4957", {"start": v(-4.98, -40.95) * mm, "end": v(-4.96, -41.12) * mm});
            skLineSegment(sketch, "E4958", {"start": v(-4.96, -41.12) * mm, "end": v(-4.94, -41.3) * mm});
            skLineSegment(sketch, "E4959", {"start": v(-4.94, -41.3) * mm, "end": v(-4.91, -41.47) * mm});
            skLineSegment(sketch, "E4960", {"start": v(-4.91, -41.47) * mm, "end": v(-4.88, -41.65) * mm});
            skLineSegment(sketch, "E4961", {"start": v(-4.88, -41.65) * mm, "end": v(-4.85, -41.82) * mm});
            skLineSegment(sketch, "E4962", {"start": v(-4.85, -41.82) * mm, "end": v(-4.81, -42) * mm});
            skLineSegment(sketch, "E4963", {"start": v(-4.81, -42) * mm, "end": v(-4.77, -42.18) * mm});
            skLineSegment(sketch, "E4964", {"start": v(-4.77, -42.18) * mm, "end": v(-4.74, -42.35) * mm});
            skLineSegment(sketch, "E4965", {"start": v(-4.74, -42.35) * mm, "end": v(-4.7, -42.52) * mm});
            skLineSegment(sketch, "E4966", {"start": v(-4.7, -42.52) * mm, "end": v(-4.65, -42.7) * mm});
            skLineSegment(sketch, "E4967", {"start": v(-4.65, -42.7) * mm, "end": v(-4.6, -42.88) * mm});
            skLineSegment(sketch, "E4968", {"start": v(-4.6, -42.88) * mm, "end": v(-4.55, -43.07) * mm});
            skLineSegment(sketch, "E4969", {"start": v(-4.55, -43.07) * mm, "end": v(-4.5, -43.24) * mm});
            skLineSegment(sketch, "E4970", {"start": v(-4.5, -43.24) * mm, "end": v(-4.45, -43.4) * mm});
            skLineSegment(sketch, "E4971", {"start": v(-4.45, -43.4) * mm, "end": v(-4.4, -43.58) * mm});
            skLineSegment(sketch, "E4972", {"start": v(-4.4, -43.58) * mm, "end": v(-4.34, -43.75) * mm});
            skLineSegment(sketch, "E4973", {"start": v(-4.34, -43.75) * mm, "end": v(-4.28, -43.93) * mm});
            skLineSegment(sketch, "E4974", {"start": v(-4.28, -43.93) * mm, "end": v(-4.21, -44.12) * mm});
            skLineSegment(sketch, "E4975", {"start": v(-4.21, -44.12) * mm, "end": v(-4.15, -44.3) * mm});
            skLineSegment(sketch, "E4976", {"start": v(-4.15, -44.3) * mm, "end": v(-4.1, -44.43) * mm});
            skLineSegment(sketch, "E4977", {"start": v(-4.1, -44.43) * mm, "end": v(-3.91, -44.45) * mm});
            skLineSegment(sketch, "E4978", {"start": v(-3.91, -44.45) * mm, "end": v(-3.73, -44.47) * mm});
            skLineSegment(sketch, "E4979", {"start": v(-3.73, -44.47) * mm, "end": v(-3.55, -44.48) * mm});
            skLineSegment(sketch, "E4980", {"start": v(-3.55, -44.48) * mm, "end": v(-3.36, -44.5) * mm});
            skLineSegment(sketch, "E4981", {"start": v(-3.36, -44.5) * mm, "end": v(-3.27, -44.5) * mm});
            skLineSegment(sketch, "E4982", {"start": v(-3.27, -44.5) * mm, "end": v(-3.18, -44.34) * mm});
            skLineSegment(sketch, "E4983", {"start": v(-3.18, -44.34) * mm, "end": v(-3.09, -44.18) * mm});
            skLineSegment(sketch, "E4984", {"start": v(-3.09, -44.18) * mm, "end": v(-3, -44.02) * mm});
            skLineSegment(sketch, "E4985", {"start": v(-3, -44.02) * mm, "end": v(-2.92, -43.87) * mm});
            skLineSegment(sketch, "E4986", {"start": v(-2.92, -43.87) * mm, "end": v(-2.84, -43.71) * mm});
            skLineSegment(sketch, "E4987", {"start": v(-2.84, -43.71) * mm, "end": v(-2.76, -43.55) * mm});
            skLineSegment(sketch, "E4988", {"start": v(-2.76, -43.55) * mm, "end": v(-2.67, -43.38) * mm});
            skLineSegment(sketch, "E4989", {"start": v(-2.67, -43.38) * mm, "end": v(-2.6, -43.2) * mm});
            skLineSegment(sketch, "E4990", {"start": v(-2.6, -43.2) * mm, "end": v(-2.51, -43.03) * mm});
            skLineSegment(sketch, "E4991", {"start": v(-2.51, -43.03) * mm, "end": v(-2.43, -42.86) * mm});
            skLineSegment(sketch, "E4992", {"start": v(-2.43, -42.86) * mm, "end": v(-2.36, -42.69) * mm});
            skLineSegment(sketch, "E4993", {"start": v(-2.36, -42.69) * mm, "end": v(-2.29, -42.51) * mm});
            skLineSegment(sketch, "E4994", {"start": v(-2.29, -42.51) * mm, "end": v(-2.22, -42.35) * mm});
            skLineSegment(sketch, "E4995", {"start": v(-2.22, -42.35) * mm, "end": v(-2.15, -42.17) * mm});
            skLineSegment(sketch, "E4996", {"start": v(-2.15, -42.17) * mm, "end": v(-2.08, -42) * mm});
            skLineSegment(sketch, "E4997", {"start": v(-2.08, -42) * mm, "end": v(-2.02, -41.83) * mm});
            skLineSegment(sketch, "E4998", {"start": v(-2.02, -41.83) * mm, "end": v(-1.96, -41.65) * mm});
            skLineSegment(sketch, "E4999", {"start": v(-1.96, -41.65) * mm, "end": v(-1.9, -41.47) * mm});
            skLineSegment(sketch, "E5000", {"start": v(-1.9, -41.47) * mm, "end": v(-1.85, -41.28) * mm});
            skLineSegment(sketch, "E5001", {"start": v(-1.85, -41.28) * mm, "end": v(-1.83, -41.2) * mm});
            skLineSegment(sketch, "E5002", {"start": v(-1.83, -41.2) * mm, "end": v(-1.64, -41.21) * mm});
            skLineSegment(sketch, "E5003", {"start": v(-1.64, -41.21) * mm, "end": v(-1.44, -41.22) * mm});
            skLineSegment(sketch, "E5004", {"start": v(-1.44, -41.22) * mm, "end": v(-1.25, -41.23) * mm});
            skLineSegment(sketch, "E5005", {"start": v(-1.25, -41.23) * mm, "end": v(-1.05, -41.23) * mm});
            skLineSegment(sketch, "E5006", {"start": v(-1.05, -41.23) * mm, "end": v(-0.87, -41.24) * mm});
            skLineSegment(sketch, "E5007", {"start": v(-0.87, -41.24) * mm, "end": v(-0.67, -41.24) * mm});
            skLineSegment(sketch, "E5008", {"start": v(-0.67, -41.24) * mm, "end": v(-0.48, -41.25) * mm});
            skLineSegment(sketch, "E5009", {"start": v(-0.48, -41.25) * mm, "end": v(-0.45, -41.25) * mm});
            skLineSegment(sketch, "E5010", {"start": v(-0.45, -41.25) * mm, "end": v(-0.4, -41.42) * mm});
            skLineSegment(sketch, "E5011", {"start": v(-0.4, -41.42) * mm, "end": v(-0.36, -41.6) * mm});
            skLineSegment(sketch, "E5012", {"start": v(-0.36, -41.6) * mm, "end": v(-0.32, -41.76) * mm});
            skLineSegment(sketch, "E5013", {"start": v(-0.32, -41.76) * mm, "end": v(-0.27, -41.94) * mm});
            skLineSegment(sketch, "E5014", {"start": v(-0.27, -41.94) * mm, "end": v(-0.22, -42.1) * mm});
            skLineSegment(sketch, "E5015", {"start": v(-0.22, -42.1) * mm, "end": v(-0.16, -42.28) * mm});
            skLineSegment(sketch, "E5016", {"start": v(-0.16, -42.28) * mm, "end": v(-0.1, -42.45) * mm});
            skLineSegment(sketch, "E5017", {"start": v(-0.1, -42.45) * mm, "end": v(-0.05, -42.62) * mm});
            skLineSegment(sketch, "E5018", {"start": v(-0.05, -42.62) * mm, "end": v(0.01, -42.78) * mm});
            skLineSegment(sketch, "E5019", {"start": v(0.01, -42.78) * mm, "end": v(0.08, -42.95) * mm});
            skLineSegment(sketch, "E5020", {"start": v(0.08, -42.95) * mm, "end": v(0.14, -43.13) * mm});
            skLineSegment(sketch, "E5021", {"start": v(0.14, -43.13) * mm, "end": v(0.22, -43.3) * mm});
            skLineSegment(sketch, "E5022", {"start": v(0.22, -43.3) * mm, "end": v(0.28, -43.47) * mm});
            skLineSegment(sketch, "E5023", {"start": v(0.28, -43.47) * mm, "end": v(0.35, -43.63) * mm});
            skLineSegment(sketch, "E5024", {"start": v(0.35, -43.63) * mm, "end": v(0.42, -43.8) * mm});
            skLineSegment(sketch, "E5025", {"start": v(0.42, -43.8) * mm, "end": v(0.5, -43.96) * mm});
            skLineSegment(sketch, "E5026", {"start": v(0.5, -43.96) * mm, "end": v(0.58, -44.14) * mm});
            skLineSegment(sketch, "E5027", {"start": v(0.58, -44.14) * mm, "end": v(0.66, -44.31) * mm});
            skLineSegment(sketch, "E5028", {"start": v(0.66, -44.31) * mm, "end": v(0.75, -44.49) * mm});
            skLineSegment(sketch, "E5029", {"start": v(0.75, -44.49) * mm, "end": v(0.81, -44.61) * mm});
            skLineSegment(sketch, "E5030", {"start": v(0.81, -44.61) * mm, "end": v(1, -44.61) * mm});
            skLineSegment(sketch, "E5031", {"start": v(1, -44.61) * mm, "end": v(1.18, -44.6) * mm});
            skLineSegment(sketch, "E5032", {"start": v(1.18, -44.6) * mm, "end": v(1.37, -44.6) * mm});
            skLineSegment(sketch, "E5033", {"start": v(1.37, -44.6) * mm, "end": v(1.55, -44.6) * mm});
            skLineSegment(sketch, "E5034", {"start": v(1.55, -44.6) * mm, "end": v(1.64, -44.6) * mm});
            skLineSegment(sketch, "E5035", {"start": v(1.64, -44.6) * mm, "end": v(1.72, -44.42) * mm});
            skLineSegment(sketch, "E5036", {"start": v(1.72, -44.42) * mm, "end": v(1.79, -44.25) * mm});
            skLineSegment(sketch, "E5037", {"start": v(1.79, -44.25) * mm, "end": v(1.86, -44.08) * mm});
            skLineSegment(sketch, "E5038", {"start": v(1.86, -44.08) * mm, "end": v(1.92, -43.92) * mm});
            skLineSegment(sketch, "E5039", {"start": v(1.92, -43.92) * mm, "end": v(1.98, -43.76) * mm});
            skLineSegment(sketch, "E5040", {"start": v(1.98, -43.76) * mm, "end": v(2.05, -43.58) * mm});
            skLineSegment(sketch, "E5041", {"start": v(2.05, -43.58) * mm, "end": v(2.11, -43.4) * mm});
            skLineSegment(sketch, "E5042", {"start": v(2.11, -43.4) * mm, "end": v(2.18, -43.23) * mm});
            skLineSegment(sketch, "E5043", {"start": v(2.18, -43.23) * mm, "end": v(2.24, -43.05) * mm});
            skLineSegment(sketch, "E5044", {"start": v(2.24, -43.05) * mm, "end": v(2.3, -42.87) * mm});
            skLineSegment(sketch, "E5045", {"start": v(2.3, -42.87) * mm, "end": v(2.35, -42.69) * mm});
            skLineSegment(sketch, "E5046", {"start": v(2.35, -42.69) * mm, "end": v(2.4, -42.5) * mm});
            skLineSegment(sketch, "E5047", {"start": v(2.4, -42.5) * mm, "end": v(2.45, -42.34) * mm});
            skLineSegment(sketch, "E5048", {"start": v(2.45, -42.34) * mm, "end": v(2.5, -42.15) * mm});
            skLineSegment(sketch, "E5049", {"start": v(2.5, -42.15) * mm, "end": v(2.55, -41.97) * mm});
            skLineSegment(sketch, "E5050", {"start": v(2.55, -41.97) * mm, "end": v(2.59, -41.8) * mm});
            skLineSegment(sketch, "E5051", {"start": v(2.59, -41.8) * mm, "end": v(2.63, -41.61) * mm});
            skLineSegment(sketch, "E5052", {"start": v(2.63, -41.61) * mm, "end": v(2.67, -41.43) * mm});
            skLineSegment(sketch, "E5053", {"start": v(2.67, -41.43) * mm, "end": v(2.7, -41.24) * mm});
            skLineSegment(sketch, "E5054", {"start": v(2.7, -41.24) * mm, "end": v(2.72, -41.16) * mm});
            skLineSegment(sketch, "E5055", {"start": v(2.72, -41.16) * mm, "end": v(2.9, -41.14) * mm});
            skLineSegment(sketch, "E5056", {"start": v(2.9, -41.14) * mm, "end": v(3.1, -41.13) * mm});
            skLineSegment(sketch, "E5057", {"start": v(3.1, -41.13) * mm, "end": v(3.3, -41.12) * mm});
            skLineSegment(sketch, "E5058", {"start": v(3.3, -41.12) * mm, "end": v(3.49, -41.1) * mm});
            skLineSegment(sketch, "E5059", {"start": v(3.49, -41.1) * mm, "end": v(3.68, -41.08) * mm});
            skLineSegment(sketch, "E5060", {"start": v(3.68, -41.08) * mm, "end": v(3.87, -41.06) * mm});
            skLineSegment(sketch, "E5061", {"start": v(3.87, -41.06) * mm, "end": v(4.06, -41.05) * mm});
            skLineSegment(sketch, "E5062", {"start": v(4.06, -41.05) * mm, "end": v(4.1, -41.05) * mm});
            skLineSegment(sketch, "E5063", {"start": v(4.1, -41.05) * mm, "end": v(4.15, -41.2) * mm});
            skLineSegment(sketch, "E5064", {"start": v(4.15, -41.2) * mm, "end": v(4.22, -41.38) * mm});
            skLineSegment(sketch, "E5065", {"start": v(4.22, -41.38) * mm, "end": v(4.28, -41.54) * mm});
            skLineSegment(sketch, "E5066", {"start": v(4.28, -41.54) * mm, "end": v(4.35, -41.71) * mm});
            skLineSegment(sketch, "E5067", {"start": v(4.35, -41.71) * mm, "end": v(4.42, -41.87) * mm});
            skLineSegment(sketch, "E5068", {"start": v(4.42, -41.87) * mm, "end": v(4.49, -42.04) * mm});
            skLineSegment(sketch, "E5069", {"start": v(4.49, -42.04) * mm, "end": v(4.57, -42.2) * mm});
            skLineSegment(sketch, "E5070", {"start": v(4.57, -42.2) * mm, "end": v(4.64, -42.36) * mm});
            skLineSegment(sketch, "E5071", {"start": v(4.64, -42.36) * mm, "end": v(4.72, -42.52) * mm});
            skLineSegment(sketch, "E5072", {"start": v(4.72, -42.52) * mm, "end": v(4.8, -42.68) * mm});
            skLineSegment(sketch, "E5073", {"start": v(4.8, -42.68) * mm, "end": v(4.89, -42.85) * mm});
            skLineSegment(sketch, "E5074", {"start": v(4.89, -42.85) * mm, "end": v(4.98, -43.02) * mm});
            skLineSegment(sketch, "E5075", {"start": v(4.98, -43.02) * mm, "end": v(5.06, -43.17) * mm});
            skLineSegment(sketch, "E5076", {"start": v(5.06, -43.17) * mm, "end": v(5.15, -43.33) * mm});
            skLineSegment(sketch, "E5077", {"start": v(5.15, -43.33) * mm, "end": v(5.24, -43.48) * mm});
            skLineSegment(sketch, "E5078", {"start": v(5.24, -43.48) * mm, "end": v(5.33, -43.64) * mm});
            skLineSegment(sketch, "E5079", {"start": v(5.33, -43.64) * mm, "end": v(5.43, -43.8) * mm});
            skLineSegment(sketch, "E5080", {"start": v(5.43, -43.8) * mm, "end": v(5.54, -43.97) * mm});
            skLineSegment(sketch, "E5081", {"start": v(5.54, -43.97) * mm, "end": v(5.64, -44.14) * mm});
            skLineSegment(sketch, "E5082", {"start": v(5.64, -44.14) * mm, "end": v(5.72, -44.25) * mm});
            skLineSegment(sketch, "E5083", {"start": v(5.72, -44.25) * mm, "end": v(5.9, -44.23) * mm});
            skLineSegment(sketch, "E5084", {"start": v(5.9, -44.23) * mm, "end": v(6.08, -44.2) * mm});
            skLineSegment(sketch, "E5085", {"start": v(6.08, -44.2) * mm, "end": v(6.27, -44.18) * mm});
            skLineSegment(sketch, "E5086", {"start": v(6.27, -44.18) * mm, "end": v(6.45, -44.15) * mm});
            skLineSegment(sketch, "E5087", {"start": v(6.45, -44.15) * mm, "end": v(6.54, -44.14) * mm});
            skLineSegment(sketch, "E5088", {"start": v(6.54, -44.14) * mm, "end": v(6.6, -43.96) * mm});
            skLineSegment(sketch, "E5089", {"start": v(6.6, -43.96) * mm, "end": v(6.65, -43.78) * mm});
            skLineSegment(sketch, "E5090", {"start": v(6.65, -43.78) * mm, "end": v(6.7, -43.61) * mm});
            skLineSegment(sketch, "E5091", {"start": v(6.7, -43.61) * mm, "end": v(6.74, -43.44) * mm});
            skLineSegment(sketch, "E5092", {"start": v(6.74, -43.44) * mm, "end": v(6.79, -43.28) * mm});
            skLineSegment(sketch, "E5093", {"start": v(6.79, -43.28) * mm, "end": v(6.83, -43.1) * mm});
            skLineSegment(sketch, "E5094", {"start": v(6.83, -43.1) * mm, "end": v(6.88, -42.91) * mm});
            skLineSegment(sketch, "E5095", {"start": v(6.88, -42.91) * mm, "end": v(6.92, -42.73) * mm});
            skLineSegment(sketch, "E5096", {"start": v(6.92, -42.73) * mm, "end": v(6.96, -42.54) * mm});
            skLineSegment(sketch, "E5097", {"start": v(6.96, -42.54) * mm, "end": v(7, -42.36) * mm});
            skLineSegment(sketch, "E5098", {"start": v(7, -42.36) * mm, "end": v(7.03, -42.17) * mm});
            skLineSegment(sketch, "E5099", {"start": v(7.03, -42.17) * mm, "end": v(7.07, -41.98) * mm});
            skLineSegment(sketch, "E5100", {"start": v(7.07, -41.98) * mm, "end": v(7.1, -41.8) * mm});
            skLineSegment(sketch, "E5101", {"start": v(7.1, -41.8) * mm, "end": v(7.13, -41.62) * mm});
            skLineSegment(sketch, "E5102", {"start": v(7.13, -41.62) * mm, "end": v(7.15, -41.43) * mm});
            skLineSegment(sketch, "E5103", {"start": v(7.15, -41.43) * mm, "end": v(7.17, -41.26) * mm});
            skLineSegment(sketch, "E5104", {"start": v(7.17, -41.26) * mm, "end": v(7.2, -41.07) * mm});
            skLineSegment(sketch, "E5105", {"start": v(7.2, -41.07) * mm, "end": v(7.2, -40.88) * mm});
            skLineSegment(sketch, "E5106", {"start": v(7.2, -40.88) * mm, "end": v(7.22, -40.69) * mm});
            skLineSegment(sketch, "E5107", {"start": v(7.22, -40.69) * mm, "end": v(7.23, -40.6) * mm});
            skLineSegment(sketch, "E5108", {"start": v(7.23, -40.6) * mm, "end": v(7.41, -40.57) * mm});
            skLineSegment(sketch, "E5109", {"start": v(7.41, -40.57) * mm, "end": v(7.6, -40.54) * mm});
            skLineSegment(sketch, "E5110", {"start": v(7.6, -40.54) * mm, "end": v(7.8, -40.5) * mm});
            skLineSegment(sketch, "E5111", {"start": v(7.8, -40.5) * mm, "end": v(7.99, -40.47) * mm});
            skLineSegment(sketch, "E5112", {"start": v(7.99, -40.47) * mm, "end": v(8.17, -40.43) * mm});
            skLineSegment(sketch, "E5113", {"start": v(8.17, -40.43) * mm, "end": v(8.37, -40.39) * mm});
            skLineSegment(sketch, "E5114", {"start": v(8.37, -40.39) * mm, "end": v(8.55, -40.35) * mm});
            skLineSegment(sketch, "E5115", {"start": v(8.55, -40.35) * mm, "end": v(8.59, -40.35) * mm});
            skLineSegment(sketch, "E5116", {"start": v(8.59, -40.35) * mm, "end": v(8.66, -40.5) * mm});
            skLineSegment(sketch, "E5117", {"start": v(8.66, -40.5) * mm, "end": v(8.74, -40.67) * mm});
            skLineSegment(sketch, "E5118", {"start": v(8.74, -40.67) * mm, "end": v(8.82, -40.82) * mm});
            skLineSegment(sketch, "E5119", {"start": v(8.82, -40.82) * mm, "end": v(8.91, -40.98) * mm});
            skLineSegment(sketch, "E5120", {"start": v(8.91, -40.98) * mm, "end": v(9, -41.13) * mm});
            skLineSegment(sketch, "E5121", {"start": v(9, -41.13) * mm, "end": v(9.09, -41.29) * mm});
            skLineSegment(sketch, "E5122", {"start": v(9.09, -41.29) * mm, "end": v(9.18, -41.45) * mm});
            skLineSegment(sketch, "E5123", {"start": v(9.18, -41.45) * mm, "end": v(9.27, -41.6) * mm});
            skLineSegment(sketch, "E5124", {"start": v(9.27, -41.6) * mm, "end": v(9.37, -41.74) * mm});
            skLineSegment(sketch, "E5125", {"start": v(9.37, -41.74) * mm, "end": v(9.47, -41.9) * mm});
            skLineSegment(sketch, "E5126", {"start": v(9.47, -41.9) * mm, "end": v(9.57, -42.05) * mm});
            skLineSegment(sketch, "E5127", {"start": v(9.57, -42.05) * mm, "end": v(9.68, -42.21) * mm});
            skLineSegment(sketch, "E5128", {"start": v(9.68, -42.21) * mm, "end": v(9.78, -42.35) * mm});
            skLineSegment(sketch, "E5129", {"start": v(9.78, -42.35) * mm, "end": v(9.89, -42.5) * mm});
            skLineSegment(sketch, "E5130", {"start": v(9.89, -42.5) * mm, "end": v(10, -42.64) * mm});
            skLineSegment(sketch, "E5131", {"start": v(10, -42.64) * mm, "end": v(10.1, -42.8) * mm});
            skLineSegment(sketch, "E5132", {"start": v(10.1, -42.8) * mm, "end": v(10.22, -42.94) * mm});
            skLineSegment(sketch, "E5133", {"start": v(10.22, -42.94) * mm, "end": v(10.34, -43.1) * mm});
            skLineSegment(sketch, "E5134", {"start": v(10.34, -43.1) * mm, "end": v(10.46, -43.25) * mm});
            skLineSegment(sketch, "E5135", {"start": v(10.46, -43.25) * mm, "end": v(10.55, -43.36) * mm});
            skLineSegment(sketch, "E5136", {"start": v(10.55, -43.36) * mm, "end": v(10.73, -43.31) * mm});
            skLineSegment(sketch, "E5137", {"start": v(10.73, -43.31) * mm, "end": v(10.91, -43.27) * mm});
            skLineSegment(sketch, "E5138", {"start": v(10.91, -43.27) * mm, "end": v(11.09, -43.22) * mm});
            skLineSegment(sketch, "E5139", {"start": v(11.09, -43.22) * mm, "end": v(11.27, -43.18) * mm});
            skLineSegment(sketch, "E5140", {"start": v(11.27, -43.18) * mm, "end": v(11.35, -43.15) * mm});
            skLineSegment(sketch, "E5141", {"start": v(11.35, -43.15) * mm, "end": v(11.4, -42.96) * mm});
            skLineSegment(sketch, "E5142", {"start": v(11.4, -42.96) * mm, "end": v(11.42, -42.79) * mm});
            skLineSegment(sketch, "E5143", {"start": v(11.42, -42.79) * mm, "end": v(11.45, -42.6) * mm});
            skLineSegment(sketch, "E5144", {"start": v(11.45, -42.6) * mm, "end": v(11.48, -42.44) * mm});
            skLineSegment(sketch, "E5145", {"start": v(11.48, -42.44) * mm, "end": v(11.5, -42.27) * mm});
            skLineSegment(sketch, "E5146", {"start": v(11.5, -42.27) * mm, "end": v(11.53, -42.08) * mm});
            skLineSegment(sketch, "E5147", {"start": v(11.53, -42.08) * mm, "end": v(11.56, -41.9) * mm});
            skLineSegment(sketch, "E5148", {"start": v(11.56, -41.9) * mm, "end": v(11.58, -41.7) * mm});
            skLineSegment(sketch, "E5149", {"start": v(11.58, -41.7) * mm, "end": v(11.6, -41.52) * mm});
            skLineSegment(sketch, "E5150", {"start": v(11.6, -41.52) * mm, "end": v(11.62, -41.33) * mm});
            skLineSegment(sketch, "E5151", {"start": v(11.62, -41.33) * mm, "end": v(11.63, -41.14) * mm});
            skLineSegment(sketch, "E5152", {"start": v(11.63, -41.14) * mm, "end": v(11.64, -40.95) * mm});
            skLineSegment(sketch, "E5153", {"start": v(11.64, -40.95) * mm, "end": v(11.65, -40.77) * mm});
            skLineSegment(sketch, "E5154", {"start": v(11.65, -40.77) * mm, "end": v(11.66, -40.58) * mm});
            skLineSegment(sketch, "E5155", {"start": v(11.66, -40.58) * mm, "end": v(11.67, -40.4) * mm});
            skLineSegment(sketch, "E5156", {"start": v(11.67, -40.4) * mm, "end": v(11.67, -40.22) * mm});
            skLineSegment(sketch, "E5157", {"start": v(11.67, -40.22) * mm, "end": v(11.67, -40.03) * mm});
            skLineSegment(sketch, "E5158", {"start": v(11.67, -40.03) * mm, "end": v(11.66, -39.84) * mm});
            skLineSegment(sketch, "E5159", {"start": v(11.66, -39.84) * mm, "end": v(11.66, -39.65) * mm});
            skLineSegment(sketch, "E5160", {"start": v(11.66, -39.65) * mm, "end": v(11.65, -39.57) * mm});
            skLineSegment(sketch, "E5161", {"start": v(11.65, -39.57) * mm, "end": v(11.83, -39.51) * mm});
            skLineSegment(sketch, "E5162", {"start": v(11.83, -39.51) * mm, "end": v(12.02, -39.46) * mm});
            skLineSegment(sketch, "E5163", {"start": v(12.02, -39.46) * mm, "end": v(12.2, -39.4) * mm});
            skLineSegment(sketch, "E5164", {"start": v(12.2, -39.4) * mm, "end": v(12.4, -39.34) * mm});
            skLineSegment(sketch, "E5165", {"start": v(12.4, -39.34) * mm, "end": v(12.57, -39.28) * mm});
            skLineSegment(sketch, "E5166", {"start": v(12.57, -39.28) * mm, "end": v(12.76, -39.22) * mm});
            skLineSegment(sketch, "E5167", {"start": v(12.76, -39.22) * mm, "end": v(12.94, -39.17) * mm});
            skLineSegment(sketch, "E5168", {"start": v(12.94, -39.17) * mm, "end": v(12.97, -39.16) * mm});
            skLineSegment(sketch, "E5169", {"start": v(12.97, -39.16) * mm, "end": v(13.06, -39.3) * mm});
            skLineSegment(sketch, "E5170", {"start": v(13.06, -39.3) * mm, "end": v(13.16, -39.46) * mm});
            skLineSegment(sketch, "E5171", {"start": v(13.16, -39.46) * mm, "end": v(13.26, -39.6) * mm});
            skLineSegment(sketch, "E5172", {"start": v(13.26, -39.6) * mm, "end": v(13.37, -39.75) * mm});
            skLineSegment(sketch, "E5173", {"start": v(13.37, -39.75) * mm, "end": v(13.47, -39.9) * mm});
            skLineSegment(sketch, "E5174", {"start": v(13.47, -39.9) * mm, "end": v(13.57, -40.04) * mm});
            skLineSegment(sketch, "E5175", {"start": v(13.57, -40.04) * mm, "end": v(13.69, -40.19) * mm});
            skLineSegment(sketch, "E5176", {"start": v(13.69, -40.19) * mm, "end": v(13.8, -40.32) * mm});
            skLineSegment(sketch, "E5177", {"start": v(13.8, -40.32) * mm, "end": v(13.9, -40.46) * mm});
            skLineSegment(sketch, "E5178", {"start": v(13.9, -40.46) * mm, "end": v(14.02, -40.6) * mm});
            skLineSegment(sketch, "E5179", {"start": v(14.02, -40.6) * mm, "end": v(14.14, -40.74) * mm});
            skLineSegment(sketch, "E5180", {"start": v(14.14, -40.74) * mm, "end": v(14.27, -40.9) * mm});
            skLineSegment(sketch, "E5181", {"start": v(14.27, -40.9) * mm, "end": v(14.38, -41.02) * mm});
            skLineSegment(sketch, "E5182", {"start": v(14.38, -41.02) * mm, "end": v(14.5, -41.15) * mm});
            skLineSegment(sketch, "E5183", {"start": v(14.5, -41.15) * mm, "end": v(14.62, -41.28) * mm});
            skLineSegment(sketch, "E5184", {"start": v(14.62, -41.28) * mm, "end": v(14.75, -41.42) * mm});
            skLineSegment(sketch, "E5185", {"start": v(14.75, -41.42) * mm, "end": v(14.88, -41.56) * mm});
            skLineSegment(sketch, "E5186", {"start": v(14.88, -41.56) * mm, "end": v(15.02, -41.7) * mm});
            skLineSegment(sketch, "E5187", {"start": v(15.02, -41.7) * mm, "end": v(15.16, -41.83) * mm});
            skLineSegment(sketch, "E5188", {"start": v(15.16, -41.83) * mm, "end": v(15.26, -41.93) * mm});
            skLineSegment(sketch, "E5189", {"start": v(15.26, -41.93) * mm, "end": v(15.43, -41.87) * mm});
            skLineSegment(sketch, "E5190", {"start": v(15.43, -41.87) * mm, "end": v(15.6, -41.8) * mm});
            skLineSegment(sketch, "E5191", {"start": v(15.6, -41.8) * mm, "end": v(15.78, -41.74) * mm});
            skLineSegment(sketch, "E5192", {"start": v(15.78, -41.74) * mm, "end": v(15.95, -41.67) * mm});
            skLineSegment(sketch, "E5193", {"start": v(15.95, -41.67) * mm, "end": v(16.03, -41.64) * mm});
            skLineSegment(sketch, "E5194", {"start": v(16.03, -41.64) * mm, "end": v(16.05, -41.45) * mm});
            skLineSegment(sketch, "E5195", {"start": v(16.05, -41.45) * mm, "end": v(16.06, -41.27) * mm});
            skLineSegment(sketch, "E5196", {"start": v(16.06, -41.27) * mm, "end": v(16.07, -41.1) * mm});
            skLineSegment(sketch, "E5197", {"start": v(16.07, -41.1) * mm, "end": v(16.08, -40.92) * mm});
            skLineSegment(sketch, "E5198", {"start": v(16.08, -40.92) * mm, "end": v(16.09, -40.75) * mm});
            skLineSegment(sketch, "E5199", {"start": v(16.09, -40.75) * mm, "end": v(16.1, -40.56) * mm});
            skLineSegment(sketch, "E5200", {"start": v(16.1, -40.56) * mm, "end": v(16.1, -40.37) * mm});
            skLineSegment(sketch, "E5201", {"start": v(16.1, -40.37) * mm, "end": v(16.1, -40.18) * mm});
            skLineSegment(sketch, "E5202", {"start": v(16.1, -40.18) * mm, "end": v(16.1, -39.99) * mm});
            skLineSegment(sketch, "E5203", {"start": v(16.1, -39.99) * mm, "end": v(16.1, -39.8) * mm});
            skLineSegment(sketch, "E5204", {"start": v(16.1, -39.8) * mm, "end": v(16.09, -39.61) * mm});
            skLineSegment(sketch, "E5205", {"start": v(16.09, -39.61) * mm, "end": v(16.08, -39.42) * mm});
            skLineSegment(sketch, "E5206", {"start": v(16.08, -39.42) * mm, "end": v(16.07, -39.24) * mm});
            skLineSegment(sketch, "E5207", {"start": v(16.07, -39.24) * mm, "end": v(16.06, -39.05) * mm});
            skLineSegment(sketch, "E5208", {"start": v(16.06, -39.05) * mm, "end": v(16.04, -38.87) * mm});
            skLineSegment(sketch, "E5209", {"start": v(16.04, -38.87) * mm, "end": v(16.02, -38.7) * mm});
            skLineSegment(sketch, "E5210", {"start": v(16.02, -38.7) * mm, "end": v(16, -38.5) * mm});
            skLineSegment(sketch, "E5211", {"start": v(16, -38.5) * mm, "end": v(15.98, -38.32) * mm});
            skLineSegment(sketch, "E5212", {"start": v(15.98, -38.32) * mm, "end": v(15.95, -38.12) * mm});
            skLineSegment(sketch, "E5213", {"start": v(15.95, -38.12) * mm, "end": v(15.93, -38.04) * mm});
            skLineSegment(sketch, "E5214", {"start": v(15.93, -38.04) * mm, "end": v(16.1, -37.97) * mm});
            skLineSegment(sketch, "E5215", {"start": v(16.1, -37.97) * mm, "end": v(16.3, -37.9) * mm});
            skLineSegment(sketch, "E5216", {"start": v(16.3, -37.9) * mm, "end": v(16.46, -37.82) * mm});
            skLineSegment(sketch, "E5217", {"start": v(16.46, -37.82) * mm, "end": v(16.64, -37.74) * mm});
            skLineSegment(sketch, "E5218", {"start": v(16.64, -37.74) * mm, "end": v(16.82, -37.66) * mm});
            skLineSegment(sketch, "E5219", {"start": v(16.82, -37.66) * mm, "end": v(17, -37.58) * mm});
            skLineSegment(sketch, "E5220", {"start": v(17, -37.58) * mm, "end": v(17.17, -37.5) * mm});
            skLineSegment(sketch, "E5221", {"start": v(17.17, -37.5) * mm, "end": v(17.2, -37.5) * mm});
            skLineSegment(sketch, "E5222", {"start": v(17.2, -37.5) * mm, "end": v(17.3, -37.63) * mm});
            skLineSegment(sketch, "E5223", {"start": v(17.3, -37.63) * mm, "end": v(17.42, -37.77) * mm});
            skLineSegment(sketch, "E5224", {"start": v(17.42, -37.77) * mm, "end": v(17.54, -37.9) * mm});
            skLineSegment(sketch, "E5225", {"start": v(17.54, -37.9) * mm, "end": v(17.66, -38.04) * mm});
            skLineSegment(sketch, "E5226", {"start": v(17.66, -38.04) * mm, "end": v(17.77, -38.17) * mm});
            skLineSegment(sketch, "E5227", {"start": v(17.77, -38.17) * mm, "end": v(17.9, -38.3) * mm});
            skLineSegment(sketch, "E5228", {"start": v(17.9, -38.3) * mm, "end": v(18.03, -38.44) * mm});
            skLineSegment(sketch, "E5229", {"start": v(18.03, -38.44) * mm, "end": v(18.15, -38.56) * mm});
            skLineSegment(sketch, "E5230", {"start": v(18.15, -38.56) * mm, "end": v(18.27, -38.68) * mm});
            skLineSegment(sketch, "E5231", {"start": v(18.27, -38.68) * mm, "end": v(18.4, -38.81) * mm});
            skLineSegment(sketch, "E5232", {"start": v(18.4, -38.81) * mm, "end": v(18.54, -38.94) * mm});
            skLineSegment(sketch, "E5233", {"start": v(18.54, -38.94) * mm, "end": v(18.68, -39.07) * mm});
            skLineSegment(sketch, "E5234", {"start": v(18.68, -39.07) * mm, "end": v(18.8, -39.19) * mm});
            skLineSegment(sketch, "E5235", {"start": v(18.8, -39.19) * mm, "end": v(18.94, -39.3) * mm});
            skLineSegment(sketch, "E5236", {"start": v(18.94, -39.3) * mm, "end": v(19.08, -39.43) * mm});
            skLineSegment(sketch, "E5237", {"start": v(19.08, -39.43) * mm, "end": v(19.22, -39.55) * mm});
            skLineSegment(sketch, "E5238", {"start": v(19.22, -39.55) * mm, "end": v(19.36, -39.67) * mm});
            skLineSegment(sketch, "E5239", {"start": v(19.36, -39.67) * mm, "end": v(19.51, -39.79) * mm});
            skLineSegment(sketch, "E5240", {"start": v(19.51, -39.79) * mm, "end": v(19.67, -39.91) * mm});
            skLineSegment(sketch, "E5241", {"start": v(19.67, -39.91) * mm, "end": v(19.78, -40) * mm});
            skLineSegment(sketch, "E5242", {"start": v(19.78, -40) * mm, "end": v(19.94, -39.92) * mm});
            skLineSegment(sketch, "E5243", {"start": v(19.94, -39.92) * mm, "end": v(20.1, -39.83) * mm});
            skLineSegment(sketch, "E5244", {"start": v(20.1, -39.83) * mm, "end": v(20.27, -39.75) * mm});
            skLineSegment(sketch, "E5245", {"start": v(20.27, -39.75) * mm, "end": v(20.44, -39.67) * mm});
            skLineSegment(sketch, "E5246", {"start": v(20.44, -39.67) * mm, "end": v(20.52, -39.62) * mm});
            skLineSegment(sketch, "E5247", {"start": v(20.52, -39.62) * mm, "end": v(20.51, -39.43) * mm});
            skLineSegment(sketch, "E5248", {"start": v(20.51, -39.43) * mm, "end": v(20.5, -39.25) * mm});
            skLineSegment(sketch, "E5249", {"start": v(20.5, -39.25) * mm, "end": v(20.5, -39.07) * mm});
            skLineSegment(sketch, "E5250", {"start": v(20.5, -39.07) * mm, "end": v(20.48, -38.9) * mm});
            skLineSegment(sketch, "E5251", {"start": v(20.48, -38.9) * mm, "end": v(20.47, -38.73) * mm});
            skLineSegment(sketch, "E5252", {"start": v(20.47, -38.73) * mm, "end": v(20.46, -38.54) * mm});
            skLineSegment(sketch, "E5253", {"start": v(20.46, -38.54) * mm, "end": v(20.44, -38.35) * mm});
            skLineSegment(sketch, "E5254", {"start": v(20.44, -38.35) * mm, "end": v(20.42, -38.16) * mm});
            skLineSegment(sketch, "E5255", {"start": v(20.42, -38.16) * mm, "end": v(20.4, -37.98) * mm});
            skLineSegment(sketch, "E5256", {"start": v(20.4, -37.98) * mm, "end": v(20.37, -37.79) * mm});
            skLineSegment(sketch, "E5257", {"start": v(20.37, -37.79) * mm, "end": v(20.35, -37.6) * mm});
            skLineSegment(sketch, "E5258", {"start": v(20.35, -37.6) * mm, "end": v(20.32, -37.41) * mm});
            skLineSegment(sketch, "E5259", {"start": v(20.32, -37.41) * mm, "end": v(20.29, -37.24) * mm});
            skLineSegment(sketch, "E5260", {"start": v(20.29, -37.24) * mm, "end": v(20.25, -37.05) * mm});
            skLineSegment(sketch, "E5261", {"start": v(20.25, -37.05) * mm, "end": v(20.22, -36.87) * mm});
            skLineSegment(sketch, "E5262", {"start": v(20.22, -36.87) * mm, "end": v(20.18, -36.7) * mm});
            skLineSegment(sketch, "E5263", {"start": v(20.18, -36.7) * mm, "end": v(20.14, -36.51) * mm});
            skLineSegment(sketch, "E5264", {"start": v(20.14, -36.51) * mm, "end": v(20.1, -36.33) * mm});
            skLineSegment(sketch, "E5265", {"start": v(20.1, -36.33) * mm, "end": v(20.04, -36.14) * mm});
            skLineSegment(sketch, "E5266", {"start": v(20.04, -36.14) * mm, "end": v(20.02, -36.06) * mm});
            skLineSegment(sketch, "E5267", {"start": v(20.02, -36.06) * mm, "end": v(20.19, -35.97) * mm});
            skLineSegment(sketch, "E5268", {"start": v(20.19, -35.97) * mm, "end": v(20.36, -35.87) * mm});
            skLineSegment(sketch, "E5269", {"start": v(20.36, -35.87) * mm, "end": v(20.52, -35.78) * mm});
            skLineSegment(sketch, "E5270", {"start": v(20.52, -35.78) * mm, "end": v(20.7, -35.68) * mm});
            skLineSegment(sketch, "E5271", {"start": v(20.7, -35.68) * mm, "end": v(20.86, -35.58) * mm});
            skLineSegment(sketch, "E5272", {"start": v(20.86, -35.58) * mm, "end": v(21.03, -35.48) * mm});
            skLineSegment(sketch, "E5273", {"start": v(21.03, -35.48) * mm, "end": v(21.2, -35.4) * mm});
            skLineSegment(sketch, "E5274", {"start": v(21.2, -35.4) * mm, "end": v(21.22, -35.37) * mm});
            skLineSegment(sketch, "E5275", {"start": v(21.22, -35.37) * mm, "end": v(21.34, -35.5) * mm});
            skLineSegment(sketch, "E5276", {"start": v(21.34, -35.5) * mm, "end": v(21.47, -35.62) * mm});
            skLineSegment(sketch, "E5277", {"start": v(21.47, -35.62) * mm, "end": v(21.6, -35.74) * mm});
            skLineSegment(sketch, "E5278", {"start": v(21.6, -35.74) * mm, "end": v(21.74, -35.87) * mm});
            skLineSegment(sketch, "E5279", {"start": v(21.74, -35.87) * mm, "end": v(21.87, -35.98) * mm});
            skLineSegment(sketch, "E5280", {"start": v(21.87, -35.98) * mm, "end": v(22, -36.1) * mm});
            skLineSegment(sketch, "E5281", {"start": v(22, -36.1) * mm, "end": v(22.15, -36.22) * mm});
            skLineSegment(sketch, "E5282", {"start": v(22.15, -36.22) * mm, "end": v(22.28, -36.33) * mm});
            skLineSegment(sketch, "E5283", {"start": v(22.28, -36.33) * mm, "end": v(22.42, -36.44) * mm});
            skLineSegment(sketch, "E5284", {"start": v(22.42, -36.44) * mm, "end": v(22.56, -36.55) * mm});
            skLineSegment(sketch, "E5285", {"start": v(22.56, -36.55) * mm, "end": v(22.71, -36.67) * mm});
            skLineSegment(sketch, "E5286", {"start": v(22.71, -36.67) * mm, "end": v(22.87, -36.78) * mm});
            skLineSegment(sketch, "E5287", {"start": v(22.87, -36.78) * mm, "end": v(23, -36.88) * mm});
            skLineSegment(sketch, "E5288", {"start": v(23, -36.88) * mm, "end": v(23.15, -36.98) * mm});
            skLineSegment(sketch, "E5289", {"start": v(23.15, -36.98) * mm, "end": v(23.3, -37.09) * mm});
            skLineSegment(sketch, "E5290", {"start": v(23.3, -37.09) * mm, "end": v(23.45, -37.2) * mm});
            skLineSegment(sketch, "E5291", {"start": v(23.45, -37.2) * mm, "end": v(23.6, -37.3) * mm});
            skLineSegment(sketch, "E5292", {"start": v(23.6, -37.3) * mm, "end": v(23.77, -37.4) * mm});
            skLineSegment(sketch, "E5293", {"start": v(23.77, -37.4) * mm, "end": v(23.94, -37.5) * mm});
            skLineSegment(sketch, "E5294", {"start": v(23.94, -37.5) * mm, "end": v(24.06, -37.58) * mm});
            skLineSegment(sketch, "E5295", {"start": v(24.06, -37.58) * mm, "end": v(24.21, -37.48) * mm});
            skLineSegment(sketch, "E5296", {"start": v(24.21, -37.48) * mm, "end": v(24.37, -37.38) * mm});
            skLineSegment(sketch, "E5297", {"start": v(24.37, -37.38) * mm, "end": v(24.52, -37.28) * mm});
            skLineSegment(sketch, "E5298", {"start": v(24.52, -37.28) * mm, "end": v(24.68, -37.18) * mm});
            skLineSegment(sketch, "E5299", {"start": v(24.68, -37.18) * mm, "end": v(24.75, -37.13) * mm});
            skLineSegment(sketch, "E5300", {"start": v(24.75, -37.13) * mm, "end": v(24.73, -36.94) * mm});
            skLineSegment(sketch, "E5301", {"start": v(24.73, -36.94) * mm, "end": v(24.7, -36.76) * mm});
            skLineSegment(sketch, "E5302", {"start": v(24.7, -36.76) * mm, "end": v(24.67, -36.58) * mm});
            skLineSegment(sketch, "E5303", {"start": v(24.67, -36.58) * mm, "end": v(24.64, -36.4) * mm});
            skLineSegment(sketch, "E5304", {"start": v(24.64, -36.4) * mm, "end": v(24.6, -36.24) * mm});
            skLineSegment(sketch, "E5305", {"start": v(24.6, -36.24) * mm, "end": v(24.57, -36.06) * mm});
            skLineSegment(sketch, "E5306", {"start": v(24.57, -36.06) * mm, "end": v(24.53, -35.87) * mm});
            skLineSegment(sketch, "E5307", {"start": v(24.53, -35.87) * mm, "end": v(24.5, -35.68) * mm});
            skLineSegment(sketch, "E5308", {"start": v(24.5, -35.68) * mm, "end": v(24.45, -35.5) * mm});
            skLineSegment(sketch, "E5309", {"start": v(24.45, -35.5) * mm, "end": v(24.4, -35.32) * mm});
            skLineSegment(sketch, "E5310", {"start": v(24.4, -35.32) * mm, "end": v(24.36, -35.13) * mm});
            skLineSegment(sketch, "E5311", {"start": v(24.36, -35.13) * mm, "end": v(24.31, -34.95) * mm});
            skLineSegment(sketch, "E5312", {"start": v(24.31, -34.95) * mm, "end": v(24.26, -34.78) * mm});
            skLineSegment(sketch, "E5313", {"start": v(24.26, -34.78) * mm, "end": v(24.2, -34.6) * mm});
            skLineSegment(sketch, "E5314", {"start": v(24.2, -34.6) * mm, "end": v(24.15, -34.42) * mm});
            skLineSegment(sketch, "E5315", {"start": v(24.15, -34.42) * mm, "end": v(24.1, -34.25) * mm});
            skLineSegment(sketch, "E5316", {"start": v(24.1, -34.25) * mm, "end": v(24.03, -34.07) * mm});
            skLineSegment(sketch, "E5317", {"start": v(24.03, -34.07) * mm, "end": v(23.97, -33.9) * mm});
            skLineSegment(sketch, "E5318", {"start": v(23.97, -33.9) * mm, "end": v(23.9, -33.71) * mm});
            skLineSegment(sketch, "E5319", {"start": v(23.9, -33.71) * mm, "end": v(23.87, -33.64) * mm});
            skLineSegment(sketch, "E5320", {"start": v(23.87, -33.64) * mm, "end": v(24.02, -33.53) * mm});
            skLineSegment(sketch, "E5321", {"start": v(24.02, -33.53) * mm, "end": v(24.18, -33.41) * mm});
            skLineSegment(sketch, "E5322", {"start": v(24.18, -33.41) * mm, "end": v(24.34, -33.3) * mm});
            skLineSegment(sketch, "E5323", {"start": v(24.34, -33.3) * mm, "end": v(24.5, -33.19) * mm});
            skLineSegment(sketch, "E5324", {"start": v(24.5, -33.19) * mm, "end": v(24.65, -33.07) * mm});
            skLineSegment(sketch, "E5325", {"start": v(24.65, -33.07) * mm, "end": v(24.8, -32.95) * mm});
            skLineSegment(sketch, "E5326", {"start": v(24.8, -32.95) * mm, "end": v(24.96, -32.84) * mm});
            skLineSegment(sketch, "E5327", {"start": v(24.96, -32.84) * mm, "end": v(24.99, -32.82) * mm});
            skLineSegment(sketch, "E5328", {"start": v(24.99, -32.82) * mm, "end": v(25.12, -32.93) * mm});
            skLineSegment(sketch, "E5329", {"start": v(25.12, -32.93) * mm, "end": v(25.26, -33.04) * mm});
            skLineSegment(sketch, "E5330", {"start": v(25.26, -33.04) * mm, "end": v(25.4, -33.15) * mm});
            skLineSegment(sketch, "E5331", {"start": v(25.4, -33.15) * mm, "end": v(25.55, -33.26) * mm});
            skLineSegment(sketch, "E5332", {"start": v(25.55, -33.26) * mm, "end": v(25.7, -33.36) * mm});
            skLineSegment(sketch, "E5333", {"start": v(25.7, -33.36) * mm, "end": v(25.84, -33.46) * mm});
            skLineSegment(sketch, "E5334", {"start": v(25.84, -33.46) * mm, "end": v(26, -33.56) * mm});
            skLineSegment(sketch, "E5335", {"start": v(26, -33.56) * mm, "end": v(26.14, -33.66) * mm});
            skLineSegment(sketch, "E5336", {"start": v(26.14, -33.66) * mm, "end": v(26.29, -33.75) * mm});
            skLineSegment(sketch, "E5337", {"start": v(26.29, -33.75) * mm, "end": v(26.44, -33.85) * mm});
            skLineSegment(sketch, "E5338", {"start": v(26.44, -33.85) * mm, "end": v(26.6, -33.95) * mm});
            skLineSegment(sketch, "E5339", {"start": v(26.6, -33.95) * mm, "end": v(26.77, -34.04) * mm});
            skLineSegment(sketch, "E5340", {"start": v(26.77, -34.04) * mm, "end": v(26.92, -34.13) * mm});
            skLineSegment(sketch, "E5341", {"start": v(26.92, -34.13) * mm, "end": v(27.08, -34.21) * mm});
            skLineSegment(sketch, "E5342", {"start": v(27.08, -34.21) * mm, "end": v(27.24, -34.3) * mm});
            skLineSegment(sketch, "E5343", {"start": v(27.24, -34.3) * mm, "end": v(27.4, -34.39) * mm});
            skLineSegment(sketch, "E5344", {"start": v(27.4, -34.39) * mm, "end": v(27.57, -34.47) * mm});
            skLineSegment(sketch, "E5345", {"start": v(27.57, -34.47) * mm, "end": v(27.74, -34.56) * mm});
            skLineSegment(sketch, "E5346", {"start": v(27.74, -34.56) * mm, "end": v(27.92, -34.65) * mm});
            skLineSegment(sketch, "E5347", {"start": v(27.92, -34.65) * mm, "end": v(28.05, -34.7) * mm});
            skLineSegment(sketch, "E5348", {"start": v(28.05, -34.7) * mm, "end": v(28.2, -34.59) * mm});
            skLineSegment(sketch, "E5349", {"start": v(28.2, -34.59) * mm, "end": v(28.33, -34.47) * mm});
            skLineSegment(sketch, "E5350", {"start": v(28.33, -34.47) * mm, "end": v(28.48, -34.35) * mm});
            skLineSegment(sketch, "E5351", {"start": v(28.48, -34.35) * mm, "end": v(28.62, -34.24) * mm});
            skLineSegment(sketch, "E5352", {"start": v(28.62, -34.24) * mm, "end": v(28.69, -34.18) * mm});
            skLineSegment(sketch, "E5353", {"start": v(28.69, -34.18) * mm, "end": v(28.64, -34) * mm});
            skLineSegment(sketch, "E5354", {"start": v(28.64, -34) * mm, "end": v(28.6, -33.82) * mm});
            skLineSegment(sketch, "E5355", {"start": v(28.6, -33.82) * mm, "end": v(28.54, -33.65) * mm});
            skLineSegment(sketch, "E5356", {"start": v(28.54, -33.65) * mm, "end": v(28.5, -33.48) * mm});
            skLineSegment(sketch, "E5357", {"start": v(28.5, -33.48) * mm, "end": v(28.45, -33.31) * mm});
            skLineSegment(sketch, "E5358", {"start": v(28.45, -33.31) * mm, "end": v(28.39, -33.13) * mm});
            skLineSegment(sketch, "E5359", {"start": v(28.39, -33.13) * mm, "end": v(28.33, -32.96) * mm});
            skLineSegment(sketch, "E5360", {"start": v(28.33, -32.96) * mm, "end": v(28.27, -32.77) * mm});
            skLineSegment(sketch, "E5361", {"start": v(28.27, -32.77) * mm, "end": v(28.2, -32.6) * mm});
            skLineSegment(sketch, "E5362", {"start": v(28.2, -32.6) * mm, "end": v(28.14, -32.42) * mm});
            skLineSegment(sketch, "E5363", {"start": v(28.14, -32.42) * mm, "end": v(28.08, -32.24) * mm});
            skLineSegment(sketch, "E5364", {"start": v(28.08, -32.24) * mm, "end": v(28, -32.07) * mm});
            skLineSegment(sketch, "E5365", {"start": v(28, -32.07) * mm, "end": v(27.94, -31.9) * mm});
            skLineSegment(sketch, "E5366", {"start": v(27.94, -31.9) * mm, "end": v(27.87, -31.72) * mm});
            skLineSegment(sketch, "E5367", {"start": v(27.87, -31.72) * mm, "end": v(27.8, -31.55) * mm});
            skLineSegment(sketch, "E5368", {"start": v(27.8, -31.55) * mm, "end": v(27.72, -31.4) * mm});
            skLineSegment(sketch, "E5369", {"start": v(27.72, -31.4) * mm, "end": v(27.64, -31.22) * mm});
            skLineSegment(sketch, "E5370", {"start": v(27.64, -31.22) * mm, "end": v(27.55, -31.05) * mm});
            skLineSegment(sketch, "E5371", {"start": v(27.55, -31.05) * mm, "end": v(27.46, -30.88) * mm});
            skLineSegment(sketch, "E5372", {"start": v(27.46, -30.88) * mm, "end": v(27.42, -30.8) * mm});
            skLineSegment(sketch, "E5373", {"start": v(27.42, -30.8) * mm, "end": v(27.57, -30.68) * mm});
            skLineSegment(sketch, "E5374", {"start": v(27.57, -30.68) * mm, "end": v(27.71, -30.55) * mm});
            skLineSegment(sketch, "E5375", {"start": v(27.71, -30.55) * mm, "end": v(27.85, -30.42) * mm});
            skLineSegment(sketch, "E5376", {"start": v(27.85, -30.42) * mm, "end": v(28, -30.29) * mm});
            skLineSegment(sketch, "E5377", {"start": v(28, -30.29) * mm, "end": v(28.14, -30.16) * mm});
            skLineSegment(sketch, "E5378", {"start": v(28.14, -30.16) * mm, "end": v(28.28, -30.03) * mm});
            skLineSegment(sketch, "E5379", {"start": v(28.28, -30.03) * mm, "end": v(28.42, -29.9) * mm});
            skLineSegment(sketch, "E5380", {"start": v(28.42, -29.9) * mm, "end": v(28.45, -29.88) * mm});
            skLineSegment(sketch, "E5381", {"start": v(28.45, -29.88) * mm, "end": v(28.59, -29.97) * mm});
            skLineSegment(sketch, "E5382", {"start": v(28.59, -29.97) * mm, "end": v(28.74, -30.06) * mm});
            skLineSegment(sketch, "E5383", {"start": v(28.74, -30.06) * mm, "end": v(28.9, -30.15) * mm});
            skLineSegment(sketch, "E5384", {"start": v(28.9, -30.15) * mm, "end": v(29.05, -30.25) * mm});
            skLineSegment(sketch, "E5385", {"start": v(29.05, -30.25) * mm, "end": v(29.2, -30.33) * mm});
            skLineSegment(sketch, "E5386", {"start": v(29.2, -30.33) * mm, "end": v(29.36, -30.41) * mm});
            skLineSegment(sketch, "E5387", {"start": v(29.36, -30.41) * mm, "end": v(29.53, -30.5) * mm});
            skLineSegment(sketch, "E5388", {"start": v(29.53, -30.5) * mm, "end": v(29.68, -30.58) * mm});
            skLineSegment(sketch, "E5389", {"start": v(29.68, -30.58) * mm, "end": v(29.84, -30.66) * mm});
            skLineSegment(sketch, "E5390", {"start": v(29.84, -30.66) * mm, "end": v(30, -30.73) * mm});
            skLineSegment(sketch, "E5391", {"start": v(30, -30.73) * mm, "end": v(30.18, -30.81) * mm});
            skLineSegment(sketch, "E5392", {"start": v(30.18, -30.81) * mm, "end": v(30.36, -30.9) * mm});
            skLineSegment(sketch, "E5393", {"start": v(30.36, -30.9) * mm, "end": v(30.52, -30.96) * mm});
            skLineSegment(sketch, "E5394", {"start": v(30.52, -30.96) * mm, "end": v(30.68, -31.03) * mm});
            skLineSegment(sketch, "E5395", {"start": v(30.68, -31.03) * mm, "end": v(30.85, -31.1) * mm});
            skLineSegment(sketch, "E5396", {"start": v(30.85, -31.1) * mm, "end": v(31.02, -31.16) * mm});
            skLineSegment(sketch, "E5397", {"start": v(31.02, -31.16) * mm, "end": v(31.2, -31.23) * mm});
            skLineSegment(sketch, "E5398", {"start": v(31.2, -31.23) * mm, "end": v(31.38, -31.3) * mm});
            skLineSegment(sketch, "E5399", {"start": v(31.38, -31.3) * mm, "end": v(31.56, -31.36) * mm});
            skLineSegment(sketch, "E5400", {"start": v(31.56, -31.36) * mm, "end": v(31.7, -31.4) * mm});
            skLineSegment(sketch, "E5401", {"start": v(31.7, -31.4) * mm, "end": v(31.83, -31.28) * mm});
            skLineSegment(sketch, "E5402", {"start": v(31.83, -31.28) * mm, "end": v(31.95, -31.15) * mm});
            skLineSegment(sketch, "E5403", {"start": v(31.95, -31.15) * mm, "end": v(32.08, -31.01) * mm});
            skLineSegment(sketch, "E5404", {"start": v(32.08, -31.01) * mm, "end": v(32.21, -30.88) * mm});
            skLineSegment(sketch, "E5405", {"start": v(32.21, -30.88) * mm, "end": v(32.27, -30.82) * mm});
            skLineSegment(sketch, "E5406", {"start": v(32.27, -30.82) * mm, "end": v(32.2, -30.64) * mm});
            skLineSegment(sketch, "E5407", {"start": v(32.2, -30.64) * mm, "end": v(32.14, -30.47) * mm});
            skLineSegment(sketch, "E5408", {"start": v(32.14, -30.47) * mm, "end": v(32.07, -30.3) * mm});
            skLineSegment(sketch, "E5409", {"start": v(32.07, -30.3) * mm, "end": v(32, -30.14) * mm});
            skLineSegment(sketch, "E5410", {"start": v(32, -30.14) * mm, "end": v(31.94, -29.98) * mm});
            skLineSegment(sketch, "E5411", {"start": v(31.94, -29.98) * mm, "end": v(31.86, -29.81) * mm});
            skLineSegment(sketch, "E5412", {"start": v(31.86, -29.81) * mm, "end": v(31.79, -29.64) * mm});
            skLineSegment(sketch, "E5413", {"start": v(31.79, -29.64) * mm, "end": v(31.7, -29.46) * mm});
            skLineSegment(sketch, "E5414", {"start": v(31.7, -29.46) * mm, "end": v(31.62, -29.3) * mm});
            skLineSegment(sketch, "E5415", {"start": v(31.62, -29.3) * mm, "end": v(31.54, -29.12) * mm});
            skLineSegment(sketch, "E5416", {"start": v(31.54, -29.12) * mm, "end": v(31.45, -28.96) * mm});
            skLineSegment(sketch, "E5417", {"start": v(31.45, -28.96) * mm, "end": v(31.37, -28.79) * mm});
            skLineSegment(sketch, "E5418", {"start": v(31.37, -28.79) * mm, "end": v(31.28, -28.63) * mm});
            skLineSegment(sketch, "E5419", {"start": v(31.28, -28.63) * mm, "end": v(31.19, -28.46) * mm});
            skLineSegment(sketch, "E5420", {"start": v(31.19, -28.46) * mm, "end": v(31.1, -28.3) * mm});
            skLineSegment(sketch, "E5421", {"start": v(31.1, -28.3) * mm, "end": v(31, -28.15) * mm});
            skLineSegment(sketch, "E5422", {"start": v(31, -28.15) * mm, "end": v(30.9, -28) * mm});
            skLineSegment(sketch, "E5423", {"start": v(30.9, -28) * mm, "end": v(30.8, -27.83) * mm});
            skLineSegment(sketch, "E5424", {"start": v(30.8, -27.83) * mm, "end": v(30.7, -27.67) * mm});
            skLineSegment(sketch, "E5425", {"start": v(30.7, -27.67) * mm, "end": v(30.65, -27.6) * mm});
            skLineSegment(sketch, "E5426", {"start": v(30.65, -27.6) * mm, "end": v(30.77, -27.46) * mm});
            skLineSegment(sketch, "E5427", {"start": v(30.77, -27.46) * mm, "end": v(30.9, -27.32) * mm});
            skLineSegment(sketch, "E5428", {"start": v(30.9, -27.32) * mm, "end": v(31.03, -27.17) * mm});
            skLineSegment(sketch, "E5429", {"start": v(31.03, -27.17) * mm, "end": v(31.16, -27.03) * mm});
            skLineSegment(sketch, "E5430", {"start": v(31.16, -27.03) * mm, "end": v(31.28, -26.88) * mm});
            skLineSegment(sketch, "E5431", {"start": v(31.28, -26.88) * mm, "end": v(31.41, -26.73) * mm});
            skLineSegment(sketch, "E5432", {"start": v(31.41, -26.73) * mm, "end": v(31.54, -26.6) * mm});
            skLineSegment(sketch, "E5433", {"start": v(31.54, -26.6) * mm, "end": v(31.56, -26.57) * mm});
            skLineSegment(sketch, "E5434", {"start": v(31.56, -26.57) * mm, "end": v(31.71, -26.64) * mm});
            skLineSegment(sketch, "E5435", {"start": v(31.71, -26.64) * mm, "end": v(31.88, -26.72) * mm});
            skLineSegment(sketch, "E5436", {"start": v(31.88, -26.72) * mm, "end": v(32.04, -26.8) * mm});
            skLineSegment(sketch, "E5437", {"start": v(32.04, -26.8) * mm, "end": v(32.2, -26.87) * mm});
            skLineSegment(sketch, "E5438", {"start": v(32.2, -26.87) * mm, "end": v(32.36, -26.93) * mm});
            skLineSegment(sketch, "E5439", {"start": v(32.36, -26.93) * mm, "end": v(32.53, -27) * mm});
            skLineSegment(sketch, "E5440", {"start": v(32.53, -27) * mm, "end": v(32.7, -27.07) * mm});
            skLineSegment(sketch, "E5441", {"start": v(32.7, -27.07) * mm, "end": v(32.87, -27.13) * mm});
            skLineSegment(sketch, "E5442", {"start": v(32.87, -27.13) * mm, "end": v(33.03, -27.19) * mm});
            skLineSegment(sketch, "E5443", {"start": v(33.03, -27.19) * mm, "end": v(33.2, -27.25) * mm});
            skLineSegment(sketch, "E5444", {"start": v(33.2, -27.25) * mm, "end": v(33.39, -27.3) * mm});
            skLineSegment(sketch, "E5445", {"start": v(33.39, -27.3) * mm, "end": v(33.57, -27.36) * mm});
            skLineSegment(sketch, "E5446", {"start": v(33.57, -27.36) * mm, "end": v(33.74, -27.41) * mm});
            skLineSegment(sketch, "E5447", {"start": v(33.74, -27.41) * mm, "end": v(33.9, -27.46) * mm});
            skLineSegment(sketch, "E5448", {"start": v(33.9, -27.46) * mm, "end": v(34.08, -27.51) * mm});
            skLineSegment(sketch, "E5449", {"start": v(34.08, -27.51) * mm, "end": v(34.26, -27.56) * mm});
            skLineSegment(sketch, "E5450", {"start": v(34.26, -27.56) * mm, "end": v(34.44, -27.6) * mm});
            skLineSegment(sketch, "E5451", {"start": v(34.44, -27.6) * mm, "end": v(34.63, -27.65) * mm});
            skLineSegment(sketch, "E5452", {"start": v(34.63, -27.65) * mm, "end": v(34.82, -27.7) * mm});
            skLineSegment(sketch, "E5453", {"start": v(34.82, -27.7) * mm, "end": v(34.96, -27.73) * mm});
            skLineSegment(sketch, "E5454", {"start": v(34.96, -27.73) * mm, "end": v(35.07, -27.59) * mm});
            skLineSegment(sketch, "E5455", {"start": v(35.07, -27.59) * mm, "end": v(35.19, -27.44) * mm});
            skLineSegment(sketch, "E5456", {"start": v(35.19, -27.44) * mm, "end": v(35.3, -27.3) * mm});
            skLineSegment(sketch, "E5457", {"start": v(35.3, -27.3) * mm, "end": v(35.41, -27.15) * mm});
            skLineSegment(sketch, "E5458", {"start": v(35.41, -27.15) * mm, "end": v(35.47, -27.08) * mm});
            skLineSegment(sketch, "E5459", {"start": v(35.47, -27.08) * mm, "end": v(35.38, -26.9) * mm});
            skLineSegment(sketch, "E5460", {"start": v(35.38, -26.9) * mm, "end": v(35.3, -26.75) * mm});
            skLineSegment(sketch, "E5461", {"start": v(35.3, -26.75) * mm, "end": v(35.21, -26.59) * mm});
            skLineSegment(sketch, "E5462", {"start": v(35.21, -26.59) * mm, "end": v(35.13, -26.44) * mm});
            skLineSegment(sketch, "E5463", {"start": v(35.13, -26.44) * mm, "end": v(35.04, -26.29) * mm});
            skLineSegment(sketch, "E5464", {"start": v(35.04, -26.29) * mm, "end": v(34.95, -26.12) * mm});
            skLineSegment(sketch, "E5465", {"start": v(34.95, -26.12) * mm, "end": v(34.85, -25.96) * mm});
            skLineSegment(sketch, "E5466", {"start": v(34.85, -25.96) * mm, "end": v(34.75, -25.8) * mm});
            skLineSegment(sketch, "E5467", {"start": v(34.75, -25.8) * mm, "end": v(34.65, -25.64) * mm});
            skLineSegment(sketch, "E5468", {"start": v(34.65, -25.64) * mm, "end": v(34.55, -25.48) * mm});
            skLineSegment(sketch, "E5469", {"start": v(34.55, -25.48) * mm, "end": v(34.45, -25.32) * mm});
            skLineSegment(sketch, "E5470", {"start": v(34.45, -25.32) * mm, "end": v(34.34, -25.16) * mm});
            skLineSegment(sketch, "E5471", {"start": v(34.34, -25.16) * mm, "end": v(34.24, -25.02) * mm});
            skLineSegment(sketch, "E5472", {"start": v(34.24, -25.02) * mm, "end": v(34.13, -24.86) * mm});
            skLineSegment(sketch, "E5473", {"start": v(34.13, -24.86) * mm, "end": v(34.02, -24.71) * mm});
            skLineSegment(sketch, "E5474", {"start": v(34.02, -24.71) * mm, "end": v(33.91, -24.57) * mm});
            skLineSegment(sketch, "E5475", {"start": v(33.91, -24.57) * mm, "end": v(33.8, -24.42) * mm});
            skLineSegment(sketch, "E5476", {"start": v(33.8, -24.42) * mm, "end": v(33.68, -24.28) * mm});
            skLineSegment(sketch, "E5477", {"start": v(33.68, -24.28) * mm, "end": v(33.55, -24.13) * mm});
            skLineSegment(sketch, "E5478", {"start": v(33.55, -24.13) * mm, "end": v(33.5, -24.07) * mm});
            skLineSegment(sketch, "E5479", {"start": v(33.5, -24.07) * mm, "end": v(33.6, -23.91) * mm});
            skLineSegment(sketch, "E5480", {"start": v(33.6, -23.91) * mm, "end": v(33.72, -23.75) * mm});
            skLineSegment(sketch, "E5481", {"start": v(33.72, -23.75) * mm, "end": v(33.83, -23.6) * mm});
            skLineSegment(sketch, "E5482", {"start": v(33.83, -23.6) * mm, "end": v(33.94, -23.43) * mm});
            skLineSegment(sketch, "E5483", {"start": v(33.94, -23.43) * mm, "end": v(34.05, -23.28) * mm});
            skLineSegment(sketch, "E5484", {"start": v(34.05, -23.28) * mm, "end": v(34.16, -23.11) * mm});
            skLineSegment(sketch, "E5485", {"start": v(34.16, -23.11) * mm, "end": v(34.27, -22.96) * mm});
            skLineSegment(sketch, "E5486", {"start": v(34.27, -22.96) * mm, "end": v(34.3, -22.93) * mm});
            skLineSegment(sketch, "E5487", {"start": v(34.3, -22.93) * mm, "end": v(34.45, -23) * mm});
            skLineSegment(sketch, "E5488", {"start": v(34.45, -23) * mm, "end": v(34.62, -23.05) * mm});
            skLineSegment(sketch, "E5489", {"start": v(34.62, -23.05) * mm, "end": v(34.79, -23.1) * mm});
            skLineSegment(sketch, "E5490", {"start": v(34.79, -23.1) * mm, "end": v(34.97, -23.16) * mm});
            skLineSegment(sketch, "E5491", {"start": v(34.97, -23.16) * mm, "end": v(35.13, -23.2) * mm});
            skLineSegment(sketch, "E5492", {"start": v(35.13, -23.2) * mm, "end": v(35.3, -23.26) * mm});
            skLineSegment(sketch, "E5493", {"start": v(35.3, -23.26) * mm, "end": v(35.49, -23.3) * mm});
            skLineSegment(sketch, "E5494", {"start": v(35.49, -23.3) * mm, "end": v(35.65, -23.35) * mm});
            skLineSegment(sketch, "E5495", {"start": v(35.65, -23.35) * mm, "end": v(35.82, -23.39) * mm});
            skLineSegment(sketch, "E5496", {"start": v(35.82, -23.39) * mm, "end": v(36, -23.43) * mm});
            skLineSegment(sketch, "E5497", {"start": v(36, -23.43) * mm, "end": v(36.19, -23.47) * mm});
            skLineSegment(sketch, "E5498", {"start": v(36.19, -23.47) * mm, "end": v(36.38, -23.5) * mm});
            skLineSegment(sketch, "E5499", {"start": v(36.38, -23.5) * mm, "end": v(36.55, -23.54) * mm});
            skLineSegment(sketch, "E5500", {"start": v(36.55, -23.54) * mm, "end": v(36.72, -23.57) * mm});
            skLineSegment(sketch, "E5501", {"start": v(36.72, -23.57) * mm, "end": v(36.9, -23.6) * mm});
            skLineSegment(sketch, "E5502", {"start": v(36.9, -23.6) * mm, "end": v(37.08, -23.62) * mm});
            skLineSegment(sketch, "E5503", {"start": v(37.08, -23.62) * mm, "end": v(37.27, -23.65) * mm});
            skLineSegment(sketch, "E5504", {"start": v(37.27, -23.65) * mm, "end": v(37.46, -23.68) * mm});
            skLineSegment(sketch, "E5505", {"start": v(37.46, -23.68) * mm, "end": v(37.66, -23.7) * mm});
            skLineSegment(sketch, "E5506", {"start": v(37.66, -23.7) * mm, "end": v(37.8, -23.72) * mm});
            skLineSegment(sketch, "E5507", {"start": v(37.8, -23.72) * mm, "end": v(37.9, -23.56) * mm});
            skLineSegment(sketch, "E5508", {"start": v(37.9, -23.56) * mm, "end": v(38, -23.4) * mm});
            skLineSegment(sketch, "E5509", {"start": v(38, -23.4) * mm, "end": v(38.09, -23.25) * mm});
            skLineSegment(sketch, "E5510", {"start": v(38.09, -23.25) * mm, "end": v(38.19, -23.09) * mm});
            skLineSegment(sketch, "E5511", {"start": v(38.19, -23.09) * mm, "end": v(38.23, -23.01) * mm});
            skLineSegment(sketch, "E5512", {"start": v(38.23, -23.01) * mm, "end": v(38.13, -22.85) * mm});
            skLineSegment(sketch, "E5513", {"start": v(38.13, -22.85) * mm, "end": v(38.02, -22.7) * mm});
            skLineSegment(sketch, "E5514", {"start": v(38.02, -22.7) * mm, "end": v(37.92, -22.55) * mm});
            skLineSegment(sketch, "E5515", {"start": v(37.92, -22.55) * mm, "end": v(37.82, -22.41) * mm});
            skLineSegment(sketch, "E5516", {"start": v(37.82, -22.41) * mm, "end": v(37.72, -22.27) * mm});
            skLineSegment(sketch, "E5517", {"start": v(37.72, -22.27) * mm, "end": v(37.61, -22.12) * mm});
            skLineSegment(sketch, "E5518", {"start": v(37.61, -22.12) * mm, "end": v(37.5, -21.97) * mm});
            skLineSegment(sketch, "E5519", {"start": v(37.5, -21.97) * mm, "end": v(37.38, -21.82) * mm});
            skLineSegment(sketch, "E5520", {"start": v(37.38, -21.82) * mm, "end": v(37.27, -21.67) * mm});
            skLineSegment(sketch, "E5521", {"start": v(37.27, -21.67) * mm, "end": v(37.15, -21.52) * mm});
            skLineSegment(sketch, "E5522", {"start": v(37.15, -21.52) * mm, "end": v(37.03, -21.38) * mm});
            skLineSegment(sketch, "E5523", {"start": v(37.03, -21.38) * mm, "end": v(36.9, -21.23) * mm});
            skLineSegment(sketch, "E5524", {"start": v(36.9, -21.23) * mm, "end": v(36.79, -21.1) * mm});
            skLineSegment(sketch, "E5525", {"start": v(36.79, -21.1) * mm, "end": v(36.66, -20.95) * mm});
            skLineSegment(sketch, "E5526", {"start": v(36.66, -20.95) * mm, "end": v(36.53, -20.82) * mm});
            skLineSegment(sketch, "E5527", {"start": v(36.53, -20.82) * mm, "end": v(36.41, -20.7) * mm});
            skLineSegment(sketch, "E5528", {"start": v(36.41, -20.7) * mm, "end": v(36.28, -20.56) * mm});
            skLineSegment(sketch, "E5529", {"start": v(36.28, -20.56) * mm, "end": v(36.14, -20.42) * mm});
            skLineSegment(sketch, "E5530", {"start": v(36.14, -20.42) * mm, "end": v(36, -20.29) * mm});
            skLineSegment(sketch, "E5531", {"start": v(36, -20.29) * mm, "end": v(35.94, -20.23) * mm});
            skLineSegment(sketch, "E5532", {"start": v(35.94, -20.23) * mm, "end": v(36.04, -20.07) * mm});
            skLineSegment(sketch, "E5533", {"start": v(36.04, -20.07) * mm, "end": v(36.13, -19.9) * mm});
            skLineSegment(sketch, "E5534", {"start": v(36.13, -19.9) * mm, "end": v(36.22, -19.73) * mm});
            skLineSegment(sketch, "E5535", {"start": v(36.22, -19.73) * mm, "end": v(36.32, -19.56) * mm});
            skLineSegment(sketch, "E5536", {"start": v(36.32, -19.56) * mm, "end": v(36.4, -19.4) * mm});
            skLineSegment(sketch, "E5537", {"start": v(36.4, -19.4) * mm, "end": v(36.5, -19.21) * mm});
            skLineSegment(sketch, "E5538", {"start": v(36.5, -19.21) * mm, "end": v(36.6, -19.05) * mm});
            skLineSegment(sketch, "E5539", {"start": v(36.6, -19.05) * mm, "end": v(36.6, -19.02) * mm});
            skLineSegment(sketch, "E5540", {"start": v(36.6, -19.02) * mm, "end": v(36.77, -19.06) * mm});
            skLineSegment(sketch, "E5541", {"start": v(36.77, -19.06) * mm, "end": v(36.95, -19.1) * mm});
            skLineSegment(sketch, "E5542", {"start": v(36.95, -19.1) * mm, "end": v(37.12, -19.14) * mm});
            skLineSegment(sketch, "E5543", {"start": v(37.12, -19.14) * mm, "end": v(37.3, -19.17) * mm});
            skLineSegment(sketch, "E5544", {"start": v(37.3, -19.17) * mm, "end": v(37.47, -19.2) * mm});
            skLineSegment(sketch, "E5545", {"start": v(37.47, -19.2) * mm, "end": v(37.65, -19.23) * mm});
            skLineSegment(sketch, "E5546", {"start": v(37.65, -19.23) * mm, "end": v(37.84, -19.26) * mm});
            skLineSegment(sketch, "E5547", {"start": v(37.84, -19.26) * mm, "end": v(38, -19.28) * mm});
            skLineSegment(sketch, "E5548", {"start": v(38, -19.28) * mm, "end": v(38.18, -19.3) * mm});
            skLineSegment(sketch, "E5549", {"start": v(38.18, -19.3) * mm, "end": v(38.36, -19.32) * mm});
            skLineSegment(sketch, "E5550", {"start": v(38.36, -19.32) * mm, "end": v(38.55, -19.34) * mm});
            skLineSegment(sketch, "E5551", {"start": v(38.55, -19.34) * mm, "end": v(38.74, -19.36) * mm});
            skLineSegment(sketch, "E5552", {"start": v(38.74, -19.36) * mm, "end": v(38.92, -19.37) * mm});
            skLineSegment(sketch, "E5553", {"start": v(38.92, -19.37) * mm, "end": v(39.1, -19.38) * mm});
            skLineSegment(sketch, "E5554", {"start": v(39.1, -19.38) * mm, "end": v(39.27, -19.4) * mm});
            skLineSegment(sketch, "E5555", {"start": v(39.27, -19.4) * mm, "end": v(39.46, -19.4) * mm});
            skLineSegment(sketch, "E5556", {"start": v(39.46, -19.4) * mm, "end": v(39.65, -19.4) * mm});
            skLineSegment(sketch, "E5557", {"start": v(39.65, -19.4) * mm, "end": v(39.84, -19.41) * mm});
            skLineSegment(sketch, "E5558", {"start": v(39.84, -19.41) * mm, "end": v(40.04, -19.41) * mm});
            skLineSegment(sketch, "E5559", {"start": v(40.04, -19.41) * mm, "end": v(40.18, -19.42) * mm});
            skLineSegment(sketch, "E5560", {"start": v(40.18, -19.42) * mm, "end": v(40.26, -19.25) * mm});
            skLineSegment(sketch, "E5561", {"start": v(40.26, -19.25) * mm, "end": v(40.34, -19.08) * mm});
            skLineSegment(sketch, "E5562", {"start": v(40.34, -19.08) * mm, "end": v(40.42, -18.91) * mm});
            skLineSegment(sketch, "E5563", {"start": v(40.42, -18.91) * mm, "end": v(40.5, -18.75) * mm});
            skLineSegment(sketch, "E5564", {"start": v(40.5, -18.75) * mm, "end": v(40.53, -18.67) * mm});
            skLineSegment(sketch, "E5565", {"start": v(40.53, -18.67) * mm, "end": v(40.4, -18.52) * mm});
            skLineSegment(sketch, "E5566", {"start": v(40.4, -18.52) * mm, "end": v(40.3, -18.38) * mm});
            skLineSegment(sketch, "E5567", {"start": v(40.3, -18.38) * mm, "end": v(40.17, -18.25) * mm});
            skLineSegment(sketch, "E5568", {"start": v(40.17, -18.25) * mm, "end": v(40.06, -18.11) * mm});
            skLineSegment(sketch, "E5569", {"start": v(40.06, -18.11) * mm, "end": v(39.94, -17.99) * mm});
            skLineSegment(sketch, "E5570", {"start": v(39.94, -17.99) * mm, "end": v(39.82, -17.85) * mm});
            skLineSegment(sketch, "E5571", {"start": v(39.82, -17.85) * mm, "end": v(39.69, -17.71) * mm});
            skLineSegment(sketch, "E5572", {"start": v(39.69, -17.71) * mm, "end": v(39.56, -17.57) * mm});
            skLineSegment(sketch, "E5573", {"start": v(39.56, -17.57) * mm, "end": v(39.42, -17.44) * mm});
            skLineSegment(sketch, "E5574", {"start": v(39.42, -17.44) * mm, "end": v(39.29, -17.3) * mm});
            skLineSegment(sketch, "E5575", {"start": v(39.29, -17.3) * mm, "end": v(39.15, -17.17) * mm});
            skLineSegment(sketch, "E5576", {"start": v(39.15, -17.17) * mm, "end": v(39.02, -17.04) * mm});
            skLineSegment(sketch, "E5577", {"start": v(39.02, -17.04) * mm, "end": v(38.88, -16.92) * mm});
            skLineSegment(sketch, "E5578", {"start": v(38.88, -16.92) * mm, "end": v(38.74, -16.8) * mm});
            skLineSegment(sketch, "E5579", {"start": v(38.74, -16.8) * mm, "end": v(38.6, -16.67) * mm});
            skLineSegment(sketch, "E5580", {"start": v(38.6, -16.67) * mm, "end": v(38.47, -16.56) * mm});
            skLineSegment(sketch, "E5581", {"start": v(38.47, -16.56) * mm, "end": v(38.32, -16.44) * mm});
            skLineSegment(sketch, "E5582", {"start": v(38.32, -16.44) * mm, "end": v(38.17, -16.32) * mm});
            skLineSegment(sketch, "E5583", {"start": v(38.17, -16.32) * mm, "end": v(38.02, -16.2) * mm});
            skLineSegment(sketch, "E5584", {"start": v(38.02, -16.2) * mm, "end": v(37.95, -16.16) * mm});
            skLineSegment(sketch, "E5585", {"start": v(37.95, -16.16) * mm, "end": v(38.03, -15.98) * mm});
            skLineSegment(sketch, "E5586", {"start": v(38.03, -15.98) * mm, "end": v(38.1, -15.8) * mm});
            skLineSegment(sketch, "E5587", {"start": v(38.1, -15.8) * mm, "end": v(38.17, -15.63) * mm});
            skLineSegment(sketch, "E5588", {"start": v(38.17, -15.63) * mm, "end": v(38.25, -15.44) * mm});
            skLineSegment(sketch, "E5589", {"start": v(38.25, -15.44) * mm, "end": v(38.32, -15.27) * mm});
            skLineSegment(sketch, "E5590", {"start": v(38.32, -15.27) * mm, "end": v(38.4, -15.08) * mm});
            skLineSegment(sketch, "E5591", {"start": v(38.4, -15.08) * mm, "end": v(38.46, -14.9) * mm});
            skLineSegment(sketch, "E5592", {"start": v(38.46, -14.9) * mm, "end": v(38.48, -14.88) * mm});
            skLineSegment(sketch, "E5593", {"start": v(38.48, -14.88) * mm, "end": v(38.65, -14.9) * mm});
            skLineSegment(sketch, "E5594", {"start": v(38.65, -14.9) * mm, "end": v(38.83, -14.92) * mm});
            skLineSegment(sketch, "E5595", {"start": v(38.83, -14.92) * mm, "end": v(39, -14.94) * mm});
            skLineSegment(sketch, "E5596", {"start": v(39, -14.94) * mm, "end": v(39.19, -14.95) * mm});
            skLineSegment(sketch, "E5597", {"start": v(39.19, -14.95) * mm, "end": v(39.36, -14.96) * mm});
            skLineSegment(sketch, "E5598", {"start": v(39.36, -14.96) * mm, "end": v(39.54, -14.97) * mm});
            skLineSegment(sketch, "E5599", {"start": v(39.54, -14.97) * mm, "end": v(39.72, -14.98) * mm});
            skLineSegment(sketch, "E5600", {"start": v(39.72, -14.98) * mm, "end": v(39.9, -14.98) * mm});
            skLineSegment(sketch, "E5601", {"start": v(39.9, -14.98) * mm, "end": v(40.07, -14.99) * mm});
            skLineSegment(sketch, "E5602", {"start": v(40.07, -14.99) * mm, "end": v(40.26, -14.99) * mm});
            skLineSegment(sketch, "E5603", {"start": v(40.26, -14.99) * mm, "end": v(40.44, -14.98) * mm});
            skLineSegment(sketch, "E5604", {"start": v(40.44, -14.98) * mm, "end": v(40.64, -14.98) * mm});
            skLineSegment(sketch, "E5605", {"start": v(40.64, -14.98) * mm, "end": v(40.81, -14.97) * mm});
            skLineSegment(sketch, "E5606", {"start": v(40.81, -14.97) * mm, "end": v(40.99, -14.97) * mm});
            skLineSegment(sketch, "E5607", {"start": v(40.99, -14.97) * mm, "end": v(41.17, -14.96) * mm});
            skLineSegment(sketch, "E5608", {"start": v(41.17, -14.96) * mm, "end": v(41.35, -14.94) * mm});
            skLineSegment(sketch, "E5609", {"start": v(41.35, -14.94) * mm, "end": v(41.54, -14.93) * mm});
            skLineSegment(sketch, "E5610", {"start": v(41.54, -14.93) * mm, "end": v(41.73, -14.91) * mm});
            skLineSegment(sketch, "E5611", {"start": v(41.73, -14.91) * mm, "end": v(41.93, -14.9) * mm});
            skLineSegment(sketch, "E5612", {"start": v(41.93, -14.9) * mm, "end": v(42.07, -14.88) * mm});
            skLineSegment(sketch, "E5613", {"start": v(42.07, -14.88) * mm, "end": v(42.13, -14.7) * mm});
            skLineSegment(sketch, "E5614", {"start": v(42.13, -14.7) * mm, "end": v(42.2, -14.53) * mm});
            skLineSegment(sketch, "E5615", {"start": v(42.2, -14.53) * mm, "end": v(42.25, -14.35) * mm});
            skLineSegment(sketch, "E5616", {"start": v(42.25, -14.35) * mm, "end": v(42.31, -14.18) * mm});
            skLineSegment(sketch, "E5617", {"start": v(42.31, -14.18) * mm, "end": v(42.34, -14.1) * mm});
            skLineSegment(sketch, "E5618", {"start": v(42.34, -14.1) * mm, "end": v(42.2, -13.96) * mm});
            skLineSegment(sketch, "E5619", {"start": v(42.2, -13.96) * mm, "end": v(42.07, -13.84) * mm});
            skLineSegment(sketch, "E5620", {"start": v(42.07, -13.84) * mm, "end": v(41.94, -13.71) * mm});
            skLineSegment(sketch, "E5621", {"start": v(41.94, -13.71) * mm, "end": v(41.8, -13.6) * mm});
            skLineSegment(sketch, "E5622", {"start": v(41.8, -13.6) * mm, "end": v(41.68, -13.48) * mm});
            skLineSegment(sketch, "E5623", {"start": v(41.68, -13.48) * mm, "end": v(41.54, -13.36) * mm});
            skLineSegment(sketch, "E5624", {"start": v(41.54, -13.36) * mm, "end": v(41.4, -13.24) * mm});
            skLineSegment(sketch, "E5625", {"start": v(41.4, -13.24) * mm, "end": v(41.25, -13.11) * mm});
            skLineSegment(sketch, "E5626", {"start": v(41.25, -13.11) * mm, "end": v(41.1, -13) * mm});
            skLineSegment(sketch, "E5627", {"start": v(41.1, -13) * mm, "end": v(40.95, -12.88) * mm});
            skLineSegment(sketch, "E5628", {"start": v(40.95, -12.88) * mm, "end": v(40.8, -12.76) * mm});
            skLineSegment(sketch, "E5629", {"start": v(40.8, -12.76) * mm, "end": v(40.65, -12.65) * mm});
            skLineSegment(sketch, "E5630", {"start": v(40.65, -12.65) * mm, "end": v(40.51, -12.54) * mm});
            skLineSegment(sketch, "E5631", {"start": v(40.51, -12.54) * mm, "end": v(40.35, -12.43) * mm});
            skLineSegment(sketch, "E5632", {"start": v(40.35, -12.43) * mm, "end": v(40.2, -12.33) * mm});
            skLineSegment(sketch, "E5633", {"start": v(40.2, -12.33) * mm, "end": v(40.06, -12.23) * mm});
            skLineSegment(sketch, "E5634", {"start": v(40.06, -12.23) * mm, "end": v(39.9, -12.13) * mm});
            skLineSegment(sketch, "E5635", {"start": v(39.9, -12.13) * mm, "end": v(39.74, -12.03) * mm});
            skLineSegment(sketch, "E5636", {"start": v(39.74, -12.03) * mm, "end": v(39.57, -11.92) * mm});
            skLineSegment(sketch, "E5637", {"start": v(39.57, -11.92) * mm, "end": v(39.5, -11.88) * mm});
            skLineSegment(sketch, "E5638", {"start": v(39.5, -11.88) * mm, "end": v(39.55, -11.7) * mm});
            skLineSegment(sketch, "E5639", {"start": v(39.55, -11.7) * mm, "end": v(39.6, -11.51) * mm});
            skLineSegment(sketch, "E5640", {"start": v(39.6, -11.51) * mm, "end": v(39.66, -11.33) * mm});
            skLineSegment(sketch, "E5641", {"start": v(39.66, -11.33) * mm, "end": v(39.72, -11.14) * mm});
            skLineSegment(sketch, "E5642", {"start": v(39.72, -11.14) * mm, "end": v(39.77, -10.96) * mm});
            skLineSegment(sketch, "E5643", {"start": v(39.77, -10.96) * mm, "end": v(39.82, -10.77) * mm});
            skLineSegment(sketch, "E5644", {"start": v(39.82, -10.77) * mm, "end": v(39.87, -10.59) * mm});
            skLineSegment(sketch, "E5645", {"start": v(39.87, -10.59) * mm, "end": v(39.88, -10.55) * mm});
            skLineSegment(sketch, "E5646", {"start": v(39.88, -10.55) * mm, "end": v(40.05, -10.56) * mm});
            skLineSegment(sketch, "E5647", {"start": v(40.05, -10.56) * mm, "end": v(40.23, -10.56) * mm});
            skLineSegment(sketch, "E5648", {"start": v(40.23, -10.56) * mm, "end": v(40.4, -10.56) * mm});
            skLineSegment(sketch, "E5649", {"start": v(40.4, -10.56) * mm, "end": v(40.6, -10.55) * mm});
            skLineSegment(sketch, "E5650", {"start": v(40.6, -10.55) * mm, "end": v(40.76, -10.54) * mm});
            skLineSegment(sketch, "E5651", {"start": v(40.76, -10.54) * mm, "end": v(40.94, -10.53) * mm});
            skLineSegment(sketch, "E5652", {"start": v(40.94, -10.53) * mm, "end": v(41.13, -10.52) * mm});
            skLineSegment(sketch, "E5653", {"start": v(41.13, -10.52) * mm, "end": v(41.3, -10.5) * mm});
            skLineSegment(sketch, "E5654", {"start": v(41.3, -10.5) * mm, "end": v(41.48, -10.49) * mm});
            skLineSegment(sketch, "E5655", {"start": v(41.48, -10.49) * mm, "end": v(41.66, -10.47) * mm});
            skLineSegment(sketch, "E5656", {"start": v(41.66, -10.47) * mm, "end": v(41.85, -10.44) * mm});
            skLineSegment(sketch, "E5657", {"start": v(41.85, -10.44) * mm, "end": v(42.04, -10.42) * mm});
            skLineSegment(sketch, "E5658", {"start": v(42.04, -10.42) * mm, "end": v(42.21, -10.4) * mm});
            skLineSegment(sketch, "E5659", {"start": v(42.21, -10.4) * mm, "end": v(42.38, -10.37) * mm});
            skLineSegment(sketch, "E5660", {"start": v(42.38, -10.37) * mm, "end": v(42.56, -10.34) * mm});
            skLineSegment(sketch, "E5661", {"start": v(42.56, -10.34) * mm, "end": v(42.74, -10.3) * mm});
            skLineSegment(sketch, "E5662", {"start": v(42.74, -10.3) * mm, "end": v(42.93, -10.27) * mm});
            skLineSegment(sketch, "E5663", {"start": v(42.93, -10.27) * mm, "end": v(43.12, -10.23) * mm});
            skLineSegment(sketch, "E5664", {"start": v(43.12, -10.23) * mm, "end": v(43.32, -10.19) * mm});
            skLineSegment(sketch, "E5665", {"start": v(43.32, -10.19) * mm, "end": v(43.45, -10.16) * mm});
            skLineSegment(sketch, "E5666", {"start": v(43.45, -10.16) * mm, "end": v(43.5, -9.98) * mm});
            skLineSegment(sketch, "E5667", {"start": v(43.5, -9.98) * mm, "end": v(43.53, -9.8) * mm});
            skLineSegment(sketch, "E5668", {"start": v(43.53, -9.8) * mm, "end": v(43.57, -9.62) * mm});
            skLineSegment(sketch, "E5669", {"start": v(43.57, -9.62) * mm, "end": v(43.61, -9.44) * mm});
            skLineSegment(sketch, "E5670", {"start": v(43.61, -9.44) * mm, "end": v(43.63, -9.35) * mm});
            skLineSegment(sketch, "E5671", {"start": v(43.63, -9.35) * mm, "end": v(43.48, -9.23) * mm});
            skLineSegment(sketch, "E5672", {"start": v(43.48, -9.23) * mm, "end": v(43.34, -9.12) * mm});
            skLineSegment(sketch, "E5673", {"start": v(43.34, -9.12) * mm, "end": v(43.2, -9.02) * mm});
            skLineSegment(sketch, "E5674", {"start": v(43.2, -9.02) * mm, "end": v(43.05, -8.92) * mm});
            skLineSegment(sketch, "E5675", {"start": v(43.05, -8.92) * mm, "end": v(42.91, -8.82) * mm});
            skLineSegment(sketch, "E5676", {"start": v(42.91, -8.82) * mm, "end": v(42.76, -8.7) * mm});
            skLineSegment(sketch, "E5677", {"start": v(42.76, -8.7) * mm, "end": v(42.6, -8.6) * mm});
            skLineSegment(sketch, "E5678", {"start": v(42.6, -8.6) * mm, "end": v(42.44, -8.5) * mm});
            skLineSegment(sketch, "E5679", {"start": v(42.44, -8.5) * mm, "end": v(42.28, -8.4) * mm});
            skLineSegment(sketch, "E5680", {"start": v(42.28, -8.4) * mm, "end": v(42.12, -8.3) * mm});
            skLineSegment(sketch, "E5681", {"start": v(42.12, -8.3) * mm, "end": v(41.96, -8.2) * mm});
            skLineSegment(sketch, "E5682", {"start": v(41.96, -8.2) * mm, "end": v(41.8, -8.1) * mm});
            skLineSegment(sketch, "E5683", {"start": v(41.8, -8.1) * mm, "end": v(41.65, -8.01) * mm});
            skLineSegment(sketch, "E5684", {"start": v(41.65, -8.01) * mm, "end": v(41.48, -7.92) * mm});
            skLineSegment(sketch, "E5685", {"start": v(41.48, -7.92) * mm, "end": v(41.31, -7.83) * mm});
            skLineSegment(sketch, "E5686", {"start": v(41.31, -7.83) * mm, "end": v(41.16, -7.75) * mm});
            skLineSegment(sketch, "E5687", {"start": v(41.16, -7.75) * mm, "end": v(40.99, -7.66) * mm});
            skLineSegment(sketch, "E5688", {"start": v(40.99, -7.66) * mm, "end": v(40.82, -7.58) * mm});
            skLineSegment(sketch, "E5689", {"start": v(40.82, -7.58) * mm, "end": v(40.64, -7.5) * mm});
            skLineSegment(sketch, "E5690", {"start": v(40.64, -7.5) * mm, "end": v(40.57, -7.47) * mm});
            skLineSegment(sketch, "E5691", {"start": v(40.57, -7.47) * mm, "end": v(40.6, -7.28) * mm});
            skLineSegment(sketch, "E5692", {"start": v(40.6, -7.28) * mm, "end": v(40.64, -7.09) * mm});
            skLineSegment(sketch, "E5693", {"start": v(40.64, -7.09) * mm, "end": v(40.67, -6.9) * mm});
            skLineSegment(sketch, "E5694", {"start": v(40.67, -6.9) * mm, "end": v(40.7, -6.7) * mm});
            skLineSegment(sketch, "E5695", {"start": v(40.7, -6.7) * mm, "end": v(40.73, -6.52) * mm});
            skLineSegment(sketch, "E5696", {"start": v(40.73, -6.52) * mm, "end": v(40.76, -6.32) * mm});
            skLineSegment(sketch, "E5697", {"start": v(40.76, -6.32) * mm, "end": v(40.8, -6.14) * mm});
            skLineSegment(sketch, "E5698", {"start": v(40.8, -6.14) * mm, "end": v(40.8, -6.1) * mm});
            skLineSegment(sketch, "E5699", {"start": v(40.8, -6.1) * mm, "end": v(40.97, -6.09) * mm});
            skLineSegment(sketch, "E5700", {"start": v(40.97, -6.09) * mm, "end": v(41.15, -6.07) * mm});
            skLineSegment(sketch, "E5701", {"start": v(41.15, -6.07) * mm, "end": v(41.32, -6.05) * mm});
            skLineSegment(sketch, "E5702", {"start": v(41.32, -6.05) * mm, "end": v(41.5, -6.02) * mm});
            skLineSegment(sketch, "E5703", {"start": v(41.5, -6.02) * mm, "end": v(41.68, -6) * mm});
            skLineSegment(sketch, "E5704", {"start": v(41.68, -6) * mm, "end": v(41.85, -5.96) * mm});
            skLineSegment(sketch, "E5705", {"start": v(41.85, -5.96) * mm, "end": v(42.04, -5.93) * mm});
            skLineSegment(sketch, "E5706", {"start": v(42.04, -5.93) * mm, "end": v(42.2, -5.9) * mm});
            skLineSegment(sketch, "E5707", {"start": v(42.2, -5.9) * mm, "end": v(42.38, -5.86) * mm});
            skLineSegment(sketch, "E5708", {"start": v(42.38, -5.86) * mm, "end": v(42.56, -5.82) * mm});
            skLineSegment(sketch, "E5709", {"start": v(42.56, -5.82) * mm, "end": v(42.74, -5.78) * mm});
            skLineSegment(sketch, "E5710", {"start": v(42.74, -5.78) * mm, "end": v(42.93, -5.73) * mm});
            skLineSegment(sketch, "E5711", {"start": v(42.93, -5.73) * mm, "end": v(43.1, -5.69) * mm});
            skLineSegment(sketch, "E5712", {"start": v(43.1, -5.69) * mm, "end": v(43.27, -5.64) * mm});
            skLineSegment(sketch, "E5713", {"start": v(43.27, -5.64) * mm, "end": v(43.44, -5.6) * mm});
            skLineSegment(sketch, "E5714", {"start": v(43.44, -5.6) * mm, "end": v(43.62, -5.54) * mm});
            skLineSegment(sketch, "E5715", {"start": v(43.62, -5.54) * mm, "end": v(43.8, -5.48) * mm});
            skLineSegment(sketch, "E5716", {"start": v(43.8, -5.48) * mm, "end": v(43.99, -5.42) * mm});
            skLineSegment(sketch, "E5717", {"start": v(43.99, -5.42) * mm, "end": v(44.17, -5.36) * mm});
            skLineSegment(sketch, "E5718", {"start": v(44.17, -5.36) * mm, "end": v(44.3, -5.32) * mm});
            skLineSegment(sketch, "E5719", {"start": v(44.3, -5.32) * mm, "end": v(44.33, -5.13) * mm});
            skLineSegment(sketch, "E5720", {"start": v(44.33, -5.13) * mm, "end": v(44.35, -4.95) * mm});
            skLineSegment(sketch, "E5721", {"start": v(44.35, -4.95) * mm, "end": v(44.37, -4.77) * mm});
            skLineSegment(sketch, "E5722", {"start": v(44.37, -4.77) * mm, "end": v(44.39, -4.58) * mm});
            skLineSegment(sketch, "E5723", {"start": v(44.39, -4.58) * mm, "end": v(44.4, -4.5) * mm});
            skLineSegment(sketch, "E5724", {"start": v(44.4, -4.5) * mm, "end": v(44.23, -4.4) * mm});
            skLineSegment(sketch, "E5725", {"start": v(44.23, -4.4) * mm, "end": v(44.08, -4.3) * mm});
            skLineSegment(sketch, "E5726", {"start": v(44.08, -4.3) * mm, "end": v(43.92, -4.21) * mm});
            skLineSegment(sketch, "E5727", {"start": v(43.92, -4.21) * mm, "end": v(43.77, -4.13) * mm});
            skLineSegment(sketch, "E5728", {"start": v(43.77, -4.13) * mm, "end": v(43.62, -4.04) * mm});
            skLineSegment(sketch, "E5729", {"start": v(43.62, -4.04) * mm, "end": v(43.46, -3.95) * mm});
            skLineSegment(sketch, "E5730", {"start": v(43.46, -3.95) * mm, "end": v(43.29, -3.86) * mm});
            skLineSegment(sketch, "E5731", {"start": v(43.29, -3.86) * mm, "end": v(43.12, -3.78) * mm});
            skLineSegment(sketch, "E5732", {"start": v(43.12, -3.78) * mm, "end": v(42.95, -3.7) * mm});
            skLineSegment(sketch, "E5733", {"start": v(42.95, -3.7) * mm, "end": v(42.78, -3.6) * mm});
            skLineSegment(sketch, "E5734", {"start": v(42.78, -3.6) * mm, "end": v(42.6, -3.53) * mm});
            skLineSegment(sketch, "E5735", {"start": v(42.6, -3.53) * mm, "end": v(42.44, -3.45) * mm});
            skLineSegment(sketch, "E5736", {"start": v(42.44, -3.45) * mm, "end": v(42.27, -3.38) * mm});
            skLineSegment(sketch, "E5737", {"start": v(42.27, -3.38) * mm, "end": v(42.1, -3.3) * mm});
            skLineSegment(sketch, "E5738", {"start": v(42.1, -3.3) * mm, "end": v(41.93, -3.24) * mm});
            skLineSegment(sketch, "E5739", {"start": v(41.93, -3.24) * mm, "end": v(41.76, -3.17) * mm});
            skLineSegment(sketch, "E5740", {"start": v(41.76, -3.17) * mm, "end": v(41.58, -3.1) * mm});
            skLineSegment(sketch, "E5741", {"start": v(41.58, -3.1) * mm, "end": v(41.4, -3.04) * mm});
            skLineSegment(sketch, "E5742", {"start": v(41.4, -3.04) * mm, "end": v(41.22, -2.98) * mm});
            skLineSegment(sketch, "E5743", {"start": v(41.22, -2.98) * mm, "end": v(41.14, -2.96) * mm});
            skLineSegment(sketch, "E5744", {"start": v(41.14, -2.96) * mm, "end": v(41.16, -2.77) * mm});
            skLineSegment(sketch, "E5745", {"start": v(41.16, -2.77) * mm, "end": v(41.17, -2.57) * mm});
            skLineSegment(sketch, "E5746", {"start": v(41.17, -2.57) * mm, "end": v(41.18, -2.38) * mm});
            skLineSegment(sketch, "E5747", {"start": v(41.18, -2.38) * mm, "end": v(41.2, -2.19) * mm});
            skLineSegment(sketch, "E5748", {"start": v(41.2, -2.19) * mm, "end": v(41.2, -2) * mm});
            skLineSegment(sketch, "E5749", {"start": v(41.2, -2) * mm, "end": v(41.2, -1.8) * mm});
            skLineSegment(sketch, "E5750", {"start": v(41.2, -1.8) * mm, "end": v(41.22, -1.61) * mm});
            skLineSegment(sketch, "E5751", {"start": v(41.22, -1.61) * mm, "end": v(41.22, -1.58) * mm});
            skSolve(sketch);
        }
        {
            var Q0;
            Q0 = qSketchRegion(id + "F17", true);
            var Q1;
            Q1=makeQuery(id+"F3.opExtrude","CAP_FACE",FACE,{"disambiguationData":[OSD([sQuery(id+"F2.wireOp",EDGE,"E16"),sQuery(id+"F2.wireOp",EDGE,"E17"),sQuery(id+"F2.wireOp",EDGE,"E18"),sQuery(id+"F2.wireOp",EDGE,"E19"),sQuery(id+"F2.wireOp",EDGE,"E20"),sQuery(id+"F2.wireOp",EDGE,"E21"),sQuery(id+"F2.wireOp",EDGE,"E22"),sQuery(id+"F2.wireOp",EDGE,"E23"),sQuery(id+"F2.wireOp",EDGE,"E24"),sQuery(id+"F2.wireOp",EDGE,"E25"),sQuery(id+"F2.wireOp",EDGE,"E26"),sQuery(id+"F2.wireOp",EDGE,"E27"),sQuery(id+"F2.wireOp",EDGE,"E28"),sQuery(id+"F2.wireOp",EDGE,"E29"),sQuery(id+"F2.wireOp",EDGE,"E30"),sQuery(id+"F2.wireOp",EDGE,"E31"),sQuery(id+"F2.wireOp",EDGE,"E32"),sQuery(id+"F2.wireOp",EDGE,"E33"),sQuery(id+"F2.wireOp",EDGE,"E34"),sQuery(id+"F2.wireOp",EDGE,"E35"),sQuery(id+"F2.wireOp",EDGE,"E36"),sQuery(id+"F2.wireOp",EDGE,"E37"),sQuery(id+"F2.wireOp",EDGE,"E38"),sQuery(id+"F2.wireOp",EDGE,"E39"),sQuery(id+"F2.wireOp",EDGE,"E40"),sQuery(id+"F2.wireOp",EDGE,"E41"),sQuery(id+"F2.wireOp",EDGE,"E42"),sQuery(id+"F2.wireOp",EDGE,"E43"),sQuery(id+"F2.wireOp",EDGE,"E44"),sQuery(id+"F2.wireOp",EDGE,"E45"),sQuery(id+"F2.wireOp",EDGE,"E46"),sQuery(id+"F2.wireOp",EDGE,"E47"),sQuery(id+"F2.wireOp",EDGE,"E48"),sQuery(id+"F2.wireOp",EDGE,"E49"),sQuery(id+"F2.wireOp",EDGE,"E50"),sQuery(id+"F2.wireOp",EDGE,"E51"),sQuery(id+"F2.wireOp",EDGE,"E52"),sQuery(id+"F2.wireOp",EDGE,"E53"),sQuery(id+"F2.wireOp",EDGE,"E54"),sQuery(id+"F2.wireOp",EDGE,"E55"),sQuery(id+"F2.wireOp",EDGE,"E56"),sQuery(id+"F2.wireOp",EDGE,"E57"),sQuery(id+"F2.wireOp",EDGE,"E58"),sQuery(id+"F2.wireOp",EDGE,"E59"),sQuery(id+"F2.wireOp",EDGE,"E60"),sQuery(id+"F2.wireOp",EDGE,"E61"),sQuery(id+"F2.wireOp",EDGE,"E62"),sQuery(id+"F2.wireOp",EDGE,"E63"),sQuery(id+"F2.wireOp",EDGE,"E64"),sQuery(id+"F2.wireOp",EDGE,"E65"),sQuery(id+"F2.wireOp",EDGE,"E66"),sQuery(id+"F2.wireOp",EDGE,"E67"),sQuery(id+"F2.wireOp",EDGE,"E68"),sQuery(id+"F2.wireOp",EDGE,"E69"),sQuery(id+"F2.wireOp",EDGE,"E70"),sQuery(id+"F2.wireOp",EDGE,"E71"),sQuery(id+"F2.wireOp",EDGE,"E72"),sQuery(id+"F2.wireOp",EDGE,"E73"),sQuery(id+"F2.wireOp",EDGE,"E74"),sQuery(id+"F2.wireOp",EDGE,"E75"),sQuery(id+"F2.wireOp",EDGE,"E76"),sQuery(id+"F2.wireOp",EDGE,"E77"),sQuery(id+"F2.wireOp",EDGE,"E78"),sQuery(id+"F2.wireOp",EDGE,"E79"),sQuery(id+"F2.wireOp",EDGE,"E80"),sQuery(id+"F2.wireOp",EDGE,"E81"),sQuery(id+"F2.wireOp",EDGE,"E82"),sQuery(id+"F2.wireOp",EDGE,"E83"),sQuery(id+"F2.wireOp",EDGE,"E84"),sQuery(id+"F2.wireOp",EDGE,"E85"),sQuery(id+"F2.wireOp",EDGE,"E86"),sQuery(id+"F2.wireOp",EDGE,"E87"),sQuery(id+"F2.wireOp",EDGE,"E88"),sQuery(id+"F2.wireOp",EDGE,"E89"),sQuery(id+"F2.wireOp",EDGE,"E90"),sQuery(id+"F2.wireOp",EDGE,"E91"),sQuery(id+"F2.wireOp",EDGE,"E92"),sQuery(id+"F2.wireOp",EDGE,"E93"),sQuery(id+"F2.wireOp",EDGE,"E94"),sQuery(id+"F2.wireOp",EDGE,"E95"),sQuery(id+"F2.wireOp",EDGE,"E96"),sQuery(id+"F2.wireOp",EDGE,"E97"),sQuery(id+"F2.wireOp",EDGE,"E98"),sQuery(id+"F2.wireOp",EDGE,"E99"),sQuery(id+"F2.wireOp",EDGE,"E100"),sQuery(id+"F2.wireOp",EDGE,"E101"),sQuery(id+"F2.wireOp",EDGE,"E102"),sQuery(id+"F2.wireOp",EDGE,"E103"),sQuery(id+"F2.wireOp",EDGE,"E104"),sQuery(id+"F2.wireOp",EDGE,"E105"),sQuery(id+"F2.wireOp",EDGE,"E106"),sQuery(id+"F2.wireOp",EDGE,"E107"),sQuery(id+"F2.wireOp",EDGE,"E108"),sQuery(id+"F2.wireOp",EDGE,"E109"),sQuery(id+"F2.wireOp",EDGE,"E110"),sQuery(id+"F2.wireOp",EDGE,"E111"),sQuery(id+"F2.wireOp",EDGE,"E112"),sQuery(id+"F2.wireOp",EDGE,"E113"),sQuery(id+"F2.wireOp",EDGE,"E114"),sQuery(id+"F2.wireOp",EDGE,"E115"),sQuery(id+"F2.wireOp",EDGE,"E116"),sQuery(id+"F2.wireOp",EDGE,"E117"),sQuery(id+"F2.wireOp",EDGE,"E118"),sQuery(id+"F2.wireOp",EDGE,"E119"),sQuery(id+"F2.wireOp",EDGE,"E120"),sQuery(id+"F2.wireOp",EDGE,"E121"),sQuery(id+"F2.wireOp",EDGE,"E122"),sQuery(id+"F2.wireOp",EDGE,"E123"),sQuery(id+"F2.wireOp",EDGE,"E124"),sQuery(id+"F2.wireOp",EDGE,"E125"),sQuery(id+"F2.wireOp",EDGE,"E126"),sQuery(id+"F2.wireOp",EDGE,"E127"),sQuery(id+"F2.wireOp",EDGE,"E128"),sQuery(id+"F2.wireOp",EDGE,"E129"),sQuery(id+"F2.wireOp",EDGE,"E130"),sQuery(id+"F2.wireOp",EDGE,"E131"),sQuery(id+"F2.wireOp",EDGE,"E132"),sQuery(id+"F2.wireOp",EDGE,"E133"),sQuery(id+"F2.wireOp",EDGE,"E134"),sQuery(id+"F2.wireOp",EDGE,"E135"),sQuery(id+"F2.wireOp",EDGE,"E136"),sQuery(id+"F2.wireOp",EDGE,"E137"),sQuery(id+"F2.wireOp",EDGE,"E138"),sQuery(id+"F2.wireOp",EDGE,"E139"),sQuery(id+"F2.wireOp",EDGE,"E140"),sQuery(id+"F2.wireOp",EDGE,"E141"),sQuery(id+"F2.wireOp",EDGE,"E142"),sQuery(id+"F2.wireOp",EDGE,"E143"),sQuery(id+"F2.wireOp",EDGE,"E144"),sQuery(id+"F2.wireOp",EDGE,"E145"),sQuery(id+"F2.wireOp",EDGE,"E146"),sQuery(id+"F2.wireOp",EDGE,"E147"),sQuery(id+"F2.wireOp",EDGE,"E148"),sQuery(id+"F2.wireOp",EDGE,"E149"),sQuery(id+"F2.wireOp",EDGE,"E150"),sQuery(id+"F2.wireOp",EDGE,"E151"),sQuery(id+"F2.wireOp",EDGE,"E152"),sQuery(id+"F2.wireOp",EDGE,"E153"),sQuery(id+"F2.wireOp",EDGE,"E154"),sQuery(id+"F2.wireOp",EDGE,"E155"),sQuery(id+"F2.wireOp",EDGE,"E156"),sQuery(id+"F2.wireOp",EDGE,"E157"),sQuery(id+"F2.wireOp",EDGE,"E158"),sQuery(id+"F2.wireOp",EDGE,"E159"),sQuery(id+"F2.wireOp",EDGE,"E160"),sQuery(id+"F2.wireOp",EDGE,"E161"),sQuery(id+"F2.wireOp",EDGE,"E162"),sQuery(id+"F2.wireOp",EDGE,"E163"),sQuery(id+"F2.wireOp",EDGE,"E164"),sQuery(id+"F2.wireOp",EDGE,"E165"),sQuery(id+"F2.wireOp",EDGE,"E166"),sQuery(id+"F2.wireOp",EDGE,"E167"),sQuery(id+"F2.wireOp",EDGE,"E168"),sQuery(id+"F2.wireOp",EDGE,"E169"),sQuery(id+"F2.wireOp",EDGE,"E170"),sQuery(id+"F2.wireOp",EDGE,"E171"),sQuery(id+"F2.wireOp",EDGE,"E172"),sQuery(id+"F2.wireOp",EDGE,"E173"),sQuery(id+"F2.wireOp",EDGE,"E174"),sQuery(id+"F2.wireOp",EDGE,"E175"),sQuery(id+"F2.wireOp",EDGE,"E176"),sQuery(id+"F2.wireOp",EDGE,"E177"),sQuery(id+"F2.wireOp",EDGE,"E178"),sQuery(id+"F2.wireOp",EDGE,"E179"),sQuery(id+"F2.wireOp",EDGE,"E180"),sQuery(id+"F2.wireOp",EDGE,"E181"),sQuery(id+"F2.wireOp",EDGE,"E182"),sQuery(id+"F2.wireOp",EDGE,"E183"),sQuery(id+"F2.wireOp",EDGE,"E184"),sQuery(id+"F2.wireOp",EDGE,"E185"),sQuery(id+"F2.wireOp",EDGE,"E186"),sQuery(id+"F2.wireOp",EDGE,"E187"),sQuery(id+"F2.wireOp",EDGE,"E188"),sQuery(id+"F2.wireOp",EDGE,"E189"),sQuery(id+"F2.wireOp",EDGE,"E190"),sQuery(id+"F2.wireOp",EDGE,"E191"),sQuery(id+"F2.wireOp",EDGE,"E192"),sQuery(id+"F2.wireOp",EDGE,"E193"),sQuery(id+"F2.wireOp",EDGE,"E194"),sQuery(id+"F2.wireOp",EDGE,"E195"),sQuery(id+"F2.wireOp",EDGE,"E196"),sQuery(id+"F2.wireOp",EDGE,"E197"),sQuery(id+"F2.wireOp",EDGE,"E198"),sQuery(id+"F2.wireOp",EDGE,"E199"),sQuery(id+"F2.wireOp",EDGE,"E200"),sQuery(id+"F2.wireOp",EDGE,"E201"),sQuery(id+"F2.wireOp",EDGE,"E202"),sQuery(id+"F2.wireOp",EDGE,"E203"),sQuery(id+"F2.wireOp",EDGE,"E204"),sQuery(id+"F2.wireOp",EDGE,"E205"),sQuery(id+"F2.wireOp",EDGE,"E206"),sQuery(id+"F2.wireOp",EDGE,"E207"),sQuery(id+"F2.wireOp",EDGE,"E208"),sQuery(id+"F2.wireOp",EDGE,"E209"),sQuery(id+"F2.wireOp",EDGE,"E210"),sQuery(id+"F2.wireOp",EDGE,"E211"),sQuery(id+"F2.wireOp",EDGE,"E212"),sQuery(id+"F2.wireOp",EDGE,"E213"),sQuery(id+"F2.wireOp",EDGE,"E214"),sQuery(id+"F2.wireOp",EDGE,"E215"),sQuery(id+"F2.wireOp",EDGE,"E216"),sQuery(id+"F2.wireOp",EDGE,"E217"),sQuery(id+"F2.wireOp",EDGE,"E218"),sQuery(id+"F2.wireOp",EDGE,"E219"),sQuery(id+"F2.wireOp",EDGE,"E220"),sQuery(id+"F2.wireOp",EDGE,"E221"),sQuery(id+"F2.wireOp",EDGE,"E222"),sQuery(id+"F2.wireOp",EDGE,"E223"),sQuery(id+"F2.wireOp",EDGE,"E224"),sQuery(id+"F2.wireOp",EDGE,"E225"),sQuery(id+"F2.wireOp",EDGE,"E226"),sQuery(id+"F2.wireOp",EDGE,"E227"),sQuery(id+"F2.wireOp",EDGE,"E228"),sQuery(id+"F2.wireOp",EDGE,"E229"),sQuery(id+"F2.wireOp",EDGE,"E230"),sQuery(id+"F2.wireOp",EDGE,"E231"),sQuery(id+"F2.wireOp",EDGE,"E232"),sQuery(id+"F2.wireOp",EDGE,"E233"),sQuery(id+"F2.wireOp",EDGE,"E234"),sQuery(id+"F2.wireOp",EDGE,"E235"),sQuery(id+"F2.wireOp",EDGE,"E236"),sQuery(id+"F2.wireOp",EDGE,"E237"),sQuery(id+"F2.wireOp",EDGE,"E238"),sQuery(id+"F2.wireOp",EDGE,"E239"),sQuery(id+"F2.wireOp",EDGE,"E240"),sQuery(id+"F2.wireOp",EDGE,"E241"),sQuery(id+"F2.wireOp",EDGE,"E242"),sQuery(id+"F2.wireOp",EDGE,"E243"),sQuery(id+"F2.wireOp",EDGE,"E244"),sQuery(id+"F2.wireOp",EDGE,"E245"),sQuery(id+"F2.wireOp",EDGE,"E246"),sQuery(id+"F2.wireOp",EDGE,"E247"),sQuery(id+"F2.wireOp",EDGE,"E248"),sQuery(id+"F2.wireOp",EDGE,"E249"),sQuery(id+"F2.wireOp",EDGE,"E250"),sQuery(id+"F2.wireOp",EDGE,"E251"),sQuery(id+"F2.wireOp",EDGE,"E252"),sQuery(id+"F2.wireOp",EDGE,"E253"),sQuery(id+"F2.wireOp",EDGE,"E254"),sQuery(id+"F2.wireOp",EDGE,"E255"),sQuery(id+"F2.wireOp",EDGE,"E256"),sQuery(id+"F2.wireOp",EDGE,"E257"),sQuery(id+"F2.wireOp",EDGE,"E258"),sQuery(id+"F2.wireOp",EDGE,"E259"),sQuery(id+"F2.wireOp",EDGE,"E260"),sQuery(id+"F2.wireOp",EDGE,"E261"),sQuery(id+"F2.wireOp",EDGE,"E262"),sQuery(id+"F2.wireOp",EDGE,"E263"),sQuery(id+"F2.wireOp",EDGE,"E264"),sQuery(id+"F2.wireOp",EDGE,"E265"),sQuery(id+"F2.wireOp",EDGE,"E266"),sQuery(id+"F2.wireOp",EDGE,"E267"),sQuery(id+"F2.wireOp",EDGE,"E268"),sQuery(id+"F2.wireOp",EDGE,"E269"),sQuery(id+"F2.wireOp",EDGE,"E270"),sQuery(id+"F2.wireOp",EDGE,"E271"),sQuery(id+"F2.wireOp",EDGE,"E272"),sQuery(id+"F2.wireOp",EDGE,"E273"),sQuery(id+"F2.wireOp",EDGE,"E274"),sQuery(id+"F2.wireOp",EDGE,"E275"),sQuery(id+"F2.wireOp",EDGE,"E276"),sQuery(id+"F2.wireOp",EDGE,"E277"),sQuery(id+"F2.wireOp",EDGE,"E278"),sQuery(id+"F2.wireOp",EDGE,"E279"),sQuery(id+"F2.wireOp",EDGE,"E280"),sQuery(id+"F2.wireOp",EDGE,"E281"),sQuery(id+"F2.wireOp",EDGE,"E282"),sQuery(id+"F2.wireOp",EDGE,"E283"),sQuery(id+"F2.wireOp",EDGE,"E284"),sQuery(id+"F2.wireOp",EDGE,"E285"),sQuery(id+"F2.wireOp",EDGE,"E286"),sQuery(id+"F2.wireOp",EDGE,"E287"),sQuery(id+"F2.wireOp",EDGE,"E288"),sQuery(id+"F2.wireOp",EDGE,"E289"),sQuery(id+"F2.wireOp",EDGE,"E290"),sQuery(id+"F2.wireOp",EDGE,"E291"),sQuery(id+"F2.wireOp",EDGE,"E292"),sQuery(id+"F2.wireOp",EDGE,"E293"),sQuery(id+"F2.wireOp",EDGE,"E294"),sQuery(id+"F2.wireOp",EDGE,"E295"),sQuery(id+"F2.wireOp",EDGE,"E296"),sQuery(id+"F2.wireOp",EDGE,"E297"),sQuery(id+"F2.wireOp",EDGE,"E298"),sQuery(id+"F2.wireOp",EDGE,"E299"),sQuery(id+"F2.wireOp",EDGE,"E300"),sQuery(id+"F2.wireOp",EDGE,"E301"),sQuery(id+"F2.wireOp",EDGE,"E302"),sQuery(id+"F2.wireOp",EDGE,"E303"),sQuery(id+"F2.wireOp",EDGE,"E304"),sQuery(id+"F2.wireOp",EDGE,"E305"),sQuery(id+"F2.wireOp",EDGE,"E306"),sQuery(id+"F2.wireOp",EDGE,"E307"),sQuery(id+"F2.wireOp",EDGE,"E308"),sQuery(id+"F2.wireOp",EDGE,"E309"),sQuery(id+"F2.wireOp",EDGE,"E310"),sQuery(id+"F2.wireOp",EDGE,"E311"),sQuery(id+"F2.wireOp",EDGE,"E312"),sQuery(id+"F2.wireOp",EDGE,"E313"),sQuery(id+"F2.wireOp",EDGE,"E314"),sQuery(id+"F2.wireOp",EDGE,"E315"),sQuery(id+"F2.wireOp",EDGE,"E316"),sQuery(id+"F2.wireOp",EDGE,"E317"),sQuery(id+"F2.wireOp",EDGE,"E318"),sQuery(id+"F2.wireOp",EDGE,"E319"),sQuery(id+"F2.wireOp",EDGE,"E320"),sQuery(id+"F2.wireOp",EDGE,"E321"),sQuery(id+"F2.wireOp",EDGE,"E322"),sQuery(id+"F2.wireOp",EDGE,"E323"),sQuery(id+"F2.wireOp",EDGE,"E324"),sQuery(id+"F2.wireOp",EDGE,"E325"),sQuery(id+"F2.wireOp",EDGE,"E326"),sQuery(id+"F2.wireOp",EDGE,"E327"),sQuery(id+"F2.wireOp",EDGE,"E328"),sQuery(id+"F2.wireOp",EDGE,"E329"),sQuery(id+"F2.wireOp",EDGE,"E330"),sQuery(id+"F2.wireOp",EDGE,"E331"),sQuery(id+"F2.wireOp",EDGE,"E332"),sQuery(id+"F2.wireOp",EDGE,"E333"),sQuery(id+"F2.wireOp",EDGE,"E334"),sQuery(id+"F2.wireOp",EDGE,"E335"),sQuery(id+"F2.wireOp",EDGE,"E336"),sQuery(id+"F2.wireOp",EDGE,"E337"),sQuery(id+"F2.wireOp",EDGE,"E338"),sQuery(id+"F2.wireOp",EDGE,"E339"),sQuery(id+"F2.wireOp",EDGE,"E340"),sQuery(id+"F2.wireOp",EDGE,"E341"),sQuery(id+"F2.wireOp",EDGE,"E342"),sQuery(id+"F2.wireOp",EDGE,"E343"),sQuery(id+"F2.wireOp",EDGE,"E344"),sQuery(id+"F2.wireOp",EDGE,"E345"),sQuery(id+"F2.wireOp",EDGE,"E346"),sQuery(id+"F2.wireOp",EDGE,"E347"),sQuery(id+"F2.wireOp",EDGE,"E348"),sQuery(id+"F2.wireOp",EDGE,"E349"),sQuery(id+"F2.wireOp",EDGE,"E350"),sQuery(id+"F2.wireOp",EDGE,"E351"),sQuery(id+"F2.wireOp",EDGE,"E352"),sQuery(id+"F2.wireOp",EDGE,"E353"),sQuery(id+"F2.wireOp",EDGE,"E354"),sQuery(id+"F2.wireOp",EDGE,"E355"),sQuery(id+"F2.wireOp",EDGE,"E356"),sQuery(id+"F2.wireOp",EDGE,"E357"),sQuery(id+"F2.wireOp",EDGE,"E358"),sQuery(id+"F2.wireOp",EDGE,"E359"),sQuery(id+"F2.wireOp",EDGE,"E360"),sQuery(id+"F2.wireOp",EDGE,"E361"),sQuery(id+"F2.wireOp",EDGE,"E362"),sQuery(id+"F2.wireOp",EDGE,"E363"),sQuery(id+"F2.wireOp",EDGE,"E364"),sQuery(id+"F2.wireOp",EDGE,"E365"),sQuery(id+"F2.wireOp",EDGE,"E366"),sQuery(id+"F2.wireOp",EDGE,"E367"),sQuery(id+"F2.wireOp",EDGE,"E368"),sQuery(id+"F2.wireOp",EDGE,"E369"),sQuery(id+"F2.wireOp",EDGE,"E370"),sQuery(id+"F2.wireOp",EDGE,"E371"),sQuery(id+"F2.wireOp",EDGE,"E372"),sQuery(id+"F2.wireOp",EDGE,"E373"),sQuery(id+"F2.wireOp",EDGE,"E374"),sQuery(id+"F2.wireOp",EDGE,"E375"),sQuery(id+"F2.wireOp",EDGE,"E376"),sQuery(id+"F2.wireOp",EDGE,"E377"),sQuery(id+"F2.wireOp",EDGE,"E378"),sQuery(id+"F2.wireOp",EDGE,"E379"),sQuery(id+"F2.wireOp",EDGE,"E380"),sQuery(id+"F2.wireOp",EDGE,"E381"),sQuery(id+"F2.wireOp",EDGE,"E382"),sQuery(id+"F2.wireOp",EDGE,"E383"),sQuery(id+"F2.wireOp",EDGE,"E384"),sQuery(id+"F2.wireOp",EDGE,"E385"),sQuery(id+"F2.wireOp",EDGE,"E386"),sQuery(id+"F2.wireOp",EDGE,"E387"),sQuery(id+"F2.wireOp",EDGE,"E388"),sQuery(id+"F2.wireOp",EDGE,"E389"),sQuery(id+"F2.wireOp",EDGE,"E390"),sQuery(id+"F2.wireOp",EDGE,"E391"),sQuery(id+"F2.wireOp",EDGE,"E392"),sQuery(id+"F2.wireOp",EDGE,"E393"),sQuery(id+"F2.wireOp",EDGE,"E394"),sQuery(id+"F2.wireOp",EDGE,"E395"),sQuery(id+"F2.wireOp",EDGE,"E396"),sQuery(id+"F2.wireOp",EDGE,"E397"),sQuery(id+"F2.wireOp",EDGE,"E398"),sQuery(id+"F2.wireOp",EDGE,"E399"),sQuery(id+"F2.wireOp",EDGE,"E400"),sQuery(id+"F2.wireOp",EDGE,"E401"),sQuery(id+"F2.wireOp",EDGE,"E402"),sQuery(id+"F2.wireOp",EDGE,"E403"),sQuery(id+"F2.wireOp",EDGE,"E404"),sQuery(id+"F2.wireOp",EDGE,"E405"),sQuery(id+"F2.wireOp",EDGE,"E406"),sQuery(id+"F2.wireOp",EDGE,"E407"),sQuery(id+"F2.wireOp",EDGE,"E408"),sQuery(id+"F2.wireOp",EDGE,"E409"),sQuery(id+"F2.wireOp",EDGE,"E410"),sQuery(id+"F2.wireOp",EDGE,"E411"),sQuery(id+"F2.wireOp",EDGE,"E412"),sQuery(id+"F2.wireOp",EDGE,"E413"),sQuery(id+"F2.wireOp",EDGE,"E414"),sQuery(id+"F2.wireOp",EDGE,"E415"),sQuery(id+"F2.wireOp",EDGE,"E416"),sQuery(id+"F2.wireOp",EDGE,"E417"),sQuery(id+"F2.wireOp",EDGE,"E418"),sQuery(id+"F2.wireOp",EDGE,"E419"),sQuery(id+"F2.wireOp",EDGE,"E420"),sQuery(id+"F2.wireOp",EDGE,"E421"),sQuery(id+"F2.wireOp",EDGE,"E422"),sQuery(id+"F2.wireOp",EDGE,"E423"),sQuery(id+"F2.wireOp",EDGE,"E424"),sQuery(id+"F2.wireOp",EDGE,"E425"),sQuery(id+"F2.wireOp",EDGE,"E426"),sQuery(id+"F2.wireOp",EDGE,"E427"),sQuery(id+"F2.wireOp",EDGE,"E428"),sQuery(id+"F2.wireOp",EDGE,"E429"),sQuery(id+"F2.wireOp",EDGE,"E430"),sQuery(id+"F2.wireOp",EDGE,"E431"),sQuery(id+"F2.wireOp",EDGE,"E432"),sQuery(id+"F2.wireOp",EDGE,"E433"),sQuery(id+"F2.wireOp",EDGE,"E434"),sQuery(id+"F2.wireOp",EDGE,"E435"),sQuery(id+"F2.wireOp",EDGE,"E436"),sQuery(id+"F2.wireOp",EDGE,"E437"),sQuery(id+"F2.wireOp",EDGE,"E438"),sQuery(id+"F2.wireOp",EDGE,"E439"),sQuery(id+"F2.wireOp",EDGE,"E440"),sQuery(id+"F2.wireOp",EDGE,"E441"),sQuery(id+"F2.wireOp",EDGE,"E442"),sQuery(id+"F2.wireOp",EDGE,"E443"),sQuery(id+"F2.wireOp",EDGE,"E444"),sQuery(id+"F2.wireOp",EDGE,"E445"),sQuery(id+"F2.wireOp",EDGE,"E446"),sQuery(id+"F2.wireOp",EDGE,"E447"),sQuery(id+"F2.wireOp",EDGE,"E447"),sQuery(id+"F2.wireOp",EDGE,"E447"),sQuery(id+"F2.wireOp",EDGE,"E448"),sQuery(id+"F2.wireOp",EDGE,"E449"),sQuery(id+"F2.wireOp",EDGE,"E450"),sQuery(id+"F2.wireOp",EDGE,"E451"),sQuery(id+"F2.wireOp",EDGE,"E452"),sQuery(id+"F2.wireOp",EDGE,"E453"),sQuery(id+"F2.wireOp",EDGE,"E454"),sQuery(id+"F2.wireOp",EDGE,"E455"),sQuery(id+"F2.wireOp",EDGE,"E456"),sQuery(id+"F2.wireOp",EDGE,"E457"),sQuery(id+"F2.wireOp",EDGE,"E458"),sQuery(id+"F2.wireOp",EDGE,"E459"),sQuery(id+"F2.wireOp",EDGE,"E460"),sQuery(id+"F2.wireOp",EDGE,"E461"),sQuery(id+"F2.wireOp",EDGE,"E462"),sQuery(id+"F2.wireOp",EDGE,"E463"),sQuery(id+"F2.wireOp",EDGE,"E464"),sQuery(id+"F2.wireOp",EDGE,"E465"),sQuery(id+"F2.wireOp",EDGE,"E466"),sQuery(id+"F2.wireOp",EDGE,"E467"),sQuery(id+"F2.wireOp",EDGE,"E468"),sQuery(id+"F2.wireOp",EDGE,"E469"),sQuery(id+"F2.wireOp",EDGE,"E470"),sQuery(id+"F2.wireOp",EDGE,"E471"),sQuery(id+"F2.wireOp",EDGE,"E472"),sQuery(id+"F2.wireOp",EDGE,"E473"),sQuery(id+"F2.wireOp",EDGE,"E474"),sQuery(id+"F2.wireOp",EDGE,"E475"),sQuery(id+"F2.wireOp",EDGE,"E476"),sQuery(id+"F2.wireOp",EDGE,"E477"),sQuery(id+"F2.wireOp",EDGE,"E478"),sQuery(id+"F2.wireOp",EDGE,"E479"),sQuery(id+"F2.wireOp",EDGE,"E480"),sQuery(id+"F2.wireOp",EDGE,"E481"),sQuery(id+"F2.wireOp",EDGE,"E482"),sQuery(id+"F2.wireOp",EDGE,"E483"),sQuery(id+"F2.wireOp",EDGE,"E484"),sQuery(id+"F2.wireOp",EDGE,"E485"),sQuery(id+"F2.wireOp",EDGE,"E486"),sQuery(id+"F2.wireOp",EDGE,"E487"),sQuery(id+"F2.wireOp",EDGE,"E488"),sQuery(id+"F2.wireOp",EDGE,"E489"),sQuery(id+"F2.wireOp",EDGE,"E490"),sQuery(id+"F2.wireOp",EDGE,"E491"),sQuery(id+"F2.wireOp",EDGE,"E492"),sQuery(id+"F2.wireOp",EDGE,"E493"),sQuery(id+"F2.wireOp",EDGE,"E494"),sQuery(id+"F2.wireOp",EDGE,"E495"),sQuery(id+"F2.wireOp",EDGE,"E496"),sQuery(id+"F2.wireOp",EDGE,"E497"),sQuery(id+"F2.wireOp",EDGE,"E498"),sQuery(id+"F2.wireOp",EDGE,"E499"),sQuery(id+"F2.wireOp",EDGE,"E500"),sQuery(id+"F2.wireOp",EDGE,"E501"),sQuery(id+"F2.wireOp",EDGE,"E502"),sQuery(id+"F2.wireOp",EDGE,"E503"),sQuery(id+"F2.wireOp",EDGE,"E504"),sQuery(id+"F2.wireOp",EDGE,"E505"),sQuery(id+"F2.wireOp",EDGE,"E506"),sQuery(id+"F2.wireOp",EDGE,"E507"),sQuery(id+"F2.wireOp",EDGE,"E508"),sQuery(id+"F2.wireOp",EDGE,"E509"),sQuery(id+"F2.wireOp",EDGE,"E510"),sQuery(id+"F2.wireOp",EDGE,"E511"),sQuery(id+"F2.wireOp",EDGE,"E512"),sQuery(id+"F2.wireOp",EDGE,"E513"),sQuery(id+"F2.wireOp",EDGE,"E514"),sQuery(id+"F2.wireOp",EDGE,"E515"),sQuery(id+"F2.wireOp",EDGE,"E516"),sQuery(id+"F2.wireOp",EDGE,"E517"),sQuery(id+"F2.wireOp",EDGE,"E518"),sQuery(id+"F2.wireOp",EDGE,"E519"),sQuery(id+"F2.wireOp",EDGE,"E520"),sQuery(id+"F2.wireOp",EDGE,"E521"),sQuery(id+"F2.wireOp",EDGE,"E522"),sQuery(id+"F2.wireOp",EDGE,"E523"),sQuery(id+"F2.wireOp",EDGE,"E524"),sQuery(id+"F2.wireOp",EDGE,"E525"),sQuery(id+"F2.wireOp",EDGE,"E526"),sQuery(id+"F2.wireOp",EDGE,"E527"),sQuery(id+"F2.wireOp",EDGE,"E528"),sQuery(id+"F2.wireOp",EDGE,"E529"),sQuery(id+"F2.wireOp",EDGE,"E530"),sQuery(id+"F2.wireOp",EDGE,"E531"),sQuery(id+"F2.wireOp",EDGE,"E532"),sQuery(id+"F2.wireOp",EDGE,"E533"),sQuery(id+"F2.wireOp",EDGE,"E534"),sQuery(id+"F2.wireOp",EDGE,"E535"),sQuery(id+"F2.wireOp",EDGE,"E536"),sQuery(id+"F2.wireOp",EDGE,"E537"),sQuery(id+"F2.wireOp",EDGE,"E538"),sQuery(id+"F2.wireOp",EDGE,"E539"),sQuery(id+"F2.wireOp",EDGE,"E540"),sQuery(id+"F2.wireOp",EDGE,"E541"),sQuery(id+"F2.wireOp",EDGE,"E542"),sQuery(id+"F2.wireOp",EDGE,"E543"),sQuery(id+"F2.wireOp",EDGE,"E544"),sQuery(id+"F2.wireOp",EDGE,"E545"),sQuery(id+"F2.wireOp",EDGE,"E546"),sQuery(id+"F2.wireOp",EDGE,"E547"),sQuery(id+"F2.wireOp",EDGE,"E547"),sQuery(id+"F2.wireOp",EDGE,"E548"),sQuery(id+"F2.wireOp",EDGE,"E549"),sQuery(id+"F2.wireOp",EDGE,"E550"),sQuery(id+"F2.wireOp",EDGE,"E551"),sQuery(id+"F2.wireOp",EDGE,"E552"),sQuery(id+"F2.wireOp",EDGE,"E553"),sQuery(id+"F2.wireOp",EDGE,"E554"),sQuery(id+"F2.wireOp",EDGE,"E555"),sQuery(id+"F2.wireOp",EDGE,"E556"),sQuery(id+"F2.wireOp",EDGE,"E557"),sQuery(id+"F2.wireOp",EDGE,"E558"),sQuery(id+"F2.wireOp",EDGE,"E559"),sQuery(id+"F2.wireOp",EDGE,"E560"),sQuery(id+"F2.wireOp",EDGE,"E561"),sQuery(id+"F2.wireOp",EDGE,"E562"),sQuery(id+"F2.wireOp",EDGE,"E563"),sQuery(id+"F2.wireOp",EDGE,"E564"),sQuery(id+"F2.wireOp",EDGE,"E565"),sQuery(id+"F2.wireOp",EDGE,"E566"),sQuery(id+"F2.wireOp",EDGE,"E567"),sQuery(id+"F2.wireOp",EDGE,"E568"),sQuery(id+"F2.wireOp",EDGE,"E569"),sQuery(id+"F2.wireOp",EDGE,"E570"),sQuery(id+"F2.wireOp",EDGE,"E571"),sQuery(id+"F2.wireOp",EDGE,"E572"),sQuery(id+"F2.wireOp",EDGE,"E573"),sQuery(id+"F2.wireOp",EDGE,"E574"),sQuery(id+"F2.wireOp",EDGE,"E575"),sQuery(id+"F2.wireOp",EDGE,"E576"),sQuery(id+"F2.wireOp",EDGE,"E577"),sQuery(id+"F2.wireOp",EDGE,"E578"),sQuery(id+"F2.wireOp",EDGE,"E579"),sQuery(id+"F2.wireOp",EDGE,"E580"),sQuery(id+"F2.wireOp",EDGE,"E581"),sQuery(id+"F2.wireOp",EDGE,"E582"),sQuery(id+"F2.wireOp",EDGE,"E583"),sQuery(id+"F2.wireOp",EDGE,"E584"),sQuery(id+"F2.wireOp",EDGE,"E585"),sQuery(id+"F2.wireOp",EDGE,"E586"),sQuery(id+"F2.wireOp",EDGE,"E587"),sQuery(id+"F2.wireOp",EDGE,"E588"),sQuery(id+"F2.wireOp",EDGE,"E589"),sQuery(id+"F2.wireOp",EDGE,"E590"),sQuery(id+"F2.wireOp",EDGE,"E591"),sQuery(id+"F2.wireOp",EDGE,"E592"),sQuery(id+"F2.wireOp",EDGE,"E593"),sQuery(id+"F2.wireOp",EDGE,"E594"),sQuery(id+"F2.wireOp",EDGE,"E595"),sQuery(id+"F2.wireOp",EDGE,"E596"),sQuery(id+"F2.wireOp",EDGE,"E597"),sQuery(id+"F2.wireOp",EDGE,"E598"),sQuery(id+"F2.wireOp",EDGE,"E599"),sQuery(id+"F2.wireOp",EDGE,"E600"),sQuery(id+"F2.wireOp",EDGE,"E601"),sQuery(id+"F2.wireOp",EDGE,"E602"),sQuery(id+"F2.wireOp",EDGE,"E603"),sQuery(id+"F2.wireOp",EDGE,"E604"),sQuery(id+"F2.wireOp",EDGE,"E605"),sQuery(id+"F2.wireOp",EDGE,"E606"),sQuery(id+"F2.wireOp",EDGE,"E607"),sQuery(id+"F2.wireOp",EDGE,"E608"),sQuery(id+"F2.wireOp",EDGE,"E609"),sQuery(id+"F2.wireOp",EDGE,"E610"),sQuery(id+"F2.wireOp",EDGE,"E611"),sQuery(id+"F2.wireOp",EDGE,"E612"),sQuery(id+"F2.wireOp",EDGE,"E613"),sQuery(id+"F2.wireOp",EDGE,"E614"),sQuery(id+"F2.wireOp",EDGE,"E615"),sQuery(id+"F2.wireOp",EDGE,"E616"),sQuery(id+"F2.wireOp",EDGE,"E617"),sQuery(id+"F2.wireOp",EDGE,"E618"),sQuery(id+"F2.wireOp",EDGE,"E619"),sQuery(id+"F2.wireOp",EDGE,"E620"),sQuery(id+"F2.wireOp",EDGE,"E621"),sQuery(id+"F2.wireOp",EDGE,"E622"),sQuery(id+"F2.wireOp",EDGE,"E623"),sQuery(id+"F2.wireOp",EDGE,"E624"),sQuery(id+"F2.wireOp",EDGE,"E625"),sQuery(id+"F2.wireOp",EDGE,"E626"),sQuery(id+"F2.wireOp",EDGE,"E627"),sQuery(id+"F2.wireOp",EDGE,"E628"),sQuery(id+"F2.wireOp",EDGE,"E629"),sQuery(id+"F2.wireOp",EDGE,"E630"),sQuery(id+"F2.wireOp",EDGE,"E631"),sQuery(id+"F2.wireOp",EDGE,"E632"),sQuery(id+"F2.wireOp",EDGE,"E633"),sQuery(id+"F2.wireOp",EDGE,"E634"),sQuery(id+"F2.wireOp",EDGE,"E635"),sQuery(id+"F2.wireOp",EDGE,"E636"),sQuery(id+"F2.wireOp",EDGE,"E637"),sQuery(id+"F2.wireOp",EDGE,"E638"),sQuery(id+"F2.wireOp",EDGE,"E639"),sQuery(id+"F2.wireOp",EDGE,"E640"),sQuery(id+"F2.wireOp",EDGE,"E641"),sQuery(id+"F2.wireOp",EDGE,"E642"),sQuery(id+"F2.wireOp",EDGE,"E643"),sQuery(id+"F2.wireOp",EDGE,"E644"),sQuery(id+"F2.wireOp",EDGE,"E645"),sQuery(id+"F2.wireOp",EDGE,"E646"),sQuery(id+"F2.wireOp",EDGE,"E647"),sQuery(id+"F2.wireOp",EDGE,"E648"),sQuery(id+"F2.wireOp",EDGE,"E649"),sQuery(id+"F2.wireOp",EDGE,"E650"),sQuery(id+"F2.wireOp",EDGE,"E651"),sQuery(id+"F2.wireOp",EDGE,"E652"),sQuery(id+"F2.wireOp",EDGE,"E653"),sQuery(id+"F2.wireOp",EDGE,"E654"),sQuery(id+"F2.wireOp",EDGE,"E655"),sQuery(id+"F2.wireOp",EDGE,"E656"),sQuery(id+"F2.wireOp",EDGE,"E657"),sQuery(id+"F2.wireOp",EDGE,"E658"),sQuery(id+"F2.wireOp",EDGE,"E659"),sQuery(id+"F2.wireOp",EDGE,"E660"),sQuery(id+"F2.wireOp",EDGE,"E661"),sQuery(id+"F2.wireOp",EDGE,"E662"),sQuery(id+"F2.wireOp",EDGE,"E663"),sQuery(id+"F2.wireOp",EDGE,"E664"),sQuery(id+"F2.wireOp",EDGE,"E665"),sQuery(id+"F2.wireOp",EDGE,"E666"),sQuery(id+"F2.wireOp",EDGE,"E667"),sQuery(id+"F2.wireOp",EDGE,"E668"),sQuery(id+"F2.wireOp",EDGE,"E669"),sQuery(id+"F2.wireOp",EDGE,"E670"),sQuery(id+"F2.wireOp",EDGE,"E671"),sQuery(id+"F2.wireOp",EDGE,"E672"),sQuery(id+"F2.wireOp",EDGE,"E673"),sQuery(id+"F2.wireOp",EDGE,"E674"),sQuery(id+"F2.wireOp",EDGE,"E675"),sQuery(id+"F2.wireOp",EDGE,"E676"),sQuery(id+"F2.wireOp",EDGE,"E677"),sQuery(id+"F2.wireOp",EDGE,"E678"),sQuery(id+"F2.wireOp",EDGE,"E679"),sQuery(id+"F2.wireOp",EDGE,"E680"),sQuery(id+"F2.wireOp",EDGE,"E681"),sQuery(id+"F2.wireOp",EDGE,"E682"),sQuery(id+"F2.wireOp",EDGE,"E683"),sQuery(id+"F2.wireOp",EDGE,"E684"),sQuery(id+"F2.wireOp",EDGE,"E685"),sQuery(id+"F2.wireOp",EDGE,"E686"),sQuery(id+"F2.wireOp",EDGE,"E687"),sQuery(id+"F2.wireOp",EDGE,"E688"),sQuery(id+"F2.wireOp",EDGE,"E689"),sQuery(id+"F2.wireOp",EDGE,"E690"),sQuery(id+"F2.wireOp",EDGE,"E691"),sQuery(id+"F2.wireOp",EDGE,"E692"),sQuery(id+"F2.wireOp",EDGE,"E693"),sQuery(id+"F2.wireOp",EDGE,"E694"),sQuery(id+"F2.wireOp",EDGE,"E695"),sQuery(id+"F2.wireOp",EDGE,"E696"),sQuery(id+"F2.wireOp",EDGE,"E697"),sQuery(id+"F2.wireOp",EDGE,"E698"),sQuery(id+"F2.wireOp",EDGE,"E699"),sQuery(id+"F2.wireOp",EDGE,"E700"),sQuery(id+"F2.wireOp",EDGE,"E701"),sQuery(id+"F2.wireOp",EDGE,"E702"),sQuery(id+"F2.wireOp",EDGE,"E703"),sQuery(id+"F2.wireOp",EDGE,"E704"),sQuery(id+"F2.wireOp",EDGE,"E705"),sQuery(id+"F2.wireOp",EDGE,"E706"),sQuery(id+"F2.wireOp",EDGE,"E707"),sQuery(id+"F2.wireOp",EDGE,"E708"),sQuery(id+"F2.wireOp",EDGE,"E709"),sQuery(id+"F2.wireOp",EDGE,"E710"),sQuery(id+"F2.wireOp",EDGE,"E711"),sQuery(id+"F2.wireOp",EDGE,"E712"),sQuery(id+"F2.wireOp",EDGE,"E713"),sQuery(id+"F2.wireOp",EDGE,"E714"),sQuery(id+"F2.wireOp",EDGE,"E715"),sQuery(id+"F2.wireOp",EDGE,"E716"),sQuery(id+"F2.wireOp",EDGE,"E717"),sQuery(id+"F2.wireOp",EDGE,"E718"),sQuery(id+"F2.wireOp",EDGE,"E719"),sQuery(id+"F2.wireOp",EDGE,"E720"),sQuery(id+"F2.wireOp",EDGE,"E721"),sQuery(id+"F2.wireOp",EDGE,"E722"),sQuery(id+"F2.wireOp",EDGE,"E723"),sQuery(id+"F2.wireOp",EDGE,"E724"),sQuery(id+"F2.wireOp",EDGE,"E725"),sQuery(id+"F2.wireOp",EDGE,"E726"),sQuery(id+"F2.wireOp",EDGE,"E727"),sQuery(id+"F2.wireOp",EDGE,"E728"),sQuery(id+"F2.wireOp",EDGE,"E729"),sQuery(id+"F2.wireOp",EDGE,"E730"),sQuery(id+"F2.wireOp",EDGE,"E731"),sQuery(id+"F2.wireOp",EDGE,"E732"),sQuery(id+"F2.wireOp",EDGE,"E733"),sQuery(id+"F2.wireOp",EDGE,"E734"),sQuery(id+"F2.wireOp",EDGE,"E735"),sQuery(id+"F2.wireOp",EDGE,"E736"),sQuery(id+"F2.wireOp",EDGE,"E737"),sQuery(id+"F2.wireOp",EDGE,"E738"),sQuery(id+"F2.wireOp",EDGE,"E739"),sQuery(id+"F2.wireOp",EDGE,"E740"),sQuery(id+"F2.wireOp",EDGE,"E741"),sQuery(id+"F2.wireOp",EDGE,"E742"),sQuery(id+"F2.wireOp",EDGE,"E743"),sQuery(id+"F2.wireOp",EDGE,"E744"),sQuery(id+"F2.wireOp",EDGE,"E745"),sQuery(id+"F2.wireOp",EDGE,"E746"),sQuery(id+"F2.wireOp",EDGE,"E747"),sQuery(id+"F2.wireOp",EDGE,"E748"),sQuery(id+"F2.wireOp",EDGE,"E749"),sQuery(id+"F2.wireOp",EDGE,"E750"),sQuery(id+"F2.wireOp",EDGE,"E751"),sQuery(id+"F2.wireOp",EDGE,"E752"),sQuery(id+"F2.wireOp",EDGE,"E753"),sQuery(id+"F2.wireOp",EDGE,"E754"),sQuery(id+"F2.wireOp",EDGE,"E755"),sQuery(id+"F2.wireOp",EDGE,"E756"),sQuery(id+"F2.wireOp",EDGE,"E757"),sQuery(id+"F2.wireOp",EDGE,"E758"),sQuery(id+"F2.wireOp",EDGE,"E759"),sQuery(id+"F2.wireOp",EDGE,"E760"),sQuery(id+"F2.wireOp",EDGE,"E761"),sQuery(id+"F2.wireOp",EDGE,"E762"),sQuery(id+"F2.wireOp",EDGE,"E763"),sQuery(id+"F2.wireOp",EDGE,"E764"),sQuery(id+"F2.wireOp",EDGE,"E765"),sQuery(id+"F2.wireOp",EDGE,"E766"),sQuery(id+"F2.wireOp",EDGE,"E767"),sQuery(id+"F2.wireOp",EDGE,"E768"),sQuery(id+"F2.wireOp",EDGE,"E769"),sQuery(id+"F2.wireOp",EDGE,"E770"),sQuery(id+"F2.wireOp",EDGE,"E771"),sQuery(id+"F2.wireOp",EDGE,"E772"),sQuery(id+"F2.wireOp",EDGE,"E773"),sQuery(id+"F2.wireOp",EDGE,"E774"),sQuery(id+"F2.wireOp",EDGE,"E775"),sQuery(id+"F2.wireOp",EDGE,"E776"),sQuery(id+"F2.wireOp",EDGE,"E777"),sQuery(id+"F2.wireOp",EDGE,"E778"),sQuery(id+"F2.wireOp",EDGE,"E779"),sQuery(id+"F2.wireOp",EDGE,"E780"),sQuery(id+"F2.wireOp",EDGE,"E781"),sQuery(id+"F2.wireOp",EDGE,"E782"),sQuery(id+"F2.wireOp",EDGE,"E783"),sQuery(id+"F2.wireOp",EDGE,"E784"),sQuery(id+"F2.wireOp",EDGE,"E785"),sQuery(id+"F2.wireOp",EDGE,"E786"),sQuery(id+"F2.wireOp",EDGE,"E787"),sQuery(id+"F2.wireOp",EDGE,"E788"),sQuery(id+"F2.wireOp",EDGE,"E789"),sQuery(id+"F2.wireOp",EDGE,"E790"),sQuery(id+"F2.wireOp",EDGE,"E791"),sQuery(id+"F2.wireOp",EDGE,"E792"),sQuery(id+"F2.wireOp",EDGE,"E793"),sQuery(id+"F2.wireOp",EDGE,"E794"),sQuery(id+"F2.wireOp",EDGE,"E795"),sQuery(id+"F2.wireOp",EDGE,"E796"),sQuery(id+"F2.wireOp",EDGE,"E797"),sQuery(id+"F2.wireOp",EDGE,"E798"),sQuery(id+"F2.wireOp",EDGE,"E799"),sQuery(id+"F2.wireOp",EDGE,"E800"),sQuery(id+"F2.wireOp",EDGE,"E801"),sQuery(id+"F2.wireOp",EDGE,"E802"),sQuery(id+"F2.wireOp",EDGE,"E803"),sQuery(id+"F2.wireOp",EDGE,"E804"),sQuery(id+"F2.wireOp",EDGE,"E805"),sQuery(id+"F2.wireOp",EDGE,"E806"),sQuery(id+"F2.wireOp",EDGE,"E807"),sQuery(id+"F2.wireOp",EDGE,"E808"),sQuery(id+"F2.wireOp",EDGE,"E809"),sQuery(id+"F2.wireOp",EDGE,"E810"),sQuery(id+"F2.wireOp",EDGE,"E811"),sQuery(id+"F2.wireOp",EDGE,"E812"),sQuery(id+"F2.wireOp",EDGE,"E813"),sQuery(id+"F2.wireOp",EDGE,"E814"),sQuery(id+"F2.wireOp",EDGE,"E815"),sQuery(id+"F2.wireOp",EDGE,"E816"),sQuery(id+"F2.wireOp",EDGE,"E817"),sQuery(id+"F2.wireOp",EDGE,"E818"),sQuery(id+"F2.wireOp",EDGE,"E819"),sQuery(id+"F2.wireOp",EDGE,"E820"),sQuery(id+"F2.wireOp",EDGE,"E821"),sQuery(id+"F2.wireOp",EDGE,"E822"),sQuery(id+"F2.wireOp",EDGE,"E823"),sQuery(id+"F2.wireOp",EDGE,"E824"),sQuery(id+"F2.wireOp",EDGE,"E825"),sQuery(id+"F2.wireOp",EDGE,"E826"),sQuery(id+"F2.wireOp",EDGE,"E827"),sQuery(id+"F2.wireOp",EDGE,"E828"),sQuery(id+"F2.wireOp",EDGE,"E829"),sQuery(id+"F2.wireOp",EDGE,"E830"),sQuery(id+"F2.wireOp",EDGE,"E831"),sQuery(id+"F2.wireOp",EDGE,"E832"),sQuery(id+"F2.wireOp",EDGE,"E833"),sQuery(id+"F2.wireOp",EDGE,"E834"),sQuery(id+"F2.wireOp",EDGE,"E835"),sQuery(id+"F2.wireOp",EDGE,"E836"),sQuery(id+"F2.wireOp",EDGE,"E837"),sQuery(id+"F2.wireOp",EDGE,"E838"),sQuery(id+"F2.wireOp",EDGE,"E839"),sQuery(id+"F2.wireOp",EDGE,"E840"),sQuery(id+"F2.wireOp",EDGE,"E841"),sQuery(id+"F2.wireOp",EDGE,"E842"),sQuery(id+"F2.wireOp",EDGE,"E843"),sQuery(id+"F2.wireOp",EDGE,"E844"),sQuery(id+"F2.wireOp",EDGE,"E845"),sQuery(id+"F2.wireOp",EDGE,"E846"),sQuery(id+"F2.wireOp",EDGE,"E847"),sQuery(id+"F2.wireOp",EDGE,"E848"),sQuery(id+"F2.wireOp",EDGE,"E849"),sQuery(id+"F2.wireOp",EDGE,"E850"),sQuery(id+"F2.wireOp",EDGE,"E851"),sQuery(id+"F2.wireOp",EDGE,"E852"),sQuery(id+"F2.wireOp",EDGE,"E853"),sQuery(id+"F2.wireOp",EDGE,"E854"),sQuery(id+"F2.wireOp",EDGE,"E855"),sQuery(id+"F2.wireOp",EDGE,"E856"),sQuery(id+"F2.wireOp",EDGE,"E857"),sQuery(id+"F2.wireOp",EDGE,"E858"),sQuery(id+"F2.wireOp",EDGE,"E859"),sQuery(id+"F2.wireOp",EDGE,"E860"),sQuery(id+"F2.wireOp",EDGE,"E861"),sQuery(id+"F2.wireOp",EDGE,"E862"),sQuery(id+"F2.wireOp",EDGE,"E863"),sQuery(id+"F2.wireOp",EDGE,"E864"),sQuery(id+"F2.wireOp",EDGE,"E865"),sQuery(id+"F2.wireOp",EDGE,"E866"),sQuery(id+"F2.wireOp",EDGE,"E867"),sQuery(id+"F2.wireOp",EDGE,"E868"),sQuery(id+"F2.wireOp",EDGE,"E869"),sQuery(id+"F2.wireOp",EDGE,"E870"),sQuery(id+"F2.wireOp",EDGE,"E871"),sQuery(id+"F2.wireOp",EDGE,"E872"),sQuery(id+"F2.wireOp",EDGE,"E873"),sQuery(id+"F2.wireOp",EDGE,"E874"),sQuery(id+"F2.wireOp",EDGE,"E875"),sQuery(id+"F2.wireOp",EDGE,"E876"),sQuery(id+"F2.wireOp",EDGE,"E877"),sQuery(id+"F2.wireOp",EDGE,"E878"),sQuery(id+"F2.wireOp",EDGE,"E879"),sQuery(id+"F2.wireOp",EDGE,"E880"),sQuery(id+"F2.wireOp",EDGE,"E881"),sQuery(id+"F2.wireOp",EDGE,"E882"),sQuery(id+"F2.wireOp",EDGE,"E883"),sQuery(id+"F2.wireOp",EDGE,"E884"),sQuery(id+"F2.wireOp",EDGE,"E885"),sQuery(id+"F2.wireOp",EDGE,"E886"),sQuery(id+"F2.wireOp",EDGE,"E887"),sQuery(id+"F2.wireOp",EDGE,"E888"),sQuery(id+"F2.wireOp",EDGE,"E889"),sQuery(id+"F2.wireOp",EDGE,"E890"),sQuery(id+"F2.wireOp",EDGE,"E891"),sQuery(id+"F2.wireOp",EDGE,"E892"),sQuery(id+"F2.wireOp",EDGE,"E893"),sQuery(id+"F2.wireOp",EDGE,"E894"),sQuery(id+"F2.wireOp",EDGE,"E895"),sQuery(id+"F2.wireOp",EDGE,"E896"),sQuery(id+"F2.wireOp",EDGE,"E897"),sQuery(id+"F2.wireOp",EDGE,"E898"),sQuery(id+"F2.wireOp",EDGE,"E899"),sQuery(id+"F2.wireOp",EDGE,"E900"),sQuery(id+"F2.wireOp",EDGE,"E901"),sQuery(id+"F2.wireOp",EDGE,"E902"),sQuery(id+"F2.wireOp",EDGE,"E903"),sQuery(id+"F2.wireOp",EDGE,"E904"),sQuery(id+"F2.wireOp",EDGE,"E905"),sQuery(id+"F2.wireOp",EDGE,"E906"),sQuery(id+"F2.wireOp",EDGE,"E907"),sQuery(id+"F2.wireOp",EDGE,"E908"),sQuery(id+"F2.wireOp",EDGE,"E909"),sQuery(id+"F2.wireOp",EDGE,"E910"),sQuery(id+"F2.wireOp",EDGE,"E911"),sQuery(id+"F2.wireOp",EDGE,"E912"),sQuery(id+"F2.wireOp",EDGE,"E913"),sQuery(id+"F2.wireOp",EDGE,"E914"),sQuery(id+"F2.wireOp",EDGE,"E915"),sQuery(id+"F2.wireOp",EDGE,"E916"),sQuery(id+"F2.wireOp",EDGE,"E917"),sQuery(id+"F2.wireOp",EDGE,"E918"),sQuery(id+"F2.wireOp",EDGE,"E919"),sQuery(id+"F2.wireOp",EDGE,"E920"),sQuery(id+"F2.wireOp",EDGE,"E921"),sQuery(id+"F2.wireOp",EDGE,"E922"),sQuery(id+"F2.wireOp",EDGE,"E923"),sQuery(id+"F2.wireOp",EDGE,"E924"),sQuery(id+"F2.wireOp",EDGE,"E925"),sQuery(id+"F2.wireOp",EDGE,"E926"),sQuery(id+"F2.wireOp",EDGE,"E927"),sQuery(id+"F2.wireOp",EDGE,"E928"),sQuery(id+"F2.wireOp",EDGE,"E929"),sQuery(id+"F2.wireOp",EDGE,"E930"),sQuery(id+"F2.wireOp",EDGE,"E931"),sQuery(id+"F2.wireOp",EDGE,"E932"),sQuery(id+"F2.wireOp",EDGE,"E933"),sQuery(id+"F2.wireOp",EDGE,"E934"),sQuery(id+"F2.wireOp",EDGE,"E935"),sQuery(id+"F2.wireOp",EDGE,"E936"),sQuery(id+"F2.wireOp",EDGE,"E937"),sQuery(id+"F2.wireOp",EDGE,"E938"),sQuery(id+"F2.wireOp",EDGE,"E939"),sQuery(id+"F2.wireOp",EDGE,"E940"),sQuery(id+"F2.wireOp",EDGE,"E941"),sQuery(id+"F2.wireOp",EDGE,"E942"),sQuery(id+"F2.wireOp",EDGE,"E943"),sQuery(id+"F2.wireOp",EDGE,"E944"),sQuery(id+"F2.wireOp",EDGE,"E945"),sQuery(id+"F2.wireOp",EDGE,"E946"),sQuery(id+"F2.wireOp",EDGE,"E947"),sQuery(id+"F2.wireOp",EDGE,"E948"),sQuery(id+"F2.wireOp",EDGE,"E949"),sQuery(id+"F2.wireOp",EDGE,"E950"),sQuery(id+"F2.wireOp",EDGE,"E951"),sQuery(id+"F2.wireOp",EDGE,"E952"),sQuery(id+"F2.wireOp",EDGE,"E953"),sQuery(id+"F2.wireOp",EDGE,"E954"),sQuery(id+"F2.wireOp",EDGE,"E955"),sQuery(id+"F2.wireOp",EDGE,"E956"),sQuery(id+"F2.wireOp",EDGE,"E957"),sQuery(id+"F2.wireOp",EDGE,"E958"),sQuery(id+"F2.wireOp",EDGE,"E959"),sQuery(id+"F2.wireOp",EDGE,"E960"),sQuery(id+"F2.wireOp",EDGE,"E961"),sQuery(id+"F2.wireOp",EDGE,"E962"),sQuery(id+"F2.wireOp",EDGE,"E963"),sQuery(id+"F2.wireOp",EDGE,"E964"),sQuery(id+"F2.wireOp",EDGE,"E965"),sQuery(id+"F2.wireOp",EDGE,"E966"),sQuery(id+"F2.wireOp",EDGE,"E967"),sQuery(id+"F2.wireOp",EDGE,"E968"),sQuery(id+"F2.wireOp",EDGE,"E969"),sQuery(id+"F2.wireOp",EDGE,"E970"),sQuery(id+"F2.wireOp",EDGE,"E971"),sQuery(id+"F2.wireOp",EDGE,"E972"),sQuery(id+"F2.wireOp",EDGE,"E973"),sQuery(id+"F2.wireOp",EDGE,"E974"),sQuery(id+"F2.wireOp",EDGE,"E975"),sQuery(id+"F2.wireOp",EDGE,"E976"),sQuery(id+"F2.wireOp",EDGE,"E977"),sQuery(id+"F2.wireOp",EDGE,"E978"),sQuery(id+"F2.wireOp",EDGE,"E979"),sQuery(id+"F2.wireOp",EDGE,"E980"),sQuery(id+"F2.wireOp",EDGE,"E981"),sQuery(id+"F2.wireOp",EDGE,"E982"),sQuery(id+"F2.wireOp",EDGE,"E983"),sQuery(id+"F2.wireOp",EDGE,"E984"),sQuery(id+"F2.wireOp",EDGE,"E985"),sQuery(id+"F2.wireOp",EDGE,"E986"),sQuery(id+"F2.wireOp",EDGE,"E987"),sQuery(id+"F2.wireOp",EDGE,"E988"),sQuery(id+"F2.wireOp",EDGE,"E989"),sQuery(id+"F2.wireOp",EDGE,"E990"),sQuery(id+"F2.wireOp",EDGE,"E991"),sQuery(id+"F2.wireOp",EDGE,"E992"),sQuery(id+"F2.wireOp",EDGE,"E993"),sQuery(id+"F2.wireOp",EDGE,"E994"),sQuery(id+"F2.wireOp",EDGE,"E995"),sQuery(id+"F2.wireOp",EDGE,"E996"),sQuery(id+"F2.wireOp",EDGE,"E997"),sQuery(id+"F2.wireOp",EDGE,"E998"),sQuery(id+"F2.wireOp",EDGE,"E999"),sQuery(id+"F2.wireOp",EDGE,"E1000"),sQuery(id+"F2.wireOp",EDGE,"E1001"),sQuery(id+"F2.wireOp",EDGE,"E1002"),sQuery(id+"F2.wireOp",EDGE,"E1003"),sQuery(id+"F2.wireOp",EDGE,"E1004"),sQuery(id+"F2.wireOp",EDGE,"E1005"),sQuery(id+"F2.wireOp",EDGE,"E1006"),sQuery(id+"F2.wireOp",EDGE,"E1007"),sQuery(id+"F2.wireOp",EDGE,"E1008"),sQuery(id+"F2.wireOp",EDGE,"E1009"),sQuery(id+"F2.wireOp",EDGE,"E1010"),sQuery(id+"F2.wireOp",EDGE,"E1011"),sQuery(id+"F2.wireOp",EDGE,"E1012"),sQuery(id+"F2.wireOp",EDGE,"E1013"),sQuery(id+"F2.wireOp",EDGE,"E1014"),sQuery(id+"F2.wireOp",EDGE,"E1015"),sQuery(id+"F2.wireOp",EDGE,"E1016"),sQuery(id+"F2.wireOp",EDGE,"E1017"),sQuery(id+"F2.wireOp",EDGE,"E1018"),sQuery(id+"F2.wireOp",EDGE,"E1019"),sQuery(id+"F2.wireOp",EDGE,"E1020"),sQuery(id+"F2.wireOp",EDGE,"E1021"),sQuery(id+"F2.wireOp",EDGE,"E1022"),sQuery(id+"F2.wireOp",EDGE,"E1023"),sQuery(id+"F2.wireOp",EDGE,"E1024"),sQuery(id+"F2.wireOp",EDGE,"E1025"),sQuery(id+"F2.wireOp",EDGE,"E1026"),sQuery(id+"F2.wireOp",EDGE,"E1027"),sQuery(id+"F2.wireOp",EDGE,"E1028"),sQuery(id+"F2.wireOp",EDGE,"E1029"),sQuery(id+"F2.wireOp",EDGE,"E1030"),sQuery(id+"F2.wireOp",EDGE,"E1031"),sQuery(id+"F2.wireOp",EDGE,"E1032"),sQuery(id+"F2.wireOp",EDGE,"E1033"),sQuery(id+"F2.wireOp",EDGE,"E1034"),sQuery(id+"F2.wireOp",EDGE,"E1035"),sQuery(id+"F2.wireOp",EDGE,"E1036"),sQuery(id+"F2.wireOp",EDGE,"E1037"),sQuery(id+"F2.wireOp",EDGE,"E1038"),sQuery(id+"F2.wireOp",EDGE,"E1039"),sQuery(id+"F2.wireOp",EDGE,"E1040"),sQuery(id+"F2.wireOp",EDGE,"E1041"),sQuery(id+"F2.wireOp",EDGE,"E1042"),sQuery(id+"F2.wireOp",EDGE,"E1043"),sQuery(id+"F2.wireOp",EDGE,"E1044"),sQuery(id+"F2.wireOp",EDGE,"E1045"),sQuery(id+"F2.wireOp",EDGE,"E1046"),sQuery(id+"F2.wireOp",EDGE,"E1047"),sQuery(id+"F2.wireOp",EDGE,"E1048"),sQuery(id+"F2.wireOp",EDGE,"E1049"),sQuery(id+"F2.wireOp",EDGE,"E1050"),sQuery(id+"F2.wireOp",EDGE,"E1051"),sQuery(id+"F2.wireOp",EDGE,"E1052"),sQuery(id+"F2.wireOp",EDGE,"E1053"),sQuery(id+"F2.wireOp",EDGE,"E1054"),sQuery(id+"F2.wireOp",EDGE,"E1055"),sQuery(id+"F2.wireOp",EDGE,"E1056"),sQuery(id+"F2.wireOp",EDGE,"E1057"),sQuery(id+"F2.wireOp",EDGE,"E1058"),sQuery(id+"F2.wireOp",EDGE,"E1059"),sQuery(id+"F2.wireOp",EDGE,"E1060"),sQuery(id+"F2.wireOp",EDGE,"E1061"),sQuery(id+"F2.wireOp",EDGE,"E1062"),sQuery(id+"F2.wireOp",EDGE,"E1063"),sQuery(id+"F2.wireOp",EDGE,"E1064"),sQuery(id+"F2.wireOp",EDGE,"E1065"),sQuery(id+"F2.wireOp",EDGE,"E1066"),sQuery(id+"F2.wireOp",EDGE,"E1067"),sQuery(id+"F2.wireOp",EDGE,"E1068"),sQuery(id+"F2.wireOp",EDGE,"E1069"),sQuery(id+"F2.wireOp",EDGE,"E1070"),sQuery(id+"F2.wireOp",EDGE,"E1071"),sQuery(id+"F2.wireOp",EDGE,"E1072"),sQuery(id+"F2.wireOp",EDGE,"E1073"),sQuery(id+"F2.wireOp",EDGE,"E1074"),sQuery(id+"F2.wireOp",EDGE,"E1075"),sQuery(id+"F2.wireOp",EDGE,"E1076"),sQuery(id+"F2.wireOp",EDGE,"E1077"),sQuery(id+"F2.wireOp",EDGE,"E1078"),sQuery(id+"F2.wireOp",EDGE,"E1079"),sQuery(id+"F2.wireOp",EDGE,"E1080"),sQuery(id+"F2.wireOp",EDGE,"E1081"),sQuery(id+"F2.wireOp",EDGE,"E1082"),sQuery(id+"F2.wireOp",EDGE,"E1083"),sQuery(id+"F2.wireOp",EDGE,"E1084"),sQuery(id+"F2.wireOp",EDGE,"E1085"),sQuery(id+"F2.wireOp",EDGE,"E1086"),sQuery(id+"F2.wireOp",EDGE,"E1087"),sQuery(id+"F2.wireOp",EDGE,"E1088"),sQuery(id+"F2.wireOp",EDGE,"E1089"),sQuery(id+"F2.wireOp",EDGE,"E1090"),sQuery(id+"F2.wireOp",EDGE,"E1091"),sQuery(id+"F2.wireOp",EDGE,"E1092"),sQuery(id+"F2.wireOp",EDGE,"E1093"),sQuery(id+"F2.wireOp",EDGE,"E1094"),sQuery(id+"F2.wireOp",EDGE,"E1095"),sQuery(id+"F2.wireOp",EDGE,"E1096"),sQuery(id+"F2.wireOp",EDGE,"E1097"),sQuery(id+"F2.wireOp",EDGE,"E1098"),sQuery(id+"F2.wireOp",EDGE,"E1099"),sQuery(id+"F2.wireOp",EDGE,"E1100"),sQuery(id+"F2.wireOp",EDGE,"E1101"),sQuery(id+"F2.wireOp",EDGE,"E1102"),sQuery(id+"F2.wireOp",EDGE,"E1103"),sQuery(id+"F2.wireOp",EDGE,"E1104"),sQuery(id+"F2.wireOp",EDGE,"E1105"),sQuery(id+"F2.wireOp",EDGE,"E1106"),sQuery(id+"F2.wireOp",EDGE,"E1107"),sQuery(id+"F2.wireOp",EDGE,"E1108"),sQuery(id+"F2.wireOp",EDGE,"E1109"),sQuery(id+"F2.wireOp",EDGE,"E1110"),sQuery(id+"F2.wireOp",EDGE,"E1111"),sQuery(id+"F2.wireOp",EDGE,"E1112"),sQuery(id+"F2.wireOp",EDGE,"E1113"),sQuery(id+"F2.wireOp",EDGE,"E1114"),sQuery(id+"F2.wireOp",EDGE,"E1115"),sQuery(id+"F2.wireOp",EDGE,"E1116"),sQuery(id+"F2.wireOp",EDGE,"E1117"),sQuery(id+"F2.wireOp",EDGE,"E1118"),sQuery(id+"F2.wireOp",EDGE,"E1119"),sQuery(id+"F2.wireOp",EDGE,"E1120"),sQuery(id+"F2.wireOp",EDGE,"E1121"),sQuery(id+"F2.wireOp",EDGE,"E1122"),sQuery(id+"F2.wireOp",EDGE,"E1123"),sQuery(id+"F2.wireOp",EDGE,"E1124"),sQuery(id+"F2.wireOp",EDGE,"E1125"),sQuery(id+"F2.wireOp",EDGE,"E1126"),sQuery(id+"F2.wireOp",EDGE,"E1127"),sQuery(id+"F2.wireOp",EDGE,"E1128"),sQuery(id+"F2.wireOp",EDGE,"E1129"),sQuery(id+"F2.wireOp",EDGE,"E1130"),sQuery(id+"F2.wireOp",EDGE,"E1131"),sQuery(id+"F2.wireOp",EDGE,"E1132"),sQuery(id+"F2.wireOp",EDGE,"E1133"),sQuery(id+"F2.wireOp",EDGE,"E1134"),sQuery(id+"F2.wireOp",EDGE,"E1135"),sQuery(id+"F2.wireOp",EDGE,"E1136"),sQuery(id+"F2.wireOp",EDGE,"E1137"),sQuery(id+"F2.wireOp",EDGE,"E1138"),sQuery(id+"F2.wireOp",EDGE,"E1139"),sQuery(id+"F2.wireOp",EDGE,"E1140"),sQuery(id+"F2.wireOp",EDGE,"E1141"),sQuery(id+"F2.wireOp",EDGE,"E1142"),sQuery(id+"F2.wireOp",EDGE,"E1143"),sQuery(id+"F2.wireOp",EDGE,"E1144"),sQuery(id+"F2.wireOp",EDGE,"E1145"),sQuery(id+"F2.wireOp",EDGE,"E1146"),sQuery(id+"F2.wireOp",EDGE,"E1147"),sQuery(id+"F2.wireOp",EDGE,"E1148"),sQuery(id+"F2.wireOp",EDGE,"E1149"),sQuery(id+"F2.wireOp",EDGE,"E1150"),sQuery(id+"F2.wireOp",EDGE,"E1151"),sQuery(id+"F2.wireOp",EDGE,"E1152"),sQuery(id+"F2.wireOp",EDGE,"E1153"),sQuery(id+"F2.wireOp",EDGE,"E1154"),sQuery(id+"F2.wireOp",EDGE,"E1155"),sQuery(id+"F2.wireOp",EDGE,"E1156"),sQuery(id+"F2.wireOp",EDGE,"E1157"),sQuery(id+"F2.wireOp",EDGE,"E1158"),sQuery(id+"F2.wireOp",EDGE,"E1159"),sQuery(id+"F2.wireOp",EDGE,"E1160"),sQuery(id+"F2.wireOp",EDGE,"E1161"),sQuery(id+"F2.wireOp",EDGE,"E1162"),sQuery(id+"F2.wireOp",EDGE,"E1163"),sQuery(id+"F2.wireOp",EDGE,"E1164"),sQuery(id+"F2.wireOp",EDGE,"E1165"),sQuery(id+"F2.wireOp",EDGE,"E1166"),sQuery(id+"F2.wireOp",EDGE,"E1167"),sQuery(id+"F2.wireOp",EDGE,"E1168"),sQuery(id+"F2.wireOp",EDGE,"E1169"),sQuery(id+"F2.wireOp",EDGE,"E1170"),sQuery(id+"F2.wireOp",EDGE,"E1171"),sQuery(id+"F2.wireOp",EDGE,"E1172"),sQuery(id+"F2.wireOp",EDGE,"E1173"),sQuery(id+"F2.wireOp",EDGE,"E1174"),sQuery(id+"F2.wireOp",EDGE,"E1175"),sQuery(id+"F2.wireOp",EDGE,"E1176"),sQuery(id+"F2.wireOp",EDGE,"E1177"),sQuery(id+"F2.wireOp",EDGE,"E1178"),sQuery(id+"F2.wireOp",EDGE,"E1179"),sQuery(id+"F2.wireOp",EDGE,"E1180"),sQuery(id+"F2.wireOp",EDGE,"E1181"),sQuery(id+"F2.wireOp",EDGE,"E1182"),sQuery(id+"F2.wireOp",EDGE,"E1183"),sQuery(id+"F2.wireOp",EDGE,"E1184"),sQuery(id+"F2.wireOp",EDGE,"E1185"),sQuery(id+"F2.wireOp",EDGE,"E1186"),sQuery(id+"F2.wireOp",EDGE,"E1187"),sQuery(id+"F2.wireOp",EDGE,"E1188"),sQuery(id+"F2.wireOp",EDGE,"E1189"),sQuery(id+"F2.wireOp",EDGE,"E1190"),sQuery(id+"F2.wireOp",EDGE,"E1191"),sQuery(id+"F2.wireOp",EDGE,"E1192"),sQuery(id+"F2.wireOp",EDGE,"E1193"),sQuery(id+"F2.wireOp",EDGE,"E1194"),sQuery(id+"F2.wireOp",EDGE,"E1195"),sQuery(id+"F2.wireOp",EDGE,"E1196"),sQuery(id+"F2.wireOp",EDGE,"E1197"),sQuery(id+"F2.wireOp",EDGE,"E1198"),sQuery(id+"F2.wireOp",EDGE,"E1199"),sQuery(id+"F2.wireOp",EDGE,"E1200"),sQuery(id+"F2.wireOp",EDGE,"E1201"),sQuery(id+"F2.wireOp",EDGE,"E1202"),sQuery(id+"F2.wireOp",EDGE,"E1203"),sQuery(id+"F2.wireOp",EDGE,"E1204"),sQuery(id+"F2.wireOp",EDGE,"E1205"),sQuery(id+"F2.wireOp",EDGE,"E1206"),sQuery(id+"F2.wireOp",EDGE,"E1207"),sQuery(id+"F2.wireOp",EDGE,"E1208"),sQuery(id+"F2.wireOp",EDGE,"E1209"),sQuery(id+"F2.wireOp",EDGE,"E1210"),sQuery(id+"F2.wireOp",EDGE,"E1211"),sQuery(id+"F2.wireOp",EDGE,"E1212"),sQuery(id+"F2.wireOp",EDGE,"E1213"),sQuery(id+"F2.wireOp",EDGE,"E1214"),sQuery(id+"F2.wireOp",EDGE,"E1215"),sQuery(id+"F2.wireOp",EDGE,"E1216"),sQuery(id+"F2.wireOp",EDGE,"E1217"),sQuery(id+"F2.wireOp",EDGE,"E1218"),sQuery(id+"F2.wireOp",EDGE,"E1219"),sQuery(id+"F2.wireOp",EDGE,"E1220"),sQuery(id+"F2.wireOp",EDGE,"E1221"),sQuery(id+"F2.wireOp",EDGE,"E1222"),sQuery(id+"F2.wireOp",EDGE,"E1223"),sQuery(id+"F2.wireOp",EDGE,"E1224"),sQuery(id+"F2.wireOp",EDGE,"E1225"),sQuery(id+"F2.wireOp",EDGE,"E1226"),sQuery(id+"F2.wireOp",EDGE,"E1227"),sQuery(id+"F2.wireOp",EDGE,"E1228"),sQuery(id+"F2.wireOp",EDGE,"E1229"),sQuery(id+"F2.wireOp",EDGE,"E1230"),sQuery(id+"F2.wireOp",EDGE,"E1231"),sQuery(id+"F2.wireOp",EDGE,"E1232"),sQuery(id+"F2.wireOp",EDGE,"E1233"),sQuery(id+"F2.wireOp",EDGE,"E1234"),sQuery(id+"F2.wireOp",EDGE,"E1235"),sQuery(id+"F2.wireOp",EDGE,"E1236"),sQuery(id+"F2.wireOp",EDGE,"E1237"),sQuery(id+"F2.wireOp",EDGE,"E1238"),sQuery(id+"F2.wireOp",EDGE,"E1239"),sQuery(id+"F2.wireOp",EDGE,"E1240"),sQuery(id+"F2.wireOp",EDGE,"E1241"),sQuery(id+"F2.wireOp",EDGE,"E1242"),sQuery(id+"F2.wireOp",EDGE,"E1243"),sQuery(id+"F2.wireOp",EDGE,"E1244"),sQuery(id+"F2.wireOp",EDGE,"E1245"),sQuery(id+"F2.wireOp",EDGE,"E1246"),sQuery(id+"F2.wireOp",EDGE,"E1247"),sQuery(id+"F2.wireOp",EDGE,"E1248"),sQuery(id+"F2.wireOp",EDGE,"E1249"),sQuery(id+"F2.wireOp",EDGE,"E1250"),sQuery(id+"F2.wireOp",EDGE,"E1251"),sQuery(id+"F2.wireOp",EDGE,"E1252"),sQuery(id+"F2.wireOp",EDGE,"E1253"),sQuery(id+"F2.wireOp",EDGE,"E1254"),sQuery(id+"F2.wireOp",EDGE,"E1255"),sQuery(id+"F2.wireOp",EDGE,"E1256"),sQuery(id+"F2.wireOp",EDGE,"E1257"),sQuery(id+"F2.wireOp",EDGE,"E1258"),sQuery(id+"F2.wireOp",EDGE,"E1259"),sQuery(id+"F2.wireOp",EDGE,"E1260"),sQuery(id+"F2.wireOp",EDGE,"E1261"),sQuery(id+"F2.wireOp",EDGE,"E1262"),sQuery(id+"F2.wireOp",EDGE,"E1263"),sQuery(id+"F2.wireOp",EDGE,"E1264"),sQuery(id+"F2.wireOp",EDGE,"E1265"),sQuery(id+"F2.wireOp",EDGE,"E1266"),sQuery(id+"F2.wireOp",EDGE,"E1267"),sQuery(id+"F2.wireOp",EDGE,"E1268"),sQuery(id+"F2.wireOp",EDGE,"E1269"),sQuery(id+"F2.wireOp",EDGE,"E1270"),sQuery(id+"F2.wireOp",EDGE,"E1271"),sQuery(id+"F2.wireOp",EDGE,"E1272"),sQuery(id+"F2.wireOp",EDGE,"E1273"),sQuery(id+"F2.wireOp",EDGE,"E1274"),sQuery(id+"F2.wireOp",EDGE,"E1275"),sQuery(id+"F2.wireOp",EDGE,"E1276"),sQuery(id+"F2.wireOp",EDGE,"E1277"),sQuery(id+"F2.wireOp",EDGE,"E1278"),sQuery(id+"F2.wireOp",EDGE,"E1279"),sQuery(id+"F2.wireOp",EDGE,"E1280"),sQuery(id+"F2.wireOp",EDGE,"E1281"),sQuery(id+"F2.wireOp",EDGE,"E1282"),sQuery(id+"F2.wireOp",EDGE,"E1283"),sQuery(id+"F2.wireOp",EDGE,"E1284"),sQuery(id+"F2.wireOp",EDGE,"E1285"),sQuery(id+"F2.wireOp",EDGE,"E1286"),sQuery(id+"F2.wireOp",EDGE,"E1287"),sQuery(id+"F2.wireOp",EDGE,"E1288"),sQuery(id+"F2.wireOp",EDGE,"E1289"),sQuery(id+"F2.wireOp",EDGE,"E1290"),sQuery(id+"F2.wireOp",EDGE,"E1291"),sQuery(id+"F2.wireOp",EDGE,"E1292"),sQuery(id+"F2.wireOp",EDGE,"E1293"),sQuery(id+"F2.wireOp",EDGE,"E1294"),sQuery(id+"F2.wireOp",EDGE,"E1295"),sQuery(id+"F2.wireOp",EDGE,"E1296"),sQuery(id+"F2.wireOp",EDGE,"E1297"),sQuery(id+"F2.wireOp",EDGE,"E1298"),sQuery(id+"F2.wireOp",EDGE,"E1299"),sQuery(id+"F2.wireOp",EDGE,"E1300"),sQuery(id+"F2.wireOp",EDGE,"E1301"),sQuery(id+"F2.wireOp",EDGE,"E1302"),sQuery(id+"F2.wireOp",EDGE,"E1303"),sQuery(id+"F2.wireOp",EDGE,"E1304"),sQuery(id+"F2.wireOp",EDGE,"E1305"),sQuery(id+"F2.wireOp",EDGE,"E1306"),sQuery(id+"F2.wireOp",EDGE,"E1307"),sQuery(id+"F2.wireOp",EDGE,"E1308"),sQuery(id+"F2.wireOp",EDGE,"E1309"),sQuery(id+"F2.wireOp",EDGE,"E1310"),sQuery(id+"F2.wireOp",EDGE,"E1311"),sQuery(id+"F2.wireOp",EDGE,"E1312"),sQuery(id+"F2.wireOp",EDGE,"E1313"),sQuery(id+"F2.wireOp",EDGE,"E1314"),sQuery(id+"F2.wireOp",EDGE,"E1315"),sQuery(id+"F2.wireOp",EDGE,"E1316"),sQuery(id+"F2.wireOp",EDGE,"E1317"),sQuery(id+"F2.wireOp",EDGE,"E1318"),sQuery(id+"F2.wireOp",EDGE,"E1319"),sQuery(id+"F2.wireOp",EDGE,"E1320"),sQuery(id+"F2.wireOp",EDGE,"E1321"),sQuery(id+"F2.wireOp",EDGE,"E1322"),sQuery(id+"F2.wireOp",EDGE,"E1323"),sQuery(id+"F2.wireOp",EDGE,"E1324"),sQuery(id+"F2.wireOp",EDGE,"E1325"),sQuery(id+"F2.wireOp",EDGE,"E1326"),sQuery(id+"F2.wireOp",EDGE,"E1327"),sQuery(id+"F2.wireOp",EDGE,"E1328"),sQuery(id+"F2.wireOp",EDGE,"E1329"),sQuery(id+"F2.wireOp",EDGE,"E1330"),sQuery(id+"F2.wireOp",EDGE,"E1331"),sQuery(id+"F2.wireOp",EDGE,"E1332"),sQuery(id+"F2.wireOp",EDGE,"E1333"),sQuery(id+"F2.wireOp",EDGE,"E1334"),sQuery(id+"F2.wireOp",EDGE,"E1335"),sQuery(id+"F2.wireOp",EDGE,"E1336"),sQuery(id+"F2.wireOp",EDGE,"E1337"),sQuery(id+"F2.wireOp",EDGE,"E1338"),sQuery(id+"F2.wireOp",EDGE,"E1339"),sQuery(id+"F2.wireOp",EDGE,"E1340"),sQuery(id+"F2.wireOp",EDGE,"E1341"),sQuery(id+"F2.wireOp",EDGE,"E1342"),sQuery(id+"F2.wireOp",EDGE,"E1343"),sQuery(id+"F2.wireOp",EDGE,"E1344"),sQuery(id+"F2.wireOp",EDGE,"E1345"),sQuery(id+"F2.wireOp",EDGE,"E1346"),sQuery(id+"F2.wireOp",EDGE,"E1347"),sQuery(id+"F2.wireOp",EDGE,"E1348"),sQuery(id+"F2.wireOp",EDGE,"E1349"),sQuery(id+"F2.wireOp",EDGE,"E1350"),sQuery(id+"F2.wireOp",EDGE,"E1351"),sQuery(id+"F2.wireOp",EDGE,"E1352"),sQuery(id+"F2.wireOp",EDGE,"E1353"),sQuery(id+"F2.wireOp",EDGE,"E1354"),sQuery(id+"F2.wireOp",EDGE,"E1355"),sQuery(id+"F2.wireOp",EDGE,"E1356"),sQuery(id+"F2.wireOp",EDGE,"E1357"),sQuery(id+"F2.wireOp",EDGE,"E1358"),sQuery(id+"F2.wireOp",EDGE,"E1359"),sQuery(id+"F2.wireOp",EDGE,"E1360"),sQuery(id+"F2.wireOp",EDGE,"E1361"),sQuery(id+"F2.wireOp",EDGE,"E1362"),sQuery(id+"F2.wireOp",EDGE,"E1363"),sQuery(id+"F2.wireOp",EDGE,"E1364"),sQuery(id+"F2.wireOp",EDGE,"E1365"),sQuery(id+"F2.wireOp",EDGE,"E1366"),sQuery(id+"F2.wireOp",EDGE,"E1367"),sQuery(id+"F2.wireOp",EDGE,"E1368"),sQuery(id+"F2.wireOp",EDGE,"E1369"),sQuery(id+"F2.wireOp",EDGE,"E1370"),sQuery(id+"F2.wireOp",EDGE,"E1371"),sQuery(id+"F2.wireOp",EDGE,"E1372"),sQuery(id+"F2.wireOp",EDGE,"E1373"),sQuery(id+"F2.wireOp",EDGE,"E1374"),sQuery(id+"F2.wireOp",EDGE,"E1375"),sQuery(id+"F2.wireOp",EDGE,"E1376"),sQuery(id+"F2.wireOp",EDGE,"E1377"),sQuery(id+"F2.wireOp",EDGE,"E1378"),sQuery(id+"F2.wireOp",EDGE,"E1379"),sQuery(id+"F2.wireOp",EDGE,"E1380"),sQuery(id+"F2.wireOp",EDGE,"E1381"),sQuery(id+"F2.wireOp",EDGE,"E1382"),sQuery(id+"F2.wireOp",EDGE,"E1383"),sQuery(id+"F2.wireOp",EDGE,"E1384"),sQuery(id+"F2.wireOp",EDGE,"E1385"),sQuery(id+"F2.wireOp",EDGE,"E1386"),sQuery(id+"F2.wireOp",EDGE,"E1387"),sQuery(id+"F2.wireOp",EDGE,"E1388"),sQuery(id+"F2.wireOp",EDGE,"E1389"),sQuery(id+"F2.wireOp",EDGE,"E1390"),sQuery(id+"F2.wireOp",EDGE,"E1391"),sQuery(id+"F2.wireOp",EDGE,"E1392"),sQuery(id+"F2.wireOp",EDGE,"E1393"),sQuery(id+"F2.wireOp",EDGE,"E1394"),sQuery(id+"F2.wireOp",EDGE,"E1395"),sQuery(id+"F2.wireOp",EDGE,"E1396"),sQuery(id+"F2.wireOp",EDGE,"E1397"),sQuery(id+"F2.wireOp",EDGE,"E1398"),sQuery(id+"F2.wireOp",EDGE,"E1399"),sQuery(id+"F2.wireOp",EDGE,"E1400"),sQuery(id+"F2.wireOp",EDGE,"E1401"),sQuery(id+"F2.wireOp",EDGE,"E1402"),sQuery(id+"F2.wireOp",EDGE,"E1403"),sQuery(id+"F2.wireOp",EDGE,"E1404"),sQuery(id+"F2.wireOp",EDGE,"E1405"),sQuery(id+"F2.wireOp",EDGE,"E1406"),sQuery(id+"F2.wireOp",EDGE,"E1407"),sQuery(id+"F2.wireOp",EDGE,"E1408"),sQuery(id+"F2.wireOp",EDGE,"E1409"),sQuery(id+"F2.wireOp",EDGE,"E1410"),sQuery(id+"F2.wireOp",EDGE,"E1411"),sQuery(id+"F2.wireOp",EDGE,"E1412"),sQuery(id+"F2.wireOp",EDGE,"E1413"),sQuery(id+"F2.wireOp",EDGE,"E1414"),sQuery(id+"F2.wireOp",EDGE,"E1415"),sQuery(id+"F2.wireOp",EDGE,"E1416"),sQuery(id+"F2.wireOp",EDGE,"E1417"),sQuery(id+"F2.wireOp",EDGE,"E1418"),sQuery(id+"F2.wireOp",EDGE,"E1419"),sQuery(id+"F2.wireOp",EDGE,"E1420"),sQuery(id+"F2.wireOp",EDGE,"E1421"),sQuery(id+"F2.wireOp",EDGE,"E1422"),sQuery(id+"F2.wireOp",EDGE,"E1423"),sQuery(id+"F2.wireOp",EDGE,"E1424"),sQuery(id+"F2.wireOp",EDGE,"E1425"),sQuery(id+"F2.wireOp",EDGE,"E1426"),sQuery(id+"F2.wireOp",EDGE,"E1427"),sQuery(id+"F2.wireOp",EDGE,"E1428"),sQuery(id+"F2.wireOp",EDGE,"E1429"),sQuery(id+"F2.wireOp",EDGE,"E1430"),sQuery(id+"F2.wireOp",EDGE,"E1431"),sQuery(id+"F2.wireOp",EDGE,"E1432"),sQuery(id+"F2.wireOp",EDGE,"E1433"),sQuery(id+"F2.wireOp",EDGE,"E1434"),sQuery(id+"F2.wireOp",EDGE,"E1435"),sQuery(id+"F2.wireOp",EDGE,"E1436"),sQuery(id+"F2.wireOp",EDGE,"E1437"),sQuery(id+"F2.wireOp",EDGE,"E1438"),sQuery(id+"F2.wireOp",EDGE,"E1439"),sQuery(id+"F2.wireOp",EDGE,"E1440"),sQuery(id+"F2.wireOp",EDGE,"E1441"),sQuery(id+"F2.wireOp",EDGE,"E1442"),sQuery(id+"F2.wireOp",EDGE,"E1443"),sQuery(id+"F2.wireOp",EDGE,"E1444"),sQuery(id+"F2.wireOp",EDGE,"E1445"),sQuery(id+"F2.wireOp",EDGE,"E1446"),sQuery(id+"F2.wireOp",EDGE,"E1447"),sQuery(id+"F2.wireOp",EDGE,"E1448"),sQuery(id+"F2.wireOp",EDGE,"E1449"),sQuery(id+"F2.wireOp",EDGE,"E1450"),sQuery(id+"F2.wireOp",EDGE,"E1451"),sQuery(id+"F2.wireOp",EDGE,"E1452"),sQuery(id+"F2.wireOp",EDGE,"E1453"),sQuery(id+"F2.wireOp",EDGE,"E1454"),sQuery(id+"F2.wireOp",EDGE,"E1455"),sQuery(id+"F2.wireOp",EDGE,"E1456"),sQuery(id+"F2.wireOp",EDGE,"E1457"),sQuery(id+"F2.wireOp",EDGE,"E1458"),sQuery(id+"F2.wireOp",EDGE,"E1459"),sQuery(id+"F2.wireOp",EDGE,"E1460"),sQuery(id+"F2.wireOp",EDGE,"E1461"),sQuery(id+"F2.wireOp",EDGE,"E1462"),sQuery(id+"F2.wireOp",EDGE,"E1463"),sQuery(id+"F2.wireOp",EDGE,"E1464"),sQuery(id+"F2.wireOp",EDGE,"E1465"),sQuery(id+"F2.wireOp",EDGE,"E1466"),sQuery(id+"F2.wireOp",EDGE,"E1467"),sQuery(id+"F2.wireOp",EDGE,"E1468"),sQuery(id+"F2.wireOp",EDGE,"E1469"),sQuery(id+"F2.wireOp",EDGE,"E1470"),sQuery(id+"F2.wireOp",EDGE,"E1471"),sQuery(id+"F2.wireOp",EDGE,"E1472"),sQuery(id+"F2.wireOp",EDGE,"E1473"),sQuery(id+"F2.wireOp",EDGE,"E1474")])],"isStart":false});
            extrude(context, id + "F18", {"entities" : qUnion([Q0]), "endBound" : BoundingType.UP_TO_SURFACE, "depth" : 5 * mm, "endBoundEntityFace" : qUnion([Q1]), "offsetDistance" : 25 * mm});
        }
        {
            var Q0;
            Q0=makeQuery(id+"F18.opExtrude","SWEPT_BODY",BODY,{"disambiguationData":[OSD([sQuery(id+"F17.wireOp",EDGE,"E2600"),sQuery(id+"F17.wireOp",EDGE,"E2601"),sQuery(id+"F17.wireOp",EDGE,"E2602"),sQuery(id+"F17.wireOp",EDGE,"E2603"),sQuery(id+"F17.wireOp",EDGE,"E2604"),sQuery(id+"F17.wireOp",EDGE,"E2605"),sQuery(id+"F17.wireOp",EDGE,"E2606"),sQuery(id+"F17.wireOp",EDGE,"E2607"),sQuery(id+"F17.wireOp",EDGE,"E2608"),sQuery(id+"F17.wireOp",EDGE,"E2609"),sQuery(id+"F17.wireOp",EDGE,"E2610"),sQuery(id+"F17.wireOp",EDGE,"E2611"),sQuery(id+"F17.wireOp",EDGE,"E2612"),sQuery(id+"F17.wireOp",EDGE,"E2613"),sQuery(id+"F17.wireOp",EDGE,"E2614"),sQuery(id+"F17.wireOp",EDGE,"E2615"),sQuery(id+"F17.wireOp",EDGE,"E2616"),sQuery(id+"F17.wireOp",EDGE,"E2617"),sQuery(id+"F17.wireOp",EDGE,"E2618"),sQuery(id+"F17.wireOp",EDGE,"E2619"),sQuery(id+"F17.wireOp",EDGE,"E2620"),sQuery(id+"F17.wireOp",EDGE,"E2621"),sQuery(id+"F17.wireOp",EDGE,"E2622"),sQuery(id+"F17.wireOp",EDGE,"E2623"),sQuery(id+"F17.wireOp",EDGE,"E2624"),sQuery(id+"F17.wireOp",EDGE,"E2625"),sQuery(id+"F17.wireOp",EDGE,"E2626"),sQuery(id+"F17.wireOp",EDGE,"E2627"),sQuery(id+"F17.wireOp",EDGE,"E2628"),sQuery(id+"F17.wireOp",EDGE,"E2629"),sQuery(id+"F17.wireOp",EDGE,"E2630"),sQuery(id+"F17.wireOp",EDGE,"E2631"),sQuery(id+"F17.wireOp",EDGE,"E2632"),sQuery(id+"F17.wireOp",EDGE,"E2633"),sQuery(id+"F17.wireOp",EDGE,"E2634"),sQuery(id+"F17.wireOp",EDGE,"E2635"),sQuery(id+"F17.wireOp",EDGE,"E2636"),sQuery(id+"F17.wireOp",EDGE,"E2637"),sQuery(id+"F17.wireOp",EDGE,"E2638"),sQuery(id+"F17.wireOp",EDGE,"E2639"),sQuery(id+"F17.wireOp",EDGE,"E2640"),sQuery(id+"F17.wireOp",EDGE,"E2641"),sQuery(id+"F17.wireOp",EDGE,"E2642"),sQuery(id+"F17.wireOp",EDGE,"E2643"),sQuery(id+"F17.wireOp",EDGE,"E2644"),sQuery(id+"F17.wireOp",EDGE,"E2645"),sQuery(id+"F17.wireOp",EDGE,"E2646"),sQuery(id+"F17.wireOp",EDGE,"E2647"),sQuery(id+"F17.wireOp",EDGE,"E2648"),sQuery(id+"F17.wireOp",EDGE,"E2649"),sQuery(id+"F17.wireOp",EDGE,"E2650"),sQuery(id+"F17.wireOp",EDGE,"E2651"),sQuery(id+"F17.wireOp",EDGE,"E2652"),sQuery(id+"F17.wireOp",EDGE,"E2653"),sQuery(id+"F17.wireOp",EDGE,"E2654"),sQuery(id+"F17.wireOp",EDGE,"E2655"),sQuery(id+"F17.wireOp",EDGE,"E2656"),sQuery(id+"F17.wireOp",EDGE,"E2657"),sQuery(id+"F17.wireOp",EDGE,"E2658"),sQuery(id+"F17.wireOp",EDGE,"E2659"),sQuery(id+"F17.wireOp",EDGE,"E2660"),sQuery(id+"F17.wireOp",EDGE,"E2661"),sQuery(id+"F17.wireOp",EDGE,"E2662"),sQuery(id+"F17.wireOp",EDGE,"E2663"),sQuery(id+"F17.wireOp",EDGE,"E2664"),sQuery(id+"F17.wireOp",EDGE,"E2665"),sQuery(id+"F17.wireOp",EDGE,"E2666"),sQuery(id+"F17.wireOp",EDGE,"E2667"),sQuery(id+"F17.wireOp",EDGE,"E2668"),sQuery(id+"F17.wireOp",EDGE,"E2669"),sQuery(id+"F17.wireOp",EDGE,"E2670"),sQuery(id+"F17.wireOp",EDGE,"E2671"),sQuery(id+"F17.wireOp",EDGE,"E2672"),sQuery(id+"F17.wireOp",EDGE,"E2673"),sQuery(id+"F17.wireOp",EDGE,"E2674"),sQuery(id+"F17.wireOp",EDGE,"E2675"),sQuery(id+"F17.wireOp",EDGE,"E2676"),sQuery(id+"F17.wireOp",EDGE,"E2677"),sQuery(id+"F17.wireOp",EDGE,"E2678"),sQuery(id+"F17.wireOp",EDGE,"E2679"),sQuery(id+"F17.wireOp",EDGE,"E2680"),sQuery(id+"F17.wireOp",EDGE,"E2681"),sQuery(id+"F17.wireOp",EDGE,"E2682"),sQuery(id+"F17.wireOp",EDGE,"E2683"),sQuery(id+"F17.wireOp",EDGE,"E2684"),sQuery(id+"F17.wireOp",EDGE,"E2685"),sQuery(id+"F17.wireOp",EDGE,"E2686"),sQuery(id+"F17.wireOp",EDGE,"E2687"),sQuery(id+"F17.wireOp",EDGE,"E2688"),sQuery(id+"F17.wireOp",EDGE,"E2689"),sQuery(id+"F17.wireOp",EDGE,"E2690"),sQuery(id+"F17.wireOp",EDGE,"E2691"),sQuery(id+"F17.wireOp",EDGE,"E2692"),sQuery(id+"F17.wireOp",EDGE,"E2693"),sQuery(id+"F17.wireOp",EDGE,"E2694"),sQuery(id+"F17.wireOp",EDGE,"E2695"),sQuery(id+"F17.wireOp",EDGE,"E2696"),sQuery(id+"F17.wireOp",EDGE,"E2697"),sQuery(id+"F17.wireOp",EDGE,"E2698"),sQuery(id+"F17.wireOp",EDGE,"E2699"),sQuery(id+"F17.wireOp",EDGE,"E2700"),sQuery(id+"F17.wireOp",EDGE,"E2701"),sQuery(id+"F17.wireOp",EDGE,"E2702"),sQuery(id+"F17.wireOp",EDGE,"E2703"),sQuery(id+"F17.wireOp",EDGE,"E2704"),sQuery(id+"F17.wireOp",EDGE,"E2705"),sQuery(id+"F17.wireOp",EDGE,"E2706"),sQuery(id+"F17.wireOp",EDGE,"E2707"),sQuery(id+"F17.wireOp",EDGE,"E2708"),sQuery(id+"F17.wireOp",EDGE,"E2709"),sQuery(id+"F17.wireOp",EDGE,"E2710"),sQuery(id+"F17.wireOp",EDGE,"E2711"),sQuery(id+"F17.wireOp",EDGE,"E2712"),sQuery(id+"F17.wireOp",EDGE,"E2713"),sQuery(id+"F17.wireOp",EDGE,"E2714"),sQuery(id+"F17.wireOp",EDGE,"E2715"),sQuery(id+"F17.wireOp",EDGE,"E2716"),sQuery(id+"F17.wireOp",EDGE,"E2717"),sQuery(id+"F17.wireOp",EDGE,"E2718"),sQuery(id+"F17.wireOp",EDGE,"E2719"),sQuery(id+"F17.wireOp",EDGE,"E2720"),sQuery(id+"F17.wireOp",EDGE,"E2721"),sQuery(id+"F17.wireOp",EDGE,"E2722"),sQuery(id+"F17.wireOp",EDGE,"E2723"),sQuery(id+"F17.wireOp",EDGE,"E2724"),sQuery(id+"F17.wireOp",EDGE,"E2725"),sQuery(id+"F17.wireOp",EDGE,"E2726"),sQuery(id+"F17.wireOp",EDGE,"E2727"),sQuery(id+"F17.wireOp",EDGE,"E2728"),sQuery(id+"F17.wireOp",EDGE,"E2729"),sQuery(id+"F17.wireOp",EDGE,"E2730"),sQuery(id+"F17.wireOp",EDGE,"E2731"),sQuery(id+"F17.wireOp",EDGE,"E2732"),sQuery(id+"F17.wireOp",EDGE,"E2733"),sQuery(id+"F17.wireOp",EDGE,"E2734"),sQuery(id+"F17.wireOp",EDGE,"E2735"),sQuery(id+"F17.wireOp",EDGE,"E2736"),sQuery(id+"F17.wireOp",EDGE,"E2737"),sQuery(id+"F17.wireOp",EDGE,"E2738"),sQuery(id+"F17.wireOp",EDGE,"E2739"),sQuery(id+"F17.wireOp",EDGE,"E2740"),sQuery(id+"F17.wireOp",EDGE,"E2741"),sQuery(id+"F17.wireOp",EDGE,"E2742"),sQuery(id+"F17.wireOp",EDGE,"E2743"),sQuery(id+"F17.wireOp",EDGE,"E2744"),sQuery(id+"F17.wireOp",EDGE,"E2745"),sQuery(id+"F17.wireOp",EDGE,"E2746"),sQuery(id+"F17.wireOp",EDGE,"E2747"),sQuery(id+"F17.wireOp",EDGE,"E2748"),sQuery(id+"F17.wireOp",EDGE,"E2749"),sQuery(id+"F17.wireOp",EDGE,"E2750"),sQuery(id+"F17.wireOp",EDGE,"E2751"),sQuery(id+"F17.wireOp",EDGE,"E2752"),sQuery(id+"F17.wireOp",EDGE,"E2753"),sQuery(id+"F17.wireOp",EDGE,"E2754"),sQuery(id+"F17.wireOp",EDGE,"E2755"),sQuery(id+"F17.wireOp",EDGE,"E2756"),sQuery(id+"F17.wireOp",EDGE,"E2757"),sQuery(id+"F17.wireOp",EDGE,"E2758"),sQuery(id+"F17.wireOp",EDGE,"E2759"),sQuery(id+"F17.wireOp",EDGE,"E2760"),sQuery(id+"F17.wireOp",EDGE,"E2761"),sQuery(id+"F17.wireOp",EDGE,"E2762"),sQuery(id+"F17.wireOp",EDGE,"E2763"),sQuery(id+"F17.wireOp",EDGE,"E2764"),sQuery(id+"F17.wireOp",EDGE,"E2765"),sQuery(id+"F17.wireOp",EDGE,"E2766"),sQuery(id+"F17.wireOp",EDGE,"E2767"),sQuery(id+"F17.wireOp",EDGE,"E2768"),sQuery(id+"F17.wireOp",EDGE,"E2769"),sQuery(id+"F17.wireOp",EDGE,"E2770"),sQuery(id+"F17.wireOp",EDGE,"E2771"),sQuery(id+"F17.wireOp",EDGE,"E2772"),sQuery(id+"F17.wireOp",EDGE,"E2773"),sQuery(id+"F17.wireOp",EDGE,"E2774"),sQuery(id+"F17.wireOp",EDGE,"E2775"),sQuery(id+"F17.wireOp",EDGE,"E2776"),sQuery(id+"F17.wireOp",EDGE,"E2777"),sQuery(id+"F17.wireOp",EDGE,"E2778"),sQuery(id+"F17.wireOp",EDGE,"E2779"),sQuery(id+"F17.wireOp",EDGE,"E2780"),sQuery(id+"F17.wireOp",EDGE,"E2781"),sQuery(id+"F17.wireOp",EDGE,"E2782"),sQuery(id+"F17.wireOp",EDGE,"E2783"),sQuery(id+"F17.wireOp",EDGE,"E2784"),sQuery(id+"F17.wireOp",EDGE,"E2785"),sQuery(id+"F17.wireOp",EDGE,"E2786"),sQuery(id+"F17.wireOp",EDGE,"E2787"),sQuery(id+"F17.wireOp",EDGE,"E2788"),sQuery(id+"F17.wireOp",EDGE,"E2789"),sQuery(id+"F17.wireOp",EDGE,"E2790"),sQuery(id+"F17.wireOp",EDGE,"E2791"),sQuery(id+"F17.wireOp",EDGE,"E2792"),sQuery(id+"F17.wireOp",EDGE,"E2793"),sQuery(id+"F17.wireOp",EDGE,"E2794"),sQuery(id+"F17.wireOp",EDGE,"E2795"),sQuery(id+"F17.wireOp",EDGE,"E2796"),sQuery(id+"F17.wireOp",EDGE,"E2797"),sQuery(id+"F17.wireOp",EDGE,"E2798"),sQuery(id+"F17.wireOp",EDGE,"E2799"),sQuery(id+"F17.wireOp",EDGE,"E2800"),sQuery(id+"F17.wireOp",EDGE,"E2801"),sQuery(id+"F17.wireOp",EDGE,"E2802"),sQuery(id+"F17.wireOp",EDGE,"E2803"),sQuery(id+"F17.wireOp",EDGE,"E2804"),sQuery(id+"F17.wireOp",EDGE,"E2805"),sQuery(id+"F17.wireOp",EDGE,"E2806"),sQuery(id+"F17.wireOp",EDGE,"E2807"),sQuery(id+"F17.wireOp",EDGE,"E2808"),sQuery(id+"F17.wireOp",EDGE,"E2809"),sQuery(id+"F17.wireOp",EDGE,"E2810"),sQuery(id+"F17.wireOp",EDGE,"E2811"),sQuery(id+"F17.wireOp",EDGE,"E2812"),sQuery(id+"F17.wireOp",EDGE,"E2813"),sQuery(id+"F17.wireOp",EDGE,"E2814"),sQuery(id+"F17.wireOp",EDGE,"E2815"),sQuery(id+"F17.wireOp",EDGE,"E2816"),sQuery(id+"F17.wireOp",EDGE,"E2817"),sQuery(id+"F17.wireOp",EDGE,"E2818"),sQuery(id+"F17.wireOp",EDGE,"E2819"),sQuery(id+"F17.wireOp",EDGE,"E2820"),sQuery(id+"F17.wireOp",EDGE,"E2821"),sQuery(id+"F17.wireOp",EDGE,"E2822"),sQuery(id+"F17.wireOp",EDGE,"E2823"),sQuery(id+"F17.wireOp",EDGE,"E2824"),sQuery(id+"F17.wireOp",EDGE,"E2825"),sQuery(id+"F17.wireOp",EDGE,"E2826"),sQuery(id+"F17.wireOp",EDGE,"E2827"),sQuery(id+"F17.wireOp",EDGE,"E2828"),sQuery(id+"F17.wireOp",EDGE,"E2829"),sQuery(id+"F17.wireOp",EDGE,"E2830"),sQuery(id+"F17.wireOp",EDGE,"E2831"),sQuery(id+"F17.wireOp",EDGE,"E2832"),sQuery(id+"F17.wireOp",EDGE,"E2833"),sQuery(id+"F17.wireOp",EDGE,"E2834"),sQuery(id+"F17.wireOp",EDGE,"E2835"),sQuery(id+"F17.wireOp",EDGE,"E2836"),sQuery(id+"F17.wireOp",EDGE,"E2837"),sQuery(id+"F17.wireOp",EDGE,"E2838"),sQuery(id+"F17.wireOp",EDGE,"E2839"),sQuery(id+"F17.wireOp",EDGE,"E2840"),sQuery(id+"F17.wireOp",EDGE,"E2841"),sQuery(id+"F17.wireOp",EDGE,"E2842"),sQuery(id+"F17.wireOp",EDGE,"E2843"),sQuery(id+"F17.wireOp",EDGE,"E2844"),sQuery(id+"F17.wireOp",EDGE,"E2845"),sQuery(id+"F17.wireOp",EDGE,"E2846"),sQuery(id+"F17.wireOp",EDGE,"E2847"),sQuery(id+"F17.wireOp",EDGE,"E2848"),sQuery(id+"F17.wireOp",EDGE,"E2849"),sQuery(id+"F17.wireOp",EDGE,"E2850"),sQuery(id+"F17.wireOp",EDGE,"E2851"),sQuery(id+"F17.wireOp",EDGE,"E2852"),sQuery(id+"F17.wireOp",EDGE,"E2853"),sQuery(id+"F17.wireOp",EDGE,"E2854"),sQuery(id+"F17.wireOp",EDGE,"E2855"),sQuery(id+"F17.wireOp",EDGE,"E2856"),sQuery(id+"F17.wireOp",EDGE,"E2857"),sQuery(id+"F17.wireOp",EDGE,"E2858"),sQuery(id+"F17.wireOp",EDGE,"E2859"),sQuery(id+"F17.wireOp",EDGE,"E2860"),sQuery(id+"F17.wireOp",EDGE,"E2861"),sQuery(id+"F17.wireOp",EDGE,"E2862"),sQuery(id+"F17.wireOp",EDGE,"E2863"),sQuery(id+"F17.wireOp",EDGE,"E2864"),sQuery(id+"F17.wireOp",EDGE,"E2865"),sQuery(id+"F17.wireOp",EDGE,"E2866"),sQuery(id+"F17.wireOp",EDGE,"E2867"),sQuery(id+"F17.wireOp",EDGE,"E2868"),sQuery(id+"F17.wireOp",EDGE,"E2869"),sQuery(id+"F17.wireOp",EDGE,"E2870"),sQuery(id+"F17.wireOp",EDGE,"E2871"),sQuery(id+"F17.wireOp",EDGE,"E2872"),sQuery(id+"F17.wireOp",EDGE,"E2873"),sQuery(id+"F17.wireOp",EDGE,"E2874"),sQuery(id+"F17.wireOp",EDGE,"E2875"),sQuery(id+"F17.wireOp",EDGE,"E2876"),sQuery(id+"F17.wireOp",EDGE,"E2877"),sQuery(id+"F17.wireOp",EDGE,"E2878"),sQuery(id+"F17.wireOp",EDGE,"E2879"),sQuery(id+"F17.wireOp",EDGE,"E2880"),sQuery(id+"F17.wireOp",EDGE,"E2881"),sQuery(id+"F17.wireOp",EDGE,"E2882"),sQuery(id+"F17.wireOp",EDGE,"E2883"),sQuery(id+"F17.wireOp",EDGE,"E2884"),sQuery(id+"F17.wireOp",EDGE,"E2885"),sQuery(id+"F17.wireOp",EDGE,"E2886"),sQuery(id+"F17.wireOp",EDGE,"E2887"),sQuery(id+"F17.wireOp",EDGE,"E2888"),sQuery(id+"F17.wireOp",EDGE,"E2889"),sQuery(id+"F17.wireOp",EDGE,"E2890"),sQuery(id+"F17.wireOp",EDGE,"E2891"),sQuery(id+"F17.wireOp",EDGE,"E2892"),sQuery(id+"F17.wireOp",EDGE,"E2893"),sQuery(id+"F17.wireOp",EDGE,"E2894"),sQuery(id+"F17.wireOp",EDGE,"E2895"),sQuery(id+"F17.wireOp",EDGE,"E2896"),sQuery(id+"F17.wireOp",EDGE,"E2897"),sQuery(id+"F17.wireOp",EDGE,"E2898"),sQuery(id+"F17.wireOp",EDGE,"E2899"),sQuery(id+"F17.wireOp",EDGE,"E2900"),sQuery(id+"F17.wireOp",EDGE,"E2901"),sQuery(id+"F17.wireOp",EDGE,"E2902"),sQuery(id+"F17.wireOp",EDGE,"E2903"),sQuery(id+"F17.wireOp",EDGE,"E2904"),sQuery(id+"F17.wireOp",EDGE,"E2905"),sQuery(id+"F17.wireOp",EDGE,"E2906"),sQuery(id+"F17.wireOp",EDGE,"E2907"),sQuery(id+"F17.wireOp",EDGE,"E2908"),sQuery(id+"F17.wireOp",EDGE,"E2909"),sQuery(id+"F17.wireOp",EDGE,"E2910"),sQuery(id+"F17.wireOp",EDGE,"E2911"),sQuery(id+"F17.wireOp",EDGE,"E2912"),sQuery(id+"F17.wireOp",EDGE,"E2913"),sQuery(id+"F17.wireOp",EDGE,"E2914"),sQuery(id+"F17.wireOp",EDGE,"E2915"),sQuery(id+"F17.wireOp",EDGE,"E2916"),sQuery(id+"F17.wireOp",EDGE,"E2917"),sQuery(id+"F17.wireOp",EDGE,"E2918"),sQuery(id+"F17.wireOp",EDGE,"E2919"),sQuery(id+"F17.wireOp",EDGE,"E2920"),sQuery(id+"F17.wireOp",EDGE,"E2921"),sQuery(id+"F17.wireOp",EDGE,"E2922"),sQuery(id+"F17.wireOp",EDGE,"E2923"),sQuery(id+"F17.wireOp",EDGE,"E2924"),sQuery(id+"F17.wireOp",EDGE,"E2925"),sQuery(id+"F17.wireOp",EDGE,"E2926"),sQuery(id+"F17.wireOp",EDGE,"E2927"),sQuery(id+"F17.wireOp",EDGE,"E2928"),sQuery(id+"F17.wireOp",EDGE,"E2929"),sQuery(id+"F17.wireOp",EDGE,"E2930"),sQuery(id+"F17.wireOp",EDGE,"E2931"),sQuery(id+"F17.wireOp",EDGE,"E2932"),sQuery(id+"F17.wireOp",EDGE,"E2933"),sQuery(id+"F17.wireOp",EDGE,"E2934"),sQuery(id+"F17.wireOp",EDGE,"E2935"),sQuery(id+"F17.wireOp",EDGE,"E2936"),sQuery(id+"F17.wireOp",EDGE,"E2937"),sQuery(id+"F17.wireOp",EDGE,"E2938"),sQuery(id+"F17.wireOp",EDGE,"E2939"),sQuery(id+"F17.wireOp",EDGE,"E2940"),sQuery(id+"F17.wireOp",EDGE,"E2941"),sQuery(id+"F17.wireOp",EDGE,"E2942"),sQuery(id+"F17.wireOp",EDGE,"E2943"),sQuery(id+"F17.wireOp",EDGE,"E2944"),sQuery(id+"F17.wireOp",EDGE,"E2945"),sQuery(id+"F17.wireOp",EDGE,"E2946"),sQuery(id+"F17.wireOp",EDGE,"E2947"),sQuery(id+"F17.wireOp",EDGE,"E2948"),sQuery(id+"F17.wireOp",EDGE,"E2949"),sQuery(id+"F17.wireOp",EDGE,"E2950"),sQuery(id+"F17.wireOp",EDGE,"E2951"),sQuery(id+"F17.wireOp",EDGE,"E2952"),sQuery(id+"F17.wireOp",EDGE,"E2953"),sQuery(id+"F17.wireOp",EDGE,"E2954"),sQuery(id+"F17.wireOp",EDGE,"E2955"),sQuery(id+"F17.wireOp",EDGE,"E2956"),sQuery(id+"F17.wireOp",EDGE,"E2957"),sQuery(id+"F17.wireOp",EDGE,"E2958"),sQuery(id+"F17.wireOp",EDGE,"E2959"),sQuery(id+"F17.wireOp",EDGE,"E2960"),sQuery(id+"F17.wireOp",EDGE,"E2961"),sQuery(id+"F17.wireOp",EDGE,"E2962"),sQuery(id+"F17.wireOp",EDGE,"E2963"),sQuery(id+"F17.wireOp",EDGE,"E2964"),sQuery(id+"F17.wireOp",EDGE,"E2965"),sQuery(id+"F17.wireOp",EDGE,"E2966"),sQuery(id+"F17.wireOp",EDGE,"E2967"),sQuery(id+"F17.wireOp",EDGE,"E2968"),sQuery(id+"F17.wireOp",EDGE,"E2969"),sQuery(id+"F17.wireOp",EDGE,"E2970"),sQuery(id+"F17.wireOp",EDGE,"E2971"),sQuery(id+"F17.wireOp",EDGE,"E2972"),sQuery(id+"F17.wireOp",EDGE,"E2973"),sQuery(id+"F17.wireOp",EDGE,"E2974"),sQuery(id+"F17.wireOp",EDGE,"E2975"),sQuery(id+"F17.wireOp",EDGE,"E2976"),sQuery(id+"F17.wireOp",EDGE,"E2977"),sQuery(id+"F17.wireOp",EDGE,"E2978"),sQuery(id+"F17.wireOp",EDGE,"E2979"),sQuery(id+"F17.wireOp",EDGE,"E2980"),sQuery(id+"F17.wireOp",EDGE,"E2981"),sQuery(id+"F17.wireOp",EDGE,"E2982"),sQuery(id+"F17.wireOp",EDGE,"E2983"),sQuery(id+"F17.wireOp",EDGE,"E2984"),sQuery(id+"F17.wireOp",EDGE,"E2985"),sQuery(id+"F17.wireOp",EDGE,"E2986"),sQuery(id+"F17.wireOp",EDGE,"E2987"),sQuery(id+"F17.wireOp",EDGE,"E2988"),sQuery(id+"F17.wireOp",EDGE,"E2989"),sQuery(id+"F17.wireOp",EDGE,"E2990"),sQuery(id+"F17.wireOp",EDGE,"E2991"),sQuery(id+"F17.wireOp",EDGE,"E2992"),sQuery(id+"F17.wireOp",EDGE,"E2993"),sQuery(id+"F17.wireOp",EDGE,"E2994"),sQuery(id+"F17.wireOp",EDGE,"E2995"),sQuery(id+"F17.wireOp",EDGE,"E2996"),sQuery(id+"F17.wireOp",EDGE,"E2997"),sQuery(id+"F17.wireOp",EDGE,"E2998"),sQuery(id+"F17.wireOp",EDGE,"E2999"),sQuery(id+"F17.wireOp",EDGE,"E3000"),sQuery(id+"F17.wireOp",EDGE,"E3001"),sQuery(id+"F17.wireOp",EDGE,"E3002"),sQuery(id+"F17.wireOp",EDGE,"E3003"),sQuery(id+"F17.wireOp",EDGE,"E3004"),sQuery(id+"F17.wireOp",EDGE,"E3005"),sQuery(id+"F17.wireOp",EDGE,"E3006"),sQuery(id+"F17.wireOp",EDGE,"E3007"),sQuery(id+"F17.wireOp",EDGE,"E3008"),sQuery(id+"F17.wireOp",EDGE,"E3009"),sQuery(id+"F17.wireOp",EDGE,"E3010"),sQuery(id+"F17.wireOp",EDGE,"E3011"),sQuery(id+"F17.wireOp",EDGE,"E3012"),sQuery(id+"F17.wireOp",EDGE,"E3013"),sQuery(id+"F17.wireOp",EDGE,"E3014"),sQuery(id+"F17.wireOp",EDGE,"E3015"),sQuery(id+"F17.wireOp",EDGE,"E3016"),sQuery(id+"F17.wireOp",EDGE,"E3017"),sQuery(id+"F17.wireOp",EDGE,"E3018"),sQuery(id+"F17.wireOp",EDGE,"E3019"),sQuery(id+"F17.wireOp",EDGE,"E3020"),sQuery(id+"F17.wireOp",EDGE,"E3021"),sQuery(id+"F17.wireOp",EDGE,"E3022"),sQuery(id+"F17.wireOp",EDGE,"E3023"),sQuery(id+"F17.wireOp",EDGE,"E3024"),sQuery(id+"F17.wireOp",EDGE,"E3025"),sQuery(id+"F17.wireOp",EDGE,"E3026"),sQuery(id+"F17.wireOp",EDGE,"E3027"),sQuery(id+"F17.wireOp",EDGE,"E3028"),sQuery(id+"F17.wireOp",EDGE,"E3029"),sQuery(id+"F17.wireOp",EDGE,"E3030"),sQuery(id+"F17.wireOp",EDGE,"E3031"),sQuery(id+"F17.wireOp",EDGE,"E3032"),sQuery(id+"F17.wireOp",EDGE,"E3033"),sQuery(id+"F17.wireOp",EDGE,"E3034"),sQuery(id+"F17.wireOp",EDGE,"E3035"),sQuery(id+"F17.wireOp",EDGE,"E3036"),sQuery(id+"F17.wireOp",EDGE,"E3037"),sQuery(id+"F17.wireOp",EDGE,"E3038"),sQuery(id+"F17.wireOp",EDGE,"E3039"),sQuery(id+"F17.wireOp",EDGE,"E3040"),sQuery(id+"F17.wireOp",EDGE,"E3041"),sQuery(id+"F17.wireOp",EDGE,"E3042"),sQuery(id+"F17.wireOp",EDGE,"E3043"),sQuery(id+"F17.wireOp",EDGE,"E3044"),sQuery(id+"F17.wireOp",EDGE,"E3045"),sQuery(id+"F17.wireOp",EDGE,"E3046"),sQuery(id+"F17.wireOp",EDGE,"E3047"),sQuery(id+"F17.wireOp",EDGE,"E3048"),sQuery(id+"F17.wireOp",EDGE,"E3049"),sQuery(id+"F17.wireOp",EDGE,"E3050"),sQuery(id+"F17.wireOp",EDGE,"E3051"),sQuery(id+"F17.wireOp",EDGE,"E3052"),sQuery(id+"F17.wireOp",EDGE,"E3053"),sQuery(id+"F17.wireOp",EDGE,"E3054"),sQuery(id+"F17.wireOp",EDGE,"E3055"),sQuery(id+"F17.wireOp",EDGE,"E3056"),sQuery(id+"F17.wireOp",EDGE,"E3057"),sQuery(id+"F17.wireOp",EDGE,"E3058"),sQuery(id+"F17.wireOp",EDGE,"E3059"),sQuery(id+"F17.wireOp",EDGE,"E3060"),sQuery(id+"F17.wireOp",EDGE,"E3061"),sQuery(id+"F17.wireOp",EDGE,"E3062"),sQuery(id+"F17.wireOp",EDGE,"E3063"),sQuery(id+"F17.wireOp",EDGE,"E3064"),sQuery(id+"F17.wireOp",EDGE,"E3065"),sQuery(id+"F17.wireOp",EDGE,"E3066"),sQuery(id+"F17.wireOp",EDGE,"E3067"),sQuery(id+"F17.wireOp",EDGE,"E3068"),sQuery(id+"F17.wireOp",EDGE,"E3069"),sQuery(id+"F17.wireOp",EDGE,"E3070"),sQuery(id+"F17.wireOp",EDGE,"E3071"),sQuery(id+"F17.wireOp",EDGE,"E3072"),sQuery(id+"F17.wireOp",EDGE,"E3073"),sQuery(id+"F17.wireOp",EDGE,"E3074"),sQuery(id+"F17.wireOp",EDGE,"E3075"),sQuery(id+"F17.wireOp",EDGE,"E3076"),sQuery(id+"F17.wireOp",EDGE,"E3077"),sQuery(id+"F17.wireOp",EDGE,"E3078"),sQuery(id+"F17.wireOp",EDGE,"E3079"),sQuery(id+"F17.wireOp",EDGE,"E3080"),sQuery(id+"F17.wireOp",EDGE,"E3081"),sQuery(id+"F17.wireOp",EDGE,"E3082"),sQuery(id+"F17.wireOp",EDGE,"E3083"),sQuery(id+"F17.wireOp",EDGE,"E3084"),sQuery(id+"F17.wireOp",EDGE,"E3085"),sQuery(id+"F17.wireOp",EDGE,"E3086"),sQuery(id+"F17.wireOp",EDGE,"E3087"),sQuery(id+"F17.wireOp",EDGE,"E3088"),sQuery(id+"F17.wireOp",EDGE,"E3089"),sQuery(id+"F17.wireOp",EDGE,"E3090"),sQuery(id+"F17.wireOp",EDGE,"E3091"),sQuery(id+"F17.wireOp",EDGE,"E3092"),sQuery(id+"F17.wireOp",EDGE,"E3093"),sQuery(id+"F17.wireOp",EDGE,"E3094"),sQuery(id+"F17.wireOp",EDGE,"E3095"),sQuery(id+"F17.wireOp",EDGE,"E3096"),sQuery(id+"F17.wireOp",EDGE,"E3097"),sQuery(id+"F17.wireOp",EDGE,"E3098"),sQuery(id+"F17.wireOp",EDGE,"E3099"),sQuery(id+"F17.wireOp",EDGE,"E3100"),sQuery(id+"F17.wireOp",EDGE,"E3101"),sQuery(id+"F17.wireOp",EDGE,"E3102"),sQuery(id+"F17.wireOp",EDGE,"E3103"),sQuery(id+"F17.wireOp",EDGE,"E3104"),sQuery(id+"F17.wireOp",EDGE,"E3105"),sQuery(id+"F17.wireOp",EDGE,"E3106"),sQuery(id+"F17.wireOp",EDGE,"E3107"),sQuery(id+"F17.wireOp",EDGE,"E3108"),sQuery(id+"F17.wireOp",EDGE,"E3109"),sQuery(id+"F17.wireOp",EDGE,"E3110"),sQuery(id+"F17.wireOp",EDGE,"E3111"),sQuery(id+"F17.wireOp",EDGE,"E3112"),sQuery(id+"F17.wireOp",EDGE,"E3113"),sQuery(id+"F17.wireOp",EDGE,"E3114"),sQuery(id+"F17.wireOp",EDGE,"E3115"),sQuery(id+"F17.wireOp",EDGE,"E3116"),sQuery(id+"F17.wireOp",EDGE,"E3117"),sQuery(id+"F17.wireOp",EDGE,"E3118"),sQuery(id+"F17.wireOp",EDGE,"E3119"),sQuery(id+"F17.wireOp",EDGE,"E3120"),sQuery(id+"F17.wireOp",EDGE,"E3121"),sQuery(id+"F17.wireOp",EDGE,"E3122"),sQuery(id+"F17.wireOp",EDGE,"E3123"),sQuery(id+"F17.wireOp",EDGE,"E3124"),sQuery(id+"F17.wireOp",EDGE,"E3125"),sQuery(id+"F17.wireOp",EDGE,"E3126"),sQuery(id+"F17.wireOp",EDGE,"E3127"),sQuery(id+"F17.wireOp",EDGE,"E3128"),sQuery(id+"F17.wireOp",EDGE,"E3129"),sQuery(id+"F17.wireOp",EDGE,"E3130"),sQuery(id+"F17.wireOp",EDGE,"E3131"),sQuery(id+"F17.wireOp",EDGE,"E3132"),sQuery(id+"F17.wireOp",EDGE,"E3133"),sQuery(id+"F17.wireOp",EDGE,"E3134"),sQuery(id+"F17.wireOp",EDGE,"E3135"),sQuery(id+"F17.wireOp",EDGE,"E3136"),sQuery(id+"F17.wireOp",EDGE,"E3137"),sQuery(id+"F17.wireOp",EDGE,"E3138"),sQuery(id+"F17.wireOp",EDGE,"E3139"),sQuery(id+"F17.wireOp",EDGE,"E3140"),sQuery(id+"F17.wireOp",EDGE,"E3141"),sQuery(id+"F17.wireOp",EDGE,"E3142"),sQuery(id+"F17.wireOp",EDGE,"E3143"),sQuery(id+"F17.wireOp",EDGE,"E3144"),sQuery(id+"F17.wireOp",EDGE,"E3145"),sQuery(id+"F17.wireOp",EDGE,"E3146"),sQuery(id+"F17.wireOp",EDGE,"E3147"),sQuery(id+"F17.wireOp",EDGE,"E3148"),sQuery(id+"F17.wireOp",EDGE,"E3149"),sQuery(id+"F17.wireOp",EDGE,"E3150"),sQuery(id+"F17.wireOp",EDGE,"E3151"),sQuery(id+"F17.wireOp",EDGE,"E3152"),sQuery(id+"F17.wireOp",EDGE,"E3153"),sQuery(id+"F17.wireOp",EDGE,"E3154"),sQuery(id+"F17.wireOp",EDGE,"E3155"),sQuery(id+"F17.wireOp",EDGE,"E3156"),sQuery(id+"F17.wireOp",EDGE,"E3157"),sQuery(id+"F17.wireOp",EDGE,"E3158"),sQuery(id+"F17.wireOp",EDGE,"E3159"),sQuery(id+"F17.wireOp",EDGE,"E3160"),sQuery(id+"F17.wireOp",EDGE,"E3161"),sQuery(id+"F17.wireOp",EDGE,"E3162"),sQuery(id+"F17.wireOp",EDGE,"E3163"),sQuery(id+"F17.wireOp",EDGE,"E3164"),sQuery(id+"F17.wireOp",EDGE,"E3165"),sQuery(id+"F17.wireOp",EDGE,"E3166"),sQuery(id+"F17.wireOp",EDGE,"E3167"),sQuery(id+"F17.wireOp",EDGE,"E3168"),sQuery(id+"F17.wireOp",EDGE,"E3169"),sQuery(id+"F17.wireOp",EDGE,"E3170"),sQuery(id+"F17.wireOp",EDGE,"E3171"),sQuery(id+"F17.wireOp",EDGE,"E3172"),sQuery(id+"F17.wireOp",EDGE,"E3173"),sQuery(id+"F17.wireOp",EDGE,"E3174"),sQuery(id+"F17.wireOp",EDGE,"E3175"),sQuery(id+"F17.wireOp",EDGE,"E3176"),sQuery(id+"F17.wireOp",EDGE,"E3177"),sQuery(id+"F17.wireOp",EDGE,"E3178"),sQuery(id+"F17.wireOp",EDGE,"E3179"),sQuery(id+"F17.wireOp",EDGE,"E3180"),sQuery(id+"F17.wireOp",EDGE,"E3181"),sQuery(id+"F17.wireOp",EDGE,"E3182"),sQuery(id+"F17.wireOp",EDGE,"E3183"),sQuery(id+"F17.wireOp",EDGE,"E3184"),sQuery(id+"F17.wireOp",EDGE,"E3185"),sQuery(id+"F17.wireOp",EDGE,"E3186"),sQuery(id+"F17.wireOp",EDGE,"E3187"),sQuery(id+"F17.wireOp",EDGE,"E3188"),sQuery(id+"F17.wireOp",EDGE,"E3189"),sQuery(id+"F17.wireOp",EDGE,"E3190"),sQuery(id+"F17.wireOp",EDGE,"E3191"),sQuery(id+"F17.wireOp",EDGE,"E3192"),sQuery(id+"F17.wireOp",EDGE,"E3193"),sQuery(id+"F17.wireOp",EDGE,"E3194"),sQuery(id+"F17.wireOp",EDGE,"E3195"),sQuery(id+"F17.wireOp",EDGE,"E3196"),sQuery(id+"F17.wireOp",EDGE,"E3197"),sQuery(id+"F17.wireOp",EDGE,"E3198"),sQuery(id+"F17.wireOp",EDGE,"E3199"),sQuery(id+"F17.wireOp",EDGE,"E3200"),sQuery(id+"F17.wireOp",EDGE,"E3201"),sQuery(id+"F17.wireOp",EDGE,"E3202"),sQuery(id+"F17.wireOp",EDGE,"E3203"),sQuery(id+"F17.wireOp",EDGE,"E3204"),sQuery(id+"F17.wireOp",EDGE,"E3205"),sQuery(id+"F17.wireOp",EDGE,"E3206"),sQuery(id+"F17.wireOp",EDGE,"E3207"),sQuery(id+"F17.wireOp",EDGE,"E3208"),sQuery(id+"F17.wireOp",EDGE,"E3209"),sQuery(id+"F17.wireOp",EDGE,"E3210"),sQuery(id+"F17.wireOp",EDGE,"E3211"),sQuery(id+"F17.wireOp",EDGE,"E3212"),sQuery(id+"F17.wireOp",EDGE,"E3213"),sQuery(id+"F17.wireOp",EDGE,"E3214"),sQuery(id+"F17.wireOp",EDGE,"E3215"),sQuery(id+"F17.wireOp",EDGE,"E3216"),sQuery(id+"F17.wireOp",EDGE,"E3217"),sQuery(id+"F17.wireOp",EDGE,"E3218"),sQuery(id+"F17.wireOp",EDGE,"E3219"),sQuery(id+"F17.wireOp",EDGE,"E3220"),sQuery(id+"F17.wireOp",EDGE,"E3221"),sQuery(id+"F17.wireOp",EDGE,"E3222"),sQuery(id+"F17.wireOp",EDGE,"E3223"),sQuery(id+"F17.wireOp",EDGE,"E3224"),sQuery(id+"F17.wireOp",EDGE,"E3225"),sQuery(id+"F17.wireOp",EDGE,"E3226"),sQuery(id+"F17.wireOp",EDGE,"E3227"),sQuery(id+"F17.wireOp",EDGE,"E3228"),sQuery(id+"F17.wireOp",EDGE,"E3229"),sQuery(id+"F17.wireOp",EDGE,"E3230"),sQuery(id+"F17.wireOp",EDGE,"E3231"),sQuery(id+"F17.wireOp",EDGE,"E3232"),sQuery(id+"F17.wireOp",EDGE,"E3233"),sQuery(id+"F17.wireOp",EDGE,"E3234"),sQuery(id+"F17.wireOp",EDGE,"E3235"),sQuery(id+"F17.wireOp",EDGE,"E3236"),sQuery(id+"F17.wireOp",EDGE,"E3237"),sQuery(id+"F17.wireOp",EDGE,"E3238"),sQuery(id+"F17.wireOp",EDGE,"E3239"),sQuery(id+"F17.wireOp",EDGE,"E3240"),sQuery(id+"F17.wireOp",EDGE,"E3241"),sQuery(id+"F17.wireOp",EDGE,"E3242"),sQuery(id+"F17.wireOp",EDGE,"E3243"),sQuery(id+"F17.wireOp",EDGE,"E3244"),sQuery(id+"F17.wireOp",EDGE,"E3245"),sQuery(id+"F17.wireOp",EDGE,"E3246"),sQuery(id+"F17.wireOp",EDGE,"E3247"),sQuery(id+"F17.wireOp",EDGE,"E3248"),sQuery(id+"F17.wireOp",EDGE,"E3249"),sQuery(id+"F17.wireOp",EDGE,"E3250"),sQuery(id+"F17.wireOp",EDGE,"E3251"),sQuery(id+"F17.wireOp",EDGE,"E3252"),sQuery(id+"F17.wireOp",EDGE,"E3253"),sQuery(id+"F17.wireOp",EDGE,"E3254"),sQuery(id+"F17.wireOp",EDGE,"E3255"),sQuery(id+"F17.wireOp",EDGE,"E3256"),sQuery(id+"F17.wireOp",EDGE,"E3257"),sQuery(id+"F17.wireOp",EDGE,"E3258"),sQuery(id+"F17.wireOp",EDGE,"E3259"),sQuery(id+"F17.wireOp",EDGE,"E3260"),sQuery(id+"F17.wireOp",EDGE,"E3261"),sQuery(id+"F17.wireOp",EDGE,"E3262"),sQuery(id+"F17.wireOp",EDGE,"E3263"),sQuery(id+"F17.wireOp",EDGE,"E3264"),sQuery(id+"F17.wireOp",EDGE,"E3265"),sQuery(id+"F17.wireOp",EDGE,"E3266"),sQuery(id+"F17.wireOp",EDGE,"E3267"),sQuery(id+"F17.wireOp",EDGE,"E3268"),sQuery(id+"F17.wireOp",EDGE,"E3269"),sQuery(id+"F17.wireOp",EDGE,"E3270"),sQuery(id+"F17.wireOp",EDGE,"E3271"),sQuery(id+"F17.wireOp",EDGE,"E3272"),sQuery(id+"F17.wireOp",EDGE,"E3273"),sQuery(id+"F17.wireOp",EDGE,"E3274"),sQuery(id+"F17.wireOp",EDGE,"E3275"),sQuery(id+"F17.wireOp",EDGE,"E3276"),sQuery(id+"F17.wireOp",EDGE,"E3277"),sQuery(id+"F17.wireOp",EDGE,"E3278"),sQuery(id+"F17.wireOp",EDGE,"E3279"),sQuery(id+"F17.wireOp",EDGE,"E3280"),sQuery(id+"F17.wireOp",EDGE,"E3281"),sQuery(id+"F17.wireOp",EDGE,"E3282"),sQuery(id+"F17.wireOp",EDGE,"E3283"),sQuery(id+"F17.wireOp",EDGE,"E3284"),sQuery(id+"F17.wireOp",EDGE,"E3285"),sQuery(id+"F17.wireOp",EDGE,"E3286"),sQuery(id+"F17.wireOp",EDGE,"E3287"),sQuery(id+"F17.wireOp",EDGE,"E3288"),sQuery(id+"F17.wireOp",EDGE,"E3289"),sQuery(id+"F17.wireOp",EDGE,"E3290"),sQuery(id+"F17.wireOp",EDGE,"E3291"),sQuery(id+"F17.wireOp",EDGE,"E3292"),sQuery(id+"F17.wireOp",EDGE,"E3293"),sQuery(id+"F17.wireOp",EDGE,"E3294"),sQuery(id+"F17.wireOp",EDGE,"E3295"),sQuery(id+"F17.wireOp",EDGE,"E3296"),sQuery(id+"F17.wireOp",EDGE,"E3297"),sQuery(id+"F17.wireOp",EDGE,"E3298"),sQuery(id+"F17.wireOp",EDGE,"E3299"),sQuery(id+"F17.wireOp",EDGE,"E3300"),sQuery(id+"F17.wireOp",EDGE,"E3301"),sQuery(id+"F17.wireOp",EDGE,"E3302"),sQuery(id+"F17.wireOp",EDGE,"E3303"),sQuery(id+"F17.wireOp",EDGE,"E3304"),sQuery(id+"F17.wireOp",EDGE,"E3305"),sQuery(id+"F17.wireOp",EDGE,"E3306"),sQuery(id+"F17.wireOp",EDGE,"E3307"),sQuery(id+"F17.wireOp",EDGE,"E3308"),sQuery(id+"F17.wireOp",EDGE,"E3309"),sQuery(id+"F17.wireOp",EDGE,"E3310"),sQuery(id+"F17.wireOp",EDGE,"E3311"),sQuery(id+"F17.wireOp",EDGE,"E3312"),sQuery(id+"F17.wireOp",EDGE,"E3313"),sQuery(id+"F17.wireOp",EDGE,"E3314"),sQuery(id+"F17.wireOp",EDGE,"E3315"),sQuery(id+"F17.wireOp",EDGE,"E3316"),sQuery(id+"F17.wireOp",EDGE,"E3317"),sQuery(id+"F17.wireOp",EDGE,"E3318"),sQuery(id+"F17.wireOp",EDGE,"E3319"),sQuery(id+"F17.wireOp",EDGE,"E3320"),sQuery(id+"F17.wireOp",EDGE,"E3321"),sQuery(id+"F17.wireOp",EDGE,"E3322"),sQuery(id+"F17.wireOp",EDGE,"E3323"),sQuery(id+"F17.wireOp",EDGE,"E3324"),sQuery(id+"F17.wireOp",EDGE,"E3325"),sQuery(id+"F17.wireOp",EDGE,"E3326"),sQuery(id+"F17.wireOp",EDGE,"E3327"),sQuery(id+"F17.wireOp",EDGE,"E3328"),sQuery(id+"F17.wireOp",EDGE,"E3329"),sQuery(id+"F17.wireOp",EDGE,"E3330"),sQuery(id+"F17.wireOp",EDGE,"E3331"),sQuery(id+"F17.wireOp",EDGE,"E3332"),sQuery(id+"F17.wireOp",EDGE,"E3333"),sQuery(id+"F17.wireOp",EDGE,"E3334"),sQuery(id+"F17.wireOp",EDGE,"E3335"),sQuery(id+"F17.wireOp",EDGE,"E3336"),sQuery(id+"F17.wireOp",EDGE,"E3337"),sQuery(id+"F17.wireOp",EDGE,"E3338"),sQuery(id+"F17.wireOp",EDGE,"E3339"),sQuery(id+"F17.wireOp",EDGE,"E3340"),sQuery(id+"F17.wireOp",EDGE,"E3341"),sQuery(id+"F17.wireOp",EDGE,"E3342"),sQuery(id+"F17.wireOp",EDGE,"E3343"),sQuery(id+"F17.wireOp",EDGE,"E3344"),sQuery(id+"F17.wireOp",EDGE,"E3345"),sQuery(id+"F17.wireOp",EDGE,"E3346"),sQuery(id+"F17.wireOp",EDGE,"E3347"),sQuery(id+"F17.wireOp",EDGE,"E3348"),sQuery(id+"F17.wireOp",EDGE,"E3349"),sQuery(id+"F17.wireOp",EDGE,"E3350"),sQuery(id+"F17.wireOp",EDGE,"E3351"),sQuery(id+"F17.wireOp",EDGE,"E3352"),sQuery(id+"F17.wireOp",EDGE,"E3353"),sQuery(id+"F17.wireOp",EDGE,"E3354"),sQuery(id+"F17.wireOp",EDGE,"E3355"),sQuery(id+"F17.wireOp",EDGE,"E3356"),sQuery(id+"F17.wireOp",EDGE,"E3357"),sQuery(id+"F17.wireOp",EDGE,"E3358"),sQuery(id+"F17.wireOp",EDGE,"E3359"),sQuery(id+"F17.wireOp",EDGE,"E3360"),sQuery(id+"F17.wireOp",EDGE,"E3361"),sQuery(id+"F17.wireOp",EDGE,"E3362"),sQuery(id+"F17.wireOp",EDGE,"E3363"),sQuery(id+"F17.wireOp",EDGE,"E3364"),sQuery(id+"F17.wireOp",EDGE,"E3365"),sQuery(id+"F17.wireOp",EDGE,"E3366"),sQuery(id+"F17.wireOp",EDGE,"E3367"),sQuery(id+"F17.wireOp",EDGE,"E3368"),sQuery(id+"F17.wireOp",EDGE,"E3369"),sQuery(id+"F17.wireOp",EDGE,"E3370"),sQuery(id+"F17.wireOp",EDGE,"E3371"),sQuery(id+"F17.wireOp",EDGE,"E3372"),sQuery(id+"F17.wireOp",EDGE,"E3373"),sQuery(id+"F17.wireOp",EDGE,"E3374"),sQuery(id+"F17.wireOp",EDGE,"E3375"),sQuery(id+"F17.wireOp",EDGE,"E3376"),sQuery(id+"F17.wireOp",EDGE,"E3377"),sQuery(id+"F17.wireOp",EDGE,"E3378"),sQuery(id+"F17.wireOp",EDGE,"E3379"),sQuery(id+"F17.wireOp",EDGE,"E3380"),sQuery(id+"F17.wireOp",EDGE,"E3381"),sQuery(id+"F17.wireOp",EDGE,"E3382"),sQuery(id+"F17.wireOp",EDGE,"E3383"),sQuery(id+"F17.wireOp",EDGE,"E3384"),sQuery(id+"F17.wireOp",EDGE,"E3385"),sQuery(id+"F17.wireOp",EDGE,"E3386"),sQuery(id+"F17.wireOp",EDGE,"E3387"),sQuery(id+"F17.wireOp",EDGE,"E3388"),sQuery(id+"F17.wireOp",EDGE,"E3389"),sQuery(id+"F17.wireOp",EDGE,"E3390"),sQuery(id+"F17.wireOp",EDGE,"E3391"),sQuery(id+"F17.wireOp",EDGE,"E3392"),sQuery(id+"F17.wireOp",EDGE,"E3393"),sQuery(id+"F17.wireOp",EDGE,"E3394"),sQuery(id+"F17.wireOp",EDGE,"E3395"),sQuery(id+"F17.wireOp",EDGE,"E3396"),sQuery(id+"F17.wireOp",EDGE,"E3397"),sQuery(id+"F17.wireOp",EDGE,"E3398"),sQuery(id+"F17.wireOp",EDGE,"E3399"),sQuery(id+"F17.wireOp",EDGE,"E3400"),sQuery(id+"F17.wireOp",EDGE,"E3401"),sQuery(id+"F17.wireOp",EDGE,"E3402"),sQuery(id+"F17.wireOp",EDGE,"E3403"),sQuery(id+"F17.wireOp",EDGE,"E3404"),sQuery(id+"F17.wireOp",EDGE,"E3405"),sQuery(id+"F17.wireOp",EDGE,"E3406"),sQuery(id+"F17.wireOp",EDGE,"E3407"),sQuery(id+"F17.wireOp",EDGE,"E3408"),sQuery(id+"F17.wireOp",EDGE,"E3409"),sQuery(id+"F17.wireOp",EDGE,"E3410"),sQuery(id+"F17.wireOp",EDGE,"E3411"),sQuery(id+"F17.wireOp",EDGE,"E3412"),sQuery(id+"F17.wireOp",EDGE,"E3413"),sQuery(id+"F17.wireOp",EDGE,"E3414"),sQuery(id+"F17.wireOp",EDGE,"E3415"),sQuery(id+"F17.wireOp",EDGE,"E3416"),sQuery(id+"F17.wireOp",EDGE,"E3417"),sQuery(id+"F17.wireOp",EDGE,"E3418"),sQuery(id+"F17.wireOp",EDGE,"E3419"),sQuery(id+"F17.wireOp",EDGE,"E3420"),sQuery(id+"F17.wireOp",EDGE,"E3421"),sQuery(id+"F17.wireOp",EDGE,"E3422"),sQuery(id+"F17.wireOp",EDGE,"E3423"),sQuery(id+"F17.wireOp",EDGE,"E3424"),sQuery(id+"F17.wireOp",EDGE,"E3425"),sQuery(id+"F17.wireOp",EDGE,"E3426"),sQuery(id+"F17.wireOp",EDGE,"E3427"),sQuery(id+"F17.wireOp",EDGE,"E3428"),sQuery(id+"F17.wireOp",EDGE,"E3429"),sQuery(id+"F17.wireOp",EDGE,"E3430"),sQuery(id+"F17.wireOp",EDGE,"E3431"),sQuery(id+"F17.wireOp",EDGE,"E3432"),sQuery(id+"F17.wireOp",EDGE,"E3433"),sQuery(id+"F17.wireOp",EDGE,"E3434"),sQuery(id+"F17.wireOp",EDGE,"E3435"),sQuery(id+"F17.wireOp",EDGE,"E3436"),sQuery(id+"F17.wireOp",EDGE,"E3437"),sQuery(id+"F17.wireOp",EDGE,"E3438"),sQuery(id+"F17.wireOp",EDGE,"E3439"),sQuery(id+"F17.wireOp",EDGE,"E3440"),sQuery(id+"F17.wireOp",EDGE,"E3441"),sQuery(id+"F17.wireOp",EDGE,"E3442"),sQuery(id+"F17.wireOp",EDGE,"E3443"),sQuery(id+"F17.wireOp",EDGE,"E3444"),sQuery(id+"F17.wireOp",EDGE,"E3445"),sQuery(id+"F17.wireOp",EDGE,"E3446"),sQuery(id+"F17.wireOp",EDGE,"E3447"),sQuery(id+"F17.wireOp",EDGE,"E3448"),sQuery(id+"F17.wireOp",EDGE,"E3449"),sQuery(id+"F17.wireOp",EDGE,"E3450"),sQuery(id+"F17.wireOp",EDGE,"E3451"),sQuery(id+"F17.wireOp",EDGE,"E3452"),sQuery(id+"F17.wireOp",EDGE,"E3453"),sQuery(id+"F17.wireOp",EDGE,"E3454"),sQuery(id+"F17.wireOp",EDGE,"E3455"),sQuery(id+"F17.wireOp",EDGE,"E3456"),sQuery(id+"F17.wireOp",EDGE,"E3457"),sQuery(id+"F17.wireOp",EDGE,"E3458"),sQuery(id+"F17.wireOp",EDGE,"E3459"),sQuery(id+"F17.wireOp",EDGE,"E3460"),sQuery(id+"F17.wireOp",EDGE,"E3461"),sQuery(id+"F17.wireOp",EDGE,"E3462"),sQuery(id+"F17.wireOp",EDGE,"E3463"),sQuery(id+"F17.wireOp",EDGE,"E3464"),sQuery(id+"F17.wireOp",EDGE,"E3465"),sQuery(id+"F17.wireOp",EDGE,"E3466"),sQuery(id+"F17.wireOp",EDGE,"E3467"),sQuery(id+"F17.wireOp",EDGE,"E3468"),sQuery(id+"F17.wireOp",EDGE,"E3469"),sQuery(id+"F17.wireOp",EDGE,"E3470"),sQuery(id+"F17.wireOp",EDGE,"E3471"),sQuery(id+"F17.wireOp",EDGE,"E3472"),sQuery(id+"F17.wireOp",EDGE,"E3473"),sQuery(id+"F17.wireOp",EDGE,"E3474"),sQuery(id+"F17.wireOp",EDGE,"E3475"),sQuery(id+"F17.wireOp",EDGE,"E3476"),sQuery(id+"F17.wireOp",EDGE,"E3477"),sQuery(id+"F17.wireOp",EDGE,"E3478"),sQuery(id+"F17.wireOp",EDGE,"E3479"),sQuery(id+"F17.wireOp",EDGE,"E3480"),sQuery(id+"F17.wireOp",EDGE,"E3481"),sQuery(id+"F17.wireOp",EDGE,"E3482"),sQuery(id+"F17.wireOp",EDGE,"E3483"),sQuery(id+"F17.wireOp",EDGE,"E3484"),sQuery(id+"F17.wireOp",EDGE,"E3485"),sQuery(id+"F17.wireOp",EDGE,"E3486"),sQuery(id+"F17.wireOp",EDGE,"E3487"),sQuery(id+"F17.wireOp",EDGE,"E3488"),sQuery(id+"F17.wireOp",EDGE,"E3489"),sQuery(id+"F17.wireOp",EDGE,"E3490"),sQuery(id+"F17.wireOp",EDGE,"E3491"),sQuery(id+"F17.wireOp",EDGE,"E3492"),sQuery(id+"F17.wireOp",EDGE,"E3493"),sQuery(id+"F17.wireOp",EDGE,"E3494"),sQuery(id+"F17.wireOp",EDGE,"E3495"),sQuery(id+"F17.wireOp",EDGE,"E3496"),sQuery(id+"F17.wireOp",EDGE,"E3497"),sQuery(id+"F17.wireOp",EDGE,"E3498"),sQuery(id+"F17.wireOp",EDGE,"E3499"),sQuery(id+"F17.wireOp",EDGE,"E3500"),sQuery(id+"F17.wireOp",EDGE,"E3501"),sQuery(id+"F17.wireOp",EDGE,"E3502"),sQuery(id+"F17.wireOp",EDGE,"E3503"),sQuery(id+"F17.wireOp",EDGE,"E3504"),sQuery(id+"F17.wireOp",EDGE,"E3505"),sQuery(id+"F17.wireOp",EDGE,"E3506"),sQuery(id+"F17.wireOp",EDGE,"E3507"),sQuery(id+"F17.wireOp",EDGE,"E3508"),sQuery(id+"F17.wireOp",EDGE,"E3509"),sQuery(id+"F17.wireOp",EDGE,"E3510"),sQuery(id+"F17.wireOp",EDGE,"E3511"),sQuery(id+"F17.wireOp",EDGE,"E3512"),sQuery(id+"F17.wireOp",EDGE,"E3513"),sQuery(id+"F17.wireOp",EDGE,"E3514"),sQuery(id+"F17.wireOp",EDGE,"E3515"),sQuery(id+"F17.wireOp",EDGE,"E3516"),sQuery(id+"F17.wireOp",EDGE,"E3517"),sQuery(id+"F17.wireOp",EDGE,"E3518"),sQuery(id+"F17.wireOp",EDGE,"E3519"),sQuery(id+"F17.wireOp",EDGE,"E3520"),sQuery(id+"F17.wireOp",EDGE,"E3521"),sQuery(id+"F17.wireOp",EDGE,"E3522"),sQuery(id+"F17.wireOp",EDGE,"E3523"),sQuery(id+"F17.wireOp",EDGE,"E3524"),sQuery(id+"F17.wireOp",EDGE,"E3525"),sQuery(id+"F17.wireOp",EDGE,"E3526"),sQuery(id+"F17.wireOp",EDGE,"E3527"),sQuery(id+"F17.wireOp",EDGE,"E3528"),sQuery(id+"F17.wireOp",EDGE,"E3529"),sQuery(id+"F17.wireOp",EDGE,"E3530"),sQuery(id+"F17.wireOp",EDGE,"E3531"),sQuery(id+"F17.wireOp",EDGE,"E3532"),sQuery(id+"F17.wireOp",EDGE,"E3533"),sQuery(id+"F17.wireOp",EDGE,"E3534"),sQuery(id+"F17.wireOp",EDGE,"E3535"),sQuery(id+"F17.wireOp",EDGE,"E3536"),sQuery(id+"F17.wireOp",EDGE,"E3537"),sQuery(id+"F17.wireOp",EDGE,"E3538"),sQuery(id+"F17.wireOp",EDGE,"E3539"),sQuery(id+"F17.wireOp",EDGE,"E3540"),sQuery(id+"F17.wireOp",EDGE,"E3541"),sQuery(id+"F17.wireOp",EDGE,"E3542"),sQuery(id+"F17.wireOp",EDGE,"E3543"),sQuery(id+"F17.wireOp",EDGE,"E3544"),sQuery(id+"F17.wireOp",EDGE,"E3545"),sQuery(id+"F17.wireOp",EDGE,"E3546"),sQuery(id+"F17.wireOp",EDGE,"E3547"),sQuery(id+"F17.wireOp",EDGE,"E3548"),sQuery(id+"F17.wireOp",EDGE,"E3549"),sQuery(id+"F17.wireOp",EDGE,"E3550"),sQuery(id+"F17.wireOp",EDGE,"E3551"),sQuery(id+"F17.wireOp",EDGE,"E3552"),sQuery(id+"F17.wireOp",EDGE,"E3553"),sQuery(id+"F17.wireOp",EDGE,"E3554"),sQuery(id+"F17.wireOp",EDGE,"E3555"),sQuery(id+"F17.wireOp",EDGE,"E3556"),sQuery(id+"F17.wireOp",EDGE,"E3557"),sQuery(id+"F17.wireOp",EDGE,"E3558"),sQuery(id+"F17.wireOp",EDGE,"E3559"),sQuery(id+"F17.wireOp",EDGE,"E3560"),sQuery(id+"F17.wireOp",EDGE,"E3561"),sQuery(id+"F17.wireOp",EDGE,"E3562"),sQuery(id+"F17.wireOp",EDGE,"E3563"),sQuery(id+"F17.wireOp",EDGE,"E3564"),sQuery(id+"F17.wireOp",EDGE,"E3565"),sQuery(id+"F17.wireOp",EDGE,"E3566"),sQuery(id+"F17.wireOp",EDGE,"E3567"),sQuery(id+"F17.wireOp",EDGE,"E3568"),sQuery(id+"F17.wireOp",EDGE,"E3569"),sQuery(id+"F17.wireOp",EDGE,"E3570"),sQuery(id+"F17.wireOp",EDGE,"E3571"),sQuery(id+"F17.wireOp",EDGE,"E3572"),sQuery(id+"F17.wireOp",EDGE,"E3573"),sQuery(id+"F17.wireOp",EDGE,"E3574"),sQuery(id+"F17.wireOp",EDGE,"E3575"),sQuery(id+"F17.wireOp",EDGE,"E3576"),sQuery(id+"F17.wireOp",EDGE,"E3577"),sQuery(id+"F17.wireOp",EDGE,"E3578"),sQuery(id+"F17.wireOp",EDGE,"E3579"),sQuery(id+"F17.wireOp",EDGE,"E3580"),sQuery(id+"F17.wireOp",EDGE,"E3581"),sQuery(id+"F17.wireOp",EDGE,"E3582"),sQuery(id+"F17.wireOp",EDGE,"E3583"),sQuery(id+"F17.wireOp",EDGE,"E3584"),sQuery(id+"F17.wireOp",EDGE,"E3585"),sQuery(id+"F17.wireOp",EDGE,"E3586"),sQuery(id+"F17.wireOp",EDGE,"E3587"),sQuery(id+"F17.wireOp",EDGE,"E3588"),sQuery(id+"F17.wireOp",EDGE,"E3589"),sQuery(id+"F17.wireOp",EDGE,"E3590"),sQuery(id+"F17.wireOp",EDGE,"E3591"),sQuery(id+"F17.wireOp",EDGE,"E3592"),sQuery(id+"F17.wireOp",EDGE,"E3593"),sQuery(id+"F17.wireOp",EDGE,"E3594"),sQuery(id+"F17.wireOp",EDGE,"E3595"),sQuery(id+"F17.wireOp",EDGE,"E3596"),sQuery(id+"F17.wireOp",EDGE,"E3597"),sQuery(id+"F17.wireOp",EDGE,"E3598"),sQuery(id+"F17.wireOp",EDGE,"E3599"),sQuery(id+"F17.wireOp",EDGE,"E3600"),sQuery(id+"F17.wireOp",EDGE,"E3601"),sQuery(id+"F17.wireOp",EDGE,"E3602"),sQuery(id+"F17.wireOp",EDGE,"E3603"),sQuery(id+"F17.wireOp",EDGE,"E3604"),sQuery(id+"F17.wireOp",EDGE,"E3605"),sQuery(id+"F17.wireOp",EDGE,"E3606"),sQuery(id+"F17.wireOp",EDGE,"E3607"),sQuery(id+"F17.wireOp",EDGE,"E3608"),sQuery(id+"F17.wireOp",EDGE,"E3609"),sQuery(id+"F17.wireOp",EDGE,"E3610"),sQuery(id+"F17.wireOp",EDGE,"E3611"),sQuery(id+"F17.wireOp",EDGE,"E3612"),sQuery(id+"F17.wireOp",EDGE,"E3613"),sQuery(id+"F17.wireOp",EDGE,"E3614"),sQuery(id+"F17.wireOp",EDGE,"E3615"),sQuery(id+"F17.wireOp",EDGE,"E3616"),sQuery(id+"F17.wireOp",EDGE,"E3617"),sQuery(id+"F17.wireOp",EDGE,"E3618"),sQuery(id+"F17.wireOp",EDGE,"E3619"),sQuery(id+"F17.wireOp",EDGE,"E3620"),sQuery(id+"F17.wireOp",EDGE,"E3621"),sQuery(id+"F17.wireOp",EDGE,"E3622"),sQuery(id+"F17.wireOp",EDGE,"E3623"),sQuery(id+"F17.wireOp",EDGE,"E3624"),sQuery(id+"F17.wireOp",EDGE,"E3625"),sQuery(id+"F17.wireOp",EDGE,"E3626"),sQuery(id+"F17.wireOp",EDGE,"E3627"),sQuery(id+"F17.wireOp",EDGE,"E3628"),sQuery(id+"F17.wireOp",EDGE,"E3629"),sQuery(id+"F17.wireOp",EDGE,"E3630"),sQuery(id+"F17.wireOp",EDGE,"E3631"),sQuery(id+"F17.wireOp",EDGE,"E3632"),sQuery(id+"F17.wireOp",EDGE,"E3633"),sQuery(id+"F17.wireOp",EDGE,"E3634"),sQuery(id+"F17.wireOp",EDGE,"E3635"),sQuery(id+"F17.wireOp",EDGE,"E3636"),sQuery(id+"F17.wireOp",EDGE,"E3637"),sQuery(id+"F17.wireOp",EDGE,"E3638"),sQuery(id+"F17.wireOp",EDGE,"E3639"),sQuery(id+"F17.wireOp",EDGE,"E3640"),sQuery(id+"F17.wireOp",EDGE,"E3641"),sQuery(id+"F17.wireOp",EDGE,"E3642"),sQuery(id+"F17.wireOp",EDGE,"E3643"),sQuery(id+"F17.wireOp",EDGE,"E3644"),sQuery(id+"F17.wireOp",EDGE,"E3645"),sQuery(id+"F17.wireOp",EDGE,"E3646"),sQuery(id+"F17.wireOp",EDGE,"E3647"),sQuery(id+"F17.wireOp",EDGE,"E3648"),sQuery(id+"F17.wireOp",EDGE,"E3649"),sQuery(id+"F17.wireOp",EDGE,"E3650"),sQuery(id+"F17.wireOp",EDGE,"E3651"),sQuery(id+"F17.wireOp",EDGE,"E3652"),sQuery(id+"F17.wireOp",EDGE,"E3653"),sQuery(id+"F17.wireOp",EDGE,"E3654"),sQuery(id+"F17.wireOp",EDGE,"E3655"),sQuery(id+"F17.wireOp",EDGE,"E3656"),sQuery(id+"F17.wireOp",EDGE,"E3657"),sQuery(id+"F17.wireOp",EDGE,"E3658"),sQuery(id+"F17.wireOp",EDGE,"E3659"),sQuery(id+"F17.wireOp",EDGE,"E3660"),sQuery(id+"F17.wireOp",EDGE,"E3661"),sQuery(id+"F17.wireOp",EDGE,"E3662"),sQuery(id+"F17.wireOp",EDGE,"E3663"),sQuery(id+"F17.wireOp",EDGE,"E3664"),sQuery(id+"F17.wireOp",EDGE,"E3665"),sQuery(id+"F17.wireOp",EDGE,"E3666"),sQuery(id+"F17.wireOp",EDGE,"E3667"),sQuery(id+"F17.wireOp",EDGE,"E3668"),sQuery(id+"F17.wireOp",EDGE,"E3669"),sQuery(id+"F17.wireOp",EDGE,"E3670"),sQuery(id+"F17.wireOp",EDGE,"E3671"),sQuery(id+"F17.wireOp",EDGE,"E3672"),sQuery(id+"F17.wireOp",EDGE,"E3673"),sQuery(id+"F17.wireOp",EDGE,"E3674"),sQuery(id+"F17.wireOp",EDGE,"E3675"),sQuery(id+"F17.wireOp",EDGE,"E3676"),sQuery(id+"F17.wireOp",EDGE,"E3677"),sQuery(id+"F17.wireOp",EDGE,"E3678"),sQuery(id+"F17.wireOp",EDGE,"E3679"),sQuery(id+"F17.wireOp",EDGE,"E3680"),sQuery(id+"F17.wireOp",EDGE,"E3681"),sQuery(id+"F17.wireOp",EDGE,"E3682"),sQuery(id+"F17.wireOp",EDGE,"E3683"),sQuery(id+"F17.wireOp",EDGE,"E3684"),sQuery(id+"F17.wireOp",EDGE,"E3685"),sQuery(id+"F17.wireOp",EDGE,"E3686"),sQuery(id+"F17.wireOp",EDGE,"E3687"),sQuery(id+"F17.wireOp",EDGE,"E3688"),sQuery(id+"F17.wireOp",EDGE,"E3689"),sQuery(id+"F17.wireOp",EDGE,"E3690"),sQuery(id+"F17.wireOp",EDGE,"E3691"),sQuery(id+"F17.wireOp",EDGE,"E3692"),sQuery(id+"F17.wireOp",EDGE,"E3693"),sQuery(id+"F17.wireOp",EDGE,"E3694"),sQuery(id+"F17.wireOp",EDGE,"E3695"),sQuery(id+"F17.wireOp",EDGE,"E3696"),sQuery(id+"F17.wireOp",EDGE,"E3697"),sQuery(id+"F17.wireOp",EDGE,"E3698"),sQuery(id+"F17.wireOp",EDGE,"E3699"),sQuery(id+"F17.wireOp",EDGE,"E3700"),sQuery(id+"F17.wireOp",EDGE,"E3701"),sQuery(id+"F17.wireOp",EDGE,"E3702"),sQuery(id+"F17.wireOp",EDGE,"E3703"),sQuery(id+"F17.wireOp",EDGE,"E3704"),sQuery(id+"F17.wireOp",EDGE,"E3705"),sQuery(id+"F17.wireOp",EDGE,"E3706"),sQuery(id+"F17.wireOp",EDGE,"E3707"),sQuery(id+"F17.wireOp",EDGE,"E3708"),sQuery(id+"F17.wireOp",EDGE,"E3709"),sQuery(id+"F17.wireOp",EDGE,"E3710"),sQuery(id+"F17.wireOp",EDGE,"E3711"),sQuery(id+"F17.wireOp",EDGE,"E3712"),sQuery(id+"F17.wireOp",EDGE,"E3713"),sQuery(id+"F17.wireOp",EDGE,"E3714"),sQuery(id+"F17.wireOp",EDGE,"E3715"),sQuery(id+"F17.wireOp",EDGE,"E3716"),sQuery(id+"F17.wireOp",EDGE,"E3717"),sQuery(id+"F17.wireOp",EDGE,"E3718"),sQuery(id+"F17.wireOp",EDGE,"E3719"),sQuery(id+"F17.wireOp",EDGE,"E3720"),sQuery(id+"F17.wireOp",EDGE,"E3721"),sQuery(id+"F17.wireOp",EDGE,"E3722"),sQuery(id+"F17.wireOp",EDGE,"E3723"),sQuery(id+"F17.wireOp",EDGE,"E3724"),sQuery(id+"F17.wireOp",EDGE,"E3725"),sQuery(id+"F17.wireOp",EDGE,"E3726"),sQuery(id+"F17.wireOp",EDGE,"E3727"),sQuery(id+"F17.wireOp",EDGE,"E3728"),sQuery(id+"F17.wireOp",EDGE,"E3729"),sQuery(id+"F17.wireOp",EDGE,"E3730"),sQuery(id+"F17.wireOp",EDGE,"E3731"),sQuery(id+"F17.wireOp",EDGE,"E3732"),sQuery(id+"F17.wireOp",EDGE,"E3733"),sQuery(id+"F17.wireOp",EDGE,"E3734"),sQuery(id+"F17.wireOp",EDGE,"E3735"),sQuery(id+"F17.wireOp",EDGE,"E3736"),sQuery(id+"F17.wireOp",EDGE,"E3737"),sQuery(id+"F17.wireOp",EDGE,"E3738"),sQuery(id+"F17.wireOp",EDGE,"E3739"),sQuery(id+"F17.wireOp",EDGE,"E3740"),sQuery(id+"F17.wireOp",EDGE,"E3741"),sQuery(id+"F17.wireOp",EDGE,"E3742"),sQuery(id+"F17.wireOp",EDGE,"E3743"),sQuery(id+"F17.wireOp",EDGE,"E3744"),sQuery(id+"F17.wireOp",EDGE,"E3745"),sQuery(id+"F17.wireOp",EDGE,"E3746"),sQuery(id+"F17.wireOp",EDGE,"E3747"),sQuery(id+"F17.wireOp",EDGE,"E3748"),sQuery(id+"F17.wireOp",EDGE,"E3749"),sQuery(id+"F17.wireOp",EDGE,"E3750"),sQuery(id+"F17.wireOp",EDGE,"E3751"),sQuery(id+"F17.wireOp",EDGE,"E3752"),sQuery(id+"F17.wireOp",EDGE,"E3753"),sQuery(id+"F17.wireOp",EDGE,"E3754"),sQuery(id+"F17.wireOp",EDGE,"E3755"),sQuery(id+"F17.wireOp",EDGE,"E3756"),sQuery(id+"F17.wireOp",EDGE,"E3757"),sQuery(id+"F17.wireOp",EDGE,"E3758"),sQuery(id+"F17.wireOp",EDGE,"E3759"),sQuery(id+"F17.wireOp",EDGE,"E3760"),sQuery(id+"F17.wireOp",EDGE,"E3761"),sQuery(id+"F17.wireOp",EDGE,"E3762"),sQuery(id+"F17.wireOp",EDGE,"E3763"),sQuery(id+"F17.wireOp",EDGE,"E3764"),sQuery(id+"F17.wireOp",EDGE,"E3765"),sQuery(id+"F17.wireOp",EDGE,"E3766"),sQuery(id+"F17.wireOp",EDGE,"E3767"),sQuery(id+"F17.wireOp",EDGE,"E3768"),sQuery(id+"F17.wireOp",EDGE,"E3769"),sQuery(id+"F17.wireOp",EDGE,"E3770"),sQuery(id+"F17.wireOp",EDGE,"E3771"),sQuery(id+"F17.wireOp",EDGE,"E3772"),sQuery(id+"F17.wireOp",EDGE,"E3773"),sQuery(id+"F17.wireOp",EDGE,"E3774"),sQuery(id+"F17.wireOp",EDGE,"E3775"),sQuery(id+"F17.wireOp",EDGE,"E3776"),sQuery(id+"F17.wireOp",EDGE,"E3777"),sQuery(id+"F17.wireOp",EDGE,"E3778"),sQuery(id+"F17.wireOp",EDGE,"E3779"),sQuery(id+"F17.wireOp",EDGE,"E3780"),sQuery(id+"F17.wireOp",EDGE,"E3781"),sQuery(id+"F17.wireOp",EDGE,"E3782"),sQuery(id+"F17.wireOp",EDGE,"E3783"),sQuery(id+"F17.wireOp",EDGE,"E3784"),sQuery(id+"F17.wireOp",EDGE,"E3785"),sQuery(id+"F17.wireOp",EDGE,"E3786"),sQuery(id+"F17.wireOp",EDGE,"E3787"),sQuery(id+"F17.wireOp",EDGE,"E3788"),sQuery(id+"F17.wireOp",EDGE,"E3789"),sQuery(id+"F17.wireOp",EDGE,"E3790"),sQuery(id+"F17.wireOp",EDGE,"E3791"),sQuery(id+"F17.wireOp",EDGE,"E3792"),sQuery(id+"F17.wireOp",EDGE,"E3793"),sQuery(id+"F17.wireOp",EDGE,"E3794"),sQuery(id+"F17.wireOp",EDGE,"E3795"),sQuery(id+"F17.wireOp",EDGE,"E3796"),sQuery(id+"F17.wireOp",EDGE,"E3797"),sQuery(id+"F17.wireOp",EDGE,"E3798"),sQuery(id+"F17.wireOp",EDGE,"E3799"),sQuery(id+"F17.wireOp",EDGE,"E3800"),sQuery(id+"F17.wireOp",EDGE,"E3801"),sQuery(id+"F17.wireOp",EDGE,"E3802"),sQuery(id+"F17.wireOp",EDGE,"E3803"),sQuery(id+"F17.wireOp",EDGE,"E3804"),sQuery(id+"F17.wireOp",EDGE,"E3805"),sQuery(id+"F17.wireOp",EDGE,"E3806"),sQuery(id+"F17.wireOp",EDGE,"E3807"),sQuery(id+"F17.wireOp",EDGE,"E3808"),sQuery(id+"F17.wireOp",EDGE,"E3809"),sQuery(id+"F17.wireOp",EDGE,"E3810"),sQuery(id+"F17.wireOp",EDGE,"E3811"),sQuery(id+"F17.wireOp",EDGE,"E3812"),sQuery(id+"F17.wireOp",EDGE,"E3813"),sQuery(id+"F17.wireOp",EDGE,"E3814"),sQuery(id+"F17.wireOp",EDGE,"E3815"),sQuery(id+"F17.wireOp",EDGE,"E3816"),sQuery(id+"F17.wireOp",EDGE,"E3817"),sQuery(id+"F17.wireOp",EDGE,"E3818"),sQuery(id+"F17.wireOp",EDGE,"E3819"),sQuery(id+"F17.wireOp",EDGE,"E3820"),sQuery(id+"F17.wireOp",EDGE,"E3821"),sQuery(id+"F17.wireOp",EDGE,"E3822"),sQuery(id+"F17.wireOp",EDGE,"E3823"),sQuery(id+"F17.wireOp",EDGE,"E3824"),sQuery(id+"F17.wireOp",EDGE,"E3825"),sQuery(id+"F17.wireOp",EDGE,"E3826"),sQuery(id+"F17.wireOp",EDGE,"E3827"),sQuery(id+"F17.wireOp",EDGE,"E3828"),sQuery(id+"F17.wireOp",EDGE,"E3829"),sQuery(id+"F17.wireOp",EDGE,"E3830"),sQuery(id+"F17.wireOp",EDGE,"E3831"),sQuery(id+"F17.wireOp",EDGE,"E3832"),sQuery(id+"F17.wireOp",EDGE,"E3833"),sQuery(id+"F17.wireOp",EDGE,"E3834"),sQuery(id+"F17.wireOp",EDGE,"E3835"),sQuery(id+"F17.wireOp",EDGE,"E3836"),sQuery(id+"F17.wireOp",EDGE,"E3837"),sQuery(id+"F17.wireOp",EDGE,"E3838"),sQuery(id+"F17.wireOp",EDGE,"E3839"),sQuery(id+"F17.wireOp",EDGE,"E3840"),sQuery(id+"F17.wireOp",EDGE,"E3841"),sQuery(id+"F17.wireOp",EDGE,"E3842"),sQuery(id+"F17.wireOp",EDGE,"E3843"),sQuery(id+"F17.wireOp",EDGE,"E3844"),sQuery(id+"F17.wireOp",EDGE,"E3845"),sQuery(id+"F17.wireOp",EDGE,"E3846"),sQuery(id+"F17.wireOp",EDGE,"E3847"),sQuery(id+"F17.wireOp",EDGE,"E3848"),sQuery(id+"F17.wireOp",EDGE,"E3849"),sQuery(id+"F17.wireOp",EDGE,"E3850"),sQuery(id+"F17.wireOp",EDGE,"E3851"),sQuery(id+"F17.wireOp",EDGE,"E3852"),sQuery(id+"F17.wireOp",EDGE,"E3853"),sQuery(id+"F17.wireOp",EDGE,"E3854"),sQuery(id+"F17.wireOp",EDGE,"E3855"),sQuery(id+"F17.wireOp",EDGE,"E3856"),sQuery(id+"F17.wireOp",EDGE,"E3857"),sQuery(id+"F17.wireOp",EDGE,"E3858"),sQuery(id+"F17.wireOp",EDGE,"E3859"),sQuery(id+"F17.wireOp",EDGE,"E3860"),sQuery(id+"F17.wireOp",EDGE,"E3861"),sQuery(id+"F17.wireOp",EDGE,"E3862"),sQuery(id+"F17.wireOp",EDGE,"E3863"),sQuery(id+"F17.wireOp",EDGE,"E3864"),sQuery(id+"F17.wireOp",EDGE,"E3865"),sQuery(id+"F17.wireOp",EDGE,"E3866"),sQuery(id+"F17.wireOp",EDGE,"E3867"),sQuery(id+"F17.wireOp",EDGE,"E3868"),sQuery(id+"F17.wireOp",EDGE,"E3869"),sQuery(id+"F17.wireOp",EDGE,"E3870"),sQuery(id+"F17.wireOp",EDGE,"E3871"),sQuery(id+"F17.wireOp",EDGE,"E3872"),sQuery(id+"F17.wireOp",EDGE,"E3873"),sQuery(id+"F17.wireOp",EDGE,"E3874"),sQuery(id+"F17.wireOp",EDGE,"E3875"),sQuery(id+"F17.wireOp",EDGE,"E3876"),sQuery(id+"F17.wireOp",EDGE,"E3877"),sQuery(id+"F17.wireOp",EDGE,"E3878"),sQuery(id+"F17.wireOp",EDGE,"E3879"),sQuery(id+"F17.wireOp",EDGE,"E3880"),sQuery(id+"F17.wireOp",EDGE,"E3881"),sQuery(id+"F17.wireOp",EDGE,"E3882"),sQuery(id+"F17.wireOp",EDGE,"E3883"),sQuery(id+"F17.wireOp",EDGE,"E3884"),sQuery(id+"F17.wireOp",EDGE,"E3885"),sQuery(id+"F17.wireOp",EDGE,"E3886"),sQuery(id+"F17.wireOp",EDGE,"E3887"),sQuery(id+"F17.wireOp",EDGE,"E3888"),sQuery(id+"F17.wireOp",EDGE,"E3889"),sQuery(id+"F17.wireOp",EDGE,"E3890"),sQuery(id+"F17.wireOp",EDGE,"E3891"),sQuery(id+"F17.wireOp",EDGE,"E3892"),sQuery(id+"F17.wireOp",EDGE,"E3893"),sQuery(id+"F17.wireOp",EDGE,"E3894"),sQuery(id+"F17.wireOp",EDGE,"E3895"),sQuery(id+"F17.wireOp",EDGE,"E3896"),sQuery(id+"F17.wireOp",EDGE,"E3897"),sQuery(id+"F17.wireOp",EDGE,"E3898"),sQuery(id+"F17.wireOp",EDGE,"E3899"),sQuery(id+"F17.wireOp",EDGE,"E3900"),sQuery(id+"F17.wireOp",EDGE,"E3901"),sQuery(id+"F17.wireOp",EDGE,"E3902"),sQuery(id+"F17.wireOp",EDGE,"E3903"),sQuery(id+"F17.wireOp",EDGE,"E3904"),sQuery(id+"F17.wireOp",EDGE,"E3905"),sQuery(id+"F17.wireOp",EDGE,"E3906"),sQuery(id+"F17.wireOp",EDGE,"E3907"),sQuery(id+"F17.wireOp",EDGE,"E3908"),sQuery(id+"F17.wireOp",EDGE,"E3909"),sQuery(id+"F17.wireOp",EDGE,"E3910"),sQuery(id+"F17.wireOp",EDGE,"E3911"),sQuery(id+"F17.wireOp",EDGE,"E3912"),sQuery(id+"F17.wireOp",EDGE,"E3913"),sQuery(id+"F17.wireOp",EDGE,"E3914"),sQuery(id+"F17.wireOp",EDGE,"E3915"),sQuery(id+"F17.wireOp",EDGE,"E3916"),sQuery(id+"F17.wireOp",EDGE,"E3917"),sQuery(id+"F17.wireOp",EDGE,"E3918"),sQuery(id+"F17.wireOp",EDGE,"E3919"),sQuery(id+"F17.wireOp",EDGE,"E3920"),sQuery(id+"F17.wireOp",EDGE,"E3921"),sQuery(id+"F17.wireOp",EDGE,"E3922"),sQuery(id+"F17.wireOp",EDGE,"E3923"),sQuery(id+"F17.wireOp",EDGE,"E3924"),sQuery(id+"F17.wireOp",EDGE,"E3925"),sQuery(id+"F17.wireOp",EDGE,"E3926"),sQuery(id+"F17.wireOp",EDGE,"E3927"),sQuery(id+"F17.wireOp",EDGE,"E3928"),sQuery(id+"F17.wireOp",EDGE,"E3929"),sQuery(id+"F17.wireOp",EDGE,"E3930"),sQuery(id+"F17.wireOp",EDGE,"E3931"),sQuery(id+"F17.wireOp",EDGE,"E3932"),sQuery(id+"F17.wireOp",EDGE,"E3933"),sQuery(id+"F17.wireOp",EDGE,"E3934"),sQuery(id+"F17.wireOp",EDGE,"E3935"),sQuery(id+"F17.wireOp",EDGE,"E3936"),sQuery(id+"F17.wireOp",EDGE,"E3937"),sQuery(id+"F17.wireOp",EDGE,"E3938"),sQuery(id+"F17.wireOp",EDGE,"E3939"),sQuery(id+"F17.wireOp",EDGE,"E3940"),sQuery(id+"F17.wireOp",EDGE,"E3941"),sQuery(id+"F17.wireOp",EDGE,"E3942"),sQuery(id+"F17.wireOp",EDGE,"E3943"),sQuery(id+"F17.wireOp",EDGE,"E3944"),sQuery(id+"F17.wireOp",EDGE,"E3945"),sQuery(id+"F17.wireOp",EDGE,"E3946"),sQuery(id+"F17.wireOp",EDGE,"E3947"),sQuery(id+"F17.wireOp",EDGE,"E3948"),sQuery(id+"F17.wireOp",EDGE,"E3949"),sQuery(id+"F17.wireOp",EDGE,"E3950"),sQuery(id+"F17.wireOp",EDGE,"E3951"),sQuery(id+"F17.wireOp",EDGE,"E3952"),sQuery(id+"F17.wireOp",EDGE,"E3953"),sQuery(id+"F17.wireOp",EDGE,"E3954"),sQuery(id+"F17.wireOp",EDGE,"E3955"),sQuery(id+"F17.wireOp",EDGE,"E3956"),sQuery(id+"F17.wireOp",EDGE,"E3957"),sQuery(id+"F17.wireOp",EDGE,"E3958"),sQuery(id+"F17.wireOp",EDGE,"E3959"),sQuery(id+"F17.wireOp",EDGE,"E3960"),sQuery(id+"F17.wireOp",EDGE,"E3961"),sQuery(id+"F17.wireOp",EDGE,"E3962"),sQuery(id+"F17.wireOp",EDGE,"E3963"),sQuery(id+"F17.wireOp",EDGE,"E3964"),sQuery(id+"F17.wireOp",EDGE,"E3965"),sQuery(id+"F17.wireOp",EDGE,"E3966"),sQuery(id+"F17.wireOp",EDGE,"E3967"),sQuery(id+"F17.wireOp",EDGE,"E3968"),sQuery(id+"F17.wireOp",EDGE,"E3969"),sQuery(id+"F17.wireOp",EDGE,"E3970"),sQuery(id+"F17.wireOp",EDGE,"E3971"),sQuery(id+"F17.wireOp",EDGE,"E3972"),sQuery(id+"F17.wireOp",EDGE,"E3973"),sQuery(id+"F17.wireOp",EDGE,"E3974"),sQuery(id+"F17.wireOp",EDGE,"E3975"),sQuery(id+"F17.wireOp",EDGE,"E3976"),sQuery(id+"F17.wireOp",EDGE,"E3977"),sQuery(id+"F17.wireOp",EDGE,"E3978"),sQuery(id+"F17.wireOp",EDGE,"E3979"),sQuery(id+"F17.wireOp",EDGE,"E3980"),sQuery(id+"F17.wireOp",EDGE,"E3981"),sQuery(id+"F17.wireOp",EDGE,"E3982"),sQuery(id+"F17.wireOp",EDGE,"E3983"),sQuery(id+"F17.wireOp",EDGE,"E3984"),sQuery(id+"F17.wireOp",EDGE,"E3985"),sQuery(id+"F17.wireOp",EDGE,"E3986"),sQuery(id+"F17.wireOp",EDGE,"E3987"),sQuery(id+"F17.wireOp",EDGE,"E3988"),sQuery(id+"F17.wireOp",EDGE,"E3989"),sQuery(id+"F17.wireOp",EDGE,"E3990"),sQuery(id+"F17.wireOp",EDGE,"E3991"),sQuery(id+"F17.wireOp",EDGE,"E3992"),sQuery(id+"F17.wireOp",EDGE,"E3993"),sQuery(id+"F17.wireOp",EDGE,"E3994"),sQuery(id+"F17.wireOp",EDGE,"E3995"),sQuery(id+"F17.wireOp",EDGE,"E3996"),sQuery(id+"F17.wireOp",EDGE,"E3997"),sQuery(id+"F17.wireOp",EDGE,"E3998"),sQuery(id+"F17.wireOp",EDGE,"E3999"),sQuery(id+"F17.wireOp",EDGE,"E4000"),sQuery(id+"F17.wireOp",EDGE,"E4001"),sQuery(id+"F17.wireOp",EDGE,"E4002"),sQuery(id+"F17.wireOp",EDGE,"E4003"),sQuery(id+"F17.wireOp",EDGE,"E4004"),sQuery(id+"F17.wireOp",EDGE,"E4005"),sQuery(id+"F17.wireOp",EDGE,"E4006"),sQuery(id+"F17.wireOp",EDGE,"E4007"),sQuery(id+"F17.wireOp",EDGE,"E4008"),sQuery(id+"F17.wireOp",EDGE,"E4009"),sQuery(id+"F17.wireOp",EDGE,"E4010"),sQuery(id+"F17.wireOp",EDGE,"E4011"),sQuery(id+"F17.wireOp",EDGE,"E4012"),sQuery(id+"F17.wireOp",EDGE,"E4013"),sQuery(id+"F17.wireOp",EDGE,"E4014"),sQuery(id+"F17.wireOp",EDGE,"E4015"),sQuery(id+"F17.wireOp",EDGE,"E4016"),sQuery(id+"F17.wireOp",EDGE,"E4017"),sQuery(id+"F17.wireOp",EDGE,"E4018"),sQuery(id+"F17.wireOp",EDGE,"E4019"),sQuery(id+"F17.wireOp",EDGE,"E4020"),sQuery(id+"F17.wireOp",EDGE,"E4021"),sQuery(id+"F17.wireOp",EDGE,"E4022"),sQuery(id+"F17.wireOp",EDGE,"E4023"),sQuery(id+"F17.wireOp",EDGE,"E4024"),sQuery(id+"F17.wireOp",EDGE,"E4025"),sQuery(id+"F17.wireOp",EDGE,"E4026"),sQuery(id+"F17.wireOp",EDGE,"E4027"),sQuery(id+"F17.wireOp",EDGE,"E4028"),sQuery(id+"F17.wireOp",EDGE,"E4029"),sQuery(id+"F17.wireOp",EDGE,"E4030"),sQuery(id+"F17.wireOp",EDGE,"E4031"),sQuery(id+"F17.wireOp",EDGE,"E4032"),sQuery(id+"F17.wireOp",EDGE,"E4033"),sQuery(id+"F17.wireOp",EDGE,"E4034"),sQuery(id+"F17.wireOp",EDGE,"E4035"),sQuery(id+"F17.wireOp",EDGE,"E4036"),sQuery(id+"F17.wireOp",EDGE,"E4037"),sQuery(id+"F17.wireOp",EDGE,"E4038"),sQuery(id+"F17.wireOp",EDGE,"E4039"),sQuery(id+"F17.wireOp",EDGE,"E4040"),sQuery(id+"F17.wireOp",EDGE,"E4041"),sQuery(id+"F17.wireOp",EDGE,"E4042"),sQuery(id+"F17.wireOp",EDGE,"E4043"),sQuery(id+"F17.wireOp",EDGE,"E4044"),sQuery(id+"F17.wireOp",EDGE,"E4045"),sQuery(id+"F17.wireOp",EDGE,"E4046"),sQuery(id+"F17.wireOp",EDGE,"E4047"),sQuery(id+"F17.wireOp",EDGE,"E4048"),sQuery(id+"F17.wireOp",EDGE,"E4049"),sQuery(id+"F17.wireOp",EDGE,"E4050"),sQuery(id+"F17.wireOp",EDGE,"E4051"),sQuery(id+"F17.wireOp",EDGE,"E4052"),sQuery(id+"F17.wireOp",EDGE,"E4053"),sQuery(id+"F17.wireOp",EDGE,"E4054"),sQuery(id+"F17.wireOp",EDGE,"E4055"),sQuery(id+"F17.wireOp",EDGE,"E4056"),sQuery(id+"F17.wireOp",EDGE,"E4057"),sQuery(id+"F17.wireOp",EDGE,"E4058"),sQuery(id+"F17.wireOp",EDGE,"E4059"),sQuery(id+"F17.wireOp",EDGE,"E4060"),sQuery(id+"F17.wireOp",EDGE,"E4061"),sQuery(id+"F17.wireOp",EDGE,"E4062"),sQuery(id+"F17.wireOp",EDGE,"E4063"),sQuery(id+"F17.wireOp",EDGE,"E4064"),sQuery(id+"F17.wireOp",EDGE,"E4065"),sQuery(id+"F17.wireOp",EDGE,"E4066"),sQuery(id+"F17.wireOp",EDGE,"E4067"),sQuery(id+"F17.wireOp",EDGE,"E4068"),sQuery(id+"F17.wireOp",EDGE,"E4069"),sQuery(id+"F17.wireOp",EDGE,"E4070"),sQuery(id+"F17.wireOp",EDGE,"E4071"),sQuery(id+"F17.wireOp",EDGE,"E4072"),sQuery(id+"F17.wireOp",EDGE,"E4073"),sQuery(id+"F17.wireOp",EDGE,"E4074"),sQuery(id+"F17.wireOp",EDGE,"E4075"),sQuery(id+"F17.wireOp",EDGE,"E4076"),sQuery(id+"F17.wireOp",EDGE,"E4077"),sQuery(id+"F17.wireOp",EDGE,"E4078"),sQuery(id+"F17.wireOp",EDGE,"E4079"),sQuery(id+"F17.wireOp",EDGE,"E4080"),sQuery(id+"F17.wireOp",EDGE,"E4081"),sQuery(id+"F17.wireOp",EDGE,"E4082"),sQuery(id+"F17.wireOp",EDGE,"E4083"),sQuery(id+"F17.wireOp",EDGE,"E4084"),sQuery(id+"F17.wireOp",EDGE,"E4085"),sQuery(id+"F17.wireOp",EDGE,"E4086"),sQuery(id+"F17.wireOp",EDGE,"E4087"),sQuery(id+"F17.wireOp",EDGE,"E4088"),sQuery(id+"F17.wireOp",EDGE,"E4089"),sQuery(id+"F17.wireOp",EDGE,"E4090"),sQuery(id+"F17.wireOp",EDGE,"E4091"),sQuery(id+"F17.wireOp",EDGE,"E4092"),sQuery(id+"F17.wireOp",EDGE,"E4093"),sQuery(id+"F17.wireOp",EDGE,"E4094"),sQuery(id+"F17.wireOp",EDGE,"E4095"),sQuery(id+"F17.wireOp",EDGE,"E4096"),sQuery(id+"F17.wireOp",EDGE,"E4097"),sQuery(id+"F17.wireOp",EDGE,"E4098"),sQuery(id+"F17.wireOp",EDGE,"E4099"),sQuery(id+"F17.wireOp",EDGE,"E4100"),sQuery(id+"F17.wireOp",EDGE,"E4101"),sQuery(id+"F17.wireOp",EDGE,"E4102"),sQuery(id+"F17.wireOp",EDGE,"E4103"),sQuery(id+"F17.wireOp",EDGE,"E4104"),sQuery(id+"F17.wireOp",EDGE,"E4105"),sQuery(id+"F17.wireOp",EDGE,"E4106"),sQuery(id+"F17.wireOp",EDGE,"E4107"),sQuery(id+"F17.wireOp",EDGE,"E4108"),sQuery(id+"F17.wireOp",EDGE,"E4109"),sQuery(id+"F17.wireOp",EDGE,"E4110"),sQuery(id+"F17.wireOp",EDGE,"E4111"),sQuery(id+"F17.wireOp",EDGE,"E4112"),sQuery(id+"F17.wireOp",EDGE,"E4113"),sQuery(id+"F17.wireOp",EDGE,"E4114"),sQuery(id+"F17.wireOp",EDGE,"E4115"),sQuery(id+"F17.wireOp",EDGE,"E4116"),sQuery(id+"F17.wireOp",EDGE,"E4117"),sQuery(id+"F17.wireOp",EDGE,"E4118"),sQuery(id+"F17.wireOp",EDGE,"E4119"),sQuery(id+"F17.wireOp",EDGE,"E4120"),sQuery(id+"F17.wireOp",EDGE,"E4121"),sQuery(id+"F17.wireOp",EDGE,"E4122"),sQuery(id+"F17.wireOp",EDGE,"E4123"),sQuery(id+"F17.wireOp",EDGE,"E4124"),sQuery(id+"F17.wireOp",EDGE,"E4125"),sQuery(id+"F17.wireOp",EDGE,"E4126"),sQuery(id+"F17.wireOp",EDGE,"E4127"),sQuery(id+"F17.wireOp",EDGE,"E4128"),sQuery(id+"F17.wireOp",EDGE,"E4129"),sQuery(id+"F17.wireOp",EDGE,"E4130"),sQuery(id+"F17.wireOp",EDGE,"E4131"),sQuery(id+"F17.wireOp",EDGE,"E4132"),sQuery(id+"F17.wireOp",EDGE,"E4133"),sQuery(id+"F17.wireOp",EDGE,"E4134"),sQuery(id+"F17.wireOp",EDGE,"E4135"),sQuery(id+"F17.wireOp",EDGE,"E4136"),sQuery(id+"F17.wireOp",EDGE,"E4137"),sQuery(id+"F17.wireOp",EDGE,"E4138"),sQuery(id+"F17.wireOp",EDGE,"E4139"),sQuery(id+"F17.wireOp",EDGE,"E4140"),sQuery(id+"F17.wireOp",EDGE,"E4141"),sQuery(id+"F17.wireOp",EDGE,"E4142"),sQuery(id+"F17.wireOp",EDGE,"E4143"),sQuery(id+"F17.wireOp",EDGE,"E4144"),sQuery(id+"F17.wireOp",EDGE,"E4145"),sQuery(id+"F17.wireOp",EDGE,"E4146"),sQuery(id+"F17.wireOp",EDGE,"E4147"),sQuery(id+"F17.wireOp",EDGE,"E4148"),sQuery(id+"F17.wireOp",EDGE,"E4149"),sQuery(id+"F17.wireOp",EDGE,"E4150"),sQuery(id+"F17.wireOp",EDGE,"E4151"),sQuery(id+"F17.wireOp",EDGE,"E4152"),sQuery(id+"F17.wireOp",EDGE,"E4153"),sQuery(id+"F17.wireOp",EDGE,"E4154"),sQuery(id+"F17.wireOp",EDGE,"E4155"),sQuery(id+"F17.wireOp",EDGE,"E4156"),sQuery(id+"F17.wireOp",EDGE,"E4157"),sQuery(id+"F17.wireOp",EDGE,"E4158"),sQuery(id+"F17.wireOp",EDGE,"E4159"),sQuery(id+"F17.wireOp",EDGE,"E4160"),sQuery(id+"F17.wireOp",EDGE,"E4161"),sQuery(id+"F17.wireOp",EDGE,"E4162"),sQuery(id+"F17.wireOp",EDGE,"E4163"),sQuery(id+"F17.wireOp",EDGE,"E4164"),sQuery(id+"F17.wireOp",EDGE,"E4165"),sQuery(id+"F17.wireOp",EDGE,"E4166"),sQuery(id+"F17.wireOp",EDGE,"E4167"),sQuery(id+"F17.wireOp",EDGE,"E4168"),sQuery(id+"F17.wireOp",EDGE,"E4169"),sQuery(id+"F17.wireOp",EDGE,"E4170"),sQuery(id+"F17.wireOp",EDGE,"E4171"),sQuery(id+"F17.wireOp",EDGE,"E4172"),sQuery(id+"F17.wireOp",EDGE,"E4173"),sQuery(id+"F17.wireOp",EDGE,"E4174"),sQuery(id+"F17.wireOp",EDGE,"E4175"),sQuery(id+"F17.wireOp",EDGE,"E4176"),sQuery(id+"F17.wireOp",EDGE,"E4177"),sQuery(id+"F17.wireOp",EDGE,"E4178"),sQuery(id+"F17.wireOp",EDGE,"E4179"),sQuery(id+"F17.wireOp",EDGE,"E4180"),sQuery(id+"F17.wireOp",EDGE,"E4181"),sQuery(id+"F17.wireOp",EDGE,"E4182"),sQuery(id+"F17.wireOp",EDGE,"E4183"),sQuery(id+"F17.wireOp",EDGE,"E4184"),sQuery(id+"F17.wireOp",EDGE,"E4185"),sQuery(id+"F17.wireOp",EDGE,"E4186"),sQuery(id+"F17.wireOp",EDGE,"E4187"),sQuery(id+"F17.wireOp",EDGE,"E4188"),sQuery(id+"F17.wireOp",EDGE,"E4189"),sQuery(id+"F17.wireOp",EDGE,"E4190"),sQuery(id+"F17.wireOp",EDGE,"E4191"),sQuery(id+"F17.wireOp",EDGE,"E4192"),sQuery(id+"F17.wireOp",EDGE,"E4193"),sQuery(id+"F17.wireOp",EDGE,"E4194"),sQuery(id+"F17.wireOp",EDGE,"E4195"),sQuery(id+"F17.wireOp",EDGE,"E4196"),sQuery(id+"F17.wireOp",EDGE,"E4197"),sQuery(id+"F17.wireOp",EDGE,"E4198"),sQuery(id+"F17.wireOp",EDGE,"E4199"),sQuery(id+"F17.wireOp",EDGE,"E4200"),sQuery(id+"F17.wireOp",EDGE,"E4201"),sQuery(id+"F17.wireOp",EDGE,"E4202"),sQuery(id+"F17.wireOp",EDGE,"E4203"),sQuery(id+"F17.wireOp",EDGE,"E4204"),sQuery(id+"F17.wireOp",EDGE,"E4205"),sQuery(id+"F17.wireOp",EDGE,"E4206"),sQuery(id+"F17.wireOp",EDGE,"E4207"),sQuery(id+"F17.wireOp",EDGE,"E4208"),sQuery(id+"F17.wireOp",EDGE,"E4209"),sQuery(id+"F17.wireOp",EDGE,"E4210"),sQuery(id+"F17.wireOp",EDGE,"E4211"),sQuery(id+"F17.wireOp",EDGE,"E4212"),sQuery(id+"F17.wireOp",EDGE,"E4213"),sQuery(id+"F17.wireOp",EDGE,"E4214"),sQuery(id+"F17.wireOp",EDGE,"E4215"),sQuery(id+"F17.wireOp",EDGE,"E4216"),sQuery(id+"F17.wireOp",EDGE,"E4217"),sQuery(id+"F17.wireOp",EDGE,"E4218"),sQuery(id+"F17.wireOp",EDGE,"E4219"),sQuery(id+"F17.wireOp",EDGE,"E4220"),sQuery(id+"F17.wireOp",EDGE,"E4221"),sQuery(id+"F17.wireOp",EDGE,"E4222"),sQuery(id+"F17.wireOp",EDGE,"E4223"),sQuery(id+"F17.wireOp",EDGE,"E4224"),sQuery(id+"F17.wireOp",EDGE,"E4225"),sQuery(id+"F17.wireOp",EDGE,"E4226"),sQuery(id+"F17.wireOp",EDGE,"E4227"),sQuery(id+"F17.wireOp",EDGE,"E4228"),sQuery(id+"F17.wireOp",EDGE,"E4229"),sQuery(id+"F17.wireOp",EDGE,"E4230"),sQuery(id+"F17.wireOp",EDGE,"E4231"),sQuery(id+"F17.wireOp",EDGE,"E4232"),sQuery(id+"F17.wireOp",EDGE,"E4233"),sQuery(id+"F17.wireOp",EDGE,"E4234"),sQuery(id+"F17.wireOp",EDGE,"E4235"),sQuery(id+"F17.wireOp",EDGE,"E4236"),sQuery(id+"F17.wireOp",EDGE,"E4237"),sQuery(id+"F17.wireOp",EDGE,"E4238"),sQuery(id+"F17.wireOp",EDGE,"E4239"),sQuery(id+"F17.wireOp",EDGE,"E4240"),sQuery(id+"F17.wireOp",EDGE,"E4241"),sQuery(id+"F17.wireOp",EDGE,"E4242"),sQuery(id+"F17.wireOp",EDGE,"E4243"),sQuery(id+"F17.wireOp",EDGE,"E4244"),sQuery(id+"F17.wireOp",EDGE,"E4245"),sQuery(id+"F17.wireOp",EDGE,"E4246"),sQuery(id+"F17.wireOp",EDGE,"E4247"),sQuery(id+"F17.wireOp",EDGE,"E4248"),sQuery(id+"F17.wireOp",EDGE,"E4249"),sQuery(id+"F17.wireOp",EDGE,"E4250"),sQuery(id+"F17.wireOp",EDGE,"E4251"),sQuery(id+"F17.wireOp",EDGE,"E4252"),sQuery(id+"F17.wireOp",EDGE,"E4253"),sQuery(id+"F17.wireOp",EDGE,"E4254"),sQuery(id+"F17.wireOp",EDGE,"E4255"),sQuery(id+"F17.wireOp",EDGE,"E4256"),sQuery(id+"F17.wireOp",EDGE,"E4257"),sQuery(id+"F17.wireOp",EDGE,"E4258"),sQuery(id+"F17.wireOp",EDGE,"E4259"),sQuery(id+"F17.wireOp",EDGE,"E4260"),sQuery(id+"F17.wireOp",EDGE,"E4261"),sQuery(id+"F17.wireOp",EDGE,"E4262"),sQuery(id+"F17.wireOp",EDGE,"E4263"),sQuery(id+"F17.wireOp",EDGE,"E4264"),sQuery(id+"F17.wireOp",EDGE,"E4265"),sQuery(id+"F17.wireOp",EDGE,"E4266"),sQuery(id+"F17.wireOp",EDGE,"E4267"),sQuery(id+"F17.wireOp",EDGE,"E4268"),sQuery(id+"F17.wireOp",EDGE,"E4269"),sQuery(id+"F17.wireOp",EDGE,"E4270"),sQuery(id+"F17.wireOp",EDGE,"E4271"),sQuery(id+"F17.wireOp",EDGE,"E4272"),sQuery(id+"F17.wireOp",EDGE,"E4273"),sQuery(id+"F17.wireOp",EDGE,"E4274"),sQuery(id+"F17.wireOp",EDGE,"E4275"),sQuery(id+"F17.wireOp",EDGE,"E4276"),sQuery(id+"F17.wireOp",EDGE,"E4277"),sQuery(id+"F17.wireOp",EDGE,"E4278"),sQuery(id+"F17.wireOp",EDGE,"E4279"),sQuery(id+"F17.wireOp",EDGE,"E4280"),sQuery(id+"F17.wireOp",EDGE,"E4281"),sQuery(id+"F17.wireOp",EDGE,"E4282"),sQuery(id+"F17.wireOp",EDGE,"E4283"),sQuery(id+"F17.wireOp",EDGE,"E4284"),sQuery(id+"F17.wireOp",EDGE,"E4285"),sQuery(id+"F17.wireOp",EDGE,"E4286"),sQuery(id+"F17.wireOp",EDGE,"E4287"),sQuery(id+"F17.wireOp",EDGE,"E4288"),sQuery(id+"F17.wireOp",EDGE,"E4289"),sQuery(id+"F17.wireOp",EDGE,"E4290"),sQuery(id+"F17.wireOp",EDGE,"E4291"),sQuery(id+"F17.wireOp",EDGE,"E4292"),sQuery(id+"F17.wireOp",EDGE,"E4293"),sQuery(id+"F17.wireOp",EDGE,"E4294"),sQuery(id+"F17.wireOp",EDGE,"E4295"),sQuery(id+"F17.wireOp",EDGE,"E4296"),sQuery(id+"F17.wireOp",EDGE,"E4297"),sQuery(id+"F17.wireOp",EDGE,"E4298"),sQuery(id+"F17.wireOp",EDGE,"E4299"),sQuery(id+"F17.wireOp",EDGE,"E4300"),sQuery(id+"F17.wireOp",EDGE,"E4301"),sQuery(id+"F17.wireOp",EDGE,"E4302"),sQuery(id+"F17.wireOp",EDGE,"E4303"),sQuery(id+"F17.wireOp",EDGE,"E4304"),sQuery(id+"F17.wireOp",EDGE,"E4305"),sQuery(id+"F17.wireOp",EDGE,"E4306"),sQuery(id+"F17.wireOp",EDGE,"E4307"),sQuery(id+"F17.wireOp",EDGE,"E4308"),sQuery(id+"F17.wireOp",EDGE,"E4309"),sQuery(id+"F17.wireOp",EDGE,"E4310"),sQuery(id+"F17.wireOp",EDGE,"E4311"),sQuery(id+"F17.wireOp",EDGE,"E4312"),sQuery(id+"F17.wireOp",EDGE,"E4313"),sQuery(id+"F17.wireOp",EDGE,"E4314"),sQuery(id+"F17.wireOp",EDGE,"E4315"),sQuery(id+"F17.wireOp",EDGE,"E4316"),sQuery(id+"F17.wireOp",EDGE,"E4317"),sQuery(id+"F17.wireOp",EDGE,"E4318"),sQuery(id+"F17.wireOp",EDGE,"E4319"),sQuery(id+"F17.wireOp",EDGE,"E4320"),sQuery(id+"F17.wireOp",EDGE,"E4321"),sQuery(id+"F17.wireOp",EDGE,"E4322"),sQuery(id+"F17.wireOp",EDGE,"E4323"),sQuery(id+"F17.wireOp",EDGE,"E4324"),sQuery(id+"F17.wireOp",EDGE,"E4325"),sQuery(id+"F17.wireOp",EDGE,"E4326"),sQuery(id+"F17.wireOp",EDGE,"E4327"),sQuery(id+"F17.wireOp",EDGE,"E4328"),sQuery(id+"F17.wireOp",EDGE,"E4329"),sQuery(id+"F17.wireOp",EDGE,"E4330"),sQuery(id+"F17.wireOp",EDGE,"E4331"),sQuery(id+"F17.wireOp",EDGE,"E4332"),sQuery(id+"F17.wireOp",EDGE,"E4333"),sQuery(id+"F17.wireOp",EDGE,"E4334"),sQuery(id+"F17.wireOp",EDGE,"E4335"),sQuery(id+"F17.wireOp",EDGE,"E4336"),sQuery(id+"F17.wireOp",EDGE,"E4337"),sQuery(id+"F17.wireOp",EDGE,"E4338"),sQuery(id+"F17.wireOp",EDGE,"E4339"),sQuery(id+"F17.wireOp",EDGE,"E4340"),sQuery(id+"F17.wireOp",EDGE,"E4341"),sQuery(id+"F17.wireOp",EDGE,"E4342"),sQuery(id+"F17.wireOp",EDGE,"E4343"),sQuery(id+"F17.wireOp",EDGE,"E4344"),sQuery(id+"F17.wireOp",EDGE,"E4345"),sQuery(id+"F17.wireOp",EDGE,"E4346"),sQuery(id+"F17.wireOp",EDGE,"E4347"),sQuery(id+"F17.wireOp",EDGE,"E4348"),sQuery(id+"F17.wireOp",EDGE,"E4349"),sQuery(id+"F17.wireOp",EDGE,"E4350"),sQuery(id+"F17.wireOp",EDGE,"E4351"),sQuery(id+"F17.wireOp",EDGE,"E4352"),sQuery(id+"F17.wireOp",EDGE,"E4353"),sQuery(id+"F17.wireOp",EDGE,"E4354"),sQuery(id+"F17.wireOp",EDGE,"E4355"),sQuery(id+"F17.wireOp",EDGE,"E4356"),sQuery(id+"F17.wireOp",EDGE,"E4357"),sQuery(id+"F17.wireOp",EDGE,"E4358"),sQuery(id+"F17.wireOp",EDGE,"E4359"),sQuery(id+"F17.wireOp",EDGE,"E4360"),sQuery(id+"F17.wireOp",EDGE,"E4361"),sQuery(id+"F17.wireOp",EDGE,"E4362"),sQuery(id+"F17.wireOp",EDGE,"E4363"),sQuery(id+"F17.wireOp",EDGE,"E4364"),sQuery(id+"F17.wireOp",EDGE,"E4365"),sQuery(id+"F17.wireOp",EDGE,"E4366"),sQuery(id+"F17.wireOp",EDGE,"E4367"),sQuery(id+"F17.wireOp",EDGE,"E4368"),sQuery(id+"F17.wireOp",EDGE,"E4369"),sQuery(id+"F17.wireOp",EDGE,"E4370"),sQuery(id+"F17.wireOp",EDGE,"E4371"),sQuery(id+"F17.wireOp",EDGE,"E4372"),sQuery(id+"F17.wireOp",EDGE,"E4373"),sQuery(id+"F17.wireOp",EDGE,"E4374"),sQuery(id+"F17.wireOp",EDGE,"E4375"),sQuery(id+"F17.wireOp",EDGE,"E4376"),sQuery(id+"F17.wireOp",EDGE,"E4377"),sQuery(id+"F17.wireOp",EDGE,"E4378"),sQuery(id+"F17.wireOp",EDGE,"E4379"),sQuery(id+"F17.wireOp",EDGE,"E4380"),sQuery(id+"F17.wireOp",EDGE,"E4381"),sQuery(id+"F17.wireOp",EDGE,"E4382"),sQuery(id+"F17.wireOp",EDGE,"E4383"),sQuery(id+"F17.wireOp",EDGE,"E4384"),sQuery(id+"F17.wireOp",EDGE,"E4385"),sQuery(id+"F17.wireOp",EDGE,"E4386"),sQuery(id+"F17.wireOp",EDGE,"E4387"),sQuery(id+"F17.wireOp",EDGE,"E4388"),sQuery(id+"F17.wireOp",EDGE,"E4389"),sQuery(id+"F17.wireOp",EDGE,"E4390"),sQuery(id+"F17.wireOp",EDGE,"E4391"),sQuery(id+"F17.wireOp",EDGE,"E4392"),sQuery(id+"F17.wireOp",EDGE,"E4393"),sQuery(id+"F17.wireOp",EDGE,"E4394"),sQuery(id+"F17.wireOp",EDGE,"E4395"),sQuery(id+"F17.wireOp",EDGE,"E4396"),sQuery(id+"F17.wireOp",EDGE,"E4397"),sQuery(id+"F17.wireOp",EDGE,"E4398"),sQuery(id+"F17.wireOp",EDGE,"E4399"),sQuery(id+"F17.wireOp",EDGE,"E4400"),sQuery(id+"F17.wireOp",EDGE,"E4401"),sQuery(id+"F17.wireOp",EDGE,"E4402"),sQuery(id+"F17.wireOp",EDGE,"E4403"),sQuery(id+"F17.wireOp",EDGE,"E4404"),sQuery(id+"F17.wireOp",EDGE,"E4405"),sQuery(id+"F17.wireOp",EDGE,"E4406"),sQuery(id+"F17.wireOp",EDGE,"E4407"),sQuery(id+"F17.wireOp",EDGE,"E4408"),sQuery(id+"F17.wireOp",EDGE,"E4409"),sQuery(id+"F17.wireOp",EDGE,"E4410"),sQuery(id+"F17.wireOp",EDGE,"E4411"),sQuery(id+"F17.wireOp",EDGE,"E4412"),sQuery(id+"F17.wireOp",EDGE,"E4413"),sQuery(id+"F17.wireOp",EDGE,"E4414"),sQuery(id+"F17.wireOp",EDGE,"E4415"),sQuery(id+"F17.wireOp",EDGE,"E4416"),sQuery(id+"F17.wireOp",EDGE,"E4417"),sQuery(id+"F17.wireOp",EDGE,"E4418"),sQuery(id+"F17.wireOp",EDGE,"E4419"),sQuery(id+"F17.wireOp",EDGE,"E4420"),sQuery(id+"F17.wireOp",EDGE,"E4421"),sQuery(id+"F17.wireOp",EDGE,"E4422"),sQuery(id+"F17.wireOp",EDGE,"E4423"),sQuery(id+"F17.wireOp",EDGE,"E4424"),sQuery(id+"F17.wireOp",EDGE,"E4425"),sQuery(id+"F17.wireOp",EDGE,"E4426"),sQuery(id+"F17.wireOp",EDGE,"E4427"),sQuery(id+"F17.wireOp",EDGE,"E4428"),sQuery(id+"F17.wireOp",EDGE,"E4429"),sQuery(id+"F17.wireOp",EDGE,"E4430"),sQuery(id+"F17.wireOp",EDGE,"E4431"),sQuery(id+"F17.wireOp",EDGE,"E4432"),sQuery(id+"F17.wireOp",EDGE,"E4433"),sQuery(id+"F17.wireOp",EDGE,"E4434"),sQuery(id+"F17.wireOp",EDGE,"E4435"),sQuery(id+"F17.wireOp",EDGE,"E4436"),sQuery(id+"F17.wireOp",EDGE,"E4437"),sQuery(id+"F17.wireOp",EDGE,"E4438"),sQuery(id+"F17.wireOp",EDGE,"E4439"),sQuery(id+"F17.wireOp",EDGE,"E4440"),sQuery(id+"F17.wireOp",EDGE,"E4441"),sQuery(id+"F17.wireOp",EDGE,"E4442"),sQuery(id+"F17.wireOp",EDGE,"E4443"),sQuery(id+"F17.wireOp",EDGE,"E4444"),sQuery(id+"F17.wireOp",EDGE,"E4445"),sQuery(id+"F17.wireOp",EDGE,"E4446"),sQuery(id+"F17.wireOp",EDGE,"E4447"),sQuery(id+"F17.wireOp",EDGE,"E4448"),sQuery(id+"F17.wireOp",EDGE,"E4449"),sQuery(id+"F17.wireOp",EDGE,"E4450"),sQuery(id+"F17.wireOp",EDGE,"E4451"),sQuery(id+"F17.wireOp",EDGE,"E4452"),sQuery(id+"F17.wireOp",EDGE,"E4453"),sQuery(id+"F17.wireOp",EDGE,"E4454"),sQuery(id+"F17.wireOp",EDGE,"E4455"),sQuery(id+"F17.wireOp",EDGE,"E4456"),sQuery(id+"F17.wireOp",EDGE,"E4457"),sQuery(id+"F17.wireOp",EDGE,"E4458"),sQuery(id+"F17.wireOp",EDGE,"E4459"),sQuery(id+"F17.wireOp",EDGE,"E4460"),sQuery(id+"F17.wireOp",EDGE,"E4461"),sQuery(id+"F17.wireOp",EDGE,"E4462"),sQuery(id+"F17.wireOp",EDGE,"E4463"),sQuery(id+"F17.wireOp",EDGE,"E4464"),sQuery(id+"F17.wireOp",EDGE,"E4465"),sQuery(id+"F17.wireOp",EDGE,"E4466"),sQuery(id+"F17.wireOp",EDGE,"E4467"),sQuery(id+"F17.wireOp",EDGE,"E4468"),sQuery(id+"F17.wireOp",EDGE,"E4469"),sQuery(id+"F17.wireOp",EDGE,"E4470"),sQuery(id+"F17.wireOp",EDGE,"E4471"),sQuery(id+"F17.wireOp",EDGE,"E4472"),sQuery(id+"F17.wireOp",EDGE,"E4473"),sQuery(id+"F17.wireOp",EDGE,"E4474"),sQuery(id+"F17.wireOp",EDGE,"E4475"),sQuery(id+"F17.wireOp",EDGE,"E4476"),sQuery(id+"F17.wireOp",EDGE,"E4477"),sQuery(id+"F17.wireOp",EDGE,"E4478"),sQuery(id+"F17.wireOp",EDGE,"E4479"),sQuery(id+"F17.wireOp",EDGE,"E4480"),sQuery(id+"F17.wireOp",EDGE,"E4481"),sQuery(id+"F17.wireOp",EDGE,"E4482"),sQuery(id+"F17.wireOp",EDGE,"E4483"),sQuery(id+"F17.wireOp",EDGE,"E4484"),sQuery(id+"F17.wireOp",EDGE,"E4485"),sQuery(id+"F17.wireOp",EDGE,"E4486"),sQuery(id+"F17.wireOp",EDGE,"E4487"),sQuery(id+"F17.wireOp",EDGE,"E4488"),sQuery(id+"F17.wireOp",EDGE,"E4489"),sQuery(id+"F17.wireOp",EDGE,"E4490"),sQuery(id+"F17.wireOp",EDGE,"E4491"),sQuery(id+"F17.wireOp",EDGE,"E4492"),sQuery(id+"F17.wireOp",EDGE,"E4493"),sQuery(id+"F17.wireOp",EDGE,"E4494"),sQuery(id+"F17.wireOp",EDGE,"E4495"),sQuery(id+"F17.wireOp",EDGE,"E4496"),sQuery(id+"F17.wireOp",EDGE,"E4497"),sQuery(id+"F17.wireOp",EDGE,"E4498"),sQuery(id+"F17.wireOp",EDGE,"E4499"),sQuery(id+"F17.wireOp",EDGE,"E4500"),sQuery(id+"F17.wireOp",EDGE,"E4501"),sQuery(id+"F17.wireOp",EDGE,"E4502"),sQuery(id+"F17.wireOp",EDGE,"E4503"),sQuery(id+"F17.wireOp",EDGE,"E4504"),sQuery(id+"F17.wireOp",EDGE,"E4505"),sQuery(id+"F17.wireOp",EDGE,"E4506"),sQuery(id+"F17.wireOp",EDGE,"E4507"),sQuery(id+"F17.wireOp",EDGE,"E4508"),sQuery(id+"F17.wireOp",EDGE,"E4509"),sQuery(id+"F17.wireOp",EDGE,"E4510"),sQuery(id+"F17.wireOp",EDGE,"E4511"),sQuery(id+"F17.wireOp",EDGE,"E4512"),sQuery(id+"F17.wireOp",EDGE,"E4513"),sQuery(id+"F17.wireOp",EDGE,"E4514"),sQuery(id+"F17.wireOp",EDGE,"E4515"),sQuery(id+"F17.wireOp",EDGE,"E4516"),sQuery(id+"F17.wireOp",EDGE,"E4517"),sQuery(id+"F17.wireOp",EDGE,"E4518"),sQuery(id+"F17.wireOp",EDGE,"E4519"),sQuery(id+"F17.wireOp",EDGE,"E4520"),sQuery(id+"F17.wireOp",EDGE,"E4521"),sQuery(id+"F17.wireOp",EDGE,"E4522"),sQuery(id+"F17.wireOp",EDGE,"E4523"),sQuery(id+"F17.wireOp",EDGE,"E4524"),sQuery(id+"F17.wireOp",EDGE,"E4525"),sQuery(id+"F17.wireOp",EDGE,"E4526"),sQuery(id+"F17.wireOp",EDGE,"E4527"),sQuery(id+"F17.wireOp",EDGE,"E4528"),sQuery(id+"F17.wireOp",EDGE,"E4529"),sQuery(id+"F17.wireOp",EDGE,"E4530"),sQuery(id+"F17.wireOp",EDGE,"E4531"),sQuery(id+"F17.wireOp",EDGE,"E4532"),sQuery(id+"F17.wireOp",EDGE,"E4533"),sQuery(id+"F17.wireOp",EDGE,"E4534"),sQuery(id+"F17.wireOp",EDGE,"E4535"),sQuery(id+"F17.wireOp",EDGE,"E4536"),sQuery(id+"F17.wireOp",EDGE,"E4537"),sQuery(id+"F17.wireOp",EDGE,"E4538"),sQuery(id+"F17.wireOp",EDGE,"E4539"),sQuery(id+"F17.wireOp",EDGE,"E4540"),sQuery(id+"F17.wireOp",EDGE,"E4541"),sQuery(id+"F17.wireOp",EDGE,"E4542"),sQuery(id+"F17.wireOp",EDGE,"E4543"),sQuery(id+"F17.wireOp",EDGE,"E4544"),sQuery(id+"F17.wireOp",EDGE,"E4545"),sQuery(id+"F17.wireOp",EDGE,"E4546"),sQuery(id+"F17.wireOp",EDGE,"E4547"),sQuery(id+"F17.wireOp",EDGE,"E4548"),sQuery(id+"F17.wireOp",EDGE,"E4549"),sQuery(id+"F17.wireOp",EDGE,"E4550"),sQuery(id+"F17.wireOp",EDGE,"E4551"),sQuery(id+"F17.wireOp",EDGE,"E4552"),sQuery(id+"F17.wireOp",EDGE,"E4553"),sQuery(id+"F17.wireOp",EDGE,"E4554"),sQuery(id+"F17.wireOp",EDGE,"E4555"),sQuery(id+"F17.wireOp",EDGE,"E4556"),sQuery(id+"F17.wireOp",EDGE,"E4557"),sQuery(id+"F17.wireOp",EDGE,"E4558"),sQuery(id+"F17.wireOp",EDGE,"E4559"),sQuery(id+"F17.wireOp",EDGE,"E4560"),sQuery(id+"F17.wireOp",EDGE,"E4561"),sQuery(id+"F17.wireOp",EDGE,"E4562"),sQuery(id+"F17.wireOp",EDGE,"E4563"),sQuery(id+"F17.wireOp",EDGE,"E4564"),sQuery(id+"F17.wireOp",EDGE,"E4565"),sQuery(id+"F17.wireOp",EDGE,"E4566"),sQuery(id+"F17.wireOp",EDGE,"E4567"),sQuery(id+"F17.wireOp",EDGE,"E4568"),sQuery(id+"F17.wireOp",EDGE,"E4569"),sQuery(id+"F17.wireOp",EDGE,"E4570"),sQuery(id+"F17.wireOp",EDGE,"E4571"),sQuery(id+"F17.wireOp",EDGE,"E4572"),sQuery(id+"F17.wireOp",EDGE,"E4573"),sQuery(id+"F17.wireOp",EDGE,"E4574"),sQuery(id+"F17.wireOp",EDGE,"E4575"),sQuery(id+"F17.wireOp",EDGE,"E4576"),sQuery(id+"F17.wireOp",EDGE,"E4577"),sQuery(id+"F17.wireOp",EDGE,"E4578"),sQuery(id+"F17.wireOp",EDGE,"E4579"),sQuery(id+"F17.wireOp",EDGE,"E4580"),sQuery(id+"F17.wireOp",EDGE,"E4581"),sQuery(id+"F17.wireOp",EDGE,"E4582"),sQuery(id+"F17.wireOp",EDGE,"E4583"),sQuery(id+"F17.wireOp",EDGE,"E4584"),sQuery(id+"F17.wireOp",EDGE,"E4585"),sQuery(id+"F17.wireOp",EDGE,"E4586"),sQuery(id+"F17.wireOp",EDGE,"E4587"),sQuery(id+"F17.wireOp",EDGE,"E4588"),sQuery(id+"F17.wireOp",EDGE,"E4589"),sQuery(id+"F17.wireOp",EDGE,"E4590"),sQuery(id+"F17.wireOp",EDGE,"E4591"),sQuery(id+"F17.wireOp",EDGE,"E4592"),sQuery(id+"F17.wireOp",EDGE,"E4593"),sQuery(id+"F17.wireOp",EDGE,"E4594"),sQuery(id+"F17.wireOp",EDGE,"E4595"),sQuery(id+"F17.wireOp",EDGE,"E4596"),sQuery(id+"F17.wireOp",EDGE,"E4597"),sQuery(id+"F17.wireOp",EDGE,"E4598"),sQuery(id+"F17.wireOp",EDGE,"E4599"),sQuery(id+"F17.wireOp",EDGE,"E4600"),sQuery(id+"F17.wireOp",EDGE,"E4601"),sQuery(id+"F17.wireOp",EDGE,"E4602"),sQuery(id+"F17.wireOp",EDGE,"E4603"),sQuery(id+"F17.wireOp",EDGE,"E4604"),sQuery(id+"F17.wireOp",EDGE,"E4605"),sQuery(id+"F17.wireOp",EDGE,"E4606"),sQuery(id+"F17.wireOp",EDGE,"E4607"),sQuery(id+"F17.wireOp",EDGE,"E4608"),sQuery(id+"F17.wireOp",EDGE,"E4609"),sQuery(id+"F17.wireOp",EDGE,"E4610"),sQuery(id+"F17.wireOp",EDGE,"E4611"),sQuery(id+"F17.wireOp",EDGE,"E4612"),sQuery(id+"F17.wireOp",EDGE,"E4613"),sQuery(id+"F17.wireOp",EDGE,"E4614"),sQuery(id+"F17.wireOp",EDGE,"E4615"),sQuery(id+"F17.wireOp",EDGE,"E4616"),sQuery(id+"F17.wireOp",EDGE,"E4617"),sQuery(id+"F17.wireOp",EDGE,"E4618"),sQuery(id+"F17.wireOp",EDGE,"E4619"),sQuery(id+"F17.wireOp",EDGE,"E4620"),sQuery(id+"F17.wireOp",EDGE,"E4621"),sQuery(id+"F17.wireOp",EDGE,"E4622"),sQuery(id+"F17.wireOp",EDGE,"E4623"),sQuery(id+"F17.wireOp",EDGE,"E4624"),sQuery(id+"F17.wireOp",EDGE,"E4625"),sQuery(id+"F17.wireOp",EDGE,"E4626"),sQuery(id+"F17.wireOp",EDGE,"E4627"),sQuery(id+"F17.wireOp",EDGE,"E4628"),sQuery(id+"F17.wireOp",EDGE,"E4629"),sQuery(id+"F17.wireOp",EDGE,"E4630"),sQuery(id+"F17.wireOp",EDGE,"E4631"),sQuery(id+"F17.wireOp",EDGE,"E4632"),sQuery(id+"F17.wireOp",EDGE,"E4633"),sQuery(id+"F17.wireOp",EDGE,"E4634"),sQuery(id+"F17.wireOp",EDGE,"E4635"),sQuery(id+"F17.wireOp",EDGE,"E4636"),sQuery(id+"F17.wireOp",EDGE,"E4637"),sQuery(id+"F17.wireOp",EDGE,"E4638"),sQuery(id+"F17.wireOp",EDGE,"E4639"),sQuery(id+"F17.wireOp",EDGE,"E4640"),sQuery(id+"F17.wireOp",EDGE,"E4641"),sQuery(id+"F17.wireOp",EDGE,"E4642"),sQuery(id+"F17.wireOp",EDGE,"E4643"),sQuery(id+"F17.wireOp",EDGE,"E4644"),sQuery(id+"F17.wireOp",EDGE,"E4645"),sQuery(id+"F17.wireOp",EDGE,"E4646"),sQuery(id+"F17.wireOp",EDGE,"E4647"),sQuery(id+"F17.wireOp",EDGE,"E4648"),sQuery(id+"F17.wireOp",EDGE,"E4649"),sQuery(id+"F17.wireOp",EDGE,"E4650"),sQuery(id+"F17.wireOp",EDGE,"E4651"),sQuery(id+"F17.wireOp",EDGE,"E4652"),sQuery(id+"F17.wireOp",EDGE,"E4653"),sQuery(id+"F17.wireOp",EDGE,"E4654"),sQuery(id+"F17.wireOp",EDGE,"E4655"),sQuery(id+"F17.wireOp",EDGE,"E4656"),sQuery(id+"F17.wireOp",EDGE,"E4657"),sQuery(id+"F17.wireOp",EDGE,"E4658"),sQuery(id+"F17.wireOp",EDGE,"E4659"),sQuery(id+"F17.wireOp",EDGE,"E4660"),sQuery(id+"F17.wireOp",EDGE,"E4661"),sQuery(id+"F17.wireOp",EDGE,"E4662"),sQuery(id+"F17.wireOp",EDGE,"E4663"),sQuery(id+"F17.wireOp",EDGE,"E4664"),sQuery(id+"F17.wireOp",EDGE,"E4665"),sQuery(id+"F17.wireOp",EDGE,"E4666"),sQuery(id+"F17.wireOp",EDGE,"E4667"),sQuery(id+"F17.wireOp",EDGE,"E4668"),sQuery(id+"F17.wireOp",EDGE,"E4669"),sQuery(id+"F17.wireOp",EDGE,"E4670"),sQuery(id+"F17.wireOp",EDGE,"E4671"),sQuery(id+"F17.wireOp",EDGE,"E4672"),sQuery(id+"F17.wireOp",EDGE,"E4673"),sQuery(id+"F17.wireOp",EDGE,"E4674"),sQuery(id+"F17.wireOp",EDGE,"E4675"),sQuery(id+"F17.wireOp",EDGE,"E4676"),sQuery(id+"F17.wireOp",EDGE,"E4677"),sQuery(id+"F17.wireOp",EDGE,"E4678"),sQuery(id+"F17.wireOp",EDGE,"E4679"),sQuery(id+"F17.wireOp",EDGE,"E4680"),sQuery(id+"F17.wireOp",EDGE,"E4681"),sQuery(id+"F17.wireOp",EDGE,"E4682"),sQuery(id+"F17.wireOp",EDGE,"E4683"),sQuery(id+"F17.wireOp",EDGE,"E4684"),sQuery(id+"F17.wireOp",EDGE,"E4685"),sQuery(id+"F17.wireOp",EDGE,"E4686"),sQuery(id+"F17.wireOp",EDGE,"E4687"),sQuery(id+"F17.wireOp",EDGE,"E4688"),sQuery(id+"F17.wireOp",EDGE,"E4689"),sQuery(id+"F17.wireOp",EDGE,"E4690"),sQuery(id+"F17.wireOp",EDGE,"E4691"),sQuery(id+"F17.wireOp",EDGE,"E4692"),sQuery(id+"F17.wireOp",EDGE,"E4693"),sQuery(id+"F17.wireOp",EDGE,"E4694"),sQuery(id+"F17.wireOp",EDGE,"E4695"),sQuery(id+"F17.wireOp",EDGE,"E4696"),sQuery(id+"F17.wireOp",EDGE,"E4697"),sQuery(id+"F17.wireOp",EDGE,"E4698"),sQuery(id+"F17.wireOp",EDGE,"E4699"),sQuery(id+"F17.wireOp",EDGE,"E4700"),sQuery(id+"F17.wireOp",EDGE,"E4701"),sQuery(id+"F17.wireOp",EDGE,"E4702"),sQuery(id+"F17.wireOp",EDGE,"E4703"),sQuery(id+"F17.wireOp",EDGE,"E4704"),sQuery(id+"F17.wireOp",EDGE,"E4705"),sQuery(id+"F17.wireOp",EDGE,"E4706"),sQuery(id+"F17.wireOp",EDGE,"E4707"),sQuery(id+"F17.wireOp",EDGE,"E4708"),sQuery(id+"F17.wireOp",EDGE,"E4709"),sQuery(id+"F17.wireOp",EDGE,"E4710"),sQuery(id+"F17.wireOp",EDGE,"E4711"),sQuery(id+"F17.wireOp",EDGE,"E4712"),sQuery(id+"F17.wireOp",EDGE,"E4713"),sQuery(id+"F17.wireOp",EDGE,"E4714"),sQuery(id+"F17.wireOp",EDGE,"E4715"),sQuery(id+"F17.wireOp",EDGE,"E4716"),sQuery(id+"F17.wireOp",EDGE,"E4717"),sQuery(id+"F17.wireOp",EDGE,"E4718"),sQuery(id+"F17.wireOp",EDGE,"E4719"),sQuery(id+"F17.wireOp",EDGE,"E4720"),sQuery(id+"F17.wireOp",EDGE,"E4721"),sQuery(id+"F17.wireOp",EDGE,"E4722"),sQuery(id+"F17.wireOp",EDGE,"E4723"),sQuery(id+"F17.wireOp",EDGE,"E4724"),sQuery(id+"F17.wireOp",EDGE,"E4725"),sQuery(id+"F17.wireOp",EDGE,"E4726"),sQuery(id+"F17.wireOp",EDGE,"E4727"),sQuery(id+"F17.wireOp",EDGE,"E4728"),sQuery(id+"F17.wireOp",EDGE,"E4729"),sQuery(id+"F17.wireOp",EDGE,"E4730"),sQuery(id+"F17.wireOp",EDGE,"E4731"),sQuery(id+"F17.wireOp",EDGE,"E4732"),sQuery(id+"F17.wireOp",EDGE,"E4733"),sQuery(id+"F17.wireOp",EDGE,"E4734"),sQuery(id+"F17.wireOp",EDGE,"E4735"),sQuery(id+"F17.wireOp",EDGE,"E4736"),sQuery(id+"F17.wireOp",EDGE,"E4737"),sQuery(id+"F17.wireOp",EDGE,"E4738"),sQuery(id+"F17.wireOp",EDGE,"E4739"),sQuery(id+"F17.wireOp",EDGE,"E4740"),sQuery(id+"F17.wireOp",EDGE,"E4741"),sQuery(id+"F17.wireOp",EDGE,"E4742"),sQuery(id+"F17.wireOp",EDGE,"E4743"),sQuery(id+"F17.wireOp",EDGE,"E4744"),sQuery(id+"F17.wireOp",EDGE,"E4745"),sQuery(id+"F17.wireOp",EDGE,"E4746"),sQuery(id+"F17.wireOp",EDGE,"E4747"),sQuery(id+"F17.wireOp",EDGE,"E4748"),sQuery(id+"F17.wireOp",EDGE,"E4749"),sQuery(id+"F17.wireOp",EDGE,"E4750"),sQuery(id+"F17.wireOp",EDGE,"E4751"),sQuery(id+"F17.wireOp",EDGE,"E4752"),sQuery(id+"F17.wireOp",EDGE,"E4753"),sQuery(id+"F17.wireOp",EDGE,"E4754"),sQuery(id+"F17.wireOp",EDGE,"E4755"),sQuery(id+"F17.wireOp",EDGE,"E4756"),sQuery(id+"F17.wireOp",EDGE,"E4757"),sQuery(id+"F17.wireOp",EDGE,"E4758"),sQuery(id+"F17.wireOp",EDGE,"E4759"),sQuery(id+"F17.wireOp",EDGE,"E4760"),sQuery(id+"F17.wireOp",EDGE,"E4761"),sQuery(id+"F17.wireOp",EDGE,"E4762"),sQuery(id+"F17.wireOp",EDGE,"E4763"),sQuery(id+"F17.wireOp",EDGE,"E4764"),sQuery(id+"F17.wireOp",EDGE,"E4765"),sQuery(id+"F17.wireOp",EDGE,"E4766"),sQuery(id+"F17.wireOp",EDGE,"E4767"),sQuery(id+"F17.wireOp",EDGE,"E4768"),sQuery(id+"F17.wireOp",EDGE,"E4769"),sQuery(id+"F17.wireOp",EDGE,"E4770"),sQuery(id+"F17.wireOp",EDGE,"E4771"),sQuery(id+"F17.wireOp",EDGE,"E4772"),sQuery(id+"F17.wireOp",EDGE,"E4773"),sQuery(id+"F17.wireOp",EDGE,"E4774"),sQuery(id+"F17.wireOp",EDGE,"E4775"),sQuery(id+"F17.wireOp",EDGE,"E4776"),sQuery(id+"F17.wireOp",EDGE,"E4777"),sQuery(id+"F17.wireOp",EDGE,"E4778"),sQuery(id+"F17.wireOp",EDGE,"E4779"),sQuery(id+"F17.wireOp",EDGE,"E4780"),sQuery(id+"F17.wireOp",EDGE,"E4781"),sQuery(id+"F17.wireOp",EDGE,"E4782"),sQuery(id+"F17.wireOp",EDGE,"E4783"),sQuery(id+"F17.wireOp",EDGE,"E4784"),sQuery(id+"F17.wireOp",EDGE,"E4785"),sQuery(id+"F17.wireOp",EDGE,"E4786"),sQuery(id+"F17.wireOp",EDGE,"E4787"),sQuery(id+"F17.wireOp",EDGE,"E4788"),sQuery(id+"F17.wireOp",EDGE,"E4789"),sQuery(id+"F17.wireOp",EDGE,"E4790"),sQuery(id+"F17.wireOp",EDGE,"E4791"),sQuery(id+"F17.wireOp",EDGE,"E4792"),sQuery(id+"F17.wireOp",EDGE,"E4793"),sQuery(id+"F17.wireOp",EDGE,"E4794"),sQuery(id+"F17.wireOp",EDGE,"E4795"),sQuery(id+"F17.wireOp",EDGE,"E4796"),sQuery(id+"F17.wireOp",EDGE,"E4797"),sQuery(id+"F17.wireOp",EDGE,"E4798"),sQuery(id+"F17.wireOp",EDGE,"E4799"),sQuery(id+"F17.wireOp",EDGE,"E4800"),sQuery(id+"F17.wireOp",EDGE,"E4801"),sQuery(id+"F17.wireOp",EDGE,"E4802"),sQuery(id+"F17.wireOp",EDGE,"E4803"),sQuery(id+"F17.wireOp",EDGE,"E4804"),sQuery(id+"F17.wireOp",EDGE,"E4805"),sQuery(id+"F17.wireOp",EDGE,"E4806"),sQuery(id+"F17.wireOp",EDGE,"E4807"),sQuery(id+"F17.wireOp",EDGE,"E4808"),sQuery(id+"F17.wireOp",EDGE,"E4809"),sQuery(id+"F17.wireOp",EDGE,"E4810"),sQuery(id+"F17.wireOp",EDGE,"E4811"),sQuery(id+"F17.wireOp",EDGE,"E4812"),sQuery(id+"F17.wireOp",EDGE,"E4813"),sQuery(id+"F17.wireOp",EDGE,"E4814"),sQuery(id+"F17.wireOp",EDGE,"E4815"),sQuery(id+"F17.wireOp",EDGE,"E4816"),sQuery(id+"F17.wireOp",EDGE,"E4817"),sQuery(id+"F17.wireOp",EDGE,"E4818"),sQuery(id+"F17.wireOp",EDGE,"E4819"),sQuery(id+"F17.wireOp",EDGE,"E4820"),sQuery(id+"F17.wireOp",EDGE,"E4821"),sQuery(id+"F17.wireOp",EDGE,"E4822"),sQuery(id+"F17.wireOp",EDGE,"E4823"),sQuery(id+"F17.wireOp",EDGE,"E4824"),sQuery(id+"F17.wireOp",EDGE,"E4825"),sQuery(id+"F17.wireOp",EDGE,"E4826"),sQuery(id+"F17.wireOp",EDGE,"E4827"),sQuery(id+"F17.wireOp",EDGE,"E4828"),sQuery(id+"F17.wireOp",EDGE,"E4829"),sQuery(id+"F17.wireOp",EDGE,"E4830"),sQuery(id+"F17.wireOp",EDGE,"E4831"),sQuery(id+"F17.wireOp",EDGE,"E4832"),sQuery(id+"F17.wireOp",EDGE,"E4833"),sQuery(id+"F17.wireOp",EDGE,"E4834"),sQuery(id+"F17.wireOp",EDGE,"E4835"),sQuery(id+"F17.wireOp",EDGE,"E4836"),sQuery(id+"F17.wireOp",EDGE,"E4837"),sQuery(id+"F17.wireOp",EDGE,"E4838"),sQuery(id+"F17.wireOp",EDGE,"E4839"),sQuery(id+"F17.wireOp",EDGE,"E4840"),sQuery(id+"F17.wireOp",EDGE,"E4841"),sQuery(id+"F17.wireOp",EDGE,"E4842"),sQuery(id+"F17.wireOp",EDGE,"E4843"),sQuery(id+"F17.wireOp",EDGE,"E4844"),sQuery(id+"F17.wireOp",EDGE,"E4845"),sQuery(id+"F17.wireOp",EDGE,"E4846"),sQuery(id+"F17.wireOp",EDGE,"E4847"),sQuery(id+"F17.wireOp",EDGE,"E4848"),sQuery(id+"F17.wireOp",EDGE,"E4849"),sQuery(id+"F17.wireOp",EDGE,"E4850"),sQuery(id+"F17.wireOp",EDGE,"E4851"),sQuery(id+"F17.wireOp",EDGE,"E4852"),sQuery(id+"F17.wireOp",EDGE,"E4853"),sQuery(id+"F17.wireOp",EDGE,"E4854"),sQuery(id+"F17.wireOp",EDGE,"E4855"),sQuery(id+"F17.wireOp",EDGE,"E4856"),sQuery(id+"F17.wireOp",EDGE,"E4857"),sQuery(id+"F17.wireOp",EDGE,"E4858"),sQuery(id+"F17.wireOp",EDGE,"E4859"),sQuery(id+"F17.wireOp",EDGE,"E4860"),sQuery(id+"F17.wireOp",EDGE,"E4861"),sQuery(id+"F17.wireOp",EDGE,"E4862"),sQuery(id+"F17.wireOp",EDGE,"E4863"),sQuery(id+"F17.wireOp",EDGE,"E4864"),sQuery(id+"F17.wireOp",EDGE,"E4865"),sQuery(id+"F17.wireOp",EDGE,"E4866"),sQuery(id+"F17.wireOp",EDGE,"E4867"),sQuery(id+"F17.wireOp",EDGE,"E4868"),sQuery(id+"F17.wireOp",EDGE,"E4869"),sQuery(id+"F17.wireOp",EDGE,"E4870"),sQuery(id+"F17.wireOp",EDGE,"E4871"),sQuery(id+"F17.wireOp",EDGE,"E4872"),sQuery(id+"F17.wireOp",EDGE,"E4873"),sQuery(id+"F17.wireOp",EDGE,"E4874"),sQuery(id+"F17.wireOp",EDGE,"E4875"),sQuery(id+"F17.wireOp",EDGE,"E4876"),sQuery(id+"F17.wireOp",EDGE,"E4877"),sQuery(id+"F17.wireOp",EDGE,"E4878"),sQuery(id+"F17.wireOp",EDGE,"E4879"),sQuery(id+"F17.wireOp",EDGE,"E4880"),sQuery(id+"F17.wireOp",EDGE,"E4881"),sQuery(id+"F17.wireOp",EDGE,"E4882"),sQuery(id+"F17.wireOp",EDGE,"E4883"),sQuery(id+"F17.wireOp",EDGE,"E4884"),sQuery(id+"F17.wireOp",EDGE,"E4885"),sQuery(id+"F17.wireOp",EDGE,"E4886"),sQuery(id+"F17.wireOp",EDGE,"E4887"),sQuery(id+"F17.wireOp",EDGE,"E4888"),sQuery(id+"F17.wireOp",EDGE,"E4889"),sQuery(id+"F17.wireOp",EDGE,"E4890"),sQuery(id+"F17.wireOp",EDGE,"E4891"),sQuery(id+"F17.wireOp",EDGE,"E4892"),sQuery(id+"F17.wireOp",EDGE,"E4893"),sQuery(id+"F17.wireOp",EDGE,"E4894"),sQuery(id+"F17.wireOp",EDGE,"E4895"),sQuery(id+"F17.wireOp",EDGE,"E4896"),sQuery(id+"F17.wireOp",EDGE,"E4897"),sQuery(id+"F17.wireOp",EDGE,"E4898"),sQuery(id+"F17.wireOp",EDGE,"E4899"),sQuery(id+"F17.wireOp",EDGE,"E4900"),sQuery(id+"F17.wireOp",EDGE,"E4901"),sQuery(id+"F17.wireOp",EDGE,"E4902"),sQuery(id+"F17.wireOp",EDGE,"E4903"),sQuery(id+"F17.wireOp",EDGE,"E4904"),sQuery(id+"F17.wireOp",EDGE,"E4905"),sQuery(id+"F17.wireOp",EDGE,"E4906"),sQuery(id+"F17.wireOp",EDGE,"E4907"),sQuery(id+"F17.wireOp",EDGE,"E4908"),sQuery(id+"F17.wireOp",EDGE,"E4909"),sQuery(id+"F17.wireOp",EDGE,"E4910"),sQuery(id+"F17.wireOp",EDGE,"E4911"),sQuery(id+"F17.wireOp",EDGE,"E4912"),sQuery(id+"F17.wireOp",EDGE,"E4913"),sQuery(id+"F17.wireOp",EDGE,"E4914"),sQuery(id+"F17.wireOp",EDGE,"E4915"),sQuery(id+"F17.wireOp",EDGE,"E4916"),sQuery(id+"F17.wireOp",EDGE,"E4917"),sQuery(id+"F17.wireOp",EDGE,"E4918"),sQuery(id+"F17.wireOp",EDGE,"E4919"),sQuery(id+"F17.wireOp",EDGE,"E4920"),sQuery(id+"F17.wireOp",EDGE,"E4921"),sQuery(id+"F17.wireOp",EDGE,"E4922"),sQuery(id+"F17.wireOp",EDGE,"E4923"),sQuery(id+"F17.wireOp",EDGE,"E4924"),sQuery(id+"F17.wireOp",EDGE,"E4925"),sQuery(id+"F17.wireOp",EDGE,"E4926"),sQuery(id+"F17.wireOp",EDGE,"E4927"),sQuery(id+"F17.wireOp",EDGE,"E4928"),sQuery(id+"F17.wireOp",EDGE,"E4929"),sQuery(id+"F17.wireOp",EDGE,"E4930"),sQuery(id+"F17.wireOp",EDGE,"E4931"),sQuery(id+"F17.wireOp",EDGE,"E4932"),sQuery(id+"F17.wireOp",EDGE,"E4933"),sQuery(id+"F17.wireOp",EDGE,"E4934"),sQuery(id+"F17.wireOp",EDGE,"E4935"),sQuery(id+"F17.wireOp",EDGE,"E4936"),sQuery(id+"F17.wireOp",EDGE,"E4937"),sQuery(id+"F17.wireOp",EDGE,"E4938"),sQuery(id+"F17.wireOp",EDGE,"E4939"),sQuery(id+"F17.wireOp",EDGE,"E4940"),sQuery(id+"F17.wireOp",EDGE,"E4941"),sQuery(id+"F17.wireOp",EDGE,"E4942"),sQuery(id+"F17.wireOp",EDGE,"E4943"),sQuery(id+"F17.wireOp",EDGE,"E4944"),sQuery(id+"F17.wireOp",EDGE,"E4945"),sQuery(id+"F17.wireOp",EDGE,"E4946"),sQuery(id+"F17.wireOp",EDGE,"E4947"),sQuery(id+"F17.wireOp",EDGE,"E4948"),sQuery(id+"F17.wireOp",EDGE,"E4949"),sQuery(id+"F17.wireOp",EDGE,"E4950"),sQuery(id+"F17.wireOp",EDGE,"E4951"),sQuery(id+"F17.wireOp",EDGE,"E4952"),sQuery(id+"F17.wireOp",EDGE,"E4953"),sQuery(id+"F17.wireOp",EDGE,"E4954"),sQuery(id+"F17.wireOp",EDGE,"E4955"),sQuery(id+"F17.wireOp",EDGE,"E4956"),sQuery(id+"F17.wireOp",EDGE,"E4957"),sQuery(id+"F17.wireOp",EDGE,"E4958"),sQuery(id+"F17.wireOp",EDGE,"E4959"),sQuery(id+"F17.wireOp",EDGE,"E4960"),sQuery(id+"F17.wireOp",EDGE,"E4961"),sQuery(id+"F17.wireOp",EDGE,"E4962"),sQuery(id+"F17.wireOp",EDGE,"E4963"),sQuery(id+"F17.wireOp",EDGE,"E4964"),sQuery(id+"F17.wireOp",EDGE,"E4965"),sQuery(id+"F17.wireOp",EDGE,"E4966"),sQuery(id+"F17.wireOp",EDGE,"E4967"),sQuery(id+"F17.wireOp",EDGE,"E4968"),sQuery(id+"F17.wireOp",EDGE,"E4969"),sQuery(id+"F17.wireOp",EDGE,"E4970"),sQuery(id+"F17.wireOp",EDGE,"E4971"),sQuery(id+"F17.wireOp",EDGE,"E4972"),sQuery(id+"F17.wireOp",EDGE,"E4973"),sQuery(id+"F17.wireOp",EDGE,"E4974"),sQuery(id+"F17.wireOp",EDGE,"E4975"),sQuery(id+"F17.wireOp",EDGE,"E4976"),sQuery(id+"F17.wireOp",EDGE,"E4977"),sQuery(id+"F17.wireOp",EDGE,"E4978"),sQuery(id+"F17.wireOp",EDGE,"E4979"),sQuery(id+"F17.wireOp",EDGE,"E4980"),sQuery(id+"F17.wireOp",EDGE,"E4981"),sQuery(id+"F17.wireOp",EDGE,"E4982"),sQuery(id+"F17.wireOp",EDGE,"E4983"),sQuery(id+"F17.wireOp",EDGE,"E4984"),sQuery(id+"F17.wireOp",EDGE,"E4985"),sQuery(id+"F17.wireOp",EDGE,"E4986"),sQuery(id+"F17.wireOp",EDGE,"E4987"),sQuery(id+"F17.wireOp",EDGE,"E4988"),sQuery(id+"F17.wireOp",EDGE,"E4989"),sQuery(id+"F17.wireOp",EDGE,"E4990"),sQuery(id+"F17.wireOp",EDGE,"E4991"),sQuery(id+"F17.wireOp",EDGE,"E4992"),sQuery(id+"F17.wireOp",EDGE,"E4993"),sQuery(id+"F17.wireOp",EDGE,"E4994"),sQuery(id+"F17.wireOp",EDGE,"E4995"),sQuery(id+"F17.wireOp",EDGE,"E4996"),sQuery(id+"F17.wireOp",EDGE,"E4997"),sQuery(id+"F17.wireOp",EDGE,"E4998"),sQuery(id+"F17.wireOp",EDGE,"E4999"),sQuery(id+"F17.wireOp",EDGE,"E5000"),sQuery(id+"F17.wireOp",EDGE,"E5001"),sQuery(id+"F17.wireOp",EDGE,"E5002"),sQuery(id+"F17.wireOp",EDGE,"E5003"),sQuery(id+"F17.wireOp",EDGE,"E5004"),sQuery(id+"F17.wireOp",EDGE,"E5005"),sQuery(id+"F17.wireOp",EDGE,"E5006"),sQuery(id+"F17.wireOp",EDGE,"E5007"),sQuery(id+"F17.wireOp",EDGE,"E5008"),sQuery(id+"F17.wireOp",EDGE,"E5009"),sQuery(id+"F17.wireOp",EDGE,"E5010"),sQuery(id+"F17.wireOp",EDGE,"E5011"),sQuery(id+"F17.wireOp",EDGE,"E5012"),sQuery(id+"F17.wireOp",EDGE,"E5013"),sQuery(id+"F17.wireOp",EDGE,"E5014"),sQuery(id+"F17.wireOp",EDGE,"E5015"),sQuery(id+"F17.wireOp",EDGE,"E5016"),sQuery(id+"F17.wireOp",EDGE,"E5017"),sQuery(id+"F17.wireOp",EDGE,"E5018"),sQuery(id+"F17.wireOp",EDGE,"E5019"),sQuery(id+"F17.wireOp",EDGE,"E5020"),sQuery(id+"F17.wireOp",EDGE,"E5021"),sQuery(id+"F17.wireOp",EDGE,"E5022"),sQuery(id+"F17.wireOp",EDGE,"E5023"),sQuery(id+"F17.wireOp",EDGE,"E5024"),sQuery(id+"F17.wireOp",EDGE,"E5025"),sQuery(id+"F17.wireOp",EDGE,"E5026"),sQuery(id+"F17.wireOp",EDGE,"E5027"),sQuery(id+"F17.wireOp",EDGE,"E5028"),sQuery(id+"F17.wireOp",EDGE,"E5029"),sQuery(id+"F17.wireOp",EDGE,"E5030"),sQuery(id+"F17.wireOp",EDGE,"E5031"),sQuery(id+"F17.wireOp",EDGE,"E5032"),sQuery(id+"F17.wireOp",EDGE,"E5033"),sQuery(id+"F17.wireOp",EDGE,"E5034"),sQuery(id+"F17.wireOp",EDGE,"E5035"),sQuery(id+"F17.wireOp",EDGE,"E5036"),sQuery(id+"F17.wireOp",EDGE,"E5037"),sQuery(id+"F17.wireOp",EDGE,"E5038"),sQuery(id+"F17.wireOp",EDGE,"E5039"),sQuery(id+"F17.wireOp",EDGE,"E5040"),sQuery(id+"F17.wireOp",EDGE,"E5041"),sQuery(id+"F17.wireOp",EDGE,"E5042"),sQuery(id+"F17.wireOp",EDGE,"E5043"),sQuery(id+"F17.wireOp",EDGE,"E5044"),sQuery(id+"F17.wireOp",EDGE,"E5045"),sQuery(id+"F17.wireOp",EDGE,"E5046"),sQuery(id+"F17.wireOp",EDGE,"E5047"),sQuery(id+"F17.wireOp",EDGE,"E5048"),sQuery(id+"F17.wireOp",EDGE,"E5049"),sQuery(id+"F17.wireOp",EDGE,"E5050"),sQuery(id+"F17.wireOp",EDGE,"E5051"),sQuery(id+"F17.wireOp",EDGE,"E5052"),sQuery(id+"F17.wireOp",EDGE,"E5053"),sQuery(id+"F17.wireOp",EDGE,"E5054"),sQuery(id+"F17.wireOp",EDGE,"E5055"),sQuery(id+"F17.wireOp",EDGE,"E5056"),sQuery(id+"F17.wireOp",EDGE,"E5057"),sQuery(id+"F17.wireOp",EDGE,"E5058"),sQuery(id+"F17.wireOp",EDGE,"E5059"),sQuery(id+"F17.wireOp",EDGE,"E5060"),sQuery(id+"F17.wireOp",EDGE,"E5061"),sQuery(id+"F17.wireOp",EDGE,"E5062"),sQuery(id+"F17.wireOp",EDGE,"E5063"),sQuery(id+"F17.wireOp",EDGE,"E5064"),sQuery(id+"F17.wireOp",EDGE,"E5065"),sQuery(id+"F17.wireOp",EDGE,"E5066"),sQuery(id+"F17.wireOp",EDGE,"E5067"),sQuery(id+"F17.wireOp",EDGE,"E5068"),sQuery(id+"F17.wireOp",EDGE,"E5069"),sQuery(id+"F17.wireOp",EDGE,"E5070"),sQuery(id+"F17.wireOp",EDGE,"E5071"),sQuery(id+"F17.wireOp",EDGE,"E5072"),sQuery(id+"F17.wireOp",EDGE,"E5073"),sQuery(id+"F17.wireOp",EDGE,"E5074"),sQuery(id+"F17.wireOp",EDGE,"E5075"),sQuery(id+"F17.wireOp",EDGE,"E5076"),sQuery(id+"F17.wireOp",EDGE,"E5077"),sQuery(id+"F17.wireOp",EDGE,"E5078"),sQuery(id+"F17.wireOp",EDGE,"E5079"),sQuery(id+"F17.wireOp",EDGE,"E5080"),sQuery(id+"F17.wireOp",EDGE,"E5081"),sQuery(id+"F17.wireOp",EDGE,"E5082"),sQuery(id+"F17.wireOp",EDGE,"E5083"),sQuery(id+"F17.wireOp",EDGE,"E5084"),sQuery(id+"F17.wireOp",EDGE,"E5085"),sQuery(id+"F17.wireOp",EDGE,"E5086"),sQuery(id+"F17.wireOp",EDGE,"E5087"),sQuery(id+"F17.wireOp",EDGE,"E5088"),sQuery(id+"F17.wireOp",EDGE,"E5089"),sQuery(id+"F17.wireOp",EDGE,"E5090"),sQuery(id+"F17.wireOp",EDGE,"E5091"),sQuery(id+"F17.wireOp",EDGE,"E5092"),sQuery(id+"F17.wireOp",EDGE,"E5093"),sQuery(id+"F17.wireOp",EDGE,"E5094"),sQuery(id+"F17.wireOp",EDGE,"E5095"),sQuery(id+"F17.wireOp",EDGE,"E5096"),sQuery(id+"F17.wireOp",EDGE,"E5097"),sQuery(id+"F17.wireOp",EDGE,"E5098"),sQuery(id+"F17.wireOp",EDGE,"E5099"),sQuery(id+"F17.wireOp",EDGE,"E5100"),sQuery(id+"F17.wireOp",EDGE,"E5101"),sQuery(id+"F17.wireOp",EDGE,"E5102"),sQuery(id+"F17.wireOp",EDGE,"E5103"),sQuery(id+"F17.wireOp",EDGE,"E5104"),sQuery(id+"F17.wireOp",EDGE,"E5105"),sQuery(id+"F17.wireOp",EDGE,"E5106"),sQuery(id+"F17.wireOp",EDGE,"E5107"),sQuery(id+"F17.wireOp",EDGE,"E5108"),sQuery(id+"F17.wireOp",EDGE,"E5109"),sQuery(id+"F17.wireOp",EDGE,"E5110"),sQuery(id+"F17.wireOp",EDGE,"E5111"),sQuery(id+"F17.wireOp",EDGE,"E5112"),sQuery(id+"F17.wireOp",EDGE,"E5113"),sQuery(id+"F17.wireOp",EDGE,"E5114"),sQuery(id+"F17.wireOp",EDGE,"E5115"),sQuery(id+"F17.wireOp",EDGE,"E5116"),sQuery(id+"F17.wireOp",EDGE,"E5117"),sQuery(id+"F17.wireOp",EDGE,"E5118"),sQuery(id+"F17.wireOp",EDGE,"E5119"),sQuery(id+"F17.wireOp",EDGE,"E5120"),sQuery(id+"F17.wireOp",EDGE,"E5121"),sQuery(id+"F17.wireOp",EDGE,"E5122"),sQuery(id+"F17.wireOp",EDGE,"E5123"),sQuery(id+"F17.wireOp",EDGE,"E5124"),sQuery(id+"F17.wireOp",EDGE,"E5125"),sQuery(id+"F17.wireOp",EDGE,"E5126"),sQuery(id+"F17.wireOp",EDGE,"E5127"),sQuery(id+"F17.wireOp",EDGE,"E5128"),sQuery(id+"F17.wireOp",EDGE,"E5129"),sQuery(id+"F17.wireOp",EDGE,"E5130"),sQuery(id+"F17.wireOp",EDGE,"E5131"),sQuery(id+"F17.wireOp",EDGE,"E5132"),sQuery(id+"F17.wireOp",EDGE,"E5133"),sQuery(id+"F17.wireOp",EDGE,"E5134"),sQuery(id+"F17.wireOp",EDGE,"E5135"),sQuery(id+"F17.wireOp",EDGE,"E5136"),sQuery(id+"F17.wireOp",EDGE,"E5137"),sQuery(id+"F17.wireOp",EDGE,"E5138"),sQuery(id+"F17.wireOp",EDGE,"E5139"),sQuery(id+"F17.wireOp",EDGE,"E5140"),sQuery(id+"F17.wireOp",EDGE,"E5141"),sQuery(id+"F17.wireOp",EDGE,"E5142"),sQuery(id+"F17.wireOp",EDGE,"E5143"),sQuery(id+"F17.wireOp",EDGE,"E5144"),sQuery(id+"F17.wireOp",EDGE,"E5145"),sQuery(id+"F17.wireOp",EDGE,"E5146"),sQuery(id+"F17.wireOp",EDGE,"E5147"),sQuery(id+"F17.wireOp",EDGE,"E5148"),sQuery(id+"F17.wireOp",EDGE,"E5149"),sQuery(id+"F17.wireOp",EDGE,"E5150"),sQuery(id+"F17.wireOp",EDGE,"E5151"),sQuery(id+"F17.wireOp",EDGE,"E5152"),sQuery(id+"F17.wireOp",EDGE,"E5153"),sQuery(id+"F17.wireOp",EDGE,"E5154"),sQuery(id+"F17.wireOp",EDGE,"E5155"),sQuery(id+"F17.wireOp",EDGE,"E5156"),sQuery(id+"F17.wireOp",EDGE,"E5157"),sQuery(id+"F17.wireOp",EDGE,"E5158"),sQuery(id+"F17.wireOp",EDGE,"E5159"),sQuery(id+"F17.wireOp",EDGE,"E5160"),sQuery(id+"F17.wireOp",EDGE,"E5161"),sQuery(id+"F17.wireOp",EDGE,"E5162"),sQuery(id+"F17.wireOp",EDGE,"E5163"),sQuery(id+"F17.wireOp",EDGE,"E5164"),sQuery(id+"F17.wireOp",EDGE,"E5165"),sQuery(id+"F17.wireOp",EDGE,"E5166"),sQuery(id+"F17.wireOp",EDGE,"E5167"),sQuery(id+"F17.wireOp",EDGE,"E5168"),sQuery(id+"F17.wireOp",EDGE,"E5169"),sQuery(id+"F17.wireOp",EDGE,"E5170"),sQuery(id+"F17.wireOp",EDGE,"E5171"),sQuery(id+"F17.wireOp",EDGE,"E5172"),sQuery(id+"F17.wireOp",EDGE,"E5173"),sQuery(id+"F17.wireOp",EDGE,"E5174"),sQuery(id+"F17.wireOp",EDGE,"E5175"),sQuery(id+"F17.wireOp",EDGE,"E5176"),sQuery(id+"F17.wireOp",EDGE,"E5177"),sQuery(id+"F17.wireOp",EDGE,"E5178"),sQuery(id+"F17.wireOp",EDGE,"E5179"),sQuery(id+"F17.wireOp",EDGE,"E5180"),sQuery(id+"F17.wireOp",EDGE,"E5181"),sQuery(id+"F17.wireOp",EDGE,"E5182"),sQuery(id+"F17.wireOp",EDGE,"E5183"),sQuery(id+"F17.wireOp",EDGE,"E5184"),sQuery(id+"F17.wireOp",EDGE,"E5185"),sQuery(id+"F17.wireOp",EDGE,"E5186"),sQuery(id+"F17.wireOp",EDGE,"E5187"),sQuery(id+"F17.wireOp",EDGE,"E5188"),sQuery(id+"F17.wireOp",EDGE,"E5189"),sQuery(id+"F17.wireOp",EDGE,"E5190"),sQuery(id+"F17.wireOp",EDGE,"E5191"),sQuery(id+"F17.wireOp",EDGE,"E5192"),sQuery(id+"F17.wireOp",EDGE,"E5193"),sQuery(id+"F17.wireOp",EDGE,"E5194"),sQuery(id+"F17.wireOp",EDGE,"E5195"),sQuery(id+"F17.wireOp",EDGE,"E5196"),sQuery(id+"F17.wireOp",EDGE,"E5197"),sQuery(id+"F17.wireOp",EDGE,"E5198"),sQuery(id+"F17.wireOp",EDGE,"E5199"),sQuery(id+"F17.wireOp",EDGE,"E5200"),sQuery(id+"F17.wireOp",EDGE,"E5201"),sQuery(id+"F17.wireOp",EDGE,"E5202"),sQuery(id+"F17.wireOp",EDGE,"E5203"),sQuery(id+"F17.wireOp",EDGE,"E5204"),sQuery(id+"F17.wireOp",EDGE,"E5205"),sQuery(id+"F17.wireOp",EDGE,"E5206"),sQuery(id+"F17.wireOp",EDGE,"E5207"),sQuery(id+"F17.wireOp",EDGE,"E5208"),sQuery(id+"F17.wireOp",EDGE,"E5209"),sQuery(id+"F17.wireOp",EDGE,"E5210"),sQuery(id+"F17.wireOp",EDGE,"E5211"),sQuery(id+"F17.wireOp",EDGE,"E5212"),sQuery(id+"F17.wireOp",EDGE,"E5213"),sQuery(id+"F17.wireOp",EDGE,"E5214"),sQuery(id+"F17.wireOp",EDGE,"E5215"),sQuery(id+"F17.wireOp",EDGE,"E5216"),sQuery(id+"F17.wireOp",EDGE,"E5217"),sQuery(id+"F17.wireOp",EDGE,"E5218"),sQuery(id+"F17.wireOp",EDGE,"E5219"),sQuery(id+"F17.wireOp",EDGE,"E5220"),sQuery(id+"F17.wireOp",EDGE,"E5221"),sQuery(id+"F17.wireOp",EDGE,"E5222"),sQuery(id+"F17.wireOp",EDGE,"E5223"),sQuery(id+"F17.wireOp",EDGE,"E5224"),sQuery(id+"F17.wireOp",EDGE,"E5225"),sQuery(id+"F17.wireOp",EDGE,"E5226"),sQuery(id+"F17.wireOp",EDGE,"E5227"),sQuery(id+"F17.wireOp",EDGE,"E5228"),sQuery(id+"F17.wireOp",EDGE,"E5229"),sQuery(id+"F17.wireOp",EDGE,"E5230"),sQuery(id+"F17.wireOp",EDGE,"E5231"),sQuery(id+"F17.wireOp",EDGE,"E5232"),sQuery(id+"F17.wireOp",EDGE,"E5233"),sQuery(id+"F17.wireOp",EDGE,"E5234"),sQuery(id+"F17.wireOp",EDGE,"E5235"),sQuery(id+"F17.wireOp",EDGE,"E5236"),sQuery(id+"F17.wireOp",EDGE,"E5237"),sQuery(id+"F17.wireOp",EDGE,"E5238"),sQuery(id+"F17.wireOp",EDGE,"E5239"),sQuery(id+"F17.wireOp",EDGE,"E5240"),sQuery(id+"F17.wireOp",EDGE,"E5241"),sQuery(id+"F17.wireOp",EDGE,"E5242"),sQuery(id+"F17.wireOp",EDGE,"E5243"),sQuery(id+"F17.wireOp",EDGE,"E5244"),sQuery(id+"F17.wireOp",EDGE,"E5245"),sQuery(id+"F17.wireOp",EDGE,"E5246"),sQuery(id+"F17.wireOp",EDGE,"E5247"),sQuery(id+"F17.wireOp",EDGE,"E5248"),sQuery(id+"F17.wireOp",EDGE,"E5249"),sQuery(id+"F17.wireOp",EDGE,"E5250"),sQuery(id+"F17.wireOp",EDGE,"E5251"),sQuery(id+"F17.wireOp",EDGE,"E5252"),sQuery(id+"F17.wireOp",EDGE,"E5253"),sQuery(id+"F17.wireOp",EDGE,"E5254"),sQuery(id+"F17.wireOp",EDGE,"E5255"),sQuery(id+"F17.wireOp",EDGE,"E5256"),sQuery(id+"F17.wireOp",EDGE,"E5257"),sQuery(id+"F17.wireOp",EDGE,"E5258"),sQuery(id+"F17.wireOp",EDGE,"E5259"),sQuery(id+"F17.wireOp",EDGE,"E5260"),sQuery(id+"F17.wireOp",EDGE,"E5261"),sQuery(id+"F17.wireOp",EDGE,"E5262"),sQuery(id+"F17.wireOp",EDGE,"E5263"),sQuery(id+"F17.wireOp",EDGE,"E5264"),sQuery(id+"F17.wireOp",EDGE,"E5265"),sQuery(id+"F17.wireOp",EDGE,"E5266"),sQuery(id+"F17.wireOp",EDGE,"E5267"),sQuery(id+"F17.wireOp",EDGE,"E5268"),sQuery(id+"F17.wireOp",EDGE,"E5269"),sQuery(id+"F17.wireOp",EDGE,"E5270"),sQuery(id+"F17.wireOp",EDGE,"E5271"),sQuery(id+"F17.wireOp",EDGE,"E5272"),sQuery(id+"F17.wireOp",EDGE,"E5273"),sQuery(id+"F17.wireOp",EDGE,"E5274"),sQuery(id+"F17.wireOp",EDGE,"E5275"),sQuery(id+"F17.wireOp",EDGE,"E5276"),sQuery(id+"F17.wireOp",EDGE,"E5277"),sQuery(id+"F17.wireOp",EDGE,"E5278"),sQuery(id+"F17.wireOp",EDGE,"E5279"),sQuery(id+"F17.wireOp",EDGE,"E5280"),sQuery(id+"F17.wireOp",EDGE,"E5281"),sQuery(id+"F17.wireOp",EDGE,"E5282"),sQuery(id+"F17.wireOp",EDGE,"E5283"),sQuery(id+"F17.wireOp",EDGE,"E5284"),sQuery(id+"F17.wireOp",EDGE,"E5285"),sQuery(id+"F17.wireOp",EDGE,"E5286"),sQuery(id+"F17.wireOp",EDGE,"E5287"),sQuery(id+"F17.wireOp",EDGE,"E5288"),sQuery(id+"F17.wireOp",EDGE,"E5289"),sQuery(id+"F17.wireOp",EDGE,"E5290"),sQuery(id+"F17.wireOp",EDGE,"E5291"),sQuery(id+"F17.wireOp",EDGE,"E5292"),sQuery(id+"F17.wireOp",EDGE,"E5293"),sQuery(id+"F17.wireOp",EDGE,"E5294"),sQuery(id+"F17.wireOp",EDGE,"E5295"),sQuery(id+"F17.wireOp",EDGE,"E5296"),sQuery(id+"F17.wireOp",EDGE,"E5297"),sQuery(id+"F17.wireOp",EDGE,"E5298"),sQuery(id+"F17.wireOp",EDGE,"E5299"),sQuery(id+"F17.wireOp",EDGE,"E5300"),sQuery(id+"F17.wireOp",EDGE,"E5301"),sQuery(id+"F17.wireOp",EDGE,"E5302"),sQuery(id+"F17.wireOp",EDGE,"E5303"),sQuery(id+"F17.wireOp",EDGE,"E5304"),sQuery(id+"F17.wireOp",EDGE,"E5305"),sQuery(id+"F17.wireOp",EDGE,"E5306"),sQuery(id+"F17.wireOp",EDGE,"E5307"),sQuery(id+"F17.wireOp",EDGE,"E5308"),sQuery(id+"F17.wireOp",EDGE,"E5309"),sQuery(id+"F17.wireOp",EDGE,"E5310"),sQuery(id+"F17.wireOp",EDGE,"E5311"),sQuery(id+"F17.wireOp",EDGE,"E5312"),sQuery(id+"F17.wireOp",EDGE,"E5313"),sQuery(id+"F17.wireOp",EDGE,"E5314"),sQuery(id+"F17.wireOp",EDGE,"E5315"),sQuery(id+"F17.wireOp",EDGE,"E5316"),sQuery(id+"F17.wireOp",EDGE,"E5317"),sQuery(id+"F17.wireOp",EDGE,"E5318"),sQuery(id+"F17.wireOp",EDGE,"E5319"),sQuery(id+"F17.wireOp",EDGE,"E5320"),sQuery(id+"F17.wireOp",EDGE,"E5321"),sQuery(id+"F17.wireOp",EDGE,"E5322"),sQuery(id+"F17.wireOp",EDGE,"E5323"),sQuery(id+"F17.wireOp",EDGE,"E5324"),sQuery(id+"F17.wireOp",EDGE,"E5325"),sQuery(id+"F17.wireOp",EDGE,"E5326"),sQuery(id+"F17.wireOp",EDGE,"E5327"),sQuery(id+"F17.wireOp",EDGE,"E5328"),sQuery(id+"F17.wireOp",EDGE,"E5329"),sQuery(id+"F17.wireOp",EDGE,"E5330"),sQuery(id+"F17.wireOp",EDGE,"E5331"),sQuery(id+"F17.wireOp",EDGE,"E5332"),sQuery(id+"F17.wireOp",EDGE,"E5333"),sQuery(id+"F17.wireOp",EDGE,"E5334"),sQuery(id+"F17.wireOp",EDGE,"E5335"),sQuery(id+"F17.wireOp",EDGE,"E5336"),sQuery(id+"F17.wireOp",EDGE,"E5337"),sQuery(id+"F17.wireOp",EDGE,"E5338"),sQuery(id+"F17.wireOp",EDGE,"E5339"),sQuery(id+"F17.wireOp",EDGE,"E5340"),sQuery(id+"F17.wireOp",EDGE,"E5341"),sQuery(id+"F17.wireOp",EDGE,"E5342"),sQuery(id+"F17.wireOp",EDGE,"E5343"),sQuery(id+"F17.wireOp",EDGE,"E5344"),sQuery(id+"F17.wireOp",EDGE,"E5345"),sQuery(id+"F17.wireOp",EDGE,"E5346"),sQuery(id+"F17.wireOp",EDGE,"E5347"),sQuery(id+"F17.wireOp",EDGE,"E5348"),sQuery(id+"F17.wireOp",EDGE,"E5349"),sQuery(id+"F17.wireOp",EDGE,"E5350"),sQuery(id+"F17.wireOp",EDGE,"E5351"),sQuery(id+"F17.wireOp",EDGE,"E5352"),sQuery(id+"F17.wireOp",EDGE,"E5353"),sQuery(id+"F17.wireOp",EDGE,"E5354"),sQuery(id+"F17.wireOp",EDGE,"E5355"),sQuery(id+"F17.wireOp",EDGE,"E5356"),sQuery(id+"F17.wireOp",EDGE,"E5357"),sQuery(id+"F17.wireOp",EDGE,"E5358"),sQuery(id+"F17.wireOp",EDGE,"E5359"),sQuery(id+"F17.wireOp",EDGE,"E5360"),sQuery(id+"F17.wireOp",EDGE,"E5361"),sQuery(id+"F17.wireOp",EDGE,"E5362"),sQuery(id+"F17.wireOp",EDGE,"E5363"),sQuery(id+"F17.wireOp",EDGE,"E5364"),sQuery(id+"F17.wireOp",EDGE,"E5365"),sQuery(id+"F17.wireOp",EDGE,"E5366"),sQuery(id+"F17.wireOp",EDGE,"E5367"),sQuery(id+"F17.wireOp",EDGE,"E5368"),sQuery(id+"F17.wireOp",EDGE,"E5369"),sQuery(id+"F17.wireOp",EDGE,"E5370"),sQuery(id+"F17.wireOp",EDGE,"E5371"),sQuery(id+"F17.wireOp",EDGE,"E5372"),sQuery(id+"F17.wireOp",EDGE,"E5373"),sQuery(id+"F17.wireOp",EDGE,"E5374"),sQuery(id+"F17.wireOp",EDGE,"E5375"),sQuery(id+"F17.wireOp",EDGE,"E5376"),sQuery(id+"F17.wireOp",EDGE,"E5377"),sQuery(id+"F17.wireOp",EDGE,"E5378"),sQuery(id+"F17.wireOp",EDGE,"E5379"),sQuery(id+"F17.wireOp",EDGE,"E5380"),sQuery(id+"F17.wireOp",EDGE,"E5381"),sQuery(id+"F17.wireOp",EDGE,"E5382"),sQuery(id+"F17.wireOp",EDGE,"E5383"),sQuery(id+"F17.wireOp",EDGE,"E5384"),sQuery(id+"F17.wireOp",EDGE,"E5385"),sQuery(id+"F17.wireOp",EDGE,"E5386"),sQuery(id+"F17.wireOp",EDGE,"E5387"),sQuery(id+"F17.wireOp",EDGE,"E5388"),sQuery(id+"F17.wireOp",EDGE,"E5389"),sQuery(id+"F17.wireOp",EDGE,"E5390"),sQuery(id+"F17.wireOp",EDGE,"E5391"),sQuery(id+"F17.wireOp",EDGE,"E5392"),sQuery(id+"F17.wireOp",EDGE,"E5393"),sQuery(id+"F17.wireOp",EDGE,"E5394"),sQuery(id+"F17.wireOp",EDGE,"E5395"),sQuery(id+"F17.wireOp",EDGE,"E5396"),sQuery(id+"F17.wireOp",EDGE,"E5397"),sQuery(id+"F17.wireOp",EDGE,"E5398"),sQuery(id+"F17.wireOp",EDGE,"E5399"),sQuery(id+"F17.wireOp",EDGE,"E5400"),sQuery(id+"F17.wireOp",EDGE,"E5401"),sQuery(id+"F17.wireOp",EDGE,"E5402"),sQuery(id+"F17.wireOp",EDGE,"E5403"),sQuery(id+"F17.wireOp",EDGE,"E5404"),sQuery(id+"F17.wireOp",EDGE,"E5405"),sQuery(id+"F17.wireOp",EDGE,"E5406"),sQuery(id+"F17.wireOp",EDGE,"E5407"),sQuery(id+"F17.wireOp",EDGE,"E5408"),sQuery(id+"F17.wireOp",EDGE,"E5409"),sQuery(id+"F17.wireOp",EDGE,"E5410"),sQuery(id+"F17.wireOp",EDGE,"E5411"),sQuery(id+"F17.wireOp",EDGE,"E5412"),sQuery(id+"F17.wireOp",EDGE,"E5413"),sQuery(id+"F17.wireOp",EDGE,"E5414"),sQuery(id+"F17.wireOp",EDGE,"E5415"),sQuery(id+"F17.wireOp",EDGE,"E5416"),sQuery(id+"F17.wireOp",EDGE,"E5417"),sQuery(id+"F17.wireOp",EDGE,"E5418"),sQuery(id+"F17.wireOp",EDGE,"E5419"),sQuery(id+"F17.wireOp",EDGE,"E5420"),sQuery(id+"F17.wireOp",EDGE,"E5421"),sQuery(id+"F17.wireOp",EDGE,"E5422"),sQuery(id+"F17.wireOp",EDGE,"E5423"),sQuery(id+"F17.wireOp",EDGE,"E5424"),sQuery(id+"F17.wireOp",EDGE,"E5425"),sQuery(id+"F17.wireOp",EDGE,"E5426"),sQuery(id+"F17.wireOp",EDGE,"E5427"),sQuery(id+"F17.wireOp",EDGE,"E5428"),sQuery(id+"F17.wireOp",EDGE,"E5429"),sQuery(id+"F17.wireOp",EDGE,"E5430"),sQuery(id+"F17.wireOp",EDGE,"E5431"),sQuery(id+"F17.wireOp",EDGE,"E5432"),sQuery(id+"F17.wireOp",EDGE,"E5433"),sQuery(id+"F17.wireOp",EDGE,"E5434"),sQuery(id+"F17.wireOp",EDGE,"E5435"),sQuery(id+"F17.wireOp",EDGE,"E5436"),sQuery(id+"F17.wireOp",EDGE,"E5437"),sQuery(id+"F17.wireOp",EDGE,"E5438"),sQuery(id+"F17.wireOp",EDGE,"E5439"),sQuery(id+"F17.wireOp",EDGE,"E5440"),sQuery(id+"F17.wireOp",EDGE,"E5441"),sQuery(id+"F17.wireOp",EDGE,"E5442"),sQuery(id+"F17.wireOp",EDGE,"E5443"),sQuery(id+"F17.wireOp",EDGE,"E5444"),sQuery(id+"F17.wireOp",EDGE,"E5445"),sQuery(id+"F17.wireOp",EDGE,"E5446"),sQuery(id+"F17.wireOp",EDGE,"E5447"),sQuery(id+"F17.wireOp",EDGE,"E5448"),sQuery(id+"F17.wireOp",EDGE,"E5449"),sQuery(id+"F17.wireOp",EDGE,"E5450"),sQuery(id+"F17.wireOp",EDGE,"E5451"),sQuery(id+"F17.wireOp",EDGE,"E5452"),sQuery(id+"F17.wireOp",EDGE,"E5453"),sQuery(id+"F17.wireOp",EDGE,"E5454"),sQuery(id+"F17.wireOp",EDGE,"E5455"),sQuery(id+"F17.wireOp",EDGE,"E5456"),sQuery(id+"F17.wireOp",EDGE,"E5457"),sQuery(id+"F17.wireOp",EDGE,"E5458"),sQuery(id+"F17.wireOp",EDGE,"E5459"),sQuery(id+"F17.wireOp",EDGE,"E5460"),sQuery(id+"F17.wireOp",EDGE,"E5461"),sQuery(id+"F17.wireOp",EDGE,"E5462"),sQuery(id+"F17.wireOp",EDGE,"E5463"),sQuery(id+"F17.wireOp",EDGE,"E5464"),sQuery(id+"F17.wireOp",EDGE,"E5465"),sQuery(id+"F17.wireOp",EDGE,"E5466"),sQuery(id+"F17.wireOp",EDGE,"E5467"),sQuery(id+"F17.wireOp",EDGE,"E5468"),sQuery(id+"F17.wireOp",EDGE,"E5469"),sQuery(id+"F17.wireOp",EDGE,"E5470"),sQuery(id+"F17.wireOp",EDGE,"E5471"),sQuery(id+"F17.wireOp",EDGE,"E5472"),sQuery(id+"F17.wireOp",EDGE,"E5473"),sQuery(id+"F17.wireOp",EDGE,"E5474"),sQuery(id+"F17.wireOp",EDGE,"E5475"),sQuery(id+"F17.wireOp",EDGE,"E5476"),sQuery(id+"F17.wireOp",EDGE,"E5477"),sQuery(id+"F17.wireOp",EDGE,"E5478"),sQuery(id+"F17.wireOp",EDGE,"E5479"),sQuery(id+"F17.wireOp",EDGE,"E5480"),sQuery(id+"F17.wireOp",EDGE,"E5481"),sQuery(id+"F17.wireOp",EDGE,"E5482"),sQuery(id+"F17.wireOp",EDGE,"E5483"),sQuery(id+"F17.wireOp",EDGE,"E5484"),sQuery(id+"F17.wireOp",EDGE,"E5485"),sQuery(id+"F17.wireOp",EDGE,"E5486"),sQuery(id+"F17.wireOp",EDGE,"E5487"),sQuery(id+"F17.wireOp",EDGE,"E5488"),sQuery(id+"F17.wireOp",EDGE,"E5489"),sQuery(id+"F17.wireOp",EDGE,"E5490"),sQuery(id+"F17.wireOp",EDGE,"E5491"),sQuery(id+"F17.wireOp",EDGE,"E5492"),sQuery(id+"F17.wireOp",EDGE,"E5493"),sQuery(id+"F17.wireOp",EDGE,"E5494"),sQuery(id+"F17.wireOp",EDGE,"E5495"),sQuery(id+"F17.wireOp",EDGE,"E5496"),sQuery(id+"F17.wireOp",EDGE,"E5497"),sQuery(id+"F17.wireOp",EDGE,"E5498"),sQuery(id+"F17.wireOp",EDGE,"E5499"),sQuery(id+"F17.wireOp",EDGE,"E5500"),sQuery(id+"F17.wireOp",EDGE,"E5501"),sQuery(id+"F17.wireOp",EDGE,"E5502"),sQuery(id+"F17.wireOp",EDGE,"E5503"),sQuery(id+"F17.wireOp",EDGE,"E5504"),sQuery(id+"F17.wireOp",EDGE,"E5505"),sQuery(id+"F17.wireOp",EDGE,"E5506"),sQuery(id+"F17.wireOp",EDGE,"E5507"),sQuery(id+"F17.wireOp",EDGE,"E5508"),sQuery(id+"F17.wireOp",EDGE,"E5509"),sQuery(id+"F17.wireOp",EDGE,"E5510"),sQuery(id+"F17.wireOp",EDGE,"E5511"),sQuery(id+"F17.wireOp",EDGE,"E5512"),sQuery(id+"F17.wireOp",EDGE,"E5513"),sQuery(id+"F17.wireOp",EDGE,"E5514"),sQuery(id+"F17.wireOp",EDGE,"E5515"),sQuery(id+"F17.wireOp",EDGE,"E5516"),sQuery(id+"F17.wireOp",EDGE,"E5517"),sQuery(id+"F17.wireOp",EDGE,"E5518"),sQuery(id+"F17.wireOp",EDGE,"E5519"),sQuery(id+"F17.wireOp",EDGE,"E5520"),sQuery(id+"F17.wireOp",EDGE,"E5521"),sQuery(id+"F17.wireOp",EDGE,"E5522"),sQuery(id+"F17.wireOp",EDGE,"E5523"),sQuery(id+"F17.wireOp",EDGE,"E5524"),sQuery(id+"F17.wireOp",EDGE,"E5525"),sQuery(id+"F17.wireOp",EDGE,"E5526"),sQuery(id+"F17.wireOp",EDGE,"E5527"),sQuery(id+"F17.wireOp",EDGE,"E5528"),sQuery(id+"F17.wireOp",EDGE,"E5529"),sQuery(id+"F17.wireOp",EDGE,"E5530"),sQuery(id+"F17.wireOp",EDGE,"E5531"),sQuery(id+"F17.wireOp",EDGE,"E5532"),sQuery(id+"F17.wireOp",EDGE,"E5533"),sQuery(id+"F17.wireOp",EDGE,"E5534"),sQuery(id+"F17.wireOp",EDGE,"E5535"),sQuery(id+"F17.wireOp",EDGE,"E5536"),sQuery(id+"F17.wireOp",EDGE,"E5537"),sQuery(id+"F17.wireOp",EDGE,"E5538"),sQuery(id+"F17.wireOp",EDGE,"E5539"),sQuery(id+"F17.wireOp",EDGE,"E5540"),sQuery(id+"F17.wireOp",EDGE,"E5541"),sQuery(id+"F17.wireOp",EDGE,"E5542"),sQuery(id+"F17.wireOp",EDGE,"E5543"),sQuery(id+"F17.wireOp",EDGE,"E5544"),sQuery(id+"F17.wireOp",EDGE,"E5545"),sQuery(id+"F17.wireOp",EDGE,"E5546"),sQuery(id+"F17.wireOp",EDGE,"E5547"),sQuery(id+"F17.wireOp",EDGE,"E5548"),sQuery(id+"F17.wireOp",EDGE,"E5549"),sQuery(id+"F17.wireOp",EDGE,"E5550"),sQuery(id+"F17.wireOp",EDGE,"E5551"),sQuery(id+"F17.wireOp",EDGE,"E5552"),sQuery(id+"F17.wireOp",EDGE,"E5553"),sQuery(id+"F17.wireOp",EDGE,"E5554"),sQuery(id+"F17.wireOp",EDGE,"E5555"),sQuery(id+"F17.wireOp",EDGE,"E5556"),sQuery(id+"F17.wireOp",EDGE,"E5557"),sQuery(id+"F17.wireOp",EDGE,"E5558"),sQuery(id+"F17.wireOp",EDGE,"E5559"),sQuery(id+"F17.wireOp",EDGE,"E5560"),sQuery(id+"F17.wireOp",EDGE,"E5561"),sQuery(id+"F17.wireOp",EDGE,"E5562"),sQuery(id+"F17.wireOp",EDGE,"E5563"),sQuery(id+"F17.wireOp",EDGE,"E5564"),sQuery(id+"F17.wireOp",EDGE,"E5565"),sQuery(id+"F17.wireOp",EDGE,"E5566"),sQuery(id+"F17.wireOp",EDGE,"E5567"),sQuery(id+"F17.wireOp",EDGE,"E5568"),sQuery(id+"F17.wireOp",EDGE,"E5569"),sQuery(id+"F17.wireOp",EDGE,"E5570"),sQuery(id+"F17.wireOp",EDGE,"E5571"),sQuery(id+"F17.wireOp",EDGE,"E5572"),sQuery(id+"F17.wireOp",EDGE,"E5573"),sQuery(id+"F17.wireOp",EDGE,"E5574"),sQuery(id+"F17.wireOp",EDGE,"E5575"),sQuery(id+"F17.wireOp",EDGE,"E5576"),sQuery(id+"F17.wireOp",EDGE,"E5577"),sQuery(id+"F17.wireOp",EDGE,"E5578"),sQuery(id+"F17.wireOp",EDGE,"E5579"),sQuery(id+"F17.wireOp",EDGE,"E5580"),sQuery(id+"F17.wireOp",EDGE,"E5581"),sQuery(id+"F17.wireOp",EDGE,"E5582"),sQuery(id+"F17.wireOp",EDGE,"E5583"),sQuery(id+"F17.wireOp",EDGE,"E5584"),sQuery(id+"F17.wireOp",EDGE,"E5585"),sQuery(id+"F17.wireOp",EDGE,"E5586"),sQuery(id+"F17.wireOp",EDGE,"E5587"),sQuery(id+"F17.wireOp",EDGE,"E5588"),sQuery(id+"F17.wireOp",EDGE,"E5589"),sQuery(id+"F17.wireOp",EDGE,"E5590"),sQuery(id+"F17.wireOp",EDGE,"E5591"),sQuery(id+"F17.wireOp",EDGE,"E5592"),sQuery(id+"F17.wireOp",EDGE,"E5593"),sQuery(id+"F17.wireOp",EDGE,"E5594"),sQuery(id+"F17.wireOp",EDGE,"E5595"),sQuery(id+"F17.wireOp",EDGE,"E5596"),sQuery(id+"F17.wireOp",EDGE,"E5597"),sQuery(id+"F17.wireOp",EDGE,"E5598"),sQuery(id+"F17.wireOp",EDGE,"E5599"),sQuery(id+"F17.wireOp",EDGE,"E5600"),sQuery(id+"F17.wireOp",EDGE,"E5601"),sQuery(id+"F17.wireOp",EDGE,"E5602"),sQuery(id+"F17.wireOp",EDGE,"E5603"),sQuery(id+"F17.wireOp",EDGE,"E5604"),sQuery(id+"F17.wireOp",EDGE,"E5605"),sQuery(id+"F17.wireOp",EDGE,"E5606"),sQuery(id+"F17.wireOp",EDGE,"E5607"),sQuery(id+"F17.wireOp",EDGE,"E5608"),sQuery(id+"F17.wireOp",EDGE,"E5609"),sQuery(id+"F17.wireOp",EDGE,"E5610"),sQuery(id+"F17.wireOp",EDGE,"E5611"),sQuery(id+"F17.wireOp",EDGE,"E5612"),sQuery(id+"F17.wireOp",EDGE,"E5613"),sQuery(id+"F17.wireOp",EDGE,"E5614"),sQuery(id+"F17.wireOp",EDGE,"E5615"),sQuery(id+"F17.wireOp",EDGE,"E5616"),sQuery(id+"F17.wireOp",EDGE,"E5617"),sQuery(id+"F17.wireOp",EDGE,"E5618"),sQuery(id+"F17.wireOp",EDGE,"E5619"),sQuery(id+"F17.wireOp",EDGE,"E5620"),sQuery(id+"F17.wireOp",EDGE,"E5621"),sQuery(id+"F17.wireOp",EDGE,"E5622"),sQuery(id+"F17.wireOp",EDGE,"E5623"),sQuery(id+"F17.wireOp",EDGE,"E5624"),sQuery(id+"F17.wireOp",EDGE,"E5625"),sQuery(id+"F17.wireOp",EDGE,"E5626"),sQuery(id+"F17.wireOp",EDGE,"E5627"),sQuery(id+"F17.wireOp",EDGE,"E5628"),sQuery(id+"F17.wireOp",EDGE,"E5629"),sQuery(id+"F17.wireOp",EDGE,"E5630"),sQuery(id+"F17.wireOp",EDGE,"E5631"),sQuery(id+"F17.wireOp",EDGE,"E5632"),sQuery(id+"F17.wireOp",EDGE,"E5633"),sQuery(id+"F17.wireOp",EDGE,"E5634"),sQuery(id+"F17.wireOp",EDGE,"E5635"),sQuery(id+"F17.wireOp",EDGE,"E5636"),sQuery(id+"F17.wireOp",EDGE,"E5637"),sQuery(id+"F17.wireOp",EDGE,"E5638"),sQuery(id+"F17.wireOp",EDGE,"E5639"),sQuery(id+"F17.wireOp",EDGE,"E5640"),sQuery(id+"F17.wireOp",EDGE,"E5641"),sQuery(id+"F17.wireOp",EDGE,"E5642"),sQuery(id+"F17.wireOp",EDGE,"E5643"),sQuery(id+"F17.wireOp",EDGE,"E5644"),sQuery(id+"F17.wireOp",EDGE,"E5645"),sQuery(id+"F17.wireOp",EDGE,"E5646"),sQuery(id+"F17.wireOp",EDGE,"E5647"),sQuery(id+"F17.wireOp",EDGE,"E5648"),sQuery(id+"F17.wireOp",EDGE,"E5649"),sQuery(id+"F17.wireOp",EDGE,"E5650"),sQuery(id+"F17.wireOp",EDGE,"E5651"),sQuery(id+"F17.wireOp",EDGE,"E5652"),sQuery(id+"F17.wireOp",EDGE,"E5653"),sQuery(id+"F17.wireOp",EDGE,"E5654"),sQuery(id+"F17.wireOp",EDGE,"E5655"),sQuery(id+"F17.wireOp",EDGE,"E5656"),sQuery(id+"F17.wireOp",EDGE,"E5657"),sQuery(id+"F17.wireOp",EDGE,"E5658"),sQuery(id+"F17.wireOp",EDGE,"E5659"),sQuery(id+"F17.wireOp",EDGE,"E5660"),sQuery(id+"F17.wireOp",EDGE,"E5661"),sQuery(id+"F17.wireOp",EDGE,"E5662"),sQuery(id+"F17.wireOp",EDGE,"E5663"),sQuery(id+"F17.wireOp",EDGE,"E5664"),sQuery(id+"F17.wireOp",EDGE,"E5665"),sQuery(id+"F17.wireOp",EDGE,"E5666"),sQuery(id+"F17.wireOp",EDGE,"E5667"),sQuery(id+"F17.wireOp",EDGE,"E5668"),sQuery(id+"F17.wireOp",EDGE,"E5669"),sQuery(id+"F17.wireOp",EDGE,"E5670"),sQuery(id+"F17.wireOp",EDGE,"E5671"),sQuery(id+"F17.wireOp",EDGE,"E5672"),sQuery(id+"F17.wireOp",EDGE,"E5673"),sQuery(id+"F17.wireOp",EDGE,"E5674"),sQuery(id+"F17.wireOp",EDGE,"E5675"),sQuery(id+"F17.wireOp",EDGE,"E5676"),sQuery(id+"F17.wireOp",EDGE,"E5677"),sQuery(id+"F17.wireOp",EDGE,"E5678"),sQuery(id+"F17.wireOp",EDGE,"E5679"),sQuery(id+"F17.wireOp",EDGE,"E5680"),sQuery(id+"F17.wireOp",EDGE,"E5681"),sQuery(id+"F17.wireOp",EDGE,"E5682"),sQuery(id+"F17.wireOp",EDGE,"E5683"),sQuery(id+"F17.wireOp",EDGE,"E5684"),sQuery(id+"F17.wireOp",EDGE,"E5685"),sQuery(id+"F17.wireOp",EDGE,"E5686"),sQuery(id+"F17.wireOp",EDGE,"E5687"),sQuery(id+"F17.wireOp",EDGE,"E5688"),sQuery(id+"F17.wireOp",EDGE,"E5689"),sQuery(id+"F17.wireOp",EDGE,"E5690"),sQuery(id+"F17.wireOp",EDGE,"E5691"),sQuery(id+"F17.wireOp",EDGE,"E5692"),sQuery(id+"F17.wireOp",EDGE,"E5693"),sQuery(id+"F17.wireOp",EDGE,"E5694"),sQuery(id+"F17.wireOp",EDGE,"E5695"),sQuery(id+"F17.wireOp",EDGE,"E5696"),sQuery(id+"F17.wireOp",EDGE,"E5697"),sQuery(id+"F17.wireOp",EDGE,"E5698"),sQuery(id+"F17.wireOp",EDGE,"E5699"),sQuery(id+"F17.wireOp",EDGE,"E5700"),sQuery(id+"F17.wireOp",EDGE,"E5701"),sQuery(id+"F17.wireOp",EDGE,"E5702"),sQuery(id+"F17.wireOp",EDGE,"E5703"),sQuery(id+"F17.wireOp",EDGE,"E5704"),sQuery(id+"F17.wireOp",EDGE,"E5705"),sQuery(id+"F17.wireOp",EDGE,"E5706"),sQuery(id+"F17.wireOp",EDGE,"E5707"),sQuery(id+"F17.wireOp",EDGE,"E5708"),sQuery(id+"F17.wireOp",EDGE,"E5709"),sQuery(id+"F17.wireOp",EDGE,"E5710"),sQuery(id+"F17.wireOp",EDGE,"E5711"),sQuery(id+"F17.wireOp",EDGE,"E5712"),sQuery(id+"F17.wireOp",EDGE,"E5713"),sQuery(id+"F17.wireOp",EDGE,"E5714"),sQuery(id+"F17.wireOp",EDGE,"E5715"),sQuery(id+"F17.wireOp",EDGE,"E5716"),sQuery(id+"F17.wireOp",EDGE,"E5717"),sQuery(id+"F17.wireOp",EDGE,"E5718"),sQuery(id+"F17.wireOp",EDGE,"E5719"),sQuery(id+"F17.wireOp",EDGE,"E5720"),sQuery(id+"F17.wireOp",EDGE,"E5721"),sQuery(id+"F17.wireOp",EDGE,"E5722"),sQuery(id+"F17.wireOp",EDGE,"E5723"),sQuery(id+"F17.wireOp",EDGE,"E5724"),sQuery(id+"F17.wireOp",EDGE,"E5725"),sQuery(id+"F17.wireOp",EDGE,"E5726"),sQuery(id+"F17.wireOp",EDGE,"E5727"),sQuery(id+"F17.wireOp",EDGE,"E5728"),sQuery(id+"F17.wireOp",EDGE,"E5729"),sQuery(id+"F17.wireOp",EDGE,"E5730"),sQuery(id+"F17.wireOp",EDGE,"E5731"),sQuery(id+"F17.wireOp",EDGE,"E5732"),sQuery(id+"F17.wireOp",EDGE,"E5733"),sQuery(id+"F17.wireOp",EDGE,"E5734"),sQuery(id+"F17.wireOp",EDGE,"E5735"),sQuery(id+"F17.wireOp",EDGE,"E5736"),sQuery(id+"F17.wireOp",EDGE,"E5737"),sQuery(id+"F17.wireOp",EDGE,"E5738"),sQuery(id+"F17.wireOp",EDGE,"E5739"),sQuery(id+"F17.wireOp",EDGE,"E5740"),sQuery(id+"F17.wireOp",EDGE,"E5741"),sQuery(id+"F17.wireOp",EDGE,"E5742"),sQuery(id+"F17.wireOp",EDGE,"E5743"),sQuery(id+"F17.wireOp",EDGE,"E5744"),sQuery(id+"F17.wireOp",EDGE,"E5745"),sQuery(id+"F17.wireOp",EDGE,"E5746"),sQuery(id+"F17.wireOp",EDGE,"E5747"),sQuery(id+"F17.wireOp",EDGE,"E5748"),sQuery(id+"F17.wireOp",EDGE,"E5749"),sQuery(id+"F17.wireOp",EDGE,"E5750"),sQuery(id+"F17.wireOp",EDGE,"E5751")])]});
            var Q1;
            Q1=sQuery(id+"F1.wireOp",EDGE,"E15");
            transform(context, id + "F19", {"entities" : qUnion([Q0]), "transformType" : TransformType.ROTATION, "transformAxis" : qUnion([Q1]), "angle" : 90 * degree, "oppositeDirection" : true, "makeCopy" : false});
        }
        {
            var Q0;
            Q0=qCreatedBy(makeId("Front.planeOp"),FACE);
            var sketch = newSketch(context, id + "F20", { "sketchPlane" : qUnion([Q0])});
            skCircle(sketch, "E5752", {"center": v(0, 0) * mm, "radius": 48.75 * mm});
            skSolve(sketch);
        }
        {
            var Q0;
            Q0 = qSketchRegion(id + "F20", true);
            extrude(context, id + "F21", {"entities" : qUnion([Q0]), "operationType" : NewBodyOperationType.ADD, "oppositeDirection" : true, "depth" : 3 * mm, "offsetDistance" : 25 * mm});
        }
        {
            var Q0;
            Q0=makeQuery(id+"F12.opExtrude","CAP_FACE",FACE,{"disambiguationData":[OSD([sQuery(id+"F11.wireOp",EDGE,"E1476"),sQuery(id+"F11.wireOp",EDGE,"E1477"),sQuery(id+"F11.wireOp",EDGE,"E1478"),sQuery(id+"F11.wireOp",EDGE,"E1479"),sQuery(id+"F11.wireOp",EDGE,"E1480"),sQuery(id+"F11.wireOp",EDGE,"E1481"),sQuery(id+"F11.wireOp",EDGE,"E1482"),sQuery(id+"F11.wireOp",EDGE,"E1483"),sQuery(id+"F11.wireOp",EDGE,"E1484"),sQuery(id+"F11.wireOp",EDGE,"E1485"),sQuery(id+"F11.wireOp",EDGE,"E1486"),sQuery(id+"F11.wireOp",EDGE,"E1487"),sQuery(id+"F11.wireOp",EDGE,"E1488"),sQuery(id+"F11.wireOp",EDGE,"E1489"),sQuery(id+"F11.wireOp",EDGE,"E1490"),sQuery(id+"F11.wireOp",EDGE,"E1491"),sQuery(id+"F11.wireOp",EDGE,"E1492"),sQuery(id+"F11.wireOp",EDGE,"E1493"),sQuery(id+"F11.wireOp",EDGE,"E1494"),sQuery(id+"F11.wireOp",EDGE,"E1495"),sQuery(id+"F11.wireOp",EDGE,"E1496"),sQuery(id+"F11.wireOp",EDGE,"E1497"),sQuery(id+"F11.wireOp",EDGE,"E1498"),sQuery(id+"F11.wireOp",EDGE,"E1499"),sQuery(id+"F11.wireOp",EDGE,"E1500"),sQuery(id+"F11.wireOp",EDGE,"E1501"),sQuery(id+"F11.wireOp",EDGE,"E1502"),sQuery(id+"F11.wireOp",EDGE,"E1503"),sQuery(id+"F11.wireOp",EDGE,"E1504"),sQuery(id+"F11.wireOp",EDGE,"E1505"),sQuery(id+"F11.wireOp",EDGE,"E1506"),sQuery(id+"F11.wireOp",EDGE,"E1507"),sQuery(id+"F11.wireOp",EDGE,"E1508"),sQuery(id+"F11.wireOp",EDGE,"E1509"),sQuery(id+"F11.wireOp",EDGE,"E1510"),sQuery(id+"F11.wireOp",EDGE,"E1511"),sQuery(id+"F11.wireOp",EDGE,"E1512"),sQuery(id+"F11.wireOp",EDGE,"E1513"),sQuery(id+"F11.wireOp",EDGE,"E1514"),sQuery(id+"F11.wireOp",EDGE,"E1515"),sQuery(id+"F11.wireOp",EDGE,"E1516"),sQuery(id+"F11.wireOp",EDGE,"E1517"),sQuery(id+"F11.wireOp",EDGE,"E1518"),sQuery(id+"F11.wireOp",EDGE,"E1519"),sQuery(id+"F11.wireOp",EDGE,"E1520"),sQuery(id+"F11.wireOp",EDGE,"E1521"),sQuery(id+"F11.wireOp",EDGE,"E1522"),sQuery(id+"F11.wireOp",EDGE,"E1523"),sQuery(id+"F11.wireOp",EDGE,"E1524"),sQuery(id+"F11.wireOp",EDGE,"E1525"),sQuery(id+"F11.wireOp",EDGE,"E1526"),sQuery(id+"F11.wireOp",EDGE,"E1527"),sQuery(id+"F11.wireOp",EDGE,"E1528"),sQuery(id+"F11.wireOp",EDGE,"E1529"),sQuery(id+"F11.wireOp",EDGE,"E1530"),sQuery(id+"F11.wireOp",EDGE,"E1531"),sQuery(id+"F11.wireOp",EDGE,"E1532"),sQuery(id+"F11.wireOp",EDGE,"E1533"),sQuery(id+"F11.wireOp",EDGE,"E1534"),sQuery(id+"F11.wireOp",EDGE,"E1535"),sQuery(id+"F11.wireOp",EDGE,"E1536"),sQuery(id+"F11.wireOp",EDGE,"E1537"),sQuery(id+"F11.wireOp",EDGE,"E1538"),sQuery(id+"F11.wireOp",EDGE,"E1539"),sQuery(id+"F11.wireOp",EDGE,"E1540"),sQuery(id+"F11.wireOp",EDGE,"E1541"),sQuery(id+"F11.wireOp",EDGE,"E1542"),sQuery(id+"F11.wireOp",EDGE,"E1543"),sQuery(id+"F11.wireOp",EDGE,"E1544"),sQuery(id+"F11.wireOp",EDGE,"E1545"),sQuery(id+"F11.wireOp",EDGE,"E1546"),sQuery(id+"F11.wireOp",EDGE,"E1547"),sQuery(id+"F11.wireOp",EDGE,"E1548"),sQuery(id+"F11.wireOp",EDGE,"E1549"),sQuery(id+"F11.wireOp",EDGE,"E1550"),sQuery(id+"F11.wireOp",EDGE,"E1551"),sQuery(id+"F11.wireOp",EDGE,"E1552"),sQuery(id+"F11.wireOp",EDGE,"E1553"),sQuery(id+"F11.wireOp",EDGE,"E1554"),sQuery(id+"F11.wireOp",EDGE,"E1555"),sQuery(id+"F11.wireOp",EDGE,"E1556"),sQuery(id+"F11.wireOp",EDGE,"E1557"),sQuery(id+"F11.wireOp",EDGE,"E1558"),sQuery(id+"F11.wireOp",EDGE,"E1559"),sQuery(id+"F11.wireOp",EDGE,"E1560"),sQuery(id+"F11.wireOp",EDGE,"E1561"),sQuery(id+"F11.wireOp",EDGE,"E1562"),sQuery(id+"F11.wireOp",EDGE,"E1563"),sQuery(id+"F11.wireOp",EDGE,"E1564"),sQuery(id+"F11.wireOp",EDGE,"E1565"),sQuery(id+"F11.wireOp",EDGE,"E1566"),sQuery(id+"F11.wireOp",EDGE,"E1567"),sQuery(id+"F11.wireOp",EDGE,"E1568"),sQuery(id+"F11.wireOp",EDGE,"E1569"),sQuery(id+"F11.wireOp",EDGE,"E1570"),sQuery(id+"F11.wireOp",EDGE,"E1571"),sQuery(id+"F11.wireOp",EDGE,"E1572"),sQuery(id+"F11.wireOp",EDGE,"E1573"),sQuery(id+"F11.wireOp",EDGE,"E1574"),sQuery(id+"F11.wireOp",EDGE,"E1575"),sQuery(id+"F11.wireOp",EDGE,"E1576"),sQuery(id+"F11.wireOp",EDGE,"E1577"),sQuery(id+"F11.wireOp",EDGE,"E1578"),sQuery(id+"F11.wireOp",EDGE,"E1579"),sQuery(id+"F11.wireOp",EDGE,"E1580"),sQuery(id+"F11.wireOp",EDGE,"E1581"),sQuery(id+"F11.wireOp",EDGE,"E1582"),sQuery(id+"F11.wireOp",EDGE,"E1583"),sQuery(id+"F11.wireOp",EDGE,"E1584"),sQuery(id+"F11.wireOp",EDGE,"E1585"),sQuery(id+"F11.wireOp",EDGE,"E1586"),sQuery(id+"F11.wireOp",EDGE,"E1587"),sQuery(id+"F11.wireOp",EDGE,"E1588"),sQuery(id+"F11.wireOp",EDGE,"E1589"),sQuery(id+"F11.wireOp",EDGE,"E1590"),sQuery(id+"F11.wireOp",EDGE,"E1591"),sQuery(id+"F11.wireOp",EDGE,"E1592"),sQuery(id+"F11.wireOp",EDGE,"E1593"),sQuery(id+"F11.wireOp",EDGE,"E1594"),sQuery(id+"F11.wireOp",EDGE,"E1595"),sQuery(id+"F11.wireOp",EDGE,"E1596"),sQuery(id+"F11.wireOp",EDGE,"E1597"),sQuery(id+"F11.wireOp",EDGE,"E1598"),sQuery(id+"F11.wireOp",EDGE,"E1599"),sQuery(id+"F11.wireOp",EDGE,"E1600"),sQuery(id+"F11.wireOp",EDGE,"E1601"),sQuery(id+"F11.wireOp",EDGE,"E1602"),sQuery(id+"F11.wireOp",EDGE,"E1603"),sQuery(id+"F11.wireOp",EDGE,"E1604"),sQuery(id+"F11.wireOp",EDGE,"E1605"),sQuery(id+"F11.wireOp",EDGE,"E1606"),sQuery(id+"F11.wireOp",EDGE,"E1607"),sQuery(id+"F11.wireOp",EDGE,"E1608"),sQuery(id+"F11.wireOp",EDGE,"E1609"),sQuery(id+"F11.wireOp",EDGE,"E1610"),sQuery(id+"F11.wireOp",EDGE,"E1611"),sQuery(id+"F11.wireOp",EDGE,"E1612"),sQuery(id+"F11.wireOp",EDGE,"E1613"),sQuery(id+"F11.wireOp",EDGE,"E1614"),sQuery(id+"F11.wireOp",EDGE,"E1615"),sQuery(id+"F11.wireOp",EDGE,"E1616"),sQuery(id+"F11.wireOp",EDGE,"E1617"),sQuery(id+"F11.wireOp",EDGE,"E1618"),sQuery(id+"F11.wireOp",EDGE,"E1619"),sQuery(id+"F11.wireOp",EDGE,"E1620"),sQuery(id+"F11.wireOp",EDGE,"E1621"),sQuery(id+"F11.wireOp",EDGE,"E1622"),sQuery(id+"F11.wireOp",EDGE,"E1623"),sQuery(id+"F11.wireOp",EDGE,"E1624"),sQuery(id+"F11.wireOp",EDGE,"E1625"),sQuery(id+"F11.wireOp",EDGE,"E1626"),sQuery(id+"F11.wireOp",EDGE,"E1627"),sQuery(id+"F11.wireOp",EDGE,"E1628"),sQuery(id+"F11.wireOp",EDGE,"E1629"),sQuery(id+"F11.wireOp",EDGE,"E1630"),sQuery(id+"F11.wireOp",EDGE,"E1631"),sQuery(id+"F11.wireOp",EDGE,"E1632"),sQuery(id+"F11.wireOp",EDGE,"E1633"),sQuery(id+"F11.wireOp",EDGE,"E1634"),sQuery(id+"F11.wireOp",EDGE,"E1635"),sQuery(id+"F11.wireOp",EDGE,"E1636"),sQuery(id+"F11.wireOp",EDGE,"E1637"),sQuery(id+"F11.wireOp",EDGE,"E1638"),sQuery(id+"F11.wireOp",EDGE,"E1639"),sQuery(id+"F11.wireOp",EDGE,"E1640"),sQuery(id+"F11.wireOp",EDGE,"E1641"),sQuery(id+"F11.wireOp",EDGE,"E1642"),sQuery(id+"F11.wireOp",EDGE,"E1643"),sQuery(id+"F11.wireOp",EDGE,"E1644"),sQuery(id+"F11.wireOp",EDGE,"E1645"),sQuery(id+"F11.wireOp",EDGE,"E1646"),sQuery(id+"F11.wireOp",EDGE,"E1647"),sQuery(id+"F11.wireOp",EDGE,"E1648"),sQuery(id+"F11.wireOp",EDGE,"E1649"),sQuery(id+"F11.wireOp",EDGE,"E1650"),sQuery(id+"F11.wireOp",EDGE,"E1651"),sQuery(id+"F11.wireOp",EDGE,"E1652"),sQuery(id+"F11.wireOp",EDGE,"E1653"),sQuery(id+"F11.wireOp",EDGE,"E1654"),sQuery(id+"F11.wireOp",EDGE,"E1655"),sQuery(id+"F11.wireOp",EDGE,"E1656"),sQuery(id+"F11.wireOp",EDGE,"E1657"),sQuery(id+"F11.wireOp",EDGE,"E1658"),sQuery(id+"F11.wireOp",EDGE,"E1659"),sQuery(id+"F11.wireOp",EDGE,"E1660"),sQuery(id+"F11.wireOp",EDGE,"E1661"),sQuery(id+"F11.wireOp",EDGE,"E1662"),sQuery(id+"F11.wireOp",EDGE,"E1663"),sQuery(id+"F11.wireOp",EDGE,"E1664"),sQuery(id+"F11.wireOp",EDGE,"E1665"),sQuery(id+"F11.wireOp",EDGE,"E1666"),sQuery(id+"F11.wireOp",EDGE,"E1667"),sQuery(id+"F11.wireOp",EDGE,"E1668"),sQuery(id+"F11.wireOp",EDGE,"E1669"),sQuery(id+"F11.wireOp",EDGE,"E1670"),sQuery(id+"F11.wireOp",EDGE,"E1671"),sQuery(id+"F11.wireOp",EDGE,"E1672"),sQuery(id+"F11.wireOp",EDGE,"E1673"),sQuery(id+"F11.wireOp",EDGE,"E1674"),sQuery(id+"F11.wireOp",EDGE,"E1675"),sQuery(id+"F11.wireOp",EDGE,"E1676"),sQuery(id+"F11.wireOp",EDGE,"E1677"),sQuery(id+"F11.wireOp",EDGE,"E1678"),sQuery(id+"F11.wireOp",EDGE,"E1679"),sQuery(id+"F11.wireOp",EDGE,"E1680"),sQuery(id+"F11.wireOp",EDGE,"E1681"),sQuery(id+"F11.wireOp",EDGE,"E1682"),sQuery(id+"F11.wireOp",EDGE,"E1683"),sQuery(id+"F11.wireOp",EDGE,"E1684"),sQuery(id+"F11.wireOp",EDGE,"E1685"),sQuery(id+"F11.wireOp",EDGE,"E1686"),sQuery(id+"F11.wireOp",EDGE,"E1687"),sQuery(id+"F11.wireOp",EDGE,"E1688"),sQuery(id+"F11.wireOp",EDGE,"E1689"),sQuery(id+"F11.wireOp",EDGE,"E1690"),sQuery(id+"F11.wireOp",EDGE,"E1691"),sQuery(id+"F11.wireOp",EDGE,"E1692"),sQuery(id+"F11.wireOp",EDGE,"E1693"),sQuery(id+"F11.wireOp",EDGE,"E1694"),sQuery(id+"F11.wireOp",EDGE,"E1695"),sQuery(id+"F11.wireOp",EDGE,"E1696"),sQuery(id+"F11.wireOp",EDGE,"E1697"),sQuery(id+"F11.wireOp",EDGE,"E1698"),sQuery(id+"F11.wireOp",EDGE,"E1699"),sQuery(id+"F11.wireOp",EDGE,"E1700"),sQuery(id+"F11.wireOp",EDGE,"E1701"),sQuery(id+"F11.wireOp",EDGE,"E1702"),sQuery(id+"F11.wireOp",EDGE,"E1703"),sQuery(id+"F11.wireOp",EDGE,"E1704"),sQuery(id+"F11.wireOp",EDGE,"E1705"),sQuery(id+"F11.wireOp",EDGE,"E1706"),sQuery(id+"F11.wireOp",EDGE,"E1707"),sQuery(id+"F11.wireOp",EDGE,"E1708"),sQuery(id+"F11.wireOp",EDGE,"E1709"),sQuery(id+"F11.wireOp",EDGE,"E1710"),sQuery(id+"F11.wireOp",EDGE,"E1711"),sQuery(id+"F11.wireOp",EDGE,"E1712"),sQuery(id+"F11.wireOp",EDGE,"E1713"),sQuery(id+"F11.wireOp",EDGE,"E1714"),sQuery(id+"F11.wireOp",EDGE,"E1715"),sQuery(id+"F11.wireOp",EDGE,"E1716"),sQuery(id+"F11.wireOp",EDGE,"E1717"),sQuery(id+"F11.wireOp",EDGE,"E1718"),sQuery(id+"F11.wireOp",EDGE,"E1719"),sQuery(id+"F11.wireOp",EDGE,"E1720"),sQuery(id+"F11.wireOp",EDGE,"E1721"),sQuery(id+"F11.wireOp",EDGE,"E1722"),sQuery(id+"F11.wireOp",EDGE,"E1723"),sQuery(id+"F11.wireOp",EDGE,"E1724"),sQuery(id+"F11.wireOp",EDGE,"E1725"),sQuery(id+"F11.wireOp",EDGE,"E1726"),sQuery(id+"F11.wireOp",EDGE,"E1727"),sQuery(id+"F11.wireOp",EDGE,"E1728"),sQuery(id+"F11.wireOp",EDGE,"E1729"),sQuery(id+"F11.wireOp",EDGE,"E1730"),sQuery(id+"F11.wireOp",EDGE,"E1731"),sQuery(id+"F11.wireOp",EDGE,"E1732"),sQuery(id+"F11.wireOp",EDGE,"E1733"),sQuery(id+"F11.wireOp",EDGE,"E1734"),sQuery(id+"F11.wireOp",EDGE,"E1735"),sQuery(id+"F11.wireOp",EDGE,"E1736"),sQuery(id+"F11.wireOp",EDGE,"E1737"),sQuery(id+"F11.wireOp",EDGE,"E1738"),sQuery(id+"F11.wireOp",EDGE,"E1739"),sQuery(id+"F11.wireOp",EDGE,"E1740"),sQuery(id+"F11.wireOp",EDGE,"E1741"),sQuery(id+"F11.wireOp",EDGE,"E1742"),sQuery(id+"F11.wireOp",EDGE,"E1743"),sQuery(id+"F11.wireOp",EDGE,"E1744"),sQuery(id+"F11.wireOp",EDGE,"E1745"),sQuery(id+"F11.wireOp",EDGE,"E1746"),sQuery(id+"F11.wireOp",EDGE,"E1747"),sQuery(id+"F11.wireOp",EDGE,"E1748"),sQuery(id+"F11.wireOp",EDGE,"E1749"),sQuery(id+"F11.wireOp",EDGE,"E1750"),sQuery(id+"F11.wireOp",EDGE,"E1751"),sQuery(id+"F11.wireOp",EDGE,"E1752"),sQuery(id+"F11.wireOp",EDGE,"E1753"),sQuery(id+"F11.wireOp",EDGE,"E1754"),sQuery(id+"F11.wireOp",EDGE,"E1755"),sQuery(id+"F11.wireOp",EDGE,"E1756"),sQuery(id+"F11.wireOp",EDGE,"E1757"),sQuery(id+"F11.wireOp",EDGE,"E1758"),sQuery(id+"F11.wireOp",EDGE,"E1759"),sQuery(id+"F11.wireOp",EDGE,"E1760"),sQuery(id+"F11.wireOp",EDGE,"E1761"),sQuery(id+"F11.wireOp",EDGE,"E1762"),sQuery(id+"F11.wireOp",EDGE,"E1763"),sQuery(id+"F11.wireOp",EDGE,"E1764"),sQuery(id+"F11.wireOp",EDGE,"E1765"),sQuery(id+"F11.wireOp",EDGE,"E1766"),sQuery(id+"F11.wireOp",EDGE,"E1767"),sQuery(id+"F11.wireOp",EDGE,"E1768"),sQuery(id+"F11.wireOp",EDGE,"E1769"),sQuery(id+"F11.wireOp",EDGE,"E1770"),sQuery(id+"F11.wireOp",EDGE,"E1771"),sQuery(id+"F11.wireOp",EDGE,"E1772"),sQuery(id+"F11.wireOp",EDGE,"E1773"),sQuery(id+"F11.wireOp",EDGE,"E1774"),sQuery(id+"F11.wireOp",EDGE,"E1775"),sQuery(id+"F11.wireOp",EDGE,"E1776"),sQuery(id+"F11.wireOp",EDGE,"E1777"),sQuery(id+"F11.wireOp",EDGE,"E1778"),sQuery(id+"F11.wireOp",EDGE,"E1779"),sQuery(id+"F11.wireOp",EDGE,"E1780"),sQuery(id+"F11.wireOp",EDGE,"E1781"),sQuery(id+"F11.wireOp",EDGE,"E1782"),sQuery(id+"F11.wireOp",EDGE,"E1783"),sQuery(id+"F11.wireOp",EDGE,"E1784"),sQuery(id+"F11.wireOp",EDGE,"E1785"),sQuery(id+"F11.wireOp",EDGE,"E1786"),sQuery(id+"F11.wireOp",EDGE,"E1787"),sQuery(id+"F11.wireOp",EDGE,"E1788"),sQuery(id+"F11.wireOp",EDGE,"E1789"),sQuery(id+"F11.wireOp",EDGE,"E1790"),sQuery(id+"F11.wireOp",EDGE,"E1791"),sQuery(id+"F11.wireOp",EDGE,"E1792"),sQuery(id+"F11.wireOp",EDGE,"E1793"),sQuery(id+"F11.wireOp",EDGE,"E1794"),sQuery(id+"F11.wireOp",EDGE,"E1795"),sQuery(id+"F11.wireOp",EDGE,"E1796"),sQuery(id+"F11.wireOp",EDGE,"E1797"),sQuery(id+"F11.wireOp",EDGE,"E1798"),sQuery(id+"F11.wireOp",EDGE,"E1799"),sQuery(id+"F11.wireOp",EDGE,"E1800"),sQuery(id+"F11.wireOp",EDGE,"E1801"),sQuery(id+"F11.wireOp",EDGE,"E1802"),sQuery(id+"F11.wireOp",EDGE,"E1803"),sQuery(id+"F11.wireOp",EDGE,"E1804"),sQuery(id+"F11.wireOp",EDGE,"E1805"),sQuery(id+"F11.wireOp",EDGE,"E1806"),sQuery(id+"F11.wireOp",EDGE,"E1807"),sQuery(id+"F11.wireOp",EDGE,"E1808"),sQuery(id+"F11.wireOp",EDGE,"E1809"),sQuery(id+"F11.wireOp",EDGE,"E1810"),sQuery(id+"F11.wireOp",EDGE,"E1811"),sQuery(id+"F11.wireOp",EDGE,"E1812"),sQuery(id+"F11.wireOp",EDGE,"E1813"),sQuery(id+"F11.wireOp",EDGE,"E1814"),sQuery(id+"F11.wireOp",EDGE,"E1815"),sQuery(id+"F11.wireOp",EDGE,"E1816"),sQuery(id+"F11.wireOp",EDGE,"E1817"),sQuery(id+"F11.wireOp",EDGE,"E1818"),sQuery(id+"F11.wireOp",EDGE,"E1819"),sQuery(id+"F11.wireOp",EDGE,"E1820"),sQuery(id+"F11.wireOp",EDGE,"E1821"),sQuery(id+"F11.wireOp",EDGE,"E1822"),sQuery(id+"F11.wireOp",EDGE,"E1823"),sQuery(id+"F11.wireOp",EDGE,"E1824"),sQuery(id+"F11.wireOp",EDGE,"E1825"),sQuery(id+"F11.wireOp",EDGE,"E1826"),sQuery(id+"F11.wireOp",EDGE,"E1827"),sQuery(id+"F11.wireOp",EDGE,"E1828"),sQuery(id+"F11.wireOp",EDGE,"E1829"),sQuery(id+"F11.wireOp",EDGE,"E1830"),sQuery(id+"F11.wireOp",EDGE,"E1831"),sQuery(id+"F11.wireOp",EDGE,"E1832"),sQuery(id+"F11.wireOp",EDGE,"E1833"),sQuery(id+"F11.wireOp",EDGE,"E1834"),sQuery(id+"F11.wireOp",EDGE,"E1835"),sQuery(id+"F11.wireOp",EDGE,"E1836"),sQuery(id+"F11.wireOp",EDGE,"E1837"),sQuery(id+"F11.wireOp",EDGE,"E1838"),sQuery(id+"F11.wireOp",EDGE,"E1839"),sQuery(id+"F11.wireOp",EDGE,"E1840"),sQuery(id+"F11.wireOp",EDGE,"E1841"),sQuery(id+"F11.wireOp",EDGE,"E1842"),sQuery(id+"F11.wireOp",EDGE,"E1843"),sQuery(id+"F11.wireOp",EDGE,"E1844"),sQuery(id+"F11.wireOp",EDGE,"E1845"),sQuery(id+"F11.wireOp",EDGE,"E1846"),sQuery(id+"F11.wireOp",EDGE,"E1847"),sQuery(id+"F11.wireOp",EDGE,"E1848"),sQuery(id+"F11.wireOp",EDGE,"E1849"),sQuery(id+"F11.wireOp",EDGE,"E1850"),sQuery(id+"F11.wireOp",EDGE,"E1851"),sQuery(id+"F11.wireOp",EDGE,"E1852"),sQuery(id+"F11.wireOp",EDGE,"E1853"),sQuery(id+"F11.wireOp",EDGE,"E1854"),sQuery(id+"F11.wireOp",EDGE,"E1855"),sQuery(id+"F11.wireOp",EDGE,"E1856"),sQuery(id+"F11.wireOp",EDGE,"E1857"),sQuery(id+"F11.wireOp",EDGE,"E1858"),sQuery(id+"F11.wireOp",EDGE,"E1859"),sQuery(id+"F11.wireOp",EDGE,"E1860"),sQuery(id+"F11.wireOp",EDGE,"E1861"),sQuery(id+"F11.wireOp",EDGE,"E1862"),sQuery(id+"F11.wireOp",EDGE,"E1863"),sQuery(id+"F11.wireOp",EDGE,"E1864"),sQuery(id+"F11.wireOp",EDGE,"E1865"),sQuery(id+"F11.wireOp",EDGE,"E1866"),sQuery(id+"F11.wireOp",EDGE,"E1867"),sQuery(id+"F11.wireOp",EDGE,"E1868"),sQuery(id+"F11.wireOp",EDGE,"E1869"),sQuery(id+"F11.wireOp",EDGE,"E1870"),sQuery(id+"F11.wireOp",EDGE,"E1871"),sQuery(id+"F11.wireOp",EDGE,"E1872"),sQuery(id+"F11.wireOp",EDGE,"E1873"),sQuery(id+"F11.wireOp",EDGE,"E1874"),sQuery(id+"F11.wireOp",EDGE,"E1875"),sQuery(id+"F11.wireOp",EDGE,"E1876"),sQuery(id+"F11.wireOp",EDGE,"E1877"),sQuery(id+"F11.wireOp",EDGE,"E1878"),sQuery(id+"F11.wireOp",EDGE,"E1879"),sQuery(id+"F11.wireOp",EDGE,"E1880"),sQuery(id+"F11.wireOp",EDGE,"E1881"),sQuery(id+"F11.wireOp",EDGE,"E1882"),sQuery(id+"F11.wireOp",EDGE,"E1883"),sQuery(id+"F11.wireOp",EDGE,"E1884"),sQuery(id+"F11.wireOp",EDGE,"E1885"),sQuery(id+"F11.wireOp",EDGE,"E1886"),sQuery(id+"F11.wireOp",EDGE,"E1887"),sQuery(id+"F11.wireOp",EDGE,"E1888"),sQuery(id+"F11.wireOp",EDGE,"E1889"),sQuery(id+"F11.wireOp",EDGE,"E1890"),sQuery(id+"F11.wireOp",EDGE,"E1891"),sQuery(id+"F11.wireOp",EDGE,"E1892"),sQuery(id+"F11.wireOp",EDGE,"E1893"),sQuery(id+"F11.wireOp",EDGE,"E1894"),sQuery(id+"F11.wireOp",EDGE,"E1895"),sQuery(id+"F11.wireOp",EDGE,"E1896"),sQuery(id+"F11.wireOp",EDGE,"E1897"),sQuery(id+"F11.wireOp",EDGE,"E1898"),sQuery(id+"F11.wireOp",EDGE,"E1899"),sQuery(id+"F11.wireOp",EDGE,"E1900"),sQuery(id+"F11.wireOp",EDGE,"E1901"),sQuery(id+"F11.wireOp",EDGE,"E1902"),sQuery(id+"F11.wireOp",EDGE,"E1903"),sQuery(id+"F11.wireOp",EDGE,"E1904"),sQuery(id+"F11.wireOp",EDGE,"E1905"),sQuery(id+"F11.wireOp",EDGE,"E1906"),sQuery(id+"F11.wireOp",EDGE,"E1907"),sQuery(id+"F11.wireOp",EDGE,"E1908"),sQuery(id+"F11.wireOp",EDGE,"E1909"),sQuery(id+"F11.wireOp",EDGE,"E1910"),sQuery(id+"F11.wireOp",EDGE,"E1911"),sQuery(id+"F11.wireOp",EDGE,"E1912"),sQuery(id+"F11.wireOp",EDGE,"E1913"),sQuery(id+"F11.wireOp",EDGE,"E1914"),sQuery(id+"F11.wireOp",EDGE,"E1915"),sQuery(id+"F11.wireOp",EDGE,"E1916"),sQuery(id+"F11.wireOp",EDGE,"E1917"),sQuery(id+"F11.wireOp",EDGE,"E1918"),sQuery(id+"F11.wireOp",EDGE,"E1919"),sQuery(id+"F11.wireOp",EDGE,"E1920"),sQuery(id+"F11.wireOp",EDGE,"E1921"),sQuery(id+"F11.wireOp",EDGE,"E1922"),sQuery(id+"F11.wireOp",EDGE,"E1923"),sQuery(id+"F11.wireOp",EDGE,"E1924"),sQuery(id+"F11.wireOp",EDGE,"E1925"),sQuery(id+"F11.wireOp",EDGE,"E1926"),sQuery(id+"F11.wireOp",EDGE,"E1927"),sQuery(id+"F11.wireOp",EDGE,"E1928"),sQuery(id+"F11.wireOp",EDGE,"E1929"),sQuery(id+"F11.wireOp",EDGE,"E1930"),sQuery(id+"F11.wireOp",EDGE,"E1931"),sQuery(id+"F11.wireOp",EDGE,"E1932"),sQuery(id+"F11.wireOp",EDGE,"E1933"),sQuery(id+"F11.wireOp",EDGE,"E1934"),sQuery(id+"F11.wireOp",EDGE,"E1935"),sQuery(id+"F11.wireOp",EDGE,"E1936"),sQuery(id+"F11.wireOp",EDGE,"E1937"),sQuery(id+"F11.wireOp",EDGE,"E1938"),sQuery(id+"F11.wireOp",EDGE,"E1939"),sQuery(id+"F11.wireOp",EDGE,"E1940"),sQuery(id+"F11.wireOp",EDGE,"E1941"),sQuery(id+"F11.wireOp",EDGE,"E1942"),sQuery(id+"F11.wireOp",EDGE,"E1943"),sQuery(id+"F11.wireOp",EDGE,"E1944"),sQuery(id+"F11.wireOp",EDGE,"E1945"),sQuery(id+"F11.wireOp",EDGE,"E1946"),sQuery(id+"F11.wireOp",EDGE,"E1947"),sQuery(id+"F11.wireOp",EDGE,"E1948"),sQuery(id+"F11.wireOp",EDGE,"E1949"),sQuery(id+"F11.wireOp",EDGE,"E1950"),sQuery(id+"F11.wireOp",EDGE,"E1951"),sQuery(id+"F11.wireOp",EDGE,"E1952"),sQuery(id+"F11.wireOp",EDGE,"E1953"),sQuery(id+"F11.wireOp",EDGE,"E1954"),sQuery(id+"F11.wireOp",EDGE,"E1955"),sQuery(id+"F11.wireOp",EDGE,"E1956"),sQuery(id+"F11.wireOp",EDGE,"E1957"),sQuery(id+"F11.wireOp",EDGE,"E1958"),sQuery(id+"F11.wireOp",EDGE,"E1959"),sQuery(id+"F11.wireOp",EDGE,"E1960"),sQuery(id+"F11.wireOp",EDGE,"E1961"),sQuery(id+"F11.wireOp",EDGE,"E1962"),sQuery(id+"F11.wireOp",EDGE,"E1963"),sQuery(id+"F11.wireOp",EDGE,"E1964"),sQuery(id+"F11.wireOp",EDGE,"E1965"),sQuery(id+"F11.wireOp",EDGE,"E1966"),sQuery(id+"F11.wireOp",EDGE,"E1967"),sQuery(id+"F11.wireOp",EDGE,"E1968"),sQuery(id+"F11.wireOp",EDGE,"E1969"),sQuery(id+"F11.wireOp",EDGE,"E1970"),sQuery(id+"F11.wireOp",EDGE,"E1971"),sQuery(id+"F11.wireOp",EDGE,"E1972"),sQuery(id+"F11.wireOp",EDGE,"E1973"),sQuery(id+"F11.wireOp",EDGE,"E1974"),sQuery(id+"F11.wireOp",EDGE,"E1975"),sQuery(id+"F11.wireOp",EDGE,"E1976"),sQuery(id+"F11.wireOp",EDGE,"E1977"),sQuery(id+"F11.wireOp",EDGE,"E1978"),sQuery(id+"F11.wireOp",EDGE,"E1979"),sQuery(id+"F11.wireOp",EDGE,"E1980"),sQuery(id+"F11.wireOp",EDGE,"E1981"),sQuery(id+"F11.wireOp",EDGE,"E1982"),sQuery(id+"F11.wireOp",EDGE,"E1983"),sQuery(id+"F11.wireOp",EDGE,"E1984"),sQuery(id+"F11.wireOp",EDGE,"E1985"),sQuery(id+"F11.wireOp",EDGE,"E1986"),sQuery(id+"F11.wireOp",EDGE,"E1987"),sQuery(id+"F11.wireOp",EDGE,"E1988"),sQuery(id+"F11.wireOp",EDGE,"E1989"),sQuery(id+"F11.wireOp",EDGE,"E1990"),sQuery(id+"F11.wireOp",EDGE,"E1991"),sQuery(id+"F11.wireOp",EDGE,"E1992"),sQuery(id+"F11.wireOp",EDGE,"E1993"),sQuery(id+"F11.wireOp",EDGE,"E1994"),sQuery(id+"F11.wireOp",EDGE,"E1995"),sQuery(id+"F11.wireOp",EDGE,"E1996"),sQuery(id+"F11.wireOp",EDGE,"E1997"),sQuery(id+"F11.wireOp",EDGE,"E1998"),sQuery(id+"F11.wireOp",EDGE,"E1999"),sQuery(id+"F11.wireOp",EDGE,"E2000"),sQuery(id+"F11.wireOp",EDGE,"E2001"),sQuery(id+"F11.wireOp",EDGE,"E2002"),sQuery(id+"F11.wireOp",EDGE,"E2003"),sQuery(id+"F11.wireOp",EDGE,"E2004"),sQuery(id+"F11.wireOp",EDGE,"E2005"),sQuery(id+"F11.wireOp",EDGE,"E2006"),sQuery(id+"F11.wireOp",EDGE,"E2007"),sQuery(id+"F11.wireOp",EDGE,"E2008"),sQuery(id+"F11.wireOp",EDGE,"E2009"),sQuery(id+"F11.wireOp",EDGE,"E2010"),sQuery(id+"F11.wireOp",EDGE,"E2011"),sQuery(id+"F11.wireOp",EDGE,"E2012"),sQuery(id+"F11.wireOp",EDGE,"E2013"),sQuery(id+"F11.wireOp",EDGE,"E2014"),sQuery(id+"F11.wireOp",EDGE,"E2015"),sQuery(id+"F11.wireOp",EDGE,"E2016"),sQuery(id+"F11.wireOp",EDGE,"E2017"),sQuery(id+"F11.wireOp",EDGE,"E2018"),sQuery(id+"F11.wireOp",EDGE,"E2019"),sQuery(id+"F11.wireOp",EDGE,"E2020"),sQuery(id+"F11.wireOp",EDGE,"E2021"),sQuery(id+"F11.wireOp",EDGE,"E2022"),sQuery(id+"F11.wireOp",EDGE,"E2023"),sQuery(id+"F11.wireOp",EDGE,"E2024"),sQuery(id+"F11.wireOp",EDGE,"E2025"),sQuery(id+"F11.wireOp",EDGE,"E2026"),sQuery(id+"F11.wireOp",EDGE,"E2027"),sQuery(id+"F11.wireOp",EDGE,"E2028"),sQuery(id+"F11.wireOp",EDGE,"E2029"),sQuery(id+"F11.wireOp",EDGE,"E2030"),sQuery(id+"F11.wireOp",EDGE,"E2031"),sQuery(id+"F11.wireOp",EDGE,"E2032"),sQuery(id+"F11.wireOp",EDGE,"E2033"),sQuery(id+"F11.wireOp",EDGE,"E2034"),sQuery(id+"F11.wireOp",EDGE,"E2035"),sQuery(id+"F11.wireOp",EDGE,"E2036"),sQuery(id+"F11.wireOp",EDGE,"E2037"),sQuery(id+"F11.wireOp",EDGE,"E2038"),sQuery(id+"F11.wireOp",EDGE,"E2039"),sQuery(id+"F11.wireOp",EDGE,"E2040"),sQuery(id+"F11.wireOp",EDGE,"E2041"),sQuery(id+"F11.wireOp",EDGE,"E2042"),sQuery(id+"F11.wireOp",EDGE,"E2043"),sQuery(id+"F11.wireOp",EDGE,"E2044"),sQuery(id+"F11.wireOp",EDGE,"E2045"),sQuery(id+"F11.wireOp",EDGE,"E2046"),sQuery(id+"F11.wireOp",EDGE,"E2047"),sQuery(id+"F11.wireOp",EDGE,"E2048"),sQuery(id+"F11.wireOp",EDGE,"E2049"),sQuery(id+"F11.wireOp",EDGE,"E2050"),sQuery(id+"F11.wireOp",EDGE,"E2051"),sQuery(id+"F11.wireOp",EDGE,"E2052"),sQuery(id+"F11.wireOp",EDGE,"E2053"),sQuery(id+"F11.wireOp",EDGE,"E2054"),sQuery(id+"F11.wireOp",EDGE,"E2055"),sQuery(id+"F11.wireOp",EDGE,"E2056"),sQuery(id+"F11.wireOp",EDGE,"E2057"),sQuery(id+"F11.wireOp",EDGE,"E2058"),sQuery(id+"F11.wireOp",EDGE,"E2059"),sQuery(id+"F11.wireOp",EDGE,"E2060"),sQuery(id+"F11.wireOp",EDGE,"E2061"),sQuery(id+"F11.wireOp",EDGE,"E2062"),sQuery(id+"F11.wireOp",EDGE,"E2063"),sQuery(id+"F11.wireOp",EDGE,"E2064"),sQuery(id+"F11.wireOp",EDGE,"E2065"),sQuery(id+"F11.wireOp",EDGE,"E2066"),sQuery(id+"F11.wireOp",EDGE,"E2067"),sQuery(id+"F11.wireOp",EDGE,"E2068"),sQuery(id+"F11.wireOp",EDGE,"E2069"),sQuery(id+"F11.wireOp",EDGE,"E2070"),sQuery(id+"F11.wireOp",EDGE,"E2071"),sQuery(id+"F11.wireOp",EDGE,"E2072"),sQuery(id+"F11.wireOp",EDGE,"E2073"),sQuery(id+"F11.wireOp",EDGE,"E2074"),sQuery(id+"F11.wireOp",EDGE,"E2075"),sQuery(id+"F11.wireOp",EDGE,"E2076"),sQuery(id+"F11.wireOp",EDGE,"E2077"),sQuery(id+"F11.wireOp",EDGE,"E2078"),sQuery(id+"F11.wireOp",EDGE,"E2079"),sQuery(id+"F11.wireOp",EDGE,"E2080"),sQuery(id+"F11.wireOp",EDGE,"E2081"),sQuery(id+"F11.wireOp",EDGE,"E2082"),sQuery(id+"F11.wireOp",EDGE,"E2083"),sQuery(id+"F11.wireOp",EDGE,"E2084"),sQuery(id+"F11.wireOp",EDGE,"E2085"),sQuery(id+"F11.wireOp",EDGE,"E2086"),sQuery(id+"F11.wireOp",EDGE,"E2087"),sQuery(id+"F11.wireOp",EDGE,"E2088"),sQuery(id+"F11.wireOp",EDGE,"E2089"),sQuery(id+"F11.wireOp",EDGE,"E2090"),sQuery(id+"F11.wireOp",EDGE,"E2091"),sQuery(id+"F11.wireOp",EDGE,"E2092"),sQuery(id+"F11.wireOp",EDGE,"E2093"),sQuery(id+"F11.wireOp",EDGE,"E2094"),sQuery(id+"F11.wireOp",EDGE,"E2095"),sQuery(id+"F11.wireOp",EDGE,"E2096"),sQuery(id+"F11.wireOp",EDGE,"E2097"),sQuery(id+"F11.wireOp",EDGE,"E2098"),sQuery(id+"F11.wireOp",EDGE,"E2099"),sQuery(id+"F11.wireOp",EDGE,"E2100"),sQuery(id+"F11.wireOp",EDGE,"E2101"),sQuery(id+"F11.wireOp",EDGE,"E2102"),sQuery(id+"F11.wireOp",EDGE,"E2103"),sQuery(id+"F11.wireOp",EDGE,"E2104"),sQuery(id+"F11.wireOp",EDGE,"E2105"),sQuery(id+"F11.wireOp",EDGE,"E2106"),sQuery(id+"F11.wireOp",EDGE,"E2107"),sQuery(id+"F11.wireOp",EDGE,"E2108"),sQuery(id+"F11.wireOp",EDGE,"E2109"),sQuery(id+"F11.wireOp",EDGE,"E2110"),sQuery(id+"F11.wireOp",EDGE,"E2111"),sQuery(id+"F11.wireOp",EDGE,"E2112"),sQuery(id+"F11.wireOp",EDGE,"E2113"),sQuery(id+"F11.wireOp",EDGE,"E2114"),sQuery(id+"F11.wireOp",EDGE,"E2115"),sQuery(id+"F11.wireOp",EDGE,"E2116"),sQuery(id+"F11.wireOp",EDGE,"E2117"),sQuery(id+"F11.wireOp",EDGE,"E2118"),sQuery(id+"F11.wireOp",EDGE,"E2119"),sQuery(id+"F11.wireOp",EDGE,"E2120"),sQuery(id+"F11.wireOp",EDGE,"E2121"),sQuery(id+"F11.wireOp",EDGE,"E2122"),sQuery(id+"F11.wireOp",EDGE,"E2123"),sQuery(id+"F11.wireOp",EDGE,"E2124"),sQuery(id+"F11.wireOp",EDGE,"E2125"),sQuery(id+"F11.wireOp",EDGE,"E2126"),sQuery(id+"F11.wireOp",EDGE,"E2127"),sQuery(id+"F11.wireOp",EDGE,"E2128"),sQuery(id+"F11.wireOp",EDGE,"E2129"),sQuery(id+"F11.wireOp",EDGE,"E2130"),sQuery(id+"F11.wireOp",EDGE,"E2131"),sQuery(id+"F11.wireOp",EDGE,"E2132"),sQuery(id+"F11.wireOp",EDGE,"E2133"),sQuery(id+"F11.wireOp",EDGE,"E2134"),sQuery(id+"F11.wireOp",EDGE,"E2135"),sQuery(id+"F11.wireOp",EDGE,"E2136"),sQuery(id+"F11.wireOp",EDGE,"E2137"),sQuery(id+"F11.wireOp",EDGE,"E2138"),sQuery(id+"F11.wireOp",EDGE,"E2139"),sQuery(id+"F11.wireOp",EDGE,"E2140"),sQuery(id+"F11.wireOp",EDGE,"E2141"),sQuery(id+"F11.wireOp",EDGE,"E2142"),sQuery(id+"F11.wireOp",EDGE,"E2143"),sQuery(id+"F11.wireOp",EDGE,"E2144"),sQuery(id+"F11.wireOp",EDGE,"E2145"),sQuery(id+"F11.wireOp",EDGE,"E2146"),sQuery(id+"F11.wireOp",EDGE,"E2147"),sQuery(id+"F11.wireOp",EDGE,"E2148"),sQuery(id+"F11.wireOp",EDGE,"E2149"),sQuery(id+"F11.wireOp",EDGE,"E2150"),sQuery(id+"F11.wireOp",EDGE,"E2151"),sQuery(id+"F11.wireOp",EDGE,"E2152"),sQuery(id+"F11.wireOp",EDGE,"E2153"),sQuery(id+"F11.wireOp",EDGE,"E2154"),sQuery(id+"F11.wireOp",EDGE,"E2155"),sQuery(id+"F11.wireOp",EDGE,"E2156"),sQuery(id+"F11.wireOp",EDGE,"E2157"),sQuery(id+"F11.wireOp",EDGE,"E2158"),sQuery(id+"F11.wireOp",EDGE,"E2159"),sQuery(id+"F11.wireOp",EDGE,"E2160"),sQuery(id+"F11.wireOp",EDGE,"E2161"),sQuery(id+"F11.wireOp",EDGE,"E2162"),sQuery(id+"F11.wireOp",EDGE,"E2163"),sQuery(id+"F11.wireOp",EDGE,"E2164"),sQuery(id+"F11.wireOp",EDGE,"E2165"),sQuery(id+"F11.wireOp",EDGE,"E2166"),sQuery(id+"F11.wireOp",EDGE,"E2167"),sQuery(id+"F11.wireOp",EDGE,"E2168"),sQuery(id+"F11.wireOp",EDGE,"E2169"),sQuery(id+"F11.wireOp",EDGE,"E2170"),sQuery(id+"F11.wireOp",EDGE,"E2171"),sQuery(id+"F11.wireOp",EDGE,"E2172"),sQuery(id+"F11.wireOp",EDGE,"E2173"),sQuery(id+"F11.wireOp",EDGE,"E2174"),sQuery(id+"F11.wireOp",EDGE,"E2175"),sQuery(id+"F11.wireOp",EDGE,"E2176"),sQuery(id+"F11.wireOp",EDGE,"E2177"),sQuery(id+"F11.wireOp",EDGE,"E2178"),sQuery(id+"F11.wireOp",EDGE,"E2179"),sQuery(id+"F11.wireOp",EDGE,"E2180"),sQuery(id+"F11.wireOp",EDGE,"E2181"),sQuery(id+"F11.wireOp",EDGE,"E2182"),sQuery(id+"F11.wireOp",EDGE,"E2183"),sQuery(id+"F11.wireOp",EDGE,"E2184"),sQuery(id+"F11.wireOp",EDGE,"E2185"),sQuery(id+"F11.wireOp",EDGE,"E2186"),sQuery(id+"F11.wireOp",EDGE,"E2187"),sQuery(id+"F11.wireOp",EDGE,"E2188"),sQuery(id+"F11.wireOp",EDGE,"E2189"),sQuery(id+"F11.wireOp",EDGE,"E2190"),sQuery(id+"F11.wireOp",EDGE,"E2191"),sQuery(id+"F11.wireOp",EDGE,"E2192"),sQuery(id+"F11.wireOp",EDGE,"E2193"),sQuery(id+"F11.wireOp",EDGE,"E2194"),sQuery(id+"F11.wireOp",EDGE,"E2195"),sQuery(id+"F11.wireOp",EDGE,"E2196"),sQuery(id+"F11.wireOp",EDGE,"E2197"),sQuery(id+"F11.wireOp",EDGE,"E2198"),sQuery(id+"F11.wireOp",EDGE,"E2199"),sQuery(id+"F11.wireOp",EDGE,"E2200"),sQuery(id+"F11.wireOp",EDGE,"E2201"),sQuery(id+"F11.wireOp",EDGE,"E2202"),sQuery(id+"F11.wireOp",EDGE,"E2203"),sQuery(id+"F11.wireOp",EDGE,"E2204"),sQuery(id+"F11.wireOp",EDGE,"E2205"),sQuery(id+"F11.wireOp",EDGE,"E2206"),sQuery(id+"F11.wireOp",EDGE,"E2207"),sQuery(id+"F11.wireOp",EDGE,"E2208"),sQuery(id+"F11.wireOp",EDGE,"E2209"),sQuery(id+"F11.wireOp",EDGE,"E2210"),sQuery(id+"F11.wireOp",EDGE,"E2211"),sQuery(id+"F11.wireOp",EDGE,"E2212"),sQuery(id+"F11.wireOp",EDGE,"E2213"),sQuery(id+"F11.wireOp",EDGE,"E2214"),sQuery(id+"F11.wireOp",EDGE,"E2215"),sQuery(id+"F11.wireOp",EDGE,"E2216"),sQuery(id+"F11.wireOp",EDGE,"E2217"),sQuery(id+"F11.wireOp",EDGE,"E2218"),sQuery(id+"F11.wireOp",EDGE,"E2219"),sQuery(id+"F11.wireOp",EDGE,"E2220"),sQuery(id+"F11.wireOp",EDGE,"E2221"),sQuery(id+"F11.wireOp",EDGE,"E2222"),sQuery(id+"F11.wireOp",EDGE,"E2223"),sQuery(id+"F11.wireOp",EDGE,"E2224"),sQuery(id+"F11.wireOp",EDGE,"E2225"),sQuery(id+"F11.wireOp",EDGE,"E2226"),sQuery(id+"F11.wireOp",EDGE,"E2227"),sQuery(id+"F11.wireOp",EDGE,"E2228"),sQuery(id+"F11.wireOp",EDGE,"E2229"),sQuery(id+"F11.wireOp",EDGE,"E2230"),sQuery(id+"F11.wireOp",EDGE,"E2231"),sQuery(id+"F11.wireOp",EDGE,"E2232"),sQuery(id+"F11.wireOp",EDGE,"E2233"),sQuery(id+"F11.wireOp",EDGE,"E2234"),sQuery(id+"F11.wireOp",EDGE,"E2235"),sQuery(id+"F11.wireOp",EDGE,"E2236"),sQuery(id+"F11.wireOp",EDGE,"E2237"),sQuery(id+"F11.wireOp",EDGE,"E2238"),sQuery(id+"F11.wireOp",EDGE,"E2239"),sQuery(id+"F11.wireOp",EDGE,"E2240"),sQuery(id+"F11.wireOp",EDGE,"E2241"),sQuery(id+"F11.wireOp",EDGE,"E2242"),sQuery(id+"F11.wireOp",EDGE,"E2243"),sQuery(id+"F11.wireOp",EDGE,"E2244"),sQuery(id+"F11.wireOp",EDGE,"E2245"),sQuery(id+"F11.wireOp",EDGE,"E2246"),sQuery(id+"F11.wireOp",EDGE,"E2247"),sQuery(id+"F11.wireOp",EDGE,"E2248"),sQuery(id+"F11.wireOp",EDGE,"E2249"),sQuery(id+"F11.wireOp",EDGE,"E2250"),sQuery(id+"F11.wireOp",EDGE,"E2251"),sQuery(id+"F11.wireOp",EDGE,"E2252"),sQuery(id+"F11.wireOp",EDGE,"E2253"),sQuery(id+"F11.wireOp",EDGE,"E2254"),sQuery(id+"F11.wireOp",EDGE,"E2255"),sQuery(id+"F11.wireOp",EDGE,"E2256"),sQuery(id+"F11.wireOp",EDGE,"E2257"),sQuery(id+"F11.wireOp",EDGE,"E2258"),sQuery(id+"F11.wireOp",EDGE,"E2259"),sQuery(id+"F11.wireOp",EDGE,"E2260"),sQuery(id+"F11.wireOp",EDGE,"E2261"),sQuery(id+"F11.wireOp",EDGE,"E2262"),sQuery(id+"F11.wireOp",EDGE,"E2263"),sQuery(id+"F11.wireOp",EDGE,"E2264"),sQuery(id+"F11.wireOp",EDGE,"E2265"),sQuery(id+"F11.wireOp",EDGE,"E2266"),sQuery(id+"F11.wireOp",EDGE,"E2267"),sQuery(id+"F11.wireOp",EDGE,"E2268"),sQuery(id+"F11.wireOp",EDGE,"E2269"),sQuery(id+"F11.wireOp",EDGE,"E2270"),sQuery(id+"F11.wireOp",EDGE,"E2271"),sQuery(id+"F11.wireOp",EDGE,"E2272"),sQuery(id+"F11.wireOp",EDGE,"E2273"),sQuery(id+"F11.wireOp",EDGE,"E2274"),sQuery(id+"F11.wireOp",EDGE,"E2275"),sQuery(id+"F11.wireOp",EDGE,"E2276"),sQuery(id+"F11.wireOp",EDGE,"E2277"),sQuery(id+"F11.wireOp",EDGE,"E2278"),sQuery(id+"F11.wireOp",EDGE,"E2279"),sQuery(id+"F11.wireOp",EDGE,"E2280"),sQuery(id+"F11.wireOp",EDGE,"E2281"),sQuery(id+"F11.wireOp",EDGE,"E2282"),sQuery(id+"F11.wireOp",EDGE,"E2283"),sQuery(id+"F11.wireOp",EDGE,"E2284"),sQuery(id+"F11.wireOp",EDGE,"E2285"),sQuery(id+"F11.wireOp",EDGE,"E2286"),sQuery(id+"F11.wireOp",EDGE,"E2287"),sQuery(id+"F11.wireOp",EDGE,"E2288"),sQuery(id+"F11.wireOp",EDGE,"E2289"),sQuery(id+"F11.wireOp",EDGE,"E2290"),sQuery(id+"F11.wireOp",EDGE,"E2291"),sQuery(id+"F11.wireOp",EDGE,"E2292"),sQuery(id+"F11.wireOp",EDGE,"E2293"),sQuery(id+"F11.wireOp",EDGE,"E2294"),sQuery(id+"F11.wireOp",EDGE,"E2295"),sQuery(id+"F11.wireOp",EDGE,"E2296"),sQuery(id+"F11.wireOp",EDGE,"E2297"),sQuery(id+"F11.wireOp",EDGE,"E2298"),sQuery(id+"F11.wireOp",EDGE,"E2299"),sQuery(id+"F11.wireOp",EDGE,"E2300"),sQuery(id+"F11.wireOp",EDGE,"E2301"),sQuery(id+"F11.wireOp",EDGE,"E2302"),sQuery(id+"F11.wireOp",EDGE,"E2303"),sQuery(id+"F11.wireOp",EDGE,"E2304"),sQuery(id+"F11.wireOp",EDGE,"E2305"),sQuery(id+"F11.wireOp",EDGE,"E2306"),sQuery(id+"F11.wireOp",EDGE,"E2307"),sQuery(id+"F11.wireOp",EDGE,"E2308"),sQuery(id+"F11.wireOp",EDGE,"E2309"),sQuery(id+"F11.wireOp",EDGE,"E2310"),sQuery(id+"F11.wireOp",EDGE,"E2311"),sQuery(id+"F11.wireOp",EDGE,"E2312"),sQuery(id+"F11.wireOp",EDGE,"E2313"),sQuery(id+"F11.wireOp",EDGE,"E2314"),sQuery(id+"F11.wireOp",EDGE,"E2315"),sQuery(id+"F11.wireOp",EDGE,"E2316"),sQuery(id+"F11.wireOp",EDGE,"E2317"),sQuery(id+"F11.wireOp",EDGE,"E2318"),sQuery(id+"F11.wireOp",EDGE,"E2319"),sQuery(id+"F11.wireOp",EDGE,"E2320"),sQuery(id+"F11.wireOp",EDGE,"E2321"),sQuery(id+"F11.wireOp",EDGE,"E2322"),sQuery(id+"F11.wireOp",EDGE,"E2323"),sQuery(id+"F11.wireOp",EDGE,"E2324"),sQuery(id+"F11.wireOp",EDGE,"E2325"),sQuery(id+"F11.wireOp",EDGE,"E2326"),sQuery(id+"F11.wireOp",EDGE,"E2327"),sQuery(id+"F11.wireOp",EDGE,"E2328"),sQuery(id+"F11.wireOp",EDGE,"E2329"),sQuery(id+"F11.wireOp",EDGE,"E2330"),sQuery(id+"F11.wireOp",EDGE,"E2331"),sQuery(id+"F11.wireOp",EDGE,"E2332"),sQuery(id+"F11.wireOp",EDGE,"E2333"),sQuery(id+"F11.wireOp",EDGE,"E2334"),sQuery(id+"F11.wireOp",EDGE,"E2335"),sQuery(id+"F11.wireOp",EDGE,"E2336"),sQuery(id+"F11.wireOp",EDGE,"E2337"),sQuery(id+"F11.wireOp",EDGE,"E2338"),sQuery(id+"F11.wireOp",EDGE,"E2339"),sQuery(id+"F11.wireOp",EDGE,"E2340"),sQuery(id+"F11.wireOp",EDGE,"E2341"),sQuery(id+"F11.wireOp",EDGE,"E2342"),sQuery(id+"F11.wireOp",EDGE,"E2343"),sQuery(id+"F11.wireOp",EDGE,"E2344"),sQuery(id+"F11.wireOp",EDGE,"E2345"),sQuery(id+"F11.wireOp",EDGE,"E2346"),sQuery(id+"F11.wireOp",EDGE,"E2347"),sQuery(id+"F11.wireOp",EDGE,"E2348"),sQuery(id+"F11.wireOp",EDGE,"E2349"),sQuery(id+"F11.wireOp",EDGE,"E2350"),sQuery(id+"F11.wireOp",EDGE,"E2351"),sQuery(id+"F11.wireOp",EDGE,"E2352"),sQuery(id+"F11.wireOp",EDGE,"E2353"),sQuery(id+"F11.wireOp",EDGE,"E2354"),sQuery(id+"F11.wireOp",EDGE,"E2355"),sQuery(id+"F11.wireOp",EDGE,"E2356"),sQuery(id+"F11.wireOp",EDGE,"E2357"),sQuery(id+"F11.wireOp",EDGE,"E2358"),sQuery(id+"F11.wireOp",EDGE,"E2359"),sQuery(id+"F11.wireOp",EDGE,"E2360"),sQuery(id+"F11.wireOp",EDGE,"E2361"),sQuery(id+"F11.wireOp",EDGE,"E2362"),sQuery(id+"F11.wireOp",EDGE,"E2363"),sQuery(id+"F11.wireOp",EDGE,"E2364"),sQuery(id+"F11.wireOp",EDGE,"E2365"),sQuery(id+"F11.wireOp",EDGE,"E2366"),sQuery(id+"F11.wireOp",EDGE,"E2367"),sQuery(id+"F11.wireOp",EDGE,"E2368"),sQuery(id+"F11.wireOp",EDGE,"E2369"),sQuery(id+"F11.wireOp",EDGE,"E2370"),sQuery(id+"F11.wireOp",EDGE,"E2371"),sQuery(id+"F11.wireOp",EDGE,"E2372"),sQuery(id+"F11.wireOp",EDGE,"E2373"),sQuery(id+"F11.wireOp",EDGE,"E2374"),sQuery(id+"F11.wireOp",EDGE,"E2375"),sQuery(id+"F11.wireOp",EDGE,"E2376"),sQuery(id+"F11.wireOp",EDGE,"E2377"),sQuery(id+"F11.wireOp",EDGE,"E2378"),sQuery(id+"F11.wireOp",EDGE,"E2379"),sQuery(id+"F11.wireOp",EDGE,"E2380"),sQuery(id+"F11.wireOp",EDGE,"E2381"),sQuery(id+"F11.wireOp",EDGE,"E2382"),sQuery(id+"F11.wireOp",EDGE,"E2383"),sQuery(id+"F11.wireOp",EDGE,"E2384"),sQuery(id+"F11.wireOp",EDGE,"E2385"),sQuery(id+"F11.wireOp",EDGE,"E2386"),sQuery(id+"F11.wireOp",EDGE,"E2387"),sQuery(id+"F11.wireOp",EDGE,"E2388"),sQuery(id+"F11.wireOp",EDGE,"E2389"),sQuery(id+"F11.wireOp",EDGE,"E2390"),sQuery(id+"F11.wireOp",EDGE,"E2391"),sQuery(id+"F11.wireOp",EDGE,"E2392"),sQuery(id+"F11.wireOp",EDGE,"E2393"),sQuery(id+"F11.wireOp",EDGE,"E2394"),sQuery(id+"F11.wireOp",EDGE,"E2395"),sQuery(id+"F11.wireOp",EDGE,"E2396"),sQuery(id+"F11.wireOp",EDGE,"E2397"),sQuery(id+"F11.wireOp",EDGE,"E2398"),sQuery(id+"F11.wireOp",EDGE,"E2399"),sQuery(id+"F11.wireOp",EDGE,"E2400"),sQuery(id+"F11.wireOp",EDGE,"E2401"),sQuery(id+"F11.wireOp",EDGE,"E2402"),sQuery(id+"F11.wireOp",EDGE,"E2403"),sQuery(id+"F11.wireOp",EDGE,"E2404"),sQuery(id+"F11.wireOp",EDGE,"E2405"),sQuery(id+"F11.wireOp",EDGE,"E2406"),sQuery(id+"F11.wireOp",EDGE,"E2407"),sQuery(id+"F11.wireOp",EDGE,"E2408"),sQuery(id+"F11.wireOp",EDGE,"E2409"),sQuery(id+"F11.wireOp",EDGE,"E2410"),sQuery(id+"F11.wireOp",EDGE,"E2411"),sQuery(id+"F11.wireOp",EDGE,"E2412"),sQuery(id+"F11.wireOp",EDGE,"E2413"),sQuery(id+"F11.wireOp",EDGE,"E2414"),sQuery(id+"F11.wireOp",EDGE,"E2415"),sQuery(id+"F11.wireOp",EDGE,"E2416"),sQuery(id+"F11.wireOp",EDGE,"E2417"),sQuery(id+"F11.wireOp",EDGE,"E2418"),sQuery(id+"F11.wireOp",EDGE,"E2419"),sQuery(id+"F11.wireOp",EDGE,"E2420"),sQuery(id+"F11.wireOp",EDGE,"E2421"),sQuery(id+"F11.wireOp",EDGE,"E2422"),sQuery(id+"F11.wireOp",EDGE,"E2423"),sQuery(id+"F11.wireOp",EDGE,"E2424"),sQuery(id+"F11.wireOp",EDGE,"E2425"),sQuery(id+"F11.wireOp",EDGE,"E2426"),sQuery(id+"F11.wireOp",EDGE,"E2427"),sQuery(id+"F11.wireOp",EDGE,"E2428"),sQuery(id+"F11.wireOp",EDGE,"E2429"),sQuery(id+"F11.wireOp",EDGE,"E2430"),sQuery(id+"F11.wireOp",EDGE,"E2431"),sQuery(id+"F11.wireOp",EDGE,"E2432"),sQuery(id+"F11.wireOp",EDGE,"E2433"),sQuery(id+"F11.wireOp",EDGE,"E2434"),sQuery(id+"F11.wireOp",EDGE,"E2435"),sQuery(id+"F11.wireOp",EDGE,"E2436"),sQuery(id+"F11.wireOp",EDGE,"E2437"),sQuery(id+"F11.wireOp",EDGE,"E2438"),sQuery(id+"F11.wireOp",EDGE,"E2439"),sQuery(id+"F11.wireOp",EDGE,"E2440"),sQuery(id+"F11.wireOp",EDGE,"E2441"),sQuery(id+"F11.wireOp",EDGE,"E2442"),sQuery(id+"F11.wireOp",EDGE,"E2443"),sQuery(id+"F11.wireOp",EDGE,"E2444"),sQuery(id+"F11.wireOp",EDGE,"E2445"),sQuery(id+"F11.wireOp",EDGE,"E2446"),sQuery(id+"F11.wireOp",EDGE,"E2447"),sQuery(id+"F11.wireOp",EDGE,"E2448"),sQuery(id+"F11.wireOp",EDGE,"E2449"),sQuery(id+"F11.wireOp",EDGE,"E2450"),sQuery(id+"F11.wireOp",EDGE,"E2451"),sQuery(id+"F11.wireOp",EDGE,"E2452"),sQuery(id+"F11.wireOp",EDGE,"E2453"),sQuery(id+"F11.wireOp",EDGE,"E2454"),sQuery(id+"F11.wireOp",EDGE,"E2455"),sQuery(id+"F11.wireOp",EDGE,"E2456"),sQuery(id+"F11.wireOp",EDGE,"E2457"),sQuery(id+"F11.wireOp",EDGE,"E2458"),sQuery(id+"F11.wireOp",EDGE,"E2459"),sQuery(id+"F11.wireOp",EDGE,"E2460"),sQuery(id+"F11.wireOp",EDGE,"E2461"),sQuery(id+"F11.wireOp",EDGE,"E2462"),sQuery(id+"F11.wireOp",EDGE,"E2463"),sQuery(id+"F11.wireOp",EDGE,"E2464"),sQuery(id+"F11.wireOp",EDGE,"E2465"),sQuery(id+"F11.wireOp",EDGE,"E2466"),sQuery(id+"F11.wireOp",EDGE,"E2467"),sQuery(id+"F11.wireOp",EDGE,"E2468"),sQuery(id+"F11.wireOp",EDGE,"E2469"),sQuery(id+"F11.wireOp",EDGE,"E2470"),sQuery(id+"F11.wireOp",EDGE,"E2471"),sQuery(id+"F11.wireOp",EDGE,"E2472"),sQuery(id+"F11.wireOp",EDGE,"E2473"),sQuery(id+"F11.wireOp",EDGE,"E2474"),sQuery(id+"F11.wireOp",EDGE,"E2475"),sQuery(id+"F11.wireOp",EDGE,"E2476"),sQuery(id+"F11.wireOp",EDGE,"E2477"),sQuery(id+"F11.wireOp",EDGE,"E2478"),sQuery(id+"F11.wireOp",EDGE,"E2479"),sQuery(id+"F11.wireOp",EDGE,"E2480"),sQuery(id+"F11.wireOp",EDGE,"E2481"),sQuery(id+"F11.wireOp",EDGE,"E2482"),sQuery(id+"F11.wireOp",EDGE,"E2483"),sQuery(id+"F11.wireOp",EDGE,"E2484"),sQuery(id+"F11.wireOp",EDGE,"E2485"),sQuery(id+"F11.wireOp",EDGE,"E2486"),sQuery(id+"F11.wireOp",EDGE,"E2487"),sQuery(id+"F11.wireOp",EDGE,"E2488"),sQuery(id+"F11.wireOp",EDGE,"E2489"),sQuery(id+"F11.wireOp",EDGE,"E2490"),sQuery(id+"F11.wireOp",EDGE,"E2491"),sQuery(id+"F11.wireOp",EDGE,"E2492"),sQuery(id+"F11.wireOp",EDGE,"E2493"),sQuery(id+"F11.wireOp",EDGE,"E2494"),sQuery(id+"F11.wireOp",EDGE,"E2495"),sQuery(id+"F11.wireOp",EDGE,"E2496"),sQuery(id+"F11.wireOp",EDGE,"E2497"),sQuery(id+"F11.wireOp",EDGE,"E2498"),sQuery(id+"F11.wireOp",EDGE,"E2499"),sQuery(id+"F11.wireOp",EDGE,"E2500"),sQuery(id+"F11.wireOp",EDGE,"E2501"),sQuery(id+"F11.wireOp",EDGE,"E2502"),sQuery(id+"F11.wireOp",EDGE,"E2503"),sQuery(id+"F11.wireOp",EDGE,"E2504"),sQuery(id+"F11.wireOp",EDGE,"E2505"),sQuery(id+"F11.wireOp",EDGE,"E2506"),sQuery(id+"F11.wireOp",EDGE,"E2507"),sQuery(id+"F11.wireOp",EDGE,"E2508"),sQuery(id+"F11.wireOp",EDGE,"E2509"),sQuery(id+"F11.wireOp",EDGE,"E2510"),sQuery(id+"F11.wireOp",EDGE,"E2511"),sQuery(id+"F11.wireOp",EDGE,"E2512"),sQuery(id+"F11.wireOp",EDGE,"E2513"),sQuery(id+"F11.wireOp",EDGE,"E2514"),sQuery(id+"F11.wireOp",EDGE,"E2515"),sQuery(id+"F11.wireOp",EDGE,"E2516"),sQuery(id+"F11.wireOp",EDGE,"E2517"),sQuery(id+"F11.wireOp",EDGE,"E2518"),sQuery(id+"F11.wireOp",EDGE,"E2519"),sQuery(id+"F11.wireOp",EDGE,"E2520"),sQuery(id+"F11.wireOp",EDGE,"E2521"),sQuery(id+"F11.wireOp",EDGE,"E2522"),sQuery(id+"F11.wireOp",EDGE,"E2523"),sQuery(id+"F11.wireOp",EDGE,"E2524"),sQuery(id+"F11.wireOp",EDGE,"E2525"),sQuery(id+"F11.wireOp",EDGE,"E2526"),sQuery(id+"F11.wireOp",EDGE,"E2527"),sQuery(id+"F11.wireOp",EDGE,"E2528"),sQuery(id+"F11.wireOp",EDGE,"E2529"),sQuery(id+"F11.wireOp",EDGE,"E2530"),sQuery(id+"F11.wireOp",EDGE,"E2531"),sQuery(id+"F11.wireOp",EDGE,"E2532"),sQuery(id+"F11.wireOp",EDGE,"E2533"),sQuery(id+"F11.wireOp",EDGE,"E2534"),sQuery(id+"F11.wireOp",EDGE,"E2535"),sQuery(id+"F11.wireOp",EDGE,"E2536"),sQuery(id+"F11.wireOp",EDGE,"E2537"),sQuery(id+"F11.wireOp",EDGE,"E2538"),sQuery(id+"F11.wireOp",EDGE,"E2539"),sQuery(id+"F11.wireOp",EDGE,"E2540"),sQuery(id+"F11.wireOp",EDGE,"E2541"),sQuery(id+"F11.wireOp",EDGE,"E2542"),sQuery(id+"F11.wireOp",EDGE,"E2543"),sQuery(id+"F11.wireOp",EDGE,"E2544"),sQuery(id+"F11.wireOp",EDGE,"E2545"),sQuery(id+"F11.wireOp",EDGE,"E2546"),sQuery(id+"F11.wireOp",EDGE,"E2547"),sQuery(id+"F11.wireOp",EDGE,"E2548"),sQuery(id+"F11.wireOp",EDGE,"E2549"),sQuery(id+"F11.wireOp",EDGE,"E2550"),sQuery(id+"F11.wireOp",EDGE,"E2551"),sQuery(id+"F11.wireOp",EDGE,"E2552"),sQuery(id+"F11.wireOp",EDGE,"E2553"),sQuery(id+"F11.wireOp",EDGE,"E2554"),sQuery(id+"F11.wireOp",EDGE,"E2555"),sQuery(id+"F11.wireOp",EDGE,"E2556"),sQuery(id+"F11.wireOp",EDGE,"E2557"),sQuery(id+"F11.wireOp",EDGE,"E2558"),sQuery(id+"F11.wireOp",EDGE,"E2559"),sQuery(id+"F11.wireOp",EDGE,"E2560"),sQuery(id+"F11.wireOp",EDGE,"E2561"),sQuery(id+"F11.wireOp",EDGE,"E2562"),sQuery(id+"F11.wireOp",EDGE,"E2563"),sQuery(id+"F11.wireOp",EDGE,"E2564"),sQuery(id+"F11.wireOp",EDGE,"E2565"),sQuery(id+"F11.wireOp",EDGE,"E2566"),sQuery(id+"F11.wireOp",EDGE,"E2567"),sQuery(id+"F11.wireOp",EDGE,"E2568"),sQuery(id+"F11.wireOp",EDGE,"E2569"),sQuery(id+"F11.wireOp",EDGE,"E2570"),sQuery(id+"F11.wireOp",EDGE,"E2571"),sQuery(id+"F11.wireOp",EDGE,"E2572"),sQuery(id+"F11.wireOp",EDGE,"E2573"),sQuery(id+"F11.wireOp",EDGE,"E2574"),sQuery(id+"F11.wireOp",EDGE,"E2575"),sQuery(id+"F11.wireOp",EDGE,"E2576"),sQuery(id+"F11.wireOp",EDGE,"E2577"),sQuery(id+"F11.wireOp",EDGE,"E2578"),sQuery(id+"F11.wireOp",EDGE,"E2579"),sQuery(id+"F11.wireOp",EDGE,"E2580"),sQuery(id+"F11.wireOp",EDGE,"E2581"),sQuery(id+"F11.wireOp",EDGE,"E2582"),sQuery(id+"F11.wireOp",EDGE,"E2583"),sQuery(id+"F11.wireOp",EDGE,"E2584"),sQuery(id+"F11.wireOp",EDGE,"E2585"),sQuery(id+"F11.wireOp",EDGE,"E2586"),sQuery(id+"F11.wireOp",EDGE,"E2587"),sQuery(id+"F11.wireOp",EDGE,"E2588"),sQuery(id+"F11.wireOp",EDGE,"E2589"),sQuery(id+"F11.wireOp",EDGE,"E2590"),sQuery(id+"F11.wireOp",EDGE,"E2591"),sQuery(id+"F11.wireOp",EDGE,"E2592"),sQuery(id+"F11.wireOp",EDGE,"E2593"),sQuery(id+"F11.wireOp",EDGE,"E2594"),sQuery(id+"F11.wireOp",EDGE,"E2595"),sQuery(id+"F11.wireOp",EDGE,"E2596"),sQuery(id+"F11.wireOp",EDGE,"E2597"),sQuery(id+"F11.wireOp",EDGE,"E2598")])],"isStart":false});
            var sketch = newSketch(context, id + "F22", { "sketchPlane" : qUnion([Q0])});
            skLineSegment(sketch, "E5753", {"start": v(0, 11.2) * mm, "end": v(0, 21.2) * mm, "construction": true});
            skArc(sketch, "E5754.0.endCap", {"start": v(-1, 21.2) * mm, "mid": v(0, 22.2) * mm, "end": v(1, 21.2) * mm});
            skLineSegment(sketch, "E5754.0.left", {"start": v(-1, 11.78) * mm, "end": v(-1, 21.2) * mm});
            skLineSegment(sketch, "E5754.0.right", {"start": v(1, 11.78) * mm, "end": v(1, 21.2) * mm});
            skLineSegment(sketch, "E5755.1.0", {"start": v(0, 10.05) * mm, "end": v(-8.16, 5.34) * mm});
            skArc(sketch, "E5755.1.1", {"start": v(-8.16, 5.34) * mm, "mid": v(-9.53, 5.7) * mm, "end": v(-9.16, 7.07) * mm});
            skLineSegment(sketch, "E5755.1.2", {"start": v(-1, 11.78) * mm, "end": v(-9.16, 7.07) * mm});
            skLineSegment(sketch, "E5755.2.0", {"start": v(1, 11.78) * mm, "end": v(9.16, 7.07) * mm});
            skArc(sketch, "E5755.2.1", {"start": v(9.16, 7.07) * mm, "mid": v(9.53, 5.7) * mm, "end": v(8.16, 5.34) * mm});
            skLineSegment(sketch, "E5755.2.2", {"start": v(0, 10.05) * mm, "end": v(8.16, 5.34) * mm});
            skPoint(sketch, "E5755.center", {"position": v(0, 11.2) * mm});
            skPoint(sketch, "E5756.orphan", {"position": v(-0.5, 10.34) * mm});
            skPoint(sketch, "E5757.orphan", {"position": v(-1, 11.2) * mm});
            skPoint(sketch, "E5758.orphan", {"position": v(-0.5, 12.07) * mm});
            skSolve(sketch);
        }
        {
            var Q0;
            Q0 = qSketchRegion(id + "F22", true);
            extrude(context, id + "F23", {"entities" : qUnion([Q0]), "operationType" : NewBodyOperationType.ADD, "depth" : 10 * mm, "offsetDistance" : 25 * mm});
        }
        {
            var Q0;
            Q0=makeQuery(id+"F18.opExtrude","CAP_FACE",FACE,{"disambiguationData":[OSD([sQuery(id+"F17.wireOp",EDGE,"E2600"),sQuery(id+"F17.wireOp",EDGE,"E2601"),sQuery(id+"F17.wireOp",EDGE,"E2602"),sQuery(id+"F17.wireOp",EDGE,"E2603"),sQuery(id+"F17.wireOp",EDGE,"E2604"),sQuery(id+"F17.wireOp",EDGE,"E2605"),sQuery(id+"F17.wireOp",EDGE,"E2606"),sQuery(id+"F17.wireOp",EDGE,"E2607"),sQuery(id+"F17.wireOp",EDGE,"E2608"),sQuery(id+"F17.wireOp",EDGE,"E2609"),sQuery(id+"F17.wireOp",EDGE,"E2610"),sQuery(id+"F17.wireOp",EDGE,"E2611"),sQuery(id+"F17.wireOp",EDGE,"E2612"),sQuery(id+"F17.wireOp",EDGE,"E2613"),sQuery(id+"F17.wireOp",EDGE,"E2614"),sQuery(id+"F17.wireOp",EDGE,"E2615"),sQuery(id+"F17.wireOp",EDGE,"E2616"),sQuery(id+"F17.wireOp",EDGE,"E2617"),sQuery(id+"F17.wireOp",EDGE,"E2618"),sQuery(id+"F17.wireOp",EDGE,"E2619"),sQuery(id+"F17.wireOp",EDGE,"E2620"),sQuery(id+"F17.wireOp",EDGE,"E2621"),sQuery(id+"F17.wireOp",EDGE,"E2622"),sQuery(id+"F17.wireOp",EDGE,"E2623"),sQuery(id+"F17.wireOp",EDGE,"E2624"),sQuery(id+"F17.wireOp",EDGE,"E2625"),sQuery(id+"F17.wireOp",EDGE,"E2626"),sQuery(id+"F17.wireOp",EDGE,"E2627"),sQuery(id+"F17.wireOp",EDGE,"E2628"),sQuery(id+"F17.wireOp",EDGE,"E2629"),sQuery(id+"F17.wireOp",EDGE,"E2630"),sQuery(id+"F17.wireOp",EDGE,"E2631"),sQuery(id+"F17.wireOp",EDGE,"E2632"),sQuery(id+"F17.wireOp",EDGE,"E2633"),sQuery(id+"F17.wireOp",EDGE,"E2634"),sQuery(id+"F17.wireOp",EDGE,"E2635"),sQuery(id+"F17.wireOp",EDGE,"E2636"),sQuery(id+"F17.wireOp",EDGE,"E2637"),sQuery(id+"F17.wireOp",EDGE,"E2638"),sQuery(id+"F17.wireOp",EDGE,"E2639"),sQuery(id+"F17.wireOp",EDGE,"E2640"),sQuery(id+"F17.wireOp",EDGE,"E2641"),sQuery(id+"F17.wireOp",EDGE,"E2642"),sQuery(id+"F17.wireOp",EDGE,"E2643"),sQuery(id+"F17.wireOp",EDGE,"E2644"),sQuery(id+"F17.wireOp",EDGE,"E2645"),sQuery(id+"F17.wireOp",EDGE,"E2646"),sQuery(id+"F17.wireOp",EDGE,"E2647"),sQuery(id+"F17.wireOp",EDGE,"E2648"),sQuery(id+"F17.wireOp",EDGE,"E2649"),sQuery(id+"F17.wireOp",EDGE,"E2650"),sQuery(id+"F17.wireOp",EDGE,"E2651"),sQuery(id+"F17.wireOp",EDGE,"E2652"),sQuery(id+"F17.wireOp",EDGE,"E2653"),sQuery(id+"F17.wireOp",EDGE,"E2654"),sQuery(id+"F17.wireOp",EDGE,"E2655"),sQuery(id+"F17.wireOp",EDGE,"E2656"),sQuery(id+"F17.wireOp",EDGE,"E2657"),sQuery(id+"F17.wireOp",EDGE,"E2658"),sQuery(id+"F17.wireOp",EDGE,"E2659"),sQuery(id+"F17.wireOp",EDGE,"E2660"),sQuery(id+"F17.wireOp",EDGE,"E2661"),sQuery(id+"F17.wireOp",EDGE,"E2662"),sQuery(id+"F17.wireOp",EDGE,"E2663"),sQuery(id+"F17.wireOp",EDGE,"E2664"),sQuery(id+"F17.wireOp",EDGE,"E2665"),sQuery(id+"F17.wireOp",EDGE,"E2666"),sQuery(id+"F17.wireOp",EDGE,"E2667"),sQuery(id+"F17.wireOp",EDGE,"E2668"),sQuery(id+"F17.wireOp",EDGE,"E2669"),sQuery(id+"F17.wireOp",EDGE,"E2670"),sQuery(id+"F17.wireOp",EDGE,"E2671"),sQuery(id+"F17.wireOp",EDGE,"E2672"),sQuery(id+"F17.wireOp",EDGE,"E2673"),sQuery(id+"F17.wireOp",EDGE,"E2674"),sQuery(id+"F17.wireOp",EDGE,"E2675"),sQuery(id+"F17.wireOp",EDGE,"E2676"),sQuery(id+"F17.wireOp",EDGE,"E2677"),sQuery(id+"F17.wireOp",EDGE,"E2678"),sQuery(id+"F17.wireOp",EDGE,"E2679"),sQuery(id+"F17.wireOp",EDGE,"E2680"),sQuery(id+"F17.wireOp",EDGE,"E2681"),sQuery(id+"F17.wireOp",EDGE,"E2682"),sQuery(id+"F17.wireOp",EDGE,"E2683"),sQuery(id+"F17.wireOp",EDGE,"E2684"),sQuery(id+"F17.wireOp",EDGE,"E2685"),sQuery(id+"F17.wireOp",EDGE,"E2686"),sQuery(id+"F17.wireOp",EDGE,"E2687"),sQuery(id+"F17.wireOp",EDGE,"E2688"),sQuery(id+"F17.wireOp",EDGE,"E2689"),sQuery(id+"F17.wireOp",EDGE,"E2690"),sQuery(id+"F17.wireOp",EDGE,"E2691"),sQuery(id+"F17.wireOp",EDGE,"E2692"),sQuery(id+"F17.wireOp",EDGE,"E2693"),sQuery(id+"F17.wireOp",EDGE,"E2694"),sQuery(id+"F17.wireOp",EDGE,"E2695"),sQuery(id+"F17.wireOp",EDGE,"E2696"),sQuery(id+"F17.wireOp",EDGE,"E2697"),sQuery(id+"F17.wireOp",EDGE,"E2698"),sQuery(id+"F17.wireOp",EDGE,"E2699"),sQuery(id+"F17.wireOp",EDGE,"E2700"),sQuery(id+"F17.wireOp",EDGE,"E2701"),sQuery(id+"F17.wireOp",EDGE,"E2702"),sQuery(id+"F17.wireOp",EDGE,"E2703"),sQuery(id+"F17.wireOp",EDGE,"E2704"),sQuery(id+"F17.wireOp",EDGE,"E2705"),sQuery(id+"F17.wireOp",EDGE,"E2706"),sQuery(id+"F17.wireOp",EDGE,"E2707"),sQuery(id+"F17.wireOp",EDGE,"E2708"),sQuery(id+"F17.wireOp",EDGE,"E2709"),sQuery(id+"F17.wireOp",EDGE,"E2710"),sQuery(id+"F17.wireOp",EDGE,"E2711"),sQuery(id+"F17.wireOp",EDGE,"E2712"),sQuery(id+"F17.wireOp",EDGE,"E2713"),sQuery(id+"F17.wireOp",EDGE,"E2714"),sQuery(id+"F17.wireOp",EDGE,"E2715"),sQuery(id+"F17.wireOp",EDGE,"E2716"),sQuery(id+"F17.wireOp",EDGE,"E2717"),sQuery(id+"F17.wireOp",EDGE,"E2718"),sQuery(id+"F17.wireOp",EDGE,"E2719"),sQuery(id+"F17.wireOp",EDGE,"E2720"),sQuery(id+"F17.wireOp",EDGE,"E2721"),sQuery(id+"F17.wireOp",EDGE,"E2722"),sQuery(id+"F17.wireOp",EDGE,"E2723"),sQuery(id+"F17.wireOp",EDGE,"E2724"),sQuery(id+"F17.wireOp",EDGE,"E2725"),sQuery(id+"F17.wireOp",EDGE,"E2726"),sQuery(id+"F17.wireOp",EDGE,"E2727"),sQuery(id+"F17.wireOp",EDGE,"E2728"),sQuery(id+"F17.wireOp",EDGE,"E2729"),sQuery(id+"F17.wireOp",EDGE,"E2730"),sQuery(id+"F17.wireOp",EDGE,"E2731"),sQuery(id+"F17.wireOp",EDGE,"E2732"),sQuery(id+"F17.wireOp",EDGE,"E2733"),sQuery(id+"F17.wireOp",EDGE,"E2734"),sQuery(id+"F17.wireOp",EDGE,"E2735"),sQuery(id+"F17.wireOp",EDGE,"E2736"),sQuery(id+"F17.wireOp",EDGE,"E2737"),sQuery(id+"F17.wireOp",EDGE,"E2738"),sQuery(id+"F17.wireOp",EDGE,"E2739"),sQuery(id+"F17.wireOp",EDGE,"E2740"),sQuery(id+"F17.wireOp",EDGE,"E2741"),sQuery(id+"F17.wireOp",EDGE,"E2742"),sQuery(id+"F17.wireOp",EDGE,"E2743"),sQuery(id+"F17.wireOp",EDGE,"E2744"),sQuery(id+"F17.wireOp",EDGE,"E2745"),sQuery(id+"F17.wireOp",EDGE,"E2746"),sQuery(id+"F17.wireOp",EDGE,"E2747"),sQuery(id+"F17.wireOp",EDGE,"E2748"),sQuery(id+"F17.wireOp",EDGE,"E2749"),sQuery(id+"F17.wireOp",EDGE,"E2750"),sQuery(id+"F17.wireOp",EDGE,"E2751"),sQuery(id+"F17.wireOp",EDGE,"E2752"),sQuery(id+"F17.wireOp",EDGE,"E2753"),sQuery(id+"F17.wireOp",EDGE,"E2754"),sQuery(id+"F17.wireOp",EDGE,"E2755"),sQuery(id+"F17.wireOp",EDGE,"E2756"),sQuery(id+"F17.wireOp",EDGE,"E2757"),sQuery(id+"F17.wireOp",EDGE,"E2758"),sQuery(id+"F17.wireOp",EDGE,"E2759"),sQuery(id+"F17.wireOp",EDGE,"E2760"),sQuery(id+"F17.wireOp",EDGE,"E2761"),sQuery(id+"F17.wireOp",EDGE,"E2762"),sQuery(id+"F17.wireOp",EDGE,"E2763"),sQuery(id+"F17.wireOp",EDGE,"E2764"),sQuery(id+"F17.wireOp",EDGE,"E2765"),sQuery(id+"F17.wireOp",EDGE,"E2766"),sQuery(id+"F17.wireOp",EDGE,"E2767"),sQuery(id+"F17.wireOp",EDGE,"E2768"),sQuery(id+"F17.wireOp",EDGE,"E2769"),sQuery(id+"F17.wireOp",EDGE,"E2770"),sQuery(id+"F17.wireOp",EDGE,"E2771"),sQuery(id+"F17.wireOp",EDGE,"E2772"),sQuery(id+"F17.wireOp",EDGE,"E2773"),sQuery(id+"F17.wireOp",EDGE,"E2774"),sQuery(id+"F17.wireOp",EDGE,"E2775"),sQuery(id+"F17.wireOp",EDGE,"E2776"),sQuery(id+"F17.wireOp",EDGE,"E2777"),sQuery(id+"F17.wireOp",EDGE,"E2778"),sQuery(id+"F17.wireOp",EDGE,"E2779"),sQuery(id+"F17.wireOp",EDGE,"E2780"),sQuery(id+"F17.wireOp",EDGE,"E2781"),sQuery(id+"F17.wireOp",EDGE,"E2782"),sQuery(id+"F17.wireOp",EDGE,"E2783"),sQuery(id+"F17.wireOp",EDGE,"E2784"),sQuery(id+"F17.wireOp",EDGE,"E2785"),sQuery(id+"F17.wireOp",EDGE,"E2786"),sQuery(id+"F17.wireOp",EDGE,"E2787"),sQuery(id+"F17.wireOp",EDGE,"E2788"),sQuery(id+"F17.wireOp",EDGE,"E2789"),sQuery(id+"F17.wireOp",EDGE,"E2790"),sQuery(id+"F17.wireOp",EDGE,"E2791"),sQuery(id+"F17.wireOp",EDGE,"E2792"),sQuery(id+"F17.wireOp",EDGE,"E2793"),sQuery(id+"F17.wireOp",EDGE,"E2794"),sQuery(id+"F17.wireOp",EDGE,"E2795"),sQuery(id+"F17.wireOp",EDGE,"E2796"),sQuery(id+"F17.wireOp",EDGE,"E2797"),sQuery(id+"F17.wireOp",EDGE,"E2798"),sQuery(id+"F17.wireOp",EDGE,"E2799"),sQuery(id+"F17.wireOp",EDGE,"E2800"),sQuery(id+"F17.wireOp",EDGE,"E2801"),sQuery(id+"F17.wireOp",EDGE,"E2802"),sQuery(id+"F17.wireOp",EDGE,"E2803"),sQuery(id+"F17.wireOp",EDGE,"E2804"),sQuery(id+"F17.wireOp",EDGE,"E2805"),sQuery(id+"F17.wireOp",EDGE,"E2806"),sQuery(id+"F17.wireOp",EDGE,"E2807"),sQuery(id+"F17.wireOp",EDGE,"E2808"),sQuery(id+"F17.wireOp",EDGE,"E2809"),sQuery(id+"F17.wireOp",EDGE,"E2810"),sQuery(id+"F17.wireOp",EDGE,"E2811"),sQuery(id+"F17.wireOp",EDGE,"E2812"),sQuery(id+"F17.wireOp",EDGE,"E2813"),sQuery(id+"F17.wireOp",EDGE,"E2814"),sQuery(id+"F17.wireOp",EDGE,"E2815"),sQuery(id+"F17.wireOp",EDGE,"E2816"),sQuery(id+"F17.wireOp",EDGE,"E2817"),sQuery(id+"F17.wireOp",EDGE,"E2818"),sQuery(id+"F17.wireOp",EDGE,"E2819"),sQuery(id+"F17.wireOp",EDGE,"E2820"),sQuery(id+"F17.wireOp",EDGE,"E2821"),sQuery(id+"F17.wireOp",EDGE,"E2822"),sQuery(id+"F17.wireOp",EDGE,"E2823"),sQuery(id+"F17.wireOp",EDGE,"E2824"),sQuery(id+"F17.wireOp",EDGE,"E2825"),sQuery(id+"F17.wireOp",EDGE,"E2826"),sQuery(id+"F17.wireOp",EDGE,"E2827"),sQuery(id+"F17.wireOp",EDGE,"E2828"),sQuery(id+"F17.wireOp",EDGE,"E2829"),sQuery(id+"F17.wireOp",EDGE,"E2830"),sQuery(id+"F17.wireOp",EDGE,"E2831"),sQuery(id+"F17.wireOp",EDGE,"E2832"),sQuery(id+"F17.wireOp",EDGE,"E2833"),sQuery(id+"F17.wireOp",EDGE,"E2834"),sQuery(id+"F17.wireOp",EDGE,"E2835"),sQuery(id+"F17.wireOp",EDGE,"E2836"),sQuery(id+"F17.wireOp",EDGE,"E2837"),sQuery(id+"F17.wireOp",EDGE,"E2838"),sQuery(id+"F17.wireOp",EDGE,"E2839"),sQuery(id+"F17.wireOp",EDGE,"E2840"),sQuery(id+"F17.wireOp",EDGE,"E2841"),sQuery(id+"F17.wireOp",EDGE,"E2842"),sQuery(id+"F17.wireOp",EDGE,"E2843"),sQuery(id+"F17.wireOp",EDGE,"E2844"),sQuery(id+"F17.wireOp",EDGE,"E2845"),sQuery(id+"F17.wireOp",EDGE,"E2846"),sQuery(id+"F17.wireOp",EDGE,"E2847"),sQuery(id+"F17.wireOp",EDGE,"E2848"),sQuery(id+"F17.wireOp",EDGE,"E2849"),sQuery(id+"F17.wireOp",EDGE,"E2850"),sQuery(id+"F17.wireOp",EDGE,"E2851"),sQuery(id+"F17.wireOp",EDGE,"E2852"),sQuery(id+"F17.wireOp",EDGE,"E2853"),sQuery(id+"F17.wireOp",EDGE,"E2854"),sQuery(id+"F17.wireOp",EDGE,"E2855"),sQuery(id+"F17.wireOp",EDGE,"E2856"),sQuery(id+"F17.wireOp",EDGE,"E2857"),sQuery(id+"F17.wireOp",EDGE,"E2858"),sQuery(id+"F17.wireOp",EDGE,"E2859"),sQuery(id+"F17.wireOp",EDGE,"E2860"),sQuery(id+"F17.wireOp",EDGE,"E2861"),sQuery(id+"F17.wireOp",EDGE,"E2862"),sQuery(id+"F17.wireOp",EDGE,"E2863"),sQuery(id+"F17.wireOp",EDGE,"E2864"),sQuery(id+"F17.wireOp",EDGE,"E2865"),sQuery(id+"F17.wireOp",EDGE,"E2866"),sQuery(id+"F17.wireOp",EDGE,"E2867"),sQuery(id+"F17.wireOp",EDGE,"E2868"),sQuery(id+"F17.wireOp",EDGE,"E2869"),sQuery(id+"F17.wireOp",EDGE,"E2870"),sQuery(id+"F17.wireOp",EDGE,"E2871"),sQuery(id+"F17.wireOp",EDGE,"E2872"),sQuery(id+"F17.wireOp",EDGE,"E2873"),sQuery(id+"F17.wireOp",EDGE,"E2874"),sQuery(id+"F17.wireOp",EDGE,"E2875"),sQuery(id+"F17.wireOp",EDGE,"E2876"),sQuery(id+"F17.wireOp",EDGE,"E2877"),sQuery(id+"F17.wireOp",EDGE,"E2878"),sQuery(id+"F17.wireOp",EDGE,"E2879"),sQuery(id+"F17.wireOp",EDGE,"E2880"),sQuery(id+"F17.wireOp",EDGE,"E2881"),sQuery(id+"F17.wireOp",EDGE,"E2882"),sQuery(id+"F17.wireOp",EDGE,"E2883"),sQuery(id+"F17.wireOp",EDGE,"E2884"),sQuery(id+"F17.wireOp",EDGE,"E2885"),sQuery(id+"F17.wireOp",EDGE,"E2886"),sQuery(id+"F17.wireOp",EDGE,"E2887"),sQuery(id+"F17.wireOp",EDGE,"E2888"),sQuery(id+"F17.wireOp",EDGE,"E2889"),sQuery(id+"F17.wireOp",EDGE,"E2890"),sQuery(id+"F17.wireOp",EDGE,"E2891"),sQuery(id+"F17.wireOp",EDGE,"E2892"),sQuery(id+"F17.wireOp",EDGE,"E2893"),sQuery(id+"F17.wireOp",EDGE,"E2894"),sQuery(id+"F17.wireOp",EDGE,"E2895"),sQuery(id+"F17.wireOp",EDGE,"E2896"),sQuery(id+"F17.wireOp",EDGE,"E2897"),sQuery(id+"F17.wireOp",EDGE,"E2898"),sQuery(id+"F17.wireOp",EDGE,"E2899"),sQuery(id+"F17.wireOp",EDGE,"E2900"),sQuery(id+"F17.wireOp",EDGE,"E2901"),sQuery(id+"F17.wireOp",EDGE,"E2902"),sQuery(id+"F17.wireOp",EDGE,"E2903"),sQuery(id+"F17.wireOp",EDGE,"E2904"),sQuery(id+"F17.wireOp",EDGE,"E2905"),sQuery(id+"F17.wireOp",EDGE,"E2906"),sQuery(id+"F17.wireOp",EDGE,"E2907"),sQuery(id+"F17.wireOp",EDGE,"E2908"),sQuery(id+"F17.wireOp",EDGE,"E2909"),sQuery(id+"F17.wireOp",EDGE,"E2910"),sQuery(id+"F17.wireOp",EDGE,"E2911"),sQuery(id+"F17.wireOp",EDGE,"E2912"),sQuery(id+"F17.wireOp",EDGE,"E2913"),sQuery(id+"F17.wireOp",EDGE,"E2914"),sQuery(id+"F17.wireOp",EDGE,"E2915"),sQuery(id+"F17.wireOp",EDGE,"E2916"),sQuery(id+"F17.wireOp",EDGE,"E2917"),sQuery(id+"F17.wireOp",EDGE,"E2918"),sQuery(id+"F17.wireOp",EDGE,"E2919"),sQuery(id+"F17.wireOp",EDGE,"E2920"),sQuery(id+"F17.wireOp",EDGE,"E2921"),sQuery(id+"F17.wireOp",EDGE,"E2922"),sQuery(id+"F17.wireOp",EDGE,"E2923"),sQuery(id+"F17.wireOp",EDGE,"E2924"),sQuery(id+"F17.wireOp",EDGE,"E2925"),sQuery(id+"F17.wireOp",EDGE,"E2926"),sQuery(id+"F17.wireOp",EDGE,"E2927"),sQuery(id+"F17.wireOp",EDGE,"E2928"),sQuery(id+"F17.wireOp",EDGE,"E2929"),sQuery(id+"F17.wireOp",EDGE,"E2930"),sQuery(id+"F17.wireOp",EDGE,"E2931"),sQuery(id+"F17.wireOp",EDGE,"E2932"),sQuery(id+"F17.wireOp",EDGE,"E2933"),sQuery(id+"F17.wireOp",EDGE,"E2934"),sQuery(id+"F17.wireOp",EDGE,"E2935"),sQuery(id+"F17.wireOp",EDGE,"E2936"),sQuery(id+"F17.wireOp",EDGE,"E2937"),sQuery(id+"F17.wireOp",EDGE,"E2938"),sQuery(id+"F17.wireOp",EDGE,"E2939"),sQuery(id+"F17.wireOp",EDGE,"E2940"),sQuery(id+"F17.wireOp",EDGE,"E2941"),sQuery(id+"F17.wireOp",EDGE,"E2942"),sQuery(id+"F17.wireOp",EDGE,"E2943"),sQuery(id+"F17.wireOp",EDGE,"E2944"),sQuery(id+"F17.wireOp",EDGE,"E2945"),sQuery(id+"F17.wireOp",EDGE,"E2946"),sQuery(id+"F17.wireOp",EDGE,"E2947"),sQuery(id+"F17.wireOp",EDGE,"E2948"),sQuery(id+"F17.wireOp",EDGE,"E2949"),sQuery(id+"F17.wireOp",EDGE,"E2950"),sQuery(id+"F17.wireOp",EDGE,"E2951"),sQuery(id+"F17.wireOp",EDGE,"E2952"),sQuery(id+"F17.wireOp",EDGE,"E2953"),sQuery(id+"F17.wireOp",EDGE,"E2954"),sQuery(id+"F17.wireOp",EDGE,"E2955"),sQuery(id+"F17.wireOp",EDGE,"E2956"),sQuery(id+"F17.wireOp",EDGE,"E2957"),sQuery(id+"F17.wireOp",EDGE,"E2958"),sQuery(id+"F17.wireOp",EDGE,"E2959"),sQuery(id+"F17.wireOp",EDGE,"E2960"),sQuery(id+"F17.wireOp",EDGE,"E2961"),sQuery(id+"F17.wireOp",EDGE,"E2962"),sQuery(id+"F17.wireOp",EDGE,"E2963"),sQuery(id+"F17.wireOp",EDGE,"E2964"),sQuery(id+"F17.wireOp",EDGE,"E2965"),sQuery(id+"F17.wireOp",EDGE,"E2966"),sQuery(id+"F17.wireOp",EDGE,"E2967"),sQuery(id+"F17.wireOp",EDGE,"E2968"),sQuery(id+"F17.wireOp",EDGE,"E2969"),sQuery(id+"F17.wireOp",EDGE,"E2970"),sQuery(id+"F17.wireOp",EDGE,"E2971"),sQuery(id+"F17.wireOp",EDGE,"E2972"),sQuery(id+"F17.wireOp",EDGE,"E2973"),sQuery(id+"F17.wireOp",EDGE,"E2974"),sQuery(id+"F17.wireOp",EDGE,"E2975"),sQuery(id+"F17.wireOp",EDGE,"E2976"),sQuery(id+"F17.wireOp",EDGE,"E2977"),sQuery(id+"F17.wireOp",EDGE,"E2978"),sQuery(id+"F17.wireOp",EDGE,"E2979"),sQuery(id+"F17.wireOp",EDGE,"E2980"),sQuery(id+"F17.wireOp",EDGE,"E2981"),sQuery(id+"F17.wireOp",EDGE,"E2982"),sQuery(id+"F17.wireOp",EDGE,"E2983"),sQuery(id+"F17.wireOp",EDGE,"E2984"),sQuery(id+"F17.wireOp",EDGE,"E2985"),sQuery(id+"F17.wireOp",EDGE,"E2986"),sQuery(id+"F17.wireOp",EDGE,"E2987"),sQuery(id+"F17.wireOp",EDGE,"E2988"),sQuery(id+"F17.wireOp",EDGE,"E2989"),sQuery(id+"F17.wireOp",EDGE,"E2990"),sQuery(id+"F17.wireOp",EDGE,"E2991"),sQuery(id+"F17.wireOp",EDGE,"E2992"),sQuery(id+"F17.wireOp",EDGE,"E2993"),sQuery(id+"F17.wireOp",EDGE,"E2994"),sQuery(id+"F17.wireOp",EDGE,"E2995"),sQuery(id+"F17.wireOp",EDGE,"E2996"),sQuery(id+"F17.wireOp",EDGE,"E2997"),sQuery(id+"F17.wireOp",EDGE,"E2998"),sQuery(id+"F17.wireOp",EDGE,"E2999"),sQuery(id+"F17.wireOp",EDGE,"E3000"),sQuery(id+"F17.wireOp",EDGE,"E3001"),sQuery(id+"F17.wireOp",EDGE,"E3002"),sQuery(id+"F17.wireOp",EDGE,"E3003"),sQuery(id+"F17.wireOp",EDGE,"E3004"),sQuery(id+"F17.wireOp",EDGE,"E3005"),sQuery(id+"F17.wireOp",EDGE,"E3006"),sQuery(id+"F17.wireOp",EDGE,"E3007"),sQuery(id+"F17.wireOp",EDGE,"E3008"),sQuery(id+"F17.wireOp",EDGE,"E3009"),sQuery(id+"F17.wireOp",EDGE,"E3010"),sQuery(id+"F17.wireOp",EDGE,"E3011"),sQuery(id+"F17.wireOp",EDGE,"E3012"),sQuery(id+"F17.wireOp",EDGE,"E3013"),sQuery(id+"F17.wireOp",EDGE,"E3014"),sQuery(id+"F17.wireOp",EDGE,"E3015"),sQuery(id+"F17.wireOp",EDGE,"E3016"),sQuery(id+"F17.wireOp",EDGE,"E3017"),sQuery(id+"F17.wireOp",EDGE,"E3018"),sQuery(id+"F17.wireOp",EDGE,"E3019"),sQuery(id+"F17.wireOp",EDGE,"E3020"),sQuery(id+"F17.wireOp",EDGE,"E3021"),sQuery(id+"F17.wireOp",EDGE,"E3022"),sQuery(id+"F17.wireOp",EDGE,"E3023"),sQuery(id+"F17.wireOp",EDGE,"E3024"),sQuery(id+"F17.wireOp",EDGE,"E3025"),sQuery(id+"F17.wireOp",EDGE,"E3026"),sQuery(id+"F17.wireOp",EDGE,"E3027"),sQuery(id+"F17.wireOp",EDGE,"E3028"),sQuery(id+"F17.wireOp",EDGE,"E3029"),sQuery(id+"F17.wireOp",EDGE,"E3030"),sQuery(id+"F17.wireOp",EDGE,"E3031"),sQuery(id+"F17.wireOp",EDGE,"E3032"),sQuery(id+"F17.wireOp",EDGE,"E3033"),sQuery(id+"F17.wireOp",EDGE,"E3034"),sQuery(id+"F17.wireOp",EDGE,"E3035"),sQuery(id+"F17.wireOp",EDGE,"E3036"),sQuery(id+"F17.wireOp",EDGE,"E3037"),sQuery(id+"F17.wireOp",EDGE,"E3038"),sQuery(id+"F17.wireOp",EDGE,"E3039"),sQuery(id+"F17.wireOp",EDGE,"E3040"),sQuery(id+"F17.wireOp",EDGE,"E3041"),sQuery(id+"F17.wireOp",EDGE,"E3042"),sQuery(id+"F17.wireOp",EDGE,"E3043"),sQuery(id+"F17.wireOp",EDGE,"E3044"),sQuery(id+"F17.wireOp",EDGE,"E3045"),sQuery(id+"F17.wireOp",EDGE,"E3046"),sQuery(id+"F17.wireOp",EDGE,"E3047"),sQuery(id+"F17.wireOp",EDGE,"E3048"),sQuery(id+"F17.wireOp",EDGE,"E3049"),sQuery(id+"F17.wireOp",EDGE,"E3050"),sQuery(id+"F17.wireOp",EDGE,"E3051"),sQuery(id+"F17.wireOp",EDGE,"E3052"),sQuery(id+"F17.wireOp",EDGE,"E3053"),sQuery(id+"F17.wireOp",EDGE,"E3054"),sQuery(id+"F17.wireOp",EDGE,"E3055"),sQuery(id+"F17.wireOp",EDGE,"E3056"),sQuery(id+"F17.wireOp",EDGE,"E3057"),sQuery(id+"F17.wireOp",EDGE,"E3058"),sQuery(id+"F17.wireOp",EDGE,"E3059"),sQuery(id+"F17.wireOp",EDGE,"E3060"),sQuery(id+"F17.wireOp",EDGE,"E3061"),sQuery(id+"F17.wireOp",EDGE,"E3062"),sQuery(id+"F17.wireOp",EDGE,"E3063"),sQuery(id+"F17.wireOp",EDGE,"E3064"),sQuery(id+"F17.wireOp",EDGE,"E3065"),sQuery(id+"F17.wireOp",EDGE,"E3066"),sQuery(id+"F17.wireOp",EDGE,"E3067"),sQuery(id+"F17.wireOp",EDGE,"E3068"),sQuery(id+"F17.wireOp",EDGE,"E3069"),sQuery(id+"F17.wireOp",EDGE,"E3070"),sQuery(id+"F17.wireOp",EDGE,"E3071"),sQuery(id+"F17.wireOp",EDGE,"E3072"),sQuery(id+"F17.wireOp",EDGE,"E3073"),sQuery(id+"F17.wireOp",EDGE,"E3074"),sQuery(id+"F17.wireOp",EDGE,"E3075"),sQuery(id+"F17.wireOp",EDGE,"E3076"),sQuery(id+"F17.wireOp",EDGE,"E3077"),sQuery(id+"F17.wireOp",EDGE,"E3078"),sQuery(id+"F17.wireOp",EDGE,"E3079"),sQuery(id+"F17.wireOp",EDGE,"E3080"),sQuery(id+"F17.wireOp",EDGE,"E3081"),sQuery(id+"F17.wireOp",EDGE,"E3082"),sQuery(id+"F17.wireOp",EDGE,"E3083"),sQuery(id+"F17.wireOp",EDGE,"E3084"),sQuery(id+"F17.wireOp",EDGE,"E3085"),sQuery(id+"F17.wireOp",EDGE,"E3086"),sQuery(id+"F17.wireOp",EDGE,"E3087"),sQuery(id+"F17.wireOp",EDGE,"E3088"),sQuery(id+"F17.wireOp",EDGE,"E3089"),sQuery(id+"F17.wireOp",EDGE,"E3090"),sQuery(id+"F17.wireOp",EDGE,"E3091"),sQuery(id+"F17.wireOp",EDGE,"E3092"),sQuery(id+"F17.wireOp",EDGE,"E3093"),sQuery(id+"F17.wireOp",EDGE,"E3094"),sQuery(id+"F17.wireOp",EDGE,"E3095"),sQuery(id+"F17.wireOp",EDGE,"E3096"),sQuery(id+"F17.wireOp",EDGE,"E3097"),sQuery(id+"F17.wireOp",EDGE,"E3098"),sQuery(id+"F17.wireOp",EDGE,"E3099"),sQuery(id+"F17.wireOp",EDGE,"E3100"),sQuery(id+"F17.wireOp",EDGE,"E3101"),sQuery(id+"F17.wireOp",EDGE,"E3102"),sQuery(id+"F17.wireOp",EDGE,"E3103"),sQuery(id+"F17.wireOp",EDGE,"E3104"),sQuery(id+"F17.wireOp",EDGE,"E3105"),sQuery(id+"F17.wireOp",EDGE,"E3106"),sQuery(id+"F17.wireOp",EDGE,"E3107"),sQuery(id+"F17.wireOp",EDGE,"E3108"),sQuery(id+"F17.wireOp",EDGE,"E3109"),sQuery(id+"F17.wireOp",EDGE,"E3110"),sQuery(id+"F17.wireOp",EDGE,"E3111"),sQuery(id+"F17.wireOp",EDGE,"E3112"),sQuery(id+"F17.wireOp",EDGE,"E3113"),sQuery(id+"F17.wireOp",EDGE,"E3114"),sQuery(id+"F17.wireOp",EDGE,"E3115"),sQuery(id+"F17.wireOp",EDGE,"E3116"),sQuery(id+"F17.wireOp",EDGE,"E3117"),sQuery(id+"F17.wireOp",EDGE,"E3118"),sQuery(id+"F17.wireOp",EDGE,"E3119"),sQuery(id+"F17.wireOp",EDGE,"E3120"),sQuery(id+"F17.wireOp",EDGE,"E3121"),sQuery(id+"F17.wireOp",EDGE,"E3122"),sQuery(id+"F17.wireOp",EDGE,"E3123"),sQuery(id+"F17.wireOp",EDGE,"E3124"),sQuery(id+"F17.wireOp",EDGE,"E3125"),sQuery(id+"F17.wireOp",EDGE,"E3126"),sQuery(id+"F17.wireOp",EDGE,"E3127"),sQuery(id+"F17.wireOp",EDGE,"E3128"),sQuery(id+"F17.wireOp",EDGE,"E3129"),sQuery(id+"F17.wireOp",EDGE,"E3130"),sQuery(id+"F17.wireOp",EDGE,"E3131"),sQuery(id+"F17.wireOp",EDGE,"E3132"),sQuery(id+"F17.wireOp",EDGE,"E3133"),sQuery(id+"F17.wireOp",EDGE,"E3134"),sQuery(id+"F17.wireOp",EDGE,"E3135"),sQuery(id+"F17.wireOp",EDGE,"E3136"),sQuery(id+"F17.wireOp",EDGE,"E3137"),sQuery(id+"F17.wireOp",EDGE,"E3138"),sQuery(id+"F17.wireOp",EDGE,"E3139"),sQuery(id+"F17.wireOp",EDGE,"E3140"),sQuery(id+"F17.wireOp",EDGE,"E3141"),sQuery(id+"F17.wireOp",EDGE,"E3142"),sQuery(id+"F17.wireOp",EDGE,"E3143"),sQuery(id+"F17.wireOp",EDGE,"E3144"),sQuery(id+"F17.wireOp",EDGE,"E3145"),sQuery(id+"F17.wireOp",EDGE,"E3146"),sQuery(id+"F17.wireOp",EDGE,"E3147"),sQuery(id+"F17.wireOp",EDGE,"E3148"),sQuery(id+"F17.wireOp",EDGE,"E3149"),sQuery(id+"F17.wireOp",EDGE,"E3150"),sQuery(id+"F17.wireOp",EDGE,"E3151"),sQuery(id+"F17.wireOp",EDGE,"E3152"),sQuery(id+"F17.wireOp",EDGE,"E3153"),sQuery(id+"F17.wireOp",EDGE,"E3154"),sQuery(id+"F17.wireOp",EDGE,"E3155"),sQuery(id+"F17.wireOp",EDGE,"E3156"),sQuery(id+"F17.wireOp",EDGE,"E3157"),sQuery(id+"F17.wireOp",EDGE,"E3158"),sQuery(id+"F17.wireOp",EDGE,"E3159"),sQuery(id+"F17.wireOp",EDGE,"E3160"),sQuery(id+"F17.wireOp",EDGE,"E3161"),sQuery(id+"F17.wireOp",EDGE,"E3162"),sQuery(id+"F17.wireOp",EDGE,"E3163"),sQuery(id+"F17.wireOp",EDGE,"E3164"),sQuery(id+"F17.wireOp",EDGE,"E3165"),sQuery(id+"F17.wireOp",EDGE,"E3166"),sQuery(id+"F17.wireOp",EDGE,"E3167"),sQuery(id+"F17.wireOp",EDGE,"E3168"),sQuery(id+"F17.wireOp",EDGE,"E3169"),sQuery(id+"F17.wireOp",EDGE,"E3170"),sQuery(id+"F17.wireOp",EDGE,"E3171"),sQuery(id+"F17.wireOp",EDGE,"E3172"),sQuery(id+"F17.wireOp",EDGE,"E3173"),sQuery(id+"F17.wireOp",EDGE,"E3174"),sQuery(id+"F17.wireOp",EDGE,"E3175"),sQuery(id+"F17.wireOp",EDGE,"E3176"),sQuery(id+"F17.wireOp",EDGE,"E3177"),sQuery(id+"F17.wireOp",EDGE,"E3178"),sQuery(id+"F17.wireOp",EDGE,"E3179"),sQuery(id+"F17.wireOp",EDGE,"E3180"),sQuery(id+"F17.wireOp",EDGE,"E3181"),sQuery(id+"F17.wireOp",EDGE,"E3182"),sQuery(id+"F17.wireOp",EDGE,"E3183"),sQuery(id+"F17.wireOp",EDGE,"E3184"),sQuery(id+"F17.wireOp",EDGE,"E3185"),sQuery(id+"F17.wireOp",EDGE,"E3186"),sQuery(id+"F17.wireOp",EDGE,"E3187"),sQuery(id+"F17.wireOp",EDGE,"E3188"),sQuery(id+"F17.wireOp",EDGE,"E3189"),sQuery(id+"F17.wireOp",EDGE,"E3190"),sQuery(id+"F17.wireOp",EDGE,"E3191"),sQuery(id+"F17.wireOp",EDGE,"E3192"),sQuery(id+"F17.wireOp",EDGE,"E3193"),sQuery(id+"F17.wireOp",EDGE,"E3194"),sQuery(id+"F17.wireOp",EDGE,"E3195"),sQuery(id+"F17.wireOp",EDGE,"E3196"),sQuery(id+"F17.wireOp",EDGE,"E3197"),sQuery(id+"F17.wireOp",EDGE,"E3198"),sQuery(id+"F17.wireOp",EDGE,"E3199"),sQuery(id+"F17.wireOp",EDGE,"E3200"),sQuery(id+"F17.wireOp",EDGE,"E3201"),sQuery(id+"F17.wireOp",EDGE,"E3202"),sQuery(id+"F17.wireOp",EDGE,"E3203"),sQuery(id+"F17.wireOp",EDGE,"E3204"),sQuery(id+"F17.wireOp",EDGE,"E3205"),sQuery(id+"F17.wireOp",EDGE,"E3206"),sQuery(id+"F17.wireOp",EDGE,"E3207"),sQuery(id+"F17.wireOp",EDGE,"E3208"),sQuery(id+"F17.wireOp",EDGE,"E3209"),sQuery(id+"F17.wireOp",EDGE,"E3210"),sQuery(id+"F17.wireOp",EDGE,"E3211"),sQuery(id+"F17.wireOp",EDGE,"E3212"),sQuery(id+"F17.wireOp",EDGE,"E3213"),sQuery(id+"F17.wireOp",EDGE,"E3214"),sQuery(id+"F17.wireOp",EDGE,"E3215"),sQuery(id+"F17.wireOp",EDGE,"E3216"),sQuery(id+"F17.wireOp",EDGE,"E3217"),sQuery(id+"F17.wireOp",EDGE,"E3218"),sQuery(id+"F17.wireOp",EDGE,"E3219"),sQuery(id+"F17.wireOp",EDGE,"E3220"),sQuery(id+"F17.wireOp",EDGE,"E3221"),sQuery(id+"F17.wireOp",EDGE,"E3222"),sQuery(id+"F17.wireOp",EDGE,"E3223"),sQuery(id+"F17.wireOp",EDGE,"E3224"),sQuery(id+"F17.wireOp",EDGE,"E3225"),sQuery(id+"F17.wireOp",EDGE,"E3226"),sQuery(id+"F17.wireOp",EDGE,"E3227"),sQuery(id+"F17.wireOp",EDGE,"E3228"),sQuery(id+"F17.wireOp",EDGE,"E3229"),sQuery(id+"F17.wireOp",EDGE,"E3230"),sQuery(id+"F17.wireOp",EDGE,"E3231"),sQuery(id+"F17.wireOp",EDGE,"E3232"),sQuery(id+"F17.wireOp",EDGE,"E3233"),sQuery(id+"F17.wireOp",EDGE,"E3234"),sQuery(id+"F17.wireOp",EDGE,"E3235"),sQuery(id+"F17.wireOp",EDGE,"E3236"),sQuery(id+"F17.wireOp",EDGE,"E3237"),sQuery(id+"F17.wireOp",EDGE,"E3238"),sQuery(id+"F17.wireOp",EDGE,"E3239"),sQuery(id+"F17.wireOp",EDGE,"E3240"),sQuery(id+"F17.wireOp",EDGE,"E3241"),sQuery(id+"F17.wireOp",EDGE,"E3242"),sQuery(id+"F17.wireOp",EDGE,"E3243"),sQuery(id+"F17.wireOp",EDGE,"E3244"),sQuery(id+"F17.wireOp",EDGE,"E3245"),sQuery(id+"F17.wireOp",EDGE,"E3246"),sQuery(id+"F17.wireOp",EDGE,"E3247"),sQuery(id+"F17.wireOp",EDGE,"E3248"),sQuery(id+"F17.wireOp",EDGE,"E3249"),sQuery(id+"F17.wireOp",EDGE,"E3250"),sQuery(id+"F17.wireOp",EDGE,"E3251"),sQuery(id+"F17.wireOp",EDGE,"E3252"),sQuery(id+"F17.wireOp",EDGE,"E3253"),sQuery(id+"F17.wireOp",EDGE,"E3254"),sQuery(id+"F17.wireOp",EDGE,"E3255"),sQuery(id+"F17.wireOp",EDGE,"E3256"),sQuery(id+"F17.wireOp",EDGE,"E3257"),sQuery(id+"F17.wireOp",EDGE,"E3258"),sQuery(id+"F17.wireOp",EDGE,"E3259"),sQuery(id+"F17.wireOp",EDGE,"E3260"),sQuery(id+"F17.wireOp",EDGE,"E3261"),sQuery(id+"F17.wireOp",EDGE,"E3262"),sQuery(id+"F17.wireOp",EDGE,"E3263"),sQuery(id+"F17.wireOp",EDGE,"E3264"),sQuery(id+"F17.wireOp",EDGE,"E3265"),sQuery(id+"F17.wireOp",EDGE,"E3266"),sQuery(id+"F17.wireOp",EDGE,"E3267"),sQuery(id+"F17.wireOp",EDGE,"E3268"),sQuery(id+"F17.wireOp",EDGE,"E3269"),sQuery(id+"F17.wireOp",EDGE,"E3270"),sQuery(id+"F17.wireOp",EDGE,"E3271"),sQuery(id+"F17.wireOp",EDGE,"E3272"),sQuery(id+"F17.wireOp",EDGE,"E3273"),sQuery(id+"F17.wireOp",EDGE,"E3274"),sQuery(id+"F17.wireOp",EDGE,"E3275"),sQuery(id+"F17.wireOp",EDGE,"E3276"),sQuery(id+"F17.wireOp",EDGE,"E3277"),sQuery(id+"F17.wireOp",EDGE,"E3278"),sQuery(id+"F17.wireOp",EDGE,"E3279"),sQuery(id+"F17.wireOp",EDGE,"E3280"),sQuery(id+"F17.wireOp",EDGE,"E3281"),sQuery(id+"F17.wireOp",EDGE,"E3282"),sQuery(id+"F17.wireOp",EDGE,"E3283"),sQuery(id+"F17.wireOp",EDGE,"E3284"),sQuery(id+"F17.wireOp",EDGE,"E3285"),sQuery(id+"F17.wireOp",EDGE,"E3286"),sQuery(id+"F17.wireOp",EDGE,"E3287"),sQuery(id+"F17.wireOp",EDGE,"E3288"),sQuery(id+"F17.wireOp",EDGE,"E3289"),sQuery(id+"F17.wireOp",EDGE,"E3290"),sQuery(id+"F17.wireOp",EDGE,"E3291"),sQuery(id+"F17.wireOp",EDGE,"E3292"),sQuery(id+"F17.wireOp",EDGE,"E3293"),sQuery(id+"F17.wireOp",EDGE,"E3294"),sQuery(id+"F17.wireOp",EDGE,"E3295"),sQuery(id+"F17.wireOp",EDGE,"E3296"),sQuery(id+"F17.wireOp",EDGE,"E3297"),sQuery(id+"F17.wireOp",EDGE,"E3298"),sQuery(id+"F17.wireOp",EDGE,"E3299"),sQuery(id+"F17.wireOp",EDGE,"E3300"),sQuery(id+"F17.wireOp",EDGE,"E3301"),sQuery(id+"F17.wireOp",EDGE,"E3302"),sQuery(id+"F17.wireOp",EDGE,"E3303"),sQuery(id+"F17.wireOp",EDGE,"E3304"),sQuery(id+"F17.wireOp",EDGE,"E3305"),sQuery(id+"F17.wireOp",EDGE,"E3306"),sQuery(id+"F17.wireOp",EDGE,"E3307"),sQuery(id+"F17.wireOp",EDGE,"E3308"),sQuery(id+"F17.wireOp",EDGE,"E3309"),sQuery(id+"F17.wireOp",EDGE,"E3310"),sQuery(id+"F17.wireOp",EDGE,"E3311"),sQuery(id+"F17.wireOp",EDGE,"E3312"),sQuery(id+"F17.wireOp",EDGE,"E3313"),sQuery(id+"F17.wireOp",EDGE,"E3314"),sQuery(id+"F17.wireOp",EDGE,"E3315"),sQuery(id+"F17.wireOp",EDGE,"E3316"),sQuery(id+"F17.wireOp",EDGE,"E3317"),sQuery(id+"F17.wireOp",EDGE,"E3318"),sQuery(id+"F17.wireOp",EDGE,"E3319"),sQuery(id+"F17.wireOp",EDGE,"E3320"),sQuery(id+"F17.wireOp",EDGE,"E3321"),sQuery(id+"F17.wireOp",EDGE,"E3322"),sQuery(id+"F17.wireOp",EDGE,"E3323"),sQuery(id+"F17.wireOp",EDGE,"E3324"),sQuery(id+"F17.wireOp",EDGE,"E3325"),sQuery(id+"F17.wireOp",EDGE,"E3326"),sQuery(id+"F17.wireOp",EDGE,"E3327"),sQuery(id+"F17.wireOp",EDGE,"E3328"),sQuery(id+"F17.wireOp",EDGE,"E3329"),sQuery(id+"F17.wireOp",EDGE,"E3330"),sQuery(id+"F17.wireOp",EDGE,"E3331"),sQuery(id+"F17.wireOp",EDGE,"E3332"),sQuery(id+"F17.wireOp",EDGE,"E3333"),sQuery(id+"F17.wireOp",EDGE,"E3334"),sQuery(id+"F17.wireOp",EDGE,"E3335"),sQuery(id+"F17.wireOp",EDGE,"E3336"),sQuery(id+"F17.wireOp",EDGE,"E3337"),sQuery(id+"F17.wireOp",EDGE,"E3338"),sQuery(id+"F17.wireOp",EDGE,"E3339"),sQuery(id+"F17.wireOp",EDGE,"E3340"),sQuery(id+"F17.wireOp",EDGE,"E3341"),sQuery(id+"F17.wireOp",EDGE,"E3342"),sQuery(id+"F17.wireOp",EDGE,"E3343"),sQuery(id+"F17.wireOp",EDGE,"E3344"),sQuery(id+"F17.wireOp",EDGE,"E3345"),sQuery(id+"F17.wireOp",EDGE,"E3346"),sQuery(id+"F17.wireOp",EDGE,"E3347"),sQuery(id+"F17.wireOp",EDGE,"E3348"),sQuery(id+"F17.wireOp",EDGE,"E3349"),sQuery(id+"F17.wireOp",EDGE,"E3350"),sQuery(id+"F17.wireOp",EDGE,"E3351"),sQuery(id+"F17.wireOp",EDGE,"E3352"),sQuery(id+"F17.wireOp",EDGE,"E3353"),sQuery(id+"F17.wireOp",EDGE,"E3354"),sQuery(id+"F17.wireOp",EDGE,"E3355"),sQuery(id+"F17.wireOp",EDGE,"E3356"),sQuery(id+"F17.wireOp",EDGE,"E3357"),sQuery(id+"F17.wireOp",EDGE,"E3358"),sQuery(id+"F17.wireOp",EDGE,"E3359"),sQuery(id+"F17.wireOp",EDGE,"E3360"),sQuery(id+"F17.wireOp",EDGE,"E3361"),sQuery(id+"F17.wireOp",EDGE,"E3362"),sQuery(id+"F17.wireOp",EDGE,"E3363"),sQuery(id+"F17.wireOp",EDGE,"E3364"),sQuery(id+"F17.wireOp",EDGE,"E3365"),sQuery(id+"F17.wireOp",EDGE,"E3366"),sQuery(id+"F17.wireOp",EDGE,"E3367"),sQuery(id+"F17.wireOp",EDGE,"E3368"),sQuery(id+"F17.wireOp",EDGE,"E3369"),sQuery(id+"F17.wireOp",EDGE,"E3370"),sQuery(id+"F17.wireOp",EDGE,"E3371"),sQuery(id+"F17.wireOp",EDGE,"E3372"),sQuery(id+"F17.wireOp",EDGE,"E3373"),sQuery(id+"F17.wireOp",EDGE,"E3374"),sQuery(id+"F17.wireOp",EDGE,"E3375"),sQuery(id+"F17.wireOp",EDGE,"E3376"),sQuery(id+"F17.wireOp",EDGE,"E3377"),sQuery(id+"F17.wireOp",EDGE,"E3378"),sQuery(id+"F17.wireOp",EDGE,"E3379"),sQuery(id+"F17.wireOp",EDGE,"E3380"),sQuery(id+"F17.wireOp",EDGE,"E3381"),sQuery(id+"F17.wireOp",EDGE,"E3382"),sQuery(id+"F17.wireOp",EDGE,"E3383"),sQuery(id+"F17.wireOp",EDGE,"E3384"),sQuery(id+"F17.wireOp",EDGE,"E3385"),sQuery(id+"F17.wireOp",EDGE,"E3386"),sQuery(id+"F17.wireOp",EDGE,"E3387"),sQuery(id+"F17.wireOp",EDGE,"E3388"),sQuery(id+"F17.wireOp",EDGE,"E3389"),sQuery(id+"F17.wireOp",EDGE,"E3390"),sQuery(id+"F17.wireOp",EDGE,"E3391"),sQuery(id+"F17.wireOp",EDGE,"E3392"),sQuery(id+"F17.wireOp",EDGE,"E3393"),sQuery(id+"F17.wireOp",EDGE,"E3394"),sQuery(id+"F17.wireOp",EDGE,"E3395"),sQuery(id+"F17.wireOp",EDGE,"E3396"),sQuery(id+"F17.wireOp",EDGE,"E3397"),sQuery(id+"F17.wireOp",EDGE,"E3398"),sQuery(id+"F17.wireOp",EDGE,"E3399"),sQuery(id+"F17.wireOp",EDGE,"E3400"),sQuery(id+"F17.wireOp",EDGE,"E3401"),sQuery(id+"F17.wireOp",EDGE,"E3402"),sQuery(id+"F17.wireOp",EDGE,"E3403"),sQuery(id+"F17.wireOp",EDGE,"E3404"),sQuery(id+"F17.wireOp",EDGE,"E3405"),sQuery(id+"F17.wireOp",EDGE,"E3406"),sQuery(id+"F17.wireOp",EDGE,"E3407"),sQuery(id+"F17.wireOp",EDGE,"E3408"),sQuery(id+"F17.wireOp",EDGE,"E3409"),sQuery(id+"F17.wireOp",EDGE,"E3410"),sQuery(id+"F17.wireOp",EDGE,"E3411"),sQuery(id+"F17.wireOp",EDGE,"E3412"),sQuery(id+"F17.wireOp",EDGE,"E3413"),sQuery(id+"F17.wireOp",EDGE,"E3414"),sQuery(id+"F17.wireOp",EDGE,"E3415"),sQuery(id+"F17.wireOp",EDGE,"E3416"),sQuery(id+"F17.wireOp",EDGE,"E3417"),sQuery(id+"F17.wireOp",EDGE,"E3418"),sQuery(id+"F17.wireOp",EDGE,"E3419"),sQuery(id+"F17.wireOp",EDGE,"E3420"),sQuery(id+"F17.wireOp",EDGE,"E3421"),sQuery(id+"F17.wireOp",EDGE,"E3422"),sQuery(id+"F17.wireOp",EDGE,"E3423"),sQuery(id+"F17.wireOp",EDGE,"E3424"),sQuery(id+"F17.wireOp",EDGE,"E3425"),sQuery(id+"F17.wireOp",EDGE,"E3426"),sQuery(id+"F17.wireOp",EDGE,"E3427"),sQuery(id+"F17.wireOp",EDGE,"E3428"),sQuery(id+"F17.wireOp",EDGE,"E3429"),sQuery(id+"F17.wireOp",EDGE,"E3430"),sQuery(id+"F17.wireOp",EDGE,"E3431"),sQuery(id+"F17.wireOp",EDGE,"E3432"),sQuery(id+"F17.wireOp",EDGE,"E3433"),sQuery(id+"F17.wireOp",EDGE,"E3434"),sQuery(id+"F17.wireOp",EDGE,"E3435"),sQuery(id+"F17.wireOp",EDGE,"E3436"),sQuery(id+"F17.wireOp",EDGE,"E3437"),sQuery(id+"F17.wireOp",EDGE,"E3438"),sQuery(id+"F17.wireOp",EDGE,"E3439"),sQuery(id+"F17.wireOp",EDGE,"E3440"),sQuery(id+"F17.wireOp",EDGE,"E3441"),sQuery(id+"F17.wireOp",EDGE,"E3442"),sQuery(id+"F17.wireOp",EDGE,"E3443"),sQuery(id+"F17.wireOp",EDGE,"E3444"),sQuery(id+"F17.wireOp",EDGE,"E3445"),sQuery(id+"F17.wireOp",EDGE,"E3446"),sQuery(id+"F17.wireOp",EDGE,"E3447"),sQuery(id+"F17.wireOp",EDGE,"E3448"),sQuery(id+"F17.wireOp",EDGE,"E3449"),sQuery(id+"F17.wireOp",EDGE,"E3450"),sQuery(id+"F17.wireOp",EDGE,"E3451"),sQuery(id+"F17.wireOp",EDGE,"E3452"),sQuery(id+"F17.wireOp",EDGE,"E3453"),sQuery(id+"F17.wireOp",EDGE,"E3454"),sQuery(id+"F17.wireOp",EDGE,"E3455"),sQuery(id+"F17.wireOp",EDGE,"E3456"),sQuery(id+"F17.wireOp",EDGE,"E3457"),sQuery(id+"F17.wireOp",EDGE,"E3458"),sQuery(id+"F17.wireOp",EDGE,"E3459"),sQuery(id+"F17.wireOp",EDGE,"E3460"),sQuery(id+"F17.wireOp",EDGE,"E3461"),sQuery(id+"F17.wireOp",EDGE,"E3462"),sQuery(id+"F17.wireOp",EDGE,"E3463"),sQuery(id+"F17.wireOp",EDGE,"E3464"),sQuery(id+"F17.wireOp",EDGE,"E3465"),sQuery(id+"F17.wireOp",EDGE,"E3466"),sQuery(id+"F17.wireOp",EDGE,"E3467"),sQuery(id+"F17.wireOp",EDGE,"E3468"),sQuery(id+"F17.wireOp",EDGE,"E3469"),sQuery(id+"F17.wireOp",EDGE,"E3470"),sQuery(id+"F17.wireOp",EDGE,"E3471"),sQuery(id+"F17.wireOp",EDGE,"E3472"),sQuery(id+"F17.wireOp",EDGE,"E3473"),sQuery(id+"F17.wireOp",EDGE,"E3474"),sQuery(id+"F17.wireOp",EDGE,"E3475"),sQuery(id+"F17.wireOp",EDGE,"E3476"),sQuery(id+"F17.wireOp",EDGE,"E3477"),sQuery(id+"F17.wireOp",EDGE,"E3478"),sQuery(id+"F17.wireOp",EDGE,"E3479"),sQuery(id+"F17.wireOp",EDGE,"E3480"),sQuery(id+"F17.wireOp",EDGE,"E3481"),sQuery(id+"F17.wireOp",EDGE,"E3482"),sQuery(id+"F17.wireOp",EDGE,"E3483"),sQuery(id+"F17.wireOp",EDGE,"E3484"),sQuery(id+"F17.wireOp",EDGE,"E3485"),sQuery(id+"F17.wireOp",EDGE,"E3486"),sQuery(id+"F17.wireOp",EDGE,"E3487"),sQuery(id+"F17.wireOp",EDGE,"E3488"),sQuery(id+"F17.wireOp",EDGE,"E3489"),sQuery(id+"F17.wireOp",EDGE,"E3490"),sQuery(id+"F17.wireOp",EDGE,"E3491"),sQuery(id+"F17.wireOp",EDGE,"E3492"),sQuery(id+"F17.wireOp",EDGE,"E3493"),sQuery(id+"F17.wireOp",EDGE,"E3494"),sQuery(id+"F17.wireOp",EDGE,"E3495"),sQuery(id+"F17.wireOp",EDGE,"E3496"),sQuery(id+"F17.wireOp",EDGE,"E3497"),sQuery(id+"F17.wireOp",EDGE,"E3498"),sQuery(id+"F17.wireOp",EDGE,"E3499"),sQuery(id+"F17.wireOp",EDGE,"E3500"),sQuery(id+"F17.wireOp",EDGE,"E3501"),sQuery(id+"F17.wireOp",EDGE,"E3502"),sQuery(id+"F17.wireOp",EDGE,"E3503"),sQuery(id+"F17.wireOp",EDGE,"E3504"),sQuery(id+"F17.wireOp",EDGE,"E3505"),sQuery(id+"F17.wireOp",EDGE,"E3506"),sQuery(id+"F17.wireOp",EDGE,"E3507"),sQuery(id+"F17.wireOp",EDGE,"E3508"),sQuery(id+"F17.wireOp",EDGE,"E3509"),sQuery(id+"F17.wireOp",EDGE,"E3510"),sQuery(id+"F17.wireOp",EDGE,"E3511"),sQuery(id+"F17.wireOp",EDGE,"E3512"),sQuery(id+"F17.wireOp",EDGE,"E3513"),sQuery(id+"F17.wireOp",EDGE,"E3514"),sQuery(id+"F17.wireOp",EDGE,"E3515"),sQuery(id+"F17.wireOp",EDGE,"E3516"),sQuery(id+"F17.wireOp",EDGE,"E3517"),sQuery(id+"F17.wireOp",EDGE,"E3518"),sQuery(id+"F17.wireOp",EDGE,"E3519"),sQuery(id+"F17.wireOp",EDGE,"E3520"),sQuery(id+"F17.wireOp",EDGE,"E3521"),sQuery(id+"F17.wireOp",EDGE,"E3522"),sQuery(id+"F17.wireOp",EDGE,"E3523"),sQuery(id+"F17.wireOp",EDGE,"E3524"),sQuery(id+"F17.wireOp",EDGE,"E3525"),sQuery(id+"F17.wireOp",EDGE,"E3526"),sQuery(id+"F17.wireOp",EDGE,"E3527"),sQuery(id+"F17.wireOp",EDGE,"E3528"),sQuery(id+"F17.wireOp",EDGE,"E3529"),sQuery(id+"F17.wireOp",EDGE,"E3530"),sQuery(id+"F17.wireOp",EDGE,"E3531"),sQuery(id+"F17.wireOp",EDGE,"E3532"),sQuery(id+"F17.wireOp",EDGE,"E3533"),sQuery(id+"F17.wireOp",EDGE,"E3534"),sQuery(id+"F17.wireOp",EDGE,"E3535"),sQuery(id+"F17.wireOp",EDGE,"E3536"),sQuery(id+"F17.wireOp",EDGE,"E3537"),sQuery(id+"F17.wireOp",EDGE,"E3538"),sQuery(id+"F17.wireOp",EDGE,"E3539"),sQuery(id+"F17.wireOp",EDGE,"E3540"),sQuery(id+"F17.wireOp",EDGE,"E3541"),sQuery(id+"F17.wireOp",EDGE,"E3542"),sQuery(id+"F17.wireOp",EDGE,"E3543"),sQuery(id+"F17.wireOp",EDGE,"E3544"),sQuery(id+"F17.wireOp",EDGE,"E3545"),sQuery(id+"F17.wireOp",EDGE,"E3546"),sQuery(id+"F17.wireOp",EDGE,"E3547"),sQuery(id+"F17.wireOp",EDGE,"E3548"),sQuery(id+"F17.wireOp",EDGE,"E3549"),sQuery(id+"F17.wireOp",EDGE,"E3550"),sQuery(id+"F17.wireOp",EDGE,"E3551"),sQuery(id+"F17.wireOp",EDGE,"E3552"),sQuery(id+"F17.wireOp",EDGE,"E3553"),sQuery(id+"F17.wireOp",EDGE,"E3554"),sQuery(id+"F17.wireOp",EDGE,"E3555"),sQuery(id+"F17.wireOp",EDGE,"E3556"),sQuery(id+"F17.wireOp",EDGE,"E3557"),sQuery(id+"F17.wireOp",EDGE,"E3558"),sQuery(id+"F17.wireOp",EDGE,"E3559"),sQuery(id+"F17.wireOp",EDGE,"E3560"),sQuery(id+"F17.wireOp",EDGE,"E3561"),sQuery(id+"F17.wireOp",EDGE,"E3562"),sQuery(id+"F17.wireOp",EDGE,"E3563"),sQuery(id+"F17.wireOp",EDGE,"E3564"),sQuery(id+"F17.wireOp",EDGE,"E3565"),sQuery(id+"F17.wireOp",EDGE,"E3566"),sQuery(id+"F17.wireOp",EDGE,"E3567"),sQuery(id+"F17.wireOp",EDGE,"E3568"),sQuery(id+"F17.wireOp",EDGE,"E3569"),sQuery(id+"F17.wireOp",EDGE,"E3570"),sQuery(id+"F17.wireOp",EDGE,"E3571"),sQuery(id+"F17.wireOp",EDGE,"E3572"),sQuery(id+"F17.wireOp",EDGE,"E3573"),sQuery(id+"F17.wireOp",EDGE,"E3574"),sQuery(id+"F17.wireOp",EDGE,"E3575"),sQuery(id+"F17.wireOp",EDGE,"E3576"),sQuery(id+"F17.wireOp",EDGE,"E3577"),sQuery(id+"F17.wireOp",EDGE,"E3578"),sQuery(id+"F17.wireOp",EDGE,"E3579"),sQuery(id+"F17.wireOp",EDGE,"E3580"),sQuery(id+"F17.wireOp",EDGE,"E3581"),sQuery(id+"F17.wireOp",EDGE,"E3582"),sQuery(id+"F17.wireOp",EDGE,"E3583"),sQuery(id+"F17.wireOp",EDGE,"E3584"),sQuery(id+"F17.wireOp",EDGE,"E3585"),sQuery(id+"F17.wireOp",EDGE,"E3586"),sQuery(id+"F17.wireOp",EDGE,"E3587"),sQuery(id+"F17.wireOp",EDGE,"E3588"),sQuery(id+"F17.wireOp",EDGE,"E3589"),sQuery(id+"F17.wireOp",EDGE,"E3590"),sQuery(id+"F17.wireOp",EDGE,"E3591"),sQuery(id+"F17.wireOp",EDGE,"E3592"),sQuery(id+"F17.wireOp",EDGE,"E3593"),sQuery(id+"F17.wireOp",EDGE,"E3594"),sQuery(id+"F17.wireOp",EDGE,"E3595"),sQuery(id+"F17.wireOp",EDGE,"E3596"),sQuery(id+"F17.wireOp",EDGE,"E3597"),sQuery(id+"F17.wireOp",EDGE,"E3598"),sQuery(id+"F17.wireOp",EDGE,"E3599"),sQuery(id+"F17.wireOp",EDGE,"E3600"),sQuery(id+"F17.wireOp",EDGE,"E3601"),sQuery(id+"F17.wireOp",EDGE,"E3602"),sQuery(id+"F17.wireOp",EDGE,"E3603"),sQuery(id+"F17.wireOp",EDGE,"E3604"),sQuery(id+"F17.wireOp",EDGE,"E3605"),sQuery(id+"F17.wireOp",EDGE,"E3606"),sQuery(id+"F17.wireOp",EDGE,"E3607"),sQuery(id+"F17.wireOp",EDGE,"E3608"),sQuery(id+"F17.wireOp",EDGE,"E3609"),sQuery(id+"F17.wireOp",EDGE,"E3610"),sQuery(id+"F17.wireOp",EDGE,"E3611"),sQuery(id+"F17.wireOp",EDGE,"E3612"),sQuery(id+"F17.wireOp",EDGE,"E3613"),sQuery(id+"F17.wireOp",EDGE,"E3614"),sQuery(id+"F17.wireOp",EDGE,"E3615"),sQuery(id+"F17.wireOp",EDGE,"E3616"),sQuery(id+"F17.wireOp",EDGE,"E3617"),sQuery(id+"F17.wireOp",EDGE,"E3618"),sQuery(id+"F17.wireOp",EDGE,"E3619"),sQuery(id+"F17.wireOp",EDGE,"E3620"),sQuery(id+"F17.wireOp",EDGE,"E3621"),sQuery(id+"F17.wireOp",EDGE,"E3622"),sQuery(id+"F17.wireOp",EDGE,"E3623"),sQuery(id+"F17.wireOp",EDGE,"E3624"),sQuery(id+"F17.wireOp",EDGE,"E3625"),sQuery(id+"F17.wireOp",EDGE,"E3626"),sQuery(id+"F17.wireOp",EDGE,"E3627"),sQuery(id+"F17.wireOp",EDGE,"E3628"),sQuery(id+"F17.wireOp",EDGE,"E3629"),sQuery(id+"F17.wireOp",EDGE,"E3630"),sQuery(id+"F17.wireOp",EDGE,"E3631"),sQuery(id+"F17.wireOp",EDGE,"E3632"),sQuery(id+"F17.wireOp",EDGE,"E3633"),sQuery(id+"F17.wireOp",EDGE,"E3634"),sQuery(id+"F17.wireOp",EDGE,"E3635"),sQuery(id+"F17.wireOp",EDGE,"E3636"),sQuery(id+"F17.wireOp",EDGE,"E3637"),sQuery(id+"F17.wireOp",EDGE,"E3638"),sQuery(id+"F17.wireOp",EDGE,"E3639"),sQuery(id+"F17.wireOp",EDGE,"E3640"),sQuery(id+"F17.wireOp",EDGE,"E3641"),sQuery(id+"F17.wireOp",EDGE,"E3642"),sQuery(id+"F17.wireOp",EDGE,"E3643"),sQuery(id+"F17.wireOp",EDGE,"E3644"),sQuery(id+"F17.wireOp",EDGE,"E3645"),sQuery(id+"F17.wireOp",EDGE,"E3646"),sQuery(id+"F17.wireOp",EDGE,"E3647"),sQuery(id+"F17.wireOp",EDGE,"E3648"),sQuery(id+"F17.wireOp",EDGE,"E3649"),sQuery(id+"F17.wireOp",EDGE,"E3650"),sQuery(id+"F17.wireOp",EDGE,"E3651"),sQuery(id+"F17.wireOp",EDGE,"E3652"),sQuery(id+"F17.wireOp",EDGE,"E3653"),sQuery(id+"F17.wireOp",EDGE,"E3654"),sQuery(id+"F17.wireOp",EDGE,"E3655"),sQuery(id+"F17.wireOp",EDGE,"E3656"),sQuery(id+"F17.wireOp",EDGE,"E3657"),sQuery(id+"F17.wireOp",EDGE,"E3658"),sQuery(id+"F17.wireOp",EDGE,"E3659"),sQuery(id+"F17.wireOp",EDGE,"E3660"),sQuery(id+"F17.wireOp",EDGE,"E3661"),sQuery(id+"F17.wireOp",EDGE,"E3662"),sQuery(id+"F17.wireOp",EDGE,"E3663"),sQuery(id+"F17.wireOp",EDGE,"E3664"),sQuery(id+"F17.wireOp",EDGE,"E3665"),sQuery(id+"F17.wireOp",EDGE,"E3666"),sQuery(id+"F17.wireOp",EDGE,"E3667"),sQuery(id+"F17.wireOp",EDGE,"E3668"),sQuery(id+"F17.wireOp",EDGE,"E3669"),sQuery(id+"F17.wireOp",EDGE,"E3670"),sQuery(id+"F17.wireOp",EDGE,"E3671"),sQuery(id+"F17.wireOp",EDGE,"E3672"),sQuery(id+"F17.wireOp",EDGE,"E3673"),sQuery(id+"F17.wireOp",EDGE,"E3674"),sQuery(id+"F17.wireOp",EDGE,"E3675"),sQuery(id+"F17.wireOp",EDGE,"E3676"),sQuery(id+"F17.wireOp",EDGE,"E3677"),sQuery(id+"F17.wireOp",EDGE,"E3678"),sQuery(id+"F17.wireOp",EDGE,"E3679"),sQuery(id+"F17.wireOp",EDGE,"E3680"),sQuery(id+"F17.wireOp",EDGE,"E3681"),sQuery(id+"F17.wireOp",EDGE,"E3682"),sQuery(id+"F17.wireOp",EDGE,"E3683"),sQuery(id+"F17.wireOp",EDGE,"E3684"),sQuery(id+"F17.wireOp",EDGE,"E3685"),sQuery(id+"F17.wireOp",EDGE,"E3686"),sQuery(id+"F17.wireOp",EDGE,"E3687"),sQuery(id+"F17.wireOp",EDGE,"E3688"),sQuery(id+"F17.wireOp",EDGE,"E3689"),sQuery(id+"F17.wireOp",EDGE,"E3690"),sQuery(id+"F17.wireOp",EDGE,"E3691"),sQuery(id+"F17.wireOp",EDGE,"E3692"),sQuery(id+"F17.wireOp",EDGE,"E3693"),sQuery(id+"F17.wireOp",EDGE,"E3694"),sQuery(id+"F17.wireOp",EDGE,"E3695"),sQuery(id+"F17.wireOp",EDGE,"E3696"),sQuery(id+"F17.wireOp",EDGE,"E3697"),sQuery(id+"F17.wireOp",EDGE,"E3698"),sQuery(id+"F17.wireOp",EDGE,"E3699"),sQuery(id+"F17.wireOp",EDGE,"E3700"),sQuery(id+"F17.wireOp",EDGE,"E3701"),sQuery(id+"F17.wireOp",EDGE,"E3702"),sQuery(id+"F17.wireOp",EDGE,"E3703"),sQuery(id+"F17.wireOp",EDGE,"E3704"),sQuery(id+"F17.wireOp",EDGE,"E3705"),sQuery(id+"F17.wireOp",EDGE,"E3706"),sQuery(id+"F17.wireOp",EDGE,"E3707"),sQuery(id+"F17.wireOp",EDGE,"E3708"),sQuery(id+"F17.wireOp",EDGE,"E3709"),sQuery(id+"F17.wireOp",EDGE,"E3710"),sQuery(id+"F17.wireOp",EDGE,"E3711"),sQuery(id+"F17.wireOp",EDGE,"E3712"),sQuery(id+"F17.wireOp",EDGE,"E3713"),sQuery(id+"F17.wireOp",EDGE,"E3714"),sQuery(id+"F17.wireOp",EDGE,"E3715"),sQuery(id+"F17.wireOp",EDGE,"E3716"),sQuery(id+"F17.wireOp",EDGE,"E3717"),sQuery(id+"F17.wireOp",EDGE,"E3718"),sQuery(id+"F17.wireOp",EDGE,"E3719"),sQuery(id+"F17.wireOp",EDGE,"E3720"),sQuery(id+"F17.wireOp",EDGE,"E3721"),sQuery(id+"F17.wireOp",EDGE,"E3722"),sQuery(id+"F17.wireOp",EDGE,"E3723"),sQuery(id+"F17.wireOp",EDGE,"E3724"),sQuery(id+"F17.wireOp",EDGE,"E3725"),sQuery(id+"F17.wireOp",EDGE,"E3726"),sQuery(id+"F17.wireOp",EDGE,"E3727"),sQuery(id+"F17.wireOp",EDGE,"E3728"),sQuery(id+"F17.wireOp",EDGE,"E3729"),sQuery(id+"F17.wireOp",EDGE,"E3730"),sQuery(id+"F17.wireOp",EDGE,"E3731"),sQuery(id+"F17.wireOp",EDGE,"E3732"),sQuery(id+"F17.wireOp",EDGE,"E3733"),sQuery(id+"F17.wireOp",EDGE,"E3734"),sQuery(id+"F17.wireOp",EDGE,"E3735"),sQuery(id+"F17.wireOp",EDGE,"E3736"),sQuery(id+"F17.wireOp",EDGE,"E3737"),sQuery(id+"F17.wireOp",EDGE,"E3738"),sQuery(id+"F17.wireOp",EDGE,"E3739"),sQuery(id+"F17.wireOp",EDGE,"E3740"),sQuery(id+"F17.wireOp",EDGE,"E3741"),sQuery(id+"F17.wireOp",EDGE,"E3742"),sQuery(id+"F17.wireOp",EDGE,"E3743"),sQuery(id+"F17.wireOp",EDGE,"E3744"),sQuery(id+"F17.wireOp",EDGE,"E3745"),sQuery(id+"F17.wireOp",EDGE,"E3746"),sQuery(id+"F17.wireOp",EDGE,"E3747"),sQuery(id+"F17.wireOp",EDGE,"E3748"),sQuery(id+"F17.wireOp",EDGE,"E3749"),sQuery(id+"F17.wireOp",EDGE,"E3750"),sQuery(id+"F17.wireOp",EDGE,"E3751"),sQuery(id+"F17.wireOp",EDGE,"E3752"),sQuery(id+"F17.wireOp",EDGE,"E3753"),sQuery(id+"F17.wireOp",EDGE,"E3754"),sQuery(id+"F17.wireOp",EDGE,"E3755"),sQuery(id+"F17.wireOp",EDGE,"E3756"),sQuery(id+"F17.wireOp",EDGE,"E3757"),sQuery(id+"F17.wireOp",EDGE,"E3758"),sQuery(id+"F17.wireOp",EDGE,"E3759"),sQuery(id+"F17.wireOp",EDGE,"E3760"),sQuery(id+"F17.wireOp",EDGE,"E3761"),sQuery(id+"F17.wireOp",EDGE,"E3762"),sQuery(id+"F17.wireOp",EDGE,"E3763"),sQuery(id+"F17.wireOp",EDGE,"E3764"),sQuery(id+"F17.wireOp",EDGE,"E3765"),sQuery(id+"F17.wireOp",EDGE,"E3766"),sQuery(id+"F17.wireOp",EDGE,"E3767"),sQuery(id+"F17.wireOp",EDGE,"E3768"),sQuery(id+"F17.wireOp",EDGE,"E3769"),sQuery(id+"F17.wireOp",EDGE,"E3770"),sQuery(id+"F17.wireOp",EDGE,"E3771"),sQuery(id+"F17.wireOp",EDGE,"E3772"),sQuery(id+"F17.wireOp",EDGE,"E3773"),sQuery(id+"F17.wireOp",EDGE,"E3774"),sQuery(id+"F17.wireOp",EDGE,"E3775"),sQuery(id+"F17.wireOp",EDGE,"E3776"),sQuery(id+"F17.wireOp",EDGE,"E3777"),sQuery(id+"F17.wireOp",EDGE,"E3778"),sQuery(id+"F17.wireOp",EDGE,"E3779"),sQuery(id+"F17.wireOp",EDGE,"E3780"),sQuery(id+"F17.wireOp",EDGE,"E3781"),sQuery(id+"F17.wireOp",EDGE,"E3782"),sQuery(id+"F17.wireOp",EDGE,"E3783"),sQuery(id+"F17.wireOp",EDGE,"E3784"),sQuery(id+"F17.wireOp",EDGE,"E3785"),sQuery(id+"F17.wireOp",EDGE,"E3786"),sQuery(id+"F17.wireOp",EDGE,"E3787"),sQuery(id+"F17.wireOp",EDGE,"E3788"),sQuery(id+"F17.wireOp",EDGE,"E3789"),sQuery(id+"F17.wireOp",EDGE,"E3790"),sQuery(id+"F17.wireOp",EDGE,"E3791"),sQuery(id+"F17.wireOp",EDGE,"E3792"),sQuery(id+"F17.wireOp",EDGE,"E3793"),sQuery(id+"F17.wireOp",EDGE,"E3794"),sQuery(id+"F17.wireOp",EDGE,"E3795"),sQuery(id+"F17.wireOp",EDGE,"E3796"),sQuery(id+"F17.wireOp",EDGE,"E3797"),sQuery(id+"F17.wireOp",EDGE,"E3798"),sQuery(id+"F17.wireOp",EDGE,"E3799"),sQuery(id+"F17.wireOp",EDGE,"E3800"),sQuery(id+"F17.wireOp",EDGE,"E3801"),sQuery(id+"F17.wireOp",EDGE,"E3802"),sQuery(id+"F17.wireOp",EDGE,"E3803"),sQuery(id+"F17.wireOp",EDGE,"E3804"),sQuery(id+"F17.wireOp",EDGE,"E3805"),sQuery(id+"F17.wireOp",EDGE,"E3806"),sQuery(id+"F17.wireOp",EDGE,"E3807"),sQuery(id+"F17.wireOp",EDGE,"E3808"),sQuery(id+"F17.wireOp",EDGE,"E3809"),sQuery(id+"F17.wireOp",EDGE,"E3810"),sQuery(id+"F17.wireOp",EDGE,"E3811"),sQuery(id+"F17.wireOp",EDGE,"E3812"),sQuery(id+"F17.wireOp",EDGE,"E3813"),sQuery(id+"F17.wireOp",EDGE,"E3814"),sQuery(id+"F17.wireOp",EDGE,"E3815"),sQuery(id+"F17.wireOp",EDGE,"E3816"),sQuery(id+"F17.wireOp",EDGE,"E3817"),sQuery(id+"F17.wireOp",EDGE,"E3818"),sQuery(id+"F17.wireOp",EDGE,"E3819"),sQuery(id+"F17.wireOp",EDGE,"E3820"),sQuery(id+"F17.wireOp",EDGE,"E3821"),sQuery(id+"F17.wireOp",EDGE,"E3822"),sQuery(id+"F17.wireOp",EDGE,"E3823"),sQuery(id+"F17.wireOp",EDGE,"E3824"),sQuery(id+"F17.wireOp",EDGE,"E3825"),sQuery(id+"F17.wireOp",EDGE,"E3826"),sQuery(id+"F17.wireOp",EDGE,"E3827"),sQuery(id+"F17.wireOp",EDGE,"E3828"),sQuery(id+"F17.wireOp",EDGE,"E3829"),sQuery(id+"F17.wireOp",EDGE,"E3830"),sQuery(id+"F17.wireOp",EDGE,"E3831"),sQuery(id+"F17.wireOp",EDGE,"E3832"),sQuery(id+"F17.wireOp",EDGE,"E3833"),sQuery(id+"F17.wireOp",EDGE,"E3834"),sQuery(id+"F17.wireOp",EDGE,"E3835"),sQuery(id+"F17.wireOp",EDGE,"E3836"),sQuery(id+"F17.wireOp",EDGE,"E3837"),sQuery(id+"F17.wireOp",EDGE,"E3838"),sQuery(id+"F17.wireOp",EDGE,"E3839"),sQuery(id+"F17.wireOp",EDGE,"E3840"),sQuery(id+"F17.wireOp",EDGE,"E3841"),sQuery(id+"F17.wireOp",EDGE,"E3842"),sQuery(id+"F17.wireOp",EDGE,"E3843"),sQuery(id+"F17.wireOp",EDGE,"E3844"),sQuery(id+"F17.wireOp",EDGE,"E3845"),sQuery(id+"F17.wireOp",EDGE,"E3846"),sQuery(id+"F17.wireOp",EDGE,"E3847"),sQuery(id+"F17.wireOp",EDGE,"E3848"),sQuery(id+"F17.wireOp",EDGE,"E3849"),sQuery(id+"F17.wireOp",EDGE,"E3850"),sQuery(id+"F17.wireOp",EDGE,"E3851"),sQuery(id+"F17.wireOp",EDGE,"E3852"),sQuery(id+"F17.wireOp",EDGE,"E3853"),sQuery(id+"F17.wireOp",EDGE,"E3854"),sQuery(id+"F17.wireOp",EDGE,"E3855"),sQuery(id+"F17.wireOp",EDGE,"E3856"),sQuery(id+"F17.wireOp",EDGE,"E3857"),sQuery(id+"F17.wireOp",EDGE,"E3858"),sQuery(id+"F17.wireOp",EDGE,"E3859"),sQuery(id+"F17.wireOp",EDGE,"E3860"),sQuery(id+"F17.wireOp",EDGE,"E3861"),sQuery(id+"F17.wireOp",EDGE,"E3862"),sQuery(id+"F17.wireOp",EDGE,"E3863"),sQuery(id+"F17.wireOp",EDGE,"E3864"),sQuery(id+"F17.wireOp",EDGE,"E3865"),sQuery(id+"F17.wireOp",EDGE,"E3866"),sQuery(id+"F17.wireOp",EDGE,"E3867"),sQuery(id+"F17.wireOp",EDGE,"E3868"),sQuery(id+"F17.wireOp",EDGE,"E3869"),sQuery(id+"F17.wireOp",EDGE,"E3870"),sQuery(id+"F17.wireOp",EDGE,"E3871"),sQuery(id+"F17.wireOp",EDGE,"E3872"),sQuery(id+"F17.wireOp",EDGE,"E3873"),sQuery(id+"F17.wireOp",EDGE,"E3874"),sQuery(id+"F17.wireOp",EDGE,"E3875"),sQuery(id+"F17.wireOp",EDGE,"E3876"),sQuery(id+"F17.wireOp",EDGE,"E3877"),sQuery(id+"F17.wireOp",EDGE,"E3878"),sQuery(id+"F17.wireOp",EDGE,"E3879"),sQuery(id+"F17.wireOp",EDGE,"E3880"),sQuery(id+"F17.wireOp",EDGE,"E3881"),sQuery(id+"F17.wireOp",EDGE,"E3882"),sQuery(id+"F17.wireOp",EDGE,"E3883"),sQuery(id+"F17.wireOp",EDGE,"E3884"),sQuery(id+"F17.wireOp",EDGE,"E3885"),sQuery(id+"F17.wireOp",EDGE,"E3886"),sQuery(id+"F17.wireOp",EDGE,"E3887"),sQuery(id+"F17.wireOp",EDGE,"E3888"),sQuery(id+"F17.wireOp",EDGE,"E3889"),sQuery(id+"F17.wireOp",EDGE,"E3890"),sQuery(id+"F17.wireOp",EDGE,"E3891"),sQuery(id+"F17.wireOp",EDGE,"E3892"),sQuery(id+"F17.wireOp",EDGE,"E3893"),sQuery(id+"F17.wireOp",EDGE,"E3894"),sQuery(id+"F17.wireOp",EDGE,"E3895"),sQuery(id+"F17.wireOp",EDGE,"E3896"),sQuery(id+"F17.wireOp",EDGE,"E3897"),sQuery(id+"F17.wireOp",EDGE,"E3898"),sQuery(id+"F17.wireOp",EDGE,"E3899"),sQuery(id+"F17.wireOp",EDGE,"E3900"),sQuery(id+"F17.wireOp",EDGE,"E3901"),sQuery(id+"F17.wireOp",EDGE,"E3902"),sQuery(id+"F17.wireOp",EDGE,"E3903"),sQuery(id+"F17.wireOp",EDGE,"E3904"),sQuery(id+"F17.wireOp",EDGE,"E3905"),sQuery(id+"F17.wireOp",EDGE,"E3906"),sQuery(id+"F17.wireOp",EDGE,"E3907"),sQuery(id+"F17.wireOp",EDGE,"E3908"),sQuery(id+"F17.wireOp",EDGE,"E3909"),sQuery(id+"F17.wireOp",EDGE,"E3910"),sQuery(id+"F17.wireOp",EDGE,"E3911"),sQuery(id+"F17.wireOp",EDGE,"E3912"),sQuery(id+"F17.wireOp",EDGE,"E3913"),sQuery(id+"F17.wireOp",EDGE,"E3914"),sQuery(id+"F17.wireOp",EDGE,"E3915"),sQuery(id+"F17.wireOp",EDGE,"E3916"),sQuery(id+"F17.wireOp",EDGE,"E3917"),sQuery(id+"F17.wireOp",EDGE,"E3918"),sQuery(id+"F17.wireOp",EDGE,"E3919"),sQuery(id+"F17.wireOp",EDGE,"E3920"),sQuery(id+"F17.wireOp",EDGE,"E3921"),sQuery(id+"F17.wireOp",EDGE,"E3922"),sQuery(id+"F17.wireOp",EDGE,"E3923"),sQuery(id+"F17.wireOp",EDGE,"E3924"),sQuery(id+"F17.wireOp",EDGE,"E3925"),sQuery(id+"F17.wireOp",EDGE,"E3926"),sQuery(id+"F17.wireOp",EDGE,"E3927"),sQuery(id+"F17.wireOp",EDGE,"E3928"),sQuery(id+"F17.wireOp",EDGE,"E3929"),sQuery(id+"F17.wireOp",EDGE,"E3930"),sQuery(id+"F17.wireOp",EDGE,"E3931"),sQuery(id+"F17.wireOp",EDGE,"E3932"),sQuery(id+"F17.wireOp",EDGE,"E3933"),sQuery(id+"F17.wireOp",EDGE,"E3934"),sQuery(id+"F17.wireOp",EDGE,"E3935"),sQuery(id+"F17.wireOp",EDGE,"E3936"),sQuery(id+"F17.wireOp",EDGE,"E3937"),sQuery(id+"F17.wireOp",EDGE,"E3938"),sQuery(id+"F17.wireOp",EDGE,"E3939"),sQuery(id+"F17.wireOp",EDGE,"E3940"),sQuery(id+"F17.wireOp",EDGE,"E3941"),sQuery(id+"F17.wireOp",EDGE,"E3942"),sQuery(id+"F17.wireOp",EDGE,"E3943"),sQuery(id+"F17.wireOp",EDGE,"E3944"),sQuery(id+"F17.wireOp",EDGE,"E3945"),sQuery(id+"F17.wireOp",EDGE,"E3946"),sQuery(id+"F17.wireOp",EDGE,"E3947"),sQuery(id+"F17.wireOp",EDGE,"E3948"),sQuery(id+"F17.wireOp",EDGE,"E3949"),sQuery(id+"F17.wireOp",EDGE,"E3950"),sQuery(id+"F17.wireOp",EDGE,"E3951"),sQuery(id+"F17.wireOp",EDGE,"E3952"),sQuery(id+"F17.wireOp",EDGE,"E3953"),sQuery(id+"F17.wireOp",EDGE,"E3954"),sQuery(id+"F17.wireOp",EDGE,"E3955"),sQuery(id+"F17.wireOp",EDGE,"E3956"),sQuery(id+"F17.wireOp",EDGE,"E3957"),sQuery(id+"F17.wireOp",EDGE,"E3958"),sQuery(id+"F17.wireOp",EDGE,"E3959"),sQuery(id+"F17.wireOp",EDGE,"E3960"),sQuery(id+"F17.wireOp",EDGE,"E3961"),sQuery(id+"F17.wireOp",EDGE,"E3962"),sQuery(id+"F17.wireOp",EDGE,"E3963"),sQuery(id+"F17.wireOp",EDGE,"E3964"),sQuery(id+"F17.wireOp",EDGE,"E3965"),sQuery(id+"F17.wireOp",EDGE,"E3966"),sQuery(id+"F17.wireOp",EDGE,"E3967"),sQuery(id+"F17.wireOp",EDGE,"E3968"),sQuery(id+"F17.wireOp",EDGE,"E3969"),sQuery(id+"F17.wireOp",EDGE,"E3970"),sQuery(id+"F17.wireOp",EDGE,"E3971"),sQuery(id+"F17.wireOp",EDGE,"E3972"),sQuery(id+"F17.wireOp",EDGE,"E3973"),sQuery(id+"F17.wireOp",EDGE,"E3974"),sQuery(id+"F17.wireOp",EDGE,"E3975"),sQuery(id+"F17.wireOp",EDGE,"E3976"),sQuery(id+"F17.wireOp",EDGE,"E3977"),sQuery(id+"F17.wireOp",EDGE,"E3978"),sQuery(id+"F17.wireOp",EDGE,"E3979"),sQuery(id+"F17.wireOp",EDGE,"E3980"),sQuery(id+"F17.wireOp",EDGE,"E3981"),sQuery(id+"F17.wireOp",EDGE,"E3982"),sQuery(id+"F17.wireOp",EDGE,"E3983"),sQuery(id+"F17.wireOp",EDGE,"E3984"),sQuery(id+"F17.wireOp",EDGE,"E3985"),sQuery(id+"F17.wireOp",EDGE,"E3986"),sQuery(id+"F17.wireOp",EDGE,"E3987"),sQuery(id+"F17.wireOp",EDGE,"E3988"),sQuery(id+"F17.wireOp",EDGE,"E3989"),sQuery(id+"F17.wireOp",EDGE,"E3990"),sQuery(id+"F17.wireOp",EDGE,"E3991"),sQuery(id+"F17.wireOp",EDGE,"E3992"),sQuery(id+"F17.wireOp",EDGE,"E3993"),sQuery(id+"F17.wireOp",EDGE,"E3994"),sQuery(id+"F17.wireOp",EDGE,"E3995"),sQuery(id+"F17.wireOp",EDGE,"E3996"),sQuery(id+"F17.wireOp",EDGE,"E3997"),sQuery(id+"F17.wireOp",EDGE,"E3998"),sQuery(id+"F17.wireOp",EDGE,"E3999"),sQuery(id+"F17.wireOp",EDGE,"E4000"),sQuery(id+"F17.wireOp",EDGE,"E4001"),sQuery(id+"F17.wireOp",EDGE,"E4002"),sQuery(id+"F17.wireOp",EDGE,"E4003"),sQuery(id+"F17.wireOp",EDGE,"E4004"),sQuery(id+"F17.wireOp",EDGE,"E4005"),sQuery(id+"F17.wireOp",EDGE,"E4006"),sQuery(id+"F17.wireOp",EDGE,"E4007"),sQuery(id+"F17.wireOp",EDGE,"E4008"),sQuery(id+"F17.wireOp",EDGE,"E4009"),sQuery(id+"F17.wireOp",EDGE,"E4010"),sQuery(id+"F17.wireOp",EDGE,"E4011"),sQuery(id+"F17.wireOp",EDGE,"E4012"),sQuery(id+"F17.wireOp",EDGE,"E4013"),sQuery(id+"F17.wireOp",EDGE,"E4014"),sQuery(id+"F17.wireOp",EDGE,"E4015"),sQuery(id+"F17.wireOp",EDGE,"E4016"),sQuery(id+"F17.wireOp",EDGE,"E4017"),sQuery(id+"F17.wireOp",EDGE,"E4018"),sQuery(id+"F17.wireOp",EDGE,"E4019"),sQuery(id+"F17.wireOp",EDGE,"E4020"),sQuery(id+"F17.wireOp",EDGE,"E4021"),sQuery(id+"F17.wireOp",EDGE,"E4022"),sQuery(id+"F17.wireOp",EDGE,"E4023"),sQuery(id+"F17.wireOp",EDGE,"E4024"),sQuery(id+"F17.wireOp",EDGE,"E4025"),sQuery(id+"F17.wireOp",EDGE,"E4026"),sQuery(id+"F17.wireOp",EDGE,"E4027"),sQuery(id+"F17.wireOp",EDGE,"E4028"),sQuery(id+"F17.wireOp",EDGE,"E4029"),sQuery(id+"F17.wireOp",EDGE,"E4030"),sQuery(id+"F17.wireOp",EDGE,"E4031"),sQuery(id+"F17.wireOp",EDGE,"E4032"),sQuery(id+"F17.wireOp",EDGE,"E4033"),sQuery(id+"F17.wireOp",EDGE,"E4034"),sQuery(id+"F17.wireOp",EDGE,"E4035"),sQuery(id+"F17.wireOp",EDGE,"E4036"),sQuery(id+"F17.wireOp",EDGE,"E4037"),sQuery(id+"F17.wireOp",EDGE,"E4038"),sQuery(id+"F17.wireOp",EDGE,"E4039"),sQuery(id+"F17.wireOp",EDGE,"E4040"),sQuery(id+"F17.wireOp",EDGE,"E4041"),sQuery(id+"F17.wireOp",EDGE,"E4042"),sQuery(id+"F17.wireOp",EDGE,"E4043"),sQuery(id+"F17.wireOp",EDGE,"E4044"),sQuery(id+"F17.wireOp",EDGE,"E4045"),sQuery(id+"F17.wireOp",EDGE,"E4046"),sQuery(id+"F17.wireOp",EDGE,"E4047"),sQuery(id+"F17.wireOp",EDGE,"E4048"),sQuery(id+"F17.wireOp",EDGE,"E4049"),sQuery(id+"F17.wireOp",EDGE,"E4050"),sQuery(id+"F17.wireOp",EDGE,"E4051"),sQuery(id+"F17.wireOp",EDGE,"E4052"),sQuery(id+"F17.wireOp",EDGE,"E4053"),sQuery(id+"F17.wireOp",EDGE,"E4054"),sQuery(id+"F17.wireOp",EDGE,"E4055"),sQuery(id+"F17.wireOp",EDGE,"E4056"),sQuery(id+"F17.wireOp",EDGE,"E4057"),sQuery(id+"F17.wireOp",EDGE,"E4058"),sQuery(id+"F17.wireOp",EDGE,"E4059"),sQuery(id+"F17.wireOp",EDGE,"E4060"),sQuery(id+"F17.wireOp",EDGE,"E4061"),sQuery(id+"F17.wireOp",EDGE,"E4062"),sQuery(id+"F17.wireOp",EDGE,"E4063"),sQuery(id+"F17.wireOp",EDGE,"E4064"),sQuery(id+"F17.wireOp",EDGE,"E4065"),sQuery(id+"F17.wireOp",EDGE,"E4066"),sQuery(id+"F17.wireOp",EDGE,"E4067"),sQuery(id+"F17.wireOp",EDGE,"E4068"),sQuery(id+"F17.wireOp",EDGE,"E4069"),sQuery(id+"F17.wireOp",EDGE,"E4070"),sQuery(id+"F17.wireOp",EDGE,"E4071"),sQuery(id+"F17.wireOp",EDGE,"E4072"),sQuery(id+"F17.wireOp",EDGE,"E4073"),sQuery(id+"F17.wireOp",EDGE,"E4074"),sQuery(id+"F17.wireOp",EDGE,"E4075"),sQuery(id+"F17.wireOp",EDGE,"E4076"),sQuery(id+"F17.wireOp",EDGE,"E4077"),sQuery(id+"F17.wireOp",EDGE,"E4078"),sQuery(id+"F17.wireOp",EDGE,"E4079"),sQuery(id+"F17.wireOp",EDGE,"E4080"),sQuery(id+"F17.wireOp",EDGE,"E4081"),sQuery(id+"F17.wireOp",EDGE,"E4082"),sQuery(id+"F17.wireOp",EDGE,"E4083"),sQuery(id+"F17.wireOp",EDGE,"E4084"),sQuery(id+"F17.wireOp",EDGE,"E4085"),sQuery(id+"F17.wireOp",EDGE,"E4086"),sQuery(id+"F17.wireOp",EDGE,"E4087"),sQuery(id+"F17.wireOp",EDGE,"E4088"),sQuery(id+"F17.wireOp",EDGE,"E4089"),sQuery(id+"F17.wireOp",EDGE,"E4090"),sQuery(id+"F17.wireOp",EDGE,"E4091"),sQuery(id+"F17.wireOp",EDGE,"E4092"),sQuery(id+"F17.wireOp",EDGE,"E4093"),sQuery(id+"F17.wireOp",EDGE,"E4094"),sQuery(id+"F17.wireOp",EDGE,"E4095"),sQuery(id+"F17.wireOp",EDGE,"E4096"),sQuery(id+"F17.wireOp",EDGE,"E4097"),sQuery(id+"F17.wireOp",EDGE,"E4098"),sQuery(id+"F17.wireOp",EDGE,"E4099"),sQuery(id+"F17.wireOp",EDGE,"E4100"),sQuery(id+"F17.wireOp",EDGE,"E4101"),sQuery(id+"F17.wireOp",EDGE,"E4102"),sQuery(id+"F17.wireOp",EDGE,"E4103"),sQuery(id+"F17.wireOp",EDGE,"E4104"),sQuery(id+"F17.wireOp",EDGE,"E4105"),sQuery(id+"F17.wireOp",EDGE,"E4106"),sQuery(id+"F17.wireOp",EDGE,"E4107"),sQuery(id+"F17.wireOp",EDGE,"E4108"),sQuery(id+"F17.wireOp",EDGE,"E4109"),sQuery(id+"F17.wireOp",EDGE,"E4110"),sQuery(id+"F17.wireOp",EDGE,"E4111"),sQuery(id+"F17.wireOp",EDGE,"E4112"),sQuery(id+"F17.wireOp",EDGE,"E4113"),sQuery(id+"F17.wireOp",EDGE,"E4114"),sQuery(id+"F17.wireOp",EDGE,"E4115"),sQuery(id+"F17.wireOp",EDGE,"E4116"),sQuery(id+"F17.wireOp",EDGE,"E4117"),sQuery(id+"F17.wireOp",EDGE,"E4118"),sQuery(id+"F17.wireOp",EDGE,"E4119"),sQuery(id+"F17.wireOp",EDGE,"E4120"),sQuery(id+"F17.wireOp",EDGE,"E4121"),sQuery(id+"F17.wireOp",EDGE,"E4122"),sQuery(id+"F17.wireOp",EDGE,"E4123"),sQuery(id+"F17.wireOp",EDGE,"E4124"),sQuery(id+"F17.wireOp",EDGE,"E4125"),sQuery(id+"F17.wireOp",EDGE,"E4126"),sQuery(id+"F17.wireOp",EDGE,"E4127"),sQuery(id+"F17.wireOp",EDGE,"E4128"),sQuery(id+"F17.wireOp",EDGE,"E4129"),sQuery(id+"F17.wireOp",EDGE,"E4130"),sQuery(id+"F17.wireOp",EDGE,"E4131"),sQuery(id+"F17.wireOp",EDGE,"E4132"),sQuery(id+"F17.wireOp",EDGE,"E4133"),sQuery(id+"F17.wireOp",EDGE,"E4134"),sQuery(id+"F17.wireOp",EDGE,"E4135"),sQuery(id+"F17.wireOp",EDGE,"E4136"),sQuery(id+"F17.wireOp",EDGE,"E4137"),sQuery(id+"F17.wireOp",EDGE,"E4138"),sQuery(id+"F17.wireOp",EDGE,"E4139"),sQuery(id+"F17.wireOp",EDGE,"E4140"),sQuery(id+"F17.wireOp",EDGE,"E4141"),sQuery(id+"F17.wireOp",EDGE,"E4142"),sQuery(id+"F17.wireOp",EDGE,"E4143"),sQuery(id+"F17.wireOp",EDGE,"E4144"),sQuery(id+"F17.wireOp",EDGE,"E4145"),sQuery(id+"F17.wireOp",EDGE,"E4146"),sQuery(id+"F17.wireOp",EDGE,"E4147"),sQuery(id+"F17.wireOp",EDGE,"E4148"),sQuery(id+"F17.wireOp",EDGE,"E4149"),sQuery(id+"F17.wireOp",EDGE,"E4150"),sQuery(id+"F17.wireOp",EDGE,"E4151"),sQuery(id+"F17.wireOp",EDGE,"E4152"),sQuery(id+"F17.wireOp",EDGE,"E4153"),sQuery(id+"F17.wireOp",EDGE,"E4154"),sQuery(id+"F17.wireOp",EDGE,"E4155"),sQuery(id+"F17.wireOp",EDGE,"E4156"),sQuery(id+"F17.wireOp",EDGE,"E4157"),sQuery(id+"F17.wireOp",EDGE,"E4158"),sQuery(id+"F17.wireOp",EDGE,"E4159"),sQuery(id+"F17.wireOp",EDGE,"E4160"),sQuery(id+"F17.wireOp",EDGE,"E4161"),sQuery(id+"F17.wireOp",EDGE,"E4162"),sQuery(id+"F17.wireOp",EDGE,"E4163"),sQuery(id+"F17.wireOp",EDGE,"E4164"),sQuery(id+"F17.wireOp",EDGE,"E4165"),sQuery(id+"F17.wireOp",EDGE,"E4166"),sQuery(id+"F17.wireOp",EDGE,"E4167"),sQuery(id+"F17.wireOp",EDGE,"E4168"),sQuery(id+"F17.wireOp",EDGE,"E4169"),sQuery(id+"F17.wireOp",EDGE,"E4170"),sQuery(id+"F17.wireOp",EDGE,"E4171"),sQuery(id+"F17.wireOp",EDGE,"E4172"),sQuery(id+"F17.wireOp",EDGE,"E4173"),sQuery(id+"F17.wireOp",EDGE,"E4174"),sQuery(id+"F17.wireOp",EDGE,"E4175"),sQuery(id+"F17.wireOp",EDGE,"E4176"),sQuery(id+"F17.wireOp",EDGE,"E4177"),sQuery(id+"F17.wireOp",EDGE,"E4178"),sQuery(id+"F17.wireOp",EDGE,"E4179"),sQuery(id+"F17.wireOp",EDGE,"E4180"),sQuery(id+"F17.wireOp",EDGE,"E4181"),sQuery(id+"F17.wireOp",EDGE,"E4182"),sQuery(id+"F17.wireOp",EDGE,"E4183"),sQuery(id+"F17.wireOp",EDGE,"E4184"),sQuery(id+"F17.wireOp",EDGE,"E4185"),sQuery(id+"F17.wireOp",EDGE,"E4186"),sQuery(id+"F17.wireOp",EDGE,"E4187"),sQuery(id+"F17.wireOp",EDGE,"E4188"),sQuery(id+"F17.wireOp",EDGE,"E4189"),sQuery(id+"F17.wireOp",EDGE,"E4190"),sQuery(id+"F17.wireOp",EDGE,"E4191"),sQuery(id+"F17.wireOp",EDGE,"E4192"),sQuery(id+"F17.wireOp",EDGE,"E4193"),sQuery(id+"F17.wireOp",EDGE,"E4194"),sQuery(id+"F17.wireOp",EDGE,"E4195"),sQuery(id+"F17.wireOp",EDGE,"E4196"),sQuery(id+"F17.wireOp",EDGE,"E4197"),sQuery(id+"F17.wireOp",EDGE,"E4198"),sQuery(id+"F17.wireOp",EDGE,"E4199"),sQuery(id+"F17.wireOp",EDGE,"E4200"),sQuery(id+"F17.wireOp",EDGE,"E4201"),sQuery(id+"F17.wireOp",EDGE,"E4202"),sQuery(id+"F17.wireOp",EDGE,"E4203"),sQuery(id+"F17.wireOp",EDGE,"E4204"),sQuery(id+"F17.wireOp",EDGE,"E4205"),sQuery(id+"F17.wireOp",EDGE,"E4206"),sQuery(id+"F17.wireOp",EDGE,"E4207"),sQuery(id+"F17.wireOp",EDGE,"E4208"),sQuery(id+"F17.wireOp",EDGE,"E4209"),sQuery(id+"F17.wireOp",EDGE,"E4210"),sQuery(id+"F17.wireOp",EDGE,"E4211"),sQuery(id+"F17.wireOp",EDGE,"E4212"),sQuery(id+"F17.wireOp",EDGE,"E4213"),sQuery(id+"F17.wireOp",EDGE,"E4214"),sQuery(id+"F17.wireOp",EDGE,"E4215"),sQuery(id+"F17.wireOp",EDGE,"E4216"),sQuery(id+"F17.wireOp",EDGE,"E4217"),sQuery(id+"F17.wireOp",EDGE,"E4218"),sQuery(id+"F17.wireOp",EDGE,"E4219"),sQuery(id+"F17.wireOp",EDGE,"E4220"),sQuery(id+"F17.wireOp",EDGE,"E4221"),sQuery(id+"F17.wireOp",EDGE,"E4222"),sQuery(id+"F17.wireOp",EDGE,"E4223"),sQuery(id+"F17.wireOp",EDGE,"E4224"),sQuery(id+"F17.wireOp",EDGE,"E4225"),sQuery(id+"F17.wireOp",EDGE,"E4226"),sQuery(id+"F17.wireOp",EDGE,"E4227"),sQuery(id+"F17.wireOp",EDGE,"E4228"),sQuery(id+"F17.wireOp",EDGE,"E4229"),sQuery(id+"F17.wireOp",EDGE,"E4230"),sQuery(id+"F17.wireOp",EDGE,"E4231"),sQuery(id+"F17.wireOp",EDGE,"E4232"),sQuery(id+"F17.wireOp",EDGE,"E4233"),sQuery(id+"F17.wireOp",EDGE,"E4234"),sQuery(id+"F17.wireOp",EDGE,"E4235"),sQuery(id+"F17.wireOp",EDGE,"E4236"),sQuery(id+"F17.wireOp",EDGE,"E4237"),sQuery(id+"F17.wireOp",EDGE,"E4238"),sQuery(id+"F17.wireOp",EDGE,"E4239"),sQuery(id+"F17.wireOp",EDGE,"E4240"),sQuery(id+"F17.wireOp",EDGE,"E4241"),sQuery(id+"F17.wireOp",EDGE,"E4242"),sQuery(id+"F17.wireOp",EDGE,"E4243"),sQuery(id+"F17.wireOp",EDGE,"E4244"),sQuery(id+"F17.wireOp",EDGE,"E4245"),sQuery(id+"F17.wireOp",EDGE,"E4246"),sQuery(id+"F17.wireOp",EDGE,"E4247"),sQuery(id+"F17.wireOp",EDGE,"E4248"),sQuery(id+"F17.wireOp",EDGE,"E4249"),sQuery(id+"F17.wireOp",EDGE,"E4250"),sQuery(id+"F17.wireOp",EDGE,"E4251"),sQuery(id+"F17.wireOp",EDGE,"E4252"),sQuery(id+"F17.wireOp",EDGE,"E4253"),sQuery(id+"F17.wireOp",EDGE,"E4254"),sQuery(id+"F17.wireOp",EDGE,"E4255"),sQuery(id+"F17.wireOp",EDGE,"E4256"),sQuery(id+"F17.wireOp",EDGE,"E4257"),sQuery(id+"F17.wireOp",EDGE,"E4258"),sQuery(id+"F17.wireOp",EDGE,"E4259"),sQuery(id+"F17.wireOp",EDGE,"E4260"),sQuery(id+"F17.wireOp",EDGE,"E4261"),sQuery(id+"F17.wireOp",EDGE,"E4262"),sQuery(id+"F17.wireOp",EDGE,"E4263"),sQuery(id+"F17.wireOp",EDGE,"E4264"),sQuery(id+"F17.wireOp",EDGE,"E4265"),sQuery(id+"F17.wireOp",EDGE,"E4266"),sQuery(id+"F17.wireOp",EDGE,"E4267"),sQuery(id+"F17.wireOp",EDGE,"E4268"),sQuery(id+"F17.wireOp",EDGE,"E4269"),sQuery(id+"F17.wireOp",EDGE,"E4270"),sQuery(id+"F17.wireOp",EDGE,"E4271"),sQuery(id+"F17.wireOp",EDGE,"E4272"),sQuery(id+"F17.wireOp",EDGE,"E4273"),sQuery(id+"F17.wireOp",EDGE,"E4274"),sQuery(id+"F17.wireOp",EDGE,"E4275"),sQuery(id+"F17.wireOp",EDGE,"E4276"),sQuery(id+"F17.wireOp",EDGE,"E4277"),sQuery(id+"F17.wireOp",EDGE,"E4278"),sQuery(id+"F17.wireOp",EDGE,"E4279"),sQuery(id+"F17.wireOp",EDGE,"E4280"),sQuery(id+"F17.wireOp",EDGE,"E4281"),sQuery(id+"F17.wireOp",EDGE,"E4282"),sQuery(id+"F17.wireOp",EDGE,"E4283"),sQuery(id+"F17.wireOp",EDGE,"E4284"),sQuery(id+"F17.wireOp",EDGE,"E4285"),sQuery(id+"F17.wireOp",EDGE,"E4286"),sQuery(id+"F17.wireOp",EDGE,"E4287"),sQuery(id+"F17.wireOp",EDGE,"E4288"),sQuery(id+"F17.wireOp",EDGE,"E4289"),sQuery(id+"F17.wireOp",EDGE,"E4290"),sQuery(id+"F17.wireOp",EDGE,"E4291"),sQuery(id+"F17.wireOp",EDGE,"E4292"),sQuery(id+"F17.wireOp",EDGE,"E4293"),sQuery(id+"F17.wireOp",EDGE,"E4294"),sQuery(id+"F17.wireOp",EDGE,"E4295"),sQuery(id+"F17.wireOp",EDGE,"E4296"),sQuery(id+"F17.wireOp",EDGE,"E4297"),sQuery(id+"F17.wireOp",EDGE,"E4298"),sQuery(id+"F17.wireOp",EDGE,"E4299"),sQuery(id+"F17.wireOp",EDGE,"E4300"),sQuery(id+"F17.wireOp",EDGE,"E4301"),sQuery(id+"F17.wireOp",EDGE,"E4302"),sQuery(id+"F17.wireOp",EDGE,"E4303"),sQuery(id+"F17.wireOp",EDGE,"E4304"),sQuery(id+"F17.wireOp",EDGE,"E4305"),sQuery(id+"F17.wireOp",EDGE,"E4306"),sQuery(id+"F17.wireOp",EDGE,"E4307"),sQuery(id+"F17.wireOp",EDGE,"E4308"),sQuery(id+"F17.wireOp",EDGE,"E4309"),sQuery(id+"F17.wireOp",EDGE,"E4310"),sQuery(id+"F17.wireOp",EDGE,"E4311"),sQuery(id+"F17.wireOp",EDGE,"E4312"),sQuery(id+"F17.wireOp",EDGE,"E4313"),sQuery(id+"F17.wireOp",EDGE,"E4314"),sQuery(id+"F17.wireOp",EDGE,"E4315"),sQuery(id+"F17.wireOp",EDGE,"E4316"),sQuery(id+"F17.wireOp",EDGE,"E4317"),sQuery(id+"F17.wireOp",EDGE,"E4318"),sQuery(id+"F17.wireOp",EDGE,"E4319"),sQuery(id+"F17.wireOp",EDGE,"E4320"),sQuery(id+"F17.wireOp",EDGE,"E4321"),sQuery(id+"F17.wireOp",EDGE,"E4322"),sQuery(id+"F17.wireOp",EDGE,"E4323"),sQuery(id+"F17.wireOp",EDGE,"E4324"),sQuery(id+"F17.wireOp",EDGE,"E4325"),sQuery(id+"F17.wireOp",EDGE,"E4326"),sQuery(id+"F17.wireOp",EDGE,"E4327"),sQuery(id+"F17.wireOp",EDGE,"E4328"),sQuery(id+"F17.wireOp",EDGE,"E4329"),sQuery(id+"F17.wireOp",EDGE,"E4330"),sQuery(id+"F17.wireOp",EDGE,"E4331"),sQuery(id+"F17.wireOp",EDGE,"E4332"),sQuery(id+"F17.wireOp",EDGE,"E4333"),sQuery(id+"F17.wireOp",EDGE,"E4334"),sQuery(id+"F17.wireOp",EDGE,"E4335"),sQuery(id+"F17.wireOp",EDGE,"E4336"),sQuery(id+"F17.wireOp",EDGE,"E4337"),sQuery(id+"F17.wireOp",EDGE,"E4338"),sQuery(id+"F17.wireOp",EDGE,"E4339"),sQuery(id+"F17.wireOp",EDGE,"E4340"),sQuery(id+"F17.wireOp",EDGE,"E4341"),sQuery(id+"F17.wireOp",EDGE,"E4342"),sQuery(id+"F17.wireOp",EDGE,"E4343"),sQuery(id+"F17.wireOp",EDGE,"E4344"),sQuery(id+"F17.wireOp",EDGE,"E4345"),sQuery(id+"F17.wireOp",EDGE,"E4346"),sQuery(id+"F17.wireOp",EDGE,"E4347"),sQuery(id+"F17.wireOp",EDGE,"E4348"),sQuery(id+"F17.wireOp",EDGE,"E4349"),sQuery(id+"F17.wireOp",EDGE,"E4350"),sQuery(id+"F17.wireOp",EDGE,"E4351"),sQuery(id+"F17.wireOp",EDGE,"E4352"),sQuery(id+"F17.wireOp",EDGE,"E4353"),sQuery(id+"F17.wireOp",EDGE,"E4354"),sQuery(id+"F17.wireOp",EDGE,"E4355"),sQuery(id+"F17.wireOp",EDGE,"E4356"),sQuery(id+"F17.wireOp",EDGE,"E4357"),sQuery(id+"F17.wireOp",EDGE,"E4358"),sQuery(id+"F17.wireOp",EDGE,"E4359"),sQuery(id+"F17.wireOp",EDGE,"E4360"),sQuery(id+"F17.wireOp",EDGE,"E4361"),sQuery(id+"F17.wireOp",EDGE,"E4362"),sQuery(id+"F17.wireOp",EDGE,"E4363"),sQuery(id+"F17.wireOp",EDGE,"E4364"),sQuery(id+"F17.wireOp",EDGE,"E4365"),sQuery(id+"F17.wireOp",EDGE,"E4366"),sQuery(id+"F17.wireOp",EDGE,"E4367"),sQuery(id+"F17.wireOp",EDGE,"E4368"),sQuery(id+"F17.wireOp",EDGE,"E4369"),sQuery(id+"F17.wireOp",EDGE,"E4370"),sQuery(id+"F17.wireOp",EDGE,"E4371"),sQuery(id+"F17.wireOp",EDGE,"E4372"),sQuery(id+"F17.wireOp",EDGE,"E4373"),sQuery(id+"F17.wireOp",EDGE,"E4374"),sQuery(id+"F17.wireOp",EDGE,"E4375"),sQuery(id+"F17.wireOp",EDGE,"E4376"),sQuery(id+"F17.wireOp",EDGE,"E4377"),sQuery(id+"F17.wireOp",EDGE,"E4378"),sQuery(id+"F17.wireOp",EDGE,"E4379"),sQuery(id+"F17.wireOp",EDGE,"E4380"),sQuery(id+"F17.wireOp",EDGE,"E4381"),sQuery(id+"F17.wireOp",EDGE,"E4382"),sQuery(id+"F17.wireOp",EDGE,"E4383"),sQuery(id+"F17.wireOp",EDGE,"E4384"),sQuery(id+"F17.wireOp",EDGE,"E4385"),sQuery(id+"F17.wireOp",EDGE,"E4386"),sQuery(id+"F17.wireOp",EDGE,"E4387"),sQuery(id+"F17.wireOp",EDGE,"E4388"),sQuery(id+"F17.wireOp",EDGE,"E4389"),sQuery(id+"F17.wireOp",EDGE,"E4390"),sQuery(id+"F17.wireOp",EDGE,"E4391"),sQuery(id+"F17.wireOp",EDGE,"E4392"),sQuery(id+"F17.wireOp",EDGE,"E4393"),sQuery(id+"F17.wireOp",EDGE,"E4394"),sQuery(id+"F17.wireOp",EDGE,"E4395"),sQuery(id+"F17.wireOp",EDGE,"E4396"),sQuery(id+"F17.wireOp",EDGE,"E4397"),sQuery(id+"F17.wireOp",EDGE,"E4398"),sQuery(id+"F17.wireOp",EDGE,"E4399"),sQuery(id+"F17.wireOp",EDGE,"E4400"),sQuery(id+"F17.wireOp",EDGE,"E4401"),sQuery(id+"F17.wireOp",EDGE,"E4402"),sQuery(id+"F17.wireOp",EDGE,"E4403"),sQuery(id+"F17.wireOp",EDGE,"E4404"),sQuery(id+"F17.wireOp",EDGE,"E4405"),sQuery(id+"F17.wireOp",EDGE,"E4406"),sQuery(id+"F17.wireOp",EDGE,"E4407"),sQuery(id+"F17.wireOp",EDGE,"E4408"),sQuery(id+"F17.wireOp",EDGE,"E4409"),sQuery(id+"F17.wireOp",EDGE,"E4410"),sQuery(id+"F17.wireOp",EDGE,"E4411"),sQuery(id+"F17.wireOp",EDGE,"E4412"),sQuery(id+"F17.wireOp",EDGE,"E4413"),sQuery(id+"F17.wireOp",EDGE,"E4414"),sQuery(id+"F17.wireOp",EDGE,"E4415"),sQuery(id+"F17.wireOp",EDGE,"E4416"),sQuery(id+"F17.wireOp",EDGE,"E4417"),sQuery(id+"F17.wireOp",EDGE,"E4418"),sQuery(id+"F17.wireOp",EDGE,"E4419"),sQuery(id+"F17.wireOp",EDGE,"E4420"),sQuery(id+"F17.wireOp",EDGE,"E4421"),sQuery(id+"F17.wireOp",EDGE,"E4422"),sQuery(id+"F17.wireOp",EDGE,"E4423"),sQuery(id+"F17.wireOp",EDGE,"E4424"),sQuery(id+"F17.wireOp",EDGE,"E4425"),sQuery(id+"F17.wireOp",EDGE,"E4426"),sQuery(id+"F17.wireOp",EDGE,"E4427"),sQuery(id+"F17.wireOp",EDGE,"E4428"),sQuery(id+"F17.wireOp",EDGE,"E4429"),sQuery(id+"F17.wireOp",EDGE,"E4430"),sQuery(id+"F17.wireOp",EDGE,"E4431"),sQuery(id+"F17.wireOp",EDGE,"E4432"),sQuery(id+"F17.wireOp",EDGE,"E4433"),sQuery(id+"F17.wireOp",EDGE,"E4434"),sQuery(id+"F17.wireOp",EDGE,"E4435"),sQuery(id+"F17.wireOp",EDGE,"E4436"),sQuery(id+"F17.wireOp",EDGE,"E4437"),sQuery(id+"F17.wireOp",EDGE,"E4438"),sQuery(id+"F17.wireOp",EDGE,"E4439"),sQuery(id+"F17.wireOp",EDGE,"E4440"),sQuery(id+"F17.wireOp",EDGE,"E4441"),sQuery(id+"F17.wireOp",EDGE,"E4442"),sQuery(id+"F17.wireOp",EDGE,"E4443"),sQuery(id+"F17.wireOp",EDGE,"E4444"),sQuery(id+"F17.wireOp",EDGE,"E4445"),sQuery(id+"F17.wireOp",EDGE,"E4446"),sQuery(id+"F17.wireOp",EDGE,"E4447"),sQuery(id+"F17.wireOp",EDGE,"E4448"),sQuery(id+"F17.wireOp",EDGE,"E4449"),sQuery(id+"F17.wireOp",EDGE,"E4450"),sQuery(id+"F17.wireOp",EDGE,"E4451"),sQuery(id+"F17.wireOp",EDGE,"E4452"),sQuery(id+"F17.wireOp",EDGE,"E4453"),sQuery(id+"F17.wireOp",EDGE,"E4454"),sQuery(id+"F17.wireOp",EDGE,"E4455"),sQuery(id+"F17.wireOp",EDGE,"E4456"),sQuery(id+"F17.wireOp",EDGE,"E4457"),sQuery(id+"F17.wireOp",EDGE,"E4458"),sQuery(id+"F17.wireOp",EDGE,"E4459"),sQuery(id+"F17.wireOp",EDGE,"E4460"),sQuery(id+"F17.wireOp",EDGE,"E4461"),sQuery(id+"F17.wireOp",EDGE,"E4462"),sQuery(id+"F17.wireOp",EDGE,"E4463"),sQuery(id+"F17.wireOp",EDGE,"E4464"),sQuery(id+"F17.wireOp",EDGE,"E4465"),sQuery(id+"F17.wireOp",EDGE,"E4466"),sQuery(id+"F17.wireOp",EDGE,"E4467"),sQuery(id+"F17.wireOp",EDGE,"E4468"),sQuery(id+"F17.wireOp",EDGE,"E4469"),sQuery(id+"F17.wireOp",EDGE,"E4470"),sQuery(id+"F17.wireOp",EDGE,"E4471"),sQuery(id+"F17.wireOp",EDGE,"E4472"),sQuery(id+"F17.wireOp",EDGE,"E4473"),sQuery(id+"F17.wireOp",EDGE,"E4474"),sQuery(id+"F17.wireOp",EDGE,"E4475"),sQuery(id+"F17.wireOp",EDGE,"E4476"),sQuery(id+"F17.wireOp",EDGE,"E4477"),sQuery(id+"F17.wireOp",EDGE,"E4478"),sQuery(id+"F17.wireOp",EDGE,"E4479"),sQuery(id+"F17.wireOp",EDGE,"E4480"),sQuery(id+"F17.wireOp",EDGE,"E4481"),sQuery(id+"F17.wireOp",EDGE,"E4482"),sQuery(id+"F17.wireOp",EDGE,"E4483"),sQuery(id+"F17.wireOp",EDGE,"E4484"),sQuery(id+"F17.wireOp",EDGE,"E4485"),sQuery(id+"F17.wireOp",EDGE,"E4486"),sQuery(id+"F17.wireOp",EDGE,"E4487"),sQuery(id+"F17.wireOp",EDGE,"E4488"),sQuery(id+"F17.wireOp",EDGE,"E4489"),sQuery(id+"F17.wireOp",EDGE,"E4490"),sQuery(id+"F17.wireOp",EDGE,"E4491"),sQuery(id+"F17.wireOp",EDGE,"E4492"),sQuery(id+"F17.wireOp",EDGE,"E4493"),sQuery(id+"F17.wireOp",EDGE,"E4494"),sQuery(id+"F17.wireOp",EDGE,"E4495"),sQuery(id+"F17.wireOp",EDGE,"E4496"),sQuery(id+"F17.wireOp",EDGE,"E4497"),sQuery(id+"F17.wireOp",EDGE,"E4498"),sQuery(id+"F17.wireOp",EDGE,"E4499"),sQuery(id+"F17.wireOp",EDGE,"E4500"),sQuery(id+"F17.wireOp",EDGE,"E4501"),sQuery(id+"F17.wireOp",EDGE,"E4502"),sQuery(id+"F17.wireOp",EDGE,"E4503"),sQuery(id+"F17.wireOp",EDGE,"E4504"),sQuery(id+"F17.wireOp",EDGE,"E4505"),sQuery(id+"F17.wireOp",EDGE,"E4506"),sQuery(id+"F17.wireOp",EDGE,"E4507"),sQuery(id+"F17.wireOp",EDGE,"E4508"),sQuery(id+"F17.wireOp",EDGE,"E4509"),sQuery(id+"F17.wireOp",EDGE,"E4510"),sQuery(id+"F17.wireOp",EDGE,"E4511"),sQuery(id+"F17.wireOp",EDGE,"E4512"),sQuery(id+"F17.wireOp",EDGE,"E4513"),sQuery(id+"F17.wireOp",EDGE,"E4514"),sQuery(id+"F17.wireOp",EDGE,"E4515"),sQuery(id+"F17.wireOp",EDGE,"E4516"),sQuery(id+"F17.wireOp",EDGE,"E4517"),sQuery(id+"F17.wireOp",EDGE,"E4518"),sQuery(id+"F17.wireOp",EDGE,"E4519"),sQuery(id+"F17.wireOp",EDGE,"E4520"),sQuery(id+"F17.wireOp",EDGE,"E4521"),sQuery(id+"F17.wireOp",EDGE,"E4522"),sQuery(id+"F17.wireOp",EDGE,"E4523"),sQuery(id+"F17.wireOp",EDGE,"E4524"),sQuery(id+"F17.wireOp",EDGE,"E4525"),sQuery(id+"F17.wireOp",EDGE,"E4526"),sQuery(id+"F17.wireOp",EDGE,"E4527"),sQuery(id+"F17.wireOp",EDGE,"E4528"),sQuery(id+"F17.wireOp",EDGE,"E4529"),sQuery(id+"F17.wireOp",EDGE,"E4530"),sQuery(id+"F17.wireOp",EDGE,"E4531"),sQuery(id+"F17.wireOp",EDGE,"E4532"),sQuery(id+"F17.wireOp",EDGE,"E4533"),sQuery(id+"F17.wireOp",EDGE,"E4534"),sQuery(id+"F17.wireOp",EDGE,"E4535"),sQuery(id+"F17.wireOp",EDGE,"E4536"),sQuery(id+"F17.wireOp",EDGE,"E4537"),sQuery(id+"F17.wireOp",EDGE,"E4538"),sQuery(id+"F17.wireOp",EDGE,"E4539"),sQuery(id+"F17.wireOp",EDGE,"E4540"),sQuery(id+"F17.wireOp",EDGE,"E4541"),sQuery(id+"F17.wireOp",EDGE,"E4542"),sQuery(id+"F17.wireOp",EDGE,"E4543"),sQuery(id+"F17.wireOp",EDGE,"E4544"),sQuery(id+"F17.wireOp",EDGE,"E4545"),sQuery(id+"F17.wireOp",EDGE,"E4546"),sQuery(id+"F17.wireOp",EDGE,"E4547"),sQuery(id+"F17.wireOp",EDGE,"E4548"),sQuery(id+"F17.wireOp",EDGE,"E4549"),sQuery(id+"F17.wireOp",EDGE,"E4550"),sQuery(id+"F17.wireOp",EDGE,"E4551"),sQuery(id+"F17.wireOp",EDGE,"E4552"),sQuery(id+"F17.wireOp",EDGE,"E4553"),sQuery(id+"F17.wireOp",EDGE,"E4554"),sQuery(id+"F17.wireOp",EDGE,"E4555"),sQuery(id+"F17.wireOp",EDGE,"E4556"),sQuery(id+"F17.wireOp",EDGE,"E4557"),sQuery(id+"F17.wireOp",EDGE,"E4558"),sQuery(id+"F17.wireOp",EDGE,"E4559"),sQuery(id+"F17.wireOp",EDGE,"E4560"),sQuery(id+"F17.wireOp",EDGE,"E4561"),sQuery(id+"F17.wireOp",EDGE,"E4562"),sQuery(id+"F17.wireOp",EDGE,"E4563"),sQuery(id+"F17.wireOp",EDGE,"E4564"),sQuery(id+"F17.wireOp",EDGE,"E4565"),sQuery(id+"F17.wireOp",EDGE,"E4566"),sQuery(id+"F17.wireOp",EDGE,"E4567"),sQuery(id+"F17.wireOp",EDGE,"E4568"),sQuery(id+"F17.wireOp",EDGE,"E4569"),sQuery(id+"F17.wireOp",EDGE,"E4570"),sQuery(id+"F17.wireOp",EDGE,"E4571"),sQuery(id+"F17.wireOp",EDGE,"E4572"),sQuery(id+"F17.wireOp",EDGE,"E4573"),sQuery(id+"F17.wireOp",EDGE,"E4574"),sQuery(id+"F17.wireOp",EDGE,"E4575"),sQuery(id+"F17.wireOp",EDGE,"E4576"),sQuery(id+"F17.wireOp",EDGE,"E4577"),sQuery(id+"F17.wireOp",EDGE,"E4578"),sQuery(id+"F17.wireOp",EDGE,"E4579"),sQuery(id+"F17.wireOp",EDGE,"E4580"),sQuery(id+"F17.wireOp",EDGE,"E4581"),sQuery(id+"F17.wireOp",EDGE,"E4582"),sQuery(id+"F17.wireOp",EDGE,"E4583"),sQuery(id+"F17.wireOp",EDGE,"E4584"),sQuery(id+"F17.wireOp",EDGE,"E4585"),sQuery(id+"F17.wireOp",EDGE,"E4586"),sQuery(id+"F17.wireOp",EDGE,"E4587"),sQuery(id+"F17.wireOp",EDGE,"E4588"),sQuery(id+"F17.wireOp",EDGE,"E4589"),sQuery(id+"F17.wireOp",EDGE,"E4590"),sQuery(id+"F17.wireOp",EDGE,"E4591"),sQuery(id+"F17.wireOp",EDGE,"E4592"),sQuery(id+"F17.wireOp",EDGE,"E4593"),sQuery(id+"F17.wireOp",EDGE,"E4594"),sQuery(id+"F17.wireOp",EDGE,"E4595"),sQuery(id+"F17.wireOp",EDGE,"E4596"),sQuery(id+"F17.wireOp",EDGE,"E4597"),sQuery(id+"F17.wireOp",EDGE,"E4598"),sQuery(id+"F17.wireOp",EDGE,"E4599"),sQuery(id+"F17.wireOp",EDGE,"E4600"),sQuery(id+"F17.wireOp",EDGE,"E4601"),sQuery(id+"F17.wireOp",EDGE,"E4602"),sQuery(id+"F17.wireOp",EDGE,"E4603"),sQuery(id+"F17.wireOp",EDGE,"E4604"),sQuery(id+"F17.wireOp",EDGE,"E4605"),sQuery(id+"F17.wireOp",EDGE,"E4606"),sQuery(id+"F17.wireOp",EDGE,"E4607"),sQuery(id+"F17.wireOp",EDGE,"E4608"),sQuery(id+"F17.wireOp",EDGE,"E4609"),sQuery(id+"F17.wireOp",EDGE,"E4610"),sQuery(id+"F17.wireOp",EDGE,"E4611"),sQuery(id+"F17.wireOp",EDGE,"E4612"),sQuery(id+"F17.wireOp",EDGE,"E4613"),sQuery(id+"F17.wireOp",EDGE,"E4614"),sQuery(id+"F17.wireOp",EDGE,"E4615"),sQuery(id+"F17.wireOp",EDGE,"E4616"),sQuery(id+"F17.wireOp",EDGE,"E4617"),sQuery(id+"F17.wireOp",EDGE,"E4618"),sQuery(id+"F17.wireOp",EDGE,"E4619"),sQuery(id+"F17.wireOp",EDGE,"E4620"),sQuery(id+"F17.wireOp",EDGE,"E4621"),sQuery(id+"F17.wireOp",EDGE,"E4622"),sQuery(id+"F17.wireOp",EDGE,"E4623"),sQuery(id+"F17.wireOp",EDGE,"E4624"),sQuery(id+"F17.wireOp",EDGE,"E4625"),sQuery(id+"F17.wireOp",EDGE,"E4626"),sQuery(id+"F17.wireOp",EDGE,"E4627"),sQuery(id+"F17.wireOp",EDGE,"E4628"),sQuery(id+"F17.wireOp",EDGE,"E4629"),sQuery(id+"F17.wireOp",EDGE,"E4630"),sQuery(id+"F17.wireOp",EDGE,"E4631"),sQuery(id+"F17.wireOp",EDGE,"E4632"),sQuery(id+"F17.wireOp",EDGE,"E4633"),sQuery(id+"F17.wireOp",EDGE,"E4634"),sQuery(id+"F17.wireOp",EDGE,"E4635"),sQuery(id+"F17.wireOp",EDGE,"E4636"),sQuery(id+"F17.wireOp",EDGE,"E4637"),sQuery(id+"F17.wireOp",EDGE,"E4638"),sQuery(id+"F17.wireOp",EDGE,"E4639"),sQuery(id+"F17.wireOp",EDGE,"E4640"),sQuery(id+"F17.wireOp",EDGE,"E4641"),sQuery(id+"F17.wireOp",EDGE,"E4642"),sQuery(id+"F17.wireOp",EDGE,"E4643"),sQuery(id+"F17.wireOp",EDGE,"E4644"),sQuery(id+"F17.wireOp",EDGE,"E4645"),sQuery(id+"F17.wireOp",EDGE,"E4646"),sQuery(id+"F17.wireOp",EDGE,"E4647"),sQuery(id+"F17.wireOp",EDGE,"E4648"),sQuery(id+"F17.wireOp",EDGE,"E4649"),sQuery(id+"F17.wireOp",EDGE,"E4650"),sQuery(id+"F17.wireOp",EDGE,"E4651"),sQuery(id+"F17.wireOp",EDGE,"E4652"),sQuery(id+"F17.wireOp",EDGE,"E4653"),sQuery(id+"F17.wireOp",EDGE,"E4654"),sQuery(id+"F17.wireOp",EDGE,"E4655"),sQuery(id+"F17.wireOp",EDGE,"E4656"),sQuery(id+"F17.wireOp",EDGE,"E4657"),sQuery(id+"F17.wireOp",EDGE,"E4658"),sQuery(id+"F17.wireOp",EDGE,"E4659"),sQuery(id+"F17.wireOp",EDGE,"E4660"),sQuery(id+"F17.wireOp",EDGE,"E4661"),sQuery(id+"F17.wireOp",EDGE,"E4662"),sQuery(id+"F17.wireOp",EDGE,"E4663"),sQuery(id+"F17.wireOp",EDGE,"E4664"),sQuery(id+"F17.wireOp",EDGE,"E4665"),sQuery(id+"F17.wireOp",EDGE,"E4666"),sQuery(id+"F17.wireOp",EDGE,"E4667"),sQuery(id+"F17.wireOp",EDGE,"E4668"),sQuery(id+"F17.wireOp",EDGE,"E4669"),sQuery(id+"F17.wireOp",EDGE,"E4670"),sQuery(id+"F17.wireOp",EDGE,"E4671"),sQuery(id+"F17.wireOp",EDGE,"E4672"),sQuery(id+"F17.wireOp",EDGE,"E4673"),sQuery(id+"F17.wireOp",EDGE,"E4674"),sQuery(id+"F17.wireOp",EDGE,"E4675"),sQuery(id+"F17.wireOp",EDGE,"E4676"),sQuery(id+"F17.wireOp",EDGE,"E4677"),sQuery(id+"F17.wireOp",EDGE,"E4678"),sQuery(id+"F17.wireOp",EDGE,"E4679"),sQuery(id+"F17.wireOp",EDGE,"E4680"),sQuery(id+"F17.wireOp",EDGE,"E4681"),sQuery(id+"F17.wireOp",EDGE,"E4682"),sQuery(id+"F17.wireOp",EDGE,"E4683"),sQuery(id+"F17.wireOp",EDGE,"E4684"),sQuery(id+"F17.wireOp",EDGE,"E4685"),sQuery(id+"F17.wireOp",EDGE,"E4686"),sQuery(id+"F17.wireOp",EDGE,"E4687"),sQuery(id+"F17.wireOp",EDGE,"E4688"),sQuery(id+"F17.wireOp",EDGE,"E4689"),sQuery(id+"F17.wireOp",EDGE,"E4690"),sQuery(id+"F17.wireOp",EDGE,"E4691"),sQuery(id+"F17.wireOp",EDGE,"E4692"),sQuery(id+"F17.wireOp",EDGE,"E4693"),sQuery(id+"F17.wireOp",EDGE,"E4694"),sQuery(id+"F17.wireOp",EDGE,"E4695"),sQuery(id+"F17.wireOp",EDGE,"E4696"),sQuery(id+"F17.wireOp",EDGE,"E4697"),sQuery(id+"F17.wireOp",EDGE,"E4698"),sQuery(id+"F17.wireOp",EDGE,"E4699"),sQuery(id+"F17.wireOp",EDGE,"E4700"),sQuery(id+"F17.wireOp",EDGE,"E4701"),sQuery(id+"F17.wireOp",EDGE,"E4702"),sQuery(id+"F17.wireOp",EDGE,"E4703"),sQuery(id+"F17.wireOp",EDGE,"E4704"),sQuery(id+"F17.wireOp",EDGE,"E4705"),sQuery(id+"F17.wireOp",EDGE,"E4706"),sQuery(id+"F17.wireOp",EDGE,"E4707"),sQuery(id+"F17.wireOp",EDGE,"E4708"),sQuery(id+"F17.wireOp",EDGE,"E4709"),sQuery(id+"F17.wireOp",EDGE,"E4710"),sQuery(id+"F17.wireOp",EDGE,"E4711"),sQuery(id+"F17.wireOp",EDGE,"E4712"),sQuery(id+"F17.wireOp",EDGE,"E4713"),sQuery(id+"F17.wireOp",EDGE,"E4714"),sQuery(id+"F17.wireOp",EDGE,"E4715"),sQuery(id+"F17.wireOp",EDGE,"E4716"),sQuery(id+"F17.wireOp",EDGE,"E4717"),sQuery(id+"F17.wireOp",EDGE,"E4718"),sQuery(id+"F17.wireOp",EDGE,"E4719"),sQuery(id+"F17.wireOp",EDGE,"E4720"),sQuery(id+"F17.wireOp",EDGE,"E4721"),sQuery(id+"F17.wireOp",EDGE,"E4722"),sQuery(id+"F17.wireOp",EDGE,"E4723"),sQuery(id+"F17.wireOp",EDGE,"E4724"),sQuery(id+"F17.wireOp",EDGE,"E4725"),sQuery(id+"F17.wireOp",EDGE,"E4726"),sQuery(id+"F17.wireOp",EDGE,"E4727"),sQuery(id+"F17.wireOp",EDGE,"E4728"),sQuery(id+"F17.wireOp",EDGE,"E4729"),sQuery(id+"F17.wireOp",EDGE,"E4730"),sQuery(id+"F17.wireOp",EDGE,"E4731"),sQuery(id+"F17.wireOp",EDGE,"E4732"),sQuery(id+"F17.wireOp",EDGE,"E4733"),sQuery(id+"F17.wireOp",EDGE,"E4734"),sQuery(id+"F17.wireOp",EDGE,"E4735"),sQuery(id+"F17.wireOp",EDGE,"E4736"),sQuery(id+"F17.wireOp",EDGE,"E4737"),sQuery(id+"F17.wireOp",EDGE,"E4738"),sQuery(id+"F17.wireOp",EDGE,"E4739"),sQuery(id+"F17.wireOp",EDGE,"E4740"),sQuery(id+"F17.wireOp",EDGE,"E4741"),sQuery(id+"F17.wireOp",EDGE,"E4742"),sQuery(id+"F17.wireOp",EDGE,"E4743"),sQuery(id+"F17.wireOp",EDGE,"E4744"),sQuery(id+"F17.wireOp",EDGE,"E4745"),sQuery(id+"F17.wireOp",EDGE,"E4746"),sQuery(id+"F17.wireOp",EDGE,"E4747"),sQuery(id+"F17.wireOp",EDGE,"E4748"),sQuery(id+"F17.wireOp",EDGE,"E4749"),sQuery(id+"F17.wireOp",EDGE,"E4750"),sQuery(id+"F17.wireOp",EDGE,"E4751"),sQuery(id+"F17.wireOp",EDGE,"E4752"),sQuery(id+"F17.wireOp",EDGE,"E4753"),sQuery(id+"F17.wireOp",EDGE,"E4754"),sQuery(id+"F17.wireOp",EDGE,"E4755"),sQuery(id+"F17.wireOp",EDGE,"E4756"),sQuery(id+"F17.wireOp",EDGE,"E4757"),sQuery(id+"F17.wireOp",EDGE,"E4758"),sQuery(id+"F17.wireOp",EDGE,"E4759"),sQuery(id+"F17.wireOp",EDGE,"E4760"),sQuery(id+"F17.wireOp",EDGE,"E4761"),sQuery(id+"F17.wireOp",EDGE,"E4762"),sQuery(id+"F17.wireOp",EDGE,"E4763"),sQuery(id+"F17.wireOp",EDGE,"E4764"),sQuery(id+"F17.wireOp",EDGE,"E4765"),sQuery(id+"F17.wireOp",EDGE,"E4766"),sQuery(id+"F17.wireOp",EDGE,"E4767"),sQuery(id+"F17.wireOp",EDGE,"E4768"),sQuery(id+"F17.wireOp",EDGE,"E4769"),sQuery(id+"F17.wireOp",EDGE,"E4770"),sQuery(id+"F17.wireOp",EDGE,"E4771"),sQuery(id+"F17.wireOp",EDGE,"E4772"),sQuery(id+"F17.wireOp",EDGE,"E4773"),sQuery(id+"F17.wireOp",EDGE,"E4774"),sQuery(id+"F17.wireOp",EDGE,"E4775"),sQuery(id+"F17.wireOp",EDGE,"E4776"),sQuery(id+"F17.wireOp",EDGE,"E4777"),sQuery(id+"F17.wireOp",EDGE,"E4778"),sQuery(id+"F17.wireOp",EDGE,"E4779"),sQuery(id+"F17.wireOp",EDGE,"E4780"),sQuery(id+"F17.wireOp",EDGE,"E4781"),sQuery(id+"F17.wireOp",EDGE,"E4782"),sQuery(id+"F17.wireOp",EDGE,"E4783"),sQuery(id+"F17.wireOp",EDGE,"E4784"),sQuery(id+"F17.wireOp",EDGE,"E4785"),sQuery(id+"F17.wireOp",EDGE,"E4786"),sQuery(id+"F17.wireOp",EDGE,"E4787"),sQuery(id+"F17.wireOp",EDGE,"E4788"),sQuery(id+"F17.wireOp",EDGE,"E4789"),sQuery(id+"F17.wireOp",EDGE,"E4790"),sQuery(id+"F17.wireOp",EDGE,"E4791"),sQuery(id+"F17.wireOp",EDGE,"E4792"),sQuery(id+"F17.wireOp",EDGE,"E4793"),sQuery(id+"F17.wireOp",EDGE,"E4794"),sQuery(id+"F17.wireOp",EDGE,"E4795"),sQuery(id+"F17.wireOp",EDGE,"E4796"),sQuery(id+"F17.wireOp",EDGE,"E4797"),sQuery(id+"F17.wireOp",EDGE,"E4798"),sQuery(id+"F17.wireOp",EDGE,"E4799"),sQuery(id+"F17.wireOp",EDGE,"E4800"),sQuery(id+"F17.wireOp",EDGE,"E4801"),sQuery(id+"F17.wireOp",EDGE,"E4802"),sQuery(id+"F17.wireOp",EDGE,"E4803"),sQuery(id+"F17.wireOp",EDGE,"E4804"),sQuery(id+"F17.wireOp",EDGE,"E4805"),sQuery(id+"F17.wireOp",EDGE,"E4806"),sQuery(id+"F17.wireOp",EDGE,"E4807"),sQuery(id+"F17.wireOp",EDGE,"E4808"),sQuery(id+"F17.wireOp",EDGE,"E4809"),sQuery(id+"F17.wireOp",EDGE,"E4810"),sQuery(id+"F17.wireOp",EDGE,"E4811"),sQuery(id+"F17.wireOp",EDGE,"E4812"),sQuery(id+"F17.wireOp",EDGE,"E4813"),sQuery(id+"F17.wireOp",EDGE,"E4814"),sQuery(id+"F17.wireOp",EDGE,"E4815"),sQuery(id+"F17.wireOp",EDGE,"E4816"),sQuery(id+"F17.wireOp",EDGE,"E4817"),sQuery(id+"F17.wireOp",EDGE,"E4818"),sQuery(id+"F17.wireOp",EDGE,"E4819"),sQuery(id+"F17.wireOp",EDGE,"E4820"),sQuery(id+"F17.wireOp",EDGE,"E4821"),sQuery(id+"F17.wireOp",EDGE,"E4822"),sQuery(id+"F17.wireOp",EDGE,"E4823"),sQuery(id+"F17.wireOp",EDGE,"E4824"),sQuery(id+"F17.wireOp",EDGE,"E4825"),sQuery(id+"F17.wireOp",EDGE,"E4826"),sQuery(id+"F17.wireOp",EDGE,"E4827"),sQuery(id+"F17.wireOp",EDGE,"E4828"),sQuery(id+"F17.wireOp",EDGE,"E4829"),sQuery(id+"F17.wireOp",EDGE,"E4830"),sQuery(id+"F17.wireOp",EDGE,"E4831"),sQuery(id+"F17.wireOp",EDGE,"E4832"),sQuery(id+"F17.wireOp",EDGE,"E4833"),sQuery(id+"F17.wireOp",EDGE,"E4834"),sQuery(id+"F17.wireOp",EDGE,"E4835"),sQuery(id+"F17.wireOp",EDGE,"E4836"),sQuery(id+"F17.wireOp",EDGE,"E4837"),sQuery(id+"F17.wireOp",EDGE,"E4838"),sQuery(id+"F17.wireOp",EDGE,"E4839"),sQuery(id+"F17.wireOp",EDGE,"E4840"),sQuery(id+"F17.wireOp",EDGE,"E4841"),sQuery(id+"F17.wireOp",EDGE,"E4842"),sQuery(id+"F17.wireOp",EDGE,"E4843"),sQuery(id+"F17.wireOp",EDGE,"E4844"),sQuery(id+"F17.wireOp",EDGE,"E4845"),sQuery(id+"F17.wireOp",EDGE,"E4846"),sQuery(id+"F17.wireOp",EDGE,"E4847"),sQuery(id+"F17.wireOp",EDGE,"E4848"),sQuery(id+"F17.wireOp",EDGE,"E4849"),sQuery(id+"F17.wireOp",EDGE,"E4850"),sQuery(id+"F17.wireOp",EDGE,"E4851"),sQuery(id+"F17.wireOp",EDGE,"E4852"),sQuery(id+"F17.wireOp",EDGE,"E4853"),sQuery(id+"F17.wireOp",EDGE,"E4854"),sQuery(id+"F17.wireOp",EDGE,"E4855"),sQuery(id+"F17.wireOp",EDGE,"E4856"),sQuery(id+"F17.wireOp",EDGE,"E4857"),sQuery(id+"F17.wireOp",EDGE,"E4858"),sQuery(id+"F17.wireOp",EDGE,"E4859"),sQuery(id+"F17.wireOp",EDGE,"E4860"),sQuery(id+"F17.wireOp",EDGE,"E4861"),sQuery(id+"F17.wireOp",EDGE,"E4862"),sQuery(id+"F17.wireOp",EDGE,"E4863"),sQuery(id+"F17.wireOp",EDGE,"E4864"),sQuery(id+"F17.wireOp",EDGE,"E4865"),sQuery(id+"F17.wireOp",EDGE,"E4866"),sQuery(id+"F17.wireOp",EDGE,"E4867"),sQuery(id+"F17.wireOp",EDGE,"E4868"),sQuery(id+"F17.wireOp",EDGE,"E4869"),sQuery(id+"F17.wireOp",EDGE,"E4870"),sQuery(id+"F17.wireOp",EDGE,"E4871"),sQuery(id+"F17.wireOp",EDGE,"E4872"),sQuery(id+"F17.wireOp",EDGE,"E4873"),sQuery(id+"F17.wireOp",EDGE,"E4874"),sQuery(id+"F17.wireOp",EDGE,"E4875"),sQuery(id+"F17.wireOp",EDGE,"E4876"),sQuery(id+"F17.wireOp",EDGE,"E4877"),sQuery(id+"F17.wireOp",EDGE,"E4878"),sQuery(id+"F17.wireOp",EDGE,"E4879"),sQuery(id+"F17.wireOp",EDGE,"E4880"),sQuery(id+"F17.wireOp",EDGE,"E4881"),sQuery(id+"F17.wireOp",EDGE,"E4882"),sQuery(id+"F17.wireOp",EDGE,"E4883"),sQuery(id+"F17.wireOp",EDGE,"E4884"),sQuery(id+"F17.wireOp",EDGE,"E4885"),sQuery(id+"F17.wireOp",EDGE,"E4886"),sQuery(id+"F17.wireOp",EDGE,"E4887"),sQuery(id+"F17.wireOp",EDGE,"E4888"),sQuery(id+"F17.wireOp",EDGE,"E4889"),sQuery(id+"F17.wireOp",EDGE,"E4890"),sQuery(id+"F17.wireOp",EDGE,"E4891"),sQuery(id+"F17.wireOp",EDGE,"E4892"),sQuery(id+"F17.wireOp",EDGE,"E4893"),sQuery(id+"F17.wireOp",EDGE,"E4894"),sQuery(id+"F17.wireOp",EDGE,"E4895"),sQuery(id+"F17.wireOp",EDGE,"E4896"),sQuery(id+"F17.wireOp",EDGE,"E4897"),sQuery(id+"F17.wireOp",EDGE,"E4898"),sQuery(id+"F17.wireOp",EDGE,"E4899"),sQuery(id+"F17.wireOp",EDGE,"E4900"),sQuery(id+"F17.wireOp",EDGE,"E4901"),sQuery(id+"F17.wireOp",EDGE,"E4902"),sQuery(id+"F17.wireOp",EDGE,"E4903"),sQuery(id+"F17.wireOp",EDGE,"E4904"),sQuery(id+"F17.wireOp",EDGE,"E4905"),sQuery(id+"F17.wireOp",EDGE,"E4906"),sQuery(id+"F17.wireOp",EDGE,"E4907"),sQuery(id+"F17.wireOp",EDGE,"E4908"),sQuery(id+"F17.wireOp",EDGE,"E4909"),sQuery(id+"F17.wireOp",EDGE,"E4910"),sQuery(id+"F17.wireOp",EDGE,"E4911"),sQuery(id+"F17.wireOp",EDGE,"E4912"),sQuery(id+"F17.wireOp",EDGE,"E4913"),sQuery(id+"F17.wireOp",EDGE,"E4914"),sQuery(id+"F17.wireOp",EDGE,"E4915"),sQuery(id+"F17.wireOp",EDGE,"E4916"),sQuery(id+"F17.wireOp",EDGE,"E4917"),sQuery(id+"F17.wireOp",EDGE,"E4918"),sQuery(id+"F17.wireOp",EDGE,"E4919"),sQuery(id+"F17.wireOp",EDGE,"E4920"),sQuery(id+"F17.wireOp",EDGE,"E4921"),sQuery(id+"F17.wireOp",EDGE,"E4922"),sQuery(id+"F17.wireOp",EDGE,"E4923"),sQuery(id+"F17.wireOp",EDGE,"E4924"),sQuery(id+"F17.wireOp",EDGE,"E4925"),sQuery(id+"F17.wireOp",EDGE,"E4926"),sQuery(id+"F17.wireOp",EDGE,"E4927"),sQuery(id+"F17.wireOp",EDGE,"E4928"),sQuery(id+"F17.wireOp",EDGE,"E4929"),sQuery(id+"F17.wireOp",EDGE,"E4930"),sQuery(id+"F17.wireOp",EDGE,"E4931"),sQuery(id+"F17.wireOp",EDGE,"E4932"),sQuery(id+"F17.wireOp",EDGE,"E4933"),sQuery(id+"F17.wireOp",EDGE,"E4934"),sQuery(id+"F17.wireOp",EDGE,"E4935"),sQuery(id+"F17.wireOp",EDGE,"E4936"),sQuery(id+"F17.wireOp",EDGE,"E4937"),sQuery(id+"F17.wireOp",EDGE,"E4938"),sQuery(id+"F17.wireOp",EDGE,"E4939"),sQuery(id+"F17.wireOp",EDGE,"E4940"),sQuery(id+"F17.wireOp",EDGE,"E4941"),sQuery(id+"F17.wireOp",EDGE,"E4942"),sQuery(id+"F17.wireOp",EDGE,"E4943"),sQuery(id+"F17.wireOp",EDGE,"E4944"),sQuery(id+"F17.wireOp",EDGE,"E4945"),sQuery(id+"F17.wireOp",EDGE,"E4946"),sQuery(id+"F17.wireOp",EDGE,"E4947"),sQuery(id+"F17.wireOp",EDGE,"E4948"),sQuery(id+"F17.wireOp",EDGE,"E4949"),sQuery(id+"F17.wireOp",EDGE,"E4950"),sQuery(id+"F17.wireOp",EDGE,"E4951"),sQuery(id+"F17.wireOp",EDGE,"E4952"),sQuery(id+"F17.wireOp",EDGE,"E4953"),sQuery(id+"F17.wireOp",EDGE,"E4954"),sQuery(id+"F17.wireOp",EDGE,"E4955"),sQuery(id+"F17.wireOp",EDGE,"E4956"),sQuery(id+"F17.wireOp",EDGE,"E4957"),sQuery(id+"F17.wireOp",EDGE,"E4958"),sQuery(id+"F17.wireOp",EDGE,"E4959"),sQuery(id+"F17.wireOp",EDGE,"E4960"),sQuery(id+"F17.wireOp",EDGE,"E4961"),sQuery(id+"F17.wireOp",EDGE,"E4962"),sQuery(id+"F17.wireOp",EDGE,"E4963"),sQuery(id+"F17.wireOp",EDGE,"E4964"),sQuery(id+"F17.wireOp",EDGE,"E4965"),sQuery(id+"F17.wireOp",EDGE,"E4966"),sQuery(id+"F17.wireOp",EDGE,"E4967"),sQuery(id+"F17.wireOp",EDGE,"E4968"),sQuery(id+"F17.wireOp",EDGE,"E4969"),sQuery(id+"F17.wireOp",EDGE,"E4970"),sQuery(id+"F17.wireOp",EDGE,"E4971"),sQuery(id+"F17.wireOp",EDGE,"E4972"),sQuery(id+"F17.wireOp",EDGE,"E4973"),sQuery(id+"F17.wireOp",EDGE,"E4974"),sQuery(id+"F17.wireOp",EDGE,"E4975"),sQuery(id+"F17.wireOp",EDGE,"E4976"),sQuery(id+"F17.wireOp",EDGE,"E4977"),sQuery(id+"F17.wireOp",EDGE,"E4978"),sQuery(id+"F17.wireOp",EDGE,"E4979"),sQuery(id+"F17.wireOp",EDGE,"E4980"),sQuery(id+"F17.wireOp",EDGE,"E4981"),sQuery(id+"F17.wireOp",EDGE,"E4982"),sQuery(id+"F17.wireOp",EDGE,"E4983"),sQuery(id+"F17.wireOp",EDGE,"E4984"),sQuery(id+"F17.wireOp",EDGE,"E4985"),sQuery(id+"F17.wireOp",EDGE,"E4986"),sQuery(id+"F17.wireOp",EDGE,"E4987"),sQuery(id+"F17.wireOp",EDGE,"E4988"),sQuery(id+"F17.wireOp",EDGE,"E4989"),sQuery(id+"F17.wireOp",EDGE,"E4990"),sQuery(id+"F17.wireOp",EDGE,"E4991"),sQuery(id+"F17.wireOp",EDGE,"E4992"),sQuery(id+"F17.wireOp",EDGE,"E4993"),sQuery(id+"F17.wireOp",EDGE,"E4994"),sQuery(id+"F17.wireOp",EDGE,"E4995"),sQuery(id+"F17.wireOp",EDGE,"E4996"),sQuery(id+"F17.wireOp",EDGE,"E4997"),sQuery(id+"F17.wireOp",EDGE,"E4998"),sQuery(id+"F17.wireOp",EDGE,"E4999"),sQuery(id+"F17.wireOp",EDGE,"E5000"),sQuery(id+"F17.wireOp",EDGE,"E5001"),sQuery(id+"F17.wireOp",EDGE,"E5002"),sQuery(id+"F17.wireOp",EDGE,"E5003"),sQuery(id+"F17.wireOp",EDGE,"E5004"),sQuery(id+"F17.wireOp",EDGE,"E5005"),sQuery(id+"F17.wireOp",EDGE,"E5006"),sQuery(id+"F17.wireOp",EDGE,"E5007"),sQuery(id+"F17.wireOp",EDGE,"E5008"),sQuery(id+"F17.wireOp",EDGE,"E5009"),sQuery(id+"F17.wireOp",EDGE,"E5010"),sQuery(id+"F17.wireOp",EDGE,"E5011"),sQuery(id+"F17.wireOp",EDGE,"E5012"),sQuery(id+"F17.wireOp",EDGE,"E5013"),sQuery(id+"F17.wireOp",EDGE,"E5014"),sQuery(id+"F17.wireOp",EDGE,"E5015"),sQuery(id+"F17.wireOp",EDGE,"E5016"),sQuery(id+"F17.wireOp",EDGE,"E5017"),sQuery(id+"F17.wireOp",EDGE,"E5018"),sQuery(id+"F17.wireOp",EDGE,"E5019"),sQuery(id+"F17.wireOp",EDGE,"E5020"),sQuery(id+"F17.wireOp",EDGE,"E5021"),sQuery(id+"F17.wireOp",EDGE,"E5022"),sQuery(id+"F17.wireOp",EDGE,"E5023"),sQuery(id+"F17.wireOp",EDGE,"E5024"),sQuery(id+"F17.wireOp",EDGE,"E5025"),sQuery(id+"F17.wireOp",EDGE,"E5026"),sQuery(id+"F17.wireOp",EDGE,"E5027"),sQuery(id+"F17.wireOp",EDGE,"E5028"),sQuery(id+"F17.wireOp",EDGE,"E5029"),sQuery(id+"F17.wireOp",EDGE,"E5030"),sQuery(id+"F17.wireOp",EDGE,"E5031"),sQuery(id+"F17.wireOp",EDGE,"E5032"),sQuery(id+"F17.wireOp",EDGE,"E5033"),sQuery(id+"F17.wireOp",EDGE,"E5034"),sQuery(id+"F17.wireOp",EDGE,"E5035"),sQuery(id+"F17.wireOp",EDGE,"E5036"),sQuery(id+"F17.wireOp",EDGE,"E5037"),sQuery(id+"F17.wireOp",EDGE,"E5038"),sQuery(id+"F17.wireOp",EDGE,"E5039"),sQuery(id+"F17.wireOp",EDGE,"E5040"),sQuery(id+"F17.wireOp",EDGE,"E5041"),sQuery(id+"F17.wireOp",EDGE,"E5042"),sQuery(id+"F17.wireOp",EDGE,"E5043"),sQuery(id+"F17.wireOp",EDGE,"E5044"),sQuery(id+"F17.wireOp",EDGE,"E5045"),sQuery(id+"F17.wireOp",EDGE,"E5046"),sQuery(id+"F17.wireOp",EDGE,"E5047"),sQuery(id+"F17.wireOp",EDGE,"E5048"),sQuery(id+"F17.wireOp",EDGE,"E5049"),sQuery(id+"F17.wireOp",EDGE,"E5050"),sQuery(id+"F17.wireOp",EDGE,"E5051"),sQuery(id+"F17.wireOp",EDGE,"E5052"),sQuery(id+"F17.wireOp",EDGE,"E5053"),sQuery(id+"F17.wireOp",EDGE,"E5054"),sQuery(id+"F17.wireOp",EDGE,"E5055"),sQuery(id+"F17.wireOp",EDGE,"E5056"),sQuery(id+"F17.wireOp",EDGE,"E5057"),sQuery(id+"F17.wireOp",EDGE,"E5058"),sQuery(id+"F17.wireOp",EDGE,"E5059"),sQuery(id+"F17.wireOp",EDGE,"E5060"),sQuery(id+"F17.wireOp",EDGE,"E5061"),sQuery(id+"F17.wireOp",EDGE,"E5062"),sQuery(id+"F17.wireOp",EDGE,"E5063"),sQuery(id+"F17.wireOp",EDGE,"E5064"),sQuery(id+"F17.wireOp",EDGE,"E5065"),sQuery(id+"F17.wireOp",EDGE,"E5066"),sQuery(id+"F17.wireOp",EDGE,"E5067"),sQuery(id+"F17.wireOp",EDGE,"E5068"),sQuery(id+"F17.wireOp",EDGE,"E5069"),sQuery(id+"F17.wireOp",EDGE,"E5070"),sQuery(id+"F17.wireOp",EDGE,"E5071"),sQuery(id+"F17.wireOp",EDGE,"E5072"),sQuery(id+"F17.wireOp",EDGE,"E5073"),sQuery(id+"F17.wireOp",EDGE,"E5074"),sQuery(id+"F17.wireOp",EDGE,"E5075"),sQuery(id+"F17.wireOp",EDGE,"E5076"),sQuery(id+"F17.wireOp",EDGE,"E5077"),sQuery(id+"F17.wireOp",EDGE,"E5078"),sQuery(id+"F17.wireOp",EDGE,"E5079"),sQuery(id+"F17.wireOp",EDGE,"E5080"),sQuery(id+"F17.wireOp",EDGE,"E5081"),sQuery(id+"F17.wireOp",EDGE,"E5082"),sQuery(id+"F17.wireOp",EDGE,"E5083"),sQuery(id+"F17.wireOp",EDGE,"E5084"),sQuery(id+"F17.wireOp",EDGE,"E5085"),sQuery(id+"F17.wireOp",EDGE,"E5086"),sQuery(id+"F17.wireOp",EDGE,"E5087"),sQuery(id+"F17.wireOp",EDGE,"E5088"),sQuery(id+"F17.wireOp",EDGE,"E5089"),sQuery(id+"F17.wireOp",EDGE,"E5090"),sQuery(id+"F17.wireOp",EDGE,"E5091"),sQuery(id+"F17.wireOp",EDGE,"E5092"),sQuery(id+"F17.wireOp",EDGE,"E5093"),sQuery(id+"F17.wireOp",EDGE,"E5094"),sQuery(id+"F17.wireOp",EDGE,"E5095"),sQuery(id+"F17.wireOp",EDGE,"E5096"),sQuery(id+"F17.wireOp",EDGE,"E5097"),sQuery(id+"F17.wireOp",EDGE,"E5098"),sQuery(id+"F17.wireOp",EDGE,"E5099"),sQuery(id+"F17.wireOp",EDGE,"E5100"),sQuery(id+"F17.wireOp",EDGE,"E5101"),sQuery(id+"F17.wireOp",EDGE,"E5102"),sQuery(id+"F17.wireOp",EDGE,"E5103"),sQuery(id+"F17.wireOp",EDGE,"E5104"),sQuery(id+"F17.wireOp",EDGE,"E5105"),sQuery(id+"F17.wireOp",EDGE,"E5106"),sQuery(id+"F17.wireOp",EDGE,"E5107"),sQuery(id+"F17.wireOp",EDGE,"E5108"),sQuery(id+"F17.wireOp",EDGE,"E5109"),sQuery(id+"F17.wireOp",EDGE,"E5110"),sQuery(id+"F17.wireOp",EDGE,"E5111"),sQuery(id+"F17.wireOp",EDGE,"E5112"),sQuery(id+"F17.wireOp",EDGE,"E5113"),sQuery(id+"F17.wireOp",EDGE,"E5114"),sQuery(id+"F17.wireOp",EDGE,"E5115"),sQuery(id+"F17.wireOp",EDGE,"E5116"),sQuery(id+"F17.wireOp",EDGE,"E5117"),sQuery(id+"F17.wireOp",EDGE,"E5118"),sQuery(id+"F17.wireOp",EDGE,"E5119"),sQuery(id+"F17.wireOp",EDGE,"E5120"),sQuery(id+"F17.wireOp",EDGE,"E5121"),sQuery(id+"F17.wireOp",EDGE,"E5122"),sQuery(id+"F17.wireOp",EDGE,"E5123"),sQuery(id+"F17.wireOp",EDGE,"E5124"),sQuery(id+"F17.wireOp",EDGE,"E5125"),sQuery(id+"F17.wireOp",EDGE,"E5126"),sQuery(id+"F17.wireOp",EDGE,"E5127"),sQuery(id+"F17.wireOp",EDGE,"E5128"),sQuery(id+"F17.wireOp",EDGE,"E5129"),sQuery(id+"F17.wireOp",EDGE,"E5130"),sQuery(id+"F17.wireOp",EDGE,"E5131"),sQuery(id+"F17.wireOp",EDGE,"E5132"),sQuery(id+"F17.wireOp",EDGE,"E5133"),sQuery(id+"F17.wireOp",EDGE,"E5134"),sQuery(id+"F17.wireOp",EDGE,"E5135"),sQuery(id+"F17.wireOp",EDGE,"E5136"),sQuery(id+"F17.wireOp",EDGE,"E5137"),sQuery(id+"F17.wireOp",EDGE,"E5138"),sQuery(id+"F17.wireOp",EDGE,"E5139"),sQuery(id+"F17.wireOp",EDGE,"E5140"),sQuery(id+"F17.wireOp",EDGE,"E5141"),sQuery(id+"F17.wireOp",EDGE,"E5142"),sQuery(id+"F17.wireOp",EDGE,"E5143"),sQuery(id+"F17.wireOp",EDGE,"E5144"),sQuery(id+"F17.wireOp",EDGE,"E5145"),sQuery(id+"F17.wireOp",EDGE,"E5146"),sQuery(id+"F17.wireOp",EDGE,"E5147"),sQuery(id+"F17.wireOp",EDGE,"E5148"),sQuery(id+"F17.wireOp",EDGE,"E5149"),sQuery(id+"F17.wireOp",EDGE,"E5150"),sQuery(id+"F17.wireOp",EDGE,"E5151"),sQuery(id+"F17.wireOp",EDGE,"E5152"),sQuery(id+"F17.wireOp",EDGE,"E5153"),sQuery(id+"F17.wireOp",EDGE,"E5154"),sQuery(id+"F17.wireOp",EDGE,"E5155"),sQuery(id+"F17.wireOp",EDGE,"E5156"),sQuery(id+"F17.wireOp",EDGE,"E5157"),sQuery(id+"F17.wireOp",EDGE,"E5158"),sQuery(id+"F17.wireOp",EDGE,"E5159"),sQuery(id+"F17.wireOp",EDGE,"E5160"),sQuery(id+"F17.wireOp",EDGE,"E5161"),sQuery(id+"F17.wireOp",EDGE,"E5162"),sQuery(id+"F17.wireOp",EDGE,"E5163"),sQuery(id+"F17.wireOp",EDGE,"E5164"),sQuery(id+"F17.wireOp",EDGE,"E5165"),sQuery(id+"F17.wireOp",EDGE,"E5166"),sQuery(id+"F17.wireOp",EDGE,"E5167"),sQuery(id+"F17.wireOp",EDGE,"E5168"),sQuery(id+"F17.wireOp",EDGE,"E5169"),sQuery(id+"F17.wireOp",EDGE,"E5170"),sQuery(id+"F17.wireOp",EDGE,"E5171"),sQuery(id+"F17.wireOp",EDGE,"E5172"),sQuery(id+"F17.wireOp",EDGE,"E5173"),sQuery(id+"F17.wireOp",EDGE,"E5174"),sQuery(id+"F17.wireOp",EDGE,"E5175"),sQuery(id+"F17.wireOp",EDGE,"E5176"),sQuery(id+"F17.wireOp",EDGE,"E5177"),sQuery(id+"F17.wireOp",EDGE,"E5178"),sQuery(id+"F17.wireOp",EDGE,"E5179"),sQuery(id+"F17.wireOp",EDGE,"E5180"),sQuery(id+"F17.wireOp",EDGE,"E5181"),sQuery(id+"F17.wireOp",EDGE,"E5182"),sQuery(id+"F17.wireOp",EDGE,"E5183"),sQuery(id+"F17.wireOp",EDGE,"E5184"),sQuery(id+"F17.wireOp",EDGE,"E5185"),sQuery(id+"F17.wireOp",EDGE,"E5186"),sQuery(id+"F17.wireOp",EDGE,"E5187"),sQuery(id+"F17.wireOp",EDGE,"E5188"),sQuery(id+"F17.wireOp",EDGE,"E5189"),sQuery(id+"F17.wireOp",EDGE,"E5190"),sQuery(id+"F17.wireOp",EDGE,"E5191"),sQuery(id+"F17.wireOp",EDGE,"E5192"),sQuery(id+"F17.wireOp",EDGE,"E5193"),sQuery(id+"F17.wireOp",EDGE,"E5194"),sQuery(id+"F17.wireOp",EDGE,"E5195"),sQuery(id+"F17.wireOp",EDGE,"E5196"),sQuery(id+"F17.wireOp",EDGE,"E5197"),sQuery(id+"F17.wireOp",EDGE,"E5198"),sQuery(id+"F17.wireOp",EDGE,"E5199"),sQuery(id+"F17.wireOp",EDGE,"E5200"),sQuery(id+"F17.wireOp",EDGE,"E5201"),sQuery(id+"F17.wireOp",EDGE,"E5202"),sQuery(id+"F17.wireOp",EDGE,"E5203"),sQuery(id+"F17.wireOp",EDGE,"E5204"),sQuery(id+"F17.wireOp",EDGE,"E5205"),sQuery(id+"F17.wireOp",EDGE,"E5206"),sQuery(id+"F17.wireOp",EDGE,"E5207"),sQuery(id+"F17.wireOp",EDGE,"E5208"),sQuery(id+"F17.wireOp",EDGE,"E5209"),sQuery(id+"F17.wireOp",EDGE,"E5210"),sQuery(id+"F17.wireOp",EDGE,"E5211"),sQuery(id+"F17.wireOp",EDGE,"E5212"),sQuery(id+"F17.wireOp",EDGE,"E5213"),sQuery(id+"F17.wireOp",EDGE,"E5214"),sQuery(id+"F17.wireOp",EDGE,"E5215"),sQuery(id+"F17.wireOp",EDGE,"E5216"),sQuery(id+"F17.wireOp",EDGE,"E5217"),sQuery(id+"F17.wireOp",EDGE,"E5218"),sQuery(id+"F17.wireOp",EDGE,"E5219"),sQuery(id+"F17.wireOp",EDGE,"E5220"),sQuery(id+"F17.wireOp",EDGE,"E5221"),sQuery(id+"F17.wireOp",EDGE,"E5222"),sQuery(id+"F17.wireOp",EDGE,"E5223"),sQuery(id+"F17.wireOp",EDGE,"E5224"),sQuery(id+"F17.wireOp",EDGE,"E5225"),sQuery(id+"F17.wireOp",EDGE,"E5226"),sQuery(id+"F17.wireOp",EDGE,"E5227"),sQuery(id+"F17.wireOp",EDGE,"E5228"),sQuery(id+"F17.wireOp",EDGE,"E5229"),sQuery(id+"F17.wireOp",EDGE,"E5230"),sQuery(id+"F17.wireOp",EDGE,"E5231"),sQuery(id+"F17.wireOp",EDGE,"E5232"),sQuery(id+"F17.wireOp",EDGE,"E5233"),sQuery(id+"F17.wireOp",EDGE,"E5234"),sQuery(id+"F17.wireOp",EDGE,"E5235"),sQuery(id+"F17.wireOp",EDGE,"E5236"),sQuery(id+"F17.wireOp",EDGE,"E5237"),sQuery(id+"F17.wireOp",EDGE,"E5238"),sQuery(id+"F17.wireOp",EDGE,"E5239"),sQuery(id+"F17.wireOp",EDGE,"E5240"),sQuery(id+"F17.wireOp",EDGE,"E5241"),sQuery(id+"F17.wireOp",EDGE,"E5242"),sQuery(id+"F17.wireOp",EDGE,"E5243"),sQuery(id+"F17.wireOp",EDGE,"E5244"),sQuery(id+"F17.wireOp",EDGE,"E5245"),sQuery(id+"F17.wireOp",EDGE,"E5246"),sQuery(id+"F17.wireOp",EDGE,"E5247"),sQuery(id+"F17.wireOp",EDGE,"E5248"),sQuery(id+"F17.wireOp",EDGE,"E5249"),sQuery(id+"F17.wireOp",EDGE,"E5250"),sQuery(id+"F17.wireOp",EDGE,"E5251"),sQuery(id+"F17.wireOp",EDGE,"E5252"),sQuery(id+"F17.wireOp",EDGE,"E5253"),sQuery(id+"F17.wireOp",EDGE,"E5254"),sQuery(id+"F17.wireOp",EDGE,"E5255"),sQuery(id+"F17.wireOp",EDGE,"E5256"),sQuery(id+"F17.wireOp",EDGE,"E5257"),sQuery(id+"F17.wireOp",EDGE,"E5258"),sQuery(id+"F17.wireOp",EDGE,"E5259"),sQuery(id+"F17.wireOp",EDGE,"E5260"),sQuery(id+"F17.wireOp",EDGE,"E5261"),sQuery(id+"F17.wireOp",EDGE,"E5262"),sQuery(id+"F17.wireOp",EDGE,"E5263"),sQuery(id+"F17.wireOp",EDGE,"E5264"),sQuery(id+"F17.wireOp",EDGE,"E5265"),sQuery(id+"F17.wireOp",EDGE,"E5266"),sQuery(id+"F17.wireOp",EDGE,"E5267"),sQuery(id+"F17.wireOp",EDGE,"E5268"),sQuery(id+"F17.wireOp",EDGE,"E5269"),sQuery(id+"F17.wireOp",EDGE,"E5270"),sQuery(id+"F17.wireOp",EDGE,"E5271"),sQuery(id+"F17.wireOp",EDGE,"E5272"),sQuery(id+"F17.wireOp",EDGE,"E5273"),sQuery(id+"F17.wireOp",EDGE,"E5274"),sQuery(id+"F17.wireOp",EDGE,"E5275"),sQuery(id+"F17.wireOp",EDGE,"E5276"),sQuery(id+"F17.wireOp",EDGE,"E5277"),sQuery(id+"F17.wireOp",EDGE,"E5278"),sQuery(id+"F17.wireOp",EDGE,"E5279"),sQuery(id+"F17.wireOp",EDGE,"E5280"),sQuery(id+"F17.wireOp",EDGE,"E5281"),sQuery(id+"F17.wireOp",EDGE,"E5282"),sQuery(id+"F17.wireOp",EDGE,"E5283"),sQuery(id+"F17.wireOp",EDGE,"E5284"),sQuery(id+"F17.wireOp",EDGE,"E5285"),sQuery(id+"F17.wireOp",EDGE,"E5286"),sQuery(id+"F17.wireOp",EDGE,"E5287"),sQuery(id+"F17.wireOp",EDGE,"E5288"),sQuery(id+"F17.wireOp",EDGE,"E5289"),sQuery(id+"F17.wireOp",EDGE,"E5290"),sQuery(id+"F17.wireOp",EDGE,"E5291"),sQuery(id+"F17.wireOp",EDGE,"E5292"),sQuery(id+"F17.wireOp",EDGE,"E5293"),sQuery(id+"F17.wireOp",EDGE,"E5294"),sQuery(id+"F17.wireOp",EDGE,"E5295"),sQuery(id+"F17.wireOp",EDGE,"E5296"),sQuery(id+"F17.wireOp",EDGE,"E5297"),sQuery(id+"F17.wireOp",EDGE,"E5298"),sQuery(id+"F17.wireOp",EDGE,"E5299"),sQuery(id+"F17.wireOp",EDGE,"E5300"),sQuery(id+"F17.wireOp",EDGE,"E5301"),sQuery(id+"F17.wireOp",EDGE,"E5302"),sQuery(id+"F17.wireOp",EDGE,"E5303"),sQuery(id+"F17.wireOp",EDGE,"E5304"),sQuery(id+"F17.wireOp",EDGE,"E5305"),sQuery(id+"F17.wireOp",EDGE,"E5306"),sQuery(id+"F17.wireOp",EDGE,"E5307"),sQuery(id+"F17.wireOp",EDGE,"E5308"),sQuery(id+"F17.wireOp",EDGE,"E5309"),sQuery(id+"F17.wireOp",EDGE,"E5310"),sQuery(id+"F17.wireOp",EDGE,"E5311"),sQuery(id+"F17.wireOp",EDGE,"E5312"),sQuery(id+"F17.wireOp",EDGE,"E5313"),sQuery(id+"F17.wireOp",EDGE,"E5314"),sQuery(id+"F17.wireOp",EDGE,"E5315"),sQuery(id+"F17.wireOp",EDGE,"E5316"),sQuery(id+"F17.wireOp",EDGE,"E5317"),sQuery(id+"F17.wireOp",EDGE,"E5318"),sQuery(id+"F17.wireOp",EDGE,"E5319"),sQuery(id+"F17.wireOp",EDGE,"E5320"),sQuery(id+"F17.wireOp",EDGE,"E5321"),sQuery(id+"F17.wireOp",EDGE,"E5322"),sQuery(id+"F17.wireOp",EDGE,"E5323"),sQuery(id+"F17.wireOp",EDGE,"E5324"),sQuery(id+"F17.wireOp",EDGE,"E5325"),sQuery(id+"F17.wireOp",EDGE,"E5326"),sQuery(id+"F17.wireOp",EDGE,"E5327"),sQuery(id+"F17.wireOp",EDGE,"E5328"),sQuery(id+"F17.wireOp",EDGE,"E5329"),sQuery(id+"F17.wireOp",EDGE,"E5330"),sQuery(id+"F17.wireOp",EDGE,"E5331"),sQuery(id+"F17.wireOp",EDGE,"E5332"),sQuery(id+"F17.wireOp",EDGE,"E5333"),sQuery(id+"F17.wireOp",EDGE,"E5334"),sQuery(id+"F17.wireOp",EDGE,"E5335"),sQuery(id+"F17.wireOp",EDGE,"E5336"),sQuery(id+"F17.wireOp",EDGE,"E5337"),sQuery(id+"F17.wireOp",EDGE,"E5338"),sQuery(id+"F17.wireOp",EDGE,"E5339"),sQuery(id+"F17.wireOp",EDGE,"E5340"),sQuery(id+"F17.wireOp",EDGE,"E5341"),sQuery(id+"F17.wireOp",EDGE,"E5342"),sQuery(id+"F17.wireOp",EDGE,"E5343"),sQuery(id+"F17.wireOp",EDGE,"E5344"),sQuery(id+"F17.wireOp",EDGE,"E5345"),sQuery(id+"F17.wireOp",EDGE,"E5346"),sQuery(id+"F17.wireOp",EDGE,"E5347"),sQuery(id+"F17.wireOp",EDGE,"E5348"),sQuery(id+"F17.wireOp",EDGE,"E5349"),sQuery(id+"F17.wireOp",EDGE,"E5350"),sQuery(id+"F17.wireOp",EDGE,"E5351"),sQuery(id+"F17.wireOp",EDGE,"E5352"),sQuery(id+"F17.wireOp",EDGE,"E5353"),sQuery(id+"F17.wireOp",EDGE,"E5354"),sQuery(id+"F17.wireOp",EDGE,"E5355"),sQuery(id+"F17.wireOp",EDGE,"E5356"),sQuery(id+"F17.wireOp",EDGE,"E5357"),sQuery(id+"F17.wireOp",EDGE,"E5358"),sQuery(id+"F17.wireOp",EDGE,"E5359"),sQuery(id+"F17.wireOp",EDGE,"E5360"),sQuery(id+"F17.wireOp",EDGE,"E5361"),sQuery(id+"F17.wireOp",EDGE,"E5362"),sQuery(id+"F17.wireOp",EDGE,"E5363"),sQuery(id+"F17.wireOp",EDGE,"E5364"),sQuery(id+"F17.wireOp",EDGE,"E5365"),sQuery(id+"F17.wireOp",EDGE,"E5366"),sQuery(id+"F17.wireOp",EDGE,"E5367"),sQuery(id+"F17.wireOp",EDGE,"E5368"),sQuery(id+"F17.wireOp",EDGE,"E5369"),sQuery(id+"F17.wireOp",EDGE,"E5370"),sQuery(id+"F17.wireOp",EDGE,"E5371"),sQuery(id+"F17.wireOp",EDGE,"E5372"),sQuery(id+"F17.wireOp",EDGE,"E5373"),sQuery(id+"F17.wireOp",EDGE,"E5374"),sQuery(id+"F17.wireOp",EDGE,"E5375"),sQuery(id+"F17.wireOp",EDGE,"E5376"),sQuery(id+"F17.wireOp",EDGE,"E5377"),sQuery(id+"F17.wireOp",EDGE,"E5378"),sQuery(id+"F17.wireOp",EDGE,"E5379"),sQuery(id+"F17.wireOp",EDGE,"E5380"),sQuery(id+"F17.wireOp",EDGE,"E5381"),sQuery(id+"F17.wireOp",EDGE,"E5382"),sQuery(id+"F17.wireOp",EDGE,"E5383"),sQuery(id+"F17.wireOp",EDGE,"E5384"),sQuery(id+"F17.wireOp",EDGE,"E5385"),sQuery(id+"F17.wireOp",EDGE,"E5386"),sQuery(id+"F17.wireOp",EDGE,"E5387"),sQuery(id+"F17.wireOp",EDGE,"E5388"),sQuery(id+"F17.wireOp",EDGE,"E5389"),sQuery(id+"F17.wireOp",EDGE,"E5390"),sQuery(id+"F17.wireOp",EDGE,"E5391"),sQuery(id+"F17.wireOp",EDGE,"E5392"),sQuery(id+"F17.wireOp",EDGE,"E5393"),sQuery(id+"F17.wireOp",EDGE,"E5394"),sQuery(id+"F17.wireOp",EDGE,"E5395"),sQuery(id+"F17.wireOp",EDGE,"E5396"),sQuery(id+"F17.wireOp",EDGE,"E5397"),sQuery(id+"F17.wireOp",EDGE,"E5398"),sQuery(id+"F17.wireOp",EDGE,"E5399"),sQuery(id+"F17.wireOp",EDGE,"E5400"),sQuery(id+"F17.wireOp",EDGE,"E5401"),sQuery(id+"F17.wireOp",EDGE,"E5402"),sQuery(id+"F17.wireOp",EDGE,"E5403"),sQuery(id+"F17.wireOp",EDGE,"E5404"),sQuery(id+"F17.wireOp",EDGE,"E5405"),sQuery(id+"F17.wireOp",EDGE,"E5406"),sQuery(id+"F17.wireOp",EDGE,"E5407"),sQuery(id+"F17.wireOp",EDGE,"E5408"),sQuery(id+"F17.wireOp",EDGE,"E5409"),sQuery(id+"F17.wireOp",EDGE,"E5410"),sQuery(id+"F17.wireOp",EDGE,"E5411"),sQuery(id+"F17.wireOp",EDGE,"E5412"),sQuery(id+"F17.wireOp",EDGE,"E5413"),sQuery(id+"F17.wireOp",EDGE,"E5414"),sQuery(id+"F17.wireOp",EDGE,"E5415"),sQuery(id+"F17.wireOp",EDGE,"E5416"),sQuery(id+"F17.wireOp",EDGE,"E5417"),sQuery(id+"F17.wireOp",EDGE,"E5418"),sQuery(id+"F17.wireOp",EDGE,"E5419"),sQuery(id+"F17.wireOp",EDGE,"E5420"),sQuery(id+"F17.wireOp",EDGE,"E5421"),sQuery(id+"F17.wireOp",EDGE,"E5422"),sQuery(id+"F17.wireOp",EDGE,"E5423"),sQuery(id+"F17.wireOp",EDGE,"E5424"),sQuery(id+"F17.wireOp",EDGE,"E5425"),sQuery(id+"F17.wireOp",EDGE,"E5426"),sQuery(id+"F17.wireOp",EDGE,"E5427"),sQuery(id+"F17.wireOp",EDGE,"E5428"),sQuery(id+"F17.wireOp",EDGE,"E5429"),sQuery(id+"F17.wireOp",EDGE,"E5430"),sQuery(id+"F17.wireOp",EDGE,"E5431"),sQuery(id+"F17.wireOp",EDGE,"E5432"),sQuery(id+"F17.wireOp",EDGE,"E5433"),sQuery(id+"F17.wireOp",EDGE,"E5434"),sQuery(id+"F17.wireOp",EDGE,"E5435"),sQuery(id+"F17.wireOp",EDGE,"E5436"),sQuery(id+"F17.wireOp",EDGE,"E5437"),sQuery(id+"F17.wireOp",EDGE,"E5438"),sQuery(id+"F17.wireOp",EDGE,"E5439"),sQuery(id+"F17.wireOp",EDGE,"E5440"),sQuery(id+"F17.wireOp",EDGE,"E5441"),sQuery(id+"F17.wireOp",EDGE,"E5442"),sQuery(id+"F17.wireOp",EDGE,"E5443"),sQuery(id+"F17.wireOp",EDGE,"E5444"),sQuery(id+"F17.wireOp",EDGE,"E5445"),sQuery(id+"F17.wireOp",EDGE,"E5446"),sQuery(id+"F17.wireOp",EDGE,"E5447"),sQuery(id+"F17.wireOp",EDGE,"E5448"),sQuery(id+"F17.wireOp",EDGE,"E5449"),sQuery(id+"F17.wireOp",EDGE,"E5450"),sQuery(id+"F17.wireOp",EDGE,"E5451"),sQuery(id+"F17.wireOp",EDGE,"E5452"),sQuery(id+"F17.wireOp",EDGE,"E5453"),sQuery(id+"F17.wireOp",EDGE,"E5454"),sQuery(id+"F17.wireOp",EDGE,"E5455"),sQuery(id+"F17.wireOp",EDGE,"E5456"),sQuery(id+"F17.wireOp",EDGE,"E5457"),sQuery(id+"F17.wireOp",EDGE,"E5458"),sQuery(id+"F17.wireOp",EDGE,"E5459"),sQuery(id+"F17.wireOp",EDGE,"E5460"),sQuery(id+"F17.wireOp",EDGE,"E5461"),sQuery(id+"F17.wireOp",EDGE,"E5462"),sQuery(id+"F17.wireOp",EDGE,"E5463"),sQuery(id+"F17.wireOp",EDGE,"E5464"),sQuery(id+"F17.wireOp",EDGE,"E5465"),sQuery(id+"F17.wireOp",EDGE,"E5466"),sQuery(id+"F17.wireOp",EDGE,"E5467"),sQuery(id+"F17.wireOp",EDGE,"E5468"),sQuery(id+"F17.wireOp",EDGE,"E5469"),sQuery(id+"F17.wireOp",EDGE,"E5470"),sQuery(id+"F17.wireOp",EDGE,"E5471"),sQuery(id+"F17.wireOp",EDGE,"E5472"),sQuery(id+"F17.wireOp",EDGE,"E5473"),sQuery(id+"F17.wireOp",EDGE,"E5474"),sQuery(id+"F17.wireOp",EDGE,"E5475"),sQuery(id+"F17.wireOp",EDGE,"E5476"),sQuery(id+"F17.wireOp",EDGE,"E5477"),sQuery(id+"F17.wireOp",EDGE,"E5478"),sQuery(id+"F17.wireOp",EDGE,"E5479"),sQuery(id+"F17.wireOp",EDGE,"E5480"),sQuery(id+"F17.wireOp",EDGE,"E5481"),sQuery(id+"F17.wireOp",EDGE,"E5482"),sQuery(id+"F17.wireOp",EDGE,"E5483"),sQuery(id+"F17.wireOp",EDGE,"E5484"),sQuery(id+"F17.wireOp",EDGE,"E5485"),sQuery(id+"F17.wireOp",EDGE,"E5486"),sQuery(id+"F17.wireOp",EDGE,"E5487"),sQuery(id+"F17.wireOp",EDGE,"E5488"),sQuery(id+"F17.wireOp",EDGE,"E5489"),sQuery(id+"F17.wireOp",EDGE,"E5490"),sQuery(id+"F17.wireOp",EDGE,"E5491"),sQuery(id+"F17.wireOp",EDGE,"E5492"),sQuery(id+"F17.wireOp",EDGE,"E5493"),sQuery(id+"F17.wireOp",EDGE,"E5494"),sQuery(id+"F17.wireOp",EDGE,"E5495"),sQuery(id+"F17.wireOp",EDGE,"E5496"),sQuery(id+"F17.wireOp",EDGE,"E5497"),sQuery(id+"F17.wireOp",EDGE,"E5498"),sQuery(id+"F17.wireOp",EDGE,"E5499"),sQuery(id+"F17.wireOp",EDGE,"E5500"),sQuery(id+"F17.wireOp",EDGE,"E5501"),sQuery(id+"F17.wireOp",EDGE,"E5502"),sQuery(id+"F17.wireOp",EDGE,"E5503"),sQuery(id+"F17.wireOp",EDGE,"E5504"),sQuery(id+"F17.wireOp",EDGE,"E5505"),sQuery(id+"F17.wireOp",EDGE,"E5506"),sQuery(id+"F17.wireOp",EDGE,"E5507"),sQuery(id+"F17.wireOp",EDGE,"E5508"),sQuery(id+"F17.wireOp",EDGE,"E5509"),sQuery(id+"F17.wireOp",EDGE,"E5510"),sQuery(id+"F17.wireOp",EDGE,"E5511"),sQuery(id+"F17.wireOp",EDGE,"E5512"),sQuery(id+"F17.wireOp",EDGE,"E5513"),sQuery(id+"F17.wireOp",EDGE,"E5514"),sQuery(id+"F17.wireOp",EDGE,"E5515"),sQuery(id+"F17.wireOp",EDGE,"E5516"),sQuery(id+"F17.wireOp",EDGE,"E5517"),sQuery(id+"F17.wireOp",EDGE,"E5518"),sQuery(id+"F17.wireOp",EDGE,"E5519"),sQuery(id+"F17.wireOp",EDGE,"E5520"),sQuery(id+"F17.wireOp",EDGE,"E5521"),sQuery(id+"F17.wireOp",EDGE,"E5522"),sQuery(id+"F17.wireOp",EDGE,"E5523"),sQuery(id+"F17.wireOp",EDGE,"E5524"),sQuery(id+"F17.wireOp",EDGE,"E5525"),sQuery(id+"F17.wireOp",EDGE,"E5526"),sQuery(id+"F17.wireOp",EDGE,"E5527"),sQuery(id+"F17.wireOp",EDGE,"E5528"),sQuery(id+"F17.wireOp",EDGE,"E5529"),sQuery(id+"F17.wireOp",EDGE,"E5530"),sQuery(id+"F17.wireOp",EDGE,"E5531"),sQuery(id+"F17.wireOp",EDGE,"E5532"),sQuery(id+"F17.wireOp",EDGE,"E5533"),sQuery(id+"F17.wireOp",EDGE,"E5534"),sQuery(id+"F17.wireOp",EDGE,"E5535"),sQuery(id+"F17.wireOp",EDGE,"E5536"),sQuery(id+"F17.wireOp",EDGE,"E5537"),sQuery(id+"F17.wireOp",EDGE,"E5538"),sQuery(id+"F17.wireOp",EDGE,"E5539"),sQuery(id+"F17.wireOp",EDGE,"E5540"),sQuery(id+"F17.wireOp",EDGE,"E5541"),sQuery(id+"F17.wireOp",EDGE,"E5542"),sQuery(id+"F17.wireOp",EDGE,"E5543"),sQuery(id+"F17.wireOp",EDGE,"E5544"),sQuery(id+"F17.wireOp",EDGE,"E5545"),sQuery(id+"F17.wireOp",EDGE,"E5546"),sQuery(id+"F17.wireOp",EDGE,"E5547"),sQuery(id+"F17.wireOp",EDGE,"E5548"),sQuery(id+"F17.wireOp",EDGE,"E5549"),sQuery(id+"F17.wireOp",EDGE,"E5550"),sQuery(id+"F17.wireOp",EDGE,"E5551"),sQuery(id+"F17.wireOp",EDGE,"E5552"),sQuery(id+"F17.wireOp",EDGE,"E5553"),sQuery(id+"F17.wireOp",EDGE,"E5554"),sQuery(id+"F17.wireOp",EDGE,"E5555"),sQuery(id+"F17.wireOp",EDGE,"E5556"),sQuery(id+"F17.wireOp",EDGE,"E5557"),sQuery(id+"F17.wireOp",EDGE,"E5558"),sQuery(id+"F17.wireOp",EDGE,"E5559"),sQuery(id+"F17.wireOp",EDGE,"E5560"),sQuery(id+"F17.wireOp",EDGE,"E5561"),sQuery(id+"F17.wireOp",EDGE,"E5562"),sQuery(id+"F17.wireOp",EDGE,"E5563"),sQuery(id+"F17.wireOp",EDGE,"E5564"),sQuery(id+"F17.wireOp",EDGE,"E5565"),sQuery(id+"F17.wireOp",EDGE,"E5566"),sQuery(id+"F17.wireOp",EDGE,"E5567"),sQuery(id+"F17.wireOp",EDGE,"E5568"),sQuery(id+"F17.wireOp",EDGE,"E5569"),sQuery(id+"F17.wireOp",EDGE,"E5570"),sQuery(id+"F17.wireOp",EDGE,"E5571"),sQuery(id+"F17.wireOp",EDGE,"E5572"),sQuery(id+"F17.wireOp",EDGE,"E5573"),sQuery(id+"F17.wireOp",EDGE,"E5574"),sQuery(id+"F17.wireOp",EDGE,"E5575"),sQuery(id+"F17.wireOp",EDGE,"E5576"),sQuery(id+"F17.wireOp",EDGE,"E5577"),sQuery(id+"F17.wireOp",EDGE,"E5578"),sQuery(id+"F17.wireOp",EDGE,"E5579"),sQuery(id+"F17.wireOp",EDGE,"E5580"),sQuery(id+"F17.wireOp",EDGE,"E5581"),sQuery(id+"F17.wireOp",EDGE,"E5582"),sQuery(id+"F17.wireOp",EDGE,"E5583"),sQuery(id+"F17.wireOp",EDGE,"E5584"),sQuery(id+"F17.wireOp",EDGE,"E5585"),sQuery(id+"F17.wireOp",EDGE,"E5586"),sQuery(id+"F17.wireOp",EDGE,"E5587"),sQuery(id+"F17.wireOp",EDGE,"E5588"),sQuery(id+"F17.wireOp",EDGE,"E5589"),sQuery(id+"F17.wireOp",EDGE,"E5590"),sQuery(id+"F17.wireOp",EDGE,"E5591"),sQuery(id+"F17.wireOp",EDGE,"E5592"),sQuery(id+"F17.wireOp",EDGE,"E5593"),sQuery(id+"F17.wireOp",EDGE,"E5594"),sQuery(id+"F17.wireOp",EDGE,"E5595"),sQuery(id+"F17.wireOp",EDGE,"E5596"),sQuery(id+"F17.wireOp",EDGE,"E5597"),sQuery(id+"F17.wireOp",EDGE,"E5598"),sQuery(id+"F17.wireOp",EDGE,"E5599"),sQuery(id+"F17.wireOp",EDGE,"E5600"),sQuery(id+"F17.wireOp",EDGE,"E5601"),sQuery(id+"F17.wireOp",EDGE,"E5602"),sQuery(id+"F17.wireOp",EDGE,"E5603"),sQuery(id+"F17.wireOp",EDGE,"E5604"),sQuery(id+"F17.wireOp",EDGE,"E5605"),sQuery(id+"F17.wireOp",EDGE,"E5606"),sQuery(id+"F17.wireOp",EDGE,"E5607"),sQuery(id+"F17.wireOp",EDGE,"E5608"),sQuery(id+"F17.wireOp",EDGE,"E5609"),sQuery(id+"F17.wireOp",EDGE,"E5610"),sQuery(id+"F17.wireOp",EDGE,"E5611"),sQuery(id+"F17.wireOp",EDGE,"E5612"),sQuery(id+"F17.wireOp",EDGE,"E5613"),sQuery(id+"F17.wireOp",EDGE,"E5614"),sQuery(id+"F17.wireOp",EDGE,"E5615"),sQuery(id+"F17.wireOp",EDGE,"E5616"),sQuery(id+"F17.wireOp",EDGE,"E5617"),sQuery(id+"F17.wireOp",EDGE,"E5618"),sQuery(id+"F17.wireOp",EDGE,"E5619"),sQuery(id+"F17.wireOp",EDGE,"E5620"),sQuery(id+"F17.wireOp",EDGE,"E5621"),sQuery(id+"F17.wireOp",EDGE,"E5622"),sQuery(id+"F17.wireOp",EDGE,"E5623"),sQuery(id+"F17.wireOp",EDGE,"E5624"),sQuery(id+"F17.wireOp",EDGE,"E5625"),sQuery(id+"F17.wireOp",EDGE,"E5626"),sQuery(id+"F17.wireOp",EDGE,"E5627"),sQuery(id+"F17.wireOp",EDGE,"E5628"),sQuery(id+"F17.wireOp",EDGE,"E5629"),sQuery(id+"F17.wireOp",EDGE,"E5630"),sQuery(id+"F17.wireOp",EDGE,"E5631"),sQuery(id+"F17.wireOp",EDGE,"E5632"),sQuery(id+"F17.wireOp",EDGE,"E5633"),sQuery(id+"F17.wireOp",EDGE,"E5634"),sQuery(id+"F17.wireOp",EDGE,"E5635"),sQuery(id+"F17.wireOp",EDGE,"E5636"),sQuery(id+"F17.wireOp",EDGE,"E5637"),sQuery(id+"F17.wireOp",EDGE,"E5638"),sQuery(id+"F17.wireOp",EDGE,"E5639"),sQuery(id+"F17.wireOp",EDGE,"E5640"),sQuery(id+"F17.wireOp",EDGE,"E5641"),sQuery(id+"F17.wireOp",EDGE,"E5642"),sQuery(id+"F17.wireOp",EDGE,"E5643"),sQuery(id+"F17.wireOp",EDGE,"E5644"),sQuery(id+"F17.wireOp",EDGE,"E5645"),sQuery(id+"F17.wireOp",EDGE,"E5646"),sQuery(id+"F17.wireOp",EDGE,"E5647"),sQuery(id+"F17.wireOp",EDGE,"E5648"),sQuery(id+"F17.wireOp",EDGE,"E5649"),sQuery(id+"F17.wireOp",EDGE,"E5650"),sQuery(id+"F17.wireOp",EDGE,"E5651"),sQuery(id+"F17.wireOp",EDGE,"E5652"),sQuery(id+"F17.wireOp",EDGE,"E5653"),sQuery(id+"F17.wireOp",EDGE,"E5654"),sQuery(id+"F17.wireOp",EDGE,"E5655"),sQuery(id+"F17.wireOp",EDGE,"E5656"),sQuery(id+"F17.wireOp",EDGE,"E5657"),sQuery(id+"F17.wireOp",EDGE,"E5658"),sQuery(id+"F17.wireOp",EDGE,"E5659"),sQuery(id+"F17.wireOp",EDGE,"E5660"),sQuery(id+"F17.wireOp",EDGE,"E5661"),sQuery(id+"F17.wireOp",EDGE,"E5662"),sQuery(id+"F17.wireOp",EDGE,"E5663"),sQuery(id+"F17.wireOp",EDGE,"E5664"),sQuery(id+"F17.wireOp",EDGE,"E5665"),sQuery(id+"F17.wireOp",EDGE,"E5666"),sQuery(id+"F17.wireOp",EDGE,"E5667"),sQuery(id+"F17.wireOp",EDGE,"E5668"),sQuery(id+"F17.wireOp",EDGE,"E5669"),sQuery(id+"F17.wireOp",EDGE,"E5670"),sQuery(id+"F17.wireOp",EDGE,"E5671"),sQuery(id+"F17.wireOp",EDGE,"E5672"),sQuery(id+"F17.wireOp",EDGE,"E5673"),sQuery(id+"F17.wireOp",EDGE,"E5674"),sQuery(id+"F17.wireOp",EDGE,"E5675"),sQuery(id+"F17.wireOp",EDGE,"E5676"),sQuery(id+"F17.wireOp",EDGE,"E5677"),sQuery(id+"F17.wireOp",EDGE,"E5678"),sQuery(id+"F17.wireOp",EDGE,"E5679"),sQuery(id+"F17.wireOp",EDGE,"E5680"),sQuery(id+"F17.wireOp",EDGE,"E5681"),sQuery(id+"F17.wireOp",EDGE,"E5682"),sQuery(id+"F17.wireOp",EDGE,"E5683"),sQuery(id+"F17.wireOp",EDGE,"E5684"),sQuery(id+"F17.wireOp",EDGE,"E5685"),sQuery(id+"F17.wireOp",EDGE,"E5686"),sQuery(id+"F17.wireOp",EDGE,"E5687"),sQuery(id+"F17.wireOp",EDGE,"E5688"),sQuery(id+"F17.wireOp",EDGE,"E5689"),sQuery(id+"F17.wireOp",EDGE,"E5690"),sQuery(id+"F17.wireOp",EDGE,"E5691"),sQuery(id+"F17.wireOp",EDGE,"E5692"),sQuery(id+"F17.wireOp",EDGE,"E5693"),sQuery(id+"F17.wireOp",EDGE,"E5694"),sQuery(id+"F17.wireOp",EDGE,"E5695"),sQuery(id+"F17.wireOp",EDGE,"E5696"),sQuery(id+"F17.wireOp",EDGE,"E5697"),sQuery(id+"F17.wireOp",EDGE,"E5698"),sQuery(id+"F17.wireOp",EDGE,"E5699"),sQuery(id+"F17.wireOp",EDGE,"E5700"),sQuery(id+"F17.wireOp",EDGE,"E5701"),sQuery(id+"F17.wireOp",EDGE,"E5702"),sQuery(id+"F17.wireOp",EDGE,"E5703"),sQuery(id+"F17.wireOp",EDGE,"E5704"),sQuery(id+"F17.wireOp",EDGE,"E5705"),sQuery(id+"F17.wireOp",EDGE,"E5706"),sQuery(id+"F17.wireOp",EDGE,"E5707"),sQuery(id+"F17.wireOp",EDGE,"E5708"),sQuery(id+"F17.wireOp",EDGE,"E5709"),sQuery(id+"F17.wireOp",EDGE,"E5710"),sQuery(id+"F17.wireOp",EDGE,"E5711"),sQuery(id+"F17.wireOp",EDGE,"E5712"),sQuery(id+"F17.wireOp",EDGE,"E5713"),sQuery(id+"F17.wireOp",EDGE,"E5714"),sQuery(id+"F17.wireOp",EDGE,"E5715"),sQuery(id+"F17.wireOp",EDGE,"E5716"),sQuery(id+"F17.wireOp",EDGE,"E5717"),sQuery(id+"F17.wireOp",EDGE,"E5718"),sQuery(id+"F17.wireOp",EDGE,"E5719"),sQuery(id+"F17.wireOp",EDGE,"E5720"),sQuery(id+"F17.wireOp",EDGE,"E5721"),sQuery(id+"F17.wireOp",EDGE,"E5722"),sQuery(id+"F17.wireOp",EDGE,"E5723"),sQuery(id+"F17.wireOp",EDGE,"E5724"),sQuery(id+"F17.wireOp",EDGE,"E5725"),sQuery(id+"F17.wireOp",EDGE,"E5726"),sQuery(id+"F17.wireOp",EDGE,"E5727"),sQuery(id+"F17.wireOp",EDGE,"E5728"),sQuery(id+"F17.wireOp",EDGE,"E5729"),sQuery(id+"F17.wireOp",EDGE,"E5730"),sQuery(id+"F17.wireOp",EDGE,"E5731"),sQuery(id+"F17.wireOp",EDGE,"E5732"),sQuery(id+"F17.wireOp",EDGE,"E5733"),sQuery(id+"F17.wireOp",EDGE,"E5734"),sQuery(id+"F17.wireOp",EDGE,"E5735"),sQuery(id+"F17.wireOp",EDGE,"E5736"),sQuery(id+"F17.wireOp",EDGE,"E5737"),sQuery(id+"F17.wireOp",EDGE,"E5738"),sQuery(id+"F17.wireOp",EDGE,"E5739"),sQuery(id+"F17.wireOp",EDGE,"E5740"),sQuery(id+"F17.wireOp",EDGE,"E5741"),sQuery(id+"F17.wireOp",EDGE,"E5742"),sQuery(id+"F17.wireOp",EDGE,"E5743"),sQuery(id+"F17.wireOp",EDGE,"E5744"),sQuery(id+"F17.wireOp",EDGE,"E5745"),sQuery(id+"F17.wireOp",EDGE,"E5746"),sQuery(id+"F17.wireOp",EDGE,"E5747"),sQuery(id+"F17.wireOp",EDGE,"E5748"),sQuery(id+"F17.wireOp",EDGE,"E5749"),sQuery(id+"F17.wireOp",EDGE,"E5750"),sQuery(id+"F17.wireOp",EDGE,"E5751")])],"isStart":false});
            var sketch = newSketch(context, id + "F24", { "sketchPlane" : qUnion([Q0])});
            skCircle(sketch, "E5759", {"center": v(0, 46.5) * mm, "radius": 0.5 * mm});
            skCircle(sketch, "E5760", {"center": v(44.23, -14.34) * mm, "radius": 0.5 * mm});
            skCircle(sketch, "E5761.MirrorC", {"center": v(-44.23, -14.34) * mm, "radius": 0.5 * mm});
            skSolve(sketch);
        }
        {
            var Q0;
            Q0 = qSketchRegion(id + "F24", true);
            extrude(context, id + "F25", {"entities" : qUnion([Q0]), "operationType" : NewBodyOperationType.ADD, "depth" : 0.5 * mm, "offsetDistance" : 25 * mm});
        }
        {
            var Q0;
            Q0=makeQuery(id+"F23.opExtrude","CAP_EDGE",EDGE,{"disambiguationData":[OSD([sQuery(id+"F22.wireOp",EDGE,"E5755.1.2")])],"isStart":false});
            var Q1;
            Q1=makeQuery(id+"F23.opExtrude","CAP_EDGE",EDGE,{"disambiguationData":[OSD([sQuery(id+"F22.wireOp",EDGE,"E5755.2.2")])],"isStart":false});
            var Q2;
            Q2=makeQuery(id+"F23.opExtrude","CAP_EDGE",EDGE,{"disambiguationData":[OSD([sQuery(id+"F22.wireOp",EDGE,"E5754.0.right")])],"isStart":false});
            fillet(context, id + "F26", {"entities" : qUnion([Q0, Q1, Q2]), "radius" : 1 * mm, "tangentPropagation" : true, "allowEdgeOverflow" : false});
        }
        {
            var Q0;
            Q0=makeQuery(id+"F18.opExtrude","CAP_EDGE",EDGE,{"disambiguationData":[OSD([sQuery(id+"F17.wireOp",EDGE,"E2725")])],"isStart":false});
            var Q1;
            Q1=makeQuery(id+"F18.opExtrude","CAP_EDGE",EDGE,{"disambiguationData":[OSD([sQuery(id+"F17.wireOp",EDGE,"E2719")])],"isStart":false});
            var Q2;
            Q2=makeQuery(id+"F18.opExtrude","CAP_EDGE",EDGE,{"disambiguationData":[OSD([sQuery(id+"F17.wireOp",EDGE,"E2720")])],"isStart":false});
            var Q3;
            Q3=makeQuery(id+"F18.opExtrude","CAP_EDGE",EDGE,{"disambiguationData":[OSD([sQuery(id+"F17.wireOp",EDGE,"E2721")])],"isStart":false});
            var Q4;
            Q4=makeQuery(id+"F18.opExtrude","CAP_EDGE",EDGE,{"disambiguationData":[OSD([sQuery(id+"F17.wireOp",EDGE,"E2722")])],"isStart":false});
            var Q5;
            Q5=makeQuery(id+"F18.opExtrude","CAP_EDGE",EDGE,{"disambiguationData":[OSD([sQuery(id+"F17.wireOp",EDGE,"E2723")])],"isStart":false});
            var Q6;
            Q6=makeQuery(id+"F18.opExtrude","CAP_EDGE",EDGE,{"disambiguationData":[OSD([sQuery(id+"F17.wireOp",EDGE,"E2724")])],"isStart":false});
            var Q7;
            Q7=makeQuery(id+"F18.opExtrude","CAP_EDGE",EDGE,{"disambiguationData":[OSD([sQuery(id+"F17.wireOp",EDGE,"E2718")])],"isStart":false});
            var Q8;
            Q8=makeQuery(id+"F18.opExtrude","CAP_EDGE",EDGE,{"disambiguationData":[OSD([sQuery(id+"F17.wireOp",EDGE,"E2717")])],"isStart":false});
            var Q9;
            Q9=makeQuery(id+"F18.opExtrude","CAP_EDGE",EDGE,{"disambiguationData":[OSD([sQuery(id+"F17.wireOp",EDGE,"E2716")])],"isStart":false});
            var Q10;
            Q10=makeQuery(id+"F18.opExtrude","CAP_EDGE",EDGE,{"disambiguationData":[OSD([sQuery(id+"F17.wireOp",EDGE,"E2715")])],"isStart":false});
            var Q11;
            Q11=makeQuery(id+"F18.opExtrude","CAP_EDGE",EDGE,{"disambiguationData":[OSD([sQuery(id+"F17.wireOp",EDGE,"E2714")])],"isStart":false});
            var Q12;
            Q12=makeQuery(id+"F18.opExtrude","CAP_EDGE",EDGE,{"disambiguationData":[OSD([sQuery(id+"F17.wireOp",EDGE,"E2713")])],"isStart":false});
            var Q13;
            Q13=makeQuery(id+"F18.opExtrude","CAP_EDGE",EDGE,{"disambiguationData":[OSD([sQuery(id+"F17.wireOp",EDGE,"E2712")])],"isStart":false});
            var Q14;
            Q14=makeQuery(id+"F18.opExtrude","CAP_EDGE",EDGE,{"disambiguationData":[OSD([sQuery(id+"F17.wireOp",EDGE,"E2711")])],"isStart":false});
            var Q15;
            Q15=makeQuery(id+"F18.opExtrude","CAP_EDGE",EDGE,{"disambiguationData":[OSD([sQuery(id+"F17.wireOp",EDGE,"E2710")])],"isStart":false});
            var Q16;
            Q16=makeQuery(id+"F18.opExtrude","CAP_EDGE",EDGE,{"disambiguationData":[OSD([sQuery(id+"F17.wireOp",EDGE,"E2709")])],"isStart":false});
            var Q17;
            Q17=makeQuery(id+"F18.opExtrude","CAP_EDGE",EDGE,{"disambiguationData":[OSD([sQuery(id+"F17.wireOp",EDGE,"E2708")])],"isStart":false});
            var Q18;
            Q18=makeQuery(id+"F18.opExtrude","CAP_EDGE",EDGE,{"disambiguationData":[OSD([sQuery(id+"F17.wireOp",EDGE,"E2707")])],"isStart":false});
            var Q19;
            Q19=makeQuery(id+"F18.opExtrude","CAP_EDGE",EDGE,{"disambiguationData":[OSD([sQuery(id+"F17.wireOp",EDGE,"E2706")])],"isStart":false});
            var Q20;
            Q20=makeQuery(id+"F18.opExtrude","CAP_EDGE",EDGE,{"disambiguationData":[OSD([sQuery(id+"F17.wireOp",EDGE,"E2705")])],"isStart":false});
            var Q21;
            Q21=makeQuery(id+"F18.opExtrude","CAP_EDGE",EDGE,{"disambiguationData":[OSD([sQuery(id+"F17.wireOp",EDGE,"E2704")])],"isStart":false});
            var Q22;
            Q22=makeQuery(id+"F18.opExtrude","CAP_EDGE",EDGE,{"disambiguationData":[OSD([sQuery(id+"F17.wireOp",EDGE,"E2703")])],"isStart":false});
            var Q23;
            Q23=makeQuery(id+"F18.opExtrude","CAP_EDGE",EDGE,{"disambiguationData":[OSD([sQuery(id+"F17.wireOp",EDGE,"E2702")])],"isStart":false});
            var Q24;
            Q24=makeQuery(id+"F18.opExtrude","CAP_EDGE",EDGE,{"disambiguationData":[OSD([sQuery(id+"F17.wireOp",EDGE,"E2701")])],"isStart":false});
            var Q25;
            Q25=makeQuery(id+"F18.opExtrude","CAP_EDGE",EDGE,{"disambiguationData":[OSD([sQuery(id+"F17.wireOp",EDGE,"E2700")])],"isStart":false});
            var Q26;
            Q26=makeQuery(id+"F18.opExtrude","CAP_EDGE",EDGE,{"disambiguationData":[OSD([sQuery(id+"F17.wireOp",EDGE,"E2699")])],"isStart":false});
            var Q27;
            Q27=makeQuery(id+"F18.opExtrude","CAP_EDGE",EDGE,{"disambiguationData":[OSD([sQuery(id+"F17.wireOp",EDGE,"E2698")])],"isStart":false});
            var Q28;
            Q28=makeQuery(id+"F18.opExtrude","CAP_EDGE",EDGE,{"disambiguationData":[OSD([sQuery(id+"F17.wireOp",EDGE,"E2697")])],"isStart":false});
            var Q29;
            Q29=makeQuery(id+"F18.opExtrude","CAP_EDGE",EDGE,{"disambiguationData":[OSD([sQuery(id+"F17.wireOp",EDGE,"E2696")])],"isStart":false});
            var Q30;
            Q30=makeQuery(id+"F18.opExtrude","CAP_EDGE",EDGE,{"disambiguationData":[OSD([sQuery(id+"F17.wireOp",EDGE,"E2695")])],"isStart":false});
            var Q31;
            Q31=makeQuery(id+"F18.opExtrude","CAP_EDGE",EDGE,{"disambiguationData":[OSD([sQuery(id+"F17.wireOp",EDGE,"E2694")])],"isStart":false});
            var Q32;
            Q32=makeQuery(id+"F18.opExtrude","CAP_EDGE",EDGE,{"disambiguationData":[OSD([sQuery(id+"F17.wireOp",EDGE,"E2693")])],"isStart":false});
            var Q33;
            Q33=makeQuery(id+"F18.opExtrude","CAP_EDGE",EDGE,{"disambiguationData":[OSD([sQuery(id+"F17.wireOp",EDGE,"E2692")])],"isStart":false});
            var Q34;
            Q34=makeQuery(id+"F18.opExtrude","CAP_EDGE",EDGE,{"disambiguationData":[OSD([sQuery(id+"F17.wireOp",EDGE,"E2691")])],"isStart":false});
            var Q35;
            Q35=makeQuery(id+"F18.opExtrude","CAP_EDGE",EDGE,{"disambiguationData":[OSD([sQuery(id+"F17.wireOp",EDGE,"E2690")])],"isStart":false});
            var Q36;
            Q36=makeQuery(id+"F18.opExtrude","CAP_EDGE",EDGE,{"disambiguationData":[OSD([sQuery(id+"F17.wireOp",EDGE,"E2689")])],"isStart":false});
            var Q37;
            Q37=makeQuery(id+"F18.opExtrude","CAP_EDGE",EDGE,{"disambiguationData":[OSD([sQuery(id+"F17.wireOp",EDGE,"E2688")])],"isStart":false});
            var Q38;
            Q38=makeQuery(id+"F18.opExtrude","CAP_EDGE",EDGE,{"disambiguationData":[OSD([sQuery(id+"F17.wireOp",EDGE,"E2687")])],"isStart":false});
            var Q39;
            Q39=makeQuery(id+"F18.opExtrude","CAP_EDGE",EDGE,{"disambiguationData":[OSD([sQuery(id+"F17.wireOp",EDGE,"E2686")])],"isStart":false});
            var Q40;
            Q40=makeQuery(id+"F18.opExtrude","CAP_EDGE",EDGE,{"disambiguationData":[OSD([sQuery(id+"F17.wireOp",EDGE,"E2685")])],"isStart":false});
            var Q41;
            Q41=makeQuery(id+"F18.opExtrude","CAP_EDGE",EDGE,{"disambiguationData":[OSD([sQuery(id+"F17.wireOp",EDGE,"E2684")])],"isStart":false});
            var Q42;
            Q42=makeQuery(id+"F18.opExtrude","CAP_EDGE",EDGE,{"disambiguationData":[OSD([sQuery(id+"F17.wireOp",EDGE,"E2683")])],"isStart":false});
            var Q43;
            Q43=makeQuery(id+"F18.opExtrude","CAP_EDGE",EDGE,{"disambiguationData":[OSD([sQuery(id+"F17.wireOp",EDGE,"E2682")])],"isStart":false});
            var Q44;
            Q44=makeQuery(id+"F18.opExtrude","CAP_EDGE",EDGE,{"disambiguationData":[OSD([sQuery(id+"F17.wireOp",EDGE,"E2681")])],"isStart":false});
            var Q45;
            Q45=makeQuery(id+"F18.opExtrude","CAP_EDGE",EDGE,{"disambiguationData":[OSD([sQuery(id+"F17.wireOp",EDGE,"E2680")])],"isStart":false});
            var Q46;
            Q46=makeQuery(id+"F18.opExtrude","CAP_EDGE",EDGE,{"disambiguationData":[OSD([sQuery(id+"F17.wireOp",EDGE,"E2679")])],"isStart":false});
            var Q47;
            Q47=makeQuery(id+"F18.opExtrude","CAP_EDGE",EDGE,{"disambiguationData":[OSD([sQuery(id+"F17.wireOp",EDGE,"E2678")])],"isStart":false});
            var Q48;
            Q48=makeQuery(id+"F18.opExtrude","CAP_EDGE",EDGE,{"disambiguationData":[OSD([sQuery(id+"F17.wireOp",EDGE,"E2677")])],"isStart":false});
            var Q49;
            Q49=makeQuery(id+"F18.opExtrude","CAP_EDGE",EDGE,{"disambiguationData":[OSD([sQuery(id+"F17.wireOp",EDGE,"E2676")])],"isStart":false});
            var Q50;
            Q50=makeQuery(id+"F18.opExtrude","CAP_EDGE",EDGE,{"disambiguationData":[OSD([sQuery(id+"F17.wireOp",EDGE,"E2675")])],"isStart":false});
            var Q51;
            Q51=makeQuery(id+"F18.opExtrude","CAP_EDGE",EDGE,{"disambiguationData":[OSD([sQuery(id+"F17.wireOp",EDGE,"E2674")])],"isStart":false});
            var Q52;
            Q52=makeQuery(id+"F18.opExtrude","CAP_EDGE",EDGE,{"disambiguationData":[OSD([sQuery(id+"F17.wireOp",EDGE,"E2673")])],"isStart":false});
            var Q53;
            Q53=makeQuery(id+"F18.opExtrude","CAP_EDGE",EDGE,{"disambiguationData":[OSD([sQuery(id+"F17.wireOp",EDGE,"E2672")])],"isStart":false});
            var Q54;
            Q54=makeQuery(id+"F18.opExtrude","CAP_EDGE",EDGE,{"disambiguationData":[OSD([sQuery(id+"F17.wireOp",EDGE,"E2671")])],"isStart":false});
            var Q55;
            Q55=makeQuery(id+"F18.opExtrude","CAP_EDGE",EDGE,{"disambiguationData":[OSD([sQuery(id+"F17.wireOp",EDGE,"E2670")])],"isStart":false});
            var Q56;
            Q56=makeQuery(id+"F18.opExtrude","CAP_EDGE",EDGE,{"disambiguationData":[OSD([sQuery(id+"F17.wireOp",EDGE,"E2669")])],"isStart":false});
            var Q57;
            Q57=makeQuery(id+"F18.opExtrude","CAP_EDGE",EDGE,{"disambiguationData":[OSD([sQuery(id+"F17.wireOp",EDGE,"E2668")])],"isStart":false});
            var Q58;
            Q58=makeQuery(id+"F18.opExtrude","CAP_EDGE",EDGE,{"disambiguationData":[OSD([sQuery(id+"F17.wireOp",EDGE,"E2667")])],"isStart":false});
            var Q59;
            Q59=makeQuery(id+"F18.opExtrude","CAP_EDGE",EDGE,{"disambiguationData":[OSD([sQuery(id+"F17.wireOp",EDGE,"E2666")])],"isStart":false});
            var Q60;
            Q60=makeQuery(id+"F18.opExtrude","CAP_EDGE",EDGE,{"disambiguationData":[OSD([sQuery(id+"F17.wireOp",EDGE,"E2665")])],"isStart":false});
            var Q61;
            Q61=makeQuery(id+"F18.opExtrude","CAP_EDGE",EDGE,{"disambiguationData":[OSD([sQuery(id+"F17.wireOp",EDGE,"E2664")])],"isStart":false});
            var Q62;
            Q62=makeQuery(id+"F18.opExtrude","CAP_EDGE",EDGE,{"disambiguationData":[OSD([sQuery(id+"F17.wireOp",EDGE,"E2663")])],"isStart":false});
            var Q63;
            Q63=makeQuery(id+"F18.opExtrude","CAP_EDGE",EDGE,{"disambiguationData":[OSD([sQuery(id+"F17.wireOp",EDGE,"E2662")])],"isStart":false});
            var Q64;
            Q64=makeQuery(id+"F18.opExtrude","CAP_EDGE",EDGE,{"disambiguationData":[OSD([sQuery(id+"F17.wireOp",EDGE,"E2661")])],"isStart":false});
            var Q65;
            Q65=makeQuery(id+"F18.opExtrude","CAP_EDGE",EDGE,{"disambiguationData":[OSD([sQuery(id+"F17.wireOp",EDGE,"E2660")])],"isStart":false});
            var Q66;
            Q66=makeQuery(id+"F18.opExtrude","CAP_EDGE",EDGE,{"disambiguationData":[OSD([sQuery(id+"F17.wireOp",EDGE,"E2659")])],"isStart":false});
            var Q67;
            Q67=makeQuery(id+"F18.opExtrude","CAP_EDGE",EDGE,{"disambiguationData":[OSD([sQuery(id+"F17.wireOp",EDGE,"E2658")])],"isStart":false});
            var Q68;
            Q68=makeQuery(id+"F18.opExtrude","CAP_EDGE",EDGE,{"disambiguationData":[OSD([sQuery(id+"F17.wireOp",EDGE,"E2657")])],"isStart":false});
            var Q69;
            Q69=makeQuery(id+"F18.opExtrude","CAP_EDGE",EDGE,{"disambiguationData":[OSD([sQuery(id+"F17.wireOp",EDGE,"E2656")])],"isStart":false});
            var Q70;
            Q70=makeQuery(id+"F18.opExtrude","CAP_EDGE",EDGE,{"disambiguationData":[OSD([sQuery(id+"F17.wireOp",EDGE,"E2655")])],"isStart":false});
            var Q71;
            Q71=makeQuery(id+"F18.opExtrude","CAP_EDGE",EDGE,{"disambiguationData":[OSD([sQuery(id+"F17.wireOp",EDGE,"E2654")])],"isStart":false});
            var Q72;
            Q72=makeQuery(id+"F18.opExtrude","CAP_EDGE",EDGE,{"disambiguationData":[OSD([sQuery(id+"F17.wireOp",EDGE,"E2653")])],"isStart":false});
            var Q73;
            Q73=makeQuery(id+"F18.opExtrude","CAP_EDGE",EDGE,{"disambiguationData":[OSD([sQuery(id+"F17.wireOp",EDGE,"E2652")])],"isStart":false});
            var Q74;
            Q74=makeQuery(id+"F18.opExtrude","CAP_EDGE",EDGE,{"disambiguationData":[OSD([sQuery(id+"F17.wireOp",EDGE,"E2651")])],"isStart":false});
            var Q75;
            Q75=makeQuery(id+"F18.opExtrude","CAP_EDGE",EDGE,{"disambiguationData":[OSD([sQuery(id+"F17.wireOp",EDGE,"E2650")])],"isStart":false});
            var Q76;
            Q76=makeQuery(id+"F18.opExtrude","CAP_EDGE",EDGE,{"disambiguationData":[OSD([sQuery(id+"F17.wireOp",EDGE,"E2649")])],"isStart":false});
            var Q77;
            Q77=makeQuery(id+"F18.opExtrude","CAP_EDGE",EDGE,{"disambiguationData":[OSD([sQuery(id+"F17.wireOp",EDGE,"E2648")])],"isStart":false});
            var Q78;
            Q78=makeQuery(id+"F18.opExtrude","CAP_EDGE",EDGE,{"disambiguationData":[OSD([sQuery(id+"F17.wireOp",EDGE,"E2647")])],"isStart":false});
            var Q79;
            Q79=makeQuery(id+"F18.opExtrude","CAP_EDGE",EDGE,{"disambiguationData":[OSD([sQuery(id+"F17.wireOp",EDGE,"E2646")])],"isStart":false});
            var Q80;
            Q80=makeQuery(id+"F18.opExtrude","CAP_EDGE",EDGE,{"disambiguationData":[OSD([sQuery(id+"F17.wireOp",EDGE,"E2645")])],"isStart":false});
            var Q81;
            Q81=makeQuery(id+"F18.opExtrude","CAP_EDGE",EDGE,{"disambiguationData":[OSD([sQuery(id+"F17.wireOp",EDGE,"E2644")])],"isStart":false});
            var Q82;
            Q82=makeQuery(id+"F18.opExtrude","CAP_EDGE",EDGE,{"disambiguationData":[OSD([sQuery(id+"F17.wireOp",EDGE,"E2643")])],"isStart":false});
            var Q83;
            Q83=makeQuery(id+"F18.opExtrude","CAP_EDGE",EDGE,{"disambiguationData":[OSD([sQuery(id+"F17.wireOp",EDGE,"E2642")])],"isStart":false});
            var Q84;
            Q84=makeQuery(id+"F18.opExtrude","CAP_EDGE",EDGE,{"disambiguationData":[OSD([sQuery(id+"F17.wireOp",EDGE,"E2641")])],"isStart":false});
            var Q85;
            Q85=makeQuery(id+"F18.opExtrude","CAP_EDGE",EDGE,{"disambiguationData":[OSD([sQuery(id+"F17.wireOp",EDGE,"E2640")])],"isStart":false});
            var Q86;
            Q86=makeQuery(id+"F18.opExtrude","CAP_EDGE",EDGE,{"disambiguationData":[OSD([sQuery(id+"F17.wireOp",EDGE,"E2639")])],"isStart":false});
            var Q87;
            Q87=makeQuery(id+"F18.opExtrude","CAP_EDGE",EDGE,{"disambiguationData":[OSD([sQuery(id+"F17.wireOp",EDGE,"E2638")])],"isStart":false});
            var Q88;
            Q88=makeQuery(id+"F18.opExtrude","CAP_EDGE",EDGE,{"disambiguationData":[OSD([sQuery(id+"F17.wireOp",EDGE,"E2637")])],"isStart":false});
            var Q89;
            Q89=makeQuery(id+"F18.opExtrude","CAP_EDGE",EDGE,{"disambiguationData":[OSD([sQuery(id+"F17.wireOp",EDGE,"E2636")])],"isStart":false});
            var Q90;
            Q90=makeQuery(id+"F18.opExtrude","CAP_EDGE",EDGE,{"disambiguationData":[OSD([sQuery(id+"F17.wireOp",EDGE,"E2635")])],"isStart":false});
            var Q91;
            Q91=makeQuery(id+"F18.opExtrude","CAP_EDGE",EDGE,{"disambiguationData":[OSD([sQuery(id+"F17.wireOp",EDGE,"E2634")])],"isStart":false});
            var Q92;
            Q92=makeQuery(id+"F18.opExtrude","CAP_EDGE",EDGE,{"disambiguationData":[OSD([sQuery(id+"F17.wireOp",EDGE,"E2633")])],"isStart":false});
            var Q93;
            Q93=makeQuery(id+"F18.opExtrude","CAP_EDGE",EDGE,{"disambiguationData":[OSD([sQuery(id+"F17.wireOp",EDGE,"E2632")])],"isStart":false});
            var Q94;
            Q94=makeQuery(id+"F18.opExtrude","CAP_EDGE",EDGE,{"disambiguationData":[OSD([sQuery(id+"F17.wireOp",EDGE,"E2631")])],"isStart":false});
            var Q95;
            Q95=makeQuery(id+"F18.opExtrude","CAP_EDGE",EDGE,{"disambiguationData":[OSD([sQuery(id+"F17.wireOp",EDGE,"E2630")])],"isStart":false});
            var Q96;
            Q96=makeQuery(id+"F18.opExtrude","CAP_EDGE",EDGE,{"disambiguationData":[OSD([sQuery(id+"F17.wireOp",EDGE,"E2629")])],"isStart":false});
            var Q97;
            Q97=makeQuery(id+"F18.opExtrude","CAP_EDGE",EDGE,{"disambiguationData":[OSD([sQuery(id+"F17.wireOp",EDGE,"E2628")])],"isStart":false});
            var Q98;
            Q98=makeQuery(id+"F18.opExtrude","CAP_EDGE",EDGE,{"disambiguationData":[OSD([sQuery(id+"F17.wireOp",EDGE,"E2627")])],"isStart":false});
            var Q99;
            Q99=makeQuery(id+"F18.opExtrude","CAP_EDGE",EDGE,{"disambiguationData":[OSD([sQuery(id+"F17.wireOp",EDGE,"E2626")])],"isStart":false});
            var Q100;
            Q100=makeQuery(id+"F18.opExtrude","CAP_EDGE",EDGE,{"disambiguationData":[OSD([sQuery(id+"F17.wireOp",EDGE,"E2625")])],"isStart":false});
            var Q101;
            Q101=makeQuery(id+"F18.opExtrude","CAP_EDGE",EDGE,{"disambiguationData":[OSD([sQuery(id+"F17.wireOp",EDGE,"E2624")])],"isStart":false});
            var Q102;
            Q102=makeQuery(id+"F18.opExtrude","CAP_EDGE",EDGE,{"disambiguationData":[OSD([sQuery(id+"F17.wireOp",EDGE,"E2623")])],"isStart":false});
            var Q103;
            Q103=makeQuery(id+"F18.opExtrude","CAP_EDGE",EDGE,{"disambiguationData":[OSD([sQuery(id+"F17.wireOp",EDGE,"E2622")])],"isStart":false});
            var Q104;
            Q104=makeQuery(id+"F18.opExtrude","CAP_EDGE",EDGE,{"disambiguationData":[OSD([sQuery(id+"F17.wireOp",EDGE,"E2621")])],"isStart":false});
            var Q105;
            Q105=makeQuery(id+"F18.opExtrude","CAP_EDGE",EDGE,{"disambiguationData":[OSD([sQuery(id+"F17.wireOp",EDGE,"E2620")])],"isStart":false});
            var Q106;
            Q106=makeQuery(id+"F18.opExtrude","CAP_EDGE",EDGE,{"disambiguationData":[OSD([sQuery(id+"F17.wireOp",EDGE,"E2619")])],"isStart":false});
            var Q107;
            Q107=makeQuery(id+"F18.opExtrude","CAP_EDGE",EDGE,{"disambiguationData":[OSD([sQuery(id+"F17.wireOp",EDGE,"E2618")])],"isStart":false});
            var Q108;
            Q108=makeQuery(id+"F18.opExtrude","CAP_EDGE",EDGE,{"disambiguationData":[OSD([sQuery(id+"F17.wireOp",EDGE,"E2617")])],"isStart":false});
            var Q109;
            Q109=makeQuery(id+"F18.opExtrude","CAP_EDGE",EDGE,{"disambiguationData":[OSD([sQuery(id+"F17.wireOp",EDGE,"E2616")])],"isStart":false});
            var Q110;
            Q110=makeQuery(id+"F18.opExtrude","CAP_EDGE",EDGE,{"disambiguationData":[OSD([sQuery(id+"F17.wireOp",EDGE,"E2615")])],"isStart":false});
            var Q111;
            Q111=makeQuery(id+"F18.opExtrude","CAP_EDGE",EDGE,{"disambiguationData":[OSD([sQuery(id+"F17.wireOp",EDGE,"E2614")])],"isStart":false});
            var Q112;
            Q112=makeQuery(id+"F18.opExtrude","CAP_EDGE",EDGE,{"disambiguationData":[OSD([sQuery(id+"F17.wireOp",EDGE,"E2613")])],"isStart":false});
            var Q113;
            Q113=makeQuery(id+"F18.opExtrude","CAP_EDGE",EDGE,{"disambiguationData":[OSD([sQuery(id+"F17.wireOp",EDGE,"E2612")])],"isStart":false});
            var Q114;
            Q114=makeQuery(id+"F18.opExtrude","CAP_EDGE",EDGE,{"disambiguationData":[OSD([sQuery(id+"F17.wireOp",EDGE,"E2611")])],"isStart":false});
            var Q115;
            Q115=makeQuery(id+"F18.opExtrude","CAP_EDGE",EDGE,{"disambiguationData":[OSD([sQuery(id+"F17.wireOp",EDGE,"E2610")])],"isStart":false});
            var Q116;
            Q116=makeQuery(id+"F18.opExtrude","CAP_EDGE",EDGE,{"disambiguationData":[OSD([sQuery(id+"F17.wireOp",EDGE,"E2609")])],"isStart":false});
            var Q117;
            Q117=makeQuery(id+"F18.opExtrude","CAP_EDGE",EDGE,{"disambiguationData":[OSD([sQuery(id+"F17.wireOp",EDGE,"E2608")])],"isStart":false});
            var Q118;
            Q118=makeQuery(id+"F18.opExtrude","CAP_EDGE",EDGE,{"disambiguationData":[OSD([sQuery(id+"F17.wireOp",EDGE,"E2607")])],"isStart":false});
            var Q119;
            Q119=makeQuery(id+"F18.opExtrude","CAP_EDGE",EDGE,{"disambiguationData":[OSD([sQuery(id+"F17.wireOp",EDGE,"E2606")])],"isStart":false});
            var Q120;
            Q120=makeQuery(id+"F18.opExtrude","CAP_EDGE",EDGE,{"disambiguationData":[OSD([sQuery(id+"F17.wireOp",EDGE,"E2605")])],"isStart":false});
            var Q121;
            Q121=makeQuery(id+"F18.opExtrude","CAP_EDGE",EDGE,{"disambiguationData":[OSD([sQuery(id+"F17.wireOp",EDGE,"E2600")])],"isStart":false});
            var Q122;
            Q122=makeQuery(id+"F18.opExtrude","CAP_EDGE",EDGE,{"disambiguationData":[OSD([sQuery(id+"F17.wireOp",EDGE,"E2601")])],"isStart":false});
            var Q123;
            Q123=makeQuery(id+"F18.opExtrude","CAP_EDGE",EDGE,{"disambiguationData":[OSD([sQuery(id+"F17.wireOp",EDGE,"E2602")])],"isStart":false});
            var Q124;
            Q124=makeQuery(id+"F18.opExtrude","CAP_EDGE",EDGE,{"disambiguationData":[OSD([sQuery(id+"F17.wireOp",EDGE,"E2603")])],"isStart":false});
            var Q125;
            Q125=makeQuery(id+"F18.opExtrude","CAP_EDGE",EDGE,{"disambiguationData":[OSD([sQuery(id+"F17.wireOp",EDGE,"E2604")])],"isStart":false});
            var Q126;
            Q126=makeQuery(id+"F21.opExtrude","CAP_EDGE",EDGE,{"disambiguationData":[OSD([sQuery(id+"F20.wireOp",EDGE,"E5752")])],"isStart":false});
            fillet(context, id + "F27", {"entities" : qUnion([Q0, Q1, Q2, Q3, Q4, Q5, Q6, Q7, Q8, Q9, Q10, Q11, Q12, Q13, Q14, Q15, Q16, Q17, Q18, Q19, Q20, Q21, Q22, Q23, Q24, Q25, Q26, Q27, Q28, Q29, Q30, Q31, Q32, Q33, Q34, Q35, Q36, Q37, Q38, Q39, Q40, Q41, Q42, Q43, Q44, Q45, Q46, Q47, Q48, Q49, Q50, Q51, Q52, Q53, Q54, Q55, Q56, Q57, Q58, Q59, Q60, Q61, Q62, Q63, Q64, Q65, Q66, Q67, Q68, Q69, Q70, Q71, Q72, Q73, Q74, Q75, Q76, Q77, Q78, Q79, Q80, Q81, Q82, Q83, Q84, Q85, Q86, Q87, Q88, Q89, Q90, Q91, Q92, Q93, Q94, Q95, Q96, Q97, Q98, Q99, Q100, Q101, Q102, Q103, Q104, Q105, Q106, Q107, Q108, Q109, Q110, Q111, Q112, Q113, Q114, Q115, Q116, Q117, Q118, Q119, Q120, Q121, Q122, Q123, Q124, Q125, Q126]), "radius" : 2 * mm, "tangentPropagation" : true, "allowEdgeOverflow" : false});
        }
    });
